FCSTD DOCUMENT  (FreeCAD 1.0R39285 (Git))
Label: pinWheel
License: All rights reserved
LicenseURL: https://en.wikipedia.org/wiki/All_rights_reserved
objects: Sketcher::SketchObject×193, Part::Extrusion×189, Part::Feature×37, Part::MultiFuse×17, Part::Cut×10, App::Part×5, Part::Cylinder×3, Part::Box×2, Part::Loft×2, Part::Fillet×2, Part::Compound×1
note: 649 computed .brp shape members not serialized (recipe doc carries the construction recipe); baked Part::Feature solids carry a one-line shape summary decoded from their .brp

FEATURE [Sketcher::SketchObject] Sketch
  ArcFitTolerance = 1e-06
  FullyConstrained = true
  MakeInternals = false
  Placement = pos=(0,0,0) rot=(1,0,0;1.5708rad)
  sketch-geometry (14):
    g0: LineSegment StartX=0 StartY=130 StartZ=0 EndX=-112.583 EndY=65 EndZ=0
    g1: LineSegment StartX=-112.583 StartY=65 StartZ=0 EndX=-112.583 EndY=-65 EndZ=0
    g2: LineSegment StartX=-112.583 StartY=-65 StartZ=0 EndX=-4.9e-15 EndY=-130 EndZ=0
    g3: LineSegment StartX=0 StartY=-130 StartZ=0 EndX=112.583 EndY=-65 EndZ=0
    g4: LineSegment StartX=112.583 StartY=-65 StartZ=0 EndX=112.583 EndY=65 EndZ=0
    g5: LineSegment StartX=112.583 StartY=65 StartZ=0 EndX=4.9e-15 EndY=130 EndZ=0
    g6: Circle [constr] CenterX=0 CenterY=0 CenterZ=0 NormalX=0 NormalY=0 NormalZ=1 AngleXU=0 Radius=130
    g7: LineSegment StartX=0 StartY=135 StartZ=0 EndX=-116.913 EndY=67.5 EndZ=0
    g8: LineSegment StartX=-116.913 StartY=67.5 StartZ=0 EndX=-116.913 EndY=-67.5 EndZ=0
    g9: LineSegment StartX=-116.913 StartY=-67.5 StartZ=0 EndX=4.2e-15 EndY=-135 EndZ=0
    g10: LineSegment StartX=0 StartY=-135 StartZ=0 EndX=116.913 EndY=-67.5 EndZ=0
    g11: LineSegment StartX=116.913 StartY=-67.5 StartZ=0 EndX=116.913 EndY=67.5 EndZ=0
    g12: LineSegment StartX=116.913 StartY=67.5 StartZ=0 EndX=-5e-15 EndY=135 EndZ=0
    g13: Circle [constr] CenterX=0 CenterY=0 CenterZ=0 NormalX=0 NormalY=0 NormalZ=1 AngleXU=0 Radius=135
  constraints (32):
    c: Coincident(g0,g1)
    c: Coincident(g1,g2)
    c: Coincident(g2,g3)
    c: Coincident(g3,g4)
    c: Coincident(g4,g5)
    c: Coincident(g5,g0)
    c: Equal(g0, g1-g5) x5
    c: PointOnObject(g0,g6)
    c: PointOnObject(g1,g6)
    c: PointOnObject(g2,g6)
    c: PointOnObject(g3,g6)
    c: PointOnObject(g4,g6)
    c: PointOnObject(g5,g6)
    c: Coincident(g6,g-1)
    c: PointOnObject(g5,g-2)
    c: Diameter(g6) = 260
    c: Coincident(g7,g8)
    c: Coincident(g8,g9)
    c: Coincident(g9,g10)
    c: Coincident(g10,g11)
    c: Coincident(g11,g12)
    c: Coincident(g12,g7)
    c: Equal(g7, g8-g12) x5
    c: PointOnObject(g7,g13)
    c: PointOnObject(g8,g13)
    c: PointOnObject(g9,g13)
    c: PointOnObject(g10,g13)
    c: PointOnObject(g11,g13)
    c: PointOnObject(g12,g13)
    c: Coincident(g13,g6)
    c: PointOnObject(g12,g-2)
    c: Diameter(g13) = 270
FEATURE [Part::Extrusion] Extrude  label="hexShell"
  Base = -> Sketch
  Dir = (0,-1,2e-16)
  DirMode = 2
  FaceMakerClass = Part::FaceMakerBullseye
  FaceMakerMode = 3
  LengthFwd = 150
  LengthRev = 0
  Solid = true
  Symmetric = false
FEATURE [Part::Feature] Shape  label="hex"
  Placement = pos=(13,10,0) rot=(0,0,1;0rad)
  shape: bbox 306 x 310 x 2e-07 mm, 718 faces, 0 solids (baked)
FEATURE [Part::Box] Box  label="Cube"
  AttacherType = Attacher::AttachEngine3D
  Height = 10
  Length = 320
  Width = 320
FEATURE [Part::Extrusion] Extrude001
  Base = -> Shape
  Dir = (0,0,1)
  DirMode = 2
  FaceMakerClass = Part::FaceMakerBullseye
  FaceMakerMode = 3
  LengthFwd = 10
  LengthRev = 0
  Solid = false
  Symmetric = false
FEATURE [Part::Cut] Cut  label="hexMesh"
  Base = -> Box
  Placement = pos=(-170,-139.5,-157.5) rot=(1,0,0;1.5708rad)
  Refine = true
  Tool = -> Extrude001
FEATURE [Sketcher::SketchObject] Sketch001
  ArcFitTolerance = 1e-06
  FullyConstrained = true
  MakeInternals = false
  Placement = pos=(0,0,0) rot=(1,0,0;1.5708rad)
  sketch-geometry (11):
    g0: LineSegment StartX=0 StartY=132.5 StartZ=0 EndX=-114.748 EndY=66.25 EndZ=0
    g1: LineSegment StartX=-114.748 StartY=66.25 StartZ=0 EndX=-114.748 EndY=-66.25 EndZ=0
    g2: LineSegment StartX=-114.748 StartY=-66.25 StartZ=0 EndX=3.8584e-11 EndY=-132.5 EndZ=0
    g3: LineSegment StartX=3.85825e-11 StartY=-132.5 StartZ=0 EndX=114.748 EndY=-66.25 EndZ=0
    g4: LineSegment StartX=114.748 StartY=-66.25 StartZ=0 EndX=114.748 EndY=66.25 EndZ=0
    g5: LineSegment StartX=114.748 StartY=66.25 StartZ=0 EndX=7e-15 EndY=132.5 EndZ=0
    g6: Circle [constr] CenterX=0 CenterY=0 CenterZ=0 NormalX=0 NormalY=0 NormalZ=1 AngleXU=0 Radius=132.5
    g7: LineSegment StartX=-175 StartY=165 StartZ=0 EndX=-175 EndY=-165 EndZ=0
    g8: LineSegment StartX=-175 StartY=-165 StartZ=0 EndX=155 EndY=-165 EndZ=0
    g9: LineSegment StartX=155 StartY=-165 StartZ=0 EndX=155 EndY=165 EndZ=0
    g10: LineSegment StartX=155 StartY=165 StartZ=0 EndX=-175 EndY=165 EndZ=0
  constraints (28):
    c: Coincident(g0,g1)
    c: Coincident(g1,g2)
    c: Coincident(g2,g3)
    c: Coincident(g3,g4)
    c: Coincident(g4,g5)
    c: Coincident(g5,g0)
    c: Equal(g0, g1-g5) x5
    c: PointOnObject(g0,g6)
    c: PointOnObject(g1,g6)
    c: PointOnObject(g2,g6)
    c: PointOnObject(g3,g6)
    c: PointOnObject(g4,g6)
    c: PointOnObject(g5,g6)
    c: Coincident(g6,g-1)
    c: PointOnObject(g5,g-2)
    c: Diameter(g6) = 265
    c: Coincident(g7,g8)
    c: Coincident(g8,g9)
    c: Coincident(g9,g10)
    c: Coincident(g10,g7)
    c: Vertical(g7)
    c: Vertical(g9)
    c: Horizontal(g8)
    c: Horizontal(g10)
    c: DistanceY(g7,g7) = 330
    c: DistanceX(g10,g10) = 330
    c: Distance(g7,g-1) = 165
    c: Distance(g7,g-2) = 175
FEATURE [Part::Extrusion] Extrude002
  Base = -> Sketch001
  Dir = (0,-1,2e-16)
  DirMode = 2
  FaceMakerClass = Part::FaceMakerBullseye
  FaceMakerMode = 3
  LengthFwd = 20
  LengthRev = 0
  Placement = pos=(0,-134,0) rot=(0,0,1;0rad)
  Solid = true
  Symmetric = false
FEATURE [Part::Cut] Cut001  label="Mesh"
  Base = -> Cut
  Refine = true
  Tool = -> Extrude002
FEATURE [Part::Box] Box001  label="stand"
  AttacherType = Attacher::AttachEngine3D
  Height = 500
  Length = 60
  Placement = pos=(-30,150,-472) rot=(0,0,1;0rad)
  Width = 30
FEATURE [Part::Cylinder] Cylinder  label="pinWheelAxis"
  Angle = 360
  AttacherType = Attacher::AttachEngine3D
  FirstAngle = 0
  Height = 25
  Placement = pos=(0,-140,0) rot=(1,0,0;1.5708rad)
  Radius = 3
  SecondAngle = 0
FEATURE [Part::Feature] Part__Feature  label="PW00.01"
  Placement = pos=(0,0,0) rot=(1,0,0;1.5708rad)
  shape: bbox 56.83 x 111.6 x 23.27 mm, 29 faces (baked)
FEATURE [Part::Feature] Part__Feature001  label="PW00.02"
  Placement = pos=(0,0,0.1) rot=(0.862856,-0.357407,-0.357407;1.71777rad)
  shape: bbox 94.97 x 95.87 x 23.27 mm, 29 faces (baked)
FEATURE [Part::Feature] Part__Feature002  label="PW00.03"
  Placement = pos=(0,0,0.2) rot=(0.57735,-0.57735,-0.57735;2.0944rad)
  shape: bbox 111.6 x 56.83 x 23.27 mm, 29 faces (baked)
FEATURE [Part::Feature] Part__Feature003  label="PW00.04"
  Placement = pos=(0,0,0.3) rot=(-0.281085,0.678598,0.678598;3.68962rad)
  shape: bbox 95.87 x 94.97 x 23.27 mm, 29 faces (baked)
FEATURE [Part::Feature] Part__Feature004  label="PW00.05"
  Placement = pos=(0,0,0.4) rot=(0,0.707107,0.707107;3.14159rad)
  shape: bbox 56.83 x 111.6 x 23.27 mm, 29 faces (baked)
FEATURE [Part::Feature] Part__Feature005  label="PW00.06"
  Placement = pos=(0,0,0.5) rot=(0.281085,0.678598,0.678598;2.59356rad)
  shape: bbox 94.97 x 95.87 x 23.27 mm, 29 faces (baked)
FEATURE [Part::Feature] Part__Feature006  label="PW00.07"
  Placement = pos=(0,0,0.6) rot=(0.57735,0.57735,0.57735;2.0944rad)
  shape: bbox 111.6 x 56.83 x 23.27 mm, 29 faces (baked)
FEATURE [Part::Feature] Part__Feature007  label="PW00.08"
  Placement = pos=(0,0,0.7) rot=(0.862856,0.357407,0.357407;1.71777rad)
  shape: bbox 95.87 x 94.97 x 23.27 mm, 29 faces (baked)
FEATURE [Part::Feature] Part__Feature009  label="PW00.10"
  Placement = pos=(2.46e-14,1.99e-14,-6.99945) rot=(0,0,1;0rad)
  shape: bbox 12 x 12 x 10 mm, 5 faces (baked)
FEATURE [Part::Feature] Part__Feature010  label="PW00.11"
  Placement = pos=(1.67e-14,1.9e-15,-6.5475) rot=(0,0,1;0rad)
  shape: bbox 5.016 x 5.016 x 2.016 mm, 3 faces (baked)
FEATURE [App::Part] PW00_00  label="wheel"
  Group = -> [Part__Feature,Part__Feature001,Part__Feature002,Part__Feature003,Part__Feature004,Part__Feature005,Part__Feature006,Part__Feature007,Part__Feature009,Part__Feature010]
  Origin = -> Origin
  Placement = pos=(0,-166.5,-5.03e-14) rot=(1,0,0;1.5708rad)
FEATURE [Sketcher::SketchObject] Sketch004
  ArcFitTolerance = 1e-06
  FullyConstrained = true
  MakeInternals = false
  Placement = pos=(0,-150,0) rot=(1,0,0;1.5708rad)
  sketch-geometry (7):
    g0: LineSegment StartX=0 StartY=135 StartZ=0 EndX=-116.913 EndY=67.5 EndZ=0
    g1: LineSegment StartX=-116.913 StartY=67.5 StartZ=0 EndX=-116.913 EndY=-67.5 EndZ=0
    g2: LineSegment StartX=-116.913 StartY=-67.5 StartZ=0 EndX=1.92e-14 EndY=-135 EndZ=0
    g3: LineSegment StartX=1.42e-14 StartY=-135 StartZ=0 EndX=116.913 EndY=-67.5 EndZ=0
    g4: LineSegment StartX=116.913 StartY=-67.5 StartZ=0 EndX=116.913 EndY=67.5 EndZ=0
    g5: LineSegment StartX=116.913 StartY=67.5 StartZ=0 EndX=-4.2e-15 EndY=135 EndZ=0
    g6: Circle [constr] CenterX=0 CenterY=0 CenterZ=0 NormalX=0 NormalY=0 NormalZ=1 AngleXU=0 Radius=135
  constraints (16):
    c: Coincident(g0,g1)
    c: Coincident(g1,g2)
    c: Coincident(g2,g3)
    c: Coincident(g3,g4)
    c: Coincident(g4,g5)
    c: Coincident(g5,g0)
    c: Equal(g0, g1-g5) x5
    c: PointOnObject(g0,g6)
    c: PointOnObject(g1,g6)
    c: PointOnObject(g2,g6)
    c: PointOnObject(g3,g6)
    c: PointOnObject(g4,g6)
    c: PointOnObject(g5,g6)
    c: PointOnObject(g5,g-2)
    c: Diameter(g6) = 270
    c: Coincident(g6,g-1)
FEATURE [Sketcher::SketchObject] Sketch005
  ArcFitTolerance = 1e-06
  FullyConstrained = true
  MakeInternals = false
  Placement = pos=(0,0,0) rot=(1,0,0;1.5708rad)
  sketch-geometry (8):
    g0: Circle [constr] CenterX=0 CenterY=0 CenterZ=0 NormalX=0 NormalY=0 NormalZ=1 AngleXU=0 Radius=20
    g1: LineSegment StartX=0 StartY=25 StartZ=0 EndX=-21.6506 EndY=12.5 EndZ=0
    g2: LineSegment StartX=-21.6506 StartY=12.5 StartZ=0 EndX=-21.6506 EndY=-12.5 EndZ=0
    g3: LineSegment StartX=-21.6506 StartY=-12.5 StartZ=0 EndX=-1.7133e-12 EndY=-25 EndZ=0
    g4: LineSegment StartX=-1.7124e-12 StartY=-25 StartZ=0 EndX=21.6506 EndY=-12.5 EndZ=0
    g5: LineSegment StartX=21.6506 StartY=-12.5 StartZ=0 EndX=21.6506 EndY=12.5 EndZ=0
    g6: LineSegment StartX=21.6506 StartY=12.5 StartZ=0 EndX=1e-15 EndY=25 EndZ=0
    g7: Circle [constr] CenterX=0 CenterY=0 CenterZ=0 NormalX=0 NormalY=0 NormalZ=1 AngleXU=0 Radius=25
  constraints (18):
    c: Coincident(g0,g-1)
    c: Diameter(g0) = 40
    c: Coincident(g1,g2)
    c: Coincident(g2,g3)
    c: Coincident(g3,g4)
    c: Coincident(g4,g5)
    c: Coincident(g5,g6)
    c: Coincident(g6,g1)
    c: Equal(g1, g2-g6) x5
    c: PointOnObject(g1,g7)
    c: PointOnObject(g2,g7)
    c: PointOnObject(g3,g7)
    c: PointOnObject(g4,g7)
    c: PointOnObject(g5,g7)
    c: PointOnObject(g6,g7)
    c: Coincident(g7,g0)
    c: PointOnObject(g6,g-2)
    c: Diameter(g7) = 50
FEATURE [Sketcher::SketchObject] Sketch006
  ArcFitTolerance = 1e-06
  FullyConstrained = true
  MakeInternals = false
  Placement = pos=(0,-150,0) rot=(1,0,0;1.5708rad)
  sketch-geometry (8):
    g0: LineSegment StartX=0 StartY=130 StartZ=0 EndX=-112.583 EndY=65 EndZ=0
    g1: LineSegment StartX=-112.583 StartY=65 StartZ=0 EndX=-112.583 EndY=-65 EndZ=0
    g2: LineSegment StartX=-112.583 StartY=-65 StartZ=0 EndX=-1.13e-14 EndY=-130 EndZ=0
    g3: LineSegment StartX=1.42e-14 StartY=-130 StartZ=0 EndX=112.583 EndY=-65 EndZ=0
    g4: LineSegment StartX=112.583 StartY=-65 StartZ=0 EndX=112.583 EndY=65 EndZ=0
    g5: LineSegment StartX=112.583 StartY=65 StartZ=0 EndX=4.7e-15 EndY=130 EndZ=0
    g6: Circle [constr] CenterX=0 CenterY=0 CenterZ=0 NormalX=0 NormalY=0 NormalZ=1 AngleXU=0 Radius=130
    g7: Circle [constr] CenterX=0 CenterY=0 CenterZ=0 NormalX=0 NormalY=0 NormalZ=1 AngleXU=0 Radius=135
  constraints (18):
    c: Coincident(g0,g1)
    c: Coincident(g1,g2)
    c: Coincident(g2,g3)
    c: Coincident(g3,g4)
    c: Coincident(g4,g5)
    c: Coincident(g5,g0)
    c: Equal(g0, g1-g5) x5
    c: PointOnObject(g0,g6)
    c: PointOnObject(g1,g6)
    c: PointOnObject(g2,g6)
    c: PointOnObject(g3,g6)
    c: PointOnObject(g4,g6)
    c: PointOnObject(g5,g6)
    c: Coincident(g6,g-1)
    c: PointOnObject(g5,g-2)
    c: Diameter(g6) = 260
    c: Coincident(g7,g6)
    c: Diameter(g7) = 270
FEATURE [Sketcher::SketchObject] Sketch007
  ArcFitTolerance = 1e-06
  FullyConstrained = true
  MakeInternals = false
  Placement = pos=(0,0,0) rot=(1,0,0;1.5708rad)
  sketch-geometry (8):
    g0: LineSegment StartX=0 StartY=20 StartZ=0 EndX=-17.3205 EndY=10 EndZ=0
    g1: LineSegment StartX=-17.3205 StartY=10 StartZ=0 EndX=-17.3205 EndY=-10 EndZ=0
    g2: LineSegment StartX=-17.3205 StartY=-10 StartZ=0 EndX=-2.7e-15 EndY=-20 EndZ=0
    g3: LineSegment StartX=-3.6e-15 StartY=-20 StartZ=0 EndX=17.3205 EndY=-10 EndZ=0
    g4: LineSegment StartX=17.3205 StartY=-10 StartZ=0 EndX=17.3205 EndY=10 EndZ=0
    g5: LineSegment StartX=17.3205 StartY=10 StartZ=0 EndX=4e-16 EndY=20 EndZ=0
    g6: Circle [constr] CenterX=0 CenterY=0 CenterZ=0 NormalX=0 NormalY=0 NormalZ=1 AngleXU=0 Radius=20
    g7: Circle [constr] CenterX=0 CenterY=0 CenterZ=0 NormalX=0 NormalY=0 NormalZ=1 AngleXU=0 Radius=25
  constraints (18):
    c: Coincident(g0,g1)
    c: Coincident(g1,g2)
    c: Coincident(g2,g3)
    c: Coincident(g3,g4)
    c: Coincident(g4,g5)
    c: Coincident(g5,g0)
    c: Equal(g0, g1-g5) x5
    c: PointOnObject(g0,g6)
    c: PointOnObject(g1,g6)
    c: PointOnObject(g2,g6)
    c: PointOnObject(g3,g6)
    c: PointOnObject(g4,g6)
    c: PointOnObject(g5,g6)
    c: Coincident(g6,g-1)
    c: PointOnObject(g5,g-2)
    c: Diameter(g6) = 40
    c: Coincident(g7,g6)
    c: Diameter(g7) = 50
FEATURE [Part::Loft] Loft002
  Closed = false
  MaxDegree = 5
  Ruled = false
  Sections = -> [Sketch006,Sketch007]
  Solid = true
FEATURE [Part::Loft] Loft003
  Closed = false
  MaxDegree = 5
  Ruled = false
  Sections = -> [Sketch004,Sketch005]
  Solid = true
FEATURE [Part::Cut] Cut002  label="backEncloser"
  Base = -> Loft003
  Placement = pos=(0,150,0) rot=(0,0,1;0rad)
  Refine = true
  Tool = -> Loft002
FEATURE [Part::Feature] Part__Feature023  label="COZIR"
  Placement = pos=(5.41029,2.97838,5.56111) rot=(0,0,1;0rad)
  shape: bbox 51.61 x 17 x 50.23 mm, 43 faces (baked)
FEATURE [Part::Feature] Part__Feature024  label="COMPOUND"
  shape: bbox 3.14 x 5 x 10.76 mm, 60 faces, 10 solids (baked)
FEATURE [App::Part] COZIR_Sensor_v2  label="COZIR Sensor v2"
  Group = -> [Part__Feature023,Part__Feature024]
  Origin = -> Origin002
  Placement = pos=(18,-15,8.25) rot=(0,-1,0;5.75959rad)
FEATURE [Part::Feature] Part__Feature059  label="ips7100"
  Placement = pos=(-24,0,222) rot=(0.999993,-0.003655,0;3.14159rad)
  shape: bbox 48.14 x 14.05 x 44.14 mm, 1935 faces (baked)
FEATURE [Part::Compound] Compound  label="ips7100s"
  Links = -> [Part__Feature059]
  Placement = pos=(48.8551,-46.85,39.7193) rot=(-0.127223,0.126421,0.983785;4.70221rad)
FEATURE [Part::Feature] Part__Feature334  label="CAPC-0805-T0.95-BN v012"
  Placement = pos=(-5.48627,2.66154,1.6) rot=(0,0,-1;1.5708rad)
  shape: bbox 1.35 x 2.1 x 0.95 mm, 42 faces (baked)
FEATURE [Part::Feature] Part__Feature335  label="CAPC-0805-T0.95-BN v013"
  Placement = pos=(-3.43627,2.66154,1.6) rot=(0,0,-1;1.5708rad)
  shape: bbox 1.35 x 2.1 x 0.95 mm, 42 faces (baked)
FEATURE [Part::Feature] Part__Feature336  label="CAPC-0603-T0.9-BN v009"
  Placement = pos=(-1.69987,-3.28475,1.6) rot=(0,0,1;0rad)
  shape: bbox 1.7 x 0.9 x 0.9 mm, 42 faces (baked)
FEATURE [Part::Feature] Part__Feature337  label="BODY_MF06A003"
  Placement = pos=(0,0,0.762) rot=(0.57735,-0.57735,-0.57735;2.0944rad)
  shape: bbox 1.601 x 2.921 x 1.016 mm, 42 faces (baked)
FEATURE [Part::Feature] Part__Feature338  label="LEAD_MF06A018"
  Placement = pos=(-0.9652,-0.9525,0.1016) rot=(0.57735,-0.57735,-0.57735;2.0944rad)
  shape: bbox 0.6223 x 0.3749 x 0.8636 mm, 14 faces (baked)
FEATURE [Part::Feature] Part__Feature339  label="LEAD_MF06A019"
  Placement = pos=(-0.9652,0,0.1016) rot=(0.57735,-0.57735,-0.57735;2.0944rad)
  shape: bbox 0.6223 x 0.3749 x 0.8636 mm, 14 faces (baked)
FEATURE [Part::Feature] Part__Feature340  label="LEAD_MF06A020"
  Placement = pos=(-0.9652,0.9525,0.1016) rot=(0.57735,-0.57735,-0.57735;2.0944rad)
  shape: bbox 0.6223 x 0.3749 x 0.8636 mm, 14 faces (baked)
FEATURE [Part::Feature] Part__Feature341  label="LEAD_MF06A021"
  Placement = pos=(0.9652,-0.9525,0.1016) rot=(0.57735,0.57735,0.57735;2.0944rad)
  shape: bbox 0.6223 x 0.3749 x 0.8636 mm, 14 faces (baked)
FEATURE [Part::Feature] Part__Feature342  label="LEAD_MF06A022"
  Placement = pos=(0.9652,0,0.1016) rot=(0.57735,0.57735,0.57735;2.0944rad)
  shape: bbox 0.6223 x 0.3749 x 0.8636 mm, 14 faces (baked)
FEATURE [Part::Feature] Part__Feature343  label="LEAD_MF06A023"
  Placement = pos=(0.9652,0.9525,0.1016) rot=(0.57735,0.57735,0.57735;2.0944rad)
  shape: bbox 0.6223 x 0.3749 x 0.8636 mm, 14 faces (baked)
FEATURE [Part::Feature] Part__Feature344  label="SOT363 v005"
  Placement = pos=(4.97054,-0.645171,1.675) rot=(0,0,1;3.14159rad)
  shape: bbox 2.1 x 2 x 1.1 mm, 94 faces, 7 solids (baked)
FEATURE [Part::Feature] Part__Feature345  label="LED 0603 single color v005"
  Placement = pos=(-9.18406,3.72778,1.60762) rot=(0,0,1;1.5708rad)
  shape: bbox 1.961 x 0.7932 x 0.7145 mm, 63 faces, 5 solids (baked)
FEATURE [Part::Feature] Part__Feature346  label="RESC-0603 v007"
  Placement = pos=(4.83432,-3.67461,1.6) rot=(0,0,1;0rad)
  shape: bbox 1.7 x 0.9 x 0.55 mm, 52 faces, 3 solids (baked)
FEATURE [Part::Feature] Part__Feature347  label="RESC-0603 v008"
  Placement = pos=(-7.14949,3.61248,1.6) rot=(0,0,-1;1.5708rad)
  shape: bbox 0.9 x 1.7 x 0.55 mm, 52 faces, 3 solids (baked)
FEATURE [Part::Feature] Part__Feature348  label="Printed Circuit Board004"
  shape: bbox 25.4 x 17.78 x 1.6 mm, 42 faces (baked)
FEATURE [Part::Feature] Part__Feature349  label="EAHC2835WD009"
  shape: bbox 3.513 x 2.813 x 0.7485 mm, 108 faces, 4 solids (baked)
FEATURE [Part::Feature] Part__Feature350  label="AS7341 v005"
  Placement = pos=(0,-0.339822,1.6) rot=(0,0,1;0rad)
  shape: bbox 2 x 3.1 x 1.1 mm, 267 faces, 26 solids (baked)
FEATURE [Part::Feature] Part__Feature351  label="CAPC-0805-T0.95-BN v014"
  Placement = pos=(-5.01759,-3.15294,1.6) rot=(0,0,1;0rad)
  shape: bbox 2.1 x 1.35 x 0.95 mm, 42 faces (baked)
FEATURE [Part::Feature] Part__Feature352  label="YC164_RESPACK v007"
  Placement = pos=(2.99591,1.52916,1.6) rot=(0,0,1;0rad)
  shape: bbox 3.2 x 1.6 x 0.61 mm, 172 faces (baked)
FEATURE [Part::Feature] Part__Feature353  label="qwicc v009"
  Placement = pos=(-10.8364,0.0607456,1.65) rot=(0,0,-1;1.5708rad)
  shape: bbox 4.95 x 6 x 2.96 mm, 229 faces, 7 solids (baked)
FEATURE [Part::Feature] Part__Feature354  label="qwicc v010"
  Placement = pos=(10.8256,0.00556102,1.65) rot=(0,0,1;1.5708rad)
  shape: bbox 4.95 x 6 x 2.96 mm, 229 faces, 7 solids (baked)
FEATURE [App::Part] sot_23_6_v005  label="sot-23-6 v005"
  Group = -> [Part__Feature337,Part__Feature338,Part__Feature339,Part__Feature340,Part__Feature341,Part__Feature342,Part__Feature343]
  Origin = -> Origin019
  Placement = pos=(-4.47945,-0.603742,1.69152) rot=(0,0,1;0rad)
FEATURE [App::Part] Adafruit_AS7341_STEMMA_QT_v005  label="bme280"
  Group = -> [Part__Feature348,Part__Feature349,Part__Feature350,Part__Feature351,Part__Feature334,Part__Feature335,Part__Feature336,sot_23_6_v005,Part__Feature344,Part__Feature345,Part__Feature346,Part__Feature347,Part__Feature352,Part__Feature353,Part__Feature354]
  Origin = -> Origin020
  Placement = pos=(-39.4483,-2,71.3086) rot=(-0.962637,0.19148,-0.19148;4.67432rad)
FEATURE [Sketcher::SketchObject] Sketch386
  ArcFitTolerance = 0
  FullyConstrained = true
  MakeInternals = false
  Placement = pos=(0,0,0) rot=(1,0,0;1.5708rad)
  sketch-geometry (6):
    g0: Circle CenterX=202.5 CenterY=16.1 CenterZ=0 NormalX=0 NormalY=0 NormalZ=1 AngleXU=0 Radius=1.625
    g1: Circle CenterX=202.5 CenterY=16.1 CenterZ=0 NormalX=0 NormalY=0 NormalZ=1 AngleXU=0 Radius=5
    g2: Circle CenterX=224.07 CenterY=53.45 CenterZ=0 NormalX=0 NormalY=0 NormalZ=1 AngleXU=0 Radius=5
    g3: Circle CenterX=180.93 CenterY=53.45 CenterZ=0 NormalX=0 NormalY=0 NormalZ=1 AngleXU=0 Radius=5
    g4: Circle CenterX=180.93 CenterY=53.45 CenterZ=0 NormalX=0 NormalY=0 NormalZ=1 AngleXU=0 Radius=1.625
    g5: Circle CenterX=224.07 CenterY=53.45 CenterZ=0 NormalX=0 NormalY=0 NormalZ=1 AngleXU=0 Radius=1.625
  constraints (15):
    c: DistanceX(g0) = 202.5
    c: DistanceY(g0) = 16.1
    c: Coincident(g0,g1)
    c: DistanceY(g3,g2) = 0
    c: Equal(g1,g2)
    c: Equal(g1,g3)
    c: Diameter(g1) = 10
    c: Equal(g0,g5)
    c: Equal(g0,g4)
    c: Diameter(g0) = 3.25
    c: DistanceY(g0,g3) = 37.35
    c: DistanceX(g3,g0) = 21.57
    c: DistanceX(g0,g2) = 21.57
    c: Coincident(g5,g2)
    c: Coincident(g4,g3)
FEATURE [Part::Extrusion] Extrude379  label="co2Mount003"
  Base = -> Sketch386
  Dir = (0,-1,2e-16)
  DirMode = 2
  FaceMakerClass = Part::FaceMakerBullseye
  FaceMakerMode = 3
  LengthFwd = 22
  LengthRev = 0
  Placement = pos=(-202.681,8,35.5181) rot=(0,0,1;0rad)
  Solid = true
  Symmetric = false
FEATURE [Sketcher::SketchObject] Sketch387
  ArcFitTolerance = 1e-06
  FullyConstrained = true
  MakeInternals = false
  Placement = pos=(0,0,0) rot=(1,0,0;1.5708rad)
  sketch-geometry (11):
    g0: ArcOfCircle CenterX=0 CenterY=75 CenterZ=0 NormalX=0 NormalY=0 NormalZ=1 AngleXU=0 Radius=65 StartAngle=3.14161 EndAngle=6.2832
    g1: LineSegment StartX=-65 StartY=74.999 StartZ=0 EndX=3e-16 EndY=105.31 EndZ=0
    g2: LineSegment StartX=3e-16 StartY=105.31 StartZ=0 EndX=65 EndY=75.001 EndZ=0
    g3: ArcOfCircle CenterX=32.0734 CenterY=74.8326 CenterZ=0 NormalX=0 NormalY=0 NormalZ=1 AngleXU=0 Radius=4 StartAngle=0.252249 EndAngle=3.39384
    g4: ArcOfCircle CenterX=37.1 CenterY=55.33 CenterZ=0 NormalX=0 NormalY=0 NormalZ=1 AngleXU=0 Radius=4 StartAngle=3.39384 EndAngle=6.53543
    g5: LineSegment StartX=35.9468 StartY=75.831 StartZ=0 EndX=40.9734 EndY=56.3283 EndZ=0
    g6: LineSegment StartX=28.2 StartY=73.8343 StartZ=0 EndX=33.2266 EndY=54.3317 EndZ=0
    g7: Circle CenterX=-60 CenterY=70 CenterZ=0 NormalX=0 NormalY=0 NormalZ=1 AngleXU=0 Radius=1.75
    g8: Circle CenterX=60 CenterY=70 CenterZ=0 NormalX=0 NormalY=0 NormalZ=1 AngleXU=0 Radius=1.75
    g9: Circle CenterX=-6 CenterY=100 CenterZ=0 NormalX=0 NormalY=0 NormalZ=1 AngleXU=0 Radius=1.75
    g10: Circle CenterX=6 CenterY=100 CenterZ=0 NormalX=0 NormalY=0 NormalZ=1 AngleXU=0 Radius=1.75
  constraints (32):
    c: PointOnObject(g0,g-2)
    c: Radius(g0) = 65
    c: Coincident(g1,g0)
    c: PointOnObject(g1,g-2)
    c: Coincident(g2,g1)
    c: Coincident(g2,g0)
    c: Angle(g1,g2) = 2.26893
    c: Angle(g0) = 3.14159
    c: Distance(g1,g1) = 71.72
    c: DistanceY(g-1,g0) = 75
    c: Tangent(g3,g5) = 1.5708
    c: Tangent(g3,g6) = -1.5708
    c: Tangent(g4,g5) = 1.5708
    c: Tangent(g4,g6) = -1.5708
    c: Equal(g3,g4)
    c: Distance(g4,g-2) = 37.1
    c: DistanceY(g-1,g4) = 55.33
    c: Distance(g4,g4) = 8
    c: Distance(g4,g3) = 20.14
    c: Distance(g3,g-2) = 28.2
    c: Equal(g9,g10)
    c: Equal(g9,g8)
    c: Equal(g9,g7)
    c: Diameter(g9) = 3.5
    c: Distance(g7,g-2) = 60
    c: Distance(g8,g-2) = 60
    c: Horizontal(g7,g8)
    c: DistanceY(g-1,g7) = 70
    c: DistanceY(g-1,g9) = 100
    c: DistanceX(g9,g-1) = 6
    c: Horizontal(g9,g10)
    c: Distance(g10,g-2) = 6
FEATURE [Part::Extrusion] Extrude380  label="sensorBase"
  Base = -> Sketch387
  Dir = (0,-1,2e-16)
  DirMode = 2
  FaceMakerClass = Part::FaceMakerBullseye
  FaceMakerMode = 3
  LengthFwd = 7
  LengthRev = 0
  Placement = pos=(0,15,0) rot=(0,0,1;0rad)
  Solid = true
  Symmetric = false
FEATURE [Sketcher::SketchObject] Sketch388
  ArcFitTolerance = 0
  FullyConstrained = true
  MakeInternals = false
  Placement = pos=(0,0,0) rot=(1,0,0;1.5708rad)
  sketch-geometry (8):
    g0: Circle CenterX=173.65 CenterY=40.16 CenterZ=0 NormalX=0 NormalY=0 NormalZ=1 AngleXU=0 Radius=5
    g1: Circle CenterX=186.35 CenterY=40.16 CenterZ=0 NormalX=0 NormalY=0 NormalZ=1 AngleXU=0 Radius=5
    g2: Circle CenterX=173.65 CenterY=19.84 CenterZ=0 NormalX=0 NormalY=0 NormalZ=1 AngleXU=0 Radius=5
    g3: Circle CenterX=186.35 CenterY=19.84 CenterZ=0 NormalX=0 NormalY=0 NormalZ=1 AngleXU=0 Radius=5
    g4: Circle CenterX=173.65 CenterY=19.84 CenterZ=0 NormalX=0 NormalY=0 NormalZ=1 AngleXU=0 Radius=1.125
    g5: Circle CenterX=186.35 CenterY=19.84 CenterZ=0 NormalX=0 NormalY=0 NormalZ=1 AngleXU=0 Radius=1.125
    g6: Circle CenterX=186.35 CenterY=40.16 CenterZ=0 NormalX=0 NormalY=0 NormalZ=1 AngleXU=0 Radius=1.125
    g7: Circle CenterX=173.65 CenterY=40.16 CenterZ=0 NormalX=0 NormalY=0 NormalZ=1 AngleXU=0 Radius=1.125
  constraints (20):
    c: DistanceY(g1,g0) = 0
    c: DistanceX(g0) = 173.65
    c: DistanceY(g0) = 40.16
    c: DistanceY(g2,g0) = 20.32
    c: Horizontal(g2,g3)
    c: Vertical(g3,g1)
    c: Equal(g0,g1)
    c: Equal(g0,g2)
    c: Equal(g0,g3)
    c: Diameter(g0) = 10
    c: DistanceX(g0,g1) = 12.7
    c: Vertical(g2,g0)
    c: Coincident(g4,g2)
    c: Coincident(g5,g3)
    c: Coincident(g6,g1)
    c: Coincident(g7,g0)
    c: Equal(g4,g5)
    c: Equal(g4,g7)
    c: Equal(g4,g6)
    c: Diameter(g4) = 2.25
FEATURE [Part::Extrusion] Extrude381  label="i2cMounts003"
  Base = -> Sketch388
  Dir = (0,-1,2e-16)
  DirMode = 2
  FaceMakerClass = Part::FaceMakerBullseye
  FaceMakerMode = 3
  LengthFwd = 10
  LengthRev = 0
  Placement = pos=(-136.04,8,226.12) rot=(0,-1,0;5.10509rad)
  Solid = true
  Symmetric = false
FEATURE [Part::Feature] Part__Feature355  label="ips7101"
  Placement = pos=(-24,0,222) rot=(0.999993,-0.003655,0;3.14159rad)
  shape: bbox 48.14 x 14.05 x 44.14 mm, 1935 faces (baked)
FEATURE [Sketcher::SketchObject] Sketch390
  ArcFitTolerance = 1e-06
  FullyConstrained = true
  MakeInternals = false
  MapMode = 3
  Placement = pos=(103.996,0.641742,-0.641742) rot=(0.578538,-0.574968,-0.578538;2.08727rad)
  sketch-geometry (10):
    g0: LineSegment StartX=-55 StartY=0 StartZ=0 EndX=-39.5 EndY=0 EndZ=0
    g1: LineSegment StartX=-39.5 StartY=0 StartZ=0 EndX=-39.5 EndY=7.25 EndZ=0
    g2: LineSegment StartX=-39.5 StartY=7.25 StartZ=0 EndX=-55 EndY=7.25 EndZ=0
    g3: LineSegment StartX=-55 StartY=7.25 StartZ=0 EndX=-55 EndY=0 EndZ=0
    g4: LineSegment StartX=-55 StartY=36.75 StartZ=0 EndX=7.1e-15 EndY=36.75 EndZ=0
    g5: LineSegment StartX=7.1e-15 StartY=36.75 StartZ=0 EndX=7.1e-15 EndY=44 EndZ=0
    g6: LineSegment StartX=7.1e-15 StartY=44 StartZ=0 EndX=-55 EndY=44 EndZ=0
    g7: LineSegment StartX=-55 StartY=44 StartZ=0 EndX=-55 EndY=36.75 EndZ=0
    g8: Circle CenterX=-44.4 CenterY=3.625 CenterZ=0 NormalX=0 NormalY=0 NormalZ=1 AngleXU=0 Radius=1.25
    g9: Circle CenterX=-3.625 CenterY=40.375 CenterZ=0 NormalX=0 NormalY=0 NormalZ=1 AngleXU=0 Radius=1.25
  constraints (30):
    c: Coincident(g0,g1)
    c: Coincident(g1,g2)
    c: Coincident(g2,g3)
    c: Coincident(g3,g0)
    c: Horizontal(g0)
    c: Horizontal(g2)
    c: Vertical(g1)
    c: Vertical(g3)
    c: PointOnObject(g0,g-1)
    c: Coincident(g4,g5)
    c: Coincident(g5,g6)
    c: Coincident(g6,g7)
    c: Coincident(g7,g4)
    c: Horizontal(g4)
    c: Horizontal(g6)
    c: Vertical(g5)
    c: Vertical(g7)
    c: Distance(g3,g3) = 7.25
    c: Distance(g-1,g3) = 55
    c: Distance(g-2,g7) = 55
    c: DistanceY(g2,g4) = 29.5
    c: Distance(g5,g5) = 7.25
    c: DistanceX(g6,g6) = 55
    c: Distance(g4,g1) = 39.5
    c: DistanceX(g8,g-1) = 44.4
    c: DistanceY(g-1,g8) = 3.625
    c: Diameter(g8) = 2.5
    c: Distance(g9,g4) = 3.625
    c: Diameter(g9) = 2.5
    c: Distance(g9,g5) = 3.625
FEATURE [Part::Extrusion] Extrude382  label="ipsHold"
  Base = -> Sketch390
  Dir = (-0.999962,-0.00617059,0.00617059)
  DirMode = 2
  FaceMakerClass = Part::FaceMakerBullseye
  FaceMakerMode = 3
  LengthFwd = 6
  LengthRev = 0
  Placement = pos=(-46,-47.5,15) rot=(0,1,0;6.02139rad)
  Solid = true
  Symmetric = false
FEATURE [Part::MultiFuse] Fusion
  Refine = true
  Shapes = -> [Extrude380,Extrude381,Extrude379]
FEATURE [Part::MultiFuse] Fusion545  label="BaseHold"
  Refine = true
  Shapes = -> [Extrude382,Fusion]
FEATURE [Part::Feature] Part__Feature356  label="RaspberryPiZeroW002"
  Placement = pos=(-13.5,25.25,64.18) rot=(0,-1,0;3.14159rad)
  shape: bbox 65.9 x 4.8 x 31.25 mm, 368 faces, 2 solids (baked)
FEATURE [Sketcher::SketchObject] Sketch391
  ArcFitTolerance = 1e-06
  AttachmentSupport = -> [Fusion545]
  FullyConstrained = true
  MakeInternals = false
  MapMode = 3
  Placement = pos=(0,0,0) rot=(1,0,0;1.5708rad)
  sketch-geometry (8):
    g0: Circle CenterX=15.525 CenterY=75.71 CenterZ=0 NormalX=0 NormalY=0 NormalZ=1 AngleXU=0 Radius=1.125
    g1: Circle CenterX=-42.525 CenterY=75.71 CenterZ=0 NormalX=0 NormalY=0 NormalZ=1 AngleXU=0 Radius=1.125
    g2: Circle CenterX=15.525 CenterY=52.66 CenterZ=0 NormalX=0 NormalY=0 NormalZ=1 AngleXU=0 Radius=1.125
    g3: Circle CenterX=-42.525 CenterY=52.66 CenterZ=0 NormalX=0 NormalY=0 NormalZ=1 AngleXU=0 Radius=1.125
    g4: Circle CenterX=15.525 CenterY=75.71 CenterZ=0 NormalX=0 NormalY=0 NormalZ=1 AngleXU=0 Radius=5
    g5: Circle CenterX=15.525 CenterY=52.66 CenterZ=0 NormalX=0 NormalY=0 NormalZ=1 AngleXU=0 Radius=5
    g6: Circle CenterX=-42.525 CenterY=52.66 CenterZ=0 NormalX=0 NormalY=0 NormalZ=1 AngleXU=0 Radius=5
    g7: Circle CenterX=-42.525 CenterY=75.71 CenterZ=0 NormalX=0 NormalY=0 NormalZ=1 AngleXU=0 Radius=5
  constraints (20):
    c: Equal(g0,g1)
    c: Equal(g0,g2)
    c: Equal(g0,g3)
    c: Diameter(g0) = 2.25
    c: Coincident(g4,g0)
    c: Coincident(g5,g2)
    c: Coincident(g6,g3)
    c: Coincident(g7,g1)
    c: Equal(g4,g5)
    c: Equal(g4,g6)
    c: Equal(g4,g7)
    c: Diameter(g4) = 10
    c: Distance(g2,g-2) = 15.525
    c: Distance(g2,g-1) = 52.66
    c: Vertical(g2,g0)
    c: Horizontal(g3,g2)
    c: DistanceX(g3,g2) = 58.05
    c: Vertical(g1,g3)
    c: DistanceY(g2,g0) = 23.05
    c: Horizontal(g0,g1)
FEATURE [Part::Extrusion] Extrude383  label="piHold"
  Base = -> Sketch391
  Dir = (0,-1,2e-16)
  DirMode = 2
  FaceMakerClass = Part::FaceMakerBullseye
  FaceMakerMode = 3
  LengthFwd = 10
  LengthRev = 0
  Placement = pos=(0,25,0) rot=(0,0,1;0rad)
  Solid = true
  Symmetric = false
FEATURE [Part::MultiFuse] Fusion546
  Refine = true
  Shapes = -> [Fusion545,Extrude383]
FEATURE [Part::Fillet] Fillet096  label="sensorBaseFillet"
  Base = -> Fusion546
  EdgeLinks = -> Fusion546 [Edge1,Edge3,Edge4,Edge6,Edge7,Edge11,Edge12,Edge17,Edge21,Edge22,Edge20,Edge23,Edge19,Edge25,Edge26,Edge27,Edge28,Edge29,Edge30,Edge31,Edge32,Edge35,Edge36,Edge38,Edge39,Edge41,Edge60,Edge62,Edge64,Edge66,Edge72,Edge74,Edge76,Edge77,Edge84,Edge85,Edge86,Edge87,Edge99]
  Edges = 39 edges: [Edge1 r=1,Edge3 r=1,Edge4 r=1,Edge6 r=1,Edge7 r=1,Edge11 r=1,Edge12 r=1,Edge17 r=1,Edge21 r=1,Edge22 r=1,Edge20 r=1,Edge23 r=1,Edge19 r=1,Edge25 r=1,Edge26 r=1,Edge27 r=1,Edge28 r=1,Edge29 r=1,Edge30 r=1,Edge31 r=1,Edge32 r=1,Edge35 r=1,Edge36 r=1,Edge38 r=5,Edge39 r=5,Edge41 r=5,Edge60 r=1,Edge62 r=1,Edge64 r=1,Edge66 r=1,Edge72 r=1,Edge74 r=1,Edge76 r=1,Edge77 r=1,Edge84 r=1,Edge85 r=1,Edge86 r=1,Edge87 r=1,Edge99 r=1]
FEATURE [Sketcher::SketchObject] Sketch392
  ArcFitTolerance = 1e-06
  FullyConstrained = true
  MakeInternals = false
  Placement = pos=(0,0,0) rot=(1,0,0;1.5708rad)
  sketch-geometry (8):
    g0: Circle CenterX=-60 CenterY=70 CenterZ=0 NormalX=0 NormalY=0 NormalZ=1 AngleXU=0 Radius=5
    g1: Circle CenterX=-60 CenterY=70 CenterZ=0 NormalX=0 NormalY=0 NormalZ=1 AngleXU=0 Radius=1.75
    g2: Circle CenterX=60 CenterY=70 CenterZ=0 NormalX=0 NormalY=0 NormalZ=1 AngleXU=0 Radius=5
    g3: Circle CenterX=60 CenterY=70 CenterZ=0 NormalX=0 NormalY=0 NormalZ=1 AngleXU=0 Radius=1.75
    g4: Circle CenterX=-6 CenterY=100 CenterZ=0 NormalX=0 NormalY=0 NormalZ=1 AngleXU=0 Radius=5
    g5: Circle CenterX=6 CenterY=100 CenterZ=0 NormalX=0 NormalY=0 NormalZ=1 AngleXU=0 Radius=5
    g6: Circle CenterX=-6 CenterY=100 CenterZ=0 NormalX=0 NormalY=0 NormalZ=1 AngleXU=0 Radius=1.75
    g7: Circle CenterX=6 CenterY=100 CenterZ=0 NormalX=0 NormalY=0 NormalZ=1 AngleXU=0 Radius=1.75
  constraints (20):
    c: Coincident(g1,g0)
    c: Coincident(g3,g2)
    c: Equal(g0,g2)
    c: Diameter(g0) = 10
    c: Equal(g1,g3)
    c: Diameter(g1) = 3.5
    c: Distance(g0,g-2) = 60
    c: Distance(g0,g-1) = 70
    c: Horizontal(g0,g2)
    c: Distance(g2,g-2) = 60
    c: Coincident(g6,g4)
    c: Coincident(g7,g5)
    c: Equal(g4,g5)
    c: Diameter(g4) = 10
    c: Equal(g6,g7)
    c: Diameter(g6) = 3.5
    c: Distance(g4,g-2) = 6
    c: DistanceY(g-1,g4) = 100
    c: Horizontal(g4,g5)
    c: DistanceX(g-1,g5) = 6
FEATURE [Part::Extrusion] Extrude384  label="baseMount"
  Base = -> Sketch392
  Dir = (0,-1,2e-16)
  DirMode = 2
  FaceMakerClass = Part::FaceMakerBullseye
  FaceMakerMode = 3
  LengthFwd = 40
  LengthRev = 0
  Placement = pos=(0,55,0) rot=(0,0,1;0rad)
  Solid = true
  Symmetric = false
FEATURE [Sketcher::SketchObject] Sketch393
  ArcFitTolerance = 1e-06
  FullyConstrained = true
  MakeInternals = false
  Placement = pos=(0,0,0) rot=(1,0,0;1.5708rad)
  sketch-geometry (14):
    g0: LineSegment StartX=6.2e-15 StartY=122.5 StartZ=0 EndX=-106.088 EndY=61.25 EndZ=0
    g1: LineSegment StartX=-106.088 StartY=61.25 StartZ=0 EndX=-106.088 EndY=-61.25 EndZ=0
    g2: LineSegment StartX=-106.088 StartY=-61.25 StartZ=0 EndX=-1.66e-14 EndY=-122.5 EndZ=0
    g3: LineSegment StartX=-1.66e-14 StartY=-122.5 StartZ=0 EndX=106.088 EndY=-61.25 EndZ=0
    g4: LineSegment StartX=106.088 StartY=-61.25 StartZ=0 EndX=106.088 EndY=61.25 EndZ=0
    g5: LineSegment StartX=106.088 StartY=61.25 StartZ=0 EndX=6.2e-15 EndY=122.5 EndZ=0
    g6: Circle [constr] CenterX=0 CenterY=0 CenterZ=0 NormalX=0 NormalY=0 NormalZ=1 AngleXU=0 Radius=122.5
    g7: LineSegment StartX=4.7e-15 StartY=130 StartZ=0 EndX=-112.583 EndY=65 EndZ=0
    g8: LineSegment StartX=-112.583 StartY=65 StartZ=0 EndX=-112.583 EndY=-65 EndZ=0
    g9: LineSegment StartX=-112.583 StartY=-65 StartZ=0 EndX=-4.9e-15 EndY=-130 EndZ=0
    g10: LineSegment StartX=-4.9e-15 StartY=-130 StartZ=0 EndX=112.583 EndY=-65 EndZ=0
    g11: LineSegment StartX=112.583 StartY=-65 StartZ=0 EndX=112.583 EndY=65 EndZ=0
    g12: LineSegment StartX=112.583 StartY=65 StartZ=0 EndX=4.7e-15 EndY=130 EndZ=0
    g13: Circle [constr] CenterX=0 CenterY=0 CenterZ=0 NormalX=0 NormalY=0 NormalZ=1 AngleXU=0 Radius=130
  constraints (32):
    c: Coincident(g0,g1)
    c: Coincident(g1,g2)
    c: Coincident(g2,g3)
    c: Coincident(g3,g4)
    c: Coincident(g4,g5)
    c: Coincident(g5,g0)
    c: Equal(g0, g1-g5) x5
    c: PointOnObject(g0,g6)
    c: PointOnObject(g1,g6)
    c: PointOnObject(g2,g6)
    c: PointOnObject(g3,g6)
    c: PointOnObject(g4,g6)
    c: PointOnObject(g5,g6)
    c: Coincident(g6,g-1)
    c: PointOnObject(g5,g-2)
    c: Diameter(g6) = 245
    c: Coincident(g7,g8)
    c: Coincident(g8,g9)
    c: Coincident(g9,g10)
    c: Coincident(g10,g11)
    c: Coincident(g11,g12)
    c: Coincident(g12,g7)
    c: Equal(g7, g8-g12) x5
    c: PointOnObject(g7,g13)
    c: PointOnObject(g8,g13)
    c: PointOnObject(g9,g13)
    c: PointOnObject(g10,g13)
    c: PointOnObject(g11,g13)
    c: PointOnObject(g12,g13)
    c: Coincident(g13,g6)
    c: PointOnObject(g12,g-2)
    c: Diameter(g13) = 260
FEATURE [Part::Extrusion] Extrude385  label="hexShellinner"
  Base = -> Sketch393
  Dir = (0,-1,2e-16)
  DirMode = 2
  FaceMakerClass = Part::FaceMakerBullseye
  FaceMakerMode = 3
  LengthFwd = 10
  LengthRev = 0
  Placement = pos=(0,-125,0) rot=(0,0,1;0rad)
  Solid = true
  Symmetric = false
FEATURE [Sketcher::SketchObject] Sketch394
  ArcFitTolerance = 1e-06
  FullyConstrained = true
  MakeInternals = false
  Placement = pos=(0,0,0) rot=(1,0,0;1.5708rad)
  sketch-geometry (49):
    g0: LineSegment StartX=1e-16 StartY=3.5 StartZ=0 EndX=-3.03109 EndY=1.75 EndZ=0
    g1: LineSegment StartX=-3.03109 StartY=1.75 StartZ=0 EndX=-3.03109 EndY=-1.75 EndZ=0
    g2: LineSegment StartX=-3.03109 StartY=-1.75 StartZ=0 EndX=-1e-16 EndY=-3.5 EndZ=0
    g3: LineSegment StartX=-1e-16 StartY=-3.5 StartZ=0 EndX=3.03109 EndY=-1.75 EndZ=0
    g4: LineSegment StartX=3.03109 StartY=-1.75 StartZ=0 EndX=3.03109 EndY=1.75 EndZ=0
    g5: LineSegment StartX=3.03109 StartY=1.75 StartZ=0 EndX=1e-16 EndY=3.5 EndZ=0
    g6: Circle [constr] CenterX=0 CenterY=0 CenterZ=0 NormalX=0 NormalY=0 NormalZ=1 AngleXU=0 Radius=3.5
    g7: LineSegment StartX=4.96892 StartY=-1.75002 StartZ=0 EndX=8.00002 EndY=-3.5 EndZ=0
    g8: LineSegment StartX=8.00002 StartY=-3.5 StartZ=0 EndX=11.0311 EndY=-1.74998 EndZ=0
    g9: LineSegment StartX=11.0311 StartY=-1.74998 StartZ=0 EndX=11.0311 EndY=1.75002 EndZ=0
    g10: LineSegment StartX=11.0311 StartY=1.75002 StartZ=0 EndX=7.99998 EndY=3.5 EndZ=0
    g11: LineSegment StartX=7.99998 StartY=3.5 StartZ=0 EndX=4.9689 EndY=1.74998 EndZ=0
    g12: LineSegment StartX=4.9689 StartY=1.74998 StartZ=0 EndX=4.96892 EndY=-1.75002 EndZ=0
    g13: Circle [constr] CenterX=8 CenterY=0 CenterZ=0 NormalX=0 NormalY=0 NormalZ=1 AngleXU=0 Radius=3.5
    g14: LineSegment StartX=4.03109 StartY=3.5 StartZ=0 EndX=7.06218 EndY=5.25 EndZ=0
    g15: LineSegment StartX=7.06218 StartY=5.25 StartZ=0 EndX=7.06218 EndY=8.75 EndZ=0
    g16: LineSegment StartX=7.06218 StartY=8.75 StartZ=0 EndX=4.03109 EndY=10.5 EndZ=0
    g17: LineSegment StartX=4.03109 StartY=10.5 StartZ=0 EndX=1 EndY=8.75 EndZ=0
    g18: LineSegment StartX=1 StartY=8.75 StartZ=0 EndX=1 EndY=5.25 EndZ=0
    g19: LineSegment StartX=1 StartY=5.25 StartZ=0 EndX=4.03109 EndY=3.5 EndZ=0
    g20: Circle [constr] CenterX=4.03109 CenterY=7 CenterZ=0 NormalX=0 NormalY=0 NormalZ=1 AngleXU=0 Radius=3.5
    g21: LineSegment StartX=-1 StartY=5.25 StartZ=0 EndX=-1 EndY=8.75 EndZ=0
    g22: LineSegment StartX=-1 StartY=8.75 StartZ=0 EndX=-4.03109 EndY=10.5 EndZ=0
    g23: LineSegment StartX=-4.03109 StartY=10.5 StartZ=0 EndX=-7.06218 EndY=8.75 EndZ=0
    g24: LineSegment StartX=-7.06218 StartY=8.75 StartZ=0 EndX=-7.06218 EndY=5.25 EndZ=0
    g25: LineSegment StartX=-7.06218 StartY=5.25 StartZ=0 EndX=-4.03109 EndY=3.5 EndZ=0
    g26: LineSegment StartX=-4.03109 StartY=3.5 StartZ=0 EndX=-1 EndY=5.25 EndZ=0
    g27: Circle [constr] CenterX=-4.03109 CenterY=7 CenterZ=0 NormalX=0 NormalY=0 NormalZ=1 AngleXU=0 Radius=3.5
    g28: LineSegment StartX=-4.96891 StartY=-1.75 StartZ=0 EndX=-4.96891 EndY=1.75 EndZ=0
    g29: LineSegment StartX=-4.96891 StartY=1.75 StartZ=0 EndX=-8 EndY=3.5 EndZ=0
    g30: LineSegment StartX=-8 StartY=3.5 StartZ=0 EndX=-11.0311 EndY=1.75 EndZ=0
    g31: LineSegment StartX=-11.0311 StartY=1.75 StartZ=0 EndX=-11.0311 EndY=-1.75 EndZ=0
    g32: LineSegment StartX=-11.0311 StartY=-1.75 StartZ=0 EndX=-8 EndY=-3.5 EndZ=0
    g33: LineSegment StartX=-8 StartY=-3.5 StartZ=0 EndX=-4.96891 EndY=-1.75 EndZ=0
    g34: Circle [constr] CenterX=-8 CenterY=0 CenterZ=0 NormalX=0 NormalY=0 NormalZ=1 AngleXU=0 Radius=3.5
    g35: LineSegment StartX=-4.03109 StartY=-3.5 StartZ=0 EndX=-7.06218 EndY=-5.25 EndZ=0
    g36: LineSegment StartX=-7.06218 StartY=-5.25 StartZ=0 EndX=-7.06218 EndY=-8.75 EndZ=0
    g37: LineSegment StartX=-7.06218 StartY=-8.75 StartZ=0 EndX=-4.03109 EndY=-10.5 EndZ=0
    g38: LineSegment StartX=-4.03109 StartY=-10.5 StartZ=0 EndX=-1 EndY=-8.75 EndZ=0
    g39: LineSegment StartX=-1 StartY=-8.75 StartZ=0 EndX=-1 EndY=-5.25 EndZ=0
    g40: LineSegment StartX=-1 StartY=-5.25 StartZ=0 EndX=-4.03109 EndY=-3.5 EndZ=0
    g41: Circle [constr] CenterX=-4.03109 CenterY=-7 CenterZ=0 NormalX=0 NormalY=0 NormalZ=1 AngleXU=0 Radius=3.5
    g42: LineSegment StartX=4.03109 StartY=-3.5 StartZ=0 EndX=1 EndY=-5.25 EndZ=0
    g43: LineSegment StartX=1 StartY=-5.25 StartZ=0 EndX=1 EndY=-8.75 EndZ=0
    g44: LineSegment StartX=1 StartY=-8.75 StartZ=0 EndX=4.03109 EndY=-10.5 EndZ=0
    g45: LineSegment StartX=4.03109 StartY=-10.5 StartZ=0 EndX=7.06218 EndY=-8.75 EndZ=0
    g46: LineSegment StartX=7.06218 StartY=-8.75 StartZ=0 EndX=7.06218 EndY=-5.25 EndZ=0
    g47: LineSegment StartX=7.06218 StartY=-5.25 StartZ=0 EndX=4.03109 EndY=-3.5 EndZ=0
    g48: Circle [constr] CenterX=4.03109 CenterY=-7 CenterZ=0 NormalX=0 NormalY=0 NormalZ=1 AngleXU=0 Radius=3.5
  constraints (117):
    c: Coincident(g0,g1)
    c: Coincident(g1,g2)
    c: Coincident(g2,g3)
    c: Coincident(g3,g4)
    c: Coincident(g4,g5)
    c: Coincident(g5,g0)
    c: Equal(g0, g1-g5) x5
    c: PointOnObject(g0,g6)
    c: PointOnObject(g1,g6)
    c: PointOnObject(g2,g6)
    c: PointOnObject(g3,g6)
    c: PointOnObject(g4,g6)
    c: PointOnObject(g5,g6)
    c: Coincident(g6,g-1)
    c: Diameter(g6) = 7
    c: PointOnObject(g0,g-2)
    c: Coincident(g7,g8)
    c: Coincident(g8,g9)
    c: Coincident(g9,g10)
    c: Coincident(g10,g11)
    c: Coincident(g11,g12)
    c: Coincident(g12,g7)
    c: Equal(g7, g8-g12) x5
    c: PointOnObject(g7,g13)
    c: PointOnObject(g8,g13)
    c: PointOnObject(g9,g13)
    c: PointOnObject(g10,g13)
    c: PointOnObject(g11,g13)
    c: PointOnObject(g12,g13)
    c: PointOnObject(g13,g-1)
    c: Diameter(g13) = 7
    c: Distance(g6,g13) = 8
    c: Horizontal(g0,g10)
    c: Coincident(g14,g15)
    c: Coincident(g15,g16)
    c: Coincident(g16,g17)
    c: Coincident(g17,g18)
    c: Coincident(g18,g19)
    c: Coincident(g19,g14)
    c: Equal(g14, g15-g19) x5
    c: PointOnObject(g14,g20)
    c: PointOnObject(g15,g20)
    c: PointOnObject(g16,g20)
    c: PointOnObject(g17,g20)
    c: PointOnObject(g18,g20)
    c: PointOnObject(g19,g20)
    c: Diameter(g20) = 7
    c: DistanceY(g-1,g20) = 7
    c: Vertical(g18)
    c: Distance(g17,g-2) = 1
    c: Coincident(g21,g22)
    c: Coincident(g22,g23)
    c: Coincident(g23,g24)
    c: Coincident(g24,g25)
    c: Coincident(g25,g26)
    c: Coincident(g26,g21)
    c: Equal(g21, g22-g26) x5
    c: PointOnObject(g21,g27)
    c: PointOnObject(g22,g27)
    c: PointOnObject(g23,g27)
    c: PointOnObject(g24,g27)
    c: PointOnObject(g25,g27)
    c: PointOnObject(g26,g27)
    c: Diameter(g27) = 7
    c: DistanceY(g-1,g27) = 7
    c: DistanceX(g21,g-1) = 1
    c: Vertical(g21)
    c: Coincident(g28,g29)
    c: Coincident(g29,g30)
    c: Coincident(g30,g31)
    c: Coincident(g31,g32)
    c: Coincident(g32,g33)
    c: Coincident(g33,g28)
    c: Equal(g28, g29-g33) x5
    c: PointOnObject(g28,g34)
    c: PointOnObject(g29,g34)
    c: PointOnObject(g30,g34)
    c: PointOnObject(g31,g34)
    c: PointOnObject(g32,g34)
    c: PointOnObject(g33,g34)
    c: PointOnObject(g34,g-1)
    c: Diameter(g34) = 7
    c: Vertical(g31)
    c: DistanceX(g34,g-1) = 8
    c: Coincident(g35,g36)
    c: Coincident(g36,g37)
    c: Coincident(g37,g38)
    c: Coincident(g38,g39)
    c: Coincident(g39,g40)
    c: Coincident(g40,g35)
    c: Equal(g35, g36-g40) x5
    c: PointOnObject(g35,g41)
    c: PointOnObject(g36,g41)
    c: PointOnObject(g37,g41)
    c: PointOnObject(g38,g41)
    c: PointOnObject(g39,g41)
    c: PointOnObject(g40,g41)
    c: Coincident(g42,g43)
    c: Coincident(g43,g44)
    c: Coincident(g44,g45)
    c: Coincident(g45,g46)
    c: Coincident(g46,g47)
    c: Coincident(g47,g42)
    c: Equal(g42, g43-g47) x5
    c: PointOnObject(g42,g48)
    c: PointOnObject(g43,g48)
    c: PointOnObject(g44,g48)
    c: PointOnObject(g45,g48)
    c: PointOnObject(g46,g48)
    c: PointOnObject(g47,g48)
    c: Equal(g41,g48)
    c: Diameter(g41) = 7
    c: Vertical(g39)
    c: Vertical(g43)
    c: Distance(g-2,g39) = 1
    c: Symmetric(g38,g43,g-2)
    c: Distance(g41,g-1) = 7
FEATURE [Part::Extrusion] Extrude386  label="hex1"
  Base = -> Sketch394
  Dir = (0,-1,2e-16)
  DirMode = 2
  FaceMakerClass = Part::FaceMakerBullseye
  FaceMakerMode = 3
  LengthFwd = 10
  LengthRev = 0
  Solid = true
  Symmetric = false
FEATURE [Sketcher::SketchObject] Sketch395
  ArcFitTolerance = 1e-06
  FullyConstrained = true
  MakeInternals = false
  Placement = pos=(0,0,0) rot=(1,0,0;1.5708rad)
  sketch-geometry (49):
    g0: LineSegment StartX=1e-16 StartY=3.5 StartZ=0 EndX=-3.03109 EndY=1.75 EndZ=0
    g1: LineSegment StartX=-3.03109 StartY=1.75 StartZ=0 EndX=-3.03109 EndY=-1.75 EndZ=0
    g2: LineSegment StartX=-3.03109 StartY=-1.75 StartZ=0 EndX=-1e-16 EndY=-3.5 EndZ=0
    g3: LineSegment StartX=-1e-16 StartY=-3.5 StartZ=0 EndX=3.03109 EndY=-1.75 EndZ=0
    g4: LineSegment StartX=3.03109 StartY=-1.75 StartZ=0 EndX=3.03109 EndY=1.75 EndZ=0
    g5: LineSegment StartX=3.03109 StartY=1.75 StartZ=0 EndX=1e-16 EndY=3.5 EndZ=0
    g6: Circle [constr] CenterX=0 CenterY=0 CenterZ=0 NormalX=0 NormalY=0 NormalZ=1 AngleXU=0 Radius=3.5
    g7: LineSegment StartX=4.96892 StartY=-1.75002 StartZ=0 EndX=8.00002 EndY=-3.5 EndZ=0
    g8: LineSegment StartX=8.00002 StartY=-3.5 StartZ=0 EndX=11.0311 EndY=-1.74998 EndZ=0
    g9: LineSegment StartX=11.0311 StartY=-1.74998 StartZ=0 EndX=11.0311 EndY=1.75002 EndZ=0
    g10: LineSegment StartX=11.0311 StartY=1.75002 StartZ=0 EndX=7.99998 EndY=3.5 EndZ=0
    g11: LineSegment StartX=7.99998 StartY=3.5 StartZ=0 EndX=4.9689 EndY=1.74998 EndZ=0
    g12: LineSegment StartX=4.9689 StartY=1.74998 StartZ=0 EndX=4.96892 EndY=-1.75002 EndZ=0
    g13: Circle [constr] CenterX=8 CenterY=0 CenterZ=0 NormalX=0 NormalY=0 NormalZ=1 AngleXU=0 Radius=3.5
    g14: LineSegment StartX=4.03109 StartY=3.5 StartZ=0 EndX=7.06218 EndY=5.25 EndZ=0
    g15: LineSegment StartX=7.06218 StartY=5.25 StartZ=0 EndX=7.06218 EndY=8.75 EndZ=0
    g16: LineSegment StartX=7.06218 StartY=8.75 StartZ=0 EndX=4.03109 EndY=10.5 EndZ=0
    g17: LineSegment StartX=4.03109 StartY=10.5 StartZ=0 EndX=1 EndY=8.75 EndZ=0
    g18: LineSegment StartX=1 StartY=8.75 StartZ=0 EndX=1 EndY=5.25 EndZ=0
    g19: LineSegment StartX=1 StartY=5.25 StartZ=0 EndX=4.03109 EndY=3.5 EndZ=0
    g20: Circle [constr] CenterX=4.03109 CenterY=7 CenterZ=0 NormalX=0 NormalY=0 NormalZ=1 AngleXU=0 Radius=3.5
    g21: LineSegment StartX=-1 StartY=5.25 StartZ=0 EndX=-1 EndY=8.75 EndZ=0
    g22: LineSegment StartX=-1 StartY=8.75 StartZ=0 EndX=-4.03109 EndY=10.5 EndZ=0
    g23: LineSegment StartX=-4.03109 StartY=10.5 StartZ=0 EndX=-7.06218 EndY=8.75 EndZ=0
    g24: LineSegment StartX=-7.06218 StartY=8.75 StartZ=0 EndX=-7.06218 EndY=5.25 EndZ=0
    g25: LineSegment StartX=-7.06218 StartY=5.25 StartZ=0 EndX=-4.03109 EndY=3.5 EndZ=0
    g26: LineSegment StartX=-4.03109 StartY=3.5 StartZ=0 EndX=-1 EndY=5.25 EndZ=0
    g27: Circle [constr] CenterX=-4.03109 CenterY=7 CenterZ=0 NormalX=0 NormalY=0 NormalZ=1 AngleXU=0 Radius=3.5
    g28: LineSegment StartX=-4.96891 StartY=-1.75 StartZ=0 EndX=-4.96891 EndY=1.75 EndZ=0
    g29: LineSegment StartX=-4.96891 StartY=1.75 StartZ=0 EndX=-8 EndY=3.5 EndZ=0
    g30: LineSegment StartX=-8 StartY=3.5 StartZ=0 EndX=-11.0311 EndY=1.75 EndZ=0
    g31: LineSegment StartX=-11.0311 StartY=1.75 StartZ=0 EndX=-11.0311 EndY=-1.75 EndZ=0
    g32: LineSegment StartX=-11.0311 StartY=-1.75 StartZ=0 EndX=-8 EndY=-3.5 EndZ=0
    g33: LineSegment StartX=-8 StartY=-3.5 StartZ=0 EndX=-4.96891 EndY=-1.75 EndZ=0
    g34: Circle [constr] CenterX=-8 CenterY=0 CenterZ=0 NormalX=0 NormalY=0 NormalZ=1 AngleXU=0 Radius=3.5
    g35: LineSegment StartX=-4.03109 StartY=-3.5 StartZ=0 EndX=-7.06218 EndY=-5.25 EndZ=0
    g36: LineSegment StartX=-7.06218 StartY=-5.25 StartZ=0 EndX=-7.06218 EndY=-8.75 EndZ=0
    g37: LineSegment StartX=-7.06218 StartY=-8.75 StartZ=0 EndX=-4.03109 EndY=-10.5 EndZ=0
    g38: LineSegment StartX=-4.03109 StartY=-10.5 StartZ=0 EndX=-1 EndY=-8.75 EndZ=0
    g39: LineSegment StartX=-1 StartY=-8.75 StartZ=0 EndX=-1 EndY=-5.25 EndZ=0
    g40: LineSegment StartX=-1 StartY=-5.25 StartZ=0 EndX=-4.03109 EndY=-3.5 EndZ=0
    g41: Circle [constr] CenterX=-4.03109 CenterY=-7 CenterZ=0 NormalX=0 NormalY=0 NormalZ=1 AngleXU=0 Radius=3.5
    g42: LineSegment StartX=4.03109 StartY=-3.5 StartZ=0 EndX=1 EndY=-5.25 EndZ=0
    g43: LineSegment StartX=1 StartY=-5.25 StartZ=0 EndX=1 EndY=-8.75 EndZ=0
    g44: LineSegment StartX=1 StartY=-8.75 StartZ=0 EndX=4.03109 EndY=-10.5 EndZ=0
    g45: LineSegment StartX=4.03109 StartY=-10.5 StartZ=0 EndX=7.06218 EndY=-8.75 EndZ=0
    g46: LineSegment StartX=7.06218 StartY=-8.75 StartZ=0 EndX=7.06218 EndY=-5.25 EndZ=0
    g47: LineSegment StartX=7.06218 StartY=-5.25 StartZ=0 EndX=4.03109 EndY=-3.5 EndZ=0
    g48: Circle [constr] CenterX=4.03109 CenterY=-7 CenterZ=0 NormalX=0 NormalY=0 NormalZ=1 AngleXU=0 Radius=3.5
  constraints (117):
    c: Coincident(g0,g1)
    c: Coincident(g1,g2)
    c: Coincident(g2,g3)
    c: Coincident(g3,g4)
    c: Coincident(g4,g5)
    c: Coincident(g5,g0)
    c: Equal(g0, g1-g5) x5
    c: PointOnObject(g0,g6)
    c: PointOnObject(g1,g6)
    c: PointOnObject(g2,g6)
    c: PointOnObject(g3,g6)
    c: PointOnObject(g4,g6)
    c: PointOnObject(g5,g6)
    c: Coincident(g6,g-1)
    c: Diameter(g6) = 7
    c: PointOnObject(g0,g-2)
    c: Coincident(g7,g8)
    c: Coincident(g8,g9)
    c: Coincident(g9,g10)
    c: Coincident(g10,g11)
    c: Coincident(g11,g12)
    c: Coincident(g12,g7)
    c: Equal(g7, g8-g12) x5
    c: PointOnObject(g7,g13)
    c: PointOnObject(g8,g13)
    c: PointOnObject(g9,g13)
    c: PointOnObject(g10,g13)
    c: PointOnObject(g11,g13)
    c: PointOnObject(g12,g13)
    c: PointOnObject(g13,g-1)
    c: Diameter(g13) = 7
    c: Distance(g6,g13) = 8
    c: Horizontal(g0,g10)
    c: Coincident(g14,g15)
    c: Coincident(g15,g16)
    c: Coincident(g16,g17)
    c: Coincident(g17,g18)
    c: Coincident(g18,g19)
    c: Coincident(g19,g14)
    c: Equal(g14, g15-g19) x5
    c: PointOnObject(g14,g20)
    c: PointOnObject(g15,g20)
    c: PointOnObject(g16,g20)
    c: PointOnObject(g17,g20)
    c: PointOnObject(g18,g20)
    c: PointOnObject(g19,g20)
    c: Diameter(g20) = 7
    c: DistanceY(g-1,g20) = 7
    c: Vertical(g18)
    c: Distance(g17,g-2) = 1
    c: Coincident(g21,g22)
    c: Coincident(g22,g23)
    c: Coincident(g23,g24)
    c: Coincident(g24,g25)
    c: Coincident(g25,g26)
    c: Coincident(g26,g21)
    c: Equal(g21, g22-g26) x5
    c: PointOnObject(g21,g27)
    c: PointOnObject(g22,g27)
    c: PointOnObject(g23,g27)
    c: PointOnObject(g24,g27)
    c: PointOnObject(g25,g27)
    c: PointOnObject(g26,g27)
    c: Diameter(g27) = 7
    c: DistanceY(g-1,g27) = 7
    c: DistanceX(g21,g-1) = 1
    c: Vertical(g21)
    c: Coincident(g28,g29)
    c: Coincident(g29,g30)
    c: Coincident(g30,g31)
    c: Coincident(g31,g32)
    c: Coincident(g32,g33)
    c: Coincident(g33,g28)
    c: Equal(g28, g29-g33) x5
    c: PointOnObject(g28,g34)
    c: PointOnObject(g29,g34)
    c: PointOnObject(g30,g34)
    c: PointOnObject(g31,g34)
    c: PointOnObject(g32,g34)
    c: PointOnObject(g33,g34)
    c: PointOnObject(g34,g-1)
    c: Diameter(g34) = 7
    c: Vertical(g31)
    c: DistanceX(g34,g-1) = 8
    c: Coincident(g35,g36)
    c: Coincident(g36,g37)
    c: Coincident(g37,g38)
    c: Coincident(g38,g39)
    c: Coincident(g39,g40)
    c: Coincident(g40,g35)
    c: Equal(g35, g36-g40) x5
    c: PointOnObject(g35,g41)
    c: PointOnObject(g36,g41)
    c: PointOnObject(g37,g41)
    c: PointOnObject(g38,g41)
    c: PointOnObject(g39,g41)
    c: PointOnObject(g40,g41)
    c: Coincident(g42,g43)
    c: Coincident(g43,g44)
    c: Coincident(g44,g45)
    c: Coincident(g45,g46)
    c: Coincident(g46,g47)
    c: Coincident(g47,g42)
    c: Equal(g42, g43-g47) x5
    c: PointOnObject(g42,g48)
    c: PointOnObject(g43,g48)
    c: PointOnObject(g44,g48)
    c: PointOnObject(g45,g48)
    c: PointOnObject(g46,g48)
    c: PointOnObject(g47,g48)
    c: Equal(g41,g48)
    c: Diameter(g41) = 7
    c: Vertical(g39)
    c: Vertical(g43)
    c: Distance(g-2,g39) = 1
    c: Symmetric(g38,g43,g-2)
    c: Distance(g41,g-1) = 7
FEATURE [Part::Extrusion] Extrude387  label="hex002"
  Base = -> Sketch395
  Dir = (0,-1,2e-16)
  DirMode = 2
  FaceMakerClass = Part::FaceMakerBullseye
  FaceMakerMode = 3
  LengthFwd = 10
  LengthRev = 0
  Placement = pos=(20,0,-7) rot=(0,0,1;0rad)
  Solid = true
  Symmetric = false
FEATURE [Sketcher::SketchObject] Sketch396
  ArcFitTolerance = 1e-06
  FullyConstrained = true
  MakeInternals = false
  Placement = pos=(0,0,0) rot=(1,0,0;1.5708rad)
  sketch-geometry (49):
    g0: LineSegment StartX=1e-16 StartY=3.5 StartZ=0 EndX=-3.03109 EndY=1.75 EndZ=0
    g1: LineSegment StartX=-3.03109 StartY=1.75 StartZ=0 EndX=-3.03109 EndY=-1.75 EndZ=0
    g2: LineSegment StartX=-3.03109 StartY=-1.75 StartZ=0 EndX=-1e-16 EndY=-3.5 EndZ=0
    g3: LineSegment StartX=-1e-16 StartY=-3.5 StartZ=0 EndX=3.03109 EndY=-1.75 EndZ=0
    g4: LineSegment StartX=3.03109 StartY=-1.75 StartZ=0 EndX=3.03109 EndY=1.75 EndZ=0
    g5: LineSegment StartX=3.03109 StartY=1.75 StartZ=0 EndX=1e-16 EndY=3.5 EndZ=0
    g6: Circle [constr] CenterX=0 CenterY=0 CenterZ=0 NormalX=0 NormalY=0 NormalZ=1 AngleXU=0 Radius=3.5
    g7: LineSegment StartX=4.96892 StartY=-1.75002 StartZ=0 EndX=8.00002 EndY=-3.5 EndZ=0
    g8: LineSegment StartX=8.00002 StartY=-3.5 StartZ=0 EndX=11.0311 EndY=-1.74998 EndZ=0
    g9: LineSegment StartX=11.0311 StartY=-1.74998 StartZ=0 EndX=11.0311 EndY=1.75002 EndZ=0
    g10: LineSegment StartX=11.0311 StartY=1.75002 StartZ=0 EndX=7.99998 EndY=3.5 EndZ=0
    g11: LineSegment StartX=7.99998 StartY=3.5 StartZ=0 EndX=4.9689 EndY=1.74998 EndZ=0
    g12: LineSegment StartX=4.9689 StartY=1.74998 StartZ=0 EndX=4.96892 EndY=-1.75002 EndZ=0
    g13: Circle [constr] CenterX=8 CenterY=0 CenterZ=0 NormalX=0 NormalY=0 NormalZ=1 AngleXU=0 Radius=3.5
    g14: LineSegment StartX=4.03109 StartY=3.5 StartZ=0 EndX=7.06218 EndY=5.25 EndZ=0
    g15: LineSegment StartX=7.06218 StartY=5.25 StartZ=0 EndX=7.06218 EndY=8.75 EndZ=0
    g16: LineSegment StartX=7.06218 StartY=8.75 StartZ=0 EndX=4.03109 EndY=10.5 EndZ=0
    g17: LineSegment StartX=4.03109 StartY=10.5 StartZ=0 EndX=1 EndY=8.75 EndZ=0
    g18: LineSegment StartX=1 StartY=8.75 StartZ=0 EndX=1 EndY=5.25 EndZ=0
    g19: LineSegment StartX=1 StartY=5.25 StartZ=0 EndX=4.03109 EndY=3.5 EndZ=0
    g20: Circle [constr] CenterX=4.03109 CenterY=7 CenterZ=0 NormalX=0 NormalY=0 NormalZ=1 AngleXU=0 Radius=3.5
    g21: LineSegment StartX=-1 StartY=5.25 StartZ=0 EndX=-1 EndY=8.75 EndZ=0
    g22: LineSegment StartX=-1 StartY=8.75 StartZ=0 EndX=-4.03109 EndY=10.5 EndZ=0
    g23: LineSegment StartX=-4.03109 StartY=10.5 StartZ=0 EndX=-7.06218 EndY=8.75 EndZ=0
    g24: LineSegment StartX=-7.06218 StartY=8.75 StartZ=0 EndX=-7.06218 EndY=5.25 EndZ=0
    g25: LineSegment StartX=-7.06218 StartY=5.25 StartZ=0 EndX=-4.03109 EndY=3.5 EndZ=0
    g26: LineSegment StartX=-4.03109 StartY=3.5 StartZ=0 EndX=-1 EndY=5.25 EndZ=0
    g27: Circle [constr] CenterX=-4.03109 CenterY=7 CenterZ=0 NormalX=0 NormalY=0 NormalZ=1 AngleXU=0 Radius=3.5
    g28: LineSegment StartX=-4.96891 StartY=-1.75 StartZ=0 EndX=-4.96891 EndY=1.75 EndZ=0
    g29: LineSegment StartX=-4.96891 StartY=1.75 StartZ=0 EndX=-8 EndY=3.5 EndZ=0
    g30: LineSegment StartX=-8 StartY=3.5 StartZ=0 EndX=-11.0311 EndY=1.75 EndZ=0
    g31: LineSegment StartX=-11.0311 StartY=1.75 StartZ=0 EndX=-11.0311 EndY=-1.75 EndZ=0
    g32: LineSegment StartX=-11.0311 StartY=-1.75 StartZ=0 EndX=-8 EndY=-3.5 EndZ=0
    g33: LineSegment StartX=-8 StartY=-3.5 StartZ=0 EndX=-4.96891 EndY=-1.75 EndZ=0
    g34: Circle [constr] CenterX=-8 CenterY=0 CenterZ=0 NormalX=0 NormalY=0 NormalZ=1 AngleXU=0 Radius=3.5
    g35: LineSegment StartX=-4.03109 StartY=-3.5 StartZ=0 EndX=-7.06218 EndY=-5.25 EndZ=0
    g36: LineSegment StartX=-7.06218 StartY=-5.25 StartZ=0 EndX=-7.06218 EndY=-8.75 EndZ=0
    g37: LineSegment StartX=-7.06218 StartY=-8.75 StartZ=0 EndX=-4.03109 EndY=-10.5 EndZ=0
    g38: LineSegment StartX=-4.03109 StartY=-10.5 StartZ=0 EndX=-1 EndY=-8.75 EndZ=0
    g39: LineSegment StartX=-1 StartY=-8.75 StartZ=0 EndX=-1 EndY=-5.25 EndZ=0
    g40: LineSegment StartX=-1 StartY=-5.25 StartZ=0 EndX=-4.03109 EndY=-3.5 EndZ=0
    g41: Circle [constr] CenterX=-4.03109 CenterY=-7 CenterZ=0 NormalX=0 NormalY=0 NormalZ=1 AngleXU=0 Radius=3.5
    g42: LineSegment StartX=4.03109 StartY=-3.5 StartZ=0 EndX=1 EndY=-5.25 EndZ=0
    g43: LineSegment StartX=1 StartY=-5.25 StartZ=0 EndX=1 EndY=-8.75 EndZ=0
    g44: LineSegment StartX=1 StartY=-8.75 StartZ=0 EndX=4.03109 EndY=-10.5 EndZ=0
    g45: LineSegment StartX=4.03109 StartY=-10.5 StartZ=0 EndX=7.06218 EndY=-8.75 EndZ=0
    g46: LineSegment StartX=7.06218 StartY=-8.75 StartZ=0 EndX=7.06218 EndY=-5.25 EndZ=0
    g47: LineSegment StartX=7.06218 StartY=-5.25 StartZ=0 EndX=4.03109 EndY=-3.5 EndZ=0
    g48: Circle [constr] CenterX=4.03109 CenterY=-7 CenterZ=0 NormalX=0 NormalY=0 NormalZ=1 AngleXU=0 Radius=3.5
  constraints (117):
    c: Coincident(g0,g1)
    c: Coincident(g1,g2)
    c: Coincident(g2,g3)
    c: Coincident(g3,g4)
    c: Coincident(g4,g5)
    c: Coincident(g5,g0)
    c: Equal(g0, g1-g5) x5
    c: PointOnObject(g0,g6)
    c: PointOnObject(g1,g6)
    c: PointOnObject(g2,g6)
    c: PointOnObject(g3,g6)
    c: PointOnObject(g4,g6)
    c: PointOnObject(g5,g6)
    c: Coincident(g6,g-1)
    c: Diameter(g6) = 7
    c: PointOnObject(g0,g-2)
    c: Coincident(g7,g8)
    c: Coincident(g8,g9)
    c: Coincident(g9,g10)
    c: Coincident(g10,g11)
    c: Coincident(g11,g12)
    c: Coincident(g12,g7)
    c: Equal(g7, g8-g12) x5
    c: PointOnObject(g7,g13)
    c: PointOnObject(g8,g13)
    c: PointOnObject(g9,g13)
    c: PointOnObject(g10,g13)
    c: PointOnObject(g11,g13)
    c: PointOnObject(g12,g13)
    c: PointOnObject(g13,g-1)
    c: Diameter(g13) = 7
    c: Distance(g6,g13) = 8
    c: Horizontal(g0,g10)
    c: Coincident(g14,g15)
    c: Coincident(g15,g16)
    c: Coincident(g16,g17)
    c: Coincident(g17,g18)
    c: Coincident(g18,g19)
    c: Coincident(g19,g14)
    c: Equal(g14, g15-g19) x5
    c: PointOnObject(g14,g20)
    c: PointOnObject(g15,g20)
    c: PointOnObject(g16,g20)
    c: PointOnObject(g17,g20)
    c: PointOnObject(g18,g20)
    c: PointOnObject(g19,g20)
    c: Diameter(g20) = 7
    c: DistanceY(g-1,g20) = 7
    c: Vertical(g18)
    c: Distance(g17,g-2) = 1
    c: Coincident(g21,g22)
    c: Coincident(g22,g23)
    c: Coincident(g23,g24)
    c: Coincident(g24,g25)
    c: Coincident(g25,g26)
    c: Coincident(g26,g21)
    c: Equal(g21, g22-g26) x5
    c: PointOnObject(g21,g27)
    c: PointOnObject(g22,g27)
    c: PointOnObject(g23,g27)
    c: PointOnObject(g24,g27)
    c: PointOnObject(g25,g27)
    c: PointOnObject(g26,g27)
    c: Diameter(g27) = 7
    c: DistanceY(g-1,g27) = 7
    c: DistanceX(g21,g-1) = 1
    c: Vertical(g21)
    c: Coincident(g28,g29)
    c: Coincident(g29,g30)
    c: Coincident(g30,g31)
    c: Coincident(g31,g32)
    c: Coincident(g32,g33)
    c: Coincident(g33,g28)
    c: Equal(g28, g29-g33) x5
    c: PointOnObject(g28,g34)
    c: PointOnObject(g29,g34)
    c: PointOnObject(g30,g34)
    c: PointOnObject(g31,g34)
    c: PointOnObject(g32,g34)
    c: PointOnObject(g33,g34)
    c: PointOnObject(g34,g-1)
    c: Diameter(g34) = 7
    c: Vertical(g31)
    c: DistanceX(g34,g-1) = 8
    c: Coincident(g35,g36)
    c: Coincident(g36,g37)
    c: Coincident(g37,g38)
    c: Coincident(g38,g39)
    c: Coincident(g39,g40)
    c: Coincident(g40,g35)
    c: Equal(g35, g36-g40) x5
    c: PointOnObject(g35,g41)
    c: PointOnObject(g36,g41)
    c: PointOnObject(g37,g41)
    c: PointOnObject(g38,g41)
    c: PointOnObject(g39,g41)
    c: PointOnObject(g40,g41)
    c: Coincident(g42,g43)
    c: Coincident(g43,g44)
    c: Coincident(g44,g45)
    c: Coincident(g45,g46)
    c: Coincident(g46,g47)
    c: Coincident(g47,g42)
    c: Equal(g42, g43-g47) x5
    c: PointOnObject(g42,g48)
    c: PointOnObject(g43,g48)
    c: PointOnObject(g44,g48)
    c: PointOnObject(g45,g48)
    c: PointOnObject(g46,g48)
    c: PointOnObject(g47,g48)
    c: Equal(g41,g48)
    c: Diameter(g41) = 7
    c: Vertical(g39)
    c: Vertical(g43)
    c: Distance(g-2,g39) = 1
    c: Symmetric(g38,g43,g-2)
    c: Distance(g41,g-1) = 7
FEATURE [Part::Extrusion] Extrude388  label="hex003"
  Base = -> Sketch396
  Dir = (0,-1,2e-16)
  DirMode = 2
  FaceMakerClass = Part::FaceMakerBullseye
  FaceMakerMode = 3
  LengthFwd = 10
  LengthRev = 0
  Placement = pos=(16,0,14) rot=(0,0,1;0rad)
  Solid = true
  Symmetric = false
FEATURE [Sketcher::SketchObject] Sketch397
  ArcFitTolerance = 1e-06
  FullyConstrained = true
  MakeInternals = false
  Placement = pos=(0,0,0) rot=(1,0,0;1.5708rad)
  sketch-geometry (49):
    g0: LineSegment StartX=1e-16 StartY=3.5 StartZ=0 EndX=-3.03109 EndY=1.75 EndZ=0
    g1: LineSegment StartX=-3.03109 StartY=1.75 StartZ=0 EndX=-3.03109 EndY=-1.75 EndZ=0
    g2: LineSegment StartX=-3.03109 StartY=-1.75 StartZ=0 EndX=-1e-16 EndY=-3.5 EndZ=0
    g3: LineSegment StartX=-1e-16 StartY=-3.5 StartZ=0 EndX=3.03109 EndY=-1.75 EndZ=0
    g4: LineSegment StartX=3.03109 StartY=-1.75 StartZ=0 EndX=3.03109 EndY=1.75 EndZ=0
    g5: LineSegment StartX=3.03109 StartY=1.75 StartZ=0 EndX=1e-16 EndY=3.5 EndZ=0
    g6: Circle [constr] CenterX=0 CenterY=0 CenterZ=0 NormalX=0 NormalY=0 NormalZ=1 AngleXU=0 Radius=3.5
    g7: LineSegment StartX=4.96892 StartY=-1.75002 StartZ=0 EndX=8.00002 EndY=-3.5 EndZ=0
    g8: LineSegment StartX=8.00002 StartY=-3.5 StartZ=0 EndX=11.0311 EndY=-1.74998 EndZ=0
    g9: LineSegment StartX=11.0311 StartY=-1.74998 StartZ=0 EndX=11.0311 EndY=1.75002 EndZ=0
    g10: LineSegment StartX=11.0311 StartY=1.75002 StartZ=0 EndX=7.99998 EndY=3.5 EndZ=0
    g11: LineSegment StartX=7.99998 StartY=3.5 StartZ=0 EndX=4.9689 EndY=1.74998 EndZ=0
    g12: LineSegment StartX=4.9689 StartY=1.74998 StartZ=0 EndX=4.96892 EndY=-1.75002 EndZ=0
    g13: Circle [constr] CenterX=8 CenterY=0 CenterZ=0 NormalX=0 NormalY=0 NormalZ=1 AngleXU=0 Radius=3.5
    g14: LineSegment StartX=4.03109 StartY=3.5 StartZ=0 EndX=7.06218 EndY=5.25 EndZ=0
    g15: LineSegment StartX=7.06218 StartY=5.25 StartZ=0 EndX=7.06218 EndY=8.75 EndZ=0
    g16: LineSegment StartX=7.06218 StartY=8.75 StartZ=0 EndX=4.03109 EndY=10.5 EndZ=0
    g17: LineSegment StartX=4.03109 StartY=10.5 StartZ=0 EndX=1 EndY=8.75 EndZ=0
    g18: LineSegment StartX=1 StartY=8.75 StartZ=0 EndX=1 EndY=5.25 EndZ=0
    g19: LineSegment StartX=1 StartY=5.25 StartZ=0 EndX=4.03109 EndY=3.5 EndZ=0
    g20: Circle [constr] CenterX=4.03109 CenterY=7 CenterZ=0 NormalX=0 NormalY=0 NormalZ=1 AngleXU=0 Radius=3.5
    g21: LineSegment StartX=-1 StartY=5.25 StartZ=0 EndX=-1 EndY=8.75 EndZ=0
    g22: LineSegment StartX=-1 StartY=8.75 StartZ=0 EndX=-4.03109 EndY=10.5 EndZ=0
    g23: LineSegment StartX=-4.03109 StartY=10.5 StartZ=0 EndX=-7.06218 EndY=8.75 EndZ=0
    g24: LineSegment StartX=-7.06218 StartY=8.75 StartZ=0 EndX=-7.06218 EndY=5.25 EndZ=0
    g25: LineSegment StartX=-7.06218 StartY=5.25 StartZ=0 EndX=-4.03109 EndY=3.5 EndZ=0
    g26: LineSegment StartX=-4.03109 StartY=3.5 StartZ=0 EndX=-1 EndY=5.25 EndZ=0
    g27: Circle [constr] CenterX=-4.03109 CenterY=7 CenterZ=0 NormalX=0 NormalY=0 NormalZ=1 AngleXU=0 Radius=3.5
    g28: LineSegment StartX=-4.96891 StartY=-1.75 StartZ=0 EndX=-4.96891 EndY=1.75 EndZ=0
    g29: LineSegment StartX=-4.96891 StartY=1.75 StartZ=0 EndX=-8 EndY=3.5 EndZ=0
    g30: LineSegment StartX=-8 StartY=3.5 StartZ=0 EndX=-11.0311 EndY=1.75 EndZ=0
    g31: LineSegment StartX=-11.0311 StartY=1.75 StartZ=0 EndX=-11.0311 EndY=-1.75 EndZ=0
    g32: LineSegment StartX=-11.0311 StartY=-1.75 StartZ=0 EndX=-8 EndY=-3.5 EndZ=0
    g33: LineSegment StartX=-8 StartY=-3.5 StartZ=0 EndX=-4.96891 EndY=-1.75 EndZ=0
    g34: Circle [constr] CenterX=-8 CenterY=0 CenterZ=0 NormalX=0 NormalY=0 NormalZ=1 AngleXU=0 Radius=3.5
    g35: LineSegment StartX=-4.03109 StartY=-3.5 StartZ=0 EndX=-7.06218 EndY=-5.25 EndZ=0
    g36: LineSegment StartX=-7.06218 StartY=-5.25 StartZ=0 EndX=-7.06218 EndY=-8.75 EndZ=0
    g37: LineSegment StartX=-7.06218 StartY=-8.75 StartZ=0 EndX=-4.03109 EndY=-10.5 EndZ=0
    g38: LineSegment StartX=-4.03109 StartY=-10.5 StartZ=0 EndX=-1 EndY=-8.75 EndZ=0
    g39: LineSegment StartX=-1 StartY=-8.75 StartZ=0 EndX=-1 EndY=-5.25 EndZ=0
    g40: LineSegment StartX=-1 StartY=-5.25 StartZ=0 EndX=-4.03109 EndY=-3.5 EndZ=0
    g41: Circle [constr] CenterX=-4.03109 CenterY=-7 CenterZ=0 NormalX=0 NormalY=0 NormalZ=1 AngleXU=0 Radius=3.5
    g42: LineSegment StartX=4.03109 StartY=-3.5 StartZ=0 EndX=1 EndY=-5.25 EndZ=0
    g43: LineSegment StartX=1 StartY=-5.25 StartZ=0 EndX=1 EndY=-8.75 EndZ=0
    g44: LineSegment StartX=1 StartY=-8.75 StartZ=0 EndX=4.03109 EndY=-10.5 EndZ=0
    g45: LineSegment StartX=4.03109 StartY=-10.5 StartZ=0 EndX=7.06218 EndY=-8.75 EndZ=0
    g46: LineSegment StartX=7.06218 StartY=-8.75 StartZ=0 EndX=7.06218 EndY=-5.25 EndZ=0
    g47: LineSegment StartX=7.06218 StartY=-5.25 StartZ=0 EndX=4.03109 EndY=-3.5 EndZ=0
    g48: Circle [constr] CenterX=4.03109 CenterY=-7 CenterZ=0 NormalX=0 NormalY=0 NormalZ=1 AngleXU=0 Radius=3.5
  constraints (117):
    c: Coincident(g0,g1)
    c: Coincident(g1,g2)
    c: Coincident(g2,g3)
    c: Coincident(g3,g4)
    c: Coincident(g4,g5)
    c: Coincident(g5,g0)
    c: Equal(g0, g1-g5) x5
    c: PointOnObject(g0,g6)
    c: PointOnObject(g1,g6)
    c: PointOnObject(g2,g6)
    c: PointOnObject(g3,g6)
    c: PointOnObject(g4,g6)
    c: PointOnObject(g5,g6)
    c: Coincident(g6,g-1)
    c: Diameter(g6) = 7
    c: PointOnObject(g0,g-2)
    c: Coincident(g7,g8)
    c: Coincident(g8,g9)
    c: Coincident(g9,g10)
    c: Coincident(g10,g11)
    c: Coincident(g11,g12)
    c: Coincident(g12,g7)
    c: Equal(g7, g8-g12) x5
    c: PointOnObject(g7,g13)
    c: PointOnObject(g8,g13)
    c: PointOnObject(g9,g13)
    c: PointOnObject(g10,g13)
    c: PointOnObject(g11,g13)
    c: PointOnObject(g12,g13)
    c: PointOnObject(g13,g-1)
    c: Diameter(g13) = 7
    c: Distance(g6,g13) = 8
    c: Horizontal(g0,g10)
    c: Coincident(g14,g15)
    c: Coincident(g15,g16)
    c: Coincident(g16,g17)
    c: Coincident(g17,g18)
    c: Coincident(g18,g19)
    c: Coincident(g19,g14)
    c: Equal(g14, g15-g19) x5
    c: PointOnObject(g14,g20)
    c: PointOnObject(g15,g20)
    c: PointOnObject(g16,g20)
    c: PointOnObject(g17,g20)
    c: PointOnObject(g18,g20)
    c: PointOnObject(g19,g20)
    c: Diameter(g20) = 7
    c: DistanceY(g-1,g20) = 7
    c: Vertical(g18)
    c: Distance(g17,g-2) = 1
    c: Coincident(g21,g22)
    c: Coincident(g22,g23)
    c: Coincident(g23,g24)
    c: Coincident(g24,g25)
    c: Coincident(g25,g26)
    c: Coincident(g26,g21)
    c: Equal(g21, g22-g26) x5
    c: PointOnObject(g21,g27)
    c: PointOnObject(g22,g27)
    c: PointOnObject(g23,g27)
    c: PointOnObject(g24,g27)
    c: PointOnObject(g25,g27)
    c: PointOnObject(g26,g27)
    c: Diameter(g27) = 7
    c: DistanceY(g-1,g27) = 7
    c: DistanceX(g21,g-1) = 1
    c: Vertical(g21)
    c: Coincident(g28,g29)
    c: Coincident(g29,g30)
    c: Coincident(g30,g31)
    c: Coincident(g31,g32)
    c: Coincident(g32,g33)
    c: Coincident(g33,g28)
    c: Equal(g28, g29-g33) x5
    c: PointOnObject(g28,g34)
    c: PointOnObject(g29,g34)
    c: PointOnObject(g30,g34)
    c: PointOnObject(g31,g34)
    c: PointOnObject(g32,g34)
    c: PointOnObject(g33,g34)
    c: PointOnObject(g34,g-1)
    c: Diameter(g34) = 7
    c: Vertical(g31)
    c: DistanceX(g34,g-1) = 8
    c: Coincident(g35,g36)
    c: Coincident(g36,g37)
    c: Coincident(g37,g38)
    c: Coincident(g38,g39)
    c: Coincident(g39,g40)
    c: Coincident(g40,g35)
    c: Equal(g35, g36-g40) x5
    c: PointOnObject(g35,g41)
    c: PointOnObject(g36,g41)
    c: PointOnObject(g37,g41)
    c: PointOnObject(g38,g41)
    c: PointOnObject(g39,g41)
    c: PointOnObject(g40,g41)
    c: Coincident(g42,g43)
    c: Coincident(g43,g44)
    c: Coincident(g44,g45)
    c: Coincident(g45,g46)
    c: Coincident(g46,g47)
    c: Coincident(g47,g42)
    c: Equal(g42, g43-g47) x5
    c: PointOnObject(g42,g48)
    c: PointOnObject(g43,g48)
    c: PointOnObject(g44,g48)
    c: PointOnObject(g45,g48)
    c: PointOnObject(g46,g48)
    c: PointOnObject(g47,g48)
    c: Equal(g41,g48)
    c: Diameter(g41) = 7
    c: Vertical(g39)
    c: Vertical(g43)
    c: Distance(g-2,g39) = 1
    c: Symmetric(g38,g43,g-2)
    c: Distance(g41,g-1) = 7
FEATURE [Part::Extrusion] Extrude389  label="hex004"
  Base = -> Sketch397
  Dir = (0,-1,2e-16)
  DirMode = 2
  FaceMakerClass = Part::FaceMakerBullseye
  FaceMakerMode = 3
  LengthFwd = 10
  LengthRev = 0
  Placement = pos=(-20,0,-7) rot=(0,0,1;0rad)
  Solid = true
  Symmetric = false
FEATURE [Sketcher::SketchObject] Sketch398
  ArcFitTolerance = 1e-06
  FullyConstrained = true
  MakeInternals = false
  Placement = pos=(0,0,0) rot=(1,0,0;1.5708rad)
  sketch-geometry (49):
    g0: LineSegment StartX=1e-16 StartY=3.5 StartZ=0 EndX=-3.03109 EndY=1.75 EndZ=0
    g1: LineSegment StartX=-3.03109 StartY=1.75 StartZ=0 EndX=-3.03109 EndY=-1.75 EndZ=0
    g2: LineSegment StartX=-3.03109 StartY=-1.75 StartZ=0 EndX=-1e-16 EndY=-3.5 EndZ=0
    g3: LineSegment StartX=-1e-16 StartY=-3.5 StartZ=0 EndX=3.03109 EndY=-1.75 EndZ=0
    g4: LineSegment StartX=3.03109 StartY=-1.75 StartZ=0 EndX=3.03109 EndY=1.75 EndZ=0
    g5: LineSegment StartX=3.03109 StartY=1.75 StartZ=0 EndX=1e-16 EndY=3.5 EndZ=0
    g6: Circle [constr] CenterX=0 CenterY=0 CenterZ=0 NormalX=0 NormalY=0 NormalZ=1 AngleXU=0 Radius=3.5
    g7: LineSegment StartX=4.96892 StartY=-1.75002 StartZ=0 EndX=8.00002 EndY=-3.5 EndZ=0
    g8: LineSegment StartX=8.00002 StartY=-3.5 StartZ=0 EndX=11.0311 EndY=-1.74998 EndZ=0
    g9: LineSegment StartX=11.0311 StartY=-1.74998 StartZ=0 EndX=11.0311 EndY=1.75002 EndZ=0
    g10: LineSegment StartX=11.0311 StartY=1.75002 StartZ=0 EndX=7.99998 EndY=3.5 EndZ=0
    g11: LineSegment StartX=7.99998 StartY=3.5 StartZ=0 EndX=4.9689 EndY=1.74998 EndZ=0
    g12: LineSegment StartX=4.9689 StartY=1.74998 StartZ=0 EndX=4.96892 EndY=-1.75002 EndZ=0
    g13: Circle [constr] CenterX=8 CenterY=0 CenterZ=0 NormalX=0 NormalY=0 NormalZ=1 AngleXU=0 Radius=3.5
    g14: LineSegment StartX=4.03109 StartY=3.5 StartZ=0 EndX=7.06218 EndY=5.25 EndZ=0
    g15: LineSegment StartX=7.06218 StartY=5.25 StartZ=0 EndX=7.06218 EndY=8.75 EndZ=0
    g16: LineSegment StartX=7.06218 StartY=8.75 StartZ=0 EndX=4.03109 EndY=10.5 EndZ=0
    g17: LineSegment StartX=4.03109 StartY=10.5 StartZ=0 EndX=1 EndY=8.75 EndZ=0
    g18: LineSegment StartX=1 StartY=8.75 StartZ=0 EndX=1 EndY=5.25 EndZ=0
    g19: LineSegment StartX=1 StartY=5.25 StartZ=0 EndX=4.03109 EndY=3.5 EndZ=0
    g20: Circle [constr] CenterX=4.03109 CenterY=7 CenterZ=0 NormalX=0 NormalY=0 NormalZ=1 AngleXU=0 Radius=3.5
    g21: LineSegment StartX=-1 StartY=5.25 StartZ=0 EndX=-1 EndY=8.75 EndZ=0
    g22: LineSegment StartX=-1 StartY=8.75 StartZ=0 EndX=-4.03109 EndY=10.5 EndZ=0
    g23: LineSegment StartX=-4.03109 StartY=10.5 StartZ=0 EndX=-7.06218 EndY=8.75 EndZ=0
    g24: LineSegment StartX=-7.06218 StartY=8.75 StartZ=0 EndX=-7.06218 EndY=5.25 EndZ=0
    g25: LineSegment StartX=-7.06218 StartY=5.25 StartZ=0 EndX=-4.03109 EndY=3.5 EndZ=0
    g26: LineSegment StartX=-4.03109 StartY=3.5 StartZ=0 EndX=-1 EndY=5.25 EndZ=0
    g27: Circle [constr] CenterX=-4.03109 CenterY=7 CenterZ=0 NormalX=0 NormalY=0 NormalZ=1 AngleXU=0 Radius=3.5
    g28: LineSegment StartX=-4.96891 StartY=-1.75 StartZ=0 EndX=-4.96891 EndY=1.75 EndZ=0
    g29: LineSegment StartX=-4.96891 StartY=1.75 StartZ=0 EndX=-8 EndY=3.5 EndZ=0
    g30: LineSegment StartX=-8 StartY=3.5 StartZ=0 EndX=-11.0311 EndY=1.75 EndZ=0
    g31: LineSegment StartX=-11.0311 StartY=1.75 StartZ=0 EndX=-11.0311 EndY=-1.75 EndZ=0
    g32: LineSegment StartX=-11.0311 StartY=-1.75 StartZ=0 EndX=-8 EndY=-3.5 EndZ=0
    g33: LineSegment StartX=-8 StartY=-3.5 StartZ=0 EndX=-4.96891 EndY=-1.75 EndZ=0
    g34: Circle [constr] CenterX=-8 CenterY=0 CenterZ=0 NormalX=0 NormalY=0 NormalZ=1 AngleXU=0 Radius=3.5
    g35: LineSegment StartX=-4.03109 StartY=-3.5 StartZ=0 EndX=-7.06218 EndY=-5.25 EndZ=0
    g36: LineSegment StartX=-7.06218 StartY=-5.25 StartZ=0 EndX=-7.06218 EndY=-8.75 EndZ=0
    g37: LineSegment StartX=-7.06218 StartY=-8.75 StartZ=0 EndX=-4.03109 EndY=-10.5 EndZ=0
    g38: LineSegment StartX=-4.03109 StartY=-10.5 StartZ=0 EndX=-1 EndY=-8.75 EndZ=0
    g39: LineSegment StartX=-1 StartY=-8.75 StartZ=0 EndX=-1 EndY=-5.25 EndZ=0
    g40: LineSegment StartX=-1 StartY=-5.25 StartZ=0 EndX=-4.03109 EndY=-3.5 EndZ=0
    g41: Circle [constr] CenterX=-4.03109 CenterY=-7 CenterZ=0 NormalX=0 NormalY=0 NormalZ=1 AngleXU=0 Radius=3.5
    g42: LineSegment StartX=4.03109 StartY=-3.5 StartZ=0 EndX=1 EndY=-5.25 EndZ=0
    g43: LineSegment StartX=1 StartY=-5.25 StartZ=0 EndX=1 EndY=-8.75 EndZ=0
    g44: LineSegment StartX=1 StartY=-8.75 StartZ=0 EndX=4.03109 EndY=-10.5 EndZ=0
    g45: LineSegment StartX=4.03109 StartY=-10.5 StartZ=0 EndX=7.06218 EndY=-8.75 EndZ=0
    g46: LineSegment StartX=7.06218 StartY=-8.75 StartZ=0 EndX=7.06218 EndY=-5.25 EndZ=0
    g47: LineSegment StartX=7.06218 StartY=-5.25 StartZ=0 EndX=4.03109 EndY=-3.5 EndZ=0
    g48: Circle [constr] CenterX=4.03109 CenterY=-7 CenterZ=0 NormalX=0 NormalY=0 NormalZ=1 AngleXU=0 Radius=3.5
  constraints (117):
    c: Coincident(g0,g1)
    c: Coincident(g1,g2)
    c: Coincident(g2,g3)
    c: Coincident(g3,g4)
    c: Coincident(g4,g5)
    c: Coincident(g5,g0)
    c: Equal(g0, g1-g5) x5
    c: PointOnObject(g0,g6)
    c: PointOnObject(g1,g6)
    c: PointOnObject(g2,g6)
    c: PointOnObject(g3,g6)
    c: PointOnObject(g4,g6)
    c: PointOnObject(g5,g6)
    c: Coincident(g6,g-1)
    c: Diameter(g6) = 7
    c: PointOnObject(g0,g-2)
    c: Coincident(g7,g8)
    c: Coincident(g8,g9)
    c: Coincident(g9,g10)
    c: Coincident(g10,g11)
    c: Coincident(g11,g12)
    c: Coincident(g12,g7)
    c: Equal(g7, g8-g12) x5
    c: PointOnObject(g7,g13)
    c: PointOnObject(g8,g13)
    c: PointOnObject(g9,g13)
    c: PointOnObject(g10,g13)
    c: PointOnObject(g11,g13)
    c: PointOnObject(g12,g13)
    c: PointOnObject(g13,g-1)
    c: Diameter(g13) = 7
    c: Distance(g6,g13) = 8
    c: Horizontal(g0,g10)
    c: Coincident(g14,g15)
    c: Coincident(g15,g16)
    c: Coincident(g16,g17)
    c: Coincident(g17,g18)
    c: Coincident(g18,g19)
    c: Coincident(g19,g14)
    c: Equal(g14, g15-g19) x5
    c: PointOnObject(g14,g20)
    c: PointOnObject(g15,g20)
    c: PointOnObject(g16,g20)
    c: PointOnObject(g17,g20)
    c: PointOnObject(g18,g20)
    c: PointOnObject(g19,g20)
    c: Diameter(g20) = 7
    c: DistanceY(g-1,g20) = 7
    c: Vertical(g18)
    c: Distance(g17,g-2) = 1
    c: Coincident(g21,g22)
    c: Coincident(g22,g23)
    c: Coincident(g23,g24)
    c: Coincident(g24,g25)
    c: Coincident(g25,g26)
    c: Coincident(g26,g21)
    c: Equal(g21, g22-g26) x5
    c: PointOnObject(g21,g27)
    c: PointOnObject(g22,g27)
    c: PointOnObject(g23,g27)
    c: PointOnObject(g24,g27)
    c: PointOnObject(g25,g27)
    c: PointOnObject(g26,g27)
    c: Diameter(g27) = 7
    c: DistanceY(g-1,g27) = 7
    c: DistanceX(g21,g-1) = 1
    c: Vertical(g21)
    c: Coincident(g28,g29)
    c: Coincident(g29,g30)
    c: Coincident(g30,g31)
    c: Coincident(g31,g32)
    c: Coincident(g32,g33)
    c: Coincident(g33,g28)
    c: Equal(g28, g29-g33) x5
    c: PointOnObject(g28,g34)
    c: PointOnObject(g29,g34)
    c: PointOnObject(g30,g34)
    c: PointOnObject(g31,g34)
    c: PointOnObject(g32,g34)
    c: PointOnObject(g33,g34)
    c: PointOnObject(g34,g-1)
    c: Diameter(g34) = 7
    c: Vertical(g31)
    c: DistanceX(g34,g-1) = 8
    c: Coincident(g35,g36)
    c: Coincident(g36,g37)
    c: Coincident(g37,g38)
    c: Coincident(g38,g39)
    c: Coincident(g39,g40)
    c: Coincident(g40,g35)
    c: Equal(g35, g36-g40) x5
    c: PointOnObject(g35,g41)
    c: PointOnObject(g36,g41)
    c: PointOnObject(g37,g41)
    c: PointOnObject(g38,g41)
    c: PointOnObject(g39,g41)
    c: PointOnObject(g40,g41)
    c: Coincident(g42,g43)
    c: Coincident(g43,g44)
    c: Coincident(g44,g45)
    c: Coincident(g45,g46)
    c: Coincident(g46,g47)
    c: Coincident(g47,g42)
    c: Equal(g42, g43-g47) x5
    c: PointOnObject(g42,g48)
    c: PointOnObject(g43,g48)
    c: PointOnObject(g44,g48)
    c: PointOnObject(g45,g48)
    c: PointOnObject(g46,g48)
    c: PointOnObject(g47,g48)
    c: Equal(g41,g48)
    c: Diameter(g41) = 7
    c: Vertical(g39)
    c: Vertical(g43)
    c: Distance(g-2,g39) = 1
    c: Symmetric(g38,g43,g-2)
    c: Distance(g41,g-1) = 7
FEATURE [Part::Extrusion] Extrude390  label="hex005"
  Base = -> Sketch398
  Dir = (0,-1,2e-16)
  DirMode = 2
  FaceMakerClass = Part::FaceMakerBullseye
  FaceMakerMode = 3
  LengthFwd = 10
  LengthRev = 0
  Placement = pos=(-16,0,14) rot=(0,0,1;0rad)
  Solid = true
  Symmetric = false
FEATURE [Sketcher::SketchObject] Sketch399
  ArcFitTolerance = 1e-06
  FullyConstrained = true
  MakeInternals = false
  Placement = pos=(0,0,0) rot=(1,0,0;1.5708rad)
  sketch-geometry (49):
    g0: LineSegment StartX=1e-16 StartY=3.5 StartZ=0 EndX=-3.03109 EndY=1.75 EndZ=0
    g1: LineSegment StartX=-3.03109 StartY=1.75 StartZ=0 EndX=-3.03109 EndY=-1.75 EndZ=0
    g2: LineSegment StartX=-3.03109 StartY=-1.75 StartZ=0 EndX=-1e-16 EndY=-3.5 EndZ=0
    g3: LineSegment StartX=-1e-16 StartY=-3.5 StartZ=0 EndX=3.03109 EndY=-1.75 EndZ=0
    g4: LineSegment StartX=3.03109 StartY=-1.75 StartZ=0 EndX=3.03109 EndY=1.75 EndZ=0
    g5: LineSegment StartX=3.03109 StartY=1.75 StartZ=0 EndX=1e-16 EndY=3.5 EndZ=0
    g6: Circle [constr] CenterX=0 CenterY=0 CenterZ=0 NormalX=0 NormalY=0 NormalZ=1 AngleXU=0 Radius=3.5
    g7: LineSegment StartX=4.96892 StartY=-1.75002 StartZ=0 EndX=8.00002 EndY=-3.5 EndZ=0
    g8: LineSegment StartX=8.00002 StartY=-3.5 StartZ=0 EndX=11.0311 EndY=-1.74998 EndZ=0
    g9: LineSegment StartX=11.0311 StartY=-1.74998 StartZ=0 EndX=11.0311 EndY=1.75002 EndZ=0
    g10: LineSegment StartX=11.0311 StartY=1.75002 StartZ=0 EndX=7.99998 EndY=3.5 EndZ=0
    g11: LineSegment StartX=7.99998 StartY=3.5 StartZ=0 EndX=4.9689 EndY=1.74998 EndZ=0
    g12: LineSegment StartX=4.9689 StartY=1.74998 StartZ=0 EndX=4.96892 EndY=-1.75002 EndZ=0
    g13: Circle [constr] CenterX=8 CenterY=0 CenterZ=0 NormalX=0 NormalY=0 NormalZ=1 AngleXU=0 Radius=3.5
    g14: LineSegment StartX=4.03109 StartY=3.5 StartZ=0 EndX=7.06218 EndY=5.25 EndZ=0
    g15: LineSegment StartX=7.06218 StartY=5.25 StartZ=0 EndX=7.06218 EndY=8.75 EndZ=0
    g16: LineSegment StartX=7.06218 StartY=8.75 StartZ=0 EndX=4.03109 EndY=10.5 EndZ=0
    g17: LineSegment StartX=4.03109 StartY=10.5 StartZ=0 EndX=1 EndY=8.75 EndZ=0
    g18: LineSegment StartX=1 StartY=8.75 StartZ=0 EndX=1 EndY=5.25 EndZ=0
    g19: LineSegment StartX=1 StartY=5.25 StartZ=0 EndX=4.03109 EndY=3.5 EndZ=0
    g20: Circle [constr] CenterX=4.03109 CenterY=7 CenterZ=0 NormalX=0 NormalY=0 NormalZ=1 AngleXU=0 Radius=3.5
    g21: LineSegment StartX=-1 StartY=5.25 StartZ=0 EndX=-1 EndY=8.75 EndZ=0
    g22: LineSegment StartX=-1 StartY=8.75 StartZ=0 EndX=-4.03109 EndY=10.5 EndZ=0
    g23: LineSegment StartX=-4.03109 StartY=10.5 StartZ=0 EndX=-7.06218 EndY=8.75 EndZ=0
    g24: LineSegment StartX=-7.06218 StartY=8.75 StartZ=0 EndX=-7.06218 EndY=5.25 EndZ=0
    g25: LineSegment StartX=-7.06218 StartY=5.25 StartZ=0 EndX=-4.03109 EndY=3.5 EndZ=0
    g26: LineSegment StartX=-4.03109 StartY=3.5 StartZ=0 EndX=-1 EndY=5.25 EndZ=0
    g27: Circle [constr] CenterX=-4.03109 CenterY=7 CenterZ=0 NormalX=0 NormalY=0 NormalZ=1 AngleXU=0 Radius=3.5
    g28: LineSegment StartX=-4.96891 StartY=-1.75 StartZ=0 EndX=-4.96891 EndY=1.75 EndZ=0
    g29: LineSegment StartX=-4.96891 StartY=1.75 StartZ=0 EndX=-8 EndY=3.5 EndZ=0
    g30: LineSegment StartX=-8 StartY=3.5 StartZ=0 EndX=-11.0311 EndY=1.75 EndZ=0
    g31: LineSegment StartX=-11.0311 StartY=1.75 StartZ=0 EndX=-11.0311 EndY=-1.75 EndZ=0
    g32: LineSegment StartX=-11.0311 StartY=-1.75 StartZ=0 EndX=-8 EndY=-3.5 EndZ=0
    g33: LineSegment StartX=-8 StartY=-3.5 StartZ=0 EndX=-4.96891 EndY=-1.75 EndZ=0
    g34: Circle [constr] CenterX=-8 CenterY=0 CenterZ=0 NormalX=0 NormalY=0 NormalZ=1 AngleXU=0 Radius=3.5
    g35: LineSegment StartX=-4.03109 StartY=-3.5 StartZ=0 EndX=-7.06218 EndY=-5.25 EndZ=0
    g36: LineSegment StartX=-7.06218 StartY=-5.25 StartZ=0 EndX=-7.06218 EndY=-8.75 EndZ=0
    g37: LineSegment StartX=-7.06218 StartY=-8.75 StartZ=0 EndX=-4.03109 EndY=-10.5 EndZ=0
    g38: LineSegment StartX=-4.03109 StartY=-10.5 StartZ=0 EndX=-1 EndY=-8.75 EndZ=0
    g39: LineSegment StartX=-1 StartY=-8.75 StartZ=0 EndX=-1 EndY=-5.25 EndZ=0
    g40: LineSegment StartX=-1 StartY=-5.25 StartZ=0 EndX=-4.03109 EndY=-3.5 EndZ=0
    g41: Circle [constr] CenterX=-4.03109 CenterY=-7 CenterZ=0 NormalX=0 NormalY=0 NormalZ=1 AngleXU=0 Radius=3.5
    g42: LineSegment StartX=4.03109 StartY=-3.5 StartZ=0 EndX=1 EndY=-5.25 EndZ=0
    g43: LineSegment StartX=1 StartY=-5.25 StartZ=0 EndX=1 EndY=-8.75 EndZ=0
    g44: LineSegment StartX=1 StartY=-8.75 StartZ=0 EndX=4.03109 EndY=-10.5 EndZ=0
    g45: LineSegment StartX=4.03109 StartY=-10.5 StartZ=0 EndX=7.06218 EndY=-8.75 EndZ=0
    g46: LineSegment StartX=7.06218 StartY=-8.75 StartZ=0 EndX=7.06218 EndY=-5.25 EndZ=0
    g47: LineSegment StartX=7.06218 StartY=-5.25 StartZ=0 EndX=4.03109 EndY=-3.5 EndZ=0
    g48: Circle [constr] CenterX=4.03109 CenterY=-7 CenterZ=0 NormalX=0 NormalY=0 NormalZ=1 AngleXU=0 Radius=3.5
  constraints (117):
    c: Coincident(g0,g1)
    c: Coincident(g1,g2)
    c: Coincident(g2,g3)
    c: Coincident(g3,g4)
    c: Coincident(g4,g5)
    c: Coincident(g5,g0)
    c: Equal(g0, g1-g5) x5
    c: PointOnObject(g0,g6)
    c: PointOnObject(g1,g6)
    c: PointOnObject(g2,g6)
    c: PointOnObject(g3,g6)
    c: PointOnObject(g4,g6)
    c: PointOnObject(g5,g6)
    c: Coincident(g6,g-1)
    c: Diameter(g6) = 7
    c: PointOnObject(g0,g-2)
    c: Coincident(g7,g8)
    c: Coincident(g8,g9)
    c: Coincident(g9,g10)
    c: Coincident(g10,g11)
    c: Coincident(g11,g12)
    c: Coincident(g12,g7)
    c: Equal(g7, g8-g12) x5
    c: PointOnObject(g7,g13)
    c: PointOnObject(g8,g13)
    c: PointOnObject(g9,g13)
    c: PointOnObject(g10,g13)
    c: PointOnObject(g11,g13)
    c: PointOnObject(g12,g13)
    c: PointOnObject(g13,g-1)
    c: Diameter(g13) = 7
    c: Distance(g6,g13) = 8
    c: Horizontal(g0,g10)
    c: Coincident(g14,g15)
    c: Coincident(g15,g16)
    c: Coincident(g16,g17)
    c: Coincident(g17,g18)
    c: Coincident(g18,g19)
    c: Coincident(g19,g14)
    c: Equal(g14, g15-g19) x5
    c: PointOnObject(g14,g20)
    c: PointOnObject(g15,g20)
    c: PointOnObject(g16,g20)
    c: PointOnObject(g17,g20)
    c: PointOnObject(g18,g20)
    c: PointOnObject(g19,g20)
    c: Diameter(g20) = 7
    c: DistanceY(g-1,g20) = 7
    c: Vertical(g18)
    c: Distance(g17,g-2) = 1
    c: Coincident(g21,g22)
    c: Coincident(g22,g23)
    c: Coincident(g23,g24)
    c: Coincident(g24,g25)
    c: Coincident(g25,g26)
    c: Coincident(g26,g21)
    c: Equal(g21, g22-g26) x5
    c: PointOnObject(g21,g27)
    c: PointOnObject(g22,g27)
    c: PointOnObject(g23,g27)
    c: PointOnObject(g24,g27)
    c: PointOnObject(g25,g27)
    c: PointOnObject(g26,g27)
    c: Diameter(g27) = 7
    c: DistanceY(g-1,g27) = 7
    c: DistanceX(g21,g-1) = 1
    c: Vertical(g21)
    c: Coincident(g28,g29)
    c: Coincident(g29,g30)
    c: Coincident(g30,g31)
    c: Coincident(g31,g32)
    c: Coincident(g32,g33)
    c: Coincident(g33,g28)
    c: Equal(g28, g29-g33) x5
    c: PointOnObject(g28,g34)
    c: PointOnObject(g29,g34)
    c: PointOnObject(g30,g34)
    c: PointOnObject(g31,g34)
    c: PointOnObject(g32,g34)
    c: PointOnObject(g33,g34)
    c: PointOnObject(g34,g-1)
    c: Diameter(g34) = 7
    c: Vertical(g31)
    c: DistanceX(g34,g-1) = 8
    c: Coincident(g35,g36)
    c: Coincident(g36,g37)
    c: Coincident(g37,g38)
    c: Coincident(g38,g39)
    c: Coincident(g39,g40)
    c: Coincident(g40,g35)
    c: Equal(g35, g36-g40) x5
    c: PointOnObject(g35,g41)
    c: PointOnObject(g36,g41)
    c: PointOnObject(g37,g41)
    c: PointOnObject(g38,g41)
    c: PointOnObject(g39,g41)
    c: PointOnObject(g40,g41)
    c: Coincident(g42,g43)
    c: Coincident(g43,g44)
    c: Coincident(g44,g45)
    c: Coincident(g45,g46)
    c: Coincident(g46,g47)
    c: Coincident(g47,g42)
    c: Equal(g42, g43-g47) x5
    c: PointOnObject(g42,g48)
    c: PointOnObject(g43,g48)
    c: PointOnObject(g44,g48)
    c: PointOnObject(g45,g48)
    c: PointOnObject(g46,g48)
    c: PointOnObject(g47,g48)
    c: Equal(g41,g48)
    c: Diameter(g41) = 7
    c: Vertical(g39)
    c: Vertical(g43)
    c: Distance(g-2,g39) = 1
    c: Symmetric(g38,g43,g-2)
    c: Distance(g41,g-1) = 7
FEATURE [Part::Extrusion] Extrude391  label="hex006"
  Base = -> Sketch399
  Dir = (0,-1,2e-16)
  DirMode = 2
  FaceMakerClass = Part::FaceMakerBullseye
  FaceMakerMode = 3
  LengthFwd = 10
  LengthRev = 0
  Placement = pos=(-4,0,-21) rot=(0,0,1;0rad)
  Solid = true
  Symmetric = false
FEATURE [Sketcher::SketchObject] Sketch400
  ArcFitTolerance = 1e-06
  FullyConstrained = true
  MakeInternals = false
  Placement = pos=(0,0,0) rot=(1,0,0;1.5708rad)
  sketch-geometry (49):
    g0: LineSegment StartX=1e-16 StartY=3.5 StartZ=0 EndX=-3.03109 EndY=1.75 EndZ=0
    g1: LineSegment StartX=-3.03109 StartY=1.75 StartZ=0 EndX=-3.03109 EndY=-1.75 EndZ=0
    g2: LineSegment StartX=-3.03109 StartY=-1.75 StartZ=0 EndX=-1e-16 EndY=-3.5 EndZ=0
    g3: LineSegment StartX=-1e-16 StartY=-3.5 StartZ=0 EndX=3.03109 EndY=-1.75 EndZ=0
    g4: LineSegment StartX=3.03109 StartY=-1.75 StartZ=0 EndX=3.03109 EndY=1.75 EndZ=0
    g5: LineSegment StartX=3.03109 StartY=1.75 StartZ=0 EndX=1e-16 EndY=3.5 EndZ=0
    g6: Circle [constr] CenterX=0 CenterY=0 CenterZ=0 NormalX=0 NormalY=0 NormalZ=1 AngleXU=0 Radius=3.5
    g7: LineSegment StartX=4.96892 StartY=-1.75002 StartZ=0 EndX=8.00002 EndY=-3.5 EndZ=0
    g8: LineSegment StartX=8.00002 StartY=-3.5 StartZ=0 EndX=11.0311 EndY=-1.74998 EndZ=0
    g9: LineSegment StartX=11.0311 StartY=-1.74998 StartZ=0 EndX=11.0311 EndY=1.75002 EndZ=0
    g10: LineSegment StartX=11.0311 StartY=1.75002 StartZ=0 EndX=7.99998 EndY=3.5 EndZ=0
    g11: LineSegment StartX=7.99998 StartY=3.5 StartZ=0 EndX=4.9689 EndY=1.74998 EndZ=0
    g12: LineSegment StartX=4.9689 StartY=1.74998 StartZ=0 EndX=4.96892 EndY=-1.75002 EndZ=0
    g13: Circle [constr] CenterX=8 CenterY=0 CenterZ=0 NormalX=0 NormalY=0 NormalZ=1 AngleXU=0 Radius=3.5
    g14: LineSegment StartX=4.03109 StartY=3.5 StartZ=0 EndX=7.06218 EndY=5.25 EndZ=0
    g15: LineSegment StartX=7.06218 StartY=5.25 StartZ=0 EndX=7.06218 EndY=8.75 EndZ=0
    g16: LineSegment StartX=7.06218 StartY=8.75 StartZ=0 EndX=4.03109 EndY=10.5 EndZ=0
    g17: LineSegment StartX=4.03109 StartY=10.5 StartZ=0 EndX=1 EndY=8.75 EndZ=0
    g18: LineSegment StartX=1 StartY=8.75 StartZ=0 EndX=1 EndY=5.25 EndZ=0
    g19: LineSegment StartX=1 StartY=5.25 StartZ=0 EndX=4.03109 EndY=3.5 EndZ=0
    g20: Circle [constr] CenterX=4.03109 CenterY=7 CenterZ=0 NormalX=0 NormalY=0 NormalZ=1 AngleXU=0 Radius=3.5
    g21: LineSegment StartX=-1 StartY=5.25 StartZ=0 EndX=-1 EndY=8.75 EndZ=0
    g22: LineSegment StartX=-1 StartY=8.75 StartZ=0 EndX=-4.03109 EndY=10.5 EndZ=0
    g23: LineSegment StartX=-4.03109 StartY=10.5 StartZ=0 EndX=-7.06218 EndY=8.75 EndZ=0
    g24: LineSegment StartX=-7.06218 StartY=8.75 StartZ=0 EndX=-7.06218 EndY=5.25 EndZ=0
    g25: LineSegment StartX=-7.06218 StartY=5.25 StartZ=0 EndX=-4.03109 EndY=3.5 EndZ=0
    g26: LineSegment StartX=-4.03109 StartY=3.5 StartZ=0 EndX=-1 EndY=5.25 EndZ=0
    g27: Circle [constr] CenterX=-4.03109 CenterY=7 CenterZ=0 NormalX=0 NormalY=0 NormalZ=1 AngleXU=0 Radius=3.5
    g28: LineSegment StartX=-4.96891 StartY=-1.75 StartZ=0 EndX=-4.96891 EndY=1.75 EndZ=0
    g29: LineSegment StartX=-4.96891 StartY=1.75 StartZ=0 EndX=-8 EndY=3.5 EndZ=0
    g30: LineSegment StartX=-8 StartY=3.5 StartZ=0 EndX=-11.0311 EndY=1.75 EndZ=0
    g31: LineSegment StartX=-11.0311 StartY=1.75 StartZ=0 EndX=-11.0311 EndY=-1.75 EndZ=0
    g32: LineSegment StartX=-11.0311 StartY=-1.75 StartZ=0 EndX=-8 EndY=-3.5 EndZ=0
    g33: LineSegment StartX=-8 StartY=-3.5 StartZ=0 EndX=-4.96891 EndY=-1.75 EndZ=0
    g34: Circle [constr] CenterX=-8 CenterY=0 CenterZ=0 NormalX=0 NormalY=0 NormalZ=1 AngleXU=0 Radius=3.5
    g35: LineSegment StartX=-4.03109 StartY=-3.5 StartZ=0 EndX=-7.06218 EndY=-5.25 EndZ=0
    g36: LineSegment StartX=-7.06218 StartY=-5.25 StartZ=0 EndX=-7.06218 EndY=-8.75 EndZ=0
    g37: LineSegment StartX=-7.06218 StartY=-8.75 StartZ=0 EndX=-4.03109 EndY=-10.5 EndZ=0
    g38: LineSegment StartX=-4.03109 StartY=-10.5 StartZ=0 EndX=-1 EndY=-8.75 EndZ=0
    g39: LineSegment StartX=-1 StartY=-8.75 StartZ=0 EndX=-1 EndY=-5.25 EndZ=0
    g40: LineSegment StartX=-1 StartY=-5.25 StartZ=0 EndX=-4.03109 EndY=-3.5 EndZ=0
    g41: Circle [constr] CenterX=-4.03109 CenterY=-7 CenterZ=0 NormalX=0 NormalY=0 NormalZ=1 AngleXU=0 Radius=3.5
    g42: LineSegment StartX=4.03109 StartY=-3.5 StartZ=0 EndX=1 EndY=-5.25 EndZ=0
    g43: LineSegment StartX=1 StartY=-5.25 StartZ=0 EndX=1 EndY=-8.75 EndZ=0
    g44: LineSegment StartX=1 StartY=-8.75 StartZ=0 EndX=4.03109 EndY=-10.5 EndZ=0
    g45: LineSegment StartX=4.03109 StartY=-10.5 StartZ=0 EndX=7.06218 EndY=-8.75 EndZ=0
    g46: LineSegment StartX=7.06218 StartY=-8.75 StartZ=0 EndX=7.06218 EndY=-5.25 EndZ=0
    g47: LineSegment StartX=7.06218 StartY=-5.25 StartZ=0 EndX=4.03109 EndY=-3.5 EndZ=0
    g48: Circle [constr] CenterX=4.03109 CenterY=-7 CenterZ=0 NormalX=0 NormalY=0 NormalZ=1 AngleXU=0 Radius=3.5
  constraints (117):
    c: Coincident(g0,g1)
    c: Coincident(g1,g2)
    c: Coincident(g2,g3)
    c: Coincident(g3,g4)
    c: Coincident(g4,g5)
    c: Coincident(g5,g0)
    c: Equal(g0, g1-g5) x5
    c: PointOnObject(g0,g6)
    c: PointOnObject(g1,g6)
    c: PointOnObject(g2,g6)
    c: PointOnObject(g3,g6)
    c: PointOnObject(g4,g6)
    c: PointOnObject(g5,g6)
    c: Coincident(g6,g-1)
    c: Diameter(g6) = 7
    c: PointOnObject(g0,g-2)
    c: Coincident(g7,g8)
    c: Coincident(g8,g9)
    c: Coincident(g9,g10)
    c: Coincident(g10,g11)
    c: Coincident(g11,g12)
    c: Coincident(g12,g7)
    c: Equal(g7, g8-g12) x5
    c: PointOnObject(g7,g13)
    c: PointOnObject(g8,g13)
    c: PointOnObject(g9,g13)
    c: PointOnObject(g10,g13)
    c: PointOnObject(g11,g13)
    c: PointOnObject(g12,g13)
    c: PointOnObject(g13,g-1)
    c: Diameter(g13) = 7
    c: Distance(g6,g13) = 8
    c: Horizontal(g0,g10)
    c: Coincident(g14,g15)
    c: Coincident(g15,g16)
    c: Coincident(g16,g17)
    c: Coincident(g17,g18)
    c: Coincident(g18,g19)
    c: Coincident(g19,g14)
    c: Equal(g14, g15-g19) x5
    c: PointOnObject(g14,g20)
    c: PointOnObject(g15,g20)
    c: PointOnObject(g16,g20)
    c: PointOnObject(g17,g20)
    c: PointOnObject(g18,g20)
    c: PointOnObject(g19,g20)
    c: Diameter(g20) = 7
    c: DistanceY(g-1,g20) = 7
    c: Vertical(g18)
    c: Distance(g17,g-2) = 1
    c: Coincident(g21,g22)
    c: Coincident(g22,g23)
    c: Coincident(g23,g24)
    c: Coincident(g24,g25)
    c: Coincident(g25,g26)
    c: Coincident(g26,g21)
    c: Equal(g21, g22-g26) x5
    c: PointOnObject(g21,g27)
    c: PointOnObject(g22,g27)
    c: PointOnObject(g23,g27)
    c: PointOnObject(g24,g27)
    c: PointOnObject(g25,g27)
    c: PointOnObject(g26,g27)
    c: Diameter(g27) = 7
    c: DistanceY(g-1,g27) = 7
    c: DistanceX(g21,g-1) = 1
    c: Vertical(g21)
    c: Coincident(g28,g29)
    c: Coincident(g29,g30)
    c: Coincident(g30,g31)
    c: Coincident(g31,g32)
    c: Coincident(g32,g33)
    c: Coincident(g33,g28)
    c: Equal(g28, g29-g33) x5
    c: PointOnObject(g28,g34)
    c: PointOnObject(g29,g34)
    c: PointOnObject(g30,g34)
    c: PointOnObject(g31,g34)
    c: PointOnObject(g32,g34)
    c: PointOnObject(g33,g34)
    c: PointOnObject(g34,g-1)
    c: Diameter(g34) = 7
    c: Vertical(g31)
    c: DistanceX(g34,g-1) = 8
    c: Coincident(g35,g36)
    c: Coincident(g36,g37)
    c: Coincident(g37,g38)
    c: Coincident(g38,g39)
    c: Coincident(g39,g40)
    c: Coincident(g40,g35)
    c: Equal(g35, g36-g40) x5
    c: PointOnObject(g35,g41)
    c: PointOnObject(g36,g41)
    c: PointOnObject(g37,g41)
    c: PointOnObject(g38,g41)
    c: PointOnObject(g39,g41)
    c: PointOnObject(g40,g41)
    c: Coincident(g42,g43)
    c: Coincident(g43,g44)
    c: Coincident(g44,g45)
    c: Coincident(g45,g46)
    c: Coincident(g46,g47)
    c: Coincident(g47,g42)
    c: Equal(g42, g43-g47) x5
    c: PointOnObject(g42,g48)
    c: PointOnObject(g43,g48)
    c: PointOnObject(g44,g48)
    c: PointOnObject(g45,g48)
    c: PointOnObject(g46,g48)
    c: PointOnObject(g47,g48)
    c: Equal(g41,g48)
    c: Diameter(g41) = 7
    c: Vertical(g39)
    c: Vertical(g43)
    c: Distance(g-2,g39) = 1
    c: Symmetric(g38,g43,g-2)
    c: Distance(g41,g-1) = 7
FEATURE [Part::Extrusion] Extrude392  label="hex007"
  Base = -> Sketch400
  Dir = (0,-1,2e-16)
  DirMode = 2
  FaceMakerClass = Part::FaceMakerBullseye
  FaceMakerMode = 3
  LengthFwd = 10
  LengthRev = 0
  Placement = pos=(16,0,-14) rot=(0,0,1;0rad)
  Solid = true
  Symmetric = false
FEATURE [Sketcher::SketchObject] Sketch401
  ArcFitTolerance = 1e-06
  FullyConstrained = true
  MakeInternals = false
  Placement = pos=(0,0,0) rot=(1,0,0;1.5708rad)
  sketch-geometry (49):
    g0: LineSegment StartX=1e-16 StartY=3.5 StartZ=0 EndX=-3.03109 EndY=1.75 EndZ=0
    g1: LineSegment StartX=-3.03109 StartY=1.75 StartZ=0 EndX=-3.03109 EndY=-1.75 EndZ=0
    g2: LineSegment StartX=-3.03109 StartY=-1.75 StartZ=0 EndX=-1e-16 EndY=-3.5 EndZ=0
    g3: LineSegment StartX=-1e-16 StartY=-3.5 StartZ=0 EndX=3.03109 EndY=-1.75 EndZ=0
    g4: LineSegment StartX=3.03109 StartY=-1.75 StartZ=0 EndX=3.03109 EndY=1.75 EndZ=0
    g5: LineSegment StartX=3.03109 StartY=1.75 StartZ=0 EndX=1e-16 EndY=3.5 EndZ=0
    g6: Circle [constr] CenterX=0 CenterY=0 CenterZ=0 NormalX=0 NormalY=0 NormalZ=1 AngleXU=0 Radius=3.5
    g7: LineSegment StartX=4.96892 StartY=-1.75002 StartZ=0 EndX=8.00002 EndY=-3.5 EndZ=0
    g8: LineSegment StartX=8.00002 StartY=-3.5 StartZ=0 EndX=11.0311 EndY=-1.74998 EndZ=0
    g9: LineSegment StartX=11.0311 StartY=-1.74998 StartZ=0 EndX=11.0311 EndY=1.75002 EndZ=0
    g10: LineSegment StartX=11.0311 StartY=1.75002 StartZ=0 EndX=7.99998 EndY=3.5 EndZ=0
    g11: LineSegment StartX=7.99998 StartY=3.5 StartZ=0 EndX=4.9689 EndY=1.74998 EndZ=0
    g12: LineSegment StartX=4.9689 StartY=1.74998 StartZ=0 EndX=4.96892 EndY=-1.75002 EndZ=0
    g13: Circle [constr] CenterX=8 CenterY=0 CenterZ=0 NormalX=0 NormalY=0 NormalZ=1 AngleXU=0 Radius=3.5
    g14: LineSegment StartX=4.03109 StartY=3.5 StartZ=0 EndX=7.06218 EndY=5.25 EndZ=0
    g15: LineSegment StartX=7.06218 StartY=5.25 StartZ=0 EndX=7.06218 EndY=8.75 EndZ=0
    g16: LineSegment StartX=7.06218 StartY=8.75 StartZ=0 EndX=4.03109 EndY=10.5 EndZ=0
    g17: LineSegment StartX=4.03109 StartY=10.5 StartZ=0 EndX=1 EndY=8.75 EndZ=0
    g18: LineSegment StartX=1 StartY=8.75 StartZ=0 EndX=1 EndY=5.25 EndZ=0
    g19: LineSegment StartX=1 StartY=5.25 StartZ=0 EndX=4.03109 EndY=3.5 EndZ=0
    g20: Circle [constr] CenterX=4.03109 CenterY=7 CenterZ=0 NormalX=0 NormalY=0 NormalZ=1 AngleXU=0 Radius=3.5
    g21: LineSegment StartX=-1 StartY=5.25 StartZ=0 EndX=-1 EndY=8.75 EndZ=0
    g22: LineSegment StartX=-1 StartY=8.75 StartZ=0 EndX=-4.03109 EndY=10.5 EndZ=0
    g23: LineSegment StartX=-4.03109 StartY=10.5 StartZ=0 EndX=-7.06218 EndY=8.75 EndZ=0
    g24: LineSegment StartX=-7.06218 StartY=8.75 StartZ=0 EndX=-7.06218 EndY=5.25 EndZ=0
    g25: LineSegment StartX=-7.06218 StartY=5.25 StartZ=0 EndX=-4.03109 EndY=3.5 EndZ=0
    g26: LineSegment StartX=-4.03109 StartY=3.5 StartZ=0 EndX=-1 EndY=5.25 EndZ=0
    g27: Circle [constr] CenterX=-4.03109 CenterY=7 CenterZ=0 NormalX=0 NormalY=0 NormalZ=1 AngleXU=0 Radius=3.5
    g28: LineSegment StartX=-4.96891 StartY=-1.75 StartZ=0 EndX=-4.96891 EndY=1.75 EndZ=0
    g29: LineSegment StartX=-4.96891 StartY=1.75 StartZ=0 EndX=-8 EndY=3.5 EndZ=0
    g30: LineSegment StartX=-8 StartY=3.5 StartZ=0 EndX=-11.0311 EndY=1.75 EndZ=0
    g31: LineSegment StartX=-11.0311 StartY=1.75 StartZ=0 EndX=-11.0311 EndY=-1.75 EndZ=0
    g32: LineSegment StartX=-11.0311 StartY=-1.75 StartZ=0 EndX=-8 EndY=-3.5 EndZ=0
    g33: LineSegment StartX=-8 StartY=-3.5 StartZ=0 EndX=-4.96891 EndY=-1.75 EndZ=0
    g34: Circle [constr] CenterX=-8 CenterY=0 CenterZ=0 NormalX=0 NormalY=0 NormalZ=1 AngleXU=0 Radius=3.5
    g35: LineSegment StartX=-4.03109 StartY=-3.5 StartZ=0 EndX=-7.06218 EndY=-5.25 EndZ=0
    g36: LineSegment StartX=-7.06218 StartY=-5.25 StartZ=0 EndX=-7.06218 EndY=-8.75 EndZ=0
    g37: LineSegment StartX=-7.06218 StartY=-8.75 StartZ=0 EndX=-4.03109 EndY=-10.5 EndZ=0
    g38: LineSegment StartX=-4.03109 StartY=-10.5 StartZ=0 EndX=-1 EndY=-8.75 EndZ=0
    g39: LineSegment StartX=-1 StartY=-8.75 StartZ=0 EndX=-1 EndY=-5.25 EndZ=0
    g40: LineSegment StartX=-1 StartY=-5.25 StartZ=0 EndX=-4.03109 EndY=-3.5 EndZ=0
    g41: Circle [constr] CenterX=-4.03109 CenterY=-7 CenterZ=0 NormalX=0 NormalY=0 NormalZ=1 AngleXU=0 Radius=3.5
    g42: LineSegment StartX=4.03109 StartY=-3.5 StartZ=0 EndX=1 EndY=-5.25 EndZ=0
    g43: LineSegment StartX=1 StartY=-5.25 StartZ=0 EndX=1 EndY=-8.75 EndZ=0
    g44: LineSegment StartX=1 StartY=-8.75 StartZ=0 EndX=4.03109 EndY=-10.5 EndZ=0
    g45: LineSegment StartX=4.03109 StartY=-10.5 StartZ=0 EndX=7.06218 EndY=-8.75 EndZ=0
    g46: LineSegment StartX=7.06218 StartY=-8.75 StartZ=0 EndX=7.06218 EndY=-5.25 EndZ=0
    g47: LineSegment StartX=7.06218 StartY=-5.25 StartZ=0 EndX=4.03109 EndY=-3.5 EndZ=0
    g48: Circle [constr] CenterX=4.03109 CenterY=-7 CenterZ=0 NormalX=0 NormalY=0 NormalZ=1 AngleXU=0 Radius=3.5
  constraints (117):
    c: Coincident(g0,g1)
    c: Coincident(g1,g2)
    c: Coincident(g2,g3)
    c: Coincident(g3,g4)
    c: Coincident(g4,g5)
    c: Coincident(g5,g0)
    c: Equal(g0, g1-g5) x5
    c: PointOnObject(g0,g6)
    c: PointOnObject(g1,g6)
    c: PointOnObject(g2,g6)
    c: PointOnObject(g3,g6)
    c: PointOnObject(g4,g6)
    c: PointOnObject(g5,g6)
    c: Coincident(g6,g-1)
    c: Diameter(g6) = 7
    c: PointOnObject(g0,g-2)
    c: Coincident(g7,g8)
    c: Coincident(g8,g9)
    c: Coincident(g9,g10)
    c: Coincident(g10,g11)
    c: Coincident(g11,g12)
    c: Coincident(g12,g7)
    c: Equal(g7, g8-g12) x5
    c: PointOnObject(g7,g13)
    c: PointOnObject(g8,g13)
    c: PointOnObject(g9,g13)
    c: PointOnObject(g10,g13)
    c: PointOnObject(g11,g13)
    c: PointOnObject(g12,g13)
    c: PointOnObject(g13,g-1)
    c: Diameter(g13) = 7
    c: Distance(g6,g13) = 8
    c: Horizontal(g0,g10)
    c: Coincident(g14,g15)
    c: Coincident(g15,g16)
    c: Coincident(g16,g17)
    c: Coincident(g17,g18)
    c: Coincident(g18,g19)
    c: Coincident(g19,g14)
    c: Equal(g14, g15-g19) x5
    c: PointOnObject(g14,g20)
    c: PointOnObject(g15,g20)
    c: PointOnObject(g16,g20)
    c: PointOnObject(g17,g20)
    c: PointOnObject(g18,g20)
    c: PointOnObject(g19,g20)
    c: Diameter(g20) = 7
    c: DistanceY(g-1,g20) = 7
    c: Vertical(g18)
    c: Distance(g17,g-2) = 1
    c: Coincident(g21,g22)
    c: Coincident(g22,g23)
    c: Coincident(g23,g24)
    c: Coincident(g24,g25)
    c: Coincident(g25,g26)
    c: Coincident(g26,g21)
    c: Equal(g21, g22-g26) x5
    c: PointOnObject(g21,g27)
    c: PointOnObject(g22,g27)
    c: PointOnObject(g23,g27)
    c: PointOnObject(g24,g27)
    c: PointOnObject(g25,g27)
    c: PointOnObject(g26,g27)
    c: Diameter(g27) = 7
    c: DistanceY(g-1,g27) = 7
    c: DistanceX(g21,g-1) = 1
    c: Vertical(g21)
    c: Coincident(g28,g29)
    c: Coincident(g29,g30)
    c: Coincident(g30,g31)
    c: Coincident(g31,g32)
    c: Coincident(g32,g33)
    c: Coincident(g33,g28)
    c: Equal(g28, g29-g33) x5
    c: PointOnObject(g28,g34)
    c: PointOnObject(g29,g34)
    c: PointOnObject(g30,g34)
    c: PointOnObject(g31,g34)
    c: PointOnObject(g32,g34)
    c: PointOnObject(g33,g34)
    c: PointOnObject(g34,g-1)
    c: Diameter(g34) = 7
    c: Vertical(g31)
    c: DistanceX(g34,g-1) = 8
    c: Coincident(g35,g36)
    c: Coincident(g36,g37)
    c: Coincident(g37,g38)
    c: Coincident(g38,g39)
    c: Coincident(g39,g40)
    c: Coincident(g40,g35)
    c: Equal(g35, g36-g40) x5
    c: PointOnObject(g35,g41)
    c: PointOnObject(g36,g41)
    c: PointOnObject(g37,g41)
    c: PointOnObject(g38,g41)
    c: PointOnObject(g39,g41)
    c: PointOnObject(g40,g41)
    c: Coincident(g42,g43)
    c: Coincident(g43,g44)
    c: Coincident(g44,g45)
    c: Coincident(g45,g46)
    c: Coincident(g46,g47)
    c: Coincident(g47,g42)
    c: Equal(g42, g43-g47) x5
    c: PointOnObject(g42,g48)
    c: PointOnObject(g43,g48)
    c: PointOnObject(g44,g48)
    c: PointOnObject(g45,g48)
    c: PointOnObject(g46,g48)
    c: PointOnObject(g47,g48)
    c: Equal(g41,g48)
    c: Diameter(g41) = 7
    c: Vertical(g39)
    c: Vertical(g43)
    c: Distance(g-2,g39) = 1
    c: Symmetric(g38,g43,g-2)
    c: Distance(g41,g-1) = 7
FEATURE [Part::Extrusion] Extrude393  label="hex008"
  Base = -> Sketch401
  Dir = (0,-1,2e-16)
  DirMode = 2
  FaceMakerClass = Part::FaceMakerBullseye
  FaceMakerMode = 3
  LengthFwd = 10
  LengthRev = 0
  Placement = pos=(-4,0,21) rot=(0,0,1;0rad)
  Solid = true
  Symmetric = false
FEATURE [Sketcher::SketchObject] Sketch402
  ArcFitTolerance = 1e-06
  FullyConstrained = true
  MakeInternals = false
  Placement = pos=(0,0,0) rot=(1,0,0;1.5708rad)
  sketch-geometry (49):
    g0: LineSegment StartX=1e-16 StartY=3.5 StartZ=0 EndX=-3.03109 EndY=1.75 EndZ=0
    g1: LineSegment StartX=-3.03109 StartY=1.75 StartZ=0 EndX=-3.03109 EndY=-1.75 EndZ=0
    g2: LineSegment StartX=-3.03109 StartY=-1.75 StartZ=0 EndX=-1e-16 EndY=-3.5 EndZ=0
    g3: LineSegment StartX=-1e-16 StartY=-3.5 StartZ=0 EndX=3.03109 EndY=-1.75 EndZ=0
    g4: LineSegment StartX=3.03109 StartY=-1.75 StartZ=0 EndX=3.03109 EndY=1.75 EndZ=0
    g5: LineSegment StartX=3.03109 StartY=1.75 StartZ=0 EndX=1e-16 EndY=3.5 EndZ=0
    g6: Circle [constr] CenterX=0 CenterY=0 CenterZ=0 NormalX=0 NormalY=0 NormalZ=1 AngleXU=0 Radius=3.5
    g7: LineSegment StartX=4.96892 StartY=-1.75002 StartZ=0 EndX=8.00002 EndY=-3.5 EndZ=0
    g8: LineSegment StartX=8.00002 StartY=-3.5 StartZ=0 EndX=11.0311 EndY=-1.74998 EndZ=0
    g9: LineSegment StartX=11.0311 StartY=-1.74998 StartZ=0 EndX=11.0311 EndY=1.75002 EndZ=0
    g10: LineSegment StartX=11.0311 StartY=1.75002 StartZ=0 EndX=7.99998 EndY=3.5 EndZ=0
    g11: LineSegment StartX=7.99998 StartY=3.5 StartZ=0 EndX=4.9689 EndY=1.74998 EndZ=0
    g12: LineSegment StartX=4.9689 StartY=1.74998 StartZ=0 EndX=4.96892 EndY=-1.75002 EndZ=0
    g13: Circle [constr] CenterX=8 CenterY=0 CenterZ=0 NormalX=0 NormalY=0 NormalZ=1 AngleXU=0 Radius=3.5
    g14: LineSegment StartX=4.03109 StartY=3.5 StartZ=0 EndX=7.06218 EndY=5.25 EndZ=0
    g15: LineSegment StartX=7.06218 StartY=5.25 StartZ=0 EndX=7.06218 EndY=8.75 EndZ=0
    g16: LineSegment StartX=7.06218 StartY=8.75 StartZ=0 EndX=4.03109 EndY=10.5 EndZ=0
    g17: LineSegment StartX=4.03109 StartY=10.5 StartZ=0 EndX=1 EndY=8.75 EndZ=0
    g18: LineSegment StartX=1 StartY=8.75 StartZ=0 EndX=1 EndY=5.25 EndZ=0
    g19: LineSegment StartX=1 StartY=5.25 StartZ=0 EndX=4.03109 EndY=3.5 EndZ=0
    g20: Circle [constr] CenterX=4.03109 CenterY=7 CenterZ=0 NormalX=0 NormalY=0 NormalZ=1 AngleXU=0 Radius=3.5
    g21: LineSegment StartX=-1 StartY=5.25 StartZ=0 EndX=-1 EndY=8.75 EndZ=0
    g22: LineSegment StartX=-1 StartY=8.75 StartZ=0 EndX=-4.03109 EndY=10.5 EndZ=0
    g23: LineSegment StartX=-4.03109 StartY=10.5 StartZ=0 EndX=-7.06218 EndY=8.75 EndZ=0
    g24: LineSegment StartX=-7.06218 StartY=8.75 StartZ=0 EndX=-7.06218 EndY=5.25 EndZ=0
    g25: LineSegment StartX=-7.06218 StartY=5.25 StartZ=0 EndX=-4.03109 EndY=3.5 EndZ=0
    g26: LineSegment StartX=-4.03109 StartY=3.5 StartZ=0 EndX=-1 EndY=5.25 EndZ=0
    g27: Circle [constr] CenterX=-4.03109 CenterY=7 CenterZ=0 NormalX=0 NormalY=0 NormalZ=1 AngleXU=0 Radius=3.5
    g28: LineSegment StartX=-4.96891 StartY=-1.75 StartZ=0 EndX=-4.96891 EndY=1.75 EndZ=0
    g29: LineSegment StartX=-4.96891 StartY=1.75 StartZ=0 EndX=-8 EndY=3.5 EndZ=0
    g30: LineSegment StartX=-8 StartY=3.5 StartZ=0 EndX=-11.0311 EndY=1.75 EndZ=0
    g31: LineSegment StartX=-11.0311 StartY=1.75 StartZ=0 EndX=-11.0311 EndY=-1.75 EndZ=0
    g32: LineSegment StartX=-11.0311 StartY=-1.75 StartZ=0 EndX=-8 EndY=-3.5 EndZ=0
    g33: LineSegment StartX=-8 StartY=-3.5 StartZ=0 EndX=-4.96891 EndY=-1.75 EndZ=0
    g34: Circle [constr] CenterX=-8 CenterY=0 CenterZ=0 NormalX=0 NormalY=0 NormalZ=1 AngleXU=0 Radius=3.5
    g35: LineSegment StartX=-4.03109 StartY=-3.5 StartZ=0 EndX=-7.06218 EndY=-5.25 EndZ=0
    g36: LineSegment StartX=-7.06218 StartY=-5.25 StartZ=0 EndX=-7.06218 EndY=-8.75 EndZ=0
    g37: LineSegment StartX=-7.06218 StartY=-8.75 StartZ=0 EndX=-4.03109 EndY=-10.5 EndZ=0
    g38: LineSegment StartX=-4.03109 StartY=-10.5 StartZ=0 EndX=-1 EndY=-8.75 EndZ=0
    g39: LineSegment StartX=-1 StartY=-8.75 StartZ=0 EndX=-1 EndY=-5.25 EndZ=0
    g40: LineSegment StartX=-1 StartY=-5.25 StartZ=0 EndX=-4.03109 EndY=-3.5 EndZ=0
    g41: Circle [constr] CenterX=-4.03109 CenterY=-7 CenterZ=0 NormalX=0 NormalY=0 NormalZ=1 AngleXU=0 Radius=3.5
    g42: LineSegment StartX=4.03109 StartY=-3.5 StartZ=0 EndX=1 EndY=-5.25 EndZ=0
    g43: LineSegment StartX=1 StartY=-5.25 StartZ=0 EndX=1 EndY=-8.75 EndZ=0
    g44: LineSegment StartX=1 StartY=-8.75 StartZ=0 EndX=4.03109 EndY=-10.5 EndZ=0
    g45: LineSegment StartX=4.03109 StartY=-10.5 StartZ=0 EndX=7.06218 EndY=-8.75 EndZ=0
    g46: LineSegment StartX=7.06218 StartY=-8.75 StartZ=0 EndX=7.06218 EndY=-5.25 EndZ=0
    g47: LineSegment StartX=7.06218 StartY=-5.25 StartZ=0 EndX=4.03109 EndY=-3.5 EndZ=0
    g48: Circle [constr] CenterX=4.03109 CenterY=-7 CenterZ=0 NormalX=0 NormalY=0 NormalZ=1 AngleXU=0 Radius=3.5
  constraints (117):
    c: Coincident(g0,g1)
    c: Coincident(g1,g2)
    c: Coincident(g2,g3)
    c: Coincident(g3,g4)
    c: Coincident(g4,g5)
    c: Coincident(g5,g0)
    c: Equal(g0, g1-g5) x5
    c: PointOnObject(g0,g6)
    c: PointOnObject(g1,g6)
    c: PointOnObject(g2,g6)
    c: PointOnObject(g3,g6)
    c: PointOnObject(g4,g6)
    c: PointOnObject(g5,g6)
    c: Coincident(g6,g-1)
    c: Diameter(g6) = 7
    c: PointOnObject(g0,g-2)
    c: Coincident(g7,g8)
    c: Coincident(g8,g9)
    c: Coincident(g9,g10)
    c: Coincident(g10,g11)
    c: Coincident(g11,g12)
    c: Coincident(g12,g7)
    c: Equal(g7, g8-g12) x5
    c: PointOnObject(g7,g13)
    c: PointOnObject(g8,g13)
    c: PointOnObject(g9,g13)
    c: PointOnObject(g10,g13)
    c: PointOnObject(g11,g13)
    c: PointOnObject(g12,g13)
    c: PointOnObject(g13,g-1)
    c: Diameter(g13) = 7
    c: Distance(g6,g13) = 8
    c: Horizontal(g0,g10)
    c: Coincident(g14,g15)
    c: Coincident(g15,g16)
    c: Coincident(g16,g17)
    c: Coincident(g17,g18)
    c: Coincident(g18,g19)
    c: Coincident(g19,g14)
    c: Equal(g14, g15-g19) x5
    c: PointOnObject(g14,g20)
    c: PointOnObject(g15,g20)
    c: PointOnObject(g16,g20)
    c: PointOnObject(g17,g20)
    c: PointOnObject(g18,g20)
    c: PointOnObject(g19,g20)
    c: Diameter(g20) = 7
    c: DistanceY(g-1,g20) = 7
    c: Vertical(g18)
    c: Distance(g17,g-2) = 1
    c: Coincident(g21,g22)
    c: Coincident(g22,g23)
    c: Coincident(g23,g24)
    c: Coincident(g24,g25)
    c: Coincident(g25,g26)
    c: Coincident(g26,g21)
    c: Equal(g21, g22-g26) x5
    c: PointOnObject(g21,g27)
    c: PointOnObject(g22,g27)
    c: PointOnObject(g23,g27)
    c: PointOnObject(g24,g27)
    c: PointOnObject(g25,g27)
    c: PointOnObject(g26,g27)
    c: Diameter(g27) = 7
    c: DistanceY(g-1,g27) = 7
    c: DistanceX(g21,g-1) = 1
    c: Vertical(g21)
    c: Coincident(g28,g29)
    c: Coincident(g29,g30)
    c: Coincident(g30,g31)
    c: Coincident(g31,g32)
    c: Coincident(g32,g33)
    c: Coincident(g33,g28)
    c: Equal(g28, g29-g33) x5
    c: PointOnObject(g28,g34)
    c: PointOnObject(g29,g34)
    c: PointOnObject(g30,g34)
    c: PointOnObject(g31,g34)
    c: PointOnObject(g32,g34)
    c: PointOnObject(g33,g34)
    c: PointOnObject(g34,g-1)
    c: Diameter(g34) = 7
    c: Vertical(g31)
    c: DistanceX(g34,g-1) = 8
    c: Coincident(g35,g36)
    c: Coincident(g36,g37)
    c: Coincident(g37,g38)
    c: Coincident(g38,g39)
    c: Coincident(g39,g40)
    c: Coincident(g40,g35)
    c: Equal(g35, g36-g40) x5
    c: PointOnObject(g35,g41)
    c: PointOnObject(g36,g41)
    c: PointOnObject(g37,g41)
    c: PointOnObject(g38,g41)
    c: PointOnObject(g39,g41)
    c: PointOnObject(g40,g41)
    c: Coincident(g42,g43)
    c: Coincident(g43,g44)
    c: Coincident(g44,g45)
    c: Coincident(g45,g46)
    c: Coincident(g46,g47)
    c: Coincident(g47,g42)
    c: Equal(g42, g43-g47) x5
    c: PointOnObject(g42,g48)
    c: PointOnObject(g43,g48)
    c: PointOnObject(g44,g48)
    c: PointOnObject(g45,g48)
    c: PointOnObject(g46,g48)
    c: PointOnObject(g47,g48)
    c: Equal(g41,g48)
    c: Diameter(g41) = 7
    c: Vertical(g39)
    c: Vertical(g43)
    c: Distance(g-2,g39) = 1
    c: Symmetric(g38,g43,g-2)
    c: Distance(g41,g-1) = 7
FEATURE [Part::Extrusion] Extrude394  label="hex009"
  Base = -> Sketch402
  Dir = (0,-1,2e-16)
  DirMode = 2
  FaceMakerClass = Part::FaceMakerBullseye
  FaceMakerMode = 3
  LengthFwd = 10
  LengthRev = 0
  Placement = pos=(12,0,-35) rot=(0,0,1;0rad)
  Solid = true
  Symmetric = false
FEATURE [Sketcher::SketchObject] Sketch403
  ArcFitTolerance = 1e-06
  FullyConstrained = true
  MakeInternals = false
  Placement = pos=(0,0,0) rot=(1,0,0;1.5708rad)
  sketch-geometry (49):
    g0: LineSegment StartX=1e-16 StartY=3.5 StartZ=0 EndX=-3.03109 EndY=1.75 EndZ=0
    g1: LineSegment StartX=-3.03109 StartY=1.75 StartZ=0 EndX=-3.03109 EndY=-1.75 EndZ=0
    g2: LineSegment StartX=-3.03109 StartY=-1.75 StartZ=0 EndX=-1e-16 EndY=-3.5 EndZ=0
    g3: LineSegment StartX=-1e-16 StartY=-3.5 StartZ=0 EndX=3.03109 EndY=-1.75 EndZ=0
    g4: LineSegment StartX=3.03109 StartY=-1.75 StartZ=0 EndX=3.03109 EndY=1.75 EndZ=0
    g5: LineSegment StartX=3.03109 StartY=1.75 StartZ=0 EndX=1e-16 EndY=3.5 EndZ=0
    g6: Circle [constr] CenterX=0 CenterY=0 CenterZ=0 NormalX=0 NormalY=0 NormalZ=1 AngleXU=0 Radius=3.5
    g7: LineSegment StartX=4.96892 StartY=-1.75002 StartZ=0 EndX=8.00002 EndY=-3.5 EndZ=0
    g8: LineSegment StartX=8.00002 StartY=-3.5 StartZ=0 EndX=11.0311 EndY=-1.74998 EndZ=0
    g9: LineSegment StartX=11.0311 StartY=-1.74998 StartZ=0 EndX=11.0311 EndY=1.75002 EndZ=0
    g10: LineSegment StartX=11.0311 StartY=1.75002 StartZ=0 EndX=7.99998 EndY=3.5 EndZ=0
    g11: LineSegment StartX=7.99998 StartY=3.5 StartZ=0 EndX=4.9689 EndY=1.74998 EndZ=0
    g12: LineSegment StartX=4.9689 StartY=1.74998 StartZ=0 EndX=4.96892 EndY=-1.75002 EndZ=0
    g13: Circle [constr] CenterX=8 CenterY=0 CenterZ=0 NormalX=0 NormalY=0 NormalZ=1 AngleXU=0 Radius=3.5
    g14: LineSegment StartX=4.03109 StartY=3.5 StartZ=0 EndX=7.06218 EndY=5.25 EndZ=0
    g15: LineSegment StartX=7.06218 StartY=5.25 StartZ=0 EndX=7.06218 EndY=8.75 EndZ=0
    g16: LineSegment StartX=7.06218 StartY=8.75 StartZ=0 EndX=4.03109 EndY=10.5 EndZ=0
    g17: LineSegment StartX=4.03109 StartY=10.5 StartZ=0 EndX=1 EndY=8.75 EndZ=0
    g18: LineSegment StartX=1 StartY=8.75 StartZ=0 EndX=1 EndY=5.25 EndZ=0
    g19: LineSegment StartX=1 StartY=5.25 StartZ=0 EndX=4.03109 EndY=3.5 EndZ=0
    g20: Circle [constr] CenterX=4.03109 CenterY=7 CenterZ=0 NormalX=0 NormalY=0 NormalZ=1 AngleXU=0 Radius=3.5
    g21: LineSegment StartX=-1 StartY=5.25 StartZ=0 EndX=-1 EndY=8.75 EndZ=0
    g22: LineSegment StartX=-1 StartY=8.75 StartZ=0 EndX=-4.03109 EndY=10.5 EndZ=0
    g23: LineSegment StartX=-4.03109 StartY=10.5 StartZ=0 EndX=-7.06218 EndY=8.75 EndZ=0
    g24: LineSegment StartX=-7.06218 StartY=8.75 StartZ=0 EndX=-7.06218 EndY=5.25 EndZ=0
    g25: LineSegment StartX=-7.06218 StartY=5.25 StartZ=0 EndX=-4.03109 EndY=3.5 EndZ=0
    g26: LineSegment StartX=-4.03109 StartY=3.5 StartZ=0 EndX=-1 EndY=5.25 EndZ=0
    g27: Circle [constr] CenterX=-4.03109 CenterY=7 CenterZ=0 NormalX=0 NormalY=0 NormalZ=1 AngleXU=0 Radius=3.5
    g28: LineSegment StartX=-4.96891 StartY=-1.75 StartZ=0 EndX=-4.96891 EndY=1.75 EndZ=0
    g29: LineSegment StartX=-4.96891 StartY=1.75 StartZ=0 EndX=-8 EndY=3.5 EndZ=0
    g30: LineSegment StartX=-8 StartY=3.5 StartZ=0 EndX=-11.0311 EndY=1.75 EndZ=0
    g31: LineSegment StartX=-11.0311 StartY=1.75 StartZ=0 EndX=-11.0311 EndY=-1.75 EndZ=0
    g32: LineSegment StartX=-11.0311 StartY=-1.75 StartZ=0 EndX=-8 EndY=-3.5 EndZ=0
    g33: LineSegment StartX=-8 StartY=-3.5 StartZ=0 EndX=-4.96891 EndY=-1.75 EndZ=0
    g34: Circle [constr] CenterX=-8 CenterY=0 CenterZ=0 NormalX=0 NormalY=0 NormalZ=1 AngleXU=0 Radius=3.5
    g35: LineSegment StartX=-4.03109 StartY=-3.5 StartZ=0 EndX=-7.06218 EndY=-5.25 EndZ=0
    g36: LineSegment StartX=-7.06218 StartY=-5.25 StartZ=0 EndX=-7.06218 EndY=-8.75 EndZ=0
    g37: LineSegment StartX=-7.06218 StartY=-8.75 StartZ=0 EndX=-4.03109 EndY=-10.5 EndZ=0
    g38: LineSegment StartX=-4.03109 StartY=-10.5 StartZ=0 EndX=-1 EndY=-8.75 EndZ=0
    g39: LineSegment StartX=-1 StartY=-8.75 StartZ=0 EndX=-1 EndY=-5.25 EndZ=0
    g40: LineSegment StartX=-1 StartY=-5.25 StartZ=0 EndX=-4.03109 EndY=-3.5 EndZ=0
    g41: Circle [constr] CenterX=-4.03109 CenterY=-7 CenterZ=0 NormalX=0 NormalY=0 NormalZ=1 AngleXU=0 Radius=3.5
    g42: LineSegment StartX=4.03109 StartY=-3.5 StartZ=0 EndX=1 EndY=-5.25 EndZ=0
    g43: LineSegment StartX=1 StartY=-5.25 StartZ=0 EndX=1 EndY=-8.75 EndZ=0
    g44: LineSegment StartX=1 StartY=-8.75 StartZ=0 EndX=4.03109 EndY=-10.5 EndZ=0
    g45: LineSegment StartX=4.03109 StartY=-10.5 StartZ=0 EndX=7.06218 EndY=-8.75 EndZ=0
    g46: LineSegment StartX=7.06218 StartY=-8.75 StartZ=0 EndX=7.06218 EndY=-5.25 EndZ=0
    g47: LineSegment StartX=7.06218 StartY=-5.25 StartZ=0 EndX=4.03109 EndY=-3.5 EndZ=0
    g48: Circle [constr] CenterX=4.03109 CenterY=-7 CenterZ=0 NormalX=0 NormalY=0 NormalZ=1 AngleXU=0 Radius=3.5
  constraints (117):
    c: Coincident(g0,g1)
    c: Coincident(g1,g2)
    c: Coincident(g2,g3)
    c: Coincident(g3,g4)
    c: Coincident(g4,g5)
    c: Coincident(g5,g0)
    c: Equal(g0, g1-g5) x5
    c: PointOnObject(g0,g6)
    c: PointOnObject(g1,g6)
    c: PointOnObject(g2,g6)
    c: PointOnObject(g3,g6)
    c: PointOnObject(g4,g6)
    c: PointOnObject(g5,g6)
    c: Coincident(g6,g-1)
    c: Diameter(g6) = 7
    c: PointOnObject(g0,g-2)
    c: Coincident(g7,g8)
    c: Coincident(g8,g9)
    c: Coincident(g9,g10)
    c: Coincident(g10,g11)
    c: Coincident(g11,g12)
    c: Coincident(g12,g7)
    c: Equal(g7, g8-g12) x5
    c: PointOnObject(g7,g13)
    c: PointOnObject(g8,g13)
    c: PointOnObject(g9,g13)
    c: PointOnObject(g10,g13)
    c: PointOnObject(g11,g13)
    c: PointOnObject(g12,g13)
    c: PointOnObject(g13,g-1)
    c: Diameter(g13) = 7
    c: Distance(g6,g13) = 8
    c: Horizontal(g0,g10)
    c: Coincident(g14,g15)
    c: Coincident(g15,g16)
    c: Coincident(g16,g17)
    c: Coincident(g17,g18)
    c: Coincident(g18,g19)
    c: Coincident(g19,g14)
    c: Equal(g14, g15-g19) x5
    c: PointOnObject(g14,g20)
    c: PointOnObject(g15,g20)
    c: PointOnObject(g16,g20)
    c: PointOnObject(g17,g20)
    c: PointOnObject(g18,g20)
    c: PointOnObject(g19,g20)
    c: Diameter(g20) = 7
    c: DistanceY(g-1,g20) = 7
    c: Vertical(g18)
    c: Distance(g17,g-2) = 1
    c: Coincident(g21,g22)
    c: Coincident(g22,g23)
    c: Coincident(g23,g24)
    c: Coincident(g24,g25)
    c: Coincident(g25,g26)
    c: Coincident(g26,g21)
    c: Equal(g21, g22-g26) x5
    c: PointOnObject(g21,g27)
    c: PointOnObject(g22,g27)
    c: PointOnObject(g23,g27)
    c: PointOnObject(g24,g27)
    c: PointOnObject(g25,g27)
    c: PointOnObject(g26,g27)
    c: Diameter(g27) = 7
    c: DistanceY(g-1,g27) = 7
    c: DistanceX(g21,g-1) = 1
    c: Vertical(g21)
    c: Coincident(g28,g29)
    c: Coincident(g29,g30)
    c: Coincident(g30,g31)
    c: Coincident(g31,g32)
    c: Coincident(g32,g33)
    c: Coincident(g33,g28)
    c: Equal(g28, g29-g33) x5
    c: PointOnObject(g28,g34)
    c: PointOnObject(g29,g34)
    c: PointOnObject(g30,g34)
    c: PointOnObject(g31,g34)
    c: PointOnObject(g32,g34)
    c: PointOnObject(g33,g34)
    c: PointOnObject(g34,g-1)
    c: Diameter(g34) = 7
    c: Vertical(g31)
    c: DistanceX(g34,g-1) = 8
    c: Coincident(g35,g36)
    c: Coincident(g36,g37)
    c: Coincident(g37,g38)
    c: Coincident(g38,g39)
    c: Coincident(g39,g40)
    c: Coincident(g40,g35)
    c: Equal(g35, g36-g40) x5
    c: PointOnObject(g35,g41)
    c: PointOnObject(g36,g41)
    c: PointOnObject(g37,g41)
    c: PointOnObject(g38,g41)
    c: PointOnObject(g39,g41)
    c: PointOnObject(g40,g41)
    c: Coincident(g42,g43)
    c: Coincident(g43,g44)
    c: Coincident(g44,g45)
    c: Coincident(g45,g46)
    c: Coincident(g46,g47)
    c: Coincident(g47,g42)
    c: Equal(g42, g43-g47) x5
    c: PointOnObject(g42,g48)
    c: PointOnObject(g43,g48)
    c: PointOnObject(g44,g48)
    c: PointOnObject(g45,g48)
    c: PointOnObject(g46,g48)
    c: PointOnObject(g47,g48)
    c: Equal(g41,g48)
    c: Diameter(g41) = 7
    c: Vertical(g39)
    c: Vertical(g43)
    c: Distance(g-2,g39) = 1
    c: Symmetric(g38,g43,g-2)
    c: Distance(g41,g-1) = 7
FEATURE [Part::Extrusion] Extrude395  label="hex010"
  Base = -> Sketch403
  Dir = (0,-1,2e-16)
  DirMode = 2
  FaceMakerClass = Part::FaceMakerBullseye
  FaceMakerMode = 3
  LengthFwd = 10
  LengthRev = 0
  Placement = pos=(12,0,35) rot=(0,0,1;0rad)
  Solid = true
  Symmetric = false
FEATURE [Sketcher::SketchObject] Sketch404
  ArcFitTolerance = 1e-06
  FullyConstrained = true
  MakeInternals = false
  Placement = pos=(0,0,0) rot=(1,0,0;1.5708rad)
  sketch-geometry (49):
    g0: LineSegment StartX=1e-16 StartY=3.5 StartZ=0 EndX=-3.03109 EndY=1.75 EndZ=0
    g1: LineSegment StartX=-3.03109 StartY=1.75 StartZ=0 EndX=-3.03109 EndY=-1.75 EndZ=0
    g2: LineSegment StartX=-3.03109 StartY=-1.75 StartZ=0 EndX=-1e-16 EndY=-3.5 EndZ=0
    g3: LineSegment StartX=-1e-16 StartY=-3.5 StartZ=0 EndX=3.03109 EndY=-1.75 EndZ=0
    g4: LineSegment StartX=3.03109 StartY=-1.75 StartZ=0 EndX=3.03109 EndY=1.75 EndZ=0
    g5: LineSegment StartX=3.03109 StartY=1.75 StartZ=0 EndX=1e-16 EndY=3.5 EndZ=0
    g6: Circle [constr] CenterX=0 CenterY=0 CenterZ=0 NormalX=0 NormalY=0 NormalZ=1 AngleXU=0 Radius=3.5
    g7: LineSegment StartX=4.96892 StartY=-1.75002 StartZ=0 EndX=8.00002 EndY=-3.5 EndZ=0
    g8: LineSegment StartX=8.00002 StartY=-3.5 StartZ=0 EndX=11.0311 EndY=-1.74998 EndZ=0
    g9: LineSegment StartX=11.0311 StartY=-1.74998 StartZ=0 EndX=11.0311 EndY=1.75002 EndZ=0
    g10: LineSegment StartX=11.0311 StartY=1.75002 StartZ=0 EndX=7.99998 EndY=3.5 EndZ=0
    g11: LineSegment StartX=7.99998 StartY=3.5 StartZ=0 EndX=4.9689 EndY=1.74998 EndZ=0
    g12: LineSegment StartX=4.9689 StartY=1.74998 StartZ=0 EndX=4.96892 EndY=-1.75002 EndZ=0
    g13: Circle [constr] CenterX=8 CenterY=0 CenterZ=0 NormalX=0 NormalY=0 NormalZ=1 AngleXU=0 Radius=3.5
    g14: LineSegment StartX=4.03109 StartY=3.5 StartZ=0 EndX=7.06218 EndY=5.25 EndZ=0
    g15: LineSegment StartX=7.06218 StartY=5.25 StartZ=0 EndX=7.06218 EndY=8.75 EndZ=0
    g16: LineSegment StartX=7.06218 StartY=8.75 StartZ=0 EndX=4.03109 EndY=10.5 EndZ=0
    g17: LineSegment StartX=4.03109 StartY=10.5 StartZ=0 EndX=1 EndY=8.75 EndZ=0
    g18: LineSegment StartX=1 StartY=8.75 StartZ=0 EndX=1 EndY=5.25 EndZ=0
    g19: LineSegment StartX=1 StartY=5.25 StartZ=0 EndX=4.03109 EndY=3.5 EndZ=0
    g20: Circle [constr] CenterX=4.03109 CenterY=7 CenterZ=0 NormalX=0 NormalY=0 NormalZ=1 AngleXU=0 Radius=3.5
    g21: LineSegment StartX=-1 StartY=5.25 StartZ=0 EndX=-1 EndY=8.75 EndZ=0
    g22: LineSegment StartX=-1 StartY=8.75 StartZ=0 EndX=-4.03109 EndY=10.5 EndZ=0
    g23: LineSegment StartX=-4.03109 StartY=10.5 StartZ=0 EndX=-7.06218 EndY=8.75 EndZ=0
    g24: LineSegment StartX=-7.06218 StartY=8.75 StartZ=0 EndX=-7.06218 EndY=5.25 EndZ=0
    g25: LineSegment StartX=-7.06218 StartY=5.25 StartZ=0 EndX=-4.03109 EndY=3.5 EndZ=0
    g26: LineSegment StartX=-4.03109 StartY=3.5 StartZ=0 EndX=-1 EndY=5.25 EndZ=0
    g27: Circle [constr] CenterX=-4.03109 CenterY=7 CenterZ=0 NormalX=0 NormalY=0 NormalZ=1 AngleXU=0 Radius=3.5
    g28: LineSegment StartX=-4.96891 StartY=-1.75 StartZ=0 EndX=-4.96891 EndY=1.75 EndZ=0
    g29: LineSegment StartX=-4.96891 StartY=1.75 StartZ=0 EndX=-8 EndY=3.5 EndZ=0
    g30: LineSegment StartX=-8 StartY=3.5 StartZ=0 EndX=-11.0311 EndY=1.75 EndZ=0
    g31: LineSegment StartX=-11.0311 StartY=1.75 StartZ=0 EndX=-11.0311 EndY=-1.75 EndZ=0
    g32: LineSegment StartX=-11.0311 StartY=-1.75 StartZ=0 EndX=-8 EndY=-3.5 EndZ=0
    g33: LineSegment StartX=-8 StartY=-3.5 StartZ=0 EndX=-4.96891 EndY=-1.75 EndZ=0
    g34: Circle [constr] CenterX=-8 CenterY=0 CenterZ=0 NormalX=0 NormalY=0 NormalZ=1 AngleXU=0 Radius=3.5
    g35: LineSegment StartX=-4.03109 StartY=-3.5 StartZ=0 EndX=-7.06218 EndY=-5.25 EndZ=0
    g36: LineSegment StartX=-7.06218 StartY=-5.25 StartZ=0 EndX=-7.06218 EndY=-8.75 EndZ=0
    g37: LineSegment StartX=-7.06218 StartY=-8.75 StartZ=0 EndX=-4.03109 EndY=-10.5 EndZ=0
    g38: LineSegment StartX=-4.03109 StartY=-10.5 StartZ=0 EndX=-1 EndY=-8.75 EndZ=0
    g39: LineSegment StartX=-1 StartY=-8.75 StartZ=0 EndX=-1 EndY=-5.25 EndZ=0
    g40: LineSegment StartX=-1 StartY=-5.25 StartZ=0 EndX=-4.03109 EndY=-3.5 EndZ=0
    g41: Circle [constr] CenterX=-4.03109 CenterY=-7 CenterZ=0 NormalX=0 NormalY=0 NormalZ=1 AngleXU=0 Radius=3.5
    g42: LineSegment StartX=4.03109 StartY=-3.5 StartZ=0 EndX=1 EndY=-5.25 EndZ=0
    g43: LineSegment StartX=1 StartY=-5.25 StartZ=0 EndX=1 EndY=-8.75 EndZ=0
    g44: LineSegment StartX=1 StartY=-8.75 StartZ=0 EndX=4.03109 EndY=-10.5 EndZ=0
    g45: LineSegment StartX=4.03109 StartY=-10.5 StartZ=0 EndX=7.06218 EndY=-8.75 EndZ=0
    g46: LineSegment StartX=7.06218 StartY=-8.75 StartZ=0 EndX=7.06218 EndY=-5.25 EndZ=0
    g47: LineSegment StartX=7.06218 StartY=-5.25 StartZ=0 EndX=4.03109 EndY=-3.5 EndZ=0
    g48: Circle [constr] CenterX=4.03109 CenterY=-7 CenterZ=0 NormalX=0 NormalY=0 NormalZ=1 AngleXU=0 Radius=3.5
  constraints (117):
    c: Coincident(g0,g1)
    c: Coincident(g1,g2)
    c: Coincident(g2,g3)
    c: Coincident(g3,g4)
    c: Coincident(g4,g5)
    c: Coincident(g5,g0)
    c: Equal(g0, g1-g5) x5
    c: PointOnObject(g0,g6)
    c: PointOnObject(g1,g6)
    c: PointOnObject(g2,g6)
    c: PointOnObject(g3,g6)
    c: PointOnObject(g4,g6)
    c: PointOnObject(g5,g6)
    c: Coincident(g6,g-1)
    c: Diameter(g6) = 7
    c: PointOnObject(g0,g-2)
    c: Coincident(g7,g8)
    c: Coincident(g8,g9)
    c: Coincident(g9,g10)
    c: Coincident(g10,g11)
    c: Coincident(g11,g12)
    c: Coincident(g12,g7)
    c: Equal(g7, g8-g12) x5
    c: PointOnObject(g7,g13)
    c: PointOnObject(g8,g13)
    c: PointOnObject(g9,g13)
    c: PointOnObject(g10,g13)
    c: PointOnObject(g11,g13)
    c: PointOnObject(g12,g13)
    c: PointOnObject(g13,g-1)
    c: Diameter(g13) = 7
    c: Distance(g6,g13) = 8
    c: Horizontal(g0,g10)
    c: Coincident(g14,g15)
    c: Coincident(g15,g16)
    c: Coincident(g16,g17)
    c: Coincident(g17,g18)
    c: Coincident(g18,g19)
    c: Coincident(g19,g14)
    c: Equal(g14, g15-g19) x5
    c: PointOnObject(g14,g20)
    c: PointOnObject(g15,g20)
    c: PointOnObject(g16,g20)
    c: PointOnObject(g17,g20)
    c: PointOnObject(g18,g20)
    c: PointOnObject(g19,g20)
    c: Diameter(g20) = 7
    c: DistanceY(g-1,g20) = 7
    c: Vertical(g18)
    c: Distance(g17,g-2) = 1
    c: Coincident(g21,g22)
    c: Coincident(g22,g23)
    c: Coincident(g23,g24)
    c: Coincident(g24,g25)
    c: Coincident(g25,g26)
    c: Coincident(g26,g21)
    c: Equal(g21, g22-g26) x5
    c: PointOnObject(g21,g27)
    c: PointOnObject(g22,g27)
    c: PointOnObject(g23,g27)
    c: PointOnObject(g24,g27)
    c: PointOnObject(g25,g27)
    c: PointOnObject(g26,g27)
    c: Diameter(g27) = 7
    c: DistanceY(g-1,g27) = 7
    c: DistanceX(g21,g-1) = 1
    c: Vertical(g21)
    c: Coincident(g28,g29)
    c: Coincident(g29,g30)
    c: Coincident(g30,g31)
    c: Coincident(g31,g32)
    c: Coincident(g32,g33)
    c: Coincident(g33,g28)
    c: Equal(g28, g29-g33) x5
    c: PointOnObject(g28,g34)
    c: PointOnObject(g29,g34)
    c: PointOnObject(g30,g34)
    c: PointOnObject(g31,g34)
    c: PointOnObject(g32,g34)
    c: PointOnObject(g33,g34)
    c: PointOnObject(g34,g-1)
    c: Diameter(g34) = 7
    c: Vertical(g31)
    c: DistanceX(g34,g-1) = 8
    c: Coincident(g35,g36)
    c: Coincident(g36,g37)
    c: Coincident(g37,g38)
    c: Coincident(g38,g39)
    c: Coincident(g39,g40)
    c: Coincident(g40,g35)
    c: Equal(g35, g36-g40) x5
    c: PointOnObject(g35,g41)
    c: PointOnObject(g36,g41)
    c: PointOnObject(g37,g41)
    c: PointOnObject(g38,g41)
    c: PointOnObject(g39,g41)
    c: PointOnObject(g40,g41)
    c: Coincident(g42,g43)
    c: Coincident(g43,g44)
    c: Coincident(g44,g45)
    c: Coincident(g45,g46)
    c: Coincident(g46,g47)
    c: Coincident(g47,g42)
    c: Equal(g42, g43-g47) x5
    c: PointOnObject(g42,g48)
    c: PointOnObject(g43,g48)
    c: PointOnObject(g44,g48)
    c: PointOnObject(g45,g48)
    c: PointOnObject(g46,g48)
    c: PointOnObject(g47,g48)
    c: Equal(g41,g48)
    c: Diameter(g41) = 7
    c: Vertical(g39)
    c: Vertical(g43)
    c: Distance(g-2,g39) = 1
    c: Symmetric(g38,g43,g-2)
    c: Distance(g41,g-1) = 7
FEATURE [Part::Extrusion] Extrude396  label="hex011"
  Base = -> Sketch404
  Dir = (0,-1,2e-16)
  DirMode = 2
  FaceMakerClass = Part::FaceMakerBullseye
  FaceMakerMode = 3
  LengthFwd = 10
  LengthRev = 0
  Placement = pos=(-36,0,7) rot=(0,0,1;0rad)
  Solid = true
  Symmetric = false
FEATURE [Sketcher::SketchObject] Sketch405
  ArcFitTolerance = 1e-06
  FullyConstrained = true
  MakeInternals = false
  Placement = pos=(0,0,0) rot=(1,0,0;1.5708rad)
  sketch-geometry (49):
    g0: LineSegment StartX=1e-16 StartY=3.5 StartZ=0 EndX=-3.03109 EndY=1.75 EndZ=0
    g1: LineSegment StartX=-3.03109 StartY=1.75 StartZ=0 EndX=-3.03109 EndY=-1.75 EndZ=0
    g2: LineSegment StartX=-3.03109 StartY=-1.75 StartZ=0 EndX=-1e-16 EndY=-3.5 EndZ=0
    g3: LineSegment StartX=-1e-16 StartY=-3.5 StartZ=0 EndX=3.03109 EndY=-1.75 EndZ=0
    g4: LineSegment StartX=3.03109 StartY=-1.75 StartZ=0 EndX=3.03109 EndY=1.75 EndZ=0
    g5: LineSegment StartX=3.03109 StartY=1.75 StartZ=0 EndX=1e-16 EndY=3.5 EndZ=0
    g6: Circle [constr] CenterX=0 CenterY=0 CenterZ=0 NormalX=0 NormalY=0 NormalZ=1 AngleXU=0 Radius=3.5
    g7: LineSegment StartX=4.96892 StartY=-1.75002 StartZ=0 EndX=8.00002 EndY=-3.5 EndZ=0
    g8: LineSegment StartX=8.00002 StartY=-3.5 StartZ=0 EndX=11.0311 EndY=-1.74998 EndZ=0
    g9: LineSegment StartX=11.0311 StartY=-1.74998 StartZ=0 EndX=11.0311 EndY=1.75002 EndZ=0
    g10: LineSegment StartX=11.0311 StartY=1.75002 StartZ=0 EndX=7.99998 EndY=3.5 EndZ=0
    g11: LineSegment StartX=7.99998 StartY=3.5 StartZ=0 EndX=4.9689 EndY=1.74998 EndZ=0
    g12: LineSegment StartX=4.9689 StartY=1.74998 StartZ=0 EndX=4.96892 EndY=-1.75002 EndZ=0
    g13: Circle [constr] CenterX=8 CenterY=0 CenterZ=0 NormalX=0 NormalY=0 NormalZ=1 AngleXU=0 Radius=3.5
    g14: LineSegment StartX=4.03109 StartY=3.5 StartZ=0 EndX=7.06218 EndY=5.25 EndZ=0
    g15: LineSegment StartX=7.06218 StartY=5.25 StartZ=0 EndX=7.06218 EndY=8.75 EndZ=0
    g16: LineSegment StartX=7.06218 StartY=8.75 StartZ=0 EndX=4.03109 EndY=10.5 EndZ=0
    g17: LineSegment StartX=4.03109 StartY=10.5 StartZ=0 EndX=1 EndY=8.75 EndZ=0
    g18: LineSegment StartX=1 StartY=8.75 StartZ=0 EndX=1 EndY=5.25 EndZ=0
    g19: LineSegment StartX=1 StartY=5.25 StartZ=0 EndX=4.03109 EndY=3.5 EndZ=0
    g20: Circle [constr] CenterX=4.03109 CenterY=7 CenterZ=0 NormalX=0 NormalY=0 NormalZ=1 AngleXU=0 Radius=3.5
    g21: LineSegment StartX=-1 StartY=5.25 StartZ=0 EndX=-1 EndY=8.75 EndZ=0
    g22: LineSegment StartX=-1 StartY=8.75 StartZ=0 EndX=-4.03109 EndY=10.5 EndZ=0
    g23: LineSegment StartX=-4.03109 StartY=10.5 StartZ=0 EndX=-7.06218 EndY=8.75 EndZ=0
    g24: LineSegment StartX=-7.06218 StartY=8.75 StartZ=0 EndX=-7.06218 EndY=5.25 EndZ=0
    g25: LineSegment StartX=-7.06218 StartY=5.25 StartZ=0 EndX=-4.03109 EndY=3.5 EndZ=0
    g26: LineSegment StartX=-4.03109 StartY=3.5 StartZ=0 EndX=-1 EndY=5.25 EndZ=0
    g27: Circle [constr] CenterX=-4.03109 CenterY=7 CenterZ=0 NormalX=0 NormalY=0 NormalZ=1 AngleXU=0 Radius=3.5
    g28: LineSegment StartX=-4.96891 StartY=-1.75 StartZ=0 EndX=-4.96891 EndY=1.75 EndZ=0
    g29: LineSegment StartX=-4.96891 StartY=1.75 StartZ=0 EndX=-8 EndY=3.5 EndZ=0
    g30: LineSegment StartX=-8 StartY=3.5 StartZ=0 EndX=-11.0311 EndY=1.75 EndZ=0
    g31: LineSegment StartX=-11.0311 StartY=1.75 StartZ=0 EndX=-11.0311 EndY=-1.75 EndZ=0
    g32: LineSegment StartX=-11.0311 StartY=-1.75 StartZ=0 EndX=-8 EndY=-3.5 EndZ=0
    g33: LineSegment StartX=-8 StartY=-3.5 StartZ=0 EndX=-4.96891 EndY=-1.75 EndZ=0
    g34: Circle [constr] CenterX=-8 CenterY=0 CenterZ=0 NormalX=0 NormalY=0 NormalZ=1 AngleXU=0 Radius=3.5
    g35: LineSegment StartX=-4.03109 StartY=-3.5 StartZ=0 EndX=-7.06218 EndY=-5.25 EndZ=0
    g36: LineSegment StartX=-7.06218 StartY=-5.25 StartZ=0 EndX=-7.06218 EndY=-8.75 EndZ=0
    g37: LineSegment StartX=-7.06218 StartY=-8.75 StartZ=0 EndX=-4.03109 EndY=-10.5 EndZ=0
    g38: LineSegment StartX=-4.03109 StartY=-10.5 StartZ=0 EndX=-1 EndY=-8.75 EndZ=0
    g39: LineSegment StartX=-1 StartY=-8.75 StartZ=0 EndX=-1 EndY=-5.25 EndZ=0
    g40: LineSegment StartX=-1 StartY=-5.25 StartZ=0 EndX=-4.03109 EndY=-3.5 EndZ=0
    g41: Circle [constr] CenterX=-4.03109 CenterY=-7 CenterZ=0 NormalX=0 NormalY=0 NormalZ=1 AngleXU=0 Radius=3.5
    g42: LineSegment StartX=4.03109 StartY=-3.5 StartZ=0 EndX=1 EndY=-5.25 EndZ=0
    g43: LineSegment StartX=1 StartY=-5.25 StartZ=0 EndX=1 EndY=-8.75 EndZ=0
    g44: LineSegment StartX=1 StartY=-8.75 StartZ=0 EndX=4.03109 EndY=-10.5 EndZ=0
    g45: LineSegment StartX=4.03109 StartY=-10.5 StartZ=0 EndX=7.06218 EndY=-8.75 EndZ=0
    g46: LineSegment StartX=7.06218 StartY=-8.75 StartZ=0 EndX=7.06218 EndY=-5.25 EndZ=0
    g47: LineSegment StartX=7.06218 StartY=-5.25 StartZ=0 EndX=4.03109 EndY=-3.5 EndZ=0
    g48: Circle [constr] CenterX=4.03109 CenterY=-7 CenterZ=0 NormalX=0 NormalY=0 NormalZ=1 AngleXU=0 Radius=3.5
  constraints (117):
    c: Coincident(g0,g1)
    c: Coincident(g1,g2)
    c: Coincident(g2,g3)
    c: Coincident(g3,g4)
    c: Coincident(g4,g5)
    c: Coincident(g5,g0)
    c: Equal(g0, g1-g5) x5
    c: PointOnObject(g0,g6)
    c: PointOnObject(g1,g6)
    c: PointOnObject(g2,g6)
    c: PointOnObject(g3,g6)
    c: PointOnObject(g4,g6)
    c: PointOnObject(g5,g6)
    c: Coincident(g6,g-1)
    c: Diameter(g6) = 7
    c: PointOnObject(g0,g-2)
    c: Coincident(g7,g8)
    c: Coincident(g8,g9)
    c: Coincident(g9,g10)
    c: Coincident(g10,g11)
    c: Coincident(g11,g12)
    c: Coincident(g12,g7)
    c: Equal(g7, g8-g12) x5
    c: PointOnObject(g7,g13)
    c: PointOnObject(g8,g13)
    c: PointOnObject(g9,g13)
    c: PointOnObject(g10,g13)
    c: PointOnObject(g11,g13)
    c: PointOnObject(g12,g13)
    c: PointOnObject(g13,g-1)
    c: Diameter(g13) = 7
    c: Distance(g6,g13) = 8
    c: Horizontal(g0,g10)
    c: Coincident(g14,g15)
    c: Coincident(g15,g16)
    c: Coincident(g16,g17)
    c: Coincident(g17,g18)
    c: Coincident(g18,g19)
    c: Coincident(g19,g14)
    c: Equal(g14, g15-g19) x5
    c: PointOnObject(g14,g20)
    c: PointOnObject(g15,g20)
    c: PointOnObject(g16,g20)
    c: PointOnObject(g17,g20)
    c: PointOnObject(g18,g20)
    c: PointOnObject(g19,g20)
    c: Diameter(g20) = 7
    c: DistanceY(g-1,g20) = 7
    c: Vertical(g18)
    c: Distance(g17,g-2) = 1
    c: Coincident(g21,g22)
    c: Coincident(g22,g23)
    c: Coincident(g23,g24)
    c: Coincident(g24,g25)
    c: Coincident(g25,g26)
    c: Coincident(g26,g21)
    c: Equal(g21, g22-g26) x5
    c: PointOnObject(g21,g27)
    c: PointOnObject(g22,g27)
    c: PointOnObject(g23,g27)
    c: PointOnObject(g24,g27)
    c: PointOnObject(g25,g27)
    c: PointOnObject(g26,g27)
    c: Diameter(g27) = 7
    c: DistanceY(g-1,g27) = 7
    c: DistanceX(g21,g-1) = 1
    c: Vertical(g21)
    c: Coincident(g28,g29)
    c: Coincident(g29,g30)
    c: Coincident(g30,g31)
    c: Coincident(g31,g32)
    c: Coincident(g32,g33)
    c: Coincident(g33,g28)
    c: Equal(g28, g29-g33) x5
    c: PointOnObject(g28,g34)
    c: PointOnObject(g29,g34)
    c: PointOnObject(g30,g34)
    c: PointOnObject(g31,g34)
    c: PointOnObject(g32,g34)
    c: PointOnObject(g33,g34)
    c: PointOnObject(g34,g-1)
    c: Diameter(g34) = 7
    c: Vertical(g31)
    c: DistanceX(g34,g-1) = 8
    c: Coincident(g35,g36)
    c: Coincident(g36,g37)
    c: Coincident(g37,g38)
    c: Coincident(g38,g39)
    c: Coincident(g39,g40)
    c: Coincident(g40,g35)
    c: Equal(g35, g36-g40) x5
    c: PointOnObject(g35,g41)
    c: PointOnObject(g36,g41)
    c: PointOnObject(g37,g41)
    c: PointOnObject(g38,g41)
    c: PointOnObject(g39,g41)
    c: PointOnObject(g40,g41)
    c: Coincident(g42,g43)
    c: Coincident(g43,g44)
    c: Coincident(g44,g45)
    c: Coincident(g45,g46)
    c: Coincident(g46,g47)
    c: Coincident(g47,g42)
    c: Equal(g42, g43-g47) x5
    c: PointOnObject(g42,g48)
    c: PointOnObject(g43,g48)
    c: PointOnObject(g44,g48)
    c: PointOnObject(g45,g48)
    c: PointOnObject(g46,g48)
    c: PointOnObject(g47,g48)
    c: Equal(g41,g48)
    c: Diameter(g41) = 7
    c: Vertical(g39)
    c: Vertical(g43)
    c: Distance(g-2,g39) = 1
    c: Symmetric(g38,g43,g-2)
    c: Distance(g41,g-1) = 7
FEATURE [Part::Extrusion] Extrude397  label="hex012"
  Base = -> Sketch405
  Dir = (0,-1,2e-16)
  DirMode = 2
  FaceMakerClass = Part::FaceMakerBullseye
  FaceMakerMode = 3
  LengthFwd = 10
  LengthRev = 0
  Placement = pos=(36,0,7) rot=(0,0,1;0rad)
  Solid = true
  Symmetric = false
FEATURE [Sketcher::SketchObject] Sketch406
  ArcFitTolerance = 1e-06
  FullyConstrained = true
  MakeInternals = false
  Placement = pos=(0,0,0) rot=(1,0,0;1.5708rad)
  sketch-geometry (49):
    g0: LineSegment StartX=1e-16 StartY=3.5 StartZ=0 EndX=-3.03109 EndY=1.75 EndZ=0
    g1: LineSegment StartX=-3.03109 StartY=1.75 StartZ=0 EndX=-3.03109 EndY=-1.75 EndZ=0
    g2: LineSegment StartX=-3.03109 StartY=-1.75 StartZ=0 EndX=-1e-16 EndY=-3.5 EndZ=0
    g3: LineSegment StartX=-1e-16 StartY=-3.5 StartZ=0 EndX=3.03109 EndY=-1.75 EndZ=0
    g4: LineSegment StartX=3.03109 StartY=-1.75 StartZ=0 EndX=3.03109 EndY=1.75 EndZ=0
    g5: LineSegment StartX=3.03109 StartY=1.75 StartZ=0 EndX=1e-16 EndY=3.5 EndZ=0
    g6: Circle [constr] CenterX=0 CenterY=0 CenterZ=0 NormalX=0 NormalY=0 NormalZ=1 AngleXU=0 Radius=3.5
    g7: LineSegment StartX=4.96892 StartY=-1.75002 StartZ=0 EndX=8.00002 EndY=-3.5 EndZ=0
    g8: LineSegment StartX=8.00002 StartY=-3.5 StartZ=0 EndX=11.0311 EndY=-1.74998 EndZ=0
    g9: LineSegment StartX=11.0311 StartY=-1.74998 StartZ=0 EndX=11.0311 EndY=1.75002 EndZ=0
    g10: LineSegment StartX=11.0311 StartY=1.75002 StartZ=0 EndX=7.99998 EndY=3.5 EndZ=0
    g11: LineSegment StartX=7.99998 StartY=3.5 StartZ=0 EndX=4.9689 EndY=1.74998 EndZ=0
    g12: LineSegment StartX=4.9689 StartY=1.74998 StartZ=0 EndX=4.96892 EndY=-1.75002 EndZ=0
    g13: Circle [constr] CenterX=8 CenterY=0 CenterZ=0 NormalX=0 NormalY=0 NormalZ=1 AngleXU=0 Radius=3.5
    g14: LineSegment StartX=4.03109 StartY=3.5 StartZ=0 EndX=7.06218 EndY=5.25 EndZ=0
    g15: LineSegment StartX=7.06218 StartY=5.25 StartZ=0 EndX=7.06218 EndY=8.75 EndZ=0
    g16: LineSegment StartX=7.06218 StartY=8.75 StartZ=0 EndX=4.03109 EndY=10.5 EndZ=0
    g17: LineSegment StartX=4.03109 StartY=10.5 StartZ=0 EndX=1 EndY=8.75 EndZ=0
    g18: LineSegment StartX=1 StartY=8.75 StartZ=0 EndX=1 EndY=5.25 EndZ=0
    g19: LineSegment StartX=1 StartY=5.25 StartZ=0 EndX=4.03109 EndY=3.5 EndZ=0
    g20: Circle [constr] CenterX=4.03109 CenterY=7 CenterZ=0 NormalX=0 NormalY=0 NormalZ=1 AngleXU=0 Radius=3.5
    g21: LineSegment StartX=-1 StartY=5.25 StartZ=0 EndX=-1 EndY=8.75 EndZ=0
    g22: LineSegment StartX=-1 StartY=8.75 StartZ=0 EndX=-4.03109 EndY=10.5 EndZ=0
    g23: LineSegment StartX=-4.03109 StartY=10.5 StartZ=0 EndX=-7.06218 EndY=8.75 EndZ=0
    g24: LineSegment StartX=-7.06218 StartY=8.75 StartZ=0 EndX=-7.06218 EndY=5.25 EndZ=0
    g25: LineSegment StartX=-7.06218 StartY=5.25 StartZ=0 EndX=-4.03109 EndY=3.5 EndZ=0
    g26: LineSegment StartX=-4.03109 StartY=3.5 StartZ=0 EndX=-1 EndY=5.25 EndZ=0
    g27: Circle [constr] CenterX=-4.03109 CenterY=7 CenterZ=0 NormalX=0 NormalY=0 NormalZ=1 AngleXU=0 Radius=3.5
    g28: LineSegment StartX=-4.96891 StartY=-1.75 StartZ=0 EndX=-4.96891 EndY=1.75 EndZ=0
    g29: LineSegment StartX=-4.96891 StartY=1.75 StartZ=0 EndX=-8 EndY=3.5 EndZ=0
    g30: LineSegment StartX=-8 StartY=3.5 StartZ=0 EndX=-11.0311 EndY=1.75 EndZ=0
    g31: LineSegment StartX=-11.0311 StartY=1.75 StartZ=0 EndX=-11.0311 EndY=-1.75 EndZ=0
    g32: LineSegment StartX=-11.0311 StartY=-1.75 StartZ=0 EndX=-8 EndY=-3.5 EndZ=0
    g33: LineSegment StartX=-8 StartY=-3.5 StartZ=0 EndX=-4.96891 EndY=-1.75 EndZ=0
    g34: Circle [constr] CenterX=-8 CenterY=0 CenterZ=0 NormalX=0 NormalY=0 NormalZ=1 AngleXU=0 Radius=3.5
    g35: LineSegment StartX=-4.03109 StartY=-3.5 StartZ=0 EndX=-7.06218 EndY=-5.25 EndZ=0
    g36: LineSegment StartX=-7.06218 StartY=-5.25 StartZ=0 EndX=-7.06218 EndY=-8.75 EndZ=0
    g37: LineSegment StartX=-7.06218 StartY=-8.75 StartZ=0 EndX=-4.03109 EndY=-10.5 EndZ=0
    g38: LineSegment StartX=-4.03109 StartY=-10.5 StartZ=0 EndX=-1 EndY=-8.75 EndZ=0
    g39: LineSegment StartX=-1 StartY=-8.75 StartZ=0 EndX=-1 EndY=-5.25 EndZ=0
    g40: LineSegment StartX=-1 StartY=-5.25 StartZ=0 EndX=-4.03109 EndY=-3.5 EndZ=0
    g41: Circle [constr] CenterX=-4.03109 CenterY=-7 CenterZ=0 NormalX=0 NormalY=0 NormalZ=1 AngleXU=0 Radius=3.5
    g42: LineSegment StartX=4.03109 StartY=-3.5 StartZ=0 EndX=1 EndY=-5.25 EndZ=0
    g43: LineSegment StartX=1 StartY=-5.25 StartZ=0 EndX=1 EndY=-8.75 EndZ=0
    g44: LineSegment StartX=1 StartY=-8.75 StartZ=0 EndX=4.03109 EndY=-10.5 EndZ=0
    g45: LineSegment StartX=4.03109 StartY=-10.5 StartZ=0 EndX=7.06218 EndY=-8.75 EndZ=0
    g46: LineSegment StartX=7.06218 StartY=-8.75 StartZ=0 EndX=7.06218 EndY=-5.25 EndZ=0
    g47: LineSegment StartX=7.06218 StartY=-5.25 StartZ=0 EndX=4.03109 EndY=-3.5 EndZ=0
    g48: Circle [constr] CenterX=4.03109 CenterY=-7 CenterZ=0 NormalX=0 NormalY=0 NormalZ=1 AngleXU=0 Radius=3.5
  constraints (117):
    c: Coincident(g0,g1)
    c: Coincident(g1,g2)
    c: Coincident(g2,g3)
    c: Coincident(g3,g4)
    c: Coincident(g4,g5)
    c: Coincident(g5,g0)
    c: Equal(g0, g1-g5) x5
    c: PointOnObject(g0,g6)
    c: PointOnObject(g1,g6)
    c: PointOnObject(g2,g6)
    c: PointOnObject(g3,g6)
    c: PointOnObject(g4,g6)
    c: PointOnObject(g5,g6)
    c: Coincident(g6,g-1)
    c: Diameter(g6) = 7
    c: PointOnObject(g0,g-2)
    c: Coincident(g7,g8)
    c: Coincident(g8,g9)
    c: Coincident(g9,g10)
    c: Coincident(g10,g11)
    c: Coincident(g11,g12)
    c: Coincident(g12,g7)
    c: Equal(g7, g8-g12) x5
    c: PointOnObject(g7,g13)
    c: PointOnObject(g8,g13)
    c: PointOnObject(g9,g13)
    c: PointOnObject(g10,g13)
    c: PointOnObject(g11,g13)
    c: PointOnObject(g12,g13)
    c: PointOnObject(g13,g-1)
    c: Diameter(g13) = 7
    c: Distance(g6,g13) = 8
    c: Horizontal(g0,g10)
    c: Coincident(g14,g15)
    c: Coincident(g15,g16)
    c: Coincident(g16,g17)
    c: Coincident(g17,g18)
    c: Coincident(g18,g19)
    c: Coincident(g19,g14)
    c: Equal(g14, g15-g19) x5
    c: PointOnObject(g14,g20)
    c: PointOnObject(g15,g20)
    c: PointOnObject(g16,g20)
    c: PointOnObject(g17,g20)
    c: PointOnObject(g18,g20)
    c: PointOnObject(g19,g20)
    c: Diameter(g20) = 7
    c: DistanceY(g-1,g20) = 7
    c: Vertical(g18)
    c: Distance(g17,g-2) = 1
    c: Coincident(g21,g22)
    c: Coincident(g22,g23)
    c: Coincident(g23,g24)
    c: Coincident(g24,g25)
    c: Coincident(g25,g26)
    c: Coincident(g26,g21)
    c: Equal(g21, g22-g26) x5
    c: PointOnObject(g21,g27)
    c: PointOnObject(g22,g27)
    c: PointOnObject(g23,g27)
    c: PointOnObject(g24,g27)
    c: PointOnObject(g25,g27)
    c: PointOnObject(g26,g27)
    c: Diameter(g27) = 7
    c: DistanceY(g-1,g27) = 7
    c: DistanceX(g21,g-1) = 1
    c: Vertical(g21)
    c: Coincident(g28,g29)
    c: Coincident(g29,g30)
    c: Coincident(g30,g31)
    c: Coincident(g31,g32)
    c: Coincident(g32,g33)
    c: Coincident(g33,g28)
    c: Equal(g28, g29-g33) x5
    c: PointOnObject(g28,g34)
    c: PointOnObject(g29,g34)
    c: PointOnObject(g30,g34)
    c: PointOnObject(g31,g34)
    c: PointOnObject(g32,g34)
    c: PointOnObject(g33,g34)
    c: PointOnObject(g34,g-1)
    c: Diameter(g34) = 7
    c: Vertical(g31)
    c: DistanceX(g34,g-1) = 8
    c: Coincident(g35,g36)
    c: Coincident(g36,g37)
    c: Coincident(g37,g38)
    c: Coincident(g38,g39)
    c: Coincident(g39,g40)
    c: Coincident(g40,g35)
    c: Equal(g35, g36-g40) x5
    c: PointOnObject(g35,g41)
    c: PointOnObject(g36,g41)
    c: PointOnObject(g37,g41)
    c: PointOnObject(g38,g41)
    c: PointOnObject(g39,g41)
    c: PointOnObject(g40,g41)
    c: Coincident(g42,g43)
    c: Coincident(g43,g44)
    c: Coincident(g44,g45)
    c: Coincident(g45,g46)
    c: Coincident(g46,g47)
    c: Coincident(g47,g42)
    c: Equal(g42, g43-g47) x5
    c: PointOnObject(g42,g48)
    c: PointOnObject(g43,g48)
    c: PointOnObject(g44,g48)
    c: PointOnObject(g45,g48)
    c: PointOnObject(g46,g48)
    c: PointOnObject(g47,g48)
    c: Equal(g41,g48)
    c: Diameter(g41) = 7
    c: Vertical(g39)
    c: Vertical(g43)
    c: Distance(g-2,g39) = 1
    c: Symmetric(g38,g43,g-2)
    c: Distance(g41,g-1) = 7
FEATURE [Part::Extrusion] Extrude398  label="hex013"
  Base = -> Sketch406
  Dir = (0,-1,2e-16)
  DirMode = 2
  FaceMakerClass = Part::FaceMakerBullseye
  FaceMakerMode = 3
  LengthFwd = 10
  LengthRev = 0
  Placement = pos=(32,0,28) rot=(0,0,1;0rad)
  Solid = true
  Symmetric = false
FEATURE [Sketcher::SketchObject] Sketch407
  ArcFitTolerance = 1e-06
  FullyConstrained = true
  MakeInternals = false
  Placement = pos=(0,0,0) rot=(1,0,0;1.5708rad)
  sketch-geometry (49):
    g0: LineSegment StartX=1e-16 StartY=3.5 StartZ=0 EndX=-3.03109 EndY=1.75 EndZ=0
    g1: LineSegment StartX=-3.03109 StartY=1.75 StartZ=0 EndX=-3.03109 EndY=-1.75 EndZ=0
    g2: LineSegment StartX=-3.03109 StartY=-1.75 StartZ=0 EndX=-1e-16 EndY=-3.5 EndZ=0
    g3: LineSegment StartX=-1e-16 StartY=-3.5 StartZ=0 EndX=3.03109 EndY=-1.75 EndZ=0
    g4: LineSegment StartX=3.03109 StartY=-1.75 StartZ=0 EndX=3.03109 EndY=1.75 EndZ=0
    g5: LineSegment StartX=3.03109 StartY=1.75 StartZ=0 EndX=1e-16 EndY=3.5 EndZ=0
    g6: Circle [constr] CenterX=0 CenterY=0 CenterZ=0 NormalX=0 NormalY=0 NormalZ=1 AngleXU=0 Radius=3.5
    g7: LineSegment StartX=4.96892 StartY=-1.75002 StartZ=0 EndX=8.00002 EndY=-3.5 EndZ=0
    g8: LineSegment StartX=8.00002 StartY=-3.5 StartZ=0 EndX=11.0311 EndY=-1.74998 EndZ=0
    g9: LineSegment StartX=11.0311 StartY=-1.74998 StartZ=0 EndX=11.0311 EndY=1.75002 EndZ=0
    g10: LineSegment StartX=11.0311 StartY=1.75002 StartZ=0 EndX=7.99998 EndY=3.5 EndZ=0
    g11: LineSegment StartX=7.99998 StartY=3.5 StartZ=0 EndX=4.9689 EndY=1.74998 EndZ=0
    g12: LineSegment StartX=4.9689 StartY=1.74998 StartZ=0 EndX=4.96892 EndY=-1.75002 EndZ=0
    g13: Circle [constr] CenterX=8 CenterY=0 CenterZ=0 NormalX=0 NormalY=0 NormalZ=1 AngleXU=0 Radius=3.5
    g14: LineSegment StartX=4.03109 StartY=3.5 StartZ=0 EndX=7.06218 EndY=5.25 EndZ=0
    g15: LineSegment StartX=7.06218 StartY=5.25 StartZ=0 EndX=7.06218 EndY=8.75 EndZ=0
    g16: LineSegment StartX=7.06218 StartY=8.75 StartZ=0 EndX=4.03109 EndY=10.5 EndZ=0
    g17: LineSegment StartX=4.03109 StartY=10.5 StartZ=0 EndX=1 EndY=8.75 EndZ=0
    g18: LineSegment StartX=1 StartY=8.75 StartZ=0 EndX=1 EndY=5.25 EndZ=0
    g19: LineSegment StartX=1 StartY=5.25 StartZ=0 EndX=4.03109 EndY=3.5 EndZ=0
    g20: Circle [constr] CenterX=4.03109 CenterY=7 CenterZ=0 NormalX=0 NormalY=0 NormalZ=1 AngleXU=0 Radius=3.5
    g21: LineSegment StartX=-1 StartY=5.25 StartZ=0 EndX=-1 EndY=8.75 EndZ=0
    g22: LineSegment StartX=-1 StartY=8.75 StartZ=0 EndX=-4.03109 EndY=10.5 EndZ=0
    g23: LineSegment StartX=-4.03109 StartY=10.5 StartZ=0 EndX=-7.06218 EndY=8.75 EndZ=0
    g24: LineSegment StartX=-7.06218 StartY=8.75 StartZ=0 EndX=-7.06218 EndY=5.25 EndZ=0
    g25: LineSegment StartX=-7.06218 StartY=5.25 StartZ=0 EndX=-4.03109 EndY=3.5 EndZ=0
    g26: LineSegment StartX=-4.03109 StartY=3.5 StartZ=0 EndX=-1 EndY=5.25 EndZ=0
    g27: Circle [constr] CenterX=-4.03109 CenterY=7 CenterZ=0 NormalX=0 NormalY=0 NormalZ=1 AngleXU=0 Radius=3.5
    g28: LineSegment StartX=-4.96891 StartY=-1.75 StartZ=0 EndX=-4.96891 EndY=1.75 EndZ=0
    g29: LineSegment StartX=-4.96891 StartY=1.75 StartZ=0 EndX=-8 EndY=3.5 EndZ=0
    g30: LineSegment StartX=-8 StartY=3.5 StartZ=0 EndX=-11.0311 EndY=1.75 EndZ=0
    g31: LineSegment StartX=-11.0311 StartY=1.75 StartZ=0 EndX=-11.0311 EndY=-1.75 EndZ=0
    g32: LineSegment StartX=-11.0311 StartY=-1.75 StartZ=0 EndX=-8 EndY=-3.5 EndZ=0
    g33: LineSegment StartX=-8 StartY=-3.5 StartZ=0 EndX=-4.96891 EndY=-1.75 EndZ=0
    g34: Circle [constr] CenterX=-8 CenterY=0 CenterZ=0 NormalX=0 NormalY=0 NormalZ=1 AngleXU=0 Radius=3.5
    g35: LineSegment StartX=-4.03109 StartY=-3.5 StartZ=0 EndX=-7.06218 EndY=-5.25 EndZ=0
    g36: LineSegment StartX=-7.06218 StartY=-5.25 StartZ=0 EndX=-7.06218 EndY=-8.75 EndZ=0
    g37: LineSegment StartX=-7.06218 StartY=-8.75 StartZ=0 EndX=-4.03109 EndY=-10.5 EndZ=0
    g38: LineSegment StartX=-4.03109 StartY=-10.5 StartZ=0 EndX=-1 EndY=-8.75 EndZ=0
    g39: LineSegment StartX=-1 StartY=-8.75 StartZ=0 EndX=-1 EndY=-5.25 EndZ=0
    g40: LineSegment StartX=-1 StartY=-5.25 StartZ=0 EndX=-4.03109 EndY=-3.5 EndZ=0
    g41: Circle [constr] CenterX=-4.03109 CenterY=-7 CenterZ=0 NormalX=0 NormalY=0 NormalZ=1 AngleXU=0 Radius=3.5
    g42: LineSegment StartX=4.03109 StartY=-3.5 StartZ=0 EndX=1 EndY=-5.25 EndZ=0
    g43: LineSegment StartX=1 StartY=-5.25 StartZ=0 EndX=1 EndY=-8.75 EndZ=0
    g44: LineSegment StartX=1 StartY=-8.75 StartZ=0 EndX=4.03109 EndY=-10.5 EndZ=0
    g45: LineSegment StartX=4.03109 StartY=-10.5 StartZ=0 EndX=7.06218 EndY=-8.75 EndZ=0
    g46: LineSegment StartX=7.06218 StartY=-8.75 StartZ=0 EndX=7.06218 EndY=-5.25 EndZ=0
    g47: LineSegment StartX=7.06218 StartY=-5.25 StartZ=0 EndX=4.03109 EndY=-3.5 EndZ=0
    g48: Circle [constr] CenterX=4.03109 CenterY=-7 CenterZ=0 NormalX=0 NormalY=0 NormalZ=1 AngleXU=0 Radius=3.5
  constraints (117):
    c: Coincident(g0,g1)
    c: Coincident(g1,g2)
    c: Coincident(g2,g3)
    c: Coincident(g3,g4)
    c: Coincident(g4,g5)
    c: Coincident(g5,g0)
    c: Equal(g0, g1-g5) x5
    c: PointOnObject(g0,g6)
    c: PointOnObject(g1,g6)
    c: PointOnObject(g2,g6)
    c: PointOnObject(g3,g6)
    c: PointOnObject(g4,g6)
    c: PointOnObject(g5,g6)
    c: Coincident(g6,g-1)
    c: Diameter(g6) = 7
    c: PointOnObject(g0,g-2)
    c: Coincident(g7,g8)
    c: Coincident(g8,g9)
    c: Coincident(g9,g10)
    c: Coincident(g10,g11)
    c: Coincident(g11,g12)
    c: Coincident(g12,g7)
    c: Equal(g7, g8-g12) x5
    c: PointOnObject(g7,g13)
    c: PointOnObject(g8,g13)
    c: PointOnObject(g9,g13)
    c: PointOnObject(g10,g13)
    c: PointOnObject(g11,g13)
    c: PointOnObject(g12,g13)
    c: PointOnObject(g13,g-1)
    c: Diameter(g13) = 7
    c: Distance(g6,g13) = 8
    c: Horizontal(g0,g10)
    c: Coincident(g14,g15)
    c: Coincident(g15,g16)
    c: Coincident(g16,g17)
    c: Coincident(g17,g18)
    c: Coincident(g18,g19)
    c: Coincident(g19,g14)
    c: Equal(g14, g15-g19) x5
    c: PointOnObject(g14,g20)
    c: PointOnObject(g15,g20)
    c: PointOnObject(g16,g20)
    c: PointOnObject(g17,g20)
    c: PointOnObject(g18,g20)
    c: PointOnObject(g19,g20)
    c: Diameter(g20) = 7
    c: DistanceY(g-1,g20) = 7
    c: Vertical(g18)
    c: Distance(g17,g-2) = 1
    c: Coincident(g21,g22)
    c: Coincident(g22,g23)
    c: Coincident(g23,g24)
    c: Coincident(g24,g25)
    c: Coincident(g25,g26)
    c: Coincident(g26,g21)
    c: Equal(g21, g22-g26) x5
    c: PointOnObject(g21,g27)
    c: PointOnObject(g22,g27)
    c: PointOnObject(g23,g27)
    c: PointOnObject(g24,g27)
    c: PointOnObject(g25,g27)
    c: PointOnObject(g26,g27)
    c: Diameter(g27) = 7
    c: DistanceY(g-1,g27) = 7
    c: DistanceX(g21,g-1) = 1
    c: Vertical(g21)
    c: Coincident(g28,g29)
    c: Coincident(g29,g30)
    c: Coincident(g30,g31)
    c: Coincident(g31,g32)
    c: Coincident(g32,g33)
    c: Coincident(g33,g28)
    c: Equal(g28, g29-g33) x5
    c: PointOnObject(g28,g34)
    c: PointOnObject(g29,g34)
    c: PointOnObject(g30,g34)
    c: PointOnObject(g31,g34)
    c: PointOnObject(g32,g34)
    c: PointOnObject(g33,g34)
    c: PointOnObject(g34,g-1)
    c: Diameter(g34) = 7
    c: Vertical(g31)
    c: DistanceX(g34,g-1) = 8
    c: Coincident(g35,g36)
    c: Coincident(g36,g37)
    c: Coincident(g37,g38)
    c: Coincident(g38,g39)
    c: Coincident(g39,g40)
    c: Coincident(g40,g35)
    c: Equal(g35, g36-g40) x5
    c: PointOnObject(g35,g41)
    c: PointOnObject(g36,g41)
    c: PointOnObject(g37,g41)
    c: PointOnObject(g38,g41)
    c: PointOnObject(g39,g41)
    c: PointOnObject(g40,g41)
    c: Coincident(g42,g43)
    c: Coincident(g43,g44)
    c: Coincident(g44,g45)
    c: Coincident(g45,g46)
    c: Coincident(g46,g47)
    c: Coincident(g47,g42)
    c: Equal(g42, g43-g47) x5
    c: PointOnObject(g42,g48)
    c: PointOnObject(g43,g48)
    c: PointOnObject(g44,g48)
    c: PointOnObject(g45,g48)
    c: PointOnObject(g46,g48)
    c: PointOnObject(g47,g48)
    c: Equal(g41,g48)
    c: Diameter(g41) = 7
    c: Vertical(g39)
    c: Vertical(g43)
    c: Distance(g-2,g39) = 1
    c: Symmetric(g38,g43,g-2)
    c: Distance(g41,g-1) = 7
FEATURE [Part::Extrusion] Extrude399  label="hex014"
  Base = -> Sketch407
  Dir = (0,-1,2e-16)
  DirMode = 2
  FaceMakerClass = Part::FaceMakerBullseye
  FaceMakerMode = 3
  LengthFwd = 10
  LengthRev = 0
  Placement = pos=(-40,0,-14) rot=(0,0,1;0rad)
  Solid = true
  Symmetric = false
FEATURE [Sketcher::SketchObject] Sketch408
  ArcFitTolerance = 1e-06
  FullyConstrained = true
  MakeInternals = false
  Placement = pos=(0,0,0) rot=(1,0,0;1.5708rad)
  sketch-geometry (49):
    g0: LineSegment StartX=1e-16 StartY=3.5 StartZ=0 EndX=-3.03109 EndY=1.75 EndZ=0
    g1: LineSegment StartX=-3.03109 StartY=1.75 StartZ=0 EndX=-3.03109 EndY=-1.75 EndZ=0
    g2: LineSegment StartX=-3.03109 StartY=-1.75 StartZ=0 EndX=-1e-16 EndY=-3.5 EndZ=0
    g3: LineSegment StartX=-1e-16 StartY=-3.5 StartZ=0 EndX=3.03109 EndY=-1.75 EndZ=0
    g4: LineSegment StartX=3.03109 StartY=-1.75 StartZ=0 EndX=3.03109 EndY=1.75 EndZ=0
    g5: LineSegment StartX=3.03109 StartY=1.75 StartZ=0 EndX=1e-16 EndY=3.5 EndZ=0
    g6: Circle [constr] CenterX=0 CenterY=0 CenterZ=0 NormalX=0 NormalY=0 NormalZ=1 AngleXU=0 Radius=3.5
    g7: LineSegment StartX=4.96892 StartY=-1.75002 StartZ=0 EndX=8.00002 EndY=-3.5 EndZ=0
    g8: LineSegment StartX=8.00002 StartY=-3.5 StartZ=0 EndX=11.0311 EndY=-1.74998 EndZ=0
    g9: LineSegment StartX=11.0311 StartY=-1.74998 StartZ=0 EndX=11.0311 EndY=1.75002 EndZ=0
    g10: LineSegment StartX=11.0311 StartY=1.75002 StartZ=0 EndX=7.99998 EndY=3.5 EndZ=0
    g11: LineSegment StartX=7.99998 StartY=3.5 StartZ=0 EndX=4.9689 EndY=1.74998 EndZ=0
    g12: LineSegment StartX=4.9689 StartY=1.74998 StartZ=0 EndX=4.96892 EndY=-1.75002 EndZ=0
    g13: Circle [constr] CenterX=8 CenterY=0 CenterZ=0 NormalX=0 NormalY=0 NormalZ=1 AngleXU=0 Radius=3.5
    g14: LineSegment StartX=4.03109 StartY=3.5 StartZ=0 EndX=7.06218 EndY=5.25 EndZ=0
    g15: LineSegment StartX=7.06218 StartY=5.25 StartZ=0 EndX=7.06218 EndY=8.75 EndZ=0
    g16: LineSegment StartX=7.06218 StartY=8.75 StartZ=0 EndX=4.03109 EndY=10.5 EndZ=0
    g17: LineSegment StartX=4.03109 StartY=10.5 StartZ=0 EndX=1 EndY=8.75 EndZ=0
    g18: LineSegment StartX=1 StartY=8.75 StartZ=0 EndX=1 EndY=5.25 EndZ=0
    g19: LineSegment StartX=1 StartY=5.25 StartZ=0 EndX=4.03109 EndY=3.5 EndZ=0
    g20: Circle [constr] CenterX=4.03109 CenterY=7 CenterZ=0 NormalX=0 NormalY=0 NormalZ=1 AngleXU=0 Radius=3.5
    g21: LineSegment StartX=-1 StartY=5.25 StartZ=0 EndX=-1 EndY=8.75 EndZ=0
    g22: LineSegment StartX=-1 StartY=8.75 StartZ=0 EndX=-4.03109 EndY=10.5 EndZ=0
    g23: LineSegment StartX=-4.03109 StartY=10.5 StartZ=0 EndX=-7.06218 EndY=8.75 EndZ=0
    g24: LineSegment StartX=-7.06218 StartY=8.75 StartZ=0 EndX=-7.06218 EndY=5.25 EndZ=0
    g25: LineSegment StartX=-7.06218 StartY=5.25 StartZ=0 EndX=-4.03109 EndY=3.5 EndZ=0
    g26: LineSegment StartX=-4.03109 StartY=3.5 StartZ=0 EndX=-1 EndY=5.25 EndZ=0
    g27: Circle [constr] CenterX=-4.03109 CenterY=7 CenterZ=0 NormalX=0 NormalY=0 NormalZ=1 AngleXU=0 Radius=3.5
    g28: LineSegment StartX=-4.96891 StartY=-1.75 StartZ=0 EndX=-4.96891 EndY=1.75 EndZ=0
    g29: LineSegment StartX=-4.96891 StartY=1.75 StartZ=0 EndX=-8 EndY=3.5 EndZ=0
    g30: LineSegment StartX=-8 StartY=3.5 StartZ=0 EndX=-11.0311 EndY=1.75 EndZ=0
    g31: LineSegment StartX=-11.0311 StartY=1.75 StartZ=0 EndX=-11.0311 EndY=-1.75 EndZ=0
    g32: LineSegment StartX=-11.0311 StartY=-1.75 StartZ=0 EndX=-8 EndY=-3.5 EndZ=0
    g33: LineSegment StartX=-8 StartY=-3.5 StartZ=0 EndX=-4.96891 EndY=-1.75 EndZ=0
    g34: Circle [constr] CenterX=-8 CenterY=0 CenterZ=0 NormalX=0 NormalY=0 NormalZ=1 AngleXU=0 Radius=3.5
    g35: LineSegment StartX=-4.03109 StartY=-3.5 StartZ=0 EndX=-7.06218 EndY=-5.25 EndZ=0
    g36: LineSegment StartX=-7.06218 StartY=-5.25 StartZ=0 EndX=-7.06218 EndY=-8.75 EndZ=0
    g37: LineSegment StartX=-7.06218 StartY=-8.75 StartZ=0 EndX=-4.03109 EndY=-10.5 EndZ=0
    g38: LineSegment StartX=-4.03109 StartY=-10.5 StartZ=0 EndX=-1 EndY=-8.75 EndZ=0
    g39: LineSegment StartX=-1 StartY=-8.75 StartZ=0 EndX=-1 EndY=-5.25 EndZ=0
    g40: LineSegment StartX=-1 StartY=-5.25 StartZ=0 EndX=-4.03109 EndY=-3.5 EndZ=0
    g41: Circle [constr] CenterX=-4.03109 CenterY=-7 CenterZ=0 NormalX=0 NormalY=0 NormalZ=1 AngleXU=0 Radius=3.5
    g42: LineSegment StartX=4.03109 StartY=-3.5 StartZ=0 EndX=1 EndY=-5.25 EndZ=0
    g43: LineSegment StartX=1 StartY=-5.25 StartZ=0 EndX=1 EndY=-8.75 EndZ=0
    g44: LineSegment StartX=1 StartY=-8.75 StartZ=0 EndX=4.03109 EndY=-10.5 EndZ=0
    g45: LineSegment StartX=4.03109 StartY=-10.5 StartZ=0 EndX=7.06218 EndY=-8.75 EndZ=0
    g46: LineSegment StartX=7.06218 StartY=-8.75 StartZ=0 EndX=7.06218 EndY=-5.25 EndZ=0
    g47: LineSegment StartX=7.06218 StartY=-5.25 StartZ=0 EndX=4.03109 EndY=-3.5 EndZ=0
    g48: Circle [constr] CenterX=4.03109 CenterY=-7 CenterZ=0 NormalX=0 NormalY=0 NormalZ=1 AngleXU=0 Radius=3.5
  constraints (117):
    c: Coincident(g0,g1)
    c: Coincident(g1,g2)
    c: Coincident(g2,g3)
    c: Coincident(g3,g4)
    c: Coincident(g4,g5)
    c: Coincident(g5,g0)
    c: Equal(g0, g1-g5) x5
    c: PointOnObject(g0,g6)
    c: PointOnObject(g1,g6)
    c: PointOnObject(g2,g6)
    c: PointOnObject(g3,g6)
    c: PointOnObject(g4,g6)
    c: PointOnObject(g5,g6)
    c: Coincident(g6,g-1)
    c: Diameter(g6) = 7
    c: PointOnObject(g0,g-2)
    c: Coincident(g7,g8)
    c: Coincident(g8,g9)
    c: Coincident(g9,g10)
    c: Coincident(g10,g11)
    c: Coincident(g11,g12)
    c: Coincident(g12,g7)
    c: Equal(g7, g8-g12) x5
    c: PointOnObject(g7,g13)
    c: PointOnObject(g8,g13)
    c: PointOnObject(g9,g13)
    c: PointOnObject(g10,g13)
    c: PointOnObject(g11,g13)
    c: PointOnObject(g12,g13)
    c: PointOnObject(g13,g-1)
    c: Diameter(g13) = 7
    c: Distance(g6,g13) = 8
    c: Horizontal(g0,g10)
    c: Coincident(g14,g15)
    c: Coincident(g15,g16)
    c: Coincident(g16,g17)
    c: Coincident(g17,g18)
    c: Coincident(g18,g19)
    c: Coincident(g19,g14)
    c: Equal(g14, g15-g19) x5
    c: PointOnObject(g14,g20)
    c: PointOnObject(g15,g20)
    c: PointOnObject(g16,g20)
    c: PointOnObject(g17,g20)
    c: PointOnObject(g18,g20)
    c: PointOnObject(g19,g20)
    c: Diameter(g20) = 7
    c: DistanceY(g-1,g20) = 7
    c: Vertical(g18)
    c: Distance(g17,g-2) = 1
    c: Coincident(g21,g22)
    c: Coincident(g22,g23)
    c: Coincident(g23,g24)
    c: Coincident(g24,g25)
    c: Coincident(g25,g26)
    c: Coincident(g26,g21)
    c: Equal(g21, g22-g26) x5
    c: PointOnObject(g21,g27)
    c: PointOnObject(g22,g27)
    c: PointOnObject(g23,g27)
    c: PointOnObject(g24,g27)
    c: PointOnObject(g25,g27)
    c: PointOnObject(g26,g27)
    c: Diameter(g27) = 7
    c: DistanceY(g-1,g27) = 7
    c: DistanceX(g21,g-1) = 1
    c: Vertical(g21)
    c: Coincident(g28,g29)
    c: Coincident(g29,g30)
    c: Coincident(g30,g31)
    c: Coincident(g31,g32)
    c: Coincident(g32,g33)
    c: Coincident(g33,g28)
    c: Equal(g28, g29-g33) x5
    c: PointOnObject(g28,g34)
    c: PointOnObject(g29,g34)
    c: PointOnObject(g30,g34)
    c: PointOnObject(g31,g34)
    c: PointOnObject(g32,g34)
    c: PointOnObject(g33,g34)
    c: PointOnObject(g34,g-1)
    c: Diameter(g34) = 7
    c: Vertical(g31)
    c: DistanceX(g34,g-1) = 8
    c: Coincident(g35,g36)
    c: Coincident(g36,g37)
    c: Coincident(g37,g38)
    c: Coincident(g38,g39)
    c: Coincident(g39,g40)
    c: Coincident(g40,g35)
    c: Equal(g35, g36-g40) x5
    c: PointOnObject(g35,g41)
    c: PointOnObject(g36,g41)
    c: PointOnObject(g37,g41)
    c: PointOnObject(g38,g41)
    c: PointOnObject(g39,g41)
    c: PointOnObject(g40,g41)
    c: Coincident(g42,g43)
    c: Coincident(g43,g44)
    c: Coincident(g44,g45)
    c: Coincident(g45,g46)
    c: Coincident(g46,g47)
    c: Coincident(g47,g42)
    c: Equal(g42, g43-g47) x5
    c: PointOnObject(g42,g48)
    c: PointOnObject(g43,g48)
    c: PointOnObject(g44,g48)
    c: PointOnObject(g45,g48)
    c: PointOnObject(g46,g48)
    c: PointOnObject(g47,g48)
    c: Equal(g41,g48)
    c: Diameter(g41) = 7
    c: Vertical(g39)
    c: Vertical(g43)
    c: Distance(g-2,g39) = 1
    c: Symmetric(g38,g43,g-2)
    c: Distance(g41,g-1) = 7
FEATURE [Part::Extrusion] Extrude400  label="hex015"
  Base = -> Sketch408
  Dir = (0,-1,2e-16)
  DirMode = 2
  FaceMakerClass = Part::FaceMakerBullseye
  FaceMakerMode = 3
  LengthFwd = 10
  LengthRev = 0
  Placement = pos=(-24,0,-28) rot=(0,0,1;0rad)
  Solid = true
  Symmetric = false
FEATURE [Sketcher::SketchObject] Sketch409
  ArcFitTolerance = 1e-06
  FullyConstrained = true
  MakeInternals = false
  Placement = pos=(0,0,0) rot=(1,0,0;1.5708rad)
  sketch-geometry (49):
    g0: LineSegment StartX=1e-16 StartY=3.5 StartZ=0 EndX=-3.03109 EndY=1.75 EndZ=0
    g1: LineSegment StartX=-3.03109 StartY=1.75 StartZ=0 EndX=-3.03109 EndY=-1.75 EndZ=0
    g2: LineSegment StartX=-3.03109 StartY=-1.75 StartZ=0 EndX=-1e-16 EndY=-3.5 EndZ=0
    g3: LineSegment StartX=-1e-16 StartY=-3.5 StartZ=0 EndX=3.03109 EndY=-1.75 EndZ=0
    g4: LineSegment StartX=3.03109 StartY=-1.75 StartZ=0 EndX=3.03109 EndY=1.75 EndZ=0
    g5: LineSegment StartX=3.03109 StartY=1.75 StartZ=0 EndX=1e-16 EndY=3.5 EndZ=0
    g6: Circle [constr] CenterX=0 CenterY=0 CenterZ=0 NormalX=0 NormalY=0 NormalZ=1 AngleXU=0 Radius=3.5
    g7: LineSegment StartX=4.96892 StartY=-1.75002 StartZ=0 EndX=8.00002 EndY=-3.5 EndZ=0
    g8: LineSegment StartX=8.00002 StartY=-3.5 StartZ=0 EndX=11.0311 EndY=-1.74998 EndZ=0
    g9: LineSegment StartX=11.0311 StartY=-1.74998 StartZ=0 EndX=11.0311 EndY=1.75002 EndZ=0
    g10: LineSegment StartX=11.0311 StartY=1.75002 StartZ=0 EndX=7.99998 EndY=3.5 EndZ=0
    g11: LineSegment StartX=7.99998 StartY=3.5 StartZ=0 EndX=4.9689 EndY=1.74998 EndZ=0
    g12: LineSegment StartX=4.9689 StartY=1.74998 StartZ=0 EndX=4.96892 EndY=-1.75002 EndZ=0
    g13: Circle [constr] CenterX=8 CenterY=0 CenterZ=0 NormalX=0 NormalY=0 NormalZ=1 AngleXU=0 Radius=3.5
    g14: LineSegment StartX=4.03109 StartY=3.5 StartZ=0 EndX=7.06218 EndY=5.25 EndZ=0
    g15: LineSegment StartX=7.06218 StartY=5.25 StartZ=0 EndX=7.06218 EndY=8.75 EndZ=0
    g16: LineSegment StartX=7.06218 StartY=8.75 StartZ=0 EndX=4.03109 EndY=10.5 EndZ=0
    g17: LineSegment StartX=4.03109 StartY=10.5 StartZ=0 EndX=1 EndY=8.75 EndZ=0
    g18: LineSegment StartX=1 StartY=8.75 StartZ=0 EndX=1 EndY=5.25 EndZ=0
    g19: LineSegment StartX=1 StartY=5.25 StartZ=0 EndX=4.03109 EndY=3.5 EndZ=0
    g20: Circle [constr] CenterX=4.03109 CenterY=7 CenterZ=0 NormalX=0 NormalY=0 NormalZ=1 AngleXU=0 Radius=3.5
    g21: LineSegment StartX=-1 StartY=5.25 StartZ=0 EndX=-1 EndY=8.75 EndZ=0
    g22: LineSegment StartX=-1 StartY=8.75 StartZ=0 EndX=-4.03109 EndY=10.5 EndZ=0
    g23: LineSegment StartX=-4.03109 StartY=10.5 StartZ=0 EndX=-7.06218 EndY=8.75 EndZ=0
    g24: LineSegment StartX=-7.06218 StartY=8.75 StartZ=0 EndX=-7.06218 EndY=5.25 EndZ=0
    g25: LineSegment StartX=-7.06218 StartY=5.25 StartZ=0 EndX=-4.03109 EndY=3.5 EndZ=0
    g26: LineSegment StartX=-4.03109 StartY=3.5 StartZ=0 EndX=-1 EndY=5.25 EndZ=0
    g27: Circle [constr] CenterX=-4.03109 CenterY=7 CenterZ=0 NormalX=0 NormalY=0 NormalZ=1 AngleXU=0 Radius=3.5
    g28: LineSegment StartX=-4.96891 StartY=-1.75 StartZ=0 EndX=-4.96891 EndY=1.75 EndZ=0
    g29: LineSegment StartX=-4.96891 StartY=1.75 StartZ=0 EndX=-8 EndY=3.5 EndZ=0
    g30: LineSegment StartX=-8 StartY=3.5 StartZ=0 EndX=-11.0311 EndY=1.75 EndZ=0
    g31: LineSegment StartX=-11.0311 StartY=1.75 StartZ=0 EndX=-11.0311 EndY=-1.75 EndZ=0
    g32: LineSegment StartX=-11.0311 StartY=-1.75 StartZ=0 EndX=-8 EndY=-3.5 EndZ=0
    g33: LineSegment StartX=-8 StartY=-3.5 StartZ=0 EndX=-4.96891 EndY=-1.75 EndZ=0
    g34: Circle [constr] CenterX=-8 CenterY=0 CenterZ=0 NormalX=0 NormalY=0 NormalZ=1 AngleXU=0 Radius=3.5
    g35: LineSegment StartX=-4.03109 StartY=-3.5 StartZ=0 EndX=-7.06218 EndY=-5.25 EndZ=0
    g36: LineSegment StartX=-7.06218 StartY=-5.25 StartZ=0 EndX=-7.06218 EndY=-8.75 EndZ=0
    g37: LineSegment StartX=-7.06218 StartY=-8.75 StartZ=0 EndX=-4.03109 EndY=-10.5 EndZ=0
    g38: LineSegment StartX=-4.03109 StartY=-10.5 StartZ=0 EndX=-1 EndY=-8.75 EndZ=0
    g39: LineSegment StartX=-1 StartY=-8.75 StartZ=0 EndX=-1 EndY=-5.25 EndZ=0
    g40: LineSegment StartX=-1 StartY=-5.25 StartZ=0 EndX=-4.03109 EndY=-3.5 EndZ=0
    g41: Circle [constr] CenterX=-4.03109 CenterY=-7 CenterZ=0 NormalX=0 NormalY=0 NormalZ=1 AngleXU=0 Radius=3.5
    g42: LineSegment StartX=4.03109 StartY=-3.5 StartZ=0 EndX=1 EndY=-5.25 EndZ=0
    g43: LineSegment StartX=1 StartY=-5.25 StartZ=0 EndX=1 EndY=-8.75 EndZ=0
    g44: LineSegment StartX=1 StartY=-8.75 StartZ=0 EndX=4.03109 EndY=-10.5 EndZ=0
    g45: LineSegment StartX=4.03109 StartY=-10.5 StartZ=0 EndX=7.06218 EndY=-8.75 EndZ=0
    g46: LineSegment StartX=7.06218 StartY=-8.75 StartZ=0 EndX=7.06218 EndY=-5.25 EndZ=0
    g47: LineSegment StartX=7.06218 StartY=-5.25 StartZ=0 EndX=4.03109 EndY=-3.5 EndZ=0
    g48: Circle [constr] CenterX=4.03109 CenterY=-7 CenterZ=0 NormalX=0 NormalY=0 NormalZ=1 AngleXU=0 Radius=3.5
  constraints (117):
    c: Coincident(g0,g1)
    c: Coincident(g1,g2)
    c: Coincident(g2,g3)
    c: Coincident(g3,g4)
    c: Coincident(g4,g5)
    c: Coincident(g5,g0)
    c: Equal(g0, g1-g5) x5
    c: PointOnObject(g0,g6)
    c: PointOnObject(g1,g6)
    c: PointOnObject(g2,g6)
    c: PointOnObject(g3,g6)
    c: PointOnObject(g4,g6)
    c: PointOnObject(g5,g6)
    c: Coincident(g6,g-1)
    c: Diameter(g6) = 7
    c: PointOnObject(g0,g-2)
    c: Coincident(g7,g8)
    c: Coincident(g8,g9)
    c: Coincident(g9,g10)
    c: Coincident(g10,g11)
    c: Coincident(g11,g12)
    c: Coincident(g12,g7)
    c: Equal(g7, g8-g12) x5
    c: PointOnObject(g7,g13)
    c: PointOnObject(g8,g13)
    c: PointOnObject(g9,g13)
    c: PointOnObject(g10,g13)
    c: PointOnObject(g11,g13)
    c: PointOnObject(g12,g13)
    c: PointOnObject(g13,g-1)
    c: Diameter(g13) = 7
    c: Distance(g6,g13) = 8
    c: Horizontal(g0,g10)
    c: Coincident(g14,g15)
    c: Coincident(g15,g16)
    c: Coincident(g16,g17)
    c: Coincident(g17,g18)
    c: Coincident(g18,g19)
    c: Coincident(g19,g14)
    c: Equal(g14, g15-g19) x5
    c: PointOnObject(g14,g20)
    c: PointOnObject(g15,g20)
    c: PointOnObject(g16,g20)
    c: PointOnObject(g17,g20)
    c: PointOnObject(g18,g20)
    c: PointOnObject(g19,g20)
    c: Diameter(g20) = 7
    c: DistanceY(g-1,g20) = 7
    c: Vertical(g18)
    c: Distance(g17,g-2) = 1
    c: Coincident(g21,g22)
    c: Coincident(g22,g23)
    c: Coincident(g23,g24)
    c: Coincident(g24,g25)
    c: Coincident(g25,g26)
    c: Coincident(g26,g21)
    c: Equal(g21, g22-g26) x5
    c: PointOnObject(g21,g27)
    c: PointOnObject(g22,g27)
    c: PointOnObject(g23,g27)
    c: PointOnObject(g24,g27)
    c: PointOnObject(g25,g27)
    c: PointOnObject(g26,g27)
    c: Diameter(g27) = 7
    c: DistanceY(g-1,g27) = 7
    c: DistanceX(g21,g-1) = 1
    c: Vertical(g21)
    c: Coincident(g28,g29)
    c: Coincident(g29,g30)
    c: Coincident(g30,g31)
    c: Coincident(g31,g32)
    c: Coincident(g32,g33)
    c: Coincident(g33,g28)
    c: Equal(g28, g29-g33) x5
    c: PointOnObject(g28,g34)
    c: PointOnObject(g29,g34)
    c: PointOnObject(g30,g34)
    c: PointOnObject(g31,g34)
    c: PointOnObject(g32,g34)
    c: PointOnObject(g33,g34)
    c: PointOnObject(g34,g-1)
    c: Diameter(g34) = 7
    c: Vertical(g31)
    c: DistanceX(g34,g-1) = 8
    c: Coincident(g35,g36)
    c: Coincident(g36,g37)
    c: Coincident(g37,g38)
    c: Coincident(g38,g39)
    c: Coincident(g39,g40)
    c: Coincident(g40,g35)
    c: Equal(g35, g36-g40) x5
    c: PointOnObject(g35,g41)
    c: PointOnObject(g36,g41)
    c: PointOnObject(g37,g41)
    c: PointOnObject(g38,g41)
    c: PointOnObject(g39,g41)
    c: PointOnObject(g40,g41)
    c: Coincident(g42,g43)
    c: Coincident(g43,g44)
    c: Coincident(g44,g45)
    c: Coincident(g45,g46)
    c: Coincident(g46,g47)
    c: Coincident(g47,g42)
    c: Equal(g42, g43-g47) x5
    c: PointOnObject(g42,g48)
    c: PointOnObject(g43,g48)
    c: PointOnObject(g44,g48)
    c: PointOnObject(g45,g48)
    c: PointOnObject(g46,g48)
    c: PointOnObject(g47,g48)
    c: Equal(g41,g48)
    c: Diameter(g41) = 7
    c: Vertical(g39)
    c: Vertical(g43)
    c: Distance(g-2,g39) = 1
    c: Symmetric(g38,g43,g-2)
    c: Distance(g41,g-1) = 7
FEATURE [Part::Extrusion] Extrude401  label="hex016"
  Base = -> Sketch409
  Dir = (0,-1,2e-16)
  DirMode = 2
  FaceMakerClass = Part::FaceMakerBullseye
  FaceMakerMode = 3
  LengthFwd = 10
  LengthRev = 0
  Placement = pos=(-8,0,-42) rot=(0,0,1;0rad)
  Solid = true
  Symmetric = false
FEATURE [Sketcher::SketchObject] Sketch410
  ArcFitTolerance = 1e-06
  FullyConstrained = true
  MakeInternals = false
  Placement = pos=(0,0,0) rot=(1,0,0;1.5708rad)
  sketch-geometry (49):
    g0: LineSegment StartX=1e-16 StartY=3.5 StartZ=0 EndX=-3.03109 EndY=1.75 EndZ=0
    g1: LineSegment StartX=-3.03109 StartY=1.75 StartZ=0 EndX=-3.03109 EndY=-1.75 EndZ=0
    g2: LineSegment StartX=-3.03109 StartY=-1.75 StartZ=0 EndX=-1e-16 EndY=-3.5 EndZ=0
    g3: LineSegment StartX=-1e-16 StartY=-3.5 StartZ=0 EndX=3.03109 EndY=-1.75 EndZ=0
    g4: LineSegment StartX=3.03109 StartY=-1.75 StartZ=0 EndX=3.03109 EndY=1.75 EndZ=0
    g5: LineSegment StartX=3.03109 StartY=1.75 StartZ=0 EndX=1e-16 EndY=3.5 EndZ=0
    g6: Circle [constr] CenterX=0 CenterY=0 CenterZ=0 NormalX=0 NormalY=0 NormalZ=1 AngleXU=0 Radius=3.5
    g7: LineSegment StartX=4.96892 StartY=-1.75002 StartZ=0 EndX=8.00002 EndY=-3.5 EndZ=0
    g8: LineSegment StartX=8.00002 StartY=-3.5 StartZ=0 EndX=11.0311 EndY=-1.74998 EndZ=0
    g9: LineSegment StartX=11.0311 StartY=-1.74998 StartZ=0 EndX=11.0311 EndY=1.75002 EndZ=0
    g10: LineSegment StartX=11.0311 StartY=1.75002 StartZ=0 EndX=7.99998 EndY=3.5 EndZ=0
    g11: LineSegment StartX=7.99998 StartY=3.5 StartZ=0 EndX=4.9689 EndY=1.74998 EndZ=0
    g12: LineSegment StartX=4.9689 StartY=1.74998 StartZ=0 EndX=4.96892 EndY=-1.75002 EndZ=0
    g13: Circle [constr] CenterX=8 CenterY=0 CenterZ=0 NormalX=0 NormalY=0 NormalZ=1 AngleXU=0 Radius=3.5
    g14: LineSegment StartX=4.03109 StartY=3.5 StartZ=0 EndX=7.06218 EndY=5.25 EndZ=0
    g15: LineSegment StartX=7.06218 StartY=5.25 StartZ=0 EndX=7.06218 EndY=8.75 EndZ=0
    g16: LineSegment StartX=7.06218 StartY=8.75 StartZ=0 EndX=4.03109 EndY=10.5 EndZ=0
    g17: LineSegment StartX=4.03109 StartY=10.5 StartZ=0 EndX=1 EndY=8.75 EndZ=0
    g18: LineSegment StartX=1 StartY=8.75 StartZ=0 EndX=1 EndY=5.25 EndZ=0
    g19: LineSegment StartX=1 StartY=5.25 StartZ=0 EndX=4.03109 EndY=3.5 EndZ=0
    g20: Circle [constr] CenterX=4.03109 CenterY=7 CenterZ=0 NormalX=0 NormalY=0 NormalZ=1 AngleXU=0 Radius=3.5
    g21: LineSegment StartX=-1 StartY=5.25 StartZ=0 EndX=-1 EndY=8.75 EndZ=0
    g22: LineSegment StartX=-1 StartY=8.75 StartZ=0 EndX=-4.03109 EndY=10.5 EndZ=0
    g23: LineSegment StartX=-4.03109 StartY=10.5 StartZ=0 EndX=-7.06218 EndY=8.75 EndZ=0
    g24: LineSegment StartX=-7.06218 StartY=8.75 StartZ=0 EndX=-7.06218 EndY=5.25 EndZ=0
    g25: LineSegment StartX=-7.06218 StartY=5.25 StartZ=0 EndX=-4.03109 EndY=3.5 EndZ=0
    g26: LineSegment StartX=-4.03109 StartY=3.5 StartZ=0 EndX=-1 EndY=5.25 EndZ=0
    g27: Circle [constr] CenterX=-4.03109 CenterY=7 CenterZ=0 NormalX=0 NormalY=0 NormalZ=1 AngleXU=0 Radius=3.5
    g28: LineSegment StartX=-4.96891 StartY=-1.75 StartZ=0 EndX=-4.96891 EndY=1.75 EndZ=0
    g29: LineSegment StartX=-4.96891 StartY=1.75 StartZ=0 EndX=-8 EndY=3.5 EndZ=0
    g30: LineSegment StartX=-8 StartY=3.5 StartZ=0 EndX=-11.0311 EndY=1.75 EndZ=0
    g31: LineSegment StartX=-11.0311 StartY=1.75 StartZ=0 EndX=-11.0311 EndY=-1.75 EndZ=0
    g32: LineSegment StartX=-11.0311 StartY=-1.75 StartZ=0 EndX=-8 EndY=-3.5 EndZ=0
    g33: LineSegment StartX=-8 StartY=-3.5 StartZ=0 EndX=-4.96891 EndY=-1.75 EndZ=0
    g34: Circle [constr] CenterX=-8 CenterY=0 CenterZ=0 NormalX=0 NormalY=0 NormalZ=1 AngleXU=0 Radius=3.5
    g35: LineSegment StartX=-4.03109 StartY=-3.5 StartZ=0 EndX=-7.06218 EndY=-5.25 EndZ=0
    g36: LineSegment StartX=-7.06218 StartY=-5.25 StartZ=0 EndX=-7.06218 EndY=-8.75 EndZ=0
    g37: LineSegment StartX=-7.06218 StartY=-8.75 StartZ=0 EndX=-4.03109 EndY=-10.5 EndZ=0
    g38: LineSegment StartX=-4.03109 StartY=-10.5 StartZ=0 EndX=-1 EndY=-8.75 EndZ=0
    g39: LineSegment StartX=-1 StartY=-8.75 StartZ=0 EndX=-1 EndY=-5.25 EndZ=0
    g40: LineSegment StartX=-1 StartY=-5.25 StartZ=0 EndX=-4.03109 EndY=-3.5 EndZ=0
    g41: Circle [constr] CenterX=-4.03109 CenterY=-7 CenterZ=0 NormalX=0 NormalY=0 NormalZ=1 AngleXU=0 Radius=3.5
    g42: LineSegment StartX=4.03109 StartY=-3.5 StartZ=0 EndX=1 EndY=-5.25 EndZ=0
    g43: LineSegment StartX=1 StartY=-5.25 StartZ=0 EndX=1 EndY=-8.75 EndZ=0
    g44: LineSegment StartX=1 StartY=-8.75 StartZ=0 EndX=4.03109 EndY=-10.5 EndZ=0
    g45: LineSegment StartX=4.03109 StartY=-10.5 StartZ=0 EndX=7.06218 EndY=-8.75 EndZ=0
    g46: LineSegment StartX=7.06218 StartY=-8.75 StartZ=0 EndX=7.06218 EndY=-5.25 EndZ=0
    g47: LineSegment StartX=7.06218 StartY=-5.25 StartZ=0 EndX=4.03109 EndY=-3.5 EndZ=0
    g48: Circle [constr] CenterX=4.03109 CenterY=-7 CenterZ=0 NormalX=0 NormalY=0 NormalZ=1 AngleXU=0 Radius=3.5
  constraints (117):
    c: Coincident(g0,g1)
    c: Coincident(g1,g2)
    c: Coincident(g2,g3)
    c: Coincident(g3,g4)
    c: Coincident(g4,g5)
    c: Coincident(g5,g0)
    c: Equal(g0, g1-g5) x5
    c: PointOnObject(g0,g6)
    c: PointOnObject(g1,g6)
    c: PointOnObject(g2,g6)
    c: PointOnObject(g3,g6)
    c: PointOnObject(g4,g6)
    c: PointOnObject(g5,g6)
    c: Coincident(g6,g-1)
    c: Diameter(g6) = 7
    c: PointOnObject(g0,g-2)
    c: Coincident(g7,g8)
    c: Coincident(g8,g9)
    c: Coincident(g9,g10)
    c: Coincident(g10,g11)
    c: Coincident(g11,g12)
    c: Coincident(g12,g7)
    c: Equal(g7, g8-g12) x5
    c: PointOnObject(g7,g13)
    c: PointOnObject(g8,g13)
    c: PointOnObject(g9,g13)
    c: PointOnObject(g10,g13)
    c: PointOnObject(g11,g13)
    c: PointOnObject(g12,g13)
    c: PointOnObject(g13,g-1)
    c: Diameter(g13) = 7
    c: Distance(g6,g13) = 8
    c: Horizontal(g0,g10)
    c: Coincident(g14,g15)
    c: Coincident(g15,g16)
    c: Coincident(g16,g17)
    c: Coincident(g17,g18)
    c: Coincident(g18,g19)
    c: Coincident(g19,g14)
    c: Equal(g14, g15-g19) x5
    c: PointOnObject(g14,g20)
    c: PointOnObject(g15,g20)
    c: PointOnObject(g16,g20)
    c: PointOnObject(g17,g20)
    c: PointOnObject(g18,g20)
    c: PointOnObject(g19,g20)
    c: Diameter(g20) = 7
    c: DistanceY(g-1,g20) = 7
    c: Vertical(g18)
    c: Distance(g17,g-2) = 1
    c: Coincident(g21,g22)
    c: Coincident(g22,g23)
    c: Coincident(g23,g24)
    c: Coincident(g24,g25)
    c: Coincident(g25,g26)
    c: Coincident(g26,g21)
    c: Equal(g21, g22-g26) x5
    c: PointOnObject(g21,g27)
    c: PointOnObject(g22,g27)
    c: PointOnObject(g23,g27)
    c: PointOnObject(g24,g27)
    c: PointOnObject(g25,g27)
    c: PointOnObject(g26,g27)
    c: Diameter(g27) = 7
    c: DistanceY(g-1,g27) = 7
    c: DistanceX(g21,g-1) = 1
    c: Vertical(g21)
    c: Coincident(g28,g29)
    c: Coincident(g29,g30)
    c: Coincident(g30,g31)
    c: Coincident(g31,g32)
    c: Coincident(g32,g33)
    c: Coincident(g33,g28)
    c: Equal(g28, g29-g33) x5
    c: PointOnObject(g28,g34)
    c: PointOnObject(g29,g34)
    c: PointOnObject(g30,g34)
    c: PointOnObject(g31,g34)
    c: PointOnObject(g32,g34)
    c: PointOnObject(g33,g34)
    c: PointOnObject(g34,g-1)
    c: Diameter(g34) = 7
    c: Vertical(g31)
    c: DistanceX(g34,g-1) = 8
    c: Coincident(g35,g36)
    c: Coincident(g36,g37)
    c: Coincident(g37,g38)
    c: Coincident(g38,g39)
    c: Coincident(g39,g40)
    c: Coincident(g40,g35)
    c: Equal(g35, g36-g40) x5
    c: PointOnObject(g35,g41)
    c: PointOnObject(g36,g41)
    c: PointOnObject(g37,g41)
    c: PointOnObject(g38,g41)
    c: PointOnObject(g39,g41)
    c: PointOnObject(g40,g41)
    c: Coincident(g42,g43)
    c: Coincident(g43,g44)
    c: Coincident(g44,g45)
    c: Coincident(g45,g46)
    c: Coincident(g46,g47)
    c: Coincident(g47,g42)
    c: Equal(g42, g43-g47) x5
    c: PointOnObject(g42,g48)
    c: PointOnObject(g43,g48)
    c: PointOnObject(g44,g48)
    c: PointOnObject(g45,g48)
    c: PointOnObject(g46,g48)
    c: PointOnObject(g47,g48)
    c: Equal(g41,g48)
    c: Diameter(g41) = 7
    c: Vertical(g39)
    c: Vertical(g43)
    c: Distance(g-2,g39) = 1
    c: Symmetric(g38,g43,g-2)
    c: Distance(g41,g-1) = 7
FEATURE [Part::Extrusion] Extrude402  label="hex017"
  Base = -> Sketch410
  Dir = (0,-1,2e-16)
  DirMode = 2
  FaceMakerClass = Part::FaceMakerBullseye
  FaceMakerMode = 3
  LengthFwd = 10
  LengthRev = 0
  Placement = pos=(32,0,-28) rot=(0,0,1;0rad)
  Solid = true
  Symmetric = false
FEATURE [Sketcher::SketchObject] Sketch411
  ArcFitTolerance = 1e-06
  FullyConstrained = true
  MakeInternals = false
  Placement = pos=(0,0,0) rot=(1,0,0;1.5708rad)
  sketch-geometry (49):
    g0: LineSegment StartX=1e-16 StartY=3.5 StartZ=0 EndX=-3.03109 EndY=1.75 EndZ=0
    g1: LineSegment StartX=-3.03109 StartY=1.75 StartZ=0 EndX=-3.03109 EndY=-1.75 EndZ=0
    g2: LineSegment StartX=-3.03109 StartY=-1.75 StartZ=0 EndX=-1e-16 EndY=-3.5 EndZ=0
    g3: LineSegment StartX=-1e-16 StartY=-3.5 StartZ=0 EndX=3.03109 EndY=-1.75 EndZ=0
    g4: LineSegment StartX=3.03109 StartY=-1.75 StartZ=0 EndX=3.03109 EndY=1.75 EndZ=0
    g5: LineSegment StartX=3.03109 StartY=1.75 StartZ=0 EndX=1e-16 EndY=3.5 EndZ=0
    g6: Circle [constr] CenterX=0 CenterY=0 CenterZ=0 NormalX=0 NormalY=0 NormalZ=1 AngleXU=0 Radius=3.5
    g7: LineSegment StartX=4.96892 StartY=-1.75002 StartZ=0 EndX=8.00002 EndY=-3.5 EndZ=0
    g8: LineSegment StartX=8.00002 StartY=-3.5 StartZ=0 EndX=11.0311 EndY=-1.74998 EndZ=0
    g9: LineSegment StartX=11.0311 StartY=-1.74998 StartZ=0 EndX=11.0311 EndY=1.75002 EndZ=0
    g10: LineSegment StartX=11.0311 StartY=1.75002 StartZ=0 EndX=7.99998 EndY=3.5 EndZ=0
    g11: LineSegment StartX=7.99998 StartY=3.5 StartZ=0 EndX=4.9689 EndY=1.74998 EndZ=0
    g12: LineSegment StartX=4.9689 StartY=1.74998 StartZ=0 EndX=4.96892 EndY=-1.75002 EndZ=0
    g13: Circle [constr] CenterX=8 CenterY=0 CenterZ=0 NormalX=0 NormalY=0 NormalZ=1 AngleXU=0 Radius=3.5
    g14: LineSegment StartX=4.03109 StartY=3.5 StartZ=0 EndX=7.06218 EndY=5.25 EndZ=0
    g15: LineSegment StartX=7.06218 StartY=5.25 StartZ=0 EndX=7.06218 EndY=8.75 EndZ=0
    g16: LineSegment StartX=7.06218 StartY=8.75 StartZ=0 EndX=4.03109 EndY=10.5 EndZ=0
    g17: LineSegment StartX=4.03109 StartY=10.5 StartZ=0 EndX=1 EndY=8.75 EndZ=0
    g18: LineSegment StartX=1 StartY=8.75 StartZ=0 EndX=1 EndY=5.25 EndZ=0
    g19: LineSegment StartX=1 StartY=5.25 StartZ=0 EndX=4.03109 EndY=3.5 EndZ=0
    g20: Circle [constr] CenterX=4.03109 CenterY=7 CenterZ=0 NormalX=0 NormalY=0 NormalZ=1 AngleXU=0 Radius=3.5
    g21: LineSegment StartX=-1 StartY=5.25 StartZ=0 EndX=-1 EndY=8.75 EndZ=0
    g22: LineSegment StartX=-1 StartY=8.75 StartZ=0 EndX=-4.03109 EndY=10.5 EndZ=0
    g23: LineSegment StartX=-4.03109 StartY=10.5 StartZ=0 EndX=-7.06218 EndY=8.75 EndZ=0
    g24: LineSegment StartX=-7.06218 StartY=8.75 StartZ=0 EndX=-7.06218 EndY=5.25 EndZ=0
    g25: LineSegment StartX=-7.06218 StartY=5.25 StartZ=0 EndX=-4.03109 EndY=3.5 EndZ=0
    g26: LineSegment StartX=-4.03109 StartY=3.5 StartZ=0 EndX=-1 EndY=5.25 EndZ=0
    g27: Circle [constr] CenterX=-4.03109 CenterY=7 CenterZ=0 NormalX=0 NormalY=0 NormalZ=1 AngleXU=0 Radius=3.5
    g28: LineSegment StartX=-4.96891 StartY=-1.75 StartZ=0 EndX=-4.96891 EndY=1.75 EndZ=0
    g29: LineSegment StartX=-4.96891 StartY=1.75 StartZ=0 EndX=-8 EndY=3.5 EndZ=0
    g30: LineSegment StartX=-8 StartY=3.5 StartZ=0 EndX=-11.0311 EndY=1.75 EndZ=0
    g31: LineSegment StartX=-11.0311 StartY=1.75 StartZ=0 EndX=-11.0311 EndY=-1.75 EndZ=0
    g32: LineSegment StartX=-11.0311 StartY=-1.75 StartZ=0 EndX=-8 EndY=-3.5 EndZ=0
    g33: LineSegment StartX=-8 StartY=-3.5 StartZ=0 EndX=-4.96891 EndY=-1.75 EndZ=0
    g34: Circle [constr] CenterX=-8 CenterY=0 CenterZ=0 NormalX=0 NormalY=0 NormalZ=1 AngleXU=0 Radius=3.5
    g35: LineSegment StartX=-4.03109 StartY=-3.5 StartZ=0 EndX=-7.06218 EndY=-5.25 EndZ=0
    g36: LineSegment StartX=-7.06218 StartY=-5.25 StartZ=0 EndX=-7.06218 EndY=-8.75 EndZ=0
    g37: LineSegment StartX=-7.06218 StartY=-8.75 StartZ=0 EndX=-4.03109 EndY=-10.5 EndZ=0
    g38: LineSegment StartX=-4.03109 StartY=-10.5 StartZ=0 EndX=-1 EndY=-8.75 EndZ=0
    g39: LineSegment StartX=-1 StartY=-8.75 StartZ=0 EndX=-1 EndY=-5.25 EndZ=0
    g40: LineSegment StartX=-1 StartY=-5.25 StartZ=0 EndX=-4.03109 EndY=-3.5 EndZ=0
    g41: Circle [constr] CenterX=-4.03109 CenterY=-7 CenterZ=0 NormalX=0 NormalY=0 NormalZ=1 AngleXU=0 Radius=3.5
    g42: LineSegment StartX=4.03109 StartY=-3.5 StartZ=0 EndX=1 EndY=-5.25 EndZ=0
    g43: LineSegment StartX=1 StartY=-5.25 StartZ=0 EndX=1 EndY=-8.75 EndZ=0
    g44: LineSegment StartX=1 StartY=-8.75 StartZ=0 EndX=4.03109 EndY=-10.5 EndZ=0
    g45: LineSegment StartX=4.03109 StartY=-10.5 StartZ=0 EndX=7.06218 EndY=-8.75 EndZ=0
    g46: LineSegment StartX=7.06218 StartY=-8.75 StartZ=0 EndX=7.06218 EndY=-5.25 EndZ=0
    g47: LineSegment StartX=7.06218 StartY=-5.25 StartZ=0 EndX=4.03109 EndY=-3.5 EndZ=0
    g48: Circle [constr] CenterX=4.03109 CenterY=-7 CenterZ=0 NormalX=0 NormalY=0 NormalZ=1 AngleXU=0 Radius=3.5
  constraints (117):
    c: Coincident(g0,g1)
    c: Coincident(g1,g2)
    c: Coincident(g2,g3)
    c: Coincident(g3,g4)
    c: Coincident(g4,g5)
    c: Coincident(g5,g0)
    c: Equal(g0, g1-g5) x5
    c: PointOnObject(g0,g6)
    c: PointOnObject(g1,g6)
    c: PointOnObject(g2,g6)
    c: PointOnObject(g3,g6)
    c: PointOnObject(g4,g6)
    c: PointOnObject(g5,g6)
    c: Coincident(g6,g-1)
    c: Diameter(g6) = 7
    c: PointOnObject(g0,g-2)
    c: Coincident(g7,g8)
    c: Coincident(g8,g9)
    c: Coincident(g9,g10)
    c: Coincident(g10,g11)
    c: Coincident(g11,g12)
    c: Coincident(g12,g7)
    c: Equal(g7, g8-g12) x5
    c: PointOnObject(g7,g13)
    c: PointOnObject(g8,g13)
    c: PointOnObject(g9,g13)
    c: PointOnObject(g10,g13)
    c: PointOnObject(g11,g13)
    c: PointOnObject(g12,g13)
    c: PointOnObject(g13,g-1)
    c: Diameter(g13) = 7
    c: Distance(g6,g13) = 8
    c: Horizontal(g0,g10)
    c: Coincident(g14,g15)
    c: Coincident(g15,g16)
    c: Coincident(g16,g17)
    c: Coincident(g17,g18)
    c: Coincident(g18,g19)
    c: Coincident(g19,g14)
    c: Equal(g14, g15-g19) x5
    c: PointOnObject(g14,g20)
    c: PointOnObject(g15,g20)
    c: PointOnObject(g16,g20)
    c: PointOnObject(g17,g20)
    c: PointOnObject(g18,g20)
    c: PointOnObject(g19,g20)
    c: Diameter(g20) = 7
    c: DistanceY(g-1,g20) = 7
    c: Vertical(g18)
    c: Distance(g17,g-2) = 1
    c: Coincident(g21,g22)
    c: Coincident(g22,g23)
    c: Coincident(g23,g24)
    c: Coincident(g24,g25)
    c: Coincident(g25,g26)
    c: Coincident(g26,g21)
    c: Equal(g21, g22-g26) x5
    c: PointOnObject(g21,g27)
    c: PointOnObject(g22,g27)
    c: PointOnObject(g23,g27)
    c: PointOnObject(g24,g27)
    c: PointOnObject(g25,g27)
    c: PointOnObject(g26,g27)
    c: Diameter(g27) = 7
    c: DistanceY(g-1,g27) = 7
    c: DistanceX(g21,g-1) = 1
    c: Vertical(g21)
    c: Coincident(g28,g29)
    c: Coincident(g29,g30)
    c: Coincident(g30,g31)
    c: Coincident(g31,g32)
    c: Coincident(g32,g33)
    c: Coincident(g33,g28)
    c: Equal(g28, g29-g33) x5
    c: PointOnObject(g28,g34)
    c: PointOnObject(g29,g34)
    c: PointOnObject(g30,g34)
    c: PointOnObject(g31,g34)
    c: PointOnObject(g32,g34)
    c: PointOnObject(g33,g34)
    c: PointOnObject(g34,g-1)
    c: Diameter(g34) = 7
    c: Vertical(g31)
    c: DistanceX(g34,g-1) = 8
    c: Coincident(g35,g36)
    c: Coincident(g36,g37)
    c: Coincident(g37,g38)
    c: Coincident(g38,g39)
    c: Coincident(g39,g40)
    c: Coincident(g40,g35)
    c: Equal(g35, g36-g40) x5
    c: PointOnObject(g35,g41)
    c: PointOnObject(g36,g41)
    c: PointOnObject(g37,g41)
    c: PointOnObject(g38,g41)
    c: PointOnObject(g39,g41)
    c: PointOnObject(g40,g41)
    c: Coincident(g42,g43)
    c: Coincident(g43,g44)
    c: Coincident(g44,g45)
    c: Coincident(g45,g46)
    c: Coincident(g46,g47)
    c: Coincident(g47,g42)
    c: Equal(g42, g43-g47) x5
    c: PointOnObject(g42,g48)
    c: PointOnObject(g43,g48)
    c: PointOnObject(g44,g48)
    c: PointOnObject(g45,g48)
    c: PointOnObject(g46,g48)
    c: PointOnObject(g47,g48)
    c: Equal(g41,g48)
    c: Diameter(g41) = 7
    c: Vertical(g39)
    c: Vertical(g43)
    c: Distance(g-2,g39) = 1
    c: Symmetric(g38,g43,g-2)
    c: Distance(g41,g-1) = 7
FEATURE [Part::Extrusion] Extrude403  label="hex018"
  Base = -> Sketch411
  Dir = (0,-1,2e-16)
  DirMode = 2
  FaceMakerClass = Part::FaceMakerBullseye
  FaceMakerMode = 3
  LengthFwd = 10
  LengthRev = 0
  Placement = pos=(36,0,-7) rot=(0,0,1;0rad)
  Solid = true
  Symmetric = false
FEATURE [Sketcher::SketchObject] Sketch412
  ArcFitTolerance = 1e-06
  FullyConstrained = true
  MakeInternals = false
  Placement = pos=(0,0,0) rot=(1,0,0;1.5708rad)
  sketch-geometry (49):
    g0: LineSegment StartX=1e-16 StartY=3.5 StartZ=0 EndX=-3.03109 EndY=1.75 EndZ=0
    g1: LineSegment StartX=-3.03109 StartY=1.75 StartZ=0 EndX=-3.03109 EndY=-1.75 EndZ=0
    g2: LineSegment StartX=-3.03109 StartY=-1.75 StartZ=0 EndX=-1e-16 EndY=-3.5 EndZ=0
    g3: LineSegment StartX=-1e-16 StartY=-3.5 StartZ=0 EndX=3.03109 EndY=-1.75 EndZ=0
    g4: LineSegment StartX=3.03109 StartY=-1.75 StartZ=0 EndX=3.03109 EndY=1.75 EndZ=0
    g5: LineSegment StartX=3.03109 StartY=1.75 StartZ=0 EndX=1e-16 EndY=3.5 EndZ=0
    g6: Circle [constr] CenterX=0 CenterY=0 CenterZ=0 NormalX=0 NormalY=0 NormalZ=1 AngleXU=0 Radius=3.5
    g7: LineSegment StartX=4.96892 StartY=-1.75002 StartZ=0 EndX=8.00002 EndY=-3.5 EndZ=0
    g8: LineSegment StartX=8.00002 StartY=-3.5 StartZ=0 EndX=11.0311 EndY=-1.74998 EndZ=0
    g9: LineSegment StartX=11.0311 StartY=-1.74998 StartZ=0 EndX=11.0311 EndY=1.75002 EndZ=0
    g10: LineSegment StartX=11.0311 StartY=1.75002 StartZ=0 EndX=7.99998 EndY=3.5 EndZ=0
    g11: LineSegment StartX=7.99998 StartY=3.5 StartZ=0 EndX=4.9689 EndY=1.74998 EndZ=0
    g12: LineSegment StartX=4.9689 StartY=1.74998 StartZ=0 EndX=4.96892 EndY=-1.75002 EndZ=0
    g13: Circle [constr] CenterX=8 CenterY=0 CenterZ=0 NormalX=0 NormalY=0 NormalZ=1 AngleXU=0 Radius=3.5
    g14: LineSegment StartX=4.03109 StartY=3.5 StartZ=0 EndX=7.06218 EndY=5.25 EndZ=0
    g15: LineSegment StartX=7.06218 StartY=5.25 StartZ=0 EndX=7.06218 EndY=8.75 EndZ=0
    g16: LineSegment StartX=7.06218 StartY=8.75 StartZ=0 EndX=4.03109 EndY=10.5 EndZ=0
    g17: LineSegment StartX=4.03109 StartY=10.5 StartZ=0 EndX=1 EndY=8.75 EndZ=0
    g18: LineSegment StartX=1 StartY=8.75 StartZ=0 EndX=1 EndY=5.25 EndZ=0
    g19: LineSegment StartX=1 StartY=5.25 StartZ=0 EndX=4.03109 EndY=3.5 EndZ=0
    g20: Circle [constr] CenterX=4.03109 CenterY=7 CenterZ=0 NormalX=0 NormalY=0 NormalZ=1 AngleXU=0 Radius=3.5
    g21: LineSegment StartX=-1 StartY=5.25 StartZ=0 EndX=-1 EndY=8.75 EndZ=0
    g22: LineSegment StartX=-1 StartY=8.75 StartZ=0 EndX=-4.03109 EndY=10.5 EndZ=0
    g23: LineSegment StartX=-4.03109 StartY=10.5 StartZ=0 EndX=-7.06218 EndY=8.75 EndZ=0
    g24: LineSegment StartX=-7.06218 StartY=8.75 StartZ=0 EndX=-7.06218 EndY=5.25 EndZ=0
    g25: LineSegment StartX=-7.06218 StartY=5.25 StartZ=0 EndX=-4.03109 EndY=3.5 EndZ=0
    g26: LineSegment StartX=-4.03109 StartY=3.5 StartZ=0 EndX=-1 EndY=5.25 EndZ=0
    g27: Circle [constr] CenterX=-4.03109 CenterY=7 CenterZ=0 NormalX=0 NormalY=0 NormalZ=1 AngleXU=0 Radius=3.5
    g28: LineSegment StartX=-4.96891 StartY=-1.75 StartZ=0 EndX=-4.96891 EndY=1.75 EndZ=0
    g29: LineSegment StartX=-4.96891 StartY=1.75 StartZ=0 EndX=-8 EndY=3.5 EndZ=0
    g30: LineSegment StartX=-8 StartY=3.5 StartZ=0 EndX=-11.0311 EndY=1.75 EndZ=0
    g31: LineSegment StartX=-11.0311 StartY=1.75 StartZ=0 EndX=-11.0311 EndY=-1.75 EndZ=0
    g32: LineSegment StartX=-11.0311 StartY=-1.75 StartZ=0 EndX=-8 EndY=-3.5 EndZ=0
    g33: LineSegment StartX=-8 StartY=-3.5 StartZ=0 EndX=-4.96891 EndY=-1.75 EndZ=0
    g34: Circle [constr] CenterX=-8 CenterY=0 CenterZ=0 NormalX=0 NormalY=0 NormalZ=1 AngleXU=0 Radius=3.5
    g35: LineSegment StartX=-4.03109 StartY=-3.5 StartZ=0 EndX=-7.06218 EndY=-5.25 EndZ=0
    g36: LineSegment StartX=-7.06218 StartY=-5.25 StartZ=0 EndX=-7.06218 EndY=-8.75 EndZ=0
    g37: LineSegment StartX=-7.06218 StartY=-8.75 StartZ=0 EndX=-4.03109 EndY=-10.5 EndZ=0
    g38: LineSegment StartX=-4.03109 StartY=-10.5 StartZ=0 EndX=-1 EndY=-8.75 EndZ=0
    g39: LineSegment StartX=-1 StartY=-8.75 StartZ=0 EndX=-1 EndY=-5.25 EndZ=0
    g40: LineSegment StartX=-1 StartY=-5.25 StartZ=0 EndX=-4.03109 EndY=-3.5 EndZ=0
    g41: Circle [constr] CenterX=-4.03109 CenterY=-7 CenterZ=0 NormalX=0 NormalY=0 NormalZ=1 AngleXU=0 Radius=3.5
    g42: LineSegment StartX=4.03109 StartY=-3.5 StartZ=0 EndX=1 EndY=-5.25 EndZ=0
    g43: LineSegment StartX=1 StartY=-5.25 StartZ=0 EndX=1 EndY=-8.75 EndZ=0
    g44: LineSegment StartX=1 StartY=-8.75 StartZ=0 EndX=4.03109 EndY=-10.5 EndZ=0
    g45: LineSegment StartX=4.03109 StartY=-10.5 StartZ=0 EndX=7.06218 EndY=-8.75 EndZ=0
    g46: LineSegment StartX=7.06218 StartY=-8.75 StartZ=0 EndX=7.06218 EndY=-5.25 EndZ=0
    g47: LineSegment StartX=7.06218 StartY=-5.25 StartZ=0 EndX=4.03109 EndY=-3.5 EndZ=0
    g48: Circle [constr] CenterX=4.03109 CenterY=-7 CenterZ=0 NormalX=0 NormalY=0 NormalZ=1 AngleXU=0 Radius=3.5
  constraints (117):
    c: Coincident(g0,g1)
    c: Coincident(g1,g2)
    c: Coincident(g2,g3)
    c: Coincident(g3,g4)
    c: Coincident(g4,g5)
    c: Coincident(g5,g0)
    c: Equal(g0, g1-g5) x5
    c: PointOnObject(g0,g6)
    c: PointOnObject(g1,g6)
    c: PointOnObject(g2,g6)
    c: PointOnObject(g3,g6)
    c: PointOnObject(g4,g6)
    c: PointOnObject(g5,g6)
    c: Coincident(g6,g-1)
    c: Diameter(g6) = 7
    c: PointOnObject(g0,g-2)
    c: Coincident(g7,g8)
    c: Coincident(g8,g9)
    c: Coincident(g9,g10)
    c: Coincident(g10,g11)
    c: Coincident(g11,g12)
    c: Coincident(g12,g7)
    c: Equal(g7, g8-g12) x5
    c: PointOnObject(g7,g13)
    c: PointOnObject(g8,g13)
    c: PointOnObject(g9,g13)
    c: PointOnObject(g10,g13)
    c: PointOnObject(g11,g13)
    c: PointOnObject(g12,g13)
    c: PointOnObject(g13,g-1)
    c: Diameter(g13) = 7
    c: Distance(g6,g13) = 8
    c: Horizontal(g0,g10)
    c: Coincident(g14,g15)
    c: Coincident(g15,g16)
    c: Coincident(g16,g17)
    c: Coincident(g17,g18)
    c: Coincident(g18,g19)
    c: Coincident(g19,g14)
    c: Equal(g14, g15-g19) x5
    c: PointOnObject(g14,g20)
    c: PointOnObject(g15,g20)
    c: PointOnObject(g16,g20)
    c: PointOnObject(g17,g20)
    c: PointOnObject(g18,g20)
    c: PointOnObject(g19,g20)
    c: Diameter(g20) = 7
    c: DistanceY(g-1,g20) = 7
    c: Vertical(g18)
    c: Distance(g17,g-2) = 1
    c: Coincident(g21,g22)
    c: Coincident(g22,g23)
    c: Coincident(g23,g24)
    c: Coincident(g24,g25)
    c: Coincident(g25,g26)
    c: Coincident(g26,g21)
    c: Equal(g21, g22-g26) x5
    c: PointOnObject(g21,g27)
    c: PointOnObject(g22,g27)
    c: PointOnObject(g23,g27)
    c: PointOnObject(g24,g27)
    c: PointOnObject(g25,g27)
    c: PointOnObject(g26,g27)
    c: Diameter(g27) = 7
    c: DistanceY(g-1,g27) = 7
    c: DistanceX(g21,g-1) = 1
    c: Vertical(g21)
    c: Coincident(g28,g29)
    c: Coincident(g29,g30)
    c: Coincident(g30,g31)
    c: Coincident(g31,g32)
    c: Coincident(g32,g33)
    c: Coincident(g33,g28)
    c: Equal(g28, g29-g33) x5
    c: PointOnObject(g28,g34)
    c: PointOnObject(g29,g34)
    c: PointOnObject(g30,g34)
    c: PointOnObject(g31,g34)
    c: PointOnObject(g32,g34)
    c: PointOnObject(g33,g34)
    c: PointOnObject(g34,g-1)
    c: Diameter(g34) = 7
    c: Vertical(g31)
    c: DistanceX(g34,g-1) = 8
    c: Coincident(g35,g36)
    c: Coincident(g36,g37)
    c: Coincident(g37,g38)
    c: Coincident(g38,g39)
    c: Coincident(g39,g40)
    c: Coincident(g40,g35)
    c: Equal(g35, g36-g40) x5
    c: PointOnObject(g35,g41)
    c: PointOnObject(g36,g41)
    c: PointOnObject(g37,g41)
    c: PointOnObject(g38,g41)
    c: PointOnObject(g39,g41)
    c: PointOnObject(g40,g41)
    c: Coincident(g42,g43)
    c: Coincident(g43,g44)
    c: Coincident(g44,g45)
    c: Coincident(g45,g46)
    c: Coincident(g46,g47)
    c: Coincident(g47,g42)
    c: Equal(g42, g43-g47) x5
    c: PointOnObject(g42,g48)
    c: PointOnObject(g43,g48)
    c: PointOnObject(g44,g48)
    c: PointOnObject(g45,g48)
    c: PointOnObject(g46,g48)
    c: PointOnObject(g47,g48)
    c: Equal(g41,g48)
    c: Diameter(g41) = 7
    c: Vertical(g39)
    c: Vertical(g43)
    c: Distance(g-2,g39) = 1
    c: Symmetric(g38,g43,g-2)
    c: Distance(g41,g-1) = 7
FEATURE [Part::Extrusion] Extrude404  label="hex019"
  Base = -> Sketch412
  Dir = (0,-1,2e-16)
  DirMode = 2
  FaceMakerClass = Part::FaceMakerBullseye
  FaceMakerMode = 3
  LengthFwd = 10
  LengthRev = 0
  Placement = pos=(56,0,0) rot=(0,0,1;0rad)
  Solid = true
  Symmetric = false
FEATURE [Sketcher::SketchObject] Sketch413
  ArcFitTolerance = 1e-06
  FullyConstrained = true
  MakeInternals = false
  Placement = pos=(0,0,0) rot=(1,0,0;1.5708rad)
  sketch-geometry (49):
    g0: LineSegment StartX=1e-16 StartY=3.5 StartZ=0 EndX=-3.03109 EndY=1.75 EndZ=0
    g1: LineSegment StartX=-3.03109 StartY=1.75 StartZ=0 EndX=-3.03109 EndY=-1.75 EndZ=0
    g2: LineSegment StartX=-3.03109 StartY=-1.75 StartZ=0 EndX=-1e-16 EndY=-3.5 EndZ=0
    g3: LineSegment StartX=-1e-16 StartY=-3.5 StartZ=0 EndX=3.03109 EndY=-1.75 EndZ=0
    g4: LineSegment StartX=3.03109 StartY=-1.75 StartZ=0 EndX=3.03109 EndY=1.75 EndZ=0
    g5: LineSegment StartX=3.03109 StartY=1.75 StartZ=0 EndX=1e-16 EndY=3.5 EndZ=0
    g6: Circle [constr] CenterX=0 CenterY=0 CenterZ=0 NormalX=0 NormalY=0 NormalZ=1 AngleXU=0 Radius=3.5
    g7: LineSegment StartX=4.96892 StartY=-1.75002 StartZ=0 EndX=8.00002 EndY=-3.5 EndZ=0
    g8: LineSegment StartX=8.00002 StartY=-3.5 StartZ=0 EndX=11.0311 EndY=-1.74998 EndZ=0
    g9: LineSegment StartX=11.0311 StartY=-1.74998 StartZ=0 EndX=11.0311 EndY=1.75002 EndZ=0
    g10: LineSegment StartX=11.0311 StartY=1.75002 StartZ=0 EndX=7.99998 EndY=3.5 EndZ=0
    g11: LineSegment StartX=7.99998 StartY=3.5 StartZ=0 EndX=4.9689 EndY=1.74998 EndZ=0
    g12: LineSegment StartX=4.9689 StartY=1.74998 StartZ=0 EndX=4.96892 EndY=-1.75002 EndZ=0
    g13: Circle [constr] CenterX=8 CenterY=0 CenterZ=0 NormalX=0 NormalY=0 NormalZ=1 AngleXU=0 Radius=3.5
    g14: LineSegment StartX=4.03109 StartY=3.5 StartZ=0 EndX=7.06218 EndY=5.25 EndZ=0
    g15: LineSegment StartX=7.06218 StartY=5.25 StartZ=0 EndX=7.06218 EndY=8.75 EndZ=0
    g16: LineSegment StartX=7.06218 StartY=8.75 StartZ=0 EndX=4.03109 EndY=10.5 EndZ=0
    g17: LineSegment StartX=4.03109 StartY=10.5 StartZ=0 EndX=1 EndY=8.75 EndZ=0
    g18: LineSegment StartX=1 StartY=8.75 StartZ=0 EndX=1 EndY=5.25 EndZ=0
    g19: LineSegment StartX=1 StartY=5.25 StartZ=0 EndX=4.03109 EndY=3.5 EndZ=0
    g20: Circle [constr] CenterX=4.03109 CenterY=7 CenterZ=0 NormalX=0 NormalY=0 NormalZ=1 AngleXU=0 Radius=3.5
    g21: LineSegment StartX=-1 StartY=5.25 StartZ=0 EndX=-1 EndY=8.75 EndZ=0
    g22: LineSegment StartX=-1 StartY=8.75 StartZ=0 EndX=-4.03109 EndY=10.5 EndZ=0
    g23: LineSegment StartX=-4.03109 StartY=10.5 StartZ=0 EndX=-7.06218 EndY=8.75 EndZ=0
    g24: LineSegment StartX=-7.06218 StartY=8.75 StartZ=0 EndX=-7.06218 EndY=5.25 EndZ=0
    g25: LineSegment StartX=-7.06218 StartY=5.25 StartZ=0 EndX=-4.03109 EndY=3.5 EndZ=0
    g26: LineSegment StartX=-4.03109 StartY=3.5 StartZ=0 EndX=-1 EndY=5.25 EndZ=0
    g27: Circle [constr] CenterX=-4.03109 CenterY=7 CenterZ=0 NormalX=0 NormalY=0 NormalZ=1 AngleXU=0 Radius=3.5
    g28: LineSegment StartX=-4.96891 StartY=-1.75 StartZ=0 EndX=-4.96891 EndY=1.75 EndZ=0
    g29: LineSegment StartX=-4.96891 StartY=1.75 StartZ=0 EndX=-8 EndY=3.5 EndZ=0
    g30: LineSegment StartX=-8 StartY=3.5 StartZ=0 EndX=-11.0311 EndY=1.75 EndZ=0
    g31: LineSegment StartX=-11.0311 StartY=1.75 StartZ=0 EndX=-11.0311 EndY=-1.75 EndZ=0
    g32: LineSegment StartX=-11.0311 StartY=-1.75 StartZ=0 EndX=-8 EndY=-3.5 EndZ=0
    g33: LineSegment StartX=-8 StartY=-3.5 StartZ=0 EndX=-4.96891 EndY=-1.75 EndZ=0
    g34: Circle [constr] CenterX=-8 CenterY=0 CenterZ=0 NormalX=0 NormalY=0 NormalZ=1 AngleXU=0 Radius=3.5
    g35: LineSegment StartX=-4.03109 StartY=-3.5 StartZ=0 EndX=-7.06218 EndY=-5.25 EndZ=0
    g36: LineSegment StartX=-7.06218 StartY=-5.25 StartZ=0 EndX=-7.06218 EndY=-8.75 EndZ=0
    g37: LineSegment StartX=-7.06218 StartY=-8.75 StartZ=0 EndX=-4.03109 EndY=-10.5 EndZ=0
    g38: LineSegment StartX=-4.03109 StartY=-10.5 StartZ=0 EndX=-1 EndY=-8.75 EndZ=0
    g39: LineSegment StartX=-1 StartY=-8.75 StartZ=0 EndX=-1 EndY=-5.25 EndZ=0
    g40: LineSegment StartX=-1 StartY=-5.25 StartZ=0 EndX=-4.03109 EndY=-3.5 EndZ=0
    g41: Circle [constr] CenterX=-4.03109 CenterY=-7 CenterZ=0 NormalX=0 NormalY=0 NormalZ=1 AngleXU=0 Radius=3.5
    g42: LineSegment StartX=4.03109 StartY=-3.5 StartZ=0 EndX=1 EndY=-5.25 EndZ=0
    g43: LineSegment StartX=1 StartY=-5.25 StartZ=0 EndX=1 EndY=-8.75 EndZ=0
    g44: LineSegment StartX=1 StartY=-8.75 StartZ=0 EndX=4.03109 EndY=-10.5 EndZ=0
    g45: LineSegment StartX=4.03109 StartY=-10.5 StartZ=0 EndX=7.06218 EndY=-8.75 EndZ=0
    g46: LineSegment StartX=7.06218 StartY=-8.75 StartZ=0 EndX=7.06218 EndY=-5.25 EndZ=0
    g47: LineSegment StartX=7.06218 StartY=-5.25 StartZ=0 EndX=4.03109 EndY=-3.5 EndZ=0
    g48: Circle [constr] CenterX=4.03109 CenterY=-7 CenterZ=0 NormalX=0 NormalY=0 NormalZ=1 AngleXU=0 Radius=3.5
  constraints (117):
    c: Coincident(g0,g1)
    c: Coincident(g1,g2)
    c: Coincident(g2,g3)
    c: Coincident(g3,g4)
    c: Coincident(g4,g5)
    c: Coincident(g5,g0)
    c: Equal(g0, g1-g5) x5
    c: PointOnObject(g0,g6)
    c: PointOnObject(g1,g6)
    c: PointOnObject(g2,g6)
    c: PointOnObject(g3,g6)
    c: PointOnObject(g4,g6)
    c: PointOnObject(g5,g6)
    c: Coincident(g6,g-1)
    c: Diameter(g6) = 7
    c: PointOnObject(g0,g-2)
    c: Coincident(g7,g8)
    c: Coincident(g8,g9)
    c: Coincident(g9,g10)
    c: Coincident(g10,g11)
    c: Coincident(g11,g12)
    c: Coincident(g12,g7)
    c: Equal(g7, g8-g12) x5
    c: PointOnObject(g7,g13)
    c: PointOnObject(g8,g13)
    c: PointOnObject(g9,g13)
    c: PointOnObject(g10,g13)
    c: PointOnObject(g11,g13)
    c: PointOnObject(g12,g13)
    c: PointOnObject(g13,g-1)
    c: Diameter(g13) = 7
    c: Distance(g6,g13) = 8
    c: Horizontal(g0,g10)
    c: Coincident(g14,g15)
    c: Coincident(g15,g16)
    c: Coincident(g16,g17)
    c: Coincident(g17,g18)
    c: Coincident(g18,g19)
    c: Coincident(g19,g14)
    c: Equal(g14, g15-g19) x5
    c: PointOnObject(g14,g20)
    c: PointOnObject(g15,g20)
    c: PointOnObject(g16,g20)
    c: PointOnObject(g17,g20)
    c: PointOnObject(g18,g20)
    c: PointOnObject(g19,g20)
    c: Diameter(g20) = 7
    c: DistanceY(g-1,g20) = 7
    c: Vertical(g18)
    c: Distance(g17,g-2) = 1
    c: Coincident(g21,g22)
    c: Coincident(g22,g23)
    c: Coincident(g23,g24)
    c: Coincident(g24,g25)
    c: Coincident(g25,g26)
    c: Coincident(g26,g21)
    c: Equal(g21, g22-g26) x5
    c: PointOnObject(g21,g27)
    c: PointOnObject(g22,g27)
    c: PointOnObject(g23,g27)
    c: PointOnObject(g24,g27)
    c: PointOnObject(g25,g27)
    c: PointOnObject(g26,g27)
    c: Diameter(g27) = 7
    c: DistanceY(g-1,g27) = 7
    c: DistanceX(g21,g-1) = 1
    c: Vertical(g21)
    c: Coincident(g28,g29)
    c: Coincident(g29,g30)
    c: Coincident(g30,g31)
    c: Coincident(g31,g32)
    c: Coincident(g32,g33)
    c: Coincident(g33,g28)
    c: Equal(g28, g29-g33) x5
    c: PointOnObject(g28,g34)
    c: PointOnObject(g29,g34)
    c: PointOnObject(g30,g34)
    c: PointOnObject(g31,g34)
    c: PointOnObject(g32,g34)
    c: PointOnObject(g33,g34)
    c: PointOnObject(g34,g-1)
    c: Diameter(g34) = 7
    c: Vertical(g31)
    c: DistanceX(g34,g-1) = 8
    c: Coincident(g35,g36)
    c: Coincident(g36,g37)
    c: Coincident(g37,g38)
    c: Coincident(g38,g39)
    c: Coincident(g39,g40)
    c: Coincident(g40,g35)
    c: Equal(g35, g36-g40) x5
    c: PointOnObject(g35,g41)
    c: PointOnObject(g36,g41)
    c: PointOnObject(g37,g41)
    c: PointOnObject(g38,g41)
    c: PointOnObject(g39,g41)
    c: PointOnObject(g40,g41)
    c: Coincident(g42,g43)
    c: Coincident(g43,g44)
    c: Coincident(g44,g45)
    c: Coincident(g45,g46)
    c: Coincident(g46,g47)
    c: Coincident(g47,g42)
    c: Equal(g42, g43-g47) x5
    c: PointOnObject(g42,g48)
    c: PointOnObject(g43,g48)
    c: PointOnObject(g44,g48)
    c: PointOnObject(g45,g48)
    c: PointOnObject(g46,g48)
    c: PointOnObject(g47,g48)
    c: Equal(g41,g48)
    c: Diameter(g41) = 7
    c: Vertical(g39)
    c: Vertical(g43)
    c: Distance(g-2,g39) = 1
    c: Symmetric(g38,g43,g-2)
    c: Distance(g41,g-1) = 7
FEATURE [Part::Extrusion] Extrude405  label="hex020"
  Base = -> Sketch413
  Dir = (0,-1,2e-16)
  DirMode = 2
  FaceMakerClass = Part::FaceMakerBullseye
  FaceMakerMode = 3
  LengthFwd = 10
  LengthRev = 0
  Placement = pos=(52,0,-21) rot=(0,0,1;0rad)
  Solid = true
  Symmetric = false
FEATURE [Sketcher::SketchObject] Sketch414
  ArcFitTolerance = 1e-06
  FullyConstrained = true
  MakeInternals = false
  Placement = pos=(0,0,0) rot=(1,0,0;1.5708rad)
  sketch-geometry (49):
    g0: LineSegment StartX=1e-16 StartY=3.5 StartZ=0 EndX=-3.03109 EndY=1.75 EndZ=0
    g1: LineSegment StartX=-3.03109 StartY=1.75 StartZ=0 EndX=-3.03109 EndY=-1.75 EndZ=0
    g2: LineSegment StartX=-3.03109 StartY=-1.75 StartZ=0 EndX=-1e-16 EndY=-3.5 EndZ=0
    g3: LineSegment StartX=-1e-16 StartY=-3.5 StartZ=0 EndX=3.03109 EndY=-1.75 EndZ=0
    g4: LineSegment StartX=3.03109 StartY=-1.75 StartZ=0 EndX=3.03109 EndY=1.75 EndZ=0
    g5: LineSegment StartX=3.03109 StartY=1.75 StartZ=0 EndX=1e-16 EndY=3.5 EndZ=0
    g6: Circle [constr] CenterX=0 CenterY=0 CenterZ=0 NormalX=0 NormalY=0 NormalZ=1 AngleXU=0 Radius=3.5
    g7: LineSegment StartX=4.96892 StartY=-1.75002 StartZ=0 EndX=8.00002 EndY=-3.5 EndZ=0
    g8: LineSegment StartX=8.00002 StartY=-3.5 StartZ=0 EndX=11.0311 EndY=-1.74998 EndZ=0
    g9: LineSegment StartX=11.0311 StartY=-1.74998 StartZ=0 EndX=11.0311 EndY=1.75002 EndZ=0
    g10: LineSegment StartX=11.0311 StartY=1.75002 StartZ=0 EndX=7.99998 EndY=3.5 EndZ=0
    g11: LineSegment StartX=7.99998 StartY=3.5 StartZ=0 EndX=4.9689 EndY=1.74998 EndZ=0
    g12: LineSegment StartX=4.9689 StartY=1.74998 StartZ=0 EndX=4.96892 EndY=-1.75002 EndZ=0
    g13: Circle [constr] CenterX=8 CenterY=0 CenterZ=0 NormalX=0 NormalY=0 NormalZ=1 AngleXU=0 Radius=3.5
    g14: LineSegment StartX=4.03109 StartY=3.5 StartZ=0 EndX=7.06218 EndY=5.25 EndZ=0
    g15: LineSegment StartX=7.06218 StartY=5.25 StartZ=0 EndX=7.06218 EndY=8.75 EndZ=0
    g16: LineSegment StartX=7.06218 StartY=8.75 StartZ=0 EndX=4.03109 EndY=10.5 EndZ=0
    g17: LineSegment StartX=4.03109 StartY=10.5 StartZ=0 EndX=1 EndY=8.75 EndZ=0
    g18: LineSegment StartX=1 StartY=8.75 StartZ=0 EndX=1 EndY=5.25 EndZ=0
    g19: LineSegment StartX=1 StartY=5.25 StartZ=0 EndX=4.03109 EndY=3.5 EndZ=0
    g20: Circle [constr] CenterX=4.03109 CenterY=7 CenterZ=0 NormalX=0 NormalY=0 NormalZ=1 AngleXU=0 Radius=3.5
    g21: LineSegment StartX=-1 StartY=5.25 StartZ=0 EndX=-1 EndY=8.75 EndZ=0
    g22: LineSegment StartX=-1 StartY=8.75 StartZ=0 EndX=-4.03109 EndY=10.5 EndZ=0
    g23: LineSegment StartX=-4.03109 StartY=10.5 StartZ=0 EndX=-7.06218 EndY=8.75 EndZ=0
    g24: LineSegment StartX=-7.06218 StartY=8.75 StartZ=0 EndX=-7.06218 EndY=5.25 EndZ=0
    g25: LineSegment StartX=-7.06218 StartY=5.25 StartZ=0 EndX=-4.03109 EndY=3.5 EndZ=0
    g26: LineSegment StartX=-4.03109 StartY=3.5 StartZ=0 EndX=-1 EndY=5.25 EndZ=0
    g27: Circle [constr] CenterX=-4.03109 CenterY=7 CenterZ=0 NormalX=0 NormalY=0 NormalZ=1 AngleXU=0 Radius=3.5
    g28: LineSegment StartX=-4.96891 StartY=-1.75 StartZ=0 EndX=-4.96891 EndY=1.75 EndZ=0
    g29: LineSegment StartX=-4.96891 StartY=1.75 StartZ=0 EndX=-8 EndY=3.5 EndZ=0
    g30: LineSegment StartX=-8 StartY=3.5 StartZ=0 EndX=-11.0311 EndY=1.75 EndZ=0
    g31: LineSegment StartX=-11.0311 StartY=1.75 StartZ=0 EndX=-11.0311 EndY=-1.75 EndZ=0
    g32: LineSegment StartX=-11.0311 StartY=-1.75 StartZ=0 EndX=-8 EndY=-3.5 EndZ=0
    g33: LineSegment StartX=-8 StartY=-3.5 StartZ=0 EndX=-4.96891 EndY=-1.75 EndZ=0
    g34: Circle [constr] CenterX=-8 CenterY=0 CenterZ=0 NormalX=0 NormalY=0 NormalZ=1 AngleXU=0 Radius=3.5
    g35: LineSegment StartX=-4.03109 StartY=-3.5 StartZ=0 EndX=-7.06218 EndY=-5.25 EndZ=0
    g36: LineSegment StartX=-7.06218 StartY=-5.25 StartZ=0 EndX=-7.06218 EndY=-8.75 EndZ=0
    g37: LineSegment StartX=-7.06218 StartY=-8.75 StartZ=0 EndX=-4.03109 EndY=-10.5 EndZ=0
    g38: LineSegment StartX=-4.03109 StartY=-10.5 StartZ=0 EndX=-1 EndY=-8.75 EndZ=0
    g39: LineSegment StartX=-1 StartY=-8.75 StartZ=0 EndX=-1 EndY=-5.25 EndZ=0
    g40: LineSegment StartX=-1 StartY=-5.25 StartZ=0 EndX=-4.03109 EndY=-3.5 EndZ=0
    g41: Circle [constr] CenterX=-4.03109 CenterY=-7 CenterZ=0 NormalX=0 NormalY=0 NormalZ=1 AngleXU=0 Radius=3.5
    g42: LineSegment StartX=4.03109 StartY=-3.5 StartZ=0 EndX=1 EndY=-5.25 EndZ=0
    g43: LineSegment StartX=1 StartY=-5.25 StartZ=0 EndX=1 EndY=-8.75 EndZ=0
    g44: LineSegment StartX=1 StartY=-8.75 StartZ=0 EndX=4.03109 EndY=-10.5 EndZ=0
    g45: LineSegment StartX=4.03109 StartY=-10.5 StartZ=0 EndX=7.06218 EndY=-8.75 EndZ=0
    g46: LineSegment StartX=7.06218 StartY=-8.75 StartZ=0 EndX=7.06218 EndY=-5.25 EndZ=0
    g47: LineSegment StartX=7.06218 StartY=-5.25 StartZ=0 EndX=4.03109 EndY=-3.5 EndZ=0
    g48: Circle [constr] CenterX=4.03109 CenterY=-7 CenterZ=0 NormalX=0 NormalY=0 NormalZ=1 AngleXU=0 Radius=3.5
  constraints (117):
    c: Coincident(g0,g1)
    c: Coincident(g1,g2)
    c: Coincident(g2,g3)
    c: Coincident(g3,g4)
    c: Coincident(g4,g5)
    c: Coincident(g5,g0)
    c: Equal(g0, g1-g5) x5
    c: PointOnObject(g0,g6)
    c: PointOnObject(g1,g6)
    c: PointOnObject(g2,g6)
    c: PointOnObject(g3,g6)
    c: PointOnObject(g4,g6)
    c: PointOnObject(g5,g6)
    c: Coincident(g6,g-1)
    c: Diameter(g6) = 7
    c: PointOnObject(g0,g-2)
    c: Coincident(g7,g8)
    c: Coincident(g8,g9)
    c: Coincident(g9,g10)
    c: Coincident(g10,g11)
    c: Coincident(g11,g12)
    c: Coincident(g12,g7)
    c: Equal(g7, g8-g12) x5
    c: PointOnObject(g7,g13)
    c: PointOnObject(g8,g13)
    c: PointOnObject(g9,g13)
    c: PointOnObject(g10,g13)
    c: PointOnObject(g11,g13)
    c: PointOnObject(g12,g13)
    c: PointOnObject(g13,g-1)
    c: Diameter(g13) = 7
    c: Distance(g6,g13) = 8
    c: Horizontal(g0,g10)
    c: Coincident(g14,g15)
    c: Coincident(g15,g16)
    c: Coincident(g16,g17)
    c: Coincident(g17,g18)
    c: Coincident(g18,g19)
    c: Coincident(g19,g14)
    c: Equal(g14, g15-g19) x5
    c: PointOnObject(g14,g20)
    c: PointOnObject(g15,g20)
    c: PointOnObject(g16,g20)
    c: PointOnObject(g17,g20)
    c: PointOnObject(g18,g20)
    c: PointOnObject(g19,g20)
    c: Diameter(g20) = 7
    c: DistanceY(g-1,g20) = 7
    c: Vertical(g18)
    c: Distance(g17,g-2) = 1
    c: Coincident(g21,g22)
    c: Coincident(g22,g23)
    c: Coincident(g23,g24)
    c: Coincident(g24,g25)
    c: Coincident(g25,g26)
    c: Coincident(g26,g21)
    c: Equal(g21, g22-g26) x5
    c: PointOnObject(g21,g27)
    c: PointOnObject(g22,g27)
    c: PointOnObject(g23,g27)
    c: PointOnObject(g24,g27)
    c: PointOnObject(g25,g27)
    c: PointOnObject(g26,g27)
    c: Diameter(g27) = 7
    c: DistanceY(g-1,g27) = 7
    c: DistanceX(g21,g-1) = 1
    c: Vertical(g21)
    c: Coincident(g28,g29)
    c: Coincident(g29,g30)
    c: Coincident(g30,g31)
    c: Coincident(g31,g32)
    c: Coincident(g32,g33)
    c: Coincident(g33,g28)
    c: Equal(g28, g29-g33) x5
    c: PointOnObject(g28,g34)
    c: PointOnObject(g29,g34)
    c: PointOnObject(g30,g34)
    c: PointOnObject(g31,g34)
    c: PointOnObject(g32,g34)
    c: PointOnObject(g33,g34)
    c: PointOnObject(g34,g-1)
    c: Diameter(g34) = 7
    c: Vertical(g31)
    c: DistanceX(g34,g-1) = 8
    c: Coincident(g35,g36)
    c: Coincident(g36,g37)
    c: Coincident(g37,g38)
    c: Coincident(g38,g39)
    c: Coincident(g39,g40)
    c: Coincident(g40,g35)
    c: Equal(g35, g36-g40) x5
    c: PointOnObject(g35,g41)
    c: PointOnObject(g36,g41)
    c: PointOnObject(g37,g41)
    c: PointOnObject(g38,g41)
    c: PointOnObject(g39,g41)
    c: PointOnObject(g40,g41)
    c: Coincident(g42,g43)
    c: Coincident(g43,g44)
    c: Coincident(g44,g45)
    c: Coincident(g45,g46)
    c: Coincident(g46,g47)
    c: Coincident(g47,g42)
    c: Equal(g42, g43-g47) x5
    c: PointOnObject(g42,g48)
    c: PointOnObject(g43,g48)
    c: PointOnObject(g44,g48)
    c: PointOnObject(g45,g48)
    c: PointOnObject(g46,g48)
    c: PointOnObject(g47,g48)
    c: Equal(g41,g48)
    c: Diameter(g41) = 7
    c: Vertical(g39)
    c: Vertical(g43)
    c: Distance(g-2,g39) = 1
    c: Symmetric(g38,g43,g-2)
    c: Distance(g41,g-1) = 7
FEATURE [Part::Extrusion] Extrude406  label="hex021"
  Base = -> Sketch414
  Dir = (0,-1,2e-16)
  DirMode = 2
  FaceMakerClass = Part::FaceMakerBullseye
  FaceMakerMode = 3
  LengthFwd = 10
  LengthRev = 0
  Placement = pos=(-56,0,0) rot=(0,0,1;0rad)
  Solid = true
  Symmetric = false
FEATURE [Sketcher::SketchObject] Sketch415
  ArcFitTolerance = 1e-06
  FullyConstrained = true
  MakeInternals = false
  Placement = pos=(0,0,0) rot=(1,0,0;1.5708rad)
  sketch-geometry (49):
    g0: LineSegment StartX=1e-16 StartY=3.5 StartZ=0 EndX=-3.03109 EndY=1.75 EndZ=0
    g1: LineSegment StartX=-3.03109 StartY=1.75 StartZ=0 EndX=-3.03109 EndY=-1.75 EndZ=0
    g2: LineSegment StartX=-3.03109 StartY=-1.75 StartZ=0 EndX=-1e-16 EndY=-3.5 EndZ=0
    g3: LineSegment StartX=-1e-16 StartY=-3.5 StartZ=0 EndX=3.03109 EndY=-1.75 EndZ=0
    g4: LineSegment StartX=3.03109 StartY=-1.75 StartZ=0 EndX=3.03109 EndY=1.75 EndZ=0
    g5: LineSegment StartX=3.03109 StartY=1.75 StartZ=0 EndX=1e-16 EndY=3.5 EndZ=0
    g6: Circle [constr] CenterX=0 CenterY=0 CenterZ=0 NormalX=0 NormalY=0 NormalZ=1 AngleXU=0 Radius=3.5
    g7: LineSegment StartX=4.96892 StartY=-1.75002 StartZ=0 EndX=8.00002 EndY=-3.5 EndZ=0
    g8: LineSegment StartX=8.00002 StartY=-3.5 StartZ=0 EndX=11.0311 EndY=-1.74998 EndZ=0
    g9: LineSegment StartX=11.0311 StartY=-1.74998 StartZ=0 EndX=11.0311 EndY=1.75002 EndZ=0
    g10: LineSegment StartX=11.0311 StartY=1.75002 StartZ=0 EndX=7.99998 EndY=3.5 EndZ=0
    g11: LineSegment StartX=7.99998 StartY=3.5 StartZ=0 EndX=4.9689 EndY=1.74998 EndZ=0
    g12: LineSegment StartX=4.9689 StartY=1.74998 StartZ=0 EndX=4.96892 EndY=-1.75002 EndZ=0
    g13: Circle [constr] CenterX=8 CenterY=0 CenterZ=0 NormalX=0 NormalY=0 NormalZ=1 AngleXU=0 Radius=3.5
    g14: LineSegment StartX=4.03109 StartY=3.5 StartZ=0 EndX=7.06218 EndY=5.25 EndZ=0
    g15: LineSegment StartX=7.06218 StartY=5.25 StartZ=0 EndX=7.06218 EndY=8.75 EndZ=0
    g16: LineSegment StartX=7.06218 StartY=8.75 StartZ=0 EndX=4.03109 EndY=10.5 EndZ=0
    g17: LineSegment StartX=4.03109 StartY=10.5 StartZ=0 EndX=1 EndY=8.75 EndZ=0
    g18: LineSegment StartX=1 StartY=8.75 StartZ=0 EndX=1 EndY=5.25 EndZ=0
    g19: LineSegment StartX=1 StartY=5.25 StartZ=0 EndX=4.03109 EndY=3.5 EndZ=0
    g20: Circle [constr] CenterX=4.03109 CenterY=7 CenterZ=0 NormalX=0 NormalY=0 NormalZ=1 AngleXU=0 Radius=3.5
    g21: LineSegment StartX=-1 StartY=5.25 StartZ=0 EndX=-1 EndY=8.75 EndZ=0
    g22: LineSegment StartX=-1 StartY=8.75 StartZ=0 EndX=-4.03109 EndY=10.5 EndZ=0
    g23: LineSegment StartX=-4.03109 StartY=10.5 StartZ=0 EndX=-7.06218 EndY=8.75 EndZ=0
    g24: LineSegment StartX=-7.06218 StartY=8.75 StartZ=0 EndX=-7.06218 EndY=5.25 EndZ=0
    g25: LineSegment StartX=-7.06218 StartY=5.25 StartZ=0 EndX=-4.03109 EndY=3.5 EndZ=0
    g26: LineSegment StartX=-4.03109 StartY=3.5 StartZ=0 EndX=-1 EndY=5.25 EndZ=0
    g27: Circle [constr] CenterX=-4.03109 CenterY=7 CenterZ=0 NormalX=0 NormalY=0 NormalZ=1 AngleXU=0 Radius=3.5
    g28: LineSegment StartX=-4.96891 StartY=-1.75 StartZ=0 EndX=-4.96891 EndY=1.75 EndZ=0
    g29: LineSegment StartX=-4.96891 StartY=1.75 StartZ=0 EndX=-8 EndY=3.5 EndZ=0
    g30: LineSegment StartX=-8 StartY=3.5 StartZ=0 EndX=-11.0311 EndY=1.75 EndZ=0
    g31: LineSegment StartX=-11.0311 StartY=1.75 StartZ=0 EndX=-11.0311 EndY=-1.75 EndZ=0
    g32: LineSegment StartX=-11.0311 StartY=-1.75 StartZ=0 EndX=-8 EndY=-3.5 EndZ=0
    g33: LineSegment StartX=-8 StartY=-3.5 StartZ=0 EndX=-4.96891 EndY=-1.75 EndZ=0
    g34: Circle [constr] CenterX=-8 CenterY=0 CenterZ=0 NormalX=0 NormalY=0 NormalZ=1 AngleXU=0 Radius=3.5
    g35: LineSegment StartX=-4.03109 StartY=-3.5 StartZ=0 EndX=-7.06218 EndY=-5.25 EndZ=0
    g36: LineSegment StartX=-7.06218 StartY=-5.25 StartZ=0 EndX=-7.06218 EndY=-8.75 EndZ=0
    g37: LineSegment StartX=-7.06218 StartY=-8.75 StartZ=0 EndX=-4.03109 EndY=-10.5 EndZ=0
    g38: LineSegment StartX=-4.03109 StartY=-10.5 StartZ=0 EndX=-1 EndY=-8.75 EndZ=0
    g39: LineSegment StartX=-1 StartY=-8.75 StartZ=0 EndX=-1 EndY=-5.25 EndZ=0
    g40: LineSegment StartX=-1 StartY=-5.25 StartZ=0 EndX=-4.03109 EndY=-3.5 EndZ=0
    g41: Circle [constr] CenterX=-4.03109 CenterY=-7 CenterZ=0 NormalX=0 NormalY=0 NormalZ=1 AngleXU=0 Radius=3.5
    g42: LineSegment StartX=4.03109 StartY=-3.5 StartZ=0 EndX=1 EndY=-5.25 EndZ=0
    g43: LineSegment StartX=1 StartY=-5.25 StartZ=0 EndX=1 EndY=-8.75 EndZ=0
    g44: LineSegment StartX=1 StartY=-8.75 StartZ=0 EndX=4.03109 EndY=-10.5 EndZ=0
    g45: LineSegment StartX=4.03109 StartY=-10.5 StartZ=0 EndX=7.06218 EndY=-8.75 EndZ=0
    g46: LineSegment StartX=7.06218 StartY=-8.75 StartZ=0 EndX=7.06218 EndY=-5.25 EndZ=0
    g47: LineSegment StartX=7.06218 StartY=-5.25 StartZ=0 EndX=4.03109 EndY=-3.5 EndZ=0
    g48: Circle [constr] CenterX=4.03109 CenterY=-7 CenterZ=0 NormalX=0 NormalY=0 NormalZ=1 AngleXU=0 Radius=3.5
  constraints (117):
    c: Coincident(g0,g1)
    c: Coincident(g1,g2)
    c: Coincident(g2,g3)
    c: Coincident(g3,g4)
    c: Coincident(g4,g5)
    c: Coincident(g5,g0)
    c: Equal(g0, g1-g5) x5
    c: PointOnObject(g0,g6)
    c: PointOnObject(g1,g6)
    c: PointOnObject(g2,g6)
    c: PointOnObject(g3,g6)
    c: PointOnObject(g4,g6)
    c: PointOnObject(g5,g6)
    c: Coincident(g6,g-1)
    c: Diameter(g6) = 7
    c: PointOnObject(g0,g-2)
    c: Coincident(g7,g8)
    c: Coincident(g8,g9)
    c: Coincident(g9,g10)
    c: Coincident(g10,g11)
    c: Coincident(g11,g12)
    c: Coincident(g12,g7)
    c: Equal(g7, g8-g12) x5
    c: PointOnObject(g7,g13)
    c: PointOnObject(g8,g13)
    c: PointOnObject(g9,g13)
    c: PointOnObject(g10,g13)
    c: PointOnObject(g11,g13)
    c: PointOnObject(g12,g13)
    c: PointOnObject(g13,g-1)
    c: Diameter(g13) = 7
    c: Distance(g6,g13) = 8
    c: Horizontal(g0,g10)
    c: Coincident(g14,g15)
    c: Coincident(g15,g16)
    c: Coincident(g16,g17)
    c: Coincident(g17,g18)
    c: Coincident(g18,g19)
    c: Coincident(g19,g14)
    c: Equal(g14, g15-g19) x5
    c: PointOnObject(g14,g20)
    c: PointOnObject(g15,g20)
    c: PointOnObject(g16,g20)
    c: PointOnObject(g17,g20)
    c: PointOnObject(g18,g20)
    c: PointOnObject(g19,g20)
    c: Diameter(g20) = 7
    c: DistanceY(g-1,g20) = 7
    c: Vertical(g18)
    c: Distance(g17,g-2) = 1
    c: Coincident(g21,g22)
    c: Coincident(g22,g23)
    c: Coincident(g23,g24)
    c: Coincident(g24,g25)
    c: Coincident(g25,g26)
    c: Coincident(g26,g21)
    c: Equal(g21, g22-g26) x5
    c: PointOnObject(g21,g27)
    c: PointOnObject(g22,g27)
    c: PointOnObject(g23,g27)
    c: PointOnObject(g24,g27)
    c: PointOnObject(g25,g27)
    c: PointOnObject(g26,g27)
    c: Diameter(g27) = 7
    c: DistanceY(g-1,g27) = 7
    c: DistanceX(g21,g-1) = 1
    c: Vertical(g21)
    c: Coincident(g28,g29)
    c: Coincident(g29,g30)
    c: Coincident(g30,g31)
    c: Coincident(g31,g32)
    c: Coincident(g32,g33)
    c: Coincident(g33,g28)
    c: Equal(g28, g29-g33) x5
    c: PointOnObject(g28,g34)
    c: PointOnObject(g29,g34)
    c: PointOnObject(g30,g34)
    c: PointOnObject(g31,g34)
    c: PointOnObject(g32,g34)
    c: PointOnObject(g33,g34)
    c: PointOnObject(g34,g-1)
    c: Diameter(g34) = 7
    c: Vertical(g31)
    c: DistanceX(g34,g-1) = 8
    c: Coincident(g35,g36)
    c: Coincident(g36,g37)
    c: Coincident(g37,g38)
    c: Coincident(g38,g39)
    c: Coincident(g39,g40)
    c: Coincident(g40,g35)
    c: Equal(g35, g36-g40) x5
    c: PointOnObject(g35,g41)
    c: PointOnObject(g36,g41)
    c: PointOnObject(g37,g41)
    c: PointOnObject(g38,g41)
    c: PointOnObject(g39,g41)
    c: PointOnObject(g40,g41)
    c: Coincident(g42,g43)
    c: Coincident(g43,g44)
    c: Coincident(g44,g45)
    c: Coincident(g45,g46)
    c: Coincident(g46,g47)
    c: Coincident(g47,g42)
    c: Equal(g42, g43-g47) x5
    c: PointOnObject(g42,g48)
    c: PointOnObject(g43,g48)
    c: PointOnObject(g44,g48)
    c: PointOnObject(g45,g48)
    c: PointOnObject(g46,g48)
    c: PointOnObject(g47,g48)
    c: Equal(g41,g48)
    c: Diameter(g41) = 7
    c: Vertical(g39)
    c: Vertical(g43)
    c: Distance(g-2,g39) = 1
    c: Symmetric(g38,g43,g-2)
    c: Distance(g41,g-1) = 7
FEATURE [Part::Extrusion] Extrude407  label="hex022"
  Base = -> Sketch415
  Dir = (0,-1,2e-16)
  DirMode = 2
  FaceMakerClass = Part::FaceMakerBullseye
  FaceMakerMode = 3
  LengthFwd = 10
  LengthRev = 0
  Placement = pos=(-52,0,21) rot=(0,0,1;0rad)
  Solid = true
  Symmetric = false
FEATURE [Sketcher::SketchObject] Sketch416
  ArcFitTolerance = 1e-06
  FullyConstrained = true
  MakeInternals = false
  Placement = pos=(0,0,0) rot=(1,0,0;1.5708rad)
  sketch-geometry (49):
    g0: LineSegment StartX=1e-16 StartY=3.5 StartZ=0 EndX=-3.03109 EndY=1.75 EndZ=0
    g1: LineSegment StartX=-3.03109 StartY=1.75 StartZ=0 EndX=-3.03109 EndY=-1.75 EndZ=0
    g2: LineSegment StartX=-3.03109 StartY=-1.75 StartZ=0 EndX=-1e-16 EndY=-3.5 EndZ=0
    g3: LineSegment StartX=-1e-16 StartY=-3.5 StartZ=0 EndX=3.03109 EndY=-1.75 EndZ=0
    g4: LineSegment StartX=3.03109 StartY=-1.75 StartZ=0 EndX=3.03109 EndY=1.75 EndZ=0
    g5: LineSegment StartX=3.03109 StartY=1.75 StartZ=0 EndX=1e-16 EndY=3.5 EndZ=0
    g6: Circle [constr] CenterX=0 CenterY=0 CenterZ=0 NormalX=0 NormalY=0 NormalZ=1 AngleXU=0 Radius=3.5
    g7: LineSegment StartX=4.96892 StartY=-1.75002 StartZ=0 EndX=8.00002 EndY=-3.5 EndZ=0
    g8: LineSegment StartX=8.00002 StartY=-3.5 StartZ=0 EndX=11.0311 EndY=-1.74998 EndZ=0
    g9: LineSegment StartX=11.0311 StartY=-1.74998 StartZ=0 EndX=11.0311 EndY=1.75002 EndZ=0
    g10: LineSegment StartX=11.0311 StartY=1.75002 StartZ=0 EndX=7.99998 EndY=3.5 EndZ=0
    g11: LineSegment StartX=7.99998 StartY=3.5 StartZ=0 EndX=4.9689 EndY=1.74998 EndZ=0
    g12: LineSegment StartX=4.9689 StartY=1.74998 StartZ=0 EndX=4.96892 EndY=-1.75002 EndZ=0
    g13: Circle [constr] CenterX=8 CenterY=0 CenterZ=0 NormalX=0 NormalY=0 NormalZ=1 AngleXU=0 Radius=3.5
    g14: LineSegment StartX=4.03109 StartY=3.5 StartZ=0 EndX=7.06218 EndY=5.25 EndZ=0
    g15: LineSegment StartX=7.06218 StartY=5.25 StartZ=0 EndX=7.06218 EndY=8.75 EndZ=0
    g16: LineSegment StartX=7.06218 StartY=8.75 StartZ=0 EndX=4.03109 EndY=10.5 EndZ=0
    g17: LineSegment StartX=4.03109 StartY=10.5 StartZ=0 EndX=1 EndY=8.75 EndZ=0
    g18: LineSegment StartX=1 StartY=8.75 StartZ=0 EndX=1 EndY=5.25 EndZ=0
    g19: LineSegment StartX=1 StartY=5.25 StartZ=0 EndX=4.03109 EndY=3.5 EndZ=0
    g20: Circle [constr] CenterX=4.03109 CenterY=7 CenterZ=0 NormalX=0 NormalY=0 NormalZ=1 AngleXU=0 Radius=3.5
    g21: LineSegment StartX=-1 StartY=5.25 StartZ=0 EndX=-1 EndY=8.75 EndZ=0
    g22: LineSegment StartX=-1 StartY=8.75 StartZ=0 EndX=-4.03109 EndY=10.5 EndZ=0
    g23: LineSegment StartX=-4.03109 StartY=10.5 StartZ=0 EndX=-7.06218 EndY=8.75 EndZ=0
    g24: LineSegment StartX=-7.06218 StartY=8.75 StartZ=0 EndX=-7.06218 EndY=5.25 EndZ=0
    g25: LineSegment StartX=-7.06218 StartY=5.25 StartZ=0 EndX=-4.03109 EndY=3.5 EndZ=0
    g26: LineSegment StartX=-4.03109 StartY=3.5 StartZ=0 EndX=-1 EndY=5.25 EndZ=0
    g27: Circle [constr] CenterX=-4.03109 CenterY=7 CenterZ=0 NormalX=0 NormalY=0 NormalZ=1 AngleXU=0 Radius=3.5
    g28: LineSegment StartX=-4.96891 StartY=-1.75 StartZ=0 EndX=-4.96891 EndY=1.75 EndZ=0
    g29: LineSegment StartX=-4.96891 StartY=1.75 StartZ=0 EndX=-8 EndY=3.5 EndZ=0
    g30: LineSegment StartX=-8 StartY=3.5 StartZ=0 EndX=-11.0311 EndY=1.75 EndZ=0
    g31: LineSegment StartX=-11.0311 StartY=1.75 StartZ=0 EndX=-11.0311 EndY=-1.75 EndZ=0
    g32: LineSegment StartX=-11.0311 StartY=-1.75 StartZ=0 EndX=-8 EndY=-3.5 EndZ=0
    g33: LineSegment StartX=-8 StartY=-3.5 StartZ=0 EndX=-4.96891 EndY=-1.75 EndZ=0
    g34: Circle [constr] CenterX=-8 CenterY=0 CenterZ=0 NormalX=0 NormalY=0 NormalZ=1 AngleXU=0 Radius=3.5
    g35: LineSegment StartX=-4.03109 StartY=-3.5 StartZ=0 EndX=-7.06218 EndY=-5.25 EndZ=0
    g36: LineSegment StartX=-7.06218 StartY=-5.25 StartZ=0 EndX=-7.06218 EndY=-8.75 EndZ=0
    g37: LineSegment StartX=-7.06218 StartY=-8.75 StartZ=0 EndX=-4.03109 EndY=-10.5 EndZ=0
    g38: LineSegment StartX=-4.03109 StartY=-10.5 StartZ=0 EndX=-1 EndY=-8.75 EndZ=0
    g39: LineSegment StartX=-1 StartY=-8.75 StartZ=0 EndX=-1 EndY=-5.25 EndZ=0
    g40: LineSegment StartX=-1 StartY=-5.25 StartZ=0 EndX=-4.03109 EndY=-3.5 EndZ=0
    g41: Circle [constr] CenterX=-4.03109 CenterY=-7 CenterZ=0 NormalX=0 NormalY=0 NormalZ=1 AngleXU=0 Radius=3.5
    g42: LineSegment StartX=4.03109 StartY=-3.5 StartZ=0 EndX=1 EndY=-5.25 EndZ=0
    g43: LineSegment StartX=1 StartY=-5.25 StartZ=0 EndX=1 EndY=-8.75 EndZ=0
    g44: LineSegment StartX=1 StartY=-8.75 StartZ=0 EndX=4.03109 EndY=-10.5 EndZ=0
    g45: LineSegment StartX=4.03109 StartY=-10.5 StartZ=0 EndX=7.06218 EndY=-8.75 EndZ=0
    g46: LineSegment StartX=7.06218 StartY=-8.75 StartZ=0 EndX=7.06218 EndY=-5.25 EndZ=0
    g47: LineSegment StartX=7.06218 StartY=-5.25 StartZ=0 EndX=4.03109 EndY=-3.5 EndZ=0
    g48: Circle [constr] CenterX=4.03109 CenterY=-7 CenterZ=0 NormalX=0 NormalY=0 NormalZ=1 AngleXU=0 Radius=3.5
  constraints (117):
    c: Coincident(g0,g1)
    c: Coincident(g1,g2)
    c: Coincident(g2,g3)
    c: Coincident(g3,g4)
    c: Coincident(g4,g5)
    c: Coincident(g5,g0)
    c: Equal(g0, g1-g5) x5
    c: PointOnObject(g0,g6)
    c: PointOnObject(g1,g6)
    c: PointOnObject(g2,g6)
    c: PointOnObject(g3,g6)
    c: PointOnObject(g4,g6)
    c: PointOnObject(g5,g6)
    c: Coincident(g6,g-1)
    c: Diameter(g6) = 7
    c: PointOnObject(g0,g-2)
    c: Coincident(g7,g8)
    c: Coincident(g8,g9)
    c: Coincident(g9,g10)
    c: Coincident(g10,g11)
    c: Coincident(g11,g12)
    c: Coincident(g12,g7)
    c: Equal(g7, g8-g12) x5
    c: PointOnObject(g7,g13)
    c: PointOnObject(g8,g13)
    c: PointOnObject(g9,g13)
    c: PointOnObject(g10,g13)
    c: PointOnObject(g11,g13)
    c: PointOnObject(g12,g13)
    c: PointOnObject(g13,g-1)
    c: Diameter(g13) = 7
    c: Distance(g6,g13) = 8
    c: Horizontal(g0,g10)
    c: Coincident(g14,g15)
    c: Coincident(g15,g16)
    c: Coincident(g16,g17)
    c: Coincident(g17,g18)
    c: Coincident(g18,g19)
    c: Coincident(g19,g14)
    c: Equal(g14, g15-g19) x5
    c: PointOnObject(g14,g20)
    c: PointOnObject(g15,g20)
    c: PointOnObject(g16,g20)
    c: PointOnObject(g17,g20)
    c: PointOnObject(g18,g20)
    c: PointOnObject(g19,g20)
    c: Diameter(g20) = 7
    c: DistanceY(g-1,g20) = 7
    c: Vertical(g18)
    c: Distance(g17,g-2) = 1
    c: Coincident(g21,g22)
    c: Coincident(g22,g23)
    c: Coincident(g23,g24)
    c: Coincident(g24,g25)
    c: Coincident(g25,g26)
    c: Coincident(g26,g21)
    c: Equal(g21, g22-g26) x5
    c: PointOnObject(g21,g27)
    c: PointOnObject(g22,g27)
    c: PointOnObject(g23,g27)
    c: PointOnObject(g24,g27)
    c: PointOnObject(g25,g27)
    c: PointOnObject(g26,g27)
    c: Diameter(g27) = 7
    c: DistanceY(g-1,g27) = 7
    c: DistanceX(g21,g-1) = 1
    c: Vertical(g21)
    c: Coincident(g28,g29)
    c: Coincident(g29,g30)
    c: Coincident(g30,g31)
    c: Coincident(g31,g32)
    c: Coincident(g32,g33)
    c: Coincident(g33,g28)
    c: Equal(g28, g29-g33) x5
    c: PointOnObject(g28,g34)
    c: PointOnObject(g29,g34)
    c: PointOnObject(g30,g34)
    c: PointOnObject(g31,g34)
    c: PointOnObject(g32,g34)
    c: PointOnObject(g33,g34)
    c: PointOnObject(g34,g-1)
    c: Diameter(g34) = 7
    c: Vertical(g31)
    c: DistanceX(g34,g-1) = 8
    c: Coincident(g35,g36)
    c: Coincident(g36,g37)
    c: Coincident(g37,g38)
    c: Coincident(g38,g39)
    c: Coincident(g39,g40)
    c: Coincident(g40,g35)
    c: Equal(g35, g36-g40) x5
    c: PointOnObject(g35,g41)
    c: PointOnObject(g36,g41)
    c: PointOnObject(g37,g41)
    c: PointOnObject(g38,g41)
    c: PointOnObject(g39,g41)
    c: PointOnObject(g40,g41)
    c: Coincident(g42,g43)
    c: Coincident(g43,g44)
    c: Coincident(g44,g45)
    c: Coincident(g45,g46)
    c: Coincident(g46,g47)
    c: Coincident(g47,g42)
    c: Equal(g42, g43-g47) x5
    c: PointOnObject(g42,g48)
    c: PointOnObject(g43,g48)
    c: PointOnObject(g44,g48)
    c: PointOnObject(g45,g48)
    c: PointOnObject(g46,g48)
    c: PointOnObject(g47,g48)
    c: Equal(g41,g48)
    c: Diameter(g41) = 7
    c: Vertical(g39)
    c: Vertical(g43)
    c: Distance(g-2,g39) = 1
    c: Symmetric(g38,g43,g-2)
    c: Distance(g41,g-1) = 7
FEATURE [Part::Extrusion] Extrude408  label="hex023"
  Base = -> Sketch416
  Dir = (0,-1,2e-16)
  DirMode = 2
  FaceMakerClass = Part::FaceMakerBullseye
  FaceMakerMode = 3
  LengthFwd = 10
  LengthRev = 0
  Placement = pos=(52,0,21) rot=(0,0,1;0rad)
  Solid = true
  Symmetric = false
FEATURE [Sketcher::SketchObject] Sketch417
  ArcFitTolerance = 1e-06
  FullyConstrained = true
  MakeInternals = false
  Placement = pos=(0,0,0) rot=(1,0,0;1.5708rad)
  sketch-geometry (49):
    g0: LineSegment StartX=1e-16 StartY=3.5 StartZ=0 EndX=-3.03109 EndY=1.75 EndZ=0
    g1: LineSegment StartX=-3.03109 StartY=1.75 StartZ=0 EndX=-3.03109 EndY=-1.75 EndZ=0
    g2: LineSegment StartX=-3.03109 StartY=-1.75 StartZ=0 EndX=-1e-16 EndY=-3.5 EndZ=0
    g3: LineSegment StartX=-1e-16 StartY=-3.5 StartZ=0 EndX=3.03109 EndY=-1.75 EndZ=0
    g4: LineSegment StartX=3.03109 StartY=-1.75 StartZ=0 EndX=3.03109 EndY=1.75 EndZ=0
    g5: LineSegment StartX=3.03109 StartY=1.75 StartZ=0 EndX=1e-16 EndY=3.5 EndZ=0
    g6: Circle [constr] CenterX=0 CenterY=0 CenterZ=0 NormalX=0 NormalY=0 NormalZ=1 AngleXU=0 Radius=3.5
    g7: LineSegment StartX=4.96892 StartY=-1.75002 StartZ=0 EndX=8.00002 EndY=-3.5 EndZ=0
    g8: LineSegment StartX=8.00002 StartY=-3.5 StartZ=0 EndX=11.0311 EndY=-1.74998 EndZ=0
    g9: LineSegment StartX=11.0311 StartY=-1.74998 StartZ=0 EndX=11.0311 EndY=1.75002 EndZ=0
    g10: LineSegment StartX=11.0311 StartY=1.75002 StartZ=0 EndX=7.99998 EndY=3.5 EndZ=0
    g11: LineSegment StartX=7.99998 StartY=3.5 StartZ=0 EndX=4.9689 EndY=1.74998 EndZ=0
    g12: LineSegment StartX=4.9689 StartY=1.74998 StartZ=0 EndX=4.96892 EndY=-1.75002 EndZ=0
    g13: Circle [constr] CenterX=8 CenterY=0 CenterZ=0 NormalX=0 NormalY=0 NormalZ=1 AngleXU=0 Radius=3.5
    g14: LineSegment StartX=4.03109 StartY=3.5 StartZ=0 EndX=7.06218 EndY=5.25 EndZ=0
    g15: LineSegment StartX=7.06218 StartY=5.25 StartZ=0 EndX=7.06218 EndY=8.75 EndZ=0
    g16: LineSegment StartX=7.06218 StartY=8.75 StartZ=0 EndX=4.03109 EndY=10.5 EndZ=0
    g17: LineSegment StartX=4.03109 StartY=10.5 StartZ=0 EndX=1 EndY=8.75 EndZ=0
    g18: LineSegment StartX=1 StartY=8.75 StartZ=0 EndX=1 EndY=5.25 EndZ=0
    g19: LineSegment StartX=1 StartY=5.25 StartZ=0 EndX=4.03109 EndY=3.5 EndZ=0
    g20: Circle [constr] CenterX=4.03109 CenterY=7 CenterZ=0 NormalX=0 NormalY=0 NormalZ=1 AngleXU=0 Radius=3.5
    g21: LineSegment StartX=-1 StartY=5.25 StartZ=0 EndX=-1 EndY=8.75 EndZ=0
    g22: LineSegment StartX=-1 StartY=8.75 StartZ=0 EndX=-4.03109 EndY=10.5 EndZ=0
    g23: LineSegment StartX=-4.03109 StartY=10.5 StartZ=0 EndX=-7.06218 EndY=8.75 EndZ=0
    g24: LineSegment StartX=-7.06218 StartY=8.75 StartZ=0 EndX=-7.06218 EndY=5.25 EndZ=0
    g25: LineSegment StartX=-7.06218 StartY=5.25 StartZ=0 EndX=-4.03109 EndY=3.5 EndZ=0
    g26: LineSegment StartX=-4.03109 StartY=3.5 StartZ=0 EndX=-1 EndY=5.25 EndZ=0
    g27: Circle [constr] CenterX=-4.03109 CenterY=7 CenterZ=0 NormalX=0 NormalY=0 NormalZ=1 AngleXU=0 Radius=3.5
    g28: LineSegment StartX=-4.96891 StartY=-1.75 StartZ=0 EndX=-4.96891 EndY=1.75 EndZ=0
    g29: LineSegment StartX=-4.96891 StartY=1.75 StartZ=0 EndX=-8 EndY=3.5 EndZ=0
    g30: LineSegment StartX=-8 StartY=3.5 StartZ=0 EndX=-11.0311 EndY=1.75 EndZ=0
    g31: LineSegment StartX=-11.0311 StartY=1.75 StartZ=0 EndX=-11.0311 EndY=-1.75 EndZ=0
    g32: LineSegment StartX=-11.0311 StartY=-1.75 StartZ=0 EndX=-8 EndY=-3.5 EndZ=0
    g33: LineSegment StartX=-8 StartY=-3.5 StartZ=0 EndX=-4.96891 EndY=-1.75 EndZ=0
    g34: Circle [constr] CenterX=-8 CenterY=0 CenterZ=0 NormalX=0 NormalY=0 NormalZ=1 AngleXU=0 Radius=3.5
    g35: LineSegment StartX=-4.03109 StartY=-3.5 StartZ=0 EndX=-7.06218 EndY=-5.25 EndZ=0
    g36: LineSegment StartX=-7.06218 StartY=-5.25 StartZ=0 EndX=-7.06218 EndY=-8.75 EndZ=0
    g37: LineSegment StartX=-7.06218 StartY=-8.75 StartZ=0 EndX=-4.03109 EndY=-10.5 EndZ=0
    g38: LineSegment StartX=-4.03109 StartY=-10.5 StartZ=0 EndX=-1 EndY=-8.75 EndZ=0
    g39: LineSegment StartX=-1 StartY=-8.75 StartZ=0 EndX=-1 EndY=-5.25 EndZ=0
    g40: LineSegment StartX=-1 StartY=-5.25 StartZ=0 EndX=-4.03109 EndY=-3.5 EndZ=0
    g41: Circle [constr] CenterX=-4.03109 CenterY=-7 CenterZ=0 NormalX=0 NormalY=0 NormalZ=1 AngleXU=0 Radius=3.5
    g42: LineSegment StartX=4.03109 StartY=-3.5 StartZ=0 EndX=1 EndY=-5.25 EndZ=0
    g43: LineSegment StartX=1 StartY=-5.25 StartZ=0 EndX=1 EndY=-8.75 EndZ=0
    g44: LineSegment StartX=1 StartY=-8.75 StartZ=0 EndX=4.03109 EndY=-10.5 EndZ=0
    g45: LineSegment StartX=4.03109 StartY=-10.5 StartZ=0 EndX=7.06218 EndY=-8.75 EndZ=0
    g46: LineSegment StartX=7.06218 StartY=-8.75 StartZ=0 EndX=7.06218 EndY=-5.25 EndZ=0
    g47: LineSegment StartX=7.06218 StartY=-5.25 StartZ=0 EndX=4.03109 EndY=-3.5 EndZ=0
    g48: Circle [constr] CenterX=4.03109 CenterY=-7 CenterZ=0 NormalX=0 NormalY=0 NormalZ=1 AngleXU=0 Radius=3.5
  constraints (117):
    c: Coincident(g0,g1)
    c: Coincident(g1,g2)
    c: Coincident(g2,g3)
    c: Coincident(g3,g4)
    c: Coincident(g4,g5)
    c: Coincident(g5,g0)
    c: Equal(g0, g1-g5) x5
    c: PointOnObject(g0,g6)
    c: PointOnObject(g1,g6)
    c: PointOnObject(g2,g6)
    c: PointOnObject(g3,g6)
    c: PointOnObject(g4,g6)
    c: PointOnObject(g5,g6)
    c: Coincident(g6,g-1)
    c: Diameter(g6) = 7
    c: PointOnObject(g0,g-2)
    c: Coincident(g7,g8)
    c: Coincident(g8,g9)
    c: Coincident(g9,g10)
    c: Coincident(g10,g11)
    c: Coincident(g11,g12)
    c: Coincident(g12,g7)
    c: Equal(g7, g8-g12) x5
    c: PointOnObject(g7,g13)
    c: PointOnObject(g8,g13)
    c: PointOnObject(g9,g13)
    c: PointOnObject(g10,g13)
    c: PointOnObject(g11,g13)
    c: PointOnObject(g12,g13)
    c: PointOnObject(g13,g-1)
    c: Diameter(g13) = 7
    c: Distance(g6,g13) = 8
    c: Horizontal(g0,g10)
    c: Coincident(g14,g15)
    c: Coincident(g15,g16)
    c: Coincident(g16,g17)
    c: Coincident(g17,g18)
    c: Coincident(g18,g19)
    c: Coincident(g19,g14)
    c: Equal(g14, g15-g19) x5
    c: PointOnObject(g14,g20)
    c: PointOnObject(g15,g20)
    c: PointOnObject(g16,g20)
    c: PointOnObject(g17,g20)
    c: PointOnObject(g18,g20)
    c: PointOnObject(g19,g20)
    c: Diameter(g20) = 7
    c: DistanceY(g-1,g20) = 7
    c: Vertical(g18)
    c: Distance(g17,g-2) = 1
    c: Coincident(g21,g22)
    c: Coincident(g22,g23)
    c: Coincident(g23,g24)
    c: Coincident(g24,g25)
    c: Coincident(g25,g26)
    c: Coincident(g26,g21)
    c: Equal(g21, g22-g26) x5
    c: PointOnObject(g21,g27)
    c: PointOnObject(g22,g27)
    c: PointOnObject(g23,g27)
    c: PointOnObject(g24,g27)
    c: PointOnObject(g25,g27)
    c: PointOnObject(g26,g27)
    c: Diameter(g27) = 7
    c: DistanceY(g-1,g27) = 7
    c: DistanceX(g21,g-1) = 1
    c: Vertical(g21)
    c: Coincident(g28,g29)
    c: Coincident(g29,g30)
    c: Coincident(g30,g31)
    c: Coincident(g31,g32)
    c: Coincident(g32,g33)
    c: Coincident(g33,g28)
    c: Equal(g28, g29-g33) x5
    c: PointOnObject(g28,g34)
    c: PointOnObject(g29,g34)
    c: PointOnObject(g30,g34)
    c: PointOnObject(g31,g34)
    c: PointOnObject(g32,g34)
    c: PointOnObject(g33,g34)
    c: PointOnObject(g34,g-1)
    c: Diameter(g34) = 7
    c: Vertical(g31)
    c: DistanceX(g34,g-1) = 8
    c: Coincident(g35,g36)
    c: Coincident(g36,g37)
    c: Coincident(g37,g38)
    c: Coincident(g38,g39)
    c: Coincident(g39,g40)
    c: Coincident(g40,g35)
    c: Equal(g35, g36-g40) x5
    c: PointOnObject(g35,g41)
    c: PointOnObject(g36,g41)
    c: PointOnObject(g37,g41)
    c: PointOnObject(g38,g41)
    c: PointOnObject(g39,g41)
    c: PointOnObject(g40,g41)
    c: Coincident(g42,g43)
    c: Coincident(g43,g44)
    c: Coincident(g44,g45)
    c: Coincident(g45,g46)
    c: Coincident(g46,g47)
    c: Coincident(g47,g42)
    c: Equal(g42, g43-g47) x5
    c: PointOnObject(g42,g48)
    c: PointOnObject(g43,g48)
    c: PointOnObject(g44,g48)
    c: PointOnObject(g45,g48)
    c: PointOnObject(g46,g48)
    c: PointOnObject(g47,g48)
    c: Equal(g41,g48)
    c: Diameter(g41) = 7
    c: Vertical(g39)
    c: Vertical(g43)
    c: Distance(g-2,g39) = 1
    c: Symmetric(g38,g43,g-2)
    c: Distance(g41,g-1) = 7
FEATURE [Part::Extrusion] Extrude409  label="hex024"
  Base = -> Sketch417
  Dir = (0,-1,2e-16)
  DirMode = 2
  FaceMakerClass = Part::FaceMakerBullseye
  FaceMakerMode = 3
  LengthFwd = 10
  LengthRev = 0
  Placement = pos=(-32,0,28) rot=(0,0,1;0rad)
  Solid = true
  Symmetric = false
FEATURE [Sketcher::SketchObject] Sketch418
  ArcFitTolerance = 1e-06
  FullyConstrained = true
  MakeInternals = false
  Placement = pos=(0,0,0) rot=(1,0,0;1.5708rad)
  sketch-geometry (49):
    g0: LineSegment StartX=1e-16 StartY=3.5 StartZ=0 EndX=-3.03109 EndY=1.75 EndZ=0
    g1: LineSegment StartX=-3.03109 StartY=1.75 StartZ=0 EndX=-3.03109 EndY=-1.75 EndZ=0
    g2: LineSegment StartX=-3.03109 StartY=-1.75 StartZ=0 EndX=-1e-16 EndY=-3.5 EndZ=0
    g3: LineSegment StartX=-1e-16 StartY=-3.5 StartZ=0 EndX=3.03109 EndY=-1.75 EndZ=0
    g4: LineSegment StartX=3.03109 StartY=-1.75 StartZ=0 EndX=3.03109 EndY=1.75 EndZ=0
    g5: LineSegment StartX=3.03109 StartY=1.75 StartZ=0 EndX=1e-16 EndY=3.5 EndZ=0
    g6: Circle [constr] CenterX=0 CenterY=0 CenterZ=0 NormalX=0 NormalY=0 NormalZ=1 AngleXU=0 Radius=3.5
    g7: LineSegment StartX=4.96892 StartY=-1.75002 StartZ=0 EndX=8.00002 EndY=-3.5 EndZ=0
    g8: LineSegment StartX=8.00002 StartY=-3.5 StartZ=0 EndX=11.0311 EndY=-1.74998 EndZ=0
    g9: LineSegment StartX=11.0311 StartY=-1.74998 StartZ=0 EndX=11.0311 EndY=1.75002 EndZ=0
    g10: LineSegment StartX=11.0311 StartY=1.75002 StartZ=0 EndX=7.99998 EndY=3.5 EndZ=0
    g11: LineSegment StartX=7.99998 StartY=3.5 StartZ=0 EndX=4.9689 EndY=1.74998 EndZ=0
    g12: LineSegment StartX=4.9689 StartY=1.74998 StartZ=0 EndX=4.96892 EndY=-1.75002 EndZ=0
    g13: Circle [constr] CenterX=8 CenterY=0 CenterZ=0 NormalX=0 NormalY=0 NormalZ=1 AngleXU=0 Radius=3.5
    g14: LineSegment StartX=4.03109 StartY=3.5 StartZ=0 EndX=7.06218 EndY=5.25 EndZ=0
    g15: LineSegment StartX=7.06218 StartY=5.25 StartZ=0 EndX=7.06218 EndY=8.75 EndZ=0
    g16: LineSegment StartX=7.06218 StartY=8.75 StartZ=0 EndX=4.03109 EndY=10.5 EndZ=0
    g17: LineSegment StartX=4.03109 StartY=10.5 StartZ=0 EndX=1 EndY=8.75 EndZ=0
    g18: LineSegment StartX=1 StartY=8.75 StartZ=0 EndX=1 EndY=5.25 EndZ=0
    g19: LineSegment StartX=1 StartY=5.25 StartZ=0 EndX=4.03109 EndY=3.5 EndZ=0
    g20: Circle [constr] CenterX=4.03109 CenterY=7 CenterZ=0 NormalX=0 NormalY=0 NormalZ=1 AngleXU=0 Radius=3.5
    g21: LineSegment StartX=-1 StartY=5.25 StartZ=0 EndX=-1 EndY=8.75 EndZ=0
    g22: LineSegment StartX=-1 StartY=8.75 StartZ=0 EndX=-4.03109 EndY=10.5 EndZ=0
    g23: LineSegment StartX=-4.03109 StartY=10.5 StartZ=0 EndX=-7.06218 EndY=8.75 EndZ=0
    g24: LineSegment StartX=-7.06218 StartY=8.75 StartZ=0 EndX=-7.06218 EndY=5.25 EndZ=0
    g25: LineSegment StartX=-7.06218 StartY=5.25 StartZ=0 EndX=-4.03109 EndY=3.5 EndZ=0
    g26: LineSegment StartX=-4.03109 StartY=3.5 StartZ=0 EndX=-1 EndY=5.25 EndZ=0
    g27: Circle [constr] CenterX=-4.03109 CenterY=7 CenterZ=0 NormalX=0 NormalY=0 NormalZ=1 AngleXU=0 Radius=3.5
    g28: LineSegment StartX=-4.96891 StartY=-1.75 StartZ=0 EndX=-4.96891 EndY=1.75 EndZ=0
    g29: LineSegment StartX=-4.96891 StartY=1.75 StartZ=0 EndX=-8 EndY=3.5 EndZ=0
    g30: LineSegment StartX=-8 StartY=3.5 StartZ=0 EndX=-11.0311 EndY=1.75 EndZ=0
    g31: LineSegment StartX=-11.0311 StartY=1.75 StartZ=0 EndX=-11.0311 EndY=-1.75 EndZ=0
    g32: LineSegment StartX=-11.0311 StartY=-1.75 StartZ=0 EndX=-8 EndY=-3.5 EndZ=0
    g33: LineSegment StartX=-8 StartY=-3.5 StartZ=0 EndX=-4.96891 EndY=-1.75 EndZ=0
    g34: Circle [constr] CenterX=-8 CenterY=0 CenterZ=0 NormalX=0 NormalY=0 NormalZ=1 AngleXU=0 Radius=3.5
    g35: LineSegment StartX=-4.03109 StartY=-3.5 StartZ=0 EndX=-7.06218 EndY=-5.25 EndZ=0
    g36: LineSegment StartX=-7.06218 StartY=-5.25 StartZ=0 EndX=-7.06218 EndY=-8.75 EndZ=0
    g37: LineSegment StartX=-7.06218 StartY=-8.75 StartZ=0 EndX=-4.03109 EndY=-10.5 EndZ=0
    g38: LineSegment StartX=-4.03109 StartY=-10.5 StartZ=0 EndX=-1 EndY=-8.75 EndZ=0
    g39: LineSegment StartX=-1 StartY=-8.75 StartZ=0 EndX=-1 EndY=-5.25 EndZ=0
    g40: LineSegment StartX=-1 StartY=-5.25 StartZ=0 EndX=-4.03109 EndY=-3.5 EndZ=0
    g41: Circle [constr] CenterX=-4.03109 CenterY=-7 CenterZ=0 NormalX=0 NormalY=0 NormalZ=1 AngleXU=0 Radius=3.5
    g42: LineSegment StartX=4.03109 StartY=-3.5 StartZ=0 EndX=1 EndY=-5.25 EndZ=0
    g43: LineSegment StartX=1 StartY=-5.25 StartZ=0 EndX=1 EndY=-8.75 EndZ=0
    g44: LineSegment StartX=1 StartY=-8.75 StartZ=0 EndX=4.03109 EndY=-10.5 EndZ=0
    g45: LineSegment StartX=4.03109 StartY=-10.5 StartZ=0 EndX=7.06218 EndY=-8.75 EndZ=0
    g46: LineSegment StartX=7.06218 StartY=-8.75 StartZ=0 EndX=7.06218 EndY=-5.25 EndZ=0
    g47: LineSegment StartX=7.06218 StartY=-5.25 StartZ=0 EndX=4.03109 EndY=-3.5 EndZ=0
    g48: Circle [constr] CenterX=4.03109 CenterY=-7 CenterZ=0 NormalX=0 NormalY=0 NormalZ=1 AngleXU=0 Radius=3.5
  constraints (117):
    c: Coincident(g0,g1)
    c: Coincident(g1,g2)
    c: Coincident(g2,g3)
    c: Coincident(g3,g4)
    c: Coincident(g4,g5)
    c: Coincident(g5,g0)
    c: Equal(g0, g1-g5) x5
    c: PointOnObject(g0,g6)
    c: PointOnObject(g1,g6)
    c: PointOnObject(g2,g6)
    c: PointOnObject(g3,g6)
    c: PointOnObject(g4,g6)
    c: PointOnObject(g5,g6)
    c: Coincident(g6,g-1)
    c: Diameter(g6) = 7
    c: PointOnObject(g0,g-2)
    c: Coincident(g7,g8)
    c: Coincident(g8,g9)
    c: Coincident(g9,g10)
    c: Coincident(g10,g11)
    c: Coincident(g11,g12)
    c: Coincident(g12,g7)
    c: Equal(g7, g8-g12) x5
    c: PointOnObject(g7,g13)
    c: PointOnObject(g8,g13)
    c: PointOnObject(g9,g13)
    c: PointOnObject(g10,g13)
    c: PointOnObject(g11,g13)
    c: PointOnObject(g12,g13)
    c: PointOnObject(g13,g-1)
    c: Diameter(g13) = 7
    c: Distance(g6,g13) = 8
    c: Horizontal(g0,g10)
    c: Coincident(g14,g15)
    c: Coincident(g15,g16)
    c: Coincident(g16,g17)
    c: Coincident(g17,g18)
    c: Coincident(g18,g19)
    c: Coincident(g19,g14)
    c: Equal(g14, g15-g19) x5
    c: PointOnObject(g14,g20)
    c: PointOnObject(g15,g20)
    c: PointOnObject(g16,g20)
    c: PointOnObject(g17,g20)
    c: PointOnObject(g18,g20)
    c: PointOnObject(g19,g20)
    c: Diameter(g20) = 7
    c: DistanceY(g-1,g20) = 7
    c: Vertical(g18)
    c: Distance(g17,g-2) = 1
    c: Coincident(g21,g22)
    c: Coincident(g22,g23)
    c: Coincident(g23,g24)
    c: Coincident(g24,g25)
    c: Coincident(g25,g26)
    c: Coincident(g26,g21)
    c: Equal(g21, g22-g26) x5
    c: PointOnObject(g21,g27)
    c: PointOnObject(g22,g27)
    c: PointOnObject(g23,g27)
    c: PointOnObject(g24,g27)
    c: PointOnObject(g25,g27)
    c: PointOnObject(g26,g27)
    c: Diameter(g27) = 7
    c: DistanceY(g-1,g27) = 7
    c: DistanceX(g21,g-1) = 1
    c: Vertical(g21)
    c: Coincident(g28,g29)
    c: Coincident(g29,g30)
    c: Coincident(g30,g31)
    c: Coincident(g31,g32)
    c: Coincident(g32,g33)
    c: Coincident(g33,g28)
    c: Equal(g28, g29-g33) x5
    c: PointOnObject(g28,g34)
    c: PointOnObject(g29,g34)
    c: PointOnObject(g30,g34)
    c: PointOnObject(g31,g34)
    c: PointOnObject(g32,g34)
    c: PointOnObject(g33,g34)
    c: PointOnObject(g34,g-1)
    c: Diameter(g34) = 7
    c: Vertical(g31)
    c: DistanceX(g34,g-1) = 8
    c: Coincident(g35,g36)
    c: Coincident(g36,g37)
    c: Coincident(g37,g38)
    c: Coincident(g38,g39)
    c: Coincident(g39,g40)
    c: Coincident(g40,g35)
    c: Equal(g35, g36-g40) x5
    c: PointOnObject(g35,g41)
    c: PointOnObject(g36,g41)
    c: PointOnObject(g37,g41)
    c: PointOnObject(g38,g41)
    c: PointOnObject(g39,g41)
    c: PointOnObject(g40,g41)
    c: Coincident(g42,g43)
    c: Coincident(g43,g44)
    c: Coincident(g44,g45)
    c: Coincident(g45,g46)
    c: Coincident(g46,g47)
    c: Coincident(g47,g42)
    c: Equal(g42, g43-g47) x5
    c: PointOnObject(g42,g48)
    c: PointOnObject(g43,g48)
    c: PointOnObject(g44,g48)
    c: PointOnObject(g45,g48)
    c: PointOnObject(g46,g48)
    c: PointOnObject(g47,g48)
    c: Equal(g41,g48)
    c: Diameter(g41) = 7
    c: Vertical(g39)
    c: Vertical(g43)
    c: Distance(g-2,g39) = 1
    c: Symmetric(g38,g43,g-2)
    c: Distance(g41,g-1) = 7
FEATURE [Part::Extrusion] Extrude410  label="hex025"
  Base = -> Sketch418
  Dir = (0,-1,2e-16)
  DirMode = 2
  FaceMakerClass = Part::FaceMakerBullseye
  FaceMakerMode = 3
  LengthFwd = 10
  LengthRev = 0
  Placement = pos=(-12,0,35) rot=(0,0,1;0rad)
  Solid = true
  Symmetric = false
FEATURE [Sketcher::SketchObject] Sketch419
  ArcFitTolerance = 1e-06
  FullyConstrained = true
  MakeInternals = false
  Placement = pos=(0,0,0) rot=(1,0,0;1.5708rad)
  sketch-geometry (49):
    g0: LineSegment StartX=1e-16 StartY=3.5 StartZ=0 EndX=-3.03109 EndY=1.75 EndZ=0
    g1: LineSegment StartX=-3.03109 StartY=1.75 StartZ=0 EndX=-3.03109 EndY=-1.75 EndZ=0
    g2: LineSegment StartX=-3.03109 StartY=-1.75 StartZ=0 EndX=-1e-16 EndY=-3.5 EndZ=0
    g3: LineSegment StartX=-1e-16 StartY=-3.5 StartZ=0 EndX=3.03109 EndY=-1.75 EndZ=0
    g4: LineSegment StartX=3.03109 StartY=-1.75 StartZ=0 EndX=3.03109 EndY=1.75 EndZ=0
    g5: LineSegment StartX=3.03109 StartY=1.75 StartZ=0 EndX=1e-16 EndY=3.5 EndZ=0
    g6: Circle [constr] CenterX=0 CenterY=0 CenterZ=0 NormalX=0 NormalY=0 NormalZ=1 AngleXU=0 Radius=3.5
    g7: LineSegment StartX=4.96892 StartY=-1.75002 StartZ=0 EndX=8.00002 EndY=-3.5 EndZ=0
    g8: LineSegment StartX=8.00002 StartY=-3.5 StartZ=0 EndX=11.0311 EndY=-1.74998 EndZ=0
    g9: LineSegment StartX=11.0311 StartY=-1.74998 StartZ=0 EndX=11.0311 EndY=1.75002 EndZ=0
    g10: LineSegment StartX=11.0311 StartY=1.75002 StartZ=0 EndX=7.99998 EndY=3.5 EndZ=0
    g11: LineSegment StartX=7.99998 StartY=3.5 StartZ=0 EndX=4.9689 EndY=1.74998 EndZ=0
    g12: LineSegment StartX=4.9689 StartY=1.74998 StartZ=0 EndX=4.96892 EndY=-1.75002 EndZ=0
    g13: Circle [constr] CenterX=8 CenterY=0 CenterZ=0 NormalX=0 NormalY=0 NormalZ=1 AngleXU=0 Radius=3.5
    g14: LineSegment StartX=4.03109 StartY=3.5 StartZ=0 EndX=7.06218 EndY=5.25 EndZ=0
    g15: LineSegment StartX=7.06218 StartY=5.25 StartZ=0 EndX=7.06218 EndY=8.75 EndZ=0
    g16: LineSegment StartX=7.06218 StartY=8.75 StartZ=0 EndX=4.03109 EndY=10.5 EndZ=0
    g17: LineSegment StartX=4.03109 StartY=10.5 StartZ=0 EndX=1 EndY=8.75 EndZ=0
    g18: LineSegment StartX=1 StartY=8.75 StartZ=0 EndX=1 EndY=5.25 EndZ=0
    g19: LineSegment StartX=1 StartY=5.25 StartZ=0 EndX=4.03109 EndY=3.5 EndZ=0
    g20: Circle [constr] CenterX=4.03109 CenterY=7 CenterZ=0 NormalX=0 NormalY=0 NormalZ=1 AngleXU=0 Radius=3.5
    g21: LineSegment StartX=-1 StartY=5.25 StartZ=0 EndX=-1 EndY=8.75 EndZ=0
    g22: LineSegment StartX=-1 StartY=8.75 StartZ=0 EndX=-4.03109 EndY=10.5 EndZ=0
    g23: LineSegment StartX=-4.03109 StartY=10.5 StartZ=0 EndX=-7.06218 EndY=8.75 EndZ=0
    g24: LineSegment StartX=-7.06218 StartY=8.75 StartZ=0 EndX=-7.06218 EndY=5.25 EndZ=0
    g25: LineSegment StartX=-7.06218 StartY=5.25 StartZ=0 EndX=-4.03109 EndY=3.5 EndZ=0
    g26: LineSegment StartX=-4.03109 StartY=3.5 StartZ=0 EndX=-1 EndY=5.25 EndZ=0
    g27: Circle [constr] CenterX=-4.03109 CenterY=7 CenterZ=0 NormalX=0 NormalY=0 NormalZ=1 AngleXU=0 Radius=3.5
    g28: LineSegment StartX=-4.96891 StartY=-1.75 StartZ=0 EndX=-4.96891 EndY=1.75 EndZ=0
    g29: LineSegment StartX=-4.96891 StartY=1.75 StartZ=0 EndX=-8 EndY=3.5 EndZ=0
    g30: LineSegment StartX=-8 StartY=3.5 StartZ=0 EndX=-11.0311 EndY=1.75 EndZ=0
    g31: LineSegment StartX=-11.0311 StartY=1.75 StartZ=0 EndX=-11.0311 EndY=-1.75 EndZ=0
    g32: LineSegment StartX=-11.0311 StartY=-1.75 StartZ=0 EndX=-8 EndY=-3.5 EndZ=0
    g33: LineSegment StartX=-8 StartY=-3.5 StartZ=0 EndX=-4.96891 EndY=-1.75 EndZ=0
    g34: Circle [constr] CenterX=-8 CenterY=0 CenterZ=0 NormalX=0 NormalY=0 NormalZ=1 AngleXU=0 Radius=3.5
    g35: LineSegment StartX=-4.03109 StartY=-3.5 StartZ=0 EndX=-7.06218 EndY=-5.25 EndZ=0
    g36: LineSegment StartX=-7.06218 StartY=-5.25 StartZ=0 EndX=-7.06218 EndY=-8.75 EndZ=0
    g37: LineSegment StartX=-7.06218 StartY=-8.75 StartZ=0 EndX=-4.03109 EndY=-10.5 EndZ=0
    g38: LineSegment StartX=-4.03109 StartY=-10.5 StartZ=0 EndX=-1 EndY=-8.75 EndZ=0
    g39: LineSegment StartX=-1 StartY=-8.75 StartZ=0 EndX=-1 EndY=-5.25 EndZ=0
    g40: LineSegment StartX=-1 StartY=-5.25 StartZ=0 EndX=-4.03109 EndY=-3.5 EndZ=0
    g41: Circle [constr] CenterX=-4.03109 CenterY=-7 CenterZ=0 NormalX=0 NormalY=0 NormalZ=1 AngleXU=0 Radius=3.5
    g42: LineSegment StartX=4.03109 StartY=-3.5 StartZ=0 EndX=1 EndY=-5.25 EndZ=0
    g43: LineSegment StartX=1 StartY=-5.25 StartZ=0 EndX=1 EndY=-8.75 EndZ=0
    g44: LineSegment StartX=1 StartY=-8.75 StartZ=0 EndX=4.03109 EndY=-10.5 EndZ=0
    g45: LineSegment StartX=4.03109 StartY=-10.5 StartZ=0 EndX=7.06218 EndY=-8.75 EndZ=0
    g46: LineSegment StartX=7.06218 StartY=-8.75 StartZ=0 EndX=7.06218 EndY=-5.25 EndZ=0
    g47: LineSegment StartX=7.06218 StartY=-5.25 StartZ=0 EndX=4.03109 EndY=-3.5 EndZ=0
    g48: Circle [constr] CenterX=4.03109 CenterY=-7 CenterZ=0 NormalX=0 NormalY=0 NormalZ=1 AngleXU=0 Radius=3.5
  constraints (117):
    c: Coincident(g0,g1)
    c: Coincident(g1,g2)
    c: Coincident(g2,g3)
    c: Coincident(g3,g4)
    c: Coincident(g4,g5)
    c: Coincident(g5,g0)
    c: Equal(g0, g1-g5) x5
    c: PointOnObject(g0,g6)
    c: PointOnObject(g1,g6)
    c: PointOnObject(g2,g6)
    c: PointOnObject(g3,g6)
    c: PointOnObject(g4,g6)
    c: PointOnObject(g5,g6)
    c: Coincident(g6,g-1)
    c: Diameter(g6) = 7
    c: PointOnObject(g0,g-2)
    c: Coincident(g7,g8)
    c: Coincident(g8,g9)
    c: Coincident(g9,g10)
    c: Coincident(g10,g11)
    c: Coincident(g11,g12)
    c: Coincident(g12,g7)
    c: Equal(g7, g8-g12) x5
    c: PointOnObject(g7,g13)
    c: PointOnObject(g8,g13)
    c: PointOnObject(g9,g13)
    c: PointOnObject(g10,g13)
    c: PointOnObject(g11,g13)
    c: PointOnObject(g12,g13)
    c: PointOnObject(g13,g-1)
    c: Diameter(g13) = 7
    c: Distance(g6,g13) = 8
    c: Horizontal(g0,g10)
    c: Coincident(g14,g15)
    c: Coincident(g15,g16)
    c: Coincident(g16,g17)
    c: Coincident(g17,g18)
    c: Coincident(g18,g19)
    c: Coincident(g19,g14)
    c: Equal(g14, g15-g19) x5
    c: PointOnObject(g14,g20)
    c: PointOnObject(g15,g20)
    c: PointOnObject(g16,g20)
    c: PointOnObject(g17,g20)
    c: PointOnObject(g18,g20)
    c: PointOnObject(g19,g20)
    c: Diameter(g20) = 7
    c: DistanceY(g-1,g20) = 7
    c: Vertical(g18)
    c: Distance(g17,g-2) = 1
    c: Coincident(g21,g22)
    c: Coincident(g22,g23)
    c: Coincident(g23,g24)
    c: Coincident(g24,g25)
    c: Coincident(g25,g26)
    c: Coincident(g26,g21)
    c: Equal(g21, g22-g26) x5
    c: PointOnObject(g21,g27)
    c: PointOnObject(g22,g27)
    c: PointOnObject(g23,g27)
    c: PointOnObject(g24,g27)
    c: PointOnObject(g25,g27)
    c: PointOnObject(g26,g27)
    c: Diameter(g27) = 7
    c: DistanceY(g-1,g27) = 7
    c: DistanceX(g21,g-1) = 1
    c: Vertical(g21)
    c: Coincident(g28,g29)
    c: Coincident(g29,g30)
    c: Coincident(g30,g31)
    c: Coincident(g31,g32)
    c: Coincident(g32,g33)
    c: Coincident(g33,g28)
    c: Equal(g28, g29-g33) x5
    c: PointOnObject(g28,g34)
    c: PointOnObject(g29,g34)
    c: PointOnObject(g30,g34)
    c: PointOnObject(g31,g34)
    c: PointOnObject(g32,g34)
    c: PointOnObject(g33,g34)
    c: PointOnObject(g34,g-1)
    c: Diameter(g34) = 7
    c: Vertical(g31)
    c: DistanceX(g34,g-1) = 8
    c: Coincident(g35,g36)
    c: Coincident(g36,g37)
    c: Coincident(g37,g38)
    c: Coincident(g38,g39)
    c: Coincident(g39,g40)
    c: Coincident(g40,g35)
    c: Equal(g35, g36-g40) x5
    c: PointOnObject(g35,g41)
    c: PointOnObject(g36,g41)
    c: PointOnObject(g37,g41)
    c: PointOnObject(g38,g41)
    c: PointOnObject(g39,g41)
    c: PointOnObject(g40,g41)
    c: Coincident(g42,g43)
    c: Coincident(g43,g44)
    c: Coincident(g44,g45)
    c: Coincident(g45,g46)
    c: Coincident(g46,g47)
    c: Coincident(g47,g42)
    c: Equal(g42, g43-g47) x5
    c: PointOnObject(g42,g48)
    c: PointOnObject(g43,g48)
    c: PointOnObject(g44,g48)
    c: PointOnObject(g45,g48)
    c: PointOnObject(g46,g48)
    c: PointOnObject(g47,g48)
    c: Equal(g41,g48)
    c: Diameter(g41) = 7
    c: Vertical(g39)
    c: Vertical(g43)
    c: Distance(g-2,g39) = 1
    c: Symmetric(g38,g43,g-2)
    c: Distance(g41,g-1) = 7
FEATURE [Part::Extrusion] Extrude411  label="hex026"
  Base = -> Sketch419
  Dir = (0,-1,2e-16)
  DirMode = 2
  FaceMakerClass = Part::FaceMakerBullseye
  FaceMakerMode = 3
  LengthFwd = 10
  LengthRev = 0
  Placement = pos=(-80,0,0) rot=(0,0,1;0rad)
  Solid = true
  Symmetric = false
FEATURE [Sketcher::SketchObject] Sketch420
  ArcFitTolerance = 1e-06
  FullyConstrained = true
  MakeInternals = false
  Placement = pos=(0,0,0) rot=(1,0,0;1.5708rad)
  sketch-geometry (49):
    g0: LineSegment StartX=1e-16 StartY=3.5 StartZ=0 EndX=-3.03109 EndY=1.75 EndZ=0
    g1: LineSegment StartX=-3.03109 StartY=1.75 StartZ=0 EndX=-3.03109 EndY=-1.75 EndZ=0
    g2: LineSegment StartX=-3.03109 StartY=-1.75 StartZ=0 EndX=-1e-16 EndY=-3.5 EndZ=0
    g3: LineSegment StartX=-1e-16 StartY=-3.5 StartZ=0 EndX=3.03109 EndY=-1.75 EndZ=0
    g4: LineSegment StartX=3.03109 StartY=-1.75 StartZ=0 EndX=3.03109 EndY=1.75 EndZ=0
    g5: LineSegment StartX=3.03109 StartY=1.75 StartZ=0 EndX=1e-16 EndY=3.5 EndZ=0
    g6: Circle [constr] CenterX=0 CenterY=0 CenterZ=0 NormalX=0 NormalY=0 NormalZ=1 AngleXU=0 Radius=3.5
    g7: LineSegment StartX=4.96892 StartY=-1.75002 StartZ=0 EndX=8.00002 EndY=-3.5 EndZ=0
    g8: LineSegment StartX=8.00002 StartY=-3.5 StartZ=0 EndX=11.0311 EndY=-1.74998 EndZ=0
    g9: LineSegment StartX=11.0311 StartY=-1.74998 StartZ=0 EndX=11.0311 EndY=1.75002 EndZ=0
    g10: LineSegment StartX=11.0311 StartY=1.75002 StartZ=0 EndX=7.99998 EndY=3.5 EndZ=0
    g11: LineSegment StartX=7.99998 StartY=3.5 StartZ=0 EndX=4.9689 EndY=1.74998 EndZ=0
    g12: LineSegment StartX=4.9689 StartY=1.74998 StartZ=0 EndX=4.96892 EndY=-1.75002 EndZ=0
    g13: Circle [constr] CenterX=8 CenterY=0 CenterZ=0 NormalX=0 NormalY=0 NormalZ=1 AngleXU=0 Radius=3.5
    g14: LineSegment StartX=4.03109 StartY=3.5 StartZ=0 EndX=7.06218 EndY=5.25 EndZ=0
    g15: LineSegment StartX=7.06218 StartY=5.25 StartZ=0 EndX=7.06218 EndY=8.75 EndZ=0
    g16: LineSegment StartX=7.06218 StartY=8.75 StartZ=0 EndX=4.03109 EndY=10.5 EndZ=0
    g17: LineSegment StartX=4.03109 StartY=10.5 StartZ=0 EndX=1 EndY=8.75 EndZ=0
    g18: LineSegment StartX=1 StartY=8.75 StartZ=0 EndX=1 EndY=5.25 EndZ=0
    g19: LineSegment StartX=1 StartY=5.25 StartZ=0 EndX=4.03109 EndY=3.5 EndZ=0
    g20: Circle [constr] CenterX=4.03109 CenterY=7 CenterZ=0 NormalX=0 NormalY=0 NormalZ=1 AngleXU=0 Radius=3.5
    g21: LineSegment StartX=-1 StartY=5.25 StartZ=0 EndX=-1 EndY=8.75 EndZ=0
    g22: LineSegment StartX=-1 StartY=8.75 StartZ=0 EndX=-4.03109 EndY=10.5 EndZ=0
    g23: LineSegment StartX=-4.03109 StartY=10.5 StartZ=0 EndX=-7.06218 EndY=8.75 EndZ=0
    g24: LineSegment StartX=-7.06218 StartY=8.75 StartZ=0 EndX=-7.06218 EndY=5.25 EndZ=0
    g25: LineSegment StartX=-7.06218 StartY=5.25 StartZ=0 EndX=-4.03109 EndY=3.5 EndZ=0
    g26: LineSegment StartX=-4.03109 StartY=3.5 StartZ=0 EndX=-1 EndY=5.25 EndZ=0
    g27: Circle [constr] CenterX=-4.03109 CenterY=7 CenterZ=0 NormalX=0 NormalY=0 NormalZ=1 AngleXU=0 Radius=3.5
    g28: LineSegment StartX=-4.96891 StartY=-1.75 StartZ=0 EndX=-4.96891 EndY=1.75 EndZ=0
    g29: LineSegment StartX=-4.96891 StartY=1.75 StartZ=0 EndX=-8 EndY=3.5 EndZ=0
    g30: LineSegment StartX=-8 StartY=3.5 StartZ=0 EndX=-11.0311 EndY=1.75 EndZ=0
    g31: LineSegment StartX=-11.0311 StartY=1.75 StartZ=0 EndX=-11.0311 EndY=-1.75 EndZ=0
    g32: LineSegment StartX=-11.0311 StartY=-1.75 StartZ=0 EndX=-8 EndY=-3.5 EndZ=0
    g33: LineSegment StartX=-8 StartY=-3.5 StartZ=0 EndX=-4.96891 EndY=-1.75 EndZ=0
    g34: Circle [constr] CenterX=-8 CenterY=0 CenterZ=0 NormalX=0 NormalY=0 NormalZ=1 AngleXU=0 Radius=3.5
    g35: LineSegment StartX=-4.03109 StartY=-3.5 StartZ=0 EndX=-7.06218 EndY=-5.25 EndZ=0
    g36: LineSegment StartX=-7.06218 StartY=-5.25 StartZ=0 EndX=-7.06218 EndY=-8.75 EndZ=0
    g37: LineSegment StartX=-7.06218 StartY=-8.75 StartZ=0 EndX=-4.03109 EndY=-10.5 EndZ=0
    g38: LineSegment StartX=-4.03109 StartY=-10.5 StartZ=0 EndX=-1 EndY=-8.75 EndZ=0
    g39: LineSegment StartX=-1 StartY=-8.75 StartZ=0 EndX=-1 EndY=-5.25 EndZ=0
    g40: LineSegment StartX=-1 StartY=-5.25 StartZ=0 EndX=-4.03109 EndY=-3.5 EndZ=0
    g41: Circle [constr] CenterX=-4.03109 CenterY=-7 CenterZ=0 NormalX=0 NormalY=0 NormalZ=1 AngleXU=0 Radius=3.5
    g42: LineSegment StartX=4.03109 StartY=-3.5 StartZ=0 EndX=1 EndY=-5.25 EndZ=0
    g43: LineSegment StartX=1 StartY=-5.25 StartZ=0 EndX=1 EndY=-8.75 EndZ=0
    g44: LineSegment StartX=1 StartY=-8.75 StartZ=0 EndX=4.03109 EndY=-10.5 EndZ=0
    g45: LineSegment StartX=4.03109 StartY=-10.5 StartZ=0 EndX=7.06218 EndY=-8.75 EndZ=0
    g46: LineSegment StartX=7.06218 StartY=-8.75 StartZ=0 EndX=7.06218 EndY=-5.25 EndZ=0
    g47: LineSegment StartX=7.06218 StartY=-5.25 StartZ=0 EndX=4.03109 EndY=-3.5 EndZ=0
    g48: Circle [constr] CenterX=4.03109 CenterY=-7 CenterZ=0 NormalX=0 NormalY=0 NormalZ=1 AngleXU=0 Radius=3.5
  constraints (117):
    c: Coincident(g0,g1)
    c: Coincident(g1,g2)
    c: Coincident(g2,g3)
    c: Coincident(g3,g4)
    c: Coincident(g4,g5)
    c: Coincident(g5,g0)
    c: Equal(g0, g1-g5) x5
    c: PointOnObject(g0,g6)
    c: PointOnObject(g1,g6)
    c: PointOnObject(g2,g6)
    c: PointOnObject(g3,g6)
    c: PointOnObject(g4,g6)
    c: PointOnObject(g5,g6)
    c: Coincident(g6,g-1)
    c: Diameter(g6) = 7
    c: PointOnObject(g0,g-2)
    c: Coincident(g7,g8)
    c: Coincident(g8,g9)
    c: Coincident(g9,g10)
    c: Coincident(g10,g11)
    c: Coincident(g11,g12)
    c: Coincident(g12,g7)
    c: Equal(g7, g8-g12) x5
    c: PointOnObject(g7,g13)
    c: PointOnObject(g8,g13)
    c: PointOnObject(g9,g13)
    c: PointOnObject(g10,g13)
    c: PointOnObject(g11,g13)
    c: PointOnObject(g12,g13)
    c: PointOnObject(g13,g-1)
    c: Diameter(g13) = 7
    c: Distance(g6,g13) = 8
    c: Horizontal(g0,g10)
    c: Coincident(g14,g15)
    c: Coincident(g15,g16)
    c: Coincident(g16,g17)
    c: Coincident(g17,g18)
    c: Coincident(g18,g19)
    c: Coincident(g19,g14)
    c: Equal(g14, g15-g19) x5
    c: PointOnObject(g14,g20)
    c: PointOnObject(g15,g20)
    c: PointOnObject(g16,g20)
    c: PointOnObject(g17,g20)
    c: PointOnObject(g18,g20)
    c: PointOnObject(g19,g20)
    c: Diameter(g20) = 7
    c: DistanceY(g-1,g20) = 7
    c: Vertical(g18)
    c: Distance(g17,g-2) = 1
    c: Coincident(g21,g22)
    c: Coincident(g22,g23)
    c: Coincident(g23,g24)
    c: Coincident(g24,g25)
    c: Coincident(g25,g26)
    c: Coincident(g26,g21)
    c: Equal(g21, g22-g26) x5
    c: PointOnObject(g21,g27)
    c: PointOnObject(g22,g27)
    c: PointOnObject(g23,g27)
    c: PointOnObject(g24,g27)
    c: PointOnObject(g25,g27)
    c: PointOnObject(g26,g27)
    c: Diameter(g27) = 7
    c: DistanceY(g-1,g27) = 7
    c: DistanceX(g21,g-1) = 1
    c: Vertical(g21)
    c: Coincident(g28,g29)
    c: Coincident(g29,g30)
    c: Coincident(g30,g31)
    c: Coincident(g31,g32)
    c: Coincident(g32,g33)
    c: Coincident(g33,g28)
    c: Equal(g28, g29-g33) x5
    c: PointOnObject(g28,g34)
    c: PointOnObject(g29,g34)
    c: PointOnObject(g30,g34)
    c: PointOnObject(g31,g34)
    c: PointOnObject(g32,g34)
    c: PointOnObject(g33,g34)
    c: PointOnObject(g34,g-1)
    c: Diameter(g34) = 7
    c: Vertical(g31)
    c: DistanceX(g34,g-1) = 8
    c: Coincident(g35,g36)
    c: Coincident(g36,g37)
    c: Coincident(g37,g38)
    c: Coincident(g38,g39)
    c: Coincident(g39,g40)
    c: Coincident(g40,g35)
    c: Equal(g35, g36-g40) x5
    c: PointOnObject(g35,g41)
    c: PointOnObject(g36,g41)
    c: PointOnObject(g37,g41)
    c: PointOnObject(g38,g41)
    c: PointOnObject(g39,g41)
    c: PointOnObject(g40,g41)
    c: Coincident(g42,g43)
    c: Coincident(g43,g44)
    c: Coincident(g44,g45)
    c: Coincident(g45,g46)
    c: Coincident(g46,g47)
    c: Coincident(g47,g42)
    c: Equal(g42, g43-g47) x5
    c: PointOnObject(g42,g48)
    c: PointOnObject(g43,g48)
    c: PointOnObject(g44,g48)
    c: PointOnObject(g45,g48)
    c: PointOnObject(g46,g48)
    c: PointOnObject(g47,g48)
    c: Equal(g41,g48)
    c: Diameter(g41) = 7
    c: Vertical(g39)
    c: Vertical(g43)
    c: Distance(g-2,g39) = 1
    c: Symmetric(g38,g43,g-2)
    c: Distance(g41,g-1) = 7
FEATURE [Part::Extrusion] Extrude412  label="hex027"
  Base = -> Sketch420
  Dir = (0,-1,2e-16)
  DirMode = 2
  FaceMakerClass = Part::FaceMakerBullseye
  FaceMakerMode = 3
  LengthFwd = 10
  LengthRev = 0
  Placement = pos=(-104,0,0) rot=(0,0,1;0rad)
  Solid = true
  Symmetric = false
FEATURE [Sketcher::SketchObject] Sketch421
  ArcFitTolerance = 1e-06
  FullyConstrained = true
  MakeInternals = false
  Placement = pos=(0,0,0) rot=(1,0,0;1.5708rad)
  sketch-geometry (49):
    g0: LineSegment StartX=1e-16 StartY=3.5 StartZ=0 EndX=-3.03109 EndY=1.75 EndZ=0
    g1: LineSegment StartX=-3.03109 StartY=1.75 StartZ=0 EndX=-3.03109 EndY=-1.75 EndZ=0
    g2: LineSegment StartX=-3.03109 StartY=-1.75 StartZ=0 EndX=-1e-16 EndY=-3.5 EndZ=0
    g3: LineSegment StartX=-1e-16 StartY=-3.5 StartZ=0 EndX=3.03109 EndY=-1.75 EndZ=0
    g4: LineSegment StartX=3.03109 StartY=-1.75 StartZ=0 EndX=3.03109 EndY=1.75 EndZ=0
    g5: LineSegment StartX=3.03109 StartY=1.75 StartZ=0 EndX=1e-16 EndY=3.5 EndZ=0
    g6: Circle [constr] CenterX=0 CenterY=0 CenterZ=0 NormalX=0 NormalY=0 NormalZ=1 AngleXU=0 Radius=3.5
    g7: LineSegment StartX=4.96892 StartY=-1.75002 StartZ=0 EndX=8.00002 EndY=-3.5 EndZ=0
    g8: LineSegment StartX=8.00002 StartY=-3.5 StartZ=0 EndX=11.0311 EndY=-1.74998 EndZ=0
    g9: LineSegment StartX=11.0311 StartY=-1.74998 StartZ=0 EndX=11.0311 EndY=1.75002 EndZ=0
    g10: LineSegment StartX=11.0311 StartY=1.75002 StartZ=0 EndX=7.99998 EndY=3.5 EndZ=0
    g11: LineSegment StartX=7.99998 StartY=3.5 StartZ=0 EndX=4.9689 EndY=1.74998 EndZ=0
    g12: LineSegment StartX=4.9689 StartY=1.74998 StartZ=0 EndX=4.96892 EndY=-1.75002 EndZ=0
    g13: Circle [constr] CenterX=8 CenterY=0 CenterZ=0 NormalX=0 NormalY=0 NormalZ=1 AngleXU=0 Radius=3.5
    g14: LineSegment StartX=4.03109 StartY=3.5 StartZ=0 EndX=7.06218 EndY=5.25 EndZ=0
    g15: LineSegment StartX=7.06218 StartY=5.25 StartZ=0 EndX=7.06218 EndY=8.75 EndZ=0
    g16: LineSegment StartX=7.06218 StartY=8.75 StartZ=0 EndX=4.03109 EndY=10.5 EndZ=0
    g17: LineSegment StartX=4.03109 StartY=10.5 StartZ=0 EndX=1 EndY=8.75 EndZ=0
    g18: LineSegment StartX=1 StartY=8.75 StartZ=0 EndX=1 EndY=5.25 EndZ=0
    g19: LineSegment StartX=1 StartY=5.25 StartZ=0 EndX=4.03109 EndY=3.5 EndZ=0
    g20: Circle [constr] CenterX=4.03109 CenterY=7 CenterZ=0 NormalX=0 NormalY=0 NormalZ=1 AngleXU=0 Radius=3.5
    g21: LineSegment StartX=-1 StartY=5.25 StartZ=0 EndX=-1 EndY=8.75 EndZ=0
    g22: LineSegment StartX=-1 StartY=8.75 StartZ=0 EndX=-4.03109 EndY=10.5 EndZ=0
    g23: LineSegment StartX=-4.03109 StartY=10.5 StartZ=0 EndX=-7.06218 EndY=8.75 EndZ=0
    g24: LineSegment StartX=-7.06218 StartY=8.75 StartZ=0 EndX=-7.06218 EndY=5.25 EndZ=0
    g25: LineSegment StartX=-7.06218 StartY=5.25 StartZ=0 EndX=-4.03109 EndY=3.5 EndZ=0
    g26: LineSegment StartX=-4.03109 StartY=3.5 StartZ=0 EndX=-1 EndY=5.25 EndZ=0
    g27: Circle [constr] CenterX=-4.03109 CenterY=7 CenterZ=0 NormalX=0 NormalY=0 NormalZ=1 AngleXU=0 Radius=3.5
    g28: LineSegment StartX=-4.96891 StartY=-1.75 StartZ=0 EndX=-4.96891 EndY=1.75 EndZ=0
    g29: LineSegment StartX=-4.96891 StartY=1.75 StartZ=0 EndX=-8 EndY=3.5 EndZ=0
    g30: LineSegment StartX=-8 StartY=3.5 StartZ=0 EndX=-11.0311 EndY=1.75 EndZ=0
    g31: LineSegment StartX=-11.0311 StartY=1.75 StartZ=0 EndX=-11.0311 EndY=-1.75 EndZ=0
    g32: LineSegment StartX=-11.0311 StartY=-1.75 StartZ=0 EndX=-8 EndY=-3.5 EndZ=0
    g33: LineSegment StartX=-8 StartY=-3.5 StartZ=0 EndX=-4.96891 EndY=-1.75 EndZ=0
    g34: Circle [constr] CenterX=-8 CenterY=0 CenterZ=0 NormalX=0 NormalY=0 NormalZ=1 AngleXU=0 Radius=3.5
    g35: LineSegment StartX=-4.03109 StartY=-3.5 StartZ=0 EndX=-7.06218 EndY=-5.25 EndZ=0
    g36: LineSegment StartX=-7.06218 StartY=-5.25 StartZ=0 EndX=-7.06218 EndY=-8.75 EndZ=0
    g37: LineSegment StartX=-7.06218 StartY=-8.75 StartZ=0 EndX=-4.03109 EndY=-10.5 EndZ=0
    g38: LineSegment StartX=-4.03109 StartY=-10.5 StartZ=0 EndX=-1 EndY=-8.75 EndZ=0
    g39: LineSegment StartX=-1 StartY=-8.75 StartZ=0 EndX=-1 EndY=-5.25 EndZ=0
    g40: LineSegment StartX=-1 StartY=-5.25 StartZ=0 EndX=-4.03109 EndY=-3.5 EndZ=0
    g41: Circle [constr] CenterX=-4.03109 CenterY=-7 CenterZ=0 NormalX=0 NormalY=0 NormalZ=1 AngleXU=0 Radius=3.5
    g42: LineSegment StartX=4.03109 StartY=-3.5 StartZ=0 EndX=1 EndY=-5.25 EndZ=0
    g43: LineSegment StartX=1 StartY=-5.25 StartZ=0 EndX=1 EndY=-8.75 EndZ=0
    g44: LineSegment StartX=1 StartY=-8.75 StartZ=0 EndX=4.03109 EndY=-10.5 EndZ=0
    g45: LineSegment StartX=4.03109 StartY=-10.5 StartZ=0 EndX=7.06218 EndY=-8.75 EndZ=0
    g46: LineSegment StartX=7.06218 StartY=-8.75 StartZ=0 EndX=7.06218 EndY=-5.25 EndZ=0
    g47: LineSegment StartX=7.06218 StartY=-5.25 StartZ=0 EndX=4.03109 EndY=-3.5 EndZ=0
    g48: Circle [constr] CenterX=4.03109 CenterY=-7 CenterZ=0 NormalX=0 NormalY=0 NormalZ=1 AngleXU=0 Radius=3.5
  constraints (117):
    c: Coincident(g0,g1)
    c: Coincident(g1,g2)
    c: Coincident(g2,g3)
    c: Coincident(g3,g4)
    c: Coincident(g4,g5)
    c: Coincident(g5,g0)
    c: Equal(g0, g1-g5) x5
    c: PointOnObject(g0,g6)
    c: PointOnObject(g1,g6)
    c: PointOnObject(g2,g6)
    c: PointOnObject(g3,g6)
    c: PointOnObject(g4,g6)
    c: PointOnObject(g5,g6)
    c: Coincident(g6,g-1)
    c: Diameter(g6) = 7
    c: PointOnObject(g0,g-2)
    c: Coincident(g7,g8)
    c: Coincident(g8,g9)
    c: Coincident(g9,g10)
    c: Coincident(g10,g11)
    c: Coincident(g11,g12)
    c: Coincident(g12,g7)
    c: Equal(g7, g8-g12) x5
    c: PointOnObject(g7,g13)
    c: PointOnObject(g8,g13)
    c: PointOnObject(g9,g13)
    c: PointOnObject(g10,g13)
    c: PointOnObject(g11,g13)
    c: PointOnObject(g12,g13)
    c: PointOnObject(g13,g-1)
    c: Diameter(g13) = 7
    c: Distance(g6,g13) = 8
    c: Horizontal(g0,g10)
    c: Coincident(g14,g15)
    c: Coincident(g15,g16)
    c: Coincident(g16,g17)
    c: Coincident(g17,g18)
    c: Coincident(g18,g19)
    c: Coincident(g19,g14)
    c: Equal(g14, g15-g19) x5
    c: PointOnObject(g14,g20)
    c: PointOnObject(g15,g20)
    c: PointOnObject(g16,g20)
    c: PointOnObject(g17,g20)
    c: PointOnObject(g18,g20)
    c: PointOnObject(g19,g20)
    c: Diameter(g20) = 7
    c: DistanceY(g-1,g20) = 7
    c: Vertical(g18)
    c: Distance(g17,g-2) = 1
    c: Coincident(g21,g22)
    c: Coincident(g22,g23)
    c: Coincident(g23,g24)
    c: Coincident(g24,g25)
    c: Coincident(g25,g26)
    c: Coincident(g26,g21)
    c: Equal(g21, g22-g26) x5
    c: PointOnObject(g21,g27)
    c: PointOnObject(g22,g27)
    c: PointOnObject(g23,g27)
    c: PointOnObject(g24,g27)
    c: PointOnObject(g25,g27)
    c: PointOnObject(g26,g27)
    c: Diameter(g27) = 7
    c: DistanceY(g-1,g27) = 7
    c: DistanceX(g21,g-1) = 1
    c: Vertical(g21)
    c: Coincident(g28,g29)
    c: Coincident(g29,g30)
    c: Coincident(g30,g31)
    c: Coincident(g31,g32)
    c: Coincident(g32,g33)
    c: Coincident(g33,g28)
    c: Equal(g28, g29-g33) x5
    c: PointOnObject(g28,g34)
    c: PointOnObject(g29,g34)
    c: PointOnObject(g30,g34)
    c: PointOnObject(g31,g34)
    c: PointOnObject(g32,g34)
    c: PointOnObject(g33,g34)
    c: PointOnObject(g34,g-1)
    c: Diameter(g34) = 7
    c: Vertical(g31)
    c: DistanceX(g34,g-1) = 8
    c: Coincident(g35,g36)
    c: Coincident(g36,g37)
    c: Coincident(g37,g38)
    c: Coincident(g38,g39)
    c: Coincident(g39,g40)
    c: Coincident(g40,g35)
    c: Equal(g35, g36-g40) x5
    c: PointOnObject(g35,g41)
    c: PointOnObject(g36,g41)
    c: PointOnObject(g37,g41)
    c: PointOnObject(g38,g41)
    c: PointOnObject(g39,g41)
    c: PointOnObject(g40,g41)
    c: Coincident(g42,g43)
    c: Coincident(g43,g44)
    c: Coincident(g44,g45)
    c: Coincident(g45,g46)
    c: Coincident(g46,g47)
    c: Coincident(g47,g42)
    c: Equal(g42, g43-g47) x5
    c: PointOnObject(g42,g48)
    c: PointOnObject(g43,g48)
    c: PointOnObject(g44,g48)
    c: PointOnObject(g45,g48)
    c: PointOnObject(g46,g48)
    c: PointOnObject(g47,g48)
    c: Equal(g41,g48)
    c: Diameter(g41) = 7
    c: Vertical(g39)
    c: Vertical(g43)
    c: Distance(g-2,g39) = 1
    c: Symmetric(g38,g43,g-2)
    c: Distance(g41,g-1) = 7
FEATURE [Part::Extrusion] Extrude413  label="hex028"
  Base = -> Sketch421
  Dir = (0,-1,2e-16)
  DirMode = 2
  FaceMakerClass = Part::FaceMakerBullseye
  FaceMakerMode = 3
  LengthFwd = 10
  LengthRev = 0
  Placement = pos=(-64,0,14) rot=(0,0,1;0rad)
  Solid = true
  Symmetric = false
FEATURE [Sketcher::SketchObject] Sketch422
  ArcFitTolerance = 1e-06
  FullyConstrained = true
  MakeInternals = false
  Placement = pos=(0,0,0) rot=(1,0,0;1.5708rad)
  sketch-geometry (49):
    g0: LineSegment StartX=1e-16 StartY=3.5 StartZ=0 EndX=-3.03109 EndY=1.75 EndZ=0
    g1: LineSegment StartX=-3.03109 StartY=1.75 StartZ=0 EndX=-3.03109 EndY=-1.75 EndZ=0
    g2: LineSegment StartX=-3.03109 StartY=-1.75 StartZ=0 EndX=-1e-16 EndY=-3.5 EndZ=0
    g3: LineSegment StartX=-1e-16 StartY=-3.5 StartZ=0 EndX=3.03109 EndY=-1.75 EndZ=0
    g4: LineSegment StartX=3.03109 StartY=-1.75 StartZ=0 EndX=3.03109 EndY=1.75 EndZ=0
    g5: LineSegment StartX=3.03109 StartY=1.75 StartZ=0 EndX=1e-16 EndY=3.5 EndZ=0
    g6: Circle [constr] CenterX=0 CenterY=0 CenterZ=0 NormalX=0 NormalY=0 NormalZ=1 AngleXU=0 Radius=3.5
    g7: LineSegment StartX=4.96892 StartY=-1.75002 StartZ=0 EndX=8.00002 EndY=-3.5 EndZ=0
    g8: LineSegment StartX=8.00002 StartY=-3.5 StartZ=0 EndX=11.0311 EndY=-1.74998 EndZ=0
    g9: LineSegment StartX=11.0311 StartY=-1.74998 StartZ=0 EndX=11.0311 EndY=1.75002 EndZ=0
    g10: LineSegment StartX=11.0311 StartY=1.75002 StartZ=0 EndX=7.99998 EndY=3.5 EndZ=0
    g11: LineSegment StartX=7.99998 StartY=3.5 StartZ=0 EndX=4.9689 EndY=1.74998 EndZ=0
    g12: LineSegment StartX=4.9689 StartY=1.74998 StartZ=0 EndX=4.96892 EndY=-1.75002 EndZ=0
    g13: Circle [constr] CenterX=8 CenterY=0 CenterZ=0 NormalX=0 NormalY=0 NormalZ=1 AngleXU=0 Radius=3.5
    g14: LineSegment StartX=4.03109 StartY=3.5 StartZ=0 EndX=7.06218 EndY=5.25 EndZ=0
    g15: LineSegment StartX=7.06218 StartY=5.25 StartZ=0 EndX=7.06218 EndY=8.75 EndZ=0
    g16: LineSegment StartX=7.06218 StartY=8.75 StartZ=0 EndX=4.03109 EndY=10.5 EndZ=0
    g17: LineSegment StartX=4.03109 StartY=10.5 StartZ=0 EndX=1 EndY=8.75 EndZ=0
    g18: LineSegment StartX=1 StartY=8.75 StartZ=0 EndX=1 EndY=5.25 EndZ=0
    g19: LineSegment StartX=1 StartY=5.25 StartZ=0 EndX=4.03109 EndY=3.5 EndZ=0
    g20: Circle [constr] CenterX=4.03109 CenterY=7 CenterZ=0 NormalX=0 NormalY=0 NormalZ=1 AngleXU=0 Radius=3.5
    g21: LineSegment StartX=-1 StartY=5.25 StartZ=0 EndX=-1 EndY=8.75 EndZ=0
    g22: LineSegment StartX=-1 StartY=8.75 StartZ=0 EndX=-4.03109 EndY=10.5 EndZ=0
    g23: LineSegment StartX=-4.03109 StartY=10.5 StartZ=0 EndX=-7.06218 EndY=8.75 EndZ=0
    g24: LineSegment StartX=-7.06218 StartY=8.75 StartZ=0 EndX=-7.06218 EndY=5.25 EndZ=0
    g25: LineSegment StartX=-7.06218 StartY=5.25 StartZ=0 EndX=-4.03109 EndY=3.5 EndZ=0
    g26: LineSegment StartX=-4.03109 StartY=3.5 StartZ=0 EndX=-1 EndY=5.25 EndZ=0
    g27: Circle [constr] CenterX=-4.03109 CenterY=7 CenterZ=0 NormalX=0 NormalY=0 NormalZ=1 AngleXU=0 Radius=3.5
    g28: LineSegment StartX=-4.96891 StartY=-1.75 StartZ=0 EndX=-4.96891 EndY=1.75 EndZ=0
    g29: LineSegment StartX=-4.96891 StartY=1.75 StartZ=0 EndX=-8 EndY=3.5 EndZ=0
    g30: LineSegment StartX=-8 StartY=3.5 StartZ=0 EndX=-11.0311 EndY=1.75 EndZ=0
    g31: LineSegment StartX=-11.0311 StartY=1.75 StartZ=0 EndX=-11.0311 EndY=-1.75 EndZ=0
    g32: LineSegment StartX=-11.0311 StartY=-1.75 StartZ=0 EndX=-8 EndY=-3.5 EndZ=0
    g33: LineSegment StartX=-8 StartY=-3.5 StartZ=0 EndX=-4.96891 EndY=-1.75 EndZ=0
    g34: Circle [constr] CenterX=-8 CenterY=0 CenterZ=0 NormalX=0 NormalY=0 NormalZ=1 AngleXU=0 Radius=3.5
    g35: LineSegment StartX=-4.03109 StartY=-3.5 StartZ=0 EndX=-7.06218 EndY=-5.25 EndZ=0
    g36: LineSegment StartX=-7.06218 StartY=-5.25 StartZ=0 EndX=-7.06218 EndY=-8.75 EndZ=0
    g37: LineSegment StartX=-7.06218 StartY=-8.75 StartZ=0 EndX=-4.03109 EndY=-10.5 EndZ=0
    g38: LineSegment StartX=-4.03109 StartY=-10.5 StartZ=0 EndX=-1 EndY=-8.75 EndZ=0
    g39: LineSegment StartX=-1 StartY=-8.75 StartZ=0 EndX=-1 EndY=-5.25 EndZ=0
    g40: LineSegment StartX=-1 StartY=-5.25 StartZ=0 EndX=-4.03109 EndY=-3.5 EndZ=0
    g41: Circle [constr] CenterX=-4.03109 CenterY=-7 CenterZ=0 NormalX=0 NormalY=0 NormalZ=1 AngleXU=0 Radius=3.5
    g42: LineSegment StartX=4.03109 StartY=-3.5 StartZ=0 EndX=1 EndY=-5.25 EndZ=0
    g43: LineSegment StartX=1 StartY=-5.25 StartZ=0 EndX=1 EndY=-8.75 EndZ=0
    g44: LineSegment StartX=1 StartY=-8.75 StartZ=0 EndX=4.03109 EndY=-10.5 EndZ=0
    g45: LineSegment StartX=4.03109 StartY=-10.5 StartZ=0 EndX=7.06218 EndY=-8.75 EndZ=0
    g46: LineSegment StartX=7.06218 StartY=-8.75 StartZ=0 EndX=7.06218 EndY=-5.25 EndZ=0
    g47: LineSegment StartX=7.06218 StartY=-5.25 StartZ=0 EndX=4.03109 EndY=-3.5 EndZ=0
    g48: Circle [constr] CenterX=4.03109 CenterY=-7 CenterZ=0 NormalX=0 NormalY=0 NormalZ=1 AngleXU=0 Radius=3.5
  constraints (117):
    c: Coincident(g0,g1)
    c: Coincident(g1,g2)
    c: Coincident(g2,g3)
    c: Coincident(g3,g4)
    c: Coincident(g4,g5)
    c: Coincident(g5,g0)
    c: Equal(g0, g1-g5) x5
    c: PointOnObject(g0,g6)
    c: PointOnObject(g1,g6)
    c: PointOnObject(g2,g6)
    c: PointOnObject(g3,g6)
    c: PointOnObject(g4,g6)
    c: PointOnObject(g5,g6)
    c: Coincident(g6,g-1)
    c: Diameter(g6) = 7
    c: PointOnObject(g0,g-2)
    c: Coincident(g7,g8)
    c: Coincident(g8,g9)
    c: Coincident(g9,g10)
    c: Coincident(g10,g11)
    c: Coincident(g11,g12)
    c: Coincident(g12,g7)
    c: Equal(g7, g8-g12) x5
    c: PointOnObject(g7,g13)
    c: PointOnObject(g8,g13)
    c: PointOnObject(g9,g13)
    c: PointOnObject(g10,g13)
    c: PointOnObject(g11,g13)
    c: PointOnObject(g12,g13)
    c: PointOnObject(g13,g-1)
    c: Diameter(g13) = 7
    c: Distance(g6,g13) = 8
    c: Horizontal(g0,g10)
    c: Coincident(g14,g15)
    c: Coincident(g15,g16)
    c: Coincident(g16,g17)
    c: Coincident(g17,g18)
    c: Coincident(g18,g19)
    c: Coincident(g19,g14)
    c: Equal(g14, g15-g19) x5
    c: PointOnObject(g14,g20)
    c: PointOnObject(g15,g20)
    c: PointOnObject(g16,g20)
    c: PointOnObject(g17,g20)
    c: PointOnObject(g18,g20)
    c: PointOnObject(g19,g20)
    c: Diameter(g20) = 7
    c: DistanceY(g-1,g20) = 7
    c: Vertical(g18)
    c: Distance(g17,g-2) = 1
    c: Coincident(g21,g22)
    c: Coincident(g22,g23)
    c: Coincident(g23,g24)
    c: Coincident(g24,g25)
    c: Coincident(g25,g26)
    c: Coincident(g26,g21)
    c: Equal(g21, g22-g26) x5
    c: PointOnObject(g21,g27)
    c: PointOnObject(g22,g27)
    c: PointOnObject(g23,g27)
    c: PointOnObject(g24,g27)
    c: PointOnObject(g25,g27)
    c: PointOnObject(g26,g27)
    c: Diameter(g27) = 7
    c: DistanceY(g-1,g27) = 7
    c: DistanceX(g21,g-1) = 1
    c: Vertical(g21)
    c: Coincident(g28,g29)
    c: Coincident(g29,g30)
    c: Coincident(g30,g31)
    c: Coincident(g31,g32)
    c: Coincident(g32,g33)
    c: Coincident(g33,g28)
    c: Equal(g28, g29-g33) x5
    c: PointOnObject(g28,g34)
    c: PointOnObject(g29,g34)
    c: PointOnObject(g30,g34)
    c: PointOnObject(g31,g34)
    c: PointOnObject(g32,g34)
    c: PointOnObject(g33,g34)
    c: PointOnObject(g34,g-1)
    c: Diameter(g34) = 7
    c: Vertical(g31)
    c: DistanceX(g34,g-1) = 8
    c: Coincident(g35,g36)
    c: Coincident(g36,g37)
    c: Coincident(g37,g38)
    c: Coincident(g38,g39)
    c: Coincident(g39,g40)
    c: Coincident(g40,g35)
    c: Equal(g35, g36-g40) x5
    c: PointOnObject(g35,g41)
    c: PointOnObject(g36,g41)
    c: PointOnObject(g37,g41)
    c: PointOnObject(g38,g41)
    c: PointOnObject(g39,g41)
    c: PointOnObject(g40,g41)
    c: Coincident(g42,g43)
    c: Coincident(g43,g44)
    c: Coincident(g44,g45)
    c: Coincident(g45,g46)
    c: Coincident(g46,g47)
    c: Coincident(g47,g42)
    c: Equal(g42, g43-g47) x5
    c: PointOnObject(g42,g48)
    c: PointOnObject(g43,g48)
    c: PointOnObject(g44,g48)
    c: PointOnObject(g45,g48)
    c: PointOnObject(g46,g48)
    c: PointOnObject(g47,g48)
    c: Equal(g41,g48)
    c: Diameter(g41) = 7
    c: Vertical(g39)
    c: Vertical(g43)
    c: Distance(g-2,g39) = 1
    c: Symmetric(g38,g43,g-2)
    c: Distance(g41,g-1) = 7
FEATURE [Part::Extrusion] Extrude414  label="hex029"
  Base = -> Sketch422
  Dir = (0,-1,2e-16)
  DirMode = 2
  FaceMakerClass = Part::FaceMakerBullseye
  FaceMakerMode = 3
  LengthFwd = 10
  LengthRev = 0
  Placement = pos=(-64,0,-14) rot=(0,0,1;0rad)
  Solid = true
  Symmetric = false
FEATURE [Sketcher::SketchObject] Sketch423
  ArcFitTolerance = 1e-06
  FullyConstrained = true
  MakeInternals = false
  Placement = pos=(0,0,0) rot=(1,0,0;1.5708rad)
  sketch-geometry (49):
    g0: LineSegment StartX=1e-16 StartY=3.5 StartZ=0 EndX=-3.03109 EndY=1.75 EndZ=0
    g1: LineSegment StartX=-3.03109 StartY=1.75 StartZ=0 EndX=-3.03109 EndY=-1.75 EndZ=0
    g2: LineSegment StartX=-3.03109 StartY=-1.75 StartZ=0 EndX=-1e-16 EndY=-3.5 EndZ=0
    g3: LineSegment StartX=-1e-16 StartY=-3.5 StartZ=0 EndX=3.03109 EndY=-1.75 EndZ=0
    g4: LineSegment StartX=3.03109 StartY=-1.75 StartZ=0 EndX=3.03109 EndY=1.75 EndZ=0
    g5: LineSegment StartX=3.03109 StartY=1.75 StartZ=0 EndX=1e-16 EndY=3.5 EndZ=0
    g6: Circle [constr] CenterX=0 CenterY=0 CenterZ=0 NormalX=0 NormalY=0 NormalZ=1 AngleXU=0 Radius=3.5
    g7: LineSegment StartX=4.96892 StartY=-1.75002 StartZ=0 EndX=8.00002 EndY=-3.5 EndZ=0
    g8: LineSegment StartX=8.00002 StartY=-3.5 StartZ=0 EndX=11.0311 EndY=-1.74998 EndZ=0
    g9: LineSegment StartX=11.0311 StartY=-1.74998 StartZ=0 EndX=11.0311 EndY=1.75002 EndZ=0
    g10: LineSegment StartX=11.0311 StartY=1.75002 StartZ=0 EndX=7.99998 EndY=3.5 EndZ=0
    g11: LineSegment StartX=7.99998 StartY=3.5 StartZ=0 EndX=4.9689 EndY=1.74998 EndZ=0
    g12: LineSegment StartX=4.9689 StartY=1.74998 StartZ=0 EndX=4.96892 EndY=-1.75002 EndZ=0
    g13: Circle [constr] CenterX=8 CenterY=0 CenterZ=0 NormalX=0 NormalY=0 NormalZ=1 AngleXU=0 Radius=3.5
    g14: LineSegment StartX=4.03109 StartY=3.5 StartZ=0 EndX=7.06218 EndY=5.25 EndZ=0
    g15: LineSegment StartX=7.06218 StartY=5.25 StartZ=0 EndX=7.06218 EndY=8.75 EndZ=0
    g16: LineSegment StartX=7.06218 StartY=8.75 StartZ=0 EndX=4.03109 EndY=10.5 EndZ=0
    g17: LineSegment StartX=4.03109 StartY=10.5 StartZ=0 EndX=1 EndY=8.75 EndZ=0
    g18: LineSegment StartX=1 StartY=8.75 StartZ=0 EndX=1 EndY=5.25 EndZ=0
    g19: LineSegment StartX=1 StartY=5.25 StartZ=0 EndX=4.03109 EndY=3.5 EndZ=0
    g20: Circle [constr] CenterX=4.03109 CenterY=7 CenterZ=0 NormalX=0 NormalY=0 NormalZ=1 AngleXU=0 Radius=3.5
    g21: LineSegment StartX=-1 StartY=5.25 StartZ=0 EndX=-1 EndY=8.75 EndZ=0
    g22: LineSegment StartX=-1 StartY=8.75 StartZ=0 EndX=-4.03109 EndY=10.5 EndZ=0
    g23: LineSegment StartX=-4.03109 StartY=10.5 StartZ=0 EndX=-7.06218 EndY=8.75 EndZ=0
    g24: LineSegment StartX=-7.06218 StartY=8.75 StartZ=0 EndX=-7.06218 EndY=5.25 EndZ=0
    g25: LineSegment StartX=-7.06218 StartY=5.25 StartZ=0 EndX=-4.03109 EndY=3.5 EndZ=0
    g26: LineSegment StartX=-4.03109 StartY=3.5 StartZ=0 EndX=-1 EndY=5.25 EndZ=0
    g27: Circle [constr] CenterX=-4.03109 CenterY=7 CenterZ=0 NormalX=0 NormalY=0 NormalZ=1 AngleXU=0 Radius=3.5
    g28: LineSegment StartX=-4.96891 StartY=-1.75 StartZ=0 EndX=-4.96891 EndY=1.75 EndZ=0
    g29: LineSegment StartX=-4.96891 StartY=1.75 StartZ=0 EndX=-8 EndY=3.5 EndZ=0
    g30: LineSegment StartX=-8 StartY=3.5 StartZ=0 EndX=-11.0311 EndY=1.75 EndZ=0
    g31: LineSegment StartX=-11.0311 StartY=1.75 StartZ=0 EndX=-11.0311 EndY=-1.75 EndZ=0
    g32: LineSegment StartX=-11.0311 StartY=-1.75 StartZ=0 EndX=-8 EndY=-3.5 EndZ=0
    g33: LineSegment StartX=-8 StartY=-3.5 StartZ=0 EndX=-4.96891 EndY=-1.75 EndZ=0
    g34: Circle [constr] CenterX=-8 CenterY=0 CenterZ=0 NormalX=0 NormalY=0 NormalZ=1 AngleXU=0 Radius=3.5
    g35: LineSegment StartX=-4.03109 StartY=-3.5 StartZ=0 EndX=-7.06218 EndY=-5.25 EndZ=0
    g36: LineSegment StartX=-7.06218 StartY=-5.25 StartZ=0 EndX=-7.06218 EndY=-8.75 EndZ=0
    g37: LineSegment StartX=-7.06218 StartY=-8.75 StartZ=0 EndX=-4.03109 EndY=-10.5 EndZ=0
    g38: LineSegment StartX=-4.03109 StartY=-10.5 StartZ=0 EndX=-1 EndY=-8.75 EndZ=0
    g39: LineSegment StartX=-1 StartY=-8.75 StartZ=0 EndX=-1 EndY=-5.25 EndZ=0
    g40: LineSegment StartX=-1 StartY=-5.25 StartZ=0 EndX=-4.03109 EndY=-3.5 EndZ=0
    g41: Circle [constr] CenterX=-4.03109 CenterY=-7 CenterZ=0 NormalX=0 NormalY=0 NormalZ=1 AngleXU=0 Radius=3.5
    g42: LineSegment StartX=4.03109 StartY=-3.5 StartZ=0 EndX=1 EndY=-5.25 EndZ=0
    g43: LineSegment StartX=1 StartY=-5.25 StartZ=0 EndX=1 EndY=-8.75 EndZ=0
    g44: LineSegment StartX=1 StartY=-8.75 StartZ=0 EndX=4.03109 EndY=-10.5 EndZ=0
    g45: LineSegment StartX=4.03109 StartY=-10.5 StartZ=0 EndX=7.06218 EndY=-8.75 EndZ=0
    g46: LineSegment StartX=7.06218 StartY=-8.75 StartZ=0 EndX=7.06218 EndY=-5.25 EndZ=0
    g47: LineSegment StartX=7.06218 StartY=-5.25 StartZ=0 EndX=4.03109 EndY=-3.5 EndZ=0
    g48: Circle [constr] CenterX=4.03109 CenterY=-7 CenterZ=0 NormalX=0 NormalY=0 NormalZ=1 AngleXU=0 Radius=3.5
  constraints (117):
    c: Coincident(g0,g1)
    c: Coincident(g1,g2)
    c: Coincident(g2,g3)
    c: Coincident(g3,g4)
    c: Coincident(g4,g5)
    c: Coincident(g5,g0)
    c: Equal(g0, g1-g5) x5
    c: PointOnObject(g0,g6)
    c: PointOnObject(g1,g6)
    c: PointOnObject(g2,g6)
    c: PointOnObject(g3,g6)
    c: PointOnObject(g4,g6)
    c: PointOnObject(g5,g6)
    c: Coincident(g6,g-1)
    c: Diameter(g6) = 7
    c: PointOnObject(g0,g-2)
    c: Coincident(g7,g8)
    c: Coincident(g8,g9)
    c: Coincident(g9,g10)
    c: Coincident(g10,g11)
    c: Coincident(g11,g12)
    c: Coincident(g12,g7)
    c: Equal(g7, g8-g12) x5
    c: PointOnObject(g7,g13)
    c: PointOnObject(g8,g13)
    c: PointOnObject(g9,g13)
    c: PointOnObject(g10,g13)
    c: PointOnObject(g11,g13)
    c: PointOnObject(g12,g13)
    c: PointOnObject(g13,g-1)
    c: Diameter(g13) = 7
    c: Distance(g6,g13) = 8
    c: Horizontal(g0,g10)
    c: Coincident(g14,g15)
    c: Coincident(g15,g16)
    c: Coincident(g16,g17)
    c: Coincident(g17,g18)
    c: Coincident(g18,g19)
    c: Coincident(g19,g14)
    c: Equal(g14, g15-g19) x5
    c: PointOnObject(g14,g20)
    c: PointOnObject(g15,g20)
    c: PointOnObject(g16,g20)
    c: PointOnObject(g17,g20)
    c: PointOnObject(g18,g20)
    c: PointOnObject(g19,g20)
    c: Diameter(g20) = 7
    c: DistanceY(g-1,g20) = 7
    c: Vertical(g18)
    c: Distance(g17,g-2) = 1
    c: Coincident(g21,g22)
    c: Coincident(g22,g23)
    c: Coincident(g23,g24)
    c: Coincident(g24,g25)
    c: Coincident(g25,g26)
    c: Coincident(g26,g21)
    c: Equal(g21, g22-g26) x5
    c: PointOnObject(g21,g27)
    c: PointOnObject(g22,g27)
    c: PointOnObject(g23,g27)
    c: PointOnObject(g24,g27)
    c: PointOnObject(g25,g27)
    c: PointOnObject(g26,g27)
    c: Diameter(g27) = 7
    c: DistanceY(g-1,g27) = 7
    c: DistanceX(g21,g-1) = 1
    c: Vertical(g21)
    c: Coincident(g28,g29)
    c: Coincident(g29,g30)
    c: Coincident(g30,g31)
    c: Coincident(g31,g32)
    c: Coincident(g32,g33)
    c: Coincident(g33,g28)
    c: Equal(g28, g29-g33) x5
    c: PointOnObject(g28,g34)
    c: PointOnObject(g29,g34)
    c: PointOnObject(g30,g34)
    c: PointOnObject(g31,g34)
    c: PointOnObject(g32,g34)
    c: PointOnObject(g33,g34)
    c: PointOnObject(g34,g-1)
    c: Diameter(g34) = 7
    c: Vertical(g31)
    c: DistanceX(g34,g-1) = 8
    c: Coincident(g35,g36)
    c: Coincident(g36,g37)
    c: Coincident(g37,g38)
    c: Coincident(g38,g39)
    c: Coincident(g39,g40)
    c: Coincident(g40,g35)
    c: Equal(g35, g36-g40) x5
    c: PointOnObject(g35,g41)
    c: PointOnObject(g36,g41)
    c: PointOnObject(g37,g41)
    c: PointOnObject(g38,g41)
    c: PointOnObject(g39,g41)
    c: PointOnObject(g40,g41)
    c: Coincident(g42,g43)
    c: Coincident(g43,g44)
    c: Coincident(g44,g45)
    c: Coincident(g45,g46)
    c: Coincident(g46,g47)
    c: Coincident(g47,g42)
    c: Equal(g42, g43-g47) x5
    c: PointOnObject(g42,g48)
    c: PointOnObject(g43,g48)
    c: PointOnObject(g44,g48)
    c: PointOnObject(g45,g48)
    c: PointOnObject(g46,g48)
    c: PointOnObject(g47,g48)
    c: Equal(g41,g48)
    c: Diameter(g41) = 7
    c: Vertical(g39)
    c: Vertical(g43)
    c: Distance(g-2,g39) = 1
    c: Symmetric(g38,g43,g-2)
    c: Distance(g41,g-1) = 7
FEATURE [Part::Extrusion] Extrude415  label="hex030"
  Base = -> Sketch423
  Dir = (0,-1,2e-16)
  DirMode = 2
  FaceMakerClass = Part::FaceMakerBullseye
  FaceMakerMode = 3
  LengthFwd = 10
  LengthRev = 0
  Placement = pos=(-48,0,-28) rot=(0,0,1;0rad)
  Solid = true
  Symmetric = false
FEATURE [Sketcher::SketchObject] Sketch424
  ArcFitTolerance = 1e-06
  FullyConstrained = true
  MakeInternals = false
  Placement = pos=(0,0,0) rot=(1,0,0;1.5708rad)
  sketch-geometry (49):
    g0: LineSegment StartX=1e-16 StartY=3.5 StartZ=0 EndX=-3.03109 EndY=1.75 EndZ=0
    g1: LineSegment StartX=-3.03109 StartY=1.75 StartZ=0 EndX=-3.03109 EndY=-1.75 EndZ=0
    g2: LineSegment StartX=-3.03109 StartY=-1.75 StartZ=0 EndX=-1e-16 EndY=-3.5 EndZ=0
    g3: LineSegment StartX=-1e-16 StartY=-3.5 StartZ=0 EndX=3.03109 EndY=-1.75 EndZ=0
    g4: LineSegment StartX=3.03109 StartY=-1.75 StartZ=0 EndX=3.03109 EndY=1.75 EndZ=0
    g5: LineSegment StartX=3.03109 StartY=1.75 StartZ=0 EndX=1e-16 EndY=3.5 EndZ=0
    g6: Circle [constr] CenterX=0 CenterY=0 CenterZ=0 NormalX=0 NormalY=0 NormalZ=1 AngleXU=0 Radius=3.5
    g7: LineSegment StartX=4.96892 StartY=-1.75002 StartZ=0 EndX=8.00002 EndY=-3.5 EndZ=0
    g8: LineSegment StartX=8.00002 StartY=-3.5 StartZ=0 EndX=11.0311 EndY=-1.74998 EndZ=0
    g9: LineSegment StartX=11.0311 StartY=-1.74998 StartZ=0 EndX=11.0311 EndY=1.75002 EndZ=0
    g10: LineSegment StartX=11.0311 StartY=1.75002 StartZ=0 EndX=7.99998 EndY=3.5 EndZ=0
    g11: LineSegment StartX=7.99998 StartY=3.5 StartZ=0 EndX=4.9689 EndY=1.74998 EndZ=0
    g12: LineSegment StartX=4.9689 StartY=1.74998 StartZ=0 EndX=4.96892 EndY=-1.75002 EndZ=0
    g13: Circle [constr] CenterX=8 CenterY=0 CenterZ=0 NormalX=0 NormalY=0 NormalZ=1 AngleXU=0 Radius=3.5
    g14: LineSegment StartX=4.03109 StartY=3.5 StartZ=0 EndX=7.06218 EndY=5.25 EndZ=0
    g15: LineSegment StartX=7.06218 StartY=5.25 StartZ=0 EndX=7.06218 EndY=8.75 EndZ=0
    g16: LineSegment StartX=7.06218 StartY=8.75 StartZ=0 EndX=4.03109 EndY=10.5 EndZ=0
    g17: LineSegment StartX=4.03109 StartY=10.5 StartZ=0 EndX=1 EndY=8.75 EndZ=0
    g18: LineSegment StartX=1 StartY=8.75 StartZ=0 EndX=1 EndY=5.25 EndZ=0
    g19: LineSegment StartX=1 StartY=5.25 StartZ=0 EndX=4.03109 EndY=3.5 EndZ=0
    g20: Circle [constr] CenterX=4.03109 CenterY=7 CenterZ=0 NormalX=0 NormalY=0 NormalZ=1 AngleXU=0 Radius=3.5
    g21: LineSegment StartX=-1 StartY=5.25 StartZ=0 EndX=-1 EndY=8.75 EndZ=0
    g22: LineSegment StartX=-1 StartY=8.75 StartZ=0 EndX=-4.03109 EndY=10.5 EndZ=0
    g23: LineSegment StartX=-4.03109 StartY=10.5 StartZ=0 EndX=-7.06218 EndY=8.75 EndZ=0
    g24: LineSegment StartX=-7.06218 StartY=8.75 StartZ=0 EndX=-7.06218 EndY=5.25 EndZ=0
    g25: LineSegment StartX=-7.06218 StartY=5.25 StartZ=0 EndX=-4.03109 EndY=3.5 EndZ=0
    g26: LineSegment StartX=-4.03109 StartY=3.5 StartZ=0 EndX=-1 EndY=5.25 EndZ=0
    g27: Circle [constr] CenterX=-4.03109 CenterY=7 CenterZ=0 NormalX=0 NormalY=0 NormalZ=1 AngleXU=0 Radius=3.5
    g28: LineSegment StartX=-4.96891 StartY=-1.75 StartZ=0 EndX=-4.96891 EndY=1.75 EndZ=0
    g29: LineSegment StartX=-4.96891 StartY=1.75 StartZ=0 EndX=-8 EndY=3.5 EndZ=0
    g30: LineSegment StartX=-8 StartY=3.5 StartZ=0 EndX=-11.0311 EndY=1.75 EndZ=0
    g31: LineSegment StartX=-11.0311 StartY=1.75 StartZ=0 EndX=-11.0311 EndY=-1.75 EndZ=0
    g32: LineSegment StartX=-11.0311 StartY=-1.75 StartZ=0 EndX=-8 EndY=-3.5 EndZ=0
    g33: LineSegment StartX=-8 StartY=-3.5 StartZ=0 EndX=-4.96891 EndY=-1.75 EndZ=0
    g34: Circle [constr] CenterX=-8 CenterY=0 CenterZ=0 NormalX=0 NormalY=0 NormalZ=1 AngleXU=0 Radius=3.5
    g35: LineSegment StartX=-4.03109 StartY=-3.5 StartZ=0 EndX=-7.06218 EndY=-5.25 EndZ=0
    g36: LineSegment StartX=-7.06218 StartY=-5.25 StartZ=0 EndX=-7.06218 EndY=-8.75 EndZ=0
    g37: LineSegment StartX=-7.06218 StartY=-8.75 StartZ=0 EndX=-4.03109 EndY=-10.5 EndZ=0
    g38: LineSegment StartX=-4.03109 StartY=-10.5 StartZ=0 EndX=-1 EndY=-8.75 EndZ=0
    g39: LineSegment StartX=-1 StartY=-8.75 StartZ=0 EndX=-1 EndY=-5.25 EndZ=0
    g40: LineSegment StartX=-1 StartY=-5.25 StartZ=0 EndX=-4.03109 EndY=-3.5 EndZ=0
    g41: Circle [constr] CenterX=-4.03109 CenterY=-7 CenterZ=0 NormalX=0 NormalY=0 NormalZ=1 AngleXU=0 Radius=3.5
    g42: LineSegment StartX=4.03109 StartY=-3.5 StartZ=0 EndX=1 EndY=-5.25 EndZ=0
    g43: LineSegment StartX=1 StartY=-5.25 StartZ=0 EndX=1 EndY=-8.75 EndZ=0
    g44: LineSegment StartX=1 StartY=-8.75 StartZ=0 EndX=4.03109 EndY=-10.5 EndZ=0
    g45: LineSegment StartX=4.03109 StartY=-10.5 StartZ=0 EndX=7.06218 EndY=-8.75 EndZ=0
    g46: LineSegment StartX=7.06218 StartY=-8.75 StartZ=0 EndX=7.06218 EndY=-5.25 EndZ=0
    g47: LineSegment StartX=7.06218 StartY=-5.25 StartZ=0 EndX=4.03109 EndY=-3.5 EndZ=0
    g48: Circle [constr] CenterX=4.03109 CenterY=-7 CenterZ=0 NormalX=0 NormalY=0 NormalZ=1 AngleXU=0 Radius=3.5
  constraints (117):
    c: Coincident(g0,g1)
    c: Coincident(g1,g2)
    c: Coincident(g2,g3)
    c: Coincident(g3,g4)
    c: Coincident(g4,g5)
    c: Coincident(g5,g0)
    c: Equal(g0, g1-g5) x5
    c: PointOnObject(g0,g6)
    c: PointOnObject(g1,g6)
    c: PointOnObject(g2,g6)
    c: PointOnObject(g3,g6)
    c: PointOnObject(g4,g6)
    c: PointOnObject(g5,g6)
    c: Coincident(g6,g-1)
    c: Diameter(g6) = 7
    c: PointOnObject(g0,g-2)
    c: Coincident(g7,g8)
    c: Coincident(g8,g9)
    c: Coincident(g9,g10)
    c: Coincident(g10,g11)
    c: Coincident(g11,g12)
    c: Coincident(g12,g7)
    c: Equal(g7, g8-g12) x5
    c: PointOnObject(g7,g13)
    c: PointOnObject(g8,g13)
    c: PointOnObject(g9,g13)
    c: PointOnObject(g10,g13)
    c: PointOnObject(g11,g13)
    c: PointOnObject(g12,g13)
    c: PointOnObject(g13,g-1)
    c: Diameter(g13) = 7
    c: Distance(g6,g13) = 8
    c: Horizontal(g0,g10)
    c: Coincident(g14,g15)
    c: Coincident(g15,g16)
    c: Coincident(g16,g17)
    c: Coincident(g17,g18)
    c: Coincident(g18,g19)
    c: Coincident(g19,g14)
    c: Equal(g14, g15-g19) x5
    c: PointOnObject(g14,g20)
    c: PointOnObject(g15,g20)
    c: PointOnObject(g16,g20)
    c: PointOnObject(g17,g20)
    c: PointOnObject(g18,g20)
    c: PointOnObject(g19,g20)
    c: Diameter(g20) = 7
    c: DistanceY(g-1,g20) = 7
    c: Vertical(g18)
    c: Distance(g17,g-2) = 1
    c: Coincident(g21,g22)
    c: Coincident(g22,g23)
    c: Coincident(g23,g24)
    c: Coincident(g24,g25)
    c: Coincident(g25,g26)
    c: Coincident(g26,g21)
    c: Equal(g21, g22-g26) x5
    c: PointOnObject(g21,g27)
    c: PointOnObject(g22,g27)
    c: PointOnObject(g23,g27)
    c: PointOnObject(g24,g27)
    c: PointOnObject(g25,g27)
    c: PointOnObject(g26,g27)
    c: Diameter(g27) = 7
    c: DistanceY(g-1,g27) = 7
    c: DistanceX(g21,g-1) = 1
    c: Vertical(g21)
    c: Coincident(g28,g29)
    c: Coincident(g29,g30)
    c: Coincident(g30,g31)
    c: Coincident(g31,g32)
    c: Coincident(g32,g33)
    c: Coincident(g33,g28)
    c: Equal(g28, g29-g33) x5
    c: PointOnObject(g28,g34)
    c: PointOnObject(g29,g34)
    c: PointOnObject(g30,g34)
    c: PointOnObject(g31,g34)
    c: PointOnObject(g32,g34)
    c: PointOnObject(g33,g34)
    c: PointOnObject(g34,g-1)
    c: Diameter(g34) = 7
    c: Vertical(g31)
    c: DistanceX(g34,g-1) = 8
    c: Coincident(g35,g36)
    c: Coincident(g36,g37)
    c: Coincident(g37,g38)
    c: Coincident(g38,g39)
    c: Coincident(g39,g40)
    c: Coincident(g40,g35)
    c: Equal(g35, g36-g40) x5
    c: PointOnObject(g35,g41)
    c: PointOnObject(g36,g41)
    c: PointOnObject(g37,g41)
    c: PointOnObject(g38,g41)
    c: PointOnObject(g39,g41)
    c: PointOnObject(g40,g41)
    c: Coincident(g42,g43)
    c: Coincident(g43,g44)
    c: Coincident(g44,g45)
    c: Coincident(g45,g46)
    c: Coincident(g46,g47)
    c: Coincident(g47,g42)
    c: Equal(g42, g43-g47) x5
    c: PointOnObject(g42,g48)
    c: PointOnObject(g43,g48)
    c: PointOnObject(g44,g48)
    c: PointOnObject(g45,g48)
    c: PointOnObject(g46,g48)
    c: PointOnObject(g47,g48)
    c: Equal(g41,g48)
    c: Diameter(g41) = 7
    c: Vertical(g39)
    c: Vertical(g43)
    c: Distance(g-2,g39) = 1
    c: Symmetric(g38,g43,g-2)
    c: Distance(g41,g-1) = 7
FEATURE [Part::Extrusion] Extrude416  label="hex031"
  Base = -> Sketch424
  Dir = (0,-1,2e-16)
  DirMode = 2
  FaceMakerClass = Part::FaceMakerBullseye
  FaceMakerMode = 3
  LengthFwd = 10
  LengthRev = 0
  Placement = pos=(-32,0,-42) rot=(0,0,1;0rad)
  Solid = true
  Symmetric = false
FEATURE [Sketcher::SketchObject] Sketch425
  ArcFitTolerance = 1e-06
  FullyConstrained = true
  MakeInternals = false
  Placement = pos=(0,0,0) rot=(1,0,0;1.5708rad)
  sketch-geometry (49):
    g0: LineSegment StartX=1e-16 StartY=3.5 StartZ=0 EndX=-3.03109 EndY=1.75 EndZ=0
    g1: LineSegment StartX=-3.03109 StartY=1.75 StartZ=0 EndX=-3.03109 EndY=-1.75 EndZ=0
    g2: LineSegment StartX=-3.03109 StartY=-1.75 StartZ=0 EndX=-1e-16 EndY=-3.5 EndZ=0
    g3: LineSegment StartX=-1e-16 StartY=-3.5 StartZ=0 EndX=3.03109 EndY=-1.75 EndZ=0
    g4: LineSegment StartX=3.03109 StartY=-1.75 StartZ=0 EndX=3.03109 EndY=1.75 EndZ=0
    g5: LineSegment StartX=3.03109 StartY=1.75 StartZ=0 EndX=1e-16 EndY=3.5 EndZ=0
    g6: Circle [constr] CenterX=0 CenterY=0 CenterZ=0 NormalX=0 NormalY=0 NormalZ=1 AngleXU=0 Radius=3.5
    g7: LineSegment StartX=4.96892 StartY=-1.75002 StartZ=0 EndX=8.00002 EndY=-3.5 EndZ=0
    g8: LineSegment StartX=8.00002 StartY=-3.5 StartZ=0 EndX=11.0311 EndY=-1.74998 EndZ=0
    g9: LineSegment StartX=11.0311 StartY=-1.74998 StartZ=0 EndX=11.0311 EndY=1.75002 EndZ=0
    g10: LineSegment StartX=11.0311 StartY=1.75002 StartZ=0 EndX=7.99998 EndY=3.5 EndZ=0
    g11: LineSegment StartX=7.99998 StartY=3.5 StartZ=0 EndX=4.9689 EndY=1.74998 EndZ=0
    g12: LineSegment StartX=4.9689 StartY=1.74998 StartZ=0 EndX=4.96892 EndY=-1.75002 EndZ=0
    g13: Circle [constr] CenterX=8 CenterY=0 CenterZ=0 NormalX=0 NormalY=0 NormalZ=1 AngleXU=0 Radius=3.5
    g14: LineSegment StartX=4.03109 StartY=3.5 StartZ=0 EndX=7.06218 EndY=5.25 EndZ=0
    g15: LineSegment StartX=7.06218 StartY=5.25 StartZ=0 EndX=7.06218 EndY=8.75 EndZ=0
    g16: LineSegment StartX=7.06218 StartY=8.75 StartZ=0 EndX=4.03109 EndY=10.5 EndZ=0
    g17: LineSegment StartX=4.03109 StartY=10.5 StartZ=0 EndX=1 EndY=8.75 EndZ=0
    g18: LineSegment StartX=1 StartY=8.75 StartZ=0 EndX=1 EndY=5.25 EndZ=0
    g19: LineSegment StartX=1 StartY=5.25 StartZ=0 EndX=4.03109 EndY=3.5 EndZ=0
    g20: Circle [constr] CenterX=4.03109 CenterY=7 CenterZ=0 NormalX=0 NormalY=0 NormalZ=1 AngleXU=0 Radius=3.5
    g21: LineSegment StartX=-1 StartY=5.25 StartZ=0 EndX=-1 EndY=8.75 EndZ=0
    g22: LineSegment StartX=-1 StartY=8.75 StartZ=0 EndX=-4.03109 EndY=10.5 EndZ=0
    g23: LineSegment StartX=-4.03109 StartY=10.5 StartZ=0 EndX=-7.06218 EndY=8.75 EndZ=0
    g24: LineSegment StartX=-7.06218 StartY=8.75 StartZ=0 EndX=-7.06218 EndY=5.25 EndZ=0
    g25: LineSegment StartX=-7.06218 StartY=5.25 StartZ=0 EndX=-4.03109 EndY=3.5 EndZ=0
    g26: LineSegment StartX=-4.03109 StartY=3.5 StartZ=0 EndX=-1 EndY=5.25 EndZ=0
    g27: Circle [constr] CenterX=-4.03109 CenterY=7 CenterZ=0 NormalX=0 NormalY=0 NormalZ=1 AngleXU=0 Radius=3.5
    g28: LineSegment StartX=-4.96891 StartY=-1.75 StartZ=0 EndX=-4.96891 EndY=1.75 EndZ=0
    g29: LineSegment StartX=-4.96891 StartY=1.75 StartZ=0 EndX=-8 EndY=3.5 EndZ=0
    g30: LineSegment StartX=-8 StartY=3.5 StartZ=0 EndX=-11.0311 EndY=1.75 EndZ=0
    g31: LineSegment StartX=-11.0311 StartY=1.75 StartZ=0 EndX=-11.0311 EndY=-1.75 EndZ=0
    g32: LineSegment StartX=-11.0311 StartY=-1.75 StartZ=0 EndX=-8 EndY=-3.5 EndZ=0
    g33: LineSegment StartX=-8 StartY=-3.5 StartZ=0 EndX=-4.96891 EndY=-1.75 EndZ=0
    g34: Circle [constr] CenterX=-8 CenterY=0 CenterZ=0 NormalX=0 NormalY=0 NormalZ=1 AngleXU=0 Radius=3.5
    g35: LineSegment StartX=-4.03109 StartY=-3.5 StartZ=0 EndX=-7.06218 EndY=-5.25 EndZ=0
    g36: LineSegment StartX=-7.06218 StartY=-5.25 StartZ=0 EndX=-7.06218 EndY=-8.75 EndZ=0
    g37: LineSegment StartX=-7.06218 StartY=-8.75 StartZ=0 EndX=-4.03109 EndY=-10.5 EndZ=0
    g38: LineSegment StartX=-4.03109 StartY=-10.5 StartZ=0 EndX=-1 EndY=-8.75 EndZ=0
    g39: LineSegment StartX=-1 StartY=-8.75 StartZ=0 EndX=-1 EndY=-5.25 EndZ=0
    g40: LineSegment StartX=-1 StartY=-5.25 StartZ=0 EndX=-4.03109 EndY=-3.5 EndZ=0
    g41: Circle [constr] CenterX=-4.03109 CenterY=-7 CenterZ=0 NormalX=0 NormalY=0 NormalZ=1 AngleXU=0 Radius=3.5
    g42: LineSegment StartX=4.03109 StartY=-3.5 StartZ=0 EndX=1 EndY=-5.25 EndZ=0
    g43: LineSegment StartX=1 StartY=-5.25 StartZ=0 EndX=1 EndY=-8.75 EndZ=0
    g44: LineSegment StartX=1 StartY=-8.75 StartZ=0 EndX=4.03109 EndY=-10.5 EndZ=0
    g45: LineSegment StartX=4.03109 StartY=-10.5 StartZ=0 EndX=7.06218 EndY=-8.75 EndZ=0
    g46: LineSegment StartX=7.06218 StartY=-8.75 StartZ=0 EndX=7.06218 EndY=-5.25 EndZ=0
    g47: LineSegment StartX=7.06218 StartY=-5.25 StartZ=0 EndX=4.03109 EndY=-3.5 EndZ=0
    g48: Circle [constr] CenterX=4.03109 CenterY=-7 CenterZ=0 NormalX=0 NormalY=0 NormalZ=1 AngleXU=0 Radius=3.5
  constraints (117):
    c: Coincident(g0,g1)
    c: Coincident(g1,g2)
    c: Coincident(g2,g3)
    c: Coincident(g3,g4)
    c: Coincident(g4,g5)
    c: Coincident(g5,g0)
    c: Equal(g0, g1-g5) x5
    c: PointOnObject(g0,g6)
    c: PointOnObject(g1,g6)
    c: PointOnObject(g2,g6)
    c: PointOnObject(g3,g6)
    c: PointOnObject(g4,g6)
    c: PointOnObject(g5,g6)
    c: Coincident(g6,g-1)
    c: Diameter(g6) = 7
    c: PointOnObject(g0,g-2)
    c: Coincident(g7,g8)
    c: Coincident(g8,g9)
    c: Coincident(g9,g10)
    c: Coincident(g10,g11)
    c: Coincident(g11,g12)
    c: Coincident(g12,g7)
    c: Equal(g7, g8-g12) x5
    c: PointOnObject(g7,g13)
    c: PointOnObject(g8,g13)
    c: PointOnObject(g9,g13)
    c: PointOnObject(g10,g13)
    c: PointOnObject(g11,g13)
    c: PointOnObject(g12,g13)
    c: PointOnObject(g13,g-1)
    c: Diameter(g13) = 7
    c: Distance(g6,g13) = 8
    c: Horizontal(g0,g10)
    c: Coincident(g14,g15)
    c: Coincident(g15,g16)
    c: Coincident(g16,g17)
    c: Coincident(g17,g18)
    c: Coincident(g18,g19)
    c: Coincident(g19,g14)
    c: Equal(g14, g15-g19) x5
    c: PointOnObject(g14,g20)
    c: PointOnObject(g15,g20)
    c: PointOnObject(g16,g20)
    c: PointOnObject(g17,g20)
    c: PointOnObject(g18,g20)
    c: PointOnObject(g19,g20)
    c: Diameter(g20) = 7
    c: DistanceY(g-1,g20) = 7
    c: Vertical(g18)
    c: Distance(g17,g-2) = 1
    c: Coincident(g21,g22)
    c: Coincident(g22,g23)
    c: Coincident(g23,g24)
    c: Coincident(g24,g25)
    c: Coincident(g25,g26)
    c: Coincident(g26,g21)
    c: Equal(g21, g22-g26) x5
    c: PointOnObject(g21,g27)
    c: PointOnObject(g22,g27)
    c: PointOnObject(g23,g27)
    c: PointOnObject(g24,g27)
    c: PointOnObject(g25,g27)
    c: PointOnObject(g26,g27)
    c: Diameter(g27) = 7
    c: DistanceY(g-1,g27) = 7
    c: DistanceX(g21,g-1) = 1
    c: Vertical(g21)
    c: Coincident(g28,g29)
    c: Coincident(g29,g30)
    c: Coincident(g30,g31)
    c: Coincident(g31,g32)
    c: Coincident(g32,g33)
    c: Coincident(g33,g28)
    c: Equal(g28, g29-g33) x5
    c: PointOnObject(g28,g34)
    c: PointOnObject(g29,g34)
    c: PointOnObject(g30,g34)
    c: PointOnObject(g31,g34)
    c: PointOnObject(g32,g34)
    c: PointOnObject(g33,g34)
    c: PointOnObject(g34,g-1)
    c: Diameter(g34) = 7
    c: Vertical(g31)
    c: DistanceX(g34,g-1) = 8
    c: Coincident(g35,g36)
    c: Coincident(g36,g37)
    c: Coincident(g37,g38)
    c: Coincident(g38,g39)
    c: Coincident(g39,g40)
    c: Coincident(g40,g35)
    c: Equal(g35, g36-g40) x5
    c: PointOnObject(g35,g41)
    c: PointOnObject(g36,g41)
    c: PointOnObject(g37,g41)
    c: PointOnObject(g38,g41)
    c: PointOnObject(g39,g41)
    c: PointOnObject(g40,g41)
    c: Coincident(g42,g43)
    c: Coincident(g43,g44)
    c: Coincident(g44,g45)
    c: Coincident(g45,g46)
    c: Coincident(g46,g47)
    c: Coincident(g47,g42)
    c: Equal(g42, g43-g47) x5
    c: PointOnObject(g42,g48)
    c: PointOnObject(g43,g48)
    c: PointOnObject(g44,g48)
    c: PointOnObject(g45,g48)
    c: PointOnObject(g46,g48)
    c: PointOnObject(g47,g48)
    c: Equal(g41,g48)
    c: Diameter(g41) = 7
    c: Vertical(g39)
    c: Vertical(g43)
    c: Distance(g-2,g39) = 1
    c: Symmetric(g38,g43,g-2)
    c: Distance(g41,g-1) = 7
FEATURE [Part::Extrusion] Extrude417  label="hex032"
  Base = -> Sketch425
  Dir = (0,-1,2e-16)
  DirMode = 2
  FaceMakerClass = Part::FaceMakerBullseye
  FaceMakerMode = 3
  LengthFwd = 10
  LengthRev = 0
  Placement = pos=(-56,0,-42) rot=(0,0,1;0rad)
  Solid = true
  Symmetric = false
FEATURE [Sketcher::SketchObject] Sketch426
  ArcFitTolerance = 1e-06
  FullyConstrained = true
  MakeInternals = false
  Placement = pos=(0,0,0) rot=(1,0,0;1.5708rad)
  sketch-geometry (49):
    g0: LineSegment StartX=1e-16 StartY=3.5 StartZ=0 EndX=-3.03109 EndY=1.75 EndZ=0
    g1: LineSegment StartX=-3.03109 StartY=1.75 StartZ=0 EndX=-3.03109 EndY=-1.75 EndZ=0
    g2: LineSegment StartX=-3.03109 StartY=-1.75 StartZ=0 EndX=-1e-16 EndY=-3.5 EndZ=0
    g3: LineSegment StartX=-1e-16 StartY=-3.5 StartZ=0 EndX=3.03109 EndY=-1.75 EndZ=0
    g4: LineSegment StartX=3.03109 StartY=-1.75 StartZ=0 EndX=3.03109 EndY=1.75 EndZ=0
    g5: LineSegment StartX=3.03109 StartY=1.75 StartZ=0 EndX=1e-16 EndY=3.5 EndZ=0
    g6: Circle [constr] CenterX=0 CenterY=0 CenterZ=0 NormalX=0 NormalY=0 NormalZ=1 AngleXU=0 Radius=3.5
    g7: LineSegment StartX=4.96892 StartY=-1.75002 StartZ=0 EndX=8.00002 EndY=-3.5 EndZ=0
    g8: LineSegment StartX=8.00002 StartY=-3.5 StartZ=0 EndX=11.0311 EndY=-1.74998 EndZ=0
    g9: LineSegment StartX=11.0311 StartY=-1.74998 StartZ=0 EndX=11.0311 EndY=1.75002 EndZ=0
    g10: LineSegment StartX=11.0311 StartY=1.75002 StartZ=0 EndX=7.99998 EndY=3.5 EndZ=0
    g11: LineSegment StartX=7.99998 StartY=3.5 StartZ=0 EndX=4.9689 EndY=1.74998 EndZ=0
    g12: LineSegment StartX=4.9689 StartY=1.74998 StartZ=0 EndX=4.96892 EndY=-1.75002 EndZ=0
    g13: Circle [constr] CenterX=8 CenterY=0 CenterZ=0 NormalX=0 NormalY=0 NormalZ=1 AngleXU=0 Radius=3.5
    g14: LineSegment StartX=4.03109 StartY=3.5 StartZ=0 EndX=7.06218 EndY=5.25 EndZ=0
    g15: LineSegment StartX=7.06218 StartY=5.25 StartZ=0 EndX=7.06218 EndY=8.75 EndZ=0
    g16: LineSegment StartX=7.06218 StartY=8.75 StartZ=0 EndX=4.03109 EndY=10.5 EndZ=0
    g17: LineSegment StartX=4.03109 StartY=10.5 StartZ=0 EndX=1 EndY=8.75 EndZ=0
    g18: LineSegment StartX=1 StartY=8.75 StartZ=0 EndX=1 EndY=5.25 EndZ=0
    g19: LineSegment StartX=1 StartY=5.25 StartZ=0 EndX=4.03109 EndY=3.5 EndZ=0
    g20: Circle [constr] CenterX=4.03109 CenterY=7 CenterZ=0 NormalX=0 NormalY=0 NormalZ=1 AngleXU=0 Radius=3.5
    g21: LineSegment StartX=-1 StartY=5.25 StartZ=0 EndX=-1 EndY=8.75 EndZ=0
    g22: LineSegment StartX=-1 StartY=8.75 StartZ=0 EndX=-4.03109 EndY=10.5 EndZ=0
    g23: LineSegment StartX=-4.03109 StartY=10.5 StartZ=0 EndX=-7.06218 EndY=8.75 EndZ=0
    g24: LineSegment StartX=-7.06218 StartY=8.75 StartZ=0 EndX=-7.06218 EndY=5.25 EndZ=0
    g25: LineSegment StartX=-7.06218 StartY=5.25 StartZ=0 EndX=-4.03109 EndY=3.5 EndZ=0
    g26: LineSegment StartX=-4.03109 StartY=3.5 StartZ=0 EndX=-1 EndY=5.25 EndZ=0
    g27: Circle [constr] CenterX=-4.03109 CenterY=7 CenterZ=0 NormalX=0 NormalY=0 NormalZ=1 AngleXU=0 Radius=3.5
    g28: LineSegment StartX=-4.96891 StartY=-1.75 StartZ=0 EndX=-4.96891 EndY=1.75 EndZ=0
    g29: LineSegment StartX=-4.96891 StartY=1.75 StartZ=0 EndX=-8 EndY=3.5 EndZ=0
    g30: LineSegment StartX=-8 StartY=3.5 StartZ=0 EndX=-11.0311 EndY=1.75 EndZ=0
    g31: LineSegment StartX=-11.0311 StartY=1.75 StartZ=0 EndX=-11.0311 EndY=-1.75 EndZ=0
    g32: LineSegment StartX=-11.0311 StartY=-1.75 StartZ=0 EndX=-8 EndY=-3.5 EndZ=0
    g33: LineSegment StartX=-8 StartY=-3.5 StartZ=0 EndX=-4.96891 EndY=-1.75 EndZ=0
    g34: Circle [constr] CenterX=-8 CenterY=0 CenterZ=0 NormalX=0 NormalY=0 NormalZ=1 AngleXU=0 Radius=3.5
    g35: LineSegment StartX=-4.03109 StartY=-3.5 StartZ=0 EndX=-7.06218 EndY=-5.25 EndZ=0
    g36: LineSegment StartX=-7.06218 StartY=-5.25 StartZ=0 EndX=-7.06218 EndY=-8.75 EndZ=0
    g37: LineSegment StartX=-7.06218 StartY=-8.75 StartZ=0 EndX=-4.03109 EndY=-10.5 EndZ=0
    g38: LineSegment StartX=-4.03109 StartY=-10.5 StartZ=0 EndX=-1 EndY=-8.75 EndZ=0
    g39: LineSegment StartX=-1 StartY=-8.75 StartZ=0 EndX=-1 EndY=-5.25 EndZ=0
    g40: LineSegment StartX=-1 StartY=-5.25 StartZ=0 EndX=-4.03109 EndY=-3.5 EndZ=0
    g41: Circle [constr] CenterX=-4.03109 CenterY=-7 CenterZ=0 NormalX=0 NormalY=0 NormalZ=1 AngleXU=0 Radius=3.5
    g42: LineSegment StartX=4.03109 StartY=-3.5 StartZ=0 EndX=1 EndY=-5.25 EndZ=0
    g43: LineSegment StartX=1 StartY=-5.25 StartZ=0 EndX=1 EndY=-8.75 EndZ=0
    g44: LineSegment StartX=1 StartY=-8.75 StartZ=0 EndX=4.03109 EndY=-10.5 EndZ=0
    g45: LineSegment StartX=4.03109 StartY=-10.5 StartZ=0 EndX=7.06218 EndY=-8.75 EndZ=0
    g46: LineSegment StartX=7.06218 StartY=-8.75 StartZ=0 EndX=7.06218 EndY=-5.25 EndZ=0
    g47: LineSegment StartX=7.06218 StartY=-5.25 StartZ=0 EndX=4.03109 EndY=-3.5 EndZ=0
    g48: Circle [constr] CenterX=4.03109 CenterY=-7 CenterZ=0 NormalX=0 NormalY=0 NormalZ=1 AngleXU=0 Radius=3.5
  constraints (117):
    c: Coincident(g0,g1)
    c: Coincident(g1,g2)
    c: Coincident(g2,g3)
    c: Coincident(g3,g4)
    c: Coincident(g4,g5)
    c: Coincident(g5,g0)
    c: Equal(g0, g1-g5) x5
    c: PointOnObject(g0,g6)
    c: PointOnObject(g1,g6)
    c: PointOnObject(g2,g6)
    c: PointOnObject(g3,g6)
    c: PointOnObject(g4,g6)
    c: PointOnObject(g5,g6)
    c: Coincident(g6,g-1)
    c: Diameter(g6) = 7
    c: PointOnObject(g0,g-2)
    c: Coincident(g7,g8)
    c: Coincident(g8,g9)
    c: Coincident(g9,g10)
    c: Coincident(g10,g11)
    c: Coincident(g11,g12)
    c: Coincident(g12,g7)
    c: Equal(g7, g8-g12) x5
    c: PointOnObject(g7,g13)
    c: PointOnObject(g8,g13)
    c: PointOnObject(g9,g13)
    c: PointOnObject(g10,g13)
    c: PointOnObject(g11,g13)
    c: PointOnObject(g12,g13)
    c: PointOnObject(g13,g-1)
    c: Diameter(g13) = 7
    c: Distance(g6,g13) = 8
    c: Horizontal(g0,g10)
    c: Coincident(g14,g15)
    c: Coincident(g15,g16)
    c: Coincident(g16,g17)
    c: Coincident(g17,g18)
    c: Coincident(g18,g19)
    c: Coincident(g19,g14)
    c: Equal(g14, g15-g19) x5
    c: PointOnObject(g14,g20)
    c: PointOnObject(g15,g20)
    c: PointOnObject(g16,g20)
    c: PointOnObject(g17,g20)
    c: PointOnObject(g18,g20)
    c: PointOnObject(g19,g20)
    c: Diameter(g20) = 7
    c: DistanceY(g-1,g20) = 7
    c: Vertical(g18)
    c: Distance(g17,g-2) = 1
    c: Coincident(g21,g22)
    c: Coincident(g22,g23)
    c: Coincident(g23,g24)
    c: Coincident(g24,g25)
    c: Coincident(g25,g26)
    c: Coincident(g26,g21)
    c: Equal(g21, g22-g26) x5
    c: PointOnObject(g21,g27)
    c: PointOnObject(g22,g27)
    c: PointOnObject(g23,g27)
    c: PointOnObject(g24,g27)
    c: PointOnObject(g25,g27)
    c: PointOnObject(g26,g27)
    c: Diameter(g27) = 7
    c: DistanceY(g-1,g27) = 7
    c: DistanceX(g21,g-1) = 1
    c: Vertical(g21)
    c: Coincident(g28,g29)
    c: Coincident(g29,g30)
    c: Coincident(g30,g31)
    c: Coincident(g31,g32)
    c: Coincident(g32,g33)
    c: Coincident(g33,g28)
    c: Equal(g28, g29-g33) x5
    c: PointOnObject(g28,g34)
    c: PointOnObject(g29,g34)
    c: PointOnObject(g30,g34)
    c: PointOnObject(g31,g34)
    c: PointOnObject(g32,g34)
    c: PointOnObject(g33,g34)
    c: PointOnObject(g34,g-1)
    c: Diameter(g34) = 7
    c: Vertical(g31)
    c: DistanceX(g34,g-1) = 8
    c: Coincident(g35,g36)
    c: Coincident(g36,g37)
    c: Coincident(g37,g38)
    c: Coincident(g38,g39)
    c: Coincident(g39,g40)
    c: Coincident(g40,g35)
    c: Equal(g35, g36-g40) x5
    c: PointOnObject(g35,g41)
    c: PointOnObject(g36,g41)
    c: PointOnObject(g37,g41)
    c: PointOnObject(g38,g41)
    c: PointOnObject(g39,g41)
    c: PointOnObject(g40,g41)
    c: Coincident(g42,g43)
    c: Coincident(g43,g44)
    c: Coincident(g44,g45)
    c: Coincident(g45,g46)
    c: Coincident(g46,g47)
    c: Coincident(g47,g42)
    c: Equal(g42, g43-g47) x5
    c: PointOnObject(g42,g48)
    c: PointOnObject(g43,g48)
    c: PointOnObject(g44,g48)
    c: PointOnObject(g45,g48)
    c: PointOnObject(g46,g48)
    c: PointOnObject(g47,g48)
    c: Equal(g41,g48)
    c: Diameter(g41) = 7
    c: Vertical(g39)
    c: Vertical(g43)
    c: Distance(g-2,g39) = 1
    c: Symmetric(g38,g43,g-2)
    c: Distance(g41,g-1) = 7
FEATURE [Part::Extrusion] Extrude418  label="hex033"
  Base = -> Sketch426
  Dir = (0,-1,2e-16)
  DirMode = 2
  FaceMakerClass = Part::FaceMakerBullseye
  FaceMakerMode = 3
  LengthFwd = 10
  LengthRev = 0
  Placement = pos=(-40,0,-56) rot=(0,0,1;0rad)
  Solid = true
  Symmetric = false
FEATURE [Sketcher::SketchObject] Sketch427
  ArcFitTolerance = 1e-06
  FullyConstrained = true
  MakeInternals = false
  Placement = pos=(0,0,0) rot=(1,0,0;1.5708rad)
  sketch-geometry (49):
    g0: LineSegment StartX=1e-16 StartY=3.5 StartZ=0 EndX=-3.03109 EndY=1.75 EndZ=0
    g1: LineSegment StartX=-3.03109 StartY=1.75 StartZ=0 EndX=-3.03109 EndY=-1.75 EndZ=0
    g2: LineSegment StartX=-3.03109 StartY=-1.75 StartZ=0 EndX=-1e-16 EndY=-3.5 EndZ=0
    g3: LineSegment StartX=-1e-16 StartY=-3.5 StartZ=0 EndX=3.03109 EndY=-1.75 EndZ=0
    g4: LineSegment StartX=3.03109 StartY=-1.75 StartZ=0 EndX=3.03109 EndY=1.75 EndZ=0
    g5: LineSegment StartX=3.03109 StartY=1.75 StartZ=0 EndX=1e-16 EndY=3.5 EndZ=0
    g6: Circle [constr] CenterX=0 CenterY=0 CenterZ=0 NormalX=0 NormalY=0 NormalZ=1 AngleXU=0 Radius=3.5
    g7: LineSegment StartX=4.96892 StartY=-1.75002 StartZ=0 EndX=8.00002 EndY=-3.5 EndZ=0
    g8: LineSegment StartX=8.00002 StartY=-3.5 StartZ=0 EndX=11.0311 EndY=-1.74998 EndZ=0
    g9: LineSegment StartX=11.0311 StartY=-1.74998 StartZ=0 EndX=11.0311 EndY=1.75002 EndZ=0
    g10: LineSegment StartX=11.0311 StartY=1.75002 StartZ=0 EndX=7.99998 EndY=3.5 EndZ=0
    g11: LineSegment StartX=7.99998 StartY=3.5 StartZ=0 EndX=4.9689 EndY=1.74998 EndZ=0
    g12: LineSegment StartX=4.9689 StartY=1.74998 StartZ=0 EndX=4.96892 EndY=-1.75002 EndZ=0
    g13: Circle [constr] CenterX=8 CenterY=0 CenterZ=0 NormalX=0 NormalY=0 NormalZ=1 AngleXU=0 Radius=3.5
    g14: LineSegment StartX=4.03109 StartY=3.5 StartZ=0 EndX=7.06218 EndY=5.25 EndZ=0
    g15: LineSegment StartX=7.06218 StartY=5.25 StartZ=0 EndX=7.06218 EndY=8.75 EndZ=0
    g16: LineSegment StartX=7.06218 StartY=8.75 StartZ=0 EndX=4.03109 EndY=10.5 EndZ=0
    g17: LineSegment StartX=4.03109 StartY=10.5 StartZ=0 EndX=1 EndY=8.75 EndZ=0
    g18: LineSegment StartX=1 StartY=8.75 StartZ=0 EndX=1 EndY=5.25 EndZ=0
    g19: LineSegment StartX=1 StartY=5.25 StartZ=0 EndX=4.03109 EndY=3.5 EndZ=0
    g20: Circle [constr] CenterX=4.03109 CenterY=7 CenterZ=0 NormalX=0 NormalY=0 NormalZ=1 AngleXU=0 Radius=3.5
    g21: LineSegment StartX=-1 StartY=5.25 StartZ=0 EndX=-1 EndY=8.75 EndZ=0
    g22: LineSegment StartX=-1 StartY=8.75 StartZ=0 EndX=-4.03109 EndY=10.5 EndZ=0
    g23: LineSegment StartX=-4.03109 StartY=10.5 StartZ=0 EndX=-7.06218 EndY=8.75 EndZ=0
    g24: LineSegment StartX=-7.06218 StartY=8.75 StartZ=0 EndX=-7.06218 EndY=5.25 EndZ=0
    g25: LineSegment StartX=-7.06218 StartY=5.25 StartZ=0 EndX=-4.03109 EndY=3.5 EndZ=0
    g26: LineSegment StartX=-4.03109 StartY=3.5 StartZ=0 EndX=-1 EndY=5.25 EndZ=0
    g27: Circle [constr] CenterX=-4.03109 CenterY=7 CenterZ=0 NormalX=0 NormalY=0 NormalZ=1 AngleXU=0 Radius=3.5
    g28: LineSegment StartX=-4.96891 StartY=-1.75 StartZ=0 EndX=-4.96891 EndY=1.75 EndZ=0
    g29: LineSegment StartX=-4.96891 StartY=1.75 StartZ=0 EndX=-8 EndY=3.5 EndZ=0
    g30: LineSegment StartX=-8 StartY=3.5 StartZ=0 EndX=-11.0311 EndY=1.75 EndZ=0
    g31: LineSegment StartX=-11.0311 StartY=1.75 StartZ=0 EndX=-11.0311 EndY=-1.75 EndZ=0
    g32: LineSegment StartX=-11.0311 StartY=-1.75 StartZ=0 EndX=-8 EndY=-3.5 EndZ=0
    g33: LineSegment StartX=-8 StartY=-3.5 StartZ=0 EndX=-4.96891 EndY=-1.75 EndZ=0
    g34: Circle [constr] CenterX=-8 CenterY=0 CenterZ=0 NormalX=0 NormalY=0 NormalZ=1 AngleXU=0 Radius=3.5
    g35: LineSegment StartX=-4.03109 StartY=-3.5 StartZ=0 EndX=-7.06218 EndY=-5.25 EndZ=0
    g36: LineSegment StartX=-7.06218 StartY=-5.25 StartZ=0 EndX=-7.06218 EndY=-8.75 EndZ=0
    g37: LineSegment StartX=-7.06218 StartY=-8.75 StartZ=0 EndX=-4.03109 EndY=-10.5 EndZ=0
    g38: LineSegment StartX=-4.03109 StartY=-10.5 StartZ=0 EndX=-1 EndY=-8.75 EndZ=0
    g39: LineSegment StartX=-1 StartY=-8.75 StartZ=0 EndX=-1 EndY=-5.25 EndZ=0
    g40: LineSegment StartX=-1 StartY=-5.25 StartZ=0 EndX=-4.03109 EndY=-3.5 EndZ=0
    g41: Circle [constr] CenterX=-4.03109 CenterY=-7 CenterZ=0 NormalX=0 NormalY=0 NormalZ=1 AngleXU=0 Radius=3.5
    g42: LineSegment StartX=4.03109 StartY=-3.5 StartZ=0 EndX=1 EndY=-5.25 EndZ=0
    g43: LineSegment StartX=1 StartY=-5.25 StartZ=0 EndX=1 EndY=-8.75 EndZ=0
    g44: LineSegment StartX=1 StartY=-8.75 StartZ=0 EndX=4.03109 EndY=-10.5 EndZ=0
    g45: LineSegment StartX=4.03109 StartY=-10.5 StartZ=0 EndX=7.06218 EndY=-8.75 EndZ=0
    g46: LineSegment StartX=7.06218 StartY=-8.75 StartZ=0 EndX=7.06218 EndY=-5.25 EndZ=0
    g47: LineSegment StartX=7.06218 StartY=-5.25 StartZ=0 EndX=4.03109 EndY=-3.5 EndZ=0
    g48: Circle [constr] CenterX=4.03109 CenterY=-7 CenterZ=0 NormalX=0 NormalY=0 NormalZ=1 AngleXU=0 Radius=3.5
  constraints (117):
    c: Coincident(g0,g1)
    c: Coincident(g1,g2)
    c: Coincident(g2,g3)
    c: Coincident(g3,g4)
    c: Coincident(g4,g5)
    c: Coincident(g5,g0)
    c: Equal(g0, g1-g5) x5
    c: PointOnObject(g0,g6)
    c: PointOnObject(g1,g6)
    c: PointOnObject(g2,g6)
    c: PointOnObject(g3,g6)
    c: PointOnObject(g4,g6)
    c: PointOnObject(g5,g6)
    c: Coincident(g6,g-1)
    c: Diameter(g6) = 7
    c: PointOnObject(g0,g-2)
    c: Coincident(g7,g8)
    c: Coincident(g8,g9)
    c: Coincident(g9,g10)
    c: Coincident(g10,g11)
    c: Coincident(g11,g12)
    c: Coincident(g12,g7)
    c: Equal(g7, g8-g12) x5
    c: PointOnObject(g7,g13)
    c: PointOnObject(g8,g13)
    c: PointOnObject(g9,g13)
    c: PointOnObject(g10,g13)
    c: PointOnObject(g11,g13)
    c: PointOnObject(g12,g13)
    c: PointOnObject(g13,g-1)
    c: Diameter(g13) = 7
    c: Distance(g6,g13) = 8
    c: Horizontal(g0,g10)
    c: Coincident(g14,g15)
    c: Coincident(g15,g16)
    c: Coincident(g16,g17)
    c: Coincident(g17,g18)
    c: Coincident(g18,g19)
    c: Coincident(g19,g14)
    c: Equal(g14, g15-g19) x5
    c: PointOnObject(g14,g20)
    c: PointOnObject(g15,g20)
    c: PointOnObject(g16,g20)
    c: PointOnObject(g17,g20)
    c: PointOnObject(g18,g20)
    c: PointOnObject(g19,g20)
    c: Diameter(g20) = 7
    c: DistanceY(g-1,g20) = 7
    c: Vertical(g18)
    c: Distance(g17,g-2) = 1
    c: Coincident(g21,g22)
    c: Coincident(g22,g23)
    c: Coincident(g23,g24)
    c: Coincident(g24,g25)
    c: Coincident(g25,g26)
    c: Coincident(g26,g21)
    c: Equal(g21, g22-g26) x5
    c: PointOnObject(g21,g27)
    c: PointOnObject(g22,g27)
    c: PointOnObject(g23,g27)
    c: PointOnObject(g24,g27)
    c: PointOnObject(g25,g27)
    c: PointOnObject(g26,g27)
    c: Diameter(g27) = 7
    c: DistanceY(g-1,g27) = 7
    c: DistanceX(g21,g-1) = 1
    c: Vertical(g21)
    c: Coincident(g28,g29)
    c: Coincident(g29,g30)
    c: Coincident(g30,g31)
    c: Coincident(g31,g32)
    c: Coincident(g32,g33)
    c: Coincident(g33,g28)
    c: Equal(g28, g29-g33) x5
    c: PointOnObject(g28,g34)
    c: PointOnObject(g29,g34)
    c: PointOnObject(g30,g34)
    c: PointOnObject(g31,g34)
    c: PointOnObject(g32,g34)
    c: PointOnObject(g33,g34)
    c: PointOnObject(g34,g-1)
    c: Diameter(g34) = 7
    c: Vertical(g31)
    c: DistanceX(g34,g-1) = 8
    c: Coincident(g35,g36)
    c: Coincident(g36,g37)
    c: Coincident(g37,g38)
    c: Coincident(g38,g39)
    c: Coincident(g39,g40)
    c: Coincident(g40,g35)
    c: Equal(g35, g36-g40) x5
    c: PointOnObject(g35,g41)
    c: PointOnObject(g36,g41)
    c: PointOnObject(g37,g41)
    c: PointOnObject(g38,g41)
    c: PointOnObject(g39,g41)
    c: PointOnObject(g40,g41)
    c: Coincident(g42,g43)
    c: Coincident(g43,g44)
    c: Coincident(g44,g45)
    c: Coincident(g45,g46)
    c: Coincident(g46,g47)
    c: Coincident(g47,g42)
    c: Equal(g42, g43-g47) x5
    c: PointOnObject(g42,g48)
    c: PointOnObject(g43,g48)
    c: PointOnObject(g44,g48)
    c: PointOnObject(g45,g48)
    c: PointOnObject(g46,g48)
    c: PointOnObject(g47,g48)
    c: Equal(g41,g48)
    c: Diameter(g41) = 7
    c: Vertical(g39)
    c: Vertical(g43)
    c: Distance(g-2,g39) = 1
    c: Symmetric(g38,g43,g-2)
    c: Distance(g41,g-1) = 7
FEATURE [Part::Extrusion] Extrude419  label="hex034"
  Base = -> Sketch427
  Dir = (0,-1,2e-16)
  DirMode = 2
  FaceMakerClass = Part::FaceMakerBullseye
  FaceMakerMode = 3
  LengthFwd = 10
  LengthRev = 0
  Placement = pos=(-16,0,-56) rot=(0,0,1;0rad)
  Solid = true
  Symmetric = false
FEATURE [Sketcher::SketchObject] Sketch428
  ArcFitTolerance = 1e-06
  FullyConstrained = true
  MakeInternals = false
  Placement = pos=(0,0,0) rot=(1,0,0;1.5708rad)
  sketch-geometry (49):
    g0: LineSegment StartX=1e-16 StartY=3.5 StartZ=0 EndX=-3.03109 EndY=1.75 EndZ=0
    g1: LineSegment StartX=-3.03109 StartY=1.75 StartZ=0 EndX=-3.03109 EndY=-1.75 EndZ=0
    g2: LineSegment StartX=-3.03109 StartY=-1.75 StartZ=0 EndX=-1e-16 EndY=-3.5 EndZ=0
    g3: LineSegment StartX=-1e-16 StartY=-3.5 StartZ=0 EndX=3.03109 EndY=-1.75 EndZ=0
    g4: LineSegment StartX=3.03109 StartY=-1.75 StartZ=0 EndX=3.03109 EndY=1.75 EndZ=0
    g5: LineSegment StartX=3.03109 StartY=1.75 StartZ=0 EndX=1e-16 EndY=3.5 EndZ=0
    g6: Circle [constr] CenterX=0 CenterY=0 CenterZ=0 NormalX=0 NormalY=0 NormalZ=1 AngleXU=0 Radius=3.5
    g7: LineSegment StartX=4.96892 StartY=-1.75002 StartZ=0 EndX=8.00002 EndY=-3.5 EndZ=0
    g8: LineSegment StartX=8.00002 StartY=-3.5 StartZ=0 EndX=11.0311 EndY=-1.74998 EndZ=0
    g9: LineSegment StartX=11.0311 StartY=-1.74998 StartZ=0 EndX=11.0311 EndY=1.75002 EndZ=0
    g10: LineSegment StartX=11.0311 StartY=1.75002 StartZ=0 EndX=7.99998 EndY=3.5 EndZ=0
    g11: LineSegment StartX=7.99998 StartY=3.5 StartZ=0 EndX=4.9689 EndY=1.74998 EndZ=0
    g12: LineSegment StartX=4.9689 StartY=1.74998 StartZ=0 EndX=4.96892 EndY=-1.75002 EndZ=0
    g13: Circle [constr] CenterX=8 CenterY=0 CenterZ=0 NormalX=0 NormalY=0 NormalZ=1 AngleXU=0 Radius=3.5
    g14: LineSegment StartX=4.03109 StartY=3.5 StartZ=0 EndX=7.06218 EndY=5.25 EndZ=0
    g15: LineSegment StartX=7.06218 StartY=5.25 StartZ=0 EndX=7.06218 EndY=8.75 EndZ=0
    g16: LineSegment StartX=7.06218 StartY=8.75 StartZ=0 EndX=4.03109 EndY=10.5 EndZ=0
    g17: LineSegment StartX=4.03109 StartY=10.5 StartZ=0 EndX=1 EndY=8.75 EndZ=0
    g18: LineSegment StartX=1 StartY=8.75 StartZ=0 EndX=1 EndY=5.25 EndZ=0
    g19: LineSegment StartX=1 StartY=5.25 StartZ=0 EndX=4.03109 EndY=3.5 EndZ=0
    g20: Circle [constr] CenterX=4.03109 CenterY=7 CenterZ=0 NormalX=0 NormalY=0 NormalZ=1 AngleXU=0 Radius=3.5
    g21: LineSegment StartX=-1 StartY=5.25 StartZ=0 EndX=-1 EndY=8.75 EndZ=0
    g22: LineSegment StartX=-1 StartY=8.75 StartZ=0 EndX=-4.03109 EndY=10.5 EndZ=0
    g23: LineSegment StartX=-4.03109 StartY=10.5 StartZ=0 EndX=-7.06218 EndY=8.75 EndZ=0
    g24: LineSegment StartX=-7.06218 StartY=8.75 StartZ=0 EndX=-7.06218 EndY=5.25 EndZ=0
    g25: LineSegment StartX=-7.06218 StartY=5.25 StartZ=0 EndX=-4.03109 EndY=3.5 EndZ=0
    g26: LineSegment StartX=-4.03109 StartY=3.5 StartZ=0 EndX=-1 EndY=5.25 EndZ=0
    g27: Circle [constr] CenterX=-4.03109 CenterY=7 CenterZ=0 NormalX=0 NormalY=0 NormalZ=1 AngleXU=0 Radius=3.5
    g28: LineSegment StartX=-4.96891 StartY=-1.75 StartZ=0 EndX=-4.96891 EndY=1.75 EndZ=0
    g29: LineSegment StartX=-4.96891 StartY=1.75 StartZ=0 EndX=-8 EndY=3.5 EndZ=0
    g30: LineSegment StartX=-8 StartY=3.5 StartZ=0 EndX=-11.0311 EndY=1.75 EndZ=0
    g31: LineSegment StartX=-11.0311 StartY=1.75 StartZ=0 EndX=-11.0311 EndY=-1.75 EndZ=0
    g32: LineSegment StartX=-11.0311 StartY=-1.75 StartZ=0 EndX=-8 EndY=-3.5 EndZ=0
    g33: LineSegment StartX=-8 StartY=-3.5 StartZ=0 EndX=-4.96891 EndY=-1.75 EndZ=0
    g34: Circle [constr] CenterX=-8 CenterY=0 CenterZ=0 NormalX=0 NormalY=0 NormalZ=1 AngleXU=0 Radius=3.5
    g35: LineSegment StartX=-4.03109 StartY=-3.5 StartZ=0 EndX=-7.06218 EndY=-5.25 EndZ=0
    g36: LineSegment StartX=-7.06218 StartY=-5.25 StartZ=0 EndX=-7.06218 EndY=-8.75 EndZ=0
    g37: LineSegment StartX=-7.06218 StartY=-8.75 StartZ=0 EndX=-4.03109 EndY=-10.5 EndZ=0
    g38: LineSegment StartX=-4.03109 StartY=-10.5 StartZ=0 EndX=-1 EndY=-8.75 EndZ=0
    g39: LineSegment StartX=-1 StartY=-8.75 StartZ=0 EndX=-1 EndY=-5.25 EndZ=0
    g40: LineSegment StartX=-1 StartY=-5.25 StartZ=0 EndX=-4.03109 EndY=-3.5 EndZ=0
    g41: Circle [constr] CenterX=-4.03109 CenterY=-7 CenterZ=0 NormalX=0 NormalY=0 NormalZ=1 AngleXU=0 Radius=3.5
    g42: LineSegment StartX=4.03109 StartY=-3.5 StartZ=0 EndX=1 EndY=-5.25 EndZ=0
    g43: LineSegment StartX=1 StartY=-5.25 StartZ=0 EndX=1 EndY=-8.75 EndZ=0
    g44: LineSegment StartX=1 StartY=-8.75 StartZ=0 EndX=4.03109 EndY=-10.5 EndZ=0
    g45: LineSegment StartX=4.03109 StartY=-10.5 StartZ=0 EndX=7.06218 EndY=-8.75 EndZ=0
    g46: LineSegment StartX=7.06218 StartY=-8.75 StartZ=0 EndX=7.06218 EndY=-5.25 EndZ=0
    g47: LineSegment StartX=7.06218 StartY=-5.25 StartZ=0 EndX=4.03109 EndY=-3.5 EndZ=0
    g48: Circle [constr] CenterX=4.03109 CenterY=-7 CenterZ=0 NormalX=0 NormalY=0 NormalZ=1 AngleXU=0 Radius=3.5
  constraints (117):
    c: Coincident(g0,g1)
    c: Coincident(g1,g2)
    c: Coincident(g2,g3)
    c: Coincident(g3,g4)
    c: Coincident(g4,g5)
    c: Coincident(g5,g0)
    c: Equal(g0, g1-g5) x5
    c: PointOnObject(g0,g6)
    c: PointOnObject(g1,g6)
    c: PointOnObject(g2,g6)
    c: PointOnObject(g3,g6)
    c: PointOnObject(g4,g6)
    c: PointOnObject(g5,g6)
    c: Coincident(g6,g-1)
    c: Diameter(g6) = 7
    c: PointOnObject(g0,g-2)
    c: Coincident(g7,g8)
    c: Coincident(g8,g9)
    c: Coincident(g9,g10)
    c: Coincident(g10,g11)
    c: Coincident(g11,g12)
    c: Coincident(g12,g7)
    c: Equal(g7, g8-g12) x5
    c: PointOnObject(g7,g13)
    c: PointOnObject(g8,g13)
    c: PointOnObject(g9,g13)
    c: PointOnObject(g10,g13)
    c: PointOnObject(g11,g13)
    c: PointOnObject(g12,g13)
    c: PointOnObject(g13,g-1)
    c: Diameter(g13) = 7
    c: Distance(g6,g13) = 8
    c: Horizontal(g0,g10)
    c: Coincident(g14,g15)
    c: Coincident(g15,g16)
    c: Coincident(g16,g17)
    c: Coincident(g17,g18)
    c: Coincident(g18,g19)
    c: Coincident(g19,g14)
    c: Equal(g14, g15-g19) x5
    c: PointOnObject(g14,g20)
    c: PointOnObject(g15,g20)
    c: PointOnObject(g16,g20)
    c: PointOnObject(g17,g20)
    c: PointOnObject(g18,g20)
    c: PointOnObject(g19,g20)
    c: Diameter(g20) = 7
    c: DistanceY(g-1,g20) = 7
    c: Vertical(g18)
    c: Distance(g17,g-2) = 1
    c: Coincident(g21,g22)
    c: Coincident(g22,g23)
    c: Coincident(g23,g24)
    c: Coincident(g24,g25)
    c: Coincident(g25,g26)
    c: Coincident(g26,g21)
    c: Equal(g21, g22-g26) x5
    c: PointOnObject(g21,g27)
    c: PointOnObject(g22,g27)
    c: PointOnObject(g23,g27)
    c: PointOnObject(g24,g27)
    c: PointOnObject(g25,g27)
    c: PointOnObject(g26,g27)
    c: Diameter(g27) = 7
    c: DistanceY(g-1,g27) = 7
    c: DistanceX(g21,g-1) = 1
    c: Vertical(g21)
    c: Coincident(g28,g29)
    c: Coincident(g29,g30)
    c: Coincident(g30,g31)
    c: Coincident(g31,g32)
    c: Coincident(g32,g33)
    c: Coincident(g33,g28)
    c: Equal(g28, g29-g33) x5
    c: PointOnObject(g28,g34)
    c: PointOnObject(g29,g34)
    c: PointOnObject(g30,g34)
    c: PointOnObject(g31,g34)
    c: PointOnObject(g32,g34)
    c: PointOnObject(g33,g34)
    c: PointOnObject(g34,g-1)
    c: Diameter(g34) = 7
    c: Vertical(g31)
    c: DistanceX(g34,g-1) = 8
    c: Coincident(g35,g36)
    c: Coincident(g36,g37)
    c: Coincident(g37,g38)
    c: Coincident(g38,g39)
    c: Coincident(g39,g40)
    c: Coincident(g40,g35)
    c: Equal(g35, g36-g40) x5
    c: PointOnObject(g35,g41)
    c: PointOnObject(g36,g41)
    c: PointOnObject(g37,g41)
    c: PointOnObject(g38,g41)
    c: PointOnObject(g39,g41)
    c: PointOnObject(g40,g41)
    c: Coincident(g42,g43)
    c: Coincident(g43,g44)
    c: Coincident(g44,g45)
    c: Coincident(g45,g46)
    c: Coincident(g46,g47)
    c: Coincident(g47,g42)
    c: Equal(g42, g43-g47) x5
    c: PointOnObject(g42,g48)
    c: PointOnObject(g43,g48)
    c: PointOnObject(g44,g48)
    c: PointOnObject(g45,g48)
    c: PointOnObject(g46,g48)
    c: PointOnObject(g47,g48)
    c: Equal(g41,g48)
    c: Diameter(g41) = 7
    c: Vertical(g39)
    c: Vertical(g43)
    c: Distance(g-2,g39) = 1
    c: Symmetric(g38,g43,g-2)
    c: Distance(g41,g-1) = 7
FEATURE [Part::Extrusion] Extrude420  label="hex035"
  Base = -> Sketch428
  Dir = (0,-1,2e-16)
  DirMode = 2
  FaceMakerClass = Part::FaceMakerBullseye
  FaceMakerMode = 3
  LengthFwd = 10
  LengthRev = 0
  Placement = pos=(8,0,-56) rot=(0,0,1;0rad)
  Solid = true
  Symmetric = false
FEATURE [Sketcher::SketchObject] Sketch429
  ArcFitTolerance = 1e-06
  FullyConstrained = true
  MakeInternals = false
  Placement = pos=(0,0,0) rot=(1,0,0;1.5708rad)
  sketch-geometry (49):
    g0: LineSegment StartX=1e-16 StartY=3.5 StartZ=0 EndX=-3.03109 EndY=1.75 EndZ=0
    g1: LineSegment StartX=-3.03109 StartY=1.75 StartZ=0 EndX=-3.03109 EndY=-1.75 EndZ=0
    g2: LineSegment StartX=-3.03109 StartY=-1.75 StartZ=0 EndX=-1e-16 EndY=-3.5 EndZ=0
    g3: LineSegment StartX=-1e-16 StartY=-3.5 StartZ=0 EndX=3.03109 EndY=-1.75 EndZ=0
    g4: LineSegment StartX=3.03109 StartY=-1.75 StartZ=0 EndX=3.03109 EndY=1.75 EndZ=0
    g5: LineSegment StartX=3.03109 StartY=1.75 StartZ=0 EndX=1e-16 EndY=3.5 EndZ=0
    g6: Circle [constr] CenterX=0 CenterY=0 CenterZ=0 NormalX=0 NormalY=0 NormalZ=1 AngleXU=0 Radius=3.5
    g7: LineSegment StartX=4.96892 StartY=-1.75002 StartZ=0 EndX=8.00002 EndY=-3.5 EndZ=0
    g8: LineSegment StartX=8.00002 StartY=-3.5 StartZ=0 EndX=11.0311 EndY=-1.74998 EndZ=0
    g9: LineSegment StartX=11.0311 StartY=-1.74998 StartZ=0 EndX=11.0311 EndY=1.75002 EndZ=0
    g10: LineSegment StartX=11.0311 StartY=1.75002 StartZ=0 EndX=7.99998 EndY=3.5 EndZ=0
    g11: LineSegment StartX=7.99998 StartY=3.5 StartZ=0 EndX=4.9689 EndY=1.74998 EndZ=0
    g12: LineSegment StartX=4.9689 StartY=1.74998 StartZ=0 EndX=4.96892 EndY=-1.75002 EndZ=0
    g13: Circle [constr] CenterX=8 CenterY=0 CenterZ=0 NormalX=0 NormalY=0 NormalZ=1 AngleXU=0 Radius=3.5
    g14: LineSegment StartX=4.03109 StartY=3.5 StartZ=0 EndX=7.06218 EndY=5.25 EndZ=0
    g15: LineSegment StartX=7.06218 StartY=5.25 StartZ=0 EndX=7.06218 EndY=8.75 EndZ=0
    g16: LineSegment StartX=7.06218 StartY=8.75 StartZ=0 EndX=4.03109 EndY=10.5 EndZ=0
    g17: LineSegment StartX=4.03109 StartY=10.5 StartZ=0 EndX=1 EndY=8.75 EndZ=0
    g18: LineSegment StartX=1 StartY=8.75 StartZ=0 EndX=1 EndY=5.25 EndZ=0
    g19: LineSegment StartX=1 StartY=5.25 StartZ=0 EndX=4.03109 EndY=3.5 EndZ=0
    g20: Circle [constr] CenterX=4.03109 CenterY=7 CenterZ=0 NormalX=0 NormalY=0 NormalZ=1 AngleXU=0 Radius=3.5
    g21: LineSegment StartX=-1 StartY=5.25 StartZ=0 EndX=-1 EndY=8.75 EndZ=0
    g22: LineSegment StartX=-1 StartY=8.75 StartZ=0 EndX=-4.03109 EndY=10.5 EndZ=0
    g23: LineSegment StartX=-4.03109 StartY=10.5 StartZ=0 EndX=-7.06218 EndY=8.75 EndZ=0
    g24: LineSegment StartX=-7.06218 StartY=8.75 StartZ=0 EndX=-7.06218 EndY=5.25 EndZ=0
    g25: LineSegment StartX=-7.06218 StartY=5.25 StartZ=0 EndX=-4.03109 EndY=3.5 EndZ=0
    g26: LineSegment StartX=-4.03109 StartY=3.5 StartZ=0 EndX=-1 EndY=5.25 EndZ=0
    g27: Circle [constr] CenterX=-4.03109 CenterY=7 CenterZ=0 NormalX=0 NormalY=0 NormalZ=1 AngleXU=0 Radius=3.5
    g28: LineSegment StartX=-4.96891 StartY=-1.75 StartZ=0 EndX=-4.96891 EndY=1.75 EndZ=0
    g29: LineSegment StartX=-4.96891 StartY=1.75 StartZ=0 EndX=-8 EndY=3.5 EndZ=0
    g30: LineSegment StartX=-8 StartY=3.5 StartZ=0 EndX=-11.0311 EndY=1.75 EndZ=0
    g31: LineSegment StartX=-11.0311 StartY=1.75 StartZ=0 EndX=-11.0311 EndY=-1.75 EndZ=0
    g32: LineSegment StartX=-11.0311 StartY=-1.75 StartZ=0 EndX=-8 EndY=-3.5 EndZ=0
    g33: LineSegment StartX=-8 StartY=-3.5 StartZ=0 EndX=-4.96891 EndY=-1.75 EndZ=0
    g34: Circle [constr] CenterX=-8 CenterY=0 CenterZ=0 NormalX=0 NormalY=0 NormalZ=1 AngleXU=0 Radius=3.5
    g35: LineSegment StartX=-4.03109 StartY=-3.5 StartZ=0 EndX=-7.06218 EndY=-5.25 EndZ=0
    g36: LineSegment StartX=-7.06218 StartY=-5.25 StartZ=0 EndX=-7.06218 EndY=-8.75 EndZ=0
    g37: LineSegment StartX=-7.06218 StartY=-8.75 StartZ=0 EndX=-4.03109 EndY=-10.5 EndZ=0
    g38: LineSegment StartX=-4.03109 StartY=-10.5 StartZ=0 EndX=-1 EndY=-8.75 EndZ=0
    g39: LineSegment StartX=-1 StartY=-8.75 StartZ=0 EndX=-1 EndY=-5.25 EndZ=0
    g40: LineSegment StartX=-1 StartY=-5.25 StartZ=0 EndX=-4.03109 EndY=-3.5 EndZ=0
    g41: Circle [constr] CenterX=-4.03109 CenterY=-7 CenterZ=0 NormalX=0 NormalY=0 NormalZ=1 AngleXU=0 Radius=3.5
    g42: LineSegment StartX=4.03109 StartY=-3.5 StartZ=0 EndX=1 EndY=-5.25 EndZ=0
    g43: LineSegment StartX=1 StartY=-5.25 StartZ=0 EndX=1 EndY=-8.75 EndZ=0
    g44: LineSegment StartX=1 StartY=-8.75 StartZ=0 EndX=4.03109 EndY=-10.5 EndZ=0
    g45: LineSegment StartX=4.03109 StartY=-10.5 StartZ=0 EndX=7.06218 EndY=-8.75 EndZ=0
    g46: LineSegment StartX=7.06218 StartY=-8.75 StartZ=0 EndX=7.06218 EndY=-5.25 EndZ=0
    g47: LineSegment StartX=7.06218 StartY=-5.25 StartZ=0 EndX=4.03109 EndY=-3.5 EndZ=0
    g48: Circle [constr] CenterX=4.03109 CenterY=-7 CenterZ=0 NormalX=0 NormalY=0 NormalZ=1 AngleXU=0 Radius=3.5
  constraints (117):
    c: Coincident(g0,g1)
    c: Coincident(g1,g2)
    c: Coincident(g2,g3)
    c: Coincident(g3,g4)
    c: Coincident(g4,g5)
    c: Coincident(g5,g0)
    c: Equal(g0, g1-g5) x5
    c: PointOnObject(g0,g6)
    c: PointOnObject(g1,g6)
    c: PointOnObject(g2,g6)
    c: PointOnObject(g3,g6)
    c: PointOnObject(g4,g6)
    c: PointOnObject(g5,g6)
    c: Coincident(g6,g-1)
    c: Diameter(g6) = 7
    c: PointOnObject(g0,g-2)
    c: Coincident(g7,g8)
    c: Coincident(g8,g9)
    c: Coincident(g9,g10)
    c: Coincident(g10,g11)
    c: Coincident(g11,g12)
    c: Coincident(g12,g7)
    c: Equal(g7, g8-g12) x5
    c: PointOnObject(g7,g13)
    c: PointOnObject(g8,g13)
    c: PointOnObject(g9,g13)
    c: PointOnObject(g10,g13)
    c: PointOnObject(g11,g13)
    c: PointOnObject(g12,g13)
    c: PointOnObject(g13,g-1)
    c: Diameter(g13) = 7
    c: Distance(g6,g13) = 8
    c: Horizontal(g0,g10)
    c: Coincident(g14,g15)
    c: Coincident(g15,g16)
    c: Coincident(g16,g17)
    c: Coincident(g17,g18)
    c: Coincident(g18,g19)
    c: Coincident(g19,g14)
    c: Equal(g14, g15-g19) x5
    c: PointOnObject(g14,g20)
    c: PointOnObject(g15,g20)
    c: PointOnObject(g16,g20)
    c: PointOnObject(g17,g20)
    c: PointOnObject(g18,g20)
    c: PointOnObject(g19,g20)
    c: Diameter(g20) = 7
    c: DistanceY(g-1,g20) = 7
    c: Vertical(g18)
    c: Distance(g17,g-2) = 1
    c: Coincident(g21,g22)
    c: Coincident(g22,g23)
    c: Coincident(g23,g24)
    c: Coincident(g24,g25)
    c: Coincident(g25,g26)
    c: Coincident(g26,g21)
    c: Equal(g21, g22-g26) x5
    c: PointOnObject(g21,g27)
    c: PointOnObject(g22,g27)
    c: PointOnObject(g23,g27)
    c: PointOnObject(g24,g27)
    c: PointOnObject(g25,g27)
    c: PointOnObject(g26,g27)
    c: Diameter(g27) = 7
    c: DistanceY(g-1,g27) = 7
    c: DistanceX(g21,g-1) = 1
    c: Vertical(g21)
    c: Coincident(g28,g29)
    c: Coincident(g29,g30)
    c: Coincident(g30,g31)
    c: Coincident(g31,g32)
    c: Coincident(g32,g33)
    c: Coincident(g33,g28)
    c: Equal(g28, g29-g33) x5
    c: PointOnObject(g28,g34)
    c: PointOnObject(g29,g34)
    c: PointOnObject(g30,g34)
    c: PointOnObject(g31,g34)
    c: PointOnObject(g32,g34)
    c: PointOnObject(g33,g34)
    c: PointOnObject(g34,g-1)
    c: Diameter(g34) = 7
    c: Vertical(g31)
    c: DistanceX(g34,g-1) = 8
    c: Coincident(g35,g36)
    c: Coincident(g36,g37)
    c: Coincident(g37,g38)
    c: Coincident(g38,g39)
    c: Coincident(g39,g40)
    c: Coincident(g40,g35)
    c: Equal(g35, g36-g40) x5
    c: PointOnObject(g35,g41)
    c: PointOnObject(g36,g41)
    c: PointOnObject(g37,g41)
    c: PointOnObject(g38,g41)
    c: PointOnObject(g39,g41)
    c: PointOnObject(g40,g41)
    c: Coincident(g42,g43)
    c: Coincident(g43,g44)
    c: Coincident(g44,g45)
    c: Coincident(g45,g46)
    c: Coincident(g46,g47)
    c: Coincident(g47,g42)
    c: Equal(g42, g43-g47) x5
    c: PointOnObject(g42,g48)
    c: PointOnObject(g43,g48)
    c: PointOnObject(g44,g48)
    c: PointOnObject(g45,g48)
    c: PointOnObject(g46,g48)
    c: PointOnObject(g47,g48)
    c: Equal(g41,g48)
    c: Diameter(g41) = 7
    c: Vertical(g39)
    c: Vertical(g43)
    c: Distance(g-2,g39) = 1
    c: Symmetric(g38,g43,g-2)
    c: Distance(g41,g-1) = 7
FEATURE [Part::Extrusion] Extrude421  label="hex036"
  Base = -> Sketch429
  Dir = (0,-1,2e-16)
  DirMode = 2
  FaceMakerClass = Part::FaceMakerBullseye
  FaceMakerMode = 3
  LengthFwd = 10
  LengthRev = 0
  Placement = pos=(28,0,-49) rot=(0,0,1;0rad)
  Solid = true
  Symmetric = false
FEATURE [Sketcher::SketchObject] Sketch430
  ArcFitTolerance = 1e-06
  FullyConstrained = true
  MakeInternals = false
  Placement = pos=(0,0,0) rot=(1,0,0;1.5708rad)
  sketch-geometry (49):
    g0: LineSegment StartX=1e-16 StartY=3.5 StartZ=0 EndX=-3.03109 EndY=1.75 EndZ=0
    g1: LineSegment StartX=-3.03109 StartY=1.75 StartZ=0 EndX=-3.03109 EndY=-1.75 EndZ=0
    g2: LineSegment StartX=-3.03109 StartY=-1.75 StartZ=0 EndX=-1e-16 EndY=-3.5 EndZ=0
    g3: LineSegment StartX=-1e-16 StartY=-3.5 StartZ=0 EndX=3.03109 EndY=-1.75 EndZ=0
    g4: LineSegment StartX=3.03109 StartY=-1.75 StartZ=0 EndX=3.03109 EndY=1.75 EndZ=0
    g5: LineSegment StartX=3.03109 StartY=1.75 StartZ=0 EndX=1e-16 EndY=3.5 EndZ=0
    g6: Circle [constr] CenterX=0 CenterY=0 CenterZ=0 NormalX=0 NormalY=0 NormalZ=1 AngleXU=0 Radius=3.5
    g7: LineSegment StartX=4.96892 StartY=-1.75002 StartZ=0 EndX=8.00002 EndY=-3.5 EndZ=0
    g8: LineSegment StartX=8.00002 StartY=-3.5 StartZ=0 EndX=11.0311 EndY=-1.74998 EndZ=0
    g9: LineSegment StartX=11.0311 StartY=-1.74998 StartZ=0 EndX=11.0311 EndY=1.75002 EndZ=0
    g10: LineSegment StartX=11.0311 StartY=1.75002 StartZ=0 EndX=7.99998 EndY=3.5 EndZ=0
    g11: LineSegment StartX=7.99998 StartY=3.5 StartZ=0 EndX=4.9689 EndY=1.74998 EndZ=0
    g12: LineSegment StartX=4.9689 StartY=1.74998 StartZ=0 EndX=4.96892 EndY=-1.75002 EndZ=0
    g13: Circle [constr] CenterX=8 CenterY=0 CenterZ=0 NormalX=0 NormalY=0 NormalZ=1 AngleXU=0 Radius=3.5
    g14: LineSegment StartX=4.03109 StartY=3.5 StartZ=0 EndX=7.06218 EndY=5.25 EndZ=0
    g15: LineSegment StartX=7.06218 StartY=5.25 StartZ=0 EndX=7.06218 EndY=8.75 EndZ=0
    g16: LineSegment StartX=7.06218 StartY=8.75 StartZ=0 EndX=4.03109 EndY=10.5 EndZ=0
    g17: LineSegment StartX=4.03109 StartY=10.5 StartZ=0 EndX=1 EndY=8.75 EndZ=0
    g18: LineSegment StartX=1 StartY=8.75 StartZ=0 EndX=1 EndY=5.25 EndZ=0
    g19: LineSegment StartX=1 StartY=5.25 StartZ=0 EndX=4.03109 EndY=3.5 EndZ=0
    g20: Circle [constr] CenterX=4.03109 CenterY=7 CenterZ=0 NormalX=0 NormalY=0 NormalZ=1 AngleXU=0 Radius=3.5
    g21: LineSegment StartX=-1 StartY=5.25 StartZ=0 EndX=-1 EndY=8.75 EndZ=0
    g22: LineSegment StartX=-1 StartY=8.75 StartZ=0 EndX=-4.03109 EndY=10.5 EndZ=0
    g23: LineSegment StartX=-4.03109 StartY=10.5 StartZ=0 EndX=-7.06218 EndY=8.75 EndZ=0
    g24: LineSegment StartX=-7.06218 StartY=8.75 StartZ=0 EndX=-7.06218 EndY=5.25 EndZ=0
    g25: LineSegment StartX=-7.06218 StartY=5.25 StartZ=0 EndX=-4.03109 EndY=3.5 EndZ=0
    g26: LineSegment StartX=-4.03109 StartY=3.5 StartZ=0 EndX=-1 EndY=5.25 EndZ=0
    g27: Circle [constr] CenterX=-4.03109 CenterY=7 CenterZ=0 NormalX=0 NormalY=0 NormalZ=1 AngleXU=0 Radius=3.5
    g28: LineSegment StartX=-4.96891 StartY=-1.75 StartZ=0 EndX=-4.96891 EndY=1.75 EndZ=0
    g29: LineSegment StartX=-4.96891 StartY=1.75 StartZ=0 EndX=-8 EndY=3.5 EndZ=0
    g30: LineSegment StartX=-8 StartY=3.5 StartZ=0 EndX=-11.0311 EndY=1.75 EndZ=0
    g31: LineSegment StartX=-11.0311 StartY=1.75 StartZ=0 EndX=-11.0311 EndY=-1.75 EndZ=0
    g32: LineSegment StartX=-11.0311 StartY=-1.75 StartZ=0 EndX=-8 EndY=-3.5 EndZ=0
    g33: LineSegment StartX=-8 StartY=-3.5 StartZ=0 EndX=-4.96891 EndY=-1.75 EndZ=0
    g34: Circle [constr] CenterX=-8 CenterY=0 CenterZ=0 NormalX=0 NormalY=0 NormalZ=1 AngleXU=0 Radius=3.5
    g35: LineSegment StartX=-4.03109 StartY=-3.5 StartZ=0 EndX=-7.06218 EndY=-5.25 EndZ=0
    g36: LineSegment StartX=-7.06218 StartY=-5.25 StartZ=0 EndX=-7.06218 EndY=-8.75 EndZ=0
    g37: LineSegment StartX=-7.06218 StartY=-8.75 StartZ=0 EndX=-4.03109 EndY=-10.5 EndZ=0
    g38: LineSegment StartX=-4.03109 StartY=-10.5 StartZ=0 EndX=-1 EndY=-8.75 EndZ=0
    g39: LineSegment StartX=-1 StartY=-8.75 StartZ=0 EndX=-1 EndY=-5.25 EndZ=0
    g40: LineSegment StartX=-1 StartY=-5.25 StartZ=0 EndX=-4.03109 EndY=-3.5 EndZ=0
    g41: Circle [constr] CenterX=-4.03109 CenterY=-7 CenterZ=0 NormalX=0 NormalY=0 NormalZ=1 AngleXU=0 Radius=3.5
    g42: LineSegment StartX=4.03109 StartY=-3.5 StartZ=0 EndX=1 EndY=-5.25 EndZ=0
    g43: LineSegment StartX=1 StartY=-5.25 StartZ=0 EndX=1 EndY=-8.75 EndZ=0
    g44: LineSegment StartX=1 StartY=-8.75 StartZ=0 EndX=4.03109 EndY=-10.5 EndZ=0
    g45: LineSegment StartX=4.03109 StartY=-10.5 StartZ=0 EndX=7.06218 EndY=-8.75 EndZ=0
    g46: LineSegment StartX=7.06218 StartY=-8.75 StartZ=0 EndX=7.06218 EndY=-5.25 EndZ=0
    g47: LineSegment StartX=7.06218 StartY=-5.25 StartZ=0 EndX=4.03109 EndY=-3.5 EndZ=0
    g48: Circle [constr] CenterX=4.03109 CenterY=-7 CenterZ=0 NormalX=0 NormalY=0 NormalZ=1 AngleXU=0 Radius=3.5
  constraints (117):
    c: Coincident(g0,g1)
    c: Coincident(g1,g2)
    c: Coincident(g2,g3)
    c: Coincident(g3,g4)
    c: Coincident(g4,g5)
    c: Coincident(g5,g0)
    c: Equal(g0, g1-g5) x5
    c: PointOnObject(g0,g6)
    c: PointOnObject(g1,g6)
    c: PointOnObject(g2,g6)
    c: PointOnObject(g3,g6)
    c: PointOnObject(g4,g6)
    c: PointOnObject(g5,g6)
    c: Coincident(g6,g-1)
    c: Diameter(g6) = 7
    c: PointOnObject(g0,g-2)
    c: Coincident(g7,g8)
    c: Coincident(g8,g9)
    c: Coincident(g9,g10)
    c: Coincident(g10,g11)
    c: Coincident(g11,g12)
    c: Coincident(g12,g7)
    c: Equal(g7, g8-g12) x5
    c: PointOnObject(g7,g13)
    c: PointOnObject(g8,g13)
    c: PointOnObject(g9,g13)
    c: PointOnObject(g10,g13)
    c: PointOnObject(g11,g13)
    c: PointOnObject(g12,g13)
    c: PointOnObject(g13,g-1)
    c: Diameter(g13) = 7
    c: Distance(g6,g13) = 8
    c: Horizontal(g0,g10)
    c: Coincident(g14,g15)
    c: Coincident(g15,g16)
    c: Coincident(g16,g17)
    c: Coincident(g17,g18)
    c: Coincident(g18,g19)
    c: Coincident(g19,g14)
    c: Equal(g14, g15-g19) x5
    c: PointOnObject(g14,g20)
    c: PointOnObject(g15,g20)
    c: PointOnObject(g16,g20)
    c: PointOnObject(g17,g20)
    c: PointOnObject(g18,g20)
    c: PointOnObject(g19,g20)
    c: Diameter(g20) = 7
    c: DistanceY(g-1,g20) = 7
    c: Vertical(g18)
    c: Distance(g17,g-2) = 1
    c: Coincident(g21,g22)
    c: Coincident(g22,g23)
    c: Coincident(g23,g24)
    c: Coincident(g24,g25)
    c: Coincident(g25,g26)
    c: Coincident(g26,g21)
    c: Equal(g21, g22-g26) x5
    c: PointOnObject(g21,g27)
    c: PointOnObject(g22,g27)
    c: PointOnObject(g23,g27)
    c: PointOnObject(g24,g27)
    c: PointOnObject(g25,g27)
    c: PointOnObject(g26,g27)
    c: Diameter(g27) = 7
    c: DistanceY(g-1,g27) = 7
    c: DistanceX(g21,g-1) = 1
    c: Vertical(g21)
    c: Coincident(g28,g29)
    c: Coincident(g29,g30)
    c: Coincident(g30,g31)
    c: Coincident(g31,g32)
    c: Coincident(g32,g33)
    c: Coincident(g33,g28)
    c: Equal(g28, g29-g33) x5
    c: PointOnObject(g28,g34)
    c: PointOnObject(g29,g34)
    c: PointOnObject(g30,g34)
    c: PointOnObject(g31,g34)
    c: PointOnObject(g32,g34)
    c: PointOnObject(g33,g34)
    c: PointOnObject(g34,g-1)
    c: Diameter(g34) = 7
    c: Vertical(g31)
    c: DistanceX(g34,g-1) = 8
    c: Coincident(g35,g36)
    c: Coincident(g36,g37)
    c: Coincident(g37,g38)
    c: Coincident(g38,g39)
    c: Coincident(g39,g40)
    c: Coincident(g40,g35)
    c: Equal(g35, g36-g40) x5
    c: PointOnObject(g35,g41)
    c: PointOnObject(g36,g41)
    c: PointOnObject(g37,g41)
    c: PointOnObject(g38,g41)
    c: PointOnObject(g39,g41)
    c: PointOnObject(g40,g41)
    c: Coincident(g42,g43)
    c: Coincident(g43,g44)
    c: Coincident(g44,g45)
    c: Coincident(g45,g46)
    c: Coincident(g46,g47)
    c: Coincident(g47,g42)
    c: Equal(g42, g43-g47) x5
    c: PointOnObject(g42,g48)
    c: PointOnObject(g43,g48)
    c: PointOnObject(g44,g48)
    c: PointOnObject(g45,g48)
    c: PointOnObject(g46,g48)
    c: PointOnObject(g47,g48)
    c: Equal(g41,g48)
    c: Diameter(g41) = 7
    c: Vertical(g39)
    c: Vertical(g43)
    c: Distance(g-2,g39) = 1
    c: Symmetric(g38,g43,g-2)
    c: Distance(g41,g-1) = 7
FEATURE [Part::Extrusion] Extrude422  label="hex037"
  Base = -> Sketch430
  Dir = (0,-1,2e-16)
  DirMode = 2
  FaceMakerClass = Part::FaceMakerBullseye
  FaceMakerMode = 3
  LengthFwd = 10
  LengthRev = 0
  Placement = pos=(48,0,-42) rot=(0,0,1;0rad)
  Solid = true
  Symmetric = false
FEATURE [Sketcher::SketchObject] Sketch431
  ArcFitTolerance = 1e-06
  FullyConstrained = true
  MakeInternals = false
  Placement = pos=(0,0,0) rot=(1,0,0;1.5708rad)
  sketch-geometry (49):
    g0: LineSegment StartX=1e-16 StartY=3.5 StartZ=0 EndX=-3.03109 EndY=1.75 EndZ=0
    g1: LineSegment StartX=-3.03109 StartY=1.75 StartZ=0 EndX=-3.03109 EndY=-1.75 EndZ=0
    g2: LineSegment StartX=-3.03109 StartY=-1.75 StartZ=0 EndX=-1e-16 EndY=-3.5 EndZ=0
    g3: LineSegment StartX=-1e-16 StartY=-3.5 StartZ=0 EndX=3.03109 EndY=-1.75 EndZ=0
    g4: LineSegment StartX=3.03109 StartY=-1.75 StartZ=0 EndX=3.03109 EndY=1.75 EndZ=0
    g5: LineSegment StartX=3.03109 StartY=1.75 StartZ=0 EndX=1e-16 EndY=3.5 EndZ=0
    g6: Circle [constr] CenterX=0 CenterY=0 CenterZ=0 NormalX=0 NormalY=0 NormalZ=1 AngleXU=0 Radius=3.5
    g7: LineSegment StartX=4.96892 StartY=-1.75002 StartZ=0 EndX=8.00002 EndY=-3.5 EndZ=0
    g8: LineSegment StartX=8.00002 StartY=-3.5 StartZ=0 EndX=11.0311 EndY=-1.74998 EndZ=0
    g9: LineSegment StartX=11.0311 StartY=-1.74998 StartZ=0 EndX=11.0311 EndY=1.75002 EndZ=0
    g10: LineSegment StartX=11.0311 StartY=1.75002 StartZ=0 EndX=7.99998 EndY=3.5 EndZ=0
    g11: LineSegment StartX=7.99998 StartY=3.5 StartZ=0 EndX=4.9689 EndY=1.74998 EndZ=0
    g12: LineSegment StartX=4.9689 StartY=1.74998 StartZ=0 EndX=4.96892 EndY=-1.75002 EndZ=0
    g13: Circle [constr] CenterX=8 CenterY=0 CenterZ=0 NormalX=0 NormalY=0 NormalZ=1 AngleXU=0 Radius=3.5
    g14: LineSegment StartX=4.03109 StartY=3.5 StartZ=0 EndX=7.06218 EndY=5.25 EndZ=0
    g15: LineSegment StartX=7.06218 StartY=5.25 StartZ=0 EndX=7.06218 EndY=8.75 EndZ=0
    g16: LineSegment StartX=7.06218 StartY=8.75 StartZ=0 EndX=4.03109 EndY=10.5 EndZ=0
    g17: LineSegment StartX=4.03109 StartY=10.5 StartZ=0 EndX=1 EndY=8.75 EndZ=0
    g18: LineSegment StartX=1 StartY=8.75 StartZ=0 EndX=1 EndY=5.25 EndZ=0
    g19: LineSegment StartX=1 StartY=5.25 StartZ=0 EndX=4.03109 EndY=3.5 EndZ=0
    g20: Circle [constr] CenterX=4.03109 CenterY=7 CenterZ=0 NormalX=0 NormalY=0 NormalZ=1 AngleXU=0 Radius=3.5
    g21: LineSegment StartX=-1 StartY=5.25 StartZ=0 EndX=-1 EndY=8.75 EndZ=0
    g22: LineSegment StartX=-1 StartY=8.75 StartZ=0 EndX=-4.03109 EndY=10.5 EndZ=0
    g23: LineSegment StartX=-4.03109 StartY=10.5 StartZ=0 EndX=-7.06218 EndY=8.75 EndZ=0
    g24: LineSegment StartX=-7.06218 StartY=8.75 StartZ=0 EndX=-7.06218 EndY=5.25 EndZ=0
    g25: LineSegment StartX=-7.06218 StartY=5.25 StartZ=0 EndX=-4.03109 EndY=3.5 EndZ=0
    g26: LineSegment StartX=-4.03109 StartY=3.5 StartZ=0 EndX=-1 EndY=5.25 EndZ=0
    g27: Circle [constr] CenterX=-4.03109 CenterY=7 CenterZ=0 NormalX=0 NormalY=0 NormalZ=1 AngleXU=0 Radius=3.5
    g28: LineSegment StartX=-4.96891 StartY=-1.75 StartZ=0 EndX=-4.96891 EndY=1.75 EndZ=0
    g29: LineSegment StartX=-4.96891 StartY=1.75 StartZ=0 EndX=-8 EndY=3.5 EndZ=0
    g30: LineSegment StartX=-8 StartY=3.5 StartZ=0 EndX=-11.0311 EndY=1.75 EndZ=0
    g31: LineSegment StartX=-11.0311 StartY=1.75 StartZ=0 EndX=-11.0311 EndY=-1.75 EndZ=0
    g32: LineSegment StartX=-11.0311 StartY=-1.75 StartZ=0 EndX=-8 EndY=-3.5 EndZ=0
    g33: LineSegment StartX=-8 StartY=-3.5 StartZ=0 EndX=-4.96891 EndY=-1.75 EndZ=0
    g34: Circle [constr] CenterX=-8 CenterY=0 CenterZ=0 NormalX=0 NormalY=0 NormalZ=1 AngleXU=0 Radius=3.5
    g35: LineSegment StartX=-4.03109 StartY=-3.5 StartZ=0 EndX=-7.06218 EndY=-5.25 EndZ=0
    g36: LineSegment StartX=-7.06218 StartY=-5.25 StartZ=0 EndX=-7.06218 EndY=-8.75 EndZ=0
    g37: LineSegment StartX=-7.06218 StartY=-8.75 StartZ=0 EndX=-4.03109 EndY=-10.5 EndZ=0
    g38: LineSegment StartX=-4.03109 StartY=-10.5 StartZ=0 EndX=-1 EndY=-8.75 EndZ=0
    g39: LineSegment StartX=-1 StartY=-8.75 StartZ=0 EndX=-1 EndY=-5.25 EndZ=0
    g40: LineSegment StartX=-1 StartY=-5.25 StartZ=0 EndX=-4.03109 EndY=-3.5 EndZ=0
    g41: Circle [constr] CenterX=-4.03109 CenterY=-7 CenterZ=0 NormalX=0 NormalY=0 NormalZ=1 AngleXU=0 Radius=3.5
    g42: LineSegment StartX=4.03109 StartY=-3.5 StartZ=0 EndX=1 EndY=-5.25 EndZ=0
    g43: LineSegment StartX=1 StartY=-5.25 StartZ=0 EndX=1 EndY=-8.75 EndZ=0
    g44: LineSegment StartX=1 StartY=-8.75 StartZ=0 EndX=4.03109 EndY=-10.5 EndZ=0
    g45: LineSegment StartX=4.03109 StartY=-10.5 StartZ=0 EndX=7.06218 EndY=-8.75 EndZ=0
    g46: LineSegment StartX=7.06218 StartY=-8.75 StartZ=0 EndX=7.06218 EndY=-5.25 EndZ=0
    g47: LineSegment StartX=7.06218 StartY=-5.25 StartZ=0 EndX=4.03109 EndY=-3.5 EndZ=0
    g48: Circle [constr] CenterX=4.03109 CenterY=-7 CenterZ=0 NormalX=0 NormalY=0 NormalZ=1 AngleXU=0 Radius=3.5
  constraints (117):
    c: Coincident(g0,g1)
    c: Coincident(g1,g2)
    c: Coincident(g2,g3)
    c: Coincident(g3,g4)
    c: Coincident(g4,g5)
    c: Coincident(g5,g0)
    c: Equal(g0, g1-g5) x5
    c: PointOnObject(g0,g6)
    c: PointOnObject(g1,g6)
    c: PointOnObject(g2,g6)
    c: PointOnObject(g3,g6)
    c: PointOnObject(g4,g6)
    c: PointOnObject(g5,g6)
    c: Coincident(g6,g-1)
    c: Diameter(g6) = 7
    c: PointOnObject(g0,g-2)
    c: Coincident(g7,g8)
    c: Coincident(g8,g9)
    c: Coincident(g9,g10)
    c: Coincident(g10,g11)
    c: Coincident(g11,g12)
    c: Coincident(g12,g7)
    c: Equal(g7, g8-g12) x5
    c: PointOnObject(g7,g13)
    c: PointOnObject(g8,g13)
    c: PointOnObject(g9,g13)
    c: PointOnObject(g10,g13)
    c: PointOnObject(g11,g13)
    c: PointOnObject(g12,g13)
    c: PointOnObject(g13,g-1)
    c: Diameter(g13) = 7
    c: Distance(g6,g13) = 8
    c: Horizontal(g0,g10)
    c: Coincident(g14,g15)
    c: Coincident(g15,g16)
    c: Coincident(g16,g17)
    c: Coincident(g17,g18)
    c: Coincident(g18,g19)
    c: Coincident(g19,g14)
    c: Equal(g14, g15-g19) x5
    c: PointOnObject(g14,g20)
    c: PointOnObject(g15,g20)
    c: PointOnObject(g16,g20)
    c: PointOnObject(g17,g20)
    c: PointOnObject(g18,g20)
    c: PointOnObject(g19,g20)
    c: Diameter(g20) = 7
    c: DistanceY(g-1,g20) = 7
    c: Vertical(g18)
    c: Distance(g17,g-2) = 1
    c: Coincident(g21,g22)
    c: Coincident(g22,g23)
    c: Coincident(g23,g24)
    c: Coincident(g24,g25)
    c: Coincident(g25,g26)
    c: Coincident(g26,g21)
    c: Equal(g21, g22-g26) x5
    c: PointOnObject(g21,g27)
    c: PointOnObject(g22,g27)
    c: PointOnObject(g23,g27)
    c: PointOnObject(g24,g27)
    c: PointOnObject(g25,g27)
    c: PointOnObject(g26,g27)
    c: Diameter(g27) = 7
    c: DistanceY(g-1,g27) = 7
    c: DistanceX(g21,g-1) = 1
    c: Vertical(g21)
    c: Coincident(g28,g29)
    c: Coincident(g29,g30)
    c: Coincident(g30,g31)
    c: Coincident(g31,g32)
    c: Coincident(g32,g33)
    c: Coincident(g33,g28)
    c: Equal(g28, g29-g33) x5
    c: PointOnObject(g28,g34)
    c: PointOnObject(g29,g34)
    c: PointOnObject(g30,g34)
    c: PointOnObject(g31,g34)
    c: PointOnObject(g32,g34)
    c: PointOnObject(g33,g34)
    c: PointOnObject(g34,g-1)
    c: Diameter(g34) = 7
    c: Vertical(g31)
    c: DistanceX(g34,g-1) = 8
    c: Coincident(g35,g36)
    c: Coincident(g36,g37)
    c: Coincident(g37,g38)
    c: Coincident(g38,g39)
    c: Coincident(g39,g40)
    c: Coincident(g40,g35)
    c: Equal(g35, g36-g40) x5
    c: PointOnObject(g35,g41)
    c: PointOnObject(g36,g41)
    c: PointOnObject(g37,g41)
    c: PointOnObject(g38,g41)
    c: PointOnObject(g39,g41)
    c: PointOnObject(g40,g41)
    c: Coincident(g42,g43)
    c: Coincident(g43,g44)
    c: Coincident(g44,g45)
    c: Coincident(g45,g46)
    c: Coincident(g46,g47)
    c: Coincident(g47,g42)
    c: Equal(g42, g43-g47) x5
    c: PointOnObject(g42,g48)
    c: PointOnObject(g43,g48)
    c: PointOnObject(g44,g48)
    c: PointOnObject(g45,g48)
    c: PointOnObject(g46,g48)
    c: PointOnObject(g47,g48)
    c: Equal(g41,g48)
    c: Diameter(g41) = 7
    c: Vertical(g39)
    c: Vertical(g43)
    c: Distance(g-2,g39) = 1
    c: Symmetric(g38,g43,g-2)
    c: Distance(g41,g-1) = 7
FEATURE [Part::Extrusion] Extrude423  label="hex038"
  Base = -> Sketch431
  Dir = (0,-1,2e-16)
  DirMode = 2
  FaceMakerClass = Part::FaceMakerBullseye
  FaceMakerMode = 3
  LengthFwd = 10
  LengthRev = 0
  Placement = pos=(68,0,-35) rot=(0,0,1;0rad)
  Solid = true
  Symmetric = false
FEATURE [Sketcher::SketchObject] Sketch432
  ArcFitTolerance = 1e-06
  FullyConstrained = true
  MakeInternals = false
  Placement = pos=(0,0,0) rot=(1,0,0;1.5708rad)
  sketch-geometry (49):
    g0: LineSegment StartX=1e-16 StartY=3.5 StartZ=0 EndX=-3.03109 EndY=1.75 EndZ=0
    g1: LineSegment StartX=-3.03109 StartY=1.75 StartZ=0 EndX=-3.03109 EndY=-1.75 EndZ=0
    g2: LineSegment StartX=-3.03109 StartY=-1.75 StartZ=0 EndX=-1e-16 EndY=-3.5 EndZ=0
    g3: LineSegment StartX=-1e-16 StartY=-3.5 StartZ=0 EndX=3.03109 EndY=-1.75 EndZ=0
    g4: LineSegment StartX=3.03109 StartY=-1.75 StartZ=0 EndX=3.03109 EndY=1.75 EndZ=0
    g5: LineSegment StartX=3.03109 StartY=1.75 StartZ=0 EndX=1e-16 EndY=3.5 EndZ=0
    g6: Circle [constr] CenterX=0 CenterY=0 CenterZ=0 NormalX=0 NormalY=0 NormalZ=1 AngleXU=0 Radius=3.5
    g7: LineSegment StartX=4.96892 StartY=-1.75002 StartZ=0 EndX=8.00002 EndY=-3.5 EndZ=0
    g8: LineSegment StartX=8.00002 StartY=-3.5 StartZ=0 EndX=11.0311 EndY=-1.74998 EndZ=0
    g9: LineSegment StartX=11.0311 StartY=-1.74998 StartZ=0 EndX=11.0311 EndY=1.75002 EndZ=0
    g10: LineSegment StartX=11.0311 StartY=1.75002 StartZ=0 EndX=7.99998 EndY=3.5 EndZ=0
    g11: LineSegment StartX=7.99998 StartY=3.5 StartZ=0 EndX=4.9689 EndY=1.74998 EndZ=0
    g12: LineSegment StartX=4.9689 StartY=1.74998 StartZ=0 EndX=4.96892 EndY=-1.75002 EndZ=0
    g13: Circle [constr] CenterX=8 CenterY=0 CenterZ=0 NormalX=0 NormalY=0 NormalZ=1 AngleXU=0 Radius=3.5
    g14: LineSegment StartX=4.03109 StartY=3.5 StartZ=0 EndX=7.06218 EndY=5.25 EndZ=0
    g15: LineSegment StartX=7.06218 StartY=5.25 StartZ=0 EndX=7.06218 EndY=8.75 EndZ=0
    g16: LineSegment StartX=7.06218 StartY=8.75 StartZ=0 EndX=4.03109 EndY=10.5 EndZ=0
    g17: LineSegment StartX=4.03109 StartY=10.5 StartZ=0 EndX=1 EndY=8.75 EndZ=0
    g18: LineSegment StartX=1 StartY=8.75 StartZ=0 EndX=1 EndY=5.25 EndZ=0
    g19: LineSegment StartX=1 StartY=5.25 StartZ=0 EndX=4.03109 EndY=3.5 EndZ=0
    g20: Circle [constr] CenterX=4.03109 CenterY=7 CenterZ=0 NormalX=0 NormalY=0 NormalZ=1 AngleXU=0 Radius=3.5
    g21: LineSegment StartX=-1 StartY=5.25 StartZ=0 EndX=-1 EndY=8.75 EndZ=0
    g22: LineSegment StartX=-1 StartY=8.75 StartZ=0 EndX=-4.03109 EndY=10.5 EndZ=0
    g23: LineSegment StartX=-4.03109 StartY=10.5 StartZ=0 EndX=-7.06218 EndY=8.75 EndZ=0
    g24: LineSegment StartX=-7.06218 StartY=8.75 StartZ=0 EndX=-7.06218 EndY=5.25 EndZ=0
    g25: LineSegment StartX=-7.06218 StartY=5.25 StartZ=0 EndX=-4.03109 EndY=3.5 EndZ=0
    g26: LineSegment StartX=-4.03109 StartY=3.5 StartZ=0 EndX=-1 EndY=5.25 EndZ=0
    g27: Circle [constr] CenterX=-4.03109 CenterY=7 CenterZ=0 NormalX=0 NormalY=0 NormalZ=1 AngleXU=0 Radius=3.5
    g28: LineSegment StartX=-4.96891 StartY=-1.75 StartZ=0 EndX=-4.96891 EndY=1.75 EndZ=0
    g29: LineSegment StartX=-4.96891 StartY=1.75 StartZ=0 EndX=-8 EndY=3.5 EndZ=0
    g30: LineSegment StartX=-8 StartY=3.5 StartZ=0 EndX=-11.0311 EndY=1.75 EndZ=0
    g31: LineSegment StartX=-11.0311 StartY=1.75 StartZ=0 EndX=-11.0311 EndY=-1.75 EndZ=0
    g32: LineSegment StartX=-11.0311 StartY=-1.75 StartZ=0 EndX=-8 EndY=-3.5 EndZ=0
    g33: LineSegment StartX=-8 StartY=-3.5 StartZ=0 EndX=-4.96891 EndY=-1.75 EndZ=0
    g34: Circle [constr] CenterX=-8 CenterY=0 CenterZ=0 NormalX=0 NormalY=0 NormalZ=1 AngleXU=0 Radius=3.5
    g35: LineSegment StartX=-4.03109 StartY=-3.5 StartZ=0 EndX=-7.06218 EndY=-5.25 EndZ=0
    g36: LineSegment StartX=-7.06218 StartY=-5.25 StartZ=0 EndX=-7.06218 EndY=-8.75 EndZ=0
    g37: LineSegment StartX=-7.06218 StartY=-8.75 StartZ=0 EndX=-4.03109 EndY=-10.5 EndZ=0
    g38: LineSegment StartX=-4.03109 StartY=-10.5 StartZ=0 EndX=-1 EndY=-8.75 EndZ=0
    g39: LineSegment StartX=-1 StartY=-8.75 StartZ=0 EndX=-1 EndY=-5.25 EndZ=0
    g40: LineSegment StartX=-1 StartY=-5.25 StartZ=0 EndX=-4.03109 EndY=-3.5 EndZ=0
    g41: Circle [constr] CenterX=-4.03109 CenterY=-7 CenterZ=0 NormalX=0 NormalY=0 NormalZ=1 AngleXU=0 Radius=3.5
    g42: LineSegment StartX=4.03109 StartY=-3.5 StartZ=0 EndX=1 EndY=-5.25 EndZ=0
    g43: LineSegment StartX=1 StartY=-5.25 StartZ=0 EndX=1 EndY=-8.75 EndZ=0
    g44: LineSegment StartX=1 StartY=-8.75 StartZ=0 EndX=4.03109 EndY=-10.5 EndZ=0
    g45: LineSegment StartX=4.03109 StartY=-10.5 StartZ=0 EndX=7.06218 EndY=-8.75 EndZ=0
    g46: LineSegment StartX=7.06218 StartY=-8.75 StartZ=0 EndX=7.06218 EndY=-5.25 EndZ=0
    g47: LineSegment StartX=7.06218 StartY=-5.25 StartZ=0 EndX=4.03109 EndY=-3.5 EndZ=0
    g48: Circle [constr] CenterX=4.03109 CenterY=-7 CenterZ=0 NormalX=0 NormalY=0 NormalZ=1 AngleXU=0 Radius=3.5
  constraints (117):
    c: Coincident(g0,g1)
    c: Coincident(g1,g2)
    c: Coincident(g2,g3)
    c: Coincident(g3,g4)
    c: Coincident(g4,g5)
    c: Coincident(g5,g0)
    c: Equal(g0, g1-g5) x5
    c: PointOnObject(g0,g6)
    c: PointOnObject(g1,g6)
    c: PointOnObject(g2,g6)
    c: PointOnObject(g3,g6)
    c: PointOnObject(g4,g6)
    c: PointOnObject(g5,g6)
    c: Coincident(g6,g-1)
    c: Diameter(g6) = 7
    c: PointOnObject(g0,g-2)
    c: Coincident(g7,g8)
    c: Coincident(g8,g9)
    c: Coincident(g9,g10)
    c: Coincident(g10,g11)
    c: Coincident(g11,g12)
    c: Coincident(g12,g7)
    c: Equal(g7, g8-g12) x5
    c: PointOnObject(g7,g13)
    c: PointOnObject(g8,g13)
    c: PointOnObject(g9,g13)
    c: PointOnObject(g10,g13)
    c: PointOnObject(g11,g13)
    c: PointOnObject(g12,g13)
    c: PointOnObject(g13,g-1)
    c: Diameter(g13) = 7
    c: Distance(g6,g13) = 8
    c: Horizontal(g0,g10)
    c: Coincident(g14,g15)
    c: Coincident(g15,g16)
    c: Coincident(g16,g17)
    c: Coincident(g17,g18)
    c: Coincident(g18,g19)
    c: Coincident(g19,g14)
    c: Equal(g14, g15-g19) x5
    c: PointOnObject(g14,g20)
    c: PointOnObject(g15,g20)
    c: PointOnObject(g16,g20)
    c: PointOnObject(g17,g20)
    c: PointOnObject(g18,g20)
    c: PointOnObject(g19,g20)
    c: Diameter(g20) = 7
    c: DistanceY(g-1,g20) = 7
    c: Vertical(g18)
    c: Distance(g17,g-2) = 1
    c: Coincident(g21,g22)
    c: Coincident(g22,g23)
    c: Coincident(g23,g24)
    c: Coincident(g24,g25)
    c: Coincident(g25,g26)
    c: Coincident(g26,g21)
    c: Equal(g21, g22-g26) x5
    c: PointOnObject(g21,g27)
    c: PointOnObject(g22,g27)
    c: PointOnObject(g23,g27)
    c: PointOnObject(g24,g27)
    c: PointOnObject(g25,g27)
    c: PointOnObject(g26,g27)
    c: Diameter(g27) = 7
    c: DistanceY(g-1,g27) = 7
    c: DistanceX(g21,g-1) = 1
    c: Vertical(g21)
    c: Coincident(g28,g29)
    c: Coincident(g29,g30)
    c: Coincident(g30,g31)
    c: Coincident(g31,g32)
    c: Coincident(g32,g33)
    c: Coincident(g33,g28)
    c: Equal(g28, g29-g33) x5
    c: PointOnObject(g28,g34)
    c: PointOnObject(g29,g34)
    c: PointOnObject(g30,g34)
    c: PointOnObject(g31,g34)
    c: PointOnObject(g32,g34)
    c: PointOnObject(g33,g34)
    c: PointOnObject(g34,g-1)
    c: Diameter(g34) = 7
    c: Vertical(g31)
    c: DistanceX(g34,g-1) = 8
    c: Coincident(g35,g36)
    c: Coincident(g36,g37)
    c: Coincident(g37,g38)
    c: Coincident(g38,g39)
    c: Coincident(g39,g40)
    c: Coincident(g40,g35)
    c: Equal(g35, g36-g40) x5
    c: PointOnObject(g35,g41)
    c: PointOnObject(g36,g41)
    c: PointOnObject(g37,g41)
    c: PointOnObject(g38,g41)
    c: PointOnObject(g39,g41)
    c: PointOnObject(g40,g41)
    c: Coincident(g42,g43)
    c: Coincident(g43,g44)
    c: Coincident(g44,g45)
    c: Coincident(g45,g46)
    c: Coincident(g46,g47)
    c: Coincident(g47,g42)
    c: Equal(g42, g43-g47) x5
    c: PointOnObject(g42,g48)
    c: PointOnObject(g43,g48)
    c: PointOnObject(g44,g48)
    c: PointOnObject(g45,g48)
    c: PointOnObject(g46,g48)
    c: PointOnObject(g47,g48)
    c: Equal(g41,g48)
    c: Diameter(g41) = 7
    c: Vertical(g39)
    c: Vertical(g43)
    c: Distance(g-2,g39) = 1
    c: Symmetric(g38,g43,g-2)
    c: Distance(g41,g-1) = 7
FEATURE [Part::Extrusion] Extrude424  label="hex039"
  Base = -> Sketch432
  Dir = (0,-1,2e-16)
  DirMode = 2
  FaceMakerClass = Part::FaceMakerBullseye
  FaceMakerMode = 3
  LengthFwd = 10
  LengthRev = 0
  Placement = pos=(72,0,-14) rot=(0,0,1;0rad)
  Solid = true
  Symmetric = false
FEATURE [Sketcher::SketchObject] Sketch433
  ArcFitTolerance = 1e-06
  FullyConstrained = true
  MakeInternals = false
  Placement = pos=(0,0,0) rot=(1,0,0;1.5708rad)
  sketch-geometry (49):
    g0: LineSegment StartX=1e-16 StartY=3.5 StartZ=0 EndX=-3.03109 EndY=1.75 EndZ=0
    g1: LineSegment StartX=-3.03109 StartY=1.75 StartZ=0 EndX=-3.03109 EndY=-1.75 EndZ=0
    g2: LineSegment StartX=-3.03109 StartY=-1.75 StartZ=0 EndX=-1e-16 EndY=-3.5 EndZ=0
    g3: LineSegment StartX=-1e-16 StartY=-3.5 StartZ=0 EndX=3.03109 EndY=-1.75 EndZ=0
    g4: LineSegment StartX=3.03109 StartY=-1.75 StartZ=0 EndX=3.03109 EndY=1.75 EndZ=0
    g5: LineSegment StartX=3.03109 StartY=1.75 StartZ=0 EndX=1e-16 EndY=3.5 EndZ=0
    g6: Circle [constr] CenterX=0 CenterY=0 CenterZ=0 NormalX=0 NormalY=0 NormalZ=1 AngleXU=0 Radius=3.5
    g7: LineSegment StartX=4.96892 StartY=-1.75002 StartZ=0 EndX=8.00002 EndY=-3.5 EndZ=0
    g8: LineSegment StartX=8.00002 StartY=-3.5 StartZ=0 EndX=11.0311 EndY=-1.74998 EndZ=0
    g9: LineSegment StartX=11.0311 StartY=-1.74998 StartZ=0 EndX=11.0311 EndY=1.75002 EndZ=0
    g10: LineSegment StartX=11.0311 StartY=1.75002 StartZ=0 EndX=7.99998 EndY=3.5 EndZ=0
    g11: LineSegment StartX=7.99998 StartY=3.5 StartZ=0 EndX=4.9689 EndY=1.74998 EndZ=0
    g12: LineSegment StartX=4.9689 StartY=1.74998 StartZ=0 EndX=4.96892 EndY=-1.75002 EndZ=0
    g13: Circle [constr] CenterX=8 CenterY=0 CenterZ=0 NormalX=0 NormalY=0 NormalZ=1 AngleXU=0 Radius=3.5
    g14: LineSegment StartX=4.03109 StartY=3.5 StartZ=0 EndX=7.06218 EndY=5.25 EndZ=0
    g15: LineSegment StartX=7.06218 StartY=5.25 StartZ=0 EndX=7.06218 EndY=8.75 EndZ=0
    g16: LineSegment StartX=7.06218 StartY=8.75 StartZ=0 EndX=4.03109 EndY=10.5 EndZ=0
    g17: LineSegment StartX=4.03109 StartY=10.5 StartZ=0 EndX=1 EndY=8.75 EndZ=0
    g18: LineSegment StartX=1 StartY=8.75 StartZ=0 EndX=1 EndY=5.25 EndZ=0
    g19: LineSegment StartX=1 StartY=5.25 StartZ=0 EndX=4.03109 EndY=3.5 EndZ=0
    g20: Circle [constr] CenterX=4.03109 CenterY=7 CenterZ=0 NormalX=0 NormalY=0 NormalZ=1 AngleXU=0 Radius=3.5
    g21: LineSegment StartX=-1 StartY=5.25 StartZ=0 EndX=-1 EndY=8.75 EndZ=0
    g22: LineSegment StartX=-1 StartY=8.75 StartZ=0 EndX=-4.03109 EndY=10.5 EndZ=0
    g23: LineSegment StartX=-4.03109 StartY=10.5 StartZ=0 EndX=-7.06218 EndY=8.75 EndZ=0
    g24: LineSegment StartX=-7.06218 StartY=8.75 StartZ=0 EndX=-7.06218 EndY=5.25 EndZ=0
    g25: LineSegment StartX=-7.06218 StartY=5.25 StartZ=0 EndX=-4.03109 EndY=3.5 EndZ=0
    g26: LineSegment StartX=-4.03109 StartY=3.5 StartZ=0 EndX=-1 EndY=5.25 EndZ=0
    g27: Circle [constr] CenterX=-4.03109 CenterY=7 CenterZ=0 NormalX=0 NormalY=0 NormalZ=1 AngleXU=0 Radius=3.5
    g28: LineSegment StartX=-4.96891 StartY=-1.75 StartZ=0 EndX=-4.96891 EndY=1.75 EndZ=0
    g29: LineSegment StartX=-4.96891 StartY=1.75 StartZ=0 EndX=-8 EndY=3.5 EndZ=0
    g30: LineSegment StartX=-8 StartY=3.5 StartZ=0 EndX=-11.0311 EndY=1.75 EndZ=0
    g31: LineSegment StartX=-11.0311 StartY=1.75 StartZ=0 EndX=-11.0311 EndY=-1.75 EndZ=0
    g32: LineSegment StartX=-11.0311 StartY=-1.75 StartZ=0 EndX=-8 EndY=-3.5 EndZ=0
    g33: LineSegment StartX=-8 StartY=-3.5 StartZ=0 EndX=-4.96891 EndY=-1.75 EndZ=0
    g34: Circle [constr] CenterX=-8 CenterY=0 CenterZ=0 NormalX=0 NormalY=0 NormalZ=1 AngleXU=0 Radius=3.5
    g35: LineSegment StartX=-4.03109 StartY=-3.5 StartZ=0 EndX=-7.06218 EndY=-5.25 EndZ=0
    g36: LineSegment StartX=-7.06218 StartY=-5.25 StartZ=0 EndX=-7.06218 EndY=-8.75 EndZ=0
    g37: LineSegment StartX=-7.06218 StartY=-8.75 StartZ=0 EndX=-4.03109 EndY=-10.5 EndZ=0
    g38: LineSegment StartX=-4.03109 StartY=-10.5 StartZ=0 EndX=-1 EndY=-8.75 EndZ=0
    g39: LineSegment StartX=-1 StartY=-8.75 StartZ=0 EndX=-1 EndY=-5.25 EndZ=0
    g40: LineSegment StartX=-1 StartY=-5.25 StartZ=0 EndX=-4.03109 EndY=-3.5 EndZ=0
    g41: Circle [constr] CenterX=-4.03109 CenterY=-7 CenterZ=0 NormalX=0 NormalY=0 NormalZ=1 AngleXU=0 Radius=3.5
    g42: LineSegment StartX=4.03109 StartY=-3.5 StartZ=0 EndX=1 EndY=-5.25 EndZ=0
    g43: LineSegment StartX=1 StartY=-5.25 StartZ=0 EndX=1 EndY=-8.75 EndZ=0
    g44: LineSegment StartX=1 StartY=-8.75 StartZ=0 EndX=4.03109 EndY=-10.5 EndZ=0
    g45: LineSegment StartX=4.03109 StartY=-10.5 StartZ=0 EndX=7.06218 EndY=-8.75 EndZ=0
    g46: LineSegment StartX=7.06218 StartY=-8.75 StartZ=0 EndX=7.06218 EndY=-5.25 EndZ=0
    g47: LineSegment StartX=7.06218 StartY=-5.25 StartZ=0 EndX=4.03109 EndY=-3.5 EndZ=0
    g48: Circle [constr] CenterX=4.03109 CenterY=-7 CenterZ=0 NormalX=0 NormalY=0 NormalZ=1 AngleXU=0 Radius=3.5
  constraints (117):
    c: Coincident(g0,g1)
    c: Coincident(g1,g2)
    c: Coincident(g2,g3)
    c: Coincident(g3,g4)
    c: Coincident(g4,g5)
    c: Coincident(g5,g0)
    c: Equal(g0, g1-g5) x5
    c: PointOnObject(g0,g6)
    c: PointOnObject(g1,g6)
    c: PointOnObject(g2,g6)
    c: PointOnObject(g3,g6)
    c: PointOnObject(g4,g6)
    c: PointOnObject(g5,g6)
    c: Coincident(g6,g-1)
    c: Diameter(g6) = 7
    c: PointOnObject(g0,g-2)
    c: Coincident(g7,g8)
    c: Coincident(g8,g9)
    c: Coincident(g9,g10)
    c: Coincident(g10,g11)
    c: Coincident(g11,g12)
    c: Coincident(g12,g7)
    c: Equal(g7, g8-g12) x5
    c: PointOnObject(g7,g13)
    c: PointOnObject(g8,g13)
    c: PointOnObject(g9,g13)
    c: PointOnObject(g10,g13)
    c: PointOnObject(g11,g13)
    c: PointOnObject(g12,g13)
    c: PointOnObject(g13,g-1)
    c: Diameter(g13) = 7
    c: Distance(g6,g13) = 8
    c: Horizontal(g0,g10)
    c: Coincident(g14,g15)
    c: Coincident(g15,g16)
    c: Coincident(g16,g17)
    c: Coincident(g17,g18)
    c: Coincident(g18,g19)
    c: Coincident(g19,g14)
    c: Equal(g14, g15-g19) x5
    c: PointOnObject(g14,g20)
    c: PointOnObject(g15,g20)
    c: PointOnObject(g16,g20)
    c: PointOnObject(g17,g20)
    c: PointOnObject(g18,g20)
    c: PointOnObject(g19,g20)
    c: Diameter(g20) = 7
    c: DistanceY(g-1,g20) = 7
    c: Vertical(g18)
    c: Distance(g17,g-2) = 1
    c: Coincident(g21,g22)
    c: Coincident(g22,g23)
    c: Coincident(g23,g24)
    c: Coincident(g24,g25)
    c: Coincident(g25,g26)
    c: Coincident(g26,g21)
    c: Equal(g21, g22-g26) x5
    c: PointOnObject(g21,g27)
    c: PointOnObject(g22,g27)
    c: PointOnObject(g23,g27)
    c: PointOnObject(g24,g27)
    c: PointOnObject(g25,g27)
    c: PointOnObject(g26,g27)
    c: Diameter(g27) = 7
    c: DistanceY(g-1,g27) = 7
    c: DistanceX(g21,g-1) = 1
    c: Vertical(g21)
    c: Coincident(g28,g29)
    c: Coincident(g29,g30)
    c: Coincident(g30,g31)
    c: Coincident(g31,g32)
    c: Coincident(g32,g33)
    c: Coincident(g33,g28)
    c: Equal(g28, g29-g33) x5
    c: PointOnObject(g28,g34)
    c: PointOnObject(g29,g34)
    c: PointOnObject(g30,g34)
    c: PointOnObject(g31,g34)
    c: PointOnObject(g32,g34)
    c: PointOnObject(g33,g34)
    c: PointOnObject(g34,g-1)
    c: Diameter(g34) = 7
    c: Vertical(g31)
    c: DistanceX(g34,g-1) = 8
    c: Coincident(g35,g36)
    c: Coincident(g36,g37)
    c: Coincident(g37,g38)
    c: Coincident(g38,g39)
    c: Coincident(g39,g40)
    c: Coincident(g40,g35)
    c: Equal(g35, g36-g40) x5
    c: PointOnObject(g35,g41)
    c: PointOnObject(g36,g41)
    c: PointOnObject(g37,g41)
    c: PointOnObject(g38,g41)
    c: PointOnObject(g39,g41)
    c: PointOnObject(g40,g41)
    c: Coincident(g42,g43)
    c: Coincident(g43,g44)
    c: Coincident(g44,g45)
    c: Coincident(g45,g46)
    c: Coincident(g46,g47)
    c: Coincident(g47,g42)
    c: Equal(g42, g43-g47) x5
    c: PointOnObject(g42,g48)
    c: PointOnObject(g43,g48)
    c: PointOnObject(g44,g48)
    c: PointOnObject(g45,g48)
    c: PointOnObject(g46,g48)
    c: PointOnObject(g47,g48)
    c: Equal(g41,g48)
    c: Diameter(g41) = 7
    c: Vertical(g39)
    c: Vertical(g43)
    c: Distance(g-2,g39) = 1
    c: Symmetric(g38,g43,g-2)
    c: Distance(g41,g-1) = 7
FEATURE [Part::Extrusion] Extrude425  label="hex040"
  Base = -> Sketch433
  Dir = (0,-1,2e-16)
  DirMode = 2
  FaceMakerClass = Part::FaceMakerBullseye
  FaceMakerMode = 3
  LengthFwd = 10
  LengthRev = 0
  Placement = pos=(72,0,14) rot=(0,0,1;0rad)
  Solid = true
  Symmetric = false
FEATURE [Sketcher::SketchObject] Sketch434
  ArcFitTolerance = 1e-06
  FullyConstrained = true
  MakeInternals = false
  Placement = pos=(0,0,0) rot=(1,0,0;1.5708rad)
  sketch-geometry (49):
    g0: LineSegment StartX=1e-16 StartY=3.5 StartZ=0 EndX=-3.03109 EndY=1.75 EndZ=0
    g1: LineSegment StartX=-3.03109 StartY=1.75 StartZ=0 EndX=-3.03109 EndY=-1.75 EndZ=0
    g2: LineSegment StartX=-3.03109 StartY=-1.75 StartZ=0 EndX=-1e-16 EndY=-3.5 EndZ=0
    g3: LineSegment StartX=-1e-16 StartY=-3.5 StartZ=0 EndX=3.03109 EndY=-1.75 EndZ=0
    g4: LineSegment StartX=3.03109 StartY=-1.75 StartZ=0 EndX=3.03109 EndY=1.75 EndZ=0
    g5: LineSegment StartX=3.03109 StartY=1.75 StartZ=0 EndX=1e-16 EndY=3.5 EndZ=0
    g6: Circle [constr] CenterX=0 CenterY=0 CenterZ=0 NormalX=0 NormalY=0 NormalZ=1 AngleXU=0 Radius=3.5
    g7: LineSegment StartX=4.96892 StartY=-1.75002 StartZ=0 EndX=8.00002 EndY=-3.5 EndZ=0
    g8: LineSegment StartX=8.00002 StartY=-3.5 StartZ=0 EndX=11.0311 EndY=-1.74998 EndZ=0
    g9: LineSegment StartX=11.0311 StartY=-1.74998 StartZ=0 EndX=11.0311 EndY=1.75002 EndZ=0
    g10: LineSegment StartX=11.0311 StartY=1.75002 StartZ=0 EndX=7.99998 EndY=3.5 EndZ=0
    g11: LineSegment StartX=7.99998 StartY=3.5 StartZ=0 EndX=4.9689 EndY=1.74998 EndZ=0
    g12: LineSegment StartX=4.9689 StartY=1.74998 StartZ=0 EndX=4.96892 EndY=-1.75002 EndZ=0
    g13: Circle [constr] CenterX=8 CenterY=0 CenterZ=0 NormalX=0 NormalY=0 NormalZ=1 AngleXU=0 Radius=3.5
    g14: LineSegment StartX=4.03109 StartY=3.5 StartZ=0 EndX=7.06218 EndY=5.25 EndZ=0
    g15: LineSegment StartX=7.06218 StartY=5.25 StartZ=0 EndX=7.06218 EndY=8.75 EndZ=0
    g16: LineSegment StartX=7.06218 StartY=8.75 StartZ=0 EndX=4.03109 EndY=10.5 EndZ=0
    g17: LineSegment StartX=4.03109 StartY=10.5 StartZ=0 EndX=1 EndY=8.75 EndZ=0
    g18: LineSegment StartX=1 StartY=8.75 StartZ=0 EndX=1 EndY=5.25 EndZ=0
    g19: LineSegment StartX=1 StartY=5.25 StartZ=0 EndX=4.03109 EndY=3.5 EndZ=0
    g20: Circle [constr] CenterX=4.03109 CenterY=7 CenterZ=0 NormalX=0 NormalY=0 NormalZ=1 AngleXU=0 Radius=3.5
    g21: LineSegment StartX=-1 StartY=5.25 StartZ=0 EndX=-1 EndY=8.75 EndZ=0
    g22: LineSegment StartX=-1 StartY=8.75 StartZ=0 EndX=-4.03109 EndY=10.5 EndZ=0
    g23: LineSegment StartX=-4.03109 StartY=10.5 StartZ=0 EndX=-7.06218 EndY=8.75 EndZ=0
    g24: LineSegment StartX=-7.06218 StartY=8.75 StartZ=0 EndX=-7.06218 EndY=5.25 EndZ=0
    g25: LineSegment StartX=-7.06218 StartY=5.25 StartZ=0 EndX=-4.03109 EndY=3.5 EndZ=0
    g26: LineSegment StartX=-4.03109 StartY=3.5 StartZ=0 EndX=-1 EndY=5.25 EndZ=0
    g27: Circle [constr] CenterX=-4.03109 CenterY=7 CenterZ=0 NormalX=0 NormalY=0 NormalZ=1 AngleXU=0 Radius=3.5
    g28: LineSegment StartX=-4.96891 StartY=-1.75 StartZ=0 EndX=-4.96891 EndY=1.75 EndZ=0
    g29: LineSegment StartX=-4.96891 StartY=1.75 StartZ=0 EndX=-8 EndY=3.5 EndZ=0
    g30: LineSegment StartX=-8 StartY=3.5 StartZ=0 EndX=-11.0311 EndY=1.75 EndZ=0
    g31: LineSegment StartX=-11.0311 StartY=1.75 StartZ=0 EndX=-11.0311 EndY=-1.75 EndZ=0
    g32: LineSegment StartX=-11.0311 StartY=-1.75 StartZ=0 EndX=-8 EndY=-3.5 EndZ=0
    g33: LineSegment StartX=-8 StartY=-3.5 StartZ=0 EndX=-4.96891 EndY=-1.75 EndZ=0
    g34: Circle [constr] CenterX=-8 CenterY=0 CenterZ=0 NormalX=0 NormalY=0 NormalZ=1 AngleXU=0 Radius=3.5
    g35: LineSegment StartX=-4.03109 StartY=-3.5 StartZ=0 EndX=-7.06218 EndY=-5.25 EndZ=0
    g36: LineSegment StartX=-7.06218 StartY=-5.25 StartZ=0 EndX=-7.06218 EndY=-8.75 EndZ=0
    g37: LineSegment StartX=-7.06218 StartY=-8.75 StartZ=0 EndX=-4.03109 EndY=-10.5 EndZ=0
    g38: LineSegment StartX=-4.03109 StartY=-10.5 StartZ=0 EndX=-1 EndY=-8.75 EndZ=0
    g39: LineSegment StartX=-1 StartY=-8.75 StartZ=0 EndX=-1 EndY=-5.25 EndZ=0
    g40: LineSegment StartX=-1 StartY=-5.25 StartZ=0 EndX=-4.03109 EndY=-3.5 EndZ=0
    g41: Circle [constr] CenterX=-4.03109 CenterY=-7 CenterZ=0 NormalX=0 NormalY=0 NormalZ=1 AngleXU=0 Radius=3.5
    g42: LineSegment StartX=4.03109 StartY=-3.5 StartZ=0 EndX=1 EndY=-5.25 EndZ=0
    g43: LineSegment StartX=1 StartY=-5.25 StartZ=0 EndX=1 EndY=-8.75 EndZ=0
    g44: LineSegment StartX=1 StartY=-8.75 StartZ=0 EndX=4.03109 EndY=-10.5 EndZ=0
    g45: LineSegment StartX=4.03109 StartY=-10.5 StartZ=0 EndX=7.06218 EndY=-8.75 EndZ=0
    g46: LineSegment StartX=7.06218 StartY=-8.75 StartZ=0 EndX=7.06218 EndY=-5.25 EndZ=0
    g47: LineSegment StartX=7.06218 StartY=-5.25 StartZ=0 EndX=4.03109 EndY=-3.5 EndZ=0
    g48: Circle [constr] CenterX=4.03109 CenterY=-7 CenterZ=0 NormalX=0 NormalY=0 NormalZ=1 AngleXU=0 Radius=3.5
  constraints (117):
    c: Coincident(g0,g1)
    c: Coincident(g1,g2)
    c: Coincident(g2,g3)
    c: Coincident(g3,g4)
    c: Coincident(g4,g5)
    c: Coincident(g5,g0)
    c: Equal(g0, g1-g5) x5
    c: PointOnObject(g0,g6)
    c: PointOnObject(g1,g6)
    c: PointOnObject(g2,g6)
    c: PointOnObject(g3,g6)
    c: PointOnObject(g4,g6)
    c: PointOnObject(g5,g6)
    c: Coincident(g6,g-1)
    c: Diameter(g6) = 7
    c: PointOnObject(g0,g-2)
    c: Coincident(g7,g8)
    c: Coincident(g8,g9)
    c: Coincident(g9,g10)
    c: Coincident(g10,g11)
    c: Coincident(g11,g12)
    c: Coincident(g12,g7)
    c: Equal(g7, g8-g12) x5
    c: PointOnObject(g7,g13)
    c: PointOnObject(g8,g13)
    c: PointOnObject(g9,g13)
    c: PointOnObject(g10,g13)
    c: PointOnObject(g11,g13)
    c: PointOnObject(g12,g13)
    c: PointOnObject(g13,g-1)
    c: Diameter(g13) = 7
    c: Distance(g6,g13) = 8
    c: Horizontal(g0,g10)
    c: Coincident(g14,g15)
    c: Coincident(g15,g16)
    c: Coincident(g16,g17)
    c: Coincident(g17,g18)
    c: Coincident(g18,g19)
    c: Coincident(g19,g14)
    c: Equal(g14, g15-g19) x5
    c: PointOnObject(g14,g20)
    c: PointOnObject(g15,g20)
    c: PointOnObject(g16,g20)
    c: PointOnObject(g17,g20)
    c: PointOnObject(g18,g20)
    c: PointOnObject(g19,g20)
    c: Diameter(g20) = 7
    c: DistanceY(g-1,g20) = 7
    c: Vertical(g18)
    c: Distance(g17,g-2) = 1
    c: Coincident(g21,g22)
    c: Coincident(g22,g23)
    c: Coincident(g23,g24)
    c: Coincident(g24,g25)
    c: Coincident(g25,g26)
    c: Coincident(g26,g21)
    c: Equal(g21, g22-g26) x5
    c: PointOnObject(g21,g27)
    c: PointOnObject(g22,g27)
    c: PointOnObject(g23,g27)
    c: PointOnObject(g24,g27)
    c: PointOnObject(g25,g27)
    c: PointOnObject(g26,g27)
    c: Diameter(g27) = 7
    c: DistanceY(g-1,g27) = 7
    c: DistanceX(g21,g-1) = 1
    c: Vertical(g21)
    c: Coincident(g28,g29)
    c: Coincident(g29,g30)
    c: Coincident(g30,g31)
    c: Coincident(g31,g32)
    c: Coincident(g32,g33)
    c: Coincident(g33,g28)
    c: Equal(g28, g29-g33) x5
    c: PointOnObject(g28,g34)
    c: PointOnObject(g29,g34)
    c: PointOnObject(g30,g34)
    c: PointOnObject(g31,g34)
    c: PointOnObject(g32,g34)
    c: PointOnObject(g33,g34)
    c: PointOnObject(g34,g-1)
    c: Diameter(g34) = 7
    c: Vertical(g31)
    c: DistanceX(g34,g-1) = 8
    c: Coincident(g35,g36)
    c: Coincident(g36,g37)
    c: Coincident(g37,g38)
    c: Coincident(g38,g39)
    c: Coincident(g39,g40)
    c: Coincident(g40,g35)
    c: Equal(g35, g36-g40) x5
    c: PointOnObject(g35,g41)
    c: PointOnObject(g36,g41)
    c: PointOnObject(g37,g41)
    c: PointOnObject(g38,g41)
    c: PointOnObject(g39,g41)
    c: PointOnObject(g40,g41)
    c: Coincident(g42,g43)
    c: Coincident(g43,g44)
    c: Coincident(g44,g45)
    c: Coincident(g45,g46)
    c: Coincident(g46,g47)
    c: Coincident(g47,g42)
    c: Equal(g42, g43-g47) x5
    c: PointOnObject(g42,g48)
    c: PointOnObject(g43,g48)
    c: PointOnObject(g44,g48)
    c: PointOnObject(g45,g48)
    c: PointOnObject(g46,g48)
    c: PointOnObject(g47,g48)
    c: Equal(g41,g48)
    c: Diameter(g41) = 7
    c: Vertical(g39)
    c: Vertical(g43)
    c: Distance(g-2,g39) = 1
    c: Symmetric(g38,g43,g-2)
    c: Distance(g41,g-1) = 7
FEATURE [Part::Extrusion] Extrude426  label="hex041"
  Base = -> Sketch434
  Dir = (0,-1,2e-16)
  DirMode = 2
  FaceMakerClass = Part::FaceMakerBullseye
  FaceMakerMode = 3
  LengthFwd = 10
  LengthRev = 0
  Placement = pos=(80,0,0) rot=(0,0,1;0rad)
  Solid = true
  Symmetric = false
FEATURE [Sketcher::SketchObject] Sketch435
  ArcFitTolerance = 1e-06
  FullyConstrained = true
  MakeInternals = false
  Placement = pos=(0,0,0) rot=(1,0,0;1.5708rad)
  sketch-geometry (49):
    g0: LineSegment StartX=1e-16 StartY=3.5 StartZ=0 EndX=-3.03109 EndY=1.75 EndZ=0
    g1: LineSegment StartX=-3.03109 StartY=1.75 StartZ=0 EndX=-3.03109 EndY=-1.75 EndZ=0
    g2: LineSegment StartX=-3.03109 StartY=-1.75 StartZ=0 EndX=-1e-16 EndY=-3.5 EndZ=0
    g3: LineSegment StartX=-1e-16 StartY=-3.5 StartZ=0 EndX=3.03109 EndY=-1.75 EndZ=0
    g4: LineSegment StartX=3.03109 StartY=-1.75 StartZ=0 EndX=3.03109 EndY=1.75 EndZ=0
    g5: LineSegment StartX=3.03109 StartY=1.75 StartZ=0 EndX=1e-16 EndY=3.5 EndZ=0
    g6: Circle [constr] CenterX=0 CenterY=0 CenterZ=0 NormalX=0 NormalY=0 NormalZ=1 AngleXU=0 Radius=3.5
    g7: LineSegment StartX=4.96892 StartY=-1.75002 StartZ=0 EndX=8.00002 EndY=-3.5 EndZ=0
    g8: LineSegment StartX=8.00002 StartY=-3.5 StartZ=0 EndX=11.0311 EndY=-1.74998 EndZ=0
    g9: LineSegment StartX=11.0311 StartY=-1.74998 StartZ=0 EndX=11.0311 EndY=1.75002 EndZ=0
    g10: LineSegment StartX=11.0311 StartY=1.75002 StartZ=0 EndX=7.99998 EndY=3.5 EndZ=0
    g11: LineSegment StartX=7.99998 StartY=3.5 StartZ=0 EndX=4.9689 EndY=1.74998 EndZ=0
    g12: LineSegment StartX=4.9689 StartY=1.74998 StartZ=0 EndX=4.96892 EndY=-1.75002 EndZ=0
    g13: Circle [constr] CenterX=8 CenterY=0 CenterZ=0 NormalX=0 NormalY=0 NormalZ=1 AngleXU=0 Radius=3.5
    g14: LineSegment StartX=4.03109 StartY=3.5 StartZ=0 EndX=7.06218 EndY=5.25 EndZ=0
    g15: LineSegment StartX=7.06218 StartY=5.25 StartZ=0 EndX=7.06218 EndY=8.75 EndZ=0
    g16: LineSegment StartX=7.06218 StartY=8.75 StartZ=0 EndX=4.03109 EndY=10.5 EndZ=0
    g17: LineSegment StartX=4.03109 StartY=10.5 StartZ=0 EndX=1 EndY=8.75 EndZ=0
    g18: LineSegment StartX=1 StartY=8.75 StartZ=0 EndX=1 EndY=5.25 EndZ=0
    g19: LineSegment StartX=1 StartY=5.25 StartZ=0 EndX=4.03109 EndY=3.5 EndZ=0
    g20: Circle [constr] CenterX=4.03109 CenterY=7 CenterZ=0 NormalX=0 NormalY=0 NormalZ=1 AngleXU=0 Radius=3.5
    g21: LineSegment StartX=-1 StartY=5.25 StartZ=0 EndX=-1 EndY=8.75 EndZ=0
    g22: LineSegment StartX=-1 StartY=8.75 StartZ=0 EndX=-4.03109 EndY=10.5 EndZ=0
    g23: LineSegment StartX=-4.03109 StartY=10.5 StartZ=0 EndX=-7.06218 EndY=8.75 EndZ=0
    g24: LineSegment StartX=-7.06218 StartY=8.75 StartZ=0 EndX=-7.06218 EndY=5.25 EndZ=0
    g25: LineSegment StartX=-7.06218 StartY=5.25 StartZ=0 EndX=-4.03109 EndY=3.5 EndZ=0
    g26: LineSegment StartX=-4.03109 StartY=3.5 StartZ=0 EndX=-1 EndY=5.25 EndZ=0
    g27: Circle [constr] CenterX=-4.03109 CenterY=7 CenterZ=0 NormalX=0 NormalY=0 NormalZ=1 AngleXU=0 Radius=3.5
    g28: LineSegment StartX=-4.96891 StartY=-1.75 StartZ=0 EndX=-4.96891 EndY=1.75 EndZ=0
    g29: LineSegment StartX=-4.96891 StartY=1.75 StartZ=0 EndX=-8 EndY=3.5 EndZ=0
    g30: LineSegment StartX=-8 StartY=3.5 StartZ=0 EndX=-11.0311 EndY=1.75 EndZ=0
    g31: LineSegment StartX=-11.0311 StartY=1.75 StartZ=0 EndX=-11.0311 EndY=-1.75 EndZ=0
    g32: LineSegment StartX=-11.0311 StartY=-1.75 StartZ=0 EndX=-8 EndY=-3.5 EndZ=0
    g33: LineSegment StartX=-8 StartY=-3.5 StartZ=0 EndX=-4.96891 EndY=-1.75 EndZ=0
    g34: Circle [constr] CenterX=-8 CenterY=0 CenterZ=0 NormalX=0 NormalY=0 NormalZ=1 AngleXU=0 Radius=3.5
    g35: LineSegment StartX=-4.03109 StartY=-3.5 StartZ=0 EndX=-7.06218 EndY=-5.25 EndZ=0
    g36: LineSegment StartX=-7.06218 StartY=-5.25 StartZ=0 EndX=-7.06218 EndY=-8.75 EndZ=0
    g37: LineSegment StartX=-7.06218 StartY=-8.75 StartZ=0 EndX=-4.03109 EndY=-10.5 EndZ=0
    g38: LineSegment StartX=-4.03109 StartY=-10.5 StartZ=0 EndX=-1 EndY=-8.75 EndZ=0
    g39: LineSegment StartX=-1 StartY=-8.75 StartZ=0 EndX=-1 EndY=-5.25 EndZ=0
    g40: LineSegment StartX=-1 StartY=-5.25 StartZ=0 EndX=-4.03109 EndY=-3.5 EndZ=0
    g41: Circle [constr] CenterX=-4.03109 CenterY=-7 CenterZ=0 NormalX=0 NormalY=0 NormalZ=1 AngleXU=0 Radius=3.5
    g42: LineSegment StartX=4.03109 StartY=-3.5 StartZ=0 EndX=1 EndY=-5.25 EndZ=0
    g43: LineSegment StartX=1 StartY=-5.25 StartZ=0 EndX=1 EndY=-8.75 EndZ=0
    g44: LineSegment StartX=1 StartY=-8.75 StartZ=0 EndX=4.03109 EndY=-10.5 EndZ=0
    g45: LineSegment StartX=4.03109 StartY=-10.5 StartZ=0 EndX=7.06218 EndY=-8.75 EndZ=0
    g46: LineSegment StartX=7.06218 StartY=-8.75 StartZ=0 EndX=7.06218 EndY=-5.25 EndZ=0
    g47: LineSegment StartX=7.06218 StartY=-5.25 StartZ=0 EndX=4.03109 EndY=-3.5 EndZ=0
    g48: Circle [constr] CenterX=4.03109 CenterY=-7 CenterZ=0 NormalX=0 NormalY=0 NormalZ=1 AngleXU=0 Radius=3.5
  constraints (117):
    c: Coincident(g0,g1)
    c: Coincident(g1,g2)
    c: Coincident(g2,g3)
    c: Coincident(g3,g4)
    c: Coincident(g4,g5)
    c: Coincident(g5,g0)
    c: Equal(g0, g1-g5) x5
    c: PointOnObject(g0,g6)
    c: PointOnObject(g1,g6)
    c: PointOnObject(g2,g6)
    c: PointOnObject(g3,g6)
    c: PointOnObject(g4,g6)
    c: PointOnObject(g5,g6)
    c: Coincident(g6,g-1)
    c: Diameter(g6) = 7
    c: PointOnObject(g0,g-2)
    c: Coincident(g7,g8)
    c: Coincident(g8,g9)
    c: Coincident(g9,g10)
    c: Coincident(g10,g11)
    c: Coincident(g11,g12)
    c: Coincident(g12,g7)
    c: Equal(g7, g8-g12) x5
    c: PointOnObject(g7,g13)
    c: PointOnObject(g8,g13)
    c: PointOnObject(g9,g13)
    c: PointOnObject(g10,g13)
    c: PointOnObject(g11,g13)
    c: PointOnObject(g12,g13)
    c: PointOnObject(g13,g-1)
    c: Diameter(g13) = 7
    c: Distance(g6,g13) = 8
    c: Horizontal(g0,g10)
    c: Coincident(g14,g15)
    c: Coincident(g15,g16)
    c: Coincident(g16,g17)
    c: Coincident(g17,g18)
    c: Coincident(g18,g19)
    c: Coincident(g19,g14)
    c: Equal(g14, g15-g19) x5
    c: PointOnObject(g14,g20)
    c: PointOnObject(g15,g20)
    c: PointOnObject(g16,g20)
    c: PointOnObject(g17,g20)
    c: PointOnObject(g18,g20)
    c: PointOnObject(g19,g20)
    c: Diameter(g20) = 7
    c: DistanceY(g-1,g20) = 7
    c: Vertical(g18)
    c: Distance(g17,g-2) = 1
    c: Coincident(g21,g22)
    c: Coincident(g22,g23)
    c: Coincident(g23,g24)
    c: Coincident(g24,g25)
    c: Coincident(g25,g26)
    c: Coincident(g26,g21)
    c: Equal(g21, g22-g26) x5
    c: PointOnObject(g21,g27)
    c: PointOnObject(g22,g27)
    c: PointOnObject(g23,g27)
    c: PointOnObject(g24,g27)
    c: PointOnObject(g25,g27)
    c: PointOnObject(g26,g27)
    c: Diameter(g27) = 7
    c: DistanceY(g-1,g27) = 7
    c: DistanceX(g21,g-1) = 1
    c: Vertical(g21)
    c: Coincident(g28,g29)
    c: Coincident(g29,g30)
    c: Coincident(g30,g31)
    c: Coincident(g31,g32)
    c: Coincident(g32,g33)
    c: Coincident(g33,g28)
    c: Equal(g28, g29-g33) x5
    c: PointOnObject(g28,g34)
    c: PointOnObject(g29,g34)
    c: PointOnObject(g30,g34)
    c: PointOnObject(g31,g34)
    c: PointOnObject(g32,g34)
    c: PointOnObject(g33,g34)
    c: PointOnObject(g34,g-1)
    c: Diameter(g34) = 7
    c: Vertical(g31)
    c: DistanceX(g34,g-1) = 8
    c: Coincident(g35,g36)
    c: Coincident(g36,g37)
    c: Coincident(g37,g38)
    c: Coincident(g38,g39)
    c: Coincident(g39,g40)
    c: Coincident(g40,g35)
    c: Equal(g35, g36-g40) x5
    c: PointOnObject(g35,g41)
    c: PointOnObject(g36,g41)
    c: PointOnObject(g37,g41)
    c: PointOnObject(g38,g41)
    c: PointOnObject(g39,g41)
    c: PointOnObject(g40,g41)
    c: Coincident(g42,g43)
    c: Coincident(g43,g44)
    c: Coincident(g44,g45)
    c: Coincident(g45,g46)
    c: Coincident(g46,g47)
    c: Coincident(g47,g42)
    c: Equal(g42, g43-g47) x5
    c: PointOnObject(g42,g48)
    c: PointOnObject(g43,g48)
    c: PointOnObject(g44,g48)
    c: PointOnObject(g45,g48)
    c: PointOnObject(g46,g48)
    c: PointOnObject(g47,g48)
    c: Equal(g41,g48)
    c: Diameter(g41) = 7
    c: Vertical(g39)
    c: Vertical(g43)
    c: Distance(g-2,g39) = 1
    c: Symmetric(g38,g43,g-2)
    c: Distance(g41,g-1) = 7
FEATURE [Part::Extrusion] Extrude427  label="hex042"
  Base = -> Sketch435
  Dir = (0,-1,2e-16)
  DirMode = 2
  FaceMakerClass = Part::FaceMakerBullseye
  FaceMakerMode = 3
  LengthFwd = 10
  LengthRev = 0
  Placement = pos=(104,0,0) rot=(0,0,1;0rad)
  Solid = true
  Symmetric = false
FEATURE [Sketcher::SketchObject] Sketch436
  ArcFitTolerance = 1e-06
  FullyConstrained = true
  MakeInternals = false
  Placement = pos=(0,0,0) rot=(1,0,0;1.5708rad)
  sketch-geometry (49):
    g0: LineSegment StartX=1e-16 StartY=3.5 StartZ=0 EndX=-3.03109 EndY=1.75 EndZ=0
    g1: LineSegment StartX=-3.03109 StartY=1.75 StartZ=0 EndX=-3.03109 EndY=-1.75 EndZ=0
    g2: LineSegment StartX=-3.03109 StartY=-1.75 StartZ=0 EndX=-1e-16 EndY=-3.5 EndZ=0
    g3: LineSegment StartX=-1e-16 StartY=-3.5 StartZ=0 EndX=3.03109 EndY=-1.75 EndZ=0
    g4: LineSegment StartX=3.03109 StartY=-1.75 StartZ=0 EndX=3.03109 EndY=1.75 EndZ=0
    g5: LineSegment StartX=3.03109 StartY=1.75 StartZ=0 EndX=1e-16 EndY=3.5 EndZ=0
    g6: Circle [constr] CenterX=0 CenterY=0 CenterZ=0 NormalX=0 NormalY=0 NormalZ=1 AngleXU=0 Radius=3.5
    g7: LineSegment StartX=4.96892 StartY=-1.75002 StartZ=0 EndX=8.00002 EndY=-3.5 EndZ=0
    g8: LineSegment StartX=8.00002 StartY=-3.5 StartZ=0 EndX=11.0311 EndY=-1.74998 EndZ=0
    g9: LineSegment StartX=11.0311 StartY=-1.74998 StartZ=0 EndX=11.0311 EndY=1.75002 EndZ=0
    g10: LineSegment StartX=11.0311 StartY=1.75002 StartZ=0 EndX=7.99998 EndY=3.5 EndZ=0
    g11: LineSegment StartX=7.99998 StartY=3.5 StartZ=0 EndX=4.9689 EndY=1.74998 EndZ=0
    g12: LineSegment StartX=4.9689 StartY=1.74998 StartZ=0 EndX=4.96892 EndY=-1.75002 EndZ=0
    g13: Circle [constr] CenterX=8 CenterY=0 CenterZ=0 NormalX=0 NormalY=0 NormalZ=1 AngleXU=0 Radius=3.5
    g14: LineSegment StartX=4.03109 StartY=3.5 StartZ=0 EndX=7.06218 EndY=5.25 EndZ=0
    g15: LineSegment StartX=7.06218 StartY=5.25 StartZ=0 EndX=7.06218 EndY=8.75 EndZ=0
    g16: LineSegment StartX=7.06218 StartY=8.75 StartZ=0 EndX=4.03109 EndY=10.5 EndZ=0
    g17: LineSegment StartX=4.03109 StartY=10.5 StartZ=0 EndX=1 EndY=8.75 EndZ=0
    g18: LineSegment StartX=1 StartY=8.75 StartZ=0 EndX=1 EndY=5.25 EndZ=0
    g19: LineSegment StartX=1 StartY=5.25 StartZ=0 EndX=4.03109 EndY=3.5 EndZ=0
    g20: Circle [constr] CenterX=4.03109 CenterY=7 CenterZ=0 NormalX=0 NormalY=0 NormalZ=1 AngleXU=0 Radius=3.5
    g21: LineSegment StartX=-1 StartY=5.25 StartZ=0 EndX=-1 EndY=8.75 EndZ=0
    g22: LineSegment StartX=-1 StartY=8.75 StartZ=0 EndX=-4.03109 EndY=10.5 EndZ=0
    g23: LineSegment StartX=-4.03109 StartY=10.5 StartZ=0 EndX=-7.06218 EndY=8.75 EndZ=0
    g24: LineSegment StartX=-7.06218 StartY=8.75 StartZ=0 EndX=-7.06218 EndY=5.25 EndZ=0
    g25: LineSegment StartX=-7.06218 StartY=5.25 StartZ=0 EndX=-4.03109 EndY=3.5 EndZ=0
    g26: LineSegment StartX=-4.03109 StartY=3.5 StartZ=0 EndX=-1 EndY=5.25 EndZ=0
    g27: Circle [constr] CenterX=-4.03109 CenterY=7 CenterZ=0 NormalX=0 NormalY=0 NormalZ=1 AngleXU=0 Radius=3.5
    g28: LineSegment StartX=-4.96891 StartY=-1.75 StartZ=0 EndX=-4.96891 EndY=1.75 EndZ=0
    g29: LineSegment StartX=-4.96891 StartY=1.75 StartZ=0 EndX=-8 EndY=3.5 EndZ=0
    g30: LineSegment StartX=-8 StartY=3.5 StartZ=0 EndX=-11.0311 EndY=1.75 EndZ=0
    g31: LineSegment StartX=-11.0311 StartY=1.75 StartZ=0 EndX=-11.0311 EndY=-1.75 EndZ=0
    g32: LineSegment StartX=-11.0311 StartY=-1.75 StartZ=0 EndX=-8 EndY=-3.5 EndZ=0
    g33: LineSegment StartX=-8 StartY=-3.5 StartZ=0 EndX=-4.96891 EndY=-1.75 EndZ=0
    g34: Circle [constr] CenterX=-8 CenterY=0 CenterZ=0 NormalX=0 NormalY=0 NormalZ=1 AngleXU=0 Radius=3.5
    g35: LineSegment StartX=-4.03109 StartY=-3.5 StartZ=0 EndX=-7.06218 EndY=-5.25 EndZ=0
    g36: LineSegment StartX=-7.06218 StartY=-5.25 StartZ=0 EndX=-7.06218 EndY=-8.75 EndZ=0
    g37: LineSegment StartX=-7.06218 StartY=-8.75 StartZ=0 EndX=-4.03109 EndY=-10.5 EndZ=0
    g38: LineSegment StartX=-4.03109 StartY=-10.5 StartZ=0 EndX=-1 EndY=-8.75 EndZ=0
    g39: LineSegment StartX=-1 StartY=-8.75 StartZ=0 EndX=-1 EndY=-5.25 EndZ=0
    g40: LineSegment StartX=-1 StartY=-5.25 StartZ=0 EndX=-4.03109 EndY=-3.5 EndZ=0
    g41: Circle [constr] CenterX=-4.03109 CenterY=-7 CenterZ=0 NormalX=0 NormalY=0 NormalZ=1 AngleXU=0 Radius=3.5
    g42: LineSegment StartX=4.03109 StartY=-3.5 StartZ=0 EndX=1 EndY=-5.25 EndZ=0
    g43: LineSegment StartX=1 StartY=-5.25 StartZ=0 EndX=1 EndY=-8.75 EndZ=0
    g44: LineSegment StartX=1 StartY=-8.75 StartZ=0 EndX=4.03109 EndY=-10.5 EndZ=0
    g45: LineSegment StartX=4.03109 StartY=-10.5 StartZ=0 EndX=7.06218 EndY=-8.75 EndZ=0
    g46: LineSegment StartX=7.06218 StartY=-8.75 StartZ=0 EndX=7.06218 EndY=-5.25 EndZ=0
    g47: LineSegment StartX=7.06218 StartY=-5.25 StartZ=0 EndX=4.03109 EndY=-3.5 EndZ=0
    g48: Circle [constr] CenterX=4.03109 CenterY=-7 CenterZ=0 NormalX=0 NormalY=0 NormalZ=1 AngleXU=0 Radius=3.5
  constraints (117):
    c: Coincident(g0,g1)
    c: Coincident(g1,g2)
    c: Coincident(g2,g3)
    c: Coincident(g3,g4)
    c: Coincident(g4,g5)
    c: Coincident(g5,g0)
    c: Equal(g0, g1-g5) x5
    c: PointOnObject(g0,g6)
    c: PointOnObject(g1,g6)
    c: PointOnObject(g2,g6)
    c: PointOnObject(g3,g6)
    c: PointOnObject(g4,g6)
    c: PointOnObject(g5,g6)
    c: Coincident(g6,g-1)
    c: Diameter(g6) = 7
    c: PointOnObject(g0,g-2)
    c: Coincident(g7,g8)
    c: Coincident(g8,g9)
    c: Coincident(g9,g10)
    c: Coincident(g10,g11)
    c: Coincident(g11,g12)
    c: Coincident(g12,g7)
    c: Equal(g7, g8-g12) x5
    c: PointOnObject(g7,g13)
    c: PointOnObject(g8,g13)
    c: PointOnObject(g9,g13)
    c: PointOnObject(g10,g13)
    c: PointOnObject(g11,g13)
    c: PointOnObject(g12,g13)
    c: PointOnObject(g13,g-1)
    c: Diameter(g13) = 7
    c: Distance(g6,g13) = 8
    c: Horizontal(g0,g10)
    c: Coincident(g14,g15)
    c: Coincident(g15,g16)
    c: Coincident(g16,g17)
    c: Coincident(g17,g18)
    c: Coincident(g18,g19)
    c: Coincident(g19,g14)
    c: Equal(g14, g15-g19) x5
    c: PointOnObject(g14,g20)
    c: PointOnObject(g15,g20)
    c: PointOnObject(g16,g20)
    c: PointOnObject(g17,g20)
    c: PointOnObject(g18,g20)
    c: PointOnObject(g19,g20)
    c: Diameter(g20) = 7
    c: DistanceY(g-1,g20) = 7
    c: Vertical(g18)
    c: Distance(g17,g-2) = 1
    c: Coincident(g21,g22)
    c: Coincident(g22,g23)
    c: Coincident(g23,g24)
    c: Coincident(g24,g25)
    c: Coincident(g25,g26)
    c: Coincident(g26,g21)
    c: Equal(g21, g22-g26) x5
    c: PointOnObject(g21,g27)
    c: PointOnObject(g22,g27)
    c: PointOnObject(g23,g27)
    c: PointOnObject(g24,g27)
    c: PointOnObject(g25,g27)
    c: PointOnObject(g26,g27)
    c: Diameter(g27) = 7
    c: DistanceY(g-1,g27) = 7
    c: DistanceX(g21,g-1) = 1
    c: Vertical(g21)
    c: Coincident(g28,g29)
    c: Coincident(g29,g30)
    c: Coincident(g30,g31)
    c: Coincident(g31,g32)
    c: Coincident(g32,g33)
    c: Coincident(g33,g28)
    c: Equal(g28, g29-g33) x5
    c: PointOnObject(g28,g34)
    c: PointOnObject(g29,g34)
    c: PointOnObject(g30,g34)
    c: PointOnObject(g31,g34)
    c: PointOnObject(g32,g34)
    c: PointOnObject(g33,g34)
    c: PointOnObject(g34,g-1)
    c: Diameter(g34) = 7
    c: Vertical(g31)
    c: DistanceX(g34,g-1) = 8
    c: Coincident(g35,g36)
    c: Coincident(g36,g37)
    c: Coincident(g37,g38)
    c: Coincident(g38,g39)
    c: Coincident(g39,g40)
    c: Coincident(g40,g35)
    c: Equal(g35, g36-g40) x5
    c: PointOnObject(g35,g41)
    c: PointOnObject(g36,g41)
    c: PointOnObject(g37,g41)
    c: PointOnObject(g38,g41)
    c: PointOnObject(g39,g41)
    c: PointOnObject(g40,g41)
    c: Coincident(g42,g43)
    c: Coincident(g43,g44)
    c: Coincident(g44,g45)
    c: Coincident(g45,g46)
    c: Coincident(g46,g47)
    c: Coincident(g47,g42)
    c: Equal(g42, g43-g47) x5
    c: PointOnObject(g42,g48)
    c: PointOnObject(g43,g48)
    c: PointOnObject(g44,g48)
    c: PointOnObject(g45,g48)
    c: PointOnObject(g46,g48)
    c: PointOnObject(g47,g48)
    c: Equal(g41,g48)
    c: Diameter(g41) = 7
    c: Vertical(g39)
    c: Vertical(g43)
    c: Distance(g-2,g39) = 1
    c: Symmetric(g38,g43,g-2)
    c: Distance(g41,g-1) = 7
FEATURE [Part::Extrusion] Extrude428  label="hex043"
  Base = -> Sketch436
  Dir = (0,-1,2e-16)
  DirMode = 2
  FaceMakerClass = Part::FaceMakerBullseye
  FaceMakerMode = 3
  LengthFwd = 10
  LengthRev = 0
  Placement = pos=(96,0,-14) rot=(0,0,1;0rad)
  Solid = true
  Symmetric = false
FEATURE [Sketcher::SketchObject] Sketch437
  ArcFitTolerance = 1e-06
  FullyConstrained = true
  MakeInternals = false
  Placement = pos=(0,0,0) rot=(1,0,0;1.5708rad)
  sketch-geometry (49):
    g0: LineSegment StartX=1e-16 StartY=3.5 StartZ=0 EndX=-3.03109 EndY=1.75 EndZ=0
    g1: LineSegment StartX=-3.03109 StartY=1.75 StartZ=0 EndX=-3.03109 EndY=-1.75 EndZ=0
    g2: LineSegment StartX=-3.03109 StartY=-1.75 StartZ=0 EndX=-1e-16 EndY=-3.5 EndZ=0
    g3: LineSegment StartX=-1e-16 StartY=-3.5 StartZ=0 EndX=3.03109 EndY=-1.75 EndZ=0
    g4: LineSegment StartX=3.03109 StartY=-1.75 StartZ=0 EndX=3.03109 EndY=1.75 EndZ=0
    g5: LineSegment StartX=3.03109 StartY=1.75 StartZ=0 EndX=1e-16 EndY=3.5 EndZ=0
    g6: Circle [constr] CenterX=0 CenterY=0 CenterZ=0 NormalX=0 NormalY=0 NormalZ=1 AngleXU=0 Radius=3.5
    g7: LineSegment StartX=4.96892 StartY=-1.75002 StartZ=0 EndX=8.00002 EndY=-3.5 EndZ=0
    g8: LineSegment StartX=8.00002 StartY=-3.5 StartZ=0 EndX=11.0311 EndY=-1.74998 EndZ=0
    g9: LineSegment StartX=11.0311 StartY=-1.74998 StartZ=0 EndX=11.0311 EndY=1.75002 EndZ=0
    g10: LineSegment StartX=11.0311 StartY=1.75002 StartZ=0 EndX=7.99998 EndY=3.5 EndZ=0
    g11: LineSegment StartX=7.99998 StartY=3.5 StartZ=0 EndX=4.9689 EndY=1.74998 EndZ=0
    g12: LineSegment StartX=4.9689 StartY=1.74998 StartZ=0 EndX=4.96892 EndY=-1.75002 EndZ=0
    g13: Circle [constr] CenterX=8 CenterY=0 CenterZ=0 NormalX=0 NormalY=0 NormalZ=1 AngleXU=0 Radius=3.5
    g14: LineSegment StartX=4.03109 StartY=3.5 StartZ=0 EndX=7.06218 EndY=5.25 EndZ=0
    g15: LineSegment StartX=7.06218 StartY=5.25 StartZ=0 EndX=7.06218 EndY=8.75 EndZ=0
    g16: LineSegment StartX=7.06218 StartY=8.75 StartZ=0 EndX=4.03109 EndY=10.5 EndZ=0
    g17: LineSegment StartX=4.03109 StartY=10.5 StartZ=0 EndX=1 EndY=8.75 EndZ=0
    g18: LineSegment StartX=1 StartY=8.75 StartZ=0 EndX=1 EndY=5.25 EndZ=0
    g19: LineSegment StartX=1 StartY=5.25 StartZ=0 EndX=4.03109 EndY=3.5 EndZ=0
    g20: Circle [constr] CenterX=4.03109 CenterY=7 CenterZ=0 NormalX=0 NormalY=0 NormalZ=1 AngleXU=0 Radius=3.5
    g21: LineSegment StartX=-1 StartY=5.25 StartZ=0 EndX=-1 EndY=8.75 EndZ=0
    g22: LineSegment StartX=-1 StartY=8.75 StartZ=0 EndX=-4.03109 EndY=10.5 EndZ=0
    g23: LineSegment StartX=-4.03109 StartY=10.5 StartZ=0 EndX=-7.06218 EndY=8.75 EndZ=0
    g24: LineSegment StartX=-7.06218 StartY=8.75 StartZ=0 EndX=-7.06218 EndY=5.25 EndZ=0
    g25: LineSegment StartX=-7.06218 StartY=5.25 StartZ=0 EndX=-4.03109 EndY=3.5 EndZ=0
    g26: LineSegment StartX=-4.03109 StartY=3.5 StartZ=0 EndX=-1 EndY=5.25 EndZ=0
    g27: Circle [constr] CenterX=-4.03109 CenterY=7 CenterZ=0 NormalX=0 NormalY=0 NormalZ=1 AngleXU=0 Radius=3.5
    g28: LineSegment StartX=-4.96891 StartY=-1.75 StartZ=0 EndX=-4.96891 EndY=1.75 EndZ=0
    g29: LineSegment StartX=-4.96891 StartY=1.75 StartZ=0 EndX=-8 EndY=3.5 EndZ=0
    g30: LineSegment StartX=-8 StartY=3.5 StartZ=0 EndX=-11.0311 EndY=1.75 EndZ=0
    g31: LineSegment StartX=-11.0311 StartY=1.75 StartZ=0 EndX=-11.0311 EndY=-1.75 EndZ=0
    g32: LineSegment StartX=-11.0311 StartY=-1.75 StartZ=0 EndX=-8 EndY=-3.5 EndZ=0
    g33: LineSegment StartX=-8 StartY=-3.5 StartZ=0 EndX=-4.96891 EndY=-1.75 EndZ=0
    g34: Circle [constr] CenterX=-8 CenterY=0 CenterZ=0 NormalX=0 NormalY=0 NormalZ=1 AngleXU=0 Radius=3.5
    g35: LineSegment StartX=-4.03109 StartY=-3.5 StartZ=0 EndX=-7.06218 EndY=-5.25 EndZ=0
    g36: LineSegment StartX=-7.06218 StartY=-5.25 StartZ=0 EndX=-7.06218 EndY=-8.75 EndZ=0
    g37: LineSegment StartX=-7.06218 StartY=-8.75 StartZ=0 EndX=-4.03109 EndY=-10.5 EndZ=0
    g38: LineSegment StartX=-4.03109 StartY=-10.5 StartZ=0 EndX=-1 EndY=-8.75 EndZ=0
    g39: LineSegment StartX=-1 StartY=-8.75 StartZ=0 EndX=-1 EndY=-5.25 EndZ=0
    g40: LineSegment StartX=-1 StartY=-5.25 StartZ=0 EndX=-4.03109 EndY=-3.5 EndZ=0
    g41: Circle [constr] CenterX=-4.03109 CenterY=-7 CenterZ=0 NormalX=0 NormalY=0 NormalZ=1 AngleXU=0 Radius=3.5
    g42: LineSegment StartX=4.03109 StartY=-3.5 StartZ=0 EndX=1 EndY=-5.25 EndZ=0
    g43: LineSegment StartX=1 StartY=-5.25 StartZ=0 EndX=1 EndY=-8.75 EndZ=0
    g44: LineSegment StartX=1 StartY=-8.75 StartZ=0 EndX=4.03109 EndY=-10.5 EndZ=0
    g45: LineSegment StartX=4.03109 StartY=-10.5 StartZ=0 EndX=7.06218 EndY=-8.75 EndZ=0
    g46: LineSegment StartX=7.06218 StartY=-8.75 StartZ=0 EndX=7.06218 EndY=-5.25 EndZ=0
    g47: LineSegment StartX=7.06218 StartY=-5.25 StartZ=0 EndX=4.03109 EndY=-3.5 EndZ=0
    g48: Circle [constr] CenterX=4.03109 CenterY=-7 CenterZ=0 NormalX=0 NormalY=0 NormalZ=1 AngleXU=0 Radius=3.5
  constraints (117):
    c: Coincident(g0,g1)
    c: Coincident(g1,g2)
    c: Coincident(g2,g3)
    c: Coincident(g3,g4)
    c: Coincident(g4,g5)
    c: Coincident(g5,g0)
    c: Equal(g0, g1-g5) x5
    c: PointOnObject(g0,g6)
    c: PointOnObject(g1,g6)
    c: PointOnObject(g2,g6)
    c: PointOnObject(g3,g6)
    c: PointOnObject(g4,g6)
    c: PointOnObject(g5,g6)
    c: Coincident(g6,g-1)
    c: Diameter(g6) = 7
    c: PointOnObject(g0,g-2)
    c: Coincident(g7,g8)
    c: Coincident(g8,g9)
    c: Coincident(g9,g10)
    c: Coincident(g10,g11)
    c: Coincident(g11,g12)
    c: Coincident(g12,g7)
    c: Equal(g7, g8-g12) x5
    c: PointOnObject(g7,g13)
    c: PointOnObject(g8,g13)
    c: PointOnObject(g9,g13)
    c: PointOnObject(g10,g13)
    c: PointOnObject(g11,g13)
    c: PointOnObject(g12,g13)
    c: PointOnObject(g13,g-1)
    c: Diameter(g13) = 7
    c: Distance(g6,g13) = 8
    c: Horizontal(g0,g10)
    c: Coincident(g14,g15)
    c: Coincident(g15,g16)
    c: Coincident(g16,g17)
    c: Coincident(g17,g18)
    c: Coincident(g18,g19)
    c: Coincident(g19,g14)
    c: Equal(g14, g15-g19) x5
    c: PointOnObject(g14,g20)
    c: PointOnObject(g15,g20)
    c: PointOnObject(g16,g20)
    c: PointOnObject(g17,g20)
    c: PointOnObject(g18,g20)
    c: PointOnObject(g19,g20)
    c: Diameter(g20) = 7
    c: DistanceY(g-1,g20) = 7
    c: Vertical(g18)
    c: Distance(g17,g-2) = 1
    c: Coincident(g21,g22)
    c: Coincident(g22,g23)
    c: Coincident(g23,g24)
    c: Coincident(g24,g25)
    c: Coincident(g25,g26)
    c: Coincident(g26,g21)
    c: Equal(g21, g22-g26) x5
    c: PointOnObject(g21,g27)
    c: PointOnObject(g22,g27)
    c: PointOnObject(g23,g27)
    c: PointOnObject(g24,g27)
    c: PointOnObject(g25,g27)
    c: PointOnObject(g26,g27)
    c: Diameter(g27) = 7
    c: DistanceY(g-1,g27) = 7
    c: DistanceX(g21,g-1) = 1
    c: Vertical(g21)
    c: Coincident(g28,g29)
    c: Coincident(g29,g30)
    c: Coincident(g30,g31)
    c: Coincident(g31,g32)
    c: Coincident(g32,g33)
    c: Coincident(g33,g28)
    c: Equal(g28, g29-g33) x5
    c: PointOnObject(g28,g34)
    c: PointOnObject(g29,g34)
    c: PointOnObject(g30,g34)
    c: PointOnObject(g31,g34)
    c: PointOnObject(g32,g34)
    c: PointOnObject(g33,g34)
    c: PointOnObject(g34,g-1)
    c: Diameter(g34) = 7
    c: Vertical(g31)
    c: DistanceX(g34,g-1) = 8
    c: Coincident(g35,g36)
    c: Coincident(g36,g37)
    c: Coincident(g37,g38)
    c: Coincident(g38,g39)
    c: Coincident(g39,g40)
    c: Coincident(g40,g35)
    c: Equal(g35, g36-g40) x5
    c: PointOnObject(g35,g41)
    c: PointOnObject(g36,g41)
    c: PointOnObject(g37,g41)
    c: PointOnObject(g38,g41)
    c: PointOnObject(g39,g41)
    c: PointOnObject(g40,g41)
    c: Coincident(g42,g43)
    c: Coincident(g43,g44)
    c: Coincident(g44,g45)
    c: Coincident(g45,g46)
    c: Coincident(g46,g47)
    c: Coincident(g47,g42)
    c: Equal(g42, g43-g47) x5
    c: PointOnObject(g42,g48)
    c: PointOnObject(g43,g48)
    c: PointOnObject(g44,g48)
    c: PointOnObject(g45,g48)
    c: PointOnObject(g46,g48)
    c: PointOnObject(g47,g48)
    c: Equal(g41,g48)
    c: Diameter(g41) = 7
    c: Vertical(g39)
    c: Vertical(g43)
    c: Distance(g-2,g39) = 1
    c: Symmetric(g38,g43,g-2)
    c: Distance(g41,g-1) = 7
FEATURE [Part::Extrusion] Extrude429  label="hex044"
  Base = -> Sketch437
  Dir = (0,-1,2e-16)
  DirMode = 2
  FaceMakerClass = Part::FaceMakerBullseye
  FaceMakerMode = 3
  LengthFwd = 10
  LengthRev = 0
  Placement = pos=(88,0,-28) rot=(0,0,1;0rad)
  Solid = true
  Symmetric = false
FEATURE [Sketcher::SketchObject] Sketch438
  ArcFitTolerance = 1e-06
  FullyConstrained = true
  MakeInternals = false
  Placement = pos=(0,0,0) rot=(1,0,0;1.5708rad)
  sketch-geometry (49):
    g0: LineSegment StartX=1e-16 StartY=3.5 StartZ=0 EndX=-3.03109 EndY=1.75 EndZ=0
    g1: LineSegment StartX=-3.03109 StartY=1.75 StartZ=0 EndX=-3.03109 EndY=-1.75 EndZ=0
    g2: LineSegment StartX=-3.03109 StartY=-1.75 StartZ=0 EndX=-1e-16 EndY=-3.5 EndZ=0
    g3: LineSegment StartX=-1e-16 StartY=-3.5 StartZ=0 EndX=3.03109 EndY=-1.75 EndZ=0
    g4: LineSegment StartX=3.03109 StartY=-1.75 StartZ=0 EndX=3.03109 EndY=1.75 EndZ=0
    g5: LineSegment StartX=3.03109 StartY=1.75 StartZ=0 EndX=1e-16 EndY=3.5 EndZ=0
    g6: Circle [constr] CenterX=0 CenterY=0 CenterZ=0 NormalX=0 NormalY=0 NormalZ=1 AngleXU=0 Radius=3.5
    g7: LineSegment StartX=4.96892 StartY=-1.75002 StartZ=0 EndX=8.00002 EndY=-3.5 EndZ=0
    g8: LineSegment StartX=8.00002 StartY=-3.5 StartZ=0 EndX=11.0311 EndY=-1.74998 EndZ=0
    g9: LineSegment StartX=11.0311 StartY=-1.74998 StartZ=0 EndX=11.0311 EndY=1.75002 EndZ=0
    g10: LineSegment StartX=11.0311 StartY=1.75002 StartZ=0 EndX=7.99998 EndY=3.5 EndZ=0
    g11: LineSegment StartX=7.99998 StartY=3.5 StartZ=0 EndX=4.9689 EndY=1.74998 EndZ=0
    g12: LineSegment StartX=4.9689 StartY=1.74998 StartZ=0 EndX=4.96892 EndY=-1.75002 EndZ=0
    g13: Circle [constr] CenterX=8 CenterY=0 CenterZ=0 NormalX=0 NormalY=0 NormalZ=1 AngleXU=0 Radius=3.5
    g14: LineSegment StartX=4.03109 StartY=3.5 StartZ=0 EndX=7.06218 EndY=5.25 EndZ=0
    g15: LineSegment StartX=7.06218 StartY=5.25 StartZ=0 EndX=7.06218 EndY=8.75 EndZ=0
    g16: LineSegment StartX=7.06218 StartY=8.75 StartZ=0 EndX=4.03109 EndY=10.5 EndZ=0
    g17: LineSegment StartX=4.03109 StartY=10.5 StartZ=0 EndX=1 EndY=8.75 EndZ=0
    g18: LineSegment StartX=1 StartY=8.75 StartZ=0 EndX=1 EndY=5.25 EndZ=0
    g19: LineSegment StartX=1 StartY=5.25 StartZ=0 EndX=4.03109 EndY=3.5 EndZ=0
    g20: Circle [constr] CenterX=4.03109 CenterY=7 CenterZ=0 NormalX=0 NormalY=0 NormalZ=1 AngleXU=0 Radius=3.5
    g21: LineSegment StartX=-1 StartY=5.25 StartZ=0 EndX=-1 EndY=8.75 EndZ=0
    g22: LineSegment StartX=-1 StartY=8.75 StartZ=0 EndX=-4.03109 EndY=10.5 EndZ=0
    g23: LineSegment StartX=-4.03109 StartY=10.5 StartZ=0 EndX=-7.06218 EndY=8.75 EndZ=0
    g24: LineSegment StartX=-7.06218 StartY=8.75 StartZ=0 EndX=-7.06218 EndY=5.25 EndZ=0
    g25: LineSegment StartX=-7.06218 StartY=5.25 StartZ=0 EndX=-4.03109 EndY=3.5 EndZ=0
    g26: LineSegment StartX=-4.03109 StartY=3.5 StartZ=0 EndX=-1 EndY=5.25 EndZ=0
    g27: Circle [constr] CenterX=-4.03109 CenterY=7 CenterZ=0 NormalX=0 NormalY=0 NormalZ=1 AngleXU=0 Radius=3.5
    g28: LineSegment StartX=-4.96891 StartY=-1.75 StartZ=0 EndX=-4.96891 EndY=1.75 EndZ=0
    g29: LineSegment StartX=-4.96891 StartY=1.75 StartZ=0 EndX=-8 EndY=3.5 EndZ=0
    g30: LineSegment StartX=-8 StartY=3.5 StartZ=0 EndX=-11.0311 EndY=1.75 EndZ=0
    g31: LineSegment StartX=-11.0311 StartY=1.75 StartZ=0 EndX=-11.0311 EndY=-1.75 EndZ=0
    g32: LineSegment StartX=-11.0311 StartY=-1.75 StartZ=0 EndX=-8 EndY=-3.5 EndZ=0
    g33: LineSegment StartX=-8 StartY=-3.5 StartZ=0 EndX=-4.96891 EndY=-1.75 EndZ=0
    g34: Circle [constr] CenterX=-8 CenterY=0 CenterZ=0 NormalX=0 NormalY=0 NormalZ=1 AngleXU=0 Radius=3.5
    g35: LineSegment StartX=-4.03109 StartY=-3.5 StartZ=0 EndX=-7.06218 EndY=-5.25 EndZ=0
    g36: LineSegment StartX=-7.06218 StartY=-5.25 StartZ=0 EndX=-7.06218 EndY=-8.75 EndZ=0
    g37: LineSegment StartX=-7.06218 StartY=-8.75 StartZ=0 EndX=-4.03109 EndY=-10.5 EndZ=0
    g38: LineSegment StartX=-4.03109 StartY=-10.5 StartZ=0 EndX=-1 EndY=-8.75 EndZ=0
    g39: LineSegment StartX=-1 StartY=-8.75 StartZ=0 EndX=-1 EndY=-5.25 EndZ=0
    g40: LineSegment StartX=-1 StartY=-5.25 StartZ=0 EndX=-4.03109 EndY=-3.5 EndZ=0
    g41: Circle [constr] CenterX=-4.03109 CenterY=-7 CenterZ=0 NormalX=0 NormalY=0 NormalZ=1 AngleXU=0 Radius=3.5
    g42: LineSegment StartX=4.03109 StartY=-3.5 StartZ=0 EndX=1 EndY=-5.25 EndZ=0
    g43: LineSegment StartX=1 StartY=-5.25 StartZ=0 EndX=1 EndY=-8.75 EndZ=0
    g44: LineSegment StartX=1 StartY=-8.75 StartZ=0 EndX=4.03109 EndY=-10.5 EndZ=0
    g45: LineSegment StartX=4.03109 StartY=-10.5 StartZ=0 EndX=7.06218 EndY=-8.75 EndZ=0
    g46: LineSegment StartX=7.06218 StartY=-8.75 StartZ=0 EndX=7.06218 EndY=-5.25 EndZ=0
    g47: LineSegment StartX=7.06218 StartY=-5.25 StartZ=0 EndX=4.03109 EndY=-3.5 EndZ=0
    g48: Circle [constr] CenterX=4.03109 CenterY=-7 CenterZ=0 NormalX=0 NormalY=0 NormalZ=1 AngleXU=0 Radius=3.5
  constraints (117):
    c: Coincident(g0,g1)
    c: Coincident(g1,g2)
    c: Coincident(g2,g3)
    c: Coincident(g3,g4)
    c: Coincident(g4,g5)
    c: Coincident(g5,g0)
    c: Equal(g0, g1-g5) x5
    c: PointOnObject(g0,g6)
    c: PointOnObject(g1,g6)
    c: PointOnObject(g2,g6)
    c: PointOnObject(g3,g6)
    c: PointOnObject(g4,g6)
    c: PointOnObject(g5,g6)
    c: Coincident(g6,g-1)
    c: Diameter(g6) = 7
    c: PointOnObject(g0,g-2)
    c: Coincident(g7,g8)
    c: Coincident(g8,g9)
    c: Coincident(g9,g10)
    c: Coincident(g10,g11)
    c: Coincident(g11,g12)
    c: Coincident(g12,g7)
    c: Equal(g7, g8-g12) x5
    c: PointOnObject(g7,g13)
    c: PointOnObject(g8,g13)
    c: PointOnObject(g9,g13)
    c: PointOnObject(g10,g13)
    c: PointOnObject(g11,g13)
    c: PointOnObject(g12,g13)
    c: PointOnObject(g13,g-1)
    c: Diameter(g13) = 7
    c: Distance(g6,g13) = 8
    c: Horizontal(g0,g10)
    c: Coincident(g14,g15)
    c: Coincident(g15,g16)
    c: Coincident(g16,g17)
    c: Coincident(g17,g18)
    c: Coincident(g18,g19)
    c: Coincident(g19,g14)
    c: Equal(g14, g15-g19) x5
    c: PointOnObject(g14,g20)
    c: PointOnObject(g15,g20)
    c: PointOnObject(g16,g20)
    c: PointOnObject(g17,g20)
    c: PointOnObject(g18,g20)
    c: PointOnObject(g19,g20)
    c: Diameter(g20) = 7
    c: DistanceY(g-1,g20) = 7
    c: Vertical(g18)
    c: Distance(g17,g-2) = 1
    c: Coincident(g21,g22)
    c: Coincident(g22,g23)
    c: Coincident(g23,g24)
    c: Coincident(g24,g25)
    c: Coincident(g25,g26)
    c: Coincident(g26,g21)
    c: Equal(g21, g22-g26) x5
    c: PointOnObject(g21,g27)
    c: PointOnObject(g22,g27)
    c: PointOnObject(g23,g27)
    c: PointOnObject(g24,g27)
    c: PointOnObject(g25,g27)
    c: PointOnObject(g26,g27)
    c: Diameter(g27) = 7
    c: DistanceY(g-1,g27) = 7
    c: DistanceX(g21,g-1) = 1
    c: Vertical(g21)
    c: Coincident(g28,g29)
    c: Coincident(g29,g30)
    c: Coincident(g30,g31)
    c: Coincident(g31,g32)
    c: Coincident(g32,g33)
    c: Coincident(g33,g28)
    c: Equal(g28, g29-g33) x5
    c: PointOnObject(g28,g34)
    c: PointOnObject(g29,g34)
    c: PointOnObject(g30,g34)
    c: PointOnObject(g31,g34)
    c: PointOnObject(g32,g34)
    c: PointOnObject(g33,g34)
    c: PointOnObject(g34,g-1)
    c: Diameter(g34) = 7
    c: Vertical(g31)
    c: DistanceX(g34,g-1) = 8
    c: Coincident(g35,g36)
    c: Coincident(g36,g37)
    c: Coincident(g37,g38)
    c: Coincident(g38,g39)
    c: Coincident(g39,g40)
    c: Coincident(g40,g35)
    c: Equal(g35, g36-g40) x5
    c: PointOnObject(g35,g41)
    c: PointOnObject(g36,g41)
    c: PointOnObject(g37,g41)
    c: PointOnObject(g38,g41)
    c: PointOnObject(g39,g41)
    c: PointOnObject(g40,g41)
    c: Coincident(g42,g43)
    c: Coincident(g43,g44)
    c: Coincident(g44,g45)
    c: Coincident(g45,g46)
    c: Coincident(g46,g47)
    c: Coincident(g47,g42)
    c: Equal(g42, g43-g47) x5
    c: PointOnObject(g42,g48)
    c: PointOnObject(g43,g48)
    c: PointOnObject(g44,g48)
    c: PointOnObject(g45,g48)
    c: PointOnObject(g46,g48)
    c: PointOnObject(g47,g48)
    c: Equal(g41,g48)
    c: Diameter(g41) = 7
    c: Vertical(g39)
    c: Vertical(g43)
    c: Distance(g-2,g39) = 1
    c: Symmetric(g38,g43,g-2)
    c: Distance(g41,g-1) = 7
FEATURE [Part::Extrusion] Extrude430  label="hex045"
  Base = -> Sketch438
  Dir = (0,-1,2e-16)
  DirMode = 2
  FaceMakerClass = Part::FaceMakerBullseye
  FaceMakerMode = 3
  LengthFwd = 10
  LengthRev = 0
  Placement = pos=(104,0,-28) rot=(0,0,1;0rad)
  Solid = true
  Symmetric = false
FEATURE [Sketcher::SketchObject] Sketch439
  ArcFitTolerance = 1e-06
  FullyConstrained = true
  MakeInternals = false
  Placement = pos=(0,0,0) rot=(1,0,0;1.5708rad)
  sketch-geometry (49):
    g0: LineSegment StartX=1e-16 StartY=3.5 StartZ=0 EndX=-3.03109 EndY=1.75 EndZ=0
    g1: LineSegment StartX=-3.03109 StartY=1.75 StartZ=0 EndX=-3.03109 EndY=-1.75 EndZ=0
    g2: LineSegment StartX=-3.03109 StartY=-1.75 StartZ=0 EndX=-1e-16 EndY=-3.5 EndZ=0
    g3: LineSegment StartX=-1e-16 StartY=-3.5 StartZ=0 EndX=3.03109 EndY=-1.75 EndZ=0
    g4: LineSegment StartX=3.03109 StartY=-1.75 StartZ=0 EndX=3.03109 EndY=1.75 EndZ=0
    g5: LineSegment StartX=3.03109 StartY=1.75 StartZ=0 EndX=1e-16 EndY=3.5 EndZ=0
    g6: Circle [constr] CenterX=0 CenterY=0 CenterZ=0 NormalX=0 NormalY=0 NormalZ=1 AngleXU=0 Radius=3.5
    g7: LineSegment StartX=4.96892 StartY=-1.75002 StartZ=0 EndX=8.00002 EndY=-3.5 EndZ=0
    g8: LineSegment StartX=8.00002 StartY=-3.5 StartZ=0 EndX=11.0311 EndY=-1.74998 EndZ=0
    g9: LineSegment StartX=11.0311 StartY=-1.74998 StartZ=0 EndX=11.0311 EndY=1.75002 EndZ=0
    g10: LineSegment StartX=11.0311 StartY=1.75002 StartZ=0 EndX=7.99998 EndY=3.5 EndZ=0
    g11: LineSegment StartX=7.99998 StartY=3.5 StartZ=0 EndX=4.9689 EndY=1.74998 EndZ=0
    g12: LineSegment StartX=4.9689 StartY=1.74998 StartZ=0 EndX=4.96892 EndY=-1.75002 EndZ=0
    g13: Circle [constr] CenterX=8 CenterY=0 CenterZ=0 NormalX=0 NormalY=0 NormalZ=1 AngleXU=0 Radius=3.5
    g14: LineSegment StartX=4.03109 StartY=3.5 StartZ=0 EndX=7.06218 EndY=5.25 EndZ=0
    g15: LineSegment StartX=7.06218 StartY=5.25 StartZ=0 EndX=7.06218 EndY=8.75 EndZ=0
    g16: LineSegment StartX=7.06218 StartY=8.75 StartZ=0 EndX=4.03109 EndY=10.5 EndZ=0
    g17: LineSegment StartX=4.03109 StartY=10.5 StartZ=0 EndX=1 EndY=8.75 EndZ=0
    g18: LineSegment StartX=1 StartY=8.75 StartZ=0 EndX=1 EndY=5.25 EndZ=0
    g19: LineSegment StartX=1 StartY=5.25 StartZ=0 EndX=4.03109 EndY=3.5 EndZ=0
    g20: Circle [constr] CenterX=4.03109 CenterY=7 CenterZ=0 NormalX=0 NormalY=0 NormalZ=1 AngleXU=0 Radius=3.5
    g21: LineSegment StartX=-1 StartY=5.25 StartZ=0 EndX=-1 EndY=8.75 EndZ=0
    g22: LineSegment StartX=-1 StartY=8.75 StartZ=0 EndX=-4.03109 EndY=10.5 EndZ=0
    g23: LineSegment StartX=-4.03109 StartY=10.5 StartZ=0 EndX=-7.06218 EndY=8.75 EndZ=0
    g24: LineSegment StartX=-7.06218 StartY=8.75 StartZ=0 EndX=-7.06218 EndY=5.25 EndZ=0
    g25: LineSegment StartX=-7.06218 StartY=5.25 StartZ=0 EndX=-4.03109 EndY=3.5 EndZ=0
    g26: LineSegment StartX=-4.03109 StartY=3.5 StartZ=0 EndX=-1 EndY=5.25 EndZ=0
    g27: Circle [constr] CenterX=-4.03109 CenterY=7 CenterZ=0 NormalX=0 NormalY=0 NormalZ=1 AngleXU=0 Radius=3.5
    g28: LineSegment StartX=-4.96891 StartY=-1.75 StartZ=0 EndX=-4.96891 EndY=1.75 EndZ=0
    g29: LineSegment StartX=-4.96891 StartY=1.75 StartZ=0 EndX=-8 EndY=3.5 EndZ=0
    g30: LineSegment StartX=-8 StartY=3.5 StartZ=0 EndX=-11.0311 EndY=1.75 EndZ=0
    g31: LineSegment StartX=-11.0311 StartY=1.75 StartZ=0 EndX=-11.0311 EndY=-1.75 EndZ=0
    g32: LineSegment StartX=-11.0311 StartY=-1.75 StartZ=0 EndX=-8 EndY=-3.5 EndZ=0
    g33: LineSegment StartX=-8 StartY=-3.5 StartZ=0 EndX=-4.96891 EndY=-1.75 EndZ=0
    g34: Circle [constr] CenterX=-8 CenterY=0 CenterZ=0 NormalX=0 NormalY=0 NormalZ=1 AngleXU=0 Radius=3.5
    g35: LineSegment StartX=-4.03109 StartY=-3.5 StartZ=0 EndX=-7.06218 EndY=-5.25 EndZ=0
    g36: LineSegment StartX=-7.06218 StartY=-5.25 StartZ=0 EndX=-7.06218 EndY=-8.75 EndZ=0
    g37: LineSegment StartX=-7.06218 StartY=-8.75 StartZ=0 EndX=-4.03109 EndY=-10.5 EndZ=0
    g38: LineSegment StartX=-4.03109 StartY=-10.5 StartZ=0 EndX=-1 EndY=-8.75 EndZ=0
    g39: LineSegment StartX=-1 StartY=-8.75 StartZ=0 EndX=-1 EndY=-5.25 EndZ=0
    g40: LineSegment StartX=-1 StartY=-5.25 StartZ=0 EndX=-4.03109 EndY=-3.5 EndZ=0
    g41: Circle [constr] CenterX=-4.03109 CenterY=-7 CenterZ=0 NormalX=0 NormalY=0 NormalZ=1 AngleXU=0 Radius=3.5
    g42: LineSegment StartX=4.03109 StartY=-3.5 StartZ=0 EndX=1 EndY=-5.25 EndZ=0
    g43: LineSegment StartX=1 StartY=-5.25 StartZ=0 EndX=1 EndY=-8.75 EndZ=0
    g44: LineSegment StartX=1 StartY=-8.75 StartZ=0 EndX=4.03109 EndY=-10.5 EndZ=0
    g45: LineSegment StartX=4.03109 StartY=-10.5 StartZ=0 EndX=7.06218 EndY=-8.75 EndZ=0
    g46: LineSegment StartX=7.06218 StartY=-8.75 StartZ=0 EndX=7.06218 EndY=-5.25 EndZ=0
    g47: LineSegment StartX=7.06218 StartY=-5.25 StartZ=0 EndX=4.03109 EndY=-3.5 EndZ=0
    g48: Circle [constr] CenterX=4.03109 CenterY=-7 CenterZ=0 NormalX=0 NormalY=0 NormalZ=1 AngleXU=0 Radius=3.5
  constraints (117):
    c: Coincident(g0,g1)
    c: Coincident(g1,g2)
    c: Coincident(g2,g3)
    c: Coincident(g3,g4)
    c: Coincident(g4,g5)
    c: Coincident(g5,g0)
    c: Equal(g0, g1-g5) x5
    c: PointOnObject(g0,g6)
    c: PointOnObject(g1,g6)
    c: PointOnObject(g2,g6)
    c: PointOnObject(g3,g6)
    c: PointOnObject(g4,g6)
    c: PointOnObject(g5,g6)
    c: Coincident(g6,g-1)
    c: Diameter(g6) = 7
    c: PointOnObject(g0,g-2)
    c: Coincident(g7,g8)
    c: Coincident(g8,g9)
    c: Coincident(g9,g10)
    c: Coincident(g10,g11)
    c: Coincident(g11,g12)
    c: Coincident(g12,g7)
    c: Equal(g7, g8-g12) x5
    c: PointOnObject(g7,g13)
    c: PointOnObject(g8,g13)
    c: PointOnObject(g9,g13)
    c: PointOnObject(g10,g13)
    c: PointOnObject(g11,g13)
    c: PointOnObject(g12,g13)
    c: PointOnObject(g13,g-1)
    c: Diameter(g13) = 7
    c: Distance(g6,g13) = 8
    c: Horizontal(g0,g10)
    c: Coincident(g14,g15)
    c: Coincident(g15,g16)
    c: Coincident(g16,g17)
    c: Coincident(g17,g18)
    c: Coincident(g18,g19)
    c: Coincident(g19,g14)
    c: Equal(g14, g15-g19) x5
    c: PointOnObject(g14,g20)
    c: PointOnObject(g15,g20)
    c: PointOnObject(g16,g20)
    c: PointOnObject(g17,g20)
    c: PointOnObject(g18,g20)
    c: PointOnObject(g19,g20)
    c: Diameter(g20) = 7
    c: DistanceY(g-1,g20) = 7
    c: Vertical(g18)
    c: Distance(g17,g-2) = 1
    c: Coincident(g21,g22)
    c: Coincident(g22,g23)
    c: Coincident(g23,g24)
    c: Coincident(g24,g25)
    c: Coincident(g25,g26)
    c: Coincident(g26,g21)
    c: Equal(g21, g22-g26) x5
    c: PointOnObject(g21,g27)
    c: PointOnObject(g22,g27)
    c: PointOnObject(g23,g27)
    c: PointOnObject(g24,g27)
    c: PointOnObject(g25,g27)
    c: PointOnObject(g26,g27)
    c: Diameter(g27) = 7
    c: DistanceY(g-1,g27) = 7
    c: DistanceX(g21,g-1) = 1
    c: Vertical(g21)
    c: Coincident(g28,g29)
    c: Coincident(g29,g30)
    c: Coincident(g30,g31)
    c: Coincident(g31,g32)
    c: Coincident(g32,g33)
    c: Coincident(g33,g28)
    c: Equal(g28, g29-g33) x5
    c: PointOnObject(g28,g34)
    c: PointOnObject(g29,g34)
    c: PointOnObject(g30,g34)
    c: PointOnObject(g31,g34)
    c: PointOnObject(g32,g34)
    c: PointOnObject(g33,g34)
    c: PointOnObject(g34,g-1)
    c: Diameter(g34) = 7
    c: Vertical(g31)
    c: DistanceX(g34,g-1) = 8
    c: Coincident(g35,g36)
    c: Coincident(g36,g37)
    c: Coincident(g37,g38)
    c: Coincident(g38,g39)
    c: Coincident(g39,g40)
    c: Coincident(g40,g35)
    c: Equal(g35, g36-g40) x5
    c: PointOnObject(g35,g41)
    c: PointOnObject(g36,g41)
    c: PointOnObject(g37,g41)
    c: PointOnObject(g38,g41)
    c: PointOnObject(g39,g41)
    c: PointOnObject(g40,g41)
    c: Coincident(g42,g43)
    c: Coincident(g43,g44)
    c: Coincident(g44,g45)
    c: Coincident(g45,g46)
    c: Coincident(g46,g47)
    c: Coincident(g47,g42)
    c: Equal(g42, g43-g47) x5
    c: PointOnObject(g42,g48)
    c: PointOnObject(g43,g48)
    c: PointOnObject(g44,g48)
    c: PointOnObject(g45,g48)
    c: PointOnObject(g46,g48)
    c: PointOnObject(g47,g48)
    c: Equal(g41,g48)
    c: Diameter(g41) = 7
    c: Vertical(g39)
    c: Vertical(g43)
    c: Distance(g-2,g39) = 1
    c: Symmetric(g38,g43,g-2)
    c: Distance(g41,g-1) = 7
FEATURE [Part::Extrusion] Extrude431  label="hex046"
  Base = -> Sketch439
  Dir = (0,-1,2e-16)
  DirMode = 2
  FaceMakerClass = Part::FaceMakerBullseye
  FaceMakerMode = 3
  LengthFwd = 10
  LengthRev = 0
  Placement = pos=(-96,0,-14) rot=(0,0,1;0rad)
  Solid = true
  Symmetric = false
FEATURE [Sketcher::SketchObject] Sketch440
  ArcFitTolerance = 1e-06
  FullyConstrained = true
  MakeInternals = false
  Placement = pos=(0,0,0) rot=(1,0,0;1.5708rad)
  sketch-geometry (49):
    g0: LineSegment StartX=1e-16 StartY=3.5 StartZ=0 EndX=-3.03109 EndY=1.75 EndZ=0
    g1: LineSegment StartX=-3.03109 StartY=1.75 StartZ=0 EndX=-3.03109 EndY=-1.75 EndZ=0
    g2: LineSegment StartX=-3.03109 StartY=-1.75 StartZ=0 EndX=-1e-16 EndY=-3.5 EndZ=0
    g3: LineSegment StartX=-1e-16 StartY=-3.5 StartZ=0 EndX=3.03109 EndY=-1.75 EndZ=0
    g4: LineSegment StartX=3.03109 StartY=-1.75 StartZ=0 EndX=3.03109 EndY=1.75 EndZ=0
    g5: LineSegment StartX=3.03109 StartY=1.75 StartZ=0 EndX=1e-16 EndY=3.5 EndZ=0
    g6: Circle [constr] CenterX=0 CenterY=0 CenterZ=0 NormalX=0 NormalY=0 NormalZ=1 AngleXU=0 Radius=3.5
    g7: LineSegment StartX=4.96892 StartY=-1.75002 StartZ=0 EndX=8.00002 EndY=-3.5 EndZ=0
    g8: LineSegment StartX=8.00002 StartY=-3.5 StartZ=0 EndX=11.0311 EndY=-1.74998 EndZ=0
    g9: LineSegment StartX=11.0311 StartY=-1.74998 StartZ=0 EndX=11.0311 EndY=1.75002 EndZ=0
    g10: LineSegment StartX=11.0311 StartY=1.75002 StartZ=0 EndX=7.99998 EndY=3.5 EndZ=0
    g11: LineSegment StartX=7.99998 StartY=3.5 StartZ=0 EndX=4.9689 EndY=1.74998 EndZ=0
    g12: LineSegment StartX=4.9689 StartY=1.74998 StartZ=0 EndX=4.96892 EndY=-1.75002 EndZ=0
    g13: Circle [constr] CenterX=8 CenterY=0 CenterZ=0 NormalX=0 NormalY=0 NormalZ=1 AngleXU=0 Radius=3.5
    g14: LineSegment StartX=4.03109 StartY=3.5 StartZ=0 EndX=7.06218 EndY=5.25 EndZ=0
    g15: LineSegment StartX=7.06218 StartY=5.25 StartZ=0 EndX=7.06218 EndY=8.75 EndZ=0
    g16: LineSegment StartX=7.06218 StartY=8.75 StartZ=0 EndX=4.03109 EndY=10.5 EndZ=0
    g17: LineSegment StartX=4.03109 StartY=10.5 StartZ=0 EndX=1 EndY=8.75 EndZ=0
    g18: LineSegment StartX=1 StartY=8.75 StartZ=0 EndX=1 EndY=5.25 EndZ=0
    g19: LineSegment StartX=1 StartY=5.25 StartZ=0 EndX=4.03109 EndY=3.5 EndZ=0
    g20: Circle [constr] CenterX=4.03109 CenterY=7 CenterZ=0 NormalX=0 NormalY=0 NormalZ=1 AngleXU=0 Radius=3.5
    g21: LineSegment StartX=-1 StartY=5.25 StartZ=0 EndX=-1 EndY=8.75 EndZ=0
    g22: LineSegment StartX=-1 StartY=8.75 StartZ=0 EndX=-4.03109 EndY=10.5 EndZ=0
    g23: LineSegment StartX=-4.03109 StartY=10.5 StartZ=0 EndX=-7.06218 EndY=8.75 EndZ=0
    g24: LineSegment StartX=-7.06218 StartY=8.75 StartZ=0 EndX=-7.06218 EndY=5.25 EndZ=0
    g25: LineSegment StartX=-7.06218 StartY=5.25 StartZ=0 EndX=-4.03109 EndY=3.5 EndZ=0
    g26: LineSegment StartX=-4.03109 StartY=3.5 StartZ=0 EndX=-1 EndY=5.25 EndZ=0
    g27: Circle [constr] CenterX=-4.03109 CenterY=7 CenterZ=0 NormalX=0 NormalY=0 NormalZ=1 AngleXU=0 Radius=3.5
    g28: LineSegment StartX=-4.96891 StartY=-1.75 StartZ=0 EndX=-4.96891 EndY=1.75 EndZ=0
    g29: LineSegment StartX=-4.96891 StartY=1.75 StartZ=0 EndX=-8 EndY=3.5 EndZ=0
    g30: LineSegment StartX=-8 StartY=3.5 StartZ=0 EndX=-11.0311 EndY=1.75 EndZ=0
    g31: LineSegment StartX=-11.0311 StartY=1.75 StartZ=0 EndX=-11.0311 EndY=-1.75 EndZ=0
    g32: LineSegment StartX=-11.0311 StartY=-1.75 StartZ=0 EndX=-8 EndY=-3.5 EndZ=0
    g33: LineSegment StartX=-8 StartY=-3.5 StartZ=0 EndX=-4.96891 EndY=-1.75 EndZ=0
    g34: Circle [constr] CenterX=-8 CenterY=0 CenterZ=0 NormalX=0 NormalY=0 NormalZ=1 AngleXU=0 Radius=3.5
    g35: LineSegment StartX=-4.03109 StartY=-3.5 StartZ=0 EndX=-7.06218 EndY=-5.25 EndZ=0
    g36: LineSegment StartX=-7.06218 StartY=-5.25 StartZ=0 EndX=-7.06218 EndY=-8.75 EndZ=0
    g37: LineSegment StartX=-7.06218 StartY=-8.75 StartZ=0 EndX=-4.03109 EndY=-10.5 EndZ=0
    g38: LineSegment StartX=-4.03109 StartY=-10.5 StartZ=0 EndX=-1 EndY=-8.75 EndZ=0
    g39: LineSegment StartX=-1 StartY=-8.75 StartZ=0 EndX=-1 EndY=-5.25 EndZ=0
    g40: LineSegment StartX=-1 StartY=-5.25 StartZ=0 EndX=-4.03109 EndY=-3.5 EndZ=0
    g41: Circle [constr] CenterX=-4.03109 CenterY=-7 CenterZ=0 NormalX=0 NormalY=0 NormalZ=1 AngleXU=0 Radius=3.5
    g42: LineSegment StartX=4.03109 StartY=-3.5 StartZ=0 EndX=1 EndY=-5.25 EndZ=0
    g43: LineSegment StartX=1 StartY=-5.25 StartZ=0 EndX=1 EndY=-8.75 EndZ=0
    g44: LineSegment StartX=1 StartY=-8.75 StartZ=0 EndX=4.03109 EndY=-10.5 EndZ=0
    g45: LineSegment StartX=4.03109 StartY=-10.5 StartZ=0 EndX=7.06218 EndY=-8.75 EndZ=0
    g46: LineSegment StartX=7.06218 StartY=-8.75 StartZ=0 EndX=7.06218 EndY=-5.25 EndZ=0
    g47: LineSegment StartX=7.06218 StartY=-5.25 StartZ=0 EndX=4.03109 EndY=-3.5 EndZ=0
    g48: Circle [constr] CenterX=4.03109 CenterY=-7 CenterZ=0 NormalX=0 NormalY=0 NormalZ=1 AngleXU=0 Radius=3.5
  constraints (117):
    c: Coincident(g0,g1)
    c: Coincident(g1,g2)
    c: Coincident(g2,g3)
    c: Coincident(g3,g4)
    c: Coincident(g4,g5)
    c: Coincident(g5,g0)
    c: Equal(g0, g1-g5) x5
    c: PointOnObject(g0,g6)
    c: PointOnObject(g1,g6)
    c: PointOnObject(g2,g6)
    c: PointOnObject(g3,g6)
    c: PointOnObject(g4,g6)
    c: PointOnObject(g5,g6)
    c: Coincident(g6,g-1)
    c: Diameter(g6) = 7
    c: PointOnObject(g0,g-2)
    c: Coincident(g7,g8)
    c: Coincident(g8,g9)
    c: Coincident(g9,g10)
    c: Coincident(g10,g11)
    c: Coincident(g11,g12)
    c: Coincident(g12,g7)
    c: Equal(g7, g8-g12) x5
    c: PointOnObject(g7,g13)
    c: PointOnObject(g8,g13)
    c: PointOnObject(g9,g13)
    c: PointOnObject(g10,g13)
    c: PointOnObject(g11,g13)
    c: PointOnObject(g12,g13)
    c: PointOnObject(g13,g-1)
    c: Diameter(g13) = 7
    c: Distance(g6,g13) = 8
    c: Horizontal(g0,g10)
    c: Coincident(g14,g15)
    c: Coincident(g15,g16)
    c: Coincident(g16,g17)
    c: Coincident(g17,g18)
    c: Coincident(g18,g19)
    c: Coincident(g19,g14)
    c: Equal(g14, g15-g19) x5
    c: PointOnObject(g14,g20)
    c: PointOnObject(g15,g20)
    c: PointOnObject(g16,g20)
    c: PointOnObject(g17,g20)
    c: PointOnObject(g18,g20)
    c: PointOnObject(g19,g20)
    c: Diameter(g20) = 7
    c: DistanceY(g-1,g20) = 7
    c: Vertical(g18)
    c: Distance(g17,g-2) = 1
    c: Coincident(g21,g22)
    c: Coincident(g22,g23)
    c: Coincident(g23,g24)
    c: Coincident(g24,g25)
    c: Coincident(g25,g26)
    c: Coincident(g26,g21)
    c: Equal(g21, g22-g26) x5
    c: PointOnObject(g21,g27)
    c: PointOnObject(g22,g27)
    c: PointOnObject(g23,g27)
    c: PointOnObject(g24,g27)
    c: PointOnObject(g25,g27)
    c: PointOnObject(g26,g27)
    c: Diameter(g27) = 7
    c: DistanceY(g-1,g27) = 7
    c: DistanceX(g21,g-1) = 1
    c: Vertical(g21)
    c: Coincident(g28,g29)
    c: Coincident(g29,g30)
    c: Coincident(g30,g31)
    c: Coincident(g31,g32)
    c: Coincident(g32,g33)
    c: Coincident(g33,g28)
    c: Equal(g28, g29-g33) x5
    c: PointOnObject(g28,g34)
    c: PointOnObject(g29,g34)
    c: PointOnObject(g30,g34)
    c: PointOnObject(g31,g34)
    c: PointOnObject(g32,g34)
    c: PointOnObject(g33,g34)
    c: PointOnObject(g34,g-1)
    c: Diameter(g34) = 7
    c: Vertical(g31)
    c: DistanceX(g34,g-1) = 8
    c: Coincident(g35,g36)
    c: Coincident(g36,g37)
    c: Coincident(g37,g38)
    c: Coincident(g38,g39)
    c: Coincident(g39,g40)
    c: Coincident(g40,g35)
    c: Equal(g35, g36-g40) x5
    c: PointOnObject(g35,g41)
    c: PointOnObject(g36,g41)
    c: PointOnObject(g37,g41)
    c: PointOnObject(g38,g41)
    c: PointOnObject(g39,g41)
    c: PointOnObject(g40,g41)
    c: Coincident(g42,g43)
    c: Coincident(g43,g44)
    c: Coincident(g44,g45)
    c: Coincident(g45,g46)
    c: Coincident(g46,g47)
    c: Coincident(g47,g42)
    c: Equal(g42, g43-g47) x5
    c: PointOnObject(g42,g48)
    c: PointOnObject(g43,g48)
    c: PointOnObject(g44,g48)
    c: PointOnObject(g45,g48)
    c: PointOnObject(g46,g48)
    c: PointOnObject(g47,g48)
    c: Equal(g41,g48)
    c: Diameter(g41) = 7
    c: Vertical(g39)
    c: Vertical(g43)
    c: Distance(g-2,g39) = 1
    c: Symmetric(g38,g43,g-2)
    c: Distance(g41,g-1) = 7
FEATURE [Part::Extrusion] Extrude432  label="hex047"
  Base = -> Sketch440
  Dir = (0,-1,2e-16)
  DirMode = 2
  FaceMakerClass = Part::FaceMakerBullseye
  FaceMakerMode = 3
  LengthFwd = 10
  LengthRev = 0
  Placement = pos=(-68,0,-35) rot=(0,0,1;0rad)
  Solid = true
  Symmetric = false
FEATURE [Sketcher::SketchObject] Sketch441
  ArcFitTolerance = 1e-06
  FullyConstrained = true
  MakeInternals = false
  Placement = pos=(0,0,0) rot=(1,0,0;1.5708rad)
  sketch-geometry (49):
    g0: LineSegment StartX=1e-16 StartY=3.5 StartZ=0 EndX=-3.03109 EndY=1.75 EndZ=0
    g1: LineSegment StartX=-3.03109 StartY=1.75 StartZ=0 EndX=-3.03109 EndY=-1.75 EndZ=0
    g2: LineSegment StartX=-3.03109 StartY=-1.75 StartZ=0 EndX=-1e-16 EndY=-3.5 EndZ=0
    g3: LineSegment StartX=-1e-16 StartY=-3.5 StartZ=0 EndX=3.03109 EndY=-1.75 EndZ=0
    g4: LineSegment StartX=3.03109 StartY=-1.75 StartZ=0 EndX=3.03109 EndY=1.75 EndZ=0
    g5: LineSegment StartX=3.03109 StartY=1.75 StartZ=0 EndX=1e-16 EndY=3.5 EndZ=0
    g6: Circle [constr] CenterX=0 CenterY=0 CenterZ=0 NormalX=0 NormalY=0 NormalZ=1 AngleXU=0 Radius=3.5
    g7: LineSegment StartX=4.96892 StartY=-1.75002 StartZ=0 EndX=8.00002 EndY=-3.5 EndZ=0
    g8: LineSegment StartX=8.00002 StartY=-3.5 StartZ=0 EndX=11.0311 EndY=-1.74998 EndZ=0
    g9: LineSegment StartX=11.0311 StartY=-1.74998 StartZ=0 EndX=11.0311 EndY=1.75002 EndZ=0
    g10: LineSegment StartX=11.0311 StartY=1.75002 StartZ=0 EndX=7.99998 EndY=3.5 EndZ=0
    g11: LineSegment StartX=7.99998 StartY=3.5 StartZ=0 EndX=4.9689 EndY=1.74998 EndZ=0
    g12: LineSegment StartX=4.9689 StartY=1.74998 StartZ=0 EndX=4.96892 EndY=-1.75002 EndZ=0
    g13: Circle [constr] CenterX=8 CenterY=0 CenterZ=0 NormalX=0 NormalY=0 NormalZ=1 AngleXU=0 Radius=3.5
    g14: LineSegment StartX=4.03109 StartY=3.5 StartZ=0 EndX=7.06218 EndY=5.25 EndZ=0
    g15: LineSegment StartX=7.06218 StartY=5.25 StartZ=0 EndX=7.06218 EndY=8.75 EndZ=0
    g16: LineSegment StartX=7.06218 StartY=8.75 StartZ=0 EndX=4.03109 EndY=10.5 EndZ=0
    g17: LineSegment StartX=4.03109 StartY=10.5 StartZ=0 EndX=1 EndY=8.75 EndZ=0
    g18: LineSegment StartX=1 StartY=8.75 StartZ=0 EndX=1 EndY=5.25 EndZ=0
    g19: LineSegment StartX=1 StartY=5.25 StartZ=0 EndX=4.03109 EndY=3.5 EndZ=0
    g20: Circle [constr] CenterX=4.03109 CenterY=7 CenterZ=0 NormalX=0 NormalY=0 NormalZ=1 AngleXU=0 Radius=3.5
    g21: LineSegment StartX=-1 StartY=5.25 StartZ=0 EndX=-1 EndY=8.75 EndZ=0
    g22: LineSegment StartX=-1 StartY=8.75 StartZ=0 EndX=-4.03109 EndY=10.5 EndZ=0
    g23: LineSegment StartX=-4.03109 StartY=10.5 StartZ=0 EndX=-7.06218 EndY=8.75 EndZ=0
    g24: LineSegment StartX=-7.06218 StartY=8.75 StartZ=0 EndX=-7.06218 EndY=5.25 EndZ=0
    g25: LineSegment StartX=-7.06218 StartY=5.25 StartZ=0 EndX=-4.03109 EndY=3.5 EndZ=0
    g26: LineSegment StartX=-4.03109 StartY=3.5 StartZ=0 EndX=-1 EndY=5.25 EndZ=0
    g27: Circle [constr] CenterX=-4.03109 CenterY=7 CenterZ=0 NormalX=0 NormalY=0 NormalZ=1 AngleXU=0 Radius=3.5
    g28: LineSegment StartX=-4.96891 StartY=-1.75 StartZ=0 EndX=-4.96891 EndY=1.75 EndZ=0
    g29: LineSegment StartX=-4.96891 StartY=1.75 StartZ=0 EndX=-8 EndY=3.5 EndZ=0
    g30: LineSegment StartX=-8 StartY=3.5 StartZ=0 EndX=-11.0311 EndY=1.75 EndZ=0
    g31: LineSegment StartX=-11.0311 StartY=1.75 StartZ=0 EndX=-11.0311 EndY=-1.75 EndZ=0
    g32: LineSegment StartX=-11.0311 StartY=-1.75 StartZ=0 EndX=-8 EndY=-3.5 EndZ=0
    g33: LineSegment StartX=-8 StartY=-3.5 StartZ=0 EndX=-4.96891 EndY=-1.75 EndZ=0
    g34: Circle [constr] CenterX=-8 CenterY=0 CenterZ=0 NormalX=0 NormalY=0 NormalZ=1 AngleXU=0 Radius=3.5
    g35: LineSegment StartX=-4.03109 StartY=-3.5 StartZ=0 EndX=-7.06218 EndY=-5.25 EndZ=0
    g36: LineSegment StartX=-7.06218 StartY=-5.25 StartZ=0 EndX=-7.06218 EndY=-8.75 EndZ=0
    g37: LineSegment StartX=-7.06218 StartY=-8.75 StartZ=0 EndX=-4.03109 EndY=-10.5 EndZ=0
    g38: LineSegment StartX=-4.03109 StartY=-10.5 StartZ=0 EndX=-1 EndY=-8.75 EndZ=0
    g39: LineSegment StartX=-1 StartY=-8.75 StartZ=0 EndX=-1 EndY=-5.25 EndZ=0
    g40: LineSegment StartX=-1 StartY=-5.25 StartZ=0 EndX=-4.03109 EndY=-3.5 EndZ=0
    g41: Circle [constr] CenterX=-4.03109 CenterY=-7 CenterZ=0 NormalX=0 NormalY=0 NormalZ=1 AngleXU=0 Radius=3.5
    g42: LineSegment StartX=4.03109 StartY=-3.5 StartZ=0 EndX=1 EndY=-5.25 EndZ=0
    g43: LineSegment StartX=1 StartY=-5.25 StartZ=0 EndX=1 EndY=-8.75 EndZ=0
    g44: LineSegment StartX=1 StartY=-8.75 StartZ=0 EndX=4.03109 EndY=-10.5 EndZ=0
    g45: LineSegment StartX=4.03109 StartY=-10.5 StartZ=0 EndX=7.06218 EndY=-8.75 EndZ=0
    g46: LineSegment StartX=7.06218 StartY=-8.75 StartZ=0 EndX=7.06218 EndY=-5.25 EndZ=0
    g47: LineSegment StartX=7.06218 StartY=-5.25 StartZ=0 EndX=4.03109 EndY=-3.5 EndZ=0
    g48: Circle [constr] CenterX=4.03109 CenterY=-7 CenterZ=0 NormalX=0 NormalY=0 NormalZ=1 AngleXU=0 Radius=3.5
  constraints (117):
    c: Coincident(g0,g1)
    c: Coincident(g1,g2)
    c: Coincident(g2,g3)
    c: Coincident(g3,g4)
    c: Coincident(g4,g5)
    c: Coincident(g5,g0)
    c: Equal(g0, g1-g5) x5
    c: PointOnObject(g0,g6)
    c: PointOnObject(g1,g6)
    c: PointOnObject(g2,g6)
    c: PointOnObject(g3,g6)
    c: PointOnObject(g4,g6)
    c: PointOnObject(g5,g6)
    c: Coincident(g6,g-1)
    c: Diameter(g6) = 7
    c: PointOnObject(g0,g-2)
    c: Coincident(g7,g8)
    c: Coincident(g8,g9)
    c: Coincident(g9,g10)
    c: Coincident(g10,g11)
    c: Coincident(g11,g12)
    c: Coincident(g12,g7)
    c: Equal(g7, g8-g12) x5
    c: PointOnObject(g7,g13)
    c: PointOnObject(g8,g13)
    c: PointOnObject(g9,g13)
    c: PointOnObject(g10,g13)
    c: PointOnObject(g11,g13)
    c: PointOnObject(g12,g13)
    c: PointOnObject(g13,g-1)
    c: Diameter(g13) = 7
    c: Distance(g6,g13) = 8
    c: Horizontal(g0,g10)
    c: Coincident(g14,g15)
    c: Coincident(g15,g16)
    c: Coincident(g16,g17)
    c: Coincident(g17,g18)
    c: Coincident(g18,g19)
    c: Coincident(g19,g14)
    c: Equal(g14, g15-g19) x5
    c: PointOnObject(g14,g20)
    c: PointOnObject(g15,g20)
    c: PointOnObject(g16,g20)
    c: PointOnObject(g17,g20)
    c: PointOnObject(g18,g20)
    c: PointOnObject(g19,g20)
    c: Diameter(g20) = 7
    c: DistanceY(g-1,g20) = 7
    c: Vertical(g18)
    c: Distance(g17,g-2) = 1
    c: Coincident(g21,g22)
    c: Coincident(g22,g23)
    c: Coincident(g23,g24)
    c: Coincident(g24,g25)
    c: Coincident(g25,g26)
    c: Coincident(g26,g21)
    c: Equal(g21, g22-g26) x5
    c: PointOnObject(g21,g27)
    c: PointOnObject(g22,g27)
    c: PointOnObject(g23,g27)
    c: PointOnObject(g24,g27)
    c: PointOnObject(g25,g27)
    c: PointOnObject(g26,g27)
    c: Diameter(g27) = 7
    c: DistanceY(g-1,g27) = 7
    c: DistanceX(g21,g-1) = 1
    c: Vertical(g21)
    c: Coincident(g28,g29)
    c: Coincident(g29,g30)
    c: Coincident(g30,g31)
    c: Coincident(g31,g32)
    c: Coincident(g32,g33)
    c: Coincident(g33,g28)
    c: Equal(g28, g29-g33) x5
    c: PointOnObject(g28,g34)
    c: PointOnObject(g29,g34)
    c: PointOnObject(g30,g34)
    c: PointOnObject(g31,g34)
    c: PointOnObject(g32,g34)
    c: PointOnObject(g33,g34)
    c: PointOnObject(g34,g-1)
    c: Diameter(g34) = 7
    c: Vertical(g31)
    c: DistanceX(g34,g-1) = 8
    c: Coincident(g35,g36)
    c: Coincident(g36,g37)
    c: Coincident(g37,g38)
    c: Coincident(g38,g39)
    c: Coincident(g39,g40)
    c: Coincident(g40,g35)
    c: Equal(g35, g36-g40) x5
    c: PointOnObject(g35,g41)
    c: PointOnObject(g36,g41)
    c: PointOnObject(g37,g41)
    c: PointOnObject(g38,g41)
    c: PointOnObject(g39,g41)
    c: PointOnObject(g40,g41)
    c: Coincident(g42,g43)
    c: Coincident(g43,g44)
    c: Coincident(g44,g45)
    c: Coincident(g45,g46)
    c: Coincident(g46,g47)
    c: Coincident(g47,g42)
    c: Equal(g42, g43-g47) x5
    c: PointOnObject(g42,g48)
    c: PointOnObject(g43,g48)
    c: PointOnObject(g44,g48)
    c: PointOnObject(g45,g48)
    c: PointOnObject(g46,g48)
    c: PointOnObject(g47,g48)
    c: Equal(g41,g48)
    c: Diameter(g41) = 7
    c: Vertical(g39)
    c: Vertical(g43)
    c: Distance(g-2,g39) = 1
    c: Symmetric(g38,g43,g-2)
    c: Distance(g41,g-1) = 7
FEATURE [Part::Extrusion] Extrude433  label="hex048"
  Base = -> Sketch441
  Dir = (0,-1,2e-16)
  DirMode = 2
  FaceMakerClass = Part::FaceMakerBullseye
  FaceMakerMode = 3
  LengthFwd = 10
  LengthRev = 0
  Placement = pos=(-84,0,-21) rot=(0,0,1;0rad)
  Solid = true
  Symmetric = false
FEATURE [Sketcher::SketchObject] Sketch442
  ArcFitTolerance = 1e-06
  FullyConstrained = true
  MakeInternals = false
  Placement = pos=(0,0,0) rot=(1,0,0;1.5708rad)
  sketch-geometry (49):
    g0: LineSegment StartX=1e-16 StartY=3.5 StartZ=0 EndX=-3.03109 EndY=1.75 EndZ=0
    g1: LineSegment StartX=-3.03109 StartY=1.75 StartZ=0 EndX=-3.03109 EndY=-1.75 EndZ=0
    g2: LineSegment StartX=-3.03109 StartY=-1.75 StartZ=0 EndX=-1e-16 EndY=-3.5 EndZ=0
    g3: LineSegment StartX=-1e-16 StartY=-3.5 StartZ=0 EndX=3.03109 EndY=-1.75 EndZ=0
    g4: LineSegment StartX=3.03109 StartY=-1.75 StartZ=0 EndX=3.03109 EndY=1.75 EndZ=0
    g5: LineSegment StartX=3.03109 StartY=1.75 StartZ=0 EndX=1e-16 EndY=3.5 EndZ=0
    g6: Circle [constr] CenterX=0 CenterY=0 CenterZ=0 NormalX=0 NormalY=0 NormalZ=1 AngleXU=0 Radius=3.5
    g7: LineSegment StartX=4.96892 StartY=-1.75002 StartZ=0 EndX=8.00002 EndY=-3.5 EndZ=0
    g8: LineSegment StartX=8.00002 StartY=-3.5 StartZ=0 EndX=11.0311 EndY=-1.74998 EndZ=0
    g9: LineSegment StartX=11.0311 StartY=-1.74998 StartZ=0 EndX=11.0311 EndY=1.75002 EndZ=0
    g10: LineSegment StartX=11.0311 StartY=1.75002 StartZ=0 EndX=7.99998 EndY=3.5 EndZ=0
    g11: LineSegment StartX=7.99998 StartY=3.5 StartZ=0 EndX=4.9689 EndY=1.74998 EndZ=0
    g12: LineSegment StartX=4.9689 StartY=1.74998 StartZ=0 EndX=4.96892 EndY=-1.75002 EndZ=0
    g13: Circle [constr] CenterX=8 CenterY=0 CenterZ=0 NormalX=0 NormalY=0 NormalZ=1 AngleXU=0 Radius=3.5
    g14: LineSegment StartX=4.03109 StartY=3.5 StartZ=0 EndX=7.06218 EndY=5.25 EndZ=0
    g15: LineSegment StartX=7.06218 StartY=5.25 StartZ=0 EndX=7.06218 EndY=8.75 EndZ=0
    g16: LineSegment StartX=7.06218 StartY=8.75 StartZ=0 EndX=4.03109 EndY=10.5 EndZ=0
    g17: LineSegment StartX=4.03109 StartY=10.5 StartZ=0 EndX=1 EndY=8.75 EndZ=0
    g18: LineSegment StartX=1 StartY=8.75 StartZ=0 EndX=1 EndY=5.25 EndZ=0
    g19: LineSegment StartX=1 StartY=5.25 StartZ=0 EndX=4.03109 EndY=3.5 EndZ=0
    g20: Circle [constr] CenterX=4.03109 CenterY=7 CenterZ=0 NormalX=0 NormalY=0 NormalZ=1 AngleXU=0 Radius=3.5
    g21: LineSegment StartX=-1 StartY=5.25 StartZ=0 EndX=-1 EndY=8.75 EndZ=0
    g22: LineSegment StartX=-1 StartY=8.75 StartZ=0 EndX=-4.03109 EndY=10.5 EndZ=0
    g23: LineSegment StartX=-4.03109 StartY=10.5 StartZ=0 EndX=-7.06218 EndY=8.75 EndZ=0
    g24: LineSegment StartX=-7.06218 StartY=8.75 StartZ=0 EndX=-7.06218 EndY=5.25 EndZ=0
    g25: LineSegment StartX=-7.06218 StartY=5.25 StartZ=0 EndX=-4.03109 EndY=3.5 EndZ=0
    g26: LineSegment StartX=-4.03109 StartY=3.5 StartZ=0 EndX=-1 EndY=5.25 EndZ=0
    g27: Circle [constr] CenterX=-4.03109 CenterY=7 CenterZ=0 NormalX=0 NormalY=0 NormalZ=1 AngleXU=0 Radius=3.5
    g28: LineSegment StartX=-4.96891 StartY=-1.75 StartZ=0 EndX=-4.96891 EndY=1.75 EndZ=0
    g29: LineSegment StartX=-4.96891 StartY=1.75 StartZ=0 EndX=-8 EndY=3.5 EndZ=0
    g30: LineSegment StartX=-8 StartY=3.5 StartZ=0 EndX=-11.0311 EndY=1.75 EndZ=0
    g31: LineSegment StartX=-11.0311 StartY=1.75 StartZ=0 EndX=-11.0311 EndY=-1.75 EndZ=0
    g32: LineSegment StartX=-11.0311 StartY=-1.75 StartZ=0 EndX=-8 EndY=-3.5 EndZ=0
    g33: LineSegment StartX=-8 StartY=-3.5 StartZ=0 EndX=-4.96891 EndY=-1.75 EndZ=0
    g34: Circle [constr] CenterX=-8 CenterY=0 CenterZ=0 NormalX=0 NormalY=0 NormalZ=1 AngleXU=0 Radius=3.5
    g35: LineSegment StartX=-4.03109 StartY=-3.5 StartZ=0 EndX=-7.06218 EndY=-5.25 EndZ=0
    g36: LineSegment StartX=-7.06218 StartY=-5.25 StartZ=0 EndX=-7.06218 EndY=-8.75 EndZ=0
    g37: LineSegment StartX=-7.06218 StartY=-8.75 StartZ=0 EndX=-4.03109 EndY=-10.5 EndZ=0
    g38: LineSegment StartX=-4.03109 StartY=-10.5 StartZ=0 EndX=-1 EndY=-8.75 EndZ=0
    g39: LineSegment StartX=-1 StartY=-8.75 StartZ=0 EndX=-1 EndY=-5.25 EndZ=0
    g40: LineSegment StartX=-1 StartY=-5.25 StartZ=0 EndX=-4.03109 EndY=-3.5 EndZ=0
    g41: Circle [constr] CenterX=-4.03109 CenterY=-7 CenterZ=0 NormalX=0 NormalY=0 NormalZ=1 AngleXU=0 Radius=3.5
    g42: LineSegment StartX=4.03109 StartY=-3.5 StartZ=0 EndX=1 EndY=-5.25 EndZ=0
    g43: LineSegment StartX=1 StartY=-5.25 StartZ=0 EndX=1 EndY=-8.75 EndZ=0
    g44: LineSegment StartX=1 StartY=-8.75 StartZ=0 EndX=4.03109 EndY=-10.5 EndZ=0
    g45: LineSegment StartX=4.03109 StartY=-10.5 StartZ=0 EndX=7.06218 EndY=-8.75 EndZ=0
    g46: LineSegment StartX=7.06218 StartY=-8.75 StartZ=0 EndX=7.06218 EndY=-5.25 EndZ=0
    g47: LineSegment StartX=7.06218 StartY=-5.25 StartZ=0 EndX=4.03109 EndY=-3.5 EndZ=0
    g48: Circle [constr] CenterX=4.03109 CenterY=-7 CenterZ=0 NormalX=0 NormalY=0 NormalZ=1 AngleXU=0 Radius=3.5
  constraints (117):
    c: Coincident(g0,g1)
    c: Coincident(g1,g2)
    c: Coincident(g2,g3)
    c: Coincident(g3,g4)
    c: Coincident(g4,g5)
    c: Coincident(g5,g0)
    c: Equal(g0, g1-g5) x5
    c: PointOnObject(g0,g6)
    c: PointOnObject(g1,g6)
    c: PointOnObject(g2,g6)
    c: PointOnObject(g3,g6)
    c: PointOnObject(g4,g6)
    c: PointOnObject(g5,g6)
    c: Coincident(g6,g-1)
    c: Diameter(g6) = 7
    c: PointOnObject(g0,g-2)
    c: Coincident(g7,g8)
    c: Coincident(g8,g9)
    c: Coincident(g9,g10)
    c: Coincident(g10,g11)
    c: Coincident(g11,g12)
    c: Coincident(g12,g7)
    c: Equal(g7, g8-g12) x5
    c: PointOnObject(g7,g13)
    c: PointOnObject(g8,g13)
    c: PointOnObject(g9,g13)
    c: PointOnObject(g10,g13)
    c: PointOnObject(g11,g13)
    c: PointOnObject(g12,g13)
    c: PointOnObject(g13,g-1)
    c: Diameter(g13) = 7
    c: Distance(g6,g13) = 8
    c: Horizontal(g0,g10)
    c: Coincident(g14,g15)
    c: Coincident(g15,g16)
    c: Coincident(g16,g17)
    c: Coincident(g17,g18)
    c: Coincident(g18,g19)
    c: Coincident(g19,g14)
    c: Equal(g14, g15-g19) x5
    c: PointOnObject(g14,g20)
    c: PointOnObject(g15,g20)
    c: PointOnObject(g16,g20)
    c: PointOnObject(g17,g20)
    c: PointOnObject(g18,g20)
    c: PointOnObject(g19,g20)
    c: Diameter(g20) = 7
    c: DistanceY(g-1,g20) = 7
    c: Vertical(g18)
    c: Distance(g17,g-2) = 1
    c: Coincident(g21,g22)
    c: Coincident(g22,g23)
    c: Coincident(g23,g24)
    c: Coincident(g24,g25)
    c: Coincident(g25,g26)
    c: Coincident(g26,g21)
    c: Equal(g21, g22-g26) x5
    c: PointOnObject(g21,g27)
    c: PointOnObject(g22,g27)
    c: PointOnObject(g23,g27)
    c: PointOnObject(g24,g27)
    c: PointOnObject(g25,g27)
    c: PointOnObject(g26,g27)
    c: Diameter(g27) = 7
    c: DistanceY(g-1,g27) = 7
    c: DistanceX(g21,g-1) = 1
    c: Vertical(g21)
    c: Coincident(g28,g29)
    c: Coincident(g29,g30)
    c: Coincident(g30,g31)
    c: Coincident(g31,g32)
    c: Coincident(g32,g33)
    c: Coincident(g33,g28)
    c: Equal(g28, g29-g33) x5
    c: PointOnObject(g28,g34)
    c: PointOnObject(g29,g34)
    c: PointOnObject(g30,g34)
    c: PointOnObject(g31,g34)
    c: PointOnObject(g32,g34)
    c: PointOnObject(g33,g34)
    c: PointOnObject(g34,g-1)
    c: Diameter(g34) = 7
    c: Vertical(g31)
    c: DistanceX(g34,g-1) = 8
    c: Coincident(g35,g36)
    c: Coincident(g36,g37)
    c: Coincident(g37,g38)
    c: Coincident(g38,g39)
    c: Coincident(g39,g40)
    c: Coincident(g40,g35)
    c: Equal(g35, g36-g40) x5
    c: PointOnObject(g35,g41)
    c: PointOnObject(g36,g41)
    c: PointOnObject(g37,g41)
    c: PointOnObject(g38,g41)
    c: PointOnObject(g39,g41)
    c: PointOnObject(g40,g41)
    c: Coincident(g42,g43)
    c: Coincident(g43,g44)
    c: Coincident(g44,g45)
    c: Coincident(g45,g46)
    c: Coincident(g46,g47)
    c: Coincident(g47,g42)
    c: Equal(g42, g43-g47) x5
    c: PointOnObject(g42,g48)
    c: PointOnObject(g43,g48)
    c: PointOnObject(g44,g48)
    c: PointOnObject(g45,g48)
    c: PointOnObject(g46,g48)
    c: PointOnObject(g47,g48)
    c: Equal(g41,g48)
    c: Diameter(g41) = 7
    c: Vertical(g39)
    c: Vertical(g43)
    c: Distance(g-2,g39) = 1
    c: Symmetric(g38,g43,g-2)
    c: Distance(g41,g-1) = 7
FEATURE [Part::Extrusion] Extrude434  label="hex049"
  Base = -> Sketch442
  Dir = (0,-1,2e-16)
  DirMode = 2
  FaceMakerClass = Part::FaceMakerBullseye
  FaceMakerMode = 3
  LengthFwd = 10
  LengthRev = 0
  Placement = pos=(-88,0,14) rot=(0,0,1;0rad)
  Solid = true
  Symmetric = false
FEATURE [Sketcher::SketchObject] Sketch443
  ArcFitTolerance = 1e-06
  FullyConstrained = true
  MakeInternals = false
  Placement = pos=(0,0,0) rot=(1,0,0;1.5708rad)
  sketch-geometry (49):
    g0: LineSegment StartX=1e-16 StartY=3.5 StartZ=0 EndX=-3.03109 EndY=1.75 EndZ=0
    g1: LineSegment StartX=-3.03109 StartY=1.75 StartZ=0 EndX=-3.03109 EndY=-1.75 EndZ=0
    g2: LineSegment StartX=-3.03109 StartY=-1.75 StartZ=0 EndX=-1e-16 EndY=-3.5 EndZ=0
    g3: LineSegment StartX=-1e-16 StartY=-3.5 StartZ=0 EndX=3.03109 EndY=-1.75 EndZ=0
    g4: LineSegment StartX=3.03109 StartY=-1.75 StartZ=0 EndX=3.03109 EndY=1.75 EndZ=0
    g5: LineSegment StartX=3.03109 StartY=1.75 StartZ=0 EndX=1e-16 EndY=3.5 EndZ=0
    g6: Circle [constr] CenterX=0 CenterY=0 CenterZ=0 NormalX=0 NormalY=0 NormalZ=1 AngleXU=0 Radius=3.5
    g7: LineSegment StartX=4.96892 StartY=-1.75002 StartZ=0 EndX=8.00002 EndY=-3.5 EndZ=0
    g8: LineSegment StartX=8.00002 StartY=-3.5 StartZ=0 EndX=11.0311 EndY=-1.74998 EndZ=0
    g9: LineSegment StartX=11.0311 StartY=-1.74998 StartZ=0 EndX=11.0311 EndY=1.75002 EndZ=0
    g10: LineSegment StartX=11.0311 StartY=1.75002 StartZ=0 EndX=7.99998 EndY=3.5 EndZ=0
    g11: LineSegment StartX=7.99998 StartY=3.5 StartZ=0 EndX=4.9689 EndY=1.74998 EndZ=0
    g12: LineSegment StartX=4.9689 StartY=1.74998 StartZ=0 EndX=4.96892 EndY=-1.75002 EndZ=0
    g13: Circle [constr] CenterX=8 CenterY=0 CenterZ=0 NormalX=0 NormalY=0 NormalZ=1 AngleXU=0 Radius=3.5
    g14: LineSegment StartX=4.03109 StartY=3.5 StartZ=0 EndX=7.06218 EndY=5.25 EndZ=0
    g15: LineSegment StartX=7.06218 StartY=5.25 StartZ=0 EndX=7.06218 EndY=8.75 EndZ=0
    g16: LineSegment StartX=7.06218 StartY=8.75 StartZ=0 EndX=4.03109 EndY=10.5 EndZ=0
    g17: LineSegment StartX=4.03109 StartY=10.5 StartZ=0 EndX=1 EndY=8.75 EndZ=0
    g18: LineSegment StartX=1 StartY=8.75 StartZ=0 EndX=1 EndY=5.25 EndZ=0
    g19: LineSegment StartX=1 StartY=5.25 StartZ=0 EndX=4.03109 EndY=3.5 EndZ=0
    g20: Circle [constr] CenterX=4.03109 CenterY=7 CenterZ=0 NormalX=0 NormalY=0 NormalZ=1 AngleXU=0 Radius=3.5
    g21: LineSegment StartX=-1 StartY=5.25 StartZ=0 EndX=-1 EndY=8.75 EndZ=0
    g22: LineSegment StartX=-1 StartY=8.75 StartZ=0 EndX=-4.03109 EndY=10.5 EndZ=0
    g23: LineSegment StartX=-4.03109 StartY=10.5 StartZ=0 EndX=-7.06218 EndY=8.75 EndZ=0
    g24: LineSegment StartX=-7.06218 StartY=8.75 StartZ=0 EndX=-7.06218 EndY=5.25 EndZ=0
    g25: LineSegment StartX=-7.06218 StartY=5.25 StartZ=0 EndX=-4.03109 EndY=3.5 EndZ=0
    g26: LineSegment StartX=-4.03109 StartY=3.5 StartZ=0 EndX=-1 EndY=5.25 EndZ=0
    g27: Circle [constr] CenterX=-4.03109 CenterY=7 CenterZ=0 NormalX=0 NormalY=0 NormalZ=1 AngleXU=0 Radius=3.5
    g28: LineSegment StartX=-4.96891 StartY=-1.75 StartZ=0 EndX=-4.96891 EndY=1.75 EndZ=0
    g29: LineSegment StartX=-4.96891 StartY=1.75 StartZ=0 EndX=-8 EndY=3.5 EndZ=0
    g30: LineSegment StartX=-8 StartY=3.5 StartZ=0 EndX=-11.0311 EndY=1.75 EndZ=0
    g31: LineSegment StartX=-11.0311 StartY=1.75 StartZ=0 EndX=-11.0311 EndY=-1.75 EndZ=0
    g32: LineSegment StartX=-11.0311 StartY=-1.75 StartZ=0 EndX=-8 EndY=-3.5 EndZ=0
    g33: LineSegment StartX=-8 StartY=-3.5 StartZ=0 EndX=-4.96891 EndY=-1.75 EndZ=0
    g34: Circle [constr] CenterX=-8 CenterY=0 CenterZ=0 NormalX=0 NormalY=0 NormalZ=1 AngleXU=0 Radius=3.5
    g35: LineSegment StartX=-4.03109 StartY=-3.5 StartZ=0 EndX=-7.06218 EndY=-5.25 EndZ=0
    g36: LineSegment StartX=-7.06218 StartY=-5.25 StartZ=0 EndX=-7.06218 EndY=-8.75 EndZ=0
    g37: LineSegment StartX=-7.06218 StartY=-8.75 StartZ=0 EndX=-4.03109 EndY=-10.5 EndZ=0
    g38: LineSegment StartX=-4.03109 StartY=-10.5 StartZ=0 EndX=-1 EndY=-8.75 EndZ=0
    g39: LineSegment StartX=-1 StartY=-8.75 StartZ=0 EndX=-1 EndY=-5.25 EndZ=0
    g40: LineSegment StartX=-1 StartY=-5.25 StartZ=0 EndX=-4.03109 EndY=-3.5 EndZ=0
    g41: Circle [constr] CenterX=-4.03109 CenterY=-7 CenterZ=0 NormalX=0 NormalY=0 NormalZ=1 AngleXU=0 Radius=3.5
    g42: LineSegment StartX=4.03109 StartY=-3.5 StartZ=0 EndX=1 EndY=-5.25 EndZ=0
    g43: LineSegment StartX=1 StartY=-5.25 StartZ=0 EndX=1 EndY=-8.75 EndZ=0
    g44: LineSegment StartX=1 StartY=-8.75 StartZ=0 EndX=4.03109 EndY=-10.5 EndZ=0
    g45: LineSegment StartX=4.03109 StartY=-10.5 StartZ=0 EndX=7.06218 EndY=-8.75 EndZ=0
    g46: LineSegment StartX=7.06218 StartY=-8.75 StartZ=0 EndX=7.06218 EndY=-5.25 EndZ=0
    g47: LineSegment StartX=7.06218 StartY=-5.25 StartZ=0 EndX=4.03109 EndY=-3.5 EndZ=0
    g48: Circle [constr] CenterX=4.03109 CenterY=-7 CenterZ=0 NormalX=0 NormalY=0 NormalZ=1 AngleXU=0 Radius=3.5
  constraints (117):
    c: Coincident(g0,g1)
    c: Coincident(g1,g2)
    c: Coincident(g2,g3)
    c: Coincident(g3,g4)
    c: Coincident(g4,g5)
    c: Coincident(g5,g0)
    c: Equal(g0, g1-g5) x5
    c: PointOnObject(g0,g6)
    c: PointOnObject(g1,g6)
    c: PointOnObject(g2,g6)
    c: PointOnObject(g3,g6)
    c: PointOnObject(g4,g6)
    c: PointOnObject(g5,g6)
    c: Coincident(g6,g-1)
    c: Diameter(g6) = 7
    c: PointOnObject(g0,g-2)
    c: Coincident(g7,g8)
    c: Coincident(g8,g9)
    c: Coincident(g9,g10)
    c: Coincident(g10,g11)
    c: Coincident(g11,g12)
    c: Coincident(g12,g7)
    c: Equal(g7, g8-g12) x5
    c: PointOnObject(g7,g13)
    c: PointOnObject(g8,g13)
    c: PointOnObject(g9,g13)
    c: PointOnObject(g10,g13)
    c: PointOnObject(g11,g13)
    c: PointOnObject(g12,g13)
    c: PointOnObject(g13,g-1)
    c: Diameter(g13) = 7
    c: Distance(g6,g13) = 8
    c: Horizontal(g0,g10)
    c: Coincident(g14,g15)
    c: Coincident(g15,g16)
    c: Coincident(g16,g17)
    c: Coincident(g17,g18)
    c: Coincident(g18,g19)
    c: Coincident(g19,g14)
    c: Equal(g14, g15-g19) x5
    c: PointOnObject(g14,g20)
    c: PointOnObject(g15,g20)
    c: PointOnObject(g16,g20)
    c: PointOnObject(g17,g20)
    c: PointOnObject(g18,g20)
    c: PointOnObject(g19,g20)
    c: Diameter(g20) = 7
    c: DistanceY(g-1,g20) = 7
    c: Vertical(g18)
    c: Distance(g17,g-2) = 1
    c: Coincident(g21,g22)
    c: Coincident(g22,g23)
    c: Coincident(g23,g24)
    c: Coincident(g24,g25)
    c: Coincident(g25,g26)
    c: Coincident(g26,g21)
    c: Equal(g21, g22-g26) x5
    c: PointOnObject(g21,g27)
    c: PointOnObject(g22,g27)
    c: PointOnObject(g23,g27)
    c: PointOnObject(g24,g27)
    c: PointOnObject(g25,g27)
    c: PointOnObject(g26,g27)
    c: Diameter(g27) = 7
    c: DistanceY(g-1,g27) = 7
    c: DistanceX(g21,g-1) = 1
    c: Vertical(g21)
    c: Coincident(g28,g29)
    c: Coincident(g29,g30)
    c: Coincident(g30,g31)
    c: Coincident(g31,g32)
    c: Coincident(g32,g33)
    c: Coincident(g33,g28)
    c: Equal(g28, g29-g33) x5
    c: PointOnObject(g28,g34)
    c: PointOnObject(g29,g34)
    c: PointOnObject(g30,g34)
    c: PointOnObject(g31,g34)
    c: PointOnObject(g32,g34)
    c: PointOnObject(g33,g34)
    c: PointOnObject(g34,g-1)
    c: Diameter(g34) = 7
    c: Vertical(g31)
    c: DistanceX(g34,g-1) = 8
    c: Coincident(g35,g36)
    c: Coincident(g36,g37)
    c: Coincident(g37,g38)
    c: Coincident(g38,g39)
    c: Coincident(g39,g40)
    c: Coincident(g40,g35)
    c: Equal(g35, g36-g40) x5
    c: PointOnObject(g35,g41)
    c: PointOnObject(g36,g41)
    c: PointOnObject(g37,g41)
    c: PointOnObject(g38,g41)
    c: PointOnObject(g39,g41)
    c: PointOnObject(g40,g41)
    c: Coincident(g42,g43)
    c: Coincident(g43,g44)
    c: Coincident(g44,g45)
    c: Coincident(g45,g46)
    c: Coincident(g46,g47)
    c: Coincident(g47,g42)
    c: Equal(g42, g43-g47) x5
    c: PointOnObject(g42,g48)
    c: PointOnObject(g43,g48)
    c: PointOnObject(g44,g48)
    c: PointOnObject(g45,g48)
    c: PointOnObject(g46,g48)
    c: PointOnObject(g47,g48)
    c: Equal(g41,g48)
    c: Diameter(g41) = 7
    c: Vertical(g39)
    c: Vertical(g43)
    c: Distance(g-2,g39) = 1
    c: Symmetric(g38,g43,g-2)
    c: Distance(g41,g-1) = 7
FEATURE [Part::Extrusion] Extrude435  label="hex050"
  Base = -> Sketch443
  Dir = (0,-1,2e-16)
  DirMode = 2
  FaceMakerClass = Part::FaceMakerBullseye
  FaceMakerMode = 3
  LengthFwd = 10
  LengthRev = 0
  Placement = pos=(96,0,14) rot=(0,0,1;0rad)
  Solid = true
  Symmetric = false
FEATURE [Part::MultiFuse] Fusion547
  Refine = true
  Shapes = -> [Extrude386,Extrude387,Extrude388,Extrude389,Extrude390,Extrude391,Extrude392,Extrude393,Extrude394,Extrude395,Extrude396,Extrude397,Extrude398,Extrude399,Extrude400,Extrude401,Extrude402,Extrude403,Extrude404,Extrude405,Extrude406,Extrude407,Extrude408,Extrude409,Extrude410,Extrude411,Extrude412,Extrude413,Extrude414,Extrude415,Extrude416,Extrude417,Extrude418,Extrude419,Extrude420,Extrude421,+14 more]
FEATURE [Sketcher::SketchObject] Sketch444
  ArcFitTolerance = 1e-06
  FullyConstrained = true
  MakeInternals = false
  Placement = pos=(0,0,0) rot=(1,0,0;1.5708rad)
  sketch-geometry (49):
    g0: LineSegment StartX=1e-16 StartY=3.5 StartZ=0 EndX=-3.03109 EndY=1.75 EndZ=0
    g1: LineSegment StartX=-3.03109 StartY=1.75 StartZ=0 EndX=-3.03109 EndY=-1.75 EndZ=0
    g2: LineSegment StartX=-3.03109 StartY=-1.75 StartZ=0 EndX=-1e-16 EndY=-3.5 EndZ=0
    g3: LineSegment StartX=-1e-16 StartY=-3.5 StartZ=0 EndX=3.03109 EndY=-1.75 EndZ=0
    g4: LineSegment StartX=3.03109 StartY=-1.75 StartZ=0 EndX=3.03109 EndY=1.75 EndZ=0
    g5: LineSegment StartX=3.03109 StartY=1.75 StartZ=0 EndX=1e-16 EndY=3.5 EndZ=0
    g6: Circle [constr] CenterX=0 CenterY=0 CenterZ=0 NormalX=0 NormalY=0 NormalZ=1 AngleXU=0 Radius=3.5
    g7: LineSegment StartX=4.96892 StartY=-1.75002 StartZ=0 EndX=8.00002 EndY=-3.5 EndZ=0
    g8: LineSegment StartX=8.00002 StartY=-3.5 StartZ=0 EndX=11.0311 EndY=-1.74998 EndZ=0
    g9: LineSegment StartX=11.0311 StartY=-1.74998 StartZ=0 EndX=11.0311 EndY=1.75002 EndZ=0
    g10: LineSegment StartX=11.0311 StartY=1.75002 StartZ=0 EndX=7.99998 EndY=3.5 EndZ=0
    g11: LineSegment StartX=7.99998 StartY=3.5 StartZ=0 EndX=4.9689 EndY=1.74998 EndZ=0
    g12: LineSegment StartX=4.9689 StartY=1.74998 StartZ=0 EndX=4.96892 EndY=-1.75002 EndZ=0
    g13: Circle [constr] CenterX=8 CenterY=0 CenterZ=0 NormalX=0 NormalY=0 NormalZ=1 AngleXU=0 Radius=3.5
    g14: LineSegment StartX=4.03109 StartY=3.5 StartZ=0 EndX=7.06218 EndY=5.25 EndZ=0
    g15: LineSegment StartX=7.06218 StartY=5.25 StartZ=0 EndX=7.06218 EndY=8.75 EndZ=0
    g16: LineSegment StartX=7.06218 StartY=8.75 StartZ=0 EndX=4.03109 EndY=10.5 EndZ=0
    g17: LineSegment StartX=4.03109 StartY=10.5 StartZ=0 EndX=1 EndY=8.75 EndZ=0
    g18: LineSegment StartX=1 StartY=8.75 StartZ=0 EndX=1 EndY=5.25 EndZ=0
    g19: LineSegment StartX=1 StartY=5.25 StartZ=0 EndX=4.03109 EndY=3.5 EndZ=0
    g20: Circle [constr] CenterX=4.03109 CenterY=7 CenterZ=0 NormalX=0 NormalY=0 NormalZ=1 AngleXU=0 Radius=3.5
    g21: LineSegment StartX=-1 StartY=5.25 StartZ=0 EndX=-1 EndY=8.75 EndZ=0
    g22: LineSegment StartX=-1 StartY=8.75 StartZ=0 EndX=-4.03109 EndY=10.5 EndZ=0
    g23: LineSegment StartX=-4.03109 StartY=10.5 StartZ=0 EndX=-7.06218 EndY=8.75 EndZ=0
    g24: LineSegment StartX=-7.06218 StartY=8.75 StartZ=0 EndX=-7.06218 EndY=5.25 EndZ=0
    g25: LineSegment StartX=-7.06218 StartY=5.25 StartZ=0 EndX=-4.03109 EndY=3.5 EndZ=0
    g26: LineSegment StartX=-4.03109 StartY=3.5 StartZ=0 EndX=-1 EndY=5.25 EndZ=0
    g27: Circle [constr] CenterX=-4.03109 CenterY=7 CenterZ=0 NormalX=0 NormalY=0 NormalZ=1 AngleXU=0 Radius=3.5
    g28: LineSegment StartX=-4.96891 StartY=-1.75 StartZ=0 EndX=-4.96891 EndY=1.75 EndZ=0
    g29: LineSegment StartX=-4.96891 StartY=1.75 StartZ=0 EndX=-8 EndY=3.5 EndZ=0
    g30: LineSegment StartX=-8 StartY=3.5 StartZ=0 EndX=-11.0311 EndY=1.75 EndZ=0
    g31: LineSegment StartX=-11.0311 StartY=1.75 StartZ=0 EndX=-11.0311 EndY=-1.75 EndZ=0
    g32: LineSegment StartX=-11.0311 StartY=-1.75 StartZ=0 EndX=-8 EndY=-3.5 EndZ=0
    g33: LineSegment StartX=-8 StartY=-3.5 StartZ=0 EndX=-4.96891 EndY=-1.75 EndZ=0
    g34: Circle [constr] CenterX=-8 CenterY=0 CenterZ=0 NormalX=0 NormalY=0 NormalZ=1 AngleXU=0 Radius=3.5
    g35: LineSegment StartX=-4.03109 StartY=-3.5 StartZ=0 EndX=-7.06218 EndY=-5.25 EndZ=0
    g36: LineSegment StartX=-7.06218 StartY=-5.25 StartZ=0 EndX=-7.06218 EndY=-8.75 EndZ=0
    g37: LineSegment StartX=-7.06218 StartY=-8.75 StartZ=0 EndX=-4.03109 EndY=-10.5 EndZ=0
    g38: LineSegment StartX=-4.03109 StartY=-10.5 StartZ=0 EndX=-1 EndY=-8.75 EndZ=0
    g39: LineSegment StartX=-1 StartY=-8.75 StartZ=0 EndX=-1 EndY=-5.25 EndZ=0
    g40: LineSegment StartX=-1 StartY=-5.25 StartZ=0 EndX=-4.03109 EndY=-3.5 EndZ=0
    g41: Circle [constr] CenterX=-4.03109 CenterY=-7 CenterZ=0 NormalX=0 NormalY=0 NormalZ=1 AngleXU=0 Radius=3.5
    g42: LineSegment StartX=4.03109 StartY=-3.5 StartZ=0 EndX=1 EndY=-5.25 EndZ=0
    g43: LineSegment StartX=1 StartY=-5.25 StartZ=0 EndX=1 EndY=-8.75 EndZ=0
    g44: LineSegment StartX=1 StartY=-8.75 StartZ=0 EndX=4.03109 EndY=-10.5 EndZ=0
    g45: LineSegment StartX=4.03109 StartY=-10.5 StartZ=0 EndX=7.06218 EndY=-8.75 EndZ=0
    g46: LineSegment StartX=7.06218 StartY=-8.75 StartZ=0 EndX=7.06218 EndY=-5.25 EndZ=0
    g47: LineSegment StartX=7.06218 StartY=-5.25 StartZ=0 EndX=4.03109 EndY=-3.5 EndZ=0
    g48: Circle [constr] CenterX=4.03109 CenterY=-7 CenterZ=0 NormalX=0 NormalY=0 NormalZ=1 AngleXU=0 Radius=3.5
  constraints (117):
    c: Coincident(g0,g1)
    c: Coincident(g1,g2)
    c: Coincident(g2,g3)
    c: Coincident(g3,g4)
    c: Coincident(g4,g5)
    c: Coincident(g5,g0)
    c: Equal(g0, g1-g5) x5
    c: PointOnObject(g0,g6)
    c: PointOnObject(g1,g6)
    c: PointOnObject(g2,g6)
    c: PointOnObject(g3,g6)
    c: PointOnObject(g4,g6)
    c: PointOnObject(g5,g6)
    c: Coincident(g6,g-1)
    c: Diameter(g6) = 7
    c: PointOnObject(g0,g-2)
    c: Coincident(g7,g8)
    c: Coincident(g8,g9)
    c: Coincident(g9,g10)
    c: Coincident(g10,g11)
    c: Coincident(g11,g12)
    c: Coincident(g12,g7)
    c: Equal(g7, g8-g12) x5
    c: PointOnObject(g7,g13)
    c: PointOnObject(g8,g13)
    c: PointOnObject(g9,g13)
    c: PointOnObject(g10,g13)
    c: PointOnObject(g11,g13)
    c: PointOnObject(g12,g13)
    c: PointOnObject(g13,g-1)
    c: Diameter(g13) = 7
    c: Distance(g6,g13) = 8
    c: Horizontal(g0,g10)
    c: Coincident(g14,g15)
    c: Coincident(g15,g16)
    c: Coincident(g16,g17)
    c: Coincident(g17,g18)
    c: Coincident(g18,g19)
    c: Coincident(g19,g14)
    c: Equal(g14, g15-g19) x5
    c: PointOnObject(g14,g20)
    c: PointOnObject(g15,g20)
    c: PointOnObject(g16,g20)
    c: PointOnObject(g17,g20)
    c: PointOnObject(g18,g20)
    c: PointOnObject(g19,g20)
    c: Diameter(g20) = 7
    c: DistanceY(g-1,g20) = 7
    c: Vertical(g18)
    c: Distance(g17,g-2) = 1
    c: Coincident(g21,g22)
    c: Coincident(g22,g23)
    c: Coincident(g23,g24)
    c: Coincident(g24,g25)
    c: Coincident(g25,g26)
    c: Coincident(g26,g21)
    c: Equal(g21, g22-g26) x5
    c: PointOnObject(g21,g27)
    c: PointOnObject(g22,g27)
    c: PointOnObject(g23,g27)
    c: PointOnObject(g24,g27)
    c: PointOnObject(g25,g27)
    c: PointOnObject(g26,g27)
    c: Diameter(g27) = 7
    c: DistanceY(g-1,g27) = 7
    c: DistanceX(g21,g-1) = 1
    c: Vertical(g21)
    c: Coincident(g28,g29)
    c: Coincident(g29,g30)
    c: Coincident(g30,g31)
    c: Coincident(g31,g32)
    c: Coincident(g32,g33)
    c: Coincident(g33,g28)
    c: Equal(g28, g29-g33) x5
    c: PointOnObject(g28,g34)
    c: PointOnObject(g29,g34)
    c: PointOnObject(g30,g34)
    c: PointOnObject(g31,g34)
    c: PointOnObject(g32,g34)
    c: PointOnObject(g33,g34)
    c: PointOnObject(g34,g-1)
    c: Diameter(g34) = 7
    c: Vertical(g31)
    c: DistanceX(g34,g-1) = 8
    c: Coincident(g35,g36)
    c: Coincident(g36,g37)
    c: Coincident(g37,g38)
    c: Coincident(g38,g39)
    c: Coincident(g39,g40)
    c: Coincident(g40,g35)
    c: Equal(g35, g36-g40) x5
    c: PointOnObject(g35,g41)
    c: PointOnObject(g36,g41)
    c: PointOnObject(g37,g41)
    c: PointOnObject(g38,g41)
    c: PointOnObject(g39,g41)
    c: PointOnObject(g40,g41)
    c: Coincident(g42,g43)
    c: Coincident(g43,g44)
    c: Coincident(g44,g45)
    c: Coincident(g45,g46)
    c: Coincident(g46,g47)
    c: Coincident(g47,g42)
    c: Equal(g42, g43-g47) x5
    c: PointOnObject(g42,g48)
    c: PointOnObject(g43,g48)
    c: PointOnObject(g44,g48)
    c: PointOnObject(g45,g48)
    c: PointOnObject(g46,g48)
    c: PointOnObject(g47,g48)
    c: Equal(g41,g48)
    c: Diameter(g41) = 7
    c: Vertical(g39)
    c: Vertical(g43)
    c: Distance(g-2,g39) = 1
    c: Symmetric(g38,g43,g-2)
    c: Distance(g41,g-1) = 7
FEATURE [Part::Extrusion] Extrude436  label="hex051"
  Base = -> Sketch444
  Dir = (0,-1,2e-16)
  DirMode = 2
  FaceMakerClass = Part::FaceMakerBullseye
  FaceMakerMode = 3
  LengthFwd = 10
  LengthRev = 0
  Solid = true
  Symmetric = false
FEATURE [Sketcher::SketchObject] Sketch445
  ArcFitTolerance = 1e-06
  FullyConstrained = true
  MakeInternals = false
  Placement = pos=(0,0,0) rot=(1,0,0;1.5708rad)
  sketch-geometry (49):
    g0: LineSegment StartX=1e-16 StartY=3.5 StartZ=0 EndX=-3.03109 EndY=1.75 EndZ=0
    g1: LineSegment StartX=-3.03109 StartY=1.75 StartZ=0 EndX=-3.03109 EndY=-1.75 EndZ=0
    g2: LineSegment StartX=-3.03109 StartY=-1.75 StartZ=0 EndX=-1e-16 EndY=-3.5 EndZ=0
    g3: LineSegment StartX=-1e-16 StartY=-3.5 StartZ=0 EndX=3.03109 EndY=-1.75 EndZ=0
    g4: LineSegment StartX=3.03109 StartY=-1.75 StartZ=0 EndX=3.03109 EndY=1.75 EndZ=0
    g5: LineSegment StartX=3.03109 StartY=1.75 StartZ=0 EndX=1e-16 EndY=3.5 EndZ=0
    g6: Circle [constr] CenterX=0 CenterY=0 CenterZ=0 NormalX=0 NormalY=0 NormalZ=1 AngleXU=0 Radius=3.5
    g7: LineSegment StartX=4.96892 StartY=-1.75002 StartZ=0 EndX=8.00002 EndY=-3.5 EndZ=0
    g8: LineSegment StartX=8.00002 StartY=-3.5 StartZ=0 EndX=11.0311 EndY=-1.74998 EndZ=0
    g9: LineSegment StartX=11.0311 StartY=-1.74998 StartZ=0 EndX=11.0311 EndY=1.75002 EndZ=0
    g10: LineSegment StartX=11.0311 StartY=1.75002 StartZ=0 EndX=7.99998 EndY=3.5 EndZ=0
    g11: LineSegment StartX=7.99998 StartY=3.5 StartZ=0 EndX=4.9689 EndY=1.74998 EndZ=0
    g12: LineSegment StartX=4.9689 StartY=1.74998 StartZ=0 EndX=4.96892 EndY=-1.75002 EndZ=0
    g13: Circle [constr] CenterX=8 CenterY=0 CenterZ=0 NormalX=0 NormalY=0 NormalZ=1 AngleXU=0 Radius=3.5
    g14: LineSegment StartX=4.03109 StartY=3.5 StartZ=0 EndX=7.06218 EndY=5.25 EndZ=0
    g15: LineSegment StartX=7.06218 StartY=5.25 StartZ=0 EndX=7.06218 EndY=8.75 EndZ=0
    g16: LineSegment StartX=7.06218 StartY=8.75 StartZ=0 EndX=4.03109 EndY=10.5 EndZ=0
    g17: LineSegment StartX=4.03109 StartY=10.5 StartZ=0 EndX=1 EndY=8.75 EndZ=0
    g18: LineSegment StartX=1 StartY=8.75 StartZ=0 EndX=1 EndY=5.25 EndZ=0
    g19: LineSegment StartX=1 StartY=5.25 StartZ=0 EndX=4.03109 EndY=3.5 EndZ=0
    g20: Circle [constr] CenterX=4.03109 CenterY=7 CenterZ=0 NormalX=0 NormalY=0 NormalZ=1 AngleXU=0 Radius=3.5
    g21: LineSegment StartX=-1 StartY=5.25 StartZ=0 EndX=-1 EndY=8.75 EndZ=0
    g22: LineSegment StartX=-1 StartY=8.75 StartZ=0 EndX=-4.03109 EndY=10.5 EndZ=0
    g23: LineSegment StartX=-4.03109 StartY=10.5 StartZ=0 EndX=-7.06218 EndY=8.75 EndZ=0
    g24: LineSegment StartX=-7.06218 StartY=8.75 StartZ=0 EndX=-7.06218 EndY=5.25 EndZ=0
    g25: LineSegment StartX=-7.06218 StartY=5.25 StartZ=0 EndX=-4.03109 EndY=3.5 EndZ=0
    g26: LineSegment StartX=-4.03109 StartY=3.5 StartZ=0 EndX=-1 EndY=5.25 EndZ=0
    g27: Circle [constr] CenterX=-4.03109 CenterY=7 CenterZ=0 NormalX=0 NormalY=0 NormalZ=1 AngleXU=0 Radius=3.5
    g28: LineSegment StartX=-4.96891 StartY=-1.75 StartZ=0 EndX=-4.96891 EndY=1.75 EndZ=0
    g29: LineSegment StartX=-4.96891 StartY=1.75 StartZ=0 EndX=-8 EndY=3.5 EndZ=0
    g30: LineSegment StartX=-8 StartY=3.5 StartZ=0 EndX=-11.0311 EndY=1.75 EndZ=0
    g31: LineSegment StartX=-11.0311 StartY=1.75 StartZ=0 EndX=-11.0311 EndY=-1.75 EndZ=0
    g32: LineSegment StartX=-11.0311 StartY=-1.75 StartZ=0 EndX=-8 EndY=-3.5 EndZ=0
    g33: LineSegment StartX=-8 StartY=-3.5 StartZ=0 EndX=-4.96891 EndY=-1.75 EndZ=0
    g34: Circle [constr] CenterX=-8 CenterY=0 CenterZ=0 NormalX=0 NormalY=0 NormalZ=1 AngleXU=0 Radius=3.5
    g35: LineSegment StartX=-4.03109 StartY=-3.5 StartZ=0 EndX=-7.06218 EndY=-5.25 EndZ=0
    g36: LineSegment StartX=-7.06218 StartY=-5.25 StartZ=0 EndX=-7.06218 EndY=-8.75 EndZ=0
    g37: LineSegment StartX=-7.06218 StartY=-8.75 StartZ=0 EndX=-4.03109 EndY=-10.5 EndZ=0
    g38: LineSegment StartX=-4.03109 StartY=-10.5 StartZ=0 EndX=-1 EndY=-8.75 EndZ=0
    g39: LineSegment StartX=-1 StartY=-8.75 StartZ=0 EndX=-1 EndY=-5.25 EndZ=0
    g40: LineSegment StartX=-1 StartY=-5.25 StartZ=0 EndX=-4.03109 EndY=-3.5 EndZ=0
    g41: Circle [constr] CenterX=-4.03109 CenterY=-7 CenterZ=0 NormalX=0 NormalY=0 NormalZ=1 AngleXU=0 Radius=3.5
    g42: LineSegment StartX=4.03109 StartY=-3.5 StartZ=0 EndX=1 EndY=-5.25 EndZ=0
    g43: LineSegment StartX=1 StartY=-5.25 StartZ=0 EndX=1 EndY=-8.75 EndZ=0
    g44: LineSegment StartX=1 StartY=-8.75 StartZ=0 EndX=4.03109 EndY=-10.5 EndZ=0
    g45: LineSegment StartX=4.03109 StartY=-10.5 StartZ=0 EndX=7.06218 EndY=-8.75 EndZ=0
    g46: LineSegment StartX=7.06218 StartY=-8.75 StartZ=0 EndX=7.06218 EndY=-5.25 EndZ=0
    g47: LineSegment StartX=7.06218 StartY=-5.25 StartZ=0 EndX=4.03109 EndY=-3.5 EndZ=0
    g48: Circle [constr] CenterX=4.03109 CenterY=-7 CenterZ=0 NormalX=0 NormalY=0 NormalZ=1 AngleXU=0 Radius=3.5
  constraints (117):
    c: Coincident(g0,g1)
    c: Coincident(g1,g2)
    c: Coincident(g2,g3)
    c: Coincident(g3,g4)
    c: Coincident(g4,g5)
    c: Coincident(g5,g0)
    c: Equal(g0, g1-g5) x5
    c: PointOnObject(g0,g6)
    c: PointOnObject(g1,g6)
    c: PointOnObject(g2,g6)
    c: PointOnObject(g3,g6)
    c: PointOnObject(g4,g6)
    c: PointOnObject(g5,g6)
    c: Coincident(g6,g-1)
    c: Diameter(g6) = 7
    c: PointOnObject(g0,g-2)
    c: Coincident(g7,g8)
    c: Coincident(g8,g9)
    c: Coincident(g9,g10)
    c: Coincident(g10,g11)
    c: Coincident(g11,g12)
    c: Coincident(g12,g7)
    c: Equal(g7, g8-g12) x5
    c: PointOnObject(g7,g13)
    c: PointOnObject(g8,g13)
    c: PointOnObject(g9,g13)
    c: PointOnObject(g10,g13)
    c: PointOnObject(g11,g13)
    c: PointOnObject(g12,g13)
    c: PointOnObject(g13,g-1)
    c: Diameter(g13) = 7
    c: Distance(g6,g13) = 8
    c: Horizontal(g0,g10)
    c: Coincident(g14,g15)
    c: Coincident(g15,g16)
    c: Coincident(g16,g17)
    c: Coincident(g17,g18)
    c: Coincident(g18,g19)
    c: Coincident(g19,g14)
    c: Equal(g14, g15-g19) x5
    c: PointOnObject(g14,g20)
    c: PointOnObject(g15,g20)
    c: PointOnObject(g16,g20)
    c: PointOnObject(g17,g20)
    c: PointOnObject(g18,g20)
    c: PointOnObject(g19,g20)
    c: Diameter(g20) = 7
    c: DistanceY(g-1,g20) = 7
    c: Vertical(g18)
    c: Distance(g17,g-2) = 1
    c: Coincident(g21,g22)
    c: Coincident(g22,g23)
    c: Coincident(g23,g24)
    c: Coincident(g24,g25)
    c: Coincident(g25,g26)
    c: Coincident(g26,g21)
    c: Equal(g21, g22-g26) x5
    c: PointOnObject(g21,g27)
    c: PointOnObject(g22,g27)
    c: PointOnObject(g23,g27)
    c: PointOnObject(g24,g27)
    c: PointOnObject(g25,g27)
    c: PointOnObject(g26,g27)
    c: Diameter(g27) = 7
    c: DistanceY(g-1,g27) = 7
    c: DistanceX(g21,g-1) = 1
    c: Vertical(g21)
    c: Coincident(g28,g29)
    c: Coincident(g29,g30)
    c: Coincident(g30,g31)
    c: Coincident(g31,g32)
    c: Coincident(g32,g33)
    c: Coincident(g33,g28)
    c: Equal(g28, g29-g33) x5
    c: PointOnObject(g28,g34)
    c: PointOnObject(g29,g34)
    c: PointOnObject(g30,g34)
    c: PointOnObject(g31,g34)
    c: PointOnObject(g32,g34)
    c: PointOnObject(g33,g34)
    c: PointOnObject(g34,g-1)
    c: Diameter(g34) = 7
    c: Vertical(g31)
    c: DistanceX(g34,g-1) = 8
    c: Coincident(g35,g36)
    c: Coincident(g36,g37)
    c: Coincident(g37,g38)
    c: Coincident(g38,g39)
    c: Coincident(g39,g40)
    c: Coincident(g40,g35)
    c: Equal(g35, g36-g40) x5
    c: PointOnObject(g35,g41)
    c: PointOnObject(g36,g41)
    c: PointOnObject(g37,g41)
    c: PointOnObject(g38,g41)
    c: PointOnObject(g39,g41)
    c: PointOnObject(g40,g41)
    c: Coincident(g42,g43)
    c: Coincident(g43,g44)
    c: Coincident(g44,g45)
    c: Coincident(g45,g46)
    c: Coincident(g46,g47)
    c: Coincident(g47,g42)
    c: Equal(g42, g43-g47) x5
    c: PointOnObject(g42,g48)
    c: PointOnObject(g43,g48)
    c: PointOnObject(g44,g48)
    c: PointOnObject(g45,g48)
    c: PointOnObject(g46,g48)
    c: PointOnObject(g47,g48)
    c: Equal(g41,g48)
    c: Diameter(g41) = 7
    c: Vertical(g39)
    c: Vertical(g43)
    c: Distance(g-2,g39) = 1
    c: Symmetric(g38,g43,g-2)
    c: Distance(g41,g-1) = 7
FEATURE [Part::Extrusion] Extrude437  label="hex052"
  Base = -> Sketch445
  Dir = (0,-1,2e-16)
  DirMode = 2
  FaceMakerClass = Part::FaceMakerBullseye
  FaceMakerMode = 3
  LengthFwd = 10
  LengthRev = 0
  Placement = pos=(20,0,-7) rot=(0,0,1;0rad)
  Solid = true
  Symmetric = false
FEATURE [Sketcher::SketchObject] Sketch446
  ArcFitTolerance = 1e-06
  FullyConstrained = true
  MakeInternals = false
  Placement = pos=(0,0,0) rot=(1,0,0;1.5708rad)
  sketch-geometry (49):
    g0: LineSegment StartX=1e-16 StartY=3.5 StartZ=0 EndX=-3.03109 EndY=1.75 EndZ=0
    g1: LineSegment StartX=-3.03109 StartY=1.75 StartZ=0 EndX=-3.03109 EndY=-1.75 EndZ=0
    g2: LineSegment StartX=-3.03109 StartY=-1.75 StartZ=0 EndX=-1e-16 EndY=-3.5 EndZ=0
    g3: LineSegment StartX=-1e-16 StartY=-3.5 StartZ=0 EndX=3.03109 EndY=-1.75 EndZ=0
    g4: LineSegment StartX=3.03109 StartY=-1.75 StartZ=0 EndX=3.03109 EndY=1.75 EndZ=0
    g5: LineSegment StartX=3.03109 StartY=1.75 StartZ=0 EndX=1e-16 EndY=3.5 EndZ=0
    g6: Circle [constr] CenterX=0 CenterY=0 CenterZ=0 NormalX=0 NormalY=0 NormalZ=1 AngleXU=0 Radius=3.5
    g7: LineSegment StartX=4.96892 StartY=-1.75002 StartZ=0 EndX=8.00002 EndY=-3.5 EndZ=0
    g8: LineSegment StartX=8.00002 StartY=-3.5 StartZ=0 EndX=11.0311 EndY=-1.74998 EndZ=0
    g9: LineSegment StartX=11.0311 StartY=-1.74998 StartZ=0 EndX=11.0311 EndY=1.75002 EndZ=0
    g10: LineSegment StartX=11.0311 StartY=1.75002 StartZ=0 EndX=7.99998 EndY=3.5 EndZ=0
    g11: LineSegment StartX=7.99998 StartY=3.5 StartZ=0 EndX=4.9689 EndY=1.74998 EndZ=0
    g12: LineSegment StartX=4.9689 StartY=1.74998 StartZ=0 EndX=4.96892 EndY=-1.75002 EndZ=0
    g13: Circle [constr] CenterX=8 CenterY=0 CenterZ=0 NormalX=0 NormalY=0 NormalZ=1 AngleXU=0 Radius=3.5
    g14: LineSegment StartX=4.03109 StartY=3.5 StartZ=0 EndX=7.06218 EndY=5.25 EndZ=0
    g15: LineSegment StartX=7.06218 StartY=5.25 StartZ=0 EndX=7.06218 EndY=8.75 EndZ=0
    g16: LineSegment StartX=7.06218 StartY=8.75 StartZ=0 EndX=4.03109 EndY=10.5 EndZ=0
    g17: LineSegment StartX=4.03109 StartY=10.5 StartZ=0 EndX=1 EndY=8.75 EndZ=0
    g18: LineSegment StartX=1 StartY=8.75 StartZ=0 EndX=1 EndY=5.25 EndZ=0
    g19: LineSegment StartX=1 StartY=5.25 StartZ=0 EndX=4.03109 EndY=3.5 EndZ=0
    g20: Circle [constr] CenterX=4.03109 CenterY=7 CenterZ=0 NormalX=0 NormalY=0 NormalZ=1 AngleXU=0 Radius=3.5
    g21: LineSegment StartX=-1 StartY=5.25 StartZ=0 EndX=-1 EndY=8.75 EndZ=0
    g22: LineSegment StartX=-1 StartY=8.75 StartZ=0 EndX=-4.03109 EndY=10.5 EndZ=0
    g23: LineSegment StartX=-4.03109 StartY=10.5 StartZ=0 EndX=-7.06218 EndY=8.75 EndZ=0
    g24: LineSegment StartX=-7.06218 StartY=8.75 StartZ=0 EndX=-7.06218 EndY=5.25 EndZ=0
    g25: LineSegment StartX=-7.06218 StartY=5.25 StartZ=0 EndX=-4.03109 EndY=3.5 EndZ=0
    g26: LineSegment StartX=-4.03109 StartY=3.5 StartZ=0 EndX=-1 EndY=5.25 EndZ=0
    g27: Circle [constr] CenterX=-4.03109 CenterY=7 CenterZ=0 NormalX=0 NormalY=0 NormalZ=1 AngleXU=0 Radius=3.5
    g28: LineSegment StartX=-4.96891 StartY=-1.75 StartZ=0 EndX=-4.96891 EndY=1.75 EndZ=0
    g29: LineSegment StartX=-4.96891 StartY=1.75 StartZ=0 EndX=-8 EndY=3.5 EndZ=0
    g30: LineSegment StartX=-8 StartY=3.5 StartZ=0 EndX=-11.0311 EndY=1.75 EndZ=0
    g31: LineSegment StartX=-11.0311 StartY=1.75 StartZ=0 EndX=-11.0311 EndY=-1.75 EndZ=0
    g32: LineSegment StartX=-11.0311 StartY=-1.75 StartZ=0 EndX=-8 EndY=-3.5 EndZ=0
    g33: LineSegment StartX=-8 StartY=-3.5 StartZ=0 EndX=-4.96891 EndY=-1.75 EndZ=0
    g34: Circle [constr] CenterX=-8 CenterY=0 CenterZ=0 NormalX=0 NormalY=0 NormalZ=1 AngleXU=0 Radius=3.5
    g35: LineSegment StartX=-4.03109 StartY=-3.5 StartZ=0 EndX=-7.06218 EndY=-5.25 EndZ=0
    g36: LineSegment StartX=-7.06218 StartY=-5.25 StartZ=0 EndX=-7.06218 EndY=-8.75 EndZ=0
    g37: LineSegment StartX=-7.06218 StartY=-8.75 StartZ=0 EndX=-4.03109 EndY=-10.5 EndZ=0
    g38: LineSegment StartX=-4.03109 StartY=-10.5 StartZ=0 EndX=-1 EndY=-8.75 EndZ=0
    g39: LineSegment StartX=-1 StartY=-8.75 StartZ=0 EndX=-1 EndY=-5.25 EndZ=0
    g40: LineSegment StartX=-1 StartY=-5.25 StartZ=0 EndX=-4.03109 EndY=-3.5 EndZ=0
    g41: Circle [constr] CenterX=-4.03109 CenterY=-7 CenterZ=0 NormalX=0 NormalY=0 NormalZ=1 AngleXU=0 Radius=3.5
    g42: LineSegment StartX=4.03109 StartY=-3.5 StartZ=0 EndX=1 EndY=-5.25 EndZ=0
    g43: LineSegment StartX=1 StartY=-5.25 StartZ=0 EndX=1 EndY=-8.75 EndZ=0
    g44: LineSegment StartX=1 StartY=-8.75 StartZ=0 EndX=4.03109 EndY=-10.5 EndZ=0
    g45: LineSegment StartX=4.03109 StartY=-10.5 StartZ=0 EndX=7.06218 EndY=-8.75 EndZ=0
    g46: LineSegment StartX=7.06218 StartY=-8.75 StartZ=0 EndX=7.06218 EndY=-5.25 EndZ=0
    g47: LineSegment StartX=7.06218 StartY=-5.25 StartZ=0 EndX=4.03109 EndY=-3.5 EndZ=0
    g48: Circle [constr] CenterX=4.03109 CenterY=-7 CenterZ=0 NormalX=0 NormalY=0 NormalZ=1 AngleXU=0 Radius=3.5
  constraints (117):
    c: Coincident(g0,g1)
    c: Coincident(g1,g2)
    c: Coincident(g2,g3)
    c: Coincident(g3,g4)
    c: Coincident(g4,g5)
    c: Coincident(g5,g0)
    c: Equal(g0, g1-g5) x5
    c: PointOnObject(g0,g6)
    c: PointOnObject(g1,g6)
    c: PointOnObject(g2,g6)
    c: PointOnObject(g3,g6)
    c: PointOnObject(g4,g6)
    c: PointOnObject(g5,g6)
    c: Coincident(g6,g-1)
    c: Diameter(g6) = 7
    c: PointOnObject(g0,g-2)
    c: Coincident(g7,g8)
    c: Coincident(g8,g9)
    c: Coincident(g9,g10)
    c: Coincident(g10,g11)
    c: Coincident(g11,g12)
    c: Coincident(g12,g7)
    c: Equal(g7, g8-g12) x5
    c: PointOnObject(g7,g13)
    c: PointOnObject(g8,g13)
    c: PointOnObject(g9,g13)
    c: PointOnObject(g10,g13)
    c: PointOnObject(g11,g13)
    c: PointOnObject(g12,g13)
    c: PointOnObject(g13,g-1)
    c: Diameter(g13) = 7
    c: Distance(g6,g13) = 8
    c: Horizontal(g0,g10)
    c: Coincident(g14,g15)
    c: Coincident(g15,g16)
    c: Coincident(g16,g17)
    c: Coincident(g17,g18)
    c: Coincident(g18,g19)
    c: Coincident(g19,g14)
    c: Equal(g14, g15-g19) x5
    c: PointOnObject(g14,g20)
    c: PointOnObject(g15,g20)
    c: PointOnObject(g16,g20)
    c: PointOnObject(g17,g20)
    c: PointOnObject(g18,g20)
    c: PointOnObject(g19,g20)
    c: Diameter(g20) = 7
    c: DistanceY(g-1,g20) = 7
    c: Vertical(g18)
    c: Distance(g17,g-2) = 1
    c: Coincident(g21,g22)
    c: Coincident(g22,g23)
    c: Coincident(g23,g24)
    c: Coincident(g24,g25)
    c: Coincident(g25,g26)
    c: Coincident(g26,g21)
    c: Equal(g21, g22-g26) x5
    c: PointOnObject(g21,g27)
    c: PointOnObject(g22,g27)
    c: PointOnObject(g23,g27)
    c: PointOnObject(g24,g27)
    c: PointOnObject(g25,g27)
    c: PointOnObject(g26,g27)
    c: Diameter(g27) = 7
    c: DistanceY(g-1,g27) = 7
    c: DistanceX(g21,g-1) = 1
    c: Vertical(g21)
    c: Coincident(g28,g29)
    c: Coincident(g29,g30)
    c: Coincident(g30,g31)
    c: Coincident(g31,g32)
    c: Coincident(g32,g33)
    c: Coincident(g33,g28)
    c: Equal(g28, g29-g33) x5
    c: PointOnObject(g28,g34)
    c: PointOnObject(g29,g34)
    c: PointOnObject(g30,g34)
    c: PointOnObject(g31,g34)
    c: PointOnObject(g32,g34)
    c: PointOnObject(g33,g34)
    c: PointOnObject(g34,g-1)
    c: Diameter(g34) = 7
    c: Vertical(g31)
    c: DistanceX(g34,g-1) = 8
    c: Coincident(g35,g36)
    c: Coincident(g36,g37)
    c: Coincident(g37,g38)
    c: Coincident(g38,g39)
    c: Coincident(g39,g40)
    c: Coincident(g40,g35)
    c: Equal(g35, g36-g40) x5
    c: PointOnObject(g35,g41)
    c: PointOnObject(g36,g41)
    c: PointOnObject(g37,g41)
    c: PointOnObject(g38,g41)
    c: PointOnObject(g39,g41)
    c: PointOnObject(g40,g41)
    c: Coincident(g42,g43)
    c: Coincident(g43,g44)
    c: Coincident(g44,g45)
    c: Coincident(g45,g46)
    c: Coincident(g46,g47)
    c: Coincident(g47,g42)
    c: Equal(g42, g43-g47) x5
    c: PointOnObject(g42,g48)
    c: PointOnObject(g43,g48)
    c: PointOnObject(g44,g48)
    c: PointOnObject(g45,g48)
    c: PointOnObject(g46,g48)
    c: PointOnObject(g47,g48)
    c: Equal(g41,g48)
    c: Diameter(g41) = 7
    c: Vertical(g39)
    c: Vertical(g43)
    c: Distance(g-2,g39) = 1
    c: Symmetric(g38,g43,g-2)
    c: Distance(g41,g-1) = 7
FEATURE [Part::Extrusion] Extrude438  label="hex053"
  Base = -> Sketch446
  Dir = (0,-1,2e-16)
  DirMode = 2
  FaceMakerClass = Part::FaceMakerBullseye
  FaceMakerMode = 3
  LengthFwd = 10
  LengthRev = 0
  Placement = pos=(16,0,14) rot=(0,0,1;0rad)
  Solid = true
  Symmetric = false
FEATURE [Sketcher::SketchObject] Sketch447
  ArcFitTolerance = 1e-06
  FullyConstrained = true
  MakeInternals = false
  Placement = pos=(0,0,0) rot=(1,0,0;1.5708rad)
  sketch-geometry (49):
    g0: LineSegment StartX=1e-16 StartY=3.5 StartZ=0 EndX=-3.03109 EndY=1.75 EndZ=0
    g1: LineSegment StartX=-3.03109 StartY=1.75 StartZ=0 EndX=-3.03109 EndY=-1.75 EndZ=0
    g2: LineSegment StartX=-3.03109 StartY=-1.75 StartZ=0 EndX=-1e-16 EndY=-3.5 EndZ=0
    g3: LineSegment StartX=-1e-16 StartY=-3.5 StartZ=0 EndX=3.03109 EndY=-1.75 EndZ=0
    g4: LineSegment StartX=3.03109 StartY=-1.75 StartZ=0 EndX=3.03109 EndY=1.75 EndZ=0
    g5: LineSegment StartX=3.03109 StartY=1.75 StartZ=0 EndX=1e-16 EndY=3.5 EndZ=0
    g6: Circle [constr] CenterX=0 CenterY=0 CenterZ=0 NormalX=0 NormalY=0 NormalZ=1 AngleXU=0 Radius=3.5
    g7: LineSegment StartX=4.96892 StartY=-1.75002 StartZ=0 EndX=8.00002 EndY=-3.5 EndZ=0
    g8: LineSegment StartX=8.00002 StartY=-3.5 StartZ=0 EndX=11.0311 EndY=-1.74998 EndZ=0
    g9: LineSegment StartX=11.0311 StartY=-1.74998 StartZ=0 EndX=11.0311 EndY=1.75002 EndZ=0
    g10: LineSegment StartX=11.0311 StartY=1.75002 StartZ=0 EndX=7.99998 EndY=3.5 EndZ=0
    g11: LineSegment StartX=7.99998 StartY=3.5 StartZ=0 EndX=4.9689 EndY=1.74998 EndZ=0
    g12: LineSegment StartX=4.9689 StartY=1.74998 StartZ=0 EndX=4.96892 EndY=-1.75002 EndZ=0
    g13: Circle [constr] CenterX=8 CenterY=0 CenterZ=0 NormalX=0 NormalY=0 NormalZ=1 AngleXU=0 Radius=3.5
    g14: LineSegment StartX=4.03109 StartY=3.5 StartZ=0 EndX=7.06218 EndY=5.25 EndZ=0
    g15: LineSegment StartX=7.06218 StartY=5.25 StartZ=0 EndX=7.06218 EndY=8.75 EndZ=0
    g16: LineSegment StartX=7.06218 StartY=8.75 StartZ=0 EndX=4.03109 EndY=10.5 EndZ=0
    g17: LineSegment StartX=4.03109 StartY=10.5 StartZ=0 EndX=1 EndY=8.75 EndZ=0
    g18: LineSegment StartX=1 StartY=8.75 StartZ=0 EndX=1 EndY=5.25 EndZ=0
    g19: LineSegment StartX=1 StartY=5.25 StartZ=0 EndX=4.03109 EndY=3.5 EndZ=0
    g20: Circle [constr] CenterX=4.03109 CenterY=7 CenterZ=0 NormalX=0 NormalY=0 NormalZ=1 AngleXU=0 Radius=3.5
    g21: LineSegment StartX=-1 StartY=5.25 StartZ=0 EndX=-1 EndY=8.75 EndZ=0
    g22: LineSegment StartX=-1 StartY=8.75 StartZ=0 EndX=-4.03109 EndY=10.5 EndZ=0
    g23: LineSegment StartX=-4.03109 StartY=10.5 StartZ=0 EndX=-7.06218 EndY=8.75 EndZ=0
    g24: LineSegment StartX=-7.06218 StartY=8.75 StartZ=0 EndX=-7.06218 EndY=5.25 EndZ=0
    g25: LineSegment StartX=-7.06218 StartY=5.25 StartZ=0 EndX=-4.03109 EndY=3.5 EndZ=0
    g26: LineSegment StartX=-4.03109 StartY=3.5 StartZ=0 EndX=-1 EndY=5.25 EndZ=0
    g27: Circle [constr] CenterX=-4.03109 CenterY=7 CenterZ=0 NormalX=0 NormalY=0 NormalZ=1 AngleXU=0 Radius=3.5
    g28: LineSegment StartX=-4.96891 StartY=-1.75 StartZ=0 EndX=-4.96891 EndY=1.75 EndZ=0
    g29: LineSegment StartX=-4.96891 StartY=1.75 StartZ=0 EndX=-8 EndY=3.5 EndZ=0
    g30: LineSegment StartX=-8 StartY=3.5 StartZ=0 EndX=-11.0311 EndY=1.75 EndZ=0
    g31: LineSegment StartX=-11.0311 StartY=1.75 StartZ=0 EndX=-11.0311 EndY=-1.75 EndZ=0
    g32: LineSegment StartX=-11.0311 StartY=-1.75 StartZ=0 EndX=-8 EndY=-3.5 EndZ=0
    g33: LineSegment StartX=-8 StartY=-3.5 StartZ=0 EndX=-4.96891 EndY=-1.75 EndZ=0
    g34: Circle [constr] CenterX=-8 CenterY=0 CenterZ=0 NormalX=0 NormalY=0 NormalZ=1 AngleXU=0 Radius=3.5
    g35: LineSegment StartX=-4.03109 StartY=-3.5 StartZ=0 EndX=-7.06218 EndY=-5.25 EndZ=0
    g36: LineSegment StartX=-7.06218 StartY=-5.25 StartZ=0 EndX=-7.06218 EndY=-8.75 EndZ=0
    g37: LineSegment StartX=-7.06218 StartY=-8.75 StartZ=0 EndX=-4.03109 EndY=-10.5 EndZ=0
    g38: LineSegment StartX=-4.03109 StartY=-10.5 StartZ=0 EndX=-1 EndY=-8.75 EndZ=0
    g39: LineSegment StartX=-1 StartY=-8.75 StartZ=0 EndX=-1 EndY=-5.25 EndZ=0
    g40: LineSegment StartX=-1 StartY=-5.25 StartZ=0 EndX=-4.03109 EndY=-3.5 EndZ=0
    g41: Circle [constr] CenterX=-4.03109 CenterY=-7 CenterZ=0 NormalX=0 NormalY=0 NormalZ=1 AngleXU=0 Radius=3.5
    g42: LineSegment StartX=4.03109 StartY=-3.5 StartZ=0 EndX=1 EndY=-5.25 EndZ=0
    g43: LineSegment StartX=1 StartY=-5.25 StartZ=0 EndX=1 EndY=-8.75 EndZ=0
    g44: LineSegment StartX=1 StartY=-8.75 StartZ=0 EndX=4.03109 EndY=-10.5 EndZ=0
    g45: LineSegment StartX=4.03109 StartY=-10.5 StartZ=0 EndX=7.06218 EndY=-8.75 EndZ=0
    g46: LineSegment StartX=7.06218 StartY=-8.75 StartZ=0 EndX=7.06218 EndY=-5.25 EndZ=0
    g47: LineSegment StartX=7.06218 StartY=-5.25 StartZ=0 EndX=4.03109 EndY=-3.5 EndZ=0
    g48: Circle [constr] CenterX=4.03109 CenterY=-7 CenterZ=0 NormalX=0 NormalY=0 NormalZ=1 AngleXU=0 Radius=3.5
  constraints (117):
    c: Coincident(g0,g1)
    c: Coincident(g1,g2)
    c: Coincident(g2,g3)
    c: Coincident(g3,g4)
    c: Coincident(g4,g5)
    c: Coincident(g5,g0)
    c: Equal(g0, g1-g5) x5
    c: PointOnObject(g0,g6)
    c: PointOnObject(g1,g6)
    c: PointOnObject(g2,g6)
    c: PointOnObject(g3,g6)
    c: PointOnObject(g4,g6)
    c: PointOnObject(g5,g6)
    c: Coincident(g6,g-1)
    c: Diameter(g6) = 7
    c: PointOnObject(g0,g-2)
    c: Coincident(g7,g8)
    c: Coincident(g8,g9)
    c: Coincident(g9,g10)
    c: Coincident(g10,g11)
    c: Coincident(g11,g12)
    c: Coincident(g12,g7)
    c: Equal(g7, g8-g12) x5
    c: PointOnObject(g7,g13)
    c: PointOnObject(g8,g13)
    c: PointOnObject(g9,g13)
    c: PointOnObject(g10,g13)
    c: PointOnObject(g11,g13)
    c: PointOnObject(g12,g13)
    c: PointOnObject(g13,g-1)
    c: Diameter(g13) = 7
    c: Distance(g6,g13) = 8
    c: Horizontal(g0,g10)
    c: Coincident(g14,g15)
    c: Coincident(g15,g16)
    c: Coincident(g16,g17)
    c: Coincident(g17,g18)
    c: Coincident(g18,g19)
    c: Coincident(g19,g14)
    c: Equal(g14, g15-g19) x5
    c: PointOnObject(g14,g20)
    c: PointOnObject(g15,g20)
    c: PointOnObject(g16,g20)
    c: PointOnObject(g17,g20)
    c: PointOnObject(g18,g20)
    c: PointOnObject(g19,g20)
    c: Diameter(g20) = 7
    c: DistanceY(g-1,g20) = 7
    c: Vertical(g18)
    c: Distance(g17,g-2) = 1
    c: Coincident(g21,g22)
    c: Coincident(g22,g23)
    c: Coincident(g23,g24)
    c: Coincident(g24,g25)
    c: Coincident(g25,g26)
    c: Coincident(g26,g21)
    c: Equal(g21, g22-g26) x5
    c: PointOnObject(g21,g27)
    c: PointOnObject(g22,g27)
    c: PointOnObject(g23,g27)
    c: PointOnObject(g24,g27)
    c: PointOnObject(g25,g27)
    c: PointOnObject(g26,g27)
    c: Diameter(g27) = 7
    c: DistanceY(g-1,g27) = 7
    c: DistanceX(g21,g-1) = 1
    c: Vertical(g21)
    c: Coincident(g28,g29)
    c: Coincident(g29,g30)
    c: Coincident(g30,g31)
    c: Coincident(g31,g32)
    c: Coincident(g32,g33)
    c: Coincident(g33,g28)
    c: Equal(g28, g29-g33) x5
    c: PointOnObject(g28,g34)
    c: PointOnObject(g29,g34)
    c: PointOnObject(g30,g34)
    c: PointOnObject(g31,g34)
    c: PointOnObject(g32,g34)
    c: PointOnObject(g33,g34)
    c: PointOnObject(g34,g-1)
    c: Diameter(g34) = 7
    c: Vertical(g31)
    c: DistanceX(g34,g-1) = 8
    c: Coincident(g35,g36)
    c: Coincident(g36,g37)
    c: Coincident(g37,g38)
    c: Coincident(g38,g39)
    c: Coincident(g39,g40)
    c: Coincident(g40,g35)
    c: Equal(g35, g36-g40) x5
    c: PointOnObject(g35,g41)
    c: PointOnObject(g36,g41)
    c: PointOnObject(g37,g41)
    c: PointOnObject(g38,g41)
    c: PointOnObject(g39,g41)
    c: PointOnObject(g40,g41)
    c: Coincident(g42,g43)
    c: Coincident(g43,g44)
    c: Coincident(g44,g45)
    c: Coincident(g45,g46)
    c: Coincident(g46,g47)
    c: Coincident(g47,g42)
    c: Equal(g42, g43-g47) x5
    c: PointOnObject(g42,g48)
    c: PointOnObject(g43,g48)
    c: PointOnObject(g44,g48)
    c: PointOnObject(g45,g48)
    c: PointOnObject(g46,g48)
    c: PointOnObject(g47,g48)
    c: Equal(g41,g48)
    c: Diameter(g41) = 7
    c: Vertical(g39)
    c: Vertical(g43)
    c: Distance(g-2,g39) = 1
    c: Symmetric(g38,g43,g-2)
    c: Distance(g41,g-1) = 7
FEATURE [Part::Extrusion] Extrude439  label="hex054"
  Base = -> Sketch447
  Dir = (0,-1,2e-16)
  DirMode = 2
  FaceMakerClass = Part::FaceMakerBullseye
  FaceMakerMode = 3
  LengthFwd = 10
  LengthRev = 0
  Placement = pos=(-20,0,-7) rot=(0,0,1;0rad)
  Solid = true
  Symmetric = false
FEATURE [Sketcher::SketchObject] Sketch448
  ArcFitTolerance = 1e-06
  FullyConstrained = true
  MakeInternals = false
  Placement = pos=(0,0,0) rot=(1,0,0;1.5708rad)
  sketch-geometry (49):
    g0: LineSegment StartX=1e-16 StartY=3.5 StartZ=0 EndX=-3.03109 EndY=1.75 EndZ=0
    g1: LineSegment StartX=-3.03109 StartY=1.75 StartZ=0 EndX=-3.03109 EndY=-1.75 EndZ=0
    g2: LineSegment StartX=-3.03109 StartY=-1.75 StartZ=0 EndX=-1e-16 EndY=-3.5 EndZ=0
    g3: LineSegment StartX=-1e-16 StartY=-3.5 StartZ=0 EndX=3.03109 EndY=-1.75 EndZ=0
    g4: LineSegment StartX=3.03109 StartY=-1.75 StartZ=0 EndX=3.03109 EndY=1.75 EndZ=0
    g5: LineSegment StartX=3.03109 StartY=1.75 StartZ=0 EndX=1e-16 EndY=3.5 EndZ=0
    g6: Circle [constr] CenterX=0 CenterY=0 CenterZ=0 NormalX=0 NormalY=0 NormalZ=1 AngleXU=0 Radius=3.5
    g7: LineSegment StartX=4.96892 StartY=-1.75002 StartZ=0 EndX=8.00002 EndY=-3.5 EndZ=0
    g8: LineSegment StartX=8.00002 StartY=-3.5 StartZ=0 EndX=11.0311 EndY=-1.74998 EndZ=0
    g9: LineSegment StartX=11.0311 StartY=-1.74998 StartZ=0 EndX=11.0311 EndY=1.75002 EndZ=0
    g10: LineSegment StartX=11.0311 StartY=1.75002 StartZ=0 EndX=7.99998 EndY=3.5 EndZ=0
    g11: LineSegment StartX=7.99998 StartY=3.5 StartZ=0 EndX=4.9689 EndY=1.74998 EndZ=0
    g12: LineSegment StartX=4.9689 StartY=1.74998 StartZ=0 EndX=4.96892 EndY=-1.75002 EndZ=0
    g13: Circle [constr] CenterX=8 CenterY=0 CenterZ=0 NormalX=0 NormalY=0 NormalZ=1 AngleXU=0 Radius=3.5
    g14: LineSegment StartX=4.03109 StartY=3.5 StartZ=0 EndX=7.06218 EndY=5.25 EndZ=0
    g15: LineSegment StartX=7.06218 StartY=5.25 StartZ=0 EndX=7.06218 EndY=8.75 EndZ=0
    g16: LineSegment StartX=7.06218 StartY=8.75 StartZ=0 EndX=4.03109 EndY=10.5 EndZ=0
    g17: LineSegment StartX=4.03109 StartY=10.5 StartZ=0 EndX=1 EndY=8.75 EndZ=0
    g18: LineSegment StartX=1 StartY=8.75 StartZ=0 EndX=1 EndY=5.25 EndZ=0
    g19: LineSegment StartX=1 StartY=5.25 StartZ=0 EndX=4.03109 EndY=3.5 EndZ=0
    g20: Circle [constr] CenterX=4.03109 CenterY=7 CenterZ=0 NormalX=0 NormalY=0 NormalZ=1 AngleXU=0 Radius=3.5
    g21: LineSegment StartX=-1 StartY=5.25 StartZ=0 EndX=-1 EndY=8.75 EndZ=0
    g22: LineSegment StartX=-1 StartY=8.75 StartZ=0 EndX=-4.03109 EndY=10.5 EndZ=0
    g23: LineSegment StartX=-4.03109 StartY=10.5 StartZ=0 EndX=-7.06218 EndY=8.75 EndZ=0
    g24: LineSegment StartX=-7.06218 StartY=8.75 StartZ=0 EndX=-7.06218 EndY=5.25 EndZ=0
    g25: LineSegment StartX=-7.06218 StartY=5.25 StartZ=0 EndX=-4.03109 EndY=3.5 EndZ=0
    g26: LineSegment StartX=-4.03109 StartY=3.5 StartZ=0 EndX=-1 EndY=5.25 EndZ=0
    g27: Circle [constr] CenterX=-4.03109 CenterY=7 CenterZ=0 NormalX=0 NormalY=0 NormalZ=1 AngleXU=0 Radius=3.5
    g28: LineSegment StartX=-4.96891 StartY=-1.75 StartZ=0 EndX=-4.96891 EndY=1.75 EndZ=0
    g29: LineSegment StartX=-4.96891 StartY=1.75 StartZ=0 EndX=-8 EndY=3.5 EndZ=0
    g30: LineSegment StartX=-8 StartY=3.5 StartZ=0 EndX=-11.0311 EndY=1.75 EndZ=0
    g31: LineSegment StartX=-11.0311 StartY=1.75 StartZ=0 EndX=-11.0311 EndY=-1.75 EndZ=0
    g32: LineSegment StartX=-11.0311 StartY=-1.75 StartZ=0 EndX=-8 EndY=-3.5 EndZ=0
    g33: LineSegment StartX=-8 StartY=-3.5 StartZ=0 EndX=-4.96891 EndY=-1.75 EndZ=0
    g34: Circle [constr] CenterX=-8 CenterY=0 CenterZ=0 NormalX=0 NormalY=0 NormalZ=1 AngleXU=0 Radius=3.5
    g35: LineSegment StartX=-4.03109 StartY=-3.5 StartZ=0 EndX=-7.06218 EndY=-5.25 EndZ=0
    g36: LineSegment StartX=-7.06218 StartY=-5.25 StartZ=0 EndX=-7.06218 EndY=-8.75 EndZ=0
    g37: LineSegment StartX=-7.06218 StartY=-8.75 StartZ=0 EndX=-4.03109 EndY=-10.5 EndZ=0
    g38: LineSegment StartX=-4.03109 StartY=-10.5 StartZ=0 EndX=-1 EndY=-8.75 EndZ=0
    g39: LineSegment StartX=-1 StartY=-8.75 StartZ=0 EndX=-1 EndY=-5.25 EndZ=0
    g40: LineSegment StartX=-1 StartY=-5.25 StartZ=0 EndX=-4.03109 EndY=-3.5 EndZ=0
    g41: Circle [constr] CenterX=-4.03109 CenterY=-7 CenterZ=0 NormalX=0 NormalY=0 NormalZ=1 AngleXU=0 Radius=3.5
    g42: LineSegment StartX=4.03109 StartY=-3.5 StartZ=0 EndX=1 EndY=-5.25 EndZ=0
    g43: LineSegment StartX=1 StartY=-5.25 StartZ=0 EndX=1 EndY=-8.75 EndZ=0
    g44: LineSegment StartX=1 StartY=-8.75 StartZ=0 EndX=4.03109 EndY=-10.5 EndZ=0
    g45: LineSegment StartX=4.03109 StartY=-10.5 StartZ=0 EndX=7.06218 EndY=-8.75 EndZ=0
    g46: LineSegment StartX=7.06218 StartY=-8.75 StartZ=0 EndX=7.06218 EndY=-5.25 EndZ=0
    g47: LineSegment StartX=7.06218 StartY=-5.25 StartZ=0 EndX=4.03109 EndY=-3.5 EndZ=0
    g48: Circle [constr] CenterX=4.03109 CenterY=-7 CenterZ=0 NormalX=0 NormalY=0 NormalZ=1 AngleXU=0 Radius=3.5
  constraints (117):
    c: Coincident(g0,g1)
    c: Coincident(g1,g2)
    c: Coincident(g2,g3)
    c: Coincident(g3,g4)
    c: Coincident(g4,g5)
    c: Coincident(g5,g0)
    c: Equal(g0, g1-g5) x5
    c: PointOnObject(g0,g6)
    c: PointOnObject(g1,g6)
    c: PointOnObject(g2,g6)
    c: PointOnObject(g3,g6)
    c: PointOnObject(g4,g6)
    c: PointOnObject(g5,g6)
    c: Coincident(g6,g-1)
    c: Diameter(g6) = 7
    c: PointOnObject(g0,g-2)
    c: Coincident(g7,g8)
    c: Coincident(g8,g9)
    c: Coincident(g9,g10)
    c: Coincident(g10,g11)
    c: Coincident(g11,g12)
    c: Coincident(g12,g7)
    c: Equal(g7, g8-g12) x5
    c: PointOnObject(g7,g13)
    c: PointOnObject(g8,g13)
    c: PointOnObject(g9,g13)
    c: PointOnObject(g10,g13)
    c: PointOnObject(g11,g13)
    c: PointOnObject(g12,g13)
    c: PointOnObject(g13,g-1)
    c: Diameter(g13) = 7
    c: Distance(g6,g13) = 8
    c: Horizontal(g0,g10)
    c: Coincident(g14,g15)
    c: Coincident(g15,g16)
    c: Coincident(g16,g17)
    c: Coincident(g17,g18)
    c: Coincident(g18,g19)
    c: Coincident(g19,g14)
    c: Equal(g14, g15-g19) x5
    c: PointOnObject(g14,g20)
    c: PointOnObject(g15,g20)
    c: PointOnObject(g16,g20)
    c: PointOnObject(g17,g20)
    c: PointOnObject(g18,g20)
    c: PointOnObject(g19,g20)
    c: Diameter(g20) = 7
    c: DistanceY(g-1,g20) = 7
    c: Vertical(g18)
    c: Distance(g17,g-2) = 1
    c: Coincident(g21,g22)
    c: Coincident(g22,g23)
    c: Coincident(g23,g24)
    c: Coincident(g24,g25)
    c: Coincident(g25,g26)
    c: Coincident(g26,g21)
    c: Equal(g21, g22-g26) x5
    c: PointOnObject(g21,g27)
    c: PointOnObject(g22,g27)
    c: PointOnObject(g23,g27)
    c: PointOnObject(g24,g27)
    c: PointOnObject(g25,g27)
    c: PointOnObject(g26,g27)
    c: Diameter(g27) = 7
    c: DistanceY(g-1,g27) = 7
    c: DistanceX(g21,g-1) = 1
    c: Vertical(g21)
    c: Coincident(g28,g29)
    c: Coincident(g29,g30)
    c: Coincident(g30,g31)
    c: Coincident(g31,g32)
    c: Coincident(g32,g33)
    c: Coincident(g33,g28)
    c: Equal(g28, g29-g33) x5
    c: PointOnObject(g28,g34)
    c: PointOnObject(g29,g34)
    c: PointOnObject(g30,g34)
    c: PointOnObject(g31,g34)
    c: PointOnObject(g32,g34)
    c: PointOnObject(g33,g34)
    c: PointOnObject(g34,g-1)
    c: Diameter(g34) = 7
    c: Vertical(g31)
    c: DistanceX(g34,g-1) = 8
    c: Coincident(g35,g36)
    c: Coincident(g36,g37)
    c: Coincident(g37,g38)
    c: Coincident(g38,g39)
    c: Coincident(g39,g40)
    c: Coincident(g40,g35)
    c: Equal(g35, g36-g40) x5
    c: PointOnObject(g35,g41)
    c: PointOnObject(g36,g41)
    c: PointOnObject(g37,g41)
    c: PointOnObject(g38,g41)
    c: PointOnObject(g39,g41)
    c: PointOnObject(g40,g41)
    c: Coincident(g42,g43)
    c: Coincident(g43,g44)
    c: Coincident(g44,g45)
    c: Coincident(g45,g46)
    c: Coincident(g46,g47)
    c: Coincident(g47,g42)
    c: Equal(g42, g43-g47) x5
    c: PointOnObject(g42,g48)
    c: PointOnObject(g43,g48)
    c: PointOnObject(g44,g48)
    c: PointOnObject(g45,g48)
    c: PointOnObject(g46,g48)
    c: PointOnObject(g47,g48)
    c: Equal(g41,g48)
    c: Diameter(g41) = 7
    c: Vertical(g39)
    c: Vertical(g43)
    c: Distance(g-2,g39) = 1
    c: Symmetric(g38,g43,g-2)
    c: Distance(g41,g-1) = 7
FEATURE [Part::Extrusion] Extrude440  label="hex055"
  Base = -> Sketch448
  Dir = (0,-1,2e-16)
  DirMode = 2
  FaceMakerClass = Part::FaceMakerBullseye
  FaceMakerMode = 3
  LengthFwd = 10
  LengthRev = 0
  Placement = pos=(-16,0,14) rot=(0,0,1;0rad)
  Solid = true
  Symmetric = false
FEATURE [Sketcher::SketchObject] Sketch449
  ArcFitTolerance = 1e-06
  FullyConstrained = true
  MakeInternals = false
  Placement = pos=(0,0,0) rot=(1,0,0;1.5708rad)
  sketch-geometry (49):
    g0: LineSegment StartX=1e-16 StartY=3.5 StartZ=0 EndX=-3.03109 EndY=1.75 EndZ=0
    g1: LineSegment StartX=-3.03109 StartY=1.75 StartZ=0 EndX=-3.03109 EndY=-1.75 EndZ=0
    g2: LineSegment StartX=-3.03109 StartY=-1.75 StartZ=0 EndX=-1e-16 EndY=-3.5 EndZ=0
    g3: LineSegment StartX=-1e-16 StartY=-3.5 StartZ=0 EndX=3.03109 EndY=-1.75 EndZ=0
    g4: LineSegment StartX=3.03109 StartY=-1.75 StartZ=0 EndX=3.03109 EndY=1.75 EndZ=0
    g5: LineSegment StartX=3.03109 StartY=1.75 StartZ=0 EndX=1e-16 EndY=3.5 EndZ=0
    g6: Circle [constr] CenterX=0 CenterY=0 CenterZ=0 NormalX=0 NormalY=0 NormalZ=1 AngleXU=0 Radius=3.5
    g7: LineSegment StartX=4.96892 StartY=-1.75002 StartZ=0 EndX=8.00002 EndY=-3.5 EndZ=0
    g8: LineSegment StartX=8.00002 StartY=-3.5 StartZ=0 EndX=11.0311 EndY=-1.74998 EndZ=0
    g9: LineSegment StartX=11.0311 StartY=-1.74998 StartZ=0 EndX=11.0311 EndY=1.75002 EndZ=0
    g10: LineSegment StartX=11.0311 StartY=1.75002 StartZ=0 EndX=7.99998 EndY=3.5 EndZ=0
    g11: LineSegment StartX=7.99998 StartY=3.5 StartZ=0 EndX=4.9689 EndY=1.74998 EndZ=0
    g12: LineSegment StartX=4.9689 StartY=1.74998 StartZ=0 EndX=4.96892 EndY=-1.75002 EndZ=0
    g13: Circle [constr] CenterX=8 CenterY=0 CenterZ=0 NormalX=0 NormalY=0 NormalZ=1 AngleXU=0 Radius=3.5
    g14: LineSegment StartX=4.03109 StartY=3.5 StartZ=0 EndX=7.06218 EndY=5.25 EndZ=0
    g15: LineSegment StartX=7.06218 StartY=5.25 StartZ=0 EndX=7.06218 EndY=8.75 EndZ=0
    g16: LineSegment StartX=7.06218 StartY=8.75 StartZ=0 EndX=4.03109 EndY=10.5 EndZ=0
    g17: LineSegment StartX=4.03109 StartY=10.5 StartZ=0 EndX=1 EndY=8.75 EndZ=0
    g18: LineSegment StartX=1 StartY=8.75 StartZ=0 EndX=1 EndY=5.25 EndZ=0
    g19: LineSegment StartX=1 StartY=5.25 StartZ=0 EndX=4.03109 EndY=3.5 EndZ=0
    g20: Circle [constr] CenterX=4.03109 CenterY=7 CenterZ=0 NormalX=0 NormalY=0 NormalZ=1 AngleXU=0 Radius=3.5
    g21: LineSegment StartX=-1 StartY=5.25 StartZ=0 EndX=-1 EndY=8.75 EndZ=0
    g22: LineSegment StartX=-1 StartY=8.75 StartZ=0 EndX=-4.03109 EndY=10.5 EndZ=0
    g23: LineSegment StartX=-4.03109 StartY=10.5 StartZ=0 EndX=-7.06218 EndY=8.75 EndZ=0
    g24: LineSegment StartX=-7.06218 StartY=8.75 StartZ=0 EndX=-7.06218 EndY=5.25 EndZ=0
    g25: LineSegment StartX=-7.06218 StartY=5.25 StartZ=0 EndX=-4.03109 EndY=3.5 EndZ=0
    g26: LineSegment StartX=-4.03109 StartY=3.5 StartZ=0 EndX=-1 EndY=5.25 EndZ=0
    g27: Circle [constr] CenterX=-4.03109 CenterY=7 CenterZ=0 NormalX=0 NormalY=0 NormalZ=1 AngleXU=0 Radius=3.5
    g28: LineSegment StartX=-4.96891 StartY=-1.75 StartZ=0 EndX=-4.96891 EndY=1.75 EndZ=0
    g29: LineSegment StartX=-4.96891 StartY=1.75 StartZ=0 EndX=-8 EndY=3.5 EndZ=0
    g30: LineSegment StartX=-8 StartY=3.5 StartZ=0 EndX=-11.0311 EndY=1.75 EndZ=0
    g31: LineSegment StartX=-11.0311 StartY=1.75 StartZ=0 EndX=-11.0311 EndY=-1.75 EndZ=0
    g32: LineSegment StartX=-11.0311 StartY=-1.75 StartZ=0 EndX=-8 EndY=-3.5 EndZ=0
    g33: LineSegment StartX=-8 StartY=-3.5 StartZ=0 EndX=-4.96891 EndY=-1.75 EndZ=0
    g34: Circle [constr] CenterX=-8 CenterY=0 CenterZ=0 NormalX=0 NormalY=0 NormalZ=1 AngleXU=0 Radius=3.5
    g35: LineSegment StartX=-4.03109 StartY=-3.5 StartZ=0 EndX=-7.06218 EndY=-5.25 EndZ=0
    g36: LineSegment StartX=-7.06218 StartY=-5.25 StartZ=0 EndX=-7.06218 EndY=-8.75 EndZ=0
    g37: LineSegment StartX=-7.06218 StartY=-8.75 StartZ=0 EndX=-4.03109 EndY=-10.5 EndZ=0
    g38: LineSegment StartX=-4.03109 StartY=-10.5 StartZ=0 EndX=-1 EndY=-8.75 EndZ=0
    g39: LineSegment StartX=-1 StartY=-8.75 StartZ=0 EndX=-1 EndY=-5.25 EndZ=0
    g40: LineSegment StartX=-1 StartY=-5.25 StartZ=0 EndX=-4.03109 EndY=-3.5 EndZ=0
    g41: Circle [constr] CenterX=-4.03109 CenterY=-7 CenterZ=0 NormalX=0 NormalY=0 NormalZ=1 AngleXU=0 Radius=3.5
    g42: LineSegment StartX=4.03109 StartY=-3.5 StartZ=0 EndX=1 EndY=-5.25 EndZ=0
    g43: LineSegment StartX=1 StartY=-5.25 StartZ=0 EndX=1 EndY=-8.75 EndZ=0
    g44: LineSegment StartX=1 StartY=-8.75 StartZ=0 EndX=4.03109 EndY=-10.5 EndZ=0
    g45: LineSegment StartX=4.03109 StartY=-10.5 StartZ=0 EndX=7.06218 EndY=-8.75 EndZ=0
    g46: LineSegment StartX=7.06218 StartY=-8.75 StartZ=0 EndX=7.06218 EndY=-5.25 EndZ=0
    g47: LineSegment StartX=7.06218 StartY=-5.25 StartZ=0 EndX=4.03109 EndY=-3.5 EndZ=0
    g48: Circle [constr] CenterX=4.03109 CenterY=-7 CenterZ=0 NormalX=0 NormalY=0 NormalZ=1 AngleXU=0 Radius=3.5
  constraints (117):
    c: Coincident(g0,g1)
    c: Coincident(g1,g2)
    c: Coincident(g2,g3)
    c: Coincident(g3,g4)
    c: Coincident(g4,g5)
    c: Coincident(g5,g0)
    c: Equal(g0, g1-g5) x5
    c: PointOnObject(g0,g6)
    c: PointOnObject(g1,g6)
    c: PointOnObject(g2,g6)
    c: PointOnObject(g3,g6)
    c: PointOnObject(g4,g6)
    c: PointOnObject(g5,g6)
    c: Coincident(g6,g-1)
    c: Diameter(g6) = 7
    c: PointOnObject(g0,g-2)
    c: Coincident(g7,g8)
    c: Coincident(g8,g9)
    c: Coincident(g9,g10)
    c: Coincident(g10,g11)
    c: Coincident(g11,g12)
    c: Coincident(g12,g7)
    c: Equal(g7, g8-g12) x5
    c: PointOnObject(g7,g13)
    c: PointOnObject(g8,g13)
    c: PointOnObject(g9,g13)
    c: PointOnObject(g10,g13)
    c: PointOnObject(g11,g13)
    c: PointOnObject(g12,g13)
    c: PointOnObject(g13,g-1)
    c: Diameter(g13) = 7
    c: Distance(g6,g13) = 8
    c: Horizontal(g0,g10)
    c: Coincident(g14,g15)
    c: Coincident(g15,g16)
    c: Coincident(g16,g17)
    c: Coincident(g17,g18)
    c: Coincident(g18,g19)
    c: Coincident(g19,g14)
    c: Equal(g14, g15-g19) x5
    c: PointOnObject(g14,g20)
    c: PointOnObject(g15,g20)
    c: PointOnObject(g16,g20)
    c: PointOnObject(g17,g20)
    c: PointOnObject(g18,g20)
    c: PointOnObject(g19,g20)
    c: Diameter(g20) = 7
    c: DistanceY(g-1,g20) = 7
    c: Vertical(g18)
    c: Distance(g17,g-2) = 1
    c: Coincident(g21,g22)
    c: Coincident(g22,g23)
    c: Coincident(g23,g24)
    c: Coincident(g24,g25)
    c: Coincident(g25,g26)
    c: Coincident(g26,g21)
    c: Equal(g21, g22-g26) x5
    c: PointOnObject(g21,g27)
    c: PointOnObject(g22,g27)
    c: PointOnObject(g23,g27)
    c: PointOnObject(g24,g27)
    c: PointOnObject(g25,g27)
    c: PointOnObject(g26,g27)
    c: Diameter(g27) = 7
    c: DistanceY(g-1,g27) = 7
    c: DistanceX(g21,g-1) = 1
    c: Vertical(g21)
    c: Coincident(g28,g29)
    c: Coincident(g29,g30)
    c: Coincident(g30,g31)
    c: Coincident(g31,g32)
    c: Coincident(g32,g33)
    c: Coincident(g33,g28)
    c: Equal(g28, g29-g33) x5
    c: PointOnObject(g28,g34)
    c: PointOnObject(g29,g34)
    c: PointOnObject(g30,g34)
    c: PointOnObject(g31,g34)
    c: PointOnObject(g32,g34)
    c: PointOnObject(g33,g34)
    c: PointOnObject(g34,g-1)
    c: Diameter(g34) = 7
    c: Vertical(g31)
    c: DistanceX(g34,g-1) = 8
    c: Coincident(g35,g36)
    c: Coincident(g36,g37)
    c: Coincident(g37,g38)
    c: Coincident(g38,g39)
    c: Coincident(g39,g40)
    c: Coincident(g40,g35)
    c: Equal(g35, g36-g40) x5
    c: PointOnObject(g35,g41)
    c: PointOnObject(g36,g41)
    c: PointOnObject(g37,g41)
    c: PointOnObject(g38,g41)
    c: PointOnObject(g39,g41)
    c: PointOnObject(g40,g41)
    c: Coincident(g42,g43)
    c: Coincident(g43,g44)
    c: Coincident(g44,g45)
    c: Coincident(g45,g46)
    c: Coincident(g46,g47)
    c: Coincident(g47,g42)
    c: Equal(g42, g43-g47) x5
    c: PointOnObject(g42,g48)
    c: PointOnObject(g43,g48)
    c: PointOnObject(g44,g48)
    c: PointOnObject(g45,g48)
    c: PointOnObject(g46,g48)
    c: PointOnObject(g47,g48)
    c: Equal(g41,g48)
    c: Diameter(g41) = 7
    c: Vertical(g39)
    c: Vertical(g43)
    c: Distance(g-2,g39) = 1
    c: Symmetric(g38,g43,g-2)
    c: Distance(g41,g-1) = 7
FEATURE [Part::Extrusion] Extrude441  label="hex056"
  Base = -> Sketch449
  Dir = (0,-1,2e-16)
  DirMode = 2
  FaceMakerClass = Part::FaceMakerBullseye
  FaceMakerMode = 3
  LengthFwd = 10
  LengthRev = 0
  Placement = pos=(-4,0,-21) rot=(0,0,1;0rad)
  Solid = true
  Symmetric = false
FEATURE [Sketcher::SketchObject] Sketch450
  ArcFitTolerance = 1e-06
  FullyConstrained = true
  MakeInternals = false
  Placement = pos=(0,0,0) rot=(1,0,0;1.5708rad)
  sketch-geometry (49):
    g0: LineSegment StartX=1e-16 StartY=3.5 StartZ=0 EndX=-3.03109 EndY=1.75 EndZ=0
    g1: LineSegment StartX=-3.03109 StartY=1.75 StartZ=0 EndX=-3.03109 EndY=-1.75 EndZ=0
    g2: LineSegment StartX=-3.03109 StartY=-1.75 StartZ=0 EndX=-1e-16 EndY=-3.5 EndZ=0
    g3: LineSegment StartX=-1e-16 StartY=-3.5 StartZ=0 EndX=3.03109 EndY=-1.75 EndZ=0
    g4: LineSegment StartX=3.03109 StartY=-1.75 StartZ=0 EndX=3.03109 EndY=1.75 EndZ=0
    g5: LineSegment StartX=3.03109 StartY=1.75 StartZ=0 EndX=1e-16 EndY=3.5 EndZ=0
    g6: Circle [constr] CenterX=0 CenterY=0 CenterZ=0 NormalX=0 NormalY=0 NormalZ=1 AngleXU=0 Radius=3.5
    g7: LineSegment StartX=4.96892 StartY=-1.75002 StartZ=0 EndX=8.00002 EndY=-3.5 EndZ=0
    g8: LineSegment StartX=8.00002 StartY=-3.5 StartZ=0 EndX=11.0311 EndY=-1.74998 EndZ=0
    g9: LineSegment StartX=11.0311 StartY=-1.74998 StartZ=0 EndX=11.0311 EndY=1.75002 EndZ=0
    g10: LineSegment StartX=11.0311 StartY=1.75002 StartZ=0 EndX=7.99998 EndY=3.5 EndZ=0
    g11: LineSegment StartX=7.99998 StartY=3.5 StartZ=0 EndX=4.9689 EndY=1.74998 EndZ=0
    g12: LineSegment StartX=4.9689 StartY=1.74998 StartZ=0 EndX=4.96892 EndY=-1.75002 EndZ=0
    g13: Circle [constr] CenterX=8 CenterY=0 CenterZ=0 NormalX=0 NormalY=0 NormalZ=1 AngleXU=0 Radius=3.5
    g14: LineSegment StartX=4.03109 StartY=3.5 StartZ=0 EndX=7.06218 EndY=5.25 EndZ=0
    g15: LineSegment StartX=7.06218 StartY=5.25 StartZ=0 EndX=7.06218 EndY=8.75 EndZ=0
    g16: LineSegment StartX=7.06218 StartY=8.75 StartZ=0 EndX=4.03109 EndY=10.5 EndZ=0
    g17: LineSegment StartX=4.03109 StartY=10.5 StartZ=0 EndX=1 EndY=8.75 EndZ=0
    g18: LineSegment StartX=1 StartY=8.75 StartZ=0 EndX=1 EndY=5.25 EndZ=0
    g19: LineSegment StartX=1 StartY=5.25 StartZ=0 EndX=4.03109 EndY=3.5 EndZ=0
    g20: Circle [constr] CenterX=4.03109 CenterY=7 CenterZ=0 NormalX=0 NormalY=0 NormalZ=1 AngleXU=0 Radius=3.5
    g21: LineSegment StartX=-1 StartY=5.25 StartZ=0 EndX=-1 EndY=8.75 EndZ=0
    g22: LineSegment StartX=-1 StartY=8.75 StartZ=0 EndX=-4.03109 EndY=10.5 EndZ=0
    g23: LineSegment StartX=-4.03109 StartY=10.5 StartZ=0 EndX=-7.06218 EndY=8.75 EndZ=0
    g24: LineSegment StartX=-7.06218 StartY=8.75 StartZ=0 EndX=-7.06218 EndY=5.25 EndZ=0
    g25: LineSegment StartX=-7.06218 StartY=5.25 StartZ=0 EndX=-4.03109 EndY=3.5 EndZ=0
    g26: LineSegment StartX=-4.03109 StartY=3.5 StartZ=0 EndX=-1 EndY=5.25 EndZ=0
    g27: Circle [constr] CenterX=-4.03109 CenterY=7 CenterZ=0 NormalX=0 NormalY=0 NormalZ=1 AngleXU=0 Radius=3.5
    g28: LineSegment StartX=-4.96891 StartY=-1.75 StartZ=0 EndX=-4.96891 EndY=1.75 EndZ=0
    g29: LineSegment StartX=-4.96891 StartY=1.75 StartZ=0 EndX=-8 EndY=3.5 EndZ=0
    g30: LineSegment StartX=-8 StartY=3.5 StartZ=0 EndX=-11.0311 EndY=1.75 EndZ=0
    g31: LineSegment StartX=-11.0311 StartY=1.75 StartZ=0 EndX=-11.0311 EndY=-1.75 EndZ=0
    g32: LineSegment StartX=-11.0311 StartY=-1.75 StartZ=0 EndX=-8 EndY=-3.5 EndZ=0
    g33: LineSegment StartX=-8 StartY=-3.5 StartZ=0 EndX=-4.96891 EndY=-1.75 EndZ=0
    g34: Circle [constr] CenterX=-8 CenterY=0 CenterZ=0 NormalX=0 NormalY=0 NormalZ=1 AngleXU=0 Radius=3.5
    g35: LineSegment StartX=-4.03109 StartY=-3.5 StartZ=0 EndX=-7.06218 EndY=-5.25 EndZ=0
    g36: LineSegment StartX=-7.06218 StartY=-5.25 StartZ=0 EndX=-7.06218 EndY=-8.75 EndZ=0
    g37: LineSegment StartX=-7.06218 StartY=-8.75 StartZ=0 EndX=-4.03109 EndY=-10.5 EndZ=0
    g38: LineSegment StartX=-4.03109 StartY=-10.5 StartZ=0 EndX=-1 EndY=-8.75 EndZ=0
    g39: LineSegment StartX=-1 StartY=-8.75 StartZ=0 EndX=-1 EndY=-5.25 EndZ=0
    g40: LineSegment StartX=-1 StartY=-5.25 StartZ=0 EndX=-4.03109 EndY=-3.5 EndZ=0
    g41: Circle [constr] CenterX=-4.03109 CenterY=-7 CenterZ=0 NormalX=0 NormalY=0 NormalZ=1 AngleXU=0 Radius=3.5
    g42: LineSegment StartX=4.03109 StartY=-3.5 StartZ=0 EndX=1 EndY=-5.25 EndZ=0
    g43: LineSegment StartX=1 StartY=-5.25 StartZ=0 EndX=1 EndY=-8.75 EndZ=0
    g44: LineSegment StartX=1 StartY=-8.75 StartZ=0 EndX=4.03109 EndY=-10.5 EndZ=0
    g45: LineSegment StartX=4.03109 StartY=-10.5 StartZ=0 EndX=7.06218 EndY=-8.75 EndZ=0
    g46: LineSegment StartX=7.06218 StartY=-8.75 StartZ=0 EndX=7.06218 EndY=-5.25 EndZ=0
    g47: LineSegment StartX=7.06218 StartY=-5.25 StartZ=0 EndX=4.03109 EndY=-3.5 EndZ=0
    g48: Circle [constr] CenterX=4.03109 CenterY=-7 CenterZ=0 NormalX=0 NormalY=0 NormalZ=1 AngleXU=0 Radius=3.5
  constraints (117):
    c: Coincident(g0,g1)
    c: Coincident(g1,g2)
    c: Coincident(g2,g3)
    c: Coincident(g3,g4)
    c: Coincident(g4,g5)
    c: Coincident(g5,g0)
    c: Equal(g0, g1-g5) x5
    c: PointOnObject(g0,g6)
    c: PointOnObject(g1,g6)
    c: PointOnObject(g2,g6)
    c: PointOnObject(g3,g6)
    c: PointOnObject(g4,g6)
    c: PointOnObject(g5,g6)
    c: Coincident(g6,g-1)
    c: Diameter(g6) = 7
    c: PointOnObject(g0,g-2)
    c: Coincident(g7,g8)
    c: Coincident(g8,g9)
    c: Coincident(g9,g10)
    c: Coincident(g10,g11)
    c: Coincident(g11,g12)
    c: Coincident(g12,g7)
    c: Equal(g7, g8-g12) x5
    c: PointOnObject(g7,g13)
    c: PointOnObject(g8,g13)
    c: PointOnObject(g9,g13)
    c: PointOnObject(g10,g13)
    c: PointOnObject(g11,g13)
    c: PointOnObject(g12,g13)
    c: PointOnObject(g13,g-1)
    c: Diameter(g13) = 7
    c: Distance(g6,g13) = 8
    c: Horizontal(g0,g10)
    c: Coincident(g14,g15)
    c: Coincident(g15,g16)
    c: Coincident(g16,g17)
    c: Coincident(g17,g18)
    c: Coincident(g18,g19)
    c: Coincident(g19,g14)
    c: Equal(g14, g15-g19) x5
    c: PointOnObject(g14,g20)
    c: PointOnObject(g15,g20)
    c: PointOnObject(g16,g20)
    c: PointOnObject(g17,g20)
    c: PointOnObject(g18,g20)
    c: PointOnObject(g19,g20)
    c: Diameter(g20) = 7
    c: DistanceY(g-1,g20) = 7
    c: Vertical(g18)
    c: Distance(g17,g-2) = 1
    c: Coincident(g21,g22)
    c: Coincident(g22,g23)
    c: Coincident(g23,g24)
    c: Coincident(g24,g25)
    c: Coincident(g25,g26)
    c: Coincident(g26,g21)
    c: Equal(g21, g22-g26) x5
    c: PointOnObject(g21,g27)
    c: PointOnObject(g22,g27)
    c: PointOnObject(g23,g27)
    c: PointOnObject(g24,g27)
    c: PointOnObject(g25,g27)
    c: PointOnObject(g26,g27)
    c: Diameter(g27) = 7
    c: DistanceY(g-1,g27) = 7
    c: DistanceX(g21,g-1) = 1
    c: Vertical(g21)
    c: Coincident(g28,g29)
    c: Coincident(g29,g30)
    c: Coincident(g30,g31)
    c: Coincident(g31,g32)
    c: Coincident(g32,g33)
    c: Coincident(g33,g28)
    c: Equal(g28, g29-g33) x5
    c: PointOnObject(g28,g34)
    c: PointOnObject(g29,g34)
    c: PointOnObject(g30,g34)
    c: PointOnObject(g31,g34)
    c: PointOnObject(g32,g34)
    c: PointOnObject(g33,g34)
    c: PointOnObject(g34,g-1)
    c: Diameter(g34) = 7
    c: Vertical(g31)
    c: DistanceX(g34,g-1) = 8
    c: Coincident(g35,g36)
    c: Coincident(g36,g37)
    c: Coincident(g37,g38)
    c: Coincident(g38,g39)
    c: Coincident(g39,g40)
    c: Coincident(g40,g35)
    c: Equal(g35, g36-g40) x5
    c: PointOnObject(g35,g41)
    c: PointOnObject(g36,g41)
    c: PointOnObject(g37,g41)
    c: PointOnObject(g38,g41)
    c: PointOnObject(g39,g41)
    c: PointOnObject(g40,g41)
    c: Coincident(g42,g43)
    c: Coincident(g43,g44)
    c: Coincident(g44,g45)
    c: Coincident(g45,g46)
    c: Coincident(g46,g47)
    c: Coincident(g47,g42)
    c: Equal(g42, g43-g47) x5
    c: PointOnObject(g42,g48)
    c: PointOnObject(g43,g48)
    c: PointOnObject(g44,g48)
    c: PointOnObject(g45,g48)
    c: PointOnObject(g46,g48)
    c: PointOnObject(g47,g48)
    c: Equal(g41,g48)
    c: Diameter(g41) = 7
    c: Vertical(g39)
    c: Vertical(g43)
    c: Distance(g-2,g39) = 1
    c: Symmetric(g38,g43,g-2)
    c: Distance(g41,g-1) = 7
FEATURE [Part::Extrusion] Extrude442  label="hex057"
  Base = -> Sketch450
  Dir = (0,-1,2e-16)
  DirMode = 2
  FaceMakerClass = Part::FaceMakerBullseye
  FaceMakerMode = 3
  LengthFwd = 10
  LengthRev = 0
  Placement = pos=(16,0,-14) rot=(0,0,1;0rad)
  Solid = true
  Symmetric = false
FEATURE [Sketcher::SketchObject] Sketch451
  ArcFitTolerance = 1e-06
  FullyConstrained = true
  MakeInternals = false
  Placement = pos=(0,0,0) rot=(1,0,0;1.5708rad)
  sketch-geometry (49):
    g0: LineSegment StartX=1e-16 StartY=3.5 StartZ=0 EndX=-3.03109 EndY=1.75 EndZ=0
    g1: LineSegment StartX=-3.03109 StartY=1.75 StartZ=0 EndX=-3.03109 EndY=-1.75 EndZ=0
    g2: LineSegment StartX=-3.03109 StartY=-1.75 StartZ=0 EndX=-1e-16 EndY=-3.5 EndZ=0
    g3: LineSegment StartX=-1e-16 StartY=-3.5 StartZ=0 EndX=3.03109 EndY=-1.75 EndZ=0
    g4: LineSegment StartX=3.03109 StartY=-1.75 StartZ=0 EndX=3.03109 EndY=1.75 EndZ=0
    g5: LineSegment StartX=3.03109 StartY=1.75 StartZ=0 EndX=1e-16 EndY=3.5 EndZ=0
    g6: Circle [constr] CenterX=0 CenterY=0 CenterZ=0 NormalX=0 NormalY=0 NormalZ=1 AngleXU=0 Radius=3.5
    g7: LineSegment StartX=4.96892 StartY=-1.75002 StartZ=0 EndX=8.00002 EndY=-3.5 EndZ=0
    g8: LineSegment StartX=8.00002 StartY=-3.5 StartZ=0 EndX=11.0311 EndY=-1.74998 EndZ=0
    g9: LineSegment StartX=11.0311 StartY=-1.74998 StartZ=0 EndX=11.0311 EndY=1.75002 EndZ=0
    g10: LineSegment StartX=11.0311 StartY=1.75002 StartZ=0 EndX=7.99998 EndY=3.5 EndZ=0
    g11: LineSegment StartX=7.99998 StartY=3.5 StartZ=0 EndX=4.9689 EndY=1.74998 EndZ=0
    g12: LineSegment StartX=4.9689 StartY=1.74998 StartZ=0 EndX=4.96892 EndY=-1.75002 EndZ=0
    g13: Circle [constr] CenterX=8 CenterY=0 CenterZ=0 NormalX=0 NormalY=0 NormalZ=1 AngleXU=0 Radius=3.5
    g14: LineSegment StartX=4.03109 StartY=3.5 StartZ=0 EndX=7.06218 EndY=5.25 EndZ=0
    g15: LineSegment StartX=7.06218 StartY=5.25 StartZ=0 EndX=7.06218 EndY=8.75 EndZ=0
    g16: LineSegment StartX=7.06218 StartY=8.75 StartZ=0 EndX=4.03109 EndY=10.5 EndZ=0
    g17: LineSegment StartX=4.03109 StartY=10.5 StartZ=0 EndX=1 EndY=8.75 EndZ=0
    g18: LineSegment StartX=1 StartY=8.75 StartZ=0 EndX=1 EndY=5.25 EndZ=0
    g19: LineSegment StartX=1 StartY=5.25 StartZ=0 EndX=4.03109 EndY=3.5 EndZ=0
    g20: Circle [constr] CenterX=4.03109 CenterY=7 CenterZ=0 NormalX=0 NormalY=0 NormalZ=1 AngleXU=0 Radius=3.5
    g21: LineSegment StartX=-1 StartY=5.25 StartZ=0 EndX=-1 EndY=8.75 EndZ=0
    g22: LineSegment StartX=-1 StartY=8.75 StartZ=0 EndX=-4.03109 EndY=10.5 EndZ=0
    g23: LineSegment StartX=-4.03109 StartY=10.5 StartZ=0 EndX=-7.06218 EndY=8.75 EndZ=0
    g24: LineSegment StartX=-7.06218 StartY=8.75 StartZ=0 EndX=-7.06218 EndY=5.25 EndZ=0
    g25: LineSegment StartX=-7.06218 StartY=5.25 StartZ=0 EndX=-4.03109 EndY=3.5 EndZ=0
    g26: LineSegment StartX=-4.03109 StartY=3.5 StartZ=0 EndX=-1 EndY=5.25 EndZ=0
    g27: Circle [constr] CenterX=-4.03109 CenterY=7 CenterZ=0 NormalX=0 NormalY=0 NormalZ=1 AngleXU=0 Radius=3.5
    g28: LineSegment StartX=-4.96891 StartY=-1.75 StartZ=0 EndX=-4.96891 EndY=1.75 EndZ=0
    g29: LineSegment StartX=-4.96891 StartY=1.75 StartZ=0 EndX=-8 EndY=3.5 EndZ=0
    g30: LineSegment StartX=-8 StartY=3.5 StartZ=0 EndX=-11.0311 EndY=1.75 EndZ=0
    g31: LineSegment StartX=-11.0311 StartY=1.75 StartZ=0 EndX=-11.0311 EndY=-1.75 EndZ=0
    g32: LineSegment StartX=-11.0311 StartY=-1.75 StartZ=0 EndX=-8 EndY=-3.5 EndZ=0
    g33: LineSegment StartX=-8 StartY=-3.5 StartZ=0 EndX=-4.96891 EndY=-1.75 EndZ=0
    g34: Circle [constr] CenterX=-8 CenterY=0 CenterZ=0 NormalX=0 NormalY=0 NormalZ=1 AngleXU=0 Radius=3.5
    g35: LineSegment StartX=-4.03109 StartY=-3.5 StartZ=0 EndX=-7.06218 EndY=-5.25 EndZ=0
    g36: LineSegment StartX=-7.06218 StartY=-5.25 StartZ=0 EndX=-7.06218 EndY=-8.75 EndZ=0
    g37: LineSegment StartX=-7.06218 StartY=-8.75 StartZ=0 EndX=-4.03109 EndY=-10.5 EndZ=0
    g38: LineSegment StartX=-4.03109 StartY=-10.5 StartZ=0 EndX=-1 EndY=-8.75 EndZ=0
    g39: LineSegment StartX=-1 StartY=-8.75 StartZ=0 EndX=-1 EndY=-5.25 EndZ=0
    g40: LineSegment StartX=-1 StartY=-5.25 StartZ=0 EndX=-4.03109 EndY=-3.5 EndZ=0
    g41: Circle [constr] CenterX=-4.03109 CenterY=-7 CenterZ=0 NormalX=0 NormalY=0 NormalZ=1 AngleXU=0 Radius=3.5
    g42: LineSegment StartX=4.03109 StartY=-3.5 StartZ=0 EndX=1 EndY=-5.25 EndZ=0
    g43: LineSegment StartX=1 StartY=-5.25 StartZ=0 EndX=1 EndY=-8.75 EndZ=0
    g44: LineSegment StartX=1 StartY=-8.75 StartZ=0 EndX=4.03109 EndY=-10.5 EndZ=0
    g45: LineSegment StartX=4.03109 StartY=-10.5 StartZ=0 EndX=7.06218 EndY=-8.75 EndZ=0
    g46: LineSegment StartX=7.06218 StartY=-8.75 StartZ=0 EndX=7.06218 EndY=-5.25 EndZ=0
    g47: LineSegment StartX=7.06218 StartY=-5.25 StartZ=0 EndX=4.03109 EndY=-3.5 EndZ=0
    g48: Circle [constr] CenterX=4.03109 CenterY=-7 CenterZ=0 NormalX=0 NormalY=0 NormalZ=1 AngleXU=0 Radius=3.5
  constraints (117):
    c: Coincident(g0,g1)
    c: Coincident(g1,g2)
    c: Coincident(g2,g3)
    c: Coincident(g3,g4)
    c: Coincident(g4,g5)
    c: Coincident(g5,g0)
    c: Equal(g0, g1-g5) x5
    c: PointOnObject(g0,g6)
    c: PointOnObject(g1,g6)
    c: PointOnObject(g2,g6)
    c: PointOnObject(g3,g6)
    c: PointOnObject(g4,g6)
    c: PointOnObject(g5,g6)
    c: Coincident(g6,g-1)
    c: Diameter(g6) = 7
    c: PointOnObject(g0,g-2)
    c: Coincident(g7,g8)
    c: Coincident(g8,g9)
    c: Coincident(g9,g10)
    c: Coincident(g10,g11)
    c: Coincident(g11,g12)
    c: Coincident(g12,g7)
    c: Equal(g7, g8-g12) x5
    c: PointOnObject(g7,g13)
    c: PointOnObject(g8,g13)
    c: PointOnObject(g9,g13)
    c: PointOnObject(g10,g13)
    c: PointOnObject(g11,g13)
    c: PointOnObject(g12,g13)
    c: PointOnObject(g13,g-1)
    c: Diameter(g13) = 7
    c: Distance(g6,g13) = 8
    c: Horizontal(g0,g10)
    c: Coincident(g14,g15)
    c: Coincident(g15,g16)
    c: Coincident(g16,g17)
    c: Coincident(g17,g18)
    c: Coincident(g18,g19)
    c: Coincident(g19,g14)
    c: Equal(g14, g15-g19) x5
    c: PointOnObject(g14,g20)
    c: PointOnObject(g15,g20)
    c: PointOnObject(g16,g20)
    c: PointOnObject(g17,g20)
    c: PointOnObject(g18,g20)
    c: PointOnObject(g19,g20)
    c: Diameter(g20) = 7
    c: DistanceY(g-1,g20) = 7
    c: Vertical(g18)
    c: Distance(g17,g-2) = 1
    c: Coincident(g21,g22)
    c: Coincident(g22,g23)
    c: Coincident(g23,g24)
    c: Coincident(g24,g25)
    c: Coincident(g25,g26)
    c: Coincident(g26,g21)
    c: Equal(g21, g22-g26) x5
    c: PointOnObject(g21,g27)
    c: PointOnObject(g22,g27)
    c: PointOnObject(g23,g27)
    c: PointOnObject(g24,g27)
    c: PointOnObject(g25,g27)
    c: PointOnObject(g26,g27)
    c: Diameter(g27) = 7
    c: DistanceY(g-1,g27) = 7
    c: DistanceX(g21,g-1) = 1
    c: Vertical(g21)
    c: Coincident(g28,g29)
    c: Coincident(g29,g30)
    c: Coincident(g30,g31)
    c: Coincident(g31,g32)
    c: Coincident(g32,g33)
    c: Coincident(g33,g28)
    c: Equal(g28, g29-g33) x5
    c: PointOnObject(g28,g34)
    c: PointOnObject(g29,g34)
    c: PointOnObject(g30,g34)
    c: PointOnObject(g31,g34)
    c: PointOnObject(g32,g34)
    c: PointOnObject(g33,g34)
    c: PointOnObject(g34,g-1)
    c: Diameter(g34) = 7
    c: Vertical(g31)
    c: DistanceX(g34,g-1) = 8
    c: Coincident(g35,g36)
    c: Coincident(g36,g37)
    c: Coincident(g37,g38)
    c: Coincident(g38,g39)
    c: Coincident(g39,g40)
    c: Coincident(g40,g35)
    c: Equal(g35, g36-g40) x5
    c: PointOnObject(g35,g41)
    c: PointOnObject(g36,g41)
    c: PointOnObject(g37,g41)
    c: PointOnObject(g38,g41)
    c: PointOnObject(g39,g41)
    c: PointOnObject(g40,g41)
    c: Coincident(g42,g43)
    c: Coincident(g43,g44)
    c: Coincident(g44,g45)
    c: Coincident(g45,g46)
    c: Coincident(g46,g47)
    c: Coincident(g47,g42)
    c: Equal(g42, g43-g47) x5
    c: PointOnObject(g42,g48)
    c: PointOnObject(g43,g48)
    c: PointOnObject(g44,g48)
    c: PointOnObject(g45,g48)
    c: PointOnObject(g46,g48)
    c: PointOnObject(g47,g48)
    c: Equal(g41,g48)
    c: Diameter(g41) = 7
    c: Vertical(g39)
    c: Vertical(g43)
    c: Distance(g-2,g39) = 1
    c: Symmetric(g38,g43,g-2)
    c: Distance(g41,g-1) = 7
FEATURE [Part::Extrusion] Extrude443  label="hex058"
  Base = -> Sketch451
  Dir = (0,-1,2e-16)
  DirMode = 2
  FaceMakerClass = Part::FaceMakerBullseye
  FaceMakerMode = 3
  LengthFwd = 10
  LengthRev = 0
  Placement = pos=(-4,0,21) rot=(0,0,1;0rad)
  Solid = true
  Symmetric = false
FEATURE [Sketcher::SketchObject] Sketch452
  ArcFitTolerance = 1e-06
  FullyConstrained = true
  MakeInternals = false
  Placement = pos=(0,0,0) rot=(1,0,0;1.5708rad)
  sketch-geometry (49):
    g0: LineSegment StartX=1e-16 StartY=3.5 StartZ=0 EndX=-3.03109 EndY=1.75 EndZ=0
    g1: LineSegment StartX=-3.03109 StartY=1.75 StartZ=0 EndX=-3.03109 EndY=-1.75 EndZ=0
    g2: LineSegment StartX=-3.03109 StartY=-1.75 StartZ=0 EndX=-1e-16 EndY=-3.5 EndZ=0
    g3: LineSegment StartX=-1e-16 StartY=-3.5 StartZ=0 EndX=3.03109 EndY=-1.75 EndZ=0
    g4: LineSegment StartX=3.03109 StartY=-1.75 StartZ=0 EndX=3.03109 EndY=1.75 EndZ=0
    g5: LineSegment StartX=3.03109 StartY=1.75 StartZ=0 EndX=1e-16 EndY=3.5 EndZ=0
    g6: Circle [constr] CenterX=0 CenterY=0 CenterZ=0 NormalX=0 NormalY=0 NormalZ=1 AngleXU=0 Radius=3.5
    g7: LineSegment StartX=4.96892 StartY=-1.75002 StartZ=0 EndX=8.00002 EndY=-3.5 EndZ=0
    g8: LineSegment StartX=8.00002 StartY=-3.5 StartZ=0 EndX=11.0311 EndY=-1.74998 EndZ=0
    g9: LineSegment StartX=11.0311 StartY=-1.74998 StartZ=0 EndX=11.0311 EndY=1.75002 EndZ=0
    g10: LineSegment StartX=11.0311 StartY=1.75002 StartZ=0 EndX=7.99998 EndY=3.5 EndZ=0
    g11: LineSegment StartX=7.99998 StartY=3.5 StartZ=0 EndX=4.9689 EndY=1.74998 EndZ=0
    g12: LineSegment StartX=4.9689 StartY=1.74998 StartZ=0 EndX=4.96892 EndY=-1.75002 EndZ=0
    g13: Circle [constr] CenterX=8 CenterY=0 CenterZ=0 NormalX=0 NormalY=0 NormalZ=1 AngleXU=0 Radius=3.5
    g14: LineSegment StartX=4.03109 StartY=3.5 StartZ=0 EndX=7.06218 EndY=5.25 EndZ=0
    g15: LineSegment StartX=7.06218 StartY=5.25 StartZ=0 EndX=7.06218 EndY=8.75 EndZ=0
    g16: LineSegment StartX=7.06218 StartY=8.75 StartZ=0 EndX=4.03109 EndY=10.5 EndZ=0
    g17: LineSegment StartX=4.03109 StartY=10.5 StartZ=0 EndX=1 EndY=8.75 EndZ=0
    g18: LineSegment StartX=1 StartY=8.75 StartZ=0 EndX=1 EndY=5.25 EndZ=0
    g19: LineSegment StartX=1 StartY=5.25 StartZ=0 EndX=4.03109 EndY=3.5 EndZ=0
    g20: Circle [constr] CenterX=4.03109 CenterY=7 CenterZ=0 NormalX=0 NormalY=0 NormalZ=1 AngleXU=0 Radius=3.5
    g21: LineSegment StartX=-1 StartY=5.25 StartZ=0 EndX=-1 EndY=8.75 EndZ=0
    g22: LineSegment StartX=-1 StartY=8.75 StartZ=0 EndX=-4.03109 EndY=10.5 EndZ=0
    g23: LineSegment StartX=-4.03109 StartY=10.5 StartZ=0 EndX=-7.06218 EndY=8.75 EndZ=0
    g24: LineSegment StartX=-7.06218 StartY=8.75 StartZ=0 EndX=-7.06218 EndY=5.25 EndZ=0
    g25: LineSegment StartX=-7.06218 StartY=5.25 StartZ=0 EndX=-4.03109 EndY=3.5 EndZ=0
    g26: LineSegment StartX=-4.03109 StartY=3.5 StartZ=0 EndX=-1 EndY=5.25 EndZ=0
    g27: Circle [constr] CenterX=-4.03109 CenterY=7 CenterZ=0 NormalX=0 NormalY=0 NormalZ=1 AngleXU=0 Radius=3.5
    g28: LineSegment StartX=-4.96891 StartY=-1.75 StartZ=0 EndX=-4.96891 EndY=1.75 EndZ=0
    g29: LineSegment StartX=-4.96891 StartY=1.75 StartZ=0 EndX=-8 EndY=3.5 EndZ=0
    g30: LineSegment StartX=-8 StartY=3.5 StartZ=0 EndX=-11.0311 EndY=1.75 EndZ=0
    g31: LineSegment StartX=-11.0311 StartY=1.75 StartZ=0 EndX=-11.0311 EndY=-1.75 EndZ=0
    g32: LineSegment StartX=-11.0311 StartY=-1.75 StartZ=0 EndX=-8 EndY=-3.5 EndZ=0
    g33: LineSegment StartX=-8 StartY=-3.5 StartZ=0 EndX=-4.96891 EndY=-1.75 EndZ=0
    g34: Circle [constr] CenterX=-8 CenterY=0 CenterZ=0 NormalX=0 NormalY=0 NormalZ=1 AngleXU=0 Radius=3.5
    g35: LineSegment StartX=-4.03109 StartY=-3.5 StartZ=0 EndX=-7.06218 EndY=-5.25 EndZ=0
    g36: LineSegment StartX=-7.06218 StartY=-5.25 StartZ=0 EndX=-7.06218 EndY=-8.75 EndZ=0
    g37: LineSegment StartX=-7.06218 StartY=-8.75 StartZ=0 EndX=-4.03109 EndY=-10.5 EndZ=0
    g38: LineSegment StartX=-4.03109 StartY=-10.5 StartZ=0 EndX=-1 EndY=-8.75 EndZ=0
    g39: LineSegment StartX=-1 StartY=-8.75 StartZ=0 EndX=-1 EndY=-5.25 EndZ=0
    g40: LineSegment StartX=-1 StartY=-5.25 StartZ=0 EndX=-4.03109 EndY=-3.5 EndZ=0
    g41: Circle [constr] CenterX=-4.03109 CenterY=-7 CenterZ=0 NormalX=0 NormalY=0 NormalZ=1 AngleXU=0 Radius=3.5
    g42: LineSegment StartX=4.03109 StartY=-3.5 StartZ=0 EndX=1 EndY=-5.25 EndZ=0
    g43: LineSegment StartX=1 StartY=-5.25 StartZ=0 EndX=1 EndY=-8.75 EndZ=0
    g44: LineSegment StartX=1 StartY=-8.75 StartZ=0 EndX=4.03109 EndY=-10.5 EndZ=0
    g45: LineSegment StartX=4.03109 StartY=-10.5 StartZ=0 EndX=7.06218 EndY=-8.75 EndZ=0
    g46: LineSegment StartX=7.06218 StartY=-8.75 StartZ=0 EndX=7.06218 EndY=-5.25 EndZ=0
    g47: LineSegment StartX=7.06218 StartY=-5.25 StartZ=0 EndX=4.03109 EndY=-3.5 EndZ=0
    g48: Circle [constr] CenterX=4.03109 CenterY=-7 CenterZ=0 NormalX=0 NormalY=0 NormalZ=1 AngleXU=0 Radius=3.5
  constraints (117):
    c: Coincident(g0,g1)
    c: Coincident(g1,g2)
    c: Coincident(g2,g3)
    c: Coincident(g3,g4)
    c: Coincident(g4,g5)
    c: Coincident(g5,g0)
    c: Equal(g0, g1-g5) x5
    c: PointOnObject(g0,g6)
    c: PointOnObject(g1,g6)
    c: PointOnObject(g2,g6)
    c: PointOnObject(g3,g6)
    c: PointOnObject(g4,g6)
    c: PointOnObject(g5,g6)
    c: Coincident(g6,g-1)
    c: Diameter(g6) = 7
    c: PointOnObject(g0,g-2)
    c: Coincident(g7,g8)
    c: Coincident(g8,g9)
    c: Coincident(g9,g10)
    c: Coincident(g10,g11)
    c: Coincident(g11,g12)
    c: Coincident(g12,g7)
    c: Equal(g7, g8-g12) x5
    c: PointOnObject(g7,g13)
    c: PointOnObject(g8,g13)
    c: PointOnObject(g9,g13)
    c: PointOnObject(g10,g13)
    c: PointOnObject(g11,g13)
    c: PointOnObject(g12,g13)
    c: PointOnObject(g13,g-1)
    c: Diameter(g13) = 7
    c: Distance(g6,g13) = 8
    c: Horizontal(g0,g10)
    c: Coincident(g14,g15)
    c: Coincident(g15,g16)
    c: Coincident(g16,g17)
    c: Coincident(g17,g18)
    c: Coincident(g18,g19)
    c: Coincident(g19,g14)
    c: Equal(g14, g15-g19) x5
    c: PointOnObject(g14,g20)
    c: PointOnObject(g15,g20)
    c: PointOnObject(g16,g20)
    c: PointOnObject(g17,g20)
    c: PointOnObject(g18,g20)
    c: PointOnObject(g19,g20)
    c: Diameter(g20) = 7
    c: DistanceY(g-1,g20) = 7
    c: Vertical(g18)
    c: Distance(g17,g-2) = 1
    c: Coincident(g21,g22)
    c: Coincident(g22,g23)
    c: Coincident(g23,g24)
    c: Coincident(g24,g25)
    c: Coincident(g25,g26)
    c: Coincident(g26,g21)
    c: Equal(g21, g22-g26) x5
    c: PointOnObject(g21,g27)
    c: PointOnObject(g22,g27)
    c: PointOnObject(g23,g27)
    c: PointOnObject(g24,g27)
    c: PointOnObject(g25,g27)
    c: PointOnObject(g26,g27)
    c: Diameter(g27) = 7
    c: DistanceY(g-1,g27) = 7
    c: DistanceX(g21,g-1) = 1
    c: Vertical(g21)
    c: Coincident(g28,g29)
    c: Coincident(g29,g30)
    c: Coincident(g30,g31)
    c: Coincident(g31,g32)
    c: Coincident(g32,g33)
    c: Coincident(g33,g28)
    c: Equal(g28, g29-g33) x5
    c: PointOnObject(g28,g34)
    c: PointOnObject(g29,g34)
    c: PointOnObject(g30,g34)
    c: PointOnObject(g31,g34)
    c: PointOnObject(g32,g34)
    c: PointOnObject(g33,g34)
    c: PointOnObject(g34,g-1)
    c: Diameter(g34) = 7
    c: Vertical(g31)
    c: DistanceX(g34,g-1) = 8
    c: Coincident(g35,g36)
    c: Coincident(g36,g37)
    c: Coincident(g37,g38)
    c: Coincident(g38,g39)
    c: Coincident(g39,g40)
    c: Coincident(g40,g35)
    c: Equal(g35, g36-g40) x5
    c: PointOnObject(g35,g41)
    c: PointOnObject(g36,g41)
    c: PointOnObject(g37,g41)
    c: PointOnObject(g38,g41)
    c: PointOnObject(g39,g41)
    c: PointOnObject(g40,g41)
    c: Coincident(g42,g43)
    c: Coincident(g43,g44)
    c: Coincident(g44,g45)
    c: Coincident(g45,g46)
    c: Coincident(g46,g47)
    c: Coincident(g47,g42)
    c: Equal(g42, g43-g47) x5
    c: PointOnObject(g42,g48)
    c: PointOnObject(g43,g48)
    c: PointOnObject(g44,g48)
    c: PointOnObject(g45,g48)
    c: PointOnObject(g46,g48)
    c: PointOnObject(g47,g48)
    c: Equal(g41,g48)
    c: Diameter(g41) = 7
    c: Vertical(g39)
    c: Vertical(g43)
    c: Distance(g-2,g39) = 1
    c: Symmetric(g38,g43,g-2)
    c: Distance(g41,g-1) = 7
FEATURE [Part::Extrusion] Extrude444  label="hex059"
  Base = -> Sketch452
  Dir = (0,-1,2e-16)
  DirMode = 2
  FaceMakerClass = Part::FaceMakerBullseye
  FaceMakerMode = 3
  LengthFwd = 10
  LengthRev = 0
  Placement = pos=(12,0,-35) rot=(0,0,1;0rad)
  Solid = true
  Symmetric = false
FEATURE [Sketcher::SketchObject] Sketch453
  ArcFitTolerance = 1e-06
  FullyConstrained = true
  MakeInternals = false
  Placement = pos=(0,0,0) rot=(1,0,0;1.5708rad)
  sketch-geometry (49):
    g0: LineSegment StartX=1e-16 StartY=3.5 StartZ=0 EndX=-3.03109 EndY=1.75 EndZ=0
    g1: LineSegment StartX=-3.03109 StartY=1.75 StartZ=0 EndX=-3.03109 EndY=-1.75 EndZ=0
    g2: LineSegment StartX=-3.03109 StartY=-1.75 StartZ=0 EndX=-1e-16 EndY=-3.5 EndZ=0
    g3: LineSegment StartX=-1e-16 StartY=-3.5 StartZ=0 EndX=3.03109 EndY=-1.75 EndZ=0
    g4: LineSegment StartX=3.03109 StartY=-1.75 StartZ=0 EndX=3.03109 EndY=1.75 EndZ=0
    g5: LineSegment StartX=3.03109 StartY=1.75 StartZ=0 EndX=1e-16 EndY=3.5 EndZ=0
    g6: Circle [constr] CenterX=0 CenterY=0 CenterZ=0 NormalX=0 NormalY=0 NormalZ=1 AngleXU=0 Radius=3.5
    g7: LineSegment StartX=4.96892 StartY=-1.75002 StartZ=0 EndX=8.00002 EndY=-3.5 EndZ=0
    g8: LineSegment StartX=8.00002 StartY=-3.5 StartZ=0 EndX=11.0311 EndY=-1.74998 EndZ=0
    g9: LineSegment StartX=11.0311 StartY=-1.74998 StartZ=0 EndX=11.0311 EndY=1.75002 EndZ=0
    g10: LineSegment StartX=11.0311 StartY=1.75002 StartZ=0 EndX=7.99998 EndY=3.5 EndZ=0
    g11: LineSegment StartX=7.99998 StartY=3.5 StartZ=0 EndX=4.9689 EndY=1.74998 EndZ=0
    g12: LineSegment StartX=4.9689 StartY=1.74998 StartZ=0 EndX=4.96892 EndY=-1.75002 EndZ=0
    g13: Circle [constr] CenterX=8 CenterY=0 CenterZ=0 NormalX=0 NormalY=0 NormalZ=1 AngleXU=0 Radius=3.5
    g14: LineSegment StartX=4.03109 StartY=3.5 StartZ=0 EndX=7.06218 EndY=5.25 EndZ=0
    g15: LineSegment StartX=7.06218 StartY=5.25 StartZ=0 EndX=7.06218 EndY=8.75 EndZ=0
    g16: LineSegment StartX=7.06218 StartY=8.75 StartZ=0 EndX=4.03109 EndY=10.5 EndZ=0
    g17: LineSegment StartX=4.03109 StartY=10.5 StartZ=0 EndX=1 EndY=8.75 EndZ=0
    g18: LineSegment StartX=1 StartY=8.75 StartZ=0 EndX=1 EndY=5.25 EndZ=0
    g19: LineSegment StartX=1 StartY=5.25 StartZ=0 EndX=4.03109 EndY=3.5 EndZ=0
    g20: Circle [constr] CenterX=4.03109 CenterY=7 CenterZ=0 NormalX=0 NormalY=0 NormalZ=1 AngleXU=0 Radius=3.5
    g21: LineSegment StartX=-1 StartY=5.25 StartZ=0 EndX=-1 EndY=8.75 EndZ=0
    g22: LineSegment StartX=-1 StartY=8.75 StartZ=0 EndX=-4.03109 EndY=10.5 EndZ=0
    g23: LineSegment StartX=-4.03109 StartY=10.5 StartZ=0 EndX=-7.06218 EndY=8.75 EndZ=0
    g24: LineSegment StartX=-7.06218 StartY=8.75 StartZ=0 EndX=-7.06218 EndY=5.25 EndZ=0
    g25: LineSegment StartX=-7.06218 StartY=5.25 StartZ=0 EndX=-4.03109 EndY=3.5 EndZ=0
    g26: LineSegment StartX=-4.03109 StartY=3.5 StartZ=0 EndX=-1 EndY=5.25 EndZ=0
    g27: Circle [constr] CenterX=-4.03109 CenterY=7 CenterZ=0 NormalX=0 NormalY=0 NormalZ=1 AngleXU=0 Radius=3.5
    g28: LineSegment StartX=-4.96891 StartY=-1.75 StartZ=0 EndX=-4.96891 EndY=1.75 EndZ=0
    g29: LineSegment StartX=-4.96891 StartY=1.75 StartZ=0 EndX=-8 EndY=3.5 EndZ=0
    g30: LineSegment StartX=-8 StartY=3.5 StartZ=0 EndX=-11.0311 EndY=1.75 EndZ=0
    g31: LineSegment StartX=-11.0311 StartY=1.75 StartZ=0 EndX=-11.0311 EndY=-1.75 EndZ=0
    g32: LineSegment StartX=-11.0311 StartY=-1.75 StartZ=0 EndX=-8 EndY=-3.5 EndZ=0
    g33: LineSegment StartX=-8 StartY=-3.5 StartZ=0 EndX=-4.96891 EndY=-1.75 EndZ=0
    g34: Circle [constr] CenterX=-8 CenterY=0 CenterZ=0 NormalX=0 NormalY=0 NormalZ=1 AngleXU=0 Radius=3.5
    g35: LineSegment StartX=-4.03109 StartY=-3.5 StartZ=0 EndX=-7.06218 EndY=-5.25 EndZ=0
    g36: LineSegment StartX=-7.06218 StartY=-5.25 StartZ=0 EndX=-7.06218 EndY=-8.75 EndZ=0
    g37: LineSegment StartX=-7.06218 StartY=-8.75 StartZ=0 EndX=-4.03109 EndY=-10.5 EndZ=0
    g38: LineSegment StartX=-4.03109 StartY=-10.5 StartZ=0 EndX=-1 EndY=-8.75 EndZ=0
    g39: LineSegment StartX=-1 StartY=-8.75 StartZ=0 EndX=-1 EndY=-5.25 EndZ=0
    g40: LineSegment StartX=-1 StartY=-5.25 StartZ=0 EndX=-4.03109 EndY=-3.5 EndZ=0
    g41: Circle [constr] CenterX=-4.03109 CenterY=-7 CenterZ=0 NormalX=0 NormalY=0 NormalZ=1 AngleXU=0 Radius=3.5
    g42: LineSegment StartX=4.03109 StartY=-3.5 StartZ=0 EndX=1 EndY=-5.25 EndZ=0
    g43: LineSegment StartX=1 StartY=-5.25 StartZ=0 EndX=1 EndY=-8.75 EndZ=0
    g44: LineSegment StartX=1 StartY=-8.75 StartZ=0 EndX=4.03109 EndY=-10.5 EndZ=0
    g45: LineSegment StartX=4.03109 StartY=-10.5 StartZ=0 EndX=7.06218 EndY=-8.75 EndZ=0
    g46: LineSegment StartX=7.06218 StartY=-8.75 StartZ=0 EndX=7.06218 EndY=-5.25 EndZ=0
    g47: LineSegment StartX=7.06218 StartY=-5.25 StartZ=0 EndX=4.03109 EndY=-3.5 EndZ=0
    g48: Circle [constr] CenterX=4.03109 CenterY=-7 CenterZ=0 NormalX=0 NormalY=0 NormalZ=1 AngleXU=0 Radius=3.5
  constraints (117):
    c: Coincident(g0,g1)
    c: Coincident(g1,g2)
    c: Coincident(g2,g3)
    c: Coincident(g3,g4)
    c: Coincident(g4,g5)
    c: Coincident(g5,g0)
    c: Equal(g0, g1-g5) x5
    c: PointOnObject(g0,g6)
    c: PointOnObject(g1,g6)
    c: PointOnObject(g2,g6)
    c: PointOnObject(g3,g6)
    c: PointOnObject(g4,g6)
    c: PointOnObject(g5,g6)
    c: Coincident(g6,g-1)
    c: Diameter(g6) = 7
    c: PointOnObject(g0,g-2)
    c: Coincident(g7,g8)
    c: Coincident(g8,g9)
    c: Coincident(g9,g10)
    c: Coincident(g10,g11)
    c: Coincident(g11,g12)
    c: Coincident(g12,g7)
    c: Equal(g7, g8-g12) x5
    c: PointOnObject(g7,g13)
    c: PointOnObject(g8,g13)
    c: PointOnObject(g9,g13)
    c: PointOnObject(g10,g13)
    c: PointOnObject(g11,g13)
    c: PointOnObject(g12,g13)
    c: PointOnObject(g13,g-1)
    c: Diameter(g13) = 7
    c: Distance(g6,g13) = 8
    c: Horizontal(g0,g10)
    c: Coincident(g14,g15)
    c: Coincident(g15,g16)
    c: Coincident(g16,g17)
    c: Coincident(g17,g18)
    c: Coincident(g18,g19)
    c: Coincident(g19,g14)
    c: Equal(g14, g15-g19) x5
    c: PointOnObject(g14,g20)
    c: PointOnObject(g15,g20)
    c: PointOnObject(g16,g20)
    c: PointOnObject(g17,g20)
    c: PointOnObject(g18,g20)
    c: PointOnObject(g19,g20)
    c: Diameter(g20) = 7
    c: DistanceY(g-1,g20) = 7
    c: Vertical(g18)
    c: Distance(g17,g-2) = 1
    c: Coincident(g21,g22)
    c: Coincident(g22,g23)
    c: Coincident(g23,g24)
    c: Coincident(g24,g25)
    c: Coincident(g25,g26)
    c: Coincident(g26,g21)
    c: Equal(g21, g22-g26) x5
    c: PointOnObject(g21,g27)
    c: PointOnObject(g22,g27)
    c: PointOnObject(g23,g27)
    c: PointOnObject(g24,g27)
    c: PointOnObject(g25,g27)
    c: PointOnObject(g26,g27)
    c: Diameter(g27) = 7
    c: DistanceY(g-1,g27) = 7
    c: DistanceX(g21,g-1) = 1
    c: Vertical(g21)
    c: Coincident(g28,g29)
    c: Coincident(g29,g30)
    c: Coincident(g30,g31)
    c: Coincident(g31,g32)
    c: Coincident(g32,g33)
    c: Coincident(g33,g28)
    c: Equal(g28, g29-g33) x5
    c: PointOnObject(g28,g34)
    c: PointOnObject(g29,g34)
    c: PointOnObject(g30,g34)
    c: PointOnObject(g31,g34)
    c: PointOnObject(g32,g34)
    c: PointOnObject(g33,g34)
    c: PointOnObject(g34,g-1)
    c: Diameter(g34) = 7
    c: Vertical(g31)
    c: DistanceX(g34,g-1) = 8
    c: Coincident(g35,g36)
    c: Coincident(g36,g37)
    c: Coincident(g37,g38)
    c: Coincident(g38,g39)
    c: Coincident(g39,g40)
    c: Coincident(g40,g35)
    c: Equal(g35, g36-g40) x5
    c: PointOnObject(g35,g41)
    c: PointOnObject(g36,g41)
    c: PointOnObject(g37,g41)
    c: PointOnObject(g38,g41)
    c: PointOnObject(g39,g41)
    c: PointOnObject(g40,g41)
    c: Coincident(g42,g43)
    c: Coincident(g43,g44)
    c: Coincident(g44,g45)
    c: Coincident(g45,g46)
    c: Coincident(g46,g47)
    c: Coincident(g47,g42)
    c: Equal(g42, g43-g47) x5
    c: PointOnObject(g42,g48)
    c: PointOnObject(g43,g48)
    c: PointOnObject(g44,g48)
    c: PointOnObject(g45,g48)
    c: PointOnObject(g46,g48)
    c: PointOnObject(g47,g48)
    c: Equal(g41,g48)
    c: Diameter(g41) = 7
    c: Vertical(g39)
    c: Vertical(g43)
    c: Distance(g-2,g39) = 1
    c: Symmetric(g38,g43,g-2)
    c: Distance(g41,g-1) = 7
FEATURE [Part::Extrusion] Extrude445  label="hex060"
  Base = -> Sketch453
  Dir = (0,-1,2e-16)
  DirMode = 2
  FaceMakerClass = Part::FaceMakerBullseye
  FaceMakerMode = 3
  LengthFwd = 10
  LengthRev = 0
  Placement = pos=(12,0,35) rot=(0,0,1;0rad)
  Solid = true
  Symmetric = false
FEATURE [Sketcher::SketchObject] Sketch454
  ArcFitTolerance = 1e-06
  FullyConstrained = true
  MakeInternals = false
  Placement = pos=(0,0,0) rot=(1,0,0;1.5708rad)
  sketch-geometry (49):
    g0: LineSegment StartX=1e-16 StartY=3.5 StartZ=0 EndX=-3.03109 EndY=1.75 EndZ=0
    g1: LineSegment StartX=-3.03109 StartY=1.75 StartZ=0 EndX=-3.03109 EndY=-1.75 EndZ=0
    g2: LineSegment StartX=-3.03109 StartY=-1.75 StartZ=0 EndX=-1e-16 EndY=-3.5 EndZ=0
    g3: LineSegment StartX=-1e-16 StartY=-3.5 StartZ=0 EndX=3.03109 EndY=-1.75 EndZ=0
    g4: LineSegment StartX=3.03109 StartY=-1.75 StartZ=0 EndX=3.03109 EndY=1.75 EndZ=0
    g5: LineSegment StartX=3.03109 StartY=1.75 StartZ=0 EndX=1e-16 EndY=3.5 EndZ=0
    g6: Circle [constr] CenterX=0 CenterY=0 CenterZ=0 NormalX=0 NormalY=0 NormalZ=1 AngleXU=0 Radius=3.5
    g7: LineSegment StartX=4.96892 StartY=-1.75002 StartZ=0 EndX=8.00002 EndY=-3.5 EndZ=0
    g8: LineSegment StartX=8.00002 StartY=-3.5 StartZ=0 EndX=11.0311 EndY=-1.74998 EndZ=0
    g9: LineSegment StartX=11.0311 StartY=-1.74998 StartZ=0 EndX=11.0311 EndY=1.75002 EndZ=0
    g10: LineSegment StartX=11.0311 StartY=1.75002 StartZ=0 EndX=7.99998 EndY=3.5 EndZ=0
    g11: LineSegment StartX=7.99998 StartY=3.5 StartZ=0 EndX=4.9689 EndY=1.74998 EndZ=0
    g12: LineSegment StartX=4.9689 StartY=1.74998 StartZ=0 EndX=4.96892 EndY=-1.75002 EndZ=0
    g13: Circle [constr] CenterX=8 CenterY=0 CenterZ=0 NormalX=0 NormalY=0 NormalZ=1 AngleXU=0 Radius=3.5
    g14: LineSegment StartX=4.03109 StartY=3.5 StartZ=0 EndX=7.06218 EndY=5.25 EndZ=0
    g15: LineSegment StartX=7.06218 StartY=5.25 StartZ=0 EndX=7.06218 EndY=8.75 EndZ=0
    g16: LineSegment StartX=7.06218 StartY=8.75 StartZ=0 EndX=4.03109 EndY=10.5 EndZ=0
    g17: LineSegment StartX=4.03109 StartY=10.5 StartZ=0 EndX=1 EndY=8.75 EndZ=0
    g18: LineSegment StartX=1 StartY=8.75 StartZ=0 EndX=1 EndY=5.25 EndZ=0
    g19: LineSegment StartX=1 StartY=5.25 StartZ=0 EndX=4.03109 EndY=3.5 EndZ=0
    g20: Circle [constr] CenterX=4.03109 CenterY=7 CenterZ=0 NormalX=0 NormalY=0 NormalZ=1 AngleXU=0 Radius=3.5
    g21: LineSegment StartX=-1 StartY=5.25 StartZ=0 EndX=-1 EndY=8.75 EndZ=0
    g22: LineSegment StartX=-1 StartY=8.75 StartZ=0 EndX=-4.03109 EndY=10.5 EndZ=0
    g23: LineSegment StartX=-4.03109 StartY=10.5 StartZ=0 EndX=-7.06218 EndY=8.75 EndZ=0
    g24: LineSegment StartX=-7.06218 StartY=8.75 StartZ=0 EndX=-7.06218 EndY=5.25 EndZ=0
    g25: LineSegment StartX=-7.06218 StartY=5.25 StartZ=0 EndX=-4.03109 EndY=3.5 EndZ=0
    g26: LineSegment StartX=-4.03109 StartY=3.5 StartZ=0 EndX=-1 EndY=5.25 EndZ=0
    g27: Circle [constr] CenterX=-4.03109 CenterY=7 CenterZ=0 NormalX=0 NormalY=0 NormalZ=1 AngleXU=0 Radius=3.5
    g28: LineSegment StartX=-4.96891 StartY=-1.75 StartZ=0 EndX=-4.96891 EndY=1.75 EndZ=0
    g29: LineSegment StartX=-4.96891 StartY=1.75 StartZ=0 EndX=-8 EndY=3.5 EndZ=0
    g30: LineSegment StartX=-8 StartY=3.5 StartZ=0 EndX=-11.0311 EndY=1.75 EndZ=0
    g31: LineSegment StartX=-11.0311 StartY=1.75 StartZ=0 EndX=-11.0311 EndY=-1.75 EndZ=0
    g32: LineSegment StartX=-11.0311 StartY=-1.75 StartZ=0 EndX=-8 EndY=-3.5 EndZ=0
    g33: LineSegment StartX=-8 StartY=-3.5 StartZ=0 EndX=-4.96891 EndY=-1.75 EndZ=0
    g34: Circle [constr] CenterX=-8 CenterY=0 CenterZ=0 NormalX=0 NormalY=0 NormalZ=1 AngleXU=0 Radius=3.5
    g35: LineSegment StartX=-4.03109 StartY=-3.5 StartZ=0 EndX=-7.06218 EndY=-5.25 EndZ=0
    g36: LineSegment StartX=-7.06218 StartY=-5.25 StartZ=0 EndX=-7.06218 EndY=-8.75 EndZ=0
    g37: LineSegment StartX=-7.06218 StartY=-8.75 StartZ=0 EndX=-4.03109 EndY=-10.5 EndZ=0
    g38: LineSegment StartX=-4.03109 StartY=-10.5 StartZ=0 EndX=-1 EndY=-8.75 EndZ=0
    g39: LineSegment StartX=-1 StartY=-8.75 StartZ=0 EndX=-1 EndY=-5.25 EndZ=0
    g40: LineSegment StartX=-1 StartY=-5.25 StartZ=0 EndX=-4.03109 EndY=-3.5 EndZ=0
    g41: Circle [constr] CenterX=-4.03109 CenterY=-7 CenterZ=0 NormalX=0 NormalY=0 NormalZ=1 AngleXU=0 Radius=3.5
    g42: LineSegment StartX=4.03109 StartY=-3.5 StartZ=0 EndX=1 EndY=-5.25 EndZ=0
    g43: LineSegment StartX=1 StartY=-5.25 StartZ=0 EndX=1 EndY=-8.75 EndZ=0
    g44: LineSegment StartX=1 StartY=-8.75 StartZ=0 EndX=4.03109 EndY=-10.5 EndZ=0
    g45: LineSegment StartX=4.03109 StartY=-10.5 StartZ=0 EndX=7.06218 EndY=-8.75 EndZ=0
    g46: LineSegment StartX=7.06218 StartY=-8.75 StartZ=0 EndX=7.06218 EndY=-5.25 EndZ=0
    g47: LineSegment StartX=7.06218 StartY=-5.25 StartZ=0 EndX=4.03109 EndY=-3.5 EndZ=0
    g48: Circle [constr] CenterX=4.03109 CenterY=-7 CenterZ=0 NormalX=0 NormalY=0 NormalZ=1 AngleXU=0 Radius=3.5
  constraints (117):
    c: Coincident(g0,g1)
    c: Coincident(g1,g2)
    c: Coincident(g2,g3)
    c: Coincident(g3,g4)
    c: Coincident(g4,g5)
    c: Coincident(g5,g0)
    c: Equal(g0, g1-g5) x5
    c: PointOnObject(g0,g6)
    c: PointOnObject(g1,g6)
    c: PointOnObject(g2,g6)
    c: PointOnObject(g3,g6)
    c: PointOnObject(g4,g6)
    c: PointOnObject(g5,g6)
    c: Coincident(g6,g-1)
    c: Diameter(g6) = 7
    c: PointOnObject(g0,g-2)
    c: Coincident(g7,g8)
    c: Coincident(g8,g9)
    c: Coincident(g9,g10)
    c: Coincident(g10,g11)
    c: Coincident(g11,g12)
    c: Coincident(g12,g7)
    c: Equal(g7, g8-g12) x5
    c: PointOnObject(g7,g13)
    c: PointOnObject(g8,g13)
    c: PointOnObject(g9,g13)
    c: PointOnObject(g10,g13)
    c: PointOnObject(g11,g13)
    c: PointOnObject(g12,g13)
    c: PointOnObject(g13,g-1)
    c: Diameter(g13) = 7
    c: Distance(g6,g13) = 8
    c: Horizontal(g0,g10)
    c: Coincident(g14,g15)
    c: Coincident(g15,g16)
    c: Coincident(g16,g17)
    c: Coincident(g17,g18)
    c: Coincident(g18,g19)
    c: Coincident(g19,g14)
    c: Equal(g14, g15-g19) x5
    c: PointOnObject(g14,g20)
    c: PointOnObject(g15,g20)
    c: PointOnObject(g16,g20)
    c: PointOnObject(g17,g20)
    c: PointOnObject(g18,g20)
    c: PointOnObject(g19,g20)
    c: Diameter(g20) = 7
    c: DistanceY(g-1,g20) = 7
    c: Vertical(g18)
    c: Distance(g17,g-2) = 1
    c: Coincident(g21,g22)
    c: Coincident(g22,g23)
    c: Coincident(g23,g24)
    c: Coincident(g24,g25)
    c: Coincident(g25,g26)
    c: Coincident(g26,g21)
    c: Equal(g21, g22-g26) x5
    c: PointOnObject(g21,g27)
    c: PointOnObject(g22,g27)
    c: PointOnObject(g23,g27)
    c: PointOnObject(g24,g27)
    c: PointOnObject(g25,g27)
    c: PointOnObject(g26,g27)
    c: Diameter(g27) = 7
    c: DistanceY(g-1,g27) = 7
    c: DistanceX(g21,g-1) = 1
    c: Vertical(g21)
    c: Coincident(g28,g29)
    c: Coincident(g29,g30)
    c: Coincident(g30,g31)
    c: Coincident(g31,g32)
    c: Coincident(g32,g33)
    c: Coincident(g33,g28)
    c: Equal(g28, g29-g33) x5
    c: PointOnObject(g28,g34)
    c: PointOnObject(g29,g34)
    c: PointOnObject(g30,g34)
    c: PointOnObject(g31,g34)
    c: PointOnObject(g32,g34)
    c: PointOnObject(g33,g34)
    c: PointOnObject(g34,g-1)
    c: Diameter(g34) = 7
    c: Vertical(g31)
    c: DistanceX(g34,g-1) = 8
    c: Coincident(g35,g36)
    c: Coincident(g36,g37)
    c: Coincident(g37,g38)
    c: Coincident(g38,g39)
    c: Coincident(g39,g40)
    c: Coincident(g40,g35)
    c: Equal(g35, g36-g40) x5
    c: PointOnObject(g35,g41)
    c: PointOnObject(g36,g41)
    c: PointOnObject(g37,g41)
    c: PointOnObject(g38,g41)
    c: PointOnObject(g39,g41)
    c: PointOnObject(g40,g41)
    c: Coincident(g42,g43)
    c: Coincident(g43,g44)
    c: Coincident(g44,g45)
    c: Coincident(g45,g46)
    c: Coincident(g46,g47)
    c: Coincident(g47,g42)
    c: Equal(g42, g43-g47) x5
    c: PointOnObject(g42,g48)
    c: PointOnObject(g43,g48)
    c: PointOnObject(g44,g48)
    c: PointOnObject(g45,g48)
    c: PointOnObject(g46,g48)
    c: PointOnObject(g47,g48)
    c: Equal(g41,g48)
    c: Diameter(g41) = 7
    c: Vertical(g39)
    c: Vertical(g43)
    c: Distance(g-2,g39) = 1
    c: Symmetric(g38,g43,g-2)
    c: Distance(g41,g-1) = 7
FEATURE [Part::Extrusion] Extrude446  label="hex061"
  Base = -> Sketch454
  Dir = (0,-1,2e-16)
  DirMode = 2
  FaceMakerClass = Part::FaceMakerBullseye
  FaceMakerMode = 3
  LengthFwd = 10
  LengthRev = 0
  Placement = pos=(-36,0,7) rot=(0,0,1;0rad)
  Solid = true
  Symmetric = false
FEATURE [Sketcher::SketchObject] Sketch455
  ArcFitTolerance = 1e-06
  FullyConstrained = true
  MakeInternals = false
  Placement = pos=(0,0,0) rot=(1,0,0;1.5708rad)
  sketch-geometry (49):
    g0: LineSegment StartX=1e-16 StartY=3.5 StartZ=0 EndX=-3.03109 EndY=1.75 EndZ=0
    g1: LineSegment StartX=-3.03109 StartY=1.75 StartZ=0 EndX=-3.03109 EndY=-1.75 EndZ=0
    g2: LineSegment StartX=-3.03109 StartY=-1.75 StartZ=0 EndX=-1e-16 EndY=-3.5 EndZ=0
    g3: LineSegment StartX=-1e-16 StartY=-3.5 StartZ=0 EndX=3.03109 EndY=-1.75 EndZ=0
    g4: LineSegment StartX=3.03109 StartY=-1.75 StartZ=0 EndX=3.03109 EndY=1.75 EndZ=0
    g5: LineSegment StartX=3.03109 StartY=1.75 StartZ=0 EndX=1e-16 EndY=3.5 EndZ=0
    g6: Circle [constr] CenterX=0 CenterY=0 CenterZ=0 NormalX=0 NormalY=0 NormalZ=1 AngleXU=0 Radius=3.5
    g7: LineSegment StartX=4.96892 StartY=-1.75002 StartZ=0 EndX=8.00002 EndY=-3.5 EndZ=0
    g8: LineSegment StartX=8.00002 StartY=-3.5 StartZ=0 EndX=11.0311 EndY=-1.74998 EndZ=0
    g9: LineSegment StartX=11.0311 StartY=-1.74998 StartZ=0 EndX=11.0311 EndY=1.75002 EndZ=0
    g10: LineSegment StartX=11.0311 StartY=1.75002 StartZ=0 EndX=7.99998 EndY=3.5 EndZ=0
    g11: LineSegment StartX=7.99998 StartY=3.5 StartZ=0 EndX=4.9689 EndY=1.74998 EndZ=0
    g12: LineSegment StartX=4.9689 StartY=1.74998 StartZ=0 EndX=4.96892 EndY=-1.75002 EndZ=0
    g13: Circle [constr] CenterX=8 CenterY=0 CenterZ=0 NormalX=0 NormalY=0 NormalZ=1 AngleXU=0 Radius=3.5
    g14: LineSegment StartX=4.03109 StartY=3.5 StartZ=0 EndX=7.06218 EndY=5.25 EndZ=0
    g15: LineSegment StartX=7.06218 StartY=5.25 StartZ=0 EndX=7.06218 EndY=8.75 EndZ=0
    g16: LineSegment StartX=7.06218 StartY=8.75 StartZ=0 EndX=4.03109 EndY=10.5 EndZ=0
    g17: LineSegment StartX=4.03109 StartY=10.5 StartZ=0 EndX=1 EndY=8.75 EndZ=0
    g18: LineSegment StartX=1 StartY=8.75 StartZ=0 EndX=1 EndY=5.25 EndZ=0
    g19: LineSegment StartX=1 StartY=5.25 StartZ=0 EndX=4.03109 EndY=3.5 EndZ=0
    g20: Circle [constr] CenterX=4.03109 CenterY=7 CenterZ=0 NormalX=0 NormalY=0 NormalZ=1 AngleXU=0 Radius=3.5
    g21: LineSegment StartX=-1 StartY=5.25 StartZ=0 EndX=-1 EndY=8.75 EndZ=0
    g22: LineSegment StartX=-1 StartY=8.75 StartZ=0 EndX=-4.03109 EndY=10.5 EndZ=0
    g23: LineSegment StartX=-4.03109 StartY=10.5 StartZ=0 EndX=-7.06218 EndY=8.75 EndZ=0
    g24: LineSegment StartX=-7.06218 StartY=8.75 StartZ=0 EndX=-7.06218 EndY=5.25 EndZ=0
    g25: LineSegment StartX=-7.06218 StartY=5.25 StartZ=0 EndX=-4.03109 EndY=3.5 EndZ=0
    g26: LineSegment StartX=-4.03109 StartY=3.5 StartZ=0 EndX=-1 EndY=5.25 EndZ=0
    g27: Circle [constr] CenterX=-4.03109 CenterY=7 CenterZ=0 NormalX=0 NormalY=0 NormalZ=1 AngleXU=0 Radius=3.5
    g28: LineSegment StartX=-4.96891 StartY=-1.75 StartZ=0 EndX=-4.96891 EndY=1.75 EndZ=0
    g29: LineSegment StartX=-4.96891 StartY=1.75 StartZ=0 EndX=-8 EndY=3.5 EndZ=0
    g30: LineSegment StartX=-8 StartY=3.5 StartZ=0 EndX=-11.0311 EndY=1.75 EndZ=0
    g31: LineSegment StartX=-11.0311 StartY=1.75 StartZ=0 EndX=-11.0311 EndY=-1.75 EndZ=0
    g32: LineSegment StartX=-11.0311 StartY=-1.75 StartZ=0 EndX=-8 EndY=-3.5 EndZ=0
    g33: LineSegment StartX=-8 StartY=-3.5 StartZ=0 EndX=-4.96891 EndY=-1.75 EndZ=0
    g34: Circle [constr] CenterX=-8 CenterY=0 CenterZ=0 NormalX=0 NormalY=0 NormalZ=1 AngleXU=0 Radius=3.5
    g35: LineSegment StartX=-4.03109 StartY=-3.5 StartZ=0 EndX=-7.06218 EndY=-5.25 EndZ=0
    g36: LineSegment StartX=-7.06218 StartY=-5.25 StartZ=0 EndX=-7.06218 EndY=-8.75 EndZ=0
    g37: LineSegment StartX=-7.06218 StartY=-8.75 StartZ=0 EndX=-4.03109 EndY=-10.5 EndZ=0
    g38: LineSegment StartX=-4.03109 StartY=-10.5 StartZ=0 EndX=-1 EndY=-8.75 EndZ=0
    g39: LineSegment StartX=-1 StartY=-8.75 StartZ=0 EndX=-1 EndY=-5.25 EndZ=0
    g40: LineSegment StartX=-1 StartY=-5.25 StartZ=0 EndX=-4.03109 EndY=-3.5 EndZ=0
    g41: Circle [constr] CenterX=-4.03109 CenterY=-7 CenterZ=0 NormalX=0 NormalY=0 NormalZ=1 AngleXU=0 Radius=3.5
    g42: LineSegment StartX=4.03109 StartY=-3.5 StartZ=0 EndX=1 EndY=-5.25 EndZ=0
    g43: LineSegment StartX=1 StartY=-5.25 StartZ=0 EndX=1 EndY=-8.75 EndZ=0
    g44: LineSegment StartX=1 StartY=-8.75 StartZ=0 EndX=4.03109 EndY=-10.5 EndZ=0
    g45: LineSegment StartX=4.03109 StartY=-10.5 StartZ=0 EndX=7.06218 EndY=-8.75 EndZ=0
    g46: LineSegment StartX=7.06218 StartY=-8.75 StartZ=0 EndX=7.06218 EndY=-5.25 EndZ=0
    g47: LineSegment StartX=7.06218 StartY=-5.25 StartZ=0 EndX=4.03109 EndY=-3.5 EndZ=0
    g48: Circle [constr] CenterX=4.03109 CenterY=-7 CenterZ=0 NormalX=0 NormalY=0 NormalZ=1 AngleXU=0 Radius=3.5
  constraints (117):
    c: Coincident(g0,g1)
    c: Coincident(g1,g2)
    c: Coincident(g2,g3)
    c: Coincident(g3,g4)
    c: Coincident(g4,g5)
    c: Coincident(g5,g0)
    c: Equal(g0, g1-g5) x5
    c: PointOnObject(g0,g6)
    c: PointOnObject(g1,g6)
    c: PointOnObject(g2,g6)
    c: PointOnObject(g3,g6)
    c: PointOnObject(g4,g6)
    c: PointOnObject(g5,g6)
    c: Coincident(g6,g-1)
    c: Diameter(g6) = 7
    c: PointOnObject(g0,g-2)
    c: Coincident(g7,g8)
    c: Coincident(g8,g9)
    c: Coincident(g9,g10)
    c: Coincident(g10,g11)
    c: Coincident(g11,g12)
    c: Coincident(g12,g7)
    c: Equal(g7, g8-g12) x5
    c: PointOnObject(g7,g13)
    c: PointOnObject(g8,g13)
    c: PointOnObject(g9,g13)
    c: PointOnObject(g10,g13)
    c: PointOnObject(g11,g13)
    c: PointOnObject(g12,g13)
    c: PointOnObject(g13,g-1)
    c: Diameter(g13) = 7
    c: Distance(g6,g13) = 8
    c: Horizontal(g0,g10)
    c: Coincident(g14,g15)
    c: Coincident(g15,g16)
    c: Coincident(g16,g17)
    c: Coincident(g17,g18)
    c: Coincident(g18,g19)
    c: Coincident(g19,g14)
    c: Equal(g14, g15-g19) x5
    c: PointOnObject(g14,g20)
    c: PointOnObject(g15,g20)
    c: PointOnObject(g16,g20)
    c: PointOnObject(g17,g20)
    c: PointOnObject(g18,g20)
    c: PointOnObject(g19,g20)
    c: Diameter(g20) = 7
    c: DistanceY(g-1,g20) = 7
    c: Vertical(g18)
    c: Distance(g17,g-2) = 1
    c: Coincident(g21,g22)
    c: Coincident(g22,g23)
    c: Coincident(g23,g24)
    c: Coincident(g24,g25)
    c: Coincident(g25,g26)
    c: Coincident(g26,g21)
    c: Equal(g21, g22-g26) x5
    c: PointOnObject(g21,g27)
    c: PointOnObject(g22,g27)
    c: PointOnObject(g23,g27)
    c: PointOnObject(g24,g27)
    c: PointOnObject(g25,g27)
    c: PointOnObject(g26,g27)
    c: Diameter(g27) = 7
    c: DistanceY(g-1,g27) = 7
    c: DistanceX(g21,g-1) = 1
    c: Vertical(g21)
    c: Coincident(g28,g29)
    c: Coincident(g29,g30)
    c: Coincident(g30,g31)
    c: Coincident(g31,g32)
    c: Coincident(g32,g33)
    c: Coincident(g33,g28)
    c: Equal(g28, g29-g33) x5
    c: PointOnObject(g28,g34)
    c: PointOnObject(g29,g34)
    c: PointOnObject(g30,g34)
    c: PointOnObject(g31,g34)
    c: PointOnObject(g32,g34)
    c: PointOnObject(g33,g34)
    c: PointOnObject(g34,g-1)
    c: Diameter(g34) = 7
    c: Vertical(g31)
    c: DistanceX(g34,g-1) = 8
    c: Coincident(g35,g36)
    c: Coincident(g36,g37)
    c: Coincident(g37,g38)
    c: Coincident(g38,g39)
    c: Coincident(g39,g40)
    c: Coincident(g40,g35)
    c: Equal(g35, g36-g40) x5
    c: PointOnObject(g35,g41)
    c: PointOnObject(g36,g41)
    c: PointOnObject(g37,g41)
    c: PointOnObject(g38,g41)
    c: PointOnObject(g39,g41)
    c: PointOnObject(g40,g41)
    c: Coincident(g42,g43)
    c: Coincident(g43,g44)
    c: Coincident(g44,g45)
    c: Coincident(g45,g46)
    c: Coincident(g46,g47)
    c: Coincident(g47,g42)
    c: Equal(g42, g43-g47) x5
    c: PointOnObject(g42,g48)
    c: PointOnObject(g43,g48)
    c: PointOnObject(g44,g48)
    c: PointOnObject(g45,g48)
    c: PointOnObject(g46,g48)
    c: PointOnObject(g47,g48)
    c: Equal(g41,g48)
    c: Diameter(g41) = 7
    c: Vertical(g39)
    c: Vertical(g43)
    c: Distance(g-2,g39) = 1
    c: Symmetric(g38,g43,g-2)
    c: Distance(g41,g-1) = 7
FEATURE [Part::Extrusion] Extrude447  label="hex062"
  Base = -> Sketch455
  Dir = (0,-1,2e-16)
  DirMode = 2
  FaceMakerClass = Part::FaceMakerBullseye
  FaceMakerMode = 3
  LengthFwd = 10
  LengthRev = 0
  Placement = pos=(36,0,7) rot=(0,0,1;0rad)
  Solid = true
  Symmetric = false
FEATURE [Sketcher::SketchObject] Sketch456
  ArcFitTolerance = 1e-06
  FullyConstrained = true
  MakeInternals = false
  Placement = pos=(0,0,0) rot=(1,0,0;1.5708rad)
  sketch-geometry (49):
    g0: LineSegment StartX=1e-16 StartY=3.5 StartZ=0 EndX=-3.03109 EndY=1.75 EndZ=0
    g1: LineSegment StartX=-3.03109 StartY=1.75 StartZ=0 EndX=-3.03109 EndY=-1.75 EndZ=0
    g2: LineSegment StartX=-3.03109 StartY=-1.75 StartZ=0 EndX=-1e-16 EndY=-3.5 EndZ=0
    g3: LineSegment StartX=-1e-16 StartY=-3.5 StartZ=0 EndX=3.03109 EndY=-1.75 EndZ=0
    g4: LineSegment StartX=3.03109 StartY=-1.75 StartZ=0 EndX=3.03109 EndY=1.75 EndZ=0
    g5: LineSegment StartX=3.03109 StartY=1.75 StartZ=0 EndX=1e-16 EndY=3.5 EndZ=0
    g6: Circle [constr] CenterX=0 CenterY=0 CenterZ=0 NormalX=0 NormalY=0 NormalZ=1 AngleXU=0 Radius=3.5
    g7: LineSegment StartX=4.96892 StartY=-1.75002 StartZ=0 EndX=8.00002 EndY=-3.5 EndZ=0
    g8: LineSegment StartX=8.00002 StartY=-3.5 StartZ=0 EndX=11.0311 EndY=-1.74998 EndZ=0
    g9: LineSegment StartX=11.0311 StartY=-1.74998 StartZ=0 EndX=11.0311 EndY=1.75002 EndZ=0
    g10: LineSegment StartX=11.0311 StartY=1.75002 StartZ=0 EndX=7.99998 EndY=3.5 EndZ=0
    g11: LineSegment StartX=7.99998 StartY=3.5 StartZ=0 EndX=4.9689 EndY=1.74998 EndZ=0
    g12: LineSegment StartX=4.9689 StartY=1.74998 StartZ=0 EndX=4.96892 EndY=-1.75002 EndZ=0
    g13: Circle [constr] CenterX=8 CenterY=0 CenterZ=0 NormalX=0 NormalY=0 NormalZ=1 AngleXU=0 Radius=3.5
    g14: LineSegment StartX=4.03109 StartY=3.5 StartZ=0 EndX=7.06218 EndY=5.25 EndZ=0
    g15: LineSegment StartX=7.06218 StartY=5.25 StartZ=0 EndX=7.06218 EndY=8.75 EndZ=0
    g16: LineSegment StartX=7.06218 StartY=8.75 StartZ=0 EndX=4.03109 EndY=10.5 EndZ=0
    g17: LineSegment StartX=4.03109 StartY=10.5 StartZ=0 EndX=1 EndY=8.75 EndZ=0
    g18: LineSegment StartX=1 StartY=8.75 StartZ=0 EndX=1 EndY=5.25 EndZ=0
    g19: LineSegment StartX=1 StartY=5.25 StartZ=0 EndX=4.03109 EndY=3.5 EndZ=0
    g20: Circle [constr] CenterX=4.03109 CenterY=7 CenterZ=0 NormalX=0 NormalY=0 NormalZ=1 AngleXU=0 Radius=3.5
    g21: LineSegment StartX=-1 StartY=5.25 StartZ=0 EndX=-1 EndY=8.75 EndZ=0
    g22: LineSegment StartX=-1 StartY=8.75 StartZ=0 EndX=-4.03109 EndY=10.5 EndZ=0
    g23: LineSegment StartX=-4.03109 StartY=10.5 StartZ=0 EndX=-7.06218 EndY=8.75 EndZ=0
    g24: LineSegment StartX=-7.06218 StartY=8.75 StartZ=0 EndX=-7.06218 EndY=5.25 EndZ=0
    g25: LineSegment StartX=-7.06218 StartY=5.25 StartZ=0 EndX=-4.03109 EndY=3.5 EndZ=0
    g26: LineSegment StartX=-4.03109 StartY=3.5 StartZ=0 EndX=-1 EndY=5.25 EndZ=0
    g27: Circle [constr] CenterX=-4.03109 CenterY=7 CenterZ=0 NormalX=0 NormalY=0 NormalZ=1 AngleXU=0 Radius=3.5
    g28: LineSegment StartX=-4.96891 StartY=-1.75 StartZ=0 EndX=-4.96891 EndY=1.75 EndZ=0
    g29: LineSegment StartX=-4.96891 StartY=1.75 StartZ=0 EndX=-8 EndY=3.5 EndZ=0
    g30: LineSegment StartX=-8 StartY=3.5 StartZ=0 EndX=-11.0311 EndY=1.75 EndZ=0
    g31: LineSegment StartX=-11.0311 StartY=1.75 StartZ=0 EndX=-11.0311 EndY=-1.75 EndZ=0
    g32: LineSegment StartX=-11.0311 StartY=-1.75 StartZ=0 EndX=-8 EndY=-3.5 EndZ=0
    g33: LineSegment StartX=-8 StartY=-3.5 StartZ=0 EndX=-4.96891 EndY=-1.75 EndZ=0
    g34: Circle [constr] CenterX=-8 CenterY=0 CenterZ=0 NormalX=0 NormalY=0 NormalZ=1 AngleXU=0 Radius=3.5
    g35: LineSegment StartX=-4.03109 StartY=-3.5 StartZ=0 EndX=-7.06218 EndY=-5.25 EndZ=0
    g36: LineSegment StartX=-7.06218 StartY=-5.25 StartZ=0 EndX=-7.06218 EndY=-8.75 EndZ=0
    g37: LineSegment StartX=-7.06218 StartY=-8.75 StartZ=0 EndX=-4.03109 EndY=-10.5 EndZ=0
    g38: LineSegment StartX=-4.03109 StartY=-10.5 StartZ=0 EndX=-1 EndY=-8.75 EndZ=0
    g39: LineSegment StartX=-1 StartY=-8.75 StartZ=0 EndX=-1 EndY=-5.25 EndZ=0
    g40: LineSegment StartX=-1 StartY=-5.25 StartZ=0 EndX=-4.03109 EndY=-3.5 EndZ=0
    g41: Circle [constr] CenterX=-4.03109 CenterY=-7 CenterZ=0 NormalX=0 NormalY=0 NormalZ=1 AngleXU=0 Radius=3.5
    g42: LineSegment StartX=4.03109 StartY=-3.5 StartZ=0 EndX=1 EndY=-5.25 EndZ=0
    g43: LineSegment StartX=1 StartY=-5.25 StartZ=0 EndX=1 EndY=-8.75 EndZ=0
    g44: LineSegment StartX=1 StartY=-8.75 StartZ=0 EndX=4.03109 EndY=-10.5 EndZ=0
    g45: LineSegment StartX=4.03109 StartY=-10.5 StartZ=0 EndX=7.06218 EndY=-8.75 EndZ=0
    g46: LineSegment StartX=7.06218 StartY=-8.75 StartZ=0 EndX=7.06218 EndY=-5.25 EndZ=0
    g47: LineSegment StartX=7.06218 StartY=-5.25 StartZ=0 EndX=4.03109 EndY=-3.5 EndZ=0
    g48: Circle [constr] CenterX=4.03109 CenterY=-7 CenterZ=0 NormalX=0 NormalY=0 NormalZ=1 AngleXU=0 Radius=3.5
  constraints (117):
    c: Coincident(g0,g1)
    c: Coincident(g1,g2)
    c: Coincident(g2,g3)
    c: Coincident(g3,g4)
    c: Coincident(g4,g5)
    c: Coincident(g5,g0)
    c: Equal(g0, g1-g5) x5
    c: PointOnObject(g0,g6)
    c: PointOnObject(g1,g6)
    c: PointOnObject(g2,g6)
    c: PointOnObject(g3,g6)
    c: PointOnObject(g4,g6)
    c: PointOnObject(g5,g6)
    c: Coincident(g6,g-1)
    c: Diameter(g6) = 7
    c: PointOnObject(g0,g-2)
    c: Coincident(g7,g8)
    c: Coincident(g8,g9)
    c: Coincident(g9,g10)
    c: Coincident(g10,g11)
    c: Coincident(g11,g12)
    c: Coincident(g12,g7)
    c: Equal(g7, g8-g12) x5
    c: PointOnObject(g7,g13)
    c: PointOnObject(g8,g13)
    c: PointOnObject(g9,g13)
    c: PointOnObject(g10,g13)
    c: PointOnObject(g11,g13)
    c: PointOnObject(g12,g13)
    c: PointOnObject(g13,g-1)
    c: Diameter(g13) = 7
    c: Distance(g6,g13) = 8
    c: Horizontal(g0,g10)
    c: Coincident(g14,g15)
    c: Coincident(g15,g16)
    c: Coincident(g16,g17)
    c: Coincident(g17,g18)
    c: Coincident(g18,g19)
    c: Coincident(g19,g14)
    c: Equal(g14, g15-g19) x5
    c: PointOnObject(g14,g20)
    c: PointOnObject(g15,g20)
    c: PointOnObject(g16,g20)
    c: PointOnObject(g17,g20)
    c: PointOnObject(g18,g20)
    c: PointOnObject(g19,g20)
    c: Diameter(g20) = 7
    c: DistanceY(g-1,g20) = 7
    c: Vertical(g18)
    c: Distance(g17,g-2) = 1
    c: Coincident(g21,g22)
    c: Coincident(g22,g23)
    c: Coincident(g23,g24)
    c: Coincident(g24,g25)
    c: Coincident(g25,g26)
    c: Coincident(g26,g21)
    c: Equal(g21, g22-g26) x5
    c: PointOnObject(g21,g27)
    c: PointOnObject(g22,g27)
    c: PointOnObject(g23,g27)
    c: PointOnObject(g24,g27)
    c: PointOnObject(g25,g27)
    c: PointOnObject(g26,g27)
    c: Diameter(g27) = 7
    c: DistanceY(g-1,g27) = 7
    c: DistanceX(g21,g-1) = 1
    c: Vertical(g21)
    c: Coincident(g28,g29)
    c: Coincident(g29,g30)
    c: Coincident(g30,g31)
    c: Coincident(g31,g32)
    c: Coincident(g32,g33)
    c: Coincident(g33,g28)
    c: Equal(g28, g29-g33) x5
    c: PointOnObject(g28,g34)
    c: PointOnObject(g29,g34)
    c: PointOnObject(g30,g34)
    c: PointOnObject(g31,g34)
    c: PointOnObject(g32,g34)
    c: PointOnObject(g33,g34)
    c: PointOnObject(g34,g-1)
    c: Diameter(g34) = 7
    c: Vertical(g31)
    c: DistanceX(g34,g-1) = 8
    c: Coincident(g35,g36)
    c: Coincident(g36,g37)
    c: Coincident(g37,g38)
    c: Coincident(g38,g39)
    c: Coincident(g39,g40)
    c: Coincident(g40,g35)
    c: Equal(g35, g36-g40) x5
    c: PointOnObject(g35,g41)
    c: PointOnObject(g36,g41)
    c: PointOnObject(g37,g41)
    c: PointOnObject(g38,g41)
    c: PointOnObject(g39,g41)
    c: PointOnObject(g40,g41)
    c: Coincident(g42,g43)
    c: Coincident(g43,g44)
    c: Coincident(g44,g45)
    c: Coincident(g45,g46)
    c: Coincident(g46,g47)
    c: Coincident(g47,g42)
    c: Equal(g42, g43-g47) x5
    c: PointOnObject(g42,g48)
    c: PointOnObject(g43,g48)
    c: PointOnObject(g44,g48)
    c: PointOnObject(g45,g48)
    c: PointOnObject(g46,g48)
    c: PointOnObject(g47,g48)
    c: Equal(g41,g48)
    c: Diameter(g41) = 7
    c: Vertical(g39)
    c: Vertical(g43)
    c: Distance(g-2,g39) = 1
    c: Symmetric(g38,g43,g-2)
    c: Distance(g41,g-1) = 7
FEATURE [Part::Extrusion] Extrude448  label="hex063"
  Base = -> Sketch456
  Dir = (0,-1,2e-16)
  DirMode = 2
  FaceMakerClass = Part::FaceMakerBullseye
  FaceMakerMode = 3
  LengthFwd = 10
  LengthRev = 0
  Placement = pos=(32,0,28) rot=(0,0,1;0rad)
  Solid = true
  Symmetric = false
FEATURE [Sketcher::SketchObject] Sketch457
  ArcFitTolerance = 1e-06
  FullyConstrained = true
  MakeInternals = false
  Placement = pos=(0,0,0) rot=(1,0,0;1.5708rad)
  sketch-geometry (49):
    g0: LineSegment StartX=1e-16 StartY=3.5 StartZ=0 EndX=-3.03109 EndY=1.75 EndZ=0
    g1: LineSegment StartX=-3.03109 StartY=1.75 StartZ=0 EndX=-3.03109 EndY=-1.75 EndZ=0
    g2: LineSegment StartX=-3.03109 StartY=-1.75 StartZ=0 EndX=-1e-16 EndY=-3.5 EndZ=0
    g3: LineSegment StartX=-1e-16 StartY=-3.5 StartZ=0 EndX=3.03109 EndY=-1.75 EndZ=0
    g4: LineSegment StartX=3.03109 StartY=-1.75 StartZ=0 EndX=3.03109 EndY=1.75 EndZ=0
    g5: LineSegment StartX=3.03109 StartY=1.75 StartZ=0 EndX=1e-16 EndY=3.5 EndZ=0
    g6: Circle [constr] CenterX=0 CenterY=0 CenterZ=0 NormalX=0 NormalY=0 NormalZ=1 AngleXU=0 Radius=3.5
    g7: LineSegment StartX=4.96892 StartY=-1.75002 StartZ=0 EndX=8.00002 EndY=-3.5 EndZ=0
    g8: LineSegment StartX=8.00002 StartY=-3.5 StartZ=0 EndX=11.0311 EndY=-1.74998 EndZ=0
    g9: LineSegment StartX=11.0311 StartY=-1.74998 StartZ=0 EndX=11.0311 EndY=1.75002 EndZ=0
    g10: LineSegment StartX=11.0311 StartY=1.75002 StartZ=0 EndX=7.99998 EndY=3.5 EndZ=0
    g11: LineSegment StartX=7.99998 StartY=3.5 StartZ=0 EndX=4.9689 EndY=1.74998 EndZ=0
    g12: LineSegment StartX=4.9689 StartY=1.74998 StartZ=0 EndX=4.96892 EndY=-1.75002 EndZ=0
    g13: Circle [constr] CenterX=8 CenterY=0 CenterZ=0 NormalX=0 NormalY=0 NormalZ=1 AngleXU=0 Radius=3.5
    g14: LineSegment StartX=4.03109 StartY=3.5 StartZ=0 EndX=7.06218 EndY=5.25 EndZ=0
    g15: LineSegment StartX=7.06218 StartY=5.25 StartZ=0 EndX=7.06218 EndY=8.75 EndZ=0
    g16: LineSegment StartX=7.06218 StartY=8.75 StartZ=0 EndX=4.03109 EndY=10.5 EndZ=0
    g17: LineSegment StartX=4.03109 StartY=10.5 StartZ=0 EndX=1 EndY=8.75 EndZ=0
    g18: LineSegment StartX=1 StartY=8.75 StartZ=0 EndX=1 EndY=5.25 EndZ=0
    g19: LineSegment StartX=1 StartY=5.25 StartZ=0 EndX=4.03109 EndY=3.5 EndZ=0
    g20: Circle [constr] CenterX=4.03109 CenterY=7 CenterZ=0 NormalX=0 NormalY=0 NormalZ=1 AngleXU=0 Radius=3.5
    g21: LineSegment StartX=-1 StartY=5.25 StartZ=0 EndX=-1 EndY=8.75 EndZ=0
    g22: LineSegment StartX=-1 StartY=8.75 StartZ=0 EndX=-4.03109 EndY=10.5 EndZ=0
    g23: LineSegment StartX=-4.03109 StartY=10.5 StartZ=0 EndX=-7.06218 EndY=8.75 EndZ=0
    g24: LineSegment StartX=-7.06218 StartY=8.75 StartZ=0 EndX=-7.06218 EndY=5.25 EndZ=0
    g25: LineSegment StartX=-7.06218 StartY=5.25 StartZ=0 EndX=-4.03109 EndY=3.5 EndZ=0
    g26: LineSegment StartX=-4.03109 StartY=3.5 StartZ=0 EndX=-1 EndY=5.25 EndZ=0
    g27: Circle [constr] CenterX=-4.03109 CenterY=7 CenterZ=0 NormalX=0 NormalY=0 NormalZ=1 AngleXU=0 Radius=3.5
    g28: LineSegment StartX=-4.96891 StartY=-1.75 StartZ=0 EndX=-4.96891 EndY=1.75 EndZ=0
    g29: LineSegment StartX=-4.96891 StartY=1.75 StartZ=0 EndX=-8 EndY=3.5 EndZ=0
    g30: LineSegment StartX=-8 StartY=3.5 StartZ=0 EndX=-11.0311 EndY=1.75 EndZ=0
    g31: LineSegment StartX=-11.0311 StartY=1.75 StartZ=0 EndX=-11.0311 EndY=-1.75 EndZ=0
    g32: LineSegment StartX=-11.0311 StartY=-1.75 StartZ=0 EndX=-8 EndY=-3.5 EndZ=0
    g33: LineSegment StartX=-8 StartY=-3.5 StartZ=0 EndX=-4.96891 EndY=-1.75 EndZ=0
    g34: Circle [constr] CenterX=-8 CenterY=0 CenterZ=0 NormalX=0 NormalY=0 NormalZ=1 AngleXU=0 Radius=3.5
    g35: LineSegment StartX=-4.03109 StartY=-3.5 StartZ=0 EndX=-7.06218 EndY=-5.25 EndZ=0
    g36: LineSegment StartX=-7.06218 StartY=-5.25 StartZ=0 EndX=-7.06218 EndY=-8.75 EndZ=0
    g37: LineSegment StartX=-7.06218 StartY=-8.75 StartZ=0 EndX=-4.03109 EndY=-10.5 EndZ=0
    g38: LineSegment StartX=-4.03109 StartY=-10.5 StartZ=0 EndX=-1 EndY=-8.75 EndZ=0
    g39: LineSegment StartX=-1 StartY=-8.75 StartZ=0 EndX=-1 EndY=-5.25 EndZ=0
    g40: LineSegment StartX=-1 StartY=-5.25 StartZ=0 EndX=-4.03109 EndY=-3.5 EndZ=0
    g41: Circle [constr] CenterX=-4.03109 CenterY=-7 CenterZ=0 NormalX=0 NormalY=0 NormalZ=1 AngleXU=0 Radius=3.5
    g42: LineSegment StartX=4.03109 StartY=-3.5 StartZ=0 EndX=1 EndY=-5.25 EndZ=0
    g43: LineSegment StartX=1 StartY=-5.25 StartZ=0 EndX=1 EndY=-8.75 EndZ=0
    g44: LineSegment StartX=1 StartY=-8.75 StartZ=0 EndX=4.03109 EndY=-10.5 EndZ=0
    g45: LineSegment StartX=4.03109 StartY=-10.5 StartZ=0 EndX=7.06218 EndY=-8.75 EndZ=0
    g46: LineSegment StartX=7.06218 StartY=-8.75 StartZ=0 EndX=7.06218 EndY=-5.25 EndZ=0
    g47: LineSegment StartX=7.06218 StartY=-5.25 StartZ=0 EndX=4.03109 EndY=-3.5 EndZ=0
    g48: Circle [constr] CenterX=4.03109 CenterY=-7 CenterZ=0 NormalX=0 NormalY=0 NormalZ=1 AngleXU=0 Radius=3.5
  constraints (117):
    c: Coincident(g0,g1)
    c: Coincident(g1,g2)
    c: Coincident(g2,g3)
    c: Coincident(g3,g4)
    c: Coincident(g4,g5)
    c: Coincident(g5,g0)
    c: Equal(g0, g1-g5) x5
    c: PointOnObject(g0,g6)
    c: PointOnObject(g1,g6)
    c: PointOnObject(g2,g6)
    c: PointOnObject(g3,g6)
    c: PointOnObject(g4,g6)
    c: PointOnObject(g5,g6)
    c: Coincident(g6,g-1)
    c: Diameter(g6) = 7
    c: PointOnObject(g0,g-2)
    c: Coincident(g7,g8)
    c: Coincident(g8,g9)
    c: Coincident(g9,g10)
    c: Coincident(g10,g11)
    c: Coincident(g11,g12)
    c: Coincident(g12,g7)
    c: Equal(g7, g8-g12) x5
    c: PointOnObject(g7,g13)
    c: PointOnObject(g8,g13)
    c: PointOnObject(g9,g13)
    c: PointOnObject(g10,g13)
    c: PointOnObject(g11,g13)
    c: PointOnObject(g12,g13)
    c: PointOnObject(g13,g-1)
    c: Diameter(g13) = 7
    c: Distance(g6,g13) = 8
    c: Horizontal(g0,g10)
    c: Coincident(g14,g15)
    c: Coincident(g15,g16)
    c: Coincident(g16,g17)
    c: Coincident(g17,g18)
    c: Coincident(g18,g19)
    c: Coincident(g19,g14)
    c: Equal(g14, g15-g19) x5
    c: PointOnObject(g14,g20)
    c: PointOnObject(g15,g20)
    c: PointOnObject(g16,g20)
    c: PointOnObject(g17,g20)
    c: PointOnObject(g18,g20)
    c: PointOnObject(g19,g20)
    c: Diameter(g20) = 7
    c: DistanceY(g-1,g20) = 7
    c: Vertical(g18)
    c: Distance(g17,g-2) = 1
    c: Coincident(g21,g22)
    c: Coincident(g22,g23)
    c: Coincident(g23,g24)
    c: Coincident(g24,g25)
    c: Coincident(g25,g26)
    c: Coincident(g26,g21)
    c: Equal(g21, g22-g26) x5
    c: PointOnObject(g21,g27)
    c: PointOnObject(g22,g27)
    c: PointOnObject(g23,g27)
    c: PointOnObject(g24,g27)
    c: PointOnObject(g25,g27)
    c: PointOnObject(g26,g27)
    c: Diameter(g27) = 7
    c: DistanceY(g-1,g27) = 7
    c: DistanceX(g21,g-1) = 1
    c: Vertical(g21)
    c: Coincident(g28,g29)
    c: Coincident(g29,g30)
    c: Coincident(g30,g31)
    c: Coincident(g31,g32)
    c: Coincident(g32,g33)
    c: Coincident(g33,g28)
    c: Equal(g28, g29-g33) x5
    c: PointOnObject(g28,g34)
    c: PointOnObject(g29,g34)
    c: PointOnObject(g30,g34)
    c: PointOnObject(g31,g34)
    c: PointOnObject(g32,g34)
    c: PointOnObject(g33,g34)
    c: PointOnObject(g34,g-1)
    c: Diameter(g34) = 7
    c: Vertical(g31)
    c: DistanceX(g34,g-1) = 8
    c: Coincident(g35,g36)
    c: Coincident(g36,g37)
    c: Coincident(g37,g38)
    c: Coincident(g38,g39)
    c: Coincident(g39,g40)
    c: Coincident(g40,g35)
    c: Equal(g35, g36-g40) x5
    c: PointOnObject(g35,g41)
    c: PointOnObject(g36,g41)
    c: PointOnObject(g37,g41)
    c: PointOnObject(g38,g41)
    c: PointOnObject(g39,g41)
    c: PointOnObject(g40,g41)
    c: Coincident(g42,g43)
    c: Coincident(g43,g44)
    c: Coincident(g44,g45)
    c: Coincident(g45,g46)
    c: Coincident(g46,g47)
    c: Coincident(g47,g42)
    c: Equal(g42, g43-g47) x5
    c: PointOnObject(g42,g48)
    c: PointOnObject(g43,g48)
    c: PointOnObject(g44,g48)
    c: PointOnObject(g45,g48)
    c: PointOnObject(g46,g48)
    c: PointOnObject(g47,g48)
    c: Equal(g41,g48)
    c: Diameter(g41) = 7
    c: Vertical(g39)
    c: Vertical(g43)
    c: Distance(g-2,g39) = 1
    c: Symmetric(g38,g43,g-2)
    c: Distance(g41,g-1) = 7
FEATURE [Part::Extrusion] Extrude449  label="hex064"
  Base = -> Sketch457
  Dir = (0,-1,2e-16)
  DirMode = 2
  FaceMakerClass = Part::FaceMakerBullseye
  FaceMakerMode = 3
  LengthFwd = 10
  LengthRev = 0
  Placement = pos=(-40,0,-14) rot=(0,0,1;0rad)
  Solid = true
  Symmetric = false
FEATURE [Sketcher::SketchObject] Sketch458
  ArcFitTolerance = 1e-06
  FullyConstrained = true
  MakeInternals = false
  Placement = pos=(0,0,0) rot=(1,0,0;1.5708rad)
  sketch-geometry (49):
    g0: LineSegment StartX=1e-16 StartY=3.5 StartZ=0 EndX=-3.03109 EndY=1.75 EndZ=0
    g1: LineSegment StartX=-3.03109 StartY=1.75 StartZ=0 EndX=-3.03109 EndY=-1.75 EndZ=0
    g2: LineSegment StartX=-3.03109 StartY=-1.75 StartZ=0 EndX=-1e-16 EndY=-3.5 EndZ=0
    g3: LineSegment StartX=-1e-16 StartY=-3.5 StartZ=0 EndX=3.03109 EndY=-1.75 EndZ=0
    g4: LineSegment StartX=3.03109 StartY=-1.75 StartZ=0 EndX=3.03109 EndY=1.75 EndZ=0
    g5: LineSegment StartX=3.03109 StartY=1.75 StartZ=0 EndX=1e-16 EndY=3.5 EndZ=0
    g6: Circle [constr] CenterX=0 CenterY=0 CenterZ=0 NormalX=0 NormalY=0 NormalZ=1 AngleXU=0 Radius=3.5
    g7: LineSegment StartX=4.96892 StartY=-1.75002 StartZ=0 EndX=8.00002 EndY=-3.5 EndZ=0
    g8: LineSegment StartX=8.00002 StartY=-3.5 StartZ=0 EndX=11.0311 EndY=-1.74998 EndZ=0
    g9: LineSegment StartX=11.0311 StartY=-1.74998 StartZ=0 EndX=11.0311 EndY=1.75002 EndZ=0
    g10: LineSegment StartX=11.0311 StartY=1.75002 StartZ=0 EndX=7.99998 EndY=3.5 EndZ=0
    g11: LineSegment StartX=7.99998 StartY=3.5 StartZ=0 EndX=4.9689 EndY=1.74998 EndZ=0
    g12: LineSegment StartX=4.9689 StartY=1.74998 StartZ=0 EndX=4.96892 EndY=-1.75002 EndZ=0
    g13: Circle [constr] CenterX=8 CenterY=0 CenterZ=0 NormalX=0 NormalY=0 NormalZ=1 AngleXU=0 Radius=3.5
    g14: LineSegment StartX=4.03109 StartY=3.5 StartZ=0 EndX=7.06218 EndY=5.25 EndZ=0
    g15: LineSegment StartX=7.06218 StartY=5.25 StartZ=0 EndX=7.06218 EndY=8.75 EndZ=0
    g16: LineSegment StartX=7.06218 StartY=8.75 StartZ=0 EndX=4.03109 EndY=10.5 EndZ=0
    g17: LineSegment StartX=4.03109 StartY=10.5 StartZ=0 EndX=1 EndY=8.75 EndZ=0
    g18: LineSegment StartX=1 StartY=8.75 StartZ=0 EndX=1 EndY=5.25 EndZ=0
    g19: LineSegment StartX=1 StartY=5.25 StartZ=0 EndX=4.03109 EndY=3.5 EndZ=0
    g20: Circle [constr] CenterX=4.03109 CenterY=7 CenterZ=0 NormalX=0 NormalY=0 NormalZ=1 AngleXU=0 Radius=3.5
    g21: LineSegment StartX=-1 StartY=5.25 StartZ=0 EndX=-1 EndY=8.75 EndZ=0
    g22: LineSegment StartX=-1 StartY=8.75 StartZ=0 EndX=-4.03109 EndY=10.5 EndZ=0
    g23: LineSegment StartX=-4.03109 StartY=10.5 StartZ=0 EndX=-7.06218 EndY=8.75 EndZ=0
    g24: LineSegment StartX=-7.06218 StartY=8.75 StartZ=0 EndX=-7.06218 EndY=5.25 EndZ=0
    g25: LineSegment StartX=-7.06218 StartY=5.25 StartZ=0 EndX=-4.03109 EndY=3.5 EndZ=0
    g26: LineSegment StartX=-4.03109 StartY=3.5 StartZ=0 EndX=-1 EndY=5.25 EndZ=0
    g27: Circle [constr] CenterX=-4.03109 CenterY=7 CenterZ=0 NormalX=0 NormalY=0 NormalZ=1 AngleXU=0 Radius=3.5
    g28: LineSegment StartX=-4.96891 StartY=-1.75 StartZ=0 EndX=-4.96891 EndY=1.75 EndZ=0
    g29: LineSegment StartX=-4.96891 StartY=1.75 StartZ=0 EndX=-8 EndY=3.5 EndZ=0
    g30: LineSegment StartX=-8 StartY=3.5 StartZ=0 EndX=-11.0311 EndY=1.75 EndZ=0
    g31: LineSegment StartX=-11.0311 StartY=1.75 StartZ=0 EndX=-11.0311 EndY=-1.75 EndZ=0
    g32: LineSegment StartX=-11.0311 StartY=-1.75 StartZ=0 EndX=-8 EndY=-3.5 EndZ=0
    g33: LineSegment StartX=-8 StartY=-3.5 StartZ=0 EndX=-4.96891 EndY=-1.75 EndZ=0
    g34: Circle [constr] CenterX=-8 CenterY=0 CenterZ=0 NormalX=0 NormalY=0 NormalZ=1 AngleXU=0 Radius=3.5
    g35: LineSegment StartX=-4.03109 StartY=-3.5 StartZ=0 EndX=-7.06218 EndY=-5.25 EndZ=0
    g36: LineSegment StartX=-7.06218 StartY=-5.25 StartZ=0 EndX=-7.06218 EndY=-8.75 EndZ=0
    g37: LineSegment StartX=-7.06218 StartY=-8.75 StartZ=0 EndX=-4.03109 EndY=-10.5 EndZ=0
    g38: LineSegment StartX=-4.03109 StartY=-10.5 StartZ=0 EndX=-1 EndY=-8.75 EndZ=0
    g39: LineSegment StartX=-1 StartY=-8.75 StartZ=0 EndX=-1 EndY=-5.25 EndZ=0
    g40: LineSegment StartX=-1 StartY=-5.25 StartZ=0 EndX=-4.03109 EndY=-3.5 EndZ=0
    g41: Circle [constr] CenterX=-4.03109 CenterY=-7 CenterZ=0 NormalX=0 NormalY=0 NormalZ=1 AngleXU=0 Radius=3.5
    g42: LineSegment StartX=4.03109 StartY=-3.5 StartZ=0 EndX=1 EndY=-5.25 EndZ=0
    g43: LineSegment StartX=1 StartY=-5.25 StartZ=0 EndX=1 EndY=-8.75 EndZ=0
    g44: LineSegment StartX=1 StartY=-8.75 StartZ=0 EndX=4.03109 EndY=-10.5 EndZ=0
    g45: LineSegment StartX=4.03109 StartY=-10.5 StartZ=0 EndX=7.06218 EndY=-8.75 EndZ=0
    g46: LineSegment StartX=7.06218 StartY=-8.75 StartZ=0 EndX=7.06218 EndY=-5.25 EndZ=0
    g47: LineSegment StartX=7.06218 StartY=-5.25 StartZ=0 EndX=4.03109 EndY=-3.5 EndZ=0
    g48: Circle [constr] CenterX=4.03109 CenterY=-7 CenterZ=0 NormalX=0 NormalY=0 NormalZ=1 AngleXU=0 Radius=3.5
  constraints (117):
    c: Coincident(g0,g1)
    c: Coincident(g1,g2)
    c: Coincident(g2,g3)
    c: Coincident(g3,g4)
    c: Coincident(g4,g5)
    c: Coincident(g5,g0)
    c: Equal(g0, g1-g5) x5
    c: PointOnObject(g0,g6)
    c: PointOnObject(g1,g6)
    c: PointOnObject(g2,g6)
    c: PointOnObject(g3,g6)
    c: PointOnObject(g4,g6)
    c: PointOnObject(g5,g6)
    c: Coincident(g6,g-1)
    c: Diameter(g6) = 7
    c: PointOnObject(g0,g-2)
    c: Coincident(g7,g8)
    c: Coincident(g8,g9)
    c: Coincident(g9,g10)
    c: Coincident(g10,g11)
    c: Coincident(g11,g12)
    c: Coincident(g12,g7)
    c: Equal(g7, g8-g12) x5
    c: PointOnObject(g7,g13)
    c: PointOnObject(g8,g13)
    c: PointOnObject(g9,g13)
    c: PointOnObject(g10,g13)
    c: PointOnObject(g11,g13)
    c: PointOnObject(g12,g13)
    c: PointOnObject(g13,g-1)
    c: Diameter(g13) = 7
    c: Distance(g6,g13) = 8
    c: Horizontal(g0,g10)
    c: Coincident(g14,g15)
    c: Coincident(g15,g16)
    c: Coincident(g16,g17)
    c: Coincident(g17,g18)
    c: Coincident(g18,g19)
    c: Coincident(g19,g14)
    c: Equal(g14, g15-g19) x5
    c: PointOnObject(g14,g20)
    c: PointOnObject(g15,g20)
    c: PointOnObject(g16,g20)
    c: PointOnObject(g17,g20)
    c: PointOnObject(g18,g20)
    c: PointOnObject(g19,g20)
    c: Diameter(g20) = 7
    c: DistanceY(g-1,g20) = 7
    c: Vertical(g18)
    c: Distance(g17,g-2) = 1
    c: Coincident(g21,g22)
    c: Coincident(g22,g23)
    c: Coincident(g23,g24)
    c: Coincident(g24,g25)
    c: Coincident(g25,g26)
    c: Coincident(g26,g21)
    c: Equal(g21, g22-g26) x5
    c: PointOnObject(g21,g27)
    c: PointOnObject(g22,g27)
    c: PointOnObject(g23,g27)
    c: PointOnObject(g24,g27)
    c: PointOnObject(g25,g27)
    c: PointOnObject(g26,g27)
    c: Diameter(g27) = 7
    c: DistanceY(g-1,g27) = 7
    c: DistanceX(g21,g-1) = 1
    c: Vertical(g21)
    c: Coincident(g28,g29)
    c: Coincident(g29,g30)
    c: Coincident(g30,g31)
    c: Coincident(g31,g32)
    c: Coincident(g32,g33)
    c: Coincident(g33,g28)
    c: Equal(g28, g29-g33) x5
    c: PointOnObject(g28,g34)
    c: PointOnObject(g29,g34)
    c: PointOnObject(g30,g34)
    c: PointOnObject(g31,g34)
    c: PointOnObject(g32,g34)
    c: PointOnObject(g33,g34)
    c: PointOnObject(g34,g-1)
    c: Diameter(g34) = 7
    c: Vertical(g31)
    c: DistanceX(g34,g-1) = 8
    c: Coincident(g35,g36)
    c: Coincident(g36,g37)
    c: Coincident(g37,g38)
    c: Coincident(g38,g39)
    c: Coincident(g39,g40)
    c: Coincident(g40,g35)
    c: Equal(g35, g36-g40) x5
    c: PointOnObject(g35,g41)
    c: PointOnObject(g36,g41)
    c: PointOnObject(g37,g41)
    c: PointOnObject(g38,g41)
    c: PointOnObject(g39,g41)
    c: PointOnObject(g40,g41)
    c: Coincident(g42,g43)
    c: Coincident(g43,g44)
    c: Coincident(g44,g45)
    c: Coincident(g45,g46)
    c: Coincident(g46,g47)
    c: Coincident(g47,g42)
    c: Equal(g42, g43-g47) x5
    c: PointOnObject(g42,g48)
    c: PointOnObject(g43,g48)
    c: PointOnObject(g44,g48)
    c: PointOnObject(g45,g48)
    c: PointOnObject(g46,g48)
    c: PointOnObject(g47,g48)
    c: Equal(g41,g48)
    c: Diameter(g41) = 7
    c: Vertical(g39)
    c: Vertical(g43)
    c: Distance(g-2,g39) = 1
    c: Symmetric(g38,g43,g-2)
    c: Distance(g41,g-1) = 7
FEATURE [Part::Extrusion] Extrude450  label="hex065"
  Base = -> Sketch458
  Dir = (0,-1,2e-16)
  DirMode = 2
  FaceMakerClass = Part::FaceMakerBullseye
  FaceMakerMode = 3
  LengthFwd = 10
  LengthRev = 0
  Placement = pos=(-24,0,-28) rot=(0,0,1;0rad)
  Solid = true
  Symmetric = false
FEATURE [Sketcher::SketchObject] Sketch459
  ArcFitTolerance = 1e-06
  FullyConstrained = true
  MakeInternals = false
  Placement = pos=(0,0,0) rot=(1,0,0;1.5708rad)
  sketch-geometry (49):
    g0: LineSegment StartX=1e-16 StartY=3.5 StartZ=0 EndX=-3.03109 EndY=1.75 EndZ=0
    g1: LineSegment StartX=-3.03109 StartY=1.75 StartZ=0 EndX=-3.03109 EndY=-1.75 EndZ=0
    g2: LineSegment StartX=-3.03109 StartY=-1.75 StartZ=0 EndX=-1e-16 EndY=-3.5 EndZ=0
    g3: LineSegment StartX=-1e-16 StartY=-3.5 StartZ=0 EndX=3.03109 EndY=-1.75 EndZ=0
    g4: LineSegment StartX=3.03109 StartY=-1.75 StartZ=0 EndX=3.03109 EndY=1.75 EndZ=0
    g5: LineSegment StartX=3.03109 StartY=1.75 StartZ=0 EndX=1e-16 EndY=3.5 EndZ=0
    g6: Circle [constr] CenterX=0 CenterY=0 CenterZ=0 NormalX=0 NormalY=0 NormalZ=1 AngleXU=0 Radius=3.5
    g7: LineSegment StartX=4.96892 StartY=-1.75002 StartZ=0 EndX=8.00002 EndY=-3.5 EndZ=0
    g8: LineSegment StartX=8.00002 StartY=-3.5 StartZ=0 EndX=11.0311 EndY=-1.74998 EndZ=0
    g9: LineSegment StartX=11.0311 StartY=-1.74998 StartZ=0 EndX=11.0311 EndY=1.75002 EndZ=0
    g10: LineSegment StartX=11.0311 StartY=1.75002 StartZ=0 EndX=7.99998 EndY=3.5 EndZ=0
    g11: LineSegment StartX=7.99998 StartY=3.5 StartZ=0 EndX=4.9689 EndY=1.74998 EndZ=0
    g12: LineSegment StartX=4.9689 StartY=1.74998 StartZ=0 EndX=4.96892 EndY=-1.75002 EndZ=0
    g13: Circle [constr] CenterX=8 CenterY=0 CenterZ=0 NormalX=0 NormalY=0 NormalZ=1 AngleXU=0 Radius=3.5
    g14: LineSegment StartX=4.03109 StartY=3.5 StartZ=0 EndX=7.06218 EndY=5.25 EndZ=0
    g15: LineSegment StartX=7.06218 StartY=5.25 StartZ=0 EndX=7.06218 EndY=8.75 EndZ=0
    g16: LineSegment StartX=7.06218 StartY=8.75 StartZ=0 EndX=4.03109 EndY=10.5 EndZ=0
    g17: LineSegment StartX=4.03109 StartY=10.5 StartZ=0 EndX=1 EndY=8.75 EndZ=0
    g18: LineSegment StartX=1 StartY=8.75 StartZ=0 EndX=1 EndY=5.25 EndZ=0
    g19: LineSegment StartX=1 StartY=5.25 StartZ=0 EndX=4.03109 EndY=3.5 EndZ=0
    g20: Circle [constr] CenterX=4.03109 CenterY=7 CenterZ=0 NormalX=0 NormalY=0 NormalZ=1 AngleXU=0 Radius=3.5
    g21: LineSegment StartX=-1 StartY=5.25 StartZ=0 EndX=-1 EndY=8.75 EndZ=0
    g22: LineSegment StartX=-1 StartY=8.75 StartZ=0 EndX=-4.03109 EndY=10.5 EndZ=0
    g23: LineSegment StartX=-4.03109 StartY=10.5 StartZ=0 EndX=-7.06218 EndY=8.75 EndZ=0
    g24: LineSegment StartX=-7.06218 StartY=8.75 StartZ=0 EndX=-7.06218 EndY=5.25 EndZ=0
    g25: LineSegment StartX=-7.06218 StartY=5.25 StartZ=0 EndX=-4.03109 EndY=3.5 EndZ=0
    g26: LineSegment StartX=-4.03109 StartY=3.5 StartZ=0 EndX=-1 EndY=5.25 EndZ=0
    g27: Circle [constr] CenterX=-4.03109 CenterY=7 CenterZ=0 NormalX=0 NormalY=0 NormalZ=1 AngleXU=0 Radius=3.5
    g28: LineSegment StartX=-4.96891 StartY=-1.75 StartZ=0 EndX=-4.96891 EndY=1.75 EndZ=0
    g29: LineSegment StartX=-4.96891 StartY=1.75 StartZ=0 EndX=-8 EndY=3.5 EndZ=0
    g30: LineSegment StartX=-8 StartY=3.5 StartZ=0 EndX=-11.0311 EndY=1.75 EndZ=0
    g31: LineSegment StartX=-11.0311 StartY=1.75 StartZ=0 EndX=-11.0311 EndY=-1.75 EndZ=0
    g32: LineSegment StartX=-11.0311 StartY=-1.75 StartZ=0 EndX=-8 EndY=-3.5 EndZ=0
    g33: LineSegment StartX=-8 StartY=-3.5 StartZ=0 EndX=-4.96891 EndY=-1.75 EndZ=0
    g34: Circle [constr] CenterX=-8 CenterY=0 CenterZ=0 NormalX=0 NormalY=0 NormalZ=1 AngleXU=0 Radius=3.5
    g35: LineSegment StartX=-4.03109 StartY=-3.5 StartZ=0 EndX=-7.06218 EndY=-5.25 EndZ=0
    g36: LineSegment StartX=-7.06218 StartY=-5.25 StartZ=0 EndX=-7.06218 EndY=-8.75 EndZ=0
    g37: LineSegment StartX=-7.06218 StartY=-8.75 StartZ=0 EndX=-4.03109 EndY=-10.5 EndZ=0
    g38: LineSegment StartX=-4.03109 StartY=-10.5 StartZ=0 EndX=-1 EndY=-8.75 EndZ=0
    g39: LineSegment StartX=-1 StartY=-8.75 StartZ=0 EndX=-1 EndY=-5.25 EndZ=0
    g40: LineSegment StartX=-1 StartY=-5.25 StartZ=0 EndX=-4.03109 EndY=-3.5 EndZ=0
    g41: Circle [constr] CenterX=-4.03109 CenterY=-7 CenterZ=0 NormalX=0 NormalY=0 NormalZ=1 AngleXU=0 Radius=3.5
    g42: LineSegment StartX=4.03109 StartY=-3.5 StartZ=0 EndX=1 EndY=-5.25 EndZ=0
    g43: LineSegment StartX=1 StartY=-5.25 StartZ=0 EndX=1 EndY=-8.75 EndZ=0
    g44: LineSegment StartX=1 StartY=-8.75 StartZ=0 EndX=4.03109 EndY=-10.5 EndZ=0
    g45: LineSegment StartX=4.03109 StartY=-10.5 StartZ=0 EndX=7.06218 EndY=-8.75 EndZ=0
    g46: LineSegment StartX=7.06218 StartY=-8.75 StartZ=0 EndX=7.06218 EndY=-5.25 EndZ=0
    g47: LineSegment StartX=7.06218 StartY=-5.25 StartZ=0 EndX=4.03109 EndY=-3.5 EndZ=0
    g48: Circle [constr] CenterX=4.03109 CenterY=-7 CenterZ=0 NormalX=0 NormalY=0 NormalZ=1 AngleXU=0 Radius=3.5
  constraints (117):
    c: Coincident(g0,g1)
    c: Coincident(g1,g2)
    c: Coincident(g2,g3)
    c: Coincident(g3,g4)
    c: Coincident(g4,g5)
    c: Coincident(g5,g0)
    c: Equal(g0, g1-g5) x5
    c: PointOnObject(g0,g6)
    c: PointOnObject(g1,g6)
    c: PointOnObject(g2,g6)
    c: PointOnObject(g3,g6)
    c: PointOnObject(g4,g6)
    c: PointOnObject(g5,g6)
    c: Coincident(g6,g-1)
    c: Diameter(g6) = 7
    c: PointOnObject(g0,g-2)
    c: Coincident(g7,g8)
    c: Coincident(g8,g9)
    c: Coincident(g9,g10)
    c: Coincident(g10,g11)
    c: Coincident(g11,g12)
    c: Coincident(g12,g7)
    c: Equal(g7, g8-g12) x5
    c: PointOnObject(g7,g13)
    c: PointOnObject(g8,g13)
    c: PointOnObject(g9,g13)
    c: PointOnObject(g10,g13)
    c: PointOnObject(g11,g13)
    c: PointOnObject(g12,g13)
    c: PointOnObject(g13,g-1)
    c: Diameter(g13) = 7
    c: Distance(g6,g13) = 8
    c: Horizontal(g0,g10)
    c: Coincident(g14,g15)
    c: Coincident(g15,g16)
    c: Coincident(g16,g17)
    c: Coincident(g17,g18)
    c: Coincident(g18,g19)
    c: Coincident(g19,g14)
    c: Equal(g14, g15-g19) x5
    c: PointOnObject(g14,g20)
    c: PointOnObject(g15,g20)
    c: PointOnObject(g16,g20)
    c: PointOnObject(g17,g20)
    c: PointOnObject(g18,g20)
    c: PointOnObject(g19,g20)
    c: Diameter(g20) = 7
    c: DistanceY(g-1,g20) = 7
    c: Vertical(g18)
    c: Distance(g17,g-2) = 1
    c: Coincident(g21,g22)
    c: Coincident(g22,g23)
    c: Coincident(g23,g24)
    c: Coincident(g24,g25)
    c: Coincident(g25,g26)
    c: Coincident(g26,g21)
    c: Equal(g21, g22-g26) x5
    c: PointOnObject(g21,g27)
    c: PointOnObject(g22,g27)
    c: PointOnObject(g23,g27)
    c: PointOnObject(g24,g27)
    c: PointOnObject(g25,g27)
    c: PointOnObject(g26,g27)
    c: Diameter(g27) = 7
    c: DistanceY(g-1,g27) = 7
    c: DistanceX(g21,g-1) = 1
    c: Vertical(g21)
    c: Coincident(g28,g29)
    c: Coincident(g29,g30)
    c: Coincident(g30,g31)
    c: Coincident(g31,g32)
    c: Coincident(g32,g33)
    c: Coincident(g33,g28)
    c: Equal(g28, g29-g33) x5
    c: PointOnObject(g28,g34)
    c: PointOnObject(g29,g34)
    c: PointOnObject(g30,g34)
    c: PointOnObject(g31,g34)
    c: PointOnObject(g32,g34)
    c: PointOnObject(g33,g34)
    c: PointOnObject(g34,g-1)
    c: Diameter(g34) = 7
    c: Vertical(g31)
    c: DistanceX(g34,g-1) = 8
    c: Coincident(g35,g36)
    c: Coincident(g36,g37)
    c: Coincident(g37,g38)
    c: Coincident(g38,g39)
    c: Coincident(g39,g40)
    c: Coincident(g40,g35)
    c: Equal(g35, g36-g40) x5
    c: PointOnObject(g35,g41)
    c: PointOnObject(g36,g41)
    c: PointOnObject(g37,g41)
    c: PointOnObject(g38,g41)
    c: PointOnObject(g39,g41)
    c: PointOnObject(g40,g41)
    c: Coincident(g42,g43)
    c: Coincident(g43,g44)
    c: Coincident(g44,g45)
    c: Coincident(g45,g46)
    c: Coincident(g46,g47)
    c: Coincident(g47,g42)
    c: Equal(g42, g43-g47) x5
    c: PointOnObject(g42,g48)
    c: PointOnObject(g43,g48)
    c: PointOnObject(g44,g48)
    c: PointOnObject(g45,g48)
    c: PointOnObject(g46,g48)
    c: PointOnObject(g47,g48)
    c: Equal(g41,g48)
    c: Diameter(g41) = 7
    c: Vertical(g39)
    c: Vertical(g43)
    c: Distance(g-2,g39) = 1
    c: Symmetric(g38,g43,g-2)
    c: Distance(g41,g-1) = 7
FEATURE [Part::Extrusion] Extrude451  label="hex066"
  Base = -> Sketch459
  Dir = (0,-1,2e-16)
  DirMode = 2
  FaceMakerClass = Part::FaceMakerBullseye
  FaceMakerMode = 3
  LengthFwd = 10
  LengthRev = 0
  Placement = pos=(-8,0,-42) rot=(0,0,1;0rad)
  Solid = true
  Symmetric = false
FEATURE [Sketcher::SketchObject] Sketch460
  ArcFitTolerance = 1e-06
  FullyConstrained = true
  MakeInternals = false
  Placement = pos=(0,0,0) rot=(1,0,0;1.5708rad)
  sketch-geometry (49):
    g0: LineSegment StartX=1e-16 StartY=3.5 StartZ=0 EndX=-3.03109 EndY=1.75 EndZ=0
    g1: LineSegment StartX=-3.03109 StartY=1.75 StartZ=0 EndX=-3.03109 EndY=-1.75 EndZ=0
    g2: LineSegment StartX=-3.03109 StartY=-1.75 StartZ=0 EndX=-1e-16 EndY=-3.5 EndZ=0
    g3: LineSegment StartX=-1e-16 StartY=-3.5 StartZ=0 EndX=3.03109 EndY=-1.75 EndZ=0
    g4: LineSegment StartX=3.03109 StartY=-1.75 StartZ=0 EndX=3.03109 EndY=1.75 EndZ=0
    g5: LineSegment StartX=3.03109 StartY=1.75 StartZ=0 EndX=1e-16 EndY=3.5 EndZ=0
    g6: Circle [constr] CenterX=0 CenterY=0 CenterZ=0 NormalX=0 NormalY=0 NormalZ=1 AngleXU=0 Radius=3.5
    g7: LineSegment StartX=4.96892 StartY=-1.75002 StartZ=0 EndX=8.00002 EndY=-3.5 EndZ=0
    g8: LineSegment StartX=8.00002 StartY=-3.5 StartZ=0 EndX=11.0311 EndY=-1.74998 EndZ=0
    g9: LineSegment StartX=11.0311 StartY=-1.74998 StartZ=0 EndX=11.0311 EndY=1.75002 EndZ=0
    g10: LineSegment StartX=11.0311 StartY=1.75002 StartZ=0 EndX=7.99998 EndY=3.5 EndZ=0
    g11: LineSegment StartX=7.99998 StartY=3.5 StartZ=0 EndX=4.9689 EndY=1.74998 EndZ=0
    g12: LineSegment StartX=4.9689 StartY=1.74998 StartZ=0 EndX=4.96892 EndY=-1.75002 EndZ=0
    g13: Circle [constr] CenterX=8 CenterY=0 CenterZ=0 NormalX=0 NormalY=0 NormalZ=1 AngleXU=0 Radius=3.5
    g14: LineSegment StartX=4.03109 StartY=3.5 StartZ=0 EndX=7.06218 EndY=5.25 EndZ=0
    g15: LineSegment StartX=7.06218 StartY=5.25 StartZ=0 EndX=7.06218 EndY=8.75 EndZ=0
    g16: LineSegment StartX=7.06218 StartY=8.75 StartZ=0 EndX=4.03109 EndY=10.5 EndZ=0
    g17: LineSegment StartX=4.03109 StartY=10.5 StartZ=0 EndX=1 EndY=8.75 EndZ=0
    g18: LineSegment StartX=1 StartY=8.75 StartZ=0 EndX=1 EndY=5.25 EndZ=0
    g19: LineSegment StartX=1 StartY=5.25 StartZ=0 EndX=4.03109 EndY=3.5 EndZ=0
    g20: Circle [constr] CenterX=4.03109 CenterY=7 CenterZ=0 NormalX=0 NormalY=0 NormalZ=1 AngleXU=0 Radius=3.5
    g21: LineSegment StartX=-1 StartY=5.25 StartZ=0 EndX=-1 EndY=8.75 EndZ=0
    g22: LineSegment StartX=-1 StartY=8.75 StartZ=0 EndX=-4.03109 EndY=10.5 EndZ=0
    g23: LineSegment StartX=-4.03109 StartY=10.5 StartZ=0 EndX=-7.06218 EndY=8.75 EndZ=0
    g24: LineSegment StartX=-7.06218 StartY=8.75 StartZ=0 EndX=-7.06218 EndY=5.25 EndZ=0
    g25: LineSegment StartX=-7.06218 StartY=5.25 StartZ=0 EndX=-4.03109 EndY=3.5 EndZ=0
    g26: LineSegment StartX=-4.03109 StartY=3.5 StartZ=0 EndX=-1 EndY=5.25 EndZ=0
    g27: Circle [constr] CenterX=-4.03109 CenterY=7 CenterZ=0 NormalX=0 NormalY=0 NormalZ=1 AngleXU=0 Radius=3.5
    g28: LineSegment StartX=-4.96891 StartY=-1.75 StartZ=0 EndX=-4.96891 EndY=1.75 EndZ=0
    g29: LineSegment StartX=-4.96891 StartY=1.75 StartZ=0 EndX=-8 EndY=3.5 EndZ=0
    g30: LineSegment StartX=-8 StartY=3.5 StartZ=0 EndX=-11.0311 EndY=1.75 EndZ=0
    g31: LineSegment StartX=-11.0311 StartY=1.75 StartZ=0 EndX=-11.0311 EndY=-1.75 EndZ=0
    g32: LineSegment StartX=-11.0311 StartY=-1.75 StartZ=0 EndX=-8 EndY=-3.5 EndZ=0
    g33: LineSegment StartX=-8 StartY=-3.5 StartZ=0 EndX=-4.96891 EndY=-1.75 EndZ=0
    g34: Circle [constr] CenterX=-8 CenterY=0 CenterZ=0 NormalX=0 NormalY=0 NormalZ=1 AngleXU=0 Radius=3.5
    g35: LineSegment StartX=-4.03109 StartY=-3.5 StartZ=0 EndX=-7.06218 EndY=-5.25 EndZ=0
    g36: LineSegment StartX=-7.06218 StartY=-5.25 StartZ=0 EndX=-7.06218 EndY=-8.75 EndZ=0
    g37: LineSegment StartX=-7.06218 StartY=-8.75 StartZ=0 EndX=-4.03109 EndY=-10.5 EndZ=0
    g38: LineSegment StartX=-4.03109 StartY=-10.5 StartZ=0 EndX=-1 EndY=-8.75 EndZ=0
    g39: LineSegment StartX=-1 StartY=-8.75 StartZ=0 EndX=-1 EndY=-5.25 EndZ=0
    g40: LineSegment StartX=-1 StartY=-5.25 StartZ=0 EndX=-4.03109 EndY=-3.5 EndZ=0
    g41: Circle [constr] CenterX=-4.03109 CenterY=-7 CenterZ=0 NormalX=0 NormalY=0 NormalZ=1 AngleXU=0 Radius=3.5
    g42: LineSegment StartX=4.03109 StartY=-3.5 StartZ=0 EndX=1 EndY=-5.25 EndZ=0
    g43: LineSegment StartX=1 StartY=-5.25 StartZ=0 EndX=1 EndY=-8.75 EndZ=0
    g44: LineSegment StartX=1 StartY=-8.75 StartZ=0 EndX=4.03109 EndY=-10.5 EndZ=0
    g45: LineSegment StartX=4.03109 StartY=-10.5 StartZ=0 EndX=7.06218 EndY=-8.75 EndZ=0
    g46: LineSegment StartX=7.06218 StartY=-8.75 StartZ=0 EndX=7.06218 EndY=-5.25 EndZ=0
    g47: LineSegment StartX=7.06218 StartY=-5.25 StartZ=0 EndX=4.03109 EndY=-3.5 EndZ=0
    g48: Circle [constr] CenterX=4.03109 CenterY=-7 CenterZ=0 NormalX=0 NormalY=0 NormalZ=1 AngleXU=0 Radius=3.5
  constraints (117):
    c: Coincident(g0,g1)
    c: Coincident(g1,g2)
    c: Coincident(g2,g3)
    c: Coincident(g3,g4)
    c: Coincident(g4,g5)
    c: Coincident(g5,g0)
    c: Equal(g0, g1-g5) x5
    c: PointOnObject(g0,g6)
    c: PointOnObject(g1,g6)
    c: PointOnObject(g2,g6)
    c: PointOnObject(g3,g6)
    c: PointOnObject(g4,g6)
    c: PointOnObject(g5,g6)
    c: Coincident(g6,g-1)
    c: Diameter(g6) = 7
    c: PointOnObject(g0,g-2)
    c: Coincident(g7,g8)
    c: Coincident(g8,g9)
    c: Coincident(g9,g10)
    c: Coincident(g10,g11)
    c: Coincident(g11,g12)
    c: Coincident(g12,g7)
    c: Equal(g7, g8-g12) x5
    c: PointOnObject(g7,g13)
    c: PointOnObject(g8,g13)
    c: PointOnObject(g9,g13)
    c: PointOnObject(g10,g13)
    c: PointOnObject(g11,g13)
    c: PointOnObject(g12,g13)
    c: PointOnObject(g13,g-1)
    c: Diameter(g13) = 7
    c: Distance(g6,g13) = 8
    c: Horizontal(g0,g10)
    c: Coincident(g14,g15)
    c: Coincident(g15,g16)
    c: Coincident(g16,g17)
    c: Coincident(g17,g18)
    c: Coincident(g18,g19)
    c: Coincident(g19,g14)
    c: Equal(g14, g15-g19) x5
    c: PointOnObject(g14,g20)
    c: PointOnObject(g15,g20)
    c: PointOnObject(g16,g20)
    c: PointOnObject(g17,g20)
    c: PointOnObject(g18,g20)
    c: PointOnObject(g19,g20)
    c: Diameter(g20) = 7
    c: DistanceY(g-1,g20) = 7
    c: Vertical(g18)
    c: Distance(g17,g-2) = 1
    c: Coincident(g21,g22)
    c: Coincident(g22,g23)
    c: Coincident(g23,g24)
    c: Coincident(g24,g25)
    c: Coincident(g25,g26)
    c: Coincident(g26,g21)
    c: Equal(g21, g22-g26) x5
    c: PointOnObject(g21,g27)
    c: PointOnObject(g22,g27)
    c: PointOnObject(g23,g27)
    c: PointOnObject(g24,g27)
    c: PointOnObject(g25,g27)
    c: PointOnObject(g26,g27)
    c: Diameter(g27) = 7
    c: DistanceY(g-1,g27) = 7
    c: DistanceX(g21,g-1) = 1
    c: Vertical(g21)
    c: Coincident(g28,g29)
    c: Coincident(g29,g30)
    c: Coincident(g30,g31)
    c: Coincident(g31,g32)
    c: Coincident(g32,g33)
    c: Coincident(g33,g28)
    c: Equal(g28, g29-g33) x5
    c: PointOnObject(g28,g34)
    c: PointOnObject(g29,g34)
    c: PointOnObject(g30,g34)
    c: PointOnObject(g31,g34)
    c: PointOnObject(g32,g34)
    c: PointOnObject(g33,g34)
    c: PointOnObject(g34,g-1)
    c: Diameter(g34) = 7
    c: Vertical(g31)
    c: DistanceX(g34,g-1) = 8
    c: Coincident(g35,g36)
    c: Coincident(g36,g37)
    c: Coincident(g37,g38)
    c: Coincident(g38,g39)
    c: Coincident(g39,g40)
    c: Coincident(g40,g35)
    c: Equal(g35, g36-g40) x5
    c: PointOnObject(g35,g41)
    c: PointOnObject(g36,g41)
    c: PointOnObject(g37,g41)
    c: PointOnObject(g38,g41)
    c: PointOnObject(g39,g41)
    c: PointOnObject(g40,g41)
    c: Coincident(g42,g43)
    c: Coincident(g43,g44)
    c: Coincident(g44,g45)
    c: Coincident(g45,g46)
    c: Coincident(g46,g47)
    c: Coincident(g47,g42)
    c: Equal(g42, g43-g47) x5
    c: PointOnObject(g42,g48)
    c: PointOnObject(g43,g48)
    c: PointOnObject(g44,g48)
    c: PointOnObject(g45,g48)
    c: PointOnObject(g46,g48)
    c: PointOnObject(g47,g48)
    c: Equal(g41,g48)
    c: Diameter(g41) = 7
    c: Vertical(g39)
    c: Vertical(g43)
    c: Distance(g-2,g39) = 1
    c: Symmetric(g38,g43,g-2)
    c: Distance(g41,g-1) = 7
FEATURE [Part::Extrusion] Extrude452  label="hex067"
  Base = -> Sketch460
  Dir = (0,-1,2e-16)
  DirMode = 2
  FaceMakerClass = Part::FaceMakerBullseye
  FaceMakerMode = 3
  LengthFwd = 10
  LengthRev = 0
  Placement = pos=(32,0,-28) rot=(0,0,1;0rad)
  Solid = true
  Symmetric = false
FEATURE [Sketcher::SketchObject] Sketch461
  ArcFitTolerance = 1e-06
  FullyConstrained = true
  MakeInternals = false
  Placement = pos=(0,0,0) rot=(1,0,0;1.5708rad)
  sketch-geometry (49):
    g0: LineSegment StartX=1e-16 StartY=3.5 StartZ=0 EndX=-3.03109 EndY=1.75 EndZ=0
    g1: LineSegment StartX=-3.03109 StartY=1.75 StartZ=0 EndX=-3.03109 EndY=-1.75 EndZ=0
    g2: LineSegment StartX=-3.03109 StartY=-1.75 StartZ=0 EndX=-1e-16 EndY=-3.5 EndZ=0
    g3: LineSegment StartX=-1e-16 StartY=-3.5 StartZ=0 EndX=3.03109 EndY=-1.75 EndZ=0
    g4: LineSegment StartX=3.03109 StartY=-1.75 StartZ=0 EndX=3.03109 EndY=1.75 EndZ=0
    g5: LineSegment StartX=3.03109 StartY=1.75 StartZ=0 EndX=1e-16 EndY=3.5 EndZ=0
    g6: Circle [constr] CenterX=0 CenterY=0 CenterZ=0 NormalX=0 NormalY=0 NormalZ=1 AngleXU=0 Radius=3.5
    g7: LineSegment StartX=4.96892 StartY=-1.75002 StartZ=0 EndX=8.00002 EndY=-3.5 EndZ=0
    g8: LineSegment StartX=8.00002 StartY=-3.5 StartZ=0 EndX=11.0311 EndY=-1.74998 EndZ=0
    g9: LineSegment StartX=11.0311 StartY=-1.74998 StartZ=0 EndX=11.0311 EndY=1.75002 EndZ=0
    g10: LineSegment StartX=11.0311 StartY=1.75002 StartZ=0 EndX=7.99998 EndY=3.5 EndZ=0
    g11: LineSegment StartX=7.99998 StartY=3.5 StartZ=0 EndX=4.9689 EndY=1.74998 EndZ=0
    g12: LineSegment StartX=4.9689 StartY=1.74998 StartZ=0 EndX=4.96892 EndY=-1.75002 EndZ=0
    g13: Circle [constr] CenterX=8 CenterY=0 CenterZ=0 NormalX=0 NormalY=0 NormalZ=1 AngleXU=0 Radius=3.5
    g14: LineSegment StartX=4.03109 StartY=3.5 StartZ=0 EndX=7.06218 EndY=5.25 EndZ=0
    g15: LineSegment StartX=7.06218 StartY=5.25 StartZ=0 EndX=7.06218 EndY=8.75 EndZ=0
    g16: LineSegment StartX=7.06218 StartY=8.75 StartZ=0 EndX=4.03109 EndY=10.5 EndZ=0
    g17: LineSegment StartX=4.03109 StartY=10.5 StartZ=0 EndX=1 EndY=8.75 EndZ=0
    g18: LineSegment StartX=1 StartY=8.75 StartZ=0 EndX=1 EndY=5.25 EndZ=0
    g19: LineSegment StartX=1 StartY=5.25 StartZ=0 EndX=4.03109 EndY=3.5 EndZ=0
    g20: Circle [constr] CenterX=4.03109 CenterY=7 CenterZ=0 NormalX=0 NormalY=0 NormalZ=1 AngleXU=0 Radius=3.5
    g21: LineSegment StartX=-1 StartY=5.25 StartZ=0 EndX=-1 EndY=8.75 EndZ=0
    g22: LineSegment StartX=-1 StartY=8.75 StartZ=0 EndX=-4.03109 EndY=10.5 EndZ=0
    g23: LineSegment StartX=-4.03109 StartY=10.5 StartZ=0 EndX=-7.06218 EndY=8.75 EndZ=0
    g24: LineSegment StartX=-7.06218 StartY=8.75 StartZ=0 EndX=-7.06218 EndY=5.25 EndZ=0
    g25: LineSegment StartX=-7.06218 StartY=5.25 StartZ=0 EndX=-4.03109 EndY=3.5 EndZ=0
    g26: LineSegment StartX=-4.03109 StartY=3.5 StartZ=0 EndX=-1 EndY=5.25 EndZ=0
    g27: Circle [constr] CenterX=-4.03109 CenterY=7 CenterZ=0 NormalX=0 NormalY=0 NormalZ=1 AngleXU=0 Radius=3.5
    g28: LineSegment StartX=-4.96891 StartY=-1.75 StartZ=0 EndX=-4.96891 EndY=1.75 EndZ=0
    g29: LineSegment StartX=-4.96891 StartY=1.75 StartZ=0 EndX=-8 EndY=3.5 EndZ=0
    g30: LineSegment StartX=-8 StartY=3.5 StartZ=0 EndX=-11.0311 EndY=1.75 EndZ=0
    g31: LineSegment StartX=-11.0311 StartY=1.75 StartZ=0 EndX=-11.0311 EndY=-1.75 EndZ=0
    g32: LineSegment StartX=-11.0311 StartY=-1.75 StartZ=0 EndX=-8 EndY=-3.5 EndZ=0
    g33: LineSegment StartX=-8 StartY=-3.5 StartZ=0 EndX=-4.96891 EndY=-1.75 EndZ=0
    g34: Circle [constr] CenterX=-8 CenterY=0 CenterZ=0 NormalX=0 NormalY=0 NormalZ=1 AngleXU=0 Radius=3.5
    g35: LineSegment StartX=-4.03109 StartY=-3.5 StartZ=0 EndX=-7.06218 EndY=-5.25 EndZ=0
    g36: LineSegment StartX=-7.06218 StartY=-5.25 StartZ=0 EndX=-7.06218 EndY=-8.75 EndZ=0
    g37: LineSegment StartX=-7.06218 StartY=-8.75 StartZ=0 EndX=-4.03109 EndY=-10.5 EndZ=0
    g38: LineSegment StartX=-4.03109 StartY=-10.5 StartZ=0 EndX=-1 EndY=-8.75 EndZ=0
    g39: LineSegment StartX=-1 StartY=-8.75 StartZ=0 EndX=-1 EndY=-5.25 EndZ=0
    g40: LineSegment StartX=-1 StartY=-5.25 StartZ=0 EndX=-4.03109 EndY=-3.5 EndZ=0
    g41: Circle [constr] CenterX=-4.03109 CenterY=-7 CenterZ=0 NormalX=0 NormalY=0 NormalZ=1 AngleXU=0 Radius=3.5
    g42: LineSegment StartX=4.03109 StartY=-3.5 StartZ=0 EndX=1 EndY=-5.25 EndZ=0
    g43: LineSegment StartX=1 StartY=-5.25 StartZ=0 EndX=1 EndY=-8.75 EndZ=0
    g44: LineSegment StartX=1 StartY=-8.75 StartZ=0 EndX=4.03109 EndY=-10.5 EndZ=0
    g45: LineSegment StartX=4.03109 StartY=-10.5 StartZ=0 EndX=7.06218 EndY=-8.75 EndZ=0
    g46: LineSegment StartX=7.06218 StartY=-8.75 StartZ=0 EndX=7.06218 EndY=-5.25 EndZ=0
    g47: LineSegment StartX=7.06218 StartY=-5.25 StartZ=0 EndX=4.03109 EndY=-3.5 EndZ=0
    g48: Circle [constr] CenterX=4.03109 CenterY=-7 CenterZ=0 NormalX=0 NormalY=0 NormalZ=1 AngleXU=0 Radius=3.5
  constraints (117):
    c: Coincident(g0,g1)
    c: Coincident(g1,g2)
    c: Coincident(g2,g3)
    c: Coincident(g3,g4)
    c: Coincident(g4,g5)
    c: Coincident(g5,g0)
    c: Equal(g0, g1-g5) x5
    c: PointOnObject(g0,g6)
    c: PointOnObject(g1,g6)
    c: PointOnObject(g2,g6)
    c: PointOnObject(g3,g6)
    c: PointOnObject(g4,g6)
    c: PointOnObject(g5,g6)
    c: Coincident(g6,g-1)
    c: Diameter(g6) = 7
    c: PointOnObject(g0,g-2)
    c: Coincident(g7,g8)
    c: Coincident(g8,g9)
    c: Coincident(g9,g10)
    c: Coincident(g10,g11)
    c: Coincident(g11,g12)
    c: Coincident(g12,g7)
    c: Equal(g7, g8-g12) x5
    c: PointOnObject(g7,g13)
    c: PointOnObject(g8,g13)
    c: PointOnObject(g9,g13)
    c: PointOnObject(g10,g13)
    c: PointOnObject(g11,g13)
    c: PointOnObject(g12,g13)
    c: PointOnObject(g13,g-1)
    c: Diameter(g13) = 7
    c: Distance(g6,g13) = 8
    c: Horizontal(g0,g10)
    c: Coincident(g14,g15)
    c: Coincident(g15,g16)
    c: Coincident(g16,g17)
    c: Coincident(g17,g18)
    c: Coincident(g18,g19)
    c: Coincident(g19,g14)
    c: Equal(g14, g15-g19) x5
    c: PointOnObject(g14,g20)
    c: PointOnObject(g15,g20)
    c: PointOnObject(g16,g20)
    c: PointOnObject(g17,g20)
    c: PointOnObject(g18,g20)
    c: PointOnObject(g19,g20)
    c: Diameter(g20) = 7
    c: DistanceY(g-1,g20) = 7
    c: Vertical(g18)
    c: Distance(g17,g-2) = 1
    c: Coincident(g21,g22)
    c: Coincident(g22,g23)
    c: Coincident(g23,g24)
    c: Coincident(g24,g25)
    c: Coincident(g25,g26)
    c: Coincident(g26,g21)
    c: Equal(g21, g22-g26) x5
    c: PointOnObject(g21,g27)
    c: PointOnObject(g22,g27)
    c: PointOnObject(g23,g27)
    c: PointOnObject(g24,g27)
    c: PointOnObject(g25,g27)
    c: PointOnObject(g26,g27)
    c: Diameter(g27) = 7
    c: DistanceY(g-1,g27) = 7
    c: DistanceX(g21,g-1) = 1
    c: Vertical(g21)
    c: Coincident(g28,g29)
    c: Coincident(g29,g30)
    c: Coincident(g30,g31)
    c: Coincident(g31,g32)
    c: Coincident(g32,g33)
    c: Coincident(g33,g28)
    c: Equal(g28, g29-g33) x5
    c: PointOnObject(g28,g34)
    c: PointOnObject(g29,g34)
    c: PointOnObject(g30,g34)
    c: PointOnObject(g31,g34)
    c: PointOnObject(g32,g34)
    c: PointOnObject(g33,g34)
    c: PointOnObject(g34,g-1)
    c: Diameter(g34) = 7
    c: Vertical(g31)
    c: DistanceX(g34,g-1) = 8
    c: Coincident(g35,g36)
    c: Coincident(g36,g37)
    c: Coincident(g37,g38)
    c: Coincident(g38,g39)
    c: Coincident(g39,g40)
    c: Coincident(g40,g35)
    c: Equal(g35, g36-g40) x5
    c: PointOnObject(g35,g41)
    c: PointOnObject(g36,g41)
    c: PointOnObject(g37,g41)
    c: PointOnObject(g38,g41)
    c: PointOnObject(g39,g41)
    c: PointOnObject(g40,g41)
    c: Coincident(g42,g43)
    c: Coincident(g43,g44)
    c: Coincident(g44,g45)
    c: Coincident(g45,g46)
    c: Coincident(g46,g47)
    c: Coincident(g47,g42)
    c: Equal(g42, g43-g47) x5
    c: PointOnObject(g42,g48)
    c: PointOnObject(g43,g48)
    c: PointOnObject(g44,g48)
    c: PointOnObject(g45,g48)
    c: PointOnObject(g46,g48)
    c: PointOnObject(g47,g48)
    c: Equal(g41,g48)
    c: Diameter(g41) = 7
    c: Vertical(g39)
    c: Vertical(g43)
    c: Distance(g-2,g39) = 1
    c: Symmetric(g38,g43,g-2)
    c: Distance(g41,g-1) = 7
FEATURE [Part::Extrusion] Extrude453  label="hex068"
  Base = -> Sketch461
  Dir = (0,-1,2e-16)
  DirMode = 2
  FaceMakerClass = Part::FaceMakerBullseye
  FaceMakerMode = 3
  LengthFwd = 10
  LengthRev = 0
  Placement = pos=(36,0,-7) rot=(0,0,1;0rad)
  Solid = true
  Symmetric = false
FEATURE [Sketcher::SketchObject] Sketch462
  ArcFitTolerance = 1e-06
  FullyConstrained = true
  MakeInternals = false
  Placement = pos=(0,0,0) rot=(1,0,0;1.5708rad)
  sketch-geometry (49):
    g0: LineSegment StartX=1e-16 StartY=3.5 StartZ=0 EndX=-3.03109 EndY=1.75 EndZ=0
    g1: LineSegment StartX=-3.03109 StartY=1.75 StartZ=0 EndX=-3.03109 EndY=-1.75 EndZ=0
    g2: LineSegment StartX=-3.03109 StartY=-1.75 StartZ=0 EndX=-1e-16 EndY=-3.5 EndZ=0
    g3: LineSegment StartX=-1e-16 StartY=-3.5 StartZ=0 EndX=3.03109 EndY=-1.75 EndZ=0
    g4: LineSegment StartX=3.03109 StartY=-1.75 StartZ=0 EndX=3.03109 EndY=1.75 EndZ=0
    g5: LineSegment StartX=3.03109 StartY=1.75 StartZ=0 EndX=1e-16 EndY=3.5 EndZ=0
    g6: Circle [constr] CenterX=0 CenterY=0 CenterZ=0 NormalX=0 NormalY=0 NormalZ=1 AngleXU=0 Radius=3.5
    g7: LineSegment StartX=4.96892 StartY=-1.75002 StartZ=0 EndX=8.00002 EndY=-3.5 EndZ=0
    g8: LineSegment StartX=8.00002 StartY=-3.5 StartZ=0 EndX=11.0311 EndY=-1.74998 EndZ=0
    g9: LineSegment StartX=11.0311 StartY=-1.74998 StartZ=0 EndX=11.0311 EndY=1.75002 EndZ=0
    g10: LineSegment StartX=11.0311 StartY=1.75002 StartZ=0 EndX=7.99998 EndY=3.5 EndZ=0
    g11: LineSegment StartX=7.99998 StartY=3.5 StartZ=0 EndX=4.9689 EndY=1.74998 EndZ=0
    g12: LineSegment StartX=4.9689 StartY=1.74998 StartZ=0 EndX=4.96892 EndY=-1.75002 EndZ=0
    g13: Circle [constr] CenterX=8 CenterY=0 CenterZ=0 NormalX=0 NormalY=0 NormalZ=1 AngleXU=0 Radius=3.5
    g14: LineSegment StartX=4.03109 StartY=3.5 StartZ=0 EndX=7.06218 EndY=5.25 EndZ=0
    g15: LineSegment StartX=7.06218 StartY=5.25 StartZ=0 EndX=7.06218 EndY=8.75 EndZ=0
    g16: LineSegment StartX=7.06218 StartY=8.75 StartZ=0 EndX=4.03109 EndY=10.5 EndZ=0
    g17: LineSegment StartX=4.03109 StartY=10.5 StartZ=0 EndX=1 EndY=8.75 EndZ=0
    g18: LineSegment StartX=1 StartY=8.75 StartZ=0 EndX=1 EndY=5.25 EndZ=0
    g19: LineSegment StartX=1 StartY=5.25 StartZ=0 EndX=4.03109 EndY=3.5 EndZ=0
    g20: Circle [constr] CenterX=4.03109 CenterY=7 CenterZ=0 NormalX=0 NormalY=0 NormalZ=1 AngleXU=0 Radius=3.5
    g21: LineSegment StartX=-1 StartY=5.25 StartZ=0 EndX=-1 EndY=8.75 EndZ=0
    g22: LineSegment StartX=-1 StartY=8.75 StartZ=0 EndX=-4.03109 EndY=10.5 EndZ=0
    g23: LineSegment StartX=-4.03109 StartY=10.5 StartZ=0 EndX=-7.06218 EndY=8.75 EndZ=0
    g24: LineSegment StartX=-7.06218 StartY=8.75 StartZ=0 EndX=-7.06218 EndY=5.25 EndZ=0
    g25: LineSegment StartX=-7.06218 StartY=5.25 StartZ=0 EndX=-4.03109 EndY=3.5 EndZ=0
    g26: LineSegment StartX=-4.03109 StartY=3.5 StartZ=0 EndX=-1 EndY=5.25 EndZ=0
    g27: Circle [constr] CenterX=-4.03109 CenterY=7 CenterZ=0 NormalX=0 NormalY=0 NormalZ=1 AngleXU=0 Radius=3.5
    g28: LineSegment StartX=-4.96891 StartY=-1.75 StartZ=0 EndX=-4.96891 EndY=1.75 EndZ=0
    g29: LineSegment StartX=-4.96891 StartY=1.75 StartZ=0 EndX=-8 EndY=3.5 EndZ=0
    g30: LineSegment StartX=-8 StartY=3.5 StartZ=0 EndX=-11.0311 EndY=1.75 EndZ=0
    g31: LineSegment StartX=-11.0311 StartY=1.75 StartZ=0 EndX=-11.0311 EndY=-1.75 EndZ=0
    g32: LineSegment StartX=-11.0311 StartY=-1.75 StartZ=0 EndX=-8 EndY=-3.5 EndZ=0
    g33: LineSegment StartX=-8 StartY=-3.5 StartZ=0 EndX=-4.96891 EndY=-1.75 EndZ=0
    g34: Circle [constr] CenterX=-8 CenterY=0 CenterZ=0 NormalX=0 NormalY=0 NormalZ=1 AngleXU=0 Radius=3.5
    g35: LineSegment StartX=-4.03109 StartY=-3.5 StartZ=0 EndX=-7.06218 EndY=-5.25 EndZ=0
    g36: LineSegment StartX=-7.06218 StartY=-5.25 StartZ=0 EndX=-7.06218 EndY=-8.75 EndZ=0
    g37: LineSegment StartX=-7.06218 StartY=-8.75 StartZ=0 EndX=-4.03109 EndY=-10.5 EndZ=0
    g38: LineSegment StartX=-4.03109 StartY=-10.5 StartZ=0 EndX=-1 EndY=-8.75 EndZ=0
    g39: LineSegment StartX=-1 StartY=-8.75 StartZ=0 EndX=-1 EndY=-5.25 EndZ=0
    g40: LineSegment StartX=-1 StartY=-5.25 StartZ=0 EndX=-4.03109 EndY=-3.5 EndZ=0
    g41: Circle [constr] CenterX=-4.03109 CenterY=-7 CenterZ=0 NormalX=0 NormalY=0 NormalZ=1 AngleXU=0 Radius=3.5
    g42: LineSegment StartX=4.03109 StartY=-3.5 StartZ=0 EndX=1 EndY=-5.25 EndZ=0
    g43: LineSegment StartX=1 StartY=-5.25 StartZ=0 EndX=1 EndY=-8.75 EndZ=0
    g44: LineSegment StartX=1 StartY=-8.75 StartZ=0 EndX=4.03109 EndY=-10.5 EndZ=0
    g45: LineSegment StartX=4.03109 StartY=-10.5 StartZ=0 EndX=7.06218 EndY=-8.75 EndZ=0
    g46: LineSegment StartX=7.06218 StartY=-8.75 StartZ=0 EndX=7.06218 EndY=-5.25 EndZ=0
    g47: LineSegment StartX=7.06218 StartY=-5.25 StartZ=0 EndX=4.03109 EndY=-3.5 EndZ=0
    g48: Circle [constr] CenterX=4.03109 CenterY=-7 CenterZ=0 NormalX=0 NormalY=0 NormalZ=1 AngleXU=0 Radius=3.5
  constraints (117):
    c: Coincident(g0,g1)
    c: Coincident(g1,g2)
    c: Coincident(g2,g3)
    c: Coincident(g3,g4)
    c: Coincident(g4,g5)
    c: Coincident(g5,g0)
    c: Equal(g0, g1-g5) x5
    c: PointOnObject(g0,g6)
    c: PointOnObject(g1,g6)
    c: PointOnObject(g2,g6)
    c: PointOnObject(g3,g6)
    c: PointOnObject(g4,g6)
    c: PointOnObject(g5,g6)
    c: Coincident(g6,g-1)
    c: Diameter(g6) = 7
    c: PointOnObject(g0,g-2)
    c: Coincident(g7,g8)
    c: Coincident(g8,g9)
    c: Coincident(g9,g10)
    c: Coincident(g10,g11)
    c: Coincident(g11,g12)
    c: Coincident(g12,g7)
    c: Equal(g7, g8-g12) x5
    c: PointOnObject(g7,g13)
    c: PointOnObject(g8,g13)
    c: PointOnObject(g9,g13)
    c: PointOnObject(g10,g13)
    c: PointOnObject(g11,g13)
    c: PointOnObject(g12,g13)
    c: PointOnObject(g13,g-1)
    c: Diameter(g13) = 7
    c: Distance(g6,g13) = 8
    c: Horizontal(g0,g10)
    c: Coincident(g14,g15)
    c: Coincident(g15,g16)
    c: Coincident(g16,g17)
    c: Coincident(g17,g18)
    c: Coincident(g18,g19)
    c: Coincident(g19,g14)
    c: Equal(g14, g15-g19) x5
    c: PointOnObject(g14,g20)
    c: PointOnObject(g15,g20)
    c: PointOnObject(g16,g20)
    c: PointOnObject(g17,g20)
    c: PointOnObject(g18,g20)
    c: PointOnObject(g19,g20)
    c: Diameter(g20) = 7
    c: DistanceY(g-1,g20) = 7
    c: Vertical(g18)
    c: Distance(g17,g-2) = 1
    c: Coincident(g21,g22)
    c: Coincident(g22,g23)
    c: Coincident(g23,g24)
    c: Coincident(g24,g25)
    c: Coincident(g25,g26)
    c: Coincident(g26,g21)
    c: Equal(g21, g22-g26) x5
    c: PointOnObject(g21,g27)
    c: PointOnObject(g22,g27)
    c: PointOnObject(g23,g27)
    c: PointOnObject(g24,g27)
    c: PointOnObject(g25,g27)
    c: PointOnObject(g26,g27)
    c: Diameter(g27) = 7
    c: DistanceY(g-1,g27) = 7
    c: DistanceX(g21,g-1) = 1
    c: Vertical(g21)
    c: Coincident(g28,g29)
    c: Coincident(g29,g30)
    c: Coincident(g30,g31)
    c: Coincident(g31,g32)
    c: Coincident(g32,g33)
    c: Coincident(g33,g28)
    c: Equal(g28, g29-g33) x5
    c: PointOnObject(g28,g34)
    c: PointOnObject(g29,g34)
    c: PointOnObject(g30,g34)
    c: PointOnObject(g31,g34)
    c: PointOnObject(g32,g34)
    c: PointOnObject(g33,g34)
    c: PointOnObject(g34,g-1)
    c: Diameter(g34) = 7
    c: Vertical(g31)
    c: DistanceX(g34,g-1) = 8
    c: Coincident(g35,g36)
    c: Coincident(g36,g37)
    c: Coincident(g37,g38)
    c: Coincident(g38,g39)
    c: Coincident(g39,g40)
    c: Coincident(g40,g35)
    c: Equal(g35, g36-g40) x5
    c: PointOnObject(g35,g41)
    c: PointOnObject(g36,g41)
    c: PointOnObject(g37,g41)
    c: PointOnObject(g38,g41)
    c: PointOnObject(g39,g41)
    c: PointOnObject(g40,g41)
    c: Coincident(g42,g43)
    c: Coincident(g43,g44)
    c: Coincident(g44,g45)
    c: Coincident(g45,g46)
    c: Coincident(g46,g47)
    c: Coincident(g47,g42)
    c: Equal(g42, g43-g47) x5
    c: PointOnObject(g42,g48)
    c: PointOnObject(g43,g48)
    c: PointOnObject(g44,g48)
    c: PointOnObject(g45,g48)
    c: PointOnObject(g46,g48)
    c: PointOnObject(g47,g48)
    c: Equal(g41,g48)
    c: Diameter(g41) = 7
    c: Vertical(g39)
    c: Vertical(g43)
    c: Distance(g-2,g39) = 1
    c: Symmetric(g38,g43,g-2)
    c: Distance(g41,g-1) = 7
FEATURE [Part::Extrusion] Extrude454  label="hex069"
  Base = -> Sketch462
  Dir = (0,-1,2e-16)
  DirMode = 2
  FaceMakerClass = Part::FaceMakerBullseye
  FaceMakerMode = 3
  LengthFwd = 10
  LengthRev = 0
  Placement = pos=(56,0,0) rot=(0,0,1;0rad)
  Solid = true
  Symmetric = false
FEATURE [Sketcher::SketchObject] Sketch463
  ArcFitTolerance = 1e-06
  FullyConstrained = true
  MakeInternals = false
  Placement = pos=(0,0,0) rot=(1,0,0;1.5708rad)
  sketch-geometry (49):
    g0: LineSegment StartX=1e-16 StartY=3.5 StartZ=0 EndX=-3.03109 EndY=1.75 EndZ=0
    g1: LineSegment StartX=-3.03109 StartY=1.75 StartZ=0 EndX=-3.03109 EndY=-1.75 EndZ=0
    g2: LineSegment StartX=-3.03109 StartY=-1.75 StartZ=0 EndX=-1e-16 EndY=-3.5 EndZ=0
    g3: LineSegment StartX=-1e-16 StartY=-3.5 StartZ=0 EndX=3.03109 EndY=-1.75 EndZ=0
    g4: LineSegment StartX=3.03109 StartY=-1.75 StartZ=0 EndX=3.03109 EndY=1.75 EndZ=0
    g5: LineSegment StartX=3.03109 StartY=1.75 StartZ=0 EndX=1e-16 EndY=3.5 EndZ=0
    g6: Circle [constr] CenterX=0 CenterY=0 CenterZ=0 NormalX=0 NormalY=0 NormalZ=1 AngleXU=0 Radius=3.5
    g7: LineSegment StartX=4.96892 StartY=-1.75002 StartZ=0 EndX=8.00002 EndY=-3.5 EndZ=0
    g8: LineSegment StartX=8.00002 StartY=-3.5 StartZ=0 EndX=11.0311 EndY=-1.74998 EndZ=0
    g9: LineSegment StartX=11.0311 StartY=-1.74998 StartZ=0 EndX=11.0311 EndY=1.75002 EndZ=0
    g10: LineSegment StartX=11.0311 StartY=1.75002 StartZ=0 EndX=7.99998 EndY=3.5 EndZ=0
    g11: LineSegment StartX=7.99998 StartY=3.5 StartZ=0 EndX=4.9689 EndY=1.74998 EndZ=0
    g12: LineSegment StartX=4.9689 StartY=1.74998 StartZ=0 EndX=4.96892 EndY=-1.75002 EndZ=0
    g13: Circle [constr] CenterX=8 CenterY=0 CenterZ=0 NormalX=0 NormalY=0 NormalZ=1 AngleXU=0 Radius=3.5
    g14: LineSegment StartX=4.03109 StartY=3.5 StartZ=0 EndX=7.06218 EndY=5.25 EndZ=0
    g15: LineSegment StartX=7.06218 StartY=5.25 StartZ=0 EndX=7.06218 EndY=8.75 EndZ=0
    g16: LineSegment StartX=7.06218 StartY=8.75 StartZ=0 EndX=4.03109 EndY=10.5 EndZ=0
    g17: LineSegment StartX=4.03109 StartY=10.5 StartZ=0 EndX=1 EndY=8.75 EndZ=0
    g18: LineSegment StartX=1 StartY=8.75 StartZ=0 EndX=1 EndY=5.25 EndZ=0
    g19: LineSegment StartX=1 StartY=5.25 StartZ=0 EndX=4.03109 EndY=3.5 EndZ=0
    g20: Circle [constr] CenterX=4.03109 CenterY=7 CenterZ=0 NormalX=0 NormalY=0 NormalZ=1 AngleXU=0 Radius=3.5
    g21: LineSegment StartX=-1 StartY=5.25 StartZ=0 EndX=-1 EndY=8.75 EndZ=0
    g22: LineSegment StartX=-1 StartY=8.75 StartZ=0 EndX=-4.03109 EndY=10.5 EndZ=0
    g23: LineSegment StartX=-4.03109 StartY=10.5 StartZ=0 EndX=-7.06218 EndY=8.75 EndZ=0
    g24: LineSegment StartX=-7.06218 StartY=8.75 StartZ=0 EndX=-7.06218 EndY=5.25 EndZ=0
    g25: LineSegment StartX=-7.06218 StartY=5.25 StartZ=0 EndX=-4.03109 EndY=3.5 EndZ=0
    g26: LineSegment StartX=-4.03109 StartY=3.5 StartZ=0 EndX=-1 EndY=5.25 EndZ=0
    g27: Circle [constr] CenterX=-4.03109 CenterY=7 CenterZ=0 NormalX=0 NormalY=0 NormalZ=1 AngleXU=0 Radius=3.5
    g28: LineSegment StartX=-4.96891 StartY=-1.75 StartZ=0 EndX=-4.96891 EndY=1.75 EndZ=0
    g29: LineSegment StartX=-4.96891 StartY=1.75 StartZ=0 EndX=-8 EndY=3.5 EndZ=0
    g30: LineSegment StartX=-8 StartY=3.5 StartZ=0 EndX=-11.0311 EndY=1.75 EndZ=0
    g31: LineSegment StartX=-11.0311 StartY=1.75 StartZ=0 EndX=-11.0311 EndY=-1.75 EndZ=0
    g32: LineSegment StartX=-11.0311 StartY=-1.75 StartZ=0 EndX=-8 EndY=-3.5 EndZ=0
    g33: LineSegment StartX=-8 StartY=-3.5 StartZ=0 EndX=-4.96891 EndY=-1.75 EndZ=0
    g34: Circle [constr] CenterX=-8 CenterY=0 CenterZ=0 NormalX=0 NormalY=0 NormalZ=1 AngleXU=0 Radius=3.5
    g35: LineSegment StartX=-4.03109 StartY=-3.5 StartZ=0 EndX=-7.06218 EndY=-5.25 EndZ=0
    g36: LineSegment StartX=-7.06218 StartY=-5.25 StartZ=0 EndX=-7.06218 EndY=-8.75 EndZ=0
    g37: LineSegment StartX=-7.06218 StartY=-8.75 StartZ=0 EndX=-4.03109 EndY=-10.5 EndZ=0
    g38: LineSegment StartX=-4.03109 StartY=-10.5 StartZ=0 EndX=-1 EndY=-8.75 EndZ=0
    g39: LineSegment StartX=-1 StartY=-8.75 StartZ=0 EndX=-1 EndY=-5.25 EndZ=0
    g40: LineSegment StartX=-1 StartY=-5.25 StartZ=0 EndX=-4.03109 EndY=-3.5 EndZ=0
    g41: Circle [constr] CenterX=-4.03109 CenterY=-7 CenterZ=0 NormalX=0 NormalY=0 NormalZ=1 AngleXU=0 Radius=3.5
    g42: LineSegment StartX=4.03109 StartY=-3.5 StartZ=0 EndX=1 EndY=-5.25 EndZ=0
    g43: LineSegment StartX=1 StartY=-5.25 StartZ=0 EndX=1 EndY=-8.75 EndZ=0
    g44: LineSegment StartX=1 StartY=-8.75 StartZ=0 EndX=4.03109 EndY=-10.5 EndZ=0
    g45: LineSegment StartX=4.03109 StartY=-10.5 StartZ=0 EndX=7.06218 EndY=-8.75 EndZ=0
    g46: LineSegment StartX=7.06218 StartY=-8.75 StartZ=0 EndX=7.06218 EndY=-5.25 EndZ=0
    g47: LineSegment StartX=7.06218 StartY=-5.25 StartZ=0 EndX=4.03109 EndY=-3.5 EndZ=0
    g48: Circle [constr] CenterX=4.03109 CenterY=-7 CenterZ=0 NormalX=0 NormalY=0 NormalZ=1 AngleXU=0 Radius=3.5
  constraints (117):
    c: Coincident(g0,g1)
    c: Coincident(g1,g2)
    c: Coincident(g2,g3)
    c: Coincident(g3,g4)
    c: Coincident(g4,g5)
    c: Coincident(g5,g0)
    c: Equal(g0, g1-g5) x5
    c: PointOnObject(g0,g6)
    c: PointOnObject(g1,g6)
    c: PointOnObject(g2,g6)
    c: PointOnObject(g3,g6)
    c: PointOnObject(g4,g6)
    c: PointOnObject(g5,g6)
    c: Coincident(g6,g-1)
    c: Diameter(g6) = 7
    c: PointOnObject(g0,g-2)
    c: Coincident(g7,g8)
    c: Coincident(g8,g9)
    c: Coincident(g9,g10)
    c: Coincident(g10,g11)
    c: Coincident(g11,g12)
    c: Coincident(g12,g7)
    c: Equal(g7, g8-g12) x5
    c: PointOnObject(g7,g13)
    c: PointOnObject(g8,g13)
    c: PointOnObject(g9,g13)
    c: PointOnObject(g10,g13)
    c: PointOnObject(g11,g13)
    c: PointOnObject(g12,g13)
    c: PointOnObject(g13,g-1)
    c: Diameter(g13) = 7
    c: Distance(g6,g13) = 8
    c: Horizontal(g0,g10)
    c: Coincident(g14,g15)
    c: Coincident(g15,g16)
    c: Coincident(g16,g17)
    c: Coincident(g17,g18)
    c: Coincident(g18,g19)
    c: Coincident(g19,g14)
    c: Equal(g14, g15-g19) x5
    c: PointOnObject(g14,g20)
    c: PointOnObject(g15,g20)
    c: PointOnObject(g16,g20)
    c: PointOnObject(g17,g20)
    c: PointOnObject(g18,g20)
    c: PointOnObject(g19,g20)
    c: Diameter(g20) = 7
    c: DistanceY(g-1,g20) = 7
    c: Vertical(g18)
    c: Distance(g17,g-2) = 1
    c: Coincident(g21,g22)
    c: Coincident(g22,g23)
    c: Coincident(g23,g24)
    c: Coincident(g24,g25)
    c: Coincident(g25,g26)
    c: Coincident(g26,g21)
    c: Equal(g21, g22-g26) x5
    c: PointOnObject(g21,g27)
    c: PointOnObject(g22,g27)
    c: PointOnObject(g23,g27)
    c: PointOnObject(g24,g27)
    c: PointOnObject(g25,g27)
    c: PointOnObject(g26,g27)
    c: Diameter(g27) = 7
    c: DistanceY(g-1,g27) = 7
    c: DistanceX(g21,g-1) = 1
    c: Vertical(g21)
    c: Coincident(g28,g29)
    c: Coincident(g29,g30)
    c: Coincident(g30,g31)
    c: Coincident(g31,g32)
    c: Coincident(g32,g33)
    c: Coincident(g33,g28)
    c: Equal(g28, g29-g33) x5
    c: PointOnObject(g28,g34)
    c: PointOnObject(g29,g34)
    c: PointOnObject(g30,g34)
    c: PointOnObject(g31,g34)
    c: PointOnObject(g32,g34)
    c: PointOnObject(g33,g34)
    c: PointOnObject(g34,g-1)
    c: Diameter(g34) = 7
    c: Vertical(g31)
    c: DistanceX(g34,g-1) = 8
    c: Coincident(g35,g36)
    c: Coincident(g36,g37)
    c: Coincident(g37,g38)
    c: Coincident(g38,g39)
    c: Coincident(g39,g40)
    c: Coincident(g40,g35)
    c: Equal(g35, g36-g40) x5
    c: PointOnObject(g35,g41)
    c: PointOnObject(g36,g41)
    c: PointOnObject(g37,g41)
    c: PointOnObject(g38,g41)
    c: PointOnObject(g39,g41)
    c: PointOnObject(g40,g41)
    c: Coincident(g42,g43)
    c: Coincident(g43,g44)
    c: Coincident(g44,g45)
    c: Coincident(g45,g46)
    c: Coincident(g46,g47)
    c: Coincident(g47,g42)
    c: Equal(g42, g43-g47) x5
    c: PointOnObject(g42,g48)
    c: PointOnObject(g43,g48)
    c: PointOnObject(g44,g48)
    c: PointOnObject(g45,g48)
    c: PointOnObject(g46,g48)
    c: PointOnObject(g47,g48)
    c: Equal(g41,g48)
    c: Diameter(g41) = 7
    c: Vertical(g39)
    c: Vertical(g43)
    c: Distance(g-2,g39) = 1
    c: Symmetric(g38,g43,g-2)
    c: Distance(g41,g-1) = 7
FEATURE [Part::Extrusion] Extrude455  label="hex070"
  Base = -> Sketch463
  Dir = (0,-1,2e-16)
  DirMode = 2
  FaceMakerClass = Part::FaceMakerBullseye
  FaceMakerMode = 3
  LengthFwd = 10
  LengthRev = 0
  Placement = pos=(52,0,-21) rot=(0,0,1;0rad)
  Solid = true
  Symmetric = false
FEATURE [Sketcher::SketchObject] Sketch464
  ArcFitTolerance = 1e-06
  FullyConstrained = true
  MakeInternals = false
  Placement = pos=(0,0,0) rot=(1,0,0;1.5708rad)
  sketch-geometry (49):
    g0: LineSegment StartX=1e-16 StartY=3.5 StartZ=0 EndX=-3.03109 EndY=1.75 EndZ=0
    g1: LineSegment StartX=-3.03109 StartY=1.75 StartZ=0 EndX=-3.03109 EndY=-1.75 EndZ=0
    g2: LineSegment StartX=-3.03109 StartY=-1.75 StartZ=0 EndX=-1e-16 EndY=-3.5 EndZ=0
    g3: LineSegment StartX=-1e-16 StartY=-3.5 StartZ=0 EndX=3.03109 EndY=-1.75 EndZ=0
    g4: LineSegment StartX=3.03109 StartY=-1.75 StartZ=0 EndX=3.03109 EndY=1.75 EndZ=0
    g5: LineSegment StartX=3.03109 StartY=1.75 StartZ=0 EndX=1e-16 EndY=3.5 EndZ=0
    g6: Circle [constr] CenterX=0 CenterY=0 CenterZ=0 NormalX=0 NormalY=0 NormalZ=1 AngleXU=0 Radius=3.5
    g7: LineSegment StartX=4.96892 StartY=-1.75002 StartZ=0 EndX=8.00002 EndY=-3.5 EndZ=0
    g8: LineSegment StartX=8.00002 StartY=-3.5 StartZ=0 EndX=11.0311 EndY=-1.74998 EndZ=0
    g9: LineSegment StartX=11.0311 StartY=-1.74998 StartZ=0 EndX=11.0311 EndY=1.75002 EndZ=0
    g10: LineSegment StartX=11.0311 StartY=1.75002 StartZ=0 EndX=7.99998 EndY=3.5 EndZ=0
    g11: LineSegment StartX=7.99998 StartY=3.5 StartZ=0 EndX=4.9689 EndY=1.74998 EndZ=0
    g12: LineSegment StartX=4.9689 StartY=1.74998 StartZ=0 EndX=4.96892 EndY=-1.75002 EndZ=0
    g13: Circle [constr] CenterX=8 CenterY=0 CenterZ=0 NormalX=0 NormalY=0 NormalZ=1 AngleXU=0 Radius=3.5
    g14: LineSegment StartX=4.03109 StartY=3.5 StartZ=0 EndX=7.06218 EndY=5.25 EndZ=0
    g15: LineSegment StartX=7.06218 StartY=5.25 StartZ=0 EndX=7.06218 EndY=8.75 EndZ=0
    g16: LineSegment StartX=7.06218 StartY=8.75 StartZ=0 EndX=4.03109 EndY=10.5 EndZ=0
    g17: LineSegment StartX=4.03109 StartY=10.5 StartZ=0 EndX=1 EndY=8.75 EndZ=0
    g18: LineSegment StartX=1 StartY=8.75 StartZ=0 EndX=1 EndY=5.25 EndZ=0
    g19: LineSegment StartX=1 StartY=5.25 StartZ=0 EndX=4.03109 EndY=3.5 EndZ=0
    g20: Circle [constr] CenterX=4.03109 CenterY=7 CenterZ=0 NormalX=0 NormalY=0 NormalZ=1 AngleXU=0 Radius=3.5
    g21: LineSegment StartX=-1 StartY=5.25 StartZ=0 EndX=-1 EndY=8.75 EndZ=0
    g22: LineSegment StartX=-1 StartY=8.75 StartZ=0 EndX=-4.03109 EndY=10.5 EndZ=0
    g23: LineSegment StartX=-4.03109 StartY=10.5 StartZ=0 EndX=-7.06218 EndY=8.75 EndZ=0
    g24: LineSegment StartX=-7.06218 StartY=8.75 StartZ=0 EndX=-7.06218 EndY=5.25 EndZ=0
    g25: LineSegment StartX=-7.06218 StartY=5.25 StartZ=0 EndX=-4.03109 EndY=3.5 EndZ=0
    g26: LineSegment StartX=-4.03109 StartY=3.5 StartZ=0 EndX=-1 EndY=5.25 EndZ=0
    g27: Circle [constr] CenterX=-4.03109 CenterY=7 CenterZ=0 NormalX=0 NormalY=0 NormalZ=1 AngleXU=0 Radius=3.5
    g28: LineSegment StartX=-4.96891 StartY=-1.75 StartZ=0 EndX=-4.96891 EndY=1.75 EndZ=0
    g29: LineSegment StartX=-4.96891 StartY=1.75 StartZ=0 EndX=-8 EndY=3.5 EndZ=0
    g30: LineSegment StartX=-8 StartY=3.5 StartZ=0 EndX=-11.0311 EndY=1.75 EndZ=0
    g31: LineSegment StartX=-11.0311 StartY=1.75 StartZ=0 EndX=-11.0311 EndY=-1.75 EndZ=0
    g32: LineSegment StartX=-11.0311 StartY=-1.75 StartZ=0 EndX=-8 EndY=-3.5 EndZ=0
    g33: LineSegment StartX=-8 StartY=-3.5 StartZ=0 EndX=-4.96891 EndY=-1.75 EndZ=0
    g34: Circle [constr] CenterX=-8 CenterY=0 CenterZ=0 NormalX=0 NormalY=0 NormalZ=1 AngleXU=0 Radius=3.5
    g35: LineSegment StartX=-4.03109 StartY=-3.5 StartZ=0 EndX=-7.06218 EndY=-5.25 EndZ=0
    g36: LineSegment StartX=-7.06218 StartY=-5.25 StartZ=0 EndX=-7.06218 EndY=-8.75 EndZ=0
    g37: LineSegment StartX=-7.06218 StartY=-8.75 StartZ=0 EndX=-4.03109 EndY=-10.5 EndZ=0
    g38: LineSegment StartX=-4.03109 StartY=-10.5 StartZ=0 EndX=-1 EndY=-8.75 EndZ=0
    g39: LineSegment StartX=-1 StartY=-8.75 StartZ=0 EndX=-1 EndY=-5.25 EndZ=0
    g40: LineSegment StartX=-1 StartY=-5.25 StartZ=0 EndX=-4.03109 EndY=-3.5 EndZ=0
    g41: Circle [constr] CenterX=-4.03109 CenterY=-7 CenterZ=0 NormalX=0 NormalY=0 NormalZ=1 AngleXU=0 Radius=3.5
    g42: LineSegment StartX=4.03109 StartY=-3.5 StartZ=0 EndX=1 EndY=-5.25 EndZ=0
    g43: LineSegment StartX=1 StartY=-5.25 StartZ=0 EndX=1 EndY=-8.75 EndZ=0
    g44: LineSegment StartX=1 StartY=-8.75 StartZ=0 EndX=4.03109 EndY=-10.5 EndZ=0
    g45: LineSegment StartX=4.03109 StartY=-10.5 StartZ=0 EndX=7.06218 EndY=-8.75 EndZ=0
    g46: LineSegment StartX=7.06218 StartY=-8.75 StartZ=0 EndX=7.06218 EndY=-5.25 EndZ=0
    g47: LineSegment StartX=7.06218 StartY=-5.25 StartZ=0 EndX=4.03109 EndY=-3.5 EndZ=0
    g48: Circle [constr] CenterX=4.03109 CenterY=-7 CenterZ=0 NormalX=0 NormalY=0 NormalZ=1 AngleXU=0 Radius=3.5
  constraints (117):
    c: Coincident(g0,g1)
    c: Coincident(g1,g2)
    c: Coincident(g2,g3)
    c: Coincident(g3,g4)
    c: Coincident(g4,g5)
    c: Coincident(g5,g0)
    c: Equal(g0, g1-g5) x5
    c: PointOnObject(g0,g6)
    c: PointOnObject(g1,g6)
    c: PointOnObject(g2,g6)
    c: PointOnObject(g3,g6)
    c: PointOnObject(g4,g6)
    c: PointOnObject(g5,g6)
    c: Coincident(g6,g-1)
    c: Diameter(g6) = 7
    c: PointOnObject(g0,g-2)
    c: Coincident(g7,g8)
    c: Coincident(g8,g9)
    c: Coincident(g9,g10)
    c: Coincident(g10,g11)
    c: Coincident(g11,g12)
    c: Coincident(g12,g7)
    c: Equal(g7, g8-g12) x5
    c: PointOnObject(g7,g13)
    c: PointOnObject(g8,g13)
    c: PointOnObject(g9,g13)
    c: PointOnObject(g10,g13)
    c: PointOnObject(g11,g13)
    c: PointOnObject(g12,g13)
    c: PointOnObject(g13,g-1)
    c: Diameter(g13) = 7
    c: Distance(g6,g13) = 8
    c: Horizontal(g0,g10)
    c: Coincident(g14,g15)
    c: Coincident(g15,g16)
    c: Coincident(g16,g17)
    c: Coincident(g17,g18)
    c: Coincident(g18,g19)
    c: Coincident(g19,g14)
    c: Equal(g14, g15-g19) x5
    c: PointOnObject(g14,g20)
    c: PointOnObject(g15,g20)
    c: PointOnObject(g16,g20)
    c: PointOnObject(g17,g20)
    c: PointOnObject(g18,g20)
    c: PointOnObject(g19,g20)
    c: Diameter(g20) = 7
    c: DistanceY(g-1,g20) = 7
    c: Vertical(g18)
    c: Distance(g17,g-2) = 1
    c: Coincident(g21,g22)
    c: Coincident(g22,g23)
    c: Coincident(g23,g24)
    c: Coincident(g24,g25)
    c: Coincident(g25,g26)
    c: Coincident(g26,g21)
    c: Equal(g21, g22-g26) x5
    c: PointOnObject(g21,g27)
    c: PointOnObject(g22,g27)
    c: PointOnObject(g23,g27)
    c: PointOnObject(g24,g27)
    c: PointOnObject(g25,g27)
    c: PointOnObject(g26,g27)
    c: Diameter(g27) = 7
    c: DistanceY(g-1,g27) = 7
    c: DistanceX(g21,g-1) = 1
    c: Vertical(g21)
    c: Coincident(g28,g29)
    c: Coincident(g29,g30)
    c: Coincident(g30,g31)
    c: Coincident(g31,g32)
    c: Coincident(g32,g33)
    c: Coincident(g33,g28)
    c: Equal(g28, g29-g33) x5
    c: PointOnObject(g28,g34)
    c: PointOnObject(g29,g34)
    c: PointOnObject(g30,g34)
    c: PointOnObject(g31,g34)
    c: PointOnObject(g32,g34)
    c: PointOnObject(g33,g34)
    c: PointOnObject(g34,g-1)
    c: Diameter(g34) = 7
    c: Vertical(g31)
    c: DistanceX(g34,g-1) = 8
    c: Coincident(g35,g36)
    c: Coincident(g36,g37)
    c: Coincident(g37,g38)
    c: Coincident(g38,g39)
    c: Coincident(g39,g40)
    c: Coincident(g40,g35)
    c: Equal(g35, g36-g40) x5
    c: PointOnObject(g35,g41)
    c: PointOnObject(g36,g41)
    c: PointOnObject(g37,g41)
    c: PointOnObject(g38,g41)
    c: PointOnObject(g39,g41)
    c: PointOnObject(g40,g41)
    c: Coincident(g42,g43)
    c: Coincident(g43,g44)
    c: Coincident(g44,g45)
    c: Coincident(g45,g46)
    c: Coincident(g46,g47)
    c: Coincident(g47,g42)
    c: Equal(g42, g43-g47) x5
    c: PointOnObject(g42,g48)
    c: PointOnObject(g43,g48)
    c: PointOnObject(g44,g48)
    c: PointOnObject(g45,g48)
    c: PointOnObject(g46,g48)
    c: PointOnObject(g47,g48)
    c: Equal(g41,g48)
    c: Diameter(g41) = 7
    c: Vertical(g39)
    c: Vertical(g43)
    c: Distance(g-2,g39) = 1
    c: Symmetric(g38,g43,g-2)
    c: Distance(g41,g-1) = 7
FEATURE [Part::Extrusion] Extrude456  label="hex071"
  Base = -> Sketch464
  Dir = (0,-1,2e-16)
  DirMode = 2
  FaceMakerClass = Part::FaceMakerBullseye
  FaceMakerMode = 3
  LengthFwd = 10
  LengthRev = 0
  Placement = pos=(-56,0,0) rot=(0,0,1;0rad)
  Solid = true
  Symmetric = false
FEATURE [Sketcher::SketchObject] Sketch465
  ArcFitTolerance = 1e-06
  FullyConstrained = true
  MakeInternals = false
  Placement = pos=(0,0,0) rot=(1,0,0;1.5708rad)
  sketch-geometry (49):
    g0: LineSegment StartX=1e-16 StartY=3.5 StartZ=0 EndX=-3.03109 EndY=1.75 EndZ=0
    g1: LineSegment StartX=-3.03109 StartY=1.75 StartZ=0 EndX=-3.03109 EndY=-1.75 EndZ=0
    g2: LineSegment StartX=-3.03109 StartY=-1.75 StartZ=0 EndX=-1e-16 EndY=-3.5 EndZ=0
    g3: LineSegment StartX=-1e-16 StartY=-3.5 StartZ=0 EndX=3.03109 EndY=-1.75 EndZ=0
    g4: LineSegment StartX=3.03109 StartY=-1.75 StartZ=0 EndX=3.03109 EndY=1.75 EndZ=0
    g5: LineSegment StartX=3.03109 StartY=1.75 StartZ=0 EndX=1e-16 EndY=3.5 EndZ=0
    g6: Circle [constr] CenterX=0 CenterY=0 CenterZ=0 NormalX=0 NormalY=0 NormalZ=1 AngleXU=0 Radius=3.5
    g7: LineSegment StartX=4.96892 StartY=-1.75002 StartZ=0 EndX=8.00002 EndY=-3.5 EndZ=0
    g8: LineSegment StartX=8.00002 StartY=-3.5 StartZ=0 EndX=11.0311 EndY=-1.74998 EndZ=0
    g9: LineSegment StartX=11.0311 StartY=-1.74998 StartZ=0 EndX=11.0311 EndY=1.75002 EndZ=0
    g10: LineSegment StartX=11.0311 StartY=1.75002 StartZ=0 EndX=7.99998 EndY=3.5 EndZ=0
    g11: LineSegment StartX=7.99998 StartY=3.5 StartZ=0 EndX=4.9689 EndY=1.74998 EndZ=0
    g12: LineSegment StartX=4.9689 StartY=1.74998 StartZ=0 EndX=4.96892 EndY=-1.75002 EndZ=0
    g13: Circle [constr] CenterX=8 CenterY=0 CenterZ=0 NormalX=0 NormalY=0 NormalZ=1 AngleXU=0 Radius=3.5
    g14: LineSegment StartX=4.03109 StartY=3.5 StartZ=0 EndX=7.06218 EndY=5.25 EndZ=0
    g15: LineSegment StartX=7.06218 StartY=5.25 StartZ=0 EndX=7.06218 EndY=8.75 EndZ=0
    g16: LineSegment StartX=7.06218 StartY=8.75 StartZ=0 EndX=4.03109 EndY=10.5 EndZ=0
    g17: LineSegment StartX=4.03109 StartY=10.5 StartZ=0 EndX=1 EndY=8.75 EndZ=0
    g18: LineSegment StartX=1 StartY=8.75 StartZ=0 EndX=1 EndY=5.25 EndZ=0
    g19: LineSegment StartX=1 StartY=5.25 StartZ=0 EndX=4.03109 EndY=3.5 EndZ=0
    g20: Circle [constr] CenterX=4.03109 CenterY=7 CenterZ=0 NormalX=0 NormalY=0 NormalZ=1 AngleXU=0 Radius=3.5
    g21: LineSegment StartX=-1 StartY=5.25 StartZ=0 EndX=-1 EndY=8.75 EndZ=0
    g22: LineSegment StartX=-1 StartY=8.75 StartZ=0 EndX=-4.03109 EndY=10.5 EndZ=0
    g23: LineSegment StartX=-4.03109 StartY=10.5 StartZ=0 EndX=-7.06218 EndY=8.75 EndZ=0
    g24: LineSegment StartX=-7.06218 StartY=8.75 StartZ=0 EndX=-7.06218 EndY=5.25 EndZ=0
    g25: LineSegment StartX=-7.06218 StartY=5.25 StartZ=0 EndX=-4.03109 EndY=3.5 EndZ=0
    g26: LineSegment StartX=-4.03109 StartY=3.5 StartZ=0 EndX=-1 EndY=5.25 EndZ=0
    g27: Circle [constr] CenterX=-4.03109 CenterY=7 CenterZ=0 NormalX=0 NormalY=0 NormalZ=1 AngleXU=0 Radius=3.5
    g28: LineSegment StartX=-4.96891 StartY=-1.75 StartZ=0 EndX=-4.96891 EndY=1.75 EndZ=0
    g29: LineSegment StartX=-4.96891 StartY=1.75 StartZ=0 EndX=-8 EndY=3.5 EndZ=0
    g30: LineSegment StartX=-8 StartY=3.5 StartZ=0 EndX=-11.0311 EndY=1.75 EndZ=0
    g31: LineSegment StartX=-11.0311 StartY=1.75 StartZ=0 EndX=-11.0311 EndY=-1.75 EndZ=0
    g32: LineSegment StartX=-11.0311 StartY=-1.75 StartZ=0 EndX=-8 EndY=-3.5 EndZ=0
    g33: LineSegment StartX=-8 StartY=-3.5 StartZ=0 EndX=-4.96891 EndY=-1.75 EndZ=0
    g34: Circle [constr] CenterX=-8 CenterY=0 CenterZ=0 NormalX=0 NormalY=0 NormalZ=1 AngleXU=0 Radius=3.5
    g35: LineSegment StartX=-4.03109 StartY=-3.5 StartZ=0 EndX=-7.06218 EndY=-5.25 EndZ=0
    g36: LineSegment StartX=-7.06218 StartY=-5.25 StartZ=0 EndX=-7.06218 EndY=-8.75 EndZ=0
    g37: LineSegment StartX=-7.06218 StartY=-8.75 StartZ=0 EndX=-4.03109 EndY=-10.5 EndZ=0
    g38: LineSegment StartX=-4.03109 StartY=-10.5 StartZ=0 EndX=-1 EndY=-8.75 EndZ=0
    g39: LineSegment StartX=-1 StartY=-8.75 StartZ=0 EndX=-1 EndY=-5.25 EndZ=0
    g40: LineSegment StartX=-1 StartY=-5.25 StartZ=0 EndX=-4.03109 EndY=-3.5 EndZ=0
    g41: Circle [constr] CenterX=-4.03109 CenterY=-7 CenterZ=0 NormalX=0 NormalY=0 NormalZ=1 AngleXU=0 Radius=3.5
    g42: LineSegment StartX=4.03109 StartY=-3.5 StartZ=0 EndX=1 EndY=-5.25 EndZ=0
    g43: LineSegment StartX=1 StartY=-5.25 StartZ=0 EndX=1 EndY=-8.75 EndZ=0
    g44: LineSegment StartX=1 StartY=-8.75 StartZ=0 EndX=4.03109 EndY=-10.5 EndZ=0
    g45: LineSegment StartX=4.03109 StartY=-10.5 StartZ=0 EndX=7.06218 EndY=-8.75 EndZ=0
    g46: LineSegment StartX=7.06218 StartY=-8.75 StartZ=0 EndX=7.06218 EndY=-5.25 EndZ=0
    g47: LineSegment StartX=7.06218 StartY=-5.25 StartZ=0 EndX=4.03109 EndY=-3.5 EndZ=0
    g48: Circle [constr] CenterX=4.03109 CenterY=-7 CenterZ=0 NormalX=0 NormalY=0 NormalZ=1 AngleXU=0 Radius=3.5
  constraints (117):
    c: Coincident(g0,g1)
    c: Coincident(g1,g2)
    c: Coincident(g2,g3)
    c: Coincident(g3,g4)
    c: Coincident(g4,g5)
    c: Coincident(g5,g0)
    c: Equal(g0, g1-g5) x5
    c: PointOnObject(g0,g6)
    c: PointOnObject(g1,g6)
    c: PointOnObject(g2,g6)
    c: PointOnObject(g3,g6)
    c: PointOnObject(g4,g6)
    c: PointOnObject(g5,g6)
    c: Coincident(g6,g-1)
    c: Diameter(g6) = 7
    c: PointOnObject(g0,g-2)
    c: Coincident(g7,g8)
    c: Coincident(g8,g9)
    c: Coincident(g9,g10)
    c: Coincident(g10,g11)
    c: Coincident(g11,g12)
    c: Coincident(g12,g7)
    c: Equal(g7, g8-g12) x5
    c: PointOnObject(g7,g13)
    c: PointOnObject(g8,g13)
    c: PointOnObject(g9,g13)
    c: PointOnObject(g10,g13)
    c: PointOnObject(g11,g13)
    c: PointOnObject(g12,g13)
    c: PointOnObject(g13,g-1)
    c: Diameter(g13) = 7
    c: Distance(g6,g13) = 8
    c: Horizontal(g0,g10)
    c: Coincident(g14,g15)
    c: Coincident(g15,g16)
    c: Coincident(g16,g17)
    c: Coincident(g17,g18)
    c: Coincident(g18,g19)
    c: Coincident(g19,g14)
    c: Equal(g14, g15-g19) x5
    c: PointOnObject(g14,g20)
    c: PointOnObject(g15,g20)
    c: PointOnObject(g16,g20)
    c: PointOnObject(g17,g20)
    c: PointOnObject(g18,g20)
    c: PointOnObject(g19,g20)
    c: Diameter(g20) = 7
    c: DistanceY(g-1,g20) = 7
    c: Vertical(g18)
    c: Distance(g17,g-2) = 1
    c: Coincident(g21,g22)
    c: Coincident(g22,g23)
    c: Coincident(g23,g24)
    c: Coincident(g24,g25)
    c: Coincident(g25,g26)
    c: Coincident(g26,g21)
    c: Equal(g21, g22-g26) x5
    c: PointOnObject(g21,g27)
    c: PointOnObject(g22,g27)
    c: PointOnObject(g23,g27)
    c: PointOnObject(g24,g27)
    c: PointOnObject(g25,g27)
    c: PointOnObject(g26,g27)
    c: Diameter(g27) = 7
    c: DistanceY(g-1,g27) = 7
    c: DistanceX(g21,g-1) = 1
    c: Vertical(g21)
    c: Coincident(g28,g29)
    c: Coincident(g29,g30)
    c: Coincident(g30,g31)
    c: Coincident(g31,g32)
    c: Coincident(g32,g33)
    c: Coincident(g33,g28)
    c: Equal(g28, g29-g33) x5
    c: PointOnObject(g28,g34)
    c: PointOnObject(g29,g34)
    c: PointOnObject(g30,g34)
    c: PointOnObject(g31,g34)
    c: PointOnObject(g32,g34)
    c: PointOnObject(g33,g34)
    c: PointOnObject(g34,g-1)
    c: Diameter(g34) = 7
    c: Vertical(g31)
    c: DistanceX(g34,g-1) = 8
    c: Coincident(g35,g36)
    c: Coincident(g36,g37)
    c: Coincident(g37,g38)
    c: Coincident(g38,g39)
    c: Coincident(g39,g40)
    c: Coincident(g40,g35)
    c: Equal(g35, g36-g40) x5
    c: PointOnObject(g35,g41)
    c: PointOnObject(g36,g41)
    c: PointOnObject(g37,g41)
    c: PointOnObject(g38,g41)
    c: PointOnObject(g39,g41)
    c: PointOnObject(g40,g41)
    c: Coincident(g42,g43)
    c: Coincident(g43,g44)
    c: Coincident(g44,g45)
    c: Coincident(g45,g46)
    c: Coincident(g46,g47)
    c: Coincident(g47,g42)
    c: Equal(g42, g43-g47) x5
    c: PointOnObject(g42,g48)
    c: PointOnObject(g43,g48)
    c: PointOnObject(g44,g48)
    c: PointOnObject(g45,g48)
    c: PointOnObject(g46,g48)
    c: PointOnObject(g47,g48)
    c: Equal(g41,g48)
    c: Diameter(g41) = 7
    c: Vertical(g39)
    c: Vertical(g43)
    c: Distance(g-2,g39) = 1
    c: Symmetric(g38,g43,g-2)
    c: Distance(g41,g-1) = 7
FEATURE [Part::Extrusion] Extrude457  label="hex072"
  Base = -> Sketch465
  Dir = (0,-1,2e-16)
  DirMode = 2
  FaceMakerClass = Part::FaceMakerBullseye
  FaceMakerMode = 3
  LengthFwd = 10
  LengthRev = 0
  Placement = pos=(-52,0,21) rot=(0,0,1;0rad)
  Solid = true
  Symmetric = false
FEATURE [Sketcher::SketchObject] Sketch466
  ArcFitTolerance = 1e-06
  FullyConstrained = true
  MakeInternals = false
  Placement = pos=(0,0,0) rot=(1,0,0;1.5708rad)
  sketch-geometry (49):
    g0: LineSegment StartX=1e-16 StartY=3.5 StartZ=0 EndX=-3.03109 EndY=1.75 EndZ=0
    g1: LineSegment StartX=-3.03109 StartY=1.75 StartZ=0 EndX=-3.03109 EndY=-1.75 EndZ=0
    g2: LineSegment StartX=-3.03109 StartY=-1.75 StartZ=0 EndX=-1e-16 EndY=-3.5 EndZ=0
    g3: LineSegment StartX=-1e-16 StartY=-3.5 StartZ=0 EndX=3.03109 EndY=-1.75 EndZ=0
    g4: LineSegment StartX=3.03109 StartY=-1.75 StartZ=0 EndX=3.03109 EndY=1.75 EndZ=0
    g5: LineSegment StartX=3.03109 StartY=1.75 StartZ=0 EndX=1e-16 EndY=3.5 EndZ=0
    g6: Circle [constr] CenterX=0 CenterY=0 CenterZ=0 NormalX=0 NormalY=0 NormalZ=1 AngleXU=0 Radius=3.5
    g7: LineSegment StartX=4.96892 StartY=-1.75002 StartZ=0 EndX=8.00002 EndY=-3.5 EndZ=0
    g8: LineSegment StartX=8.00002 StartY=-3.5 StartZ=0 EndX=11.0311 EndY=-1.74998 EndZ=0
    g9: LineSegment StartX=11.0311 StartY=-1.74998 StartZ=0 EndX=11.0311 EndY=1.75002 EndZ=0
    g10: LineSegment StartX=11.0311 StartY=1.75002 StartZ=0 EndX=7.99998 EndY=3.5 EndZ=0
    g11: LineSegment StartX=7.99998 StartY=3.5 StartZ=0 EndX=4.9689 EndY=1.74998 EndZ=0
    g12: LineSegment StartX=4.9689 StartY=1.74998 StartZ=0 EndX=4.96892 EndY=-1.75002 EndZ=0
    g13: Circle [constr] CenterX=8 CenterY=0 CenterZ=0 NormalX=0 NormalY=0 NormalZ=1 AngleXU=0 Radius=3.5
    g14: LineSegment StartX=4.03109 StartY=3.5 StartZ=0 EndX=7.06218 EndY=5.25 EndZ=0
    g15: LineSegment StartX=7.06218 StartY=5.25 StartZ=0 EndX=7.06218 EndY=8.75 EndZ=0
    g16: LineSegment StartX=7.06218 StartY=8.75 StartZ=0 EndX=4.03109 EndY=10.5 EndZ=0
    g17: LineSegment StartX=4.03109 StartY=10.5 StartZ=0 EndX=1 EndY=8.75 EndZ=0
    g18: LineSegment StartX=1 StartY=8.75 StartZ=0 EndX=1 EndY=5.25 EndZ=0
    g19: LineSegment StartX=1 StartY=5.25 StartZ=0 EndX=4.03109 EndY=3.5 EndZ=0
    g20: Circle [constr] CenterX=4.03109 CenterY=7 CenterZ=0 NormalX=0 NormalY=0 NormalZ=1 AngleXU=0 Radius=3.5
    g21: LineSegment StartX=-1 StartY=5.25 StartZ=0 EndX=-1 EndY=8.75 EndZ=0
    g22: LineSegment StartX=-1 StartY=8.75 StartZ=0 EndX=-4.03109 EndY=10.5 EndZ=0
    g23: LineSegment StartX=-4.03109 StartY=10.5 StartZ=0 EndX=-7.06218 EndY=8.75 EndZ=0
    g24: LineSegment StartX=-7.06218 StartY=8.75 StartZ=0 EndX=-7.06218 EndY=5.25 EndZ=0
    g25: LineSegment StartX=-7.06218 StartY=5.25 StartZ=0 EndX=-4.03109 EndY=3.5 EndZ=0
    g26: LineSegment StartX=-4.03109 StartY=3.5 StartZ=0 EndX=-1 EndY=5.25 EndZ=0
    g27: Circle [constr] CenterX=-4.03109 CenterY=7 CenterZ=0 NormalX=0 NormalY=0 NormalZ=1 AngleXU=0 Radius=3.5
    g28: LineSegment StartX=-4.96891 StartY=-1.75 StartZ=0 EndX=-4.96891 EndY=1.75 EndZ=0
    g29: LineSegment StartX=-4.96891 StartY=1.75 StartZ=0 EndX=-8 EndY=3.5 EndZ=0
    g30: LineSegment StartX=-8 StartY=3.5 StartZ=0 EndX=-11.0311 EndY=1.75 EndZ=0
    g31: LineSegment StartX=-11.0311 StartY=1.75 StartZ=0 EndX=-11.0311 EndY=-1.75 EndZ=0
    g32: LineSegment StartX=-11.0311 StartY=-1.75 StartZ=0 EndX=-8 EndY=-3.5 EndZ=0
    g33: LineSegment StartX=-8 StartY=-3.5 StartZ=0 EndX=-4.96891 EndY=-1.75 EndZ=0
    g34: Circle [constr] CenterX=-8 CenterY=0 CenterZ=0 NormalX=0 NormalY=0 NormalZ=1 AngleXU=0 Radius=3.5
    g35: LineSegment StartX=-4.03109 StartY=-3.5 StartZ=0 EndX=-7.06218 EndY=-5.25 EndZ=0
    g36: LineSegment StartX=-7.06218 StartY=-5.25 StartZ=0 EndX=-7.06218 EndY=-8.75 EndZ=0
    g37: LineSegment StartX=-7.06218 StartY=-8.75 StartZ=0 EndX=-4.03109 EndY=-10.5 EndZ=0
    g38: LineSegment StartX=-4.03109 StartY=-10.5 StartZ=0 EndX=-1 EndY=-8.75 EndZ=0
    g39: LineSegment StartX=-1 StartY=-8.75 StartZ=0 EndX=-1 EndY=-5.25 EndZ=0
    g40: LineSegment StartX=-1 StartY=-5.25 StartZ=0 EndX=-4.03109 EndY=-3.5 EndZ=0
    g41: Circle [constr] CenterX=-4.03109 CenterY=-7 CenterZ=0 NormalX=0 NormalY=0 NormalZ=1 AngleXU=0 Radius=3.5
    g42: LineSegment StartX=4.03109 StartY=-3.5 StartZ=0 EndX=1 EndY=-5.25 EndZ=0
    g43: LineSegment StartX=1 StartY=-5.25 StartZ=0 EndX=1 EndY=-8.75 EndZ=0
    g44: LineSegment StartX=1 StartY=-8.75 StartZ=0 EndX=4.03109 EndY=-10.5 EndZ=0
    g45: LineSegment StartX=4.03109 StartY=-10.5 StartZ=0 EndX=7.06218 EndY=-8.75 EndZ=0
    g46: LineSegment StartX=7.06218 StartY=-8.75 StartZ=0 EndX=7.06218 EndY=-5.25 EndZ=0
    g47: LineSegment StartX=7.06218 StartY=-5.25 StartZ=0 EndX=4.03109 EndY=-3.5 EndZ=0
    g48: Circle [constr] CenterX=4.03109 CenterY=-7 CenterZ=0 NormalX=0 NormalY=0 NormalZ=1 AngleXU=0 Radius=3.5
  constraints (117):
    c: Coincident(g0,g1)
    c: Coincident(g1,g2)
    c: Coincident(g2,g3)
    c: Coincident(g3,g4)
    c: Coincident(g4,g5)
    c: Coincident(g5,g0)
    c: Equal(g0, g1-g5) x5
    c: PointOnObject(g0,g6)
    c: PointOnObject(g1,g6)
    c: PointOnObject(g2,g6)
    c: PointOnObject(g3,g6)
    c: PointOnObject(g4,g6)
    c: PointOnObject(g5,g6)
    c: Coincident(g6,g-1)
    c: Diameter(g6) = 7
    c: PointOnObject(g0,g-2)
    c: Coincident(g7,g8)
    c: Coincident(g8,g9)
    c: Coincident(g9,g10)
    c: Coincident(g10,g11)
    c: Coincident(g11,g12)
    c: Coincident(g12,g7)
    c: Equal(g7, g8-g12) x5
    c: PointOnObject(g7,g13)
    c: PointOnObject(g8,g13)
    c: PointOnObject(g9,g13)
    c: PointOnObject(g10,g13)
    c: PointOnObject(g11,g13)
    c: PointOnObject(g12,g13)
    c: PointOnObject(g13,g-1)
    c: Diameter(g13) = 7
    c: Distance(g6,g13) = 8
    c: Horizontal(g0,g10)
    c: Coincident(g14,g15)
    c: Coincident(g15,g16)
    c: Coincident(g16,g17)
    c: Coincident(g17,g18)
    c: Coincident(g18,g19)
    c: Coincident(g19,g14)
    c: Equal(g14, g15-g19) x5
    c: PointOnObject(g14,g20)
    c: PointOnObject(g15,g20)
    c: PointOnObject(g16,g20)
    c: PointOnObject(g17,g20)
    c: PointOnObject(g18,g20)
    c: PointOnObject(g19,g20)
    c: Diameter(g20) = 7
    c: DistanceY(g-1,g20) = 7
    c: Vertical(g18)
    c: Distance(g17,g-2) = 1
    c: Coincident(g21,g22)
    c: Coincident(g22,g23)
    c: Coincident(g23,g24)
    c: Coincident(g24,g25)
    c: Coincident(g25,g26)
    c: Coincident(g26,g21)
    c: Equal(g21, g22-g26) x5
    c: PointOnObject(g21,g27)
    c: PointOnObject(g22,g27)
    c: PointOnObject(g23,g27)
    c: PointOnObject(g24,g27)
    c: PointOnObject(g25,g27)
    c: PointOnObject(g26,g27)
    c: Diameter(g27) = 7
    c: DistanceY(g-1,g27) = 7
    c: DistanceX(g21,g-1) = 1
    c: Vertical(g21)
    c: Coincident(g28,g29)
    c: Coincident(g29,g30)
    c: Coincident(g30,g31)
    c: Coincident(g31,g32)
    c: Coincident(g32,g33)
    c: Coincident(g33,g28)
    c: Equal(g28, g29-g33) x5
    c: PointOnObject(g28,g34)
    c: PointOnObject(g29,g34)
    c: PointOnObject(g30,g34)
    c: PointOnObject(g31,g34)
    c: PointOnObject(g32,g34)
    c: PointOnObject(g33,g34)
    c: PointOnObject(g34,g-1)
    c: Diameter(g34) = 7
    c: Vertical(g31)
    c: DistanceX(g34,g-1) = 8
    c: Coincident(g35,g36)
    c: Coincident(g36,g37)
    c: Coincident(g37,g38)
    c: Coincident(g38,g39)
    c: Coincident(g39,g40)
    c: Coincident(g40,g35)
    c: Equal(g35, g36-g40) x5
    c: PointOnObject(g35,g41)
    c: PointOnObject(g36,g41)
    c: PointOnObject(g37,g41)
    c: PointOnObject(g38,g41)
    c: PointOnObject(g39,g41)
    c: PointOnObject(g40,g41)
    c: Coincident(g42,g43)
    c: Coincident(g43,g44)
    c: Coincident(g44,g45)
    c: Coincident(g45,g46)
    c: Coincident(g46,g47)
    c: Coincident(g47,g42)
    c: Equal(g42, g43-g47) x5
    c: PointOnObject(g42,g48)
    c: PointOnObject(g43,g48)
    c: PointOnObject(g44,g48)
    c: PointOnObject(g45,g48)
    c: PointOnObject(g46,g48)
    c: PointOnObject(g47,g48)
    c: Equal(g41,g48)
    c: Diameter(g41) = 7
    c: Vertical(g39)
    c: Vertical(g43)
    c: Distance(g-2,g39) = 1
    c: Symmetric(g38,g43,g-2)
    c: Distance(g41,g-1) = 7
FEATURE [Part::Extrusion] Extrude458  label="hex073"
  Base = -> Sketch466
  Dir = (0,-1,2e-16)
  DirMode = 2
  FaceMakerClass = Part::FaceMakerBullseye
  FaceMakerMode = 3
  LengthFwd = 10
  LengthRev = 0
  Placement = pos=(52,0,21) rot=(0,0,1;0rad)
  Solid = true
  Symmetric = false
FEATURE [Sketcher::SketchObject] Sketch467
  ArcFitTolerance = 1e-06
  FullyConstrained = true
  MakeInternals = false
  Placement = pos=(0,0,0) rot=(1,0,0;1.5708rad)
  sketch-geometry (49):
    g0: LineSegment StartX=1e-16 StartY=3.5 StartZ=0 EndX=-3.03109 EndY=1.75 EndZ=0
    g1: LineSegment StartX=-3.03109 StartY=1.75 StartZ=0 EndX=-3.03109 EndY=-1.75 EndZ=0
    g2: LineSegment StartX=-3.03109 StartY=-1.75 StartZ=0 EndX=-1e-16 EndY=-3.5 EndZ=0
    g3: LineSegment StartX=-1e-16 StartY=-3.5 StartZ=0 EndX=3.03109 EndY=-1.75 EndZ=0
    g4: LineSegment StartX=3.03109 StartY=-1.75 StartZ=0 EndX=3.03109 EndY=1.75 EndZ=0
    g5: LineSegment StartX=3.03109 StartY=1.75 StartZ=0 EndX=1e-16 EndY=3.5 EndZ=0
    g6: Circle [constr] CenterX=0 CenterY=0 CenterZ=0 NormalX=0 NormalY=0 NormalZ=1 AngleXU=0 Radius=3.5
    g7: LineSegment StartX=4.96892 StartY=-1.75002 StartZ=0 EndX=8.00002 EndY=-3.5 EndZ=0
    g8: LineSegment StartX=8.00002 StartY=-3.5 StartZ=0 EndX=11.0311 EndY=-1.74998 EndZ=0
    g9: LineSegment StartX=11.0311 StartY=-1.74998 StartZ=0 EndX=11.0311 EndY=1.75002 EndZ=0
    g10: LineSegment StartX=11.0311 StartY=1.75002 StartZ=0 EndX=7.99998 EndY=3.5 EndZ=0
    g11: LineSegment StartX=7.99998 StartY=3.5 StartZ=0 EndX=4.9689 EndY=1.74998 EndZ=0
    g12: LineSegment StartX=4.9689 StartY=1.74998 StartZ=0 EndX=4.96892 EndY=-1.75002 EndZ=0
    g13: Circle [constr] CenterX=8 CenterY=0 CenterZ=0 NormalX=0 NormalY=0 NormalZ=1 AngleXU=0 Radius=3.5
    g14: LineSegment StartX=4.03109 StartY=3.5 StartZ=0 EndX=7.06218 EndY=5.25 EndZ=0
    g15: LineSegment StartX=7.06218 StartY=5.25 StartZ=0 EndX=7.06218 EndY=8.75 EndZ=0
    g16: LineSegment StartX=7.06218 StartY=8.75 StartZ=0 EndX=4.03109 EndY=10.5 EndZ=0
    g17: LineSegment StartX=4.03109 StartY=10.5 StartZ=0 EndX=1 EndY=8.75 EndZ=0
    g18: LineSegment StartX=1 StartY=8.75 StartZ=0 EndX=1 EndY=5.25 EndZ=0
    g19: LineSegment StartX=1 StartY=5.25 StartZ=0 EndX=4.03109 EndY=3.5 EndZ=0
    g20: Circle [constr] CenterX=4.03109 CenterY=7 CenterZ=0 NormalX=0 NormalY=0 NormalZ=1 AngleXU=0 Radius=3.5
    g21: LineSegment StartX=-1 StartY=5.25 StartZ=0 EndX=-1 EndY=8.75 EndZ=0
    g22: LineSegment StartX=-1 StartY=8.75 StartZ=0 EndX=-4.03109 EndY=10.5 EndZ=0
    g23: LineSegment StartX=-4.03109 StartY=10.5 StartZ=0 EndX=-7.06218 EndY=8.75 EndZ=0
    g24: LineSegment StartX=-7.06218 StartY=8.75 StartZ=0 EndX=-7.06218 EndY=5.25 EndZ=0
    g25: LineSegment StartX=-7.06218 StartY=5.25 StartZ=0 EndX=-4.03109 EndY=3.5 EndZ=0
    g26: LineSegment StartX=-4.03109 StartY=3.5 StartZ=0 EndX=-1 EndY=5.25 EndZ=0
    g27: Circle [constr] CenterX=-4.03109 CenterY=7 CenterZ=0 NormalX=0 NormalY=0 NormalZ=1 AngleXU=0 Radius=3.5
    g28: LineSegment StartX=-4.96891 StartY=-1.75 StartZ=0 EndX=-4.96891 EndY=1.75 EndZ=0
    g29: LineSegment StartX=-4.96891 StartY=1.75 StartZ=0 EndX=-8 EndY=3.5 EndZ=0
    g30: LineSegment StartX=-8 StartY=3.5 StartZ=0 EndX=-11.0311 EndY=1.75 EndZ=0
    g31: LineSegment StartX=-11.0311 StartY=1.75 StartZ=0 EndX=-11.0311 EndY=-1.75 EndZ=0
    g32: LineSegment StartX=-11.0311 StartY=-1.75 StartZ=0 EndX=-8 EndY=-3.5 EndZ=0
    g33: LineSegment StartX=-8 StartY=-3.5 StartZ=0 EndX=-4.96891 EndY=-1.75 EndZ=0
    g34: Circle [constr] CenterX=-8 CenterY=0 CenterZ=0 NormalX=0 NormalY=0 NormalZ=1 AngleXU=0 Radius=3.5
    g35: LineSegment StartX=-4.03109 StartY=-3.5 StartZ=0 EndX=-7.06218 EndY=-5.25 EndZ=0
    g36: LineSegment StartX=-7.06218 StartY=-5.25 StartZ=0 EndX=-7.06218 EndY=-8.75 EndZ=0
    g37: LineSegment StartX=-7.06218 StartY=-8.75 StartZ=0 EndX=-4.03109 EndY=-10.5 EndZ=0
    g38: LineSegment StartX=-4.03109 StartY=-10.5 StartZ=0 EndX=-1 EndY=-8.75 EndZ=0
    g39: LineSegment StartX=-1 StartY=-8.75 StartZ=0 EndX=-1 EndY=-5.25 EndZ=0
    g40: LineSegment StartX=-1 StartY=-5.25 StartZ=0 EndX=-4.03109 EndY=-3.5 EndZ=0
    g41: Circle [constr] CenterX=-4.03109 CenterY=-7 CenterZ=0 NormalX=0 NormalY=0 NormalZ=1 AngleXU=0 Radius=3.5
    g42: LineSegment StartX=4.03109 StartY=-3.5 StartZ=0 EndX=1 EndY=-5.25 EndZ=0
    g43: LineSegment StartX=1 StartY=-5.25 StartZ=0 EndX=1 EndY=-8.75 EndZ=0
    g44: LineSegment StartX=1 StartY=-8.75 StartZ=0 EndX=4.03109 EndY=-10.5 EndZ=0
    g45: LineSegment StartX=4.03109 StartY=-10.5 StartZ=0 EndX=7.06218 EndY=-8.75 EndZ=0
    g46: LineSegment StartX=7.06218 StartY=-8.75 StartZ=0 EndX=7.06218 EndY=-5.25 EndZ=0
    g47: LineSegment StartX=7.06218 StartY=-5.25 StartZ=0 EndX=4.03109 EndY=-3.5 EndZ=0
    g48: Circle [constr] CenterX=4.03109 CenterY=-7 CenterZ=0 NormalX=0 NormalY=0 NormalZ=1 AngleXU=0 Radius=3.5
  constraints (117):
    c: Coincident(g0,g1)
    c: Coincident(g1,g2)
    c: Coincident(g2,g3)
    c: Coincident(g3,g4)
    c: Coincident(g4,g5)
    c: Coincident(g5,g0)
    c: Equal(g0, g1-g5) x5
    c: PointOnObject(g0,g6)
    c: PointOnObject(g1,g6)
    c: PointOnObject(g2,g6)
    c: PointOnObject(g3,g6)
    c: PointOnObject(g4,g6)
    c: PointOnObject(g5,g6)
    c: Coincident(g6,g-1)
    c: Diameter(g6) = 7
    c: PointOnObject(g0,g-2)
    c: Coincident(g7,g8)
    c: Coincident(g8,g9)
    c: Coincident(g9,g10)
    c: Coincident(g10,g11)
    c: Coincident(g11,g12)
    c: Coincident(g12,g7)
    c: Equal(g7, g8-g12) x5
    c: PointOnObject(g7,g13)
    c: PointOnObject(g8,g13)
    c: PointOnObject(g9,g13)
    c: PointOnObject(g10,g13)
    c: PointOnObject(g11,g13)
    c: PointOnObject(g12,g13)
    c: PointOnObject(g13,g-1)
    c: Diameter(g13) = 7
    c: Distance(g6,g13) = 8
    c: Horizontal(g0,g10)
    c: Coincident(g14,g15)
    c: Coincident(g15,g16)
    c: Coincident(g16,g17)
    c: Coincident(g17,g18)
    c: Coincident(g18,g19)
    c: Coincident(g19,g14)
    c: Equal(g14, g15-g19) x5
    c: PointOnObject(g14,g20)
    c: PointOnObject(g15,g20)
    c: PointOnObject(g16,g20)
    c: PointOnObject(g17,g20)
    c: PointOnObject(g18,g20)
    c: PointOnObject(g19,g20)
    c: Diameter(g20) = 7
    c: DistanceY(g-1,g20) = 7
    c: Vertical(g18)
    c: Distance(g17,g-2) = 1
    c: Coincident(g21,g22)
    c: Coincident(g22,g23)
    c: Coincident(g23,g24)
    c: Coincident(g24,g25)
    c: Coincident(g25,g26)
    c: Coincident(g26,g21)
    c: Equal(g21, g22-g26) x5
    c: PointOnObject(g21,g27)
    c: PointOnObject(g22,g27)
    c: PointOnObject(g23,g27)
    c: PointOnObject(g24,g27)
    c: PointOnObject(g25,g27)
    c: PointOnObject(g26,g27)
    c: Diameter(g27) = 7
    c: DistanceY(g-1,g27) = 7
    c: DistanceX(g21,g-1) = 1
    c: Vertical(g21)
    c: Coincident(g28,g29)
    c: Coincident(g29,g30)
    c: Coincident(g30,g31)
    c: Coincident(g31,g32)
    c: Coincident(g32,g33)
    c: Coincident(g33,g28)
    c: Equal(g28, g29-g33) x5
    c: PointOnObject(g28,g34)
    c: PointOnObject(g29,g34)
    c: PointOnObject(g30,g34)
    c: PointOnObject(g31,g34)
    c: PointOnObject(g32,g34)
    c: PointOnObject(g33,g34)
    c: PointOnObject(g34,g-1)
    c: Diameter(g34) = 7
    c: Vertical(g31)
    c: DistanceX(g34,g-1) = 8
    c: Coincident(g35,g36)
    c: Coincident(g36,g37)
    c: Coincident(g37,g38)
    c: Coincident(g38,g39)
    c: Coincident(g39,g40)
    c: Coincident(g40,g35)
    c: Equal(g35, g36-g40) x5
    c: PointOnObject(g35,g41)
    c: PointOnObject(g36,g41)
    c: PointOnObject(g37,g41)
    c: PointOnObject(g38,g41)
    c: PointOnObject(g39,g41)
    c: PointOnObject(g40,g41)
    c: Coincident(g42,g43)
    c: Coincident(g43,g44)
    c: Coincident(g44,g45)
    c: Coincident(g45,g46)
    c: Coincident(g46,g47)
    c: Coincident(g47,g42)
    c: Equal(g42, g43-g47) x5
    c: PointOnObject(g42,g48)
    c: PointOnObject(g43,g48)
    c: PointOnObject(g44,g48)
    c: PointOnObject(g45,g48)
    c: PointOnObject(g46,g48)
    c: PointOnObject(g47,g48)
    c: Equal(g41,g48)
    c: Diameter(g41) = 7
    c: Vertical(g39)
    c: Vertical(g43)
    c: Distance(g-2,g39) = 1
    c: Symmetric(g38,g43,g-2)
    c: Distance(g41,g-1) = 7
FEATURE [Part::Extrusion] Extrude459  label="hex074"
  Base = -> Sketch467
  Dir = (0,-1,2e-16)
  DirMode = 2
  FaceMakerClass = Part::FaceMakerBullseye
  FaceMakerMode = 3
  LengthFwd = 10
  LengthRev = 0
  Placement = pos=(-32,0,28) rot=(0,0,1;0rad)
  Solid = true
  Symmetric = false
FEATURE [Sketcher::SketchObject] Sketch468
  ArcFitTolerance = 1e-06
  FullyConstrained = true
  MakeInternals = false
  Placement = pos=(0,0,0) rot=(1,0,0;1.5708rad)
  sketch-geometry (49):
    g0: LineSegment StartX=1e-16 StartY=3.5 StartZ=0 EndX=-3.03109 EndY=1.75 EndZ=0
    g1: LineSegment StartX=-3.03109 StartY=1.75 StartZ=0 EndX=-3.03109 EndY=-1.75 EndZ=0
    g2: LineSegment StartX=-3.03109 StartY=-1.75 StartZ=0 EndX=-1e-16 EndY=-3.5 EndZ=0
    g3: LineSegment StartX=-1e-16 StartY=-3.5 StartZ=0 EndX=3.03109 EndY=-1.75 EndZ=0
    g4: LineSegment StartX=3.03109 StartY=-1.75 StartZ=0 EndX=3.03109 EndY=1.75 EndZ=0
    g5: LineSegment StartX=3.03109 StartY=1.75 StartZ=0 EndX=1e-16 EndY=3.5 EndZ=0
    g6: Circle [constr] CenterX=0 CenterY=0 CenterZ=0 NormalX=0 NormalY=0 NormalZ=1 AngleXU=0 Radius=3.5
    g7: LineSegment StartX=4.96892 StartY=-1.75002 StartZ=0 EndX=8.00002 EndY=-3.5 EndZ=0
    g8: LineSegment StartX=8.00002 StartY=-3.5 StartZ=0 EndX=11.0311 EndY=-1.74998 EndZ=0
    g9: LineSegment StartX=11.0311 StartY=-1.74998 StartZ=0 EndX=11.0311 EndY=1.75002 EndZ=0
    g10: LineSegment StartX=11.0311 StartY=1.75002 StartZ=0 EndX=7.99998 EndY=3.5 EndZ=0
    g11: LineSegment StartX=7.99998 StartY=3.5 StartZ=0 EndX=4.9689 EndY=1.74998 EndZ=0
    g12: LineSegment StartX=4.9689 StartY=1.74998 StartZ=0 EndX=4.96892 EndY=-1.75002 EndZ=0
    g13: Circle [constr] CenterX=8 CenterY=0 CenterZ=0 NormalX=0 NormalY=0 NormalZ=1 AngleXU=0 Radius=3.5
    g14: LineSegment StartX=4.03109 StartY=3.5 StartZ=0 EndX=7.06218 EndY=5.25 EndZ=0
    g15: LineSegment StartX=7.06218 StartY=5.25 StartZ=0 EndX=7.06218 EndY=8.75 EndZ=0
    g16: LineSegment StartX=7.06218 StartY=8.75 StartZ=0 EndX=4.03109 EndY=10.5 EndZ=0
    g17: LineSegment StartX=4.03109 StartY=10.5 StartZ=0 EndX=1 EndY=8.75 EndZ=0
    g18: LineSegment StartX=1 StartY=8.75 StartZ=0 EndX=1 EndY=5.25 EndZ=0
    g19: LineSegment StartX=1 StartY=5.25 StartZ=0 EndX=4.03109 EndY=3.5 EndZ=0
    g20: Circle [constr] CenterX=4.03109 CenterY=7 CenterZ=0 NormalX=0 NormalY=0 NormalZ=1 AngleXU=0 Radius=3.5
    g21: LineSegment StartX=-1 StartY=5.25 StartZ=0 EndX=-1 EndY=8.75 EndZ=0
    g22: LineSegment StartX=-1 StartY=8.75 StartZ=0 EndX=-4.03109 EndY=10.5 EndZ=0
    g23: LineSegment StartX=-4.03109 StartY=10.5 StartZ=0 EndX=-7.06218 EndY=8.75 EndZ=0
    g24: LineSegment StartX=-7.06218 StartY=8.75 StartZ=0 EndX=-7.06218 EndY=5.25 EndZ=0
    g25: LineSegment StartX=-7.06218 StartY=5.25 StartZ=0 EndX=-4.03109 EndY=3.5 EndZ=0
    g26: LineSegment StartX=-4.03109 StartY=3.5 StartZ=0 EndX=-1 EndY=5.25 EndZ=0
    g27: Circle [constr] CenterX=-4.03109 CenterY=7 CenterZ=0 NormalX=0 NormalY=0 NormalZ=1 AngleXU=0 Radius=3.5
    g28: LineSegment StartX=-4.96891 StartY=-1.75 StartZ=0 EndX=-4.96891 EndY=1.75 EndZ=0
    g29: LineSegment StartX=-4.96891 StartY=1.75 StartZ=0 EndX=-8 EndY=3.5 EndZ=0
    g30: LineSegment StartX=-8 StartY=3.5 StartZ=0 EndX=-11.0311 EndY=1.75 EndZ=0
    g31: LineSegment StartX=-11.0311 StartY=1.75 StartZ=0 EndX=-11.0311 EndY=-1.75 EndZ=0
    g32: LineSegment StartX=-11.0311 StartY=-1.75 StartZ=0 EndX=-8 EndY=-3.5 EndZ=0
    g33: LineSegment StartX=-8 StartY=-3.5 StartZ=0 EndX=-4.96891 EndY=-1.75 EndZ=0
    g34: Circle [constr] CenterX=-8 CenterY=0 CenterZ=0 NormalX=0 NormalY=0 NormalZ=1 AngleXU=0 Radius=3.5
    g35: LineSegment StartX=-4.03109 StartY=-3.5 StartZ=0 EndX=-7.06218 EndY=-5.25 EndZ=0
    g36: LineSegment StartX=-7.06218 StartY=-5.25 StartZ=0 EndX=-7.06218 EndY=-8.75 EndZ=0
    g37: LineSegment StartX=-7.06218 StartY=-8.75 StartZ=0 EndX=-4.03109 EndY=-10.5 EndZ=0
    g38: LineSegment StartX=-4.03109 StartY=-10.5 StartZ=0 EndX=-1 EndY=-8.75 EndZ=0
    g39: LineSegment StartX=-1 StartY=-8.75 StartZ=0 EndX=-1 EndY=-5.25 EndZ=0
    g40: LineSegment StartX=-1 StartY=-5.25 StartZ=0 EndX=-4.03109 EndY=-3.5 EndZ=0
    g41: Circle [constr] CenterX=-4.03109 CenterY=-7 CenterZ=0 NormalX=0 NormalY=0 NormalZ=1 AngleXU=0 Radius=3.5
    g42: LineSegment StartX=4.03109 StartY=-3.5 StartZ=0 EndX=1 EndY=-5.25 EndZ=0
    g43: LineSegment StartX=1 StartY=-5.25 StartZ=0 EndX=1 EndY=-8.75 EndZ=0
    g44: LineSegment StartX=1 StartY=-8.75 StartZ=0 EndX=4.03109 EndY=-10.5 EndZ=0
    g45: LineSegment StartX=4.03109 StartY=-10.5 StartZ=0 EndX=7.06218 EndY=-8.75 EndZ=0
    g46: LineSegment StartX=7.06218 StartY=-8.75 StartZ=0 EndX=7.06218 EndY=-5.25 EndZ=0
    g47: LineSegment StartX=7.06218 StartY=-5.25 StartZ=0 EndX=4.03109 EndY=-3.5 EndZ=0
    g48: Circle [constr] CenterX=4.03109 CenterY=-7 CenterZ=0 NormalX=0 NormalY=0 NormalZ=1 AngleXU=0 Radius=3.5
  constraints (117):
    c: Coincident(g0,g1)
    c: Coincident(g1,g2)
    c: Coincident(g2,g3)
    c: Coincident(g3,g4)
    c: Coincident(g4,g5)
    c: Coincident(g5,g0)
    c: Equal(g0, g1-g5) x5
    c: PointOnObject(g0,g6)
    c: PointOnObject(g1,g6)
    c: PointOnObject(g2,g6)
    c: PointOnObject(g3,g6)
    c: PointOnObject(g4,g6)
    c: PointOnObject(g5,g6)
    c: Coincident(g6,g-1)
    c: Diameter(g6) = 7
    c: PointOnObject(g0,g-2)
    c: Coincident(g7,g8)
    c: Coincident(g8,g9)
    c: Coincident(g9,g10)
    c: Coincident(g10,g11)
    c: Coincident(g11,g12)
    c: Coincident(g12,g7)
    c: Equal(g7, g8-g12) x5
    c: PointOnObject(g7,g13)
    c: PointOnObject(g8,g13)
    c: PointOnObject(g9,g13)
    c: PointOnObject(g10,g13)
    c: PointOnObject(g11,g13)
    c: PointOnObject(g12,g13)
    c: PointOnObject(g13,g-1)
    c: Diameter(g13) = 7
    c: Distance(g6,g13) = 8
    c: Horizontal(g0,g10)
    c: Coincident(g14,g15)
    c: Coincident(g15,g16)
    c: Coincident(g16,g17)
    c: Coincident(g17,g18)
    c: Coincident(g18,g19)
    c: Coincident(g19,g14)
    c: Equal(g14, g15-g19) x5
    c: PointOnObject(g14,g20)
    c: PointOnObject(g15,g20)
    c: PointOnObject(g16,g20)
    c: PointOnObject(g17,g20)
    c: PointOnObject(g18,g20)
    c: PointOnObject(g19,g20)
    c: Diameter(g20) = 7
    c: DistanceY(g-1,g20) = 7
    c: Vertical(g18)
    c: Distance(g17,g-2) = 1
    c: Coincident(g21,g22)
    c: Coincident(g22,g23)
    c: Coincident(g23,g24)
    c: Coincident(g24,g25)
    c: Coincident(g25,g26)
    c: Coincident(g26,g21)
    c: Equal(g21, g22-g26) x5
    c: PointOnObject(g21,g27)
    c: PointOnObject(g22,g27)
    c: PointOnObject(g23,g27)
    c: PointOnObject(g24,g27)
    c: PointOnObject(g25,g27)
    c: PointOnObject(g26,g27)
    c: Diameter(g27) = 7
    c: DistanceY(g-1,g27) = 7
    c: DistanceX(g21,g-1) = 1
    c: Vertical(g21)
    c: Coincident(g28,g29)
    c: Coincident(g29,g30)
    c: Coincident(g30,g31)
    c: Coincident(g31,g32)
    c: Coincident(g32,g33)
    c: Coincident(g33,g28)
    c: Equal(g28, g29-g33) x5
    c: PointOnObject(g28,g34)
    c: PointOnObject(g29,g34)
    c: PointOnObject(g30,g34)
    c: PointOnObject(g31,g34)
    c: PointOnObject(g32,g34)
    c: PointOnObject(g33,g34)
    c: PointOnObject(g34,g-1)
    c: Diameter(g34) = 7
    c: Vertical(g31)
    c: DistanceX(g34,g-1) = 8
    c: Coincident(g35,g36)
    c: Coincident(g36,g37)
    c: Coincident(g37,g38)
    c: Coincident(g38,g39)
    c: Coincident(g39,g40)
    c: Coincident(g40,g35)
    c: Equal(g35, g36-g40) x5
    c: PointOnObject(g35,g41)
    c: PointOnObject(g36,g41)
    c: PointOnObject(g37,g41)
    c: PointOnObject(g38,g41)
    c: PointOnObject(g39,g41)
    c: PointOnObject(g40,g41)
    c: Coincident(g42,g43)
    c: Coincident(g43,g44)
    c: Coincident(g44,g45)
    c: Coincident(g45,g46)
    c: Coincident(g46,g47)
    c: Coincident(g47,g42)
    c: Equal(g42, g43-g47) x5
    c: PointOnObject(g42,g48)
    c: PointOnObject(g43,g48)
    c: PointOnObject(g44,g48)
    c: PointOnObject(g45,g48)
    c: PointOnObject(g46,g48)
    c: PointOnObject(g47,g48)
    c: Equal(g41,g48)
    c: Diameter(g41) = 7
    c: Vertical(g39)
    c: Vertical(g43)
    c: Distance(g-2,g39) = 1
    c: Symmetric(g38,g43,g-2)
    c: Distance(g41,g-1) = 7
FEATURE [Part::Extrusion] Extrude460  label="hex075"
  Base = -> Sketch468
  Dir = (0,-1,2e-16)
  DirMode = 2
  FaceMakerClass = Part::FaceMakerBullseye
  FaceMakerMode = 3
  LengthFwd = 10
  LengthRev = 0
  Placement = pos=(-12,0,35) rot=(0,0,1;0rad)
  Solid = true
  Symmetric = false
FEATURE [Sketcher::SketchObject] Sketch469
  ArcFitTolerance = 1e-06
  FullyConstrained = true
  MakeInternals = false
  Placement = pos=(0,0,0) rot=(1,0,0;1.5708rad)
  sketch-geometry (49):
    g0: LineSegment StartX=1e-16 StartY=3.5 StartZ=0 EndX=-3.03109 EndY=1.75 EndZ=0
    g1: LineSegment StartX=-3.03109 StartY=1.75 StartZ=0 EndX=-3.03109 EndY=-1.75 EndZ=0
    g2: LineSegment StartX=-3.03109 StartY=-1.75 StartZ=0 EndX=-1e-16 EndY=-3.5 EndZ=0
    g3: LineSegment StartX=-1e-16 StartY=-3.5 StartZ=0 EndX=3.03109 EndY=-1.75 EndZ=0
    g4: LineSegment StartX=3.03109 StartY=-1.75 StartZ=0 EndX=3.03109 EndY=1.75 EndZ=0
    g5: LineSegment StartX=3.03109 StartY=1.75 StartZ=0 EndX=1e-16 EndY=3.5 EndZ=0
    g6: Circle [constr] CenterX=0 CenterY=0 CenterZ=0 NormalX=0 NormalY=0 NormalZ=1 AngleXU=0 Radius=3.5
    g7: LineSegment StartX=4.96892 StartY=-1.75002 StartZ=0 EndX=8.00002 EndY=-3.5 EndZ=0
    g8: LineSegment StartX=8.00002 StartY=-3.5 StartZ=0 EndX=11.0311 EndY=-1.74998 EndZ=0
    g9: LineSegment StartX=11.0311 StartY=-1.74998 StartZ=0 EndX=11.0311 EndY=1.75002 EndZ=0
    g10: LineSegment StartX=11.0311 StartY=1.75002 StartZ=0 EndX=7.99998 EndY=3.5 EndZ=0
    g11: LineSegment StartX=7.99998 StartY=3.5 StartZ=0 EndX=4.9689 EndY=1.74998 EndZ=0
    g12: LineSegment StartX=4.9689 StartY=1.74998 StartZ=0 EndX=4.96892 EndY=-1.75002 EndZ=0
    g13: Circle [constr] CenterX=8 CenterY=0 CenterZ=0 NormalX=0 NormalY=0 NormalZ=1 AngleXU=0 Radius=3.5
    g14: LineSegment StartX=4.03109 StartY=3.5 StartZ=0 EndX=7.06218 EndY=5.25 EndZ=0
    g15: LineSegment StartX=7.06218 StartY=5.25 StartZ=0 EndX=7.06218 EndY=8.75 EndZ=0
    g16: LineSegment StartX=7.06218 StartY=8.75 StartZ=0 EndX=4.03109 EndY=10.5 EndZ=0
    g17: LineSegment StartX=4.03109 StartY=10.5 StartZ=0 EndX=1 EndY=8.75 EndZ=0
    g18: LineSegment StartX=1 StartY=8.75 StartZ=0 EndX=1 EndY=5.25 EndZ=0
    g19: LineSegment StartX=1 StartY=5.25 StartZ=0 EndX=4.03109 EndY=3.5 EndZ=0
    g20: Circle [constr] CenterX=4.03109 CenterY=7 CenterZ=0 NormalX=0 NormalY=0 NormalZ=1 AngleXU=0 Radius=3.5
    g21: LineSegment StartX=-1 StartY=5.25 StartZ=0 EndX=-1 EndY=8.75 EndZ=0
    g22: LineSegment StartX=-1 StartY=8.75 StartZ=0 EndX=-4.03109 EndY=10.5 EndZ=0
    g23: LineSegment StartX=-4.03109 StartY=10.5 StartZ=0 EndX=-7.06218 EndY=8.75 EndZ=0
    g24: LineSegment StartX=-7.06218 StartY=8.75 StartZ=0 EndX=-7.06218 EndY=5.25 EndZ=0
    g25: LineSegment StartX=-7.06218 StartY=5.25 StartZ=0 EndX=-4.03109 EndY=3.5 EndZ=0
    g26: LineSegment StartX=-4.03109 StartY=3.5 StartZ=0 EndX=-1 EndY=5.25 EndZ=0
    g27: Circle [constr] CenterX=-4.03109 CenterY=7 CenterZ=0 NormalX=0 NormalY=0 NormalZ=1 AngleXU=0 Radius=3.5
    g28: LineSegment StartX=-4.96891 StartY=-1.75 StartZ=0 EndX=-4.96891 EndY=1.75 EndZ=0
    g29: LineSegment StartX=-4.96891 StartY=1.75 StartZ=0 EndX=-8 EndY=3.5 EndZ=0
    g30: LineSegment StartX=-8 StartY=3.5 StartZ=0 EndX=-11.0311 EndY=1.75 EndZ=0
    g31: LineSegment StartX=-11.0311 StartY=1.75 StartZ=0 EndX=-11.0311 EndY=-1.75 EndZ=0
    g32: LineSegment StartX=-11.0311 StartY=-1.75 StartZ=0 EndX=-8 EndY=-3.5 EndZ=0
    g33: LineSegment StartX=-8 StartY=-3.5 StartZ=0 EndX=-4.96891 EndY=-1.75 EndZ=0
    g34: Circle [constr] CenterX=-8 CenterY=0 CenterZ=0 NormalX=0 NormalY=0 NormalZ=1 AngleXU=0 Radius=3.5
    g35: LineSegment StartX=-4.03109 StartY=-3.5 StartZ=0 EndX=-7.06218 EndY=-5.25 EndZ=0
    g36: LineSegment StartX=-7.06218 StartY=-5.25 StartZ=0 EndX=-7.06218 EndY=-8.75 EndZ=0
    g37: LineSegment StartX=-7.06218 StartY=-8.75 StartZ=0 EndX=-4.03109 EndY=-10.5 EndZ=0
    g38: LineSegment StartX=-4.03109 StartY=-10.5 StartZ=0 EndX=-1 EndY=-8.75 EndZ=0
    g39: LineSegment StartX=-1 StartY=-8.75 StartZ=0 EndX=-1 EndY=-5.25 EndZ=0
    g40: LineSegment StartX=-1 StartY=-5.25 StartZ=0 EndX=-4.03109 EndY=-3.5 EndZ=0
    g41: Circle [constr] CenterX=-4.03109 CenterY=-7 CenterZ=0 NormalX=0 NormalY=0 NormalZ=1 AngleXU=0 Radius=3.5
    g42: LineSegment StartX=4.03109 StartY=-3.5 StartZ=0 EndX=1 EndY=-5.25 EndZ=0
    g43: LineSegment StartX=1 StartY=-5.25 StartZ=0 EndX=1 EndY=-8.75 EndZ=0
    g44: LineSegment StartX=1 StartY=-8.75 StartZ=0 EndX=4.03109 EndY=-10.5 EndZ=0
    g45: LineSegment StartX=4.03109 StartY=-10.5 StartZ=0 EndX=7.06218 EndY=-8.75 EndZ=0
    g46: LineSegment StartX=7.06218 StartY=-8.75 StartZ=0 EndX=7.06218 EndY=-5.25 EndZ=0
    g47: LineSegment StartX=7.06218 StartY=-5.25 StartZ=0 EndX=4.03109 EndY=-3.5 EndZ=0
    g48: Circle [constr] CenterX=4.03109 CenterY=-7 CenterZ=0 NormalX=0 NormalY=0 NormalZ=1 AngleXU=0 Radius=3.5
  constraints (117):
    c: Coincident(g0,g1)
    c: Coincident(g1,g2)
    c: Coincident(g2,g3)
    c: Coincident(g3,g4)
    c: Coincident(g4,g5)
    c: Coincident(g5,g0)
    c: Equal(g0, g1-g5) x5
    c: PointOnObject(g0,g6)
    c: PointOnObject(g1,g6)
    c: PointOnObject(g2,g6)
    c: PointOnObject(g3,g6)
    c: PointOnObject(g4,g6)
    c: PointOnObject(g5,g6)
    c: Coincident(g6,g-1)
    c: Diameter(g6) = 7
    c: PointOnObject(g0,g-2)
    c: Coincident(g7,g8)
    c: Coincident(g8,g9)
    c: Coincident(g9,g10)
    c: Coincident(g10,g11)
    c: Coincident(g11,g12)
    c: Coincident(g12,g7)
    c: Equal(g7, g8-g12) x5
    c: PointOnObject(g7,g13)
    c: PointOnObject(g8,g13)
    c: PointOnObject(g9,g13)
    c: PointOnObject(g10,g13)
    c: PointOnObject(g11,g13)
    c: PointOnObject(g12,g13)
    c: PointOnObject(g13,g-1)
    c: Diameter(g13) = 7
    c: Distance(g6,g13) = 8
    c: Horizontal(g0,g10)
    c: Coincident(g14,g15)
    c: Coincident(g15,g16)
    c: Coincident(g16,g17)
    c: Coincident(g17,g18)
    c: Coincident(g18,g19)
    c: Coincident(g19,g14)
    c: Equal(g14, g15-g19) x5
    c: PointOnObject(g14,g20)
    c: PointOnObject(g15,g20)
    c: PointOnObject(g16,g20)
    c: PointOnObject(g17,g20)
    c: PointOnObject(g18,g20)
    c: PointOnObject(g19,g20)
    c: Diameter(g20) = 7
    c: DistanceY(g-1,g20) = 7
    c: Vertical(g18)
    c: Distance(g17,g-2) = 1
    c: Coincident(g21,g22)
    c: Coincident(g22,g23)
    c: Coincident(g23,g24)
    c: Coincident(g24,g25)
    c: Coincident(g25,g26)
    c: Coincident(g26,g21)
    c: Equal(g21, g22-g26) x5
    c: PointOnObject(g21,g27)
    c: PointOnObject(g22,g27)
    c: PointOnObject(g23,g27)
    c: PointOnObject(g24,g27)
    c: PointOnObject(g25,g27)
    c: PointOnObject(g26,g27)
    c: Diameter(g27) = 7
    c: DistanceY(g-1,g27) = 7
    c: DistanceX(g21,g-1) = 1
    c: Vertical(g21)
    c: Coincident(g28,g29)
    c: Coincident(g29,g30)
    c: Coincident(g30,g31)
    c: Coincident(g31,g32)
    c: Coincident(g32,g33)
    c: Coincident(g33,g28)
    c: Equal(g28, g29-g33) x5
    c: PointOnObject(g28,g34)
    c: PointOnObject(g29,g34)
    c: PointOnObject(g30,g34)
    c: PointOnObject(g31,g34)
    c: PointOnObject(g32,g34)
    c: PointOnObject(g33,g34)
    c: PointOnObject(g34,g-1)
    c: Diameter(g34) = 7
    c: Vertical(g31)
    c: DistanceX(g34,g-1) = 8
    c: Coincident(g35,g36)
    c: Coincident(g36,g37)
    c: Coincident(g37,g38)
    c: Coincident(g38,g39)
    c: Coincident(g39,g40)
    c: Coincident(g40,g35)
    c: Equal(g35, g36-g40) x5
    c: PointOnObject(g35,g41)
    c: PointOnObject(g36,g41)
    c: PointOnObject(g37,g41)
    c: PointOnObject(g38,g41)
    c: PointOnObject(g39,g41)
    c: PointOnObject(g40,g41)
    c: Coincident(g42,g43)
    c: Coincident(g43,g44)
    c: Coincident(g44,g45)
    c: Coincident(g45,g46)
    c: Coincident(g46,g47)
    c: Coincident(g47,g42)
    c: Equal(g42, g43-g47) x5
    c: PointOnObject(g42,g48)
    c: PointOnObject(g43,g48)
    c: PointOnObject(g44,g48)
    c: PointOnObject(g45,g48)
    c: PointOnObject(g46,g48)
    c: PointOnObject(g47,g48)
    c: Equal(g41,g48)
    c: Diameter(g41) = 7
    c: Vertical(g39)
    c: Vertical(g43)
    c: Distance(g-2,g39) = 1
    c: Symmetric(g38,g43,g-2)
    c: Distance(g41,g-1) = 7
FEATURE [Part::Extrusion] Extrude461  label="hex076"
  Base = -> Sketch469
  Dir = (0,-1,2e-16)
  DirMode = 2
  FaceMakerClass = Part::FaceMakerBullseye
  FaceMakerMode = 3
  LengthFwd = 10
  LengthRev = 0
  Placement = pos=(-80,0,0) rot=(0,0,1;0rad)
  Solid = true
  Symmetric = false
FEATURE [Sketcher::SketchObject] Sketch470
  ArcFitTolerance = 1e-06
  FullyConstrained = true
  MakeInternals = false
  Placement = pos=(0,0,0) rot=(1,0,0;1.5708rad)
  sketch-geometry (49):
    g0: LineSegment StartX=1e-16 StartY=3.5 StartZ=0 EndX=-3.03109 EndY=1.75 EndZ=0
    g1: LineSegment StartX=-3.03109 StartY=1.75 StartZ=0 EndX=-3.03109 EndY=-1.75 EndZ=0
    g2: LineSegment StartX=-3.03109 StartY=-1.75 StartZ=0 EndX=-1e-16 EndY=-3.5 EndZ=0
    g3: LineSegment StartX=-1e-16 StartY=-3.5 StartZ=0 EndX=3.03109 EndY=-1.75 EndZ=0
    g4: LineSegment StartX=3.03109 StartY=-1.75 StartZ=0 EndX=3.03109 EndY=1.75 EndZ=0
    g5: LineSegment StartX=3.03109 StartY=1.75 StartZ=0 EndX=1e-16 EndY=3.5 EndZ=0
    g6: Circle [constr] CenterX=0 CenterY=0 CenterZ=0 NormalX=0 NormalY=0 NormalZ=1 AngleXU=0 Radius=3.5
    g7: LineSegment StartX=4.96892 StartY=-1.75002 StartZ=0 EndX=8.00002 EndY=-3.5 EndZ=0
    g8: LineSegment StartX=8.00002 StartY=-3.5 StartZ=0 EndX=11.0311 EndY=-1.74998 EndZ=0
    g9: LineSegment StartX=11.0311 StartY=-1.74998 StartZ=0 EndX=11.0311 EndY=1.75002 EndZ=0
    g10: LineSegment StartX=11.0311 StartY=1.75002 StartZ=0 EndX=7.99998 EndY=3.5 EndZ=0
    g11: LineSegment StartX=7.99998 StartY=3.5 StartZ=0 EndX=4.9689 EndY=1.74998 EndZ=0
    g12: LineSegment StartX=4.9689 StartY=1.74998 StartZ=0 EndX=4.96892 EndY=-1.75002 EndZ=0
    g13: Circle [constr] CenterX=8 CenterY=0 CenterZ=0 NormalX=0 NormalY=0 NormalZ=1 AngleXU=0 Radius=3.5
    g14: LineSegment StartX=4.03109 StartY=3.5 StartZ=0 EndX=7.06218 EndY=5.25 EndZ=0
    g15: LineSegment StartX=7.06218 StartY=5.25 StartZ=0 EndX=7.06218 EndY=8.75 EndZ=0
    g16: LineSegment StartX=7.06218 StartY=8.75 StartZ=0 EndX=4.03109 EndY=10.5 EndZ=0
    g17: LineSegment StartX=4.03109 StartY=10.5 StartZ=0 EndX=1 EndY=8.75 EndZ=0
    g18: LineSegment StartX=1 StartY=8.75 StartZ=0 EndX=1 EndY=5.25 EndZ=0
    g19: LineSegment StartX=1 StartY=5.25 StartZ=0 EndX=4.03109 EndY=3.5 EndZ=0
    g20: Circle [constr] CenterX=4.03109 CenterY=7 CenterZ=0 NormalX=0 NormalY=0 NormalZ=1 AngleXU=0 Radius=3.5
    g21: LineSegment StartX=-1 StartY=5.25 StartZ=0 EndX=-1 EndY=8.75 EndZ=0
    g22: LineSegment StartX=-1 StartY=8.75 StartZ=0 EndX=-4.03109 EndY=10.5 EndZ=0
    g23: LineSegment StartX=-4.03109 StartY=10.5 StartZ=0 EndX=-7.06218 EndY=8.75 EndZ=0
    g24: LineSegment StartX=-7.06218 StartY=8.75 StartZ=0 EndX=-7.06218 EndY=5.25 EndZ=0
    g25: LineSegment StartX=-7.06218 StartY=5.25 StartZ=0 EndX=-4.03109 EndY=3.5 EndZ=0
    g26: LineSegment StartX=-4.03109 StartY=3.5 StartZ=0 EndX=-1 EndY=5.25 EndZ=0
    g27: Circle [constr] CenterX=-4.03109 CenterY=7 CenterZ=0 NormalX=0 NormalY=0 NormalZ=1 AngleXU=0 Radius=3.5
    g28: LineSegment StartX=-4.96891 StartY=-1.75 StartZ=0 EndX=-4.96891 EndY=1.75 EndZ=0
    g29: LineSegment StartX=-4.96891 StartY=1.75 StartZ=0 EndX=-8 EndY=3.5 EndZ=0
    g30: LineSegment StartX=-8 StartY=3.5 StartZ=0 EndX=-11.0311 EndY=1.75 EndZ=0
    g31: LineSegment StartX=-11.0311 StartY=1.75 StartZ=0 EndX=-11.0311 EndY=-1.75 EndZ=0
    g32: LineSegment StartX=-11.0311 StartY=-1.75 StartZ=0 EndX=-8 EndY=-3.5 EndZ=0
    g33: LineSegment StartX=-8 StartY=-3.5 StartZ=0 EndX=-4.96891 EndY=-1.75 EndZ=0
    g34: Circle [constr] CenterX=-8 CenterY=0 CenterZ=0 NormalX=0 NormalY=0 NormalZ=1 AngleXU=0 Radius=3.5
    g35: LineSegment StartX=-4.03109 StartY=-3.5 StartZ=0 EndX=-7.06218 EndY=-5.25 EndZ=0
    g36: LineSegment StartX=-7.06218 StartY=-5.25 StartZ=0 EndX=-7.06218 EndY=-8.75 EndZ=0
    g37: LineSegment StartX=-7.06218 StartY=-8.75 StartZ=0 EndX=-4.03109 EndY=-10.5 EndZ=0
    g38: LineSegment StartX=-4.03109 StartY=-10.5 StartZ=0 EndX=-1 EndY=-8.75 EndZ=0
    g39: LineSegment StartX=-1 StartY=-8.75 StartZ=0 EndX=-1 EndY=-5.25 EndZ=0
    g40: LineSegment StartX=-1 StartY=-5.25 StartZ=0 EndX=-4.03109 EndY=-3.5 EndZ=0
    g41: Circle [constr] CenterX=-4.03109 CenterY=-7 CenterZ=0 NormalX=0 NormalY=0 NormalZ=1 AngleXU=0 Radius=3.5
    g42: LineSegment StartX=4.03109 StartY=-3.5 StartZ=0 EndX=1 EndY=-5.25 EndZ=0
    g43: LineSegment StartX=1 StartY=-5.25 StartZ=0 EndX=1 EndY=-8.75 EndZ=0
    g44: LineSegment StartX=1 StartY=-8.75 StartZ=0 EndX=4.03109 EndY=-10.5 EndZ=0
    g45: LineSegment StartX=4.03109 StartY=-10.5 StartZ=0 EndX=7.06218 EndY=-8.75 EndZ=0
    g46: LineSegment StartX=7.06218 StartY=-8.75 StartZ=0 EndX=7.06218 EndY=-5.25 EndZ=0
    g47: LineSegment StartX=7.06218 StartY=-5.25 StartZ=0 EndX=4.03109 EndY=-3.5 EndZ=0
    g48: Circle [constr] CenterX=4.03109 CenterY=-7 CenterZ=0 NormalX=0 NormalY=0 NormalZ=1 AngleXU=0 Radius=3.5
  constraints (117):
    c: Coincident(g0,g1)
    c: Coincident(g1,g2)
    c: Coincident(g2,g3)
    c: Coincident(g3,g4)
    c: Coincident(g4,g5)
    c: Coincident(g5,g0)
    c: Equal(g0, g1-g5) x5
    c: PointOnObject(g0,g6)
    c: PointOnObject(g1,g6)
    c: PointOnObject(g2,g6)
    c: PointOnObject(g3,g6)
    c: PointOnObject(g4,g6)
    c: PointOnObject(g5,g6)
    c: Coincident(g6,g-1)
    c: Diameter(g6) = 7
    c: PointOnObject(g0,g-2)
    c: Coincident(g7,g8)
    c: Coincident(g8,g9)
    c: Coincident(g9,g10)
    c: Coincident(g10,g11)
    c: Coincident(g11,g12)
    c: Coincident(g12,g7)
    c: Equal(g7, g8-g12) x5
    c: PointOnObject(g7,g13)
    c: PointOnObject(g8,g13)
    c: PointOnObject(g9,g13)
    c: PointOnObject(g10,g13)
    c: PointOnObject(g11,g13)
    c: PointOnObject(g12,g13)
    c: PointOnObject(g13,g-1)
    c: Diameter(g13) = 7
    c: Distance(g6,g13) = 8
    c: Horizontal(g0,g10)
    c: Coincident(g14,g15)
    c: Coincident(g15,g16)
    c: Coincident(g16,g17)
    c: Coincident(g17,g18)
    c: Coincident(g18,g19)
    c: Coincident(g19,g14)
    c: Equal(g14, g15-g19) x5
    c: PointOnObject(g14,g20)
    c: PointOnObject(g15,g20)
    c: PointOnObject(g16,g20)
    c: PointOnObject(g17,g20)
    c: PointOnObject(g18,g20)
    c: PointOnObject(g19,g20)
    c: Diameter(g20) = 7
    c: DistanceY(g-1,g20) = 7
    c: Vertical(g18)
    c: Distance(g17,g-2) = 1
    c: Coincident(g21,g22)
    c: Coincident(g22,g23)
    c: Coincident(g23,g24)
    c: Coincident(g24,g25)
    c: Coincident(g25,g26)
    c: Coincident(g26,g21)
    c: Equal(g21, g22-g26) x5
    c: PointOnObject(g21,g27)
    c: PointOnObject(g22,g27)
    c: PointOnObject(g23,g27)
    c: PointOnObject(g24,g27)
    c: PointOnObject(g25,g27)
    c: PointOnObject(g26,g27)
    c: Diameter(g27) = 7
    c: DistanceY(g-1,g27) = 7
    c: DistanceX(g21,g-1) = 1
    c: Vertical(g21)
    c: Coincident(g28,g29)
    c: Coincident(g29,g30)
    c: Coincident(g30,g31)
    c: Coincident(g31,g32)
    c: Coincident(g32,g33)
    c: Coincident(g33,g28)
    c: Equal(g28, g29-g33) x5
    c: PointOnObject(g28,g34)
    c: PointOnObject(g29,g34)
    c: PointOnObject(g30,g34)
    c: PointOnObject(g31,g34)
    c: PointOnObject(g32,g34)
    c: PointOnObject(g33,g34)
    c: PointOnObject(g34,g-1)
    c: Diameter(g34) = 7
    c: Vertical(g31)
    c: DistanceX(g34,g-1) = 8
    c: Coincident(g35,g36)
    c: Coincident(g36,g37)
    c: Coincident(g37,g38)
    c: Coincident(g38,g39)
    c: Coincident(g39,g40)
    c: Coincident(g40,g35)
    c: Equal(g35, g36-g40) x5
    c: PointOnObject(g35,g41)
    c: PointOnObject(g36,g41)
    c: PointOnObject(g37,g41)
    c: PointOnObject(g38,g41)
    c: PointOnObject(g39,g41)
    c: PointOnObject(g40,g41)
    c: Coincident(g42,g43)
    c: Coincident(g43,g44)
    c: Coincident(g44,g45)
    c: Coincident(g45,g46)
    c: Coincident(g46,g47)
    c: Coincident(g47,g42)
    c: Equal(g42, g43-g47) x5
    c: PointOnObject(g42,g48)
    c: PointOnObject(g43,g48)
    c: PointOnObject(g44,g48)
    c: PointOnObject(g45,g48)
    c: PointOnObject(g46,g48)
    c: PointOnObject(g47,g48)
    c: Equal(g41,g48)
    c: Diameter(g41) = 7
    c: Vertical(g39)
    c: Vertical(g43)
    c: Distance(g-2,g39) = 1
    c: Symmetric(g38,g43,g-2)
    c: Distance(g41,g-1) = 7
FEATURE [Part::Extrusion] Extrude462  label="hex077"
  Base = -> Sketch470
  Dir = (0,-1,2e-16)
  DirMode = 2
  FaceMakerClass = Part::FaceMakerBullseye
  FaceMakerMode = 3
  LengthFwd = 10
  LengthRev = 0
  Placement = pos=(-104,0,0) rot=(0,0,1;0rad)
  Solid = true
  Symmetric = false
FEATURE [Sketcher::SketchObject] Sketch471
  ArcFitTolerance = 1e-06
  FullyConstrained = true
  MakeInternals = false
  Placement = pos=(0,0,0) rot=(1,0,0;1.5708rad)
  sketch-geometry (49):
    g0: LineSegment StartX=1e-16 StartY=3.5 StartZ=0 EndX=-3.03109 EndY=1.75 EndZ=0
    g1: LineSegment StartX=-3.03109 StartY=1.75 StartZ=0 EndX=-3.03109 EndY=-1.75 EndZ=0
    g2: LineSegment StartX=-3.03109 StartY=-1.75 StartZ=0 EndX=-1e-16 EndY=-3.5 EndZ=0
    g3: LineSegment StartX=-1e-16 StartY=-3.5 StartZ=0 EndX=3.03109 EndY=-1.75 EndZ=0
    g4: LineSegment StartX=3.03109 StartY=-1.75 StartZ=0 EndX=3.03109 EndY=1.75 EndZ=0
    g5: LineSegment StartX=3.03109 StartY=1.75 StartZ=0 EndX=1e-16 EndY=3.5 EndZ=0
    g6: Circle [constr] CenterX=0 CenterY=0 CenterZ=0 NormalX=0 NormalY=0 NormalZ=1 AngleXU=0 Radius=3.5
    g7: LineSegment StartX=4.96892 StartY=-1.75002 StartZ=0 EndX=8.00002 EndY=-3.5 EndZ=0
    g8: LineSegment StartX=8.00002 StartY=-3.5 StartZ=0 EndX=11.0311 EndY=-1.74998 EndZ=0
    g9: LineSegment StartX=11.0311 StartY=-1.74998 StartZ=0 EndX=11.0311 EndY=1.75002 EndZ=0
    g10: LineSegment StartX=11.0311 StartY=1.75002 StartZ=0 EndX=7.99998 EndY=3.5 EndZ=0
    g11: LineSegment StartX=7.99998 StartY=3.5 StartZ=0 EndX=4.9689 EndY=1.74998 EndZ=0
    g12: LineSegment StartX=4.9689 StartY=1.74998 StartZ=0 EndX=4.96892 EndY=-1.75002 EndZ=0
    g13: Circle [constr] CenterX=8 CenterY=0 CenterZ=0 NormalX=0 NormalY=0 NormalZ=1 AngleXU=0 Radius=3.5
    g14: LineSegment StartX=4.03109 StartY=3.5 StartZ=0 EndX=7.06218 EndY=5.25 EndZ=0
    g15: LineSegment StartX=7.06218 StartY=5.25 StartZ=0 EndX=7.06218 EndY=8.75 EndZ=0
    g16: LineSegment StartX=7.06218 StartY=8.75 StartZ=0 EndX=4.03109 EndY=10.5 EndZ=0
    g17: LineSegment StartX=4.03109 StartY=10.5 StartZ=0 EndX=1 EndY=8.75 EndZ=0
    g18: LineSegment StartX=1 StartY=8.75 StartZ=0 EndX=1 EndY=5.25 EndZ=0
    g19: LineSegment StartX=1 StartY=5.25 StartZ=0 EndX=4.03109 EndY=3.5 EndZ=0
    g20: Circle [constr] CenterX=4.03109 CenterY=7 CenterZ=0 NormalX=0 NormalY=0 NormalZ=1 AngleXU=0 Radius=3.5
    g21: LineSegment StartX=-1 StartY=5.25 StartZ=0 EndX=-1 EndY=8.75 EndZ=0
    g22: LineSegment StartX=-1 StartY=8.75 StartZ=0 EndX=-4.03109 EndY=10.5 EndZ=0
    g23: LineSegment StartX=-4.03109 StartY=10.5 StartZ=0 EndX=-7.06218 EndY=8.75 EndZ=0
    g24: LineSegment StartX=-7.06218 StartY=8.75 StartZ=0 EndX=-7.06218 EndY=5.25 EndZ=0
    g25: LineSegment StartX=-7.06218 StartY=5.25 StartZ=0 EndX=-4.03109 EndY=3.5 EndZ=0
    g26: LineSegment StartX=-4.03109 StartY=3.5 StartZ=0 EndX=-1 EndY=5.25 EndZ=0
    g27: Circle [constr] CenterX=-4.03109 CenterY=7 CenterZ=0 NormalX=0 NormalY=0 NormalZ=1 AngleXU=0 Radius=3.5
    g28: LineSegment StartX=-4.96891 StartY=-1.75 StartZ=0 EndX=-4.96891 EndY=1.75 EndZ=0
    g29: LineSegment StartX=-4.96891 StartY=1.75 StartZ=0 EndX=-8 EndY=3.5 EndZ=0
    g30: LineSegment StartX=-8 StartY=3.5 StartZ=0 EndX=-11.0311 EndY=1.75 EndZ=0
    g31: LineSegment StartX=-11.0311 StartY=1.75 StartZ=0 EndX=-11.0311 EndY=-1.75 EndZ=0
    g32: LineSegment StartX=-11.0311 StartY=-1.75 StartZ=0 EndX=-8 EndY=-3.5 EndZ=0
    g33: LineSegment StartX=-8 StartY=-3.5 StartZ=0 EndX=-4.96891 EndY=-1.75 EndZ=0
    g34: Circle [constr] CenterX=-8 CenterY=0 CenterZ=0 NormalX=0 NormalY=0 NormalZ=1 AngleXU=0 Radius=3.5
    g35: LineSegment StartX=-4.03109 StartY=-3.5 StartZ=0 EndX=-7.06218 EndY=-5.25 EndZ=0
    g36: LineSegment StartX=-7.06218 StartY=-5.25 StartZ=0 EndX=-7.06218 EndY=-8.75 EndZ=0
    g37: LineSegment StartX=-7.06218 StartY=-8.75 StartZ=0 EndX=-4.03109 EndY=-10.5 EndZ=0
    g38: LineSegment StartX=-4.03109 StartY=-10.5 StartZ=0 EndX=-1 EndY=-8.75 EndZ=0
    g39: LineSegment StartX=-1 StartY=-8.75 StartZ=0 EndX=-1 EndY=-5.25 EndZ=0
    g40: LineSegment StartX=-1 StartY=-5.25 StartZ=0 EndX=-4.03109 EndY=-3.5 EndZ=0
    g41: Circle [constr] CenterX=-4.03109 CenterY=-7 CenterZ=0 NormalX=0 NormalY=0 NormalZ=1 AngleXU=0 Radius=3.5
    g42: LineSegment StartX=4.03109 StartY=-3.5 StartZ=0 EndX=1 EndY=-5.25 EndZ=0
    g43: LineSegment StartX=1 StartY=-5.25 StartZ=0 EndX=1 EndY=-8.75 EndZ=0
    g44: LineSegment StartX=1 StartY=-8.75 StartZ=0 EndX=4.03109 EndY=-10.5 EndZ=0
    g45: LineSegment StartX=4.03109 StartY=-10.5 StartZ=0 EndX=7.06218 EndY=-8.75 EndZ=0
    g46: LineSegment StartX=7.06218 StartY=-8.75 StartZ=0 EndX=7.06218 EndY=-5.25 EndZ=0
    g47: LineSegment StartX=7.06218 StartY=-5.25 StartZ=0 EndX=4.03109 EndY=-3.5 EndZ=0
    g48: Circle [constr] CenterX=4.03109 CenterY=-7 CenterZ=0 NormalX=0 NormalY=0 NormalZ=1 AngleXU=0 Radius=3.5
  constraints (117):
    c: Coincident(g0,g1)
    c: Coincident(g1,g2)
    c: Coincident(g2,g3)
    c: Coincident(g3,g4)
    c: Coincident(g4,g5)
    c: Coincident(g5,g0)
    c: Equal(g0, g1-g5) x5
    c: PointOnObject(g0,g6)
    c: PointOnObject(g1,g6)
    c: PointOnObject(g2,g6)
    c: PointOnObject(g3,g6)
    c: PointOnObject(g4,g6)
    c: PointOnObject(g5,g6)
    c: Coincident(g6,g-1)
    c: Diameter(g6) = 7
    c: PointOnObject(g0,g-2)
    c: Coincident(g7,g8)
    c: Coincident(g8,g9)
    c: Coincident(g9,g10)
    c: Coincident(g10,g11)
    c: Coincident(g11,g12)
    c: Coincident(g12,g7)
    c: Equal(g7, g8-g12) x5
    c: PointOnObject(g7,g13)
    c: PointOnObject(g8,g13)
    c: PointOnObject(g9,g13)
    c: PointOnObject(g10,g13)
    c: PointOnObject(g11,g13)
    c: PointOnObject(g12,g13)
    c: PointOnObject(g13,g-1)
    c: Diameter(g13) = 7
    c: Distance(g6,g13) = 8
    c: Horizontal(g0,g10)
    c: Coincident(g14,g15)
    c: Coincident(g15,g16)
    c: Coincident(g16,g17)
    c: Coincident(g17,g18)
    c: Coincident(g18,g19)
    c: Coincident(g19,g14)
    c: Equal(g14, g15-g19) x5
    c: PointOnObject(g14,g20)
    c: PointOnObject(g15,g20)
    c: PointOnObject(g16,g20)
    c: PointOnObject(g17,g20)
    c: PointOnObject(g18,g20)
    c: PointOnObject(g19,g20)
    c: Diameter(g20) = 7
    c: DistanceY(g-1,g20) = 7
    c: Vertical(g18)
    c: Distance(g17,g-2) = 1
    c: Coincident(g21,g22)
    c: Coincident(g22,g23)
    c: Coincident(g23,g24)
    c: Coincident(g24,g25)
    c: Coincident(g25,g26)
    c: Coincident(g26,g21)
    c: Equal(g21, g22-g26) x5
    c: PointOnObject(g21,g27)
    c: PointOnObject(g22,g27)
    c: PointOnObject(g23,g27)
    c: PointOnObject(g24,g27)
    c: PointOnObject(g25,g27)
    c: PointOnObject(g26,g27)
    c: Diameter(g27) = 7
    c: DistanceY(g-1,g27) = 7
    c: DistanceX(g21,g-1) = 1
    c: Vertical(g21)
    c: Coincident(g28,g29)
    c: Coincident(g29,g30)
    c: Coincident(g30,g31)
    c: Coincident(g31,g32)
    c: Coincident(g32,g33)
    c: Coincident(g33,g28)
    c: Equal(g28, g29-g33) x5
    c: PointOnObject(g28,g34)
    c: PointOnObject(g29,g34)
    c: PointOnObject(g30,g34)
    c: PointOnObject(g31,g34)
    c: PointOnObject(g32,g34)
    c: PointOnObject(g33,g34)
    c: PointOnObject(g34,g-1)
    c: Diameter(g34) = 7
    c: Vertical(g31)
    c: DistanceX(g34,g-1) = 8
    c: Coincident(g35,g36)
    c: Coincident(g36,g37)
    c: Coincident(g37,g38)
    c: Coincident(g38,g39)
    c: Coincident(g39,g40)
    c: Coincident(g40,g35)
    c: Equal(g35, g36-g40) x5
    c: PointOnObject(g35,g41)
    c: PointOnObject(g36,g41)
    c: PointOnObject(g37,g41)
    c: PointOnObject(g38,g41)
    c: PointOnObject(g39,g41)
    c: PointOnObject(g40,g41)
    c: Coincident(g42,g43)
    c: Coincident(g43,g44)
    c: Coincident(g44,g45)
    c: Coincident(g45,g46)
    c: Coincident(g46,g47)
    c: Coincident(g47,g42)
    c: Equal(g42, g43-g47) x5
    c: PointOnObject(g42,g48)
    c: PointOnObject(g43,g48)
    c: PointOnObject(g44,g48)
    c: PointOnObject(g45,g48)
    c: PointOnObject(g46,g48)
    c: PointOnObject(g47,g48)
    c: Equal(g41,g48)
    c: Diameter(g41) = 7
    c: Vertical(g39)
    c: Vertical(g43)
    c: Distance(g-2,g39) = 1
    c: Symmetric(g38,g43,g-2)
    c: Distance(g41,g-1) = 7
FEATURE [Part::Extrusion] Extrude463  label="hex078"
  Base = -> Sketch471
  Dir = (0,-1,2e-16)
  DirMode = 2
  FaceMakerClass = Part::FaceMakerBullseye
  FaceMakerMode = 3
  LengthFwd = 10
  LengthRev = 0
  Placement = pos=(-64,0,14) rot=(0,0,1;0rad)
  Solid = true
  Symmetric = false
FEATURE [Sketcher::SketchObject] Sketch472
  ArcFitTolerance = 1e-06
  FullyConstrained = true
  MakeInternals = false
  Placement = pos=(0,0,0) rot=(1,0,0;1.5708rad)
  sketch-geometry (49):
    g0: LineSegment StartX=1e-16 StartY=3.5 StartZ=0 EndX=-3.03109 EndY=1.75 EndZ=0
    g1: LineSegment StartX=-3.03109 StartY=1.75 StartZ=0 EndX=-3.03109 EndY=-1.75 EndZ=0
    g2: LineSegment StartX=-3.03109 StartY=-1.75 StartZ=0 EndX=-1e-16 EndY=-3.5 EndZ=0
    g3: LineSegment StartX=-1e-16 StartY=-3.5 StartZ=0 EndX=3.03109 EndY=-1.75 EndZ=0
    g4: LineSegment StartX=3.03109 StartY=-1.75 StartZ=0 EndX=3.03109 EndY=1.75 EndZ=0
    g5: LineSegment StartX=3.03109 StartY=1.75 StartZ=0 EndX=1e-16 EndY=3.5 EndZ=0
    g6: Circle [constr] CenterX=0 CenterY=0 CenterZ=0 NormalX=0 NormalY=0 NormalZ=1 AngleXU=0 Radius=3.5
    g7: LineSegment StartX=4.96892 StartY=-1.75002 StartZ=0 EndX=8.00002 EndY=-3.5 EndZ=0
    g8: LineSegment StartX=8.00002 StartY=-3.5 StartZ=0 EndX=11.0311 EndY=-1.74998 EndZ=0
    g9: LineSegment StartX=11.0311 StartY=-1.74998 StartZ=0 EndX=11.0311 EndY=1.75002 EndZ=0
    g10: LineSegment StartX=11.0311 StartY=1.75002 StartZ=0 EndX=7.99998 EndY=3.5 EndZ=0
    g11: LineSegment StartX=7.99998 StartY=3.5 StartZ=0 EndX=4.9689 EndY=1.74998 EndZ=0
    g12: LineSegment StartX=4.9689 StartY=1.74998 StartZ=0 EndX=4.96892 EndY=-1.75002 EndZ=0
    g13: Circle [constr] CenterX=8 CenterY=0 CenterZ=0 NormalX=0 NormalY=0 NormalZ=1 AngleXU=0 Radius=3.5
    g14: LineSegment StartX=4.03109 StartY=3.5 StartZ=0 EndX=7.06218 EndY=5.25 EndZ=0
    g15: LineSegment StartX=7.06218 StartY=5.25 StartZ=0 EndX=7.06218 EndY=8.75 EndZ=0
    g16: LineSegment StartX=7.06218 StartY=8.75 StartZ=0 EndX=4.03109 EndY=10.5 EndZ=0
    g17: LineSegment StartX=4.03109 StartY=10.5 StartZ=0 EndX=1 EndY=8.75 EndZ=0
    g18: LineSegment StartX=1 StartY=8.75 StartZ=0 EndX=1 EndY=5.25 EndZ=0
    g19: LineSegment StartX=1 StartY=5.25 StartZ=0 EndX=4.03109 EndY=3.5 EndZ=0
    g20: Circle [constr] CenterX=4.03109 CenterY=7 CenterZ=0 NormalX=0 NormalY=0 NormalZ=1 AngleXU=0 Radius=3.5
    g21: LineSegment StartX=-1 StartY=5.25 StartZ=0 EndX=-1 EndY=8.75 EndZ=0
    g22: LineSegment StartX=-1 StartY=8.75 StartZ=0 EndX=-4.03109 EndY=10.5 EndZ=0
    g23: LineSegment StartX=-4.03109 StartY=10.5 StartZ=0 EndX=-7.06218 EndY=8.75 EndZ=0
    g24: LineSegment StartX=-7.06218 StartY=8.75 StartZ=0 EndX=-7.06218 EndY=5.25 EndZ=0
    g25: LineSegment StartX=-7.06218 StartY=5.25 StartZ=0 EndX=-4.03109 EndY=3.5 EndZ=0
    g26: LineSegment StartX=-4.03109 StartY=3.5 StartZ=0 EndX=-1 EndY=5.25 EndZ=0
    g27: Circle [constr] CenterX=-4.03109 CenterY=7 CenterZ=0 NormalX=0 NormalY=0 NormalZ=1 AngleXU=0 Radius=3.5
    g28: LineSegment StartX=-4.96891 StartY=-1.75 StartZ=0 EndX=-4.96891 EndY=1.75 EndZ=0
    g29: LineSegment StartX=-4.96891 StartY=1.75 StartZ=0 EndX=-8 EndY=3.5 EndZ=0
    g30: LineSegment StartX=-8 StartY=3.5 StartZ=0 EndX=-11.0311 EndY=1.75 EndZ=0
    g31: LineSegment StartX=-11.0311 StartY=1.75 StartZ=0 EndX=-11.0311 EndY=-1.75 EndZ=0
    g32: LineSegment StartX=-11.0311 StartY=-1.75 StartZ=0 EndX=-8 EndY=-3.5 EndZ=0
    g33: LineSegment StartX=-8 StartY=-3.5 StartZ=0 EndX=-4.96891 EndY=-1.75 EndZ=0
    g34: Circle [constr] CenterX=-8 CenterY=0 CenterZ=0 NormalX=0 NormalY=0 NormalZ=1 AngleXU=0 Radius=3.5
    g35: LineSegment StartX=-4.03109 StartY=-3.5 StartZ=0 EndX=-7.06218 EndY=-5.25 EndZ=0
    g36: LineSegment StartX=-7.06218 StartY=-5.25 StartZ=0 EndX=-7.06218 EndY=-8.75 EndZ=0
    g37: LineSegment StartX=-7.06218 StartY=-8.75 StartZ=0 EndX=-4.03109 EndY=-10.5 EndZ=0
    g38: LineSegment StartX=-4.03109 StartY=-10.5 StartZ=0 EndX=-1 EndY=-8.75 EndZ=0
    g39: LineSegment StartX=-1 StartY=-8.75 StartZ=0 EndX=-1 EndY=-5.25 EndZ=0
    g40: LineSegment StartX=-1 StartY=-5.25 StartZ=0 EndX=-4.03109 EndY=-3.5 EndZ=0
    g41: Circle [constr] CenterX=-4.03109 CenterY=-7 CenterZ=0 NormalX=0 NormalY=0 NormalZ=1 AngleXU=0 Radius=3.5
    g42: LineSegment StartX=4.03109 StartY=-3.5 StartZ=0 EndX=1 EndY=-5.25 EndZ=0
    g43: LineSegment StartX=1 StartY=-5.25 StartZ=0 EndX=1 EndY=-8.75 EndZ=0
    g44: LineSegment StartX=1 StartY=-8.75 StartZ=0 EndX=4.03109 EndY=-10.5 EndZ=0
    g45: LineSegment StartX=4.03109 StartY=-10.5 StartZ=0 EndX=7.06218 EndY=-8.75 EndZ=0
    g46: LineSegment StartX=7.06218 StartY=-8.75 StartZ=0 EndX=7.06218 EndY=-5.25 EndZ=0
    g47: LineSegment StartX=7.06218 StartY=-5.25 StartZ=0 EndX=4.03109 EndY=-3.5 EndZ=0
    g48: Circle [constr] CenterX=4.03109 CenterY=-7 CenterZ=0 NormalX=0 NormalY=0 NormalZ=1 AngleXU=0 Radius=3.5
  constraints (117):
    c: Coincident(g0,g1)
    c: Coincident(g1,g2)
    c: Coincident(g2,g3)
    c: Coincident(g3,g4)
    c: Coincident(g4,g5)
    c: Coincident(g5,g0)
    c: Equal(g0, g1-g5) x5
    c: PointOnObject(g0,g6)
    c: PointOnObject(g1,g6)
    c: PointOnObject(g2,g6)
    c: PointOnObject(g3,g6)
    c: PointOnObject(g4,g6)
    c: PointOnObject(g5,g6)
    c: Coincident(g6,g-1)
    c: Diameter(g6) = 7
    c: PointOnObject(g0,g-2)
    c: Coincident(g7,g8)
    c: Coincident(g8,g9)
    c: Coincident(g9,g10)
    c: Coincident(g10,g11)
    c: Coincident(g11,g12)
    c: Coincident(g12,g7)
    c: Equal(g7, g8-g12) x5
    c: PointOnObject(g7,g13)
    c: PointOnObject(g8,g13)
    c: PointOnObject(g9,g13)
    c: PointOnObject(g10,g13)
    c: PointOnObject(g11,g13)
    c: PointOnObject(g12,g13)
    c: PointOnObject(g13,g-1)
    c: Diameter(g13) = 7
    c: Distance(g6,g13) = 8
    c: Horizontal(g0,g10)
    c: Coincident(g14,g15)
    c: Coincident(g15,g16)
    c: Coincident(g16,g17)
    c: Coincident(g17,g18)
    c: Coincident(g18,g19)
    c: Coincident(g19,g14)
    c: Equal(g14, g15-g19) x5
    c: PointOnObject(g14,g20)
    c: PointOnObject(g15,g20)
    c: PointOnObject(g16,g20)
    c: PointOnObject(g17,g20)
    c: PointOnObject(g18,g20)
    c: PointOnObject(g19,g20)
    c: Diameter(g20) = 7
    c: DistanceY(g-1,g20) = 7
    c: Vertical(g18)
    c: Distance(g17,g-2) = 1
    c: Coincident(g21,g22)
    c: Coincident(g22,g23)
    c: Coincident(g23,g24)
    c: Coincident(g24,g25)
    c: Coincident(g25,g26)
    c: Coincident(g26,g21)
    c: Equal(g21, g22-g26) x5
    c: PointOnObject(g21,g27)
    c: PointOnObject(g22,g27)
    c: PointOnObject(g23,g27)
    c: PointOnObject(g24,g27)
    c: PointOnObject(g25,g27)
    c: PointOnObject(g26,g27)
    c: Diameter(g27) = 7
    c: DistanceY(g-1,g27) = 7
    c: DistanceX(g21,g-1) = 1
    c: Vertical(g21)
    c: Coincident(g28,g29)
    c: Coincident(g29,g30)
    c: Coincident(g30,g31)
    c: Coincident(g31,g32)
    c: Coincident(g32,g33)
    c: Coincident(g33,g28)
    c: Equal(g28, g29-g33) x5
    c: PointOnObject(g28,g34)
    c: PointOnObject(g29,g34)
    c: PointOnObject(g30,g34)
    c: PointOnObject(g31,g34)
    c: PointOnObject(g32,g34)
    c: PointOnObject(g33,g34)
    c: PointOnObject(g34,g-1)
    c: Diameter(g34) = 7
    c: Vertical(g31)
    c: DistanceX(g34,g-1) = 8
    c: Coincident(g35,g36)
    c: Coincident(g36,g37)
    c: Coincident(g37,g38)
    c: Coincident(g38,g39)
    c: Coincident(g39,g40)
    c: Coincident(g40,g35)
    c: Equal(g35, g36-g40) x5
    c: PointOnObject(g35,g41)
    c: PointOnObject(g36,g41)
    c: PointOnObject(g37,g41)
    c: PointOnObject(g38,g41)
    c: PointOnObject(g39,g41)
    c: PointOnObject(g40,g41)
    c: Coincident(g42,g43)
    c: Coincident(g43,g44)
    c: Coincident(g44,g45)
    c: Coincident(g45,g46)
    c: Coincident(g46,g47)
    c: Coincident(g47,g42)
    c: Equal(g42, g43-g47) x5
    c: PointOnObject(g42,g48)
    c: PointOnObject(g43,g48)
    c: PointOnObject(g44,g48)
    c: PointOnObject(g45,g48)
    c: PointOnObject(g46,g48)
    c: PointOnObject(g47,g48)
    c: Equal(g41,g48)
    c: Diameter(g41) = 7
    c: Vertical(g39)
    c: Vertical(g43)
    c: Distance(g-2,g39) = 1
    c: Symmetric(g38,g43,g-2)
    c: Distance(g41,g-1) = 7
FEATURE [Part::Extrusion] Extrude464  label="hex079"
  Base = -> Sketch472
  Dir = (0,-1,2e-16)
  DirMode = 2
  FaceMakerClass = Part::FaceMakerBullseye
  FaceMakerMode = 3
  LengthFwd = 10
  LengthRev = 0
  Placement = pos=(-64,0,-14) rot=(0,0,1;0rad)
  Solid = true
  Symmetric = false
FEATURE [Sketcher::SketchObject] Sketch473
  ArcFitTolerance = 1e-06
  FullyConstrained = true
  MakeInternals = false
  Placement = pos=(0,0,0) rot=(1,0,0;1.5708rad)
  sketch-geometry (49):
    g0: LineSegment StartX=1e-16 StartY=3.5 StartZ=0 EndX=-3.03109 EndY=1.75 EndZ=0
    g1: LineSegment StartX=-3.03109 StartY=1.75 StartZ=0 EndX=-3.03109 EndY=-1.75 EndZ=0
    g2: LineSegment StartX=-3.03109 StartY=-1.75 StartZ=0 EndX=-1e-16 EndY=-3.5 EndZ=0
    g3: LineSegment StartX=-1e-16 StartY=-3.5 StartZ=0 EndX=3.03109 EndY=-1.75 EndZ=0
    g4: LineSegment StartX=3.03109 StartY=-1.75 StartZ=0 EndX=3.03109 EndY=1.75 EndZ=0
    g5: LineSegment StartX=3.03109 StartY=1.75 StartZ=0 EndX=1e-16 EndY=3.5 EndZ=0
    g6: Circle [constr] CenterX=0 CenterY=0 CenterZ=0 NormalX=0 NormalY=0 NormalZ=1 AngleXU=0 Radius=3.5
    g7: LineSegment StartX=4.96892 StartY=-1.75002 StartZ=0 EndX=8.00002 EndY=-3.5 EndZ=0
    g8: LineSegment StartX=8.00002 StartY=-3.5 StartZ=0 EndX=11.0311 EndY=-1.74998 EndZ=0
    g9: LineSegment StartX=11.0311 StartY=-1.74998 StartZ=0 EndX=11.0311 EndY=1.75002 EndZ=0
    g10: LineSegment StartX=11.0311 StartY=1.75002 StartZ=0 EndX=7.99998 EndY=3.5 EndZ=0
    g11: LineSegment StartX=7.99998 StartY=3.5 StartZ=0 EndX=4.9689 EndY=1.74998 EndZ=0
    g12: LineSegment StartX=4.9689 StartY=1.74998 StartZ=0 EndX=4.96892 EndY=-1.75002 EndZ=0
    g13: Circle [constr] CenterX=8 CenterY=0 CenterZ=0 NormalX=0 NormalY=0 NormalZ=1 AngleXU=0 Radius=3.5
    g14: LineSegment StartX=4.03109 StartY=3.5 StartZ=0 EndX=7.06218 EndY=5.25 EndZ=0
    g15: LineSegment StartX=7.06218 StartY=5.25 StartZ=0 EndX=7.06218 EndY=8.75 EndZ=0
    g16: LineSegment StartX=7.06218 StartY=8.75 StartZ=0 EndX=4.03109 EndY=10.5 EndZ=0
    g17: LineSegment StartX=4.03109 StartY=10.5 StartZ=0 EndX=1 EndY=8.75 EndZ=0
    g18: LineSegment StartX=1 StartY=8.75 StartZ=0 EndX=1 EndY=5.25 EndZ=0
    g19: LineSegment StartX=1 StartY=5.25 StartZ=0 EndX=4.03109 EndY=3.5 EndZ=0
    g20: Circle [constr] CenterX=4.03109 CenterY=7 CenterZ=0 NormalX=0 NormalY=0 NormalZ=1 AngleXU=0 Radius=3.5
    g21: LineSegment StartX=-1 StartY=5.25 StartZ=0 EndX=-1 EndY=8.75 EndZ=0
    g22: LineSegment StartX=-1 StartY=8.75 StartZ=0 EndX=-4.03109 EndY=10.5 EndZ=0
    g23: LineSegment StartX=-4.03109 StartY=10.5 StartZ=0 EndX=-7.06218 EndY=8.75 EndZ=0
    g24: LineSegment StartX=-7.06218 StartY=8.75 StartZ=0 EndX=-7.06218 EndY=5.25 EndZ=0
    g25: LineSegment StartX=-7.06218 StartY=5.25 StartZ=0 EndX=-4.03109 EndY=3.5 EndZ=0
    g26: LineSegment StartX=-4.03109 StartY=3.5 StartZ=0 EndX=-1 EndY=5.25 EndZ=0
    g27: Circle [constr] CenterX=-4.03109 CenterY=7 CenterZ=0 NormalX=0 NormalY=0 NormalZ=1 AngleXU=0 Radius=3.5
    g28: LineSegment StartX=-4.96891 StartY=-1.75 StartZ=0 EndX=-4.96891 EndY=1.75 EndZ=0
    g29: LineSegment StartX=-4.96891 StartY=1.75 StartZ=0 EndX=-8 EndY=3.5 EndZ=0
    g30: LineSegment StartX=-8 StartY=3.5 StartZ=0 EndX=-11.0311 EndY=1.75 EndZ=0
    g31: LineSegment StartX=-11.0311 StartY=1.75 StartZ=0 EndX=-11.0311 EndY=-1.75 EndZ=0
    g32: LineSegment StartX=-11.0311 StartY=-1.75 StartZ=0 EndX=-8 EndY=-3.5 EndZ=0
    g33: LineSegment StartX=-8 StartY=-3.5 StartZ=0 EndX=-4.96891 EndY=-1.75 EndZ=0
    g34: Circle [constr] CenterX=-8 CenterY=0 CenterZ=0 NormalX=0 NormalY=0 NormalZ=1 AngleXU=0 Radius=3.5
    g35: LineSegment StartX=-4.03109 StartY=-3.5 StartZ=0 EndX=-7.06218 EndY=-5.25 EndZ=0
    g36: LineSegment StartX=-7.06218 StartY=-5.25 StartZ=0 EndX=-7.06218 EndY=-8.75 EndZ=0
    g37: LineSegment StartX=-7.06218 StartY=-8.75 StartZ=0 EndX=-4.03109 EndY=-10.5 EndZ=0
    g38: LineSegment StartX=-4.03109 StartY=-10.5 StartZ=0 EndX=-1 EndY=-8.75 EndZ=0
    g39: LineSegment StartX=-1 StartY=-8.75 StartZ=0 EndX=-1 EndY=-5.25 EndZ=0
    g40: LineSegment StartX=-1 StartY=-5.25 StartZ=0 EndX=-4.03109 EndY=-3.5 EndZ=0
    g41: Circle [constr] CenterX=-4.03109 CenterY=-7 CenterZ=0 NormalX=0 NormalY=0 NormalZ=1 AngleXU=0 Radius=3.5
    g42: LineSegment StartX=4.03109 StartY=-3.5 StartZ=0 EndX=1 EndY=-5.25 EndZ=0
    g43: LineSegment StartX=1 StartY=-5.25 StartZ=0 EndX=1 EndY=-8.75 EndZ=0
    g44: LineSegment StartX=1 StartY=-8.75 StartZ=0 EndX=4.03109 EndY=-10.5 EndZ=0
    g45: LineSegment StartX=4.03109 StartY=-10.5 StartZ=0 EndX=7.06218 EndY=-8.75 EndZ=0
    g46: LineSegment StartX=7.06218 StartY=-8.75 StartZ=0 EndX=7.06218 EndY=-5.25 EndZ=0
    g47: LineSegment StartX=7.06218 StartY=-5.25 StartZ=0 EndX=4.03109 EndY=-3.5 EndZ=0
    g48: Circle [constr] CenterX=4.03109 CenterY=-7 CenterZ=0 NormalX=0 NormalY=0 NormalZ=1 AngleXU=0 Radius=3.5
  constraints (117):
    c: Coincident(g0,g1)
    c: Coincident(g1,g2)
    c: Coincident(g2,g3)
    c: Coincident(g3,g4)
    c: Coincident(g4,g5)
    c: Coincident(g5,g0)
    c: Equal(g0, g1-g5) x5
    c: PointOnObject(g0,g6)
    c: PointOnObject(g1,g6)
    c: PointOnObject(g2,g6)
    c: PointOnObject(g3,g6)
    c: PointOnObject(g4,g6)
    c: PointOnObject(g5,g6)
    c: Coincident(g6,g-1)
    c: Diameter(g6) = 7
    c: PointOnObject(g0,g-2)
    c: Coincident(g7,g8)
    c: Coincident(g8,g9)
    c: Coincident(g9,g10)
    c: Coincident(g10,g11)
    c: Coincident(g11,g12)
    c: Coincident(g12,g7)
    c: Equal(g7, g8-g12) x5
    c: PointOnObject(g7,g13)
    c: PointOnObject(g8,g13)
    c: PointOnObject(g9,g13)
    c: PointOnObject(g10,g13)
    c: PointOnObject(g11,g13)
    c: PointOnObject(g12,g13)
    c: PointOnObject(g13,g-1)
    c: Diameter(g13) = 7
    c: Distance(g6,g13) = 8
    c: Horizontal(g0,g10)
    c: Coincident(g14,g15)
    c: Coincident(g15,g16)
    c: Coincident(g16,g17)
    c: Coincident(g17,g18)
    c: Coincident(g18,g19)
    c: Coincident(g19,g14)
    c: Equal(g14, g15-g19) x5
    c: PointOnObject(g14,g20)
    c: PointOnObject(g15,g20)
    c: PointOnObject(g16,g20)
    c: PointOnObject(g17,g20)
    c: PointOnObject(g18,g20)
    c: PointOnObject(g19,g20)
    c: Diameter(g20) = 7
    c: DistanceY(g-1,g20) = 7
    c: Vertical(g18)
    c: Distance(g17,g-2) = 1
    c: Coincident(g21,g22)
    c: Coincident(g22,g23)
    c: Coincident(g23,g24)
    c: Coincident(g24,g25)
    c: Coincident(g25,g26)
    c: Coincident(g26,g21)
    c: Equal(g21, g22-g26) x5
    c: PointOnObject(g21,g27)
    c: PointOnObject(g22,g27)
    c: PointOnObject(g23,g27)
    c: PointOnObject(g24,g27)
    c: PointOnObject(g25,g27)
    c: PointOnObject(g26,g27)
    c: Diameter(g27) = 7
    c: DistanceY(g-1,g27) = 7
    c: DistanceX(g21,g-1) = 1
    c: Vertical(g21)
    c: Coincident(g28,g29)
    c: Coincident(g29,g30)
    c: Coincident(g30,g31)
    c: Coincident(g31,g32)
    c: Coincident(g32,g33)
    c: Coincident(g33,g28)
    c: Equal(g28, g29-g33) x5
    c: PointOnObject(g28,g34)
    c: PointOnObject(g29,g34)
    c: PointOnObject(g30,g34)
    c: PointOnObject(g31,g34)
    c: PointOnObject(g32,g34)
    c: PointOnObject(g33,g34)
    c: PointOnObject(g34,g-1)
    c: Diameter(g34) = 7
    c: Vertical(g31)
    c: DistanceX(g34,g-1) = 8
    c: Coincident(g35,g36)
    c: Coincident(g36,g37)
    c: Coincident(g37,g38)
    c: Coincident(g38,g39)
    c: Coincident(g39,g40)
    c: Coincident(g40,g35)
    c: Equal(g35, g36-g40) x5
    c: PointOnObject(g35,g41)
    c: PointOnObject(g36,g41)
    c: PointOnObject(g37,g41)
    c: PointOnObject(g38,g41)
    c: PointOnObject(g39,g41)
    c: PointOnObject(g40,g41)
    c: Coincident(g42,g43)
    c: Coincident(g43,g44)
    c: Coincident(g44,g45)
    c: Coincident(g45,g46)
    c: Coincident(g46,g47)
    c: Coincident(g47,g42)
    c: Equal(g42, g43-g47) x5
    c: PointOnObject(g42,g48)
    c: PointOnObject(g43,g48)
    c: PointOnObject(g44,g48)
    c: PointOnObject(g45,g48)
    c: PointOnObject(g46,g48)
    c: PointOnObject(g47,g48)
    c: Equal(g41,g48)
    c: Diameter(g41) = 7
    c: Vertical(g39)
    c: Vertical(g43)
    c: Distance(g-2,g39) = 1
    c: Symmetric(g38,g43,g-2)
    c: Distance(g41,g-1) = 7
FEATURE [Part::Extrusion] Extrude465  label="hex080"
  Base = -> Sketch473
  Dir = (0,-1,2e-16)
  DirMode = 2
  FaceMakerClass = Part::FaceMakerBullseye
  FaceMakerMode = 3
  LengthFwd = 10
  LengthRev = 0
  Placement = pos=(-48,0,-28) rot=(0,0,1;0rad)
  Solid = true
  Symmetric = false
FEATURE [Sketcher::SketchObject] Sketch474
  ArcFitTolerance = 1e-06
  FullyConstrained = true
  MakeInternals = false
  Placement = pos=(0,0,0) rot=(1,0,0;1.5708rad)
  sketch-geometry (49):
    g0: LineSegment StartX=1e-16 StartY=3.5 StartZ=0 EndX=-3.03109 EndY=1.75 EndZ=0
    g1: LineSegment StartX=-3.03109 StartY=1.75 StartZ=0 EndX=-3.03109 EndY=-1.75 EndZ=0
    g2: LineSegment StartX=-3.03109 StartY=-1.75 StartZ=0 EndX=-1e-16 EndY=-3.5 EndZ=0
    g3: LineSegment StartX=-1e-16 StartY=-3.5 StartZ=0 EndX=3.03109 EndY=-1.75 EndZ=0
    g4: LineSegment StartX=3.03109 StartY=-1.75 StartZ=0 EndX=3.03109 EndY=1.75 EndZ=0
    g5: LineSegment StartX=3.03109 StartY=1.75 StartZ=0 EndX=1e-16 EndY=3.5 EndZ=0
    g6: Circle [constr] CenterX=0 CenterY=0 CenterZ=0 NormalX=0 NormalY=0 NormalZ=1 AngleXU=0 Radius=3.5
    g7: LineSegment StartX=4.96892 StartY=-1.75002 StartZ=0 EndX=8.00002 EndY=-3.5 EndZ=0
    g8: LineSegment StartX=8.00002 StartY=-3.5 StartZ=0 EndX=11.0311 EndY=-1.74998 EndZ=0
    g9: LineSegment StartX=11.0311 StartY=-1.74998 StartZ=0 EndX=11.0311 EndY=1.75002 EndZ=0
    g10: LineSegment StartX=11.0311 StartY=1.75002 StartZ=0 EndX=7.99998 EndY=3.5 EndZ=0
    g11: LineSegment StartX=7.99998 StartY=3.5 StartZ=0 EndX=4.9689 EndY=1.74998 EndZ=0
    g12: LineSegment StartX=4.9689 StartY=1.74998 StartZ=0 EndX=4.96892 EndY=-1.75002 EndZ=0
    g13: Circle [constr] CenterX=8 CenterY=0 CenterZ=0 NormalX=0 NormalY=0 NormalZ=1 AngleXU=0 Radius=3.5
    g14: LineSegment StartX=4.03109 StartY=3.5 StartZ=0 EndX=7.06218 EndY=5.25 EndZ=0
    g15: LineSegment StartX=7.06218 StartY=5.25 StartZ=0 EndX=7.06218 EndY=8.75 EndZ=0
    g16: LineSegment StartX=7.06218 StartY=8.75 StartZ=0 EndX=4.03109 EndY=10.5 EndZ=0
    g17: LineSegment StartX=4.03109 StartY=10.5 StartZ=0 EndX=1 EndY=8.75 EndZ=0
    g18: LineSegment StartX=1 StartY=8.75 StartZ=0 EndX=1 EndY=5.25 EndZ=0
    g19: LineSegment StartX=1 StartY=5.25 StartZ=0 EndX=4.03109 EndY=3.5 EndZ=0
    g20: Circle [constr] CenterX=4.03109 CenterY=7 CenterZ=0 NormalX=0 NormalY=0 NormalZ=1 AngleXU=0 Radius=3.5
    g21: LineSegment StartX=-1 StartY=5.25 StartZ=0 EndX=-1 EndY=8.75 EndZ=0
    g22: LineSegment StartX=-1 StartY=8.75 StartZ=0 EndX=-4.03109 EndY=10.5 EndZ=0
    g23: LineSegment StartX=-4.03109 StartY=10.5 StartZ=0 EndX=-7.06218 EndY=8.75 EndZ=0
    g24: LineSegment StartX=-7.06218 StartY=8.75 StartZ=0 EndX=-7.06218 EndY=5.25 EndZ=0
    g25: LineSegment StartX=-7.06218 StartY=5.25 StartZ=0 EndX=-4.03109 EndY=3.5 EndZ=0
    g26: LineSegment StartX=-4.03109 StartY=3.5 StartZ=0 EndX=-1 EndY=5.25 EndZ=0
    g27: Circle [constr] CenterX=-4.03109 CenterY=7 CenterZ=0 NormalX=0 NormalY=0 NormalZ=1 AngleXU=0 Radius=3.5
    g28: LineSegment StartX=-4.96891 StartY=-1.75 StartZ=0 EndX=-4.96891 EndY=1.75 EndZ=0
    g29: LineSegment StartX=-4.96891 StartY=1.75 StartZ=0 EndX=-8 EndY=3.5 EndZ=0
    g30: LineSegment StartX=-8 StartY=3.5 StartZ=0 EndX=-11.0311 EndY=1.75 EndZ=0
    g31: LineSegment StartX=-11.0311 StartY=1.75 StartZ=0 EndX=-11.0311 EndY=-1.75 EndZ=0
    g32: LineSegment StartX=-11.0311 StartY=-1.75 StartZ=0 EndX=-8 EndY=-3.5 EndZ=0
    g33: LineSegment StartX=-8 StartY=-3.5 StartZ=0 EndX=-4.96891 EndY=-1.75 EndZ=0
    g34: Circle [constr] CenterX=-8 CenterY=0 CenterZ=0 NormalX=0 NormalY=0 NormalZ=1 AngleXU=0 Radius=3.5
    g35: LineSegment StartX=-4.03109 StartY=-3.5 StartZ=0 EndX=-7.06218 EndY=-5.25 EndZ=0
    g36: LineSegment StartX=-7.06218 StartY=-5.25 StartZ=0 EndX=-7.06218 EndY=-8.75 EndZ=0
    g37: LineSegment StartX=-7.06218 StartY=-8.75 StartZ=0 EndX=-4.03109 EndY=-10.5 EndZ=0
    g38: LineSegment StartX=-4.03109 StartY=-10.5 StartZ=0 EndX=-1 EndY=-8.75 EndZ=0
    g39: LineSegment StartX=-1 StartY=-8.75 StartZ=0 EndX=-1 EndY=-5.25 EndZ=0
    g40: LineSegment StartX=-1 StartY=-5.25 StartZ=0 EndX=-4.03109 EndY=-3.5 EndZ=0
    g41: Circle [constr] CenterX=-4.03109 CenterY=-7 CenterZ=0 NormalX=0 NormalY=0 NormalZ=1 AngleXU=0 Radius=3.5
    g42: LineSegment StartX=4.03109 StartY=-3.5 StartZ=0 EndX=1 EndY=-5.25 EndZ=0
    g43: LineSegment StartX=1 StartY=-5.25 StartZ=0 EndX=1 EndY=-8.75 EndZ=0
    g44: LineSegment StartX=1 StartY=-8.75 StartZ=0 EndX=4.03109 EndY=-10.5 EndZ=0
    g45: LineSegment StartX=4.03109 StartY=-10.5 StartZ=0 EndX=7.06218 EndY=-8.75 EndZ=0
    g46: LineSegment StartX=7.06218 StartY=-8.75 StartZ=0 EndX=7.06218 EndY=-5.25 EndZ=0
    g47: LineSegment StartX=7.06218 StartY=-5.25 StartZ=0 EndX=4.03109 EndY=-3.5 EndZ=0
    g48: Circle [constr] CenterX=4.03109 CenterY=-7 CenterZ=0 NormalX=0 NormalY=0 NormalZ=1 AngleXU=0 Radius=3.5
  constraints (117):
    c: Coincident(g0,g1)
    c: Coincident(g1,g2)
    c: Coincident(g2,g3)
    c: Coincident(g3,g4)
    c: Coincident(g4,g5)
    c: Coincident(g5,g0)
    c: Equal(g0, g1-g5) x5
    c: PointOnObject(g0,g6)
    c: PointOnObject(g1,g6)
    c: PointOnObject(g2,g6)
    c: PointOnObject(g3,g6)
    c: PointOnObject(g4,g6)
    c: PointOnObject(g5,g6)
    c: Coincident(g6,g-1)
    c: Diameter(g6) = 7
    c: PointOnObject(g0,g-2)
    c: Coincident(g7,g8)
    c: Coincident(g8,g9)
    c: Coincident(g9,g10)
    c: Coincident(g10,g11)
    c: Coincident(g11,g12)
    c: Coincident(g12,g7)
    c: Equal(g7, g8-g12) x5
    c: PointOnObject(g7,g13)
    c: PointOnObject(g8,g13)
    c: PointOnObject(g9,g13)
    c: PointOnObject(g10,g13)
    c: PointOnObject(g11,g13)
    c: PointOnObject(g12,g13)
    c: PointOnObject(g13,g-1)
    c: Diameter(g13) = 7
    c: Distance(g6,g13) = 8
    c: Horizontal(g0,g10)
    c: Coincident(g14,g15)
    c: Coincident(g15,g16)
    c: Coincident(g16,g17)
    c: Coincident(g17,g18)
    c: Coincident(g18,g19)
    c: Coincident(g19,g14)
    c: Equal(g14, g15-g19) x5
    c: PointOnObject(g14,g20)
    c: PointOnObject(g15,g20)
    c: PointOnObject(g16,g20)
    c: PointOnObject(g17,g20)
    c: PointOnObject(g18,g20)
    c: PointOnObject(g19,g20)
    c: Diameter(g20) = 7
    c: DistanceY(g-1,g20) = 7
    c: Vertical(g18)
    c: Distance(g17,g-2) = 1
    c: Coincident(g21,g22)
    c: Coincident(g22,g23)
    c: Coincident(g23,g24)
    c: Coincident(g24,g25)
    c: Coincident(g25,g26)
    c: Coincident(g26,g21)
    c: Equal(g21, g22-g26) x5
    c: PointOnObject(g21,g27)
    c: PointOnObject(g22,g27)
    c: PointOnObject(g23,g27)
    c: PointOnObject(g24,g27)
    c: PointOnObject(g25,g27)
    c: PointOnObject(g26,g27)
    c: Diameter(g27) = 7
    c: DistanceY(g-1,g27) = 7
    c: DistanceX(g21,g-1) = 1
    c: Vertical(g21)
    c: Coincident(g28,g29)
    c: Coincident(g29,g30)
    c: Coincident(g30,g31)
    c: Coincident(g31,g32)
    c: Coincident(g32,g33)
    c: Coincident(g33,g28)
    c: Equal(g28, g29-g33) x5
    c: PointOnObject(g28,g34)
    c: PointOnObject(g29,g34)
    c: PointOnObject(g30,g34)
    c: PointOnObject(g31,g34)
    c: PointOnObject(g32,g34)
    c: PointOnObject(g33,g34)
    c: PointOnObject(g34,g-1)
    c: Diameter(g34) = 7
    c: Vertical(g31)
    c: DistanceX(g34,g-1) = 8
    c: Coincident(g35,g36)
    c: Coincident(g36,g37)
    c: Coincident(g37,g38)
    c: Coincident(g38,g39)
    c: Coincident(g39,g40)
    c: Coincident(g40,g35)
    c: Equal(g35, g36-g40) x5
    c: PointOnObject(g35,g41)
    c: PointOnObject(g36,g41)
    c: PointOnObject(g37,g41)
    c: PointOnObject(g38,g41)
    c: PointOnObject(g39,g41)
    c: PointOnObject(g40,g41)
    c: Coincident(g42,g43)
    c: Coincident(g43,g44)
    c: Coincident(g44,g45)
    c: Coincident(g45,g46)
    c: Coincident(g46,g47)
    c: Coincident(g47,g42)
    c: Equal(g42, g43-g47) x5
    c: PointOnObject(g42,g48)
    c: PointOnObject(g43,g48)
    c: PointOnObject(g44,g48)
    c: PointOnObject(g45,g48)
    c: PointOnObject(g46,g48)
    c: PointOnObject(g47,g48)
    c: Equal(g41,g48)
    c: Diameter(g41) = 7
    c: Vertical(g39)
    c: Vertical(g43)
    c: Distance(g-2,g39) = 1
    c: Symmetric(g38,g43,g-2)
    c: Distance(g41,g-1) = 7
FEATURE [Part::Extrusion] Extrude466  label="hex081"
  Base = -> Sketch474
  Dir = (0,-1,2e-16)
  DirMode = 2
  FaceMakerClass = Part::FaceMakerBullseye
  FaceMakerMode = 3
  LengthFwd = 10
  LengthRev = 0
  Placement = pos=(-32,0,-42) rot=(0,0,1;0rad)
  Solid = true
  Symmetric = false
FEATURE [Sketcher::SketchObject] Sketch475
  ArcFitTolerance = 1e-06
  FullyConstrained = true
  MakeInternals = false
  Placement = pos=(0,0,0) rot=(1,0,0;1.5708rad)
  sketch-geometry (49):
    g0: LineSegment StartX=1e-16 StartY=3.5 StartZ=0 EndX=-3.03109 EndY=1.75 EndZ=0
    g1: LineSegment StartX=-3.03109 StartY=1.75 StartZ=0 EndX=-3.03109 EndY=-1.75 EndZ=0
    g2: LineSegment StartX=-3.03109 StartY=-1.75 StartZ=0 EndX=-1e-16 EndY=-3.5 EndZ=0
    g3: LineSegment StartX=-1e-16 StartY=-3.5 StartZ=0 EndX=3.03109 EndY=-1.75 EndZ=0
    g4: LineSegment StartX=3.03109 StartY=-1.75 StartZ=0 EndX=3.03109 EndY=1.75 EndZ=0
    g5: LineSegment StartX=3.03109 StartY=1.75 StartZ=0 EndX=1e-16 EndY=3.5 EndZ=0
    g6: Circle [constr] CenterX=0 CenterY=0 CenterZ=0 NormalX=0 NormalY=0 NormalZ=1 AngleXU=0 Radius=3.5
    g7: LineSegment StartX=4.96892 StartY=-1.75002 StartZ=0 EndX=8.00002 EndY=-3.5 EndZ=0
    g8: LineSegment StartX=8.00002 StartY=-3.5 StartZ=0 EndX=11.0311 EndY=-1.74998 EndZ=0
    g9: LineSegment StartX=11.0311 StartY=-1.74998 StartZ=0 EndX=11.0311 EndY=1.75002 EndZ=0
    g10: LineSegment StartX=11.0311 StartY=1.75002 StartZ=0 EndX=7.99998 EndY=3.5 EndZ=0
    g11: LineSegment StartX=7.99998 StartY=3.5 StartZ=0 EndX=4.9689 EndY=1.74998 EndZ=0
    g12: LineSegment StartX=4.9689 StartY=1.74998 StartZ=0 EndX=4.96892 EndY=-1.75002 EndZ=0
    g13: Circle [constr] CenterX=8 CenterY=0 CenterZ=0 NormalX=0 NormalY=0 NormalZ=1 AngleXU=0 Radius=3.5
    g14: LineSegment StartX=4.03109 StartY=3.5 StartZ=0 EndX=7.06218 EndY=5.25 EndZ=0
    g15: LineSegment StartX=7.06218 StartY=5.25 StartZ=0 EndX=7.06218 EndY=8.75 EndZ=0
    g16: LineSegment StartX=7.06218 StartY=8.75 StartZ=0 EndX=4.03109 EndY=10.5 EndZ=0
    g17: LineSegment StartX=4.03109 StartY=10.5 StartZ=0 EndX=1 EndY=8.75 EndZ=0
    g18: LineSegment StartX=1 StartY=8.75 StartZ=0 EndX=1 EndY=5.25 EndZ=0
    g19: LineSegment StartX=1 StartY=5.25 StartZ=0 EndX=4.03109 EndY=3.5 EndZ=0
    g20: Circle [constr] CenterX=4.03109 CenterY=7 CenterZ=0 NormalX=0 NormalY=0 NormalZ=1 AngleXU=0 Radius=3.5
    g21: LineSegment StartX=-1 StartY=5.25 StartZ=0 EndX=-1 EndY=8.75 EndZ=0
    g22: LineSegment StartX=-1 StartY=8.75 StartZ=0 EndX=-4.03109 EndY=10.5 EndZ=0
    g23: LineSegment StartX=-4.03109 StartY=10.5 StartZ=0 EndX=-7.06218 EndY=8.75 EndZ=0
    g24: LineSegment StartX=-7.06218 StartY=8.75 StartZ=0 EndX=-7.06218 EndY=5.25 EndZ=0
    g25: LineSegment StartX=-7.06218 StartY=5.25 StartZ=0 EndX=-4.03109 EndY=3.5 EndZ=0
    g26: LineSegment StartX=-4.03109 StartY=3.5 StartZ=0 EndX=-1 EndY=5.25 EndZ=0
    g27: Circle [constr] CenterX=-4.03109 CenterY=7 CenterZ=0 NormalX=0 NormalY=0 NormalZ=1 AngleXU=0 Radius=3.5
    g28: LineSegment StartX=-4.96891 StartY=-1.75 StartZ=0 EndX=-4.96891 EndY=1.75 EndZ=0
    g29: LineSegment StartX=-4.96891 StartY=1.75 StartZ=0 EndX=-8 EndY=3.5 EndZ=0
    g30: LineSegment StartX=-8 StartY=3.5 StartZ=0 EndX=-11.0311 EndY=1.75 EndZ=0
    g31: LineSegment StartX=-11.0311 StartY=1.75 StartZ=0 EndX=-11.0311 EndY=-1.75 EndZ=0
    g32: LineSegment StartX=-11.0311 StartY=-1.75 StartZ=0 EndX=-8 EndY=-3.5 EndZ=0
    g33: LineSegment StartX=-8 StartY=-3.5 StartZ=0 EndX=-4.96891 EndY=-1.75 EndZ=0
    g34: Circle [constr] CenterX=-8 CenterY=0 CenterZ=0 NormalX=0 NormalY=0 NormalZ=1 AngleXU=0 Radius=3.5
    g35: LineSegment StartX=-4.03109 StartY=-3.5 StartZ=0 EndX=-7.06218 EndY=-5.25 EndZ=0
    g36: LineSegment StartX=-7.06218 StartY=-5.25 StartZ=0 EndX=-7.06218 EndY=-8.75 EndZ=0
    g37: LineSegment StartX=-7.06218 StartY=-8.75 StartZ=0 EndX=-4.03109 EndY=-10.5 EndZ=0
    g38: LineSegment StartX=-4.03109 StartY=-10.5 StartZ=0 EndX=-1 EndY=-8.75 EndZ=0
    g39: LineSegment StartX=-1 StartY=-8.75 StartZ=0 EndX=-1 EndY=-5.25 EndZ=0
    g40: LineSegment StartX=-1 StartY=-5.25 StartZ=0 EndX=-4.03109 EndY=-3.5 EndZ=0
    g41: Circle [constr] CenterX=-4.03109 CenterY=-7 CenterZ=0 NormalX=0 NormalY=0 NormalZ=1 AngleXU=0 Radius=3.5
    g42: LineSegment StartX=4.03109 StartY=-3.5 StartZ=0 EndX=1 EndY=-5.25 EndZ=0
    g43: LineSegment StartX=1 StartY=-5.25 StartZ=0 EndX=1 EndY=-8.75 EndZ=0
    g44: LineSegment StartX=1 StartY=-8.75 StartZ=0 EndX=4.03109 EndY=-10.5 EndZ=0
    g45: LineSegment StartX=4.03109 StartY=-10.5 StartZ=0 EndX=7.06218 EndY=-8.75 EndZ=0
    g46: LineSegment StartX=7.06218 StartY=-8.75 StartZ=0 EndX=7.06218 EndY=-5.25 EndZ=0
    g47: LineSegment StartX=7.06218 StartY=-5.25 StartZ=0 EndX=4.03109 EndY=-3.5 EndZ=0
    g48: Circle [constr] CenterX=4.03109 CenterY=-7 CenterZ=0 NormalX=0 NormalY=0 NormalZ=1 AngleXU=0 Radius=3.5
  constraints (117):
    c: Coincident(g0,g1)
    c: Coincident(g1,g2)
    c: Coincident(g2,g3)
    c: Coincident(g3,g4)
    c: Coincident(g4,g5)
    c: Coincident(g5,g0)
    c: Equal(g0, g1-g5) x5
    c: PointOnObject(g0,g6)
    c: PointOnObject(g1,g6)
    c: PointOnObject(g2,g6)
    c: PointOnObject(g3,g6)
    c: PointOnObject(g4,g6)
    c: PointOnObject(g5,g6)
    c: Coincident(g6,g-1)
    c: Diameter(g6) = 7
    c: PointOnObject(g0,g-2)
    c: Coincident(g7,g8)
    c: Coincident(g8,g9)
    c: Coincident(g9,g10)
    c: Coincident(g10,g11)
    c: Coincident(g11,g12)
    c: Coincident(g12,g7)
    c: Equal(g7, g8-g12) x5
    c: PointOnObject(g7,g13)
    c: PointOnObject(g8,g13)
    c: PointOnObject(g9,g13)
    c: PointOnObject(g10,g13)
    c: PointOnObject(g11,g13)
    c: PointOnObject(g12,g13)
    c: PointOnObject(g13,g-1)
    c: Diameter(g13) = 7
    c: Distance(g6,g13) = 8
    c: Horizontal(g0,g10)
    c: Coincident(g14,g15)
    c: Coincident(g15,g16)
    c: Coincident(g16,g17)
    c: Coincident(g17,g18)
    c: Coincident(g18,g19)
    c: Coincident(g19,g14)
    c: Equal(g14, g15-g19) x5
    c: PointOnObject(g14,g20)
    c: PointOnObject(g15,g20)
    c: PointOnObject(g16,g20)
    c: PointOnObject(g17,g20)
    c: PointOnObject(g18,g20)
    c: PointOnObject(g19,g20)
    c: Diameter(g20) = 7
    c: DistanceY(g-1,g20) = 7
    c: Vertical(g18)
    c: Distance(g17,g-2) = 1
    c: Coincident(g21,g22)
    c: Coincident(g22,g23)
    c: Coincident(g23,g24)
    c: Coincident(g24,g25)
    c: Coincident(g25,g26)
    c: Coincident(g26,g21)
    c: Equal(g21, g22-g26) x5
    c: PointOnObject(g21,g27)
    c: PointOnObject(g22,g27)
    c: PointOnObject(g23,g27)
    c: PointOnObject(g24,g27)
    c: PointOnObject(g25,g27)
    c: PointOnObject(g26,g27)
    c: Diameter(g27) = 7
    c: DistanceY(g-1,g27) = 7
    c: DistanceX(g21,g-1) = 1
    c: Vertical(g21)
    c: Coincident(g28,g29)
    c: Coincident(g29,g30)
    c: Coincident(g30,g31)
    c: Coincident(g31,g32)
    c: Coincident(g32,g33)
    c: Coincident(g33,g28)
    c: Equal(g28, g29-g33) x5
    c: PointOnObject(g28,g34)
    c: PointOnObject(g29,g34)
    c: PointOnObject(g30,g34)
    c: PointOnObject(g31,g34)
    c: PointOnObject(g32,g34)
    c: PointOnObject(g33,g34)
    c: PointOnObject(g34,g-1)
    c: Diameter(g34) = 7
    c: Vertical(g31)
    c: DistanceX(g34,g-1) = 8
    c: Coincident(g35,g36)
    c: Coincident(g36,g37)
    c: Coincident(g37,g38)
    c: Coincident(g38,g39)
    c: Coincident(g39,g40)
    c: Coincident(g40,g35)
    c: Equal(g35, g36-g40) x5
    c: PointOnObject(g35,g41)
    c: PointOnObject(g36,g41)
    c: PointOnObject(g37,g41)
    c: PointOnObject(g38,g41)
    c: PointOnObject(g39,g41)
    c: PointOnObject(g40,g41)
    c: Coincident(g42,g43)
    c: Coincident(g43,g44)
    c: Coincident(g44,g45)
    c: Coincident(g45,g46)
    c: Coincident(g46,g47)
    c: Coincident(g47,g42)
    c: Equal(g42, g43-g47) x5
    c: PointOnObject(g42,g48)
    c: PointOnObject(g43,g48)
    c: PointOnObject(g44,g48)
    c: PointOnObject(g45,g48)
    c: PointOnObject(g46,g48)
    c: PointOnObject(g47,g48)
    c: Equal(g41,g48)
    c: Diameter(g41) = 7
    c: Vertical(g39)
    c: Vertical(g43)
    c: Distance(g-2,g39) = 1
    c: Symmetric(g38,g43,g-2)
    c: Distance(g41,g-1) = 7
FEATURE [Part::Extrusion] Extrude467  label="hex082"
  Base = -> Sketch475
  Dir = (0,-1,2e-16)
  DirMode = 2
  FaceMakerClass = Part::FaceMakerBullseye
  FaceMakerMode = 3
  LengthFwd = 10
  LengthRev = 0
  Placement = pos=(-56,0,-42) rot=(0,0,1;0rad)
  Solid = true
  Symmetric = false
FEATURE [Sketcher::SketchObject] Sketch476
  ArcFitTolerance = 1e-06
  FullyConstrained = true
  MakeInternals = false
  Placement = pos=(0,0,0) rot=(1,0,0;1.5708rad)
  sketch-geometry (49):
    g0: LineSegment StartX=1e-16 StartY=3.5 StartZ=0 EndX=-3.03109 EndY=1.75 EndZ=0
    g1: LineSegment StartX=-3.03109 StartY=1.75 StartZ=0 EndX=-3.03109 EndY=-1.75 EndZ=0
    g2: LineSegment StartX=-3.03109 StartY=-1.75 StartZ=0 EndX=-1e-16 EndY=-3.5 EndZ=0
    g3: LineSegment StartX=-1e-16 StartY=-3.5 StartZ=0 EndX=3.03109 EndY=-1.75 EndZ=0
    g4: LineSegment StartX=3.03109 StartY=-1.75 StartZ=0 EndX=3.03109 EndY=1.75 EndZ=0
    g5: LineSegment StartX=3.03109 StartY=1.75 StartZ=0 EndX=1e-16 EndY=3.5 EndZ=0
    g6: Circle [constr] CenterX=0 CenterY=0 CenterZ=0 NormalX=0 NormalY=0 NormalZ=1 AngleXU=0 Radius=3.5
    g7: LineSegment StartX=4.96892 StartY=-1.75002 StartZ=0 EndX=8.00002 EndY=-3.5 EndZ=0
    g8: LineSegment StartX=8.00002 StartY=-3.5 StartZ=0 EndX=11.0311 EndY=-1.74998 EndZ=0
    g9: LineSegment StartX=11.0311 StartY=-1.74998 StartZ=0 EndX=11.0311 EndY=1.75002 EndZ=0
    g10: LineSegment StartX=11.0311 StartY=1.75002 StartZ=0 EndX=7.99998 EndY=3.5 EndZ=0
    g11: LineSegment StartX=7.99998 StartY=3.5 StartZ=0 EndX=4.9689 EndY=1.74998 EndZ=0
    g12: LineSegment StartX=4.9689 StartY=1.74998 StartZ=0 EndX=4.96892 EndY=-1.75002 EndZ=0
    g13: Circle [constr] CenterX=8 CenterY=0 CenterZ=0 NormalX=0 NormalY=0 NormalZ=1 AngleXU=0 Radius=3.5
    g14: LineSegment StartX=4.03109 StartY=3.5 StartZ=0 EndX=7.06218 EndY=5.25 EndZ=0
    g15: LineSegment StartX=7.06218 StartY=5.25 StartZ=0 EndX=7.06218 EndY=8.75 EndZ=0
    g16: LineSegment StartX=7.06218 StartY=8.75 StartZ=0 EndX=4.03109 EndY=10.5 EndZ=0
    g17: LineSegment StartX=4.03109 StartY=10.5 StartZ=0 EndX=1 EndY=8.75 EndZ=0
    g18: LineSegment StartX=1 StartY=8.75 StartZ=0 EndX=1 EndY=5.25 EndZ=0
    g19: LineSegment StartX=1 StartY=5.25 StartZ=0 EndX=4.03109 EndY=3.5 EndZ=0
    g20: Circle [constr] CenterX=4.03109 CenterY=7 CenterZ=0 NormalX=0 NormalY=0 NormalZ=1 AngleXU=0 Radius=3.5
    g21: LineSegment StartX=-1 StartY=5.25 StartZ=0 EndX=-1 EndY=8.75 EndZ=0
    g22: LineSegment StartX=-1 StartY=8.75 StartZ=0 EndX=-4.03109 EndY=10.5 EndZ=0
    g23: LineSegment StartX=-4.03109 StartY=10.5 StartZ=0 EndX=-7.06218 EndY=8.75 EndZ=0
    g24: LineSegment StartX=-7.06218 StartY=8.75 StartZ=0 EndX=-7.06218 EndY=5.25 EndZ=0
    g25: LineSegment StartX=-7.06218 StartY=5.25 StartZ=0 EndX=-4.03109 EndY=3.5 EndZ=0
    g26: LineSegment StartX=-4.03109 StartY=3.5 StartZ=0 EndX=-1 EndY=5.25 EndZ=0
    g27: Circle [constr] CenterX=-4.03109 CenterY=7 CenterZ=0 NormalX=0 NormalY=0 NormalZ=1 AngleXU=0 Radius=3.5
    g28: LineSegment StartX=-4.96891 StartY=-1.75 StartZ=0 EndX=-4.96891 EndY=1.75 EndZ=0
    g29: LineSegment StartX=-4.96891 StartY=1.75 StartZ=0 EndX=-8 EndY=3.5 EndZ=0
    g30: LineSegment StartX=-8 StartY=3.5 StartZ=0 EndX=-11.0311 EndY=1.75 EndZ=0
    g31: LineSegment StartX=-11.0311 StartY=1.75 StartZ=0 EndX=-11.0311 EndY=-1.75 EndZ=0
    g32: LineSegment StartX=-11.0311 StartY=-1.75 StartZ=0 EndX=-8 EndY=-3.5 EndZ=0
    g33: LineSegment StartX=-8 StartY=-3.5 StartZ=0 EndX=-4.96891 EndY=-1.75 EndZ=0
    g34: Circle [constr] CenterX=-8 CenterY=0 CenterZ=0 NormalX=0 NormalY=0 NormalZ=1 AngleXU=0 Radius=3.5
    g35: LineSegment StartX=-4.03109 StartY=-3.5 StartZ=0 EndX=-7.06218 EndY=-5.25 EndZ=0
    g36: LineSegment StartX=-7.06218 StartY=-5.25 StartZ=0 EndX=-7.06218 EndY=-8.75 EndZ=0
    g37: LineSegment StartX=-7.06218 StartY=-8.75 StartZ=0 EndX=-4.03109 EndY=-10.5 EndZ=0
    g38: LineSegment StartX=-4.03109 StartY=-10.5 StartZ=0 EndX=-1 EndY=-8.75 EndZ=0
    g39: LineSegment StartX=-1 StartY=-8.75 StartZ=0 EndX=-1 EndY=-5.25 EndZ=0
    g40: LineSegment StartX=-1 StartY=-5.25 StartZ=0 EndX=-4.03109 EndY=-3.5 EndZ=0
    g41: Circle [constr] CenterX=-4.03109 CenterY=-7 CenterZ=0 NormalX=0 NormalY=0 NormalZ=1 AngleXU=0 Radius=3.5
    g42: LineSegment StartX=4.03109 StartY=-3.5 StartZ=0 EndX=1 EndY=-5.25 EndZ=0
    g43: LineSegment StartX=1 StartY=-5.25 StartZ=0 EndX=1 EndY=-8.75 EndZ=0
    g44: LineSegment StartX=1 StartY=-8.75 StartZ=0 EndX=4.03109 EndY=-10.5 EndZ=0
    g45: LineSegment StartX=4.03109 StartY=-10.5 StartZ=0 EndX=7.06218 EndY=-8.75 EndZ=0
    g46: LineSegment StartX=7.06218 StartY=-8.75 StartZ=0 EndX=7.06218 EndY=-5.25 EndZ=0
    g47: LineSegment StartX=7.06218 StartY=-5.25 StartZ=0 EndX=4.03109 EndY=-3.5 EndZ=0
    g48: Circle [constr] CenterX=4.03109 CenterY=-7 CenterZ=0 NormalX=0 NormalY=0 NormalZ=1 AngleXU=0 Radius=3.5
  constraints (117):
    c: Coincident(g0,g1)
    c: Coincident(g1,g2)
    c: Coincident(g2,g3)
    c: Coincident(g3,g4)
    c: Coincident(g4,g5)
    c: Coincident(g5,g0)
    c: Equal(g0, g1-g5) x5
    c: PointOnObject(g0,g6)
    c: PointOnObject(g1,g6)
    c: PointOnObject(g2,g6)
    c: PointOnObject(g3,g6)
    c: PointOnObject(g4,g6)
    c: PointOnObject(g5,g6)
    c: Coincident(g6,g-1)
    c: Diameter(g6) = 7
    c: PointOnObject(g0,g-2)
    c: Coincident(g7,g8)
    c: Coincident(g8,g9)
    c: Coincident(g9,g10)
    c: Coincident(g10,g11)
    c: Coincident(g11,g12)
    c: Coincident(g12,g7)
    c: Equal(g7, g8-g12) x5
    c: PointOnObject(g7,g13)
    c: PointOnObject(g8,g13)
    c: PointOnObject(g9,g13)
    c: PointOnObject(g10,g13)
    c: PointOnObject(g11,g13)
    c: PointOnObject(g12,g13)
    c: PointOnObject(g13,g-1)
    c: Diameter(g13) = 7
    c: Distance(g6,g13) = 8
    c: Horizontal(g0,g10)
    c: Coincident(g14,g15)
    c: Coincident(g15,g16)
    c: Coincident(g16,g17)
    c: Coincident(g17,g18)
    c: Coincident(g18,g19)
    c: Coincident(g19,g14)
    c: Equal(g14, g15-g19) x5
    c: PointOnObject(g14,g20)
    c: PointOnObject(g15,g20)
    c: PointOnObject(g16,g20)
    c: PointOnObject(g17,g20)
    c: PointOnObject(g18,g20)
    c: PointOnObject(g19,g20)
    c: Diameter(g20) = 7
    c: DistanceY(g-1,g20) = 7
    c: Vertical(g18)
    c: Distance(g17,g-2) = 1
    c: Coincident(g21,g22)
    c: Coincident(g22,g23)
    c: Coincident(g23,g24)
    c: Coincident(g24,g25)
    c: Coincident(g25,g26)
    c: Coincident(g26,g21)
    c: Equal(g21, g22-g26) x5
    c: PointOnObject(g21,g27)
    c: PointOnObject(g22,g27)
    c: PointOnObject(g23,g27)
    c: PointOnObject(g24,g27)
    c: PointOnObject(g25,g27)
    c: PointOnObject(g26,g27)
    c: Diameter(g27) = 7
    c: DistanceY(g-1,g27) = 7
    c: DistanceX(g21,g-1) = 1
    c: Vertical(g21)
    c: Coincident(g28,g29)
    c: Coincident(g29,g30)
    c: Coincident(g30,g31)
    c: Coincident(g31,g32)
    c: Coincident(g32,g33)
    c: Coincident(g33,g28)
    c: Equal(g28, g29-g33) x5
    c: PointOnObject(g28,g34)
    c: PointOnObject(g29,g34)
    c: PointOnObject(g30,g34)
    c: PointOnObject(g31,g34)
    c: PointOnObject(g32,g34)
    c: PointOnObject(g33,g34)
    c: PointOnObject(g34,g-1)
    c: Diameter(g34) = 7
    c: Vertical(g31)
    c: DistanceX(g34,g-1) = 8
    c: Coincident(g35,g36)
    c: Coincident(g36,g37)
    c: Coincident(g37,g38)
    c: Coincident(g38,g39)
    c: Coincident(g39,g40)
    c: Coincident(g40,g35)
    c: Equal(g35, g36-g40) x5
    c: PointOnObject(g35,g41)
    c: PointOnObject(g36,g41)
    c: PointOnObject(g37,g41)
    c: PointOnObject(g38,g41)
    c: PointOnObject(g39,g41)
    c: PointOnObject(g40,g41)
    c: Coincident(g42,g43)
    c: Coincident(g43,g44)
    c: Coincident(g44,g45)
    c: Coincident(g45,g46)
    c: Coincident(g46,g47)
    c: Coincident(g47,g42)
    c: Equal(g42, g43-g47) x5
    c: PointOnObject(g42,g48)
    c: PointOnObject(g43,g48)
    c: PointOnObject(g44,g48)
    c: PointOnObject(g45,g48)
    c: PointOnObject(g46,g48)
    c: PointOnObject(g47,g48)
    c: Equal(g41,g48)
    c: Diameter(g41) = 7
    c: Vertical(g39)
    c: Vertical(g43)
    c: Distance(g-2,g39) = 1
    c: Symmetric(g38,g43,g-2)
    c: Distance(g41,g-1) = 7
FEATURE [Part::Extrusion] Extrude468  label="hex083"
  Base = -> Sketch476
  Dir = (0,-1,2e-16)
  DirMode = 2
  FaceMakerClass = Part::FaceMakerBullseye
  FaceMakerMode = 3
  LengthFwd = 10
  LengthRev = 0
  Placement = pos=(-40,0,-56) rot=(0,0,1;0rad)
  Solid = true
  Symmetric = false
FEATURE [Sketcher::SketchObject] Sketch477
  ArcFitTolerance = 1e-06
  FullyConstrained = true
  MakeInternals = false
  Placement = pos=(0,0,0) rot=(1,0,0;1.5708rad)
  sketch-geometry (49):
    g0: LineSegment StartX=1e-16 StartY=3.5 StartZ=0 EndX=-3.03109 EndY=1.75 EndZ=0
    g1: LineSegment StartX=-3.03109 StartY=1.75 StartZ=0 EndX=-3.03109 EndY=-1.75 EndZ=0
    g2: LineSegment StartX=-3.03109 StartY=-1.75 StartZ=0 EndX=-1e-16 EndY=-3.5 EndZ=0
    g3: LineSegment StartX=-1e-16 StartY=-3.5 StartZ=0 EndX=3.03109 EndY=-1.75 EndZ=0
    g4: LineSegment StartX=3.03109 StartY=-1.75 StartZ=0 EndX=3.03109 EndY=1.75 EndZ=0
    g5: LineSegment StartX=3.03109 StartY=1.75 StartZ=0 EndX=1e-16 EndY=3.5 EndZ=0
    g6: Circle [constr] CenterX=0 CenterY=0 CenterZ=0 NormalX=0 NormalY=0 NormalZ=1 AngleXU=0 Radius=3.5
    g7: LineSegment StartX=4.96892 StartY=-1.75002 StartZ=0 EndX=8.00002 EndY=-3.5 EndZ=0
    g8: LineSegment StartX=8.00002 StartY=-3.5 StartZ=0 EndX=11.0311 EndY=-1.74998 EndZ=0
    g9: LineSegment StartX=11.0311 StartY=-1.74998 StartZ=0 EndX=11.0311 EndY=1.75002 EndZ=0
    g10: LineSegment StartX=11.0311 StartY=1.75002 StartZ=0 EndX=7.99998 EndY=3.5 EndZ=0
    g11: LineSegment StartX=7.99998 StartY=3.5 StartZ=0 EndX=4.9689 EndY=1.74998 EndZ=0
    g12: LineSegment StartX=4.9689 StartY=1.74998 StartZ=0 EndX=4.96892 EndY=-1.75002 EndZ=0
    g13: Circle [constr] CenterX=8 CenterY=0 CenterZ=0 NormalX=0 NormalY=0 NormalZ=1 AngleXU=0 Radius=3.5
    g14: LineSegment StartX=4.03109 StartY=3.5 StartZ=0 EndX=7.06218 EndY=5.25 EndZ=0
    g15: LineSegment StartX=7.06218 StartY=5.25 StartZ=0 EndX=7.06218 EndY=8.75 EndZ=0
    g16: LineSegment StartX=7.06218 StartY=8.75 StartZ=0 EndX=4.03109 EndY=10.5 EndZ=0
    g17: LineSegment StartX=4.03109 StartY=10.5 StartZ=0 EndX=1 EndY=8.75 EndZ=0
    g18: LineSegment StartX=1 StartY=8.75 StartZ=0 EndX=1 EndY=5.25 EndZ=0
    g19: LineSegment StartX=1 StartY=5.25 StartZ=0 EndX=4.03109 EndY=3.5 EndZ=0
    g20: Circle [constr] CenterX=4.03109 CenterY=7 CenterZ=0 NormalX=0 NormalY=0 NormalZ=1 AngleXU=0 Radius=3.5
    g21: LineSegment StartX=-1 StartY=5.25 StartZ=0 EndX=-1 EndY=8.75 EndZ=0
    g22: LineSegment StartX=-1 StartY=8.75 StartZ=0 EndX=-4.03109 EndY=10.5 EndZ=0
    g23: LineSegment StartX=-4.03109 StartY=10.5 StartZ=0 EndX=-7.06218 EndY=8.75 EndZ=0
    g24: LineSegment StartX=-7.06218 StartY=8.75 StartZ=0 EndX=-7.06218 EndY=5.25 EndZ=0
    g25: LineSegment StartX=-7.06218 StartY=5.25 StartZ=0 EndX=-4.03109 EndY=3.5 EndZ=0
    g26: LineSegment StartX=-4.03109 StartY=3.5 StartZ=0 EndX=-1 EndY=5.25 EndZ=0
    g27: Circle [constr] CenterX=-4.03109 CenterY=7 CenterZ=0 NormalX=0 NormalY=0 NormalZ=1 AngleXU=0 Radius=3.5
    g28: LineSegment StartX=-4.96891 StartY=-1.75 StartZ=0 EndX=-4.96891 EndY=1.75 EndZ=0
    g29: LineSegment StartX=-4.96891 StartY=1.75 StartZ=0 EndX=-8 EndY=3.5 EndZ=0
    g30: LineSegment StartX=-8 StartY=3.5 StartZ=0 EndX=-11.0311 EndY=1.75 EndZ=0
    g31: LineSegment StartX=-11.0311 StartY=1.75 StartZ=0 EndX=-11.0311 EndY=-1.75 EndZ=0
    g32: LineSegment StartX=-11.0311 StartY=-1.75 StartZ=0 EndX=-8 EndY=-3.5 EndZ=0
    g33: LineSegment StartX=-8 StartY=-3.5 StartZ=0 EndX=-4.96891 EndY=-1.75 EndZ=0
    g34: Circle [constr] CenterX=-8 CenterY=0 CenterZ=0 NormalX=0 NormalY=0 NormalZ=1 AngleXU=0 Radius=3.5
    g35: LineSegment StartX=-4.03109 StartY=-3.5 StartZ=0 EndX=-7.06218 EndY=-5.25 EndZ=0
    g36: LineSegment StartX=-7.06218 StartY=-5.25 StartZ=0 EndX=-7.06218 EndY=-8.75 EndZ=0
    g37: LineSegment StartX=-7.06218 StartY=-8.75 StartZ=0 EndX=-4.03109 EndY=-10.5 EndZ=0
    g38: LineSegment StartX=-4.03109 StartY=-10.5 StartZ=0 EndX=-1 EndY=-8.75 EndZ=0
    g39: LineSegment StartX=-1 StartY=-8.75 StartZ=0 EndX=-1 EndY=-5.25 EndZ=0
    g40: LineSegment StartX=-1 StartY=-5.25 StartZ=0 EndX=-4.03109 EndY=-3.5 EndZ=0
    g41: Circle [constr] CenterX=-4.03109 CenterY=-7 CenterZ=0 NormalX=0 NormalY=0 NormalZ=1 AngleXU=0 Radius=3.5
    g42: LineSegment StartX=4.03109 StartY=-3.5 StartZ=0 EndX=1 EndY=-5.25 EndZ=0
    g43: LineSegment StartX=1 StartY=-5.25 StartZ=0 EndX=1 EndY=-8.75 EndZ=0
    g44: LineSegment StartX=1 StartY=-8.75 StartZ=0 EndX=4.03109 EndY=-10.5 EndZ=0
    g45: LineSegment StartX=4.03109 StartY=-10.5 StartZ=0 EndX=7.06218 EndY=-8.75 EndZ=0
    g46: LineSegment StartX=7.06218 StartY=-8.75 StartZ=0 EndX=7.06218 EndY=-5.25 EndZ=0
    g47: LineSegment StartX=7.06218 StartY=-5.25 StartZ=0 EndX=4.03109 EndY=-3.5 EndZ=0
    g48: Circle [constr] CenterX=4.03109 CenterY=-7 CenterZ=0 NormalX=0 NormalY=0 NormalZ=1 AngleXU=0 Radius=3.5
  constraints (117):
    c: Coincident(g0,g1)
    c: Coincident(g1,g2)
    c: Coincident(g2,g3)
    c: Coincident(g3,g4)
    c: Coincident(g4,g5)
    c: Coincident(g5,g0)
    c: Equal(g0, g1-g5) x5
    c: PointOnObject(g0,g6)
    c: PointOnObject(g1,g6)
    c: PointOnObject(g2,g6)
    c: PointOnObject(g3,g6)
    c: PointOnObject(g4,g6)
    c: PointOnObject(g5,g6)
    c: Coincident(g6,g-1)
    c: Diameter(g6) = 7
    c: PointOnObject(g0,g-2)
    c: Coincident(g7,g8)
    c: Coincident(g8,g9)
    c: Coincident(g9,g10)
    c: Coincident(g10,g11)
    c: Coincident(g11,g12)
    c: Coincident(g12,g7)
    c: Equal(g7, g8-g12) x5
    c: PointOnObject(g7,g13)
    c: PointOnObject(g8,g13)
    c: PointOnObject(g9,g13)
    c: PointOnObject(g10,g13)
    c: PointOnObject(g11,g13)
    c: PointOnObject(g12,g13)
    c: PointOnObject(g13,g-1)
    c: Diameter(g13) = 7
    c: Distance(g6,g13) = 8
    c: Horizontal(g0,g10)
    c: Coincident(g14,g15)
    c: Coincident(g15,g16)
    c: Coincident(g16,g17)
    c: Coincident(g17,g18)
    c: Coincident(g18,g19)
    c: Coincident(g19,g14)
    c: Equal(g14, g15-g19) x5
    c: PointOnObject(g14,g20)
    c: PointOnObject(g15,g20)
    c: PointOnObject(g16,g20)
    c: PointOnObject(g17,g20)
    c: PointOnObject(g18,g20)
    c: PointOnObject(g19,g20)
    c: Diameter(g20) = 7
    c: DistanceY(g-1,g20) = 7
    c: Vertical(g18)
    c: Distance(g17,g-2) = 1
    c: Coincident(g21,g22)
    c: Coincident(g22,g23)
    c: Coincident(g23,g24)
    c: Coincident(g24,g25)
    c: Coincident(g25,g26)
    c: Coincident(g26,g21)
    c: Equal(g21, g22-g26) x5
    c: PointOnObject(g21,g27)
    c: PointOnObject(g22,g27)
    c: PointOnObject(g23,g27)
    c: PointOnObject(g24,g27)
    c: PointOnObject(g25,g27)
    c: PointOnObject(g26,g27)
    c: Diameter(g27) = 7
    c: DistanceY(g-1,g27) = 7
    c: DistanceX(g21,g-1) = 1
    c: Vertical(g21)
    c: Coincident(g28,g29)
    c: Coincident(g29,g30)
    c: Coincident(g30,g31)
    c: Coincident(g31,g32)
    c: Coincident(g32,g33)
    c: Coincident(g33,g28)
    c: Equal(g28, g29-g33) x5
    c: PointOnObject(g28,g34)
    c: PointOnObject(g29,g34)
    c: PointOnObject(g30,g34)
    c: PointOnObject(g31,g34)
    c: PointOnObject(g32,g34)
    c: PointOnObject(g33,g34)
    c: PointOnObject(g34,g-1)
    c: Diameter(g34) = 7
    c: Vertical(g31)
    c: DistanceX(g34,g-1) = 8
    c: Coincident(g35,g36)
    c: Coincident(g36,g37)
    c: Coincident(g37,g38)
    c: Coincident(g38,g39)
    c: Coincident(g39,g40)
    c: Coincident(g40,g35)
    c: Equal(g35, g36-g40) x5
    c: PointOnObject(g35,g41)
    c: PointOnObject(g36,g41)
    c: PointOnObject(g37,g41)
    c: PointOnObject(g38,g41)
    c: PointOnObject(g39,g41)
    c: PointOnObject(g40,g41)
    c: Coincident(g42,g43)
    c: Coincident(g43,g44)
    c: Coincident(g44,g45)
    c: Coincident(g45,g46)
    c: Coincident(g46,g47)
    c: Coincident(g47,g42)
    c: Equal(g42, g43-g47) x5
    c: PointOnObject(g42,g48)
    c: PointOnObject(g43,g48)
    c: PointOnObject(g44,g48)
    c: PointOnObject(g45,g48)
    c: PointOnObject(g46,g48)
    c: PointOnObject(g47,g48)
    c: Equal(g41,g48)
    c: Diameter(g41) = 7
    c: Vertical(g39)
    c: Vertical(g43)
    c: Distance(g-2,g39) = 1
    c: Symmetric(g38,g43,g-2)
    c: Distance(g41,g-1) = 7
FEATURE [Part::Extrusion] Extrude469  label="hex084"
  Base = -> Sketch477
  Dir = (0,-1,2e-16)
  DirMode = 2
  FaceMakerClass = Part::FaceMakerBullseye
  FaceMakerMode = 3
  LengthFwd = 10
  LengthRev = 0
  Placement = pos=(-16,0,-56) rot=(0,0,1;0rad)
  Solid = true
  Symmetric = false
FEATURE [Sketcher::SketchObject] Sketch478
  ArcFitTolerance = 1e-06
  FullyConstrained = true
  MakeInternals = false
  Placement = pos=(0,0,0) rot=(1,0,0;1.5708rad)
  sketch-geometry (49):
    g0: LineSegment StartX=1e-16 StartY=3.5 StartZ=0 EndX=-3.03109 EndY=1.75 EndZ=0
    g1: LineSegment StartX=-3.03109 StartY=1.75 StartZ=0 EndX=-3.03109 EndY=-1.75 EndZ=0
    g2: LineSegment StartX=-3.03109 StartY=-1.75 StartZ=0 EndX=-1e-16 EndY=-3.5 EndZ=0
    g3: LineSegment StartX=-1e-16 StartY=-3.5 StartZ=0 EndX=3.03109 EndY=-1.75 EndZ=0
    g4: LineSegment StartX=3.03109 StartY=-1.75 StartZ=0 EndX=3.03109 EndY=1.75 EndZ=0
    g5: LineSegment StartX=3.03109 StartY=1.75 StartZ=0 EndX=1e-16 EndY=3.5 EndZ=0
    g6: Circle [constr] CenterX=0 CenterY=0 CenterZ=0 NormalX=0 NormalY=0 NormalZ=1 AngleXU=0 Radius=3.5
    g7: LineSegment StartX=4.96892 StartY=-1.75002 StartZ=0 EndX=8.00002 EndY=-3.5 EndZ=0
    g8: LineSegment StartX=8.00002 StartY=-3.5 StartZ=0 EndX=11.0311 EndY=-1.74998 EndZ=0
    g9: LineSegment StartX=11.0311 StartY=-1.74998 StartZ=0 EndX=11.0311 EndY=1.75002 EndZ=0
    g10: LineSegment StartX=11.0311 StartY=1.75002 StartZ=0 EndX=7.99998 EndY=3.5 EndZ=0
    g11: LineSegment StartX=7.99998 StartY=3.5 StartZ=0 EndX=4.9689 EndY=1.74998 EndZ=0
    g12: LineSegment StartX=4.9689 StartY=1.74998 StartZ=0 EndX=4.96892 EndY=-1.75002 EndZ=0
    g13: Circle [constr] CenterX=8 CenterY=0 CenterZ=0 NormalX=0 NormalY=0 NormalZ=1 AngleXU=0 Radius=3.5
    g14: LineSegment StartX=4.03109 StartY=3.5 StartZ=0 EndX=7.06218 EndY=5.25 EndZ=0
    g15: LineSegment StartX=7.06218 StartY=5.25 StartZ=0 EndX=7.06218 EndY=8.75 EndZ=0
    g16: LineSegment StartX=7.06218 StartY=8.75 StartZ=0 EndX=4.03109 EndY=10.5 EndZ=0
    g17: LineSegment StartX=4.03109 StartY=10.5 StartZ=0 EndX=1 EndY=8.75 EndZ=0
    g18: LineSegment StartX=1 StartY=8.75 StartZ=0 EndX=1 EndY=5.25 EndZ=0
    g19: LineSegment StartX=1 StartY=5.25 StartZ=0 EndX=4.03109 EndY=3.5 EndZ=0
    g20: Circle [constr] CenterX=4.03109 CenterY=7 CenterZ=0 NormalX=0 NormalY=0 NormalZ=1 AngleXU=0 Radius=3.5
    g21: LineSegment StartX=-1 StartY=5.25 StartZ=0 EndX=-1 EndY=8.75 EndZ=0
    g22: LineSegment StartX=-1 StartY=8.75 StartZ=0 EndX=-4.03109 EndY=10.5 EndZ=0
    g23: LineSegment StartX=-4.03109 StartY=10.5 StartZ=0 EndX=-7.06218 EndY=8.75 EndZ=0
    g24: LineSegment StartX=-7.06218 StartY=8.75 StartZ=0 EndX=-7.06218 EndY=5.25 EndZ=0
    g25: LineSegment StartX=-7.06218 StartY=5.25 StartZ=0 EndX=-4.03109 EndY=3.5 EndZ=0
    g26: LineSegment StartX=-4.03109 StartY=3.5 StartZ=0 EndX=-1 EndY=5.25 EndZ=0
    g27: Circle [constr] CenterX=-4.03109 CenterY=7 CenterZ=0 NormalX=0 NormalY=0 NormalZ=1 AngleXU=0 Radius=3.5
    g28: LineSegment StartX=-4.96891 StartY=-1.75 StartZ=0 EndX=-4.96891 EndY=1.75 EndZ=0
    g29: LineSegment StartX=-4.96891 StartY=1.75 StartZ=0 EndX=-8 EndY=3.5 EndZ=0
    g30: LineSegment StartX=-8 StartY=3.5 StartZ=0 EndX=-11.0311 EndY=1.75 EndZ=0
    g31: LineSegment StartX=-11.0311 StartY=1.75 StartZ=0 EndX=-11.0311 EndY=-1.75 EndZ=0
    g32: LineSegment StartX=-11.0311 StartY=-1.75 StartZ=0 EndX=-8 EndY=-3.5 EndZ=0
    g33: LineSegment StartX=-8 StartY=-3.5 StartZ=0 EndX=-4.96891 EndY=-1.75 EndZ=0
    g34: Circle [constr] CenterX=-8 CenterY=0 CenterZ=0 NormalX=0 NormalY=0 NormalZ=1 AngleXU=0 Radius=3.5
    g35: LineSegment StartX=-4.03109 StartY=-3.5 StartZ=0 EndX=-7.06218 EndY=-5.25 EndZ=0
    g36: LineSegment StartX=-7.06218 StartY=-5.25 StartZ=0 EndX=-7.06218 EndY=-8.75 EndZ=0
    g37: LineSegment StartX=-7.06218 StartY=-8.75 StartZ=0 EndX=-4.03109 EndY=-10.5 EndZ=0
    g38: LineSegment StartX=-4.03109 StartY=-10.5 StartZ=0 EndX=-1 EndY=-8.75 EndZ=0
    g39: LineSegment StartX=-1 StartY=-8.75 StartZ=0 EndX=-1 EndY=-5.25 EndZ=0
    g40: LineSegment StartX=-1 StartY=-5.25 StartZ=0 EndX=-4.03109 EndY=-3.5 EndZ=0
    g41: Circle [constr] CenterX=-4.03109 CenterY=-7 CenterZ=0 NormalX=0 NormalY=0 NormalZ=1 AngleXU=0 Radius=3.5
    g42: LineSegment StartX=4.03109 StartY=-3.5 StartZ=0 EndX=1 EndY=-5.25 EndZ=0
    g43: LineSegment StartX=1 StartY=-5.25 StartZ=0 EndX=1 EndY=-8.75 EndZ=0
    g44: LineSegment StartX=1 StartY=-8.75 StartZ=0 EndX=4.03109 EndY=-10.5 EndZ=0
    g45: LineSegment StartX=4.03109 StartY=-10.5 StartZ=0 EndX=7.06218 EndY=-8.75 EndZ=0
    g46: LineSegment StartX=7.06218 StartY=-8.75 StartZ=0 EndX=7.06218 EndY=-5.25 EndZ=0
    g47: LineSegment StartX=7.06218 StartY=-5.25 StartZ=0 EndX=4.03109 EndY=-3.5 EndZ=0
    g48: Circle [constr] CenterX=4.03109 CenterY=-7 CenterZ=0 NormalX=0 NormalY=0 NormalZ=1 AngleXU=0 Radius=3.5
  constraints (117):
    c: Coincident(g0,g1)
    c: Coincident(g1,g2)
    c: Coincident(g2,g3)
    c: Coincident(g3,g4)
    c: Coincident(g4,g5)
    c: Coincident(g5,g0)
    c: Equal(g0, g1-g5) x5
    c: PointOnObject(g0,g6)
    c: PointOnObject(g1,g6)
    c: PointOnObject(g2,g6)
    c: PointOnObject(g3,g6)
    c: PointOnObject(g4,g6)
    c: PointOnObject(g5,g6)
    c: Coincident(g6,g-1)
    c: Diameter(g6) = 7
    c: PointOnObject(g0,g-2)
    c: Coincident(g7,g8)
    c: Coincident(g8,g9)
    c: Coincident(g9,g10)
    c: Coincident(g10,g11)
    c: Coincident(g11,g12)
    c: Coincident(g12,g7)
    c: Equal(g7, g8-g12) x5
    c: PointOnObject(g7,g13)
    c: PointOnObject(g8,g13)
    c: PointOnObject(g9,g13)
    c: PointOnObject(g10,g13)
    c: PointOnObject(g11,g13)
    c: PointOnObject(g12,g13)
    c: PointOnObject(g13,g-1)
    c: Diameter(g13) = 7
    c: Distance(g6,g13) = 8
    c: Horizontal(g0,g10)
    c: Coincident(g14,g15)
    c: Coincident(g15,g16)
    c: Coincident(g16,g17)
    c: Coincident(g17,g18)
    c: Coincident(g18,g19)
    c: Coincident(g19,g14)
    c: Equal(g14, g15-g19) x5
    c: PointOnObject(g14,g20)
    c: PointOnObject(g15,g20)
    c: PointOnObject(g16,g20)
    c: PointOnObject(g17,g20)
    c: PointOnObject(g18,g20)
    c: PointOnObject(g19,g20)
    c: Diameter(g20) = 7
    c: DistanceY(g-1,g20) = 7
    c: Vertical(g18)
    c: Distance(g17,g-2) = 1
    c: Coincident(g21,g22)
    c: Coincident(g22,g23)
    c: Coincident(g23,g24)
    c: Coincident(g24,g25)
    c: Coincident(g25,g26)
    c: Coincident(g26,g21)
    c: Equal(g21, g22-g26) x5
    c: PointOnObject(g21,g27)
    c: PointOnObject(g22,g27)
    c: PointOnObject(g23,g27)
    c: PointOnObject(g24,g27)
    c: PointOnObject(g25,g27)
    c: PointOnObject(g26,g27)
    c: Diameter(g27) = 7
    c: DistanceY(g-1,g27) = 7
    c: DistanceX(g21,g-1) = 1
    c: Vertical(g21)
    c: Coincident(g28,g29)
    c: Coincident(g29,g30)
    c: Coincident(g30,g31)
    c: Coincident(g31,g32)
    c: Coincident(g32,g33)
    c: Coincident(g33,g28)
    c: Equal(g28, g29-g33) x5
    c: PointOnObject(g28,g34)
    c: PointOnObject(g29,g34)
    c: PointOnObject(g30,g34)
    c: PointOnObject(g31,g34)
    c: PointOnObject(g32,g34)
    c: PointOnObject(g33,g34)
    c: PointOnObject(g34,g-1)
    c: Diameter(g34) = 7
    c: Vertical(g31)
    c: DistanceX(g34,g-1) = 8
    c: Coincident(g35,g36)
    c: Coincident(g36,g37)
    c: Coincident(g37,g38)
    c: Coincident(g38,g39)
    c: Coincident(g39,g40)
    c: Coincident(g40,g35)
    c: Equal(g35, g36-g40) x5
    c: PointOnObject(g35,g41)
    c: PointOnObject(g36,g41)
    c: PointOnObject(g37,g41)
    c: PointOnObject(g38,g41)
    c: PointOnObject(g39,g41)
    c: PointOnObject(g40,g41)
    c: Coincident(g42,g43)
    c: Coincident(g43,g44)
    c: Coincident(g44,g45)
    c: Coincident(g45,g46)
    c: Coincident(g46,g47)
    c: Coincident(g47,g42)
    c: Equal(g42, g43-g47) x5
    c: PointOnObject(g42,g48)
    c: PointOnObject(g43,g48)
    c: PointOnObject(g44,g48)
    c: PointOnObject(g45,g48)
    c: PointOnObject(g46,g48)
    c: PointOnObject(g47,g48)
    c: Equal(g41,g48)
    c: Diameter(g41) = 7
    c: Vertical(g39)
    c: Vertical(g43)
    c: Distance(g-2,g39) = 1
    c: Symmetric(g38,g43,g-2)
    c: Distance(g41,g-1) = 7
FEATURE [Part::Extrusion] Extrude470  label="hex085"
  Base = -> Sketch478
  Dir = (0,-1,2e-16)
  DirMode = 2
  FaceMakerClass = Part::FaceMakerBullseye
  FaceMakerMode = 3
  LengthFwd = 10
  LengthRev = 0
  Placement = pos=(8,0,-56) rot=(0,0,1;0rad)
  Solid = true
  Symmetric = false
FEATURE [Sketcher::SketchObject] Sketch479
  ArcFitTolerance = 1e-06
  FullyConstrained = true
  MakeInternals = false
  Placement = pos=(0,0,0) rot=(1,0,0;1.5708rad)
  sketch-geometry (49):
    g0: LineSegment StartX=1e-16 StartY=3.5 StartZ=0 EndX=-3.03109 EndY=1.75 EndZ=0
    g1: LineSegment StartX=-3.03109 StartY=1.75 StartZ=0 EndX=-3.03109 EndY=-1.75 EndZ=0
    g2: LineSegment StartX=-3.03109 StartY=-1.75 StartZ=0 EndX=-1e-16 EndY=-3.5 EndZ=0
    g3: LineSegment StartX=-1e-16 StartY=-3.5 StartZ=0 EndX=3.03109 EndY=-1.75 EndZ=0
    g4: LineSegment StartX=3.03109 StartY=-1.75 StartZ=0 EndX=3.03109 EndY=1.75 EndZ=0
    g5: LineSegment StartX=3.03109 StartY=1.75 StartZ=0 EndX=1e-16 EndY=3.5 EndZ=0
    g6: Circle [constr] CenterX=0 CenterY=0 CenterZ=0 NormalX=0 NormalY=0 NormalZ=1 AngleXU=0 Radius=3.5
    g7: LineSegment StartX=4.96892 StartY=-1.75002 StartZ=0 EndX=8.00002 EndY=-3.5 EndZ=0
    g8: LineSegment StartX=8.00002 StartY=-3.5 StartZ=0 EndX=11.0311 EndY=-1.74998 EndZ=0
    g9: LineSegment StartX=11.0311 StartY=-1.74998 StartZ=0 EndX=11.0311 EndY=1.75002 EndZ=0
    g10: LineSegment StartX=11.0311 StartY=1.75002 StartZ=0 EndX=7.99998 EndY=3.5 EndZ=0
    g11: LineSegment StartX=7.99998 StartY=3.5 StartZ=0 EndX=4.9689 EndY=1.74998 EndZ=0
    g12: LineSegment StartX=4.9689 StartY=1.74998 StartZ=0 EndX=4.96892 EndY=-1.75002 EndZ=0
    g13: Circle [constr] CenterX=8 CenterY=0 CenterZ=0 NormalX=0 NormalY=0 NormalZ=1 AngleXU=0 Radius=3.5
    g14: LineSegment StartX=4.03109 StartY=3.5 StartZ=0 EndX=7.06218 EndY=5.25 EndZ=0
    g15: LineSegment StartX=7.06218 StartY=5.25 StartZ=0 EndX=7.06218 EndY=8.75 EndZ=0
    g16: LineSegment StartX=7.06218 StartY=8.75 StartZ=0 EndX=4.03109 EndY=10.5 EndZ=0
    g17: LineSegment StartX=4.03109 StartY=10.5 StartZ=0 EndX=1 EndY=8.75 EndZ=0
    g18: LineSegment StartX=1 StartY=8.75 StartZ=0 EndX=1 EndY=5.25 EndZ=0
    g19: LineSegment StartX=1 StartY=5.25 StartZ=0 EndX=4.03109 EndY=3.5 EndZ=0
    g20: Circle [constr] CenterX=4.03109 CenterY=7 CenterZ=0 NormalX=0 NormalY=0 NormalZ=1 AngleXU=0 Radius=3.5
    g21: LineSegment StartX=-1 StartY=5.25 StartZ=0 EndX=-1 EndY=8.75 EndZ=0
    g22: LineSegment StartX=-1 StartY=8.75 StartZ=0 EndX=-4.03109 EndY=10.5 EndZ=0
    g23: LineSegment StartX=-4.03109 StartY=10.5 StartZ=0 EndX=-7.06218 EndY=8.75 EndZ=0
    g24: LineSegment StartX=-7.06218 StartY=8.75 StartZ=0 EndX=-7.06218 EndY=5.25 EndZ=0
    g25: LineSegment StartX=-7.06218 StartY=5.25 StartZ=0 EndX=-4.03109 EndY=3.5 EndZ=0
    g26: LineSegment StartX=-4.03109 StartY=3.5 StartZ=0 EndX=-1 EndY=5.25 EndZ=0
    g27: Circle [constr] CenterX=-4.03109 CenterY=7 CenterZ=0 NormalX=0 NormalY=0 NormalZ=1 AngleXU=0 Radius=3.5
    g28: LineSegment StartX=-4.96891 StartY=-1.75 StartZ=0 EndX=-4.96891 EndY=1.75 EndZ=0
    g29: LineSegment StartX=-4.96891 StartY=1.75 StartZ=0 EndX=-8 EndY=3.5 EndZ=0
    g30: LineSegment StartX=-8 StartY=3.5 StartZ=0 EndX=-11.0311 EndY=1.75 EndZ=0
    g31: LineSegment StartX=-11.0311 StartY=1.75 StartZ=0 EndX=-11.0311 EndY=-1.75 EndZ=0
    g32: LineSegment StartX=-11.0311 StartY=-1.75 StartZ=0 EndX=-8 EndY=-3.5 EndZ=0
    g33: LineSegment StartX=-8 StartY=-3.5 StartZ=0 EndX=-4.96891 EndY=-1.75 EndZ=0
    g34: Circle [constr] CenterX=-8 CenterY=0 CenterZ=0 NormalX=0 NormalY=0 NormalZ=1 AngleXU=0 Radius=3.5
    g35: LineSegment StartX=-4.03109 StartY=-3.5 StartZ=0 EndX=-7.06218 EndY=-5.25 EndZ=0
    g36: LineSegment StartX=-7.06218 StartY=-5.25 StartZ=0 EndX=-7.06218 EndY=-8.75 EndZ=0
    g37: LineSegment StartX=-7.06218 StartY=-8.75 StartZ=0 EndX=-4.03109 EndY=-10.5 EndZ=0
    g38: LineSegment StartX=-4.03109 StartY=-10.5 StartZ=0 EndX=-1 EndY=-8.75 EndZ=0
    g39: LineSegment StartX=-1 StartY=-8.75 StartZ=0 EndX=-1 EndY=-5.25 EndZ=0
    g40: LineSegment StartX=-1 StartY=-5.25 StartZ=0 EndX=-4.03109 EndY=-3.5 EndZ=0
    g41: Circle [constr] CenterX=-4.03109 CenterY=-7 CenterZ=0 NormalX=0 NormalY=0 NormalZ=1 AngleXU=0 Radius=3.5
    g42: LineSegment StartX=4.03109 StartY=-3.5 StartZ=0 EndX=1 EndY=-5.25 EndZ=0
    g43: LineSegment StartX=1 StartY=-5.25 StartZ=0 EndX=1 EndY=-8.75 EndZ=0
    g44: LineSegment StartX=1 StartY=-8.75 StartZ=0 EndX=4.03109 EndY=-10.5 EndZ=0
    g45: LineSegment StartX=4.03109 StartY=-10.5 StartZ=0 EndX=7.06218 EndY=-8.75 EndZ=0
    g46: LineSegment StartX=7.06218 StartY=-8.75 StartZ=0 EndX=7.06218 EndY=-5.25 EndZ=0
    g47: LineSegment StartX=7.06218 StartY=-5.25 StartZ=0 EndX=4.03109 EndY=-3.5 EndZ=0
    g48: Circle [constr] CenterX=4.03109 CenterY=-7 CenterZ=0 NormalX=0 NormalY=0 NormalZ=1 AngleXU=0 Radius=3.5
  constraints (117):
    c: Coincident(g0,g1)
    c: Coincident(g1,g2)
    c: Coincident(g2,g3)
    c: Coincident(g3,g4)
    c: Coincident(g4,g5)
    c: Coincident(g5,g0)
    c: Equal(g0, g1-g5) x5
    c: PointOnObject(g0,g6)
    c: PointOnObject(g1,g6)
    c: PointOnObject(g2,g6)
    c: PointOnObject(g3,g6)
    c: PointOnObject(g4,g6)
    c: PointOnObject(g5,g6)
    c: Coincident(g6,g-1)
    c: Diameter(g6) = 7
    c: PointOnObject(g0,g-2)
    c: Coincident(g7,g8)
    c: Coincident(g8,g9)
    c: Coincident(g9,g10)
    c: Coincident(g10,g11)
    c: Coincident(g11,g12)
    c: Coincident(g12,g7)
    c: Equal(g7, g8-g12) x5
    c: PointOnObject(g7,g13)
    c: PointOnObject(g8,g13)
    c: PointOnObject(g9,g13)
    c: PointOnObject(g10,g13)
    c: PointOnObject(g11,g13)
    c: PointOnObject(g12,g13)
    c: PointOnObject(g13,g-1)
    c: Diameter(g13) = 7
    c: Distance(g6,g13) = 8
    c: Horizontal(g0,g10)
    c: Coincident(g14,g15)
    c: Coincident(g15,g16)
    c: Coincident(g16,g17)
    c: Coincident(g17,g18)
    c: Coincident(g18,g19)
    c: Coincident(g19,g14)
    c: Equal(g14, g15-g19) x5
    c: PointOnObject(g14,g20)
    c: PointOnObject(g15,g20)
    c: PointOnObject(g16,g20)
    c: PointOnObject(g17,g20)
    c: PointOnObject(g18,g20)
    c: PointOnObject(g19,g20)
    c: Diameter(g20) = 7
    c: DistanceY(g-1,g20) = 7
    c: Vertical(g18)
    c: Distance(g17,g-2) = 1
    c: Coincident(g21,g22)
    c: Coincident(g22,g23)
    c: Coincident(g23,g24)
    c: Coincident(g24,g25)
    c: Coincident(g25,g26)
    c: Coincident(g26,g21)
    c: Equal(g21, g22-g26) x5
    c: PointOnObject(g21,g27)
    c: PointOnObject(g22,g27)
    c: PointOnObject(g23,g27)
    c: PointOnObject(g24,g27)
    c: PointOnObject(g25,g27)
    c: PointOnObject(g26,g27)
    c: Diameter(g27) = 7
    c: DistanceY(g-1,g27) = 7
    c: DistanceX(g21,g-1) = 1
    c: Vertical(g21)
    c: Coincident(g28,g29)
    c: Coincident(g29,g30)
    c: Coincident(g30,g31)
    c: Coincident(g31,g32)
    c: Coincident(g32,g33)
    c: Coincident(g33,g28)
    c: Equal(g28, g29-g33) x5
    c: PointOnObject(g28,g34)
    c: PointOnObject(g29,g34)
    c: PointOnObject(g30,g34)
    c: PointOnObject(g31,g34)
    c: PointOnObject(g32,g34)
    c: PointOnObject(g33,g34)
    c: PointOnObject(g34,g-1)
    c: Diameter(g34) = 7
    c: Vertical(g31)
    c: DistanceX(g34,g-1) = 8
    c: Coincident(g35,g36)
    c: Coincident(g36,g37)
    c: Coincident(g37,g38)
    c: Coincident(g38,g39)
    c: Coincident(g39,g40)
    c: Coincident(g40,g35)
    c: Equal(g35, g36-g40) x5
    c: PointOnObject(g35,g41)
    c: PointOnObject(g36,g41)
    c: PointOnObject(g37,g41)
    c: PointOnObject(g38,g41)
    c: PointOnObject(g39,g41)
    c: PointOnObject(g40,g41)
    c: Coincident(g42,g43)
    c: Coincident(g43,g44)
    c: Coincident(g44,g45)
    c: Coincident(g45,g46)
    c: Coincident(g46,g47)
    c: Coincident(g47,g42)
    c: Equal(g42, g43-g47) x5
    c: PointOnObject(g42,g48)
    c: PointOnObject(g43,g48)
    c: PointOnObject(g44,g48)
    c: PointOnObject(g45,g48)
    c: PointOnObject(g46,g48)
    c: PointOnObject(g47,g48)
    c: Equal(g41,g48)
    c: Diameter(g41) = 7
    c: Vertical(g39)
    c: Vertical(g43)
    c: Distance(g-2,g39) = 1
    c: Symmetric(g38,g43,g-2)
    c: Distance(g41,g-1) = 7
FEATURE [Part::Extrusion] Extrude471  label="hex086"
  Base = -> Sketch479
  Dir = (0,-1,2e-16)
  DirMode = 2
  FaceMakerClass = Part::FaceMakerBullseye
  FaceMakerMode = 3
  LengthFwd = 10
  LengthRev = 0
  Placement = pos=(28,0,-49) rot=(0,0,1;0rad)
  Solid = true
  Symmetric = false
FEATURE [Sketcher::SketchObject] Sketch480
  ArcFitTolerance = 1e-06
  FullyConstrained = true
  MakeInternals = false
  Placement = pos=(0,0,0) rot=(1,0,0;1.5708rad)
  sketch-geometry (49):
    g0: LineSegment StartX=1e-16 StartY=3.5 StartZ=0 EndX=-3.03109 EndY=1.75 EndZ=0
    g1: LineSegment StartX=-3.03109 StartY=1.75 StartZ=0 EndX=-3.03109 EndY=-1.75 EndZ=0
    g2: LineSegment StartX=-3.03109 StartY=-1.75 StartZ=0 EndX=-1e-16 EndY=-3.5 EndZ=0
    g3: LineSegment StartX=-1e-16 StartY=-3.5 StartZ=0 EndX=3.03109 EndY=-1.75 EndZ=0
    g4: LineSegment StartX=3.03109 StartY=-1.75 StartZ=0 EndX=3.03109 EndY=1.75 EndZ=0
    g5: LineSegment StartX=3.03109 StartY=1.75 StartZ=0 EndX=1e-16 EndY=3.5 EndZ=0
    g6: Circle [constr] CenterX=0 CenterY=0 CenterZ=0 NormalX=0 NormalY=0 NormalZ=1 AngleXU=0 Radius=3.5
    g7: LineSegment StartX=4.96892 StartY=-1.75002 StartZ=0 EndX=8.00002 EndY=-3.5 EndZ=0
    g8: LineSegment StartX=8.00002 StartY=-3.5 StartZ=0 EndX=11.0311 EndY=-1.74998 EndZ=0
    g9: LineSegment StartX=11.0311 StartY=-1.74998 StartZ=0 EndX=11.0311 EndY=1.75002 EndZ=0
    g10: LineSegment StartX=11.0311 StartY=1.75002 StartZ=0 EndX=7.99998 EndY=3.5 EndZ=0
    g11: LineSegment StartX=7.99998 StartY=3.5 StartZ=0 EndX=4.9689 EndY=1.74998 EndZ=0
    g12: LineSegment StartX=4.9689 StartY=1.74998 StartZ=0 EndX=4.96892 EndY=-1.75002 EndZ=0
    g13: Circle [constr] CenterX=8 CenterY=0 CenterZ=0 NormalX=0 NormalY=0 NormalZ=1 AngleXU=0 Radius=3.5
    g14: LineSegment StartX=4.03109 StartY=3.5 StartZ=0 EndX=7.06218 EndY=5.25 EndZ=0
    g15: LineSegment StartX=7.06218 StartY=5.25 StartZ=0 EndX=7.06218 EndY=8.75 EndZ=0
    g16: LineSegment StartX=7.06218 StartY=8.75 StartZ=0 EndX=4.03109 EndY=10.5 EndZ=0
    g17: LineSegment StartX=4.03109 StartY=10.5 StartZ=0 EndX=1 EndY=8.75 EndZ=0
    g18: LineSegment StartX=1 StartY=8.75 StartZ=0 EndX=1 EndY=5.25 EndZ=0
    g19: LineSegment StartX=1 StartY=5.25 StartZ=0 EndX=4.03109 EndY=3.5 EndZ=0
    g20: Circle [constr] CenterX=4.03109 CenterY=7 CenterZ=0 NormalX=0 NormalY=0 NormalZ=1 AngleXU=0 Radius=3.5
    g21: LineSegment StartX=-1 StartY=5.25 StartZ=0 EndX=-1 EndY=8.75 EndZ=0
    g22: LineSegment StartX=-1 StartY=8.75 StartZ=0 EndX=-4.03109 EndY=10.5 EndZ=0
    g23: LineSegment StartX=-4.03109 StartY=10.5 StartZ=0 EndX=-7.06218 EndY=8.75 EndZ=0
    g24: LineSegment StartX=-7.06218 StartY=8.75 StartZ=0 EndX=-7.06218 EndY=5.25 EndZ=0
    g25: LineSegment StartX=-7.06218 StartY=5.25 StartZ=0 EndX=-4.03109 EndY=3.5 EndZ=0
    g26: LineSegment StartX=-4.03109 StartY=3.5 StartZ=0 EndX=-1 EndY=5.25 EndZ=0
    g27: Circle [constr] CenterX=-4.03109 CenterY=7 CenterZ=0 NormalX=0 NormalY=0 NormalZ=1 AngleXU=0 Radius=3.5
    g28: LineSegment StartX=-4.96891 StartY=-1.75 StartZ=0 EndX=-4.96891 EndY=1.75 EndZ=0
    g29: LineSegment StartX=-4.96891 StartY=1.75 StartZ=0 EndX=-8 EndY=3.5 EndZ=0
    g30: LineSegment StartX=-8 StartY=3.5 StartZ=0 EndX=-11.0311 EndY=1.75 EndZ=0
    g31: LineSegment StartX=-11.0311 StartY=1.75 StartZ=0 EndX=-11.0311 EndY=-1.75 EndZ=0
    g32: LineSegment StartX=-11.0311 StartY=-1.75 StartZ=0 EndX=-8 EndY=-3.5 EndZ=0
    g33: LineSegment StartX=-8 StartY=-3.5 StartZ=0 EndX=-4.96891 EndY=-1.75 EndZ=0
    g34: Circle [constr] CenterX=-8 CenterY=0 CenterZ=0 NormalX=0 NormalY=0 NormalZ=1 AngleXU=0 Radius=3.5
    g35: LineSegment StartX=-4.03109 StartY=-3.5 StartZ=0 EndX=-7.06218 EndY=-5.25 EndZ=0
    g36: LineSegment StartX=-7.06218 StartY=-5.25 StartZ=0 EndX=-7.06218 EndY=-8.75 EndZ=0
    g37: LineSegment StartX=-7.06218 StartY=-8.75 StartZ=0 EndX=-4.03109 EndY=-10.5 EndZ=0
    g38: LineSegment StartX=-4.03109 StartY=-10.5 StartZ=0 EndX=-1 EndY=-8.75 EndZ=0
    g39: LineSegment StartX=-1 StartY=-8.75 StartZ=0 EndX=-1 EndY=-5.25 EndZ=0
    g40: LineSegment StartX=-1 StartY=-5.25 StartZ=0 EndX=-4.03109 EndY=-3.5 EndZ=0
    g41: Circle [constr] CenterX=-4.03109 CenterY=-7 CenterZ=0 NormalX=0 NormalY=0 NormalZ=1 AngleXU=0 Radius=3.5
    g42: LineSegment StartX=4.03109 StartY=-3.5 StartZ=0 EndX=1 EndY=-5.25 EndZ=0
    g43: LineSegment StartX=1 StartY=-5.25 StartZ=0 EndX=1 EndY=-8.75 EndZ=0
    g44: LineSegment StartX=1 StartY=-8.75 StartZ=0 EndX=4.03109 EndY=-10.5 EndZ=0
    g45: LineSegment StartX=4.03109 StartY=-10.5 StartZ=0 EndX=7.06218 EndY=-8.75 EndZ=0
    g46: LineSegment StartX=7.06218 StartY=-8.75 StartZ=0 EndX=7.06218 EndY=-5.25 EndZ=0
    g47: LineSegment StartX=7.06218 StartY=-5.25 StartZ=0 EndX=4.03109 EndY=-3.5 EndZ=0
    g48: Circle [constr] CenterX=4.03109 CenterY=-7 CenterZ=0 NormalX=0 NormalY=0 NormalZ=1 AngleXU=0 Radius=3.5
  constraints (117):
    c: Coincident(g0,g1)
    c: Coincident(g1,g2)
    c: Coincident(g2,g3)
    c: Coincident(g3,g4)
    c: Coincident(g4,g5)
    c: Coincident(g5,g0)
    c: Equal(g0, g1-g5) x5
    c: PointOnObject(g0,g6)
    c: PointOnObject(g1,g6)
    c: PointOnObject(g2,g6)
    c: PointOnObject(g3,g6)
    c: PointOnObject(g4,g6)
    c: PointOnObject(g5,g6)
    c: Coincident(g6,g-1)
    c: Diameter(g6) = 7
    c: PointOnObject(g0,g-2)
    c: Coincident(g7,g8)
    c: Coincident(g8,g9)
    c: Coincident(g9,g10)
    c: Coincident(g10,g11)
    c: Coincident(g11,g12)
    c: Coincident(g12,g7)
    c: Equal(g7, g8-g12) x5
    c: PointOnObject(g7,g13)
    c: PointOnObject(g8,g13)
    c: PointOnObject(g9,g13)
    c: PointOnObject(g10,g13)
    c: PointOnObject(g11,g13)
    c: PointOnObject(g12,g13)
    c: PointOnObject(g13,g-1)
    c: Diameter(g13) = 7
    c: Distance(g6,g13) = 8
    c: Horizontal(g0,g10)
    c: Coincident(g14,g15)
    c: Coincident(g15,g16)
    c: Coincident(g16,g17)
    c: Coincident(g17,g18)
    c: Coincident(g18,g19)
    c: Coincident(g19,g14)
    c: Equal(g14, g15-g19) x5
    c: PointOnObject(g14,g20)
    c: PointOnObject(g15,g20)
    c: PointOnObject(g16,g20)
    c: PointOnObject(g17,g20)
    c: PointOnObject(g18,g20)
    c: PointOnObject(g19,g20)
    c: Diameter(g20) = 7
    c: DistanceY(g-1,g20) = 7
    c: Vertical(g18)
    c: Distance(g17,g-2) = 1
    c: Coincident(g21,g22)
    c: Coincident(g22,g23)
    c: Coincident(g23,g24)
    c: Coincident(g24,g25)
    c: Coincident(g25,g26)
    c: Coincident(g26,g21)
    c: Equal(g21, g22-g26) x5
    c: PointOnObject(g21,g27)
    c: PointOnObject(g22,g27)
    c: PointOnObject(g23,g27)
    c: PointOnObject(g24,g27)
    c: PointOnObject(g25,g27)
    c: PointOnObject(g26,g27)
    c: Diameter(g27) = 7
    c: DistanceY(g-1,g27) = 7
    c: DistanceX(g21,g-1) = 1
    c: Vertical(g21)
    c: Coincident(g28,g29)
    c: Coincident(g29,g30)
    c: Coincident(g30,g31)
    c: Coincident(g31,g32)
    c: Coincident(g32,g33)
    c: Coincident(g33,g28)
    c: Equal(g28, g29-g33) x5
    c: PointOnObject(g28,g34)
    c: PointOnObject(g29,g34)
    c: PointOnObject(g30,g34)
    c: PointOnObject(g31,g34)
    c: PointOnObject(g32,g34)
    c: PointOnObject(g33,g34)
    c: PointOnObject(g34,g-1)
    c: Diameter(g34) = 7
    c: Vertical(g31)
    c: DistanceX(g34,g-1) = 8
    c: Coincident(g35,g36)
    c: Coincident(g36,g37)
    c: Coincident(g37,g38)
    c: Coincident(g38,g39)
    c: Coincident(g39,g40)
    c: Coincident(g40,g35)
    c: Equal(g35, g36-g40) x5
    c: PointOnObject(g35,g41)
    c: PointOnObject(g36,g41)
    c: PointOnObject(g37,g41)
    c: PointOnObject(g38,g41)
    c: PointOnObject(g39,g41)
    c: PointOnObject(g40,g41)
    c: Coincident(g42,g43)
    c: Coincident(g43,g44)
    c: Coincident(g44,g45)
    c: Coincident(g45,g46)
    c: Coincident(g46,g47)
    c: Coincident(g47,g42)
    c: Equal(g42, g43-g47) x5
    c: PointOnObject(g42,g48)
    c: PointOnObject(g43,g48)
    c: PointOnObject(g44,g48)
    c: PointOnObject(g45,g48)
    c: PointOnObject(g46,g48)
    c: PointOnObject(g47,g48)
    c: Equal(g41,g48)
    c: Diameter(g41) = 7
    c: Vertical(g39)
    c: Vertical(g43)
    c: Distance(g-2,g39) = 1
    c: Symmetric(g38,g43,g-2)
    c: Distance(g41,g-1) = 7
FEATURE [Part::Extrusion] Extrude472  label="hex087"
  Base = -> Sketch480
  Dir = (0,-1,2e-16)
  DirMode = 2
  FaceMakerClass = Part::FaceMakerBullseye
  FaceMakerMode = 3
  LengthFwd = 10
  LengthRev = 0
  Placement = pos=(48,0,-42) rot=(0,0,1;0rad)
  Solid = true
  Symmetric = false
FEATURE [Sketcher::SketchObject] Sketch481
  ArcFitTolerance = 1e-06
  FullyConstrained = true
  MakeInternals = false
  Placement = pos=(0,0,0) rot=(1,0,0;1.5708rad)
  sketch-geometry (49):
    g0: LineSegment StartX=1e-16 StartY=3.5 StartZ=0 EndX=-3.03109 EndY=1.75 EndZ=0
    g1: LineSegment StartX=-3.03109 StartY=1.75 StartZ=0 EndX=-3.03109 EndY=-1.75 EndZ=0
    g2: LineSegment StartX=-3.03109 StartY=-1.75 StartZ=0 EndX=-1e-16 EndY=-3.5 EndZ=0
    g3: LineSegment StartX=-1e-16 StartY=-3.5 StartZ=0 EndX=3.03109 EndY=-1.75 EndZ=0
    g4: LineSegment StartX=3.03109 StartY=-1.75 StartZ=0 EndX=3.03109 EndY=1.75 EndZ=0
    g5: LineSegment StartX=3.03109 StartY=1.75 StartZ=0 EndX=1e-16 EndY=3.5 EndZ=0
    g6: Circle [constr] CenterX=0 CenterY=0 CenterZ=0 NormalX=0 NormalY=0 NormalZ=1 AngleXU=0 Radius=3.5
    g7: LineSegment StartX=4.96892 StartY=-1.75002 StartZ=0 EndX=8.00002 EndY=-3.5 EndZ=0
    g8: LineSegment StartX=8.00002 StartY=-3.5 StartZ=0 EndX=11.0311 EndY=-1.74998 EndZ=0
    g9: LineSegment StartX=11.0311 StartY=-1.74998 StartZ=0 EndX=11.0311 EndY=1.75002 EndZ=0
    g10: LineSegment StartX=11.0311 StartY=1.75002 StartZ=0 EndX=7.99998 EndY=3.5 EndZ=0
    g11: LineSegment StartX=7.99998 StartY=3.5 StartZ=0 EndX=4.9689 EndY=1.74998 EndZ=0
    g12: LineSegment StartX=4.9689 StartY=1.74998 StartZ=0 EndX=4.96892 EndY=-1.75002 EndZ=0
    g13: Circle [constr] CenterX=8 CenterY=0 CenterZ=0 NormalX=0 NormalY=0 NormalZ=1 AngleXU=0 Radius=3.5
    g14: LineSegment StartX=4.03109 StartY=3.5 StartZ=0 EndX=7.06218 EndY=5.25 EndZ=0
    g15: LineSegment StartX=7.06218 StartY=5.25 StartZ=0 EndX=7.06218 EndY=8.75 EndZ=0
    g16: LineSegment StartX=7.06218 StartY=8.75 StartZ=0 EndX=4.03109 EndY=10.5 EndZ=0
    g17: LineSegment StartX=4.03109 StartY=10.5 StartZ=0 EndX=1 EndY=8.75 EndZ=0
    g18: LineSegment StartX=1 StartY=8.75 StartZ=0 EndX=1 EndY=5.25 EndZ=0
    g19: LineSegment StartX=1 StartY=5.25 StartZ=0 EndX=4.03109 EndY=3.5 EndZ=0
    g20: Circle [constr] CenterX=4.03109 CenterY=7 CenterZ=0 NormalX=0 NormalY=0 NormalZ=1 AngleXU=0 Radius=3.5
    g21: LineSegment StartX=-1 StartY=5.25 StartZ=0 EndX=-1 EndY=8.75 EndZ=0
    g22: LineSegment StartX=-1 StartY=8.75 StartZ=0 EndX=-4.03109 EndY=10.5 EndZ=0
    g23: LineSegment StartX=-4.03109 StartY=10.5 StartZ=0 EndX=-7.06218 EndY=8.75 EndZ=0
    g24: LineSegment StartX=-7.06218 StartY=8.75 StartZ=0 EndX=-7.06218 EndY=5.25 EndZ=0
    g25: LineSegment StartX=-7.06218 StartY=5.25 StartZ=0 EndX=-4.03109 EndY=3.5 EndZ=0
    g26: LineSegment StartX=-4.03109 StartY=3.5 StartZ=0 EndX=-1 EndY=5.25 EndZ=0
    g27: Circle [constr] CenterX=-4.03109 CenterY=7 CenterZ=0 NormalX=0 NormalY=0 NormalZ=1 AngleXU=0 Radius=3.5
    g28: LineSegment StartX=-4.96891 StartY=-1.75 StartZ=0 EndX=-4.96891 EndY=1.75 EndZ=0
    g29: LineSegment StartX=-4.96891 StartY=1.75 StartZ=0 EndX=-8 EndY=3.5 EndZ=0
    g30: LineSegment StartX=-8 StartY=3.5 StartZ=0 EndX=-11.0311 EndY=1.75 EndZ=0
    g31: LineSegment StartX=-11.0311 StartY=1.75 StartZ=0 EndX=-11.0311 EndY=-1.75 EndZ=0
    g32: LineSegment StartX=-11.0311 StartY=-1.75 StartZ=0 EndX=-8 EndY=-3.5 EndZ=0
    g33: LineSegment StartX=-8 StartY=-3.5 StartZ=0 EndX=-4.96891 EndY=-1.75 EndZ=0
    g34: Circle [constr] CenterX=-8 CenterY=0 CenterZ=0 NormalX=0 NormalY=0 NormalZ=1 AngleXU=0 Radius=3.5
    g35: LineSegment StartX=-4.03109 StartY=-3.5 StartZ=0 EndX=-7.06218 EndY=-5.25 EndZ=0
    g36: LineSegment StartX=-7.06218 StartY=-5.25 StartZ=0 EndX=-7.06218 EndY=-8.75 EndZ=0
    g37: LineSegment StartX=-7.06218 StartY=-8.75 StartZ=0 EndX=-4.03109 EndY=-10.5 EndZ=0
    g38: LineSegment StartX=-4.03109 StartY=-10.5 StartZ=0 EndX=-1 EndY=-8.75 EndZ=0
    g39: LineSegment StartX=-1 StartY=-8.75 StartZ=0 EndX=-1 EndY=-5.25 EndZ=0
    g40: LineSegment StartX=-1 StartY=-5.25 StartZ=0 EndX=-4.03109 EndY=-3.5 EndZ=0
    g41: Circle [constr] CenterX=-4.03109 CenterY=-7 CenterZ=0 NormalX=0 NormalY=0 NormalZ=1 AngleXU=0 Radius=3.5
    g42: LineSegment StartX=4.03109 StartY=-3.5 StartZ=0 EndX=1 EndY=-5.25 EndZ=0
    g43: LineSegment StartX=1 StartY=-5.25 StartZ=0 EndX=1 EndY=-8.75 EndZ=0
    g44: LineSegment StartX=1 StartY=-8.75 StartZ=0 EndX=4.03109 EndY=-10.5 EndZ=0
    g45: LineSegment StartX=4.03109 StartY=-10.5 StartZ=0 EndX=7.06218 EndY=-8.75 EndZ=0
    g46: LineSegment StartX=7.06218 StartY=-8.75 StartZ=0 EndX=7.06218 EndY=-5.25 EndZ=0
    g47: LineSegment StartX=7.06218 StartY=-5.25 StartZ=0 EndX=4.03109 EndY=-3.5 EndZ=0
    g48: Circle [constr] CenterX=4.03109 CenterY=-7 CenterZ=0 NormalX=0 NormalY=0 NormalZ=1 AngleXU=0 Radius=3.5
  constraints (117):
    c: Coincident(g0,g1)
    c: Coincident(g1,g2)
    c: Coincident(g2,g3)
    c: Coincident(g3,g4)
    c: Coincident(g4,g5)
    c: Coincident(g5,g0)
    c: Equal(g0, g1-g5) x5
    c: PointOnObject(g0,g6)
    c: PointOnObject(g1,g6)
    c: PointOnObject(g2,g6)
    c: PointOnObject(g3,g6)
    c: PointOnObject(g4,g6)
    c: PointOnObject(g5,g6)
    c: Coincident(g6,g-1)
    c: Diameter(g6) = 7
    c: PointOnObject(g0,g-2)
    c: Coincident(g7,g8)
    c: Coincident(g8,g9)
    c: Coincident(g9,g10)
    c: Coincident(g10,g11)
    c: Coincident(g11,g12)
    c: Coincident(g12,g7)
    c: Equal(g7, g8-g12) x5
    c: PointOnObject(g7,g13)
    c: PointOnObject(g8,g13)
    c: PointOnObject(g9,g13)
    c: PointOnObject(g10,g13)
    c: PointOnObject(g11,g13)
    c: PointOnObject(g12,g13)
    c: PointOnObject(g13,g-1)
    c: Diameter(g13) = 7
    c: Distance(g6,g13) = 8
    c: Horizontal(g0,g10)
    c: Coincident(g14,g15)
    c: Coincident(g15,g16)
    c: Coincident(g16,g17)
    c: Coincident(g17,g18)
    c: Coincident(g18,g19)
    c: Coincident(g19,g14)
    c: Equal(g14, g15-g19) x5
    c: PointOnObject(g14,g20)
    c: PointOnObject(g15,g20)
    c: PointOnObject(g16,g20)
    c: PointOnObject(g17,g20)
    c: PointOnObject(g18,g20)
    c: PointOnObject(g19,g20)
    c: Diameter(g20) = 7
    c: DistanceY(g-1,g20) = 7
    c: Vertical(g18)
    c: Distance(g17,g-2) = 1
    c: Coincident(g21,g22)
    c: Coincident(g22,g23)
    c: Coincident(g23,g24)
    c: Coincident(g24,g25)
    c: Coincident(g25,g26)
    c: Coincident(g26,g21)
    c: Equal(g21, g22-g26) x5
    c: PointOnObject(g21,g27)
    c: PointOnObject(g22,g27)
    c: PointOnObject(g23,g27)
    c: PointOnObject(g24,g27)
    c: PointOnObject(g25,g27)
    c: PointOnObject(g26,g27)
    c: Diameter(g27) = 7
    c: DistanceY(g-1,g27) = 7
    c: DistanceX(g21,g-1) = 1
    c: Vertical(g21)
    c: Coincident(g28,g29)
    c: Coincident(g29,g30)
    c: Coincident(g30,g31)
    c: Coincident(g31,g32)
    c: Coincident(g32,g33)
    c: Coincident(g33,g28)
    c: Equal(g28, g29-g33) x5
    c: PointOnObject(g28,g34)
    c: PointOnObject(g29,g34)
    c: PointOnObject(g30,g34)
    c: PointOnObject(g31,g34)
    c: PointOnObject(g32,g34)
    c: PointOnObject(g33,g34)
    c: PointOnObject(g34,g-1)
    c: Diameter(g34) = 7
    c: Vertical(g31)
    c: DistanceX(g34,g-1) = 8
    c: Coincident(g35,g36)
    c: Coincident(g36,g37)
    c: Coincident(g37,g38)
    c: Coincident(g38,g39)
    c: Coincident(g39,g40)
    c: Coincident(g40,g35)
    c: Equal(g35, g36-g40) x5
    c: PointOnObject(g35,g41)
    c: PointOnObject(g36,g41)
    c: PointOnObject(g37,g41)
    c: PointOnObject(g38,g41)
    c: PointOnObject(g39,g41)
    c: PointOnObject(g40,g41)
    c: Coincident(g42,g43)
    c: Coincident(g43,g44)
    c: Coincident(g44,g45)
    c: Coincident(g45,g46)
    c: Coincident(g46,g47)
    c: Coincident(g47,g42)
    c: Equal(g42, g43-g47) x5
    c: PointOnObject(g42,g48)
    c: PointOnObject(g43,g48)
    c: PointOnObject(g44,g48)
    c: PointOnObject(g45,g48)
    c: PointOnObject(g46,g48)
    c: PointOnObject(g47,g48)
    c: Equal(g41,g48)
    c: Diameter(g41) = 7
    c: Vertical(g39)
    c: Vertical(g43)
    c: Distance(g-2,g39) = 1
    c: Symmetric(g38,g43,g-2)
    c: Distance(g41,g-1) = 7
FEATURE [Part::Extrusion] Extrude473  label="hex088"
  Base = -> Sketch481
  Dir = (0,-1,2e-16)
  DirMode = 2
  FaceMakerClass = Part::FaceMakerBullseye
  FaceMakerMode = 3
  LengthFwd = 10
  LengthRev = 0
  Placement = pos=(68,0,-35) rot=(0,0,1;0rad)
  Solid = true
  Symmetric = false
FEATURE [Sketcher::SketchObject] Sketch482
  ArcFitTolerance = 1e-06
  FullyConstrained = true
  MakeInternals = false
  Placement = pos=(0,0,0) rot=(1,0,0;1.5708rad)
  sketch-geometry (49):
    g0: LineSegment StartX=1e-16 StartY=3.5 StartZ=0 EndX=-3.03109 EndY=1.75 EndZ=0
    g1: LineSegment StartX=-3.03109 StartY=1.75 StartZ=0 EndX=-3.03109 EndY=-1.75 EndZ=0
    g2: LineSegment StartX=-3.03109 StartY=-1.75 StartZ=0 EndX=-1e-16 EndY=-3.5 EndZ=0
    g3: LineSegment StartX=-1e-16 StartY=-3.5 StartZ=0 EndX=3.03109 EndY=-1.75 EndZ=0
    g4: LineSegment StartX=3.03109 StartY=-1.75 StartZ=0 EndX=3.03109 EndY=1.75 EndZ=0
    g5: LineSegment StartX=3.03109 StartY=1.75 StartZ=0 EndX=1e-16 EndY=3.5 EndZ=0
    g6: Circle [constr] CenterX=0 CenterY=0 CenterZ=0 NormalX=0 NormalY=0 NormalZ=1 AngleXU=0 Radius=3.5
    g7: LineSegment StartX=4.96892 StartY=-1.75002 StartZ=0 EndX=8.00002 EndY=-3.5 EndZ=0
    g8: LineSegment StartX=8.00002 StartY=-3.5 StartZ=0 EndX=11.0311 EndY=-1.74998 EndZ=0
    g9: LineSegment StartX=11.0311 StartY=-1.74998 StartZ=0 EndX=11.0311 EndY=1.75002 EndZ=0
    g10: LineSegment StartX=11.0311 StartY=1.75002 StartZ=0 EndX=7.99998 EndY=3.5 EndZ=0
    g11: LineSegment StartX=7.99998 StartY=3.5 StartZ=0 EndX=4.9689 EndY=1.74998 EndZ=0
    g12: LineSegment StartX=4.9689 StartY=1.74998 StartZ=0 EndX=4.96892 EndY=-1.75002 EndZ=0
    g13: Circle [constr] CenterX=8 CenterY=0 CenterZ=0 NormalX=0 NormalY=0 NormalZ=1 AngleXU=0 Radius=3.5
    g14: LineSegment StartX=4.03109 StartY=3.5 StartZ=0 EndX=7.06218 EndY=5.25 EndZ=0
    g15: LineSegment StartX=7.06218 StartY=5.25 StartZ=0 EndX=7.06218 EndY=8.75 EndZ=0
    g16: LineSegment StartX=7.06218 StartY=8.75 StartZ=0 EndX=4.03109 EndY=10.5 EndZ=0
    g17: LineSegment StartX=4.03109 StartY=10.5 StartZ=0 EndX=1 EndY=8.75 EndZ=0
    g18: LineSegment StartX=1 StartY=8.75 StartZ=0 EndX=1 EndY=5.25 EndZ=0
    g19: LineSegment StartX=1 StartY=5.25 StartZ=0 EndX=4.03109 EndY=3.5 EndZ=0
    g20: Circle [constr] CenterX=4.03109 CenterY=7 CenterZ=0 NormalX=0 NormalY=0 NormalZ=1 AngleXU=0 Radius=3.5
    g21: LineSegment StartX=-1 StartY=5.25 StartZ=0 EndX=-1 EndY=8.75 EndZ=0
    g22: LineSegment StartX=-1 StartY=8.75 StartZ=0 EndX=-4.03109 EndY=10.5 EndZ=0
    g23: LineSegment StartX=-4.03109 StartY=10.5 StartZ=0 EndX=-7.06218 EndY=8.75 EndZ=0
    g24: LineSegment StartX=-7.06218 StartY=8.75 StartZ=0 EndX=-7.06218 EndY=5.25 EndZ=0
    g25: LineSegment StartX=-7.06218 StartY=5.25 StartZ=0 EndX=-4.03109 EndY=3.5 EndZ=0
    g26: LineSegment StartX=-4.03109 StartY=3.5 StartZ=0 EndX=-1 EndY=5.25 EndZ=0
    g27: Circle [constr] CenterX=-4.03109 CenterY=7 CenterZ=0 NormalX=0 NormalY=0 NormalZ=1 AngleXU=0 Radius=3.5
    g28: LineSegment StartX=-4.96891 StartY=-1.75 StartZ=0 EndX=-4.96891 EndY=1.75 EndZ=0
    g29: LineSegment StartX=-4.96891 StartY=1.75 StartZ=0 EndX=-8 EndY=3.5 EndZ=0
    g30: LineSegment StartX=-8 StartY=3.5 StartZ=0 EndX=-11.0311 EndY=1.75 EndZ=0
    g31: LineSegment StartX=-11.0311 StartY=1.75 StartZ=0 EndX=-11.0311 EndY=-1.75 EndZ=0
    g32: LineSegment StartX=-11.0311 StartY=-1.75 StartZ=0 EndX=-8 EndY=-3.5 EndZ=0
    g33: LineSegment StartX=-8 StartY=-3.5 StartZ=0 EndX=-4.96891 EndY=-1.75 EndZ=0
    g34: Circle [constr] CenterX=-8 CenterY=0 CenterZ=0 NormalX=0 NormalY=0 NormalZ=1 AngleXU=0 Radius=3.5
    g35: LineSegment StartX=-4.03109 StartY=-3.5 StartZ=0 EndX=-7.06218 EndY=-5.25 EndZ=0
    g36: LineSegment StartX=-7.06218 StartY=-5.25 StartZ=0 EndX=-7.06218 EndY=-8.75 EndZ=0
    g37: LineSegment StartX=-7.06218 StartY=-8.75 StartZ=0 EndX=-4.03109 EndY=-10.5 EndZ=0
    g38: LineSegment StartX=-4.03109 StartY=-10.5 StartZ=0 EndX=-1 EndY=-8.75 EndZ=0
    g39: LineSegment StartX=-1 StartY=-8.75 StartZ=0 EndX=-1 EndY=-5.25 EndZ=0
    g40: LineSegment StartX=-1 StartY=-5.25 StartZ=0 EndX=-4.03109 EndY=-3.5 EndZ=0
    g41: Circle [constr] CenterX=-4.03109 CenterY=-7 CenterZ=0 NormalX=0 NormalY=0 NormalZ=1 AngleXU=0 Radius=3.5
    g42: LineSegment StartX=4.03109 StartY=-3.5 StartZ=0 EndX=1 EndY=-5.25 EndZ=0
    g43: LineSegment StartX=1 StartY=-5.25 StartZ=0 EndX=1 EndY=-8.75 EndZ=0
    g44: LineSegment StartX=1 StartY=-8.75 StartZ=0 EndX=4.03109 EndY=-10.5 EndZ=0
    g45: LineSegment StartX=4.03109 StartY=-10.5 StartZ=0 EndX=7.06218 EndY=-8.75 EndZ=0
    g46: LineSegment StartX=7.06218 StartY=-8.75 StartZ=0 EndX=7.06218 EndY=-5.25 EndZ=0
    g47: LineSegment StartX=7.06218 StartY=-5.25 StartZ=0 EndX=4.03109 EndY=-3.5 EndZ=0
    g48: Circle [constr] CenterX=4.03109 CenterY=-7 CenterZ=0 NormalX=0 NormalY=0 NormalZ=1 AngleXU=0 Radius=3.5
  constraints (117):
    c: Coincident(g0,g1)
    c: Coincident(g1,g2)
    c: Coincident(g2,g3)
    c: Coincident(g3,g4)
    c: Coincident(g4,g5)
    c: Coincident(g5,g0)
    c: Equal(g0, g1-g5) x5
    c: PointOnObject(g0,g6)
    c: PointOnObject(g1,g6)
    c: PointOnObject(g2,g6)
    c: PointOnObject(g3,g6)
    c: PointOnObject(g4,g6)
    c: PointOnObject(g5,g6)
    c: Coincident(g6,g-1)
    c: Diameter(g6) = 7
    c: PointOnObject(g0,g-2)
    c: Coincident(g7,g8)
    c: Coincident(g8,g9)
    c: Coincident(g9,g10)
    c: Coincident(g10,g11)
    c: Coincident(g11,g12)
    c: Coincident(g12,g7)
    c: Equal(g7, g8-g12) x5
    c: PointOnObject(g7,g13)
    c: PointOnObject(g8,g13)
    c: PointOnObject(g9,g13)
    c: PointOnObject(g10,g13)
    c: PointOnObject(g11,g13)
    c: PointOnObject(g12,g13)
    c: PointOnObject(g13,g-1)
    c: Diameter(g13) = 7
    c: Distance(g6,g13) = 8
    c: Horizontal(g0,g10)
    c: Coincident(g14,g15)
    c: Coincident(g15,g16)
    c: Coincident(g16,g17)
    c: Coincident(g17,g18)
    c: Coincident(g18,g19)
    c: Coincident(g19,g14)
    c: Equal(g14, g15-g19) x5
    c: PointOnObject(g14,g20)
    c: PointOnObject(g15,g20)
    c: PointOnObject(g16,g20)
    c: PointOnObject(g17,g20)
    c: PointOnObject(g18,g20)
    c: PointOnObject(g19,g20)
    c: Diameter(g20) = 7
    c: DistanceY(g-1,g20) = 7
    c: Vertical(g18)
    c: Distance(g17,g-2) = 1
    c: Coincident(g21,g22)
    c: Coincident(g22,g23)
    c: Coincident(g23,g24)
    c: Coincident(g24,g25)
    c: Coincident(g25,g26)
    c: Coincident(g26,g21)
    c: Equal(g21, g22-g26) x5
    c: PointOnObject(g21,g27)
    c: PointOnObject(g22,g27)
    c: PointOnObject(g23,g27)
    c: PointOnObject(g24,g27)
    c: PointOnObject(g25,g27)
    c: PointOnObject(g26,g27)
    c: Diameter(g27) = 7
    c: DistanceY(g-1,g27) = 7
    c: DistanceX(g21,g-1) = 1
    c: Vertical(g21)
    c: Coincident(g28,g29)
    c: Coincident(g29,g30)
    c: Coincident(g30,g31)
    c: Coincident(g31,g32)
    c: Coincident(g32,g33)
    c: Coincident(g33,g28)
    c: Equal(g28, g29-g33) x5
    c: PointOnObject(g28,g34)
    c: PointOnObject(g29,g34)
    c: PointOnObject(g30,g34)
    c: PointOnObject(g31,g34)
    c: PointOnObject(g32,g34)
    c: PointOnObject(g33,g34)
    c: PointOnObject(g34,g-1)
    c: Diameter(g34) = 7
    c: Vertical(g31)
    c: DistanceX(g34,g-1) = 8
    c: Coincident(g35,g36)
    c: Coincident(g36,g37)
    c: Coincident(g37,g38)
    c: Coincident(g38,g39)
    c: Coincident(g39,g40)
    c: Coincident(g40,g35)
    c: Equal(g35, g36-g40) x5
    c: PointOnObject(g35,g41)
    c: PointOnObject(g36,g41)
    c: PointOnObject(g37,g41)
    c: PointOnObject(g38,g41)
    c: PointOnObject(g39,g41)
    c: PointOnObject(g40,g41)
    c: Coincident(g42,g43)
    c: Coincident(g43,g44)
    c: Coincident(g44,g45)
    c: Coincident(g45,g46)
    c: Coincident(g46,g47)
    c: Coincident(g47,g42)
    c: Equal(g42, g43-g47) x5
    c: PointOnObject(g42,g48)
    c: PointOnObject(g43,g48)
    c: PointOnObject(g44,g48)
    c: PointOnObject(g45,g48)
    c: PointOnObject(g46,g48)
    c: PointOnObject(g47,g48)
    c: Equal(g41,g48)
    c: Diameter(g41) = 7
    c: Vertical(g39)
    c: Vertical(g43)
    c: Distance(g-2,g39) = 1
    c: Symmetric(g38,g43,g-2)
    c: Distance(g41,g-1) = 7
FEATURE [Part::Extrusion] Extrude474  label="hex089"
  Base = -> Sketch482
  Dir = (0,-1,2e-16)
  DirMode = 2
  FaceMakerClass = Part::FaceMakerBullseye
  FaceMakerMode = 3
  LengthFwd = 10
  LengthRev = 0
  Placement = pos=(72,0,-14) rot=(0,0,1;0rad)
  Solid = true
  Symmetric = false
FEATURE [Sketcher::SketchObject] Sketch483
  ArcFitTolerance = 1e-06
  FullyConstrained = true
  MakeInternals = false
  Placement = pos=(0,0,0) rot=(1,0,0;1.5708rad)
  sketch-geometry (49):
    g0: LineSegment StartX=1e-16 StartY=3.5 StartZ=0 EndX=-3.03109 EndY=1.75 EndZ=0
    g1: LineSegment StartX=-3.03109 StartY=1.75 StartZ=0 EndX=-3.03109 EndY=-1.75 EndZ=0
    g2: LineSegment StartX=-3.03109 StartY=-1.75 StartZ=0 EndX=-1e-16 EndY=-3.5 EndZ=0
    g3: LineSegment StartX=-1e-16 StartY=-3.5 StartZ=0 EndX=3.03109 EndY=-1.75 EndZ=0
    g4: LineSegment StartX=3.03109 StartY=-1.75 StartZ=0 EndX=3.03109 EndY=1.75 EndZ=0
    g5: LineSegment StartX=3.03109 StartY=1.75 StartZ=0 EndX=1e-16 EndY=3.5 EndZ=0
    g6: Circle [constr] CenterX=0 CenterY=0 CenterZ=0 NormalX=0 NormalY=0 NormalZ=1 AngleXU=0 Radius=3.5
    g7: LineSegment StartX=4.96892 StartY=-1.75002 StartZ=0 EndX=8.00002 EndY=-3.5 EndZ=0
    g8: LineSegment StartX=8.00002 StartY=-3.5 StartZ=0 EndX=11.0311 EndY=-1.74998 EndZ=0
    g9: LineSegment StartX=11.0311 StartY=-1.74998 StartZ=0 EndX=11.0311 EndY=1.75002 EndZ=0
    g10: LineSegment StartX=11.0311 StartY=1.75002 StartZ=0 EndX=7.99998 EndY=3.5 EndZ=0
    g11: LineSegment StartX=7.99998 StartY=3.5 StartZ=0 EndX=4.9689 EndY=1.74998 EndZ=0
    g12: LineSegment StartX=4.9689 StartY=1.74998 StartZ=0 EndX=4.96892 EndY=-1.75002 EndZ=0
    g13: Circle [constr] CenterX=8 CenterY=0 CenterZ=0 NormalX=0 NormalY=0 NormalZ=1 AngleXU=0 Radius=3.5
    g14: LineSegment StartX=4.03109 StartY=3.5 StartZ=0 EndX=7.06218 EndY=5.25 EndZ=0
    g15: LineSegment StartX=7.06218 StartY=5.25 StartZ=0 EndX=7.06218 EndY=8.75 EndZ=0
    g16: LineSegment StartX=7.06218 StartY=8.75 StartZ=0 EndX=4.03109 EndY=10.5 EndZ=0
    g17: LineSegment StartX=4.03109 StartY=10.5 StartZ=0 EndX=1 EndY=8.75 EndZ=0
    g18: LineSegment StartX=1 StartY=8.75 StartZ=0 EndX=1 EndY=5.25 EndZ=0
    g19: LineSegment StartX=1 StartY=5.25 StartZ=0 EndX=4.03109 EndY=3.5 EndZ=0
    g20: Circle [constr] CenterX=4.03109 CenterY=7 CenterZ=0 NormalX=0 NormalY=0 NormalZ=1 AngleXU=0 Radius=3.5
    g21: LineSegment StartX=-1 StartY=5.25 StartZ=0 EndX=-1 EndY=8.75 EndZ=0
    g22: LineSegment StartX=-1 StartY=8.75 StartZ=0 EndX=-4.03109 EndY=10.5 EndZ=0
    g23: LineSegment StartX=-4.03109 StartY=10.5 StartZ=0 EndX=-7.06218 EndY=8.75 EndZ=0
    g24: LineSegment StartX=-7.06218 StartY=8.75 StartZ=0 EndX=-7.06218 EndY=5.25 EndZ=0
    g25: LineSegment StartX=-7.06218 StartY=5.25 StartZ=0 EndX=-4.03109 EndY=3.5 EndZ=0
    g26: LineSegment StartX=-4.03109 StartY=3.5 StartZ=0 EndX=-1 EndY=5.25 EndZ=0
    g27: Circle [constr] CenterX=-4.03109 CenterY=7 CenterZ=0 NormalX=0 NormalY=0 NormalZ=1 AngleXU=0 Radius=3.5
    g28: LineSegment StartX=-4.96891 StartY=-1.75 StartZ=0 EndX=-4.96891 EndY=1.75 EndZ=0
    g29: LineSegment StartX=-4.96891 StartY=1.75 StartZ=0 EndX=-8 EndY=3.5 EndZ=0
    g30: LineSegment StartX=-8 StartY=3.5 StartZ=0 EndX=-11.0311 EndY=1.75 EndZ=0
    g31: LineSegment StartX=-11.0311 StartY=1.75 StartZ=0 EndX=-11.0311 EndY=-1.75 EndZ=0
    g32: LineSegment StartX=-11.0311 StartY=-1.75 StartZ=0 EndX=-8 EndY=-3.5 EndZ=0
    g33: LineSegment StartX=-8 StartY=-3.5 StartZ=0 EndX=-4.96891 EndY=-1.75 EndZ=0
    g34: Circle [constr] CenterX=-8 CenterY=0 CenterZ=0 NormalX=0 NormalY=0 NormalZ=1 AngleXU=0 Radius=3.5
    g35: LineSegment StartX=-4.03109 StartY=-3.5 StartZ=0 EndX=-7.06218 EndY=-5.25 EndZ=0
    g36: LineSegment StartX=-7.06218 StartY=-5.25 StartZ=0 EndX=-7.06218 EndY=-8.75 EndZ=0
    g37: LineSegment StartX=-7.06218 StartY=-8.75 StartZ=0 EndX=-4.03109 EndY=-10.5 EndZ=0
    g38: LineSegment StartX=-4.03109 StartY=-10.5 StartZ=0 EndX=-1 EndY=-8.75 EndZ=0
    g39: LineSegment StartX=-1 StartY=-8.75 StartZ=0 EndX=-1 EndY=-5.25 EndZ=0
    g40: LineSegment StartX=-1 StartY=-5.25 StartZ=0 EndX=-4.03109 EndY=-3.5 EndZ=0
    g41: Circle [constr] CenterX=-4.03109 CenterY=-7 CenterZ=0 NormalX=0 NormalY=0 NormalZ=1 AngleXU=0 Radius=3.5
    g42: LineSegment StartX=4.03109 StartY=-3.5 StartZ=0 EndX=1 EndY=-5.25 EndZ=0
    g43: LineSegment StartX=1 StartY=-5.25 StartZ=0 EndX=1 EndY=-8.75 EndZ=0
    g44: LineSegment StartX=1 StartY=-8.75 StartZ=0 EndX=4.03109 EndY=-10.5 EndZ=0
    g45: LineSegment StartX=4.03109 StartY=-10.5 StartZ=0 EndX=7.06218 EndY=-8.75 EndZ=0
    g46: LineSegment StartX=7.06218 StartY=-8.75 StartZ=0 EndX=7.06218 EndY=-5.25 EndZ=0
    g47: LineSegment StartX=7.06218 StartY=-5.25 StartZ=0 EndX=4.03109 EndY=-3.5 EndZ=0
    g48: Circle [constr] CenterX=4.03109 CenterY=-7 CenterZ=0 NormalX=0 NormalY=0 NormalZ=1 AngleXU=0 Radius=3.5
  constraints (117):
    c: Coincident(g0,g1)
    c: Coincident(g1,g2)
    c: Coincident(g2,g3)
    c: Coincident(g3,g4)
    c: Coincident(g4,g5)
    c: Coincident(g5,g0)
    c: Equal(g0, g1-g5) x5
    c: PointOnObject(g0,g6)
    c: PointOnObject(g1,g6)
    c: PointOnObject(g2,g6)
    c: PointOnObject(g3,g6)
    c: PointOnObject(g4,g6)
    c: PointOnObject(g5,g6)
    c: Coincident(g6,g-1)
    c: Diameter(g6) = 7
    c: PointOnObject(g0,g-2)
    c: Coincident(g7,g8)
    c: Coincident(g8,g9)
    c: Coincident(g9,g10)
    c: Coincident(g10,g11)
    c: Coincident(g11,g12)
    c: Coincident(g12,g7)
    c: Equal(g7, g8-g12) x5
    c: PointOnObject(g7,g13)
    c: PointOnObject(g8,g13)
    c: PointOnObject(g9,g13)
    c: PointOnObject(g10,g13)
    c: PointOnObject(g11,g13)
    c: PointOnObject(g12,g13)
    c: PointOnObject(g13,g-1)
    c: Diameter(g13) = 7
    c: Distance(g6,g13) = 8
    c: Horizontal(g0,g10)
    c: Coincident(g14,g15)
    c: Coincident(g15,g16)
    c: Coincident(g16,g17)
    c: Coincident(g17,g18)
    c: Coincident(g18,g19)
    c: Coincident(g19,g14)
    c: Equal(g14, g15-g19) x5
    c: PointOnObject(g14,g20)
    c: PointOnObject(g15,g20)
    c: PointOnObject(g16,g20)
    c: PointOnObject(g17,g20)
    c: PointOnObject(g18,g20)
    c: PointOnObject(g19,g20)
    c: Diameter(g20) = 7
    c: DistanceY(g-1,g20) = 7
    c: Vertical(g18)
    c: Distance(g17,g-2) = 1
    c: Coincident(g21,g22)
    c: Coincident(g22,g23)
    c: Coincident(g23,g24)
    c: Coincident(g24,g25)
    c: Coincident(g25,g26)
    c: Coincident(g26,g21)
    c: Equal(g21, g22-g26) x5
    c: PointOnObject(g21,g27)
    c: PointOnObject(g22,g27)
    c: PointOnObject(g23,g27)
    c: PointOnObject(g24,g27)
    c: PointOnObject(g25,g27)
    c: PointOnObject(g26,g27)
    c: Diameter(g27) = 7
    c: DistanceY(g-1,g27) = 7
    c: DistanceX(g21,g-1) = 1
    c: Vertical(g21)
    c: Coincident(g28,g29)
    c: Coincident(g29,g30)
    c: Coincident(g30,g31)
    c: Coincident(g31,g32)
    c: Coincident(g32,g33)
    c: Coincident(g33,g28)
    c: Equal(g28, g29-g33) x5
    c: PointOnObject(g28,g34)
    c: PointOnObject(g29,g34)
    c: PointOnObject(g30,g34)
    c: PointOnObject(g31,g34)
    c: PointOnObject(g32,g34)
    c: PointOnObject(g33,g34)
    c: PointOnObject(g34,g-1)
    c: Diameter(g34) = 7
    c: Vertical(g31)
    c: DistanceX(g34,g-1) = 8
    c: Coincident(g35,g36)
    c: Coincident(g36,g37)
    c: Coincident(g37,g38)
    c: Coincident(g38,g39)
    c: Coincident(g39,g40)
    c: Coincident(g40,g35)
    c: Equal(g35, g36-g40) x5
    c: PointOnObject(g35,g41)
    c: PointOnObject(g36,g41)
    c: PointOnObject(g37,g41)
    c: PointOnObject(g38,g41)
    c: PointOnObject(g39,g41)
    c: PointOnObject(g40,g41)
    c: Coincident(g42,g43)
    c: Coincident(g43,g44)
    c: Coincident(g44,g45)
    c: Coincident(g45,g46)
    c: Coincident(g46,g47)
    c: Coincident(g47,g42)
    c: Equal(g42, g43-g47) x5
    c: PointOnObject(g42,g48)
    c: PointOnObject(g43,g48)
    c: PointOnObject(g44,g48)
    c: PointOnObject(g45,g48)
    c: PointOnObject(g46,g48)
    c: PointOnObject(g47,g48)
    c: Equal(g41,g48)
    c: Diameter(g41) = 7
    c: Vertical(g39)
    c: Vertical(g43)
    c: Distance(g-2,g39) = 1
    c: Symmetric(g38,g43,g-2)
    c: Distance(g41,g-1) = 7
FEATURE [Part::Extrusion] Extrude475  label="hex090"
  Base = -> Sketch483
  Dir = (0,-1,2e-16)
  DirMode = 2
  FaceMakerClass = Part::FaceMakerBullseye
  FaceMakerMode = 3
  LengthFwd = 10
  LengthRev = 0
  Placement = pos=(72,0,14) rot=(0,0,1;0rad)
  Solid = true
  Symmetric = false
FEATURE [Sketcher::SketchObject] Sketch484
  ArcFitTolerance = 1e-06
  FullyConstrained = true
  MakeInternals = false
  Placement = pos=(0,0,0) rot=(1,0,0;1.5708rad)
  sketch-geometry (49):
    g0: LineSegment StartX=1e-16 StartY=3.5 StartZ=0 EndX=-3.03109 EndY=1.75 EndZ=0
    g1: LineSegment StartX=-3.03109 StartY=1.75 StartZ=0 EndX=-3.03109 EndY=-1.75 EndZ=0
    g2: LineSegment StartX=-3.03109 StartY=-1.75 StartZ=0 EndX=-1e-16 EndY=-3.5 EndZ=0
    g3: LineSegment StartX=-1e-16 StartY=-3.5 StartZ=0 EndX=3.03109 EndY=-1.75 EndZ=0
    g4: LineSegment StartX=3.03109 StartY=-1.75 StartZ=0 EndX=3.03109 EndY=1.75 EndZ=0
    g5: LineSegment StartX=3.03109 StartY=1.75 StartZ=0 EndX=1e-16 EndY=3.5 EndZ=0
    g6: Circle [constr] CenterX=0 CenterY=0 CenterZ=0 NormalX=0 NormalY=0 NormalZ=1 AngleXU=0 Radius=3.5
    g7: LineSegment StartX=4.96892 StartY=-1.75002 StartZ=0 EndX=8.00002 EndY=-3.5 EndZ=0
    g8: LineSegment StartX=8.00002 StartY=-3.5 StartZ=0 EndX=11.0311 EndY=-1.74998 EndZ=0
    g9: LineSegment StartX=11.0311 StartY=-1.74998 StartZ=0 EndX=11.0311 EndY=1.75002 EndZ=0
    g10: LineSegment StartX=11.0311 StartY=1.75002 StartZ=0 EndX=7.99998 EndY=3.5 EndZ=0
    g11: LineSegment StartX=7.99998 StartY=3.5 StartZ=0 EndX=4.9689 EndY=1.74998 EndZ=0
    g12: LineSegment StartX=4.9689 StartY=1.74998 StartZ=0 EndX=4.96892 EndY=-1.75002 EndZ=0
    g13: Circle [constr] CenterX=8 CenterY=0 CenterZ=0 NormalX=0 NormalY=0 NormalZ=1 AngleXU=0 Radius=3.5
    g14: LineSegment StartX=4.03109 StartY=3.5 StartZ=0 EndX=7.06218 EndY=5.25 EndZ=0
    g15: LineSegment StartX=7.06218 StartY=5.25 StartZ=0 EndX=7.06218 EndY=8.75 EndZ=0
    g16: LineSegment StartX=7.06218 StartY=8.75 StartZ=0 EndX=4.03109 EndY=10.5 EndZ=0
    g17: LineSegment StartX=4.03109 StartY=10.5 StartZ=0 EndX=1 EndY=8.75 EndZ=0
    g18: LineSegment StartX=1 StartY=8.75 StartZ=0 EndX=1 EndY=5.25 EndZ=0
    g19: LineSegment StartX=1 StartY=5.25 StartZ=0 EndX=4.03109 EndY=3.5 EndZ=0
    g20: Circle [constr] CenterX=4.03109 CenterY=7 CenterZ=0 NormalX=0 NormalY=0 NormalZ=1 AngleXU=0 Radius=3.5
    g21: LineSegment StartX=-1 StartY=5.25 StartZ=0 EndX=-1 EndY=8.75 EndZ=0
    g22: LineSegment StartX=-1 StartY=8.75 StartZ=0 EndX=-4.03109 EndY=10.5 EndZ=0
    g23: LineSegment StartX=-4.03109 StartY=10.5 StartZ=0 EndX=-7.06218 EndY=8.75 EndZ=0
    g24: LineSegment StartX=-7.06218 StartY=8.75 StartZ=0 EndX=-7.06218 EndY=5.25 EndZ=0
    g25: LineSegment StartX=-7.06218 StartY=5.25 StartZ=0 EndX=-4.03109 EndY=3.5 EndZ=0
    g26: LineSegment StartX=-4.03109 StartY=3.5 StartZ=0 EndX=-1 EndY=5.25 EndZ=0
    g27: Circle [constr] CenterX=-4.03109 CenterY=7 CenterZ=0 NormalX=0 NormalY=0 NormalZ=1 AngleXU=0 Radius=3.5
    g28: LineSegment StartX=-4.96891 StartY=-1.75 StartZ=0 EndX=-4.96891 EndY=1.75 EndZ=0
    g29: LineSegment StartX=-4.96891 StartY=1.75 StartZ=0 EndX=-8 EndY=3.5 EndZ=0
    g30: LineSegment StartX=-8 StartY=3.5 StartZ=0 EndX=-11.0311 EndY=1.75 EndZ=0
    g31: LineSegment StartX=-11.0311 StartY=1.75 StartZ=0 EndX=-11.0311 EndY=-1.75 EndZ=0
    g32: LineSegment StartX=-11.0311 StartY=-1.75 StartZ=0 EndX=-8 EndY=-3.5 EndZ=0
    g33: LineSegment StartX=-8 StartY=-3.5 StartZ=0 EndX=-4.96891 EndY=-1.75 EndZ=0
    g34: Circle [constr] CenterX=-8 CenterY=0 CenterZ=0 NormalX=0 NormalY=0 NormalZ=1 AngleXU=0 Radius=3.5
    g35: LineSegment StartX=-4.03109 StartY=-3.5 StartZ=0 EndX=-7.06218 EndY=-5.25 EndZ=0
    g36: LineSegment StartX=-7.06218 StartY=-5.25 StartZ=0 EndX=-7.06218 EndY=-8.75 EndZ=0
    g37: LineSegment StartX=-7.06218 StartY=-8.75 StartZ=0 EndX=-4.03109 EndY=-10.5 EndZ=0
    g38: LineSegment StartX=-4.03109 StartY=-10.5 StartZ=0 EndX=-1 EndY=-8.75 EndZ=0
    g39: LineSegment StartX=-1 StartY=-8.75 StartZ=0 EndX=-1 EndY=-5.25 EndZ=0
    g40: LineSegment StartX=-1 StartY=-5.25 StartZ=0 EndX=-4.03109 EndY=-3.5 EndZ=0
    g41: Circle [constr] CenterX=-4.03109 CenterY=-7 CenterZ=0 NormalX=0 NormalY=0 NormalZ=1 AngleXU=0 Radius=3.5
    g42: LineSegment StartX=4.03109 StartY=-3.5 StartZ=0 EndX=1 EndY=-5.25 EndZ=0
    g43: LineSegment StartX=1 StartY=-5.25 StartZ=0 EndX=1 EndY=-8.75 EndZ=0
    g44: LineSegment StartX=1 StartY=-8.75 StartZ=0 EndX=4.03109 EndY=-10.5 EndZ=0
    g45: LineSegment StartX=4.03109 StartY=-10.5 StartZ=0 EndX=7.06218 EndY=-8.75 EndZ=0
    g46: LineSegment StartX=7.06218 StartY=-8.75 StartZ=0 EndX=7.06218 EndY=-5.25 EndZ=0
    g47: LineSegment StartX=7.06218 StartY=-5.25 StartZ=0 EndX=4.03109 EndY=-3.5 EndZ=0
    g48: Circle [constr] CenterX=4.03109 CenterY=-7 CenterZ=0 NormalX=0 NormalY=0 NormalZ=1 AngleXU=0 Radius=3.5
  constraints (117):
    c: Coincident(g0,g1)
    c: Coincident(g1,g2)
    c: Coincident(g2,g3)
    c: Coincident(g3,g4)
    c: Coincident(g4,g5)
    c: Coincident(g5,g0)
    c: Equal(g0, g1-g5) x5
    c: PointOnObject(g0,g6)
    c: PointOnObject(g1,g6)
    c: PointOnObject(g2,g6)
    c: PointOnObject(g3,g6)
    c: PointOnObject(g4,g6)
    c: PointOnObject(g5,g6)
    c: Coincident(g6,g-1)
    c: Diameter(g6) = 7
    c: PointOnObject(g0,g-2)
    c: Coincident(g7,g8)
    c: Coincident(g8,g9)
    c: Coincident(g9,g10)
    c: Coincident(g10,g11)
    c: Coincident(g11,g12)
    c: Coincident(g12,g7)
    c: Equal(g7, g8-g12) x5
    c: PointOnObject(g7,g13)
    c: PointOnObject(g8,g13)
    c: PointOnObject(g9,g13)
    c: PointOnObject(g10,g13)
    c: PointOnObject(g11,g13)
    c: PointOnObject(g12,g13)
    c: PointOnObject(g13,g-1)
    c: Diameter(g13) = 7
    c: Distance(g6,g13) = 8
    c: Horizontal(g0,g10)
    c: Coincident(g14,g15)
    c: Coincident(g15,g16)
    c: Coincident(g16,g17)
    c: Coincident(g17,g18)
    c: Coincident(g18,g19)
    c: Coincident(g19,g14)
    c: Equal(g14, g15-g19) x5
    c: PointOnObject(g14,g20)
    c: PointOnObject(g15,g20)
    c: PointOnObject(g16,g20)
    c: PointOnObject(g17,g20)
    c: PointOnObject(g18,g20)
    c: PointOnObject(g19,g20)
    c: Diameter(g20) = 7
    c: DistanceY(g-1,g20) = 7
    c: Vertical(g18)
    c: Distance(g17,g-2) = 1
    c: Coincident(g21,g22)
    c: Coincident(g22,g23)
    c: Coincident(g23,g24)
    c: Coincident(g24,g25)
    c: Coincident(g25,g26)
    c: Coincident(g26,g21)
    c: Equal(g21, g22-g26) x5
    c: PointOnObject(g21,g27)
    c: PointOnObject(g22,g27)
    c: PointOnObject(g23,g27)
    c: PointOnObject(g24,g27)
    c: PointOnObject(g25,g27)
    c: PointOnObject(g26,g27)
    c: Diameter(g27) = 7
    c: DistanceY(g-1,g27) = 7
    c: DistanceX(g21,g-1) = 1
    c: Vertical(g21)
    c: Coincident(g28,g29)
    c: Coincident(g29,g30)
    c: Coincident(g30,g31)
    c: Coincident(g31,g32)
    c: Coincident(g32,g33)
    c: Coincident(g33,g28)
    c: Equal(g28, g29-g33) x5
    c: PointOnObject(g28,g34)
    c: PointOnObject(g29,g34)
    c: PointOnObject(g30,g34)
    c: PointOnObject(g31,g34)
    c: PointOnObject(g32,g34)
    c: PointOnObject(g33,g34)
    c: PointOnObject(g34,g-1)
    c: Diameter(g34) = 7
    c: Vertical(g31)
    c: DistanceX(g34,g-1) = 8
    c: Coincident(g35,g36)
    c: Coincident(g36,g37)
    c: Coincident(g37,g38)
    c: Coincident(g38,g39)
    c: Coincident(g39,g40)
    c: Coincident(g40,g35)
    c: Equal(g35, g36-g40) x5
    c: PointOnObject(g35,g41)
    c: PointOnObject(g36,g41)
    c: PointOnObject(g37,g41)
    c: PointOnObject(g38,g41)
    c: PointOnObject(g39,g41)
    c: PointOnObject(g40,g41)
    c: Coincident(g42,g43)
    c: Coincident(g43,g44)
    c: Coincident(g44,g45)
    c: Coincident(g45,g46)
    c: Coincident(g46,g47)
    c: Coincident(g47,g42)
    c: Equal(g42, g43-g47) x5
    c: PointOnObject(g42,g48)
    c: PointOnObject(g43,g48)
    c: PointOnObject(g44,g48)
    c: PointOnObject(g45,g48)
    c: PointOnObject(g46,g48)
    c: PointOnObject(g47,g48)
    c: Equal(g41,g48)
    c: Diameter(g41) = 7
    c: Vertical(g39)
    c: Vertical(g43)
    c: Distance(g-2,g39) = 1
    c: Symmetric(g38,g43,g-2)
    c: Distance(g41,g-1) = 7
FEATURE [Part::Extrusion] Extrude476  label="hex091"
  Base = -> Sketch484
  Dir = (0,-1,2e-16)
  DirMode = 2
  FaceMakerClass = Part::FaceMakerBullseye
  FaceMakerMode = 3
  LengthFwd = 10
  LengthRev = 0
  Placement = pos=(80,0,0) rot=(0,0,1;0rad)
  Solid = true
  Symmetric = false
FEATURE [Sketcher::SketchObject] Sketch485
  ArcFitTolerance = 1e-06
  FullyConstrained = true
  MakeInternals = false
  Placement = pos=(0,0,0) rot=(1,0,0;1.5708rad)
  sketch-geometry (49):
    g0: LineSegment StartX=1e-16 StartY=3.5 StartZ=0 EndX=-3.03109 EndY=1.75 EndZ=0
    g1: LineSegment StartX=-3.03109 StartY=1.75 StartZ=0 EndX=-3.03109 EndY=-1.75 EndZ=0
    g2: LineSegment StartX=-3.03109 StartY=-1.75 StartZ=0 EndX=-1e-16 EndY=-3.5 EndZ=0
    g3: LineSegment StartX=-1e-16 StartY=-3.5 StartZ=0 EndX=3.03109 EndY=-1.75 EndZ=0
    g4: LineSegment StartX=3.03109 StartY=-1.75 StartZ=0 EndX=3.03109 EndY=1.75 EndZ=0
    g5: LineSegment StartX=3.03109 StartY=1.75 StartZ=0 EndX=1e-16 EndY=3.5 EndZ=0
    g6: Circle [constr] CenterX=0 CenterY=0 CenterZ=0 NormalX=0 NormalY=0 NormalZ=1 AngleXU=0 Radius=3.5
    g7: LineSegment StartX=4.96892 StartY=-1.75002 StartZ=0 EndX=8.00002 EndY=-3.5 EndZ=0
    g8: LineSegment StartX=8.00002 StartY=-3.5 StartZ=0 EndX=11.0311 EndY=-1.74998 EndZ=0
    g9: LineSegment StartX=11.0311 StartY=-1.74998 StartZ=0 EndX=11.0311 EndY=1.75002 EndZ=0
    g10: LineSegment StartX=11.0311 StartY=1.75002 StartZ=0 EndX=7.99998 EndY=3.5 EndZ=0
    g11: LineSegment StartX=7.99998 StartY=3.5 StartZ=0 EndX=4.9689 EndY=1.74998 EndZ=0
    g12: LineSegment StartX=4.9689 StartY=1.74998 StartZ=0 EndX=4.96892 EndY=-1.75002 EndZ=0
    g13: Circle [constr] CenterX=8 CenterY=0 CenterZ=0 NormalX=0 NormalY=0 NormalZ=1 AngleXU=0 Radius=3.5
    g14: LineSegment StartX=4.03109 StartY=3.5 StartZ=0 EndX=7.06218 EndY=5.25 EndZ=0
    g15: LineSegment StartX=7.06218 StartY=5.25 StartZ=0 EndX=7.06218 EndY=8.75 EndZ=0
    g16: LineSegment StartX=7.06218 StartY=8.75 StartZ=0 EndX=4.03109 EndY=10.5 EndZ=0
    g17: LineSegment StartX=4.03109 StartY=10.5 StartZ=0 EndX=1 EndY=8.75 EndZ=0
    g18: LineSegment StartX=1 StartY=8.75 StartZ=0 EndX=1 EndY=5.25 EndZ=0
    g19: LineSegment StartX=1 StartY=5.25 StartZ=0 EndX=4.03109 EndY=3.5 EndZ=0
    g20: Circle [constr] CenterX=4.03109 CenterY=7 CenterZ=0 NormalX=0 NormalY=0 NormalZ=1 AngleXU=0 Radius=3.5
    g21: LineSegment StartX=-1 StartY=5.25 StartZ=0 EndX=-1 EndY=8.75 EndZ=0
    g22: LineSegment StartX=-1 StartY=8.75 StartZ=0 EndX=-4.03109 EndY=10.5 EndZ=0
    g23: LineSegment StartX=-4.03109 StartY=10.5 StartZ=0 EndX=-7.06218 EndY=8.75 EndZ=0
    g24: LineSegment StartX=-7.06218 StartY=8.75 StartZ=0 EndX=-7.06218 EndY=5.25 EndZ=0
    g25: LineSegment StartX=-7.06218 StartY=5.25 StartZ=0 EndX=-4.03109 EndY=3.5 EndZ=0
    g26: LineSegment StartX=-4.03109 StartY=3.5 StartZ=0 EndX=-1 EndY=5.25 EndZ=0
    g27: Circle [constr] CenterX=-4.03109 CenterY=7 CenterZ=0 NormalX=0 NormalY=0 NormalZ=1 AngleXU=0 Radius=3.5
    g28: LineSegment StartX=-4.96891 StartY=-1.75 StartZ=0 EndX=-4.96891 EndY=1.75 EndZ=0
    g29: LineSegment StartX=-4.96891 StartY=1.75 StartZ=0 EndX=-8 EndY=3.5 EndZ=0
    g30: LineSegment StartX=-8 StartY=3.5 StartZ=0 EndX=-11.0311 EndY=1.75 EndZ=0
    g31: LineSegment StartX=-11.0311 StartY=1.75 StartZ=0 EndX=-11.0311 EndY=-1.75 EndZ=0
    g32: LineSegment StartX=-11.0311 StartY=-1.75 StartZ=0 EndX=-8 EndY=-3.5 EndZ=0
    g33: LineSegment StartX=-8 StartY=-3.5 StartZ=0 EndX=-4.96891 EndY=-1.75 EndZ=0
    g34: Circle [constr] CenterX=-8 CenterY=0 CenterZ=0 NormalX=0 NormalY=0 NormalZ=1 AngleXU=0 Radius=3.5
    g35: LineSegment StartX=-4.03109 StartY=-3.5 StartZ=0 EndX=-7.06218 EndY=-5.25 EndZ=0
    g36: LineSegment StartX=-7.06218 StartY=-5.25 StartZ=0 EndX=-7.06218 EndY=-8.75 EndZ=0
    g37: LineSegment StartX=-7.06218 StartY=-8.75 StartZ=0 EndX=-4.03109 EndY=-10.5 EndZ=0
    g38: LineSegment StartX=-4.03109 StartY=-10.5 StartZ=0 EndX=-1 EndY=-8.75 EndZ=0
    g39: LineSegment StartX=-1 StartY=-8.75 StartZ=0 EndX=-1 EndY=-5.25 EndZ=0
    g40: LineSegment StartX=-1 StartY=-5.25 StartZ=0 EndX=-4.03109 EndY=-3.5 EndZ=0
    g41: Circle [constr] CenterX=-4.03109 CenterY=-7 CenterZ=0 NormalX=0 NormalY=0 NormalZ=1 AngleXU=0 Radius=3.5
    g42: LineSegment StartX=4.03109 StartY=-3.5 StartZ=0 EndX=1 EndY=-5.25 EndZ=0
    g43: LineSegment StartX=1 StartY=-5.25 StartZ=0 EndX=1 EndY=-8.75 EndZ=0
    g44: LineSegment StartX=1 StartY=-8.75 StartZ=0 EndX=4.03109 EndY=-10.5 EndZ=0
    g45: LineSegment StartX=4.03109 StartY=-10.5 StartZ=0 EndX=7.06218 EndY=-8.75 EndZ=0
    g46: LineSegment StartX=7.06218 StartY=-8.75 StartZ=0 EndX=7.06218 EndY=-5.25 EndZ=0
    g47: LineSegment StartX=7.06218 StartY=-5.25 StartZ=0 EndX=4.03109 EndY=-3.5 EndZ=0
    g48: Circle [constr] CenterX=4.03109 CenterY=-7 CenterZ=0 NormalX=0 NormalY=0 NormalZ=1 AngleXU=0 Radius=3.5
  constraints (117):
    c: Coincident(g0,g1)
    c: Coincident(g1,g2)
    c: Coincident(g2,g3)
    c: Coincident(g3,g4)
    c: Coincident(g4,g5)
    c: Coincident(g5,g0)
    c: Equal(g0, g1-g5) x5
    c: PointOnObject(g0,g6)
    c: PointOnObject(g1,g6)
    c: PointOnObject(g2,g6)
    c: PointOnObject(g3,g6)
    c: PointOnObject(g4,g6)
    c: PointOnObject(g5,g6)
    c: Coincident(g6,g-1)
    c: Diameter(g6) = 7
    c: PointOnObject(g0,g-2)
    c: Coincident(g7,g8)
    c: Coincident(g8,g9)
    c: Coincident(g9,g10)
    c: Coincident(g10,g11)
    c: Coincident(g11,g12)
    c: Coincident(g12,g7)
    c: Equal(g7, g8-g12) x5
    c: PointOnObject(g7,g13)
    c: PointOnObject(g8,g13)
    c: PointOnObject(g9,g13)
    c: PointOnObject(g10,g13)
    c: PointOnObject(g11,g13)
    c: PointOnObject(g12,g13)
    c: PointOnObject(g13,g-1)
    c: Diameter(g13) = 7
    c: Distance(g6,g13) = 8
    c: Horizontal(g0,g10)
    c: Coincident(g14,g15)
    c: Coincident(g15,g16)
    c: Coincident(g16,g17)
    c: Coincident(g17,g18)
    c: Coincident(g18,g19)
    c: Coincident(g19,g14)
    c: Equal(g14, g15-g19) x5
    c: PointOnObject(g14,g20)
    c: PointOnObject(g15,g20)
    c: PointOnObject(g16,g20)
    c: PointOnObject(g17,g20)
    c: PointOnObject(g18,g20)
    c: PointOnObject(g19,g20)
    c: Diameter(g20) = 7
    c: DistanceY(g-1,g20) = 7
    c: Vertical(g18)
    c: Distance(g17,g-2) = 1
    c: Coincident(g21,g22)
    c: Coincident(g22,g23)
    c: Coincident(g23,g24)
    c: Coincident(g24,g25)
    c: Coincident(g25,g26)
    c: Coincident(g26,g21)
    c: Equal(g21, g22-g26) x5
    c: PointOnObject(g21,g27)
    c: PointOnObject(g22,g27)
    c: PointOnObject(g23,g27)
    c: PointOnObject(g24,g27)
    c: PointOnObject(g25,g27)
    c: PointOnObject(g26,g27)
    c: Diameter(g27) = 7
    c: DistanceY(g-1,g27) = 7
    c: DistanceX(g21,g-1) = 1
    c: Vertical(g21)
    c: Coincident(g28,g29)
    c: Coincident(g29,g30)
    c: Coincident(g30,g31)
    c: Coincident(g31,g32)
    c: Coincident(g32,g33)
    c: Coincident(g33,g28)
    c: Equal(g28, g29-g33) x5
    c: PointOnObject(g28,g34)
    c: PointOnObject(g29,g34)
    c: PointOnObject(g30,g34)
    c: PointOnObject(g31,g34)
    c: PointOnObject(g32,g34)
    c: PointOnObject(g33,g34)
    c: PointOnObject(g34,g-1)
    c: Diameter(g34) = 7
    c: Vertical(g31)
    c: DistanceX(g34,g-1) = 8
    c: Coincident(g35,g36)
    c: Coincident(g36,g37)
    c: Coincident(g37,g38)
    c: Coincident(g38,g39)
    c: Coincident(g39,g40)
    c: Coincident(g40,g35)
    c: Equal(g35, g36-g40) x5
    c: PointOnObject(g35,g41)
    c: PointOnObject(g36,g41)
    c: PointOnObject(g37,g41)
    c: PointOnObject(g38,g41)
    c: PointOnObject(g39,g41)
    c: PointOnObject(g40,g41)
    c: Coincident(g42,g43)
    c: Coincident(g43,g44)
    c: Coincident(g44,g45)
    c: Coincident(g45,g46)
    c: Coincident(g46,g47)
    c: Coincident(g47,g42)
    c: Equal(g42, g43-g47) x5
    c: PointOnObject(g42,g48)
    c: PointOnObject(g43,g48)
    c: PointOnObject(g44,g48)
    c: PointOnObject(g45,g48)
    c: PointOnObject(g46,g48)
    c: PointOnObject(g47,g48)
    c: Equal(g41,g48)
    c: Diameter(g41) = 7
    c: Vertical(g39)
    c: Vertical(g43)
    c: Distance(g-2,g39) = 1
    c: Symmetric(g38,g43,g-2)
    c: Distance(g41,g-1) = 7
FEATURE [Part::Extrusion] Extrude477  label="hex092"
  Base = -> Sketch485
  Dir = (0,-1,2e-16)
  DirMode = 2
  FaceMakerClass = Part::FaceMakerBullseye
  FaceMakerMode = 3
  LengthFwd = 10
  LengthRev = 0
  Placement = pos=(104,0,0) rot=(0,0,1;0rad)
  Solid = true
  Symmetric = false
FEATURE [Sketcher::SketchObject] Sketch486
  ArcFitTolerance = 1e-06
  FullyConstrained = true
  MakeInternals = false
  Placement = pos=(0,0,0) rot=(1,0,0;1.5708rad)
  sketch-geometry (49):
    g0: LineSegment StartX=1e-16 StartY=3.5 StartZ=0 EndX=-3.03109 EndY=1.75 EndZ=0
    g1: LineSegment StartX=-3.03109 StartY=1.75 StartZ=0 EndX=-3.03109 EndY=-1.75 EndZ=0
    g2: LineSegment StartX=-3.03109 StartY=-1.75 StartZ=0 EndX=-1e-16 EndY=-3.5 EndZ=0
    g3: LineSegment StartX=-1e-16 StartY=-3.5 StartZ=0 EndX=3.03109 EndY=-1.75 EndZ=0
    g4: LineSegment StartX=3.03109 StartY=-1.75 StartZ=0 EndX=3.03109 EndY=1.75 EndZ=0
    g5: LineSegment StartX=3.03109 StartY=1.75 StartZ=0 EndX=1e-16 EndY=3.5 EndZ=0
    g6: Circle [constr] CenterX=0 CenterY=0 CenterZ=0 NormalX=0 NormalY=0 NormalZ=1 AngleXU=0 Radius=3.5
    g7: LineSegment StartX=4.96892 StartY=-1.75002 StartZ=0 EndX=8.00002 EndY=-3.5 EndZ=0
    g8: LineSegment StartX=8.00002 StartY=-3.5 StartZ=0 EndX=11.0311 EndY=-1.74998 EndZ=0
    g9: LineSegment StartX=11.0311 StartY=-1.74998 StartZ=0 EndX=11.0311 EndY=1.75002 EndZ=0
    g10: LineSegment StartX=11.0311 StartY=1.75002 StartZ=0 EndX=7.99998 EndY=3.5 EndZ=0
    g11: LineSegment StartX=7.99998 StartY=3.5 StartZ=0 EndX=4.9689 EndY=1.74998 EndZ=0
    g12: LineSegment StartX=4.9689 StartY=1.74998 StartZ=0 EndX=4.96892 EndY=-1.75002 EndZ=0
    g13: Circle [constr] CenterX=8 CenterY=0 CenterZ=0 NormalX=0 NormalY=0 NormalZ=1 AngleXU=0 Radius=3.5
    g14: LineSegment StartX=4.03109 StartY=3.5 StartZ=0 EndX=7.06218 EndY=5.25 EndZ=0
    g15: LineSegment StartX=7.06218 StartY=5.25 StartZ=0 EndX=7.06218 EndY=8.75 EndZ=0
    g16: LineSegment StartX=7.06218 StartY=8.75 StartZ=0 EndX=4.03109 EndY=10.5 EndZ=0
    g17: LineSegment StartX=4.03109 StartY=10.5 StartZ=0 EndX=1 EndY=8.75 EndZ=0
    g18: LineSegment StartX=1 StartY=8.75 StartZ=0 EndX=1 EndY=5.25 EndZ=0
    g19: LineSegment StartX=1 StartY=5.25 StartZ=0 EndX=4.03109 EndY=3.5 EndZ=0
    g20: Circle [constr] CenterX=4.03109 CenterY=7 CenterZ=0 NormalX=0 NormalY=0 NormalZ=1 AngleXU=0 Radius=3.5
    g21: LineSegment StartX=-1 StartY=5.25 StartZ=0 EndX=-1 EndY=8.75 EndZ=0
    g22: LineSegment StartX=-1 StartY=8.75 StartZ=0 EndX=-4.03109 EndY=10.5 EndZ=0
    g23: LineSegment StartX=-4.03109 StartY=10.5 StartZ=0 EndX=-7.06218 EndY=8.75 EndZ=0
    g24: LineSegment StartX=-7.06218 StartY=8.75 StartZ=0 EndX=-7.06218 EndY=5.25 EndZ=0
    g25: LineSegment StartX=-7.06218 StartY=5.25 StartZ=0 EndX=-4.03109 EndY=3.5 EndZ=0
    g26: LineSegment StartX=-4.03109 StartY=3.5 StartZ=0 EndX=-1 EndY=5.25 EndZ=0
    g27: Circle [constr] CenterX=-4.03109 CenterY=7 CenterZ=0 NormalX=0 NormalY=0 NormalZ=1 AngleXU=0 Radius=3.5
    g28: LineSegment StartX=-4.96891 StartY=-1.75 StartZ=0 EndX=-4.96891 EndY=1.75 EndZ=0
    g29: LineSegment StartX=-4.96891 StartY=1.75 StartZ=0 EndX=-8 EndY=3.5 EndZ=0
    g30: LineSegment StartX=-8 StartY=3.5 StartZ=0 EndX=-11.0311 EndY=1.75 EndZ=0
    g31: LineSegment StartX=-11.0311 StartY=1.75 StartZ=0 EndX=-11.0311 EndY=-1.75 EndZ=0
    g32: LineSegment StartX=-11.0311 StartY=-1.75 StartZ=0 EndX=-8 EndY=-3.5 EndZ=0
    g33: LineSegment StartX=-8 StartY=-3.5 StartZ=0 EndX=-4.96891 EndY=-1.75 EndZ=0
    g34: Circle [constr] CenterX=-8 CenterY=0 CenterZ=0 NormalX=0 NormalY=0 NormalZ=1 AngleXU=0 Radius=3.5
    g35: LineSegment StartX=-4.03109 StartY=-3.5 StartZ=0 EndX=-7.06218 EndY=-5.25 EndZ=0
    g36: LineSegment StartX=-7.06218 StartY=-5.25 StartZ=0 EndX=-7.06218 EndY=-8.75 EndZ=0
    g37: LineSegment StartX=-7.06218 StartY=-8.75 StartZ=0 EndX=-4.03109 EndY=-10.5 EndZ=0
    g38: LineSegment StartX=-4.03109 StartY=-10.5 StartZ=0 EndX=-1 EndY=-8.75 EndZ=0
    g39: LineSegment StartX=-1 StartY=-8.75 StartZ=0 EndX=-1 EndY=-5.25 EndZ=0
    g40: LineSegment StartX=-1 StartY=-5.25 StartZ=0 EndX=-4.03109 EndY=-3.5 EndZ=0
    g41: Circle [constr] CenterX=-4.03109 CenterY=-7 CenterZ=0 NormalX=0 NormalY=0 NormalZ=1 AngleXU=0 Radius=3.5
    g42: LineSegment StartX=4.03109 StartY=-3.5 StartZ=0 EndX=1 EndY=-5.25 EndZ=0
    g43: LineSegment StartX=1 StartY=-5.25 StartZ=0 EndX=1 EndY=-8.75 EndZ=0
    g44: LineSegment StartX=1 StartY=-8.75 StartZ=0 EndX=4.03109 EndY=-10.5 EndZ=0
    g45: LineSegment StartX=4.03109 StartY=-10.5 StartZ=0 EndX=7.06218 EndY=-8.75 EndZ=0
    g46: LineSegment StartX=7.06218 StartY=-8.75 StartZ=0 EndX=7.06218 EndY=-5.25 EndZ=0
    g47: LineSegment StartX=7.06218 StartY=-5.25 StartZ=0 EndX=4.03109 EndY=-3.5 EndZ=0
    g48: Circle [constr] CenterX=4.03109 CenterY=-7 CenterZ=0 NormalX=0 NormalY=0 NormalZ=1 AngleXU=0 Radius=3.5
  constraints (117):
    c: Coincident(g0,g1)
    c: Coincident(g1,g2)
    c: Coincident(g2,g3)
    c: Coincident(g3,g4)
    c: Coincident(g4,g5)
    c: Coincident(g5,g0)
    c: Equal(g0, g1-g5) x5
    c: PointOnObject(g0,g6)
    c: PointOnObject(g1,g6)
    c: PointOnObject(g2,g6)
    c: PointOnObject(g3,g6)
    c: PointOnObject(g4,g6)
    c: PointOnObject(g5,g6)
    c: Coincident(g6,g-1)
    c: Diameter(g6) = 7
    c: PointOnObject(g0,g-2)
    c: Coincident(g7,g8)
    c: Coincident(g8,g9)
    c: Coincident(g9,g10)
    c: Coincident(g10,g11)
    c: Coincident(g11,g12)
    c: Coincident(g12,g7)
    c: Equal(g7, g8-g12) x5
    c: PointOnObject(g7,g13)
    c: PointOnObject(g8,g13)
    c: PointOnObject(g9,g13)
    c: PointOnObject(g10,g13)
    c: PointOnObject(g11,g13)
    c: PointOnObject(g12,g13)
    c: PointOnObject(g13,g-1)
    c: Diameter(g13) = 7
    c: Distance(g6,g13) = 8
    c: Horizontal(g0,g10)
    c: Coincident(g14,g15)
    c: Coincident(g15,g16)
    c: Coincident(g16,g17)
    c: Coincident(g17,g18)
    c: Coincident(g18,g19)
    c: Coincident(g19,g14)
    c: Equal(g14, g15-g19) x5
    c: PointOnObject(g14,g20)
    c: PointOnObject(g15,g20)
    c: PointOnObject(g16,g20)
    c: PointOnObject(g17,g20)
    c: PointOnObject(g18,g20)
    c: PointOnObject(g19,g20)
    c: Diameter(g20) = 7
    c: DistanceY(g-1,g20) = 7
    c: Vertical(g18)
    c: Distance(g17,g-2) = 1
    c: Coincident(g21,g22)
    c: Coincident(g22,g23)
    c: Coincident(g23,g24)
    c: Coincident(g24,g25)
    c: Coincident(g25,g26)
    c: Coincident(g26,g21)
    c: Equal(g21, g22-g26) x5
    c: PointOnObject(g21,g27)
    c: PointOnObject(g22,g27)
    c: PointOnObject(g23,g27)
    c: PointOnObject(g24,g27)
    c: PointOnObject(g25,g27)
    c: PointOnObject(g26,g27)
    c: Diameter(g27) = 7
    c: DistanceY(g-1,g27) = 7
    c: DistanceX(g21,g-1) = 1
    c: Vertical(g21)
    c: Coincident(g28,g29)
    c: Coincident(g29,g30)
    c: Coincident(g30,g31)
    c: Coincident(g31,g32)
    c: Coincident(g32,g33)
    c: Coincident(g33,g28)
    c: Equal(g28, g29-g33) x5
    c: PointOnObject(g28,g34)
    c: PointOnObject(g29,g34)
    c: PointOnObject(g30,g34)
    c: PointOnObject(g31,g34)
    c: PointOnObject(g32,g34)
    c: PointOnObject(g33,g34)
    c: PointOnObject(g34,g-1)
    c: Diameter(g34) = 7
    c: Vertical(g31)
    c: DistanceX(g34,g-1) = 8
    c: Coincident(g35,g36)
    c: Coincident(g36,g37)
    c: Coincident(g37,g38)
    c: Coincident(g38,g39)
    c: Coincident(g39,g40)
    c: Coincident(g40,g35)
    c: Equal(g35, g36-g40) x5
    c: PointOnObject(g35,g41)
    c: PointOnObject(g36,g41)
    c: PointOnObject(g37,g41)
    c: PointOnObject(g38,g41)
    c: PointOnObject(g39,g41)
    c: PointOnObject(g40,g41)
    c: Coincident(g42,g43)
    c: Coincident(g43,g44)
    c: Coincident(g44,g45)
    c: Coincident(g45,g46)
    c: Coincident(g46,g47)
    c: Coincident(g47,g42)
    c: Equal(g42, g43-g47) x5
    c: PointOnObject(g42,g48)
    c: PointOnObject(g43,g48)
    c: PointOnObject(g44,g48)
    c: PointOnObject(g45,g48)
    c: PointOnObject(g46,g48)
    c: PointOnObject(g47,g48)
    c: Equal(g41,g48)
    c: Diameter(g41) = 7
    c: Vertical(g39)
    c: Vertical(g43)
    c: Distance(g-2,g39) = 1
    c: Symmetric(g38,g43,g-2)
    c: Distance(g41,g-1) = 7
FEATURE [Part::Extrusion] Extrude478  label="hex093"
  Base = -> Sketch486
  Dir = (0,-1,2e-16)
  DirMode = 2
  FaceMakerClass = Part::FaceMakerBullseye
  FaceMakerMode = 3
  LengthFwd = 10
  LengthRev = 0
  Placement = pos=(96,0,-14) rot=(0,0,1;0rad)
  Solid = true
  Symmetric = false
FEATURE [Sketcher::SketchObject] Sketch487
  ArcFitTolerance = 1e-06
  FullyConstrained = true
  MakeInternals = false
  Placement = pos=(0,0,0) rot=(1,0,0;1.5708rad)
  sketch-geometry (49):
    g0: LineSegment StartX=1e-16 StartY=3.5 StartZ=0 EndX=-3.03109 EndY=1.75 EndZ=0
    g1: LineSegment StartX=-3.03109 StartY=1.75 StartZ=0 EndX=-3.03109 EndY=-1.75 EndZ=0
    g2: LineSegment StartX=-3.03109 StartY=-1.75 StartZ=0 EndX=-1e-16 EndY=-3.5 EndZ=0
    g3: LineSegment StartX=-1e-16 StartY=-3.5 StartZ=0 EndX=3.03109 EndY=-1.75 EndZ=0
    g4: LineSegment StartX=3.03109 StartY=-1.75 StartZ=0 EndX=3.03109 EndY=1.75 EndZ=0
    g5: LineSegment StartX=3.03109 StartY=1.75 StartZ=0 EndX=1e-16 EndY=3.5 EndZ=0
    g6: Circle [constr] CenterX=0 CenterY=0 CenterZ=0 NormalX=0 NormalY=0 NormalZ=1 AngleXU=0 Radius=3.5
    g7: LineSegment StartX=4.96892 StartY=-1.75002 StartZ=0 EndX=8.00002 EndY=-3.5 EndZ=0
    g8: LineSegment StartX=8.00002 StartY=-3.5 StartZ=0 EndX=11.0311 EndY=-1.74998 EndZ=0
    g9: LineSegment StartX=11.0311 StartY=-1.74998 StartZ=0 EndX=11.0311 EndY=1.75002 EndZ=0
    g10: LineSegment StartX=11.0311 StartY=1.75002 StartZ=0 EndX=7.99998 EndY=3.5 EndZ=0
    g11: LineSegment StartX=7.99998 StartY=3.5 StartZ=0 EndX=4.9689 EndY=1.74998 EndZ=0
    g12: LineSegment StartX=4.9689 StartY=1.74998 StartZ=0 EndX=4.96892 EndY=-1.75002 EndZ=0
    g13: Circle [constr] CenterX=8 CenterY=0 CenterZ=0 NormalX=0 NormalY=0 NormalZ=1 AngleXU=0 Radius=3.5
    g14: LineSegment StartX=4.03109 StartY=3.5 StartZ=0 EndX=7.06218 EndY=5.25 EndZ=0
    g15: LineSegment StartX=7.06218 StartY=5.25 StartZ=0 EndX=7.06218 EndY=8.75 EndZ=0
    g16: LineSegment StartX=7.06218 StartY=8.75 StartZ=0 EndX=4.03109 EndY=10.5 EndZ=0
    g17: LineSegment StartX=4.03109 StartY=10.5 StartZ=0 EndX=1 EndY=8.75 EndZ=0
    g18: LineSegment StartX=1 StartY=8.75 StartZ=0 EndX=1 EndY=5.25 EndZ=0
    g19: LineSegment StartX=1 StartY=5.25 StartZ=0 EndX=4.03109 EndY=3.5 EndZ=0
    g20: Circle [constr] CenterX=4.03109 CenterY=7 CenterZ=0 NormalX=0 NormalY=0 NormalZ=1 AngleXU=0 Radius=3.5
    g21: LineSegment StartX=-1 StartY=5.25 StartZ=0 EndX=-1 EndY=8.75 EndZ=0
    g22: LineSegment StartX=-1 StartY=8.75 StartZ=0 EndX=-4.03109 EndY=10.5 EndZ=0
    g23: LineSegment StartX=-4.03109 StartY=10.5 StartZ=0 EndX=-7.06218 EndY=8.75 EndZ=0
    g24: LineSegment StartX=-7.06218 StartY=8.75 StartZ=0 EndX=-7.06218 EndY=5.25 EndZ=0
    g25: LineSegment StartX=-7.06218 StartY=5.25 StartZ=0 EndX=-4.03109 EndY=3.5 EndZ=0
    g26: LineSegment StartX=-4.03109 StartY=3.5 StartZ=0 EndX=-1 EndY=5.25 EndZ=0
    g27: Circle [constr] CenterX=-4.03109 CenterY=7 CenterZ=0 NormalX=0 NormalY=0 NormalZ=1 AngleXU=0 Radius=3.5
    g28: LineSegment StartX=-4.96891 StartY=-1.75 StartZ=0 EndX=-4.96891 EndY=1.75 EndZ=0
    g29: LineSegment StartX=-4.96891 StartY=1.75 StartZ=0 EndX=-8 EndY=3.5 EndZ=0
    g30: LineSegment StartX=-8 StartY=3.5 StartZ=0 EndX=-11.0311 EndY=1.75 EndZ=0
    g31: LineSegment StartX=-11.0311 StartY=1.75 StartZ=0 EndX=-11.0311 EndY=-1.75 EndZ=0
    g32: LineSegment StartX=-11.0311 StartY=-1.75 StartZ=0 EndX=-8 EndY=-3.5 EndZ=0
    g33: LineSegment StartX=-8 StartY=-3.5 StartZ=0 EndX=-4.96891 EndY=-1.75 EndZ=0
    g34: Circle [constr] CenterX=-8 CenterY=0 CenterZ=0 NormalX=0 NormalY=0 NormalZ=1 AngleXU=0 Radius=3.5
    g35: LineSegment StartX=-4.03109 StartY=-3.5 StartZ=0 EndX=-7.06218 EndY=-5.25 EndZ=0
    g36: LineSegment StartX=-7.06218 StartY=-5.25 StartZ=0 EndX=-7.06218 EndY=-8.75 EndZ=0
    g37: LineSegment StartX=-7.06218 StartY=-8.75 StartZ=0 EndX=-4.03109 EndY=-10.5 EndZ=0
    g38: LineSegment StartX=-4.03109 StartY=-10.5 StartZ=0 EndX=-1 EndY=-8.75 EndZ=0
    g39: LineSegment StartX=-1 StartY=-8.75 StartZ=0 EndX=-1 EndY=-5.25 EndZ=0
    g40: LineSegment StartX=-1 StartY=-5.25 StartZ=0 EndX=-4.03109 EndY=-3.5 EndZ=0
    g41: Circle [constr] CenterX=-4.03109 CenterY=-7 CenterZ=0 NormalX=0 NormalY=0 NormalZ=1 AngleXU=0 Radius=3.5
    g42: LineSegment StartX=4.03109 StartY=-3.5 StartZ=0 EndX=1 EndY=-5.25 EndZ=0
    g43: LineSegment StartX=1 StartY=-5.25 StartZ=0 EndX=1 EndY=-8.75 EndZ=0
    g44: LineSegment StartX=1 StartY=-8.75 StartZ=0 EndX=4.03109 EndY=-10.5 EndZ=0
    g45: LineSegment StartX=4.03109 StartY=-10.5 StartZ=0 EndX=7.06218 EndY=-8.75 EndZ=0
    g46: LineSegment StartX=7.06218 StartY=-8.75 StartZ=0 EndX=7.06218 EndY=-5.25 EndZ=0
    g47: LineSegment StartX=7.06218 StartY=-5.25 StartZ=0 EndX=4.03109 EndY=-3.5 EndZ=0
    g48: Circle [constr] CenterX=4.03109 CenterY=-7 CenterZ=0 NormalX=0 NormalY=0 NormalZ=1 AngleXU=0 Radius=3.5
  constraints (117):
    c: Coincident(g0,g1)
    c: Coincident(g1,g2)
    c: Coincident(g2,g3)
    c: Coincident(g3,g4)
    c: Coincident(g4,g5)
    c: Coincident(g5,g0)
    c: Equal(g0, g1-g5) x5
    c: PointOnObject(g0,g6)
    c: PointOnObject(g1,g6)
    c: PointOnObject(g2,g6)
    c: PointOnObject(g3,g6)
    c: PointOnObject(g4,g6)
    c: PointOnObject(g5,g6)
    c: Coincident(g6,g-1)
    c: Diameter(g6) = 7
    c: PointOnObject(g0,g-2)
    c: Coincident(g7,g8)
    c: Coincident(g8,g9)
    c: Coincident(g9,g10)
    c: Coincident(g10,g11)
    c: Coincident(g11,g12)
    c: Coincident(g12,g7)
    c: Equal(g7, g8-g12) x5
    c: PointOnObject(g7,g13)
    c: PointOnObject(g8,g13)
    c: PointOnObject(g9,g13)
    c: PointOnObject(g10,g13)
    c: PointOnObject(g11,g13)
    c: PointOnObject(g12,g13)
    c: PointOnObject(g13,g-1)
    c: Diameter(g13) = 7
    c: Distance(g6,g13) = 8
    c: Horizontal(g0,g10)
    c: Coincident(g14,g15)
    c: Coincident(g15,g16)
    c: Coincident(g16,g17)
    c: Coincident(g17,g18)
    c: Coincident(g18,g19)
    c: Coincident(g19,g14)
    c: Equal(g14, g15-g19) x5
    c: PointOnObject(g14,g20)
    c: PointOnObject(g15,g20)
    c: PointOnObject(g16,g20)
    c: PointOnObject(g17,g20)
    c: PointOnObject(g18,g20)
    c: PointOnObject(g19,g20)
    c: Diameter(g20) = 7
    c: DistanceY(g-1,g20) = 7
    c: Vertical(g18)
    c: Distance(g17,g-2) = 1
    c: Coincident(g21,g22)
    c: Coincident(g22,g23)
    c: Coincident(g23,g24)
    c: Coincident(g24,g25)
    c: Coincident(g25,g26)
    c: Coincident(g26,g21)
    c: Equal(g21, g22-g26) x5
    c: PointOnObject(g21,g27)
    c: PointOnObject(g22,g27)
    c: PointOnObject(g23,g27)
    c: PointOnObject(g24,g27)
    c: PointOnObject(g25,g27)
    c: PointOnObject(g26,g27)
    c: Diameter(g27) = 7
    c: DistanceY(g-1,g27) = 7
    c: DistanceX(g21,g-1) = 1
    c: Vertical(g21)
    c: Coincident(g28,g29)
    c: Coincident(g29,g30)
    c: Coincident(g30,g31)
    c: Coincident(g31,g32)
    c: Coincident(g32,g33)
    c: Coincident(g33,g28)
    c: Equal(g28, g29-g33) x5
    c: PointOnObject(g28,g34)
    c: PointOnObject(g29,g34)
    c: PointOnObject(g30,g34)
    c: PointOnObject(g31,g34)
    c: PointOnObject(g32,g34)
    c: PointOnObject(g33,g34)
    c: PointOnObject(g34,g-1)
    c: Diameter(g34) = 7
    c: Vertical(g31)
    c: DistanceX(g34,g-1) = 8
    c: Coincident(g35,g36)
    c: Coincident(g36,g37)
    c: Coincident(g37,g38)
    c: Coincident(g38,g39)
    c: Coincident(g39,g40)
    c: Coincident(g40,g35)
    c: Equal(g35, g36-g40) x5
    c: PointOnObject(g35,g41)
    c: PointOnObject(g36,g41)
    c: PointOnObject(g37,g41)
    c: PointOnObject(g38,g41)
    c: PointOnObject(g39,g41)
    c: PointOnObject(g40,g41)
    c: Coincident(g42,g43)
    c: Coincident(g43,g44)
    c: Coincident(g44,g45)
    c: Coincident(g45,g46)
    c: Coincident(g46,g47)
    c: Coincident(g47,g42)
    c: Equal(g42, g43-g47) x5
    c: PointOnObject(g42,g48)
    c: PointOnObject(g43,g48)
    c: PointOnObject(g44,g48)
    c: PointOnObject(g45,g48)
    c: PointOnObject(g46,g48)
    c: PointOnObject(g47,g48)
    c: Equal(g41,g48)
    c: Diameter(g41) = 7
    c: Vertical(g39)
    c: Vertical(g43)
    c: Distance(g-2,g39) = 1
    c: Symmetric(g38,g43,g-2)
    c: Distance(g41,g-1) = 7
FEATURE [Part::Extrusion] Extrude479  label="hex094"
  Base = -> Sketch487
  Dir = (0,-1,2e-16)
  DirMode = 2
  FaceMakerClass = Part::FaceMakerBullseye
  FaceMakerMode = 3
  LengthFwd = 10
  LengthRev = 0
  Placement = pos=(88,0,-28) rot=(0,0,1;0rad)
  Solid = true
  Symmetric = false
FEATURE [Sketcher::SketchObject] Sketch488
  ArcFitTolerance = 1e-06
  FullyConstrained = true
  MakeInternals = false
  Placement = pos=(0,0,0) rot=(1,0,0;1.5708rad)
  sketch-geometry (49):
    g0: LineSegment StartX=1e-16 StartY=3.5 StartZ=0 EndX=-3.03109 EndY=1.75 EndZ=0
    g1: LineSegment StartX=-3.03109 StartY=1.75 StartZ=0 EndX=-3.03109 EndY=-1.75 EndZ=0
    g2: LineSegment StartX=-3.03109 StartY=-1.75 StartZ=0 EndX=-1e-16 EndY=-3.5 EndZ=0
    g3: LineSegment StartX=-1e-16 StartY=-3.5 StartZ=0 EndX=3.03109 EndY=-1.75 EndZ=0
    g4: LineSegment StartX=3.03109 StartY=-1.75 StartZ=0 EndX=3.03109 EndY=1.75 EndZ=0
    g5: LineSegment StartX=3.03109 StartY=1.75 StartZ=0 EndX=1e-16 EndY=3.5 EndZ=0
    g6: Circle [constr] CenterX=0 CenterY=0 CenterZ=0 NormalX=0 NormalY=0 NormalZ=1 AngleXU=0 Radius=3.5
    g7: LineSegment StartX=4.96892 StartY=-1.75002 StartZ=0 EndX=8.00002 EndY=-3.5 EndZ=0
    g8: LineSegment StartX=8.00002 StartY=-3.5 StartZ=0 EndX=11.0311 EndY=-1.74998 EndZ=0
    g9: LineSegment StartX=11.0311 StartY=-1.74998 StartZ=0 EndX=11.0311 EndY=1.75002 EndZ=0
    g10: LineSegment StartX=11.0311 StartY=1.75002 StartZ=0 EndX=7.99998 EndY=3.5 EndZ=0
    g11: LineSegment StartX=7.99998 StartY=3.5 StartZ=0 EndX=4.9689 EndY=1.74998 EndZ=0
    g12: LineSegment StartX=4.9689 StartY=1.74998 StartZ=0 EndX=4.96892 EndY=-1.75002 EndZ=0
    g13: Circle [constr] CenterX=8 CenterY=0 CenterZ=0 NormalX=0 NormalY=0 NormalZ=1 AngleXU=0 Radius=3.5
    g14: LineSegment StartX=4.03109 StartY=3.5 StartZ=0 EndX=7.06218 EndY=5.25 EndZ=0
    g15: LineSegment StartX=7.06218 StartY=5.25 StartZ=0 EndX=7.06218 EndY=8.75 EndZ=0
    g16: LineSegment StartX=7.06218 StartY=8.75 StartZ=0 EndX=4.03109 EndY=10.5 EndZ=0
    g17: LineSegment StartX=4.03109 StartY=10.5 StartZ=0 EndX=1 EndY=8.75 EndZ=0
    g18: LineSegment StartX=1 StartY=8.75 StartZ=0 EndX=1 EndY=5.25 EndZ=0
    g19: LineSegment StartX=1 StartY=5.25 StartZ=0 EndX=4.03109 EndY=3.5 EndZ=0
    g20: Circle [constr] CenterX=4.03109 CenterY=7 CenterZ=0 NormalX=0 NormalY=0 NormalZ=1 AngleXU=0 Radius=3.5
    g21: LineSegment StartX=-1 StartY=5.25 StartZ=0 EndX=-1 EndY=8.75 EndZ=0
    g22: LineSegment StartX=-1 StartY=8.75 StartZ=0 EndX=-4.03109 EndY=10.5 EndZ=0
    g23: LineSegment StartX=-4.03109 StartY=10.5 StartZ=0 EndX=-7.06218 EndY=8.75 EndZ=0
    g24: LineSegment StartX=-7.06218 StartY=8.75 StartZ=0 EndX=-7.06218 EndY=5.25 EndZ=0
    g25: LineSegment StartX=-7.06218 StartY=5.25 StartZ=0 EndX=-4.03109 EndY=3.5 EndZ=0
    g26: LineSegment StartX=-4.03109 StartY=3.5 StartZ=0 EndX=-1 EndY=5.25 EndZ=0
    g27: Circle [constr] CenterX=-4.03109 CenterY=7 CenterZ=0 NormalX=0 NormalY=0 NormalZ=1 AngleXU=0 Radius=3.5
    g28: LineSegment StartX=-4.96891 StartY=-1.75 StartZ=0 EndX=-4.96891 EndY=1.75 EndZ=0
    g29: LineSegment StartX=-4.96891 StartY=1.75 StartZ=0 EndX=-8 EndY=3.5 EndZ=0
    g30: LineSegment StartX=-8 StartY=3.5 StartZ=0 EndX=-11.0311 EndY=1.75 EndZ=0
    g31: LineSegment StartX=-11.0311 StartY=1.75 StartZ=0 EndX=-11.0311 EndY=-1.75 EndZ=0
    g32: LineSegment StartX=-11.0311 StartY=-1.75 StartZ=0 EndX=-8 EndY=-3.5 EndZ=0
    g33: LineSegment StartX=-8 StartY=-3.5 StartZ=0 EndX=-4.96891 EndY=-1.75 EndZ=0
    g34: Circle [constr] CenterX=-8 CenterY=0 CenterZ=0 NormalX=0 NormalY=0 NormalZ=1 AngleXU=0 Radius=3.5
    g35: LineSegment StartX=-4.03109 StartY=-3.5 StartZ=0 EndX=-7.06218 EndY=-5.25 EndZ=0
    g36: LineSegment StartX=-7.06218 StartY=-5.25 StartZ=0 EndX=-7.06218 EndY=-8.75 EndZ=0
    g37: LineSegment StartX=-7.06218 StartY=-8.75 StartZ=0 EndX=-4.03109 EndY=-10.5 EndZ=0
    g38: LineSegment StartX=-4.03109 StartY=-10.5 StartZ=0 EndX=-1 EndY=-8.75 EndZ=0
    g39: LineSegment StartX=-1 StartY=-8.75 StartZ=0 EndX=-1 EndY=-5.25 EndZ=0
    g40: LineSegment StartX=-1 StartY=-5.25 StartZ=0 EndX=-4.03109 EndY=-3.5 EndZ=0
    g41: Circle [constr] CenterX=-4.03109 CenterY=-7 CenterZ=0 NormalX=0 NormalY=0 NormalZ=1 AngleXU=0 Radius=3.5
    g42: LineSegment StartX=4.03109 StartY=-3.5 StartZ=0 EndX=1 EndY=-5.25 EndZ=0
    g43: LineSegment StartX=1 StartY=-5.25 StartZ=0 EndX=1 EndY=-8.75 EndZ=0
    g44: LineSegment StartX=1 StartY=-8.75 StartZ=0 EndX=4.03109 EndY=-10.5 EndZ=0
    g45: LineSegment StartX=4.03109 StartY=-10.5 StartZ=0 EndX=7.06218 EndY=-8.75 EndZ=0
    g46: LineSegment StartX=7.06218 StartY=-8.75 StartZ=0 EndX=7.06218 EndY=-5.25 EndZ=0
    g47: LineSegment StartX=7.06218 StartY=-5.25 StartZ=0 EndX=4.03109 EndY=-3.5 EndZ=0
    g48: Circle [constr] CenterX=4.03109 CenterY=-7 CenterZ=0 NormalX=0 NormalY=0 NormalZ=1 AngleXU=0 Radius=3.5
  constraints (117):
    c: Coincident(g0,g1)
    c: Coincident(g1,g2)
    c: Coincident(g2,g3)
    c: Coincident(g3,g4)
    c: Coincident(g4,g5)
    c: Coincident(g5,g0)
    c: Equal(g0, g1-g5) x5
    c: PointOnObject(g0,g6)
    c: PointOnObject(g1,g6)
    c: PointOnObject(g2,g6)
    c: PointOnObject(g3,g6)
    c: PointOnObject(g4,g6)
    c: PointOnObject(g5,g6)
    c: Coincident(g6,g-1)
    c: Diameter(g6) = 7
    c: PointOnObject(g0,g-2)
    c: Coincident(g7,g8)
    c: Coincident(g8,g9)
    c: Coincident(g9,g10)
    c: Coincident(g10,g11)
    c: Coincident(g11,g12)
    c: Coincident(g12,g7)
    c: Equal(g7, g8-g12) x5
    c: PointOnObject(g7,g13)
    c: PointOnObject(g8,g13)
    c: PointOnObject(g9,g13)
    c: PointOnObject(g10,g13)
    c: PointOnObject(g11,g13)
    c: PointOnObject(g12,g13)
    c: PointOnObject(g13,g-1)
    c: Diameter(g13) = 7
    c: Distance(g6,g13) = 8
    c: Horizontal(g0,g10)
    c: Coincident(g14,g15)
    c: Coincident(g15,g16)
    c: Coincident(g16,g17)
    c: Coincident(g17,g18)
    c: Coincident(g18,g19)
    c: Coincident(g19,g14)
    c: Equal(g14, g15-g19) x5
    c: PointOnObject(g14,g20)
    c: PointOnObject(g15,g20)
    c: PointOnObject(g16,g20)
    c: PointOnObject(g17,g20)
    c: PointOnObject(g18,g20)
    c: PointOnObject(g19,g20)
    c: Diameter(g20) = 7
    c: DistanceY(g-1,g20) = 7
    c: Vertical(g18)
    c: Distance(g17,g-2) = 1
    c: Coincident(g21,g22)
    c: Coincident(g22,g23)
    c: Coincident(g23,g24)
    c: Coincident(g24,g25)
    c: Coincident(g25,g26)
    c: Coincident(g26,g21)
    c: Equal(g21, g22-g26) x5
    c: PointOnObject(g21,g27)
    c: PointOnObject(g22,g27)
    c: PointOnObject(g23,g27)
    c: PointOnObject(g24,g27)
    c: PointOnObject(g25,g27)
    c: PointOnObject(g26,g27)
    c: Diameter(g27) = 7
    c: DistanceY(g-1,g27) = 7
    c: DistanceX(g21,g-1) = 1
    c: Vertical(g21)
    c: Coincident(g28,g29)
    c: Coincident(g29,g30)
    c: Coincident(g30,g31)
    c: Coincident(g31,g32)
    c: Coincident(g32,g33)
    c: Coincident(g33,g28)
    c: Equal(g28, g29-g33) x5
    c: PointOnObject(g28,g34)
    c: PointOnObject(g29,g34)
    c: PointOnObject(g30,g34)
    c: PointOnObject(g31,g34)
    c: PointOnObject(g32,g34)
    c: PointOnObject(g33,g34)
    c: PointOnObject(g34,g-1)
    c: Diameter(g34) = 7
    c: Vertical(g31)
    c: DistanceX(g34,g-1) = 8
    c: Coincident(g35,g36)
    c: Coincident(g36,g37)
    c: Coincident(g37,g38)
    c: Coincident(g38,g39)
    c: Coincident(g39,g40)
    c: Coincident(g40,g35)
    c: Equal(g35, g36-g40) x5
    c: PointOnObject(g35,g41)
    c: PointOnObject(g36,g41)
    c: PointOnObject(g37,g41)
    c: PointOnObject(g38,g41)
    c: PointOnObject(g39,g41)
    c: PointOnObject(g40,g41)
    c: Coincident(g42,g43)
    c: Coincident(g43,g44)
    c: Coincident(g44,g45)
    c: Coincident(g45,g46)
    c: Coincident(g46,g47)
    c: Coincident(g47,g42)
    c: Equal(g42, g43-g47) x5
    c: PointOnObject(g42,g48)
    c: PointOnObject(g43,g48)
    c: PointOnObject(g44,g48)
    c: PointOnObject(g45,g48)
    c: PointOnObject(g46,g48)
    c: PointOnObject(g47,g48)
    c: Equal(g41,g48)
    c: Diameter(g41) = 7
    c: Vertical(g39)
    c: Vertical(g43)
    c: Distance(g-2,g39) = 1
    c: Symmetric(g38,g43,g-2)
    c: Distance(g41,g-1) = 7
FEATURE [Part::Extrusion] Extrude480  label="hex095"
  Base = -> Sketch488
  Dir = (0,-1,2e-16)
  DirMode = 2
  FaceMakerClass = Part::FaceMakerBullseye
  FaceMakerMode = 3
  LengthFwd = 10
  LengthRev = 0
  Placement = pos=(104,0,-28) rot=(0,0,1;0rad)
  Solid = true
  Symmetric = false
FEATURE [Sketcher::SketchObject] Sketch489
  ArcFitTolerance = 1e-06
  FullyConstrained = true
  MakeInternals = false
  Placement = pos=(0,0,0) rot=(1,0,0;1.5708rad)
  sketch-geometry (49):
    g0: LineSegment StartX=1e-16 StartY=3.5 StartZ=0 EndX=-3.03109 EndY=1.75 EndZ=0
    g1: LineSegment StartX=-3.03109 StartY=1.75 StartZ=0 EndX=-3.03109 EndY=-1.75 EndZ=0
    g2: LineSegment StartX=-3.03109 StartY=-1.75 StartZ=0 EndX=-1e-16 EndY=-3.5 EndZ=0
    g3: LineSegment StartX=-1e-16 StartY=-3.5 StartZ=0 EndX=3.03109 EndY=-1.75 EndZ=0
    g4: LineSegment StartX=3.03109 StartY=-1.75 StartZ=0 EndX=3.03109 EndY=1.75 EndZ=0
    g5: LineSegment StartX=3.03109 StartY=1.75 StartZ=0 EndX=1e-16 EndY=3.5 EndZ=0
    g6: Circle [constr] CenterX=0 CenterY=0 CenterZ=0 NormalX=0 NormalY=0 NormalZ=1 AngleXU=0 Radius=3.5
    g7: LineSegment StartX=4.96892 StartY=-1.75002 StartZ=0 EndX=8.00002 EndY=-3.5 EndZ=0
    g8: LineSegment StartX=8.00002 StartY=-3.5 StartZ=0 EndX=11.0311 EndY=-1.74998 EndZ=0
    g9: LineSegment StartX=11.0311 StartY=-1.74998 StartZ=0 EndX=11.0311 EndY=1.75002 EndZ=0
    g10: LineSegment StartX=11.0311 StartY=1.75002 StartZ=0 EndX=7.99998 EndY=3.5 EndZ=0
    g11: LineSegment StartX=7.99998 StartY=3.5 StartZ=0 EndX=4.9689 EndY=1.74998 EndZ=0
    g12: LineSegment StartX=4.9689 StartY=1.74998 StartZ=0 EndX=4.96892 EndY=-1.75002 EndZ=0
    g13: Circle [constr] CenterX=8 CenterY=0 CenterZ=0 NormalX=0 NormalY=0 NormalZ=1 AngleXU=0 Radius=3.5
    g14: LineSegment StartX=4.03109 StartY=3.5 StartZ=0 EndX=7.06218 EndY=5.25 EndZ=0
    g15: LineSegment StartX=7.06218 StartY=5.25 StartZ=0 EndX=7.06218 EndY=8.75 EndZ=0
    g16: LineSegment StartX=7.06218 StartY=8.75 StartZ=0 EndX=4.03109 EndY=10.5 EndZ=0
    g17: LineSegment StartX=4.03109 StartY=10.5 StartZ=0 EndX=1 EndY=8.75 EndZ=0
    g18: LineSegment StartX=1 StartY=8.75 StartZ=0 EndX=1 EndY=5.25 EndZ=0
    g19: LineSegment StartX=1 StartY=5.25 StartZ=0 EndX=4.03109 EndY=3.5 EndZ=0
    g20: Circle [constr] CenterX=4.03109 CenterY=7 CenterZ=0 NormalX=0 NormalY=0 NormalZ=1 AngleXU=0 Radius=3.5
    g21: LineSegment StartX=-1 StartY=5.25 StartZ=0 EndX=-1 EndY=8.75 EndZ=0
    g22: LineSegment StartX=-1 StartY=8.75 StartZ=0 EndX=-4.03109 EndY=10.5 EndZ=0
    g23: LineSegment StartX=-4.03109 StartY=10.5 StartZ=0 EndX=-7.06218 EndY=8.75 EndZ=0
    g24: LineSegment StartX=-7.06218 StartY=8.75 StartZ=0 EndX=-7.06218 EndY=5.25 EndZ=0
    g25: LineSegment StartX=-7.06218 StartY=5.25 StartZ=0 EndX=-4.03109 EndY=3.5 EndZ=0
    g26: LineSegment StartX=-4.03109 StartY=3.5 StartZ=0 EndX=-1 EndY=5.25 EndZ=0
    g27: Circle [constr] CenterX=-4.03109 CenterY=7 CenterZ=0 NormalX=0 NormalY=0 NormalZ=1 AngleXU=0 Radius=3.5
    g28: LineSegment StartX=-4.96891 StartY=-1.75 StartZ=0 EndX=-4.96891 EndY=1.75 EndZ=0
    g29: LineSegment StartX=-4.96891 StartY=1.75 StartZ=0 EndX=-8 EndY=3.5 EndZ=0
    g30: LineSegment StartX=-8 StartY=3.5 StartZ=0 EndX=-11.0311 EndY=1.75 EndZ=0
    g31: LineSegment StartX=-11.0311 StartY=1.75 StartZ=0 EndX=-11.0311 EndY=-1.75 EndZ=0
    g32: LineSegment StartX=-11.0311 StartY=-1.75 StartZ=0 EndX=-8 EndY=-3.5 EndZ=0
    g33: LineSegment StartX=-8 StartY=-3.5 StartZ=0 EndX=-4.96891 EndY=-1.75 EndZ=0
    g34: Circle [constr] CenterX=-8 CenterY=0 CenterZ=0 NormalX=0 NormalY=0 NormalZ=1 AngleXU=0 Radius=3.5
    g35: LineSegment StartX=-4.03109 StartY=-3.5 StartZ=0 EndX=-7.06218 EndY=-5.25 EndZ=0
    g36: LineSegment StartX=-7.06218 StartY=-5.25 StartZ=0 EndX=-7.06218 EndY=-8.75 EndZ=0
    g37: LineSegment StartX=-7.06218 StartY=-8.75 StartZ=0 EndX=-4.03109 EndY=-10.5 EndZ=0
    g38: LineSegment StartX=-4.03109 StartY=-10.5 StartZ=0 EndX=-1 EndY=-8.75 EndZ=0
    g39: LineSegment StartX=-1 StartY=-8.75 StartZ=0 EndX=-1 EndY=-5.25 EndZ=0
    g40: LineSegment StartX=-1 StartY=-5.25 StartZ=0 EndX=-4.03109 EndY=-3.5 EndZ=0
    g41: Circle [constr] CenterX=-4.03109 CenterY=-7 CenterZ=0 NormalX=0 NormalY=0 NormalZ=1 AngleXU=0 Radius=3.5
    g42: LineSegment StartX=4.03109 StartY=-3.5 StartZ=0 EndX=1 EndY=-5.25 EndZ=0
    g43: LineSegment StartX=1 StartY=-5.25 StartZ=0 EndX=1 EndY=-8.75 EndZ=0
    g44: LineSegment StartX=1 StartY=-8.75 StartZ=0 EndX=4.03109 EndY=-10.5 EndZ=0
    g45: LineSegment StartX=4.03109 StartY=-10.5 StartZ=0 EndX=7.06218 EndY=-8.75 EndZ=0
    g46: LineSegment StartX=7.06218 StartY=-8.75 StartZ=0 EndX=7.06218 EndY=-5.25 EndZ=0
    g47: LineSegment StartX=7.06218 StartY=-5.25 StartZ=0 EndX=4.03109 EndY=-3.5 EndZ=0
    g48: Circle [constr] CenterX=4.03109 CenterY=-7 CenterZ=0 NormalX=0 NormalY=0 NormalZ=1 AngleXU=0 Radius=3.5
  constraints (117):
    c: Coincident(g0,g1)
    c: Coincident(g1,g2)
    c: Coincident(g2,g3)
    c: Coincident(g3,g4)
    c: Coincident(g4,g5)
    c: Coincident(g5,g0)
    c: Equal(g0, g1-g5) x5
    c: PointOnObject(g0,g6)
    c: PointOnObject(g1,g6)
    c: PointOnObject(g2,g6)
    c: PointOnObject(g3,g6)
    c: PointOnObject(g4,g6)
    c: PointOnObject(g5,g6)
    c: Coincident(g6,g-1)
    c: Diameter(g6) = 7
    c: PointOnObject(g0,g-2)
    c: Coincident(g7,g8)
    c: Coincident(g8,g9)
    c: Coincident(g9,g10)
    c: Coincident(g10,g11)
    c: Coincident(g11,g12)
    c: Coincident(g12,g7)
    c: Equal(g7, g8-g12) x5
    c: PointOnObject(g7,g13)
    c: PointOnObject(g8,g13)
    c: PointOnObject(g9,g13)
    c: PointOnObject(g10,g13)
    c: PointOnObject(g11,g13)
    c: PointOnObject(g12,g13)
    c: PointOnObject(g13,g-1)
    c: Diameter(g13) = 7
    c: Distance(g6,g13) = 8
    c: Horizontal(g0,g10)
    c: Coincident(g14,g15)
    c: Coincident(g15,g16)
    c: Coincident(g16,g17)
    c: Coincident(g17,g18)
    c: Coincident(g18,g19)
    c: Coincident(g19,g14)
    c: Equal(g14, g15-g19) x5
    c: PointOnObject(g14,g20)
    c: PointOnObject(g15,g20)
    c: PointOnObject(g16,g20)
    c: PointOnObject(g17,g20)
    c: PointOnObject(g18,g20)
    c: PointOnObject(g19,g20)
    c: Diameter(g20) = 7
    c: DistanceY(g-1,g20) = 7
    c: Vertical(g18)
    c: Distance(g17,g-2) = 1
    c: Coincident(g21,g22)
    c: Coincident(g22,g23)
    c: Coincident(g23,g24)
    c: Coincident(g24,g25)
    c: Coincident(g25,g26)
    c: Coincident(g26,g21)
    c: Equal(g21, g22-g26) x5
    c: PointOnObject(g21,g27)
    c: PointOnObject(g22,g27)
    c: PointOnObject(g23,g27)
    c: PointOnObject(g24,g27)
    c: PointOnObject(g25,g27)
    c: PointOnObject(g26,g27)
    c: Diameter(g27) = 7
    c: DistanceY(g-1,g27) = 7
    c: DistanceX(g21,g-1) = 1
    c: Vertical(g21)
    c: Coincident(g28,g29)
    c: Coincident(g29,g30)
    c: Coincident(g30,g31)
    c: Coincident(g31,g32)
    c: Coincident(g32,g33)
    c: Coincident(g33,g28)
    c: Equal(g28, g29-g33) x5
    c: PointOnObject(g28,g34)
    c: PointOnObject(g29,g34)
    c: PointOnObject(g30,g34)
    c: PointOnObject(g31,g34)
    c: PointOnObject(g32,g34)
    c: PointOnObject(g33,g34)
    c: PointOnObject(g34,g-1)
    c: Diameter(g34) = 7
    c: Vertical(g31)
    c: DistanceX(g34,g-1) = 8
    c: Coincident(g35,g36)
    c: Coincident(g36,g37)
    c: Coincident(g37,g38)
    c: Coincident(g38,g39)
    c: Coincident(g39,g40)
    c: Coincident(g40,g35)
    c: Equal(g35, g36-g40) x5
    c: PointOnObject(g35,g41)
    c: PointOnObject(g36,g41)
    c: PointOnObject(g37,g41)
    c: PointOnObject(g38,g41)
    c: PointOnObject(g39,g41)
    c: PointOnObject(g40,g41)
    c: Coincident(g42,g43)
    c: Coincident(g43,g44)
    c: Coincident(g44,g45)
    c: Coincident(g45,g46)
    c: Coincident(g46,g47)
    c: Coincident(g47,g42)
    c: Equal(g42, g43-g47) x5
    c: PointOnObject(g42,g48)
    c: PointOnObject(g43,g48)
    c: PointOnObject(g44,g48)
    c: PointOnObject(g45,g48)
    c: PointOnObject(g46,g48)
    c: PointOnObject(g47,g48)
    c: Equal(g41,g48)
    c: Diameter(g41) = 7
    c: Vertical(g39)
    c: Vertical(g43)
    c: Distance(g-2,g39) = 1
    c: Symmetric(g38,g43,g-2)
    c: Distance(g41,g-1) = 7
FEATURE [Part::Extrusion] Extrude481  label="hex096"
  Base = -> Sketch489
  Dir = (0,-1,2e-16)
  DirMode = 2
  FaceMakerClass = Part::FaceMakerBullseye
  FaceMakerMode = 3
  LengthFwd = 10
  LengthRev = 0
  Placement = pos=(-96,0,-14) rot=(0,0,1;0rad)
  Solid = true
  Symmetric = false
FEATURE [Sketcher::SketchObject] Sketch490
  ArcFitTolerance = 1e-06
  FullyConstrained = true
  MakeInternals = false
  Placement = pos=(0,0,0) rot=(1,0,0;1.5708rad)
  sketch-geometry (49):
    g0: LineSegment StartX=1e-16 StartY=3.5 StartZ=0 EndX=-3.03109 EndY=1.75 EndZ=0
    g1: LineSegment StartX=-3.03109 StartY=1.75 StartZ=0 EndX=-3.03109 EndY=-1.75 EndZ=0
    g2: LineSegment StartX=-3.03109 StartY=-1.75 StartZ=0 EndX=-1e-16 EndY=-3.5 EndZ=0
    g3: LineSegment StartX=-1e-16 StartY=-3.5 StartZ=0 EndX=3.03109 EndY=-1.75 EndZ=0
    g4: LineSegment StartX=3.03109 StartY=-1.75 StartZ=0 EndX=3.03109 EndY=1.75 EndZ=0
    g5: LineSegment StartX=3.03109 StartY=1.75 StartZ=0 EndX=1e-16 EndY=3.5 EndZ=0
    g6: Circle [constr] CenterX=0 CenterY=0 CenterZ=0 NormalX=0 NormalY=0 NormalZ=1 AngleXU=0 Radius=3.5
    g7: LineSegment StartX=4.96892 StartY=-1.75002 StartZ=0 EndX=8.00002 EndY=-3.5 EndZ=0
    g8: LineSegment StartX=8.00002 StartY=-3.5 StartZ=0 EndX=11.0311 EndY=-1.74998 EndZ=0
    g9: LineSegment StartX=11.0311 StartY=-1.74998 StartZ=0 EndX=11.0311 EndY=1.75002 EndZ=0
    g10: LineSegment StartX=11.0311 StartY=1.75002 StartZ=0 EndX=7.99998 EndY=3.5 EndZ=0
    g11: LineSegment StartX=7.99998 StartY=3.5 StartZ=0 EndX=4.9689 EndY=1.74998 EndZ=0
    g12: LineSegment StartX=4.9689 StartY=1.74998 StartZ=0 EndX=4.96892 EndY=-1.75002 EndZ=0
    g13: Circle [constr] CenterX=8 CenterY=0 CenterZ=0 NormalX=0 NormalY=0 NormalZ=1 AngleXU=0 Radius=3.5
    g14: LineSegment StartX=4.03109 StartY=3.5 StartZ=0 EndX=7.06218 EndY=5.25 EndZ=0
    g15: LineSegment StartX=7.06218 StartY=5.25 StartZ=0 EndX=7.06218 EndY=8.75 EndZ=0
    g16: LineSegment StartX=7.06218 StartY=8.75 StartZ=0 EndX=4.03109 EndY=10.5 EndZ=0
    g17: LineSegment StartX=4.03109 StartY=10.5 StartZ=0 EndX=1 EndY=8.75 EndZ=0
    g18: LineSegment StartX=1 StartY=8.75 StartZ=0 EndX=1 EndY=5.25 EndZ=0
    g19: LineSegment StartX=1 StartY=5.25 StartZ=0 EndX=4.03109 EndY=3.5 EndZ=0
    g20: Circle [constr] CenterX=4.03109 CenterY=7 CenterZ=0 NormalX=0 NormalY=0 NormalZ=1 AngleXU=0 Radius=3.5
    g21: LineSegment StartX=-1 StartY=5.25 StartZ=0 EndX=-1 EndY=8.75 EndZ=0
    g22: LineSegment StartX=-1 StartY=8.75 StartZ=0 EndX=-4.03109 EndY=10.5 EndZ=0
    g23: LineSegment StartX=-4.03109 StartY=10.5 StartZ=0 EndX=-7.06218 EndY=8.75 EndZ=0
    g24: LineSegment StartX=-7.06218 StartY=8.75 StartZ=0 EndX=-7.06218 EndY=5.25 EndZ=0
    g25: LineSegment StartX=-7.06218 StartY=5.25 StartZ=0 EndX=-4.03109 EndY=3.5 EndZ=0
    g26: LineSegment StartX=-4.03109 StartY=3.5 StartZ=0 EndX=-1 EndY=5.25 EndZ=0
    g27: Circle [constr] CenterX=-4.03109 CenterY=7 CenterZ=0 NormalX=0 NormalY=0 NormalZ=1 AngleXU=0 Radius=3.5
    g28: LineSegment StartX=-4.96891 StartY=-1.75 StartZ=0 EndX=-4.96891 EndY=1.75 EndZ=0
    g29: LineSegment StartX=-4.96891 StartY=1.75 StartZ=0 EndX=-8 EndY=3.5 EndZ=0
    g30: LineSegment StartX=-8 StartY=3.5 StartZ=0 EndX=-11.0311 EndY=1.75 EndZ=0
    g31: LineSegment StartX=-11.0311 StartY=1.75 StartZ=0 EndX=-11.0311 EndY=-1.75 EndZ=0
    g32: LineSegment StartX=-11.0311 StartY=-1.75 StartZ=0 EndX=-8 EndY=-3.5 EndZ=0
    g33: LineSegment StartX=-8 StartY=-3.5 StartZ=0 EndX=-4.96891 EndY=-1.75 EndZ=0
    g34: Circle [constr] CenterX=-8 CenterY=0 CenterZ=0 NormalX=0 NormalY=0 NormalZ=1 AngleXU=0 Radius=3.5
    g35: LineSegment StartX=-4.03109 StartY=-3.5 StartZ=0 EndX=-7.06218 EndY=-5.25 EndZ=0
    g36: LineSegment StartX=-7.06218 StartY=-5.25 StartZ=0 EndX=-7.06218 EndY=-8.75 EndZ=0
    g37: LineSegment StartX=-7.06218 StartY=-8.75 StartZ=0 EndX=-4.03109 EndY=-10.5 EndZ=0
    g38: LineSegment StartX=-4.03109 StartY=-10.5 StartZ=0 EndX=-1 EndY=-8.75 EndZ=0
    g39: LineSegment StartX=-1 StartY=-8.75 StartZ=0 EndX=-1 EndY=-5.25 EndZ=0
    g40: LineSegment StartX=-1 StartY=-5.25 StartZ=0 EndX=-4.03109 EndY=-3.5 EndZ=0
    g41: Circle [constr] CenterX=-4.03109 CenterY=-7 CenterZ=0 NormalX=0 NormalY=0 NormalZ=1 AngleXU=0 Radius=3.5
    g42: LineSegment StartX=4.03109 StartY=-3.5 StartZ=0 EndX=1 EndY=-5.25 EndZ=0
    g43: LineSegment StartX=1 StartY=-5.25 StartZ=0 EndX=1 EndY=-8.75 EndZ=0
    g44: LineSegment StartX=1 StartY=-8.75 StartZ=0 EndX=4.03109 EndY=-10.5 EndZ=0
    g45: LineSegment StartX=4.03109 StartY=-10.5 StartZ=0 EndX=7.06218 EndY=-8.75 EndZ=0
    g46: LineSegment StartX=7.06218 StartY=-8.75 StartZ=0 EndX=7.06218 EndY=-5.25 EndZ=0
    g47: LineSegment StartX=7.06218 StartY=-5.25 StartZ=0 EndX=4.03109 EndY=-3.5 EndZ=0
    g48: Circle [constr] CenterX=4.03109 CenterY=-7 CenterZ=0 NormalX=0 NormalY=0 NormalZ=1 AngleXU=0 Radius=3.5
  constraints (117):
    c: Coincident(g0,g1)
    c: Coincident(g1,g2)
    c: Coincident(g2,g3)
    c: Coincident(g3,g4)
    c: Coincident(g4,g5)
    c: Coincident(g5,g0)
    c: Equal(g0, g1-g5) x5
    c: PointOnObject(g0,g6)
    c: PointOnObject(g1,g6)
    c: PointOnObject(g2,g6)
    c: PointOnObject(g3,g6)
    c: PointOnObject(g4,g6)
    c: PointOnObject(g5,g6)
    c: Coincident(g6,g-1)
    c: Diameter(g6) = 7
    c: PointOnObject(g0,g-2)
    c: Coincident(g7,g8)
    c: Coincident(g8,g9)
    c: Coincident(g9,g10)
    c: Coincident(g10,g11)
    c: Coincident(g11,g12)
    c: Coincident(g12,g7)
    c: Equal(g7, g8-g12) x5
    c: PointOnObject(g7,g13)
    c: PointOnObject(g8,g13)
    c: PointOnObject(g9,g13)
    c: PointOnObject(g10,g13)
    c: PointOnObject(g11,g13)
    c: PointOnObject(g12,g13)
    c: PointOnObject(g13,g-1)
    c: Diameter(g13) = 7
    c: Distance(g6,g13) = 8
    c: Horizontal(g0,g10)
    c: Coincident(g14,g15)
    c: Coincident(g15,g16)
    c: Coincident(g16,g17)
    c: Coincident(g17,g18)
    c: Coincident(g18,g19)
    c: Coincident(g19,g14)
    c: Equal(g14, g15-g19) x5
    c: PointOnObject(g14,g20)
    c: PointOnObject(g15,g20)
    c: PointOnObject(g16,g20)
    c: PointOnObject(g17,g20)
    c: PointOnObject(g18,g20)
    c: PointOnObject(g19,g20)
    c: Diameter(g20) = 7
    c: DistanceY(g-1,g20) = 7
    c: Vertical(g18)
    c: Distance(g17,g-2) = 1
    c: Coincident(g21,g22)
    c: Coincident(g22,g23)
    c: Coincident(g23,g24)
    c: Coincident(g24,g25)
    c: Coincident(g25,g26)
    c: Coincident(g26,g21)
    c: Equal(g21, g22-g26) x5
    c: PointOnObject(g21,g27)
    c: PointOnObject(g22,g27)
    c: PointOnObject(g23,g27)
    c: PointOnObject(g24,g27)
    c: PointOnObject(g25,g27)
    c: PointOnObject(g26,g27)
    c: Diameter(g27) = 7
    c: DistanceY(g-1,g27) = 7
    c: DistanceX(g21,g-1) = 1
    c: Vertical(g21)
    c: Coincident(g28,g29)
    c: Coincident(g29,g30)
    c: Coincident(g30,g31)
    c: Coincident(g31,g32)
    c: Coincident(g32,g33)
    c: Coincident(g33,g28)
    c: Equal(g28, g29-g33) x5
    c: PointOnObject(g28,g34)
    c: PointOnObject(g29,g34)
    c: PointOnObject(g30,g34)
    c: PointOnObject(g31,g34)
    c: PointOnObject(g32,g34)
    c: PointOnObject(g33,g34)
    c: PointOnObject(g34,g-1)
    c: Diameter(g34) = 7
    c: Vertical(g31)
    c: DistanceX(g34,g-1) = 8
    c: Coincident(g35,g36)
    c: Coincident(g36,g37)
    c: Coincident(g37,g38)
    c: Coincident(g38,g39)
    c: Coincident(g39,g40)
    c: Coincident(g40,g35)
    c: Equal(g35, g36-g40) x5
    c: PointOnObject(g35,g41)
    c: PointOnObject(g36,g41)
    c: PointOnObject(g37,g41)
    c: PointOnObject(g38,g41)
    c: PointOnObject(g39,g41)
    c: PointOnObject(g40,g41)
    c: Coincident(g42,g43)
    c: Coincident(g43,g44)
    c: Coincident(g44,g45)
    c: Coincident(g45,g46)
    c: Coincident(g46,g47)
    c: Coincident(g47,g42)
    c: Equal(g42, g43-g47) x5
    c: PointOnObject(g42,g48)
    c: PointOnObject(g43,g48)
    c: PointOnObject(g44,g48)
    c: PointOnObject(g45,g48)
    c: PointOnObject(g46,g48)
    c: PointOnObject(g47,g48)
    c: Equal(g41,g48)
    c: Diameter(g41) = 7
    c: Vertical(g39)
    c: Vertical(g43)
    c: Distance(g-2,g39) = 1
    c: Symmetric(g38,g43,g-2)
    c: Distance(g41,g-1) = 7
FEATURE [Part::Extrusion] Extrude482  label="hex097"
  Base = -> Sketch490
  Dir = (0,-1,2e-16)
  DirMode = 2
  FaceMakerClass = Part::FaceMakerBullseye
  FaceMakerMode = 3
  LengthFwd = 10
  LengthRev = 0
  Placement = pos=(-68,0,-35) rot=(0,0,1;0rad)
  Solid = true
  Symmetric = false
FEATURE [Sketcher::SketchObject] Sketch491
  ArcFitTolerance = 1e-06
  FullyConstrained = true
  MakeInternals = false
  Placement = pos=(0,0,0) rot=(1,0,0;1.5708rad)
  sketch-geometry (49):
    g0: LineSegment StartX=1e-16 StartY=3.5 StartZ=0 EndX=-3.03109 EndY=1.75 EndZ=0
    g1: LineSegment StartX=-3.03109 StartY=1.75 StartZ=0 EndX=-3.03109 EndY=-1.75 EndZ=0
    g2: LineSegment StartX=-3.03109 StartY=-1.75 StartZ=0 EndX=-1e-16 EndY=-3.5 EndZ=0
    g3: LineSegment StartX=-1e-16 StartY=-3.5 StartZ=0 EndX=3.03109 EndY=-1.75 EndZ=0
    g4: LineSegment StartX=3.03109 StartY=-1.75 StartZ=0 EndX=3.03109 EndY=1.75 EndZ=0
    g5: LineSegment StartX=3.03109 StartY=1.75 StartZ=0 EndX=1e-16 EndY=3.5 EndZ=0
    g6: Circle [constr] CenterX=0 CenterY=0 CenterZ=0 NormalX=0 NormalY=0 NormalZ=1 AngleXU=0 Radius=3.5
    g7: LineSegment StartX=4.96892 StartY=-1.75002 StartZ=0 EndX=8.00002 EndY=-3.5 EndZ=0
    g8: LineSegment StartX=8.00002 StartY=-3.5 StartZ=0 EndX=11.0311 EndY=-1.74998 EndZ=0
    g9: LineSegment StartX=11.0311 StartY=-1.74998 StartZ=0 EndX=11.0311 EndY=1.75002 EndZ=0
    g10: LineSegment StartX=11.0311 StartY=1.75002 StartZ=0 EndX=7.99998 EndY=3.5 EndZ=0
    g11: LineSegment StartX=7.99998 StartY=3.5 StartZ=0 EndX=4.9689 EndY=1.74998 EndZ=0
    g12: LineSegment StartX=4.9689 StartY=1.74998 StartZ=0 EndX=4.96892 EndY=-1.75002 EndZ=0
    g13: Circle [constr] CenterX=8 CenterY=0 CenterZ=0 NormalX=0 NormalY=0 NormalZ=1 AngleXU=0 Radius=3.5
    g14: LineSegment StartX=4.03109 StartY=3.5 StartZ=0 EndX=7.06218 EndY=5.25 EndZ=0
    g15: LineSegment StartX=7.06218 StartY=5.25 StartZ=0 EndX=7.06218 EndY=8.75 EndZ=0
    g16: LineSegment StartX=7.06218 StartY=8.75 StartZ=0 EndX=4.03109 EndY=10.5 EndZ=0
    g17: LineSegment StartX=4.03109 StartY=10.5 StartZ=0 EndX=1 EndY=8.75 EndZ=0
    g18: LineSegment StartX=1 StartY=8.75 StartZ=0 EndX=1 EndY=5.25 EndZ=0
    g19: LineSegment StartX=1 StartY=5.25 StartZ=0 EndX=4.03109 EndY=3.5 EndZ=0
    g20: Circle [constr] CenterX=4.03109 CenterY=7 CenterZ=0 NormalX=0 NormalY=0 NormalZ=1 AngleXU=0 Radius=3.5
    g21: LineSegment StartX=-1 StartY=5.25 StartZ=0 EndX=-1 EndY=8.75 EndZ=0
    g22: LineSegment StartX=-1 StartY=8.75 StartZ=0 EndX=-4.03109 EndY=10.5 EndZ=0
    g23: LineSegment StartX=-4.03109 StartY=10.5 StartZ=0 EndX=-7.06218 EndY=8.75 EndZ=0
    g24: LineSegment StartX=-7.06218 StartY=8.75 StartZ=0 EndX=-7.06218 EndY=5.25 EndZ=0
    g25: LineSegment StartX=-7.06218 StartY=5.25 StartZ=0 EndX=-4.03109 EndY=3.5 EndZ=0
    g26: LineSegment StartX=-4.03109 StartY=3.5 StartZ=0 EndX=-1 EndY=5.25 EndZ=0
    g27: Circle [constr] CenterX=-4.03109 CenterY=7 CenterZ=0 NormalX=0 NormalY=0 NormalZ=1 AngleXU=0 Radius=3.5
    g28: LineSegment StartX=-4.96891 StartY=-1.75 StartZ=0 EndX=-4.96891 EndY=1.75 EndZ=0
    g29: LineSegment StartX=-4.96891 StartY=1.75 StartZ=0 EndX=-8 EndY=3.5 EndZ=0
    g30: LineSegment StartX=-8 StartY=3.5 StartZ=0 EndX=-11.0311 EndY=1.75 EndZ=0
    g31: LineSegment StartX=-11.0311 StartY=1.75 StartZ=0 EndX=-11.0311 EndY=-1.75 EndZ=0
    g32: LineSegment StartX=-11.0311 StartY=-1.75 StartZ=0 EndX=-8 EndY=-3.5 EndZ=0
    g33: LineSegment StartX=-8 StartY=-3.5 StartZ=0 EndX=-4.96891 EndY=-1.75 EndZ=0
    g34: Circle [constr] CenterX=-8 CenterY=0 CenterZ=0 NormalX=0 NormalY=0 NormalZ=1 AngleXU=0 Radius=3.5
    g35: LineSegment StartX=-4.03109 StartY=-3.5 StartZ=0 EndX=-7.06218 EndY=-5.25 EndZ=0
    g36: LineSegment StartX=-7.06218 StartY=-5.25 StartZ=0 EndX=-7.06218 EndY=-8.75 EndZ=0
    g37: LineSegment StartX=-7.06218 StartY=-8.75 StartZ=0 EndX=-4.03109 EndY=-10.5 EndZ=0
    g38: LineSegment StartX=-4.03109 StartY=-10.5 StartZ=0 EndX=-1 EndY=-8.75 EndZ=0
    g39: LineSegment StartX=-1 StartY=-8.75 StartZ=0 EndX=-1 EndY=-5.25 EndZ=0
    g40: LineSegment StartX=-1 StartY=-5.25 StartZ=0 EndX=-4.03109 EndY=-3.5 EndZ=0
    g41: Circle [constr] CenterX=-4.03109 CenterY=-7 CenterZ=0 NormalX=0 NormalY=0 NormalZ=1 AngleXU=0 Radius=3.5
    g42: LineSegment StartX=4.03109 StartY=-3.5 StartZ=0 EndX=1 EndY=-5.25 EndZ=0
    g43: LineSegment StartX=1 StartY=-5.25 StartZ=0 EndX=1 EndY=-8.75 EndZ=0
    g44: LineSegment StartX=1 StartY=-8.75 StartZ=0 EndX=4.03109 EndY=-10.5 EndZ=0
    g45: LineSegment StartX=4.03109 StartY=-10.5 StartZ=0 EndX=7.06218 EndY=-8.75 EndZ=0
    g46: LineSegment StartX=7.06218 StartY=-8.75 StartZ=0 EndX=7.06218 EndY=-5.25 EndZ=0
    g47: LineSegment StartX=7.06218 StartY=-5.25 StartZ=0 EndX=4.03109 EndY=-3.5 EndZ=0
    g48: Circle [constr] CenterX=4.03109 CenterY=-7 CenterZ=0 NormalX=0 NormalY=0 NormalZ=1 AngleXU=0 Radius=3.5
  constraints (117):
    c: Coincident(g0,g1)
    c: Coincident(g1,g2)
    c: Coincident(g2,g3)
    c: Coincident(g3,g4)
    c: Coincident(g4,g5)
    c: Coincident(g5,g0)
    c: Equal(g0, g1-g5) x5
    c: PointOnObject(g0,g6)
    c: PointOnObject(g1,g6)
    c: PointOnObject(g2,g6)
    c: PointOnObject(g3,g6)
    c: PointOnObject(g4,g6)
    c: PointOnObject(g5,g6)
    c: Coincident(g6,g-1)
    c: Diameter(g6) = 7
    c: PointOnObject(g0,g-2)
    c: Coincident(g7,g8)
    c: Coincident(g8,g9)
    c: Coincident(g9,g10)
    c: Coincident(g10,g11)
    c: Coincident(g11,g12)
    c: Coincident(g12,g7)
    c: Equal(g7, g8-g12) x5
    c: PointOnObject(g7,g13)
    c: PointOnObject(g8,g13)
    c: PointOnObject(g9,g13)
    c: PointOnObject(g10,g13)
    c: PointOnObject(g11,g13)
    c: PointOnObject(g12,g13)
    c: PointOnObject(g13,g-1)
    c: Diameter(g13) = 7
    c: Distance(g6,g13) = 8
    c: Horizontal(g0,g10)
    c: Coincident(g14,g15)
    c: Coincident(g15,g16)
    c: Coincident(g16,g17)
    c: Coincident(g17,g18)
    c: Coincident(g18,g19)
    c: Coincident(g19,g14)
    c: Equal(g14, g15-g19) x5
    c: PointOnObject(g14,g20)
    c: PointOnObject(g15,g20)
    c: PointOnObject(g16,g20)
    c: PointOnObject(g17,g20)
    c: PointOnObject(g18,g20)
    c: PointOnObject(g19,g20)
    c: Diameter(g20) = 7
    c: DistanceY(g-1,g20) = 7
    c: Vertical(g18)
    c: Distance(g17,g-2) = 1
    c: Coincident(g21,g22)
    c: Coincident(g22,g23)
    c: Coincident(g23,g24)
    c: Coincident(g24,g25)
    c: Coincident(g25,g26)
    c: Coincident(g26,g21)
    c: Equal(g21, g22-g26) x5
    c: PointOnObject(g21,g27)
    c: PointOnObject(g22,g27)
    c: PointOnObject(g23,g27)
    c: PointOnObject(g24,g27)
    c: PointOnObject(g25,g27)
    c: PointOnObject(g26,g27)
    c: Diameter(g27) = 7
    c: DistanceY(g-1,g27) = 7
    c: DistanceX(g21,g-1) = 1
    c: Vertical(g21)
    c: Coincident(g28,g29)
    c: Coincident(g29,g30)
    c: Coincident(g30,g31)
    c: Coincident(g31,g32)
    c: Coincident(g32,g33)
    c: Coincident(g33,g28)
    c: Equal(g28, g29-g33) x5
    c: PointOnObject(g28,g34)
    c: PointOnObject(g29,g34)
    c: PointOnObject(g30,g34)
    c: PointOnObject(g31,g34)
    c: PointOnObject(g32,g34)
    c: PointOnObject(g33,g34)
    c: PointOnObject(g34,g-1)
    c: Diameter(g34) = 7
    c: Vertical(g31)
    c: DistanceX(g34,g-1) = 8
    c: Coincident(g35,g36)
    c: Coincident(g36,g37)
    c: Coincident(g37,g38)
    c: Coincident(g38,g39)
    c: Coincident(g39,g40)
    c: Coincident(g40,g35)
    c: Equal(g35, g36-g40) x5
    c: PointOnObject(g35,g41)
    c: PointOnObject(g36,g41)
    c: PointOnObject(g37,g41)
    c: PointOnObject(g38,g41)
    c: PointOnObject(g39,g41)
    c: PointOnObject(g40,g41)
    c: Coincident(g42,g43)
    c: Coincident(g43,g44)
    c: Coincident(g44,g45)
    c: Coincident(g45,g46)
    c: Coincident(g46,g47)
    c: Coincident(g47,g42)
    c: Equal(g42, g43-g47) x5
    c: PointOnObject(g42,g48)
    c: PointOnObject(g43,g48)
    c: PointOnObject(g44,g48)
    c: PointOnObject(g45,g48)
    c: PointOnObject(g46,g48)
    c: PointOnObject(g47,g48)
    c: Equal(g41,g48)
    c: Diameter(g41) = 7
    c: Vertical(g39)
    c: Vertical(g43)
    c: Distance(g-2,g39) = 1
    c: Symmetric(g38,g43,g-2)
    c: Distance(g41,g-1) = 7
FEATURE [Part::Extrusion] Extrude483  label="hex098"
  Base = -> Sketch491
  Dir = (0,-1,2e-16)
  DirMode = 2
  FaceMakerClass = Part::FaceMakerBullseye
  FaceMakerMode = 3
  LengthFwd = 10
  LengthRev = 0
  Placement = pos=(-84,0,-21) rot=(0,0,1;0rad)
  Solid = true
  Symmetric = false
FEATURE [Sketcher::SketchObject] Sketch492
  ArcFitTolerance = 1e-06
  FullyConstrained = true
  MakeInternals = false
  Placement = pos=(0,0,0) rot=(1,0,0;1.5708rad)
  sketch-geometry (49):
    g0: LineSegment StartX=1e-16 StartY=3.5 StartZ=0 EndX=-3.03109 EndY=1.75 EndZ=0
    g1: LineSegment StartX=-3.03109 StartY=1.75 StartZ=0 EndX=-3.03109 EndY=-1.75 EndZ=0
    g2: LineSegment StartX=-3.03109 StartY=-1.75 StartZ=0 EndX=-1e-16 EndY=-3.5 EndZ=0
    g3: LineSegment StartX=-1e-16 StartY=-3.5 StartZ=0 EndX=3.03109 EndY=-1.75 EndZ=0
    g4: LineSegment StartX=3.03109 StartY=-1.75 StartZ=0 EndX=3.03109 EndY=1.75 EndZ=0
    g5: LineSegment StartX=3.03109 StartY=1.75 StartZ=0 EndX=1e-16 EndY=3.5 EndZ=0
    g6: Circle [constr] CenterX=0 CenterY=0 CenterZ=0 NormalX=0 NormalY=0 NormalZ=1 AngleXU=0 Radius=3.5
    g7: LineSegment StartX=4.96892 StartY=-1.75002 StartZ=0 EndX=8.00002 EndY=-3.5 EndZ=0
    g8: LineSegment StartX=8.00002 StartY=-3.5 StartZ=0 EndX=11.0311 EndY=-1.74998 EndZ=0
    g9: LineSegment StartX=11.0311 StartY=-1.74998 StartZ=0 EndX=11.0311 EndY=1.75002 EndZ=0
    g10: LineSegment StartX=11.0311 StartY=1.75002 StartZ=0 EndX=7.99998 EndY=3.5 EndZ=0
    g11: LineSegment StartX=7.99998 StartY=3.5 StartZ=0 EndX=4.9689 EndY=1.74998 EndZ=0
    g12: LineSegment StartX=4.9689 StartY=1.74998 StartZ=0 EndX=4.96892 EndY=-1.75002 EndZ=0
    g13: Circle [constr] CenterX=8 CenterY=0 CenterZ=0 NormalX=0 NormalY=0 NormalZ=1 AngleXU=0 Radius=3.5
    g14: LineSegment StartX=4.03109 StartY=3.5 StartZ=0 EndX=7.06218 EndY=5.25 EndZ=0
    g15: LineSegment StartX=7.06218 StartY=5.25 StartZ=0 EndX=7.06218 EndY=8.75 EndZ=0
    g16: LineSegment StartX=7.06218 StartY=8.75 StartZ=0 EndX=4.03109 EndY=10.5 EndZ=0
    g17: LineSegment StartX=4.03109 StartY=10.5 StartZ=0 EndX=1 EndY=8.75 EndZ=0
    g18: LineSegment StartX=1 StartY=8.75 StartZ=0 EndX=1 EndY=5.25 EndZ=0
    g19: LineSegment StartX=1 StartY=5.25 StartZ=0 EndX=4.03109 EndY=3.5 EndZ=0
    g20: Circle [constr] CenterX=4.03109 CenterY=7 CenterZ=0 NormalX=0 NormalY=0 NormalZ=1 AngleXU=0 Radius=3.5
    g21: LineSegment StartX=-1 StartY=5.25 StartZ=0 EndX=-1 EndY=8.75 EndZ=0
    g22: LineSegment StartX=-1 StartY=8.75 StartZ=0 EndX=-4.03109 EndY=10.5 EndZ=0
    g23: LineSegment StartX=-4.03109 StartY=10.5 StartZ=0 EndX=-7.06218 EndY=8.75 EndZ=0
    g24: LineSegment StartX=-7.06218 StartY=8.75 StartZ=0 EndX=-7.06218 EndY=5.25 EndZ=0
    g25: LineSegment StartX=-7.06218 StartY=5.25 StartZ=0 EndX=-4.03109 EndY=3.5 EndZ=0
    g26: LineSegment StartX=-4.03109 StartY=3.5 StartZ=0 EndX=-1 EndY=5.25 EndZ=0
    g27: Circle [constr] CenterX=-4.03109 CenterY=7 CenterZ=0 NormalX=0 NormalY=0 NormalZ=1 AngleXU=0 Radius=3.5
    g28: LineSegment StartX=-4.96891 StartY=-1.75 StartZ=0 EndX=-4.96891 EndY=1.75 EndZ=0
    g29: LineSegment StartX=-4.96891 StartY=1.75 StartZ=0 EndX=-8 EndY=3.5 EndZ=0
    g30: LineSegment StartX=-8 StartY=3.5 StartZ=0 EndX=-11.0311 EndY=1.75 EndZ=0
    g31: LineSegment StartX=-11.0311 StartY=1.75 StartZ=0 EndX=-11.0311 EndY=-1.75 EndZ=0
    g32: LineSegment StartX=-11.0311 StartY=-1.75 StartZ=0 EndX=-8 EndY=-3.5 EndZ=0
    g33: LineSegment StartX=-8 StartY=-3.5 StartZ=0 EndX=-4.96891 EndY=-1.75 EndZ=0
    g34: Circle [constr] CenterX=-8 CenterY=0 CenterZ=0 NormalX=0 NormalY=0 NormalZ=1 AngleXU=0 Radius=3.5
    g35: LineSegment StartX=-4.03109 StartY=-3.5 StartZ=0 EndX=-7.06218 EndY=-5.25 EndZ=0
    g36: LineSegment StartX=-7.06218 StartY=-5.25 StartZ=0 EndX=-7.06218 EndY=-8.75 EndZ=0
    g37: LineSegment StartX=-7.06218 StartY=-8.75 StartZ=0 EndX=-4.03109 EndY=-10.5 EndZ=0
    g38: LineSegment StartX=-4.03109 StartY=-10.5 StartZ=0 EndX=-1 EndY=-8.75 EndZ=0
    g39: LineSegment StartX=-1 StartY=-8.75 StartZ=0 EndX=-1 EndY=-5.25 EndZ=0
    g40: LineSegment StartX=-1 StartY=-5.25 StartZ=0 EndX=-4.03109 EndY=-3.5 EndZ=0
    g41: Circle [constr] CenterX=-4.03109 CenterY=-7 CenterZ=0 NormalX=0 NormalY=0 NormalZ=1 AngleXU=0 Radius=3.5
    g42: LineSegment StartX=4.03109 StartY=-3.5 StartZ=0 EndX=1 EndY=-5.25 EndZ=0
    g43: LineSegment StartX=1 StartY=-5.25 StartZ=0 EndX=1 EndY=-8.75 EndZ=0
    g44: LineSegment StartX=1 StartY=-8.75 StartZ=0 EndX=4.03109 EndY=-10.5 EndZ=0
    g45: LineSegment StartX=4.03109 StartY=-10.5 StartZ=0 EndX=7.06218 EndY=-8.75 EndZ=0
    g46: LineSegment StartX=7.06218 StartY=-8.75 StartZ=0 EndX=7.06218 EndY=-5.25 EndZ=0
    g47: LineSegment StartX=7.06218 StartY=-5.25 StartZ=0 EndX=4.03109 EndY=-3.5 EndZ=0
    g48: Circle [constr] CenterX=4.03109 CenterY=-7 CenterZ=0 NormalX=0 NormalY=0 NormalZ=1 AngleXU=0 Radius=3.5
  constraints (117):
    c: Coincident(g0,g1)
    c: Coincident(g1,g2)
    c: Coincident(g2,g3)
    c: Coincident(g3,g4)
    c: Coincident(g4,g5)
    c: Coincident(g5,g0)
    c: Equal(g0, g1-g5) x5
    c: PointOnObject(g0,g6)
    c: PointOnObject(g1,g6)
    c: PointOnObject(g2,g6)
    c: PointOnObject(g3,g6)
    c: PointOnObject(g4,g6)
    c: PointOnObject(g5,g6)
    c: Coincident(g6,g-1)
    c: Diameter(g6) = 7
    c: PointOnObject(g0,g-2)
    c: Coincident(g7,g8)
    c: Coincident(g8,g9)
    c: Coincident(g9,g10)
    c: Coincident(g10,g11)
    c: Coincident(g11,g12)
    c: Coincident(g12,g7)
    c: Equal(g7, g8-g12) x5
    c: PointOnObject(g7,g13)
    c: PointOnObject(g8,g13)
    c: PointOnObject(g9,g13)
    c: PointOnObject(g10,g13)
    c: PointOnObject(g11,g13)
    c: PointOnObject(g12,g13)
    c: PointOnObject(g13,g-1)
    c: Diameter(g13) = 7
    c: Distance(g6,g13) = 8
    c: Horizontal(g0,g10)
    c: Coincident(g14,g15)
    c: Coincident(g15,g16)
    c: Coincident(g16,g17)
    c: Coincident(g17,g18)
    c: Coincident(g18,g19)
    c: Coincident(g19,g14)
    c: Equal(g14, g15-g19) x5
    c: PointOnObject(g14,g20)
    c: PointOnObject(g15,g20)
    c: PointOnObject(g16,g20)
    c: PointOnObject(g17,g20)
    c: PointOnObject(g18,g20)
    c: PointOnObject(g19,g20)
    c: Diameter(g20) = 7
    c: DistanceY(g-1,g20) = 7
    c: Vertical(g18)
    c: Distance(g17,g-2) = 1
    c: Coincident(g21,g22)
    c: Coincident(g22,g23)
    c: Coincident(g23,g24)
    c: Coincident(g24,g25)
    c: Coincident(g25,g26)
    c: Coincident(g26,g21)
    c: Equal(g21, g22-g26) x5
    c: PointOnObject(g21,g27)
    c: PointOnObject(g22,g27)
    c: PointOnObject(g23,g27)
    c: PointOnObject(g24,g27)
    c: PointOnObject(g25,g27)
    c: PointOnObject(g26,g27)
    c: Diameter(g27) = 7
    c: DistanceY(g-1,g27) = 7
    c: DistanceX(g21,g-1) = 1
    c: Vertical(g21)
    c: Coincident(g28,g29)
    c: Coincident(g29,g30)
    c: Coincident(g30,g31)
    c: Coincident(g31,g32)
    c: Coincident(g32,g33)
    c: Coincident(g33,g28)
    c: Equal(g28, g29-g33) x5
    c: PointOnObject(g28,g34)
    c: PointOnObject(g29,g34)
    c: PointOnObject(g30,g34)
    c: PointOnObject(g31,g34)
    c: PointOnObject(g32,g34)
    c: PointOnObject(g33,g34)
    c: PointOnObject(g34,g-1)
    c: Diameter(g34) = 7
    c: Vertical(g31)
    c: DistanceX(g34,g-1) = 8
    c: Coincident(g35,g36)
    c: Coincident(g36,g37)
    c: Coincident(g37,g38)
    c: Coincident(g38,g39)
    c: Coincident(g39,g40)
    c: Coincident(g40,g35)
    c: Equal(g35, g36-g40) x5
    c: PointOnObject(g35,g41)
    c: PointOnObject(g36,g41)
    c: PointOnObject(g37,g41)
    c: PointOnObject(g38,g41)
    c: PointOnObject(g39,g41)
    c: PointOnObject(g40,g41)
    c: Coincident(g42,g43)
    c: Coincident(g43,g44)
    c: Coincident(g44,g45)
    c: Coincident(g45,g46)
    c: Coincident(g46,g47)
    c: Coincident(g47,g42)
    c: Equal(g42, g43-g47) x5
    c: PointOnObject(g42,g48)
    c: PointOnObject(g43,g48)
    c: PointOnObject(g44,g48)
    c: PointOnObject(g45,g48)
    c: PointOnObject(g46,g48)
    c: PointOnObject(g47,g48)
    c: Equal(g41,g48)
    c: Diameter(g41) = 7
    c: Vertical(g39)
    c: Vertical(g43)
    c: Distance(g-2,g39) = 1
    c: Symmetric(g38,g43,g-2)
    c: Distance(g41,g-1) = 7
FEATURE [Part::Extrusion] Extrude484  label="hex099"
  Base = -> Sketch492
  Dir = (0,-1,2e-16)
  DirMode = 2
  FaceMakerClass = Part::FaceMakerBullseye
  FaceMakerMode = 3
  LengthFwd = 10
  LengthRev = 0
  Placement = pos=(-88,0,14) rot=(0,0,1;0rad)
  Solid = true
  Symmetric = false
FEATURE [Sketcher::SketchObject] Sketch493
  ArcFitTolerance = 1e-06
  FullyConstrained = true
  MakeInternals = false
  Placement = pos=(0,0,0) rot=(1,0,0;1.5708rad)
  sketch-geometry (49):
    g0: LineSegment StartX=1e-16 StartY=3.5 StartZ=0 EndX=-3.03109 EndY=1.75 EndZ=0
    g1: LineSegment StartX=-3.03109 StartY=1.75 StartZ=0 EndX=-3.03109 EndY=-1.75 EndZ=0
    g2: LineSegment StartX=-3.03109 StartY=-1.75 StartZ=0 EndX=-1e-16 EndY=-3.5 EndZ=0
    g3: LineSegment StartX=-1e-16 StartY=-3.5 StartZ=0 EndX=3.03109 EndY=-1.75 EndZ=0
    g4: LineSegment StartX=3.03109 StartY=-1.75 StartZ=0 EndX=3.03109 EndY=1.75 EndZ=0
    g5: LineSegment StartX=3.03109 StartY=1.75 StartZ=0 EndX=1e-16 EndY=3.5 EndZ=0
    g6: Circle [constr] CenterX=0 CenterY=0 CenterZ=0 NormalX=0 NormalY=0 NormalZ=1 AngleXU=0 Radius=3.5
    g7: LineSegment StartX=4.96892 StartY=-1.75002 StartZ=0 EndX=8.00002 EndY=-3.5 EndZ=0
    g8: LineSegment StartX=8.00002 StartY=-3.5 StartZ=0 EndX=11.0311 EndY=-1.74998 EndZ=0
    g9: LineSegment StartX=11.0311 StartY=-1.74998 StartZ=0 EndX=11.0311 EndY=1.75002 EndZ=0
    g10: LineSegment StartX=11.0311 StartY=1.75002 StartZ=0 EndX=7.99998 EndY=3.5 EndZ=0
    g11: LineSegment StartX=7.99998 StartY=3.5 StartZ=0 EndX=4.9689 EndY=1.74998 EndZ=0
    g12: LineSegment StartX=4.9689 StartY=1.74998 StartZ=0 EndX=4.96892 EndY=-1.75002 EndZ=0
    g13: Circle [constr] CenterX=8 CenterY=0 CenterZ=0 NormalX=0 NormalY=0 NormalZ=1 AngleXU=0 Radius=3.5
    g14: LineSegment StartX=4.03109 StartY=3.5 StartZ=0 EndX=7.06218 EndY=5.25 EndZ=0
    g15: LineSegment StartX=7.06218 StartY=5.25 StartZ=0 EndX=7.06218 EndY=8.75 EndZ=0
    g16: LineSegment StartX=7.06218 StartY=8.75 StartZ=0 EndX=4.03109 EndY=10.5 EndZ=0
    g17: LineSegment StartX=4.03109 StartY=10.5 StartZ=0 EndX=1 EndY=8.75 EndZ=0
    g18: LineSegment StartX=1 StartY=8.75 StartZ=0 EndX=1 EndY=5.25 EndZ=0
    g19: LineSegment StartX=1 StartY=5.25 StartZ=0 EndX=4.03109 EndY=3.5 EndZ=0
    g20: Circle [constr] CenterX=4.03109 CenterY=7 CenterZ=0 NormalX=0 NormalY=0 NormalZ=1 AngleXU=0 Radius=3.5
    g21: LineSegment StartX=-1 StartY=5.25 StartZ=0 EndX=-1 EndY=8.75 EndZ=0
    g22: LineSegment StartX=-1 StartY=8.75 StartZ=0 EndX=-4.03109 EndY=10.5 EndZ=0
    g23: LineSegment StartX=-4.03109 StartY=10.5 StartZ=0 EndX=-7.06218 EndY=8.75 EndZ=0
    g24: LineSegment StartX=-7.06218 StartY=8.75 StartZ=0 EndX=-7.06218 EndY=5.25 EndZ=0
    g25: LineSegment StartX=-7.06218 StartY=5.25 StartZ=0 EndX=-4.03109 EndY=3.5 EndZ=0
    g26: LineSegment StartX=-4.03109 StartY=3.5 StartZ=0 EndX=-1 EndY=5.25 EndZ=0
    g27: Circle [constr] CenterX=-4.03109 CenterY=7 CenterZ=0 NormalX=0 NormalY=0 NormalZ=1 AngleXU=0 Radius=3.5
    g28: LineSegment StartX=-4.96891 StartY=-1.75 StartZ=0 EndX=-4.96891 EndY=1.75 EndZ=0
    g29: LineSegment StartX=-4.96891 StartY=1.75 StartZ=0 EndX=-8 EndY=3.5 EndZ=0
    g30: LineSegment StartX=-8 StartY=3.5 StartZ=0 EndX=-11.0311 EndY=1.75 EndZ=0
    g31: LineSegment StartX=-11.0311 StartY=1.75 StartZ=0 EndX=-11.0311 EndY=-1.75 EndZ=0
    g32: LineSegment StartX=-11.0311 StartY=-1.75 StartZ=0 EndX=-8 EndY=-3.5 EndZ=0
    g33: LineSegment StartX=-8 StartY=-3.5 StartZ=0 EndX=-4.96891 EndY=-1.75 EndZ=0
    g34: Circle [constr] CenterX=-8 CenterY=0 CenterZ=0 NormalX=0 NormalY=0 NormalZ=1 AngleXU=0 Radius=3.5
    g35: LineSegment StartX=-4.03109 StartY=-3.5 StartZ=0 EndX=-7.06218 EndY=-5.25 EndZ=0
    g36: LineSegment StartX=-7.06218 StartY=-5.25 StartZ=0 EndX=-7.06218 EndY=-8.75 EndZ=0
    g37: LineSegment StartX=-7.06218 StartY=-8.75 StartZ=0 EndX=-4.03109 EndY=-10.5 EndZ=0
    g38: LineSegment StartX=-4.03109 StartY=-10.5 StartZ=0 EndX=-1 EndY=-8.75 EndZ=0
    g39: LineSegment StartX=-1 StartY=-8.75 StartZ=0 EndX=-1 EndY=-5.25 EndZ=0
    g40: LineSegment StartX=-1 StartY=-5.25 StartZ=0 EndX=-4.03109 EndY=-3.5 EndZ=0
    g41: Circle [constr] CenterX=-4.03109 CenterY=-7 CenterZ=0 NormalX=0 NormalY=0 NormalZ=1 AngleXU=0 Radius=3.5
    g42: LineSegment StartX=4.03109 StartY=-3.5 StartZ=0 EndX=1 EndY=-5.25 EndZ=0
    g43: LineSegment StartX=1 StartY=-5.25 StartZ=0 EndX=1 EndY=-8.75 EndZ=0
    g44: LineSegment StartX=1 StartY=-8.75 StartZ=0 EndX=4.03109 EndY=-10.5 EndZ=0
    g45: LineSegment StartX=4.03109 StartY=-10.5 StartZ=0 EndX=7.06218 EndY=-8.75 EndZ=0
    g46: LineSegment StartX=7.06218 StartY=-8.75 StartZ=0 EndX=7.06218 EndY=-5.25 EndZ=0
    g47: LineSegment StartX=7.06218 StartY=-5.25 StartZ=0 EndX=4.03109 EndY=-3.5 EndZ=0
    g48: Circle [constr] CenterX=4.03109 CenterY=-7 CenterZ=0 NormalX=0 NormalY=0 NormalZ=1 AngleXU=0 Radius=3.5
  constraints (117):
    c: Coincident(g0,g1)
    c: Coincident(g1,g2)
    c: Coincident(g2,g3)
    c: Coincident(g3,g4)
    c: Coincident(g4,g5)
    c: Coincident(g5,g0)
    c: Equal(g0, g1-g5) x5
    c: PointOnObject(g0,g6)
    c: PointOnObject(g1,g6)
    c: PointOnObject(g2,g6)
    c: PointOnObject(g3,g6)
    c: PointOnObject(g4,g6)
    c: PointOnObject(g5,g6)
    c: Coincident(g6,g-1)
    c: Diameter(g6) = 7
    c: PointOnObject(g0,g-2)
    c: Coincident(g7,g8)
    c: Coincident(g8,g9)
    c: Coincident(g9,g10)
    c: Coincident(g10,g11)
    c: Coincident(g11,g12)
    c: Coincident(g12,g7)
    c: Equal(g7, g8-g12) x5
    c: PointOnObject(g7,g13)
    c: PointOnObject(g8,g13)
    c: PointOnObject(g9,g13)
    c: PointOnObject(g10,g13)
    c: PointOnObject(g11,g13)
    c: PointOnObject(g12,g13)
    c: PointOnObject(g13,g-1)
    c: Diameter(g13) = 7
    c: Distance(g6,g13) = 8
    c: Horizontal(g0,g10)
    c: Coincident(g14,g15)
    c: Coincident(g15,g16)
    c: Coincident(g16,g17)
    c: Coincident(g17,g18)
    c: Coincident(g18,g19)
    c: Coincident(g19,g14)
    c: Equal(g14, g15-g19) x5
    c: PointOnObject(g14,g20)
    c: PointOnObject(g15,g20)
    c: PointOnObject(g16,g20)
    c: PointOnObject(g17,g20)
    c: PointOnObject(g18,g20)
    c: PointOnObject(g19,g20)
    c: Diameter(g20) = 7
    c: DistanceY(g-1,g20) = 7
    c: Vertical(g18)
    c: Distance(g17,g-2) = 1
    c: Coincident(g21,g22)
    c: Coincident(g22,g23)
    c: Coincident(g23,g24)
    c: Coincident(g24,g25)
    c: Coincident(g25,g26)
    c: Coincident(g26,g21)
    c: Equal(g21, g22-g26) x5
    c: PointOnObject(g21,g27)
    c: PointOnObject(g22,g27)
    c: PointOnObject(g23,g27)
    c: PointOnObject(g24,g27)
    c: PointOnObject(g25,g27)
    c: PointOnObject(g26,g27)
    c: Diameter(g27) = 7
    c: DistanceY(g-1,g27) = 7
    c: DistanceX(g21,g-1) = 1
    c: Vertical(g21)
    c: Coincident(g28,g29)
    c: Coincident(g29,g30)
    c: Coincident(g30,g31)
    c: Coincident(g31,g32)
    c: Coincident(g32,g33)
    c: Coincident(g33,g28)
    c: Equal(g28, g29-g33) x5
    c: PointOnObject(g28,g34)
    c: PointOnObject(g29,g34)
    c: PointOnObject(g30,g34)
    c: PointOnObject(g31,g34)
    c: PointOnObject(g32,g34)
    c: PointOnObject(g33,g34)
    c: PointOnObject(g34,g-1)
    c: Diameter(g34) = 7
    c: Vertical(g31)
    c: DistanceX(g34,g-1) = 8
    c: Coincident(g35,g36)
    c: Coincident(g36,g37)
    c: Coincident(g37,g38)
    c: Coincident(g38,g39)
    c: Coincident(g39,g40)
    c: Coincident(g40,g35)
    c: Equal(g35, g36-g40) x5
    c: PointOnObject(g35,g41)
    c: PointOnObject(g36,g41)
    c: PointOnObject(g37,g41)
    c: PointOnObject(g38,g41)
    c: PointOnObject(g39,g41)
    c: PointOnObject(g40,g41)
    c: Coincident(g42,g43)
    c: Coincident(g43,g44)
    c: Coincident(g44,g45)
    c: Coincident(g45,g46)
    c: Coincident(g46,g47)
    c: Coincident(g47,g42)
    c: Equal(g42, g43-g47) x5
    c: PointOnObject(g42,g48)
    c: PointOnObject(g43,g48)
    c: PointOnObject(g44,g48)
    c: PointOnObject(g45,g48)
    c: PointOnObject(g46,g48)
    c: PointOnObject(g47,g48)
    c: Equal(g41,g48)
    c: Diameter(g41) = 7
    c: Vertical(g39)
    c: Vertical(g43)
    c: Distance(g-2,g39) = 1
    c: Symmetric(g38,g43,g-2)
    c: Distance(g41,g-1) = 7
FEATURE [Part::Extrusion] Extrude485  label="hex100"
  Base = -> Sketch493
  Dir = (0,-1,2e-16)
  DirMode = 2
  FaceMakerClass = Part::FaceMakerBullseye
  FaceMakerMode = 3
  LengthFwd = 10
  LengthRev = 0
  Placement = pos=(96,0,14) rot=(0,0,1;0rad)
  Solid = true
  Symmetric = false
FEATURE [Part::MultiFuse] Fusion548
  Placement = pos=(0,0,56) rot=(0,0,1;0rad)
  Refine = true
  Shapes = -> [Extrude436,Extrude437,Extrude438,Extrude439,Extrude440,Extrude441,Extrude442,Extrude443,Extrude444,Extrude445,Extrude446,Extrude447,Extrude448,Extrude449,Extrude450,Extrude451,Extrude452,Extrude453,Extrude454,Extrude455,Extrude456,Extrude457,Extrude458,Extrude459,Extrude460,Extrude461,Extrude462,Extrude463,Extrude464,Extrude465,Extrude466,Extrude467,Extrude468,Extrude469,Extrude470,Extrude471,+14 more]
FEATURE [Sketcher::SketchObject] Sketch494
  ArcFitTolerance = 1e-06
  FullyConstrained = true
  MakeInternals = false
  Placement = pos=(0,0,0) rot=(1,0,0;1.5708rad)
  sketch-geometry (49):
    g0: LineSegment StartX=1e-16 StartY=3.5 StartZ=0 EndX=-3.03109 EndY=1.75 EndZ=0
    g1: LineSegment StartX=-3.03109 StartY=1.75 StartZ=0 EndX=-3.03109 EndY=-1.75 EndZ=0
    g2: LineSegment StartX=-3.03109 StartY=-1.75 StartZ=0 EndX=-1e-16 EndY=-3.5 EndZ=0
    g3: LineSegment StartX=-1e-16 StartY=-3.5 StartZ=0 EndX=3.03109 EndY=-1.75 EndZ=0
    g4: LineSegment StartX=3.03109 StartY=-1.75 StartZ=0 EndX=3.03109 EndY=1.75 EndZ=0
    g5: LineSegment StartX=3.03109 StartY=1.75 StartZ=0 EndX=1e-16 EndY=3.5 EndZ=0
    g6: Circle [constr] CenterX=0 CenterY=0 CenterZ=0 NormalX=0 NormalY=0 NormalZ=1 AngleXU=0 Radius=3.5
    g7: LineSegment StartX=4.96892 StartY=-1.75002 StartZ=0 EndX=8.00002 EndY=-3.5 EndZ=0
    g8: LineSegment StartX=8.00002 StartY=-3.5 StartZ=0 EndX=11.0311 EndY=-1.74998 EndZ=0
    g9: LineSegment StartX=11.0311 StartY=-1.74998 StartZ=0 EndX=11.0311 EndY=1.75002 EndZ=0
    g10: LineSegment StartX=11.0311 StartY=1.75002 StartZ=0 EndX=7.99998 EndY=3.5 EndZ=0
    g11: LineSegment StartX=7.99998 StartY=3.5 StartZ=0 EndX=4.9689 EndY=1.74998 EndZ=0
    g12: LineSegment StartX=4.9689 StartY=1.74998 StartZ=0 EndX=4.96892 EndY=-1.75002 EndZ=0
    g13: Circle [constr] CenterX=8 CenterY=0 CenterZ=0 NormalX=0 NormalY=0 NormalZ=1 AngleXU=0 Radius=3.5
    g14: LineSegment StartX=4.03109 StartY=3.5 StartZ=0 EndX=7.06218 EndY=5.25 EndZ=0
    g15: LineSegment StartX=7.06218 StartY=5.25 StartZ=0 EndX=7.06218 EndY=8.75 EndZ=0
    g16: LineSegment StartX=7.06218 StartY=8.75 StartZ=0 EndX=4.03109 EndY=10.5 EndZ=0
    g17: LineSegment StartX=4.03109 StartY=10.5 StartZ=0 EndX=1 EndY=8.75 EndZ=0
    g18: LineSegment StartX=1 StartY=8.75 StartZ=0 EndX=1 EndY=5.25 EndZ=0
    g19: LineSegment StartX=1 StartY=5.25 StartZ=0 EndX=4.03109 EndY=3.5 EndZ=0
    g20: Circle [constr] CenterX=4.03109 CenterY=7 CenterZ=0 NormalX=0 NormalY=0 NormalZ=1 AngleXU=0 Radius=3.5
    g21: LineSegment StartX=-1 StartY=5.25 StartZ=0 EndX=-1 EndY=8.75 EndZ=0
    g22: LineSegment StartX=-1 StartY=8.75 StartZ=0 EndX=-4.03109 EndY=10.5 EndZ=0
    g23: LineSegment StartX=-4.03109 StartY=10.5 StartZ=0 EndX=-7.06218 EndY=8.75 EndZ=0
    g24: LineSegment StartX=-7.06218 StartY=8.75 StartZ=0 EndX=-7.06218 EndY=5.25 EndZ=0
    g25: LineSegment StartX=-7.06218 StartY=5.25 StartZ=0 EndX=-4.03109 EndY=3.5 EndZ=0
    g26: LineSegment StartX=-4.03109 StartY=3.5 StartZ=0 EndX=-1 EndY=5.25 EndZ=0
    g27: Circle [constr] CenterX=-4.03109 CenterY=7 CenterZ=0 NormalX=0 NormalY=0 NormalZ=1 AngleXU=0 Radius=3.5
    g28: LineSegment StartX=-4.96891 StartY=-1.75 StartZ=0 EndX=-4.96891 EndY=1.75 EndZ=0
    g29: LineSegment StartX=-4.96891 StartY=1.75 StartZ=0 EndX=-8 EndY=3.5 EndZ=0
    g30: LineSegment StartX=-8 StartY=3.5 StartZ=0 EndX=-11.0311 EndY=1.75 EndZ=0
    g31: LineSegment StartX=-11.0311 StartY=1.75 StartZ=0 EndX=-11.0311 EndY=-1.75 EndZ=0
    g32: LineSegment StartX=-11.0311 StartY=-1.75 StartZ=0 EndX=-8 EndY=-3.5 EndZ=0
    g33: LineSegment StartX=-8 StartY=-3.5 StartZ=0 EndX=-4.96891 EndY=-1.75 EndZ=0
    g34: Circle [constr] CenterX=-8 CenterY=0 CenterZ=0 NormalX=0 NormalY=0 NormalZ=1 AngleXU=0 Radius=3.5
    g35: LineSegment StartX=-4.03109 StartY=-3.5 StartZ=0 EndX=-7.06218 EndY=-5.25 EndZ=0
    g36: LineSegment StartX=-7.06218 StartY=-5.25 StartZ=0 EndX=-7.06218 EndY=-8.75 EndZ=0
    g37: LineSegment StartX=-7.06218 StartY=-8.75 StartZ=0 EndX=-4.03109 EndY=-10.5 EndZ=0
    g38: LineSegment StartX=-4.03109 StartY=-10.5 StartZ=0 EndX=-1 EndY=-8.75 EndZ=0
    g39: LineSegment StartX=-1 StartY=-8.75 StartZ=0 EndX=-1 EndY=-5.25 EndZ=0
    g40: LineSegment StartX=-1 StartY=-5.25 StartZ=0 EndX=-4.03109 EndY=-3.5 EndZ=0
    g41: Circle [constr] CenterX=-4.03109 CenterY=-7 CenterZ=0 NormalX=0 NormalY=0 NormalZ=1 AngleXU=0 Radius=3.5
    g42: LineSegment StartX=4.03109 StartY=-3.5 StartZ=0 EndX=1 EndY=-5.25 EndZ=0
    g43: LineSegment StartX=1 StartY=-5.25 StartZ=0 EndX=1 EndY=-8.75 EndZ=0
    g44: LineSegment StartX=1 StartY=-8.75 StartZ=0 EndX=4.03109 EndY=-10.5 EndZ=0
    g45: LineSegment StartX=4.03109 StartY=-10.5 StartZ=0 EndX=7.06218 EndY=-8.75 EndZ=0
    g46: LineSegment StartX=7.06218 StartY=-8.75 StartZ=0 EndX=7.06218 EndY=-5.25 EndZ=0
    g47: LineSegment StartX=7.06218 StartY=-5.25 StartZ=0 EndX=4.03109 EndY=-3.5 EndZ=0
    g48: Circle [constr] CenterX=4.03109 CenterY=-7 CenterZ=0 NormalX=0 NormalY=0 NormalZ=1 AngleXU=0 Radius=3.5
  constraints (117):
    c: Coincident(g0,g1)
    c: Coincident(g1,g2)
    c: Coincident(g2,g3)
    c: Coincident(g3,g4)
    c: Coincident(g4,g5)
    c: Coincident(g5,g0)
    c: Equal(g0, g1-g5) x5
    c: PointOnObject(g0,g6)
    c: PointOnObject(g1,g6)
    c: PointOnObject(g2,g6)
    c: PointOnObject(g3,g6)
    c: PointOnObject(g4,g6)
    c: PointOnObject(g5,g6)
    c: Coincident(g6,g-1)
    c: Diameter(g6) = 7
    c: PointOnObject(g0,g-2)
    c: Coincident(g7,g8)
    c: Coincident(g8,g9)
    c: Coincident(g9,g10)
    c: Coincident(g10,g11)
    c: Coincident(g11,g12)
    c: Coincident(g12,g7)
    c: Equal(g7, g8-g12) x5
    c: PointOnObject(g7,g13)
    c: PointOnObject(g8,g13)
    c: PointOnObject(g9,g13)
    c: PointOnObject(g10,g13)
    c: PointOnObject(g11,g13)
    c: PointOnObject(g12,g13)
    c: PointOnObject(g13,g-1)
    c: Diameter(g13) = 7
    c: Distance(g6,g13) = 8
    c: Horizontal(g0,g10)
    c: Coincident(g14,g15)
    c: Coincident(g15,g16)
    c: Coincident(g16,g17)
    c: Coincident(g17,g18)
    c: Coincident(g18,g19)
    c: Coincident(g19,g14)
    c: Equal(g14, g15-g19) x5
    c: PointOnObject(g14,g20)
    c: PointOnObject(g15,g20)
    c: PointOnObject(g16,g20)
    c: PointOnObject(g17,g20)
    c: PointOnObject(g18,g20)
    c: PointOnObject(g19,g20)
    c: Diameter(g20) = 7
    c: DistanceY(g-1,g20) = 7
    c: Vertical(g18)
    c: Distance(g17,g-2) = 1
    c: Coincident(g21,g22)
    c: Coincident(g22,g23)
    c: Coincident(g23,g24)
    c: Coincident(g24,g25)
    c: Coincident(g25,g26)
    c: Coincident(g26,g21)
    c: Equal(g21, g22-g26) x5
    c: PointOnObject(g21,g27)
    c: PointOnObject(g22,g27)
    c: PointOnObject(g23,g27)
    c: PointOnObject(g24,g27)
    c: PointOnObject(g25,g27)
    c: PointOnObject(g26,g27)
    c: Diameter(g27) = 7
    c: DistanceY(g-1,g27) = 7
    c: DistanceX(g21,g-1) = 1
    c: Vertical(g21)
    c: Coincident(g28,g29)
    c: Coincident(g29,g30)
    c: Coincident(g30,g31)
    c: Coincident(g31,g32)
    c: Coincident(g32,g33)
    c: Coincident(g33,g28)
    c: Equal(g28, g29-g33) x5
    c: PointOnObject(g28,g34)
    c: PointOnObject(g29,g34)
    c: PointOnObject(g30,g34)
    c: PointOnObject(g31,g34)
    c: PointOnObject(g32,g34)
    c: PointOnObject(g33,g34)
    c: PointOnObject(g34,g-1)
    c: Diameter(g34) = 7
    c: Vertical(g31)
    c: DistanceX(g34,g-1) = 8
    c: Coincident(g35,g36)
    c: Coincident(g36,g37)
    c: Coincident(g37,g38)
    c: Coincident(g38,g39)
    c: Coincident(g39,g40)
    c: Coincident(g40,g35)
    c: Equal(g35, g36-g40) x5
    c: PointOnObject(g35,g41)
    c: PointOnObject(g36,g41)
    c: PointOnObject(g37,g41)
    c: PointOnObject(g38,g41)
    c: PointOnObject(g39,g41)
    c: PointOnObject(g40,g41)
    c: Coincident(g42,g43)
    c: Coincident(g43,g44)
    c: Coincident(g44,g45)
    c: Coincident(g45,g46)
    c: Coincident(g46,g47)
    c: Coincident(g47,g42)
    c: Equal(g42, g43-g47) x5
    c: PointOnObject(g42,g48)
    c: PointOnObject(g43,g48)
    c: PointOnObject(g44,g48)
    c: PointOnObject(g45,g48)
    c: PointOnObject(g46,g48)
    c: PointOnObject(g47,g48)
    c: Equal(g41,g48)
    c: Diameter(g41) = 7
    c: Vertical(g39)
    c: Vertical(g43)
    c: Distance(g-2,g39) = 1
    c: Symmetric(g38,g43,g-2)
    c: Distance(g41,g-1) = 7
FEATURE [Part::Extrusion] Extrude486  label="hex101"
  Base = -> Sketch494
  Dir = (0,-1,2e-16)
  DirMode = 2
  FaceMakerClass = Part::FaceMakerBullseye
  FaceMakerMode = 3
  LengthFwd = 10
  LengthRev = 0
  Solid = true
  Symmetric = false
FEATURE [Sketcher::SketchObject] Sketch495
  ArcFitTolerance = 1e-06
  FullyConstrained = true
  MakeInternals = false
  Placement = pos=(0,0,0) rot=(1,0,0;1.5708rad)
  sketch-geometry (49):
    g0: LineSegment StartX=1e-16 StartY=3.5 StartZ=0 EndX=-3.03109 EndY=1.75 EndZ=0
    g1: LineSegment StartX=-3.03109 StartY=1.75 StartZ=0 EndX=-3.03109 EndY=-1.75 EndZ=0
    g2: LineSegment StartX=-3.03109 StartY=-1.75 StartZ=0 EndX=-1e-16 EndY=-3.5 EndZ=0
    g3: LineSegment StartX=-1e-16 StartY=-3.5 StartZ=0 EndX=3.03109 EndY=-1.75 EndZ=0
    g4: LineSegment StartX=3.03109 StartY=-1.75 StartZ=0 EndX=3.03109 EndY=1.75 EndZ=0
    g5: LineSegment StartX=3.03109 StartY=1.75 StartZ=0 EndX=1e-16 EndY=3.5 EndZ=0
    g6: Circle [constr] CenterX=0 CenterY=0 CenterZ=0 NormalX=0 NormalY=0 NormalZ=1 AngleXU=0 Radius=3.5
    g7: LineSegment StartX=4.96892 StartY=-1.75002 StartZ=0 EndX=8.00002 EndY=-3.5 EndZ=0
    g8: LineSegment StartX=8.00002 StartY=-3.5 StartZ=0 EndX=11.0311 EndY=-1.74998 EndZ=0
    g9: LineSegment StartX=11.0311 StartY=-1.74998 StartZ=0 EndX=11.0311 EndY=1.75002 EndZ=0
    g10: LineSegment StartX=11.0311 StartY=1.75002 StartZ=0 EndX=7.99998 EndY=3.5 EndZ=0
    g11: LineSegment StartX=7.99998 StartY=3.5 StartZ=0 EndX=4.9689 EndY=1.74998 EndZ=0
    g12: LineSegment StartX=4.9689 StartY=1.74998 StartZ=0 EndX=4.96892 EndY=-1.75002 EndZ=0
    g13: Circle [constr] CenterX=8 CenterY=0 CenterZ=0 NormalX=0 NormalY=0 NormalZ=1 AngleXU=0 Radius=3.5
    g14: LineSegment StartX=4.03109 StartY=3.5 StartZ=0 EndX=7.06218 EndY=5.25 EndZ=0
    g15: LineSegment StartX=7.06218 StartY=5.25 StartZ=0 EndX=7.06218 EndY=8.75 EndZ=0
    g16: LineSegment StartX=7.06218 StartY=8.75 StartZ=0 EndX=4.03109 EndY=10.5 EndZ=0
    g17: LineSegment StartX=4.03109 StartY=10.5 StartZ=0 EndX=1 EndY=8.75 EndZ=0
    g18: LineSegment StartX=1 StartY=8.75 StartZ=0 EndX=1 EndY=5.25 EndZ=0
    g19: LineSegment StartX=1 StartY=5.25 StartZ=0 EndX=4.03109 EndY=3.5 EndZ=0
    g20: Circle [constr] CenterX=4.03109 CenterY=7 CenterZ=0 NormalX=0 NormalY=0 NormalZ=1 AngleXU=0 Radius=3.5
    g21: LineSegment StartX=-1 StartY=5.25 StartZ=0 EndX=-1 EndY=8.75 EndZ=0
    g22: LineSegment StartX=-1 StartY=8.75 StartZ=0 EndX=-4.03109 EndY=10.5 EndZ=0
    g23: LineSegment StartX=-4.03109 StartY=10.5 StartZ=0 EndX=-7.06218 EndY=8.75 EndZ=0
    g24: LineSegment StartX=-7.06218 StartY=8.75 StartZ=0 EndX=-7.06218 EndY=5.25 EndZ=0
    g25: LineSegment StartX=-7.06218 StartY=5.25 StartZ=0 EndX=-4.03109 EndY=3.5 EndZ=0
    g26: LineSegment StartX=-4.03109 StartY=3.5 StartZ=0 EndX=-1 EndY=5.25 EndZ=0
    g27: Circle [constr] CenterX=-4.03109 CenterY=7 CenterZ=0 NormalX=0 NormalY=0 NormalZ=1 AngleXU=0 Radius=3.5
    g28: LineSegment StartX=-4.96891 StartY=-1.75 StartZ=0 EndX=-4.96891 EndY=1.75 EndZ=0
    g29: LineSegment StartX=-4.96891 StartY=1.75 StartZ=0 EndX=-8 EndY=3.5 EndZ=0
    g30: LineSegment StartX=-8 StartY=3.5 StartZ=0 EndX=-11.0311 EndY=1.75 EndZ=0
    g31: LineSegment StartX=-11.0311 StartY=1.75 StartZ=0 EndX=-11.0311 EndY=-1.75 EndZ=0
    g32: LineSegment StartX=-11.0311 StartY=-1.75 StartZ=0 EndX=-8 EndY=-3.5 EndZ=0
    g33: LineSegment StartX=-8 StartY=-3.5 StartZ=0 EndX=-4.96891 EndY=-1.75 EndZ=0
    g34: Circle [constr] CenterX=-8 CenterY=0 CenterZ=0 NormalX=0 NormalY=0 NormalZ=1 AngleXU=0 Radius=3.5
    g35: LineSegment StartX=-4.03109 StartY=-3.5 StartZ=0 EndX=-7.06218 EndY=-5.25 EndZ=0
    g36: LineSegment StartX=-7.06218 StartY=-5.25 StartZ=0 EndX=-7.06218 EndY=-8.75 EndZ=0
    g37: LineSegment StartX=-7.06218 StartY=-8.75 StartZ=0 EndX=-4.03109 EndY=-10.5 EndZ=0
    g38: LineSegment StartX=-4.03109 StartY=-10.5 StartZ=0 EndX=-1 EndY=-8.75 EndZ=0
    g39: LineSegment StartX=-1 StartY=-8.75 StartZ=0 EndX=-1 EndY=-5.25 EndZ=0
    g40: LineSegment StartX=-1 StartY=-5.25 StartZ=0 EndX=-4.03109 EndY=-3.5 EndZ=0
    g41: Circle [constr] CenterX=-4.03109 CenterY=-7 CenterZ=0 NormalX=0 NormalY=0 NormalZ=1 AngleXU=0 Radius=3.5
    g42: LineSegment StartX=4.03109 StartY=-3.5 StartZ=0 EndX=1 EndY=-5.25 EndZ=0
    g43: LineSegment StartX=1 StartY=-5.25 StartZ=0 EndX=1 EndY=-8.75 EndZ=0
    g44: LineSegment StartX=1 StartY=-8.75 StartZ=0 EndX=4.03109 EndY=-10.5 EndZ=0
    g45: LineSegment StartX=4.03109 StartY=-10.5 StartZ=0 EndX=7.06218 EndY=-8.75 EndZ=0
    g46: LineSegment StartX=7.06218 StartY=-8.75 StartZ=0 EndX=7.06218 EndY=-5.25 EndZ=0
    g47: LineSegment StartX=7.06218 StartY=-5.25 StartZ=0 EndX=4.03109 EndY=-3.5 EndZ=0
    g48: Circle [constr] CenterX=4.03109 CenterY=-7 CenterZ=0 NormalX=0 NormalY=0 NormalZ=1 AngleXU=0 Radius=3.5
  constraints (117):
    c: Coincident(g0,g1)
    c: Coincident(g1,g2)
    c: Coincident(g2,g3)
    c: Coincident(g3,g4)
    c: Coincident(g4,g5)
    c: Coincident(g5,g0)
    c: Equal(g0, g1-g5) x5
    c: PointOnObject(g0,g6)
    c: PointOnObject(g1,g6)
    c: PointOnObject(g2,g6)
    c: PointOnObject(g3,g6)
    c: PointOnObject(g4,g6)
    c: PointOnObject(g5,g6)
    c: Coincident(g6,g-1)
    c: Diameter(g6) = 7
    c: PointOnObject(g0,g-2)
    c: Coincident(g7,g8)
    c: Coincident(g8,g9)
    c: Coincident(g9,g10)
    c: Coincident(g10,g11)
    c: Coincident(g11,g12)
    c: Coincident(g12,g7)
    c: Equal(g7, g8-g12) x5
    c: PointOnObject(g7,g13)
    c: PointOnObject(g8,g13)
    c: PointOnObject(g9,g13)
    c: PointOnObject(g10,g13)
    c: PointOnObject(g11,g13)
    c: PointOnObject(g12,g13)
    c: PointOnObject(g13,g-1)
    c: Diameter(g13) = 7
    c: Distance(g6,g13) = 8
    c: Horizontal(g0,g10)
    c: Coincident(g14,g15)
    c: Coincident(g15,g16)
    c: Coincident(g16,g17)
    c: Coincident(g17,g18)
    c: Coincident(g18,g19)
    c: Coincident(g19,g14)
    c: Equal(g14, g15-g19) x5
    c: PointOnObject(g14,g20)
    c: PointOnObject(g15,g20)
    c: PointOnObject(g16,g20)
    c: PointOnObject(g17,g20)
    c: PointOnObject(g18,g20)
    c: PointOnObject(g19,g20)
    c: Diameter(g20) = 7
    c: DistanceY(g-1,g20) = 7
    c: Vertical(g18)
    c: Distance(g17,g-2) = 1
    c: Coincident(g21,g22)
    c: Coincident(g22,g23)
    c: Coincident(g23,g24)
    c: Coincident(g24,g25)
    c: Coincident(g25,g26)
    c: Coincident(g26,g21)
    c: Equal(g21, g22-g26) x5
    c: PointOnObject(g21,g27)
    c: PointOnObject(g22,g27)
    c: PointOnObject(g23,g27)
    c: PointOnObject(g24,g27)
    c: PointOnObject(g25,g27)
    c: PointOnObject(g26,g27)
    c: Diameter(g27) = 7
    c: DistanceY(g-1,g27) = 7
    c: DistanceX(g21,g-1) = 1
    c: Vertical(g21)
    c: Coincident(g28,g29)
    c: Coincident(g29,g30)
    c: Coincident(g30,g31)
    c: Coincident(g31,g32)
    c: Coincident(g32,g33)
    c: Coincident(g33,g28)
    c: Equal(g28, g29-g33) x5
    c: PointOnObject(g28,g34)
    c: PointOnObject(g29,g34)
    c: PointOnObject(g30,g34)
    c: PointOnObject(g31,g34)
    c: PointOnObject(g32,g34)
    c: PointOnObject(g33,g34)
    c: PointOnObject(g34,g-1)
    c: Diameter(g34) = 7
    c: Vertical(g31)
    c: DistanceX(g34,g-1) = 8
    c: Coincident(g35,g36)
    c: Coincident(g36,g37)
    c: Coincident(g37,g38)
    c: Coincident(g38,g39)
    c: Coincident(g39,g40)
    c: Coincident(g40,g35)
    c: Equal(g35, g36-g40) x5
    c: PointOnObject(g35,g41)
    c: PointOnObject(g36,g41)
    c: PointOnObject(g37,g41)
    c: PointOnObject(g38,g41)
    c: PointOnObject(g39,g41)
    c: PointOnObject(g40,g41)
    c: Coincident(g42,g43)
    c: Coincident(g43,g44)
    c: Coincident(g44,g45)
    c: Coincident(g45,g46)
    c: Coincident(g46,g47)
    c: Coincident(g47,g42)
    c: Equal(g42, g43-g47) x5
    c: PointOnObject(g42,g48)
    c: PointOnObject(g43,g48)
    c: PointOnObject(g44,g48)
    c: PointOnObject(g45,g48)
    c: PointOnObject(g46,g48)
    c: PointOnObject(g47,g48)
    c: Equal(g41,g48)
    c: Diameter(g41) = 7
    c: Vertical(g39)
    c: Vertical(g43)
    c: Distance(g-2,g39) = 1
    c: Symmetric(g38,g43,g-2)
    c: Distance(g41,g-1) = 7
FEATURE [Part::Extrusion] Extrude487  label="hex102"
  Base = -> Sketch495
  Dir = (0,-1,2e-16)
  DirMode = 2
  FaceMakerClass = Part::FaceMakerBullseye
  FaceMakerMode = 3
  LengthFwd = 10
  LengthRev = 0
  Placement = pos=(20,0,-7) rot=(0,0,1;0rad)
  Solid = true
  Symmetric = false
FEATURE [Sketcher::SketchObject] Sketch496
  ArcFitTolerance = 1e-06
  FullyConstrained = true
  MakeInternals = false
  Placement = pos=(0,0,0) rot=(1,0,0;1.5708rad)
  sketch-geometry (49):
    g0: LineSegment StartX=1e-16 StartY=3.5 StartZ=0 EndX=-3.03109 EndY=1.75 EndZ=0
    g1: LineSegment StartX=-3.03109 StartY=1.75 StartZ=0 EndX=-3.03109 EndY=-1.75 EndZ=0
    g2: LineSegment StartX=-3.03109 StartY=-1.75 StartZ=0 EndX=-1e-16 EndY=-3.5 EndZ=0
    g3: LineSegment StartX=-1e-16 StartY=-3.5 StartZ=0 EndX=3.03109 EndY=-1.75 EndZ=0
    g4: LineSegment StartX=3.03109 StartY=-1.75 StartZ=0 EndX=3.03109 EndY=1.75 EndZ=0
    g5: LineSegment StartX=3.03109 StartY=1.75 StartZ=0 EndX=1e-16 EndY=3.5 EndZ=0
    g6: Circle [constr] CenterX=0 CenterY=0 CenterZ=0 NormalX=0 NormalY=0 NormalZ=1 AngleXU=0 Radius=3.5
    g7: LineSegment StartX=4.96892 StartY=-1.75002 StartZ=0 EndX=8.00002 EndY=-3.5 EndZ=0
    g8: LineSegment StartX=8.00002 StartY=-3.5 StartZ=0 EndX=11.0311 EndY=-1.74998 EndZ=0
    g9: LineSegment StartX=11.0311 StartY=-1.74998 StartZ=0 EndX=11.0311 EndY=1.75002 EndZ=0
    g10: LineSegment StartX=11.0311 StartY=1.75002 StartZ=0 EndX=7.99998 EndY=3.5 EndZ=0
    g11: LineSegment StartX=7.99998 StartY=3.5 StartZ=0 EndX=4.9689 EndY=1.74998 EndZ=0
    g12: LineSegment StartX=4.9689 StartY=1.74998 StartZ=0 EndX=4.96892 EndY=-1.75002 EndZ=0
    g13: Circle [constr] CenterX=8 CenterY=0 CenterZ=0 NormalX=0 NormalY=0 NormalZ=1 AngleXU=0 Radius=3.5
    g14: LineSegment StartX=4.03109 StartY=3.5 StartZ=0 EndX=7.06218 EndY=5.25 EndZ=0
    g15: LineSegment StartX=7.06218 StartY=5.25 StartZ=0 EndX=7.06218 EndY=8.75 EndZ=0
    g16: LineSegment StartX=7.06218 StartY=8.75 StartZ=0 EndX=4.03109 EndY=10.5 EndZ=0
    g17: LineSegment StartX=4.03109 StartY=10.5 StartZ=0 EndX=1 EndY=8.75 EndZ=0
    g18: LineSegment StartX=1 StartY=8.75 StartZ=0 EndX=1 EndY=5.25 EndZ=0
    g19: LineSegment StartX=1 StartY=5.25 StartZ=0 EndX=4.03109 EndY=3.5 EndZ=0
    g20: Circle [constr] CenterX=4.03109 CenterY=7 CenterZ=0 NormalX=0 NormalY=0 NormalZ=1 AngleXU=0 Radius=3.5
    g21: LineSegment StartX=-1 StartY=5.25 StartZ=0 EndX=-1 EndY=8.75 EndZ=0
    g22: LineSegment StartX=-1 StartY=8.75 StartZ=0 EndX=-4.03109 EndY=10.5 EndZ=0
    g23: LineSegment StartX=-4.03109 StartY=10.5 StartZ=0 EndX=-7.06218 EndY=8.75 EndZ=0
    g24: LineSegment StartX=-7.06218 StartY=8.75 StartZ=0 EndX=-7.06218 EndY=5.25 EndZ=0
    g25: LineSegment StartX=-7.06218 StartY=5.25 StartZ=0 EndX=-4.03109 EndY=3.5 EndZ=0
    g26: LineSegment StartX=-4.03109 StartY=3.5 StartZ=0 EndX=-1 EndY=5.25 EndZ=0
    g27: Circle [constr] CenterX=-4.03109 CenterY=7 CenterZ=0 NormalX=0 NormalY=0 NormalZ=1 AngleXU=0 Radius=3.5
    g28: LineSegment StartX=-4.96891 StartY=-1.75 StartZ=0 EndX=-4.96891 EndY=1.75 EndZ=0
    g29: LineSegment StartX=-4.96891 StartY=1.75 StartZ=0 EndX=-8 EndY=3.5 EndZ=0
    g30: LineSegment StartX=-8 StartY=3.5 StartZ=0 EndX=-11.0311 EndY=1.75 EndZ=0
    g31: LineSegment StartX=-11.0311 StartY=1.75 StartZ=0 EndX=-11.0311 EndY=-1.75 EndZ=0
    g32: LineSegment StartX=-11.0311 StartY=-1.75 StartZ=0 EndX=-8 EndY=-3.5 EndZ=0
    g33: LineSegment StartX=-8 StartY=-3.5 StartZ=0 EndX=-4.96891 EndY=-1.75 EndZ=0
    g34: Circle [constr] CenterX=-8 CenterY=0 CenterZ=0 NormalX=0 NormalY=0 NormalZ=1 AngleXU=0 Radius=3.5
    g35: LineSegment StartX=-4.03109 StartY=-3.5 StartZ=0 EndX=-7.06218 EndY=-5.25 EndZ=0
    g36: LineSegment StartX=-7.06218 StartY=-5.25 StartZ=0 EndX=-7.06218 EndY=-8.75 EndZ=0
    g37: LineSegment StartX=-7.06218 StartY=-8.75 StartZ=0 EndX=-4.03109 EndY=-10.5 EndZ=0
    g38: LineSegment StartX=-4.03109 StartY=-10.5 StartZ=0 EndX=-1 EndY=-8.75 EndZ=0
    g39: LineSegment StartX=-1 StartY=-8.75 StartZ=0 EndX=-1 EndY=-5.25 EndZ=0
    g40: LineSegment StartX=-1 StartY=-5.25 StartZ=0 EndX=-4.03109 EndY=-3.5 EndZ=0
    g41: Circle [constr] CenterX=-4.03109 CenterY=-7 CenterZ=0 NormalX=0 NormalY=0 NormalZ=1 AngleXU=0 Radius=3.5
    g42: LineSegment StartX=4.03109 StartY=-3.5 StartZ=0 EndX=1 EndY=-5.25 EndZ=0
    g43: LineSegment StartX=1 StartY=-5.25 StartZ=0 EndX=1 EndY=-8.75 EndZ=0
    g44: LineSegment StartX=1 StartY=-8.75 StartZ=0 EndX=4.03109 EndY=-10.5 EndZ=0
    g45: LineSegment StartX=4.03109 StartY=-10.5 StartZ=0 EndX=7.06218 EndY=-8.75 EndZ=0
    g46: LineSegment StartX=7.06218 StartY=-8.75 StartZ=0 EndX=7.06218 EndY=-5.25 EndZ=0
    g47: LineSegment StartX=7.06218 StartY=-5.25 StartZ=0 EndX=4.03109 EndY=-3.5 EndZ=0
    g48: Circle [constr] CenterX=4.03109 CenterY=-7 CenterZ=0 NormalX=0 NormalY=0 NormalZ=1 AngleXU=0 Radius=3.5
  constraints (117):
    c: Coincident(g0,g1)
    c: Coincident(g1,g2)
    c: Coincident(g2,g3)
    c: Coincident(g3,g4)
    c: Coincident(g4,g5)
    c: Coincident(g5,g0)
    c: Equal(g0, g1-g5) x5
    c: PointOnObject(g0,g6)
    c: PointOnObject(g1,g6)
    c: PointOnObject(g2,g6)
    c: PointOnObject(g3,g6)
    c: PointOnObject(g4,g6)
    c: PointOnObject(g5,g6)
    c: Coincident(g6,g-1)
    c: Diameter(g6) = 7
    c: PointOnObject(g0,g-2)
    c: Coincident(g7,g8)
    c: Coincident(g8,g9)
    c: Coincident(g9,g10)
    c: Coincident(g10,g11)
    c: Coincident(g11,g12)
    c: Coincident(g12,g7)
    c: Equal(g7, g8-g12) x5
    c: PointOnObject(g7,g13)
    c: PointOnObject(g8,g13)
    c: PointOnObject(g9,g13)
    c: PointOnObject(g10,g13)
    c: PointOnObject(g11,g13)
    c: PointOnObject(g12,g13)
    c: PointOnObject(g13,g-1)
    c: Diameter(g13) = 7
    c: Distance(g6,g13) = 8
    c: Horizontal(g0,g10)
    c: Coincident(g14,g15)
    c: Coincident(g15,g16)
    c: Coincident(g16,g17)
    c: Coincident(g17,g18)
    c: Coincident(g18,g19)
    c: Coincident(g19,g14)
    c: Equal(g14, g15-g19) x5
    c: PointOnObject(g14,g20)
    c: PointOnObject(g15,g20)
    c: PointOnObject(g16,g20)
    c: PointOnObject(g17,g20)
    c: PointOnObject(g18,g20)
    c: PointOnObject(g19,g20)
    c: Diameter(g20) = 7
    c: DistanceY(g-1,g20) = 7
    c: Vertical(g18)
    c: Distance(g17,g-2) = 1
    c: Coincident(g21,g22)
    c: Coincident(g22,g23)
    c: Coincident(g23,g24)
    c: Coincident(g24,g25)
    c: Coincident(g25,g26)
    c: Coincident(g26,g21)
    c: Equal(g21, g22-g26) x5
    c: PointOnObject(g21,g27)
    c: PointOnObject(g22,g27)
    c: PointOnObject(g23,g27)
    c: PointOnObject(g24,g27)
    c: PointOnObject(g25,g27)
    c: PointOnObject(g26,g27)
    c: Diameter(g27) = 7
    c: DistanceY(g-1,g27) = 7
    c: DistanceX(g21,g-1) = 1
    c: Vertical(g21)
    c: Coincident(g28,g29)
    c: Coincident(g29,g30)
    c: Coincident(g30,g31)
    c: Coincident(g31,g32)
    c: Coincident(g32,g33)
    c: Coincident(g33,g28)
    c: Equal(g28, g29-g33) x5
    c: PointOnObject(g28,g34)
    c: PointOnObject(g29,g34)
    c: PointOnObject(g30,g34)
    c: PointOnObject(g31,g34)
    c: PointOnObject(g32,g34)
    c: PointOnObject(g33,g34)
    c: PointOnObject(g34,g-1)
    c: Diameter(g34) = 7
    c: Vertical(g31)
    c: DistanceX(g34,g-1) = 8
    c: Coincident(g35,g36)
    c: Coincident(g36,g37)
    c: Coincident(g37,g38)
    c: Coincident(g38,g39)
    c: Coincident(g39,g40)
    c: Coincident(g40,g35)
    c: Equal(g35, g36-g40) x5
    c: PointOnObject(g35,g41)
    c: PointOnObject(g36,g41)
    c: PointOnObject(g37,g41)
    c: PointOnObject(g38,g41)
    c: PointOnObject(g39,g41)
    c: PointOnObject(g40,g41)
    c: Coincident(g42,g43)
    c: Coincident(g43,g44)
    c: Coincident(g44,g45)
    c: Coincident(g45,g46)
    c: Coincident(g46,g47)
    c: Coincident(g47,g42)
    c: Equal(g42, g43-g47) x5
    c: PointOnObject(g42,g48)
    c: PointOnObject(g43,g48)
    c: PointOnObject(g44,g48)
    c: PointOnObject(g45,g48)
    c: PointOnObject(g46,g48)
    c: PointOnObject(g47,g48)
    c: Equal(g41,g48)
    c: Diameter(g41) = 7
    c: Vertical(g39)
    c: Vertical(g43)
    c: Distance(g-2,g39) = 1
    c: Symmetric(g38,g43,g-2)
    c: Distance(g41,g-1) = 7
FEATURE [Part::Extrusion] Extrude488  label="hex103"
  Base = -> Sketch496
  Dir = (0,-1,2e-16)
  DirMode = 2
  FaceMakerClass = Part::FaceMakerBullseye
  FaceMakerMode = 3
  LengthFwd = 10
  LengthRev = 0
  Placement = pos=(16,0,14) rot=(0,0,1;0rad)
  Solid = true
  Symmetric = false
FEATURE [Sketcher::SketchObject] Sketch497
  ArcFitTolerance = 1e-06
  FullyConstrained = true
  MakeInternals = false
  Placement = pos=(0,0,0) rot=(1,0,0;1.5708rad)
  sketch-geometry (49):
    g0: LineSegment StartX=1e-16 StartY=3.5 StartZ=0 EndX=-3.03109 EndY=1.75 EndZ=0
    g1: LineSegment StartX=-3.03109 StartY=1.75 StartZ=0 EndX=-3.03109 EndY=-1.75 EndZ=0
    g2: LineSegment StartX=-3.03109 StartY=-1.75 StartZ=0 EndX=-1e-16 EndY=-3.5 EndZ=0
    g3: LineSegment StartX=-1e-16 StartY=-3.5 StartZ=0 EndX=3.03109 EndY=-1.75 EndZ=0
    g4: LineSegment StartX=3.03109 StartY=-1.75 StartZ=0 EndX=3.03109 EndY=1.75 EndZ=0
    g5: LineSegment StartX=3.03109 StartY=1.75 StartZ=0 EndX=1e-16 EndY=3.5 EndZ=0
    g6: Circle [constr] CenterX=0 CenterY=0 CenterZ=0 NormalX=0 NormalY=0 NormalZ=1 AngleXU=0 Radius=3.5
    g7: LineSegment StartX=4.96892 StartY=-1.75002 StartZ=0 EndX=8.00002 EndY=-3.5 EndZ=0
    g8: LineSegment StartX=8.00002 StartY=-3.5 StartZ=0 EndX=11.0311 EndY=-1.74998 EndZ=0
    g9: LineSegment StartX=11.0311 StartY=-1.74998 StartZ=0 EndX=11.0311 EndY=1.75002 EndZ=0
    g10: LineSegment StartX=11.0311 StartY=1.75002 StartZ=0 EndX=7.99998 EndY=3.5 EndZ=0
    g11: LineSegment StartX=7.99998 StartY=3.5 StartZ=0 EndX=4.9689 EndY=1.74998 EndZ=0
    g12: LineSegment StartX=4.9689 StartY=1.74998 StartZ=0 EndX=4.96892 EndY=-1.75002 EndZ=0
    g13: Circle [constr] CenterX=8 CenterY=0 CenterZ=0 NormalX=0 NormalY=0 NormalZ=1 AngleXU=0 Radius=3.5
    g14: LineSegment StartX=4.03109 StartY=3.5 StartZ=0 EndX=7.06218 EndY=5.25 EndZ=0
    g15: LineSegment StartX=7.06218 StartY=5.25 StartZ=0 EndX=7.06218 EndY=8.75 EndZ=0
    g16: LineSegment StartX=7.06218 StartY=8.75 StartZ=0 EndX=4.03109 EndY=10.5 EndZ=0
    g17: LineSegment StartX=4.03109 StartY=10.5 StartZ=0 EndX=1 EndY=8.75 EndZ=0
    g18: LineSegment StartX=1 StartY=8.75 StartZ=0 EndX=1 EndY=5.25 EndZ=0
    g19: LineSegment StartX=1 StartY=5.25 StartZ=0 EndX=4.03109 EndY=3.5 EndZ=0
    g20: Circle [constr] CenterX=4.03109 CenterY=7 CenterZ=0 NormalX=0 NormalY=0 NormalZ=1 AngleXU=0 Radius=3.5
    g21: LineSegment StartX=-1 StartY=5.25 StartZ=0 EndX=-1 EndY=8.75 EndZ=0
    g22: LineSegment StartX=-1 StartY=8.75 StartZ=0 EndX=-4.03109 EndY=10.5 EndZ=0
    g23: LineSegment StartX=-4.03109 StartY=10.5 StartZ=0 EndX=-7.06218 EndY=8.75 EndZ=0
    g24: LineSegment StartX=-7.06218 StartY=8.75 StartZ=0 EndX=-7.06218 EndY=5.25 EndZ=0
    g25: LineSegment StartX=-7.06218 StartY=5.25 StartZ=0 EndX=-4.03109 EndY=3.5 EndZ=0
    g26: LineSegment StartX=-4.03109 StartY=3.5 StartZ=0 EndX=-1 EndY=5.25 EndZ=0
    g27: Circle [constr] CenterX=-4.03109 CenterY=7 CenterZ=0 NormalX=0 NormalY=0 NormalZ=1 AngleXU=0 Radius=3.5
    g28: LineSegment StartX=-4.96891 StartY=-1.75 StartZ=0 EndX=-4.96891 EndY=1.75 EndZ=0
    g29: LineSegment StartX=-4.96891 StartY=1.75 StartZ=0 EndX=-8 EndY=3.5 EndZ=0
    g30: LineSegment StartX=-8 StartY=3.5 StartZ=0 EndX=-11.0311 EndY=1.75 EndZ=0
    g31: LineSegment StartX=-11.0311 StartY=1.75 StartZ=0 EndX=-11.0311 EndY=-1.75 EndZ=0
    g32: LineSegment StartX=-11.0311 StartY=-1.75 StartZ=0 EndX=-8 EndY=-3.5 EndZ=0
    g33: LineSegment StartX=-8 StartY=-3.5 StartZ=0 EndX=-4.96891 EndY=-1.75 EndZ=0
    g34: Circle [constr] CenterX=-8 CenterY=0 CenterZ=0 NormalX=0 NormalY=0 NormalZ=1 AngleXU=0 Radius=3.5
    g35: LineSegment StartX=-4.03109 StartY=-3.5 StartZ=0 EndX=-7.06218 EndY=-5.25 EndZ=0
    g36: LineSegment StartX=-7.06218 StartY=-5.25 StartZ=0 EndX=-7.06218 EndY=-8.75 EndZ=0
    g37: LineSegment StartX=-7.06218 StartY=-8.75 StartZ=0 EndX=-4.03109 EndY=-10.5 EndZ=0
    g38: LineSegment StartX=-4.03109 StartY=-10.5 StartZ=0 EndX=-1 EndY=-8.75 EndZ=0
    g39: LineSegment StartX=-1 StartY=-8.75 StartZ=0 EndX=-1 EndY=-5.25 EndZ=0
    g40: LineSegment StartX=-1 StartY=-5.25 StartZ=0 EndX=-4.03109 EndY=-3.5 EndZ=0
    g41: Circle [constr] CenterX=-4.03109 CenterY=-7 CenterZ=0 NormalX=0 NormalY=0 NormalZ=1 AngleXU=0 Radius=3.5
    g42: LineSegment StartX=4.03109 StartY=-3.5 StartZ=0 EndX=1 EndY=-5.25 EndZ=0
    g43: LineSegment StartX=1 StartY=-5.25 StartZ=0 EndX=1 EndY=-8.75 EndZ=0
    g44: LineSegment StartX=1 StartY=-8.75 StartZ=0 EndX=4.03109 EndY=-10.5 EndZ=0
    g45: LineSegment StartX=4.03109 StartY=-10.5 StartZ=0 EndX=7.06218 EndY=-8.75 EndZ=0
    g46: LineSegment StartX=7.06218 StartY=-8.75 StartZ=0 EndX=7.06218 EndY=-5.25 EndZ=0
    g47: LineSegment StartX=7.06218 StartY=-5.25 StartZ=0 EndX=4.03109 EndY=-3.5 EndZ=0
    g48: Circle [constr] CenterX=4.03109 CenterY=-7 CenterZ=0 NormalX=0 NormalY=0 NormalZ=1 AngleXU=0 Radius=3.5
  constraints (117):
    c: Coincident(g0,g1)
    c: Coincident(g1,g2)
    c: Coincident(g2,g3)
    c: Coincident(g3,g4)
    c: Coincident(g4,g5)
    c: Coincident(g5,g0)
    c: Equal(g0, g1-g5) x5
    c: PointOnObject(g0,g6)
    c: PointOnObject(g1,g6)
    c: PointOnObject(g2,g6)
    c: PointOnObject(g3,g6)
    c: PointOnObject(g4,g6)
    c: PointOnObject(g5,g6)
    c: Coincident(g6,g-1)
    c: Diameter(g6) = 7
    c: PointOnObject(g0,g-2)
    c: Coincident(g7,g8)
    c: Coincident(g8,g9)
    c: Coincident(g9,g10)
    c: Coincident(g10,g11)
    c: Coincident(g11,g12)
    c: Coincident(g12,g7)
    c: Equal(g7, g8-g12) x5
    c: PointOnObject(g7,g13)
    c: PointOnObject(g8,g13)
    c: PointOnObject(g9,g13)
    c: PointOnObject(g10,g13)
    c: PointOnObject(g11,g13)
    c: PointOnObject(g12,g13)
    c: PointOnObject(g13,g-1)
    c: Diameter(g13) = 7
    c: Distance(g6,g13) = 8
    c: Horizontal(g0,g10)
    c: Coincident(g14,g15)
    c: Coincident(g15,g16)
    c: Coincident(g16,g17)
    c: Coincident(g17,g18)
    c: Coincident(g18,g19)
    c: Coincident(g19,g14)
    c: Equal(g14, g15-g19) x5
    c: PointOnObject(g14,g20)
    c: PointOnObject(g15,g20)
    c: PointOnObject(g16,g20)
    c: PointOnObject(g17,g20)
    c: PointOnObject(g18,g20)
    c: PointOnObject(g19,g20)
    c: Diameter(g20) = 7
    c: DistanceY(g-1,g20) = 7
    c: Vertical(g18)
    c: Distance(g17,g-2) = 1
    c: Coincident(g21,g22)
    c: Coincident(g22,g23)
    c: Coincident(g23,g24)
    c: Coincident(g24,g25)
    c: Coincident(g25,g26)
    c: Coincident(g26,g21)
    c: Equal(g21, g22-g26) x5
    c: PointOnObject(g21,g27)
    c: PointOnObject(g22,g27)
    c: PointOnObject(g23,g27)
    c: PointOnObject(g24,g27)
    c: PointOnObject(g25,g27)
    c: PointOnObject(g26,g27)
    c: Diameter(g27) = 7
    c: DistanceY(g-1,g27) = 7
    c: DistanceX(g21,g-1) = 1
    c: Vertical(g21)
    c: Coincident(g28,g29)
    c: Coincident(g29,g30)
    c: Coincident(g30,g31)
    c: Coincident(g31,g32)
    c: Coincident(g32,g33)
    c: Coincident(g33,g28)
    c: Equal(g28, g29-g33) x5
    c: PointOnObject(g28,g34)
    c: PointOnObject(g29,g34)
    c: PointOnObject(g30,g34)
    c: PointOnObject(g31,g34)
    c: PointOnObject(g32,g34)
    c: PointOnObject(g33,g34)
    c: PointOnObject(g34,g-1)
    c: Diameter(g34) = 7
    c: Vertical(g31)
    c: DistanceX(g34,g-1) = 8
    c: Coincident(g35,g36)
    c: Coincident(g36,g37)
    c: Coincident(g37,g38)
    c: Coincident(g38,g39)
    c: Coincident(g39,g40)
    c: Coincident(g40,g35)
    c: Equal(g35, g36-g40) x5
    c: PointOnObject(g35,g41)
    c: PointOnObject(g36,g41)
    c: PointOnObject(g37,g41)
    c: PointOnObject(g38,g41)
    c: PointOnObject(g39,g41)
    c: PointOnObject(g40,g41)
    c: Coincident(g42,g43)
    c: Coincident(g43,g44)
    c: Coincident(g44,g45)
    c: Coincident(g45,g46)
    c: Coincident(g46,g47)
    c: Coincident(g47,g42)
    c: Equal(g42, g43-g47) x5
    c: PointOnObject(g42,g48)
    c: PointOnObject(g43,g48)
    c: PointOnObject(g44,g48)
    c: PointOnObject(g45,g48)
    c: PointOnObject(g46,g48)
    c: PointOnObject(g47,g48)
    c: Equal(g41,g48)
    c: Diameter(g41) = 7
    c: Vertical(g39)
    c: Vertical(g43)
    c: Distance(g-2,g39) = 1
    c: Symmetric(g38,g43,g-2)
    c: Distance(g41,g-1) = 7
FEATURE [Part::Extrusion] Extrude489  label="hex104"
  Base = -> Sketch497
  Dir = (0,-1,2e-16)
  DirMode = 2
  FaceMakerClass = Part::FaceMakerBullseye
  FaceMakerMode = 3
  LengthFwd = 10
  LengthRev = 0
  Placement = pos=(-20,0,-7) rot=(0,0,1;0rad)
  Solid = true
  Symmetric = false
FEATURE [Sketcher::SketchObject] Sketch498
  ArcFitTolerance = 1e-06
  FullyConstrained = true
  MakeInternals = false
  Placement = pos=(0,0,0) rot=(1,0,0;1.5708rad)
  sketch-geometry (49):
    g0: LineSegment StartX=1e-16 StartY=3.5 StartZ=0 EndX=-3.03109 EndY=1.75 EndZ=0
    g1: LineSegment StartX=-3.03109 StartY=1.75 StartZ=0 EndX=-3.03109 EndY=-1.75 EndZ=0
    g2: LineSegment StartX=-3.03109 StartY=-1.75 StartZ=0 EndX=-1e-16 EndY=-3.5 EndZ=0
    g3: LineSegment StartX=-1e-16 StartY=-3.5 StartZ=0 EndX=3.03109 EndY=-1.75 EndZ=0
    g4: LineSegment StartX=3.03109 StartY=-1.75 StartZ=0 EndX=3.03109 EndY=1.75 EndZ=0
    g5: LineSegment StartX=3.03109 StartY=1.75 StartZ=0 EndX=1e-16 EndY=3.5 EndZ=0
    g6: Circle [constr] CenterX=0 CenterY=0 CenterZ=0 NormalX=0 NormalY=0 NormalZ=1 AngleXU=0 Radius=3.5
    g7: LineSegment StartX=4.96892 StartY=-1.75002 StartZ=0 EndX=8.00002 EndY=-3.5 EndZ=0
    g8: LineSegment StartX=8.00002 StartY=-3.5 StartZ=0 EndX=11.0311 EndY=-1.74998 EndZ=0
    g9: LineSegment StartX=11.0311 StartY=-1.74998 StartZ=0 EndX=11.0311 EndY=1.75002 EndZ=0
    g10: LineSegment StartX=11.0311 StartY=1.75002 StartZ=0 EndX=7.99998 EndY=3.5 EndZ=0
    g11: LineSegment StartX=7.99998 StartY=3.5 StartZ=0 EndX=4.9689 EndY=1.74998 EndZ=0
    g12: LineSegment StartX=4.9689 StartY=1.74998 StartZ=0 EndX=4.96892 EndY=-1.75002 EndZ=0
    g13: Circle [constr] CenterX=8 CenterY=0 CenterZ=0 NormalX=0 NormalY=0 NormalZ=1 AngleXU=0 Radius=3.5
    g14: LineSegment StartX=4.03109 StartY=3.5 StartZ=0 EndX=7.06218 EndY=5.25 EndZ=0
    g15: LineSegment StartX=7.06218 StartY=5.25 StartZ=0 EndX=7.06218 EndY=8.75 EndZ=0
    g16: LineSegment StartX=7.06218 StartY=8.75 StartZ=0 EndX=4.03109 EndY=10.5 EndZ=0
    g17: LineSegment StartX=4.03109 StartY=10.5 StartZ=0 EndX=1 EndY=8.75 EndZ=0
    g18: LineSegment StartX=1 StartY=8.75 StartZ=0 EndX=1 EndY=5.25 EndZ=0
    g19: LineSegment StartX=1 StartY=5.25 StartZ=0 EndX=4.03109 EndY=3.5 EndZ=0
    g20: Circle [constr] CenterX=4.03109 CenterY=7 CenterZ=0 NormalX=0 NormalY=0 NormalZ=1 AngleXU=0 Radius=3.5
    g21: LineSegment StartX=-1 StartY=5.25 StartZ=0 EndX=-1 EndY=8.75 EndZ=0
    g22: LineSegment StartX=-1 StartY=8.75 StartZ=0 EndX=-4.03109 EndY=10.5 EndZ=0
    g23: LineSegment StartX=-4.03109 StartY=10.5 StartZ=0 EndX=-7.06218 EndY=8.75 EndZ=0
    g24: LineSegment StartX=-7.06218 StartY=8.75 StartZ=0 EndX=-7.06218 EndY=5.25 EndZ=0
    g25: LineSegment StartX=-7.06218 StartY=5.25 StartZ=0 EndX=-4.03109 EndY=3.5 EndZ=0
    g26: LineSegment StartX=-4.03109 StartY=3.5 StartZ=0 EndX=-1 EndY=5.25 EndZ=0
    g27: Circle [constr] CenterX=-4.03109 CenterY=7 CenterZ=0 NormalX=0 NormalY=0 NormalZ=1 AngleXU=0 Radius=3.5
    g28: LineSegment StartX=-4.96891 StartY=-1.75 StartZ=0 EndX=-4.96891 EndY=1.75 EndZ=0
    g29: LineSegment StartX=-4.96891 StartY=1.75 StartZ=0 EndX=-8 EndY=3.5 EndZ=0
    g30: LineSegment StartX=-8 StartY=3.5 StartZ=0 EndX=-11.0311 EndY=1.75 EndZ=0
    g31: LineSegment StartX=-11.0311 StartY=1.75 StartZ=0 EndX=-11.0311 EndY=-1.75 EndZ=0
    g32: LineSegment StartX=-11.0311 StartY=-1.75 StartZ=0 EndX=-8 EndY=-3.5 EndZ=0
    g33: LineSegment StartX=-8 StartY=-3.5 StartZ=0 EndX=-4.96891 EndY=-1.75 EndZ=0
    g34: Circle [constr] CenterX=-8 CenterY=0 CenterZ=0 NormalX=0 NormalY=0 NormalZ=1 AngleXU=0 Radius=3.5
    g35: LineSegment StartX=-4.03109 StartY=-3.5 StartZ=0 EndX=-7.06218 EndY=-5.25 EndZ=0
    g36: LineSegment StartX=-7.06218 StartY=-5.25 StartZ=0 EndX=-7.06218 EndY=-8.75 EndZ=0
    g37: LineSegment StartX=-7.06218 StartY=-8.75 StartZ=0 EndX=-4.03109 EndY=-10.5 EndZ=0
    g38: LineSegment StartX=-4.03109 StartY=-10.5 StartZ=0 EndX=-1 EndY=-8.75 EndZ=0
    g39: LineSegment StartX=-1 StartY=-8.75 StartZ=0 EndX=-1 EndY=-5.25 EndZ=0
    g40: LineSegment StartX=-1 StartY=-5.25 StartZ=0 EndX=-4.03109 EndY=-3.5 EndZ=0
    g41: Circle [constr] CenterX=-4.03109 CenterY=-7 CenterZ=0 NormalX=0 NormalY=0 NormalZ=1 AngleXU=0 Radius=3.5
    g42: LineSegment StartX=4.03109 StartY=-3.5 StartZ=0 EndX=1 EndY=-5.25 EndZ=0
    g43: LineSegment StartX=1 StartY=-5.25 StartZ=0 EndX=1 EndY=-8.75 EndZ=0
    g44: LineSegment StartX=1 StartY=-8.75 StartZ=0 EndX=4.03109 EndY=-10.5 EndZ=0
    g45: LineSegment StartX=4.03109 StartY=-10.5 StartZ=0 EndX=7.06218 EndY=-8.75 EndZ=0
    g46: LineSegment StartX=7.06218 StartY=-8.75 StartZ=0 EndX=7.06218 EndY=-5.25 EndZ=0
    g47: LineSegment StartX=7.06218 StartY=-5.25 StartZ=0 EndX=4.03109 EndY=-3.5 EndZ=0
    g48: Circle [constr] CenterX=4.03109 CenterY=-7 CenterZ=0 NormalX=0 NormalY=0 NormalZ=1 AngleXU=0 Radius=3.5
  constraints (117):
    c: Coincident(g0,g1)
    c: Coincident(g1,g2)
    c: Coincident(g2,g3)
    c: Coincident(g3,g4)
    c: Coincident(g4,g5)
    c: Coincident(g5,g0)
    c: Equal(g0, g1-g5) x5
    c: PointOnObject(g0,g6)
    c: PointOnObject(g1,g6)
    c: PointOnObject(g2,g6)
    c: PointOnObject(g3,g6)
    c: PointOnObject(g4,g6)
    c: PointOnObject(g5,g6)
    c: Coincident(g6,g-1)
    c: Diameter(g6) = 7
    c: PointOnObject(g0,g-2)
    c: Coincident(g7,g8)
    c: Coincident(g8,g9)
    c: Coincident(g9,g10)
    c: Coincident(g10,g11)
    c: Coincident(g11,g12)
    c: Coincident(g12,g7)
    c: Equal(g7, g8-g12) x5
    c: PointOnObject(g7,g13)
    c: PointOnObject(g8,g13)
    c: PointOnObject(g9,g13)
    c: PointOnObject(g10,g13)
    c: PointOnObject(g11,g13)
    c: PointOnObject(g12,g13)
    c: PointOnObject(g13,g-1)
    c: Diameter(g13) = 7
    c: Distance(g6,g13) = 8
    c: Horizontal(g0,g10)
    c: Coincident(g14,g15)
    c: Coincident(g15,g16)
    c: Coincident(g16,g17)
    c: Coincident(g17,g18)
    c: Coincident(g18,g19)
    c: Coincident(g19,g14)
    c: Equal(g14, g15-g19) x5
    c: PointOnObject(g14,g20)
    c: PointOnObject(g15,g20)
    c: PointOnObject(g16,g20)
    c: PointOnObject(g17,g20)
    c: PointOnObject(g18,g20)
    c: PointOnObject(g19,g20)
    c: Diameter(g20) = 7
    c: DistanceY(g-1,g20) = 7
    c: Vertical(g18)
    c: Distance(g17,g-2) = 1
    c: Coincident(g21,g22)
    c: Coincident(g22,g23)
    c: Coincident(g23,g24)
    c: Coincident(g24,g25)
    c: Coincident(g25,g26)
    c: Coincident(g26,g21)
    c: Equal(g21, g22-g26) x5
    c: PointOnObject(g21,g27)
    c: PointOnObject(g22,g27)
    c: PointOnObject(g23,g27)
    c: PointOnObject(g24,g27)
    c: PointOnObject(g25,g27)
    c: PointOnObject(g26,g27)
    c: Diameter(g27) = 7
    c: DistanceY(g-1,g27) = 7
    c: DistanceX(g21,g-1) = 1
    c: Vertical(g21)
    c: Coincident(g28,g29)
    c: Coincident(g29,g30)
    c: Coincident(g30,g31)
    c: Coincident(g31,g32)
    c: Coincident(g32,g33)
    c: Coincident(g33,g28)
    c: Equal(g28, g29-g33) x5
    c: PointOnObject(g28,g34)
    c: PointOnObject(g29,g34)
    c: PointOnObject(g30,g34)
    c: PointOnObject(g31,g34)
    c: PointOnObject(g32,g34)
    c: PointOnObject(g33,g34)
    c: PointOnObject(g34,g-1)
    c: Diameter(g34) = 7
    c: Vertical(g31)
    c: DistanceX(g34,g-1) = 8
    c: Coincident(g35,g36)
    c: Coincident(g36,g37)
    c: Coincident(g37,g38)
    c: Coincident(g38,g39)
    c: Coincident(g39,g40)
    c: Coincident(g40,g35)
    c: Equal(g35, g36-g40) x5
    c: PointOnObject(g35,g41)
    c: PointOnObject(g36,g41)
    c: PointOnObject(g37,g41)
    c: PointOnObject(g38,g41)
    c: PointOnObject(g39,g41)
    c: PointOnObject(g40,g41)
    c: Coincident(g42,g43)
    c: Coincident(g43,g44)
    c: Coincident(g44,g45)
    c: Coincident(g45,g46)
    c: Coincident(g46,g47)
    c: Coincident(g47,g42)
    c: Equal(g42, g43-g47) x5
    c: PointOnObject(g42,g48)
    c: PointOnObject(g43,g48)
    c: PointOnObject(g44,g48)
    c: PointOnObject(g45,g48)
    c: PointOnObject(g46,g48)
    c: PointOnObject(g47,g48)
    c: Equal(g41,g48)
    c: Diameter(g41) = 7
    c: Vertical(g39)
    c: Vertical(g43)
    c: Distance(g-2,g39) = 1
    c: Symmetric(g38,g43,g-2)
    c: Distance(g41,g-1) = 7
FEATURE [Part::Extrusion] Extrude490  label="hex105"
  Base = -> Sketch498
  Dir = (0,-1,2e-16)
  DirMode = 2
  FaceMakerClass = Part::FaceMakerBullseye
  FaceMakerMode = 3
  LengthFwd = 10
  LengthRev = 0
  Placement = pos=(-16,0,14) rot=(0,0,1;0rad)
  Solid = true
  Symmetric = false
FEATURE [Sketcher::SketchObject] Sketch499
  ArcFitTolerance = 1e-06
  FullyConstrained = true
  MakeInternals = false
  Placement = pos=(0,0,0) rot=(1,0,0;1.5708rad)
  sketch-geometry (49):
    g0: LineSegment StartX=1e-16 StartY=3.5 StartZ=0 EndX=-3.03109 EndY=1.75 EndZ=0
    g1: LineSegment StartX=-3.03109 StartY=1.75 StartZ=0 EndX=-3.03109 EndY=-1.75 EndZ=0
    g2: LineSegment StartX=-3.03109 StartY=-1.75 StartZ=0 EndX=-1e-16 EndY=-3.5 EndZ=0
    g3: LineSegment StartX=-1e-16 StartY=-3.5 StartZ=0 EndX=3.03109 EndY=-1.75 EndZ=0
    g4: LineSegment StartX=3.03109 StartY=-1.75 StartZ=0 EndX=3.03109 EndY=1.75 EndZ=0
    g5: LineSegment StartX=3.03109 StartY=1.75 StartZ=0 EndX=1e-16 EndY=3.5 EndZ=0
    g6: Circle [constr] CenterX=0 CenterY=0 CenterZ=0 NormalX=0 NormalY=0 NormalZ=1 AngleXU=0 Radius=3.5
    g7: LineSegment StartX=4.96892 StartY=-1.75002 StartZ=0 EndX=8.00002 EndY=-3.5 EndZ=0
    g8: LineSegment StartX=8.00002 StartY=-3.5 StartZ=0 EndX=11.0311 EndY=-1.74998 EndZ=0
    g9: LineSegment StartX=11.0311 StartY=-1.74998 StartZ=0 EndX=11.0311 EndY=1.75002 EndZ=0
    g10: LineSegment StartX=11.0311 StartY=1.75002 StartZ=0 EndX=7.99998 EndY=3.5 EndZ=0
    g11: LineSegment StartX=7.99998 StartY=3.5 StartZ=0 EndX=4.9689 EndY=1.74998 EndZ=0
    g12: LineSegment StartX=4.9689 StartY=1.74998 StartZ=0 EndX=4.96892 EndY=-1.75002 EndZ=0
    g13: Circle [constr] CenterX=8 CenterY=0 CenterZ=0 NormalX=0 NormalY=0 NormalZ=1 AngleXU=0 Radius=3.5
    g14: LineSegment StartX=4.03109 StartY=3.5 StartZ=0 EndX=7.06218 EndY=5.25 EndZ=0
    g15: LineSegment StartX=7.06218 StartY=5.25 StartZ=0 EndX=7.06218 EndY=8.75 EndZ=0
    g16: LineSegment StartX=7.06218 StartY=8.75 StartZ=0 EndX=4.03109 EndY=10.5 EndZ=0
    g17: LineSegment StartX=4.03109 StartY=10.5 StartZ=0 EndX=1 EndY=8.75 EndZ=0
    g18: LineSegment StartX=1 StartY=8.75 StartZ=0 EndX=1 EndY=5.25 EndZ=0
    g19: LineSegment StartX=1 StartY=5.25 StartZ=0 EndX=4.03109 EndY=3.5 EndZ=0
    g20: Circle [constr] CenterX=4.03109 CenterY=7 CenterZ=0 NormalX=0 NormalY=0 NormalZ=1 AngleXU=0 Radius=3.5
    g21: LineSegment StartX=-1 StartY=5.25 StartZ=0 EndX=-1 EndY=8.75 EndZ=0
    g22: LineSegment StartX=-1 StartY=8.75 StartZ=0 EndX=-4.03109 EndY=10.5 EndZ=0
    g23: LineSegment StartX=-4.03109 StartY=10.5 StartZ=0 EndX=-7.06218 EndY=8.75 EndZ=0
    g24: LineSegment StartX=-7.06218 StartY=8.75 StartZ=0 EndX=-7.06218 EndY=5.25 EndZ=0
    g25: LineSegment StartX=-7.06218 StartY=5.25 StartZ=0 EndX=-4.03109 EndY=3.5 EndZ=0
    g26: LineSegment StartX=-4.03109 StartY=3.5 StartZ=0 EndX=-1 EndY=5.25 EndZ=0
    g27: Circle [constr] CenterX=-4.03109 CenterY=7 CenterZ=0 NormalX=0 NormalY=0 NormalZ=1 AngleXU=0 Radius=3.5
    g28: LineSegment StartX=-4.96891 StartY=-1.75 StartZ=0 EndX=-4.96891 EndY=1.75 EndZ=0
    g29: LineSegment StartX=-4.96891 StartY=1.75 StartZ=0 EndX=-8 EndY=3.5 EndZ=0
    g30: LineSegment StartX=-8 StartY=3.5 StartZ=0 EndX=-11.0311 EndY=1.75 EndZ=0
    g31: LineSegment StartX=-11.0311 StartY=1.75 StartZ=0 EndX=-11.0311 EndY=-1.75 EndZ=0
    g32: LineSegment StartX=-11.0311 StartY=-1.75 StartZ=0 EndX=-8 EndY=-3.5 EndZ=0
    g33: LineSegment StartX=-8 StartY=-3.5 StartZ=0 EndX=-4.96891 EndY=-1.75 EndZ=0
    g34: Circle [constr] CenterX=-8 CenterY=0 CenterZ=0 NormalX=0 NormalY=0 NormalZ=1 AngleXU=0 Radius=3.5
    g35: LineSegment StartX=-4.03109 StartY=-3.5 StartZ=0 EndX=-7.06218 EndY=-5.25 EndZ=0
    g36: LineSegment StartX=-7.06218 StartY=-5.25 StartZ=0 EndX=-7.06218 EndY=-8.75 EndZ=0
    g37: LineSegment StartX=-7.06218 StartY=-8.75 StartZ=0 EndX=-4.03109 EndY=-10.5 EndZ=0
    g38: LineSegment StartX=-4.03109 StartY=-10.5 StartZ=0 EndX=-1 EndY=-8.75 EndZ=0
    g39: LineSegment StartX=-1 StartY=-8.75 StartZ=0 EndX=-1 EndY=-5.25 EndZ=0
    g40: LineSegment StartX=-1 StartY=-5.25 StartZ=0 EndX=-4.03109 EndY=-3.5 EndZ=0
    g41: Circle [constr] CenterX=-4.03109 CenterY=-7 CenterZ=0 NormalX=0 NormalY=0 NormalZ=1 AngleXU=0 Radius=3.5
    g42: LineSegment StartX=4.03109 StartY=-3.5 StartZ=0 EndX=1 EndY=-5.25 EndZ=0
    g43: LineSegment StartX=1 StartY=-5.25 StartZ=0 EndX=1 EndY=-8.75 EndZ=0
    g44: LineSegment StartX=1 StartY=-8.75 StartZ=0 EndX=4.03109 EndY=-10.5 EndZ=0
    g45: LineSegment StartX=4.03109 StartY=-10.5 StartZ=0 EndX=7.06218 EndY=-8.75 EndZ=0
    g46: LineSegment StartX=7.06218 StartY=-8.75 StartZ=0 EndX=7.06218 EndY=-5.25 EndZ=0
    g47: LineSegment StartX=7.06218 StartY=-5.25 StartZ=0 EndX=4.03109 EndY=-3.5 EndZ=0
    g48: Circle [constr] CenterX=4.03109 CenterY=-7 CenterZ=0 NormalX=0 NormalY=0 NormalZ=1 AngleXU=0 Radius=3.5
  constraints (117):
    c: Coincident(g0,g1)
    c: Coincident(g1,g2)
    c: Coincident(g2,g3)
    c: Coincident(g3,g4)
    c: Coincident(g4,g5)
    c: Coincident(g5,g0)
    c: Equal(g0, g1-g5) x5
    c: PointOnObject(g0,g6)
    c: PointOnObject(g1,g6)
    c: PointOnObject(g2,g6)
    c: PointOnObject(g3,g6)
    c: PointOnObject(g4,g6)
    c: PointOnObject(g5,g6)
    c: Coincident(g6,g-1)
    c: Diameter(g6) = 7
    c: PointOnObject(g0,g-2)
    c: Coincident(g7,g8)
    c: Coincident(g8,g9)
    c: Coincident(g9,g10)
    c: Coincident(g10,g11)
    c: Coincident(g11,g12)
    c: Coincident(g12,g7)
    c: Equal(g7, g8-g12) x5
    c: PointOnObject(g7,g13)
    c: PointOnObject(g8,g13)
    c: PointOnObject(g9,g13)
    c: PointOnObject(g10,g13)
    c: PointOnObject(g11,g13)
    c: PointOnObject(g12,g13)
    c: PointOnObject(g13,g-1)
    c: Diameter(g13) = 7
    c: Distance(g6,g13) = 8
    c: Horizontal(g0,g10)
    c: Coincident(g14,g15)
    c: Coincident(g15,g16)
    c: Coincident(g16,g17)
    c: Coincident(g17,g18)
    c: Coincident(g18,g19)
    c: Coincident(g19,g14)
    c: Equal(g14, g15-g19) x5
    c: PointOnObject(g14,g20)
    c: PointOnObject(g15,g20)
    c: PointOnObject(g16,g20)
    c: PointOnObject(g17,g20)
    c: PointOnObject(g18,g20)
    c: PointOnObject(g19,g20)
    c: Diameter(g20) = 7
    c: DistanceY(g-1,g20) = 7
    c: Vertical(g18)
    c: Distance(g17,g-2) = 1
    c: Coincident(g21,g22)
    c: Coincident(g22,g23)
    c: Coincident(g23,g24)
    c: Coincident(g24,g25)
    c: Coincident(g25,g26)
    c: Coincident(g26,g21)
    c: Equal(g21, g22-g26) x5
    c: PointOnObject(g21,g27)
    c: PointOnObject(g22,g27)
    c: PointOnObject(g23,g27)
    c: PointOnObject(g24,g27)
    c: PointOnObject(g25,g27)
    c: PointOnObject(g26,g27)
    c: Diameter(g27) = 7
    c: DistanceY(g-1,g27) = 7
    c: DistanceX(g21,g-1) = 1
    c: Vertical(g21)
    c: Coincident(g28,g29)
    c: Coincident(g29,g30)
    c: Coincident(g30,g31)
    c: Coincident(g31,g32)
    c: Coincident(g32,g33)
    c: Coincident(g33,g28)
    c: Equal(g28, g29-g33) x5
    c: PointOnObject(g28,g34)
    c: PointOnObject(g29,g34)
    c: PointOnObject(g30,g34)
    c: PointOnObject(g31,g34)
    c: PointOnObject(g32,g34)
    c: PointOnObject(g33,g34)
    c: PointOnObject(g34,g-1)
    c: Diameter(g34) = 7
    c: Vertical(g31)
    c: DistanceX(g34,g-1) = 8
    c: Coincident(g35,g36)
    c: Coincident(g36,g37)
    c: Coincident(g37,g38)
    c: Coincident(g38,g39)
    c: Coincident(g39,g40)
    c: Coincident(g40,g35)
    c: Equal(g35, g36-g40) x5
    c: PointOnObject(g35,g41)
    c: PointOnObject(g36,g41)
    c: PointOnObject(g37,g41)
    c: PointOnObject(g38,g41)
    c: PointOnObject(g39,g41)
    c: PointOnObject(g40,g41)
    c: Coincident(g42,g43)
    c: Coincident(g43,g44)
    c: Coincident(g44,g45)
    c: Coincident(g45,g46)
    c: Coincident(g46,g47)
    c: Coincident(g47,g42)
    c: Equal(g42, g43-g47) x5
    c: PointOnObject(g42,g48)
    c: PointOnObject(g43,g48)
    c: PointOnObject(g44,g48)
    c: PointOnObject(g45,g48)
    c: PointOnObject(g46,g48)
    c: PointOnObject(g47,g48)
    c: Equal(g41,g48)
    c: Diameter(g41) = 7
    c: Vertical(g39)
    c: Vertical(g43)
    c: Distance(g-2,g39) = 1
    c: Symmetric(g38,g43,g-2)
    c: Distance(g41,g-1) = 7
FEATURE [Part::Extrusion] Extrude491  label="hex106"
  Base = -> Sketch499
  Dir = (0,-1,2e-16)
  DirMode = 2
  FaceMakerClass = Part::FaceMakerBullseye
  FaceMakerMode = 3
  LengthFwd = 10
  LengthRev = 0
  Placement = pos=(-4,0,-21) rot=(0,0,1;0rad)
  Solid = true
  Symmetric = false
FEATURE [Sketcher::SketchObject] Sketch500
  ArcFitTolerance = 1e-06
  FullyConstrained = true
  MakeInternals = false
  Placement = pos=(0,0,0) rot=(1,0,0;1.5708rad)
  sketch-geometry (49):
    g0: LineSegment StartX=1e-16 StartY=3.5 StartZ=0 EndX=-3.03109 EndY=1.75 EndZ=0
    g1: LineSegment StartX=-3.03109 StartY=1.75 StartZ=0 EndX=-3.03109 EndY=-1.75 EndZ=0
    g2: LineSegment StartX=-3.03109 StartY=-1.75 StartZ=0 EndX=-1e-16 EndY=-3.5 EndZ=0
    g3: LineSegment StartX=-1e-16 StartY=-3.5 StartZ=0 EndX=3.03109 EndY=-1.75 EndZ=0
    g4: LineSegment StartX=3.03109 StartY=-1.75 StartZ=0 EndX=3.03109 EndY=1.75 EndZ=0
    g5: LineSegment StartX=3.03109 StartY=1.75 StartZ=0 EndX=1e-16 EndY=3.5 EndZ=0
    g6: Circle [constr] CenterX=0 CenterY=0 CenterZ=0 NormalX=0 NormalY=0 NormalZ=1 AngleXU=0 Radius=3.5
    g7: LineSegment StartX=4.96892 StartY=-1.75002 StartZ=0 EndX=8.00002 EndY=-3.5 EndZ=0
    g8: LineSegment StartX=8.00002 StartY=-3.5 StartZ=0 EndX=11.0311 EndY=-1.74998 EndZ=0
    g9: LineSegment StartX=11.0311 StartY=-1.74998 StartZ=0 EndX=11.0311 EndY=1.75002 EndZ=0
    g10: LineSegment StartX=11.0311 StartY=1.75002 StartZ=0 EndX=7.99998 EndY=3.5 EndZ=0
    g11: LineSegment StartX=7.99998 StartY=3.5 StartZ=0 EndX=4.9689 EndY=1.74998 EndZ=0
    g12: LineSegment StartX=4.9689 StartY=1.74998 StartZ=0 EndX=4.96892 EndY=-1.75002 EndZ=0
    g13: Circle [constr] CenterX=8 CenterY=0 CenterZ=0 NormalX=0 NormalY=0 NormalZ=1 AngleXU=0 Radius=3.5
    g14: LineSegment StartX=4.03109 StartY=3.5 StartZ=0 EndX=7.06218 EndY=5.25 EndZ=0
    g15: LineSegment StartX=7.06218 StartY=5.25 StartZ=0 EndX=7.06218 EndY=8.75 EndZ=0
    g16: LineSegment StartX=7.06218 StartY=8.75 StartZ=0 EndX=4.03109 EndY=10.5 EndZ=0
    g17: LineSegment StartX=4.03109 StartY=10.5 StartZ=0 EndX=1 EndY=8.75 EndZ=0
    g18: LineSegment StartX=1 StartY=8.75 StartZ=0 EndX=1 EndY=5.25 EndZ=0
    g19: LineSegment StartX=1 StartY=5.25 StartZ=0 EndX=4.03109 EndY=3.5 EndZ=0
    g20: Circle [constr] CenterX=4.03109 CenterY=7 CenterZ=0 NormalX=0 NormalY=0 NormalZ=1 AngleXU=0 Radius=3.5
    g21: LineSegment StartX=-1 StartY=5.25 StartZ=0 EndX=-1 EndY=8.75 EndZ=0
    g22: LineSegment StartX=-1 StartY=8.75 StartZ=0 EndX=-4.03109 EndY=10.5 EndZ=0
    g23: LineSegment StartX=-4.03109 StartY=10.5 StartZ=0 EndX=-7.06218 EndY=8.75 EndZ=0
    g24: LineSegment StartX=-7.06218 StartY=8.75 StartZ=0 EndX=-7.06218 EndY=5.25 EndZ=0
    g25: LineSegment StartX=-7.06218 StartY=5.25 StartZ=0 EndX=-4.03109 EndY=3.5 EndZ=0
    g26: LineSegment StartX=-4.03109 StartY=3.5 StartZ=0 EndX=-1 EndY=5.25 EndZ=0
    g27: Circle [constr] CenterX=-4.03109 CenterY=7 CenterZ=0 NormalX=0 NormalY=0 NormalZ=1 AngleXU=0 Radius=3.5
    g28: LineSegment StartX=-4.96891 StartY=-1.75 StartZ=0 EndX=-4.96891 EndY=1.75 EndZ=0
    g29: LineSegment StartX=-4.96891 StartY=1.75 StartZ=0 EndX=-8 EndY=3.5 EndZ=0
    g30: LineSegment StartX=-8 StartY=3.5 StartZ=0 EndX=-11.0311 EndY=1.75 EndZ=0
    g31: LineSegment StartX=-11.0311 StartY=1.75 StartZ=0 EndX=-11.0311 EndY=-1.75 EndZ=0
    g32: LineSegment StartX=-11.0311 StartY=-1.75 StartZ=0 EndX=-8 EndY=-3.5 EndZ=0
    g33: LineSegment StartX=-8 StartY=-3.5 StartZ=0 EndX=-4.96891 EndY=-1.75 EndZ=0
    g34: Circle [constr] CenterX=-8 CenterY=0 CenterZ=0 NormalX=0 NormalY=0 NormalZ=1 AngleXU=0 Radius=3.5
    g35: LineSegment StartX=-4.03109 StartY=-3.5 StartZ=0 EndX=-7.06218 EndY=-5.25 EndZ=0
    g36: LineSegment StartX=-7.06218 StartY=-5.25 StartZ=0 EndX=-7.06218 EndY=-8.75 EndZ=0
    g37: LineSegment StartX=-7.06218 StartY=-8.75 StartZ=0 EndX=-4.03109 EndY=-10.5 EndZ=0
    g38: LineSegment StartX=-4.03109 StartY=-10.5 StartZ=0 EndX=-1 EndY=-8.75 EndZ=0
    g39: LineSegment StartX=-1 StartY=-8.75 StartZ=0 EndX=-1 EndY=-5.25 EndZ=0
    g40: LineSegment StartX=-1 StartY=-5.25 StartZ=0 EndX=-4.03109 EndY=-3.5 EndZ=0
    g41: Circle [constr] CenterX=-4.03109 CenterY=-7 CenterZ=0 NormalX=0 NormalY=0 NormalZ=1 AngleXU=0 Radius=3.5
    g42: LineSegment StartX=4.03109 StartY=-3.5 StartZ=0 EndX=1 EndY=-5.25 EndZ=0
    g43: LineSegment StartX=1 StartY=-5.25 StartZ=0 EndX=1 EndY=-8.75 EndZ=0
    g44: LineSegment StartX=1 StartY=-8.75 StartZ=0 EndX=4.03109 EndY=-10.5 EndZ=0
    g45: LineSegment StartX=4.03109 StartY=-10.5 StartZ=0 EndX=7.06218 EndY=-8.75 EndZ=0
    g46: LineSegment StartX=7.06218 StartY=-8.75 StartZ=0 EndX=7.06218 EndY=-5.25 EndZ=0
    g47: LineSegment StartX=7.06218 StartY=-5.25 StartZ=0 EndX=4.03109 EndY=-3.5 EndZ=0
    g48: Circle [constr] CenterX=4.03109 CenterY=-7 CenterZ=0 NormalX=0 NormalY=0 NormalZ=1 AngleXU=0 Radius=3.5
  constraints (117):
    c: Coincident(g0,g1)
    c: Coincident(g1,g2)
    c: Coincident(g2,g3)
    c: Coincident(g3,g4)
    c: Coincident(g4,g5)
    c: Coincident(g5,g0)
    c: Equal(g0, g1-g5) x5
    c: PointOnObject(g0,g6)
    c: PointOnObject(g1,g6)
    c: PointOnObject(g2,g6)
    c: PointOnObject(g3,g6)
    c: PointOnObject(g4,g6)
    c: PointOnObject(g5,g6)
    c: Coincident(g6,g-1)
    c: Diameter(g6) = 7
    c: PointOnObject(g0,g-2)
    c: Coincident(g7,g8)
    c: Coincident(g8,g9)
    c: Coincident(g9,g10)
    c: Coincident(g10,g11)
    c: Coincident(g11,g12)
    c: Coincident(g12,g7)
    c: Equal(g7, g8-g12) x5
    c: PointOnObject(g7,g13)
    c: PointOnObject(g8,g13)
    c: PointOnObject(g9,g13)
    c: PointOnObject(g10,g13)
    c: PointOnObject(g11,g13)
    c: PointOnObject(g12,g13)
    c: PointOnObject(g13,g-1)
    c: Diameter(g13) = 7
    c: Distance(g6,g13) = 8
    c: Horizontal(g0,g10)
    c: Coincident(g14,g15)
    c: Coincident(g15,g16)
    c: Coincident(g16,g17)
    c: Coincident(g17,g18)
    c: Coincident(g18,g19)
    c: Coincident(g19,g14)
    c: Equal(g14, g15-g19) x5
    c: PointOnObject(g14,g20)
    c: PointOnObject(g15,g20)
    c: PointOnObject(g16,g20)
    c: PointOnObject(g17,g20)
    c: PointOnObject(g18,g20)
    c: PointOnObject(g19,g20)
    c: Diameter(g20) = 7
    c: DistanceY(g-1,g20) = 7
    c: Vertical(g18)
    c: Distance(g17,g-2) = 1
    c: Coincident(g21,g22)
    c: Coincident(g22,g23)
    c: Coincident(g23,g24)
    c: Coincident(g24,g25)
    c: Coincident(g25,g26)
    c: Coincident(g26,g21)
    c: Equal(g21, g22-g26) x5
    c: PointOnObject(g21,g27)
    c: PointOnObject(g22,g27)
    c: PointOnObject(g23,g27)
    c: PointOnObject(g24,g27)
    c: PointOnObject(g25,g27)
    c: PointOnObject(g26,g27)
    c: Diameter(g27) = 7
    c: DistanceY(g-1,g27) = 7
    c: DistanceX(g21,g-1) = 1
    c: Vertical(g21)
    c: Coincident(g28,g29)
    c: Coincident(g29,g30)
    c: Coincident(g30,g31)
    c: Coincident(g31,g32)
    c: Coincident(g32,g33)
    c: Coincident(g33,g28)
    c: Equal(g28, g29-g33) x5
    c: PointOnObject(g28,g34)
    c: PointOnObject(g29,g34)
    c: PointOnObject(g30,g34)
    c: PointOnObject(g31,g34)
    c: PointOnObject(g32,g34)
    c: PointOnObject(g33,g34)
    c: PointOnObject(g34,g-1)
    c: Diameter(g34) = 7
    c: Vertical(g31)
    c: DistanceX(g34,g-1) = 8
    c: Coincident(g35,g36)
    c: Coincident(g36,g37)
    c: Coincident(g37,g38)
    c: Coincident(g38,g39)
    c: Coincident(g39,g40)
    c: Coincident(g40,g35)
    c: Equal(g35, g36-g40) x5
    c: PointOnObject(g35,g41)
    c: PointOnObject(g36,g41)
    c: PointOnObject(g37,g41)
    c: PointOnObject(g38,g41)
    c: PointOnObject(g39,g41)
    c: PointOnObject(g40,g41)
    c: Coincident(g42,g43)
    c: Coincident(g43,g44)
    c: Coincident(g44,g45)
    c: Coincident(g45,g46)
    c: Coincident(g46,g47)
    c: Coincident(g47,g42)
    c: Equal(g42, g43-g47) x5
    c: PointOnObject(g42,g48)
    c: PointOnObject(g43,g48)
    c: PointOnObject(g44,g48)
    c: PointOnObject(g45,g48)
    c: PointOnObject(g46,g48)
    c: PointOnObject(g47,g48)
    c: Equal(g41,g48)
    c: Diameter(g41) = 7
    c: Vertical(g39)
    c: Vertical(g43)
    c: Distance(g-2,g39) = 1
    c: Symmetric(g38,g43,g-2)
    c: Distance(g41,g-1) = 7
FEATURE [Part::Extrusion] Extrude492  label="hex107"
  Base = -> Sketch500
  Dir = (0,-1,2e-16)
  DirMode = 2
  FaceMakerClass = Part::FaceMakerBullseye
  FaceMakerMode = 3
  LengthFwd = 10
  LengthRev = 0
  Placement = pos=(16,0,-14) rot=(0,0,1;0rad)
  Solid = true
  Symmetric = false
FEATURE [Sketcher::SketchObject] Sketch501
  ArcFitTolerance = 1e-06
  FullyConstrained = true
  MakeInternals = false
  Placement = pos=(0,0,0) rot=(1,0,0;1.5708rad)
  sketch-geometry (49):
    g0: LineSegment StartX=1e-16 StartY=3.5 StartZ=0 EndX=-3.03109 EndY=1.75 EndZ=0
    g1: LineSegment StartX=-3.03109 StartY=1.75 StartZ=0 EndX=-3.03109 EndY=-1.75 EndZ=0
    g2: LineSegment StartX=-3.03109 StartY=-1.75 StartZ=0 EndX=-1e-16 EndY=-3.5 EndZ=0
    g3: LineSegment StartX=-1e-16 StartY=-3.5 StartZ=0 EndX=3.03109 EndY=-1.75 EndZ=0
    g4: LineSegment StartX=3.03109 StartY=-1.75 StartZ=0 EndX=3.03109 EndY=1.75 EndZ=0
    g5: LineSegment StartX=3.03109 StartY=1.75 StartZ=0 EndX=1e-16 EndY=3.5 EndZ=0
    g6: Circle [constr] CenterX=0 CenterY=0 CenterZ=0 NormalX=0 NormalY=0 NormalZ=1 AngleXU=0 Radius=3.5
    g7: LineSegment StartX=4.96892 StartY=-1.75002 StartZ=0 EndX=8.00002 EndY=-3.5 EndZ=0
    g8: LineSegment StartX=8.00002 StartY=-3.5 StartZ=0 EndX=11.0311 EndY=-1.74998 EndZ=0
    g9: LineSegment StartX=11.0311 StartY=-1.74998 StartZ=0 EndX=11.0311 EndY=1.75002 EndZ=0
    g10: LineSegment StartX=11.0311 StartY=1.75002 StartZ=0 EndX=7.99998 EndY=3.5 EndZ=0
    g11: LineSegment StartX=7.99998 StartY=3.5 StartZ=0 EndX=4.9689 EndY=1.74998 EndZ=0
    g12: LineSegment StartX=4.9689 StartY=1.74998 StartZ=0 EndX=4.96892 EndY=-1.75002 EndZ=0
    g13: Circle [constr] CenterX=8 CenterY=0 CenterZ=0 NormalX=0 NormalY=0 NormalZ=1 AngleXU=0 Radius=3.5
    g14: LineSegment StartX=4.03109 StartY=3.5 StartZ=0 EndX=7.06218 EndY=5.25 EndZ=0
    g15: LineSegment StartX=7.06218 StartY=5.25 StartZ=0 EndX=7.06218 EndY=8.75 EndZ=0
    g16: LineSegment StartX=7.06218 StartY=8.75 StartZ=0 EndX=4.03109 EndY=10.5 EndZ=0
    g17: LineSegment StartX=4.03109 StartY=10.5 StartZ=0 EndX=1 EndY=8.75 EndZ=0
    g18: LineSegment StartX=1 StartY=8.75 StartZ=0 EndX=1 EndY=5.25 EndZ=0
    g19: LineSegment StartX=1 StartY=5.25 StartZ=0 EndX=4.03109 EndY=3.5 EndZ=0
    g20: Circle [constr] CenterX=4.03109 CenterY=7 CenterZ=0 NormalX=0 NormalY=0 NormalZ=1 AngleXU=0 Radius=3.5
    g21: LineSegment StartX=-1 StartY=5.25 StartZ=0 EndX=-1 EndY=8.75 EndZ=0
    g22: LineSegment StartX=-1 StartY=8.75 StartZ=0 EndX=-4.03109 EndY=10.5 EndZ=0
    g23: LineSegment StartX=-4.03109 StartY=10.5 StartZ=0 EndX=-7.06218 EndY=8.75 EndZ=0
    g24: LineSegment StartX=-7.06218 StartY=8.75 StartZ=0 EndX=-7.06218 EndY=5.25 EndZ=0
    g25: LineSegment StartX=-7.06218 StartY=5.25 StartZ=0 EndX=-4.03109 EndY=3.5 EndZ=0
    g26: LineSegment StartX=-4.03109 StartY=3.5 StartZ=0 EndX=-1 EndY=5.25 EndZ=0
    g27: Circle [constr] CenterX=-4.03109 CenterY=7 CenterZ=0 NormalX=0 NormalY=0 NormalZ=1 AngleXU=0 Radius=3.5
    g28: LineSegment StartX=-4.96891 StartY=-1.75 StartZ=0 EndX=-4.96891 EndY=1.75 EndZ=0
    g29: LineSegment StartX=-4.96891 StartY=1.75 StartZ=0 EndX=-8 EndY=3.5 EndZ=0
    g30: LineSegment StartX=-8 StartY=3.5 StartZ=0 EndX=-11.0311 EndY=1.75 EndZ=0
    g31: LineSegment StartX=-11.0311 StartY=1.75 StartZ=0 EndX=-11.0311 EndY=-1.75 EndZ=0
    g32: LineSegment StartX=-11.0311 StartY=-1.75 StartZ=0 EndX=-8 EndY=-3.5 EndZ=0
    g33: LineSegment StartX=-8 StartY=-3.5 StartZ=0 EndX=-4.96891 EndY=-1.75 EndZ=0
    g34: Circle [constr] CenterX=-8 CenterY=0 CenterZ=0 NormalX=0 NormalY=0 NormalZ=1 AngleXU=0 Radius=3.5
    g35: LineSegment StartX=-4.03109 StartY=-3.5 StartZ=0 EndX=-7.06218 EndY=-5.25 EndZ=0
    g36: LineSegment StartX=-7.06218 StartY=-5.25 StartZ=0 EndX=-7.06218 EndY=-8.75 EndZ=0
    g37: LineSegment StartX=-7.06218 StartY=-8.75 StartZ=0 EndX=-4.03109 EndY=-10.5 EndZ=0
    g38: LineSegment StartX=-4.03109 StartY=-10.5 StartZ=0 EndX=-1 EndY=-8.75 EndZ=0
    g39: LineSegment StartX=-1 StartY=-8.75 StartZ=0 EndX=-1 EndY=-5.25 EndZ=0
    g40: LineSegment StartX=-1 StartY=-5.25 StartZ=0 EndX=-4.03109 EndY=-3.5 EndZ=0
    g41: Circle [constr] CenterX=-4.03109 CenterY=-7 CenterZ=0 NormalX=0 NormalY=0 NormalZ=1 AngleXU=0 Radius=3.5
    g42: LineSegment StartX=4.03109 StartY=-3.5 StartZ=0 EndX=1 EndY=-5.25 EndZ=0
    g43: LineSegment StartX=1 StartY=-5.25 StartZ=0 EndX=1 EndY=-8.75 EndZ=0
    g44: LineSegment StartX=1 StartY=-8.75 StartZ=0 EndX=4.03109 EndY=-10.5 EndZ=0
    g45: LineSegment StartX=4.03109 StartY=-10.5 StartZ=0 EndX=7.06218 EndY=-8.75 EndZ=0
    g46: LineSegment StartX=7.06218 StartY=-8.75 StartZ=0 EndX=7.06218 EndY=-5.25 EndZ=0
    g47: LineSegment StartX=7.06218 StartY=-5.25 StartZ=0 EndX=4.03109 EndY=-3.5 EndZ=0
    g48: Circle [constr] CenterX=4.03109 CenterY=-7 CenterZ=0 NormalX=0 NormalY=0 NormalZ=1 AngleXU=0 Radius=3.5
  constraints (117):
    c: Coincident(g0,g1)
    c: Coincident(g1,g2)
    c: Coincident(g2,g3)
    c: Coincident(g3,g4)
    c: Coincident(g4,g5)
    c: Coincident(g5,g0)
    c: Equal(g0, g1-g5) x5
    c: PointOnObject(g0,g6)
    c: PointOnObject(g1,g6)
    c: PointOnObject(g2,g6)
    c: PointOnObject(g3,g6)
    c: PointOnObject(g4,g6)
    c: PointOnObject(g5,g6)
    c: Coincident(g6,g-1)
    c: Diameter(g6) = 7
    c: PointOnObject(g0,g-2)
    c: Coincident(g7,g8)
    c: Coincident(g8,g9)
    c: Coincident(g9,g10)
    c: Coincident(g10,g11)
    c: Coincident(g11,g12)
    c: Coincident(g12,g7)
    c: Equal(g7, g8-g12) x5
    c: PointOnObject(g7,g13)
    c: PointOnObject(g8,g13)
    c: PointOnObject(g9,g13)
    c: PointOnObject(g10,g13)
    c: PointOnObject(g11,g13)
    c: PointOnObject(g12,g13)
    c: PointOnObject(g13,g-1)
    c: Diameter(g13) = 7
    c: Distance(g6,g13) = 8
    c: Horizontal(g0,g10)
    c: Coincident(g14,g15)
    c: Coincident(g15,g16)
    c: Coincident(g16,g17)
    c: Coincident(g17,g18)
    c: Coincident(g18,g19)
    c: Coincident(g19,g14)
    c: Equal(g14, g15-g19) x5
    c: PointOnObject(g14,g20)
    c: PointOnObject(g15,g20)
    c: PointOnObject(g16,g20)
    c: PointOnObject(g17,g20)
    c: PointOnObject(g18,g20)
    c: PointOnObject(g19,g20)
    c: Diameter(g20) = 7
    c: DistanceY(g-1,g20) = 7
    c: Vertical(g18)
    c: Distance(g17,g-2) = 1
    c: Coincident(g21,g22)
    c: Coincident(g22,g23)
    c: Coincident(g23,g24)
    c: Coincident(g24,g25)
    c: Coincident(g25,g26)
    c: Coincident(g26,g21)
    c: Equal(g21, g22-g26) x5
    c: PointOnObject(g21,g27)
    c: PointOnObject(g22,g27)
    c: PointOnObject(g23,g27)
    c: PointOnObject(g24,g27)
    c: PointOnObject(g25,g27)
    c: PointOnObject(g26,g27)
    c: Diameter(g27) = 7
    c: DistanceY(g-1,g27) = 7
    c: DistanceX(g21,g-1) = 1
    c: Vertical(g21)
    c: Coincident(g28,g29)
    c: Coincident(g29,g30)
    c: Coincident(g30,g31)
    c: Coincident(g31,g32)
    c: Coincident(g32,g33)
    c: Coincident(g33,g28)
    c: Equal(g28, g29-g33) x5
    c: PointOnObject(g28,g34)
    c: PointOnObject(g29,g34)
    c: PointOnObject(g30,g34)
    c: PointOnObject(g31,g34)
    c: PointOnObject(g32,g34)
    c: PointOnObject(g33,g34)
    c: PointOnObject(g34,g-1)
    c: Diameter(g34) = 7
    c: Vertical(g31)
    c: DistanceX(g34,g-1) = 8
    c: Coincident(g35,g36)
    c: Coincident(g36,g37)
    c: Coincident(g37,g38)
    c: Coincident(g38,g39)
    c: Coincident(g39,g40)
    c: Coincident(g40,g35)
    c: Equal(g35, g36-g40) x5
    c: PointOnObject(g35,g41)
    c: PointOnObject(g36,g41)
    c: PointOnObject(g37,g41)
    c: PointOnObject(g38,g41)
    c: PointOnObject(g39,g41)
    c: PointOnObject(g40,g41)
    c: Coincident(g42,g43)
    c: Coincident(g43,g44)
    c: Coincident(g44,g45)
    c: Coincident(g45,g46)
    c: Coincident(g46,g47)
    c: Coincident(g47,g42)
    c: Equal(g42, g43-g47) x5
    c: PointOnObject(g42,g48)
    c: PointOnObject(g43,g48)
    c: PointOnObject(g44,g48)
    c: PointOnObject(g45,g48)
    c: PointOnObject(g46,g48)
    c: PointOnObject(g47,g48)
    c: Equal(g41,g48)
    c: Diameter(g41) = 7
    c: Vertical(g39)
    c: Vertical(g43)
    c: Distance(g-2,g39) = 1
    c: Symmetric(g38,g43,g-2)
    c: Distance(g41,g-1) = 7
FEATURE [Part::Extrusion] Extrude493  label="hex108"
  Base = -> Sketch501
  Dir = (0,-1,2e-16)
  DirMode = 2
  FaceMakerClass = Part::FaceMakerBullseye
  FaceMakerMode = 3
  LengthFwd = 10
  LengthRev = 0
  Placement = pos=(-4,0,21) rot=(0,0,1;0rad)
  Solid = true
  Symmetric = false
FEATURE [Sketcher::SketchObject] Sketch502
  ArcFitTolerance = 1e-06
  FullyConstrained = true
  MakeInternals = false
  Placement = pos=(0,0,0) rot=(1,0,0;1.5708rad)
  sketch-geometry (49):
    g0: LineSegment StartX=1e-16 StartY=3.5 StartZ=0 EndX=-3.03109 EndY=1.75 EndZ=0
    g1: LineSegment StartX=-3.03109 StartY=1.75 StartZ=0 EndX=-3.03109 EndY=-1.75 EndZ=0
    g2: LineSegment StartX=-3.03109 StartY=-1.75 StartZ=0 EndX=-1e-16 EndY=-3.5 EndZ=0
    g3: LineSegment StartX=-1e-16 StartY=-3.5 StartZ=0 EndX=3.03109 EndY=-1.75 EndZ=0
    g4: LineSegment StartX=3.03109 StartY=-1.75 StartZ=0 EndX=3.03109 EndY=1.75 EndZ=0
    g5: LineSegment StartX=3.03109 StartY=1.75 StartZ=0 EndX=1e-16 EndY=3.5 EndZ=0
    g6: Circle [constr] CenterX=0 CenterY=0 CenterZ=0 NormalX=0 NormalY=0 NormalZ=1 AngleXU=0 Radius=3.5
    g7: LineSegment StartX=4.96892 StartY=-1.75002 StartZ=0 EndX=8.00002 EndY=-3.5 EndZ=0
    g8: LineSegment StartX=8.00002 StartY=-3.5 StartZ=0 EndX=11.0311 EndY=-1.74998 EndZ=0
    g9: LineSegment StartX=11.0311 StartY=-1.74998 StartZ=0 EndX=11.0311 EndY=1.75002 EndZ=0
    g10: LineSegment StartX=11.0311 StartY=1.75002 StartZ=0 EndX=7.99998 EndY=3.5 EndZ=0
    g11: LineSegment StartX=7.99998 StartY=3.5 StartZ=0 EndX=4.9689 EndY=1.74998 EndZ=0
    g12: LineSegment StartX=4.9689 StartY=1.74998 StartZ=0 EndX=4.96892 EndY=-1.75002 EndZ=0
    g13: Circle [constr] CenterX=8 CenterY=0 CenterZ=0 NormalX=0 NormalY=0 NormalZ=1 AngleXU=0 Radius=3.5
    g14: LineSegment StartX=4.03109 StartY=3.5 StartZ=0 EndX=7.06218 EndY=5.25 EndZ=0
    g15: LineSegment StartX=7.06218 StartY=5.25 StartZ=0 EndX=7.06218 EndY=8.75 EndZ=0
    g16: LineSegment StartX=7.06218 StartY=8.75 StartZ=0 EndX=4.03109 EndY=10.5 EndZ=0
    g17: LineSegment StartX=4.03109 StartY=10.5 StartZ=0 EndX=1 EndY=8.75 EndZ=0
    g18: LineSegment StartX=1 StartY=8.75 StartZ=0 EndX=1 EndY=5.25 EndZ=0
    g19: LineSegment StartX=1 StartY=5.25 StartZ=0 EndX=4.03109 EndY=3.5 EndZ=0
    g20: Circle [constr] CenterX=4.03109 CenterY=7 CenterZ=0 NormalX=0 NormalY=0 NormalZ=1 AngleXU=0 Radius=3.5
    g21: LineSegment StartX=-1 StartY=5.25 StartZ=0 EndX=-1 EndY=8.75 EndZ=0
    g22: LineSegment StartX=-1 StartY=8.75 StartZ=0 EndX=-4.03109 EndY=10.5 EndZ=0
    g23: LineSegment StartX=-4.03109 StartY=10.5 StartZ=0 EndX=-7.06218 EndY=8.75 EndZ=0
    g24: LineSegment StartX=-7.06218 StartY=8.75 StartZ=0 EndX=-7.06218 EndY=5.25 EndZ=0
    g25: LineSegment StartX=-7.06218 StartY=5.25 StartZ=0 EndX=-4.03109 EndY=3.5 EndZ=0
    g26: LineSegment StartX=-4.03109 StartY=3.5 StartZ=0 EndX=-1 EndY=5.25 EndZ=0
    g27: Circle [constr] CenterX=-4.03109 CenterY=7 CenterZ=0 NormalX=0 NormalY=0 NormalZ=1 AngleXU=0 Radius=3.5
    g28: LineSegment StartX=-4.96891 StartY=-1.75 StartZ=0 EndX=-4.96891 EndY=1.75 EndZ=0
    g29: LineSegment StartX=-4.96891 StartY=1.75 StartZ=0 EndX=-8 EndY=3.5 EndZ=0
    g30: LineSegment StartX=-8 StartY=3.5 StartZ=0 EndX=-11.0311 EndY=1.75 EndZ=0
    g31: LineSegment StartX=-11.0311 StartY=1.75 StartZ=0 EndX=-11.0311 EndY=-1.75 EndZ=0
    g32: LineSegment StartX=-11.0311 StartY=-1.75 StartZ=0 EndX=-8 EndY=-3.5 EndZ=0
    g33: LineSegment StartX=-8 StartY=-3.5 StartZ=0 EndX=-4.96891 EndY=-1.75 EndZ=0
    g34: Circle [constr] CenterX=-8 CenterY=0 CenterZ=0 NormalX=0 NormalY=0 NormalZ=1 AngleXU=0 Radius=3.5
    g35: LineSegment StartX=-4.03109 StartY=-3.5 StartZ=0 EndX=-7.06218 EndY=-5.25 EndZ=0
    g36: LineSegment StartX=-7.06218 StartY=-5.25 StartZ=0 EndX=-7.06218 EndY=-8.75 EndZ=0
    g37: LineSegment StartX=-7.06218 StartY=-8.75 StartZ=0 EndX=-4.03109 EndY=-10.5 EndZ=0
    g38: LineSegment StartX=-4.03109 StartY=-10.5 StartZ=0 EndX=-1 EndY=-8.75 EndZ=0
    g39: LineSegment StartX=-1 StartY=-8.75 StartZ=0 EndX=-1 EndY=-5.25 EndZ=0
    g40: LineSegment StartX=-1 StartY=-5.25 StartZ=0 EndX=-4.03109 EndY=-3.5 EndZ=0
    g41: Circle [constr] CenterX=-4.03109 CenterY=-7 CenterZ=0 NormalX=0 NormalY=0 NormalZ=1 AngleXU=0 Radius=3.5
    g42: LineSegment StartX=4.03109 StartY=-3.5 StartZ=0 EndX=1 EndY=-5.25 EndZ=0
    g43: LineSegment StartX=1 StartY=-5.25 StartZ=0 EndX=1 EndY=-8.75 EndZ=0
    g44: LineSegment StartX=1 StartY=-8.75 StartZ=0 EndX=4.03109 EndY=-10.5 EndZ=0
    g45: LineSegment StartX=4.03109 StartY=-10.5 StartZ=0 EndX=7.06218 EndY=-8.75 EndZ=0
    g46: LineSegment StartX=7.06218 StartY=-8.75 StartZ=0 EndX=7.06218 EndY=-5.25 EndZ=0
    g47: LineSegment StartX=7.06218 StartY=-5.25 StartZ=0 EndX=4.03109 EndY=-3.5 EndZ=0
    g48: Circle [constr] CenterX=4.03109 CenterY=-7 CenterZ=0 NormalX=0 NormalY=0 NormalZ=1 AngleXU=0 Radius=3.5
  constraints (117):
    c: Coincident(g0,g1)
    c: Coincident(g1,g2)
    c: Coincident(g2,g3)
    c: Coincident(g3,g4)
    c: Coincident(g4,g5)
    c: Coincident(g5,g0)
    c: Equal(g0, g1-g5) x5
    c: PointOnObject(g0,g6)
    c: PointOnObject(g1,g6)
    c: PointOnObject(g2,g6)
    c: PointOnObject(g3,g6)
    c: PointOnObject(g4,g6)
    c: PointOnObject(g5,g6)
    c: Coincident(g6,g-1)
    c: Diameter(g6) = 7
    c: PointOnObject(g0,g-2)
    c: Coincident(g7,g8)
    c: Coincident(g8,g9)
    c: Coincident(g9,g10)
    c: Coincident(g10,g11)
    c: Coincident(g11,g12)
    c: Coincident(g12,g7)
    c: Equal(g7, g8-g12) x5
    c: PointOnObject(g7,g13)
    c: PointOnObject(g8,g13)
    c: PointOnObject(g9,g13)
    c: PointOnObject(g10,g13)
    c: PointOnObject(g11,g13)
    c: PointOnObject(g12,g13)
    c: PointOnObject(g13,g-1)
    c: Diameter(g13) = 7
    c: Distance(g6,g13) = 8
    c: Horizontal(g0,g10)
    c: Coincident(g14,g15)
    c: Coincident(g15,g16)
    c: Coincident(g16,g17)
    c: Coincident(g17,g18)
    c: Coincident(g18,g19)
    c: Coincident(g19,g14)
    c: Equal(g14, g15-g19) x5
    c: PointOnObject(g14,g20)
    c: PointOnObject(g15,g20)
    c: PointOnObject(g16,g20)
    c: PointOnObject(g17,g20)
    c: PointOnObject(g18,g20)
    c: PointOnObject(g19,g20)
    c: Diameter(g20) = 7
    c: DistanceY(g-1,g20) = 7
    c: Vertical(g18)
    c: Distance(g17,g-2) = 1
    c: Coincident(g21,g22)
    c: Coincident(g22,g23)
    c: Coincident(g23,g24)
    c: Coincident(g24,g25)
    c: Coincident(g25,g26)
    c: Coincident(g26,g21)
    c: Equal(g21, g22-g26) x5
    c: PointOnObject(g21,g27)
    c: PointOnObject(g22,g27)
    c: PointOnObject(g23,g27)
    c: PointOnObject(g24,g27)
    c: PointOnObject(g25,g27)
    c: PointOnObject(g26,g27)
    c: Diameter(g27) = 7
    c: DistanceY(g-1,g27) = 7
    c: DistanceX(g21,g-1) = 1
    c: Vertical(g21)
    c: Coincident(g28,g29)
    c: Coincident(g29,g30)
    c: Coincident(g30,g31)
    c: Coincident(g31,g32)
    c: Coincident(g32,g33)
    c: Coincident(g33,g28)
    c: Equal(g28, g29-g33) x5
    c: PointOnObject(g28,g34)
    c: PointOnObject(g29,g34)
    c: PointOnObject(g30,g34)
    c: PointOnObject(g31,g34)
    c: PointOnObject(g32,g34)
    c: PointOnObject(g33,g34)
    c: PointOnObject(g34,g-1)
    c: Diameter(g34) = 7
    c: Vertical(g31)
    c: DistanceX(g34,g-1) = 8
    c: Coincident(g35,g36)
    c: Coincident(g36,g37)
    c: Coincident(g37,g38)
    c: Coincident(g38,g39)
    c: Coincident(g39,g40)
    c: Coincident(g40,g35)
    c: Equal(g35, g36-g40) x5
    c: PointOnObject(g35,g41)
    c: PointOnObject(g36,g41)
    c: PointOnObject(g37,g41)
    c: PointOnObject(g38,g41)
    c: PointOnObject(g39,g41)
    c: PointOnObject(g40,g41)
    c: Coincident(g42,g43)
    c: Coincident(g43,g44)
    c: Coincident(g44,g45)
    c: Coincident(g45,g46)
    c: Coincident(g46,g47)
    c: Coincident(g47,g42)
    c: Equal(g42, g43-g47) x5
    c: PointOnObject(g42,g48)
    c: PointOnObject(g43,g48)
    c: PointOnObject(g44,g48)
    c: PointOnObject(g45,g48)
    c: PointOnObject(g46,g48)
    c: PointOnObject(g47,g48)
    c: Equal(g41,g48)
    c: Diameter(g41) = 7
    c: Vertical(g39)
    c: Vertical(g43)
    c: Distance(g-2,g39) = 1
    c: Symmetric(g38,g43,g-2)
    c: Distance(g41,g-1) = 7
FEATURE [Part::Extrusion] Extrude494  label="hex109"
  Base = -> Sketch502
  Dir = (0,-1,2e-16)
  DirMode = 2
  FaceMakerClass = Part::FaceMakerBullseye
  FaceMakerMode = 3
  LengthFwd = 10
  LengthRev = 0
  Placement = pos=(12,0,-35) rot=(0,0,1;0rad)
  Solid = true
  Symmetric = false
FEATURE [Sketcher::SketchObject] Sketch503
  ArcFitTolerance = 1e-06
  FullyConstrained = true
  MakeInternals = false
  Placement = pos=(0,0,0) rot=(1,0,0;1.5708rad)
  sketch-geometry (49):
    g0: LineSegment StartX=1e-16 StartY=3.5 StartZ=0 EndX=-3.03109 EndY=1.75 EndZ=0
    g1: LineSegment StartX=-3.03109 StartY=1.75 StartZ=0 EndX=-3.03109 EndY=-1.75 EndZ=0
    g2: LineSegment StartX=-3.03109 StartY=-1.75 StartZ=0 EndX=-1e-16 EndY=-3.5 EndZ=0
    g3: LineSegment StartX=-1e-16 StartY=-3.5 StartZ=0 EndX=3.03109 EndY=-1.75 EndZ=0
    g4: LineSegment StartX=3.03109 StartY=-1.75 StartZ=0 EndX=3.03109 EndY=1.75 EndZ=0
    g5: LineSegment StartX=3.03109 StartY=1.75 StartZ=0 EndX=1e-16 EndY=3.5 EndZ=0
    g6: Circle [constr] CenterX=0 CenterY=0 CenterZ=0 NormalX=0 NormalY=0 NormalZ=1 AngleXU=0 Radius=3.5
    g7: LineSegment StartX=4.96892 StartY=-1.75002 StartZ=0 EndX=8.00002 EndY=-3.5 EndZ=0
    g8: LineSegment StartX=8.00002 StartY=-3.5 StartZ=0 EndX=11.0311 EndY=-1.74998 EndZ=0
    g9: LineSegment StartX=11.0311 StartY=-1.74998 StartZ=0 EndX=11.0311 EndY=1.75002 EndZ=0
    g10: LineSegment StartX=11.0311 StartY=1.75002 StartZ=0 EndX=7.99998 EndY=3.5 EndZ=0
    g11: LineSegment StartX=7.99998 StartY=3.5 StartZ=0 EndX=4.9689 EndY=1.74998 EndZ=0
    g12: LineSegment StartX=4.9689 StartY=1.74998 StartZ=0 EndX=4.96892 EndY=-1.75002 EndZ=0
    g13: Circle [constr] CenterX=8 CenterY=0 CenterZ=0 NormalX=0 NormalY=0 NormalZ=1 AngleXU=0 Radius=3.5
    g14: LineSegment StartX=4.03109 StartY=3.5 StartZ=0 EndX=7.06218 EndY=5.25 EndZ=0
    g15: LineSegment StartX=7.06218 StartY=5.25 StartZ=0 EndX=7.06218 EndY=8.75 EndZ=0
    g16: LineSegment StartX=7.06218 StartY=8.75 StartZ=0 EndX=4.03109 EndY=10.5 EndZ=0
    g17: LineSegment StartX=4.03109 StartY=10.5 StartZ=0 EndX=1 EndY=8.75 EndZ=0
    g18: LineSegment StartX=1 StartY=8.75 StartZ=0 EndX=1 EndY=5.25 EndZ=0
    g19: LineSegment StartX=1 StartY=5.25 StartZ=0 EndX=4.03109 EndY=3.5 EndZ=0
    g20: Circle [constr] CenterX=4.03109 CenterY=7 CenterZ=0 NormalX=0 NormalY=0 NormalZ=1 AngleXU=0 Radius=3.5
    g21: LineSegment StartX=-1 StartY=5.25 StartZ=0 EndX=-1 EndY=8.75 EndZ=0
    g22: LineSegment StartX=-1 StartY=8.75 StartZ=0 EndX=-4.03109 EndY=10.5 EndZ=0
    g23: LineSegment StartX=-4.03109 StartY=10.5 StartZ=0 EndX=-7.06218 EndY=8.75 EndZ=0
    g24: LineSegment StartX=-7.06218 StartY=8.75 StartZ=0 EndX=-7.06218 EndY=5.25 EndZ=0
    g25: LineSegment StartX=-7.06218 StartY=5.25 StartZ=0 EndX=-4.03109 EndY=3.5 EndZ=0
    g26: LineSegment StartX=-4.03109 StartY=3.5 StartZ=0 EndX=-1 EndY=5.25 EndZ=0
    g27: Circle [constr] CenterX=-4.03109 CenterY=7 CenterZ=0 NormalX=0 NormalY=0 NormalZ=1 AngleXU=0 Radius=3.5
    g28: LineSegment StartX=-4.96891 StartY=-1.75 StartZ=0 EndX=-4.96891 EndY=1.75 EndZ=0
    g29: LineSegment StartX=-4.96891 StartY=1.75 StartZ=0 EndX=-8 EndY=3.5 EndZ=0
    g30: LineSegment StartX=-8 StartY=3.5 StartZ=0 EndX=-11.0311 EndY=1.75 EndZ=0
    g31: LineSegment StartX=-11.0311 StartY=1.75 StartZ=0 EndX=-11.0311 EndY=-1.75 EndZ=0
    g32: LineSegment StartX=-11.0311 StartY=-1.75 StartZ=0 EndX=-8 EndY=-3.5 EndZ=0
    g33: LineSegment StartX=-8 StartY=-3.5 StartZ=0 EndX=-4.96891 EndY=-1.75 EndZ=0
    g34: Circle [constr] CenterX=-8 CenterY=0 CenterZ=0 NormalX=0 NormalY=0 NormalZ=1 AngleXU=0 Radius=3.5
    g35: LineSegment StartX=-4.03109 StartY=-3.5 StartZ=0 EndX=-7.06218 EndY=-5.25 EndZ=0
    g36: LineSegment StartX=-7.06218 StartY=-5.25 StartZ=0 EndX=-7.06218 EndY=-8.75 EndZ=0
    g37: LineSegment StartX=-7.06218 StartY=-8.75 StartZ=0 EndX=-4.03109 EndY=-10.5 EndZ=0
    g38: LineSegment StartX=-4.03109 StartY=-10.5 StartZ=0 EndX=-1 EndY=-8.75 EndZ=0
    g39: LineSegment StartX=-1 StartY=-8.75 StartZ=0 EndX=-1 EndY=-5.25 EndZ=0
    g40: LineSegment StartX=-1 StartY=-5.25 StartZ=0 EndX=-4.03109 EndY=-3.5 EndZ=0
    g41: Circle [constr] CenterX=-4.03109 CenterY=-7 CenterZ=0 NormalX=0 NormalY=0 NormalZ=1 AngleXU=0 Radius=3.5
    g42: LineSegment StartX=4.03109 StartY=-3.5 StartZ=0 EndX=1 EndY=-5.25 EndZ=0
    g43: LineSegment StartX=1 StartY=-5.25 StartZ=0 EndX=1 EndY=-8.75 EndZ=0
    g44: LineSegment StartX=1 StartY=-8.75 StartZ=0 EndX=4.03109 EndY=-10.5 EndZ=0
    g45: LineSegment StartX=4.03109 StartY=-10.5 StartZ=0 EndX=7.06218 EndY=-8.75 EndZ=0
    g46: LineSegment StartX=7.06218 StartY=-8.75 StartZ=0 EndX=7.06218 EndY=-5.25 EndZ=0
    g47: LineSegment StartX=7.06218 StartY=-5.25 StartZ=0 EndX=4.03109 EndY=-3.5 EndZ=0
    g48: Circle [constr] CenterX=4.03109 CenterY=-7 CenterZ=0 NormalX=0 NormalY=0 NormalZ=1 AngleXU=0 Radius=3.5
  constraints (117):
    c: Coincident(g0,g1)
    c: Coincident(g1,g2)
    c: Coincident(g2,g3)
    c: Coincident(g3,g4)
    c: Coincident(g4,g5)
    c: Coincident(g5,g0)
    c: Equal(g0, g1-g5) x5
    c: PointOnObject(g0,g6)
    c: PointOnObject(g1,g6)
    c: PointOnObject(g2,g6)
    c: PointOnObject(g3,g6)
    c: PointOnObject(g4,g6)
    c: PointOnObject(g5,g6)
    c: Coincident(g6,g-1)
    c: Diameter(g6) = 7
    c: PointOnObject(g0,g-2)
    c: Coincident(g7,g8)
    c: Coincident(g8,g9)
    c: Coincident(g9,g10)
    c: Coincident(g10,g11)
    c: Coincident(g11,g12)
    c: Coincident(g12,g7)
    c: Equal(g7, g8-g12) x5
    c: PointOnObject(g7,g13)
    c: PointOnObject(g8,g13)
    c: PointOnObject(g9,g13)
    c: PointOnObject(g10,g13)
    c: PointOnObject(g11,g13)
    c: PointOnObject(g12,g13)
    c: PointOnObject(g13,g-1)
    c: Diameter(g13) = 7
    c: Distance(g6,g13) = 8
    c: Horizontal(g0,g10)
    c: Coincident(g14,g15)
    c: Coincident(g15,g16)
    c: Coincident(g16,g17)
    c: Coincident(g17,g18)
    c: Coincident(g18,g19)
    c: Coincident(g19,g14)
    c: Equal(g14, g15-g19) x5
    c: PointOnObject(g14,g20)
    c: PointOnObject(g15,g20)
    c: PointOnObject(g16,g20)
    c: PointOnObject(g17,g20)
    c: PointOnObject(g18,g20)
    c: PointOnObject(g19,g20)
    c: Diameter(g20) = 7
    c: DistanceY(g-1,g20) = 7
    c: Vertical(g18)
    c: Distance(g17,g-2) = 1
    c: Coincident(g21,g22)
    c: Coincident(g22,g23)
    c: Coincident(g23,g24)
    c: Coincident(g24,g25)
    c: Coincident(g25,g26)
    c: Coincident(g26,g21)
    c: Equal(g21, g22-g26) x5
    c: PointOnObject(g21,g27)
    c: PointOnObject(g22,g27)
    c: PointOnObject(g23,g27)
    c: PointOnObject(g24,g27)
    c: PointOnObject(g25,g27)
    c: PointOnObject(g26,g27)
    c: Diameter(g27) = 7
    c: DistanceY(g-1,g27) = 7
    c: DistanceX(g21,g-1) = 1
    c: Vertical(g21)
    c: Coincident(g28,g29)
    c: Coincident(g29,g30)
    c: Coincident(g30,g31)
    c: Coincident(g31,g32)
    c: Coincident(g32,g33)
    c: Coincident(g33,g28)
    c: Equal(g28, g29-g33) x5
    c: PointOnObject(g28,g34)
    c: PointOnObject(g29,g34)
    c: PointOnObject(g30,g34)
    c: PointOnObject(g31,g34)
    c: PointOnObject(g32,g34)
    c: PointOnObject(g33,g34)
    c: PointOnObject(g34,g-1)
    c: Diameter(g34) = 7
    c: Vertical(g31)
    c: DistanceX(g34,g-1) = 8
    c: Coincident(g35,g36)
    c: Coincident(g36,g37)
    c: Coincident(g37,g38)
    c: Coincident(g38,g39)
    c: Coincident(g39,g40)
    c: Coincident(g40,g35)
    c: Equal(g35, g36-g40) x5
    c: PointOnObject(g35,g41)
    c: PointOnObject(g36,g41)
    c: PointOnObject(g37,g41)
    c: PointOnObject(g38,g41)
    c: PointOnObject(g39,g41)
    c: PointOnObject(g40,g41)
    c: Coincident(g42,g43)
    c: Coincident(g43,g44)
    c: Coincident(g44,g45)
    c: Coincident(g45,g46)
    c: Coincident(g46,g47)
    c: Coincident(g47,g42)
    c: Equal(g42, g43-g47) x5
    c: PointOnObject(g42,g48)
    c: PointOnObject(g43,g48)
    c: PointOnObject(g44,g48)
    c: PointOnObject(g45,g48)
    c: PointOnObject(g46,g48)
    c: PointOnObject(g47,g48)
    c: Equal(g41,g48)
    c: Diameter(g41) = 7
    c: Vertical(g39)
    c: Vertical(g43)
    c: Distance(g-2,g39) = 1
    c: Symmetric(g38,g43,g-2)
    c: Distance(g41,g-1) = 7
FEATURE [Part::Extrusion] Extrude495  label="hex110"
  Base = -> Sketch503
  Dir = (0,-1,2e-16)
  DirMode = 2
  FaceMakerClass = Part::FaceMakerBullseye
  FaceMakerMode = 3
  LengthFwd = 10
  LengthRev = 0
  Placement = pos=(12,0,35) rot=(0,0,1;0rad)
  Solid = true
  Symmetric = false
FEATURE [Sketcher::SketchObject] Sketch504
  ArcFitTolerance = 1e-06
  FullyConstrained = true
  MakeInternals = false
  Placement = pos=(0,0,0) rot=(1,0,0;1.5708rad)
  sketch-geometry (49):
    g0: LineSegment StartX=1e-16 StartY=3.5 StartZ=0 EndX=-3.03109 EndY=1.75 EndZ=0
    g1: LineSegment StartX=-3.03109 StartY=1.75 StartZ=0 EndX=-3.03109 EndY=-1.75 EndZ=0
    g2: LineSegment StartX=-3.03109 StartY=-1.75 StartZ=0 EndX=-1e-16 EndY=-3.5 EndZ=0
    g3: LineSegment StartX=-1e-16 StartY=-3.5 StartZ=0 EndX=3.03109 EndY=-1.75 EndZ=0
    g4: LineSegment StartX=3.03109 StartY=-1.75 StartZ=0 EndX=3.03109 EndY=1.75 EndZ=0
    g5: LineSegment StartX=3.03109 StartY=1.75 StartZ=0 EndX=1e-16 EndY=3.5 EndZ=0
    g6: Circle [constr] CenterX=0 CenterY=0 CenterZ=0 NormalX=0 NormalY=0 NormalZ=1 AngleXU=0 Radius=3.5
    g7: LineSegment StartX=4.96892 StartY=-1.75002 StartZ=0 EndX=8.00002 EndY=-3.5 EndZ=0
    g8: LineSegment StartX=8.00002 StartY=-3.5 StartZ=0 EndX=11.0311 EndY=-1.74998 EndZ=0
    g9: LineSegment StartX=11.0311 StartY=-1.74998 StartZ=0 EndX=11.0311 EndY=1.75002 EndZ=0
    g10: LineSegment StartX=11.0311 StartY=1.75002 StartZ=0 EndX=7.99998 EndY=3.5 EndZ=0
    g11: LineSegment StartX=7.99998 StartY=3.5 StartZ=0 EndX=4.9689 EndY=1.74998 EndZ=0
    g12: LineSegment StartX=4.9689 StartY=1.74998 StartZ=0 EndX=4.96892 EndY=-1.75002 EndZ=0
    g13: Circle [constr] CenterX=8 CenterY=0 CenterZ=0 NormalX=0 NormalY=0 NormalZ=1 AngleXU=0 Radius=3.5
    g14: LineSegment StartX=4.03109 StartY=3.5 StartZ=0 EndX=7.06218 EndY=5.25 EndZ=0
    g15: LineSegment StartX=7.06218 StartY=5.25 StartZ=0 EndX=7.06218 EndY=8.75 EndZ=0
    g16: LineSegment StartX=7.06218 StartY=8.75 StartZ=0 EndX=4.03109 EndY=10.5 EndZ=0
    g17: LineSegment StartX=4.03109 StartY=10.5 StartZ=0 EndX=1 EndY=8.75 EndZ=0
    g18: LineSegment StartX=1 StartY=8.75 StartZ=0 EndX=1 EndY=5.25 EndZ=0
    g19: LineSegment StartX=1 StartY=5.25 StartZ=0 EndX=4.03109 EndY=3.5 EndZ=0
    g20: Circle [constr] CenterX=4.03109 CenterY=7 CenterZ=0 NormalX=0 NormalY=0 NormalZ=1 AngleXU=0 Radius=3.5
    g21: LineSegment StartX=-1 StartY=5.25 StartZ=0 EndX=-1 EndY=8.75 EndZ=0
    g22: LineSegment StartX=-1 StartY=8.75 StartZ=0 EndX=-4.03109 EndY=10.5 EndZ=0
    g23: LineSegment StartX=-4.03109 StartY=10.5 StartZ=0 EndX=-7.06218 EndY=8.75 EndZ=0
    g24: LineSegment StartX=-7.06218 StartY=8.75 StartZ=0 EndX=-7.06218 EndY=5.25 EndZ=0
    g25: LineSegment StartX=-7.06218 StartY=5.25 StartZ=0 EndX=-4.03109 EndY=3.5 EndZ=0
    g26: LineSegment StartX=-4.03109 StartY=3.5 StartZ=0 EndX=-1 EndY=5.25 EndZ=0
    g27: Circle [constr] CenterX=-4.03109 CenterY=7 CenterZ=0 NormalX=0 NormalY=0 NormalZ=1 AngleXU=0 Radius=3.5
    g28: LineSegment StartX=-4.96891 StartY=-1.75 StartZ=0 EndX=-4.96891 EndY=1.75 EndZ=0
    g29: LineSegment StartX=-4.96891 StartY=1.75 StartZ=0 EndX=-8 EndY=3.5 EndZ=0
    g30: LineSegment StartX=-8 StartY=3.5 StartZ=0 EndX=-11.0311 EndY=1.75 EndZ=0
    g31: LineSegment StartX=-11.0311 StartY=1.75 StartZ=0 EndX=-11.0311 EndY=-1.75 EndZ=0
    g32: LineSegment StartX=-11.0311 StartY=-1.75 StartZ=0 EndX=-8 EndY=-3.5 EndZ=0
    g33: LineSegment StartX=-8 StartY=-3.5 StartZ=0 EndX=-4.96891 EndY=-1.75 EndZ=0
    g34: Circle [constr] CenterX=-8 CenterY=0 CenterZ=0 NormalX=0 NormalY=0 NormalZ=1 AngleXU=0 Radius=3.5
    g35: LineSegment StartX=-4.03109 StartY=-3.5 StartZ=0 EndX=-7.06218 EndY=-5.25 EndZ=0
    g36: LineSegment StartX=-7.06218 StartY=-5.25 StartZ=0 EndX=-7.06218 EndY=-8.75 EndZ=0
    g37: LineSegment StartX=-7.06218 StartY=-8.75 StartZ=0 EndX=-4.03109 EndY=-10.5 EndZ=0
    g38: LineSegment StartX=-4.03109 StartY=-10.5 StartZ=0 EndX=-1 EndY=-8.75 EndZ=0
    g39: LineSegment StartX=-1 StartY=-8.75 StartZ=0 EndX=-1 EndY=-5.25 EndZ=0
    g40: LineSegment StartX=-1 StartY=-5.25 StartZ=0 EndX=-4.03109 EndY=-3.5 EndZ=0
    g41: Circle [constr] CenterX=-4.03109 CenterY=-7 CenterZ=0 NormalX=0 NormalY=0 NormalZ=1 AngleXU=0 Radius=3.5
    g42: LineSegment StartX=4.03109 StartY=-3.5 StartZ=0 EndX=1 EndY=-5.25 EndZ=0
    g43: LineSegment StartX=1 StartY=-5.25 StartZ=0 EndX=1 EndY=-8.75 EndZ=0
    g44: LineSegment StartX=1 StartY=-8.75 StartZ=0 EndX=4.03109 EndY=-10.5 EndZ=0
    g45: LineSegment StartX=4.03109 StartY=-10.5 StartZ=0 EndX=7.06218 EndY=-8.75 EndZ=0
    g46: LineSegment StartX=7.06218 StartY=-8.75 StartZ=0 EndX=7.06218 EndY=-5.25 EndZ=0
    g47: LineSegment StartX=7.06218 StartY=-5.25 StartZ=0 EndX=4.03109 EndY=-3.5 EndZ=0
    g48: Circle [constr] CenterX=4.03109 CenterY=-7 CenterZ=0 NormalX=0 NormalY=0 NormalZ=1 AngleXU=0 Radius=3.5
  constraints (117):
    c: Coincident(g0,g1)
    c: Coincident(g1,g2)
    c: Coincident(g2,g3)
    c: Coincident(g3,g4)
    c: Coincident(g4,g5)
    c: Coincident(g5,g0)
    c: Equal(g0, g1-g5) x5
    c: PointOnObject(g0,g6)
    c: PointOnObject(g1,g6)
    c: PointOnObject(g2,g6)
    c: PointOnObject(g3,g6)
    c: PointOnObject(g4,g6)
    c: PointOnObject(g5,g6)
    c: Coincident(g6,g-1)
    c: Diameter(g6) = 7
    c: PointOnObject(g0,g-2)
    c: Coincident(g7,g8)
    c: Coincident(g8,g9)
    c: Coincident(g9,g10)
    c: Coincident(g10,g11)
    c: Coincident(g11,g12)
    c: Coincident(g12,g7)
    c: Equal(g7, g8-g12) x5
    c: PointOnObject(g7,g13)
    c: PointOnObject(g8,g13)
    c: PointOnObject(g9,g13)
    c: PointOnObject(g10,g13)
    c: PointOnObject(g11,g13)
    c: PointOnObject(g12,g13)
    c: PointOnObject(g13,g-1)
    c: Diameter(g13) = 7
    c: Distance(g6,g13) = 8
    c: Horizontal(g0,g10)
    c: Coincident(g14,g15)
    c: Coincident(g15,g16)
    c: Coincident(g16,g17)
    c: Coincident(g17,g18)
    c: Coincident(g18,g19)
    c: Coincident(g19,g14)
    c: Equal(g14, g15-g19) x5
    c: PointOnObject(g14,g20)
    c: PointOnObject(g15,g20)
    c: PointOnObject(g16,g20)
    c: PointOnObject(g17,g20)
    c: PointOnObject(g18,g20)
    c: PointOnObject(g19,g20)
    c: Diameter(g20) = 7
    c: DistanceY(g-1,g20) = 7
    c: Vertical(g18)
    c: Distance(g17,g-2) = 1
    c: Coincident(g21,g22)
    c: Coincident(g22,g23)
    c: Coincident(g23,g24)
    c: Coincident(g24,g25)
    c: Coincident(g25,g26)
    c: Coincident(g26,g21)
    c: Equal(g21, g22-g26) x5
    c: PointOnObject(g21,g27)
    c: PointOnObject(g22,g27)
    c: PointOnObject(g23,g27)
    c: PointOnObject(g24,g27)
    c: PointOnObject(g25,g27)
    c: PointOnObject(g26,g27)
    c: Diameter(g27) = 7
    c: DistanceY(g-1,g27) = 7
    c: DistanceX(g21,g-1) = 1
    c: Vertical(g21)
    c: Coincident(g28,g29)
    c: Coincident(g29,g30)
    c: Coincident(g30,g31)
    c: Coincident(g31,g32)
    c: Coincident(g32,g33)
    c: Coincident(g33,g28)
    c: Equal(g28, g29-g33) x5
    c: PointOnObject(g28,g34)
    c: PointOnObject(g29,g34)
    c: PointOnObject(g30,g34)
    c: PointOnObject(g31,g34)
    c: PointOnObject(g32,g34)
    c: PointOnObject(g33,g34)
    c: PointOnObject(g34,g-1)
    c: Diameter(g34) = 7
    c: Vertical(g31)
    c: DistanceX(g34,g-1) = 8
    c: Coincident(g35,g36)
    c: Coincident(g36,g37)
    c: Coincident(g37,g38)
    c: Coincident(g38,g39)
    c: Coincident(g39,g40)
    c: Coincident(g40,g35)
    c: Equal(g35, g36-g40) x5
    c: PointOnObject(g35,g41)
    c: PointOnObject(g36,g41)
    c: PointOnObject(g37,g41)
    c: PointOnObject(g38,g41)
    c: PointOnObject(g39,g41)
    c: PointOnObject(g40,g41)
    c: Coincident(g42,g43)
    c: Coincident(g43,g44)
    c: Coincident(g44,g45)
    c: Coincident(g45,g46)
    c: Coincident(g46,g47)
    c: Coincident(g47,g42)
    c: Equal(g42, g43-g47) x5
    c: PointOnObject(g42,g48)
    c: PointOnObject(g43,g48)
    c: PointOnObject(g44,g48)
    c: PointOnObject(g45,g48)
    c: PointOnObject(g46,g48)
    c: PointOnObject(g47,g48)
    c: Equal(g41,g48)
    c: Diameter(g41) = 7
    c: Vertical(g39)
    c: Vertical(g43)
    c: Distance(g-2,g39) = 1
    c: Symmetric(g38,g43,g-2)
    c: Distance(g41,g-1) = 7
FEATURE [Part::Extrusion] Extrude496  label="hex111"
  Base = -> Sketch504
  Dir = (0,-1,2e-16)
  DirMode = 2
  FaceMakerClass = Part::FaceMakerBullseye
  FaceMakerMode = 3
  LengthFwd = 10
  LengthRev = 0
  Placement = pos=(-36,0,7) rot=(0,0,1;0rad)
  Solid = true
  Symmetric = false
FEATURE [Sketcher::SketchObject] Sketch505
  ArcFitTolerance = 1e-06
  FullyConstrained = true
  MakeInternals = false
  Placement = pos=(0,0,0) rot=(1,0,0;1.5708rad)
  sketch-geometry (49):
    g0: LineSegment StartX=1e-16 StartY=3.5 StartZ=0 EndX=-3.03109 EndY=1.75 EndZ=0
    g1: LineSegment StartX=-3.03109 StartY=1.75 StartZ=0 EndX=-3.03109 EndY=-1.75 EndZ=0
    g2: LineSegment StartX=-3.03109 StartY=-1.75 StartZ=0 EndX=-1e-16 EndY=-3.5 EndZ=0
    g3: LineSegment StartX=-1e-16 StartY=-3.5 StartZ=0 EndX=3.03109 EndY=-1.75 EndZ=0
    g4: LineSegment StartX=3.03109 StartY=-1.75 StartZ=0 EndX=3.03109 EndY=1.75 EndZ=0
    g5: LineSegment StartX=3.03109 StartY=1.75 StartZ=0 EndX=1e-16 EndY=3.5 EndZ=0
    g6: Circle [constr] CenterX=0 CenterY=0 CenterZ=0 NormalX=0 NormalY=0 NormalZ=1 AngleXU=0 Radius=3.5
    g7: LineSegment StartX=4.96892 StartY=-1.75002 StartZ=0 EndX=8.00002 EndY=-3.5 EndZ=0
    g8: LineSegment StartX=8.00002 StartY=-3.5 StartZ=0 EndX=11.0311 EndY=-1.74998 EndZ=0
    g9: LineSegment StartX=11.0311 StartY=-1.74998 StartZ=0 EndX=11.0311 EndY=1.75002 EndZ=0
    g10: LineSegment StartX=11.0311 StartY=1.75002 StartZ=0 EndX=7.99998 EndY=3.5 EndZ=0
    g11: LineSegment StartX=7.99998 StartY=3.5 StartZ=0 EndX=4.9689 EndY=1.74998 EndZ=0
    g12: LineSegment StartX=4.9689 StartY=1.74998 StartZ=0 EndX=4.96892 EndY=-1.75002 EndZ=0
    g13: Circle [constr] CenterX=8 CenterY=0 CenterZ=0 NormalX=0 NormalY=0 NormalZ=1 AngleXU=0 Radius=3.5
    g14: LineSegment StartX=4.03109 StartY=3.5 StartZ=0 EndX=7.06218 EndY=5.25 EndZ=0
    g15: LineSegment StartX=7.06218 StartY=5.25 StartZ=0 EndX=7.06218 EndY=8.75 EndZ=0
    g16: LineSegment StartX=7.06218 StartY=8.75 StartZ=0 EndX=4.03109 EndY=10.5 EndZ=0
    g17: LineSegment StartX=4.03109 StartY=10.5 StartZ=0 EndX=1 EndY=8.75 EndZ=0
    g18: LineSegment StartX=1 StartY=8.75 StartZ=0 EndX=1 EndY=5.25 EndZ=0
    g19: LineSegment StartX=1 StartY=5.25 StartZ=0 EndX=4.03109 EndY=3.5 EndZ=0
    g20: Circle [constr] CenterX=4.03109 CenterY=7 CenterZ=0 NormalX=0 NormalY=0 NormalZ=1 AngleXU=0 Radius=3.5
    g21: LineSegment StartX=-1 StartY=5.25 StartZ=0 EndX=-1 EndY=8.75 EndZ=0
    g22: LineSegment StartX=-1 StartY=8.75 StartZ=0 EndX=-4.03109 EndY=10.5 EndZ=0
    g23: LineSegment StartX=-4.03109 StartY=10.5 StartZ=0 EndX=-7.06218 EndY=8.75 EndZ=0
    g24: LineSegment StartX=-7.06218 StartY=8.75 StartZ=0 EndX=-7.06218 EndY=5.25 EndZ=0
    g25: LineSegment StartX=-7.06218 StartY=5.25 StartZ=0 EndX=-4.03109 EndY=3.5 EndZ=0
    g26: LineSegment StartX=-4.03109 StartY=3.5 StartZ=0 EndX=-1 EndY=5.25 EndZ=0
    g27: Circle [constr] CenterX=-4.03109 CenterY=7 CenterZ=0 NormalX=0 NormalY=0 NormalZ=1 AngleXU=0 Radius=3.5
    g28: LineSegment StartX=-4.96891 StartY=-1.75 StartZ=0 EndX=-4.96891 EndY=1.75 EndZ=0
    g29: LineSegment StartX=-4.96891 StartY=1.75 StartZ=0 EndX=-8 EndY=3.5 EndZ=0
    g30: LineSegment StartX=-8 StartY=3.5 StartZ=0 EndX=-11.0311 EndY=1.75 EndZ=0
    g31: LineSegment StartX=-11.0311 StartY=1.75 StartZ=0 EndX=-11.0311 EndY=-1.75 EndZ=0
    g32: LineSegment StartX=-11.0311 StartY=-1.75 StartZ=0 EndX=-8 EndY=-3.5 EndZ=0
    g33: LineSegment StartX=-8 StartY=-3.5 StartZ=0 EndX=-4.96891 EndY=-1.75 EndZ=0
    g34: Circle [constr] CenterX=-8 CenterY=0 CenterZ=0 NormalX=0 NormalY=0 NormalZ=1 AngleXU=0 Radius=3.5
    g35: LineSegment StartX=-4.03109 StartY=-3.5 StartZ=0 EndX=-7.06218 EndY=-5.25 EndZ=0
    g36: LineSegment StartX=-7.06218 StartY=-5.25 StartZ=0 EndX=-7.06218 EndY=-8.75 EndZ=0
    g37: LineSegment StartX=-7.06218 StartY=-8.75 StartZ=0 EndX=-4.03109 EndY=-10.5 EndZ=0
    g38: LineSegment StartX=-4.03109 StartY=-10.5 StartZ=0 EndX=-1 EndY=-8.75 EndZ=0
    g39: LineSegment StartX=-1 StartY=-8.75 StartZ=0 EndX=-1 EndY=-5.25 EndZ=0
    g40: LineSegment StartX=-1 StartY=-5.25 StartZ=0 EndX=-4.03109 EndY=-3.5 EndZ=0
    g41: Circle [constr] CenterX=-4.03109 CenterY=-7 CenterZ=0 NormalX=0 NormalY=0 NormalZ=1 AngleXU=0 Radius=3.5
    g42: LineSegment StartX=4.03109 StartY=-3.5 StartZ=0 EndX=1 EndY=-5.25 EndZ=0
    g43: LineSegment StartX=1 StartY=-5.25 StartZ=0 EndX=1 EndY=-8.75 EndZ=0
    g44: LineSegment StartX=1 StartY=-8.75 StartZ=0 EndX=4.03109 EndY=-10.5 EndZ=0
    g45: LineSegment StartX=4.03109 StartY=-10.5 StartZ=0 EndX=7.06218 EndY=-8.75 EndZ=0
    g46: LineSegment StartX=7.06218 StartY=-8.75 StartZ=0 EndX=7.06218 EndY=-5.25 EndZ=0
    g47: LineSegment StartX=7.06218 StartY=-5.25 StartZ=0 EndX=4.03109 EndY=-3.5 EndZ=0
    g48: Circle [constr] CenterX=4.03109 CenterY=-7 CenterZ=0 NormalX=0 NormalY=0 NormalZ=1 AngleXU=0 Radius=3.5
  constraints (117):
    c: Coincident(g0,g1)
    c: Coincident(g1,g2)
    c: Coincident(g2,g3)
    c: Coincident(g3,g4)
    c: Coincident(g4,g5)
    c: Coincident(g5,g0)
    c: Equal(g0, g1-g5) x5
    c: PointOnObject(g0,g6)
    c: PointOnObject(g1,g6)
    c: PointOnObject(g2,g6)
    c: PointOnObject(g3,g6)
    c: PointOnObject(g4,g6)
    c: PointOnObject(g5,g6)
    c: Coincident(g6,g-1)
    c: Diameter(g6) = 7
    c: PointOnObject(g0,g-2)
    c: Coincident(g7,g8)
    c: Coincident(g8,g9)
    c: Coincident(g9,g10)
    c: Coincident(g10,g11)
    c: Coincident(g11,g12)
    c: Coincident(g12,g7)
    c: Equal(g7, g8-g12) x5
    c: PointOnObject(g7,g13)
    c: PointOnObject(g8,g13)
    c: PointOnObject(g9,g13)
    c: PointOnObject(g10,g13)
    c: PointOnObject(g11,g13)
    c: PointOnObject(g12,g13)
    c: PointOnObject(g13,g-1)
    c: Diameter(g13) = 7
    c: Distance(g6,g13) = 8
    c: Horizontal(g0,g10)
    c: Coincident(g14,g15)
    c: Coincident(g15,g16)
    c: Coincident(g16,g17)
    c: Coincident(g17,g18)
    c: Coincident(g18,g19)
    c: Coincident(g19,g14)
    c: Equal(g14, g15-g19) x5
    c: PointOnObject(g14,g20)
    c: PointOnObject(g15,g20)
    c: PointOnObject(g16,g20)
    c: PointOnObject(g17,g20)
    c: PointOnObject(g18,g20)
    c: PointOnObject(g19,g20)
    c: Diameter(g20) = 7
    c: DistanceY(g-1,g20) = 7
    c: Vertical(g18)
    c: Distance(g17,g-2) = 1
    c: Coincident(g21,g22)
    c: Coincident(g22,g23)
    c: Coincident(g23,g24)
    c: Coincident(g24,g25)
    c: Coincident(g25,g26)
    c: Coincident(g26,g21)
    c: Equal(g21, g22-g26) x5
    c: PointOnObject(g21,g27)
    c: PointOnObject(g22,g27)
    c: PointOnObject(g23,g27)
    c: PointOnObject(g24,g27)
    c: PointOnObject(g25,g27)
    c: PointOnObject(g26,g27)
    c: Diameter(g27) = 7
    c: DistanceY(g-1,g27) = 7
    c: DistanceX(g21,g-1) = 1
    c: Vertical(g21)
    c: Coincident(g28,g29)
    c: Coincident(g29,g30)
    c: Coincident(g30,g31)
    c: Coincident(g31,g32)
    c: Coincident(g32,g33)
    c: Coincident(g33,g28)
    c: Equal(g28, g29-g33) x5
    c: PointOnObject(g28,g34)
    c: PointOnObject(g29,g34)
    c: PointOnObject(g30,g34)
    c: PointOnObject(g31,g34)
    c: PointOnObject(g32,g34)
    c: PointOnObject(g33,g34)
    c: PointOnObject(g34,g-1)
    c: Diameter(g34) = 7
    c: Vertical(g31)
    c: DistanceX(g34,g-1) = 8
    c: Coincident(g35,g36)
    c: Coincident(g36,g37)
    c: Coincident(g37,g38)
    c: Coincident(g38,g39)
    c: Coincident(g39,g40)
    c: Coincident(g40,g35)
    c: Equal(g35, g36-g40) x5
    c: PointOnObject(g35,g41)
    c: PointOnObject(g36,g41)
    c: PointOnObject(g37,g41)
    c: PointOnObject(g38,g41)
    c: PointOnObject(g39,g41)
    c: PointOnObject(g40,g41)
    c: Coincident(g42,g43)
    c: Coincident(g43,g44)
    c: Coincident(g44,g45)
    c: Coincident(g45,g46)
    c: Coincident(g46,g47)
    c: Coincident(g47,g42)
    c: Equal(g42, g43-g47) x5
    c: PointOnObject(g42,g48)
    c: PointOnObject(g43,g48)
    c: PointOnObject(g44,g48)
    c: PointOnObject(g45,g48)
    c: PointOnObject(g46,g48)
    c: PointOnObject(g47,g48)
    c: Equal(g41,g48)
    c: Diameter(g41) = 7
    c: Vertical(g39)
    c: Vertical(g43)
    c: Distance(g-2,g39) = 1
    c: Symmetric(g38,g43,g-2)
    c: Distance(g41,g-1) = 7
FEATURE [Part::Extrusion] Extrude497  label="hex112"
  Base = -> Sketch505
  Dir = (0,-1,2e-16)
  DirMode = 2
  FaceMakerClass = Part::FaceMakerBullseye
  FaceMakerMode = 3
  LengthFwd = 10
  LengthRev = 0
  Placement = pos=(36,0,7) rot=(0,0,1;0rad)
  Solid = true
  Symmetric = false
FEATURE [Sketcher::SketchObject] Sketch506
  ArcFitTolerance = 1e-06
  FullyConstrained = true
  MakeInternals = false
  Placement = pos=(0,0,0) rot=(1,0,0;1.5708rad)
  sketch-geometry (49):
    g0: LineSegment StartX=1e-16 StartY=3.5 StartZ=0 EndX=-3.03109 EndY=1.75 EndZ=0
    g1: LineSegment StartX=-3.03109 StartY=1.75 StartZ=0 EndX=-3.03109 EndY=-1.75 EndZ=0
    g2: LineSegment StartX=-3.03109 StartY=-1.75 StartZ=0 EndX=-1e-16 EndY=-3.5 EndZ=0
    g3: LineSegment StartX=-1e-16 StartY=-3.5 StartZ=0 EndX=3.03109 EndY=-1.75 EndZ=0
    g4: LineSegment StartX=3.03109 StartY=-1.75 StartZ=0 EndX=3.03109 EndY=1.75 EndZ=0
    g5: LineSegment StartX=3.03109 StartY=1.75 StartZ=0 EndX=1e-16 EndY=3.5 EndZ=0
    g6: Circle [constr] CenterX=0 CenterY=0 CenterZ=0 NormalX=0 NormalY=0 NormalZ=1 AngleXU=0 Radius=3.5
    g7: LineSegment StartX=4.96892 StartY=-1.75002 StartZ=0 EndX=8.00002 EndY=-3.5 EndZ=0
    g8: LineSegment StartX=8.00002 StartY=-3.5 StartZ=0 EndX=11.0311 EndY=-1.74998 EndZ=0
    g9: LineSegment StartX=11.0311 StartY=-1.74998 StartZ=0 EndX=11.0311 EndY=1.75002 EndZ=0
    g10: LineSegment StartX=11.0311 StartY=1.75002 StartZ=0 EndX=7.99998 EndY=3.5 EndZ=0
    g11: LineSegment StartX=7.99998 StartY=3.5 StartZ=0 EndX=4.9689 EndY=1.74998 EndZ=0
    g12: LineSegment StartX=4.9689 StartY=1.74998 StartZ=0 EndX=4.96892 EndY=-1.75002 EndZ=0
    g13: Circle [constr] CenterX=8 CenterY=0 CenterZ=0 NormalX=0 NormalY=0 NormalZ=1 AngleXU=0 Radius=3.5
    g14: LineSegment StartX=4.03109 StartY=3.5 StartZ=0 EndX=7.06218 EndY=5.25 EndZ=0
    g15: LineSegment StartX=7.06218 StartY=5.25 StartZ=0 EndX=7.06218 EndY=8.75 EndZ=0
    g16: LineSegment StartX=7.06218 StartY=8.75 StartZ=0 EndX=4.03109 EndY=10.5 EndZ=0
    g17: LineSegment StartX=4.03109 StartY=10.5 StartZ=0 EndX=1 EndY=8.75 EndZ=0
    g18: LineSegment StartX=1 StartY=8.75 StartZ=0 EndX=1 EndY=5.25 EndZ=0
    g19: LineSegment StartX=1 StartY=5.25 StartZ=0 EndX=4.03109 EndY=3.5 EndZ=0
    g20: Circle [constr] CenterX=4.03109 CenterY=7 CenterZ=0 NormalX=0 NormalY=0 NormalZ=1 AngleXU=0 Radius=3.5
    g21: LineSegment StartX=-1 StartY=5.25 StartZ=0 EndX=-1 EndY=8.75 EndZ=0
    g22: LineSegment StartX=-1 StartY=8.75 StartZ=0 EndX=-4.03109 EndY=10.5 EndZ=0
    g23: LineSegment StartX=-4.03109 StartY=10.5 StartZ=0 EndX=-7.06218 EndY=8.75 EndZ=0
    g24: LineSegment StartX=-7.06218 StartY=8.75 StartZ=0 EndX=-7.06218 EndY=5.25 EndZ=0
    g25: LineSegment StartX=-7.06218 StartY=5.25 StartZ=0 EndX=-4.03109 EndY=3.5 EndZ=0
    g26: LineSegment StartX=-4.03109 StartY=3.5 StartZ=0 EndX=-1 EndY=5.25 EndZ=0
    g27: Circle [constr] CenterX=-4.03109 CenterY=7 CenterZ=0 NormalX=0 NormalY=0 NormalZ=1 AngleXU=0 Radius=3.5
    g28: LineSegment StartX=-4.96891 StartY=-1.75 StartZ=0 EndX=-4.96891 EndY=1.75 EndZ=0
    g29: LineSegment StartX=-4.96891 StartY=1.75 StartZ=0 EndX=-8 EndY=3.5 EndZ=0
    g30: LineSegment StartX=-8 StartY=3.5 StartZ=0 EndX=-11.0311 EndY=1.75 EndZ=0
    g31: LineSegment StartX=-11.0311 StartY=1.75 StartZ=0 EndX=-11.0311 EndY=-1.75 EndZ=0
    g32: LineSegment StartX=-11.0311 StartY=-1.75 StartZ=0 EndX=-8 EndY=-3.5 EndZ=0
    g33: LineSegment StartX=-8 StartY=-3.5 StartZ=0 EndX=-4.96891 EndY=-1.75 EndZ=0
    g34: Circle [constr] CenterX=-8 CenterY=0 CenterZ=0 NormalX=0 NormalY=0 NormalZ=1 AngleXU=0 Radius=3.5
    g35: LineSegment StartX=-4.03109 StartY=-3.5 StartZ=0 EndX=-7.06218 EndY=-5.25 EndZ=0
    g36: LineSegment StartX=-7.06218 StartY=-5.25 StartZ=0 EndX=-7.06218 EndY=-8.75 EndZ=0
    g37: LineSegment StartX=-7.06218 StartY=-8.75 StartZ=0 EndX=-4.03109 EndY=-10.5 EndZ=0
    g38: LineSegment StartX=-4.03109 StartY=-10.5 StartZ=0 EndX=-1 EndY=-8.75 EndZ=0
    g39: LineSegment StartX=-1 StartY=-8.75 StartZ=0 EndX=-1 EndY=-5.25 EndZ=0
    g40: LineSegment StartX=-1 StartY=-5.25 StartZ=0 EndX=-4.03109 EndY=-3.5 EndZ=0
    g41: Circle [constr] CenterX=-4.03109 CenterY=-7 CenterZ=0 NormalX=0 NormalY=0 NormalZ=1 AngleXU=0 Radius=3.5
    g42: LineSegment StartX=4.03109 StartY=-3.5 StartZ=0 EndX=1 EndY=-5.25 EndZ=0
    g43: LineSegment StartX=1 StartY=-5.25 StartZ=0 EndX=1 EndY=-8.75 EndZ=0
    g44: LineSegment StartX=1 StartY=-8.75 StartZ=0 EndX=4.03109 EndY=-10.5 EndZ=0
    g45: LineSegment StartX=4.03109 StartY=-10.5 StartZ=0 EndX=7.06218 EndY=-8.75 EndZ=0
    g46: LineSegment StartX=7.06218 StartY=-8.75 StartZ=0 EndX=7.06218 EndY=-5.25 EndZ=0
    g47: LineSegment StartX=7.06218 StartY=-5.25 StartZ=0 EndX=4.03109 EndY=-3.5 EndZ=0
    g48: Circle [constr] CenterX=4.03109 CenterY=-7 CenterZ=0 NormalX=0 NormalY=0 NormalZ=1 AngleXU=0 Radius=3.5
  constraints (117):
    c: Coincident(g0,g1)
    c: Coincident(g1,g2)
    c: Coincident(g2,g3)
    c: Coincident(g3,g4)
    c: Coincident(g4,g5)
    c: Coincident(g5,g0)
    c: Equal(g0, g1-g5) x5
    c: PointOnObject(g0,g6)
    c: PointOnObject(g1,g6)
    c: PointOnObject(g2,g6)
    c: PointOnObject(g3,g6)
    c: PointOnObject(g4,g6)
    c: PointOnObject(g5,g6)
    c: Coincident(g6,g-1)
    c: Diameter(g6) = 7
    c: PointOnObject(g0,g-2)
    c: Coincident(g7,g8)
    c: Coincident(g8,g9)
    c: Coincident(g9,g10)
    c: Coincident(g10,g11)
    c: Coincident(g11,g12)
    c: Coincident(g12,g7)
    c: Equal(g7, g8-g12) x5
    c: PointOnObject(g7,g13)
    c: PointOnObject(g8,g13)
    c: PointOnObject(g9,g13)
    c: PointOnObject(g10,g13)
    c: PointOnObject(g11,g13)
    c: PointOnObject(g12,g13)
    c: PointOnObject(g13,g-1)
    c: Diameter(g13) = 7
    c: Distance(g6,g13) = 8
    c: Horizontal(g0,g10)
    c: Coincident(g14,g15)
    c: Coincident(g15,g16)
    c: Coincident(g16,g17)
    c: Coincident(g17,g18)
    c: Coincident(g18,g19)
    c: Coincident(g19,g14)
    c: Equal(g14, g15-g19) x5
    c: PointOnObject(g14,g20)
    c: PointOnObject(g15,g20)
    c: PointOnObject(g16,g20)
    c: PointOnObject(g17,g20)
    c: PointOnObject(g18,g20)
    c: PointOnObject(g19,g20)
    c: Diameter(g20) = 7
    c: DistanceY(g-1,g20) = 7
    c: Vertical(g18)
    c: Distance(g17,g-2) = 1
    c: Coincident(g21,g22)
    c: Coincident(g22,g23)
    c: Coincident(g23,g24)
    c: Coincident(g24,g25)
    c: Coincident(g25,g26)
    c: Coincident(g26,g21)
    c: Equal(g21, g22-g26) x5
    c: PointOnObject(g21,g27)
    c: PointOnObject(g22,g27)
    c: PointOnObject(g23,g27)
    c: PointOnObject(g24,g27)
    c: PointOnObject(g25,g27)
    c: PointOnObject(g26,g27)
    c: Diameter(g27) = 7
    c: DistanceY(g-1,g27) = 7
    c: DistanceX(g21,g-1) = 1
    c: Vertical(g21)
    c: Coincident(g28,g29)
    c: Coincident(g29,g30)
    c: Coincident(g30,g31)
    c: Coincident(g31,g32)
    c: Coincident(g32,g33)
    c: Coincident(g33,g28)
    c: Equal(g28, g29-g33) x5
    c: PointOnObject(g28,g34)
    c: PointOnObject(g29,g34)
    c: PointOnObject(g30,g34)
    c: PointOnObject(g31,g34)
    c: PointOnObject(g32,g34)
    c: PointOnObject(g33,g34)
    c: PointOnObject(g34,g-1)
    c: Diameter(g34) = 7
    c: Vertical(g31)
    c: DistanceX(g34,g-1) = 8
    c: Coincident(g35,g36)
    c: Coincident(g36,g37)
    c: Coincident(g37,g38)
    c: Coincident(g38,g39)
    c: Coincident(g39,g40)
    c: Coincident(g40,g35)
    c: Equal(g35, g36-g40) x5
    c: PointOnObject(g35,g41)
    c: PointOnObject(g36,g41)
    c: PointOnObject(g37,g41)
    c: PointOnObject(g38,g41)
    c: PointOnObject(g39,g41)
    c: PointOnObject(g40,g41)
    c: Coincident(g42,g43)
    c: Coincident(g43,g44)
    c: Coincident(g44,g45)
    c: Coincident(g45,g46)
    c: Coincident(g46,g47)
    c: Coincident(g47,g42)
    c: Equal(g42, g43-g47) x5
    c: PointOnObject(g42,g48)
    c: PointOnObject(g43,g48)
    c: PointOnObject(g44,g48)
    c: PointOnObject(g45,g48)
    c: PointOnObject(g46,g48)
    c: PointOnObject(g47,g48)
    c: Equal(g41,g48)
    c: Diameter(g41) = 7
    c: Vertical(g39)
    c: Vertical(g43)
    c: Distance(g-2,g39) = 1
    c: Symmetric(g38,g43,g-2)
    c: Distance(g41,g-1) = 7
FEATURE [Part::Extrusion] Extrude498  label="hex113"
  Base = -> Sketch506
  Dir = (0,-1,2e-16)
  DirMode = 2
  FaceMakerClass = Part::FaceMakerBullseye
  FaceMakerMode = 3
  LengthFwd = 10
  LengthRev = 0
  Placement = pos=(32,0,28) rot=(0,0,1;0rad)
  Solid = true
  Symmetric = false
FEATURE [Sketcher::SketchObject] Sketch507
  ArcFitTolerance = 1e-06
  FullyConstrained = true
  MakeInternals = false
  Placement = pos=(0,0,0) rot=(1,0,0;1.5708rad)
  sketch-geometry (49):
    g0: LineSegment StartX=1e-16 StartY=3.5 StartZ=0 EndX=-3.03109 EndY=1.75 EndZ=0
    g1: LineSegment StartX=-3.03109 StartY=1.75 StartZ=0 EndX=-3.03109 EndY=-1.75 EndZ=0
    g2: LineSegment StartX=-3.03109 StartY=-1.75 StartZ=0 EndX=-1e-16 EndY=-3.5 EndZ=0
    g3: LineSegment StartX=-1e-16 StartY=-3.5 StartZ=0 EndX=3.03109 EndY=-1.75 EndZ=0
    g4: LineSegment StartX=3.03109 StartY=-1.75 StartZ=0 EndX=3.03109 EndY=1.75 EndZ=0
    g5: LineSegment StartX=3.03109 StartY=1.75 StartZ=0 EndX=1e-16 EndY=3.5 EndZ=0
    g6: Circle [constr] CenterX=0 CenterY=0 CenterZ=0 NormalX=0 NormalY=0 NormalZ=1 AngleXU=0 Radius=3.5
    g7: LineSegment StartX=4.96892 StartY=-1.75002 StartZ=0 EndX=8.00002 EndY=-3.5 EndZ=0
    g8: LineSegment StartX=8.00002 StartY=-3.5 StartZ=0 EndX=11.0311 EndY=-1.74998 EndZ=0
    g9: LineSegment StartX=11.0311 StartY=-1.74998 StartZ=0 EndX=11.0311 EndY=1.75002 EndZ=0
    g10: LineSegment StartX=11.0311 StartY=1.75002 StartZ=0 EndX=7.99998 EndY=3.5 EndZ=0
    g11: LineSegment StartX=7.99998 StartY=3.5 StartZ=0 EndX=4.9689 EndY=1.74998 EndZ=0
    g12: LineSegment StartX=4.9689 StartY=1.74998 StartZ=0 EndX=4.96892 EndY=-1.75002 EndZ=0
    g13: Circle [constr] CenterX=8 CenterY=0 CenterZ=0 NormalX=0 NormalY=0 NormalZ=1 AngleXU=0 Radius=3.5
    g14: LineSegment StartX=4.03109 StartY=3.5 StartZ=0 EndX=7.06218 EndY=5.25 EndZ=0
    g15: LineSegment StartX=7.06218 StartY=5.25 StartZ=0 EndX=7.06218 EndY=8.75 EndZ=0
    g16: LineSegment StartX=7.06218 StartY=8.75 StartZ=0 EndX=4.03109 EndY=10.5 EndZ=0
    g17: LineSegment StartX=4.03109 StartY=10.5 StartZ=0 EndX=1 EndY=8.75 EndZ=0
    g18: LineSegment StartX=1 StartY=8.75 StartZ=0 EndX=1 EndY=5.25 EndZ=0
    g19: LineSegment StartX=1 StartY=5.25 StartZ=0 EndX=4.03109 EndY=3.5 EndZ=0
    g20: Circle [constr] CenterX=4.03109 CenterY=7 CenterZ=0 NormalX=0 NormalY=0 NormalZ=1 AngleXU=0 Radius=3.5
    g21: LineSegment StartX=-1 StartY=5.25 StartZ=0 EndX=-1 EndY=8.75 EndZ=0
    g22: LineSegment StartX=-1 StartY=8.75 StartZ=0 EndX=-4.03109 EndY=10.5 EndZ=0
    g23: LineSegment StartX=-4.03109 StartY=10.5 StartZ=0 EndX=-7.06218 EndY=8.75 EndZ=0
    g24: LineSegment StartX=-7.06218 StartY=8.75 StartZ=0 EndX=-7.06218 EndY=5.25 EndZ=0
    g25: LineSegment StartX=-7.06218 StartY=5.25 StartZ=0 EndX=-4.03109 EndY=3.5 EndZ=0
    g26: LineSegment StartX=-4.03109 StartY=3.5 StartZ=0 EndX=-1 EndY=5.25 EndZ=0
    g27: Circle [constr] CenterX=-4.03109 CenterY=7 CenterZ=0 NormalX=0 NormalY=0 NormalZ=1 AngleXU=0 Radius=3.5
    g28: LineSegment StartX=-4.96891 StartY=-1.75 StartZ=0 EndX=-4.96891 EndY=1.75 EndZ=0
    g29: LineSegment StartX=-4.96891 StartY=1.75 StartZ=0 EndX=-8 EndY=3.5 EndZ=0
    g30: LineSegment StartX=-8 StartY=3.5 StartZ=0 EndX=-11.0311 EndY=1.75 EndZ=0
    g31: LineSegment StartX=-11.0311 StartY=1.75 StartZ=0 EndX=-11.0311 EndY=-1.75 EndZ=0
    g32: LineSegment StartX=-11.0311 StartY=-1.75 StartZ=0 EndX=-8 EndY=-3.5 EndZ=0
    g33: LineSegment StartX=-8 StartY=-3.5 StartZ=0 EndX=-4.96891 EndY=-1.75 EndZ=0
    g34: Circle [constr] CenterX=-8 CenterY=0 CenterZ=0 NormalX=0 NormalY=0 NormalZ=1 AngleXU=0 Radius=3.5
    g35: LineSegment StartX=-4.03109 StartY=-3.5 StartZ=0 EndX=-7.06218 EndY=-5.25 EndZ=0
    g36: LineSegment StartX=-7.06218 StartY=-5.25 StartZ=0 EndX=-7.06218 EndY=-8.75 EndZ=0
    g37: LineSegment StartX=-7.06218 StartY=-8.75 StartZ=0 EndX=-4.03109 EndY=-10.5 EndZ=0
    g38: LineSegment StartX=-4.03109 StartY=-10.5 StartZ=0 EndX=-1 EndY=-8.75 EndZ=0
    g39: LineSegment StartX=-1 StartY=-8.75 StartZ=0 EndX=-1 EndY=-5.25 EndZ=0
    g40: LineSegment StartX=-1 StartY=-5.25 StartZ=0 EndX=-4.03109 EndY=-3.5 EndZ=0
    g41: Circle [constr] CenterX=-4.03109 CenterY=-7 CenterZ=0 NormalX=0 NormalY=0 NormalZ=1 AngleXU=0 Radius=3.5
    g42: LineSegment StartX=4.03109 StartY=-3.5 StartZ=0 EndX=1 EndY=-5.25 EndZ=0
    g43: LineSegment StartX=1 StartY=-5.25 StartZ=0 EndX=1 EndY=-8.75 EndZ=0
    g44: LineSegment StartX=1 StartY=-8.75 StartZ=0 EndX=4.03109 EndY=-10.5 EndZ=0
    g45: LineSegment StartX=4.03109 StartY=-10.5 StartZ=0 EndX=7.06218 EndY=-8.75 EndZ=0
    g46: LineSegment StartX=7.06218 StartY=-8.75 StartZ=0 EndX=7.06218 EndY=-5.25 EndZ=0
    g47: LineSegment StartX=7.06218 StartY=-5.25 StartZ=0 EndX=4.03109 EndY=-3.5 EndZ=0
    g48: Circle [constr] CenterX=4.03109 CenterY=-7 CenterZ=0 NormalX=0 NormalY=0 NormalZ=1 AngleXU=0 Radius=3.5
  constraints (117):
    c: Coincident(g0,g1)
    c: Coincident(g1,g2)
    c: Coincident(g2,g3)
    c: Coincident(g3,g4)
    c: Coincident(g4,g5)
    c: Coincident(g5,g0)
    c: Equal(g0, g1-g5) x5
    c: PointOnObject(g0,g6)
    c: PointOnObject(g1,g6)
    c: PointOnObject(g2,g6)
    c: PointOnObject(g3,g6)
    c: PointOnObject(g4,g6)
    c: PointOnObject(g5,g6)
    c: Coincident(g6,g-1)
    c: Diameter(g6) = 7
    c: PointOnObject(g0,g-2)
    c: Coincident(g7,g8)
    c: Coincident(g8,g9)
    c: Coincident(g9,g10)
    c: Coincident(g10,g11)
    c: Coincident(g11,g12)
    c: Coincident(g12,g7)
    c: Equal(g7, g8-g12) x5
    c: PointOnObject(g7,g13)
    c: PointOnObject(g8,g13)
    c: PointOnObject(g9,g13)
    c: PointOnObject(g10,g13)
    c: PointOnObject(g11,g13)
    c: PointOnObject(g12,g13)
    c: PointOnObject(g13,g-1)
    c: Diameter(g13) = 7
    c: Distance(g6,g13) = 8
    c: Horizontal(g0,g10)
    c: Coincident(g14,g15)
    c: Coincident(g15,g16)
    c: Coincident(g16,g17)
    c: Coincident(g17,g18)
    c: Coincident(g18,g19)
    c: Coincident(g19,g14)
    c: Equal(g14, g15-g19) x5
    c: PointOnObject(g14,g20)
    c: PointOnObject(g15,g20)
    c: PointOnObject(g16,g20)
    c: PointOnObject(g17,g20)
    c: PointOnObject(g18,g20)
    c: PointOnObject(g19,g20)
    c: Diameter(g20) = 7
    c: DistanceY(g-1,g20) = 7
    c: Vertical(g18)
    c: Distance(g17,g-2) = 1
    c: Coincident(g21,g22)
    c: Coincident(g22,g23)
    c: Coincident(g23,g24)
    c: Coincident(g24,g25)
    c: Coincident(g25,g26)
    c: Coincident(g26,g21)
    c: Equal(g21, g22-g26) x5
    c: PointOnObject(g21,g27)
    c: PointOnObject(g22,g27)
    c: PointOnObject(g23,g27)
    c: PointOnObject(g24,g27)
    c: PointOnObject(g25,g27)
    c: PointOnObject(g26,g27)
    c: Diameter(g27) = 7
    c: DistanceY(g-1,g27) = 7
    c: DistanceX(g21,g-1) = 1
    c: Vertical(g21)
    c: Coincident(g28,g29)
    c: Coincident(g29,g30)
    c: Coincident(g30,g31)
    c: Coincident(g31,g32)
    c: Coincident(g32,g33)
    c: Coincident(g33,g28)
    c: Equal(g28, g29-g33) x5
    c: PointOnObject(g28,g34)
    c: PointOnObject(g29,g34)
    c: PointOnObject(g30,g34)
    c: PointOnObject(g31,g34)
    c: PointOnObject(g32,g34)
    c: PointOnObject(g33,g34)
    c: PointOnObject(g34,g-1)
    c: Diameter(g34) = 7
    c: Vertical(g31)
    c: DistanceX(g34,g-1) = 8
    c: Coincident(g35,g36)
    c: Coincident(g36,g37)
    c: Coincident(g37,g38)
    c: Coincident(g38,g39)
    c: Coincident(g39,g40)
    c: Coincident(g40,g35)
    c: Equal(g35, g36-g40) x5
    c: PointOnObject(g35,g41)
    c: PointOnObject(g36,g41)
    c: PointOnObject(g37,g41)
    c: PointOnObject(g38,g41)
    c: PointOnObject(g39,g41)
    c: PointOnObject(g40,g41)
    c: Coincident(g42,g43)
    c: Coincident(g43,g44)
    c: Coincident(g44,g45)
    c: Coincident(g45,g46)
    c: Coincident(g46,g47)
    c: Coincident(g47,g42)
    c: Equal(g42, g43-g47) x5
    c: PointOnObject(g42,g48)
    c: PointOnObject(g43,g48)
    c: PointOnObject(g44,g48)
    c: PointOnObject(g45,g48)
    c: PointOnObject(g46,g48)
    c: PointOnObject(g47,g48)
    c: Equal(g41,g48)
    c: Diameter(g41) = 7
    c: Vertical(g39)
    c: Vertical(g43)
    c: Distance(g-2,g39) = 1
    c: Symmetric(g38,g43,g-2)
    c: Distance(g41,g-1) = 7
FEATURE [Part::Extrusion] Extrude499  label="hex114"
  Base = -> Sketch507
  Dir = (0,-1,2e-16)
  DirMode = 2
  FaceMakerClass = Part::FaceMakerBullseye
  FaceMakerMode = 3
  LengthFwd = 10
  LengthRev = 0
  Placement = pos=(-40,0,-14) rot=(0,0,1;0rad)
  Solid = true
  Symmetric = false
FEATURE [Sketcher::SketchObject] Sketch508
  ArcFitTolerance = 1e-06
  FullyConstrained = true
  MakeInternals = false
  Placement = pos=(0,0,0) rot=(1,0,0;1.5708rad)
  sketch-geometry (49):
    g0: LineSegment StartX=1e-16 StartY=3.5 StartZ=0 EndX=-3.03109 EndY=1.75 EndZ=0
    g1: LineSegment StartX=-3.03109 StartY=1.75 StartZ=0 EndX=-3.03109 EndY=-1.75 EndZ=0
    g2: LineSegment StartX=-3.03109 StartY=-1.75 StartZ=0 EndX=-1e-16 EndY=-3.5 EndZ=0
    g3: LineSegment StartX=-1e-16 StartY=-3.5 StartZ=0 EndX=3.03109 EndY=-1.75 EndZ=0
    g4: LineSegment StartX=3.03109 StartY=-1.75 StartZ=0 EndX=3.03109 EndY=1.75 EndZ=0
    g5: LineSegment StartX=3.03109 StartY=1.75 StartZ=0 EndX=1e-16 EndY=3.5 EndZ=0
    g6: Circle [constr] CenterX=0 CenterY=0 CenterZ=0 NormalX=0 NormalY=0 NormalZ=1 AngleXU=0 Radius=3.5
    g7: LineSegment StartX=4.96892 StartY=-1.75002 StartZ=0 EndX=8.00002 EndY=-3.5 EndZ=0
    g8: LineSegment StartX=8.00002 StartY=-3.5 StartZ=0 EndX=11.0311 EndY=-1.74998 EndZ=0
    g9: LineSegment StartX=11.0311 StartY=-1.74998 StartZ=0 EndX=11.0311 EndY=1.75002 EndZ=0
    g10: LineSegment StartX=11.0311 StartY=1.75002 StartZ=0 EndX=7.99998 EndY=3.5 EndZ=0
    g11: LineSegment StartX=7.99998 StartY=3.5 StartZ=0 EndX=4.9689 EndY=1.74998 EndZ=0
    g12: LineSegment StartX=4.9689 StartY=1.74998 StartZ=0 EndX=4.96892 EndY=-1.75002 EndZ=0
    g13: Circle [constr] CenterX=8 CenterY=0 CenterZ=0 NormalX=0 NormalY=0 NormalZ=1 AngleXU=0 Radius=3.5
    g14: LineSegment StartX=4.03109 StartY=3.5 StartZ=0 EndX=7.06218 EndY=5.25 EndZ=0
    g15: LineSegment StartX=7.06218 StartY=5.25 StartZ=0 EndX=7.06218 EndY=8.75 EndZ=0
    g16: LineSegment StartX=7.06218 StartY=8.75 StartZ=0 EndX=4.03109 EndY=10.5 EndZ=0
    g17: LineSegment StartX=4.03109 StartY=10.5 StartZ=0 EndX=1 EndY=8.75 EndZ=0
    g18: LineSegment StartX=1 StartY=8.75 StartZ=0 EndX=1 EndY=5.25 EndZ=0
    g19: LineSegment StartX=1 StartY=5.25 StartZ=0 EndX=4.03109 EndY=3.5 EndZ=0
    g20: Circle [constr] CenterX=4.03109 CenterY=7 CenterZ=0 NormalX=0 NormalY=0 NormalZ=1 AngleXU=0 Radius=3.5
    g21: LineSegment StartX=-1 StartY=5.25 StartZ=0 EndX=-1 EndY=8.75 EndZ=0
    g22: LineSegment StartX=-1 StartY=8.75 StartZ=0 EndX=-4.03109 EndY=10.5 EndZ=0
    g23: LineSegment StartX=-4.03109 StartY=10.5 StartZ=0 EndX=-7.06218 EndY=8.75 EndZ=0
    g24: LineSegment StartX=-7.06218 StartY=8.75 StartZ=0 EndX=-7.06218 EndY=5.25 EndZ=0
    g25: LineSegment StartX=-7.06218 StartY=5.25 StartZ=0 EndX=-4.03109 EndY=3.5 EndZ=0
    g26: LineSegment StartX=-4.03109 StartY=3.5 StartZ=0 EndX=-1 EndY=5.25 EndZ=0
    g27: Circle [constr] CenterX=-4.03109 CenterY=7 CenterZ=0 NormalX=0 NormalY=0 NormalZ=1 AngleXU=0 Radius=3.5
    g28: LineSegment StartX=-4.96891 StartY=-1.75 StartZ=0 EndX=-4.96891 EndY=1.75 EndZ=0
    g29: LineSegment StartX=-4.96891 StartY=1.75 StartZ=0 EndX=-8 EndY=3.5 EndZ=0
    g30: LineSegment StartX=-8 StartY=3.5 StartZ=0 EndX=-11.0311 EndY=1.75 EndZ=0
    g31: LineSegment StartX=-11.0311 StartY=1.75 StartZ=0 EndX=-11.0311 EndY=-1.75 EndZ=0
    g32: LineSegment StartX=-11.0311 StartY=-1.75 StartZ=0 EndX=-8 EndY=-3.5 EndZ=0
    g33: LineSegment StartX=-8 StartY=-3.5 StartZ=0 EndX=-4.96891 EndY=-1.75 EndZ=0
    g34: Circle [constr] CenterX=-8 CenterY=0 CenterZ=0 NormalX=0 NormalY=0 NormalZ=1 AngleXU=0 Radius=3.5
    g35: LineSegment StartX=-4.03109 StartY=-3.5 StartZ=0 EndX=-7.06218 EndY=-5.25 EndZ=0
    g36: LineSegment StartX=-7.06218 StartY=-5.25 StartZ=0 EndX=-7.06218 EndY=-8.75 EndZ=0
    g37: LineSegment StartX=-7.06218 StartY=-8.75 StartZ=0 EndX=-4.03109 EndY=-10.5 EndZ=0
    g38: LineSegment StartX=-4.03109 StartY=-10.5 StartZ=0 EndX=-1 EndY=-8.75 EndZ=0
    g39: LineSegment StartX=-1 StartY=-8.75 StartZ=0 EndX=-1 EndY=-5.25 EndZ=0
    g40: LineSegment StartX=-1 StartY=-5.25 StartZ=0 EndX=-4.03109 EndY=-3.5 EndZ=0
    g41: Circle [constr] CenterX=-4.03109 CenterY=-7 CenterZ=0 NormalX=0 NormalY=0 NormalZ=1 AngleXU=0 Radius=3.5
    g42: LineSegment StartX=4.03109 StartY=-3.5 StartZ=0 EndX=1 EndY=-5.25 EndZ=0
    g43: LineSegment StartX=1 StartY=-5.25 StartZ=0 EndX=1 EndY=-8.75 EndZ=0
    g44: LineSegment StartX=1 StartY=-8.75 StartZ=0 EndX=4.03109 EndY=-10.5 EndZ=0
    g45: LineSegment StartX=4.03109 StartY=-10.5 StartZ=0 EndX=7.06218 EndY=-8.75 EndZ=0
    g46: LineSegment StartX=7.06218 StartY=-8.75 StartZ=0 EndX=7.06218 EndY=-5.25 EndZ=0
    g47: LineSegment StartX=7.06218 StartY=-5.25 StartZ=0 EndX=4.03109 EndY=-3.5 EndZ=0
    g48: Circle [constr] CenterX=4.03109 CenterY=-7 CenterZ=0 NormalX=0 NormalY=0 NormalZ=1 AngleXU=0 Radius=3.5
  constraints (117):
    c: Coincident(g0,g1)
    c: Coincident(g1,g2)
    c: Coincident(g2,g3)
    c: Coincident(g3,g4)
    c: Coincident(g4,g5)
    c: Coincident(g5,g0)
    c: Equal(g0, g1-g5) x5
    c: PointOnObject(g0,g6)
    c: PointOnObject(g1,g6)
    c: PointOnObject(g2,g6)
    c: PointOnObject(g3,g6)
    c: PointOnObject(g4,g6)
    c: PointOnObject(g5,g6)
    c: Coincident(g6,g-1)
    c: Diameter(g6) = 7
    c: PointOnObject(g0,g-2)
    c: Coincident(g7,g8)
    c: Coincident(g8,g9)
    c: Coincident(g9,g10)
    c: Coincident(g10,g11)
    c: Coincident(g11,g12)
    c: Coincident(g12,g7)
    c: Equal(g7, g8-g12) x5
    c: PointOnObject(g7,g13)
    c: PointOnObject(g8,g13)
    c: PointOnObject(g9,g13)
    c: PointOnObject(g10,g13)
    c: PointOnObject(g11,g13)
    c: PointOnObject(g12,g13)
    c: PointOnObject(g13,g-1)
    c: Diameter(g13) = 7
    c: Distance(g6,g13) = 8
    c: Horizontal(g0,g10)
    c: Coincident(g14,g15)
    c: Coincident(g15,g16)
    c: Coincident(g16,g17)
    c: Coincident(g17,g18)
    c: Coincident(g18,g19)
    c: Coincident(g19,g14)
    c: Equal(g14, g15-g19) x5
    c: PointOnObject(g14,g20)
    c: PointOnObject(g15,g20)
    c: PointOnObject(g16,g20)
    c: PointOnObject(g17,g20)
    c: PointOnObject(g18,g20)
    c: PointOnObject(g19,g20)
    c: Diameter(g20) = 7
    c: DistanceY(g-1,g20) = 7
    c: Vertical(g18)
    c: Distance(g17,g-2) = 1
    c: Coincident(g21,g22)
    c: Coincident(g22,g23)
    c: Coincident(g23,g24)
    c: Coincident(g24,g25)
    c: Coincident(g25,g26)
    c: Coincident(g26,g21)
    c: Equal(g21, g22-g26) x5
    c: PointOnObject(g21,g27)
    c: PointOnObject(g22,g27)
    c: PointOnObject(g23,g27)
    c: PointOnObject(g24,g27)
    c: PointOnObject(g25,g27)
    c: PointOnObject(g26,g27)
    c: Diameter(g27) = 7
    c: DistanceY(g-1,g27) = 7
    c: DistanceX(g21,g-1) = 1
    c: Vertical(g21)
    c: Coincident(g28,g29)
    c: Coincident(g29,g30)
    c: Coincident(g30,g31)
    c: Coincident(g31,g32)
    c: Coincident(g32,g33)
    c: Coincident(g33,g28)
    c: Equal(g28, g29-g33) x5
    c: PointOnObject(g28,g34)
    c: PointOnObject(g29,g34)
    c: PointOnObject(g30,g34)
    c: PointOnObject(g31,g34)
    c: PointOnObject(g32,g34)
    c: PointOnObject(g33,g34)
    c: PointOnObject(g34,g-1)
    c: Diameter(g34) = 7
    c: Vertical(g31)
    c: DistanceX(g34,g-1) = 8
    c: Coincident(g35,g36)
    c: Coincident(g36,g37)
    c: Coincident(g37,g38)
    c: Coincident(g38,g39)
    c: Coincident(g39,g40)
    c: Coincident(g40,g35)
    c: Equal(g35, g36-g40) x5
    c: PointOnObject(g35,g41)
    c: PointOnObject(g36,g41)
    c: PointOnObject(g37,g41)
    c: PointOnObject(g38,g41)
    c: PointOnObject(g39,g41)
    c: PointOnObject(g40,g41)
    c: Coincident(g42,g43)
    c: Coincident(g43,g44)
    c: Coincident(g44,g45)
    c: Coincident(g45,g46)
    c: Coincident(g46,g47)
    c: Coincident(g47,g42)
    c: Equal(g42, g43-g47) x5
    c: PointOnObject(g42,g48)
    c: PointOnObject(g43,g48)
    c: PointOnObject(g44,g48)
    c: PointOnObject(g45,g48)
    c: PointOnObject(g46,g48)
    c: PointOnObject(g47,g48)
    c: Equal(g41,g48)
    c: Diameter(g41) = 7
    c: Vertical(g39)
    c: Vertical(g43)
    c: Distance(g-2,g39) = 1
    c: Symmetric(g38,g43,g-2)
    c: Distance(g41,g-1) = 7
FEATURE [Part::Extrusion] Extrude500  label="hex115"
  Base = -> Sketch508
  Dir = (0,-1,2e-16)
  DirMode = 2
  FaceMakerClass = Part::FaceMakerBullseye
  FaceMakerMode = 3
  LengthFwd = 10
  LengthRev = 0
  Placement = pos=(-24,0,-28) rot=(0,0,1;0rad)
  Solid = true
  Symmetric = false
FEATURE [Sketcher::SketchObject] Sketch509
  ArcFitTolerance = 1e-06
  FullyConstrained = true
  MakeInternals = false
  Placement = pos=(0,0,0) rot=(1,0,0;1.5708rad)
  sketch-geometry (49):
    g0: LineSegment StartX=1e-16 StartY=3.5 StartZ=0 EndX=-3.03109 EndY=1.75 EndZ=0
    g1: LineSegment StartX=-3.03109 StartY=1.75 StartZ=0 EndX=-3.03109 EndY=-1.75 EndZ=0
    g2: LineSegment StartX=-3.03109 StartY=-1.75 StartZ=0 EndX=-1e-16 EndY=-3.5 EndZ=0
    g3: LineSegment StartX=-1e-16 StartY=-3.5 StartZ=0 EndX=3.03109 EndY=-1.75 EndZ=0
    g4: LineSegment StartX=3.03109 StartY=-1.75 StartZ=0 EndX=3.03109 EndY=1.75 EndZ=0
    g5: LineSegment StartX=3.03109 StartY=1.75 StartZ=0 EndX=1e-16 EndY=3.5 EndZ=0
    g6: Circle [constr] CenterX=0 CenterY=0 CenterZ=0 NormalX=0 NormalY=0 NormalZ=1 AngleXU=0 Radius=3.5
    g7: LineSegment StartX=4.96892 StartY=-1.75002 StartZ=0 EndX=8.00002 EndY=-3.5 EndZ=0
    g8: LineSegment StartX=8.00002 StartY=-3.5 StartZ=0 EndX=11.0311 EndY=-1.74998 EndZ=0
    g9: LineSegment StartX=11.0311 StartY=-1.74998 StartZ=0 EndX=11.0311 EndY=1.75002 EndZ=0
    g10: LineSegment StartX=11.0311 StartY=1.75002 StartZ=0 EndX=7.99998 EndY=3.5 EndZ=0
    g11: LineSegment StartX=7.99998 StartY=3.5 StartZ=0 EndX=4.9689 EndY=1.74998 EndZ=0
    g12: LineSegment StartX=4.9689 StartY=1.74998 StartZ=0 EndX=4.96892 EndY=-1.75002 EndZ=0
    g13: Circle [constr] CenterX=8 CenterY=0 CenterZ=0 NormalX=0 NormalY=0 NormalZ=1 AngleXU=0 Radius=3.5
    g14: LineSegment StartX=4.03109 StartY=3.5 StartZ=0 EndX=7.06218 EndY=5.25 EndZ=0
    g15: LineSegment StartX=7.06218 StartY=5.25 StartZ=0 EndX=7.06218 EndY=8.75 EndZ=0
    g16: LineSegment StartX=7.06218 StartY=8.75 StartZ=0 EndX=4.03109 EndY=10.5 EndZ=0
    g17: LineSegment StartX=4.03109 StartY=10.5 StartZ=0 EndX=1 EndY=8.75 EndZ=0
    g18: LineSegment StartX=1 StartY=8.75 StartZ=0 EndX=1 EndY=5.25 EndZ=0
    g19: LineSegment StartX=1 StartY=5.25 StartZ=0 EndX=4.03109 EndY=3.5 EndZ=0
    g20: Circle [constr] CenterX=4.03109 CenterY=7 CenterZ=0 NormalX=0 NormalY=0 NormalZ=1 AngleXU=0 Radius=3.5
    g21: LineSegment StartX=-1 StartY=5.25 StartZ=0 EndX=-1 EndY=8.75 EndZ=0
    g22: LineSegment StartX=-1 StartY=8.75 StartZ=0 EndX=-4.03109 EndY=10.5 EndZ=0
    g23: LineSegment StartX=-4.03109 StartY=10.5 StartZ=0 EndX=-7.06218 EndY=8.75 EndZ=0
    g24: LineSegment StartX=-7.06218 StartY=8.75 StartZ=0 EndX=-7.06218 EndY=5.25 EndZ=0
    g25: LineSegment StartX=-7.06218 StartY=5.25 StartZ=0 EndX=-4.03109 EndY=3.5 EndZ=0
    g26: LineSegment StartX=-4.03109 StartY=3.5 StartZ=0 EndX=-1 EndY=5.25 EndZ=0
    g27: Circle [constr] CenterX=-4.03109 CenterY=7 CenterZ=0 NormalX=0 NormalY=0 NormalZ=1 AngleXU=0 Radius=3.5
    g28: LineSegment StartX=-4.96891 StartY=-1.75 StartZ=0 EndX=-4.96891 EndY=1.75 EndZ=0
    g29: LineSegment StartX=-4.96891 StartY=1.75 StartZ=0 EndX=-8 EndY=3.5 EndZ=0
    g30: LineSegment StartX=-8 StartY=3.5 StartZ=0 EndX=-11.0311 EndY=1.75 EndZ=0
    g31: LineSegment StartX=-11.0311 StartY=1.75 StartZ=0 EndX=-11.0311 EndY=-1.75 EndZ=0
    g32: LineSegment StartX=-11.0311 StartY=-1.75 StartZ=0 EndX=-8 EndY=-3.5 EndZ=0
    g33: LineSegment StartX=-8 StartY=-3.5 StartZ=0 EndX=-4.96891 EndY=-1.75 EndZ=0
    g34: Circle [constr] CenterX=-8 CenterY=0 CenterZ=0 NormalX=0 NormalY=0 NormalZ=1 AngleXU=0 Radius=3.5
    g35: LineSegment StartX=-4.03109 StartY=-3.5 StartZ=0 EndX=-7.06218 EndY=-5.25 EndZ=0
    g36: LineSegment StartX=-7.06218 StartY=-5.25 StartZ=0 EndX=-7.06218 EndY=-8.75 EndZ=0
    g37: LineSegment StartX=-7.06218 StartY=-8.75 StartZ=0 EndX=-4.03109 EndY=-10.5 EndZ=0
    g38: LineSegment StartX=-4.03109 StartY=-10.5 StartZ=0 EndX=-1 EndY=-8.75 EndZ=0
    g39: LineSegment StartX=-1 StartY=-8.75 StartZ=0 EndX=-1 EndY=-5.25 EndZ=0
    g40: LineSegment StartX=-1 StartY=-5.25 StartZ=0 EndX=-4.03109 EndY=-3.5 EndZ=0
    g41: Circle [constr] CenterX=-4.03109 CenterY=-7 CenterZ=0 NormalX=0 NormalY=0 NormalZ=1 AngleXU=0 Radius=3.5
    g42: LineSegment StartX=4.03109 StartY=-3.5 StartZ=0 EndX=1 EndY=-5.25 EndZ=0
    g43: LineSegment StartX=1 StartY=-5.25 StartZ=0 EndX=1 EndY=-8.75 EndZ=0
    g44: LineSegment StartX=1 StartY=-8.75 StartZ=0 EndX=4.03109 EndY=-10.5 EndZ=0
    g45: LineSegment StartX=4.03109 StartY=-10.5 StartZ=0 EndX=7.06218 EndY=-8.75 EndZ=0
    g46: LineSegment StartX=7.06218 StartY=-8.75 StartZ=0 EndX=7.06218 EndY=-5.25 EndZ=0
    g47: LineSegment StartX=7.06218 StartY=-5.25 StartZ=0 EndX=4.03109 EndY=-3.5 EndZ=0
    g48: Circle [constr] CenterX=4.03109 CenterY=-7 CenterZ=0 NormalX=0 NormalY=0 NormalZ=1 AngleXU=0 Radius=3.5
  constraints (117):
    c: Coincident(g0,g1)
    c: Coincident(g1,g2)
    c: Coincident(g2,g3)
    c: Coincident(g3,g4)
    c: Coincident(g4,g5)
    c: Coincident(g5,g0)
    c: Equal(g0, g1-g5) x5
    c: PointOnObject(g0,g6)
    c: PointOnObject(g1,g6)
    c: PointOnObject(g2,g6)
    c: PointOnObject(g3,g6)
    c: PointOnObject(g4,g6)
    c: PointOnObject(g5,g6)
    c: Coincident(g6,g-1)
    c: Diameter(g6) = 7
    c: PointOnObject(g0,g-2)
    c: Coincident(g7,g8)
    c: Coincident(g8,g9)
    c: Coincident(g9,g10)
    c: Coincident(g10,g11)
    c: Coincident(g11,g12)
    c: Coincident(g12,g7)
    c: Equal(g7, g8-g12) x5
    c: PointOnObject(g7,g13)
    c: PointOnObject(g8,g13)
    c: PointOnObject(g9,g13)
    c: PointOnObject(g10,g13)
    c: PointOnObject(g11,g13)
    c: PointOnObject(g12,g13)
    c: PointOnObject(g13,g-1)
    c: Diameter(g13) = 7
    c: Distance(g6,g13) = 8
    c: Horizontal(g0,g10)
    c: Coincident(g14,g15)
    c: Coincident(g15,g16)
    c: Coincident(g16,g17)
    c: Coincident(g17,g18)
    c: Coincident(g18,g19)
    c: Coincident(g19,g14)
    c: Equal(g14, g15-g19) x5
    c: PointOnObject(g14,g20)
    c: PointOnObject(g15,g20)
    c: PointOnObject(g16,g20)
    c: PointOnObject(g17,g20)
    c: PointOnObject(g18,g20)
    c: PointOnObject(g19,g20)
    c: Diameter(g20) = 7
    c: DistanceY(g-1,g20) = 7
    c: Vertical(g18)
    c: Distance(g17,g-2) = 1
    c: Coincident(g21,g22)
    c: Coincident(g22,g23)
    c: Coincident(g23,g24)
    c: Coincident(g24,g25)
    c: Coincident(g25,g26)
    c: Coincident(g26,g21)
    c: Equal(g21, g22-g26) x5
    c: PointOnObject(g21,g27)
    c: PointOnObject(g22,g27)
    c: PointOnObject(g23,g27)
    c: PointOnObject(g24,g27)
    c: PointOnObject(g25,g27)
    c: PointOnObject(g26,g27)
    c: Diameter(g27) = 7
    c: DistanceY(g-1,g27) = 7
    c: DistanceX(g21,g-1) = 1
    c: Vertical(g21)
    c: Coincident(g28,g29)
    c: Coincident(g29,g30)
    c: Coincident(g30,g31)
    c: Coincident(g31,g32)
    c: Coincident(g32,g33)
    c: Coincident(g33,g28)
    c: Equal(g28, g29-g33) x5
    c: PointOnObject(g28,g34)
    c: PointOnObject(g29,g34)
    c: PointOnObject(g30,g34)
    c: PointOnObject(g31,g34)
    c: PointOnObject(g32,g34)
    c: PointOnObject(g33,g34)
    c: PointOnObject(g34,g-1)
    c: Diameter(g34) = 7
    c: Vertical(g31)
    c: DistanceX(g34,g-1) = 8
    c: Coincident(g35,g36)
    c: Coincident(g36,g37)
    c: Coincident(g37,g38)
    c: Coincident(g38,g39)
    c: Coincident(g39,g40)
    c: Coincident(g40,g35)
    c: Equal(g35, g36-g40) x5
    c: PointOnObject(g35,g41)
    c: PointOnObject(g36,g41)
    c: PointOnObject(g37,g41)
    c: PointOnObject(g38,g41)
    c: PointOnObject(g39,g41)
    c: PointOnObject(g40,g41)
    c: Coincident(g42,g43)
    c: Coincident(g43,g44)
    c: Coincident(g44,g45)
    c: Coincident(g45,g46)
    c: Coincident(g46,g47)
    c: Coincident(g47,g42)
    c: Equal(g42, g43-g47) x5
    c: PointOnObject(g42,g48)
    c: PointOnObject(g43,g48)
    c: PointOnObject(g44,g48)
    c: PointOnObject(g45,g48)
    c: PointOnObject(g46,g48)
    c: PointOnObject(g47,g48)
    c: Equal(g41,g48)
    c: Diameter(g41) = 7
    c: Vertical(g39)
    c: Vertical(g43)
    c: Distance(g-2,g39) = 1
    c: Symmetric(g38,g43,g-2)
    c: Distance(g41,g-1) = 7
FEATURE [Part::Extrusion] Extrude501  label="hex116"
  Base = -> Sketch509
  Dir = (0,-1,2e-16)
  DirMode = 2
  FaceMakerClass = Part::FaceMakerBullseye
  FaceMakerMode = 3
  LengthFwd = 10
  LengthRev = 0
  Placement = pos=(-8,0,-42) rot=(0,0,1;0rad)
  Solid = true
  Symmetric = false
FEATURE [Sketcher::SketchObject] Sketch510
  ArcFitTolerance = 1e-06
  FullyConstrained = true
  MakeInternals = false
  Placement = pos=(0,0,0) rot=(1,0,0;1.5708rad)
  sketch-geometry (49):
    g0: LineSegment StartX=1e-16 StartY=3.5 StartZ=0 EndX=-3.03109 EndY=1.75 EndZ=0
    g1: LineSegment StartX=-3.03109 StartY=1.75 StartZ=0 EndX=-3.03109 EndY=-1.75 EndZ=0
    g2: LineSegment StartX=-3.03109 StartY=-1.75 StartZ=0 EndX=-1e-16 EndY=-3.5 EndZ=0
    g3: LineSegment StartX=-1e-16 StartY=-3.5 StartZ=0 EndX=3.03109 EndY=-1.75 EndZ=0
    g4: LineSegment StartX=3.03109 StartY=-1.75 StartZ=0 EndX=3.03109 EndY=1.75 EndZ=0
    g5: LineSegment StartX=3.03109 StartY=1.75 StartZ=0 EndX=1e-16 EndY=3.5 EndZ=0
    g6: Circle [constr] CenterX=0 CenterY=0 CenterZ=0 NormalX=0 NormalY=0 NormalZ=1 AngleXU=0 Radius=3.5
    g7: LineSegment StartX=4.96892 StartY=-1.75002 StartZ=0 EndX=8.00002 EndY=-3.5 EndZ=0
    g8: LineSegment StartX=8.00002 StartY=-3.5 StartZ=0 EndX=11.0311 EndY=-1.74998 EndZ=0
    g9: LineSegment StartX=11.0311 StartY=-1.74998 StartZ=0 EndX=11.0311 EndY=1.75002 EndZ=0
    g10: LineSegment StartX=11.0311 StartY=1.75002 StartZ=0 EndX=7.99998 EndY=3.5 EndZ=0
    g11: LineSegment StartX=7.99998 StartY=3.5 StartZ=0 EndX=4.9689 EndY=1.74998 EndZ=0
    g12: LineSegment StartX=4.9689 StartY=1.74998 StartZ=0 EndX=4.96892 EndY=-1.75002 EndZ=0
    g13: Circle [constr] CenterX=8 CenterY=0 CenterZ=0 NormalX=0 NormalY=0 NormalZ=1 AngleXU=0 Radius=3.5
    g14: LineSegment StartX=4.03109 StartY=3.5 StartZ=0 EndX=7.06218 EndY=5.25 EndZ=0
    g15: LineSegment StartX=7.06218 StartY=5.25 StartZ=0 EndX=7.06218 EndY=8.75 EndZ=0
    g16: LineSegment StartX=7.06218 StartY=8.75 StartZ=0 EndX=4.03109 EndY=10.5 EndZ=0
    g17: LineSegment StartX=4.03109 StartY=10.5 StartZ=0 EndX=1 EndY=8.75 EndZ=0
    g18: LineSegment StartX=1 StartY=8.75 StartZ=0 EndX=1 EndY=5.25 EndZ=0
    g19: LineSegment StartX=1 StartY=5.25 StartZ=0 EndX=4.03109 EndY=3.5 EndZ=0
    g20: Circle [constr] CenterX=4.03109 CenterY=7 CenterZ=0 NormalX=0 NormalY=0 NormalZ=1 AngleXU=0 Radius=3.5
    g21: LineSegment StartX=-1 StartY=5.25 StartZ=0 EndX=-1 EndY=8.75 EndZ=0
    g22: LineSegment StartX=-1 StartY=8.75 StartZ=0 EndX=-4.03109 EndY=10.5 EndZ=0
    g23: LineSegment StartX=-4.03109 StartY=10.5 StartZ=0 EndX=-7.06218 EndY=8.75 EndZ=0
    g24: LineSegment StartX=-7.06218 StartY=8.75 StartZ=0 EndX=-7.06218 EndY=5.25 EndZ=0
    g25: LineSegment StartX=-7.06218 StartY=5.25 StartZ=0 EndX=-4.03109 EndY=3.5 EndZ=0
    g26: LineSegment StartX=-4.03109 StartY=3.5 StartZ=0 EndX=-1 EndY=5.25 EndZ=0
    g27: Circle [constr] CenterX=-4.03109 CenterY=7 CenterZ=0 NormalX=0 NormalY=0 NormalZ=1 AngleXU=0 Radius=3.5
    g28: LineSegment StartX=-4.96891 StartY=-1.75 StartZ=0 EndX=-4.96891 EndY=1.75 EndZ=0
    g29: LineSegment StartX=-4.96891 StartY=1.75 StartZ=0 EndX=-8 EndY=3.5 EndZ=0
    g30: LineSegment StartX=-8 StartY=3.5 StartZ=0 EndX=-11.0311 EndY=1.75 EndZ=0
    g31: LineSegment StartX=-11.0311 StartY=1.75 StartZ=0 EndX=-11.0311 EndY=-1.75 EndZ=0
    g32: LineSegment StartX=-11.0311 StartY=-1.75 StartZ=0 EndX=-8 EndY=-3.5 EndZ=0
    g33: LineSegment StartX=-8 StartY=-3.5 StartZ=0 EndX=-4.96891 EndY=-1.75 EndZ=0
    g34: Circle [constr] CenterX=-8 CenterY=0 CenterZ=0 NormalX=0 NormalY=0 NormalZ=1 AngleXU=0 Radius=3.5
    g35: LineSegment StartX=-4.03109 StartY=-3.5 StartZ=0 EndX=-7.06218 EndY=-5.25 EndZ=0
    g36: LineSegment StartX=-7.06218 StartY=-5.25 StartZ=0 EndX=-7.06218 EndY=-8.75 EndZ=0
    g37: LineSegment StartX=-7.06218 StartY=-8.75 StartZ=0 EndX=-4.03109 EndY=-10.5 EndZ=0
    g38: LineSegment StartX=-4.03109 StartY=-10.5 StartZ=0 EndX=-1 EndY=-8.75 EndZ=0
    g39: LineSegment StartX=-1 StartY=-8.75 StartZ=0 EndX=-1 EndY=-5.25 EndZ=0
    g40: LineSegment StartX=-1 StartY=-5.25 StartZ=0 EndX=-4.03109 EndY=-3.5 EndZ=0
    g41: Circle [constr] CenterX=-4.03109 CenterY=-7 CenterZ=0 NormalX=0 NormalY=0 NormalZ=1 AngleXU=0 Radius=3.5
    g42: LineSegment StartX=4.03109 StartY=-3.5 StartZ=0 EndX=1 EndY=-5.25 EndZ=0
    g43: LineSegment StartX=1 StartY=-5.25 StartZ=0 EndX=1 EndY=-8.75 EndZ=0
    g44: LineSegment StartX=1 StartY=-8.75 StartZ=0 EndX=4.03109 EndY=-10.5 EndZ=0
    g45: LineSegment StartX=4.03109 StartY=-10.5 StartZ=0 EndX=7.06218 EndY=-8.75 EndZ=0
    g46: LineSegment StartX=7.06218 StartY=-8.75 StartZ=0 EndX=7.06218 EndY=-5.25 EndZ=0
    g47: LineSegment StartX=7.06218 StartY=-5.25 StartZ=0 EndX=4.03109 EndY=-3.5 EndZ=0
    g48: Circle [constr] CenterX=4.03109 CenterY=-7 CenterZ=0 NormalX=0 NormalY=0 NormalZ=1 AngleXU=0 Radius=3.5
  constraints (117):
    c: Coincident(g0,g1)
    c: Coincident(g1,g2)
    c: Coincident(g2,g3)
    c: Coincident(g3,g4)
    c: Coincident(g4,g5)
    c: Coincident(g5,g0)
    c: Equal(g0, g1-g5) x5
    c: PointOnObject(g0,g6)
    c: PointOnObject(g1,g6)
    c: PointOnObject(g2,g6)
    c: PointOnObject(g3,g6)
    c: PointOnObject(g4,g6)
    c: PointOnObject(g5,g6)
    c: Coincident(g6,g-1)
    c: Diameter(g6) = 7
    c: PointOnObject(g0,g-2)
    c: Coincident(g7,g8)
    c: Coincident(g8,g9)
    c: Coincident(g9,g10)
    c: Coincident(g10,g11)
    c: Coincident(g11,g12)
    c: Coincident(g12,g7)
    c: Equal(g7, g8-g12) x5
    c: PointOnObject(g7,g13)
    c: PointOnObject(g8,g13)
    c: PointOnObject(g9,g13)
    c: PointOnObject(g10,g13)
    c: PointOnObject(g11,g13)
    c: PointOnObject(g12,g13)
    c: PointOnObject(g13,g-1)
    c: Diameter(g13) = 7
    c: Distance(g6,g13) = 8
    c: Horizontal(g0,g10)
    c: Coincident(g14,g15)
    c: Coincident(g15,g16)
    c: Coincident(g16,g17)
    c: Coincident(g17,g18)
    c: Coincident(g18,g19)
    c: Coincident(g19,g14)
    c: Equal(g14, g15-g19) x5
    c: PointOnObject(g14,g20)
    c: PointOnObject(g15,g20)
    c: PointOnObject(g16,g20)
    c: PointOnObject(g17,g20)
    c: PointOnObject(g18,g20)
    c: PointOnObject(g19,g20)
    c: Diameter(g20) = 7
    c: DistanceY(g-1,g20) = 7
    c: Vertical(g18)
    c: Distance(g17,g-2) = 1
    c: Coincident(g21,g22)
    c: Coincident(g22,g23)
    c: Coincident(g23,g24)
    c: Coincident(g24,g25)
    c: Coincident(g25,g26)
    c: Coincident(g26,g21)
    c: Equal(g21, g22-g26) x5
    c: PointOnObject(g21,g27)
    c: PointOnObject(g22,g27)
    c: PointOnObject(g23,g27)
    c: PointOnObject(g24,g27)
    c: PointOnObject(g25,g27)
    c: PointOnObject(g26,g27)
    c: Diameter(g27) = 7
    c: DistanceY(g-1,g27) = 7
    c: DistanceX(g21,g-1) = 1
    c: Vertical(g21)
    c: Coincident(g28,g29)
    c: Coincident(g29,g30)
    c: Coincident(g30,g31)
    c: Coincident(g31,g32)
    c: Coincident(g32,g33)
    c: Coincident(g33,g28)
    c: Equal(g28, g29-g33) x5
    c: PointOnObject(g28,g34)
    c: PointOnObject(g29,g34)
    c: PointOnObject(g30,g34)
    c: PointOnObject(g31,g34)
    c: PointOnObject(g32,g34)
    c: PointOnObject(g33,g34)
    c: PointOnObject(g34,g-1)
    c: Diameter(g34) = 7
    c: Vertical(g31)
    c: DistanceX(g34,g-1) = 8
    c: Coincident(g35,g36)
    c: Coincident(g36,g37)
    c: Coincident(g37,g38)
    c: Coincident(g38,g39)
    c: Coincident(g39,g40)
    c: Coincident(g40,g35)
    c: Equal(g35, g36-g40) x5
    c: PointOnObject(g35,g41)
    c: PointOnObject(g36,g41)
    c: PointOnObject(g37,g41)
    c: PointOnObject(g38,g41)
    c: PointOnObject(g39,g41)
    c: PointOnObject(g40,g41)
    c: Coincident(g42,g43)
    c: Coincident(g43,g44)
    c: Coincident(g44,g45)
    c: Coincident(g45,g46)
    c: Coincident(g46,g47)
    c: Coincident(g47,g42)
    c: Equal(g42, g43-g47) x5
    c: PointOnObject(g42,g48)
    c: PointOnObject(g43,g48)
    c: PointOnObject(g44,g48)
    c: PointOnObject(g45,g48)
    c: PointOnObject(g46,g48)
    c: PointOnObject(g47,g48)
    c: Equal(g41,g48)
    c: Diameter(g41) = 7
    c: Vertical(g39)
    c: Vertical(g43)
    c: Distance(g-2,g39) = 1
    c: Symmetric(g38,g43,g-2)
    c: Distance(g41,g-1) = 7
FEATURE [Part::Extrusion] Extrude502  label="hex117"
  Base = -> Sketch510
  Dir = (0,-1,2e-16)
  DirMode = 2
  FaceMakerClass = Part::FaceMakerBullseye
  FaceMakerMode = 3
  LengthFwd = 10
  LengthRev = 0
  Placement = pos=(32,0,-28) rot=(0,0,1;0rad)
  Solid = true
  Symmetric = false
FEATURE [Sketcher::SketchObject] Sketch511
  ArcFitTolerance = 1e-06
  FullyConstrained = true
  MakeInternals = false
  Placement = pos=(0,0,0) rot=(1,0,0;1.5708rad)
  sketch-geometry (49):
    g0: LineSegment StartX=1e-16 StartY=3.5 StartZ=0 EndX=-3.03109 EndY=1.75 EndZ=0
    g1: LineSegment StartX=-3.03109 StartY=1.75 StartZ=0 EndX=-3.03109 EndY=-1.75 EndZ=0
    g2: LineSegment StartX=-3.03109 StartY=-1.75 StartZ=0 EndX=-1e-16 EndY=-3.5 EndZ=0
    g3: LineSegment StartX=-1e-16 StartY=-3.5 StartZ=0 EndX=3.03109 EndY=-1.75 EndZ=0
    g4: LineSegment StartX=3.03109 StartY=-1.75 StartZ=0 EndX=3.03109 EndY=1.75 EndZ=0
    g5: LineSegment StartX=3.03109 StartY=1.75 StartZ=0 EndX=1e-16 EndY=3.5 EndZ=0
    g6: Circle [constr] CenterX=0 CenterY=0 CenterZ=0 NormalX=0 NormalY=0 NormalZ=1 AngleXU=0 Radius=3.5
    g7: LineSegment StartX=4.96892 StartY=-1.75002 StartZ=0 EndX=8.00002 EndY=-3.5 EndZ=0
    g8: LineSegment StartX=8.00002 StartY=-3.5 StartZ=0 EndX=11.0311 EndY=-1.74998 EndZ=0
    g9: LineSegment StartX=11.0311 StartY=-1.74998 StartZ=0 EndX=11.0311 EndY=1.75002 EndZ=0
    g10: LineSegment StartX=11.0311 StartY=1.75002 StartZ=0 EndX=7.99998 EndY=3.5 EndZ=0
    g11: LineSegment StartX=7.99998 StartY=3.5 StartZ=0 EndX=4.9689 EndY=1.74998 EndZ=0
    g12: LineSegment StartX=4.9689 StartY=1.74998 StartZ=0 EndX=4.96892 EndY=-1.75002 EndZ=0
    g13: Circle [constr] CenterX=8 CenterY=0 CenterZ=0 NormalX=0 NormalY=0 NormalZ=1 AngleXU=0 Radius=3.5
    g14: LineSegment StartX=4.03109 StartY=3.5 StartZ=0 EndX=7.06218 EndY=5.25 EndZ=0
    g15: LineSegment StartX=7.06218 StartY=5.25 StartZ=0 EndX=7.06218 EndY=8.75 EndZ=0
    g16: LineSegment StartX=7.06218 StartY=8.75 StartZ=0 EndX=4.03109 EndY=10.5 EndZ=0
    g17: LineSegment StartX=4.03109 StartY=10.5 StartZ=0 EndX=1 EndY=8.75 EndZ=0
    g18: LineSegment StartX=1 StartY=8.75 StartZ=0 EndX=1 EndY=5.25 EndZ=0
    g19: LineSegment StartX=1 StartY=5.25 StartZ=0 EndX=4.03109 EndY=3.5 EndZ=0
    g20: Circle [constr] CenterX=4.03109 CenterY=7 CenterZ=0 NormalX=0 NormalY=0 NormalZ=1 AngleXU=0 Radius=3.5
    g21: LineSegment StartX=-1 StartY=5.25 StartZ=0 EndX=-1 EndY=8.75 EndZ=0
    g22: LineSegment StartX=-1 StartY=8.75 StartZ=0 EndX=-4.03109 EndY=10.5 EndZ=0
    g23: LineSegment StartX=-4.03109 StartY=10.5 StartZ=0 EndX=-7.06218 EndY=8.75 EndZ=0
    g24: LineSegment StartX=-7.06218 StartY=8.75 StartZ=0 EndX=-7.06218 EndY=5.25 EndZ=0
    g25: LineSegment StartX=-7.06218 StartY=5.25 StartZ=0 EndX=-4.03109 EndY=3.5 EndZ=0
    g26: LineSegment StartX=-4.03109 StartY=3.5 StartZ=0 EndX=-1 EndY=5.25 EndZ=0
    g27: Circle [constr] CenterX=-4.03109 CenterY=7 CenterZ=0 NormalX=0 NormalY=0 NormalZ=1 AngleXU=0 Radius=3.5
    g28: LineSegment StartX=-4.96891 StartY=-1.75 StartZ=0 EndX=-4.96891 EndY=1.75 EndZ=0
    g29: LineSegment StartX=-4.96891 StartY=1.75 StartZ=0 EndX=-8 EndY=3.5 EndZ=0
    g30: LineSegment StartX=-8 StartY=3.5 StartZ=0 EndX=-11.0311 EndY=1.75 EndZ=0
    g31: LineSegment StartX=-11.0311 StartY=1.75 StartZ=0 EndX=-11.0311 EndY=-1.75 EndZ=0
    g32: LineSegment StartX=-11.0311 StartY=-1.75 StartZ=0 EndX=-8 EndY=-3.5 EndZ=0
    g33: LineSegment StartX=-8 StartY=-3.5 StartZ=0 EndX=-4.96891 EndY=-1.75 EndZ=0
    g34: Circle [constr] CenterX=-8 CenterY=0 CenterZ=0 NormalX=0 NormalY=0 NormalZ=1 AngleXU=0 Radius=3.5
    g35: LineSegment StartX=-4.03109 StartY=-3.5 StartZ=0 EndX=-7.06218 EndY=-5.25 EndZ=0
    g36: LineSegment StartX=-7.06218 StartY=-5.25 StartZ=0 EndX=-7.06218 EndY=-8.75 EndZ=0
    g37: LineSegment StartX=-7.06218 StartY=-8.75 StartZ=0 EndX=-4.03109 EndY=-10.5 EndZ=0
    g38: LineSegment StartX=-4.03109 StartY=-10.5 StartZ=0 EndX=-1 EndY=-8.75 EndZ=0
    g39: LineSegment StartX=-1 StartY=-8.75 StartZ=0 EndX=-1 EndY=-5.25 EndZ=0
    g40: LineSegment StartX=-1 StartY=-5.25 StartZ=0 EndX=-4.03109 EndY=-3.5 EndZ=0
    g41: Circle [constr] CenterX=-4.03109 CenterY=-7 CenterZ=0 NormalX=0 NormalY=0 NormalZ=1 AngleXU=0 Radius=3.5
    g42: LineSegment StartX=4.03109 StartY=-3.5 StartZ=0 EndX=1 EndY=-5.25 EndZ=0
    g43: LineSegment StartX=1 StartY=-5.25 StartZ=0 EndX=1 EndY=-8.75 EndZ=0
    g44: LineSegment StartX=1 StartY=-8.75 StartZ=0 EndX=4.03109 EndY=-10.5 EndZ=0
    g45: LineSegment StartX=4.03109 StartY=-10.5 StartZ=0 EndX=7.06218 EndY=-8.75 EndZ=0
    g46: LineSegment StartX=7.06218 StartY=-8.75 StartZ=0 EndX=7.06218 EndY=-5.25 EndZ=0
    g47: LineSegment StartX=7.06218 StartY=-5.25 StartZ=0 EndX=4.03109 EndY=-3.5 EndZ=0
    g48: Circle [constr] CenterX=4.03109 CenterY=-7 CenterZ=0 NormalX=0 NormalY=0 NormalZ=1 AngleXU=0 Radius=3.5
  constraints (117):
    c: Coincident(g0,g1)
    c: Coincident(g1,g2)
    c: Coincident(g2,g3)
    c: Coincident(g3,g4)
    c: Coincident(g4,g5)
    c: Coincident(g5,g0)
    c: Equal(g0, g1-g5) x5
    c: PointOnObject(g0,g6)
    c: PointOnObject(g1,g6)
    c: PointOnObject(g2,g6)
    c: PointOnObject(g3,g6)
    c: PointOnObject(g4,g6)
    c: PointOnObject(g5,g6)
    c: Coincident(g6,g-1)
    c: Diameter(g6) = 7
    c: PointOnObject(g0,g-2)
    c: Coincident(g7,g8)
    c: Coincident(g8,g9)
    c: Coincident(g9,g10)
    c: Coincident(g10,g11)
    c: Coincident(g11,g12)
    c: Coincident(g12,g7)
    c: Equal(g7, g8-g12) x5
    c: PointOnObject(g7,g13)
    c: PointOnObject(g8,g13)
    c: PointOnObject(g9,g13)
    c: PointOnObject(g10,g13)
    c: PointOnObject(g11,g13)
    c: PointOnObject(g12,g13)
    c: PointOnObject(g13,g-1)
    c: Diameter(g13) = 7
    c: Distance(g6,g13) = 8
    c: Horizontal(g0,g10)
    c: Coincident(g14,g15)
    c: Coincident(g15,g16)
    c: Coincident(g16,g17)
    c: Coincident(g17,g18)
    c: Coincident(g18,g19)
    c: Coincident(g19,g14)
    c: Equal(g14, g15-g19) x5
    c: PointOnObject(g14,g20)
    c: PointOnObject(g15,g20)
    c: PointOnObject(g16,g20)
    c: PointOnObject(g17,g20)
    c: PointOnObject(g18,g20)
    c: PointOnObject(g19,g20)
    c: Diameter(g20) = 7
    c: DistanceY(g-1,g20) = 7
    c: Vertical(g18)
    c: Distance(g17,g-2) = 1
    c: Coincident(g21,g22)
    c: Coincident(g22,g23)
    c: Coincident(g23,g24)
    c: Coincident(g24,g25)
    c: Coincident(g25,g26)
    c: Coincident(g26,g21)
    c: Equal(g21, g22-g26) x5
    c: PointOnObject(g21,g27)
    c: PointOnObject(g22,g27)
    c: PointOnObject(g23,g27)
    c: PointOnObject(g24,g27)
    c: PointOnObject(g25,g27)
    c: PointOnObject(g26,g27)
    c: Diameter(g27) = 7
    c: DistanceY(g-1,g27) = 7
    c: DistanceX(g21,g-1) = 1
    c: Vertical(g21)
    c: Coincident(g28,g29)
    c: Coincident(g29,g30)
    c: Coincident(g30,g31)
    c: Coincident(g31,g32)
    c: Coincident(g32,g33)
    c: Coincident(g33,g28)
    c: Equal(g28, g29-g33) x5
    c: PointOnObject(g28,g34)
    c: PointOnObject(g29,g34)
    c: PointOnObject(g30,g34)
    c: PointOnObject(g31,g34)
    c: PointOnObject(g32,g34)
    c: PointOnObject(g33,g34)
    c: PointOnObject(g34,g-1)
    c: Diameter(g34) = 7
    c: Vertical(g31)
    c: DistanceX(g34,g-1) = 8
    c: Coincident(g35,g36)
    c: Coincident(g36,g37)
    c: Coincident(g37,g38)
    c: Coincident(g38,g39)
    c: Coincident(g39,g40)
    c: Coincident(g40,g35)
    c: Equal(g35, g36-g40) x5
    c: PointOnObject(g35,g41)
    c: PointOnObject(g36,g41)
    c: PointOnObject(g37,g41)
    c: PointOnObject(g38,g41)
    c: PointOnObject(g39,g41)
    c: PointOnObject(g40,g41)
    c: Coincident(g42,g43)
    c: Coincident(g43,g44)
    c: Coincident(g44,g45)
    c: Coincident(g45,g46)
    c: Coincident(g46,g47)
    c: Coincident(g47,g42)
    c: Equal(g42, g43-g47) x5
    c: PointOnObject(g42,g48)
    c: PointOnObject(g43,g48)
    c: PointOnObject(g44,g48)
    c: PointOnObject(g45,g48)
    c: PointOnObject(g46,g48)
    c: PointOnObject(g47,g48)
    c: Equal(g41,g48)
    c: Diameter(g41) = 7
    c: Vertical(g39)
    c: Vertical(g43)
    c: Distance(g-2,g39) = 1
    c: Symmetric(g38,g43,g-2)
    c: Distance(g41,g-1) = 7
FEATURE [Part::Extrusion] Extrude503  label="hex118"
  Base = -> Sketch511
  Dir = (0,-1,2e-16)
  DirMode = 2
  FaceMakerClass = Part::FaceMakerBullseye
  FaceMakerMode = 3
  LengthFwd = 10
  LengthRev = 0
  Placement = pos=(36,0,-7) rot=(0,0,1;0rad)
  Solid = true
  Symmetric = false
FEATURE [Sketcher::SketchObject] Sketch512
  ArcFitTolerance = 1e-06
  FullyConstrained = true
  MakeInternals = false
  Placement = pos=(0,0,0) rot=(1,0,0;1.5708rad)
  sketch-geometry (49):
    g0: LineSegment StartX=1e-16 StartY=3.5 StartZ=0 EndX=-3.03109 EndY=1.75 EndZ=0
    g1: LineSegment StartX=-3.03109 StartY=1.75 StartZ=0 EndX=-3.03109 EndY=-1.75 EndZ=0
    g2: LineSegment StartX=-3.03109 StartY=-1.75 StartZ=0 EndX=-1e-16 EndY=-3.5 EndZ=0
    g3: LineSegment StartX=-1e-16 StartY=-3.5 StartZ=0 EndX=3.03109 EndY=-1.75 EndZ=0
    g4: LineSegment StartX=3.03109 StartY=-1.75 StartZ=0 EndX=3.03109 EndY=1.75 EndZ=0
    g5: LineSegment StartX=3.03109 StartY=1.75 StartZ=0 EndX=1e-16 EndY=3.5 EndZ=0
    g6: Circle [constr] CenterX=0 CenterY=0 CenterZ=0 NormalX=0 NormalY=0 NormalZ=1 AngleXU=0 Radius=3.5
    g7: LineSegment StartX=4.96892 StartY=-1.75002 StartZ=0 EndX=8.00002 EndY=-3.5 EndZ=0
    g8: LineSegment StartX=8.00002 StartY=-3.5 StartZ=0 EndX=11.0311 EndY=-1.74998 EndZ=0
    g9: LineSegment StartX=11.0311 StartY=-1.74998 StartZ=0 EndX=11.0311 EndY=1.75002 EndZ=0
    g10: LineSegment StartX=11.0311 StartY=1.75002 StartZ=0 EndX=7.99998 EndY=3.5 EndZ=0
    g11: LineSegment StartX=7.99998 StartY=3.5 StartZ=0 EndX=4.9689 EndY=1.74998 EndZ=0
    g12: LineSegment StartX=4.9689 StartY=1.74998 StartZ=0 EndX=4.96892 EndY=-1.75002 EndZ=0
    g13: Circle [constr] CenterX=8 CenterY=0 CenterZ=0 NormalX=0 NormalY=0 NormalZ=1 AngleXU=0 Radius=3.5
    g14: LineSegment StartX=4.03109 StartY=3.5 StartZ=0 EndX=7.06218 EndY=5.25 EndZ=0
    g15: LineSegment StartX=7.06218 StartY=5.25 StartZ=0 EndX=7.06218 EndY=8.75 EndZ=0
    g16: LineSegment StartX=7.06218 StartY=8.75 StartZ=0 EndX=4.03109 EndY=10.5 EndZ=0
    g17: LineSegment StartX=4.03109 StartY=10.5 StartZ=0 EndX=1 EndY=8.75 EndZ=0
    g18: LineSegment StartX=1 StartY=8.75 StartZ=0 EndX=1 EndY=5.25 EndZ=0
    g19: LineSegment StartX=1 StartY=5.25 StartZ=0 EndX=4.03109 EndY=3.5 EndZ=0
    g20: Circle [constr] CenterX=4.03109 CenterY=7 CenterZ=0 NormalX=0 NormalY=0 NormalZ=1 AngleXU=0 Radius=3.5
    g21: LineSegment StartX=-1 StartY=5.25 StartZ=0 EndX=-1 EndY=8.75 EndZ=0
    g22: LineSegment StartX=-1 StartY=8.75 StartZ=0 EndX=-4.03109 EndY=10.5 EndZ=0
    g23: LineSegment StartX=-4.03109 StartY=10.5 StartZ=0 EndX=-7.06218 EndY=8.75 EndZ=0
    g24: LineSegment StartX=-7.06218 StartY=8.75 StartZ=0 EndX=-7.06218 EndY=5.25 EndZ=0
    g25: LineSegment StartX=-7.06218 StartY=5.25 StartZ=0 EndX=-4.03109 EndY=3.5 EndZ=0
    g26: LineSegment StartX=-4.03109 StartY=3.5 StartZ=0 EndX=-1 EndY=5.25 EndZ=0
    g27: Circle [constr] CenterX=-4.03109 CenterY=7 CenterZ=0 NormalX=0 NormalY=0 NormalZ=1 AngleXU=0 Radius=3.5
    g28: LineSegment StartX=-4.96891 StartY=-1.75 StartZ=0 EndX=-4.96891 EndY=1.75 EndZ=0
    g29: LineSegment StartX=-4.96891 StartY=1.75 StartZ=0 EndX=-8 EndY=3.5 EndZ=0
    g30: LineSegment StartX=-8 StartY=3.5 StartZ=0 EndX=-11.0311 EndY=1.75 EndZ=0
    g31: LineSegment StartX=-11.0311 StartY=1.75 StartZ=0 EndX=-11.0311 EndY=-1.75 EndZ=0
    g32: LineSegment StartX=-11.0311 StartY=-1.75 StartZ=0 EndX=-8 EndY=-3.5 EndZ=0
    g33: LineSegment StartX=-8 StartY=-3.5 StartZ=0 EndX=-4.96891 EndY=-1.75 EndZ=0
    g34: Circle [constr] CenterX=-8 CenterY=0 CenterZ=0 NormalX=0 NormalY=0 NormalZ=1 AngleXU=0 Radius=3.5
    g35: LineSegment StartX=-4.03109 StartY=-3.5 StartZ=0 EndX=-7.06218 EndY=-5.25 EndZ=0
    g36: LineSegment StartX=-7.06218 StartY=-5.25 StartZ=0 EndX=-7.06218 EndY=-8.75 EndZ=0
    g37: LineSegment StartX=-7.06218 StartY=-8.75 StartZ=0 EndX=-4.03109 EndY=-10.5 EndZ=0
    g38: LineSegment StartX=-4.03109 StartY=-10.5 StartZ=0 EndX=-1 EndY=-8.75 EndZ=0
    g39: LineSegment StartX=-1 StartY=-8.75 StartZ=0 EndX=-1 EndY=-5.25 EndZ=0
    g40: LineSegment StartX=-1 StartY=-5.25 StartZ=0 EndX=-4.03109 EndY=-3.5 EndZ=0
    g41: Circle [constr] CenterX=-4.03109 CenterY=-7 CenterZ=0 NormalX=0 NormalY=0 NormalZ=1 AngleXU=0 Radius=3.5
    g42: LineSegment StartX=4.03109 StartY=-3.5 StartZ=0 EndX=1 EndY=-5.25 EndZ=0
    g43: LineSegment StartX=1 StartY=-5.25 StartZ=0 EndX=1 EndY=-8.75 EndZ=0
    g44: LineSegment StartX=1 StartY=-8.75 StartZ=0 EndX=4.03109 EndY=-10.5 EndZ=0
    g45: LineSegment StartX=4.03109 StartY=-10.5 StartZ=0 EndX=7.06218 EndY=-8.75 EndZ=0
    g46: LineSegment StartX=7.06218 StartY=-8.75 StartZ=0 EndX=7.06218 EndY=-5.25 EndZ=0
    g47: LineSegment StartX=7.06218 StartY=-5.25 StartZ=0 EndX=4.03109 EndY=-3.5 EndZ=0
    g48: Circle [constr] CenterX=4.03109 CenterY=-7 CenterZ=0 NormalX=0 NormalY=0 NormalZ=1 AngleXU=0 Radius=3.5
  constraints (117):
    c: Coincident(g0,g1)
    c: Coincident(g1,g2)
    c: Coincident(g2,g3)
    c: Coincident(g3,g4)
    c: Coincident(g4,g5)
    c: Coincident(g5,g0)
    c: Equal(g0, g1-g5) x5
    c: PointOnObject(g0,g6)
    c: PointOnObject(g1,g6)
    c: PointOnObject(g2,g6)
    c: PointOnObject(g3,g6)
    c: PointOnObject(g4,g6)
    c: PointOnObject(g5,g6)
    c: Coincident(g6,g-1)
    c: Diameter(g6) = 7
    c: PointOnObject(g0,g-2)
    c: Coincident(g7,g8)
    c: Coincident(g8,g9)
    c: Coincident(g9,g10)
    c: Coincident(g10,g11)
    c: Coincident(g11,g12)
    c: Coincident(g12,g7)
    c: Equal(g7, g8-g12) x5
    c: PointOnObject(g7,g13)
    c: PointOnObject(g8,g13)
    c: PointOnObject(g9,g13)
    c: PointOnObject(g10,g13)
    c: PointOnObject(g11,g13)
    c: PointOnObject(g12,g13)
    c: PointOnObject(g13,g-1)
    c: Diameter(g13) = 7
    c: Distance(g6,g13) = 8
    c: Horizontal(g0,g10)
    c: Coincident(g14,g15)
    c: Coincident(g15,g16)
    c: Coincident(g16,g17)
    c: Coincident(g17,g18)
    c: Coincident(g18,g19)
    c: Coincident(g19,g14)
    c: Equal(g14, g15-g19) x5
    c: PointOnObject(g14,g20)
    c: PointOnObject(g15,g20)
    c: PointOnObject(g16,g20)
    c: PointOnObject(g17,g20)
    c: PointOnObject(g18,g20)
    c: PointOnObject(g19,g20)
    c: Diameter(g20) = 7
    c: DistanceY(g-1,g20) = 7
    c: Vertical(g18)
    c: Distance(g17,g-2) = 1
    c: Coincident(g21,g22)
    c: Coincident(g22,g23)
    c: Coincident(g23,g24)
    c: Coincident(g24,g25)
    c: Coincident(g25,g26)
    c: Coincident(g26,g21)
    c: Equal(g21, g22-g26) x5
    c: PointOnObject(g21,g27)
    c: PointOnObject(g22,g27)
    c: PointOnObject(g23,g27)
    c: PointOnObject(g24,g27)
    c: PointOnObject(g25,g27)
    c: PointOnObject(g26,g27)
    c: Diameter(g27) = 7
    c: DistanceY(g-1,g27) = 7
    c: DistanceX(g21,g-1) = 1
    c: Vertical(g21)
    c: Coincident(g28,g29)
    c: Coincident(g29,g30)
    c: Coincident(g30,g31)
    c: Coincident(g31,g32)
    c: Coincident(g32,g33)
    c: Coincident(g33,g28)
    c: Equal(g28, g29-g33) x5
    c: PointOnObject(g28,g34)
    c: PointOnObject(g29,g34)
    c: PointOnObject(g30,g34)
    c: PointOnObject(g31,g34)
    c: PointOnObject(g32,g34)
    c: PointOnObject(g33,g34)
    c: PointOnObject(g34,g-1)
    c: Diameter(g34) = 7
    c: Vertical(g31)
    c: DistanceX(g34,g-1) = 8
    c: Coincident(g35,g36)
    c: Coincident(g36,g37)
    c: Coincident(g37,g38)
    c: Coincident(g38,g39)
    c: Coincident(g39,g40)
    c: Coincident(g40,g35)
    c: Equal(g35, g36-g40) x5
    c: PointOnObject(g35,g41)
    c: PointOnObject(g36,g41)
    c: PointOnObject(g37,g41)
    c: PointOnObject(g38,g41)
    c: PointOnObject(g39,g41)
    c: PointOnObject(g40,g41)
    c: Coincident(g42,g43)
    c: Coincident(g43,g44)
    c: Coincident(g44,g45)
    c: Coincident(g45,g46)
    c: Coincident(g46,g47)
    c: Coincident(g47,g42)
    c: Equal(g42, g43-g47) x5
    c: PointOnObject(g42,g48)
    c: PointOnObject(g43,g48)
    c: PointOnObject(g44,g48)
    c: PointOnObject(g45,g48)
    c: PointOnObject(g46,g48)
    c: PointOnObject(g47,g48)
    c: Equal(g41,g48)
    c: Diameter(g41) = 7
    c: Vertical(g39)
    c: Vertical(g43)
    c: Distance(g-2,g39) = 1
    c: Symmetric(g38,g43,g-2)
    c: Distance(g41,g-1) = 7
FEATURE [Part::Extrusion] Extrude504  label="hex119"
  Base = -> Sketch512
  Dir = (0,-1,2e-16)
  DirMode = 2
  FaceMakerClass = Part::FaceMakerBullseye
  FaceMakerMode = 3
  LengthFwd = 10
  LengthRev = 0
  Placement = pos=(56,0,0) rot=(0,0,1;0rad)
  Solid = true
  Symmetric = false
FEATURE [Sketcher::SketchObject] Sketch513
  ArcFitTolerance = 1e-06
  FullyConstrained = true
  MakeInternals = false
  Placement = pos=(0,0,0) rot=(1,0,0;1.5708rad)
  sketch-geometry (49):
    g0: LineSegment StartX=1e-16 StartY=3.5 StartZ=0 EndX=-3.03109 EndY=1.75 EndZ=0
    g1: LineSegment StartX=-3.03109 StartY=1.75 StartZ=0 EndX=-3.03109 EndY=-1.75 EndZ=0
    g2: LineSegment StartX=-3.03109 StartY=-1.75 StartZ=0 EndX=-1e-16 EndY=-3.5 EndZ=0
    g3: LineSegment StartX=-1e-16 StartY=-3.5 StartZ=0 EndX=3.03109 EndY=-1.75 EndZ=0
    g4: LineSegment StartX=3.03109 StartY=-1.75 StartZ=0 EndX=3.03109 EndY=1.75 EndZ=0
    g5: LineSegment StartX=3.03109 StartY=1.75 StartZ=0 EndX=1e-16 EndY=3.5 EndZ=0
    g6: Circle [constr] CenterX=0 CenterY=0 CenterZ=0 NormalX=0 NormalY=0 NormalZ=1 AngleXU=0 Radius=3.5
    g7: LineSegment StartX=4.96892 StartY=-1.75002 StartZ=0 EndX=8.00002 EndY=-3.5 EndZ=0
    g8: LineSegment StartX=8.00002 StartY=-3.5 StartZ=0 EndX=11.0311 EndY=-1.74998 EndZ=0
    g9: LineSegment StartX=11.0311 StartY=-1.74998 StartZ=0 EndX=11.0311 EndY=1.75002 EndZ=0
    g10: LineSegment StartX=11.0311 StartY=1.75002 StartZ=0 EndX=7.99998 EndY=3.5 EndZ=0
    g11: LineSegment StartX=7.99998 StartY=3.5 StartZ=0 EndX=4.9689 EndY=1.74998 EndZ=0
    g12: LineSegment StartX=4.9689 StartY=1.74998 StartZ=0 EndX=4.96892 EndY=-1.75002 EndZ=0
    g13: Circle [constr] CenterX=8 CenterY=0 CenterZ=0 NormalX=0 NormalY=0 NormalZ=1 AngleXU=0 Radius=3.5
    g14: LineSegment StartX=4.03109 StartY=3.5 StartZ=0 EndX=7.06218 EndY=5.25 EndZ=0
    g15: LineSegment StartX=7.06218 StartY=5.25 StartZ=0 EndX=7.06218 EndY=8.75 EndZ=0
    g16: LineSegment StartX=7.06218 StartY=8.75 StartZ=0 EndX=4.03109 EndY=10.5 EndZ=0
    g17: LineSegment StartX=4.03109 StartY=10.5 StartZ=0 EndX=1 EndY=8.75 EndZ=0
    g18: LineSegment StartX=1 StartY=8.75 StartZ=0 EndX=1 EndY=5.25 EndZ=0
    g19: LineSegment StartX=1 StartY=5.25 StartZ=0 EndX=4.03109 EndY=3.5 EndZ=0
    g20: Circle [constr] CenterX=4.03109 CenterY=7 CenterZ=0 NormalX=0 NormalY=0 NormalZ=1 AngleXU=0 Radius=3.5
    g21: LineSegment StartX=-1 StartY=5.25 StartZ=0 EndX=-1 EndY=8.75 EndZ=0
    g22: LineSegment StartX=-1 StartY=8.75 StartZ=0 EndX=-4.03109 EndY=10.5 EndZ=0
    g23: LineSegment StartX=-4.03109 StartY=10.5 StartZ=0 EndX=-7.06218 EndY=8.75 EndZ=0
    g24: LineSegment StartX=-7.06218 StartY=8.75 StartZ=0 EndX=-7.06218 EndY=5.25 EndZ=0
    g25: LineSegment StartX=-7.06218 StartY=5.25 StartZ=0 EndX=-4.03109 EndY=3.5 EndZ=0
    g26: LineSegment StartX=-4.03109 StartY=3.5 StartZ=0 EndX=-1 EndY=5.25 EndZ=0
    g27: Circle [constr] CenterX=-4.03109 CenterY=7 CenterZ=0 NormalX=0 NormalY=0 NormalZ=1 AngleXU=0 Radius=3.5
    g28: LineSegment StartX=-4.96891 StartY=-1.75 StartZ=0 EndX=-4.96891 EndY=1.75 EndZ=0
    g29: LineSegment StartX=-4.96891 StartY=1.75 StartZ=0 EndX=-8 EndY=3.5 EndZ=0
    g30: LineSegment StartX=-8 StartY=3.5 StartZ=0 EndX=-11.0311 EndY=1.75 EndZ=0
    g31: LineSegment StartX=-11.0311 StartY=1.75 StartZ=0 EndX=-11.0311 EndY=-1.75 EndZ=0
    g32: LineSegment StartX=-11.0311 StartY=-1.75 StartZ=0 EndX=-8 EndY=-3.5 EndZ=0
    g33: LineSegment StartX=-8 StartY=-3.5 StartZ=0 EndX=-4.96891 EndY=-1.75 EndZ=0
    g34: Circle [constr] CenterX=-8 CenterY=0 CenterZ=0 NormalX=0 NormalY=0 NormalZ=1 AngleXU=0 Radius=3.5
    g35: LineSegment StartX=-4.03109 StartY=-3.5 StartZ=0 EndX=-7.06218 EndY=-5.25 EndZ=0
    g36: LineSegment StartX=-7.06218 StartY=-5.25 StartZ=0 EndX=-7.06218 EndY=-8.75 EndZ=0
    g37: LineSegment StartX=-7.06218 StartY=-8.75 StartZ=0 EndX=-4.03109 EndY=-10.5 EndZ=0
    g38: LineSegment StartX=-4.03109 StartY=-10.5 StartZ=0 EndX=-1 EndY=-8.75 EndZ=0
    g39: LineSegment StartX=-1 StartY=-8.75 StartZ=0 EndX=-1 EndY=-5.25 EndZ=0
    g40: LineSegment StartX=-1 StartY=-5.25 StartZ=0 EndX=-4.03109 EndY=-3.5 EndZ=0
    g41: Circle [constr] CenterX=-4.03109 CenterY=-7 CenterZ=0 NormalX=0 NormalY=0 NormalZ=1 AngleXU=0 Radius=3.5
    g42: LineSegment StartX=4.03109 StartY=-3.5 StartZ=0 EndX=1 EndY=-5.25 EndZ=0
    g43: LineSegment StartX=1 StartY=-5.25 StartZ=0 EndX=1 EndY=-8.75 EndZ=0
    g44: LineSegment StartX=1 StartY=-8.75 StartZ=0 EndX=4.03109 EndY=-10.5 EndZ=0
    g45: LineSegment StartX=4.03109 StartY=-10.5 StartZ=0 EndX=7.06218 EndY=-8.75 EndZ=0
    g46: LineSegment StartX=7.06218 StartY=-8.75 StartZ=0 EndX=7.06218 EndY=-5.25 EndZ=0
    g47: LineSegment StartX=7.06218 StartY=-5.25 StartZ=0 EndX=4.03109 EndY=-3.5 EndZ=0
    g48: Circle [constr] CenterX=4.03109 CenterY=-7 CenterZ=0 NormalX=0 NormalY=0 NormalZ=1 AngleXU=0 Radius=3.5
  constraints (117):
    c: Coincident(g0,g1)
    c: Coincident(g1,g2)
    c: Coincident(g2,g3)
    c: Coincident(g3,g4)
    c: Coincident(g4,g5)
    c: Coincident(g5,g0)
    c: Equal(g0, g1-g5) x5
    c: PointOnObject(g0,g6)
    c: PointOnObject(g1,g6)
    c: PointOnObject(g2,g6)
    c: PointOnObject(g3,g6)
    c: PointOnObject(g4,g6)
    c: PointOnObject(g5,g6)
    c: Coincident(g6,g-1)
    c: Diameter(g6) = 7
    c: PointOnObject(g0,g-2)
    c: Coincident(g7,g8)
    c: Coincident(g8,g9)
    c: Coincident(g9,g10)
    c: Coincident(g10,g11)
    c: Coincident(g11,g12)
    c: Coincident(g12,g7)
    c: Equal(g7, g8-g12) x5
    c: PointOnObject(g7,g13)
    c: PointOnObject(g8,g13)
    c: PointOnObject(g9,g13)
    c: PointOnObject(g10,g13)
    c: PointOnObject(g11,g13)
    c: PointOnObject(g12,g13)
    c: PointOnObject(g13,g-1)
    c: Diameter(g13) = 7
    c: Distance(g6,g13) = 8
    c: Horizontal(g0,g10)
    c: Coincident(g14,g15)
    c: Coincident(g15,g16)
    c: Coincident(g16,g17)
    c: Coincident(g17,g18)
    c: Coincident(g18,g19)
    c: Coincident(g19,g14)
    c: Equal(g14, g15-g19) x5
    c: PointOnObject(g14,g20)
    c: PointOnObject(g15,g20)
    c: PointOnObject(g16,g20)
    c: PointOnObject(g17,g20)
    c: PointOnObject(g18,g20)
    c: PointOnObject(g19,g20)
    c: Diameter(g20) = 7
    c: DistanceY(g-1,g20) = 7
    c: Vertical(g18)
    c: Distance(g17,g-2) = 1
    c: Coincident(g21,g22)
    c: Coincident(g22,g23)
    c: Coincident(g23,g24)
    c: Coincident(g24,g25)
    c: Coincident(g25,g26)
    c: Coincident(g26,g21)
    c: Equal(g21, g22-g26) x5
    c: PointOnObject(g21,g27)
    c: PointOnObject(g22,g27)
    c: PointOnObject(g23,g27)
    c: PointOnObject(g24,g27)
    c: PointOnObject(g25,g27)
    c: PointOnObject(g26,g27)
    c: Diameter(g27) = 7
    c: DistanceY(g-1,g27) = 7
    c: DistanceX(g21,g-1) = 1
    c: Vertical(g21)
    c: Coincident(g28,g29)
    c: Coincident(g29,g30)
    c: Coincident(g30,g31)
    c: Coincident(g31,g32)
    c: Coincident(g32,g33)
    c: Coincident(g33,g28)
    c: Equal(g28, g29-g33) x5
    c: PointOnObject(g28,g34)
    c: PointOnObject(g29,g34)
    c: PointOnObject(g30,g34)
    c: PointOnObject(g31,g34)
    c: PointOnObject(g32,g34)
    c: PointOnObject(g33,g34)
    c: PointOnObject(g34,g-1)
    c: Diameter(g34) = 7
    c: Vertical(g31)
    c: DistanceX(g34,g-1) = 8
    c: Coincident(g35,g36)
    c: Coincident(g36,g37)
    c: Coincident(g37,g38)
    c: Coincident(g38,g39)
    c: Coincident(g39,g40)
    c: Coincident(g40,g35)
    c: Equal(g35, g36-g40) x5
    c: PointOnObject(g35,g41)
    c: PointOnObject(g36,g41)
    c: PointOnObject(g37,g41)
    c: PointOnObject(g38,g41)
    c: PointOnObject(g39,g41)
    c: PointOnObject(g40,g41)
    c: Coincident(g42,g43)
    c: Coincident(g43,g44)
    c: Coincident(g44,g45)
    c: Coincident(g45,g46)
    c: Coincident(g46,g47)
    c: Coincident(g47,g42)
    c: Equal(g42, g43-g47) x5
    c: PointOnObject(g42,g48)
    c: PointOnObject(g43,g48)
    c: PointOnObject(g44,g48)
    c: PointOnObject(g45,g48)
    c: PointOnObject(g46,g48)
    c: PointOnObject(g47,g48)
    c: Equal(g41,g48)
    c: Diameter(g41) = 7
    c: Vertical(g39)
    c: Vertical(g43)
    c: Distance(g-2,g39) = 1
    c: Symmetric(g38,g43,g-2)
    c: Distance(g41,g-1) = 7
FEATURE [Part::Extrusion] Extrude505  label="hex120"
  Base = -> Sketch513
  Dir = (0,-1,2e-16)
  DirMode = 2
  FaceMakerClass = Part::FaceMakerBullseye
  FaceMakerMode = 3
  LengthFwd = 10
  LengthRev = 0
  Placement = pos=(52,0,-21) rot=(0,0,1;0rad)
  Solid = true
  Symmetric = false
FEATURE [Sketcher::SketchObject] Sketch514
  ArcFitTolerance = 1e-06
  FullyConstrained = true
  MakeInternals = false
  Placement = pos=(0,0,0) rot=(1,0,0;1.5708rad)
  sketch-geometry (49):
    g0: LineSegment StartX=1e-16 StartY=3.5 StartZ=0 EndX=-3.03109 EndY=1.75 EndZ=0
    g1: LineSegment StartX=-3.03109 StartY=1.75 StartZ=0 EndX=-3.03109 EndY=-1.75 EndZ=0
    g2: LineSegment StartX=-3.03109 StartY=-1.75 StartZ=0 EndX=-1e-16 EndY=-3.5 EndZ=0
    g3: LineSegment StartX=-1e-16 StartY=-3.5 StartZ=0 EndX=3.03109 EndY=-1.75 EndZ=0
    g4: LineSegment StartX=3.03109 StartY=-1.75 StartZ=0 EndX=3.03109 EndY=1.75 EndZ=0
    g5: LineSegment StartX=3.03109 StartY=1.75 StartZ=0 EndX=1e-16 EndY=3.5 EndZ=0
    g6: Circle [constr] CenterX=0 CenterY=0 CenterZ=0 NormalX=0 NormalY=0 NormalZ=1 AngleXU=0 Radius=3.5
    g7: LineSegment StartX=4.96892 StartY=-1.75002 StartZ=0 EndX=8.00002 EndY=-3.5 EndZ=0
    g8: LineSegment StartX=8.00002 StartY=-3.5 StartZ=0 EndX=11.0311 EndY=-1.74998 EndZ=0
    g9: LineSegment StartX=11.0311 StartY=-1.74998 StartZ=0 EndX=11.0311 EndY=1.75002 EndZ=0
    g10: LineSegment StartX=11.0311 StartY=1.75002 StartZ=0 EndX=7.99998 EndY=3.5 EndZ=0
    g11: LineSegment StartX=7.99998 StartY=3.5 StartZ=0 EndX=4.9689 EndY=1.74998 EndZ=0
    g12: LineSegment StartX=4.9689 StartY=1.74998 StartZ=0 EndX=4.96892 EndY=-1.75002 EndZ=0
    g13: Circle [constr] CenterX=8 CenterY=0 CenterZ=0 NormalX=0 NormalY=0 NormalZ=1 AngleXU=0 Radius=3.5
    g14: LineSegment StartX=4.03109 StartY=3.5 StartZ=0 EndX=7.06218 EndY=5.25 EndZ=0
    g15: LineSegment StartX=7.06218 StartY=5.25 StartZ=0 EndX=7.06218 EndY=8.75 EndZ=0
    g16: LineSegment StartX=7.06218 StartY=8.75 StartZ=0 EndX=4.03109 EndY=10.5 EndZ=0
    g17: LineSegment StartX=4.03109 StartY=10.5 StartZ=0 EndX=1 EndY=8.75 EndZ=0
    g18: LineSegment StartX=1 StartY=8.75 StartZ=0 EndX=1 EndY=5.25 EndZ=0
    g19: LineSegment StartX=1 StartY=5.25 StartZ=0 EndX=4.03109 EndY=3.5 EndZ=0
    g20: Circle [constr] CenterX=4.03109 CenterY=7 CenterZ=0 NormalX=0 NormalY=0 NormalZ=1 AngleXU=0 Radius=3.5
    g21: LineSegment StartX=-1 StartY=5.25 StartZ=0 EndX=-1 EndY=8.75 EndZ=0
    g22: LineSegment StartX=-1 StartY=8.75 StartZ=0 EndX=-4.03109 EndY=10.5 EndZ=0
    g23: LineSegment StartX=-4.03109 StartY=10.5 StartZ=0 EndX=-7.06218 EndY=8.75 EndZ=0
    g24: LineSegment StartX=-7.06218 StartY=8.75 StartZ=0 EndX=-7.06218 EndY=5.25 EndZ=0
    g25: LineSegment StartX=-7.06218 StartY=5.25 StartZ=0 EndX=-4.03109 EndY=3.5 EndZ=0
    g26: LineSegment StartX=-4.03109 StartY=3.5 StartZ=0 EndX=-1 EndY=5.25 EndZ=0
    g27: Circle [constr] CenterX=-4.03109 CenterY=7 CenterZ=0 NormalX=0 NormalY=0 NormalZ=1 AngleXU=0 Radius=3.5
    g28: LineSegment StartX=-4.96891 StartY=-1.75 StartZ=0 EndX=-4.96891 EndY=1.75 EndZ=0
    g29: LineSegment StartX=-4.96891 StartY=1.75 StartZ=0 EndX=-8 EndY=3.5 EndZ=0
    g30: LineSegment StartX=-8 StartY=3.5 StartZ=0 EndX=-11.0311 EndY=1.75 EndZ=0
    g31: LineSegment StartX=-11.0311 StartY=1.75 StartZ=0 EndX=-11.0311 EndY=-1.75 EndZ=0
    g32: LineSegment StartX=-11.0311 StartY=-1.75 StartZ=0 EndX=-8 EndY=-3.5 EndZ=0
    g33: LineSegment StartX=-8 StartY=-3.5 StartZ=0 EndX=-4.96891 EndY=-1.75 EndZ=0
    g34: Circle [constr] CenterX=-8 CenterY=0 CenterZ=0 NormalX=0 NormalY=0 NormalZ=1 AngleXU=0 Radius=3.5
    g35: LineSegment StartX=-4.03109 StartY=-3.5 StartZ=0 EndX=-7.06218 EndY=-5.25 EndZ=0
    g36: LineSegment StartX=-7.06218 StartY=-5.25 StartZ=0 EndX=-7.06218 EndY=-8.75 EndZ=0
    g37: LineSegment StartX=-7.06218 StartY=-8.75 StartZ=0 EndX=-4.03109 EndY=-10.5 EndZ=0
    g38: LineSegment StartX=-4.03109 StartY=-10.5 StartZ=0 EndX=-1 EndY=-8.75 EndZ=0
    g39: LineSegment StartX=-1 StartY=-8.75 StartZ=0 EndX=-1 EndY=-5.25 EndZ=0
    g40: LineSegment StartX=-1 StartY=-5.25 StartZ=0 EndX=-4.03109 EndY=-3.5 EndZ=0
    g41: Circle [constr] CenterX=-4.03109 CenterY=-7 CenterZ=0 NormalX=0 NormalY=0 NormalZ=1 AngleXU=0 Radius=3.5
    g42: LineSegment StartX=4.03109 StartY=-3.5 StartZ=0 EndX=1 EndY=-5.25 EndZ=0
    g43: LineSegment StartX=1 StartY=-5.25 StartZ=0 EndX=1 EndY=-8.75 EndZ=0
    g44: LineSegment StartX=1 StartY=-8.75 StartZ=0 EndX=4.03109 EndY=-10.5 EndZ=0
    g45: LineSegment StartX=4.03109 StartY=-10.5 StartZ=0 EndX=7.06218 EndY=-8.75 EndZ=0
    g46: LineSegment StartX=7.06218 StartY=-8.75 StartZ=0 EndX=7.06218 EndY=-5.25 EndZ=0
    g47: LineSegment StartX=7.06218 StartY=-5.25 StartZ=0 EndX=4.03109 EndY=-3.5 EndZ=0
    g48: Circle [constr] CenterX=4.03109 CenterY=-7 CenterZ=0 NormalX=0 NormalY=0 NormalZ=1 AngleXU=0 Radius=3.5
  constraints (117):
    c: Coincident(g0,g1)
    c: Coincident(g1,g2)
    c: Coincident(g2,g3)
    c: Coincident(g3,g4)
    c: Coincident(g4,g5)
    c: Coincident(g5,g0)
    c: Equal(g0, g1-g5) x5
    c: PointOnObject(g0,g6)
    c: PointOnObject(g1,g6)
    c: PointOnObject(g2,g6)
    c: PointOnObject(g3,g6)
    c: PointOnObject(g4,g6)
    c: PointOnObject(g5,g6)
    c: Coincident(g6,g-1)
    c: Diameter(g6) = 7
    c: PointOnObject(g0,g-2)
    c: Coincident(g7,g8)
    c: Coincident(g8,g9)
    c: Coincident(g9,g10)
    c: Coincident(g10,g11)
    c: Coincident(g11,g12)
    c: Coincident(g12,g7)
    c: Equal(g7, g8-g12) x5
    c: PointOnObject(g7,g13)
    c: PointOnObject(g8,g13)
    c: PointOnObject(g9,g13)
    c: PointOnObject(g10,g13)
    c: PointOnObject(g11,g13)
    c: PointOnObject(g12,g13)
    c: PointOnObject(g13,g-1)
    c: Diameter(g13) = 7
    c: Distance(g6,g13) = 8
    c: Horizontal(g0,g10)
    c: Coincident(g14,g15)
    c: Coincident(g15,g16)
    c: Coincident(g16,g17)
    c: Coincident(g17,g18)
    c: Coincident(g18,g19)
    c: Coincident(g19,g14)
    c: Equal(g14, g15-g19) x5
    c: PointOnObject(g14,g20)
    c: PointOnObject(g15,g20)
    c: PointOnObject(g16,g20)
    c: PointOnObject(g17,g20)
    c: PointOnObject(g18,g20)
    c: PointOnObject(g19,g20)
    c: Diameter(g20) = 7
    c: DistanceY(g-1,g20) = 7
    c: Vertical(g18)
    c: Distance(g17,g-2) = 1
    c: Coincident(g21,g22)
    c: Coincident(g22,g23)
    c: Coincident(g23,g24)
    c: Coincident(g24,g25)
    c: Coincident(g25,g26)
    c: Coincident(g26,g21)
    c: Equal(g21, g22-g26) x5
    c: PointOnObject(g21,g27)
    c: PointOnObject(g22,g27)
    c: PointOnObject(g23,g27)
    c: PointOnObject(g24,g27)
    c: PointOnObject(g25,g27)
    c: PointOnObject(g26,g27)
    c: Diameter(g27) = 7
    c: DistanceY(g-1,g27) = 7
    c: DistanceX(g21,g-1) = 1
    c: Vertical(g21)
    c: Coincident(g28,g29)
    c: Coincident(g29,g30)
    c: Coincident(g30,g31)
    c: Coincident(g31,g32)
    c: Coincident(g32,g33)
    c: Coincident(g33,g28)
    c: Equal(g28, g29-g33) x5
    c: PointOnObject(g28,g34)
    c: PointOnObject(g29,g34)
    c: PointOnObject(g30,g34)
    c: PointOnObject(g31,g34)
    c: PointOnObject(g32,g34)
    c: PointOnObject(g33,g34)
    c: PointOnObject(g34,g-1)
    c: Diameter(g34) = 7
    c: Vertical(g31)
    c: DistanceX(g34,g-1) = 8
    c: Coincident(g35,g36)
    c: Coincident(g36,g37)
    c: Coincident(g37,g38)
    c: Coincident(g38,g39)
    c: Coincident(g39,g40)
    c: Coincident(g40,g35)
    c: Equal(g35, g36-g40) x5
    c: PointOnObject(g35,g41)
    c: PointOnObject(g36,g41)
    c: PointOnObject(g37,g41)
    c: PointOnObject(g38,g41)
    c: PointOnObject(g39,g41)
    c: PointOnObject(g40,g41)
    c: Coincident(g42,g43)
    c: Coincident(g43,g44)
    c: Coincident(g44,g45)
    c: Coincident(g45,g46)
    c: Coincident(g46,g47)
    c: Coincident(g47,g42)
    c: Equal(g42, g43-g47) x5
    c: PointOnObject(g42,g48)
    c: PointOnObject(g43,g48)
    c: PointOnObject(g44,g48)
    c: PointOnObject(g45,g48)
    c: PointOnObject(g46,g48)
    c: PointOnObject(g47,g48)
    c: Equal(g41,g48)
    c: Diameter(g41) = 7
    c: Vertical(g39)
    c: Vertical(g43)
    c: Distance(g-2,g39) = 1
    c: Symmetric(g38,g43,g-2)
    c: Distance(g41,g-1) = 7
FEATURE [Part::Extrusion] Extrude506  label="hex121"
  Base = -> Sketch514
  Dir = (0,-1,2e-16)
  DirMode = 2
  FaceMakerClass = Part::FaceMakerBullseye
  FaceMakerMode = 3
  LengthFwd = 10
  LengthRev = 0
  Placement = pos=(-56,0,0) rot=(0,0,1;0rad)
  Solid = true
  Symmetric = false
FEATURE [Sketcher::SketchObject] Sketch515
  ArcFitTolerance = 1e-06
  FullyConstrained = true
  MakeInternals = false
  Placement = pos=(0,0,0) rot=(1,0,0;1.5708rad)
  sketch-geometry (49):
    g0: LineSegment StartX=1e-16 StartY=3.5 StartZ=0 EndX=-3.03109 EndY=1.75 EndZ=0
    g1: LineSegment StartX=-3.03109 StartY=1.75 StartZ=0 EndX=-3.03109 EndY=-1.75 EndZ=0
    g2: LineSegment StartX=-3.03109 StartY=-1.75 StartZ=0 EndX=-1e-16 EndY=-3.5 EndZ=0
    g3: LineSegment StartX=-1e-16 StartY=-3.5 StartZ=0 EndX=3.03109 EndY=-1.75 EndZ=0
    g4: LineSegment StartX=3.03109 StartY=-1.75 StartZ=0 EndX=3.03109 EndY=1.75 EndZ=0
    g5: LineSegment StartX=3.03109 StartY=1.75 StartZ=0 EndX=1e-16 EndY=3.5 EndZ=0
    g6: Circle [constr] CenterX=0 CenterY=0 CenterZ=0 NormalX=0 NormalY=0 NormalZ=1 AngleXU=0 Radius=3.5
    g7: LineSegment StartX=4.96892 StartY=-1.75002 StartZ=0 EndX=8.00002 EndY=-3.5 EndZ=0
    g8: LineSegment StartX=8.00002 StartY=-3.5 StartZ=0 EndX=11.0311 EndY=-1.74998 EndZ=0
    g9: LineSegment StartX=11.0311 StartY=-1.74998 StartZ=0 EndX=11.0311 EndY=1.75002 EndZ=0
    g10: LineSegment StartX=11.0311 StartY=1.75002 StartZ=0 EndX=7.99998 EndY=3.5 EndZ=0
    g11: LineSegment StartX=7.99998 StartY=3.5 StartZ=0 EndX=4.9689 EndY=1.74998 EndZ=0
    g12: LineSegment StartX=4.9689 StartY=1.74998 StartZ=0 EndX=4.96892 EndY=-1.75002 EndZ=0
    g13: Circle [constr] CenterX=8 CenterY=0 CenterZ=0 NormalX=0 NormalY=0 NormalZ=1 AngleXU=0 Radius=3.5
    g14: LineSegment StartX=4.03109 StartY=3.5 StartZ=0 EndX=7.06218 EndY=5.25 EndZ=0
    g15: LineSegment StartX=7.06218 StartY=5.25 StartZ=0 EndX=7.06218 EndY=8.75 EndZ=0
    g16: LineSegment StartX=7.06218 StartY=8.75 StartZ=0 EndX=4.03109 EndY=10.5 EndZ=0
    g17: LineSegment StartX=4.03109 StartY=10.5 StartZ=0 EndX=1 EndY=8.75 EndZ=0
    g18: LineSegment StartX=1 StartY=8.75 StartZ=0 EndX=1 EndY=5.25 EndZ=0
    g19: LineSegment StartX=1 StartY=5.25 StartZ=0 EndX=4.03109 EndY=3.5 EndZ=0
    g20: Circle [constr] CenterX=4.03109 CenterY=7 CenterZ=0 NormalX=0 NormalY=0 NormalZ=1 AngleXU=0 Radius=3.5
    g21: LineSegment StartX=-1 StartY=5.25 StartZ=0 EndX=-1 EndY=8.75 EndZ=0
    g22: LineSegment StartX=-1 StartY=8.75 StartZ=0 EndX=-4.03109 EndY=10.5 EndZ=0
    g23: LineSegment StartX=-4.03109 StartY=10.5 StartZ=0 EndX=-7.06218 EndY=8.75 EndZ=0
    g24: LineSegment StartX=-7.06218 StartY=8.75 StartZ=0 EndX=-7.06218 EndY=5.25 EndZ=0
    g25: LineSegment StartX=-7.06218 StartY=5.25 StartZ=0 EndX=-4.03109 EndY=3.5 EndZ=0
    g26: LineSegment StartX=-4.03109 StartY=3.5 StartZ=0 EndX=-1 EndY=5.25 EndZ=0
    g27: Circle [constr] CenterX=-4.03109 CenterY=7 CenterZ=0 NormalX=0 NormalY=0 NormalZ=1 AngleXU=0 Radius=3.5
    g28: LineSegment StartX=-4.96891 StartY=-1.75 StartZ=0 EndX=-4.96891 EndY=1.75 EndZ=0
    g29: LineSegment StartX=-4.96891 StartY=1.75 StartZ=0 EndX=-8 EndY=3.5 EndZ=0
    g30: LineSegment StartX=-8 StartY=3.5 StartZ=0 EndX=-11.0311 EndY=1.75 EndZ=0
    g31: LineSegment StartX=-11.0311 StartY=1.75 StartZ=0 EndX=-11.0311 EndY=-1.75 EndZ=0
    g32: LineSegment StartX=-11.0311 StartY=-1.75 StartZ=0 EndX=-8 EndY=-3.5 EndZ=0
    g33: LineSegment StartX=-8 StartY=-3.5 StartZ=0 EndX=-4.96891 EndY=-1.75 EndZ=0
    g34: Circle [constr] CenterX=-8 CenterY=0 CenterZ=0 NormalX=0 NormalY=0 NormalZ=1 AngleXU=0 Radius=3.5
    g35: LineSegment StartX=-4.03109 StartY=-3.5 StartZ=0 EndX=-7.06218 EndY=-5.25 EndZ=0
    g36: LineSegment StartX=-7.06218 StartY=-5.25 StartZ=0 EndX=-7.06218 EndY=-8.75 EndZ=0
    g37: LineSegment StartX=-7.06218 StartY=-8.75 StartZ=0 EndX=-4.03109 EndY=-10.5 EndZ=0
    g38: LineSegment StartX=-4.03109 StartY=-10.5 StartZ=0 EndX=-1 EndY=-8.75 EndZ=0
    g39: LineSegment StartX=-1 StartY=-8.75 StartZ=0 EndX=-1 EndY=-5.25 EndZ=0
    g40: LineSegment StartX=-1 StartY=-5.25 StartZ=0 EndX=-4.03109 EndY=-3.5 EndZ=0
    g41: Circle [constr] CenterX=-4.03109 CenterY=-7 CenterZ=0 NormalX=0 NormalY=0 NormalZ=1 AngleXU=0 Radius=3.5
    g42: LineSegment StartX=4.03109 StartY=-3.5 StartZ=0 EndX=1 EndY=-5.25 EndZ=0
    g43: LineSegment StartX=1 StartY=-5.25 StartZ=0 EndX=1 EndY=-8.75 EndZ=0
    g44: LineSegment StartX=1 StartY=-8.75 StartZ=0 EndX=4.03109 EndY=-10.5 EndZ=0
    g45: LineSegment StartX=4.03109 StartY=-10.5 StartZ=0 EndX=7.06218 EndY=-8.75 EndZ=0
    g46: LineSegment StartX=7.06218 StartY=-8.75 StartZ=0 EndX=7.06218 EndY=-5.25 EndZ=0
    g47: LineSegment StartX=7.06218 StartY=-5.25 StartZ=0 EndX=4.03109 EndY=-3.5 EndZ=0
    g48: Circle [constr] CenterX=4.03109 CenterY=-7 CenterZ=0 NormalX=0 NormalY=0 NormalZ=1 AngleXU=0 Radius=3.5
  constraints (117):
    c: Coincident(g0,g1)
    c: Coincident(g1,g2)
    c: Coincident(g2,g3)
    c: Coincident(g3,g4)
    c: Coincident(g4,g5)
    c: Coincident(g5,g0)
    c: Equal(g0, g1-g5) x5
    c: PointOnObject(g0,g6)
    c: PointOnObject(g1,g6)
    c: PointOnObject(g2,g6)
    c: PointOnObject(g3,g6)
    c: PointOnObject(g4,g6)
    c: PointOnObject(g5,g6)
    c: Coincident(g6,g-1)
    c: Diameter(g6) = 7
    c: PointOnObject(g0,g-2)
    c: Coincident(g7,g8)
    c: Coincident(g8,g9)
    c: Coincident(g9,g10)
    c: Coincident(g10,g11)
    c: Coincident(g11,g12)
    c: Coincident(g12,g7)
    c: Equal(g7, g8-g12) x5
    c: PointOnObject(g7,g13)
    c: PointOnObject(g8,g13)
    c: PointOnObject(g9,g13)
    c: PointOnObject(g10,g13)
    c: PointOnObject(g11,g13)
    c: PointOnObject(g12,g13)
    c: PointOnObject(g13,g-1)
    c: Diameter(g13) = 7
    c: Distance(g6,g13) = 8
    c: Horizontal(g0,g10)
    c: Coincident(g14,g15)
    c: Coincident(g15,g16)
    c: Coincident(g16,g17)
    c: Coincident(g17,g18)
    c: Coincident(g18,g19)
    c: Coincident(g19,g14)
    c: Equal(g14, g15-g19) x5
    c: PointOnObject(g14,g20)
    c: PointOnObject(g15,g20)
    c: PointOnObject(g16,g20)
    c: PointOnObject(g17,g20)
    c: PointOnObject(g18,g20)
    c: PointOnObject(g19,g20)
    c: Diameter(g20) = 7
    c: DistanceY(g-1,g20) = 7
    c: Vertical(g18)
    c: Distance(g17,g-2) = 1
    c: Coincident(g21,g22)
    c: Coincident(g22,g23)
    c: Coincident(g23,g24)
    c: Coincident(g24,g25)
    c: Coincident(g25,g26)
    c: Coincident(g26,g21)
    c: Equal(g21, g22-g26) x5
    c: PointOnObject(g21,g27)
    c: PointOnObject(g22,g27)
    c: PointOnObject(g23,g27)
    c: PointOnObject(g24,g27)
    c: PointOnObject(g25,g27)
    c: PointOnObject(g26,g27)
    c: Diameter(g27) = 7
    c: DistanceY(g-1,g27) = 7
    c: DistanceX(g21,g-1) = 1
    c: Vertical(g21)
    c: Coincident(g28,g29)
    c: Coincident(g29,g30)
    c: Coincident(g30,g31)
    c: Coincident(g31,g32)
    c: Coincident(g32,g33)
    c: Coincident(g33,g28)
    c: Equal(g28, g29-g33) x5
    c: PointOnObject(g28,g34)
    c: PointOnObject(g29,g34)
    c: PointOnObject(g30,g34)
    c: PointOnObject(g31,g34)
    c: PointOnObject(g32,g34)
    c: PointOnObject(g33,g34)
    c: PointOnObject(g34,g-1)
    c: Diameter(g34) = 7
    c: Vertical(g31)
    c: DistanceX(g34,g-1) = 8
    c: Coincident(g35,g36)
    c: Coincident(g36,g37)
    c: Coincident(g37,g38)
    c: Coincident(g38,g39)
    c: Coincident(g39,g40)
    c: Coincident(g40,g35)
    c: Equal(g35, g36-g40) x5
    c: PointOnObject(g35,g41)
    c: PointOnObject(g36,g41)
    c: PointOnObject(g37,g41)
    c: PointOnObject(g38,g41)
    c: PointOnObject(g39,g41)
    c: PointOnObject(g40,g41)
    c: Coincident(g42,g43)
    c: Coincident(g43,g44)
    c: Coincident(g44,g45)
    c: Coincident(g45,g46)
    c: Coincident(g46,g47)
    c: Coincident(g47,g42)
    c: Equal(g42, g43-g47) x5
    c: PointOnObject(g42,g48)
    c: PointOnObject(g43,g48)
    c: PointOnObject(g44,g48)
    c: PointOnObject(g45,g48)
    c: PointOnObject(g46,g48)
    c: PointOnObject(g47,g48)
    c: Equal(g41,g48)
    c: Diameter(g41) = 7
    c: Vertical(g39)
    c: Vertical(g43)
    c: Distance(g-2,g39) = 1
    c: Symmetric(g38,g43,g-2)
    c: Distance(g41,g-1) = 7
FEATURE [Part::Extrusion] Extrude507  label="hex122"
  Base = -> Sketch515
  Dir = (0,-1,2e-16)
  DirMode = 2
  FaceMakerClass = Part::FaceMakerBullseye
  FaceMakerMode = 3
  LengthFwd = 10
  LengthRev = 0
  Placement = pos=(-52,0,21) rot=(0,0,1;0rad)
  Solid = true
  Symmetric = false
FEATURE [Sketcher::SketchObject] Sketch516
  ArcFitTolerance = 1e-06
  FullyConstrained = true
  MakeInternals = false
  Placement = pos=(0,0,0) rot=(1,0,0;1.5708rad)
  sketch-geometry (49):
    g0: LineSegment StartX=1e-16 StartY=3.5 StartZ=0 EndX=-3.03109 EndY=1.75 EndZ=0
    g1: LineSegment StartX=-3.03109 StartY=1.75 StartZ=0 EndX=-3.03109 EndY=-1.75 EndZ=0
    g2: LineSegment StartX=-3.03109 StartY=-1.75 StartZ=0 EndX=-1e-16 EndY=-3.5 EndZ=0
    g3: LineSegment StartX=-1e-16 StartY=-3.5 StartZ=0 EndX=3.03109 EndY=-1.75 EndZ=0
    g4: LineSegment StartX=3.03109 StartY=-1.75 StartZ=0 EndX=3.03109 EndY=1.75 EndZ=0
    g5: LineSegment StartX=3.03109 StartY=1.75 StartZ=0 EndX=1e-16 EndY=3.5 EndZ=0
    g6: Circle [constr] CenterX=0 CenterY=0 CenterZ=0 NormalX=0 NormalY=0 NormalZ=1 AngleXU=0 Radius=3.5
    g7: LineSegment StartX=4.96892 StartY=-1.75002 StartZ=0 EndX=8.00002 EndY=-3.5 EndZ=0
    g8: LineSegment StartX=8.00002 StartY=-3.5 StartZ=0 EndX=11.0311 EndY=-1.74998 EndZ=0
    g9: LineSegment StartX=11.0311 StartY=-1.74998 StartZ=0 EndX=11.0311 EndY=1.75002 EndZ=0
    g10: LineSegment StartX=11.0311 StartY=1.75002 StartZ=0 EndX=7.99998 EndY=3.5 EndZ=0
    g11: LineSegment StartX=7.99998 StartY=3.5 StartZ=0 EndX=4.9689 EndY=1.74998 EndZ=0
    g12: LineSegment StartX=4.9689 StartY=1.74998 StartZ=0 EndX=4.96892 EndY=-1.75002 EndZ=0
    g13: Circle [constr] CenterX=8 CenterY=0 CenterZ=0 NormalX=0 NormalY=0 NormalZ=1 AngleXU=0 Radius=3.5
    g14: LineSegment StartX=4.03109 StartY=3.5 StartZ=0 EndX=7.06218 EndY=5.25 EndZ=0
    g15: LineSegment StartX=7.06218 StartY=5.25 StartZ=0 EndX=7.06218 EndY=8.75 EndZ=0
    g16: LineSegment StartX=7.06218 StartY=8.75 StartZ=0 EndX=4.03109 EndY=10.5 EndZ=0
    g17: LineSegment StartX=4.03109 StartY=10.5 StartZ=0 EndX=1 EndY=8.75 EndZ=0
    g18: LineSegment StartX=1 StartY=8.75 StartZ=0 EndX=1 EndY=5.25 EndZ=0
    g19: LineSegment StartX=1 StartY=5.25 StartZ=0 EndX=4.03109 EndY=3.5 EndZ=0
    g20: Circle [constr] CenterX=4.03109 CenterY=7 CenterZ=0 NormalX=0 NormalY=0 NormalZ=1 AngleXU=0 Radius=3.5
    g21: LineSegment StartX=-1 StartY=5.25 StartZ=0 EndX=-1 EndY=8.75 EndZ=0
    g22: LineSegment StartX=-1 StartY=8.75 StartZ=0 EndX=-4.03109 EndY=10.5 EndZ=0
    g23: LineSegment StartX=-4.03109 StartY=10.5 StartZ=0 EndX=-7.06218 EndY=8.75 EndZ=0
    g24: LineSegment StartX=-7.06218 StartY=8.75 StartZ=0 EndX=-7.06218 EndY=5.25 EndZ=0
    g25: LineSegment StartX=-7.06218 StartY=5.25 StartZ=0 EndX=-4.03109 EndY=3.5 EndZ=0
    g26: LineSegment StartX=-4.03109 StartY=3.5 StartZ=0 EndX=-1 EndY=5.25 EndZ=0
    g27: Circle [constr] CenterX=-4.03109 CenterY=7 CenterZ=0 NormalX=0 NormalY=0 NormalZ=1 AngleXU=0 Radius=3.5
    g28: LineSegment StartX=-4.96891 StartY=-1.75 StartZ=0 EndX=-4.96891 EndY=1.75 EndZ=0
    g29: LineSegment StartX=-4.96891 StartY=1.75 StartZ=0 EndX=-8 EndY=3.5 EndZ=0
    g30: LineSegment StartX=-8 StartY=3.5 StartZ=0 EndX=-11.0311 EndY=1.75 EndZ=0
    g31: LineSegment StartX=-11.0311 StartY=1.75 StartZ=0 EndX=-11.0311 EndY=-1.75 EndZ=0
    g32: LineSegment StartX=-11.0311 StartY=-1.75 StartZ=0 EndX=-8 EndY=-3.5 EndZ=0
    g33: LineSegment StartX=-8 StartY=-3.5 StartZ=0 EndX=-4.96891 EndY=-1.75 EndZ=0
    g34: Circle [constr] CenterX=-8 CenterY=0 CenterZ=0 NormalX=0 NormalY=0 NormalZ=1 AngleXU=0 Radius=3.5
    g35: LineSegment StartX=-4.03109 StartY=-3.5 StartZ=0 EndX=-7.06218 EndY=-5.25 EndZ=0
    g36: LineSegment StartX=-7.06218 StartY=-5.25 StartZ=0 EndX=-7.06218 EndY=-8.75 EndZ=0
    g37: LineSegment StartX=-7.06218 StartY=-8.75 StartZ=0 EndX=-4.03109 EndY=-10.5 EndZ=0
    g38: LineSegment StartX=-4.03109 StartY=-10.5 StartZ=0 EndX=-1 EndY=-8.75 EndZ=0
    g39: LineSegment StartX=-1 StartY=-8.75 StartZ=0 EndX=-1 EndY=-5.25 EndZ=0
    g40: LineSegment StartX=-1 StartY=-5.25 StartZ=0 EndX=-4.03109 EndY=-3.5 EndZ=0
    g41: Circle [constr] CenterX=-4.03109 CenterY=-7 CenterZ=0 NormalX=0 NormalY=0 NormalZ=1 AngleXU=0 Radius=3.5
    g42: LineSegment StartX=4.03109 StartY=-3.5 StartZ=0 EndX=1 EndY=-5.25 EndZ=0
    g43: LineSegment StartX=1 StartY=-5.25 StartZ=0 EndX=1 EndY=-8.75 EndZ=0
    g44: LineSegment StartX=1 StartY=-8.75 StartZ=0 EndX=4.03109 EndY=-10.5 EndZ=0
    g45: LineSegment StartX=4.03109 StartY=-10.5 StartZ=0 EndX=7.06218 EndY=-8.75 EndZ=0
    g46: LineSegment StartX=7.06218 StartY=-8.75 StartZ=0 EndX=7.06218 EndY=-5.25 EndZ=0
    g47: LineSegment StartX=7.06218 StartY=-5.25 StartZ=0 EndX=4.03109 EndY=-3.5 EndZ=0
    g48: Circle [constr] CenterX=4.03109 CenterY=-7 CenterZ=0 NormalX=0 NormalY=0 NormalZ=1 AngleXU=0 Radius=3.5
  constraints (117):
    c: Coincident(g0,g1)
    c: Coincident(g1,g2)
    c: Coincident(g2,g3)
    c: Coincident(g3,g4)
    c: Coincident(g4,g5)
    c: Coincident(g5,g0)
    c: Equal(g0, g1-g5) x5
    c: PointOnObject(g0,g6)
    c: PointOnObject(g1,g6)
    c: PointOnObject(g2,g6)
    c: PointOnObject(g3,g6)
    c: PointOnObject(g4,g6)
    c: PointOnObject(g5,g6)
    c: Coincident(g6,g-1)
    c: Diameter(g6) = 7
    c: PointOnObject(g0,g-2)
    c: Coincident(g7,g8)
    c: Coincident(g8,g9)
    c: Coincident(g9,g10)
    c: Coincident(g10,g11)
    c: Coincident(g11,g12)
    c: Coincident(g12,g7)
    c: Equal(g7, g8-g12) x5
    c: PointOnObject(g7,g13)
    c: PointOnObject(g8,g13)
    c: PointOnObject(g9,g13)
    c: PointOnObject(g10,g13)
    c: PointOnObject(g11,g13)
    c: PointOnObject(g12,g13)
    c: PointOnObject(g13,g-1)
    c: Diameter(g13) = 7
    c: Distance(g6,g13) = 8
    c: Horizontal(g0,g10)
    c: Coincident(g14,g15)
    c: Coincident(g15,g16)
    c: Coincident(g16,g17)
    c: Coincident(g17,g18)
    c: Coincident(g18,g19)
    c: Coincident(g19,g14)
    c: Equal(g14, g15-g19) x5
    c: PointOnObject(g14,g20)
    c: PointOnObject(g15,g20)
    c: PointOnObject(g16,g20)
    c: PointOnObject(g17,g20)
    c: PointOnObject(g18,g20)
    c: PointOnObject(g19,g20)
    c: Diameter(g20) = 7
    c: DistanceY(g-1,g20) = 7
    c: Vertical(g18)
    c: Distance(g17,g-2) = 1
    c: Coincident(g21,g22)
    c: Coincident(g22,g23)
    c: Coincident(g23,g24)
    c: Coincident(g24,g25)
    c: Coincident(g25,g26)
    c: Coincident(g26,g21)
    c: Equal(g21, g22-g26) x5
    c: PointOnObject(g21,g27)
    c: PointOnObject(g22,g27)
    c: PointOnObject(g23,g27)
    c: PointOnObject(g24,g27)
    c: PointOnObject(g25,g27)
    c: PointOnObject(g26,g27)
    c: Diameter(g27) = 7
    c: DistanceY(g-1,g27) = 7
    c: DistanceX(g21,g-1) = 1
    c: Vertical(g21)
    c: Coincident(g28,g29)
    c: Coincident(g29,g30)
    c: Coincident(g30,g31)
    c: Coincident(g31,g32)
    c: Coincident(g32,g33)
    c: Coincident(g33,g28)
    c: Equal(g28, g29-g33) x5
    c: PointOnObject(g28,g34)
    c: PointOnObject(g29,g34)
    c: PointOnObject(g30,g34)
    c: PointOnObject(g31,g34)
    c: PointOnObject(g32,g34)
    c: PointOnObject(g33,g34)
    c: PointOnObject(g34,g-1)
    c: Diameter(g34) = 7
    c: Vertical(g31)
    c: DistanceX(g34,g-1) = 8
    c: Coincident(g35,g36)
    c: Coincident(g36,g37)
    c: Coincident(g37,g38)
    c: Coincident(g38,g39)
    c: Coincident(g39,g40)
    c: Coincident(g40,g35)
    c: Equal(g35, g36-g40) x5
    c: PointOnObject(g35,g41)
    c: PointOnObject(g36,g41)
    c: PointOnObject(g37,g41)
    c: PointOnObject(g38,g41)
    c: PointOnObject(g39,g41)
    c: PointOnObject(g40,g41)
    c: Coincident(g42,g43)
    c: Coincident(g43,g44)
    c: Coincident(g44,g45)
    c: Coincident(g45,g46)
    c: Coincident(g46,g47)
    c: Coincident(g47,g42)
    c: Equal(g42, g43-g47) x5
    c: PointOnObject(g42,g48)
    c: PointOnObject(g43,g48)
    c: PointOnObject(g44,g48)
    c: PointOnObject(g45,g48)
    c: PointOnObject(g46,g48)
    c: PointOnObject(g47,g48)
    c: Equal(g41,g48)
    c: Diameter(g41) = 7
    c: Vertical(g39)
    c: Vertical(g43)
    c: Distance(g-2,g39) = 1
    c: Symmetric(g38,g43,g-2)
    c: Distance(g41,g-1) = 7
FEATURE [Part::Extrusion] Extrude508  label="hex123"
  Base = -> Sketch516
  Dir = (0,-1,2e-16)
  DirMode = 2
  FaceMakerClass = Part::FaceMakerBullseye
  FaceMakerMode = 3
  LengthFwd = 10
  LengthRev = 0
  Placement = pos=(52,0,21) rot=(0,0,1;0rad)
  Solid = true
  Symmetric = false
FEATURE [Sketcher::SketchObject] Sketch517
  ArcFitTolerance = 1e-06
  FullyConstrained = true
  MakeInternals = false
  Placement = pos=(0,0,0) rot=(1,0,0;1.5708rad)
  sketch-geometry (49):
    g0: LineSegment StartX=1e-16 StartY=3.5 StartZ=0 EndX=-3.03109 EndY=1.75 EndZ=0
    g1: LineSegment StartX=-3.03109 StartY=1.75 StartZ=0 EndX=-3.03109 EndY=-1.75 EndZ=0
    g2: LineSegment StartX=-3.03109 StartY=-1.75 StartZ=0 EndX=-1e-16 EndY=-3.5 EndZ=0
    g3: LineSegment StartX=-1e-16 StartY=-3.5 StartZ=0 EndX=3.03109 EndY=-1.75 EndZ=0
    g4: LineSegment StartX=3.03109 StartY=-1.75 StartZ=0 EndX=3.03109 EndY=1.75 EndZ=0
    g5: LineSegment StartX=3.03109 StartY=1.75 StartZ=0 EndX=1e-16 EndY=3.5 EndZ=0
    g6: Circle [constr] CenterX=0 CenterY=0 CenterZ=0 NormalX=0 NormalY=0 NormalZ=1 AngleXU=0 Radius=3.5
    g7: LineSegment StartX=4.96892 StartY=-1.75002 StartZ=0 EndX=8.00002 EndY=-3.5 EndZ=0
    g8: LineSegment StartX=8.00002 StartY=-3.5 StartZ=0 EndX=11.0311 EndY=-1.74998 EndZ=0
    g9: LineSegment StartX=11.0311 StartY=-1.74998 StartZ=0 EndX=11.0311 EndY=1.75002 EndZ=0
    g10: LineSegment StartX=11.0311 StartY=1.75002 StartZ=0 EndX=7.99998 EndY=3.5 EndZ=0
    g11: LineSegment StartX=7.99998 StartY=3.5 StartZ=0 EndX=4.9689 EndY=1.74998 EndZ=0
    g12: LineSegment StartX=4.9689 StartY=1.74998 StartZ=0 EndX=4.96892 EndY=-1.75002 EndZ=0
    g13: Circle [constr] CenterX=8 CenterY=0 CenterZ=0 NormalX=0 NormalY=0 NormalZ=1 AngleXU=0 Radius=3.5
    g14: LineSegment StartX=4.03109 StartY=3.5 StartZ=0 EndX=7.06218 EndY=5.25 EndZ=0
    g15: LineSegment StartX=7.06218 StartY=5.25 StartZ=0 EndX=7.06218 EndY=8.75 EndZ=0
    g16: LineSegment StartX=7.06218 StartY=8.75 StartZ=0 EndX=4.03109 EndY=10.5 EndZ=0
    g17: LineSegment StartX=4.03109 StartY=10.5 StartZ=0 EndX=1 EndY=8.75 EndZ=0
    g18: LineSegment StartX=1 StartY=8.75 StartZ=0 EndX=1 EndY=5.25 EndZ=0
    g19: LineSegment StartX=1 StartY=5.25 StartZ=0 EndX=4.03109 EndY=3.5 EndZ=0
    g20: Circle [constr] CenterX=4.03109 CenterY=7 CenterZ=0 NormalX=0 NormalY=0 NormalZ=1 AngleXU=0 Radius=3.5
    g21: LineSegment StartX=-1 StartY=5.25 StartZ=0 EndX=-1 EndY=8.75 EndZ=0
    g22: LineSegment StartX=-1 StartY=8.75 StartZ=0 EndX=-4.03109 EndY=10.5 EndZ=0
    g23: LineSegment StartX=-4.03109 StartY=10.5 StartZ=0 EndX=-7.06218 EndY=8.75 EndZ=0
    g24: LineSegment StartX=-7.06218 StartY=8.75 StartZ=0 EndX=-7.06218 EndY=5.25 EndZ=0
    g25: LineSegment StartX=-7.06218 StartY=5.25 StartZ=0 EndX=-4.03109 EndY=3.5 EndZ=0
    g26: LineSegment StartX=-4.03109 StartY=3.5 StartZ=0 EndX=-1 EndY=5.25 EndZ=0
    g27: Circle [constr] CenterX=-4.03109 CenterY=7 CenterZ=0 NormalX=0 NormalY=0 NormalZ=1 AngleXU=0 Radius=3.5
    g28: LineSegment StartX=-4.96891 StartY=-1.75 StartZ=0 EndX=-4.96891 EndY=1.75 EndZ=0
    g29: LineSegment StartX=-4.96891 StartY=1.75 StartZ=0 EndX=-8 EndY=3.5 EndZ=0
    g30: LineSegment StartX=-8 StartY=3.5 StartZ=0 EndX=-11.0311 EndY=1.75 EndZ=0
    g31: LineSegment StartX=-11.0311 StartY=1.75 StartZ=0 EndX=-11.0311 EndY=-1.75 EndZ=0
    g32: LineSegment StartX=-11.0311 StartY=-1.75 StartZ=0 EndX=-8 EndY=-3.5 EndZ=0
    g33: LineSegment StartX=-8 StartY=-3.5 StartZ=0 EndX=-4.96891 EndY=-1.75 EndZ=0
    g34: Circle [constr] CenterX=-8 CenterY=0 CenterZ=0 NormalX=0 NormalY=0 NormalZ=1 AngleXU=0 Radius=3.5
    g35: LineSegment StartX=-4.03109 StartY=-3.5 StartZ=0 EndX=-7.06218 EndY=-5.25 EndZ=0
    g36: LineSegment StartX=-7.06218 StartY=-5.25 StartZ=0 EndX=-7.06218 EndY=-8.75 EndZ=0
    g37: LineSegment StartX=-7.06218 StartY=-8.75 StartZ=0 EndX=-4.03109 EndY=-10.5 EndZ=0
    g38: LineSegment StartX=-4.03109 StartY=-10.5 StartZ=0 EndX=-1 EndY=-8.75 EndZ=0
    g39: LineSegment StartX=-1 StartY=-8.75 StartZ=0 EndX=-1 EndY=-5.25 EndZ=0
    g40: LineSegment StartX=-1 StartY=-5.25 StartZ=0 EndX=-4.03109 EndY=-3.5 EndZ=0
    g41: Circle [constr] CenterX=-4.03109 CenterY=-7 CenterZ=0 NormalX=0 NormalY=0 NormalZ=1 AngleXU=0 Radius=3.5
    g42: LineSegment StartX=4.03109 StartY=-3.5 StartZ=0 EndX=1 EndY=-5.25 EndZ=0
    g43: LineSegment StartX=1 StartY=-5.25 StartZ=0 EndX=1 EndY=-8.75 EndZ=0
    g44: LineSegment StartX=1 StartY=-8.75 StartZ=0 EndX=4.03109 EndY=-10.5 EndZ=0
    g45: LineSegment StartX=4.03109 StartY=-10.5 StartZ=0 EndX=7.06218 EndY=-8.75 EndZ=0
    g46: LineSegment StartX=7.06218 StartY=-8.75 StartZ=0 EndX=7.06218 EndY=-5.25 EndZ=0
    g47: LineSegment StartX=7.06218 StartY=-5.25 StartZ=0 EndX=4.03109 EndY=-3.5 EndZ=0
    g48: Circle [constr] CenterX=4.03109 CenterY=-7 CenterZ=0 NormalX=0 NormalY=0 NormalZ=1 AngleXU=0 Radius=3.5
  constraints (117):
    c: Coincident(g0,g1)
    c: Coincident(g1,g2)
    c: Coincident(g2,g3)
    c: Coincident(g3,g4)
    c: Coincident(g4,g5)
    c: Coincident(g5,g0)
    c: Equal(g0, g1-g5) x5
    c: PointOnObject(g0,g6)
    c: PointOnObject(g1,g6)
    c: PointOnObject(g2,g6)
    c: PointOnObject(g3,g6)
    c: PointOnObject(g4,g6)
    c: PointOnObject(g5,g6)
    c: Coincident(g6,g-1)
    c: Diameter(g6) = 7
    c: PointOnObject(g0,g-2)
    c: Coincident(g7,g8)
    c: Coincident(g8,g9)
    c: Coincident(g9,g10)
    c: Coincident(g10,g11)
    c: Coincident(g11,g12)
    c: Coincident(g12,g7)
    c: Equal(g7, g8-g12) x5
    c: PointOnObject(g7,g13)
    c: PointOnObject(g8,g13)
    c: PointOnObject(g9,g13)
    c: PointOnObject(g10,g13)
    c: PointOnObject(g11,g13)
    c: PointOnObject(g12,g13)
    c: PointOnObject(g13,g-1)
    c: Diameter(g13) = 7
    c: Distance(g6,g13) = 8
    c: Horizontal(g0,g10)
    c: Coincident(g14,g15)
    c: Coincident(g15,g16)
    c: Coincident(g16,g17)
    c: Coincident(g17,g18)
    c: Coincident(g18,g19)
    c: Coincident(g19,g14)
    c: Equal(g14, g15-g19) x5
    c: PointOnObject(g14,g20)
    c: PointOnObject(g15,g20)
    c: PointOnObject(g16,g20)
    c: PointOnObject(g17,g20)
    c: PointOnObject(g18,g20)
    c: PointOnObject(g19,g20)
    c: Diameter(g20) = 7
    c: DistanceY(g-1,g20) = 7
    c: Vertical(g18)
    c: Distance(g17,g-2) = 1
    c: Coincident(g21,g22)
    c: Coincident(g22,g23)
    c: Coincident(g23,g24)
    c: Coincident(g24,g25)
    c: Coincident(g25,g26)
    c: Coincident(g26,g21)
    c: Equal(g21, g22-g26) x5
    c: PointOnObject(g21,g27)
    c: PointOnObject(g22,g27)
    c: PointOnObject(g23,g27)
    c: PointOnObject(g24,g27)
    c: PointOnObject(g25,g27)
    c: PointOnObject(g26,g27)
    c: Diameter(g27) = 7
    c: DistanceY(g-1,g27) = 7
    c: DistanceX(g21,g-1) = 1
    c: Vertical(g21)
    c: Coincident(g28,g29)
    c: Coincident(g29,g30)
    c: Coincident(g30,g31)
    c: Coincident(g31,g32)
    c: Coincident(g32,g33)
    c: Coincident(g33,g28)
    c: Equal(g28, g29-g33) x5
    c: PointOnObject(g28,g34)
    c: PointOnObject(g29,g34)
    c: PointOnObject(g30,g34)
    c: PointOnObject(g31,g34)
    c: PointOnObject(g32,g34)
    c: PointOnObject(g33,g34)
    c: PointOnObject(g34,g-1)
    c: Diameter(g34) = 7
    c: Vertical(g31)
    c: DistanceX(g34,g-1) = 8
    c: Coincident(g35,g36)
    c: Coincident(g36,g37)
    c: Coincident(g37,g38)
    c: Coincident(g38,g39)
    c: Coincident(g39,g40)
    c: Coincident(g40,g35)
    c: Equal(g35, g36-g40) x5
    c: PointOnObject(g35,g41)
    c: PointOnObject(g36,g41)
    c: PointOnObject(g37,g41)
    c: PointOnObject(g38,g41)
    c: PointOnObject(g39,g41)
    c: PointOnObject(g40,g41)
    c: Coincident(g42,g43)
    c: Coincident(g43,g44)
    c: Coincident(g44,g45)
    c: Coincident(g45,g46)
    c: Coincident(g46,g47)
    c: Coincident(g47,g42)
    c: Equal(g42, g43-g47) x5
    c: PointOnObject(g42,g48)
    c: PointOnObject(g43,g48)
    c: PointOnObject(g44,g48)
    c: PointOnObject(g45,g48)
    c: PointOnObject(g46,g48)
    c: PointOnObject(g47,g48)
    c: Equal(g41,g48)
    c: Diameter(g41) = 7
    c: Vertical(g39)
    c: Vertical(g43)
    c: Distance(g-2,g39) = 1
    c: Symmetric(g38,g43,g-2)
    c: Distance(g41,g-1) = 7
FEATURE [Part::Extrusion] Extrude509  label="hex124"
  Base = -> Sketch517
  Dir = (0,-1,2e-16)
  DirMode = 2
  FaceMakerClass = Part::FaceMakerBullseye
  FaceMakerMode = 3
  LengthFwd = 10
  LengthRev = 0
  Placement = pos=(-32,0,28) rot=(0,0,1;0rad)
  Solid = true
  Symmetric = false
FEATURE [Sketcher::SketchObject] Sketch518
  ArcFitTolerance = 1e-06
  FullyConstrained = true
  MakeInternals = false
  Placement = pos=(0,0,0) rot=(1,0,0;1.5708rad)
  sketch-geometry (49):
    g0: LineSegment StartX=1e-16 StartY=3.5 StartZ=0 EndX=-3.03109 EndY=1.75 EndZ=0
    g1: LineSegment StartX=-3.03109 StartY=1.75 StartZ=0 EndX=-3.03109 EndY=-1.75 EndZ=0
    g2: LineSegment StartX=-3.03109 StartY=-1.75 StartZ=0 EndX=-1e-16 EndY=-3.5 EndZ=0
    g3: LineSegment StartX=-1e-16 StartY=-3.5 StartZ=0 EndX=3.03109 EndY=-1.75 EndZ=0
    g4: LineSegment StartX=3.03109 StartY=-1.75 StartZ=0 EndX=3.03109 EndY=1.75 EndZ=0
    g5: LineSegment StartX=3.03109 StartY=1.75 StartZ=0 EndX=1e-16 EndY=3.5 EndZ=0
    g6: Circle [constr] CenterX=0 CenterY=0 CenterZ=0 NormalX=0 NormalY=0 NormalZ=1 AngleXU=0 Radius=3.5
    g7: LineSegment StartX=4.96892 StartY=-1.75002 StartZ=0 EndX=8.00002 EndY=-3.5 EndZ=0
    g8: LineSegment StartX=8.00002 StartY=-3.5 StartZ=0 EndX=11.0311 EndY=-1.74998 EndZ=0
    g9: LineSegment StartX=11.0311 StartY=-1.74998 StartZ=0 EndX=11.0311 EndY=1.75002 EndZ=0
    g10: LineSegment StartX=11.0311 StartY=1.75002 StartZ=0 EndX=7.99998 EndY=3.5 EndZ=0
    g11: LineSegment StartX=7.99998 StartY=3.5 StartZ=0 EndX=4.9689 EndY=1.74998 EndZ=0
    g12: LineSegment StartX=4.9689 StartY=1.74998 StartZ=0 EndX=4.96892 EndY=-1.75002 EndZ=0
    g13: Circle [constr] CenterX=8 CenterY=0 CenterZ=0 NormalX=0 NormalY=0 NormalZ=1 AngleXU=0 Radius=3.5
    g14: LineSegment StartX=4.03109 StartY=3.5 StartZ=0 EndX=7.06218 EndY=5.25 EndZ=0
    g15: LineSegment StartX=7.06218 StartY=5.25 StartZ=0 EndX=7.06218 EndY=8.75 EndZ=0
    g16: LineSegment StartX=7.06218 StartY=8.75 StartZ=0 EndX=4.03109 EndY=10.5 EndZ=0
    g17: LineSegment StartX=4.03109 StartY=10.5 StartZ=0 EndX=1 EndY=8.75 EndZ=0
    g18: LineSegment StartX=1 StartY=8.75 StartZ=0 EndX=1 EndY=5.25 EndZ=0
    g19: LineSegment StartX=1 StartY=5.25 StartZ=0 EndX=4.03109 EndY=3.5 EndZ=0
    g20: Circle [constr] CenterX=4.03109 CenterY=7 CenterZ=0 NormalX=0 NormalY=0 NormalZ=1 AngleXU=0 Radius=3.5
    g21: LineSegment StartX=-1 StartY=5.25 StartZ=0 EndX=-1 EndY=8.75 EndZ=0
    g22: LineSegment StartX=-1 StartY=8.75 StartZ=0 EndX=-4.03109 EndY=10.5 EndZ=0
    g23: LineSegment StartX=-4.03109 StartY=10.5 StartZ=0 EndX=-7.06218 EndY=8.75 EndZ=0
    g24: LineSegment StartX=-7.06218 StartY=8.75 StartZ=0 EndX=-7.06218 EndY=5.25 EndZ=0
    g25: LineSegment StartX=-7.06218 StartY=5.25 StartZ=0 EndX=-4.03109 EndY=3.5 EndZ=0
    g26: LineSegment StartX=-4.03109 StartY=3.5 StartZ=0 EndX=-1 EndY=5.25 EndZ=0
    g27: Circle [constr] CenterX=-4.03109 CenterY=7 CenterZ=0 NormalX=0 NormalY=0 NormalZ=1 AngleXU=0 Radius=3.5
    g28: LineSegment StartX=-4.96891 StartY=-1.75 StartZ=0 EndX=-4.96891 EndY=1.75 EndZ=0
    g29: LineSegment StartX=-4.96891 StartY=1.75 StartZ=0 EndX=-8 EndY=3.5 EndZ=0
    g30: LineSegment StartX=-8 StartY=3.5 StartZ=0 EndX=-11.0311 EndY=1.75 EndZ=0
    g31: LineSegment StartX=-11.0311 StartY=1.75 StartZ=0 EndX=-11.0311 EndY=-1.75 EndZ=0
    g32: LineSegment StartX=-11.0311 StartY=-1.75 StartZ=0 EndX=-8 EndY=-3.5 EndZ=0
    g33: LineSegment StartX=-8 StartY=-3.5 StartZ=0 EndX=-4.96891 EndY=-1.75 EndZ=0
    g34: Circle [constr] CenterX=-8 CenterY=0 CenterZ=0 NormalX=0 NormalY=0 NormalZ=1 AngleXU=0 Radius=3.5
    g35: LineSegment StartX=-4.03109 StartY=-3.5 StartZ=0 EndX=-7.06218 EndY=-5.25 EndZ=0
    g36: LineSegment StartX=-7.06218 StartY=-5.25 StartZ=0 EndX=-7.06218 EndY=-8.75 EndZ=0
    g37: LineSegment StartX=-7.06218 StartY=-8.75 StartZ=0 EndX=-4.03109 EndY=-10.5 EndZ=0
    g38: LineSegment StartX=-4.03109 StartY=-10.5 StartZ=0 EndX=-1 EndY=-8.75 EndZ=0
    g39: LineSegment StartX=-1 StartY=-8.75 StartZ=0 EndX=-1 EndY=-5.25 EndZ=0
    g40: LineSegment StartX=-1 StartY=-5.25 StartZ=0 EndX=-4.03109 EndY=-3.5 EndZ=0
    g41: Circle [constr] CenterX=-4.03109 CenterY=-7 CenterZ=0 NormalX=0 NormalY=0 NormalZ=1 AngleXU=0 Radius=3.5
    g42: LineSegment StartX=4.03109 StartY=-3.5 StartZ=0 EndX=1 EndY=-5.25 EndZ=0
    g43: LineSegment StartX=1 StartY=-5.25 StartZ=0 EndX=1 EndY=-8.75 EndZ=0
    g44: LineSegment StartX=1 StartY=-8.75 StartZ=0 EndX=4.03109 EndY=-10.5 EndZ=0
    g45: LineSegment StartX=4.03109 StartY=-10.5 StartZ=0 EndX=7.06218 EndY=-8.75 EndZ=0
    g46: LineSegment StartX=7.06218 StartY=-8.75 StartZ=0 EndX=7.06218 EndY=-5.25 EndZ=0
    g47: LineSegment StartX=7.06218 StartY=-5.25 StartZ=0 EndX=4.03109 EndY=-3.5 EndZ=0
    g48: Circle [constr] CenterX=4.03109 CenterY=-7 CenterZ=0 NormalX=0 NormalY=0 NormalZ=1 AngleXU=0 Radius=3.5
  constraints (117):
    c: Coincident(g0,g1)
    c: Coincident(g1,g2)
    c: Coincident(g2,g3)
    c: Coincident(g3,g4)
    c: Coincident(g4,g5)
    c: Coincident(g5,g0)
    c: Equal(g0, g1-g5) x5
    c: PointOnObject(g0,g6)
    c: PointOnObject(g1,g6)
    c: PointOnObject(g2,g6)
    c: PointOnObject(g3,g6)
    c: PointOnObject(g4,g6)
    c: PointOnObject(g5,g6)
    c: Coincident(g6,g-1)
    c: Diameter(g6) = 7
    c: PointOnObject(g0,g-2)
    c: Coincident(g7,g8)
    c: Coincident(g8,g9)
    c: Coincident(g9,g10)
    c: Coincident(g10,g11)
    c: Coincident(g11,g12)
    c: Coincident(g12,g7)
    c: Equal(g7, g8-g12) x5
    c: PointOnObject(g7,g13)
    c: PointOnObject(g8,g13)
    c: PointOnObject(g9,g13)
    c: PointOnObject(g10,g13)
    c: PointOnObject(g11,g13)
    c: PointOnObject(g12,g13)
    c: PointOnObject(g13,g-1)
    c: Diameter(g13) = 7
    c: Distance(g6,g13) = 8
    c: Horizontal(g0,g10)
    c: Coincident(g14,g15)
    c: Coincident(g15,g16)
    c: Coincident(g16,g17)
    c: Coincident(g17,g18)
    c: Coincident(g18,g19)
    c: Coincident(g19,g14)
    c: Equal(g14, g15-g19) x5
    c: PointOnObject(g14,g20)
    c: PointOnObject(g15,g20)
    c: PointOnObject(g16,g20)
    c: PointOnObject(g17,g20)
    c: PointOnObject(g18,g20)
    c: PointOnObject(g19,g20)
    c: Diameter(g20) = 7
    c: DistanceY(g-1,g20) = 7
    c: Vertical(g18)
    c: Distance(g17,g-2) = 1
    c: Coincident(g21,g22)
    c: Coincident(g22,g23)
    c: Coincident(g23,g24)
    c: Coincident(g24,g25)
    c: Coincident(g25,g26)
    c: Coincident(g26,g21)
    c: Equal(g21, g22-g26) x5
    c: PointOnObject(g21,g27)
    c: PointOnObject(g22,g27)
    c: PointOnObject(g23,g27)
    c: PointOnObject(g24,g27)
    c: PointOnObject(g25,g27)
    c: PointOnObject(g26,g27)
    c: Diameter(g27) = 7
    c: DistanceY(g-1,g27) = 7
    c: DistanceX(g21,g-1) = 1
    c: Vertical(g21)
    c: Coincident(g28,g29)
    c: Coincident(g29,g30)
    c: Coincident(g30,g31)
    c: Coincident(g31,g32)
    c: Coincident(g32,g33)
    c: Coincident(g33,g28)
    c: Equal(g28, g29-g33) x5
    c: PointOnObject(g28,g34)
    c: PointOnObject(g29,g34)
    c: PointOnObject(g30,g34)
    c: PointOnObject(g31,g34)
    c: PointOnObject(g32,g34)
    c: PointOnObject(g33,g34)
    c: PointOnObject(g34,g-1)
    c: Diameter(g34) = 7
    c: Vertical(g31)
    c: DistanceX(g34,g-1) = 8
    c: Coincident(g35,g36)
    c: Coincident(g36,g37)
    c: Coincident(g37,g38)
    c: Coincident(g38,g39)
    c: Coincident(g39,g40)
    c: Coincident(g40,g35)
    c: Equal(g35, g36-g40) x5
    c: PointOnObject(g35,g41)
    c: PointOnObject(g36,g41)
    c: PointOnObject(g37,g41)
    c: PointOnObject(g38,g41)
    c: PointOnObject(g39,g41)
    c: PointOnObject(g40,g41)
    c: Coincident(g42,g43)
    c: Coincident(g43,g44)
    c: Coincident(g44,g45)
    c: Coincident(g45,g46)
    c: Coincident(g46,g47)
    c: Coincident(g47,g42)
    c: Equal(g42, g43-g47) x5
    c: PointOnObject(g42,g48)
    c: PointOnObject(g43,g48)
    c: PointOnObject(g44,g48)
    c: PointOnObject(g45,g48)
    c: PointOnObject(g46,g48)
    c: PointOnObject(g47,g48)
    c: Equal(g41,g48)
    c: Diameter(g41) = 7
    c: Vertical(g39)
    c: Vertical(g43)
    c: Distance(g-2,g39) = 1
    c: Symmetric(g38,g43,g-2)
    c: Distance(g41,g-1) = 7
FEATURE [Part::Extrusion] Extrude510  label="hex125"
  Base = -> Sketch518
  Dir = (0,-1,2e-16)
  DirMode = 2
  FaceMakerClass = Part::FaceMakerBullseye
  FaceMakerMode = 3
  LengthFwd = 10
  LengthRev = 0
  Placement = pos=(-12,0,35) rot=(0,0,1;0rad)
  Solid = true
  Symmetric = false
FEATURE [Sketcher::SketchObject] Sketch519
  ArcFitTolerance = 1e-06
  FullyConstrained = true
  MakeInternals = false
  Placement = pos=(0,0,0) rot=(1,0,0;1.5708rad)
  sketch-geometry (49):
    g0: LineSegment StartX=1e-16 StartY=3.5 StartZ=0 EndX=-3.03109 EndY=1.75 EndZ=0
    g1: LineSegment StartX=-3.03109 StartY=1.75 StartZ=0 EndX=-3.03109 EndY=-1.75 EndZ=0
    g2: LineSegment StartX=-3.03109 StartY=-1.75 StartZ=0 EndX=-1e-16 EndY=-3.5 EndZ=0
    g3: LineSegment StartX=-1e-16 StartY=-3.5 StartZ=0 EndX=3.03109 EndY=-1.75 EndZ=0
    g4: LineSegment StartX=3.03109 StartY=-1.75 StartZ=0 EndX=3.03109 EndY=1.75 EndZ=0
    g5: LineSegment StartX=3.03109 StartY=1.75 StartZ=0 EndX=1e-16 EndY=3.5 EndZ=0
    g6: Circle [constr] CenterX=0 CenterY=0 CenterZ=0 NormalX=0 NormalY=0 NormalZ=1 AngleXU=0 Radius=3.5
    g7: LineSegment StartX=4.96892 StartY=-1.75002 StartZ=0 EndX=8.00002 EndY=-3.5 EndZ=0
    g8: LineSegment StartX=8.00002 StartY=-3.5 StartZ=0 EndX=11.0311 EndY=-1.74998 EndZ=0
    g9: LineSegment StartX=11.0311 StartY=-1.74998 StartZ=0 EndX=11.0311 EndY=1.75002 EndZ=0
    g10: LineSegment StartX=11.0311 StartY=1.75002 StartZ=0 EndX=7.99998 EndY=3.5 EndZ=0
    g11: LineSegment StartX=7.99998 StartY=3.5 StartZ=0 EndX=4.9689 EndY=1.74998 EndZ=0
    g12: LineSegment StartX=4.9689 StartY=1.74998 StartZ=0 EndX=4.96892 EndY=-1.75002 EndZ=0
    g13: Circle [constr] CenterX=8 CenterY=0 CenterZ=0 NormalX=0 NormalY=0 NormalZ=1 AngleXU=0 Radius=3.5
    g14: LineSegment StartX=4.03109 StartY=3.5 StartZ=0 EndX=7.06218 EndY=5.25 EndZ=0
    g15: LineSegment StartX=7.06218 StartY=5.25 StartZ=0 EndX=7.06218 EndY=8.75 EndZ=0
    g16: LineSegment StartX=7.06218 StartY=8.75 StartZ=0 EndX=4.03109 EndY=10.5 EndZ=0
    g17: LineSegment StartX=4.03109 StartY=10.5 StartZ=0 EndX=1 EndY=8.75 EndZ=0
    g18: LineSegment StartX=1 StartY=8.75 StartZ=0 EndX=1 EndY=5.25 EndZ=0
    g19: LineSegment StartX=1 StartY=5.25 StartZ=0 EndX=4.03109 EndY=3.5 EndZ=0
    g20: Circle [constr] CenterX=4.03109 CenterY=7 CenterZ=0 NormalX=0 NormalY=0 NormalZ=1 AngleXU=0 Radius=3.5
    g21: LineSegment StartX=-1 StartY=5.25 StartZ=0 EndX=-1 EndY=8.75 EndZ=0
    g22: LineSegment StartX=-1 StartY=8.75 StartZ=0 EndX=-4.03109 EndY=10.5 EndZ=0
    g23: LineSegment StartX=-4.03109 StartY=10.5 StartZ=0 EndX=-7.06218 EndY=8.75 EndZ=0
    g24: LineSegment StartX=-7.06218 StartY=8.75 StartZ=0 EndX=-7.06218 EndY=5.25 EndZ=0
    g25: LineSegment StartX=-7.06218 StartY=5.25 StartZ=0 EndX=-4.03109 EndY=3.5 EndZ=0
    g26: LineSegment StartX=-4.03109 StartY=3.5 StartZ=0 EndX=-1 EndY=5.25 EndZ=0
    g27: Circle [constr] CenterX=-4.03109 CenterY=7 CenterZ=0 NormalX=0 NormalY=0 NormalZ=1 AngleXU=0 Radius=3.5
    g28: LineSegment StartX=-4.96891 StartY=-1.75 StartZ=0 EndX=-4.96891 EndY=1.75 EndZ=0
    g29: LineSegment StartX=-4.96891 StartY=1.75 StartZ=0 EndX=-8 EndY=3.5 EndZ=0
    g30: LineSegment StartX=-8 StartY=3.5 StartZ=0 EndX=-11.0311 EndY=1.75 EndZ=0
    g31: LineSegment StartX=-11.0311 StartY=1.75 StartZ=0 EndX=-11.0311 EndY=-1.75 EndZ=0
    g32: LineSegment StartX=-11.0311 StartY=-1.75 StartZ=0 EndX=-8 EndY=-3.5 EndZ=0
    g33: LineSegment StartX=-8 StartY=-3.5 StartZ=0 EndX=-4.96891 EndY=-1.75 EndZ=0
    g34: Circle [constr] CenterX=-8 CenterY=0 CenterZ=0 NormalX=0 NormalY=0 NormalZ=1 AngleXU=0 Radius=3.5
    g35: LineSegment StartX=-4.03109 StartY=-3.5 StartZ=0 EndX=-7.06218 EndY=-5.25 EndZ=0
    g36: LineSegment StartX=-7.06218 StartY=-5.25 StartZ=0 EndX=-7.06218 EndY=-8.75 EndZ=0
    g37: LineSegment StartX=-7.06218 StartY=-8.75 StartZ=0 EndX=-4.03109 EndY=-10.5 EndZ=0
    g38: LineSegment StartX=-4.03109 StartY=-10.5 StartZ=0 EndX=-1 EndY=-8.75 EndZ=0
    g39: LineSegment StartX=-1 StartY=-8.75 StartZ=0 EndX=-1 EndY=-5.25 EndZ=0
    g40: LineSegment StartX=-1 StartY=-5.25 StartZ=0 EndX=-4.03109 EndY=-3.5 EndZ=0
    g41: Circle [constr] CenterX=-4.03109 CenterY=-7 CenterZ=0 NormalX=0 NormalY=0 NormalZ=1 AngleXU=0 Radius=3.5
    g42: LineSegment StartX=4.03109 StartY=-3.5 StartZ=0 EndX=1 EndY=-5.25 EndZ=0
    g43: LineSegment StartX=1 StartY=-5.25 StartZ=0 EndX=1 EndY=-8.75 EndZ=0
    g44: LineSegment StartX=1 StartY=-8.75 StartZ=0 EndX=4.03109 EndY=-10.5 EndZ=0
    g45: LineSegment StartX=4.03109 StartY=-10.5 StartZ=0 EndX=7.06218 EndY=-8.75 EndZ=0
    g46: LineSegment StartX=7.06218 StartY=-8.75 StartZ=0 EndX=7.06218 EndY=-5.25 EndZ=0
    g47: LineSegment StartX=7.06218 StartY=-5.25 StartZ=0 EndX=4.03109 EndY=-3.5 EndZ=0
    g48: Circle [constr] CenterX=4.03109 CenterY=-7 CenterZ=0 NormalX=0 NormalY=0 NormalZ=1 AngleXU=0 Radius=3.5
  constraints (117):
    c: Coincident(g0,g1)
    c: Coincident(g1,g2)
    c: Coincident(g2,g3)
    c: Coincident(g3,g4)
    c: Coincident(g4,g5)
    c: Coincident(g5,g0)
    c: Equal(g0, g1-g5) x5
    c: PointOnObject(g0,g6)
    c: PointOnObject(g1,g6)
    c: PointOnObject(g2,g6)
    c: PointOnObject(g3,g6)
    c: PointOnObject(g4,g6)
    c: PointOnObject(g5,g6)
    c: Coincident(g6,g-1)
    c: Diameter(g6) = 7
    c: PointOnObject(g0,g-2)
    c: Coincident(g7,g8)
    c: Coincident(g8,g9)
    c: Coincident(g9,g10)
    c: Coincident(g10,g11)
    c: Coincident(g11,g12)
    c: Coincident(g12,g7)
    c: Equal(g7, g8-g12) x5
    c: PointOnObject(g7,g13)
    c: PointOnObject(g8,g13)
    c: PointOnObject(g9,g13)
    c: PointOnObject(g10,g13)
    c: PointOnObject(g11,g13)
    c: PointOnObject(g12,g13)
    c: PointOnObject(g13,g-1)
    c: Diameter(g13) = 7
    c: Distance(g6,g13) = 8
    c: Horizontal(g0,g10)
    c: Coincident(g14,g15)
    c: Coincident(g15,g16)
    c: Coincident(g16,g17)
    c: Coincident(g17,g18)
    c: Coincident(g18,g19)
    c: Coincident(g19,g14)
    c: Equal(g14, g15-g19) x5
    c: PointOnObject(g14,g20)
    c: PointOnObject(g15,g20)
    c: PointOnObject(g16,g20)
    c: PointOnObject(g17,g20)
    c: PointOnObject(g18,g20)
    c: PointOnObject(g19,g20)
    c: Diameter(g20) = 7
    c: DistanceY(g-1,g20) = 7
    c: Vertical(g18)
    c: Distance(g17,g-2) = 1
    c: Coincident(g21,g22)
    c: Coincident(g22,g23)
    c: Coincident(g23,g24)
    c: Coincident(g24,g25)
    c: Coincident(g25,g26)
    c: Coincident(g26,g21)
    c: Equal(g21, g22-g26) x5
    c: PointOnObject(g21,g27)
    c: PointOnObject(g22,g27)
    c: PointOnObject(g23,g27)
    c: PointOnObject(g24,g27)
    c: PointOnObject(g25,g27)
    c: PointOnObject(g26,g27)
    c: Diameter(g27) = 7
    c: DistanceY(g-1,g27) = 7
    c: DistanceX(g21,g-1) = 1
    c: Vertical(g21)
    c: Coincident(g28,g29)
    c: Coincident(g29,g30)
    c: Coincident(g30,g31)
    c: Coincident(g31,g32)
    c: Coincident(g32,g33)
    c: Coincident(g33,g28)
    c: Equal(g28, g29-g33) x5
    c: PointOnObject(g28,g34)
    c: PointOnObject(g29,g34)
    c: PointOnObject(g30,g34)
    c: PointOnObject(g31,g34)
    c: PointOnObject(g32,g34)
    c: PointOnObject(g33,g34)
    c: PointOnObject(g34,g-1)
    c: Diameter(g34) = 7
    c: Vertical(g31)
    c: DistanceX(g34,g-1) = 8
    c: Coincident(g35,g36)
    c: Coincident(g36,g37)
    c: Coincident(g37,g38)
    c: Coincident(g38,g39)
    c: Coincident(g39,g40)
    c: Coincident(g40,g35)
    c: Equal(g35, g36-g40) x5
    c: PointOnObject(g35,g41)
    c: PointOnObject(g36,g41)
    c: PointOnObject(g37,g41)
    c: PointOnObject(g38,g41)
    c: PointOnObject(g39,g41)
    c: PointOnObject(g40,g41)
    c: Coincident(g42,g43)
    c: Coincident(g43,g44)
    c: Coincident(g44,g45)
    c: Coincident(g45,g46)
    c: Coincident(g46,g47)
    c: Coincident(g47,g42)
    c: Equal(g42, g43-g47) x5
    c: PointOnObject(g42,g48)
    c: PointOnObject(g43,g48)
    c: PointOnObject(g44,g48)
    c: PointOnObject(g45,g48)
    c: PointOnObject(g46,g48)
    c: PointOnObject(g47,g48)
    c: Equal(g41,g48)
    c: Diameter(g41) = 7
    c: Vertical(g39)
    c: Vertical(g43)
    c: Distance(g-2,g39) = 1
    c: Symmetric(g38,g43,g-2)
    c: Distance(g41,g-1) = 7
FEATURE [Part::Extrusion] Extrude511  label="hex126"
  Base = -> Sketch519
  Dir = (0,-1,2e-16)
  DirMode = 2
  FaceMakerClass = Part::FaceMakerBullseye
  FaceMakerMode = 3
  LengthFwd = 10
  LengthRev = 0
  Placement = pos=(-80,0,0) rot=(0,0,1;0rad)
  Solid = true
  Symmetric = false
FEATURE [Sketcher::SketchObject] Sketch520
  ArcFitTolerance = 1e-06
  FullyConstrained = true
  MakeInternals = false
  Placement = pos=(0,0,0) rot=(1,0,0;1.5708rad)
  sketch-geometry (49):
    g0: LineSegment StartX=1e-16 StartY=3.5 StartZ=0 EndX=-3.03109 EndY=1.75 EndZ=0
    g1: LineSegment StartX=-3.03109 StartY=1.75 StartZ=0 EndX=-3.03109 EndY=-1.75 EndZ=0
    g2: LineSegment StartX=-3.03109 StartY=-1.75 StartZ=0 EndX=-1e-16 EndY=-3.5 EndZ=0
    g3: LineSegment StartX=-1e-16 StartY=-3.5 StartZ=0 EndX=3.03109 EndY=-1.75 EndZ=0
    g4: LineSegment StartX=3.03109 StartY=-1.75 StartZ=0 EndX=3.03109 EndY=1.75 EndZ=0
    g5: LineSegment StartX=3.03109 StartY=1.75 StartZ=0 EndX=1e-16 EndY=3.5 EndZ=0
    g6: Circle [constr] CenterX=0 CenterY=0 CenterZ=0 NormalX=0 NormalY=0 NormalZ=1 AngleXU=0 Radius=3.5
    g7: LineSegment StartX=4.96892 StartY=-1.75002 StartZ=0 EndX=8.00002 EndY=-3.5 EndZ=0
    g8: LineSegment StartX=8.00002 StartY=-3.5 StartZ=0 EndX=11.0311 EndY=-1.74998 EndZ=0
    g9: LineSegment StartX=11.0311 StartY=-1.74998 StartZ=0 EndX=11.0311 EndY=1.75002 EndZ=0
    g10: LineSegment StartX=11.0311 StartY=1.75002 StartZ=0 EndX=7.99998 EndY=3.5 EndZ=0
    g11: LineSegment StartX=7.99998 StartY=3.5 StartZ=0 EndX=4.9689 EndY=1.74998 EndZ=0
    g12: LineSegment StartX=4.9689 StartY=1.74998 StartZ=0 EndX=4.96892 EndY=-1.75002 EndZ=0
    g13: Circle [constr] CenterX=8 CenterY=0 CenterZ=0 NormalX=0 NormalY=0 NormalZ=1 AngleXU=0 Radius=3.5
    g14: LineSegment StartX=4.03109 StartY=3.5 StartZ=0 EndX=7.06218 EndY=5.25 EndZ=0
    g15: LineSegment StartX=7.06218 StartY=5.25 StartZ=0 EndX=7.06218 EndY=8.75 EndZ=0
    g16: LineSegment StartX=7.06218 StartY=8.75 StartZ=0 EndX=4.03109 EndY=10.5 EndZ=0
    g17: LineSegment StartX=4.03109 StartY=10.5 StartZ=0 EndX=1 EndY=8.75 EndZ=0
    g18: LineSegment StartX=1 StartY=8.75 StartZ=0 EndX=1 EndY=5.25 EndZ=0
    g19: LineSegment StartX=1 StartY=5.25 StartZ=0 EndX=4.03109 EndY=3.5 EndZ=0
    g20: Circle [constr] CenterX=4.03109 CenterY=7 CenterZ=0 NormalX=0 NormalY=0 NormalZ=1 AngleXU=0 Radius=3.5
    g21: LineSegment StartX=-1 StartY=5.25 StartZ=0 EndX=-1 EndY=8.75 EndZ=0
    g22: LineSegment StartX=-1 StartY=8.75 StartZ=0 EndX=-4.03109 EndY=10.5 EndZ=0
    g23: LineSegment StartX=-4.03109 StartY=10.5 StartZ=0 EndX=-7.06218 EndY=8.75 EndZ=0
    g24: LineSegment StartX=-7.06218 StartY=8.75 StartZ=0 EndX=-7.06218 EndY=5.25 EndZ=0
    g25: LineSegment StartX=-7.06218 StartY=5.25 StartZ=0 EndX=-4.03109 EndY=3.5 EndZ=0
    g26: LineSegment StartX=-4.03109 StartY=3.5 StartZ=0 EndX=-1 EndY=5.25 EndZ=0
    g27: Circle [constr] CenterX=-4.03109 CenterY=7 CenterZ=0 NormalX=0 NormalY=0 NormalZ=1 AngleXU=0 Radius=3.5
    g28: LineSegment StartX=-4.96891 StartY=-1.75 StartZ=0 EndX=-4.96891 EndY=1.75 EndZ=0
    g29: LineSegment StartX=-4.96891 StartY=1.75 StartZ=0 EndX=-8 EndY=3.5 EndZ=0
    g30: LineSegment StartX=-8 StartY=3.5 StartZ=0 EndX=-11.0311 EndY=1.75 EndZ=0
    g31: LineSegment StartX=-11.0311 StartY=1.75 StartZ=0 EndX=-11.0311 EndY=-1.75 EndZ=0
    g32: LineSegment StartX=-11.0311 StartY=-1.75 StartZ=0 EndX=-8 EndY=-3.5 EndZ=0
    g33: LineSegment StartX=-8 StartY=-3.5 StartZ=0 EndX=-4.96891 EndY=-1.75 EndZ=0
    g34: Circle [constr] CenterX=-8 CenterY=0 CenterZ=0 NormalX=0 NormalY=0 NormalZ=1 AngleXU=0 Radius=3.5
    g35: LineSegment StartX=-4.03109 StartY=-3.5 StartZ=0 EndX=-7.06218 EndY=-5.25 EndZ=0
    g36: LineSegment StartX=-7.06218 StartY=-5.25 StartZ=0 EndX=-7.06218 EndY=-8.75 EndZ=0
    g37: LineSegment StartX=-7.06218 StartY=-8.75 StartZ=0 EndX=-4.03109 EndY=-10.5 EndZ=0
    g38: LineSegment StartX=-4.03109 StartY=-10.5 StartZ=0 EndX=-1 EndY=-8.75 EndZ=0
    g39: LineSegment StartX=-1 StartY=-8.75 StartZ=0 EndX=-1 EndY=-5.25 EndZ=0
    g40: LineSegment StartX=-1 StartY=-5.25 StartZ=0 EndX=-4.03109 EndY=-3.5 EndZ=0
    g41: Circle [constr] CenterX=-4.03109 CenterY=-7 CenterZ=0 NormalX=0 NormalY=0 NormalZ=1 AngleXU=0 Radius=3.5
    g42: LineSegment StartX=4.03109 StartY=-3.5 StartZ=0 EndX=1 EndY=-5.25 EndZ=0
    g43: LineSegment StartX=1 StartY=-5.25 StartZ=0 EndX=1 EndY=-8.75 EndZ=0
    g44: LineSegment StartX=1 StartY=-8.75 StartZ=0 EndX=4.03109 EndY=-10.5 EndZ=0
    g45: LineSegment StartX=4.03109 StartY=-10.5 StartZ=0 EndX=7.06218 EndY=-8.75 EndZ=0
    g46: LineSegment StartX=7.06218 StartY=-8.75 StartZ=0 EndX=7.06218 EndY=-5.25 EndZ=0
    g47: LineSegment StartX=7.06218 StartY=-5.25 StartZ=0 EndX=4.03109 EndY=-3.5 EndZ=0
    g48: Circle [constr] CenterX=4.03109 CenterY=-7 CenterZ=0 NormalX=0 NormalY=0 NormalZ=1 AngleXU=0 Radius=3.5
  constraints (117):
    c: Coincident(g0,g1)
    c: Coincident(g1,g2)
    c: Coincident(g2,g3)
    c: Coincident(g3,g4)
    c: Coincident(g4,g5)
    c: Coincident(g5,g0)
    c: Equal(g0, g1-g5) x5
    c: PointOnObject(g0,g6)
    c: PointOnObject(g1,g6)
    c: PointOnObject(g2,g6)
    c: PointOnObject(g3,g6)
    c: PointOnObject(g4,g6)
    c: PointOnObject(g5,g6)
    c: Coincident(g6,g-1)
    c: Diameter(g6) = 7
    c: PointOnObject(g0,g-2)
    c: Coincident(g7,g8)
    c: Coincident(g8,g9)
    c: Coincident(g9,g10)
    c: Coincident(g10,g11)
    c: Coincident(g11,g12)
    c: Coincident(g12,g7)
    c: Equal(g7, g8-g12) x5
    c: PointOnObject(g7,g13)
    c: PointOnObject(g8,g13)
    c: PointOnObject(g9,g13)
    c: PointOnObject(g10,g13)
    c: PointOnObject(g11,g13)
    c: PointOnObject(g12,g13)
    c: PointOnObject(g13,g-1)
    c: Diameter(g13) = 7
    c: Distance(g6,g13) = 8
    c: Horizontal(g0,g10)
    c: Coincident(g14,g15)
    c: Coincident(g15,g16)
    c: Coincident(g16,g17)
    c: Coincident(g17,g18)
    c: Coincident(g18,g19)
    c: Coincident(g19,g14)
    c: Equal(g14, g15-g19) x5
    c: PointOnObject(g14,g20)
    c: PointOnObject(g15,g20)
    c: PointOnObject(g16,g20)
    c: PointOnObject(g17,g20)
    c: PointOnObject(g18,g20)
    c: PointOnObject(g19,g20)
    c: Diameter(g20) = 7
    c: DistanceY(g-1,g20) = 7
    c: Vertical(g18)
    c: Distance(g17,g-2) = 1
    c: Coincident(g21,g22)
    c: Coincident(g22,g23)
    c: Coincident(g23,g24)
    c: Coincident(g24,g25)
    c: Coincident(g25,g26)
    c: Coincident(g26,g21)
    c: Equal(g21, g22-g26) x5
    c: PointOnObject(g21,g27)
    c: PointOnObject(g22,g27)
    c: PointOnObject(g23,g27)
    c: PointOnObject(g24,g27)
    c: PointOnObject(g25,g27)
    c: PointOnObject(g26,g27)
    c: Diameter(g27) = 7
    c: DistanceY(g-1,g27) = 7
    c: DistanceX(g21,g-1) = 1
    c: Vertical(g21)
    c: Coincident(g28,g29)
    c: Coincident(g29,g30)
    c: Coincident(g30,g31)
    c: Coincident(g31,g32)
    c: Coincident(g32,g33)
    c: Coincident(g33,g28)
    c: Equal(g28, g29-g33) x5
    c: PointOnObject(g28,g34)
    c: PointOnObject(g29,g34)
    c: PointOnObject(g30,g34)
    c: PointOnObject(g31,g34)
    c: PointOnObject(g32,g34)
    c: PointOnObject(g33,g34)
    c: PointOnObject(g34,g-1)
    c: Diameter(g34) = 7
    c: Vertical(g31)
    c: DistanceX(g34,g-1) = 8
    c: Coincident(g35,g36)
    c: Coincident(g36,g37)
    c: Coincident(g37,g38)
    c: Coincident(g38,g39)
    c: Coincident(g39,g40)
    c: Coincident(g40,g35)
    c: Equal(g35, g36-g40) x5
    c: PointOnObject(g35,g41)
    c: PointOnObject(g36,g41)
    c: PointOnObject(g37,g41)
    c: PointOnObject(g38,g41)
    c: PointOnObject(g39,g41)
    c: PointOnObject(g40,g41)
    c: Coincident(g42,g43)
    c: Coincident(g43,g44)
    c: Coincident(g44,g45)
    c: Coincident(g45,g46)
    c: Coincident(g46,g47)
    c: Coincident(g47,g42)
    c: Equal(g42, g43-g47) x5
    c: PointOnObject(g42,g48)
    c: PointOnObject(g43,g48)
    c: PointOnObject(g44,g48)
    c: PointOnObject(g45,g48)
    c: PointOnObject(g46,g48)
    c: PointOnObject(g47,g48)
    c: Equal(g41,g48)
    c: Diameter(g41) = 7
    c: Vertical(g39)
    c: Vertical(g43)
    c: Distance(g-2,g39) = 1
    c: Symmetric(g38,g43,g-2)
    c: Distance(g41,g-1) = 7
FEATURE [Part::Extrusion] Extrude512  label="hex127"
  Base = -> Sketch520
  Dir = (0,-1,2e-16)
  DirMode = 2
  FaceMakerClass = Part::FaceMakerBullseye
  FaceMakerMode = 3
  LengthFwd = 10
  LengthRev = 0
  Placement = pos=(-104,0,0) rot=(0,0,1;0rad)
  Solid = true
  Symmetric = false
FEATURE [Sketcher::SketchObject] Sketch521
  ArcFitTolerance = 1e-06
  FullyConstrained = true
  MakeInternals = false
  Placement = pos=(0,0,0) rot=(1,0,0;1.5708rad)
  sketch-geometry (49):
    g0: LineSegment StartX=1e-16 StartY=3.5 StartZ=0 EndX=-3.03109 EndY=1.75 EndZ=0
    g1: LineSegment StartX=-3.03109 StartY=1.75 StartZ=0 EndX=-3.03109 EndY=-1.75 EndZ=0
    g2: LineSegment StartX=-3.03109 StartY=-1.75 StartZ=0 EndX=-1e-16 EndY=-3.5 EndZ=0
    g3: LineSegment StartX=-1e-16 StartY=-3.5 StartZ=0 EndX=3.03109 EndY=-1.75 EndZ=0
    g4: LineSegment StartX=3.03109 StartY=-1.75 StartZ=0 EndX=3.03109 EndY=1.75 EndZ=0
    g5: LineSegment StartX=3.03109 StartY=1.75 StartZ=0 EndX=1e-16 EndY=3.5 EndZ=0
    g6: Circle [constr] CenterX=0 CenterY=0 CenterZ=0 NormalX=0 NormalY=0 NormalZ=1 AngleXU=0 Radius=3.5
    g7: LineSegment StartX=4.96892 StartY=-1.75002 StartZ=0 EndX=8.00002 EndY=-3.5 EndZ=0
    g8: LineSegment StartX=8.00002 StartY=-3.5 StartZ=0 EndX=11.0311 EndY=-1.74998 EndZ=0
    g9: LineSegment StartX=11.0311 StartY=-1.74998 StartZ=0 EndX=11.0311 EndY=1.75002 EndZ=0
    g10: LineSegment StartX=11.0311 StartY=1.75002 StartZ=0 EndX=7.99998 EndY=3.5 EndZ=0
    g11: LineSegment StartX=7.99998 StartY=3.5 StartZ=0 EndX=4.9689 EndY=1.74998 EndZ=0
    g12: LineSegment StartX=4.9689 StartY=1.74998 StartZ=0 EndX=4.96892 EndY=-1.75002 EndZ=0
    g13: Circle [constr] CenterX=8 CenterY=0 CenterZ=0 NormalX=0 NormalY=0 NormalZ=1 AngleXU=0 Radius=3.5
    g14: LineSegment StartX=4.03109 StartY=3.5 StartZ=0 EndX=7.06218 EndY=5.25 EndZ=0
    g15: LineSegment StartX=7.06218 StartY=5.25 StartZ=0 EndX=7.06218 EndY=8.75 EndZ=0
    g16: LineSegment StartX=7.06218 StartY=8.75 StartZ=0 EndX=4.03109 EndY=10.5 EndZ=0
    g17: LineSegment StartX=4.03109 StartY=10.5 StartZ=0 EndX=1 EndY=8.75 EndZ=0
    g18: LineSegment StartX=1 StartY=8.75 StartZ=0 EndX=1 EndY=5.25 EndZ=0
    g19: LineSegment StartX=1 StartY=5.25 StartZ=0 EndX=4.03109 EndY=3.5 EndZ=0
    g20: Circle [constr] CenterX=4.03109 CenterY=7 CenterZ=0 NormalX=0 NormalY=0 NormalZ=1 AngleXU=0 Radius=3.5
    g21: LineSegment StartX=-1 StartY=5.25 StartZ=0 EndX=-1 EndY=8.75 EndZ=0
    g22: LineSegment StartX=-1 StartY=8.75 StartZ=0 EndX=-4.03109 EndY=10.5 EndZ=0
    g23: LineSegment StartX=-4.03109 StartY=10.5 StartZ=0 EndX=-7.06218 EndY=8.75 EndZ=0
    g24: LineSegment StartX=-7.06218 StartY=8.75 StartZ=0 EndX=-7.06218 EndY=5.25 EndZ=0
    g25: LineSegment StartX=-7.06218 StartY=5.25 StartZ=0 EndX=-4.03109 EndY=3.5 EndZ=0
    g26: LineSegment StartX=-4.03109 StartY=3.5 StartZ=0 EndX=-1 EndY=5.25 EndZ=0
    g27: Circle [constr] CenterX=-4.03109 CenterY=7 CenterZ=0 NormalX=0 NormalY=0 NormalZ=1 AngleXU=0 Radius=3.5
    g28: LineSegment StartX=-4.96891 StartY=-1.75 StartZ=0 EndX=-4.96891 EndY=1.75 EndZ=0
    g29: LineSegment StartX=-4.96891 StartY=1.75 StartZ=0 EndX=-8 EndY=3.5 EndZ=0
    g30: LineSegment StartX=-8 StartY=3.5 StartZ=0 EndX=-11.0311 EndY=1.75 EndZ=0
    g31: LineSegment StartX=-11.0311 StartY=1.75 StartZ=0 EndX=-11.0311 EndY=-1.75 EndZ=0
    g32: LineSegment StartX=-11.0311 StartY=-1.75 StartZ=0 EndX=-8 EndY=-3.5 EndZ=0
    g33: LineSegment StartX=-8 StartY=-3.5 StartZ=0 EndX=-4.96891 EndY=-1.75 EndZ=0
    g34: Circle [constr] CenterX=-8 CenterY=0 CenterZ=0 NormalX=0 NormalY=0 NormalZ=1 AngleXU=0 Radius=3.5
    g35: LineSegment StartX=-4.03109 StartY=-3.5 StartZ=0 EndX=-7.06218 EndY=-5.25 EndZ=0
    g36: LineSegment StartX=-7.06218 StartY=-5.25 StartZ=0 EndX=-7.06218 EndY=-8.75 EndZ=0
    g37: LineSegment StartX=-7.06218 StartY=-8.75 StartZ=0 EndX=-4.03109 EndY=-10.5 EndZ=0
    g38: LineSegment StartX=-4.03109 StartY=-10.5 StartZ=0 EndX=-1 EndY=-8.75 EndZ=0
    g39: LineSegment StartX=-1 StartY=-8.75 StartZ=0 EndX=-1 EndY=-5.25 EndZ=0
    g40: LineSegment StartX=-1 StartY=-5.25 StartZ=0 EndX=-4.03109 EndY=-3.5 EndZ=0
    g41: Circle [constr] CenterX=-4.03109 CenterY=-7 CenterZ=0 NormalX=0 NormalY=0 NormalZ=1 AngleXU=0 Radius=3.5
    g42: LineSegment StartX=4.03109 StartY=-3.5 StartZ=0 EndX=1 EndY=-5.25 EndZ=0
    g43: LineSegment StartX=1 StartY=-5.25 StartZ=0 EndX=1 EndY=-8.75 EndZ=0
    g44: LineSegment StartX=1 StartY=-8.75 StartZ=0 EndX=4.03109 EndY=-10.5 EndZ=0
    g45: LineSegment StartX=4.03109 StartY=-10.5 StartZ=0 EndX=7.06218 EndY=-8.75 EndZ=0
    g46: LineSegment StartX=7.06218 StartY=-8.75 StartZ=0 EndX=7.06218 EndY=-5.25 EndZ=0
    g47: LineSegment StartX=7.06218 StartY=-5.25 StartZ=0 EndX=4.03109 EndY=-3.5 EndZ=0
    g48: Circle [constr] CenterX=4.03109 CenterY=-7 CenterZ=0 NormalX=0 NormalY=0 NormalZ=1 AngleXU=0 Radius=3.5
  constraints (117):
    c: Coincident(g0,g1)
    c: Coincident(g1,g2)
    c: Coincident(g2,g3)
    c: Coincident(g3,g4)
    c: Coincident(g4,g5)
    c: Coincident(g5,g0)
    c: Equal(g0, g1-g5) x5
    c: PointOnObject(g0,g6)
    c: PointOnObject(g1,g6)
    c: PointOnObject(g2,g6)
    c: PointOnObject(g3,g6)
    c: PointOnObject(g4,g6)
    c: PointOnObject(g5,g6)
    c: Coincident(g6,g-1)
    c: Diameter(g6) = 7
    c: PointOnObject(g0,g-2)
    c: Coincident(g7,g8)
    c: Coincident(g8,g9)
    c: Coincident(g9,g10)
    c: Coincident(g10,g11)
    c: Coincident(g11,g12)
    c: Coincident(g12,g7)
    c: Equal(g7, g8-g12) x5
    c: PointOnObject(g7,g13)
    c: PointOnObject(g8,g13)
    c: PointOnObject(g9,g13)
    c: PointOnObject(g10,g13)
    c: PointOnObject(g11,g13)
    c: PointOnObject(g12,g13)
    c: PointOnObject(g13,g-1)
    c: Diameter(g13) = 7
    c: Distance(g6,g13) = 8
    c: Horizontal(g0,g10)
    c: Coincident(g14,g15)
    c: Coincident(g15,g16)
    c: Coincident(g16,g17)
    c: Coincident(g17,g18)
    c: Coincident(g18,g19)
    c: Coincident(g19,g14)
    c: Equal(g14, g15-g19) x5
    c: PointOnObject(g14,g20)
    c: PointOnObject(g15,g20)
    c: PointOnObject(g16,g20)
    c: PointOnObject(g17,g20)
    c: PointOnObject(g18,g20)
    c: PointOnObject(g19,g20)
    c: Diameter(g20) = 7
    c: DistanceY(g-1,g20) = 7
    c: Vertical(g18)
    c: Distance(g17,g-2) = 1
    c: Coincident(g21,g22)
    c: Coincident(g22,g23)
    c: Coincident(g23,g24)
    c: Coincident(g24,g25)
    c: Coincident(g25,g26)
    c: Coincident(g26,g21)
    c: Equal(g21, g22-g26) x5
    c: PointOnObject(g21,g27)
    c: PointOnObject(g22,g27)
    c: PointOnObject(g23,g27)
    c: PointOnObject(g24,g27)
    c: PointOnObject(g25,g27)
    c: PointOnObject(g26,g27)
    c: Diameter(g27) = 7
    c: DistanceY(g-1,g27) = 7
    c: DistanceX(g21,g-1) = 1
    c: Vertical(g21)
    c: Coincident(g28,g29)
    c: Coincident(g29,g30)
    c: Coincident(g30,g31)
    c: Coincident(g31,g32)
    c: Coincident(g32,g33)
    c: Coincident(g33,g28)
    c: Equal(g28, g29-g33) x5
    c: PointOnObject(g28,g34)
    c: PointOnObject(g29,g34)
    c: PointOnObject(g30,g34)
    c: PointOnObject(g31,g34)
    c: PointOnObject(g32,g34)
    c: PointOnObject(g33,g34)
    c: PointOnObject(g34,g-1)
    c: Diameter(g34) = 7
    c: Vertical(g31)
    c: DistanceX(g34,g-1) = 8
    c: Coincident(g35,g36)
    c: Coincident(g36,g37)
    c: Coincident(g37,g38)
    c: Coincident(g38,g39)
    c: Coincident(g39,g40)
    c: Coincident(g40,g35)
    c: Equal(g35, g36-g40) x5
    c: PointOnObject(g35,g41)
    c: PointOnObject(g36,g41)
    c: PointOnObject(g37,g41)
    c: PointOnObject(g38,g41)
    c: PointOnObject(g39,g41)
    c: PointOnObject(g40,g41)
    c: Coincident(g42,g43)
    c: Coincident(g43,g44)
    c: Coincident(g44,g45)
    c: Coincident(g45,g46)
    c: Coincident(g46,g47)
    c: Coincident(g47,g42)
    c: Equal(g42, g43-g47) x5
    c: PointOnObject(g42,g48)
    c: PointOnObject(g43,g48)
    c: PointOnObject(g44,g48)
    c: PointOnObject(g45,g48)
    c: PointOnObject(g46,g48)
    c: PointOnObject(g47,g48)
    c: Equal(g41,g48)
    c: Diameter(g41) = 7
    c: Vertical(g39)
    c: Vertical(g43)
    c: Distance(g-2,g39) = 1
    c: Symmetric(g38,g43,g-2)
    c: Distance(g41,g-1) = 7
FEATURE [Part::Extrusion] Extrude513  label="hex128"
  Base = -> Sketch521
  Dir = (0,-1,2e-16)
  DirMode = 2
  FaceMakerClass = Part::FaceMakerBullseye
  FaceMakerMode = 3
  LengthFwd = 10
  LengthRev = 0
  Placement = pos=(-64,0,14) rot=(0,0,1;0rad)
  Solid = true
  Symmetric = false
FEATURE [Sketcher::SketchObject] Sketch522
  ArcFitTolerance = 1e-06
  FullyConstrained = true
  MakeInternals = false
  Placement = pos=(0,0,0) rot=(1,0,0;1.5708rad)
  sketch-geometry (49):
    g0: LineSegment StartX=1e-16 StartY=3.5 StartZ=0 EndX=-3.03109 EndY=1.75 EndZ=0
    g1: LineSegment StartX=-3.03109 StartY=1.75 StartZ=0 EndX=-3.03109 EndY=-1.75 EndZ=0
    g2: LineSegment StartX=-3.03109 StartY=-1.75 StartZ=0 EndX=-1e-16 EndY=-3.5 EndZ=0
    g3: LineSegment StartX=-1e-16 StartY=-3.5 StartZ=0 EndX=3.03109 EndY=-1.75 EndZ=0
    g4: LineSegment StartX=3.03109 StartY=-1.75 StartZ=0 EndX=3.03109 EndY=1.75 EndZ=0
    g5: LineSegment StartX=3.03109 StartY=1.75 StartZ=0 EndX=1e-16 EndY=3.5 EndZ=0
    g6: Circle [constr] CenterX=0 CenterY=0 CenterZ=0 NormalX=0 NormalY=0 NormalZ=1 AngleXU=0 Radius=3.5
    g7: LineSegment StartX=4.96892 StartY=-1.75002 StartZ=0 EndX=8.00002 EndY=-3.5 EndZ=0
    g8: LineSegment StartX=8.00002 StartY=-3.5 StartZ=0 EndX=11.0311 EndY=-1.74998 EndZ=0
    g9: LineSegment StartX=11.0311 StartY=-1.74998 StartZ=0 EndX=11.0311 EndY=1.75002 EndZ=0
    g10: LineSegment StartX=11.0311 StartY=1.75002 StartZ=0 EndX=7.99998 EndY=3.5 EndZ=0
    g11: LineSegment StartX=7.99998 StartY=3.5 StartZ=0 EndX=4.9689 EndY=1.74998 EndZ=0
    g12: LineSegment StartX=4.9689 StartY=1.74998 StartZ=0 EndX=4.96892 EndY=-1.75002 EndZ=0
    g13: Circle [constr] CenterX=8 CenterY=0 CenterZ=0 NormalX=0 NormalY=0 NormalZ=1 AngleXU=0 Radius=3.5
    g14: LineSegment StartX=4.03109 StartY=3.5 StartZ=0 EndX=7.06218 EndY=5.25 EndZ=0
    g15: LineSegment StartX=7.06218 StartY=5.25 StartZ=0 EndX=7.06218 EndY=8.75 EndZ=0
    g16: LineSegment StartX=7.06218 StartY=8.75 StartZ=0 EndX=4.03109 EndY=10.5 EndZ=0
    g17: LineSegment StartX=4.03109 StartY=10.5 StartZ=0 EndX=1 EndY=8.75 EndZ=0
    g18: LineSegment StartX=1 StartY=8.75 StartZ=0 EndX=1 EndY=5.25 EndZ=0
    g19: LineSegment StartX=1 StartY=5.25 StartZ=0 EndX=4.03109 EndY=3.5 EndZ=0
    g20: Circle [constr] CenterX=4.03109 CenterY=7 CenterZ=0 NormalX=0 NormalY=0 NormalZ=1 AngleXU=0 Radius=3.5
    g21: LineSegment StartX=-1 StartY=5.25 StartZ=0 EndX=-1 EndY=8.75 EndZ=0
    g22: LineSegment StartX=-1 StartY=8.75 StartZ=0 EndX=-4.03109 EndY=10.5 EndZ=0
    g23: LineSegment StartX=-4.03109 StartY=10.5 StartZ=0 EndX=-7.06218 EndY=8.75 EndZ=0
    g24: LineSegment StartX=-7.06218 StartY=8.75 StartZ=0 EndX=-7.06218 EndY=5.25 EndZ=0
    g25: LineSegment StartX=-7.06218 StartY=5.25 StartZ=0 EndX=-4.03109 EndY=3.5 EndZ=0
    g26: LineSegment StartX=-4.03109 StartY=3.5 StartZ=0 EndX=-1 EndY=5.25 EndZ=0
    g27: Circle [constr] CenterX=-4.03109 CenterY=7 CenterZ=0 NormalX=0 NormalY=0 NormalZ=1 AngleXU=0 Radius=3.5
    g28: LineSegment StartX=-4.96891 StartY=-1.75 StartZ=0 EndX=-4.96891 EndY=1.75 EndZ=0
    g29: LineSegment StartX=-4.96891 StartY=1.75 StartZ=0 EndX=-8 EndY=3.5 EndZ=0
    g30: LineSegment StartX=-8 StartY=3.5 StartZ=0 EndX=-11.0311 EndY=1.75 EndZ=0
    g31: LineSegment StartX=-11.0311 StartY=1.75 StartZ=0 EndX=-11.0311 EndY=-1.75 EndZ=0
    g32: LineSegment StartX=-11.0311 StartY=-1.75 StartZ=0 EndX=-8 EndY=-3.5 EndZ=0
    g33: LineSegment StartX=-8 StartY=-3.5 StartZ=0 EndX=-4.96891 EndY=-1.75 EndZ=0
    g34: Circle [constr] CenterX=-8 CenterY=0 CenterZ=0 NormalX=0 NormalY=0 NormalZ=1 AngleXU=0 Radius=3.5
    g35: LineSegment StartX=-4.03109 StartY=-3.5 StartZ=0 EndX=-7.06218 EndY=-5.25 EndZ=0
    g36: LineSegment StartX=-7.06218 StartY=-5.25 StartZ=0 EndX=-7.06218 EndY=-8.75 EndZ=0
    g37: LineSegment StartX=-7.06218 StartY=-8.75 StartZ=0 EndX=-4.03109 EndY=-10.5 EndZ=0
    g38: LineSegment StartX=-4.03109 StartY=-10.5 StartZ=0 EndX=-1 EndY=-8.75 EndZ=0
    g39: LineSegment StartX=-1 StartY=-8.75 StartZ=0 EndX=-1 EndY=-5.25 EndZ=0
    g40: LineSegment StartX=-1 StartY=-5.25 StartZ=0 EndX=-4.03109 EndY=-3.5 EndZ=0
    g41: Circle [constr] CenterX=-4.03109 CenterY=-7 CenterZ=0 NormalX=0 NormalY=0 NormalZ=1 AngleXU=0 Radius=3.5
    g42: LineSegment StartX=4.03109 StartY=-3.5 StartZ=0 EndX=1 EndY=-5.25 EndZ=0
    g43: LineSegment StartX=1 StartY=-5.25 StartZ=0 EndX=1 EndY=-8.75 EndZ=0
    g44: LineSegment StartX=1 StartY=-8.75 StartZ=0 EndX=4.03109 EndY=-10.5 EndZ=0
    g45: LineSegment StartX=4.03109 StartY=-10.5 StartZ=0 EndX=7.06218 EndY=-8.75 EndZ=0
    g46: LineSegment StartX=7.06218 StartY=-8.75 StartZ=0 EndX=7.06218 EndY=-5.25 EndZ=0
    g47: LineSegment StartX=7.06218 StartY=-5.25 StartZ=0 EndX=4.03109 EndY=-3.5 EndZ=0
    g48: Circle [constr] CenterX=4.03109 CenterY=-7 CenterZ=0 NormalX=0 NormalY=0 NormalZ=1 AngleXU=0 Radius=3.5
  constraints (117):
    c: Coincident(g0,g1)
    c: Coincident(g1,g2)
    c: Coincident(g2,g3)
    c: Coincident(g3,g4)
    c: Coincident(g4,g5)
    c: Coincident(g5,g0)
    c: Equal(g0, g1-g5) x5
    c: PointOnObject(g0,g6)
    c: PointOnObject(g1,g6)
    c: PointOnObject(g2,g6)
    c: PointOnObject(g3,g6)
    c: PointOnObject(g4,g6)
    c: PointOnObject(g5,g6)
    c: Coincident(g6,g-1)
    c: Diameter(g6) = 7
    c: PointOnObject(g0,g-2)
    c: Coincident(g7,g8)
    c: Coincident(g8,g9)
    c: Coincident(g9,g10)
    c: Coincident(g10,g11)
    c: Coincident(g11,g12)
    c: Coincident(g12,g7)
    c: Equal(g7, g8-g12) x5
    c: PointOnObject(g7,g13)
    c: PointOnObject(g8,g13)
    c: PointOnObject(g9,g13)
    c: PointOnObject(g10,g13)
    c: PointOnObject(g11,g13)
    c: PointOnObject(g12,g13)
    c: PointOnObject(g13,g-1)
    c: Diameter(g13) = 7
    c: Distance(g6,g13) = 8
    c: Horizontal(g0,g10)
    c: Coincident(g14,g15)
    c: Coincident(g15,g16)
    c: Coincident(g16,g17)
    c: Coincident(g17,g18)
    c: Coincident(g18,g19)
    c: Coincident(g19,g14)
    c: Equal(g14, g15-g19) x5
    c: PointOnObject(g14,g20)
    c: PointOnObject(g15,g20)
    c: PointOnObject(g16,g20)
    c: PointOnObject(g17,g20)
    c: PointOnObject(g18,g20)
    c: PointOnObject(g19,g20)
    c: Diameter(g20) = 7
    c: DistanceY(g-1,g20) = 7
    c: Vertical(g18)
    c: Distance(g17,g-2) = 1
    c: Coincident(g21,g22)
    c: Coincident(g22,g23)
    c: Coincident(g23,g24)
    c: Coincident(g24,g25)
    c: Coincident(g25,g26)
    c: Coincident(g26,g21)
    c: Equal(g21, g22-g26) x5
    c: PointOnObject(g21,g27)
    c: PointOnObject(g22,g27)
    c: PointOnObject(g23,g27)
    c: PointOnObject(g24,g27)
    c: PointOnObject(g25,g27)
    c: PointOnObject(g26,g27)
    c: Diameter(g27) = 7
    c: DistanceY(g-1,g27) = 7
    c: DistanceX(g21,g-1) = 1
    c: Vertical(g21)
    c: Coincident(g28,g29)
    c: Coincident(g29,g30)
    c: Coincident(g30,g31)
    c: Coincident(g31,g32)
    c: Coincident(g32,g33)
    c: Coincident(g33,g28)
    c: Equal(g28, g29-g33) x5
    c: PointOnObject(g28,g34)
    c: PointOnObject(g29,g34)
    c: PointOnObject(g30,g34)
    c: PointOnObject(g31,g34)
    c: PointOnObject(g32,g34)
    c: PointOnObject(g33,g34)
    c: PointOnObject(g34,g-1)
    c: Diameter(g34) = 7
    c: Vertical(g31)
    c: DistanceX(g34,g-1) = 8
    c: Coincident(g35,g36)
    c: Coincident(g36,g37)
    c: Coincident(g37,g38)
    c: Coincident(g38,g39)
    c: Coincident(g39,g40)
    c: Coincident(g40,g35)
    c: Equal(g35, g36-g40) x5
    c: PointOnObject(g35,g41)
    c: PointOnObject(g36,g41)
    c: PointOnObject(g37,g41)
    c: PointOnObject(g38,g41)
    c: PointOnObject(g39,g41)
    c: PointOnObject(g40,g41)
    c: Coincident(g42,g43)
    c: Coincident(g43,g44)
    c: Coincident(g44,g45)
    c: Coincident(g45,g46)
    c: Coincident(g46,g47)
    c: Coincident(g47,g42)
    c: Equal(g42, g43-g47) x5
    c: PointOnObject(g42,g48)
    c: PointOnObject(g43,g48)
    c: PointOnObject(g44,g48)
    c: PointOnObject(g45,g48)
    c: PointOnObject(g46,g48)
    c: PointOnObject(g47,g48)
    c: Equal(g41,g48)
    c: Diameter(g41) = 7
    c: Vertical(g39)
    c: Vertical(g43)
    c: Distance(g-2,g39) = 1
    c: Symmetric(g38,g43,g-2)
    c: Distance(g41,g-1) = 7
FEATURE [Part::Extrusion] Extrude514  label="hex129"
  Base = -> Sketch522
  Dir = (0,-1,2e-16)
  DirMode = 2
  FaceMakerClass = Part::FaceMakerBullseye
  FaceMakerMode = 3
  LengthFwd = 10
  LengthRev = 0
  Placement = pos=(-64,0,-14) rot=(0,0,1;0rad)
  Solid = true
  Symmetric = false
FEATURE [Sketcher::SketchObject] Sketch523
  ArcFitTolerance = 1e-06
  FullyConstrained = true
  MakeInternals = false
  Placement = pos=(0,0,0) rot=(1,0,0;1.5708rad)
  sketch-geometry (49):
    g0: LineSegment StartX=1e-16 StartY=3.5 StartZ=0 EndX=-3.03109 EndY=1.75 EndZ=0
    g1: LineSegment StartX=-3.03109 StartY=1.75 StartZ=0 EndX=-3.03109 EndY=-1.75 EndZ=0
    g2: LineSegment StartX=-3.03109 StartY=-1.75 StartZ=0 EndX=-1e-16 EndY=-3.5 EndZ=0
    g3: LineSegment StartX=-1e-16 StartY=-3.5 StartZ=0 EndX=3.03109 EndY=-1.75 EndZ=0
    g4: LineSegment StartX=3.03109 StartY=-1.75 StartZ=0 EndX=3.03109 EndY=1.75 EndZ=0
    g5: LineSegment StartX=3.03109 StartY=1.75 StartZ=0 EndX=1e-16 EndY=3.5 EndZ=0
    g6: Circle [constr] CenterX=0 CenterY=0 CenterZ=0 NormalX=0 NormalY=0 NormalZ=1 AngleXU=0 Radius=3.5
    g7: LineSegment StartX=4.96892 StartY=-1.75002 StartZ=0 EndX=8.00002 EndY=-3.5 EndZ=0
    g8: LineSegment StartX=8.00002 StartY=-3.5 StartZ=0 EndX=11.0311 EndY=-1.74998 EndZ=0
    g9: LineSegment StartX=11.0311 StartY=-1.74998 StartZ=0 EndX=11.0311 EndY=1.75002 EndZ=0
    g10: LineSegment StartX=11.0311 StartY=1.75002 StartZ=0 EndX=7.99998 EndY=3.5 EndZ=0
    g11: LineSegment StartX=7.99998 StartY=3.5 StartZ=0 EndX=4.9689 EndY=1.74998 EndZ=0
    g12: LineSegment StartX=4.9689 StartY=1.74998 StartZ=0 EndX=4.96892 EndY=-1.75002 EndZ=0
    g13: Circle [constr] CenterX=8 CenterY=0 CenterZ=0 NormalX=0 NormalY=0 NormalZ=1 AngleXU=0 Radius=3.5
    g14: LineSegment StartX=4.03109 StartY=3.5 StartZ=0 EndX=7.06218 EndY=5.25 EndZ=0
    g15: LineSegment StartX=7.06218 StartY=5.25 StartZ=0 EndX=7.06218 EndY=8.75 EndZ=0
    g16: LineSegment StartX=7.06218 StartY=8.75 StartZ=0 EndX=4.03109 EndY=10.5 EndZ=0
    g17: LineSegment StartX=4.03109 StartY=10.5 StartZ=0 EndX=1 EndY=8.75 EndZ=0
    g18: LineSegment StartX=1 StartY=8.75 StartZ=0 EndX=1 EndY=5.25 EndZ=0
    g19: LineSegment StartX=1 StartY=5.25 StartZ=0 EndX=4.03109 EndY=3.5 EndZ=0
    g20: Circle [constr] CenterX=4.03109 CenterY=7 CenterZ=0 NormalX=0 NormalY=0 NormalZ=1 AngleXU=0 Radius=3.5
    g21: LineSegment StartX=-1 StartY=5.25 StartZ=0 EndX=-1 EndY=8.75 EndZ=0
    g22: LineSegment StartX=-1 StartY=8.75 StartZ=0 EndX=-4.03109 EndY=10.5 EndZ=0
    g23: LineSegment StartX=-4.03109 StartY=10.5 StartZ=0 EndX=-7.06218 EndY=8.75 EndZ=0
    g24: LineSegment StartX=-7.06218 StartY=8.75 StartZ=0 EndX=-7.06218 EndY=5.25 EndZ=0
    g25: LineSegment StartX=-7.06218 StartY=5.25 StartZ=0 EndX=-4.03109 EndY=3.5 EndZ=0
    g26: LineSegment StartX=-4.03109 StartY=3.5 StartZ=0 EndX=-1 EndY=5.25 EndZ=0
    g27: Circle [constr] CenterX=-4.03109 CenterY=7 CenterZ=0 NormalX=0 NormalY=0 NormalZ=1 AngleXU=0 Radius=3.5
    g28: LineSegment StartX=-4.96891 StartY=-1.75 StartZ=0 EndX=-4.96891 EndY=1.75 EndZ=0
    g29: LineSegment StartX=-4.96891 StartY=1.75 StartZ=0 EndX=-8 EndY=3.5 EndZ=0
    g30: LineSegment StartX=-8 StartY=3.5 StartZ=0 EndX=-11.0311 EndY=1.75 EndZ=0
    g31: LineSegment StartX=-11.0311 StartY=1.75 StartZ=0 EndX=-11.0311 EndY=-1.75 EndZ=0
    g32: LineSegment StartX=-11.0311 StartY=-1.75 StartZ=0 EndX=-8 EndY=-3.5 EndZ=0
    g33: LineSegment StartX=-8 StartY=-3.5 StartZ=0 EndX=-4.96891 EndY=-1.75 EndZ=0
    g34: Circle [constr] CenterX=-8 CenterY=0 CenterZ=0 NormalX=0 NormalY=0 NormalZ=1 AngleXU=0 Radius=3.5
    g35: LineSegment StartX=-4.03109 StartY=-3.5 StartZ=0 EndX=-7.06218 EndY=-5.25 EndZ=0
    g36: LineSegment StartX=-7.06218 StartY=-5.25 StartZ=0 EndX=-7.06218 EndY=-8.75 EndZ=0
    g37: LineSegment StartX=-7.06218 StartY=-8.75 StartZ=0 EndX=-4.03109 EndY=-10.5 EndZ=0
    g38: LineSegment StartX=-4.03109 StartY=-10.5 StartZ=0 EndX=-1 EndY=-8.75 EndZ=0
    g39: LineSegment StartX=-1 StartY=-8.75 StartZ=0 EndX=-1 EndY=-5.25 EndZ=0
    g40: LineSegment StartX=-1 StartY=-5.25 StartZ=0 EndX=-4.03109 EndY=-3.5 EndZ=0
    g41: Circle [constr] CenterX=-4.03109 CenterY=-7 CenterZ=0 NormalX=0 NormalY=0 NormalZ=1 AngleXU=0 Radius=3.5
    g42: LineSegment StartX=4.03109 StartY=-3.5 StartZ=0 EndX=1 EndY=-5.25 EndZ=0
    g43: LineSegment StartX=1 StartY=-5.25 StartZ=0 EndX=1 EndY=-8.75 EndZ=0
    g44: LineSegment StartX=1 StartY=-8.75 StartZ=0 EndX=4.03109 EndY=-10.5 EndZ=0
    g45: LineSegment StartX=4.03109 StartY=-10.5 StartZ=0 EndX=7.06218 EndY=-8.75 EndZ=0
    g46: LineSegment StartX=7.06218 StartY=-8.75 StartZ=0 EndX=7.06218 EndY=-5.25 EndZ=0
    g47: LineSegment StartX=7.06218 StartY=-5.25 StartZ=0 EndX=4.03109 EndY=-3.5 EndZ=0
    g48: Circle [constr] CenterX=4.03109 CenterY=-7 CenterZ=0 NormalX=0 NormalY=0 NormalZ=1 AngleXU=0 Radius=3.5
  constraints (117):
    c: Coincident(g0,g1)
    c: Coincident(g1,g2)
    c: Coincident(g2,g3)
    c: Coincident(g3,g4)
    c: Coincident(g4,g5)
    c: Coincident(g5,g0)
    c: Equal(g0, g1-g5) x5
    c: PointOnObject(g0,g6)
    c: PointOnObject(g1,g6)
    c: PointOnObject(g2,g6)
    c: PointOnObject(g3,g6)
    c: PointOnObject(g4,g6)
    c: PointOnObject(g5,g6)
    c: Coincident(g6,g-1)
    c: Diameter(g6) = 7
    c: PointOnObject(g0,g-2)
    c: Coincident(g7,g8)
    c: Coincident(g8,g9)
    c: Coincident(g9,g10)
    c: Coincident(g10,g11)
    c: Coincident(g11,g12)
    c: Coincident(g12,g7)
    c: Equal(g7, g8-g12) x5
    c: PointOnObject(g7,g13)
    c: PointOnObject(g8,g13)
    c: PointOnObject(g9,g13)
    c: PointOnObject(g10,g13)
    c: PointOnObject(g11,g13)
    c: PointOnObject(g12,g13)
    c: PointOnObject(g13,g-1)
    c: Diameter(g13) = 7
    c: Distance(g6,g13) = 8
    c: Horizontal(g0,g10)
    c: Coincident(g14,g15)
    c: Coincident(g15,g16)
    c: Coincident(g16,g17)
    c: Coincident(g17,g18)
    c: Coincident(g18,g19)
    c: Coincident(g19,g14)
    c: Equal(g14, g15-g19) x5
    c: PointOnObject(g14,g20)
    c: PointOnObject(g15,g20)
    c: PointOnObject(g16,g20)
    c: PointOnObject(g17,g20)
    c: PointOnObject(g18,g20)
    c: PointOnObject(g19,g20)
    c: Diameter(g20) = 7
    c: DistanceY(g-1,g20) = 7
    c: Vertical(g18)
    c: Distance(g17,g-2) = 1
    c: Coincident(g21,g22)
    c: Coincident(g22,g23)
    c: Coincident(g23,g24)
    c: Coincident(g24,g25)
    c: Coincident(g25,g26)
    c: Coincident(g26,g21)
    c: Equal(g21, g22-g26) x5
    c: PointOnObject(g21,g27)
    c: PointOnObject(g22,g27)
    c: PointOnObject(g23,g27)
    c: PointOnObject(g24,g27)
    c: PointOnObject(g25,g27)
    c: PointOnObject(g26,g27)
    c: Diameter(g27) = 7
    c: DistanceY(g-1,g27) = 7
    c: DistanceX(g21,g-1) = 1
    c: Vertical(g21)
    c: Coincident(g28,g29)
    c: Coincident(g29,g30)
    c: Coincident(g30,g31)
    c: Coincident(g31,g32)
    c: Coincident(g32,g33)
    c: Coincident(g33,g28)
    c: Equal(g28, g29-g33) x5
    c: PointOnObject(g28,g34)
    c: PointOnObject(g29,g34)
    c: PointOnObject(g30,g34)
    c: PointOnObject(g31,g34)
    c: PointOnObject(g32,g34)
    c: PointOnObject(g33,g34)
    c: PointOnObject(g34,g-1)
    c: Diameter(g34) = 7
    c: Vertical(g31)
    c: DistanceX(g34,g-1) = 8
    c: Coincident(g35,g36)
    c: Coincident(g36,g37)
    c: Coincident(g37,g38)
    c: Coincident(g38,g39)
    c: Coincident(g39,g40)
    c: Coincident(g40,g35)
    c: Equal(g35, g36-g40) x5
    c: PointOnObject(g35,g41)
    c: PointOnObject(g36,g41)
    c: PointOnObject(g37,g41)
    c: PointOnObject(g38,g41)
    c: PointOnObject(g39,g41)
    c: PointOnObject(g40,g41)
    c: Coincident(g42,g43)
    c: Coincident(g43,g44)
    c: Coincident(g44,g45)
    c: Coincident(g45,g46)
    c: Coincident(g46,g47)
    c: Coincident(g47,g42)
    c: Equal(g42, g43-g47) x5
    c: PointOnObject(g42,g48)
    c: PointOnObject(g43,g48)
    c: PointOnObject(g44,g48)
    c: PointOnObject(g45,g48)
    c: PointOnObject(g46,g48)
    c: PointOnObject(g47,g48)
    c: Equal(g41,g48)
    c: Diameter(g41) = 7
    c: Vertical(g39)
    c: Vertical(g43)
    c: Distance(g-2,g39) = 1
    c: Symmetric(g38,g43,g-2)
    c: Distance(g41,g-1) = 7
FEATURE [Part::Extrusion] Extrude515  label="hex130"
  Base = -> Sketch523
  Dir = (0,-1,2e-16)
  DirMode = 2
  FaceMakerClass = Part::FaceMakerBullseye
  FaceMakerMode = 3
  LengthFwd = 10
  LengthRev = 0
  Placement = pos=(-48,0,-28) rot=(0,0,1;0rad)
  Solid = true
  Symmetric = false
FEATURE [Sketcher::SketchObject] Sketch524
  ArcFitTolerance = 1e-06
  FullyConstrained = true
  MakeInternals = false
  Placement = pos=(0,0,0) rot=(1,0,0;1.5708rad)
  sketch-geometry (49):
    g0: LineSegment StartX=1e-16 StartY=3.5 StartZ=0 EndX=-3.03109 EndY=1.75 EndZ=0
    g1: LineSegment StartX=-3.03109 StartY=1.75 StartZ=0 EndX=-3.03109 EndY=-1.75 EndZ=0
    g2: LineSegment StartX=-3.03109 StartY=-1.75 StartZ=0 EndX=-1e-16 EndY=-3.5 EndZ=0
    g3: LineSegment StartX=-1e-16 StartY=-3.5 StartZ=0 EndX=3.03109 EndY=-1.75 EndZ=0
    g4: LineSegment StartX=3.03109 StartY=-1.75 StartZ=0 EndX=3.03109 EndY=1.75 EndZ=0
    g5: LineSegment StartX=3.03109 StartY=1.75 StartZ=0 EndX=1e-16 EndY=3.5 EndZ=0
    g6: Circle [constr] CenterX=0 CenterY=0 CenterZ=0 NormalX=0 NormalY=0 NormalZ=1 AngleXU=0 Radius=3.5
    g7: LineSegment StartX=4.96892 StartY=-1.75002 StartZ=0 EndX=8.00002 EndY=-3.5 EndZ=0
    g8: LineSegment StartX=8.00002 StartY=-3.5 StartZ=0 EndX=11.0311 EndY=-1.74998 EndZ=0
    g9: LineSegment StartX=11.0311 StartY=-1.74998 StartZ=0 EndX=11.0311 EndY=1.75002 EndZ=0
    g10: LineSegment StartX=11.0311 StartY=1.75002 StartZ=0 EndX=7.99998 EndY=3.5 EndZ=0
    g11: LineSegment StartX=7.99998 StartY=3.5 StartZ=0 EndX=4.9689 EndY=1.74998 EndZ=0
    g12: LineSegment StartX=4.9689 StartY=1.74998 StartZ=0 EndX=4.96892 EndY=-1.75002 EndZ=0
    g13: Circle [constr] CenterX=8 CenterY=0 CenterZ=0 NormalX=0 NormalY=0 NormalZ=1 AngleXU=0 Radius=3.5
    g14: LineSegment StartX=4.03109 StartY=3.5 StartZ=0 EndX=7.06218 EndY=5.25 EndZ=0
    g15: LineSegment StartX=7.06218 StartY=5.25 StartZ=0 EndX=7.06218 EndY=8.75 EndZ=0
    g16: LineSegment StartX=7.06218 StartY=8.75 StartZ=0 EndX=4.03109 EndY=10.5 EndZ=0
    g17: LineSegment StartX=4.03109 StartY=10.5 StartZ=0 EndX=1 EndY=8.75 EndZ=0
    g18: LineSegment StartX=1 StartY=8.75 StartZ=0 EndX=1 EndY=5.25 EndZ=0
    g19: LineSegment StartX=1 StartY=5.25 StartZ=0 EndX=4.03109 EndY=3.5 EndZ=0
    g20: Circle [constr] CenterX=4.03109 CenterY=7 CenterZ=0 NormalX=0 NormalY=0 NormalZ=1 AngleXU=0 Radius=3.5
    g21: LineSegment StartX=-1 StartY=5.25 StartZ=0 EndX=-1 EndY=8.75 EndZ=0
    g22: LineSegment StartX=-1 StartY=8.75 StartZ=0 EndX=-4.03109 EndY=10.5 EndZ=0
    g23: LineSegment StartX=-4.03109 StartY=10.5 StartZ=0 EndX=-7.06218 EndY=8.75 EndZ=0
    g24: LineSegment StartX=-7.06218 StartY=8.75 StartZ=0 EndX=-7.06218 EndY=5.25 EndZ=0
    g25: LineSegment StartX=-7.06218 StartY=5.25 StartZ=0 EndX=-4.03109 EndY=3.5 EndZ=0
    g26: LineSegment StartX=-4.03109 StartY=3.5 StartZ=0 EndX=-1 EndY=5.25 EndZ=0
    g27: Circle [constr] CenterX=-4.03109 CenterY=7 CenterZ=0 NormalX=0 NormalY=0 NormalZ=1 AngleXU=0 Radius=3.5
    g28: LineSegment StartX=-4.96891 StartY=-1.75 StartZ=0 EndX=-4.96891 EndY=1.75 EndZ=0
    g29: LineSegment StartX=-4.96891 StartY=1.75 StartZ=0 EndX=-8 EndY=3.5 EndZ=0
    g30: LineSegment StartX=-8 StartY=3.5 StartZ=0 EndX=-11.0311 EndY=1.75 EndZ=0
    g31: LineSegment StartX=-11.0311 StartY=1.75 StartZ=0 EndX=-11.0311 EndY=-1.75 EndZ=0
    g32: LineSegment StartX=-11.0311 StartY=-1.75 StartZ=0 EndX=-8 EndY=-3.5 EndZ=0
    g33: LineSegment StartX=-8 StartY=-3.5 StartZ=0 EndX=-4.96891 EndY=-1.75 EndZ=0
    g34: Circle [constr] CenterX=-8 CenterY=0 CenterZ=0 NormalX=0 NormalY=0 NormalZ=1 AngleXU=0 Radius=3.5
    g35: LineSegment StartX=-4.03109 StartY=-3.5 StartZ=0 EndX=-7.06218 EndY=-5.25 EndZ=0
    g36: LineSegment StartX=-7.06218 StartY=-5.25 StartZ=0 EndX=-7.06218 EndY=-8.75 EndZ=0
    g37: LineSegment StartX=-7.06218 StartY=-8.75 StartZ=0 EndX=-4.03109 EndY=-10.5 EndZ=0
    g38: LineSegment StartX=-4.03109 StartY=-10.5 StartZ=0 EndX=-1 EndY=-8.75 EndZ=0
    g39: LineSegment StartX=-1 StartY=-8.75 StartZ=0 EndX=-1 EndY=-5.25 EndZ=0
    g40: LineSegment StartX=-1 StartY=-5.25 StartZ=0 EndX=-4.03109 EndY=-3.5 EndZ=0
    g41: Circle [constr] CenterX=-4.03109 CenterY=-7 CenterZ=0 NormalX=0 NormalY=0 NormalZ=1 AngleXU=0 Radius=3.5
    g42: LineSegment StartX=4.03109 StartY=-3.5 StartZ=0 EndX=1 EndY=-5.25 EndZ=0
    g43: LineSegment StartX=1 StartY=-5.25 StartZ=0 EndX=1 EndY=-8.75 EndZ=0
    g44: LineSegment StartX=1 StartY=-8.75 StartZ=0 EndX=4.03109 EndY=-10.5 EndZ=0
    g45: LineSegment StartX=4.03109 StartY=-10.5 StartZ=0 EndX=7.06218 EndY=-8.75 EndZ=0
    g46: LineSegment StartX=7.06218 StartY=-8.75 StartZ=0 EndX=7.06218 EndY=-5.25 EndZ=0
    g47: LineSegment StartX=7.06218 StartY=-5.25 StartZ=0 EndX=4.03109 EndY=-3.5 EndZ=0
    g48: Circle [constr] CenterX=4.03109 CenterY=-7 CenterZ=0 NormalX=0 NormalY=0 NormalZ=1 AngleXU=0 Radius=3.5
  constraints (117):
    c: Coincident(g0,g1)
    c: Coincident(g1,g2)
    c: Coincident(g2,g3)
    c: Coincident(g3,g4)
    c: Coincident(g4,g5)
    c: Coincident(g5,g0)
    c: Equal(g0, g1-g5) x5
    c: PointOnObject(g0,g6)
    c: PointOnObject(g1,g6)
    c: PointOnObject(g2,g6)
    c: PointOnObject(g3,g6)
    c: PointOnObject(g4,g6)
    c: PointOnObject(g5,g6)
    c: Coincident(g6,g-1)
    c: Diameter(g6) = 7
    c: PointOnObject(g0,g-2)
    c: Coincident(g7,g8)
    c: Coincident(g8,g9)
    c: Coincident(g9,g10)
    c: Coincident(g10,g11)
    c: Coincident(g11,g12)
    c: Coincident(g12,g7)
    c: Equal(g7, g8-g12) x5
    c: PointOnObject(g7,g13)
    c: PointOnObject(g8,g13)
    c: PointOnObject(g9,g13)
    c: PointOnObject(g10,g13)
    c: PointOnObject(g11,g13)
    c: PointOnObject(g12,g13)
    c: PointOnObject(g13,g-1)
    c: Diameter(g13) = 7
    c: Distance(g6,g13) = 8
    c: Horizontal(g0,g10)
    c: Coincident(g14,g15)
    c: Coincident(g15,g16)
    c: Coincident(g16,g17)
    c: Coincident(g17,g18)
    c: Coincident(g18,g19)
    c: Coincident(g19,g14)
    c: Equal(g14, g15-g19) x5
    c: PointOnObject(g14,g20)
    c: PointOnObject(g15,g20)
    c: PointOnObject(g16,g20)
    c: PointOnObject(g17,g20)
    c: PointOnObject(g18,g20)
    c: PointOnObject(g19,g20)
    c: Diameter(g20) = 7
    c: DistanceY(g-1,g20) = 7
    c: Vertical(g18)
    c: Distance(g17,g-2) = 1
    c: Coincident(g21,g22)
    c: Coincident(g22,g23)
    c: Coincident(g23,g24)
    c: Coincident(g24,g25)
    c: Coincident(g25,g26)
    c: Coincident(g26,g21)
    c: Equal(g21, g22-g26) x5
    c: PointOnObject(g21,g27)
    c: PointOnObject(g22,g27)
    c: PointOnObject(g23,g27)
    c: PointOnObject(g24,g27)
    c: PointOnObject(g25,g27)
    c: PointOnObject(g26,g27)
    c: Diameter(g27) = 7
    c: DistanceY(g-1,g27) = 7
    c: DistanceX(g21,g-1) = 1
    c: Vertical(g21)
    c: Coincident(g28,g29)
    c: Coincident(g29,g30)
    c: Coincident(g30,g31)
    c: Coincident(g31,g32)
    c: Coincident(g32,g33)
    c: Coincident(g33,g28)
    c: Equal(g28, g29-g33) x5
    c: PointOnObject(g28,g34)
    c: PointOnObject(g29,g34)
    c: PointOnObject(g30,g34)
    c: PointOnObject(g31,g34)
    c: PointOnObject(g32,g34)
    c: PointOnObject(g33,g34)
    c: PointOnObject(g34,g-1)
    c: Diameter(g34) = 7
    c: Vertical(g31)
    c: DistanceX(g34,g-1) = 8
    c: Coincident(g35,g36)
    c: Coincident(g36,g37)
    c: Coincident(g37,g38)
    c: Coincident(g38,g39)
    c: Coincident(g39,g40)
    c: Coincident(g40,g35)
    c: Equal(g35, g36-g40) x5
    c: PointOnObject(g35,g41)
    c: PointOnObject(g36,g41)
    c: PointOnObject(g37,g41)
    c: PointOnObject(g38,g41)
    c: PointOnObject(g39,g41)
    c: PointOnObject(g40,g41)
    c: Coincident(g42,g43)
    c: Coincident(g43,g44)
    c: Coincident(g44,g45)
    c: Coincident(g45,g46)
    c: Coincident(g46,g47)
    c: Coincident(g47,g42)
    c: Equal(g42, g43-g47) x5
    c: PointOnObject(g42,g48)
    c: PointOnObject(g43,g48)
    c: PointOnObject(g44,g48)
    c: PointOnObject(g45,g48)
    c: PointOnObject(g46,g48)
    c: PointOnObject(g47,g48)
    c: Equal(g41,g48)
    c: Diameter(g41) = 7
    c: Vertical(g39)
    c: Vertical(g43)
    c: Distance(g-2,g39) = 1
    c: Symmetric(g38,g43,g-2)
    c: Distance(g41,g-1) = 7
FEATURE [Part::Extrusion] Extrude516  label="hex131"
  Base = -> Sketch524
  Dir = (0,-1,2e-16)
  DirMode = 2
  FaceMakerClass = Part::FaceMakerBullseye
  FaceMakerMode = 3
  LengthFwd = 10
  LengthRev = 0
  Placement = pos=(-32,0,-42) rot=(0,0,1;0rad)
  Solid = true
  Symmetric = false
FEATURE [Sketcher::SketchObject] Sketch525
  ArcFitTolerance = 1e-06
  FullyConstrained = true
  MakeInternals = false
  Placement = pos=(0,0,0) rot=(1,0,0;1.5708rad)
  sketch-geometry (49):
    g0: LineSegment StartX=1e-16 StartY=3.5 StartZ=0 EndX=-3.03109 EndY=1.75 EndZ=0
    g1: LineSegment StartX=-3.03109 StartY=1.75 StartZ=0 EndX=-3.03109 EndY=-1.75 EndZ=0
    g2: LineSegment StartX=-3.03109 StartY=-1.75 StartZ=0 EndX=-1e-16 EndY=-3.5 EndZ=0
    g3: LineSegment StartX=-1e-16 StartY=-3.5 StartZ=0 EndX=3.03109 EndY=-1.75 EndZ=0
    g4: LineSegment StartX=3.03109 StartY=-1.75 StartZ=0 EndX=3.03109 EndY=1.75 EndZ=0
    g5: LineSegment StartX=3.03109 StartY=1.75 StartZ=0 EndX=1e-16 EndY=3.5 EndZ=0
    g6: Circle [constr] CenterX=0 CenterY=0 CenterZ=0 NormalX=0 NormalY=0 NormalZ=1 AngleXU=0 Radius=3.5
    g7: LineSegment StartX=4.96892 StartY=-1.75002 StartZ=0 EndX=8.00002 EndY=-3.5 EndZ=0
    g8: LineSegment StartX=8.00002 StartY=-3.5 StartZ=0 EndX=11.0311 EndY=-1.74998 EndZ=0
    g9: LineSegment StartX=11.0311 StartY=-1.74998 StartZ=0 EndX=11.0311 EndY=1.75002 EndZ=0
    g10: LineSegment StartX=11.0311 StartY=1.75002 StartZ=0 EndX=7.99998 EndY=3.5 EndZ=0
    g11: LineSegment StartX=7.99998 StartY=3.5 StartZ=0 EndX=4.9689 EndY=1.74998 EndZ=0
    g12: LineSegment StartX=4.9689 StartY=1.74998 StartZ=0 EndX=4.96892 EndY=-1.75002 EndZ=0
    g13: Circle [constr] CenterX=8 CenterY=0 CenterZ=0 NormalX=0 NormalY=0 NormalZ=1 AngleXU=0 Radius=3.5
    g14: LineSegment StartX=4.03109 StartY=3.5 StartZ=0 EndX=7.06218 EndY=5.25 EndZ=0
    g15: LineSegment StartX=7.06218 StartY=5.25 StartZ=0 EndX=7.06218 EndY=8.75 EndZ=0
    g16: LineSegment StartX=7.06218 StartY=8.75 StartZ=0 EndX=4.03109 EndY=10.5 EndZ=0
    g17: LineSegment StartX=4.03109 StartY=10.5 StartZ=0 EndX=1 EndY=8.75 EndZ=0
    g18: LineSegment StartX=1 StartY=8.75 StartZ=0 EndX=1 EndY=5.25 EndZ=0
    g19: LineSegment StartX=1 StartY=5.25 StartZ=0 EndX=4.03109 EndY=3.5 EndZ=0
    g20: Circle [constr] CenterX=4.03109 CenterY=7 CenterZ=0 NormalX=0 NormalY=0 NormalZ=1 AngleXU=0 Radius=3.5
    g21: LineSegment StartX=-1 StartY=5.25 StartZ=0 EndX=-1 EndY=8.75 EndZ=0
    g22: LineSegment StartX=-1 StartY=8.75 StartZ=0 EndX=-4.03109 EndY=10.5 EndZ=0
    g23: LineSegment StartX=-4.03109 StartY=10.5 StartZ=0 EndX=-7.06218 EndY=8.75 EndZ=0
    g24: LineSegment StartX=-7.06218 StartY=8.75 StartZ=0 EndX=-7.06218 EndY=5.25 EndZ=0
    g25: LineSegment StartX=-7.06218 StartY=5.25 StartZ=0 EndX=-4.03109 EndY=3.5 EndZ=0
    g26: LineSegment StartX=-4.03109 StartY=3.5 StartZ=0 EndX=-1 EndY=5.25 EndZ=0
    g27: Circle [constr] CenterX=-4.03109 CenterY=7 CenterZ=0 NormalX=0 NormalY=0 NormalZ=1 AngleXU=0 Radius=3.5
    g28: LineSegment StartX=-4.96891 StartY=-1.75 StartZ=0 EndX=-4.96891 EndY=1.75 EndZ=0
    g29: LineSegment StartX=-4.96891 StartY=1.75 StartZ=0 EndX=-8 EndY=3.5 EndZ=0
    g30: LineSegment StartX=-8 StartY=3.5 StartZ=0 EndX=-11.0311 EndY=1.75 EndZ=0
    g31: LineSegment StartX=-11.0311 StartY=1.75 StartZ=0 EndX=-11.0311 EndY=-1.75 EndZ=0
    g32: LineSegment StartX=-11.0311 StartY=-1.75 StartZ=0 EndX=-8 EndY=-3.5 EndZ=0
    g33: LineSegment StartX=-8 StartY=-3.5 StartZ=0 EndX=-4.96891 EndY=-1.75 EndZ=0
    g34: Circle [constr] CenterX=-8 CenterY=0 CenterZ=0 NormalX=0 NormalY=0 NormalZ=1 AngleXU=0 Radius=3.5
    g35: LineSegment StartX=-4.03109 StartY=-3.5 StartZ=0 EndX=-7.06218 EndY=-5.25 EndZ=0
    g36: LineSegment StartX=-7.06218 StartY=-5.25 StartZ=0 EndX=-7.06218 EndY=-8.75 EndZ=0
    g37: LineSegment StartX=-7.06218 StartY=-8.75 StartZ=0 EndX=-4.03109 EndY=-10.5 EndZ=0
    g38: LineSegment StartX=-4.03109 StartY=-10.5 StartZ=0 EndX=-1 EndY=-8.75 EndZ=0
    g39: LineSegment StartX=-1 StartY=-8.75 StartZ=0 EndX=-1 EndY=-5.25 EndZ=0
    g40: LineSegment StartX=-1 StartY=-5.25 StartZ=0 EndX=-4.03109 EndY=-3.5 EndZ=0
    g41: Circle [constr] CenterX=-4.03109 CenterY=-7 CenterZ=0 NormalX=0 NormalY=0 NormalZ=1 AngleXU=0 Radius=3.5
    g42: LineSegment StartX=4.03109 StartY=-3.5 StartZ=0 EndX=1 EndY=-5.25 EndZ=0
    g43: LineSegment StartX=1 StartY=-5.25 StartZ=0 EndX=1 EndY=-8.75 EndZ=0
    g44: LineSegment StartX=1 StartY=-8.75 StartZ=0 EndX=4.03109 EndY=-10.5 EndZ=0
    g45: LineSegment StartX=4.03109 StartY=-10.5 StartZ=0 EndX=7.06218 EndY=-8.75 EndZ=0
    g46: LineSegment StartX=7.06218 StartY=-8.75 StartZ=0 EndX=7.06218 EndY=-5.25 EndZ=0
    g47: LineSegment StartX=7.06218 StartY=-5.25 StartZ=0 EndX=4.03109 EndY=-3.5 EndZ=0
    g48: Circle [constr] CenterX=4.03109 CenterY=-7 CenterZ=0 NormalX=0 NormalY=0 NormalZ=1 AngleXU=0 Radius=3.5
  constraints (117):
    c: Coincident(g0,g1)
    c: Coincident(g1,g2)
    c: Coincident(g2,g3)
    c: Coincident(g3,g4)
    c: Coincident(g4,g5)
    c: Coincident(g5,g0)
    c: Equal(g0, g1-g5) x5
    c: PointOnObject(g0,g6)
    c: PointOnObject(g1,g6)
    c: PointOnObject(g2,g6)
    c: PointOnObject(g3,g6)
    c: PointOnObject(g4,g6)
    c: PointOnObject(g5,g6)
    c: Coincident(g6,g-1)
    c: Diameter(g6) = 7
    c: PointOnObject(g0,g-2)
    c: Coincident(g7,g8)
    c: Coincident(g8,g9)
    c: Coincident(g9,g10)
    c: Coincident(g10,g11)
    c: Coincident(g11,g12)
    c: Coincident(g12,g7)
    c: Equal(g7, g8-g12) x5
    c: PointOnObject(g7,g13)
    c: PointOnObject(g8,g13)
    c: PointOnObject(g9,g13)
    c: PointOnObject(g10,g13)
    c: PointOnObject(g11,g13)
    c: PointOnObject(g12,g13)
    c: PointOnObject(g13,g-1)
    c: Diameter(g13) = 7
    c: Distance(g6,g13) = 8
    c: Horizontal(g0,g10)
    c: Coincident(g14,g15)
    c: Coincident(g15,g16)
    c: Coincident(g16,g17)
    c: Coincident(g17,g18)
    c: Coincident(g18,g19)
    c: Coincident(g19,g14)
    c: Equal(g14, g15-g19) x5
    c: PointOnObject(g14,g20)
    c: PointOnObject(g15,g20)
    c: PointOnObject(g16,g20)
    c: PointOnObject(g17,g20)
    c: PointOnObject(g18,g20)
    c: PointOnObject(g19,g20)
    c: Diameter(g20) = 7
    c: DistanceY(g-1,g20) = 7
    c: Vertical(g18)
    c: Distance(g17,g-2) = 1
    c: Coincident(g21,g22)
    c: Coincident(g22,g23)
    c: Coincident(g23,g24)
    c: Coincident(g24,g25)
    c: Coincident(g25,g26)
    c: Coincident(g26,g21)
    c: Equal(g21, g22-g26) x5
    c: PointOnObject(g21,g27)
    c: PointOnObject(g22,g27)
    c: PointOnObject(g23,g27)
    c: PointOnObject(g24,g27)
    c: PointOnObject(g25,g27)
    c: PointOnObject(g26,g27)
    c: Diameter(g27) = 7
    c: DistanceY(g-1,g27) = 7
    c: DistanceX(g21,g-1) = 1
    c: Vertical(g21)
    c: Coincident(g28,g29)
    c: Coincident(g29,g30)
    c: Coincident(g30,g31)
    c: Coincident(g31,g32)
    c: Coincident(g32,g33)
    c: Coincident(g33,g28)
    c: Equal(g28, g29-g33) x5
    c: PointOnObject(g28,g34)
    c: PointOnObject(g29,g34)
    c: PointOnObject(g30,g34)
    c: PointOnObject(g31,g34)
    c: PointOnObject(g32,g34)
    c: PointOnObject(g33,g34)
    c: PointOnObject(g34,g-1)
    c: Diameter(g34) = 7
    c: Vertical(g31)
    c: DistanceX(g34,g-1) = 8
    c: Coincident(g35,g36)
    c: Coincident(g36,g37)
    c: Coincident(g37,g38)
    c: Coincident(g38,g39)
    c: Coincident(g39,g40)
    c: Coincident(g40,g35)
    c: Equal(g35, g36-g40) x5
    c: PointOnObject(g35,g41)
    c: PointOnObject(g36,g41)
    c: PointOnObject(g37,g41)
    c: PointOnObject(g38,g41)
    c: PointOnObject(g39,g41)
    c: PointOnObject(g40,g41)
    c: Coincident(g42,g43)
    c: Coincident(g43,g44)
    c: Coincident(g44,g45)
    c: Coincident(g45,g46)
    c: Coincident(g46,g47)
    c: Coincident(g47,g42)
    c: Equal(g42, g43-g47) x5
    c: PointOnObject(g42,g48)
    c: PointOnObject(g43,g48)
    c: PointOnObject(g44,g48)
    c: PointOnObject(g45,g48)
    c: PointOnObject(g46,g48)
    c: PointOnObject(g47,g48)
    c: Equal(g41,g48)
    c: Diameter(g41) = 7
    c: Vertical(g39)
    c: Vertical(g43)
    c: Distance(g-2,g39) = 1
    c: Symmetric(g38,g43,g-2)
    c: Distance(g41,g-1) = 7
FEATURE [Part::Extrusion] Extrude517  label="hex132"
  Base = -> Sketch525
  Dir = (0,-1,2e-16)
  DirMode = 2
  FaceMakerClass = Part::FaceMakerBullseye
  FaceMakerMode = 3
  LengthFwd = 10
  LengthRev = 0
  Placement = pos=(-56,0,-42) rot=(0,0,1;0rad)
  Solid = true
  Symmetric = false
FEATURE [Sketcher::SketchObject] Sketch526
  ArcFitTolerance = 1e-06
  FullyConstrained = true
  MakeInternals = false
  Placement = pos=(0,0,0) rot=(1,0,0;1.5708rad)
  sketch-geometry (49):
    g0: LineSegment StartX=1e-16 StartY=3.5 StartZ=0 EndX=-3.03109 EndY=1.75 EndZ=0
    g1: LineSegment StartX=-3.03109 StartY=1.75 StartZ=0 EndX=-3.03109 EndY=-1.75 EndZ=0
    g2: LineSegment StartX=-3.03109 StartY=-1.75 StartZ=0 EndX=-1e-16 EndY=-3.5 EndZ=0
    g3: LineSegment StartX=-1e-16 StartY=-3.5 StartZ=0 EndX=3.03109 EndY=-1.75 EndZ=0
    g4: LineSegment StartX=3.03109 StartY=-1.75 StartZ=0 EndX=3.03109 EndY=1.75 EndZ=0
    g5: LineSegment StartX=3.03109 StartY=1.75 StartZ=0 EndX=1e-16 EndY=3.5 EndZ=0
    g6: Circle [constr] CenterX=0 CenterY=0 CenterZ=0 NormalX=0 NormalY=0 NormalZ=1 AngleXU=0 Radius=3.5
    g7: LineSegment StartX=4.96892 StartY=-1.75002 StartZ=0 EndX=8.00002 EndY=-3.5 EndZ=0
    g8: LineSegment StartX=8.00002 StartY=-3.5 StartZ=0 EndX=11.0311 EndY=-1.74998 EndZ=0
    g9: LineSegment StartX=11.0311 StartY=-1.74998 StartZ=0 EndX=11.0311 EndY=1.75002 EndZ=0
    g10: LineSegment StartX=11.0311 StartY=1.75002 StartZ=0 EndX=7.99998 EndY=3.5 EndZ=0
    g11: LineSegment StartX=7.99998 StartY=3.5 StartZ=0 EndX=4.9689 EndY=1.74998 EndZ=0
    g12: LineSegment StartX=4.9689 StartY=1.74998 StartZ=0 EndX=4.96892 EndY=-1.75002 EndZ=0
    g13: Circle [constr] CenterX=8 CenterY=0 CenterZ=0 NormalX=0 NormalY=0 NormalZ=1 AngleXU=0 Radius=3.5
    g14: LineSegment StartX=4.03109 StartY=3.5 StartZ=0 EndX=7.06218 EndY=5.25 EndZ=0
    g15: LineSegment StartX=7.06218 StartY=5.25 StartZ=0 EndX=7.06218 EndY=8.75 EndZ=0
    g16: LineSegment StartX=7.06218 StartY=8.75 StartZ=0 EndX=4.03109 EndY=10.5 EndZ=0
    g17: LineSegment StartX=4.03109 StartY=10.5 StartZ=0 EndX=1 EndY=8.75 EndZ=0
    g18: LineSegment StartX=1 StartY=8.75 StartZ=0 EndX=1 EndY=5.25 EndZ=0
    g19: LineSegment StartX=1 StartY=5.25 StartZ=0 EndX=4.03109 EndY=3.5 EndZ=0
    g20: Circle [constr] CenterX=4.03109 CenterY=7 CenterZ=0 NormalX=0 NormalY=0 NormalZ=1 AngleXU=0 Radius=3.5
    g21: LineSegment StartX=-1 StartY=5.25 StartZ=0 EndX=-1 EndY=8.75 EndZ=0
    g22: LineSegment StartX=-1 StartY=8.75 StartZ=0 EndX=-4.03109 EndY=10.5 EndZ=0
    g23: LineSegment StartX=-4.03109 StartY=10.5 StartZ=0 EndX=-7.06218 EndY=8.75 EndZ=0
    g24: LineSegment StartX=-7.06218 StartY=8.75 StartZ=0 EndX=-7.06218 EndY=5.25 EndZ=0
    g25: LineSegment StartX=-7.06218 StartY=5.25 StartZ=0 EndX=-4.03109 EndY=3.5 EndZ=0
    g26: LineSegment StartX=-4.03109 StartY=3.5 StartZ=0 EndX=-1 EndY=5.25 EndZ=0
    g27: Circle [constr] CenterX=-4.03109 CenterY=7 CenterZ=0 NormalX=0 NormalY=0 NormalZ=1 AngleXU=0 Radius=3.5
    g28: LineSegment StartX=-4.96891 StartY=-1.75 StartZ=0 EndX=-4.96891 EndY=1.75 EndZ=0
    g29: LineSegment StartX=-4.96891 StartY=1.75 StartZ=0 EndX=-8 EndY=3.5 EndZ=0
    g30: LineSegment StartX=-8 StartY=3.5 StartZ=0 EndX=-11.0311 EndY=1.75 EndZ=0
    g31: LineSegment StartX=-11.0311 StartY=1.75 StartZ=0 EndX=-11.0311 EndY=-1.75 EndZ=0
    g32: LineSegment StartX=-11.0311 StartY=-1.75 StartZ=0 EndX=-8 EndY=-3.5 EndZ=0
    g33: LineSegment StartX=-8 StartY=-3.5 StartZ=0 EndX=-4.96891 EndY=-1.75 EndZ=0
    g34: Circle [constr] CenterX=-8 CenterY=0 CenterZ=0 NormalX=0 NormalY=0 NormalZ=1 AngleXU=0 Radius=3.5
    g35: LineSegment StartX=-4.03109 StartY=-3.5 StartZ=0 EndX=-7.06218 EndY=-5.25 EndZ=0
    g36: LineSegment StartX=-7.06218 StartY=-5.25 StartZ=0 EndX=-7.06218 EndY=-8.75 EndZ=0
    g37: LineSegment StartX=-7.06218 StartY=-8.75 StartZ=0 EndX=-4.03109 EndY=-10.5 EndZ=0
    g38: LineSegment StartX=-4.03109 StartY=-10.5 StartZ=0 EndX=-1 EndY=-8.75 EndZ=0
    g39: LineSegment StartX=-1 StartY=-8.75 StartZ=0 EndX=-1 EndY=-5.25 EndZ=0
    g40: LineSegment StartX=-1 StartY=-5.25 StartZ=0 EndX=-4.03109 EndY=-3.5 EndZ=0
    g41: Circle [constr] CenterX=-4.03109 CenterY=-7 CenterZ=0 NormalX=0 NormalY=0 NormalZ=1 AngleXU=0 Radius=3.5
    g42: LineSegment StartX=4.03109 StartY=-3.5 StartZ=0 EndX=1 EndY=-5.25 EndZ=0
    g43: LineSegment StartX=1 StartY=-5.25 StartZ=0 EndX=1 EndY=-8.75 EndZ=0
    g44: LineSegment StartX=1 StartY=-8.75 StartZ=0 EndX=4.03109 EndY=-10.5 EndZ=0
    g45: LineSegment StartX=4.03109 StartY=-10.5 StartZ=0 EndX=7.06218 EndY=-8.75 EndZ=0
    g46: LineSegment StartX=7.06218 StartY=-8.75 StartZ=0 EndX=7.06218 EndY=-5.25 EndZ=0
    g47: LineSegment StartX=7.06218 StartY=-5.25 StartZ=0 EndX=4.03109 EndY=-3.5 EndZ=0
    g48: Circle [constr] CenterX=4.03109 CenterY=-7 CenterZ=0 NormalX=0 NormalY=0 NormalZ=1 AngleXU=0 Radius=3.5
  constraints (117):
    c: Coincident(g0,g1)
    c: Coincident(g1,g2)
    c: Coincident(g2,g3)
    c: Coincident(g3,g4)
    c: Coincident(g4,g5)
    c: Coincident(g5,g0)
    c: Equal(g0, g1-g5) x5
    c: PointOnObject(g0,g6)
    c: PointOnObject(g1,g6)
    c: PointOnObject(g2,g6)
    c: PointOnObject(g3,g6)
    c: PointOnObject(g4,g6)
    c: PointOnObject(g5,g6)
    c: Coincident(g6,g-1)
    c: Diameter(g6) = 7
    c: PointOnObject(g0,g-2)
    c: Coincident(g7,g8)
    c: Coincident(g8,g9)
    c: Coincident(g9,g10)
    c: Coincident(g10,g11)
    c: Coincident(g11,g12)
    c: Coincident(g12,g7)
    c: Equal(g7, g8-g12) x5
    c: PointOnObject(g7,g13)
    c: PointOnObject(g8,g13)
    c: PointOnObject(g9,g13)
    c: PointOnObject(g10,g13)
    c: PointOnObject(g11,g13)
    c: PointOnObject(g12,g13)
    c: PointOnObject(g13,g-1)
    c: Diameter(g13) = 7
    c: Distance(g6,g13) = 8
    c: Horizontal(g0,g10)
    c: Coincident(g14,g15)
    c: Coincident(g15,g16)
    c: Coincident(g16,g17)
    c: Coincident(g17,g18)
    c: Coincident(g18,g19)
    c: Coincident(g19,g14)
    c: Equal(g14, g15-g19) x5
    c: PointOnObject(g14,g20)
    c: PointOnObject(g15,g20)
    c: PointOnObject(g16,g20)
    c: PointOnObject(g17,g20)
    c: PointOnObject(g18,g20)
    c: PointOnObject(g19,g20)
    c: Diameter(g20) = 7
    c: DistanceY(g-1,g20) = 7
    c: Vertical(g18)
    c: Distance(g17,g-2) = 1
    c: Coincident(g21,g22)
    c: Coincident(g22,g23)
    c: Coincident(g23,g24)
    c: Coincident(g24,g25)
    c: Coincident(g25,g26)
    c: Coincident(g26,g21)
    c: Equal(g21, g22-g26) x5
    c: PointOnObject(g21,g27)
    c: PointOnObject(g22,g27)
    c: PointOnObject(g23,g27)
    c: PointOnObject(g24,g27)
    c: PointOnObject(g25,g27)
    c: PointOnObject(g26,g27)
    c: Diameter(g27) = 7
    c: DistanceY(g-1,g27) = 7
    c: DistanceX(g21,g-1) = 1
    c: Vertical(g21)
    c: Coincident(g28,g29)
    c: Coincident(g29,g30)
    c: Coincident(g30,g31)
    c: Coincident(g31,g32)
    c: Coincident(g32,g33)
    c: Coincident(g33,g28)
    c: Equal(g28, g29-g33) x5
    c: PointOnObject(g28,g34)
    c: PointOnObject(g29,g34)
    c: PointOnObject(g30,g34)
    c: PointOnObject(g31,g34)
    c: PointOnObject(g32,g34)
    c: PointOnObject(g33,g34)
    c: PointOnObject(g34,g-1)
    c: Diameter(g34) = 7
    c: Vertical(g31)
    c: DistanceX(g34,g-1) = 8
    c: Coincident(g35,g36)
    c: Coincident(g36,g37)
    c: Coincident(g37,g38)
    c: Coincident(g38,g39)
    c: Coincident(g39,g40)
    c: Coincident(g40,g35)
    c: Equal(g35, g36-g40) x5
    c: PointOnObject(g35,g41)
    c: PointOnObject(g36,g41)
    c: PointOnObject(g37,g41)
    c: PointOnObject(g38,g41)
    c: PointOnObject(g39,g41)
    c: PointOnObject(g40,g41)
    c: Coincident(g42,g43)
    c: Coincident(g43,g44)
    c: Coincident(g44,g45)
    c: Coincident(g45,g46)
    c: Coincident(g46,g47)
    c: Coincident(g47,g42)
    c: Equal(g42, g43-g47) x5
    c: PointOnObject(g42,g48)
    c: PointOnObject(g43,g48)
    c: PointOnObject(g44,g48)
    c: PointOnObject(g45,g48)
    c: PointOnObject(g46,g48)
    c: PointOnObject(g47,g48)
    c: Equal(g41,g48)
    c: Diameter(g41) = 7
    c: Vertical(g39)
    c: Vertical(g43)
    c: Distance(g-2,g39) = 1
    c: Symmetric(g38,g43,g-2)
    c: Distance(g41,g-1) = 7
FEATURE [Part::Extrusion] Extrude518  label="hex133"
  Base = -> Sketch526
  Dir = (0,-1,2e-16)
  DirMode = 2
  FaceMakerClass = Part::FaceMakerBullseye
  FaceMakerMode = 3
  LengthFwd = 10
  LengthRev = 0
  Placement = pos=(-40,0,-56) rot=(0,0,1;0rad)
  Solid = true
  Symmetric = false
FEATURE [Sketcher::SketchObject] Sketch527
  ArcFitTolerance = 1e-06
  FullyConstrained = true
  MakeInternals = false
  Placement = pos=(0,0,0) rot=(1,0,0;1.5708rad)
  sketch-geometry (49):
    g0: LineSegment StartX=1e-16 StartY=3.5 StartZ=0 EndX=-3.03109 EndY=1.75 EndZ=0
    g1: LineSegment StartX=-3.03109 StartY=1.75 StartZ=0 EndX=-3.03109 EndY=-1.75 EndZ=0
    g2: LineSegment StartX=-3.03109 StartY=-1.75 StartZ=0 EndX=-1e-16 EndY=-3.5 EndZ=0
    g3: LineSegment StartX=-1e-16 StartY=-3.5 StartZ=0 EndX=3.03109 EndY=-1.75 EndZ=0
    g4: LineSegment StartX=3.03109 StartY=-1.75 StartZ=0 EndX=3.03109 EndY=1.75 EndZ=0
    g5: LineSegment StartX=3.03109 StartY=1.75 StartZ=0 EndX=1e-16 EndY=3.5 EndZ=0
    g6: Circle [constr] CenterX=0 CenterY=0 CenterZ=0 NormalX=0 NormalY=0 NormalZ=1 AngleXU=0 Radius=3.5
    g7: LineSegment StartX=4.96892 StartY=-1.75002 StartZ=0 EndX=8.00002 EndY=-3.5 EndZ=0
    g8: LineSegment StartX=8.00002 StartY=-3.5 StartZ=0 EndX=11.0311 EndY=-1.74998 EndZ=0
    g9: LineSegment StartX=11.0311 StartY=-1.74998 StartZ=0 EndX=11.0311 EndY=1.75002 EndZ=0
    g10: LineSegment StartX=11.0311 StartY=1.75002 StartZ=0 EndX=7.99998 EndY=3.5 EndZ=0
    g11: LineSegment StartX=7.99998 StartY=3.5 StartZ=0 EndX=4.9689 EndY=1.74998 EndZ=0
    g12: LineSegment StartX=4.9689 StartY=1.74998 StartZ=0 EndX=4.96892 EndY=-1.75002 EndZ=0
    g13: Circle [constr] CenterX=8 CenterY=0 CenterZ=0 NormalX=0 NormalY=0 NormalZ=1 AngleXU=0 Radius=3.5
    g14: LineSegment StartX=4.03109 StartY=3.5 StartZ=0 EndX=7.06218 EndY=5.25 EndZ=0
    g15: LineSegment StartX=7.06218 StartY=5.25 StartZ=0 EndX=7.06218 EndY=8.75 EndZ=0
    g16: LineSegment StartX=7.06218 StartY=8.75 StartZ=0 EndX=4.03109 EndY=10.5 EndZ=0
    g17: LineSegment StartX=4.03109 StartY=10.5 StartZ=0 EndX=1 EndY=8.75 EndZ=0
    g18: LineSegment StartX=1 StartY=8.75 StartZ=0 EndX=1 EndY=5.25 EndZ=0
    g19: LineSegment StartX=1 StartY=5.25 StartZ=0 EndX=4.03109 EndY=3.5 EndZ=0
    g20: Circle [constr] CenterX=4.03109 CenterY=7 CenterZ=0 NormalX=0 NormalY=0 NormalZ=1 AngleXU=0 Radius=3.5
    g21: LineSegment StartX=-1 StartY=5.25 StartZ=0 EndX=-1 EndY=8.75 EndZ=0
    g22: LineSegment StartX=-1 StartY=8.75 StartZ=0 EndX=-4.03109 EndY=10.5 EndZ=0
    g23: LineSegment StartX=-4.03109 StartY=10.5 StartZ=0 EndX=-7.06218 EndY=8.75 EndZ=0
    g24: LineSegment StartX=-7.06218 StartY=8.75 StartZ=0 EndX=-7.06218 EndY=5.25 EndZ=0
    g25: LineSegment StartX=-7.06218 StartY=5.25 StartZ=0 EndX=-4.03109 EndY=3.5 EndZ=0
    g26: LineSegment StartX=-4.03109 StartY=3.5 StartZ=0 EndX=-1 EndY=5.25 EndZ=0
    g27: Circle [constr] CenterX=-4.03109 CenterY=7 CenterZ=0 NormalX=0 NormalY=0 NormalZ=1 AngleXU=0 Radius=3.5
    g28: LineSegment StartX=-4.96891 StartY=-1.75 StartZ=0 EndX=-4.96891 EndY=1.75 EndZ=0
    g29: LineSegment StartX=-4.96891 StartY=1.75 StartZ=0 EndX=-8 EndY=3.5 EndZ=0
    g30: LineSegment StartX=-8 StartY=3.5 StartZ=0 EndX=-11.0311 EndY=1.75 EndZ=0
    g31: LineSegment StartX=-11.0311 StartY=1.75 StartZ=0 EndX=-11.0311 EndY=-1.75 EndZ=0
    g32: LineSegment StartX=-11.0311 StartY=-1.75 StartZ=0 EndX=-8 EndY=-3.5 EndZ=0
    g33: LineSegment StartX=-8 StartY=-3.5 StartZ=0 EndX=-4.96891 EndY=-1.75 EndZ=0
    g34: Circle [constr] CenterX=-8 CenterY=0 CenterZ=0 NormalX=0 NormalY=0 NormalZ=1 AngleXU=0 Radius=3.5
    g35: LineSegment StartX=-4.03109 StartY=-3.5 StartZ=0 EndX=-7.06218 EndY=-5.25 EndZ=0
    g36: LineSegment StartX=-7.06218 StartY=-5.25 StartZ=0 EndX=-7.06218 EndY=-8.75 EndZ=0
    g37: LineSegment StartX=-7.06218 StartY=-8.75 StartZ=0 EndX=-4.03109 EndY=-10.5 EndZ=0
    g38: LineSegment StartX=-4.03109 StartY=-10.5 StartZ=0 EndX=-1 EndY=-8.75 EndZ=0
    g39: LineSegment StartX=-1 StartY=-8.75 StartZ=0 EndX=-1 EndY=-5.25 EndZ=0
    g40: LineSegment StartX=-1 StartY=-5.25 StartZ=0 EndX=-4.03109 EndY=-3.5 EndZ=0
    g41: Circle [constr] CenterX=-4.03109 CenterY=-7 CenterZ=0 NormalX=0 NormalY=0 NormalZ=1 AngleXU=0 Radius=3.5
    g42: LineSegment StartX=4.03109 StartY=-3.5 StartZ=0 EndX=1 EndY=-5.25 EndZ=0
    g43: LineSegment StartX=1 StartY=-5.25 StartZ=0 EndX=1 EndY=-8.75 EndZ=0
    g44: LineSegment StartX=1 StartY=-8.75 StartZ=0 EndX=4.03109 EndY=-10.5 EndZ=0
    g45: LineSegment StartX=4.03109 StartY=-10.5 StartZ=0 EndX=7.06218 EndY=-8.75 EndZ=0
    g46: LineSegment StartX=7.06218 StartY=-8.75 StartZ=0 EndX=7.06218 EndY=-5.25 EndZ=0
    g47: LineSegment StartX=7.06218 StartY=-5.25 StartZ=0 EndX=4.03109 EndY=-3.5 EndZ=0
    g48: Circle [constr] CenterX=4.03109 CenterY=-7 CenterZ=0 NormalX=0 NormalY=0 NormalZ=1 AngleXU=0 Radius=3.5
  constraints (117):
    c: Coincident(g0,g1)
    c: Coincident(g1,g2)
    c: Coincident(g2,g3)
    c: Coincident(g3,g4)
    c: Coincident(g4,g5)
    c: Coincident(g5,g0)
    c: Equal(g0, g1-g5) x5
    c: PointOnObject(g0,g6)
    c: PointOnObject(g1,g6)
    c: PointOnObject(g2,g6)
    c: PointOnObject(g3,g6)
    c: PointOnObject(g4,g6)
    c: PointOnObject(g5,g6)
    c: Coincident(g6,g-1)
    c: Diameter(g6) = 7
    c: PointOnObject(g0,g-2)
    c: Coincident(g7,g8)
    c: Coincident(g8,g9)
    c: Coincident(g9,g10)
    c: Coincident(g10,g11)
    c: Coincident(g11,g12)
    c: Coincident(g12,g7)
    c: Equal(g7, g8-g12) x5
    c: PointOnObject(g7,g13)
    c: PointOnObject(g8,g13)
    c: PointOnObject(g9,g13)
    c: PointOnObject(g10,g13)
    c: PointOnObject(g11,g13)
    c: PointOnObject(g12,g13)
    c: PointOnObject(g13,g-1)
    c: Diameter(g13) = 7
    c: Distance(g6,g13) = 8
    c: Horizontal(g0,g10)
    c: Coincident(g14,g15)
    c: Coincident(g15,g16)
    c: Coincident(g16,g17)
    c: Coincident(g17,g18)
    c: Coincident(g18,g19)
    c: Coincident(g19,g14)
    c: Equal(g14, g15-g19) x5
    c: PointOnObject(g14,g20)
    c: PointOnObject(g15,g20)
    c: PointOnObject(g16,g20)
    c: PointOnObject(g17,g20)
    c: PointOnObject(g18,g20)
    c: PointOnObject(g19,g20)
    c: Diameter(g20) = 7
    c: DistanceY(g-1,g20) = 7
    c: Vertical(g18)
    c: Distance(g17,g-2) = 1
    c: Coincident(g21,g22)
    c: Coincident(g22,g23)
    c: Coincident(g23,g24)
    c: Coincident(g24,g25)
    c: Coincident(g25,g26)
    c: Coincident(g26,g21)
    c: Equal(g21, g22-g26) x5
    c: PointOnObject(g21,g27)
    c: PointOnObject(g22,g27)
    c: PointOnObject(g23,g27)
    c: PointOnObject(g24,g27)
    c: PointOnObject(g25,g27)
    c: PointOnObject(g26,g27)
    c: Diameter(g27) = 7
    c: DistanceY(g-1,g27) = 7
    c: DistanceX(g21,g-1) = 1
    c: Vertical(g21)
    c: Coincident(g28,g29)
    c: Coincident(g29,g30)
    c: Coincident(g30,g31)
    c: Coincident(g31,g32)
    c: Coincident(g32,g33)
    c: Coincident(g33,g28)
    c: Equal(g28, g29-g33) x5
    c: PointOnObject(g28,g34)
    c: PointOnObject(g29,g34)
    c: PointOnObject(g30,g34)
    c: PointOnObject(g31,g34)
    c: PointOnObject(g32,g34)
    c: PointOnObject(g33,g34)
    c: PointOnObject(g34,g-1)
    c: Diameter(g34) = 7
    c: Vertical(g31)
    c: DistanceX(g34,g-1) = 8
    c: Coincident(g35,g36)
    c: Coincident(g36,g37)
    c: Coincident(g37,g38)
    c: Coincident(g38,g39)
    c: Coincident(g39,g40)
    c: Coincident(g40,g35)
    c: Equal(g35, g36-g40) x5
    c: PointOnObject(g35,g41)
    c: PointOnObject(g36,g41)
    c: PointOnObject(g37,g41)
    c: PointOnObject(g38,g41)
    c: PointOnObject(g39,g41)
    c: PointOnObject(g40,g41)
    c: Coincident(g42,g43)
    c: Coincident(g43,g44)
    c: Coincident(g44,g45)
    c: Coincident(g45,g46)
    c: Coincident(g46,g47)
    c: Coincident(g47,g42)
    c: Equal(g42, g43-g47) x5
    c: PointOnObject(g42,g48)
    c: PointOnObject(g43,g48)
    c: PointOnObject(g44,g48)
    c: PointOnObject(g45,g48)
    c: PointOnObject(g46,g48)
    c: PointOnObject(g47,g48)
    c: Equal(g41,g48)
    c: Diameter(g41) = 7
    c: Vertical(g39)
    c: Vertical(g43)
    c: Distance(g-2,g39) = 1
    c: Symmetric(g38,g43,g-2)
    c: Distance(g41,g-1) = 7
FEATURE [Part::Extrusion] Extrude519  label="hex134"
  Base = -> Sketch527
  Dir = (0,-1,2e-16)
  DirMode = 2
  FaceMakerClass = Part::FaceMakerBullseye
  FaceMakerMode = 3
  LengthFwd = 10
  LengthRev = 0
  Placement = pos=(-16,0,-56) rot=(0,0,1;0rad)
  Solid = true
  Symmetric = false
FEATURE [Sketcher::SketchObject] Sketch528
  ArcFitTolerance = 1e-06
  FullyConstrained = true
  MakeInternals = false
  Placement = pos=(0,0,0) rot=(1,0,0;1.5708rad)
  sketch-geometry (49):
    g0: LineSegment StartX=1e-16 StartY=3.5 StartZ=0 EndX=-3.03109 EndY=1.75 EndZ=0
    g1: LineSegment StartX=-3.03109 StartY=1.75 StartZ=0 EndX=-3.03109 EndY=-1.75 EndZ=0
    g2: LineSegment StartX=-3.03109 StartY=-1.75 StartZ=0 EndX=-1e-16 EndY=-3.5 EndZ=0
    g3: LineSegment StartX=-1e-16 StartY=-3.5 StartZ=0 EndX=3.03109 EndY=-1.75 EndZ=0
    g4: LineSegment StartX=3.03109 StartY=-1.75 StartZ=0 EndX=3.03109 EndY=1.75 EndZ=0
    g5: LineSegment StartX=3.03109 StartY=1.75 StartZ=0 EndX=1e-16 EndY=3.5 EndZ=0
    g6: Circle [constr] CenterX=0 CenterY=0 CenterZ=0 NormalX=0 NormalY=0 NormalZ=1 AngleXU=0 Radius=3.5
    g7: LineSegment StartX=4.96892 StartY=-1.75002 StartZ=0 EndX=8.00002 EndY=-3.5 EndZ=0
    g8: LineSegment StartX=8.00002 StartY=-3.5 StartZ=0 EndX=11.0311 EndY=-1.74998 EndZ=0
    g9: LineSegment StartX=11.0311 StartY=-1.74998 StartZ=0 EndX=11.0311 EndY=1.75002 EndZ=0
    g10: LineSegment StartX=11.0311 StartY=1.75002 StartZ=0 EndX=7.99998 EndY=3.5 EndZ=0
    g11: LineSegment StartX=7.99998 StartY=3.5 StartZ=0 EndX=4.9689 EndY=1.74998 EndZ=0
    g12: LineSegment StartX=4.9689 StartY=1.74998 StartZ=0 EndX=4.96892 EndY=-1.75002 EndZ=0
    g13: Circle [constr] CenterX=8 CenterY=0 CenterZ=0 NormalX=0 NormalY=0 NormalZ=1 AngleXU=0 Radius=3.5
    g14: LineSegment StartX=4.03109 StartY=3.5 StartZ=0 EndX=7.06218 EndY=5.25 EndZ=0
    g15: LineSegment StartX=7.06218 StartY=5.25 StartZ=0 EndX=7.06218 EndY=8.75 EndZ=0
    g16: LineSegment StartX=7.06218 StartY=8.75 StartZ=0 EndX=4.03109 EndY=10.5 EndZ=0
    g17: LineSegment StartX=4.03109 StartY=10.5 StartZ=0 EndX=1 EndY=8.75 EndZ=0
    g18: LineSegment StartX=1 StartY=8.75 StartZ=0 EndX=1 EndY=5.25 EndZ=0
    g19: LineSegment StartX=1 StartY=5.25 StartZ=0 EndX=4.03109 EndY=3.5 EndZ=0
    g20: Circle [constr] CenterX=4.03109 CenterY=7 CenterZ=0 NormalX=0 NormalY=0 NormalZ=1 AngleXU=0 Radius=3.5
    g21: LineSegment StartX=-1 StartY=5.25 StartZ=0 EndX=-1 EndY=8.75 EndZ=0
    g22: LineSegment StartX=-1 StartY=8.75 StartZ=0 EndX=-4.03109 EndY=10.5 EndZ=0
    g23: LineSegment StartX=-4.03109 StartY=10.5 StartZ=0 EndX=-7.06218 EndY=8.75 EndZ=0
    g24: LineSegment StartX=-7.06218 StartY=8.75 StartZ=0 EndX=-7.06218 EndY=5.25 EndZ=0
    g25: LineSegment StartX=-7.06218 StartY=5.25 StartZ=0 EndX=-4.03109 EndY=3.5 EndZ=0
    g26: LineSegment StartX=-4.03109 StartY=3.5 StartZ=0 EndX=-1 EndY=5.25 EndZ=0
    g27: Circle [constr] CenterX=-4.03109 CenterY=7 CenterZ=0 NormalX=0 NormalY=0 NormalZ=1 AngleXU=0 Radius=3.5
    g28: LineSegment StartX=-4.96891 StartY=-1.75 StartZ=0 EndX=-4.96891 EndY=1.75 EndZ=0
    g29: LineSegment StartX=-4.96891 StartY=1.75 StartZ=0 EndX=-8 EndY=3.5 EndZ=0
    g30: LineSegment StartX=-8 StartY=3.5 StartZ=0 EndX=-11.0311 EndY=1.75 EndZ=0
    g31: LineSegment StartX=-11.0311 StartY=1.75 StartZ=0 EndX=-11.0311 EndY=-1.75 EndZ=0
    g32: LineSegment StartX=-11.0311 StartY=-1.75 StartZ=0 EndX=-8 EndY=-3.5 EndZ=0
    g33: LineSegment StartX=-8 StartY=-3.5 StartZ=0 EndX=-4.96891 EndY=-1.75 EndZ=0
    g34: Circle [constr] CenterX=-8 CenterY=0 CenterZ=0 NormalX=0 NormalY=0 NormalZ=1 AngleXU=0 Radius=3.5
    g35: LineSegment StartX=-4.03109 StartY=-3.5 StartZ=0 EndX=-7.06218 EndY=-5.25 EndZ=0
    g36: LineSegment StartX=-7.06218 StartY=-5.25 StartZ=0 EndX=-7.06218 EndY=-8.75 EndZ=0
    g37: LineSegment StartX=-7.06218 StartY=-8.75 StartZ=0 EndX=-4.03109 EndY=-10.5 EndZ=0
    g38: LineSegment StartX=-4.03109 StartY=-10.5 StartZ=0 EndX=-1 EndY=-8.75 EndZ=0
    g39: LineSegment StartX=-1 StartY=-8.75 StartZ=0 EndX=-1 EndY=-5.25 EndZ=0
    g40: LineSegment StartX=-1 StartY=-5.25 StartZ=0 EndX=-4.03109 EndY=-3.5 EndZ=0
    g41: Circle [constr] CenterX=-4.03109 CenterY=-7 CenterZ=0 NormalX=0 NormalY=0 NormalZ=1 AngleXU=0 Radius=3.5
    g42: LineSegment StartX=4.03109 StartY=-3.5 StartZ=0 EndX=1 EndY=-5.25 EndZ=0
    g43: LineSegment StartX=1 StartY=-5.25 StartZ=0 EndX=1 EndY=-8.75 EndZ=0
    g44: LineSegment StartX=1 StartY=-8.75 StartZ=0 EndX=4.03109 EndY=-10.5 EndZ=0
    g45: LineSegment StartX=4.03109 StartY=-10.5 StartZ=0 EndX=7.06218 EndY=-8.75 EndZ=0
    g46: LineSegment StartX=7.06218 StartY=-8.75 StartZ=0 EndX=7.06218 EndY=-5.25 EndZ=0
    g47: LineSegment StartX=7.06218 StartY=-5.25 StartZ=0 EndX=4.03109 EndY=-3.5 EndZ=0
    g48: Circle [constr] CenterX=4.03109 CenterY=-7 CenterZ=0 NormalX=0 NormalY=0 NormalZ=1 AngleXU=0 Radius=3.5
  constraints (117):
    c: Coincident(g0,g1)
    c: Coincident(g1,g2)
    c: Coincident(g2,g3)
    c: Coincident(g3,g4)
    c: Coincident(g4,g5)
    c: Coincident(g5,g0)
    c: Equal(g0, g1-g5) x5
    c: PointOnObject(g0,g6)
    c: PointOnObject(g1,g6)
    c: PointOnObject(g2,g6)
    c: PointOnObject(g3,g6)
    c: PointOnObject(g4,g6)
    c: PointOnObject(g5,g6)
    c: Coincident(g6,g-1)
    c: Diameter(g6) = 7
    c: PointOnObject(g0,g-2)
    c: Coincident(g7,g8)
    c: Coincident(g8,g9)
    c: Coincident(g9,g10)
    c: Coincident(g10,g11)
    c: Coincident(g11,g12)
    c: Coincident(g12,g7)
    c: Equal(g7, g8-g12) x5
    c: PointOnObject(g7,g13)
    c: PointOnObject(g8,g13)
    c: PointOnObject(g9,g13)
    c: PointOnObject(g10,g13)
    c: PointOnObject(g11,g13)
    c: PointOnObject(g12,g13)
    c: PointOnObject(g13,g-1)
    c: Diameter(g13) = 7
    c: Distance(g6,g13) = 8
    c: Horizontal(g0,g10)
    c: Coincident(g14,g15)
    c: Coincident(g15,g16)
    c: Coincident(g16,g17)
    c: Coincident(g17,g18)
    c: Coincident(g18,g19)
    c: Coincident(g19,g14)
    c: Equal(g14, g15-g19) x5
    c: PointOnObject(g14,g20)
    c: PointOnObject(g15,g20)
    c: PointOnObject(g16,g20)
    c: PointOnObject(g17,g20)
    c: PointOnObject(g18,g20)
    c: PointOnObject(g19,g20)
    c: Diameter(g20) = 7
    c: DistanceY(g-1,g20) = 7
    c: Vertical(g18)
    c: Distance(g17,g-2) = 1
    c: Coincident(g21,g22)
    c: Coincident(g22,g23)
    c: Coincident(g23,g24)
    c: Coincident(g24,g25)
    c: Coincident(g25,g26)
    c: Coincident(g26,g21)
    c: Equal(g21, g22-g26) x5
    c: PointOnObject(g21,g27)
    c: PointOnObject(g22,g27)
    c: PointOnObject(g23,g27)
    c: PointOnObject(g24,g27)
    c: PointOnObject(g25,g27)
    c: PointOnObject(g26,g27)
    c: Diameter(g27) = 7
    c: DistanceY(g-1,g27) = 7
    c: DistanceX(g21,g-1) = 1
    c: Vertical(g21)
    c: Coincident(g28,g29)
    c: Coincident(g29,g30)
    c: Coincident(g30,g31)
    c: Coincident(g31,g32)
    c: Coincident(g32,g33)
    c: Coincident(g33,g28)
    c: Equal(g28, g29-g33) x5
    c: PointOnObject(g28,g34)
    c: PointOnObject(g29,g34)
    c: PointOnObject(g30,g34)
    c: PointOnObject(g31,g34)
    c: PointOnObject(g32,g34)
    c: PointOnObject(g33,g34)
    c: PointOnObject(g34,g-1)
    c: Diameter(g34) = 7
    c: Vertical(g31)
    c: DistanceX(g34,g-1) = 8
    c: Coincident(g35,g36)
    c: Coincident(g36,g37)
    c: Coincident(g37,g38)
    c: Coincident(g38,g39)
    c: Coincident(g39,g40)
    c: Coincident(g40,g35)
    c: Equal(g35, g36-g40) x5
    c: PointOnObject(g35,g41)
    c: PointOnObject(g36,g41)
    c: PointOnObject(g37,g41)
    c: PointOnObject(g38,g41)
    c: PointOnObject(g39,g41)
    c: PointOnObject(g40,g41)
    c: Coincident(g42,g43)
    c: Coincident(g43,g44)
    c: Coincident(g44,g45)
    c: Coincident(g45,g46)
    c: Coincident(g46,g47)
    c: Coincident(g47,g42)
    c: Equal(g42, g43-g47) x5
    c: PointOnObject(g42,g48)
    c: PointOnObject(g43,g48)
    c: PointOnObject(g44,g48)
    c: PointOnObject(g45,g48)
    c: PointOnObject(g46,g48)
    c: PointOnObject(g47,g48)
    c: Equal(g41,g48)
    c: Diameter(g41) = 7
    c: Vertical(g39)
    c: Vertical(g43)
    c: Distance(g-2,g39) = 1
    c: Symmetric(g38,g43,g-2)
    c: Distance(g41,g-1) = 7
FEATURE [Part::Extrusion] Extrude520  label="hex135"
  Base = -> Sketch528
  Dir = (0,-1,2e-16)
  DirMode = 2
  FaceMakerClass = Part::FaceMakerBullseye
  FaceMakerMode = 3
  LengthFwd = 10
  LengthRev = 0
  Placement = pos=(8,0,-56) rot=(0,0,1;0rad)
  Solid = true
  Symmetric = false
FEATURE [Sketcher::SketchObject] Sketch529
  ArcFitTolerance = 1e-06
  FullyConstrained = true
  MakeInternals = false
  Placement = pos=(0,0,0) rot=(1,0,0;1.5708rad)
  sketch-geometry (49):
    g0: LineSegment StartX=1e-16 StartY=3.5 StartZ=0 EndX=-3.03109 EndY=1.75 EndZ=0
    g1: LineSegment StartX=-3.03109 StartY=1.75 StartZ=0 EndX=-3.03109 EndY=-1.75 EndZ=0
    g2: LineSegment StartX=-3.03109 StartY=-1.75 StartZ=0 EndX=-1e-16 EndY=-3.5 EndZ=0
    g3: LineSegment StartX=-1e-16 StartY=-3.5 StartZ=0 EndX=3.03109 EndY=-1.75 EndZ=0
    g4: LineSegment StartX=3.03109 StartY=-1.75 StartZ=0 EndX=3.03109 EndY=1.75 EndZ=0
    g5: LineSegment StartX=3.03109 StartY=1.75 StartZ=0 EndX=1e-16 EndY=3.5 EndZ=0
    g6: Circle [constr] CenterX=0 CenterY=0 CenterZ=0 NormalX=0 NormalY=0 NormalZ=1 AngleXU=0 Radius=3.5
    g7: LineSegment StartX=4.96892 StartY=-1.75002 StartZ=0 EndX=8.00002 EndY=-3.5 EndZ=0
    g8: LineSegment StartX=8.00002 StartY=-3.5 StartZ=0 EndX=11.0311 EndY=-1.74998 EndZ=0
    g9: LineSegment StartX=11.0311 StartY=-1.74998 StartZ=0 EndX=11.0311 EndY=1.75002 EndZ=0
    g10: LineSegment StartX=11.0311 StartY=1.75002 StartZ=0 EndX=7.99998 EndY=3.5 EndZ=0
    g11: LineSegment StartX=7.99998 StartY=3.5 StartZ=0 EndX=4.9689 EndY=1.74998 EndZ=0
    g12: LineSegment StartX=4.9689 StartY=1.74998 StartZ=0 EndX=4.96892 EndY=-1.75002 EndZ=0
    g13: Circle [constr] CenterX=8 CenterY=0 CenterZ=0 NormalX=0 NormalY=0 NormalZ=1 AngleXU=0 Radius=3.5
    g14: LineSegment StartX=4.03109 StartY=3.5 StartZ=0 EndX=7.06218 EndY=5.25 EndZ=0
    g15: LineSegment StartX=7.06218 StartY=5.25 StartZ=0 EndX=7.06218 EndY=8.75 EndZ=0
    g16: LineSegment StartX=7.06218 StartY=8.75 StartZ=0 EndX=4.03109 EndY=10.5 EndZ=0
    g17: LineSegment StartX=4.03109 StartY=10.5 StartZ=0 EndX=1 EndY=8.75 EndZ=0
    g18: LineSegment StartX=1 StartY=8.75 StartZ=0 EndX=1 EndY=5.25 EndZ=0
    g19: LineSegment StartX=1 StartY=5.25 StartZ=0 EndX=4.03109 EndY=3.5 EndZ=0
    g20: Circle [constr] CenterX=4.03109 CenterY=7 CenterZ=0 NormalX=0 NormalY=0 NormalZ=1 AngleXU=0 Radius=3.5
    g21: LineSegment StartX=-1 StartY=5.25 StartZ=0 EndX=-1 EndY=8.75 EndZ=0
    g22: LineSegment StartX=-1 StartY=8.75 StartZ=0 EndX=-4.03109 EndY=10.5 EndZ=0
    g23: LineSegment StartX=-4.03109 StartY=10.5 StartZ=0 EndX=-7.06218 EndY=8.75 EndZ=0
    g24: LineSegment StartX=-7.06218 StartY=8.75 StartZ=0 EndX=-7.06218 EndY=5.25 EndZ=0
    g25: LineSegment StartX=-7.06218 StartY=5.25 StartZ=0 EndX=-4.03109 EndY=3.5 EndZ=0
    g26: LineSegment StartX=-4.03109 StartY=3.5 StartZ=0 EndX=-1 EndY=5.25 EndZ=0
    g27: Circle [constr] CenterX=-4.03109 CenterY=7 CenterZ=0 NormalX=0 NormalY=0 NormalZ=1 AngleXU=0 Radius=3.5
    g28: LineSegment StartX=-4.96891 StartY=-1.75 StartZ=0 EndX=-4.96891 EndY=1.75 EndZ=0
    g29: LineSegment StartX=-4.96891 StartY=1.75 StartZ=0 EndX=-8 EndY=3.5 EndZ=0
    g30: LineSegment StartX=-8 StartY=3.5 StartZ=0 EndX=-11.0311 EndY=1.75 EndZ=0
    g31: LineSegment StartX=-11.0311 StartY=1.75 StartZ=0 EndX=-11.0311 EndY=-1.75 EndZ=0
    g32: LineSegment StartX=-11.0311 StartY=-1.75 StartZ=0 EndX=-8 EndY=-3.5 EndZ=0
    g33: LineSegment StartX=-8 StartY=-3.5 StartZ=0 EndX=-4.96891 EndY=-1.75 EndZ=0
    g34: Circle [constr] CenterX=-8 CenterY=0 CenterZ=0 NormalX=0 NormalY=0 NormalZ=1 AngleXU=0 Radius=3.5
    g35: LineSegment StartX=-4.03109 StartY=-3.5 StartZ=0 EndX=-7.06218 EndY=-5.25 EndZ=0
    g36: LineSegment StartX=-7.06218 StartY=-5.25 StartZ=0 EndX=-7.06218 EndY=-8.75 EndZ=0
    g37: LineSegment StartX=-7.06218 StartY=-8.75 StartZ=0 EndX=-4.03109 EndY=-10.5 EndZ=0
    g38: LineSegment StartX=-4.03109 StartY=-10.5 StartZ=0 EndX=-1 EndY=-8.75 EndZ=0
    g39: LineSegment StartX=-1 StartY=-8.75 StartZ=0 EndX=-1 EndY=-5.25 EndZ=0
    g40: LineSegment StartX=-1 StartY=-5.25 StartZ=0 EndX=-4.03109 EndY=-3.5 EndZ=0
    g41: Circle [constr] CenterX=-4.03109 CenterY=-7 CenterZ=0 NormalX=0 NormalY=0 NormalZ=1 AngleXU=0 Radius=3.5
    g42: LineSegment StartX=4.03109 StartY=-3.5 StartZ=0 EndX=1 EndY=-5.25 EndZ=0
    g43: LineSegment StartX=1 StartY=-5.25 StartZ=0 EndX=1 EndY=-8.75 EndZ=0
    g44: LineSegment StartX=1 StartY=-8.75 StartZ=0 EndX=4.03109 EndY=-10.5 EndZ=0
    g45: LineSegment StartX=4.03109 StartY=-10.5 StartZ=0 EndX=7.06218 EndY=-8.75 EndZ=0
    g46: LineSegment StartX=7.06218 StartY=-8.75 StartZ=0 EndX=7.06218 EndY=-5.25 EndZ=0
    g47: LineSegment StartX=7.06218 StartY=-5.25 StartZ=0 EndX=4.03109 EndY=-3.5 EndZ=0
    g48: Circle [constr] CenterX=4.03109 CenterY=-7 CenterZ=0 NormalX=0 NormalY=0 NormalZ=1 AngleXU=0 Radius=3.5
  constraints (117):
    c: Coincident(g0,g1)
    c: Coincident(g1,g2)
    c: Coincident(g2,g3)
    c: Coincident(g3,g4)
    c: Coincident(g4,g5)
    c: Coincident(g5,g0)
    c: Equal(g0, g1-g5) x5
    c: PointOnObject(g0,g6)
    c: PointOnObject(g1,g6)
    c: PointOnObject(g2,g6)
    c: PointOnObject(g3,g6)
    c: PointOnObject(g4,g6)
    c: PointOnObject(g5,g6)
    c: Coincident(g6,g-1)
    c: Diameter(g6) = 7
    c: PointOnObject(g0,g-2)
    c: Coincident(g7,g8)
    c: Coincident(g8,g9)
    c: Coincident(g9,g10)
    c: Coincident(g10,g11)
    c: Coincident(g11,g12)
    c: Coincident(g12,g7)
    c: Equal(g7, g8-g12) x5
    c: PointOnObject(g7,g13)
    c: PointOnObject(g8,g13)
    c: PointOnObject(g9,g13)
    c: PointOnObject(g10,g13)
    c: PointOnObject(g11,g13)
    c: PointOnObject(g12,g13)
    c: PointOnObject(g13,g-1)
    c: Diameter(g13) = 7
    c: Distance(g6,g13) = 8
    c: Horizontal(g0,g10)
    c: Coincident(g14,g15)
    c: Coincident(g15,g16)
    c: Coincident(g16,g17)
    c: Coincident(g17,g18)
    c: Coincident(g18,g19)
    c: Coincident(g19,g14)
    c: Equal(g14, g15-g19) x5
    c: PointOnObject(g14,g20)
    c: PointOnObject(g15,g20)
    c: PointOnObject(g16,g20)
    c: PointOnObject(g17,g20)
    c: PointOnObject(g18,g20)
    c: PointOnObject(g19,g20)
    c: Diameter(g20) = 7
    c: DistanceY(g-1,g20) = 7
    c: Vertical(g18)
    c: Distance(g17,g-2) = 1
    c: Coincident(g21,g22)
    c: Coincident(g22,g23)
    c: Coincident(g23,g24)
    c: Coincident(g24,g25)
    c: Coincident(g25,g26)
    c: Coincident(g26,g21)
    c: Equal(g21, g22-g26) x5
    c: PointOnObject(g21,g27)
    c: PointOnObject(g22,g27)
    c: PointOnObject(g23,g27)
    c: PointOnObject(g24,g27)
    c: PointOnObject(g25,g27)
    c: PointOnObject(g26,g27)
    c: Diameter(g27) = 7
    c: DistanceY(g-1,g27) = 7
    c: DistanceX(g21,g-1) = 1
    c: Vertical(g21)
    c: Coincident(g28,g29)
    c: Coincident(g29,g30)
    c: Coincident(g30,g31)
    c: Coincident(g31,g32)
    c: Coincident(g32,g33)
    c: Coincident(g33,g28)
    c: Equal(g28, g29-g33) x5
    c: PointOnObject(g28,g34)
    c: PointOnObject(g29,g34)
    c: PointOnObject(g30,g34)
    c: PointOnObject(g31,g34)
    c: PointOnObject(g32,g34)
    c: PointOnObject(g33,g34)
    c: PointOnObject(g34,g-1)
    c: Diameter(g34) = 7
    c: Vertical(g31)
    c: DistanceX(g34,g-1) = 8
    c: Coincident(g35,g36)
    c: Coincident(g36,g37)
    c: Coincident(g37,g38)
    c: Coincident(g38,g39)
    c: Coincident(g39,g40)
    c: Coincident(g40,g35)
    c: Equal(g35, g36-g40) x5
    c: PointOnObject(g35,g41)
    c: PointOnObject(g36,g41)
    c: PointOnObject(g37,g41)
    c: PointOnObject(g38,g41)
    c: PointOnObject(g39,g41)
    c: PointOnObject(g40,g41)
    c: Coincident(g42,g43)
    c: Coincident(g43,g44)
    c: Coincident(g44,g45)
    c: Coincident(g45,g46)
    c: Coincident(g46,g47)
    c: Coincident(g47,g42)
    c: Equal(g42, g43-g47) x5
    c: PointOnObject(g42,g48)
    c: PointOnObject(g43,g48)
    c: PointOnObject(g44,g48)
    c: PointOnObject(g45,g48)
    c: PointOnObject(g46,g48)
    c: PointOnObject(g47,g48)
    c: Equal(g41,g48)
    c: Diameter(g41) = 7
    c: Vertical(g39)
    c: Vertical(g43)
    c: Distance(g-2,g39) = 1
    c: Symmetric(g38,g43,g-2)
    c: Distance(g41,g-1) = 7
FEATURE [Part::Extrusion] Extrude521  label="hex136"
  Base = -> Sketch529
  Dir = (0,-1,2e-16)
  DirMode = 2
  FaceMakerClass = Part::FaceMakerBullseye
  FaceMakerMode = 3
  LengthFwd = 10
  LengthRev = 0
  Placement = pos=(28,0,-49) rot=(0,0,1;0rad)
  Solid = true
  Symmetric = false
FEATURE [Sketcher::SketchObject] Sketch530
  ArcFitTolerance = 1e-06
  FullyConstrained = true
  MakeInternals = false
  Placement = pos=(0,0,0) rot=(1,0,0;1.5708rad)
  sketch-geometry (49):
    g0: LineSegment StartX=1e-16 StartY=3.5 StartZ=0 EndX=-3.03109 EndY=1.75 EndZ=0
    g1: LineSegment StartX=-3.03109 StartY=1.75 StartZ=0 EndX=-3.03109 EndY=-1.75 EndZ=0
    g2: LineSegment StartX=-3.03109 StartY=-1.75 StartZ=0 EndX=-1e-16 EndY=-3.5 EndZ=0
    g3: LineSegment StartX=-1e-16 StartY=-3.5 StartZ=0 EndX=3.03109 EndY=-1.75 EndZ=0
    g4: LineSegment StartX=3.03109 StartY=-1.75 StartZ=0 EndX=3.03109 EndY=1.75 EndZ=0
    g5: LineSegment StartX=3.03109 StartY=1.75 StartZ=0 EndX=1e-16 EndY=3.5 EndZ=0
    g6: Circle [constr] CenterX=0 CenterY=0 CenterZ=0 NormalX=0 NormalY=0 NormalZ=1 AngleXU=0 Radius=3.5
    g7: LineSegment StartX=4.96892 StartY=-1.75002 StartZ=0 EndX=8.00002 EndY=-3.5 EndZ=0
    g8: LineSegment StartX=8.00002 StartY=-3.5 StartZ=0 EndX=11.0311 EndY=-1.74998 EndZ=0
    g9: LineSegment StartX=11.0311 StartY=-1.74998 StartZ=0 EndX=11.0311 EndY=1.75002 EndZ=0
    g10: LineSegment StartX=11.0311 StartY=1.75002 StartZ=0 EndX=7.99998 EndY=3.5 EndZ=0
    g11: LineSegment StartX=7.99998 StartY=3.5 StartZ=0 EndX=4.9689 EndY=1.74998 EndZ=0
    g12: LineSegment StartX=4.9689 StartY=1.74998 StartZ=0 EndX=4.96892 EndY=-1.75002 EndZ=0
    g13: Circle [constr] CenterX=8 CenterY=0 CenterZ=0 NormalX=0 NormalY=0 NormalZ=1 AngleXU=0 Radius=3.5
    g14: LineSegment StartX=4.03109 StartY=3.5 StartZ=0 EndX=7.06218 EndY=5.25 EndZ=0
    g15: LineSegment StartX=7.06218 StartY=5.25 StartZ=0 EndX=7.06218 EndY=8.75 EndZ=0
    g16: LineSegment StartX=7.06218 StartY=8.75 StartZ=0 EndX=4.03109 EndY=10.5 EndZ=0
    g17: LineSegment StartX=4.03109 StartY=10.5 StartZ=0 EndX=1 EndY=8.75 EndZ=0
    g18: LineSegment StartX=1 StartY=8.75 StartZ=0 EndX=1 EndY=5.25 EndZ=0
    g19: LineSegment StartX=1 StartY=5.25 StartZ=0 EndX=4.03109 EndY=3.5 EndZ=0
    g20: Circle [constr] CenterX=4.03109 CenterY=7 CenterZ=0 NormalX=0 NormalY=0 NormalZ=1 AngleXU=0 Radius=3.5
    g21: LineSegment StartX=-1 StartY=5.25 StartZ=0 EndX=-1 EndY=8.75 EndZ=0
    g22: LineSegment StartX=-1 StartY=8.75 StartZ=0 EndX=-4.03109 EndY=10.5 EndZ=0
    g23: LineSegment StartX=-4.03109 StartY=10.5 StartZ=0 EndX=-7.06218 EndY=8.75 EndZ=0
    g24: LineSegment StartX=-7.06218 StartY=8.75 StartZ=0 EndX=-7.06218 EndY=5.25 EndZ=0
    g25: LineSegment StartX=-7.06218 StartY=5.25 StartZ=0 EndX=-4.03109 EndY=3.5 EndZ=0
    g26: LineSegment StartX=-4.03109 StartY=3.5 StartZ=0 EndX=-1 EndY=5.25 EndZ=0
    g27: Circle [constr] CenterX=-4.03109 CenterY=7 CenterZ=0 NormalX=0 NormalY=0 NormalZ=1 AngleXU=0 Radius=3.5
    g28: LineSegment StartX=-4.96891 StartY=-1.75 StartZ=0 EndX=-4.96891 EndY=1.75 EndZ=0
    g29: LineSegment StartX=-4.96891 StartY=1.75 StartZ=0 EndX=-8 EndY=3.5 EndZ=0
    g30: LineSegment StartX=-8 StartY=3.5 StartZ=0 EndX=-11.0311 EndY=1.75 EndZ=0
    g31: LineSegment StartX=-11.0311 StartY=1.75 StartZ=0 EndX=-11.0311 EndY=-1.75 EndZ=0
    g32: LineSegment StartX=-11.0311 StartY=-1.75 StartZ=0 EndX=-8 EndY=-3.5 EndZ=0
    g33: LineSegment StartX=-8 StartY=-3.5 StartZ=0 EndX=-4.96891 EndY=-1.75 EndZ=0
    g34: Circle [constr] CenterX=-8 CenterY=0 CenterZ=0 NormalX=0 NormalY=0 NormalZ=1 AngleXU=0 Radius=3.5
    g35: LineSegment StartX=-4.03109 StartY=-3.5 StartZ=0 EndX=-7.06218 EndY=-5.25 EndZ=0
    g36: LineSegment StartX=-7.06218 StartY=-5.25 StartZ=0 EndX=-7.06218 EndY=-8.75 EndZ=0
    g37: LineSegment StartX=-7.06218 StartY=-8.75 StartZ=0 EndX=-4.03109 EndY=-10.5 EndZ=0
    g38: LineSegment StartX=-4.03109 StartY=-10.5 StartZ=0 EndX=-1 EndY=-8.75 EndZ=0
    g39: LineSegment StartX=-1 StartY=-8.75 StartZ=0 EndX=-1 EndY=-5.25 EndZ=0
    g40: LineSegment StartX=-1 StartY=-5.25 StartZ=0 EndX=-4.03109 EndY=-3.5 EndZ=0
    g41: Circle [constr] CenterX=-4.03109 CenterY=-7 CenterZ=0 NormalX=0 NormalY=0 NormalZ=1 AngleXU=0 Radius=3.5
    g42: LineSegment StartX=4.03109 StartY=-3.5 StartZ=0 EndX=1 EndY=-5.25 EndZ=0
    g43: LineSegment StartX=1 StartY=-5.25 StartZ=0 EndX=1 EndY=-8.75 EndZ=0
    g44: LineSegment StartX=1 StartY=-8.75 StartZ=0 EndX=4.03109 EndY=-10.5 EndZ=0
    g45: LineSegment StartX=4.03109 StartY=-10.5 StartZ=0 EndX=7.06218 EndY=-8.75 EndZ=0
    g46: LineSegment StartX=7.06218 StartY=-8.75 StartZ=0 EndX=7.06218 EndY=-5.25 EndZ=0
    g47: LineSegment StartX=7.06218 StartY=-5.25 StartZ=0 EndX=4.03109 EndY=-3.5 EndZ=0
    g48: Circle [constr] CenterX=4.03109 CenterY=-7 CenterZ=0 NormalX=0 NormalY=0 NormalZ=1 AngleXU=0 Radius=3.5
  constraints (117):
    c: Coincident(g0,g1)
    c: Coincident(g1,g2)
    c: Coincident(g2,g3)
    c: Coincident(g3,g4)
    c: Coincident(g4,g5)
    c: Coincident(g5,g0)
    c: Equal(g0, g1-g5) x5
    c: PointOnObject(g0,g6)
    c: PointOnObject(g1,g6)
    c: PointOnObject(g2,g6)
    c: PointOnObject(g3,g6)
    c: PointOnObject(g4,g6)
    c: PointOnObject(g5,g6)
    c: Coincident(g6,g-1)
    c: Diameter(g6) = 7
    c: PointOnObject(g0,g-2)
    c: Coincident(g7,g8)
    c: Coincident(g8,g9)
    c: Coincident(g9,g10)
    c: Coincident(g10,g11)
    c: Coincident(g11,g12)
    c: Coincident(g12,g7)
    c: Equal(g7, g8-g12) x5
    c: PointOnObject(g7,g13)
    c: PointOnObject(g8,g13)
    c: PointOnObject(g9,g13)
    c: PointOnObject(g10,g13)
    c: PointOnObject(g11,g13)
    c: PointOnObject(g12,g13)
    c: PointOnObject(g13,g-1)
    c: Diameter(g13) = 7
    c: Distance(g6,g13) = 8
    c: Horizontal(g0,g10)
    c: Coincident(g14,g15)
    c: Coincident(g15,g16)
    c: Coincident(g16,g17)
    c: Coincident(g17,g18)
    c: Coincident(g18,g19)
    c: Coincident(g19,g14)
    c: Equal(g14, g15-g19) x5
    c: PointOnObject(g14,g20)
    c: PointOnObject(g15,g20)
    c: PointOnObject(g16,g20)
    c: PointOnObject(g17,g20)
    c: PointOnObject(g18,g20)
    c: PointOnObject(g19,g20)
    c: Diameter(g20) = 7
    c: DistanceY(g-1,g20) = 7
    c: Vertical(g18)
    c: Distance(g17,g-2) = 1
    c: Coincident(g21,g22)
    c: Coincident(g22,g23)
    c: Coincident(g23,g24)
    c: Coincident(g24,g25)
    c: Coincident(g25,g26)
    c: Coincident(g26,g21)
    c: Equal(g21, g22-g26) x5
    c: PointOnObject(g21,g27)
    c: PointOnObject(g22,g27)
    c: PointOnObject(g23,g27)
    c: PointOnObject(g24,g27)
    c: PointOnObject(g25,g27)
    c: PointOnObject(g26,g27)
    c: Diameter(g27) = 7
    c: DistanceY(g-1,g27) = 7
    c: DistanceX(g21,g-1) = 1
    c: Vertical(g21)
    c: Coincident(g28,g29)
    c: Coincident(g29,g30)
    c: Coincident(g30,g31)
    c: Coincident(g31,g32)
    c: Coincident(g32,g33)
    c: Coincident(g33,g28)
    c: Equal(g28, g29-g33) x5
    c: PointOnObject(g28,g34)
    c: PointOnObject(g29,g34)
    c: PointOnObject(g30,g34)
    c: PointOnObject(g31,g34)
    c: PointOnObject(g32,g34)
    c: PointOnObject(g33,g34)
    c: PointOnObject(g34,g-1)
    c: Diameter(g34) = 7
    c: Vertical(g31)
    c: DistanceX(g34,g-1) = 8
    c: Coincident(g35,g36)
    c: Coincident(g36,g37)
    c: Coincident(g37,g38)
    c: Coincident(g38,g39)
    c: Coincident(g39,g40)
    c: Coincident(g40,g35)
    c: Equal(g35, g36-g40) x5
    c: PointOnObject(g35,g41)
    c: PointOnObject(g36,g41)
    c: PointOnObject(g37,g41)
    c: PointOnObject(g38,g41)
    c: PointOnObject(g39,g41)
    c: PointOnObject(g40,g41)
    c: Coincident(g42,g43)
    c: Coincident(g43,g44)
    c: Coincident(g44,g45)
    c: Coincident(g45,g46)
    c: Coincident(g46,g47)
    c: Coincident(g47,g42)
    c: Equal(g42, g43-g47) x5
    c: PointOnObject(g42,g48)
    c: PointOnObject(g43,g48)
    c: PointOnObject(g44,g48)
    c: PointOnObject(g45,g48)
    c: PointOnObject(g46,g48)
    c: PointOnObject(g47,g48)
    c: Equal(g41,g48)
    c: Diameter(g41) = 7
    c: Vertical(g39)
    c: Vertical(g43)
    c: Distance(g-2,g39) = 1
    c: Symmetric(g38,g43,g-2)
    c: Distance(g41,g-1) = 7
FEATURE [Part::Extrusion] Extrude522  label="hex137"
  Base = -> Sketch530
  Dir = (0,-1,2e-16)
  DirMode = 2
  FaceMakerClass = Part::FaceMakerBullseye
  FaceMakerMode = 3
  LengthFwd = 10
  LengthRev = 0
  Placement = pos=(48,0,-42) rot=(0,0,1;0rad)
  Solid = true
  Symmetric = false
FEATURE [Sketcher::SketchObject] Sketch531
  ArcFitTolerance = 1e-06
  FullyConstrained = true
  MakeInternals = false
  Placement = pos=(0,0,0) rot=(1,0,0;1.5708rad)
  sketch-geometry (49):
    g0: LineSegment StartX=1e-16 StartY=3.5 StartZ=0 EndX=-3.03109 EndY=1.75 EndZ=0
    g1: LineSegment StartX=-3.03109 StartY=1.75 StartZ=0 EndX=-3.03109 EndY=-1.75 EndZ=0
    g2: LineSegment StartX=-3.03109 StartY=-1.75 StartZ=0 EndX=-1e-16 EndY=-3.5 EndZ=0
    g3: LineSegment StartX=-1e-16 StartY=-3.5 StartZ=0 EndX=3.03109 EndY=-1.75 EndZ=0
    g4: LineSegment StartX=3.03109 StartY=-1.75 StartZ=0 EndX=3.03109 EndY=1.75 EndZ=0
    g5: LineSegment StartX=3.03109 StartY=1.75 StartZ=0 EndX=1e-16 EndY=3.5 EndZ=0
    g6: Circle [constr] CenterX=0 CenterY=0 CenterZ=0 NormalX=0 NormalY=0 NormalZ=1 AngleXU=0 Radius=3.5
    g7: LineSegment StartX=4.96892 StartY=-1.75002 StartZ=0 EndX=8.00002 EndY=-3.5 EndZ=0
    g8: LineSegment StartX=8.00002 StartY=-3.5 StartZ=0 EndX=11.0311 EndY=-1.74998 EndZ=0
    g9: LineSegment StartX=11.0311 StartY=-1.74998 StartZ=0 EndX=11.0311 EndY=1.75002 EndZ=0
    g10: LineSegment StartX=11.0311 StartY=1.75002 StartZ=0 EndX=7.99998 EndY=3.5 EndZ=0
    g11: LineSegment StartX=7.99998 StartY=3.5 StartZ=0 EndX=4.9689 EndY=1.74998 EndZ=0
    g12: LineSegment StartX=4.9689 StartY=1.74998 StartZ=0 EndX=4.96892 EndY=-1.75002 EndZ=0
    g13: Circle [constr] CenterX=8 CenterY=0 CenterZ=0 NormalX=0 NormalY=0 NormalZ=1 AngleXU=0 Radius=3.5
    g14: LineSegment StartX=4.03109 StartY=3.5 StartZ=0 EndX=7.06218 EndY=5.25 EndZ=0
    g15: LineSegment StartX=7.06218 StartY=5.25 StartZ=0 EndX=7.06218 EndY=8.75 EndZ=0
    g16: LineSegment StartX=7.06218 StartY=8.75 StartZ=0 EndX=4.03109 EndY=10.5 EndZ=0
    g17: LineSegment StartX=4.03109 StartY=10.5 StartZ=0 EndX=1 EndY=8.75 EndZ=0
    g18: LineSegment StartX=1 StartY=8.75 StartZ=0 EndX=1 EndY=5.25 EndZ=0
    g19: LineSegment StartX=1 StartY=5.25 StartZ=0 EndX=4.03109 EndY=3.5 EndZ=0
    g20: Circle [constr] CenterX=4.03109 CenterY=7 CenterZ=0 NormalX=0 NormalY=0 NormalZ=1 AngleXU=0 Radius=3.5
    g21: LineSegment StartX=-1 StartY=5.25 StartZ=0 EndX=-1 EndY=8.75 EndZ=0
    g22: LineSegment StartX=-1 StartY=8.75 StartZ=0 EndX=-4.03109 EndY=10.5 EndZ=0
    g23: LineSegment StartX=-4.03109 StartY=10.5 StartZ=0 EndX=-7.06218 EndY=8.75 EndZ=0
    g24: LineSegment StartX=-7.06218 StartY=8.75 StartZ=0 EndX=-7.06218 EndY=5.25 EndZ=0
    g25: LineSegment StartX=-7.06218 StartY=5.25 StartZ=0 EndX=-4.03109 EndY=3.5 EndZ=0
    g26: LineSegment StartX=-4.03109 StartY=3.5 StartZ=0 EndX=-1 EndY=5.25 EndZ=0
    g27: Circle [constr] CenterX=-4.03109 CenterY=7 CenterZ=0 NormalX=0 NormalY=0 NormalZ=1 AngleXU=0 Radius=3.5
    g28: LineSegment StartX=-4.96891 StartY=-1.75 StartZ=0 EndX=-4.96891 EndY=1.75 EndZ=0
    g29: LineSegment StartX=-4.96891 StartY=1.75 StartZ=0 EndX=-8 EndY=3.5 EndZ=0
    g30: LineSegment StartX=-8 StartY=3.5 StartZ=0 EndX=-11.0311 EndY=1.75 EndZ=0
    g31: LineSegment StartX=-11.0311 StartY=1.75 StartZ=0 EndX=-11.0311 EndY=-1.75 EndZ=0
    g32: LineSegment StartX=-11.0311 StartY=-1.75 StartZ=0 EndX=-8 EndY=-3.5 EndZ=0
    g33: LineSegment StartX=-8 StartY=-3.5 StartZ=0 EndX=-4.96891 EndY=-1.75 EndZ=0
    g34: Circle [constr] CenterX=-8 CenterY=0 CenterZ=0 NormalX=0 NormalY=0 NormalZ=1 AngleXU=0 Radius=3.5
    g35: LineSegment StartX=-4.03109 StartY=-3.5 StartZ=0 EndX=-7.06218 EndY=-5.25 EndZ=0
    g36: LineSegment StartX=-7.06218 StartY=-5.25 StartZ=0 EndX=-7.06218 EndY=-8.75 EndZ=0
    g37: LineSegment StartX=-7.06218 StartY=-8.75 StartZ=0 EndX=-4.03109 EndY=-10.5 EndZ=0
    g38: LineSegment StartX=-4.03109 StartY=-10.5 StartZ=0 EndX=-1 EndY=-8.75 EndZ=0
    g39: LineSegment StartX=-1 StartY=-8.75 StartZ=0 EndX=-1 EndY=-5.25 EndZ=0
    g40: LineSegment StartX=-1 StartY=-5.25 StartZ=0 EndX=-4.03109 EndY=-3.5 EndZ=0
    g41: Circle [constr] CenterX=-4.03109 CenterY=-7 CenterZ=0 NormalX=0 NormalY=0 NormalZ=1 AngleXU=0 Radius=3.5
    g42: LineSegment StartX=4.03109 StartY=-3.5 StartZ=0 EndX=1 EndY=-5.25 EndZ=0
    g43: LineSegment StartX=1 StartY=-5.25 StartZ=0 EndX=1 EndY=-8.75 EndZ=0
    g44: LineSegment StartX=1 StartY=-8.75 StartZ=0 EndX=4.03109 EndY=-10.5 EndZ=0
    g45: LineSegment StartX=4.03109 StartY=-10.5 StartZ=0 EndX=7.06218 EndY=-8.75 EndZ=0
    g46: LineSegment StartX=7.06218 StartY=-8.75 StartZ=0 EndX=7.06218 EndY=-5.25 EndZ=0
    g47: LineSegment StartX=7.06218 StartY=-5.25 StartZ=0 EndX=4.03109 EndY=-3.5 EndZ=0
    g48: Circle [constr] CenterX=4.03109 CenterY=-7 CenterZ=0 NormalX=0 NormalY=0 NormalZ=1 AngleXU=0 Radius=3.5
  constraints (117):
    c: Coincident(g0,g1)
    c: Coincident(g1,g2)
    c: Coincident(g2,g3)
    c: Coincident(g3,g4)
    c: Coincident(g4,g5)
    c: Coincident(g5,g0)
    c: Equal(g0, g1-g5) x5
    c: PointOnObject(g0,g6)
    c: PointOnObject(g1,g6)
    c: PointOnObject(g2,g6)
    c: PointOnObject(g3,g6)
    c: PointOnObject(g4,g6)
    c: PointOnObject(g5,g6)
    c: Coincident(g6,g-1)
    c: Diameter(g6) = 7
    c: PointOnObject(g0,g-2)
    c: Coincident(g7,g8)
    c: Coincident(g8,g9)
    c: Coincident(g9,g10)
    c: Coincident(g10,g11)
    c: Coincident(g11,g12)
    c: Coincident(g12,g7)
    c: Equal(g7, g8-g12) x5
    c: PointOnObject(g7,g13)
    c: PointOnObject(g8,g13)
    c: PointOnObject(g9,g13)
    c: PointOnObject(g10,g13)
    c: PointOnObject(g11,g13)
    c: PointOnObject(g12,g13)
    c: PointOnObject(g13,g-1)
    c: Diameter(g13) = 7
    c: Distance(g6,g13) = 8
    c: Horizontal(g0,g10)
    c: Coincident(g14,g15)
    c: Coincident(g15,g16)
    c: Coincident(g16,g17)
    c: Coincident(g17,g18)
    c: Coincident(g18,g19)
    c: Coincident(g19,g14)
    c: Equal(g14, g15-g19) x5
    c: PointOnObject(g14,g20)
    c: PointOnObject(g15,g20)
    c: PointOnObject(g16,g20)
    c: PointOnObject(g17,g20)
    c: PointOnObject(g18,g20)
    c: PointOnObject(g19,g20)
    c: Diameter(g20) = 7
    c: DistanceY(g-1,g20) = 7
    c: Vertical(g18)
    c: Distance(g17,g-2) = 1
    c: Coincident(g21,g22)
    c: Coincident(g22,g23)
    c: Coincident(g23,g24)
    c: Coincident(g24,g25)
    c: Coincident(g25,g26)
    c: Coincident(g26,g21)
    c: Equal(g21, g22-g26) x5
    c: PointOnObject(g21,g27)
    c: PointOnObject(g22,g27)
    c: PointOnObject(g23,g27)
    c: PointOnObject(g24,g27)
    c: PointOnObject(g25,g27)
    c: PointOnObject(g26,g27)
    c: Diameter(g27) = 7
    c: DistanceY(g-1,g27) = 7
    c: DistanceX(g21,g-1) = 1
    c: Vertical(g21)
    c: Coincident(g28,g29)
    c: Coincident(g29,g30)
    c: Coincident(g30,g31)
    c: Coincident(g31,g32)
    c: Coincident(g32,g33)
    c: Coincident(g33,g28)
    c: Equal(g28, g29-g33) x5
    c: PointOnObject(g28,g34)
    c: PointOnObject(g29,g34)
    c: PointOnObject(g30,g34)
    c: PointOnObject(g31,g34)
    c: PointOnObject(g32,g34)
    c: PointOnObject(g33,g34)
    c: PointOnObject(g34,g-1)
    c: Diameter(g34) = 7
    c: Vertical(g31)
    c: DistanceX(g34,g-1) = 8
    c: Coincident(g35,g36)
    c: Coincident(g36,g37)
    c: Coincident(g37,g38)
    c: Coincident(g38,g39)
    c: Coincident(g39,g40)
    c: Coincident(g40,g35)
    c: Equal(g35, g36-g40) x5
    c: PointOnObject(g35,g41)
    c: PointOnObject(g36,g41)
    c: PointOnObject(g37,g41)
    c: PointOnObject(g38,g41)
    c: PointOnObject(g39,g41)
    c: PointOnObject(g40,g41)
    c: Coincident(g42,g43)
    c: Coincident(g43,g44)
    c: Coincident(g44,g45)
    c: Coincident(g45,g46)
    c: Coincident(g46,g47)
    c: Coincident(g47,g42)
    c: Equal(g42, g43-g47) x5
    c: PointOnObject(g42,g48)
    c: PointOnObject(g43,g48)
    c: PointOnObject(g44,g48)
    c: PointOnObject(g45,g48)
    c: PointOnObject(g46,g48)
    c: PointOnObject(g47,g48)
    c: Equal(g41,g48)
    c: Diameter(g41) = 7
    c: Vertical(g39)
    c: Vertical(g43)
    c: Distance(g-2,g39) = 1
    c: Symmetric(g38,g43,g-2)
    c: Distance(g41,g-1) = 7
FEATURE [Part::Extrusion] Extrude523  label="hex138"
  Base = -> Sketch531
  Dir = (0,-1,2e-16)
  DirMode = 2
  FaceMakerClass = Part::FaceMakerBullseye
  FaceMakerMode = 3
  LengthFwd = 10
  LengthRev = 0
  Placement = pos=(68,0,-35) rot=(0,0,1;0rad)
  Solid = true
  Symmetric = false
FEATURE [Sketcher::SketchObject] Sketch532
  ArcFitTolerance = 1e-06
  FullyConstrained = true
  MakeInternals = false
  Placement = pos=(0,0,0) rot=(1,0,0;1.5708rad)
  sketch-geometry (49):
    g0: LineSegment StartX=1e-16 StartY=3.5 StartZ=0 EndX=-3.03109 EndY=1.75 EndZ=0
    g1: LineSegment StartX=-3.03109 StartY=1.75 StartZ=0 EndX=-3.03109 EndY=-1.75 EndZ=0
    g2: LineSegment StartX=-3.03109 StartY=-1.75 StartZ=0 EndX=-1e-16 EndY=-3.5 EndZ=0
    g3: LineSegment StartX=-1e-16 StartY=-3.5 StartZ=0 EndX=3.03109 EndY=-1.75 EndZ=0
    g4: LineSegment StartX=3.03109 StartY=-1.75 StartZ=0 EndX=3.03109 EndY=1.75 EndZ=0
    g5: LineSegment StartX=3.03109 StartY=1.75 StartZ=0 EndX=1e-16 EndY=3.5 EndZ=0
    g6: Circle [constr] CenterX=0 CenterY=0 CenterZ=0 NormalX=0 NormalY=0 NormalZ=1 AngleXU=0 Radius=3.5
    g7: LineSegment StartX=4.96892 StartY=-1.75002 StartZ=0 EndX=8.00002 EndY=-3.5 EndZ=0
    g8: LineSegment StartX=8.00002 StartY=-3.5 StartZ=0 EndX=11.0311 EndY=-1.74998 EndZ=0
    g9: LineSegment StartX=11.0311 StartY=-1.74998 StartZ=0 EndX=11.0311 EndY=1.75002 EndZ=0
    g10: LineSegment StartX=11.0311 StartY=1.75002 StartZ=0 EndX=7.99998 EndY=3.5 EndZ=0
    g11: LineSegment StartX=7.99998 StartY=3.5 StartZ=0 EndX=4.9689 EndY=1.74998 EndZ=0
    g12: LineSegment StartX=4.9689 StartY=1.74998 StartZ=0 EndX=4.96892 EndY=-1.75002 EndZ=0
    g13: Circle [constr] CenterX=8 CenterY=0 CenterZ=0 NormalX=0 NormalY=0 NormalZ=1 AngleXU=0 Radius=3.5
    g14: LineSegment StartX=4.03109 StartY=3.5 StartZ=0 EndX=7.06218 EndY=5.25 EndZ=0
    g15: LineSegment StartX=7.06218 StartY=5.25 StartZ=0 EndX=7.06218 EndY=8.75 EndZ=0
    g16: LineSegment StartX=7.06218 StartY=8.75 StartZ=0 EndX=4.03109 EndY=10.5 EndZ=0
    g17: LineSegment StartX=4.03109 StartY=10.5 StartZ=0 EndX=1 EndY=8.75 EndZ=0
    g18: LineSegment StartX=1 StartY=8.75 StartZ=0 EndX=1 EndY=5.25 EndZ=0
    g19: LineSegment StartX=1 StartY=5.25 StartZ=0 EndX=4.03109 EndY=3.5 EndZ=0
    g20: Circle [constr] CenterX=4.03109 CenterY=7 CenterZ=0 NormalX=0 NormalY=0 NormalZ=1 AngleXU=0 Radius=3.5
    g21: LineSegment StartX=-1 StartY=5.25 StartZ=0 EndX=-1 EndY=8.75 EndZ=0
    g22: LineSegment StartX=-1 StartY=8.75 StartZ=0 EndX=-4.03109 EndY=10.5 EndZ=0
    g23: LineSegment StartX=-4.03109 StartY=10.5 StartZ=0 EndX=-7.06218 EndY=8.75 EndZ=0
    g24: LineSegment StartX=-7.06218 StartY=8.75 StartZ=0 EndX=-7.06218 EndY=5.25 EndZ=0
    g25: LineSegment StartX=-7.06218 StartY=5.25 StartZ=0 EndX=-4.03109 EndY=3.5 EndZ=0
    g26: LineSegment StartX=-4.03109 StartY=3.5 StartZ=0 EndX=-1 EndY=5.25 EndZ=0
    g27: Circle [constr] CenterX=-4.03109 CenterY=7 CenterZ=0 NormalX=0 NormalY=0 NormalZ=1 AngleXU=0 Radius=3.5
    g28: LineSegment StartX=-4.96891 StartY=-1.75 StartZ=0 EndX=-4.96891 EndY=1.75 EndZ=0
    g29: LineSegment StartX=-4.96891 StartY=1.75 StartZ=0 EndX=-8 EndY=3.5 EndZ=0
    g30: LineSegment StartX=-8 StartY=3.5 StartZ=0 EndX=-11.0311 EndY=1.75 EndZ=0
    g31: LineSegment StartX=-11.0311 StartY=1.75 StartZ=0 EndX=-11.0311 EndY=-1.75 EndZ=0
    g32: LineSegment StartX=-11.0311 StartY=-1.75 StartZ=0 EndX=-8 EndY=-3.5 EndZ=0
    g33: LineSegment StartX=-8 StartY=-3.5 StartZ=0 EndX=-4.96891 EndY=-1.75 EndZ=0
    g34: Circle [constr] CenterX=-8 CenterY=0 CenterZ=0 NormalX=0 NormalY=0 NormalZ=1 AngleXU=0 Radius=3.5
    g35: LineSegment StartX=-4.03109 StartY=-3.5 StartZ=0 EndX=-7.06218 EndY=-5.25 EndZ=0
    g36: LineSegment StartX=-7.06218 StartY=-5.25 StartZ=0 EndX=-7.06218 EndY=-8.75 EndZ=0
    g37: LineSegment StartX=-7.06218 StartY=-8.75 StartZ=0 EndX=-4.03109 EndY=-10.5 EndZ=0
    g38: LineSegment StartX=-4.03109 StartY=-10.5 StartZ=0 EndX=-1 EndY=-8.75 EndZ=0
    g39: LineSegment StartX=-1 StartY=-8.75 StartZ=0 EndX=-1 EndY=-5.25 EndZ=0
    g40: LineSegment StartX=-1 StartY=-5.25 StartZ=0 EndX=-4.03109 EndY=-3.5 EndZ=0
    g41: Circle [constr] CenterX=-4.03109 CenterY=-7 CenterZ=0 NormalX=0 NormalY=0 NormalZ=1 AngleXU=0 Radius=3.5
    g42: LineSegment StartX=4.03109 StartY=-3.5 StartZ=0 EndX=1 EndY=-5.25 EndZ=0
    g43: LineSegment StartX=1 StartY=-5.25 StartZ=0 EndX=1 EndY=-8.75 EndZ=0
    g44: LineSegment StartX=1 StartY=-8.75 StartZ=0 EndX=4.03109 EndY=-10.5 EndZ=0
    g45: LineSegment StartX=4.03109 StartY=-10.5 StartZ=0 EndX=7.06218 EndY=-8.75 EndZ=0
    g46: LineSegment StartX=7.06218 StartY=-8.75 StartZ=0 EndX=7.06218 EndY=-5.25 EndZ=0
    g47: LineSegment StartX=7.06218 StartY=-5.25 StartZ=0 EndX=4.03109 EndY=-3.5 EndZ=0
    g48: Circle [constr] CenterX=4.03109 CenterY=-7 CenterZ=0 NormalX=0 NormalY=0 NormalZ=1 AngleXU=0 Radius=3.5
  constraints (117):
    c: Coincident(g0,g1)
    c: Coincident(g1,g2)
    c: Coincident(g2,g3)
    c: Coincident(g3,g4)
    c: Coincident(g4,g5)
    c: Coincident(g5,g0)
    c: Equal(g0, g1-g5) x5
    c: PointOnObject(g0,g6)
    c: PointOnObject(g1,g6)
    c: PointOnObject(g2,g6)
    c: PointOnObject(g3,g6)
    c: PointOnObject(g4,g6)
    c: PointOnObject(g5,g6)
    c: Coincident(g6,g-1)
    c: Diameter(g6) = 7
    c: PointOnObject(g0,g-2)
    c: Coincident(g7,g8)
    c: Coincident(g8,g9)
    c: Coincident(g9,g10)
    c: Coincident(g10,g11)
    c: Coincident(g11,g12)
    c: Coincident(g12,g7)
    c: Equal(g7, g8-g12) x5
    c: PointOnObject(g7,g13)
    c: PointOnObject(g8,g13)
    c: PointOnObject(g9,g13)
    c: PointOnObject(g10,g13)
    c: PointOnObject(g11,g13)
    c: PointOnObject(g12,g13)
    c: PointOnObject(g13,g-1)
    c: Diameter(g13) = 7
    c: Distance(g6,g13) = 8
    c: Horizontal(g0,g10)
    c: Coincident(g14,g15)
    c: Coincident(g15,g16)
    c: Coincident(g16,g17)
    c: Coincident(g17,g18)
    c: Coincident(g18,g19)
    c: Coincident(g19,g14)
    c: Equal(g14, g15-g19) x5
    c: PointOnObject(g14,g20)
    c: PointOnObject(g15,g20)
    c: PointOnObject(g16,g20)
    c: PointOnObject(g17,g20)
    c: PointOnObject(g18,g20)
    c: PointOnObject(g19,g20)
    c: Diameter(g20) = 7
    c: DistanceY(g-1,g20) = 7
    c: Vertical(g18)
    c: Distance(g17,g-2) = 1
    c: Coincident(g21,g22)
    c: Coincident(g22,g23)
    c: Coincident(g23,g24)
    c: Coincident(g24,g25)
    c: Coincident(g25,g26)
    c: Coincident(g26,g21)
    c: Equal(g21, g22-g26) x5
    c: PointOnObject(g21,g27)
    c: PointOnObject(g22,g27)
    c: PointOnObject(g23,g27)
    c: PointOnObject(g24,g27)
    c: PointOnObject(g25,g27)
    c: PointOnObject(g26,g27)
    c: Diameter(g27) = 7
    c: DistanceY(g-1,g27) = 7
    c: DistanceX(g21,g-1) = 1
    c: Vertical(g21)
    c: Coincident(g28,g29)
    c: Coincident(g29,g30)
    c: Coincident(g30,g31)
    c: Coincident(g31,g32)
    c: Coincident(g32,g33)
    c: Coincident(g33,g28)
    c: Equal(g28, g29-g33) x5
    c: PointOnObject(g28,g34)
    c: PointOnObject(g29,g34)
    c: PointOnObject(g30,g34)
    c: PointOnObject(g31,g34)
    c: PointOnObject(g32,g34)
    c: PointOnObject(g33,g34)
    c: PointOnObject(g34,g-1)
    c: Diameter(g34) = 7
    c: Vertical(g31)
    c: DistanceX(g34,g-1) = 8
    c: Coincident(g35,g36)
    c: Coincident(g36,g37)
    c: Coincident(g37,g38)
    c: Coincident(g38,g39)
    c: Coincident(g39,g40)
    c: Coincident(g40,g35)
    c: Equal(g35, g36-g40) x5
    c: PointOnObject(g35,g41)
    c: PointOnObject(g36,g41)
    c: PointOnObject(g37,g41)
    c: PointOnObject(g38,g41)
    c: PointOnObject(g39,g41)
    c: PointOnObject(g40,g41)
    c: Coincident(g42,g43)
    c: Coincident(g43,g44)
    c: Coincident(g44,g45)
    c: Coincident(g45,g46)
    c: Coincident(g46,g47)
    c: Coincident(g47,g42)
    c: Equal(g42, g43-g47) x5
    c: PointOnObject(g42,g48)
    c: PointOnObject(g43,g48)
    c: PointOnObject(g44,g48)
    c: PointOnObject(g45,g48)
    c: PointOnObject(g46,g48)
    c: PointOnObject(g47,g48)
    c: Equal(g41,g48)
    c: Diameter(g41) = 7
    c: Vertical(g39)
    c: Vertical(g43)
    c: Distance(g-2,g39) = 1
    c: Symmetric(g38,g43,g-2)
    c: Distance(g41,g-1) = 7
FEATURE [Part::Extrusion] Extrude524  label="hex139"
  Base = -> Sketch532
  Dir = (0,-1,2e-16)
  DirMode = 2
  FaceMakerClass = Part::FaceMakerBullseye
  FaceMakerMode = 3
  LengthFwd = 10
  LengthRev = 0
  Placement = pos=(72,0,-14) rot=(0,0,1;0rad)
  Solid = true
  Symmetric = false
FEATURE [Sketcher::SketchObject] Sketch533
  ArcFitTolerance = 1e-06
  FullyConstrained = true
  MakeInternals = false
  Placement = pos=(0,0,0) rot=(1,0,0;1.5708rad)
  sketch-geometry (49):
    g0: LineSegment StartX=1e-16 StartY=3.5 StartZ=0 EndX=-3.03109 EndY=1.75 EndZ=0
    g1: LineSegment StartX=-3.03109 StartY=1.75 StartZ=0 EndX=-3.03109 EndY=-1.75 EndZ=0
    g2: LineSegment StartX=-3.03109 StartY=-1.75 StartZ=0 EndX=-1e-16 EndY=-3.5 EndZ=0
    g3: LineSegment StartX=-1e-16 StartY=-3.5 StartZ=0 EndX=3.03109 EndY=-1.75 EndZ=0
    g4: LineSegment StartX=3.03109 StartY=-1.75 StartZ=0 EndX=3.03109 EndY=1.75 EndZ=0
    g5: LineSegment StartX=3.03109 StartY=1.75 StartZ=0 EndX=1e-16 EndY=3.5 EndZ=0
    g6: Circle [constr] CenterX=0 CenterY=0 CenterZ=0 NormalX=0 NormalY=0 NormalZ=1 AngleXU=0 Radius=3.5
    g7: LineSegment StartX=4.96892 StartY=-1.75002 StartZ=0 EndX=8.00002 EndY=-3.5 EndZ=0
    g8: LineSegment StartX=8.00002 StartY=-3.5 StartZ=0 EndX=11.0311 EndY=-1.74998 EndZ=0
    g9: LineSegment StartX=11.0311 StartY=-1.74998 StartZ=0 EndX=11.0311 EndY=1.75002 EndZ=0
    g10: LineSegment StartX=11.0311 StartY=1.75002 StartZ=0 EndX=7.99998 EndY=3.5 EndZ=0
    g11: LineSegment StartX=7.99998 StartY=3.5 StartZ=0 EndX=4.9689 EndY=1.74998 EndZ=0
    g12: LineSegment StartX=4.9689 StartY=1.74998 StartZ=0 EndX=4.96892 EndY=-1.75002 EndZ=0
    g13: Circle [constr] CenterX=8 CenterY=0 CenterZ=0 NormalX=0 NormalY=0 NormalZ=1 AngleXU=0 Radius=3.5
    g14: LineSegment StartX=4.03109 StartY=3.5 StartZ=0 EndX=7.06218 EndY=5.25 EndZ=0
    g15: LineSegment StartX=7.06218 StartY=5.25 StartZ=0 EndX=7.06218 EndY=8.75 EndZ=0
    g16: LineSegment StartX=7.06218 StartY=8.75 StartZ=0 EndX=4.03109 EndY=10.5 EndZ=0
    g17: LineSegment StartX=4.03109 StartY=10.5 StartZ=0 EndX=1 EndY=8.75 EndZ=0
    g18: LineSegment StartX=1 StartY=8.75 StartZ=0 EndX=1 EndY=5.25 EndZ=0
    g19: LineSegment StartX=1 StartY=5.25 StartZ=0 EndX=4.03109 EndY=3.5 EndZ=0
    g20: Circle [constr] CenterX=4.03109 CenterY=7 CenterZ=0 NormalX=0 NormalY=0 NormalZ=1 AngleXU=0 Radius=3.5
    g21: LineSegment StartX=-1 StartY=5.25 StartZ=0 EndX=-1 EndY=8.75 EndZ=0
    g22: LineSegment StartX=-1 StartY=8.75 StartZ=0 EndX=-4.03109 EndY=10.5 EndZ=0
    g23: LineSegment StartX=-4.03109 StartY=10.5 StartZ=0 EndX=-7.06218 EndY=8.75 EndZ=0
    g24: LineSegment StartX=-7.06218 StartY=8.75 StartZ=0 EndX=-7.06218 EndY=5.25 EndZ=0
    g25: LineSegment StartX=-7.06218 StartY=5.25 StartZ=0 EndX=-4.03109 EndY=3.5 EndZ=0
    g26: LineSegment StartX=-4.03109 StartY=3.5 StartZ=0 EndX=-1 EndY=5.25 EndZ=0
    g27: Circle [constr] CenterX=-4.03109 CenterY=7 CenterZ=0 NormalX=0 NormalY=0 NormalZ=1 AngleXU=0 Radius=3.5
    g28: LineSegment StartX=-4.96891 StartY=-1.75 StartZ=0 EndX=-4.96891 EndY=1.75 EndZ=0
    g29: LineSegment StartX=-4.96891 StartY=1.75 StartZ=0 EndX=-8 EndY=3.5 EndZ=0
    g30: LineSegment StartX=-8 StartY=3.5 StartZ=0 EndX=-11.0311 EndY=1.75 EndZ=0
    g31: LineSegment StartX=-11.0311 StartY=1.75 StartZ=0 EndX=-11.0311 EndY=-1.75 EndZ=0
    g32: LineSegment StartX=-11.0311 StartY=-1.75 StartZ=0 EndX=-8 EndY=-3.5 EndZ=0
    g33: LineSegment StartX=-8 StartY=-3.5 StartZ=0 EndX=-4.96891 EndY=-1.75 EndZ=0
    g34: Circle [constr] CenterX=-8 CenterY=0 CenterZ=0 NormalX=0 NormalY=0 NormalZ=1 AngleXU=0 Radius=3.5
    g35: LineSegment StartX=-4.03109 StartY=-3.5 StartZ=0 EndX=-7.06218 EndY=-5.25 EndZ=0
    g36: LineSegment StartX=-7.06218 StartY=-5.25 StartZ=0 EndX=-7.06218 EndY=-8.75 EndZ=0
    g37: LineSegment StartX=-7.06218 StartY=-8.75 StartZ=0 EndX=-4.03109 EndY=-10.5 EndZ=0
    g38: LineSegment StartX=-4.03109 StartY=-10.5 StartZ=0 EndX=-1 EndY=-8.75 EndZ=0
    g39: LineSegment StartX=-1 StartY=-8.75 StartZ=0 EndX=-1 EndY=-5.25 EndZ=0
    g40: LineSegment StartX=-1 StartY=-5.25 StartZ=0 EndX=-4.03109 EndY=-3.5 EndZ=0
    g41: Circle [constr] CenterX=-4.03109 CenterY=-7 CenterZ=0 NormalX=0 NormalY=0 NormalZ=1 AngleXU=0 Radius=3.5
    g42: LineSegment StartX=4.03109 StartY=-3.5 StartZ=0 EndX=1 EndY=-5.25 EndZ=0
    g43: LineSegment StartX=1 StartY=-5.25 StartZ=0 EndX=1 EndY=-8.75 EndZ=0
    g44: LineSegment StartX=1 StartY=-8.75 StartZ=0 EndX=4.03109 EndY=-10.5 EndZ=0
    g45: LineSegment StartX=4.03109 StartY=-10.5 StartZ=0 EndX=7.06218 EndY=-8.75 EndZ=0
    g46: LineSegment StartX=7.06218 StartY=-8.75 StartZ=0 EndX=7.06218 EndY=-5.25 EndZ=0
    g47: LineSegment StartX=7.06218 StartY=-5.25 StartZ=0 EndX=4.03109 EndY=-3.5 EndZ=0
    g48: Circle [constr] CenterX=4.03109 CenterY=-7 CenterZ=0 NormalX=0 NormalY=0 NormalZ=1 AngleXU=0 Radius=3.5
  constraints (117):
    c: Coincident(g0,g1)
    c: Coincident(g1,g2)
    c: Coincident(g2,g3)
    c: Coincident(g3,g4)
    c: Coincident(g4,g5)
    c: Coincident(g5,g0)
    c: Equal(g0, g1-g5) x5
    c: PointOnObject(g0,g6)
    c: PointOnObject(g1,g6)
    c: PointOnObject(g2,g6)
    c: PointOnObject(g3,g6)
    c: PointOnObject(g4,g6)
    c: PointOnObject(g5,g6)
    c: Coincident(g6,g-1)
    c: Diameter(g6) = 7
    c: PointOnObject(g0,g-2)
    c: Coincident(g7,g8)
    c: Coincident(g8,g9)
    c: Coincident(g9,g10)
    c: Coincident(g10,g11)
    c: Coincident(g11,g12)
    c: Coincident(g12,g7)
    c: Equal(g7, g8-g12) x5
    c: PointOnObject(g7,g13)
    c: PointOnObject(g8,g13)
    c: PointOnObject(g9,g13)
    c: PointOnObject(g10,g13)
    c: PointOnObject(g11,g13)
    c: PointOnObject(g12,g13)
    c: PointOnObject(g13,g-1)
    c: Diameter(g13) = 7
    c: Distance(g6,g13) = 8
    c: Horizontal(g0,g10)
    c: Coincident(g14,g15)
    c: Coincident(g15,g16)
    c: Coincident(g16,g17)
    c: Coincident(g17,g18)
    c: Coincident(g18,g19)
    c: Coincident(g19,g14)
    c: Equal(g14, g15-g19) x5
    c: PointOnObject(g14,g20)
    c: PointOnObject(g15,g20)
    c: PointOnObject(g16,g20)
    c: PointOnObject(g17,g20)
    c: PointOnObject(g18,g20)
    c: PointOnObject(g19,g20)
    c: Diameter(g20) = 7
    c: DistanceY(g-1,g20) = 7
    c: Vertical(g18)
    c: Distance(g17,g-2) = 1
    c: Coincident(g21,g22)
    c: Coincident(g22,g23)
    c: Coincident(g23,g24)
    c: Coincident(g24,g25)
    c: Coincident(g25,g26)
    c: Coincident(g26,g21)
    c: Equal(g21, g22-g26) x5
    c: PointOnObject(g21,g27)
    c: PointOnObject(g22,g27)
    c: PointOnObject(g23,g27)
    c: PointOnObject(g24,g27)
    c: PointOnObject(g25,g27)
    c: PointOnObject(g26,g27)
    c: Diameter(g27) = 7
    c: DistanceY(g-1,g27) = 7
    c: DistanceX(g21,g-1) = 1
    c: Vertical(g21)
    c: Coincident(g28,g29)
    c: Coincident(g29,g30)
    c: Coincident(g30,g31)
    c: Coincident(g31,g32)
    c: Coincident(g32,g33)
    c: Coincident(g33,g28)
    c: Equal(g28, g29-g33) x5
    c: PointOnObject(g28,g34)
    c: PointOnObject(g29,g34)
    c: PointOnObject(g30,g34)
    c: PointOnObject(g31,g34)
    c: PointOnObject(g32,g34)
    c: PointOnObject(g33,g34)
    c: PointOnObject(g34,g-1)
    c: Diameter(g34) = 7
    c: Vertical(g31)
    c: DistanceX(g34,g-1) = 8
    c: Coincident(g35,g36)
    c: Coincident(g36,g37)
    c: Coincident(g37,g38)
    c: Coincident(g38,g39)
    c: Coincident(g39,g40)
    c: Coincident(g40,g35)
    c: Equal(g35, g36-g40) x5
    c: PointOnObject(g35,g41)
    c: PointOnObject(g36,g41)
    c: PointOnObject(g37,g41)
    c: PointOnObject(g38,g41)
    c: PointOnObject(g39,g41)
    c: PointOnObject(g40,g41)
    c: Coincident(g42,g43)
    c: Coincident(g43,g44)
    c: Coincident(g44,g45)
    c: Coincident(g45,g46)
    c: Coincident(g46,g47)
    c: Coincident(g47,g42)
    c: Equal(g42, g43-g47) x5
    c: PointOnObject(g42,g48)
    c: PointOnObject(g43,g48)
    c: PointOnObject(g44,g48)
    c: PointOnObject(g45,g48)
    c: PointOnObject(g46,g48)
    c: PointOnObject(g47,g48)
    c: Equal(g41,g48)
    c: Diameter(g41) = 7
    c: Vertical(g39)
    c: Vertical(g43)
    c: Distance(g-2,g39) = 1
    c: Symmetric(g38,g43,g-2)
    c: Distance(g41,g-1) = 7
FEATURE [Part::Extrusion] Extrude525  label="hex140"
  Base = -> Sketch533
  Dir = (0,-1,2e-16)
  DirMode = 2
  FaceMakerClass = Part::FaceMakerBullseye
  FaceMakerMode = 3
  LengthFwd = 10
  LengthRev = 0
  Placement = pos=(72,0,14) rot=(0,0,1;0rad)
  Solid = true
  Symmetric = false
FEATURE [Sketcher::SketchObject] Sketch534
  ArcFitTolerance = 1e-06
  FullyConstrained = true
  MakeInternals = false
  Placement = pos=(0,0,0) rot=(1,0,0;1.5708rad)
  sketch-geometry (49):
    g0: LineSegment StartX=1e-16 StartY=3.5 StartZ=0 EndX=-3.03109 EndY=1.75 EndZ=0
    g1: LineSegment StartX=-3.03109 StartY=1.75 StartZ=0 EndX=-3.03109 EndY=-1.75 EndZ=0
    g2: LineSegment StartX=-3.03109 StartY=-1.75 StartZ=0 EndX=-1e-16 EndY=-3.5 EndZ=0
    g3: LineSegment StartX=-1e-16 StartY=-3.5 StartZ=0 EndX=3.03109 EndY=-1.75 EndZ=0
    g4: LineSegment StartX=3.03109 StartY=-1.75 StartZ=0 EndX=3.03109 EndY=1.75 EndZ=0
    g5: LineSegment StartX=3.03109 StartY=1.75 StartZ=0 EndX=1e-16 EndY=3.5 EndZ=0
    g6: Circle [constr] CenterX=0 CenterY=0 CenterZ=0 NormalX=0 NormalY=0 NormalZ=1 AngleXU=0 Radius=3.5
    g7: LineSegment StartX=4.96892 StartY=-1.75002 StartZ=0 EndX=8.00002 EndY=-3.5 EndZ=0
    g8: LineSegment StartX=8.00002 StartY=-3.5 StartZ=0 EndX=11.0311 EndY=-1.74998 EndZ=0
    g9: LineSegment StartX=11.0311 StartY=-1.74998 StartZ=0 EndX=11.0311 EndY=1.75002 EndZ=0
    g10: LineSegment StartX=11.0311 StartY=1.75002 StartZ=0 EndX=7.99998 EndY=3.5 EndZ=0
    g11: LineSegment StartX=7.99998 StartY=3.5 StartZ=0 EndX=4.9689 EndY=1.74998 EndZ=0
    g12: LineSegment StartX=4.9689 StartY=1.74998 StartZ=0 EndX=4.96892 EndY=-1.75002 EndZ=0
    g13: Circle [constr] CenterX=8 CenterY=0 CenterZ=0 NormalX=0 NormalY=0 NormalZ=1 AngleXU=0 Radius=3.5
    g14: LineSegment StartX=4.03109 StartY=3.5 StartZ=0 EndX=7.06218 EndY=5.25 EndZ=0
    g15: LineSegment StartX=7.06218 StartY=5.25 StartZ=0 EndX=7.06218 EndY=8.75 EndZ=0
    g16: LineSegment StartX=7.06218 StartY=8.75 StartZ=0 EndX=4.03109 EndY=10.5 EndZ=0
    g17: LineSegment StartX=4.03109 StartY=10.5 StartZ=0 EndX=1 EndY=8.75 EndZ=0
    g18: LineSegment StartX=1 StartY=8.75 StartZ=0 EndX=1 EndY=5.25 EndZ=0
    g19: LineSegment StartX=1 StartY=5.25 StartZ=0 EndX=4.03109 EndY=3.5 EndZ=0
    g20: Circle [constr] CenterX=4.03109 CenterY=7 CenterZ=0 NormalX=0 NormalY=0 NormalZ=1 AngleXU=0 Radius=3.5
    g21: LineSegment StartX=-1 StartY=5.25 StartZ=0 EndX=-1 EndY=8.75 EndZ=0
    g22: LineSegment StartX=-1 StartY=8.75 StartZ=0 EndX=-4.03109 EndY=10.5 EndZ=0
    g23: LineSegment StartX=-4.03109 StartY=10.5 StartZ=0 EndX=-7.06218 EndY=8.75 EndZ=0
    g24: LineSegment StartX=-7.06218 StartY=8.75 StartZ=0 EndX=-7.06218 EndY=5.25 EndZ=0
    g25: LineSegment StartX=-7.06218 StartY=5.25 StartZ=0 EndX=-4.03109 EndY=3.5 EndZ=0
    g26: LineSegment StartX=-4.03109 StartY=3.5 StartZ=0 EndX=-1 EndY=5.25 EndZ=0
    g27: Circle [constr] CenterX=-4.03109 CenterY=7 CenterZ=0 NormalX=0 NormalY=0 NormalZ=1 AngleXU=0 Radius=3.5
    g28: LineSegment StartX=-4.96891 StartY=-1.75 StartZ=0 EndX=-4.96891 EndY=1.75 EndZ=0
    g29: LineSegment StartX=-4.96891 StartY=1.75 StartZ=0 EndX=-8 EndY=3.5 EndZ=0
    g30: LineSegment StartX=-8 StartY=3.5 StartZ=0 EndX=-11.0311 EndY=1.75 EndZ=0
    g31: LineSegment StartX=-11.0311 StartY=1.75 StartZ=0 EndX=-11.0311 EndY=-1.75 EndZ=0
    g32: LineSegment StartX=-11.0311 StartY=-1.75 StartZ=0 EndX=-8 EndY=-3.5 EndZ=0
    g33: LineSegment StartX=-8 StartY=-3.5 StartZ=0 EndX=-4.96891 EndY=-1.75 EndZ=0
    g34: Circle [constr] CenterX=-8 CenterY=0 CenterZ=0 NormalX=0 NormalY=0 NormalZ=1 AngleXU=0 Radius=3.5
    g35: LineSegment StartX=-4.03109 StartY=-3.5 StartZ=0 EndX=-7.06218 EndY=-5.25 EndZ=0
    g36: LineSegment StartX=-7.06218 StartY=-5.25 StartZ=0 EndX=-7.06218 EndY=-8.75 EndZ=0
    g37: LineSegment StartX=-7.06218 StartY=-8.75 StartZ=0 EndX=-4.03109 EndY=-10.5 EndZ=0
    g38: LineSegment StartX=-4.03109 StartY=-10.5 StartZ=0 EndX=-1 EndY=-8.75 EndZ=0
    g39: LineSegment StartX=-1 StartY=-8.75 StartZ=0 EndX=-1 EndY=-5.25 EndZ=0
    g40: LineSegment StartX=-1 StartY=-5.25 StartZ=0 EndX=-4.03109 EndY=-3.5 EndZ=0
    g41: Circle [constr] CenterX=-4.03109 CenterY=-7 CenterZ=0 NormalX=0 NormalY=0 NormalZ=1 AngleXU=0 Radius=3.5
    g42: LineSegment StartX=4.03109 StartY=-3.5 StartZ=0 EndX=1 EndY=-5.25 EndZ=0
    g43: LineSegment StartX=1 StartY=-5.25 StartZ=0 EndX=1 EndY=-8.75 EndZ=0
    g44: LineSegment StartX=1 StartY=-8.75 StartZ=0 EndX=4.03109 EndY=-10.5 EndZ=0
    g45: LineSegment StartX=4.03109 StartY=-10.5 StartZ=0 EndX=7.06218 EndY=-8.75 EndZ=0
    g46: LineSegment StartX=7.06218 StartY=-8.75 StartZ=0 EndX=7.06218 EndY=-5.25 EndZ=0
    g47: LineSegment StartX=7.06218 StartY=-5.25 StartZ=0 EndX=4.03109 EndY=-3.5 EndZ=0
    g48: Circle [constr] CenterX=4.03109 CenterY=-7 CenterZ=0 NormalX=0 NormalY=0 NormalZ=1 AngleXU=0 Radius=3.5
  constraints (117):
    c: Coincident(g0,g1)
    c: Coincident(g1,g2)
    c: Coincident(g2,g3)
    c: Coincident(g3,g4)
    c: Coincident(g4,g5)
    c: Coincident(g5,g0)
    c: Equal(g0, g1-g5) x5
    c: PointOnObject(g0,g6)
    c: PointOnObject(g1,g6)
    c: PointOnObject(g2,g6)
    c: PointOnObject(g3,g6)
    c: PointOnObject(g4,g6)
    c: PointOnObject(g5,g6)
    c: Coincident(g6,g-1)
    c: Diameter(g6) = 7
    c: PointOnObject(g0,g-2)
    c: Coincident(g7,g8)
    c: Coincident(g8,g9)
    c: Coincident(g9,g10)
    c: Coincident(g10,g11)
    c: Coincident(g11,g12)
    c: Coincident(g12,g7)
    c: Equal(g7, g8-g12) x5
    c: PointOnObject(g7,g13)
    c: PointOnObject(g8,g13)
    c: PointOnObject(g9,g13)
    c: PointOnObject(g10,g13)
    c: PointOnObject(g11,g13)
    c: PointOnObject(g12,g13)
    c: PointOnObject(g13,g-1)
    c: Diameter(g13) = 7
    c: Distance(g6,g13) = 8
    c: Horizontal(g0,g10)
    c: Coincident(g14,g15)
    c: Coincident(g15,g16)
    c: Coincident(g16,g17)
    c: Coincident(g17,g18)
    c: Coincident(g18,g19)
    c: Coincident(g19,g14)
    c: Equal(g14, g15-g19) x5
    c: PointOnObject(g14,g20)
    c: PointOnObject(g15,g20)
    c: PointOnObject(g16,g20)
    c: PointOnObject(g17,g20)
    c: PointOnObject(g18,g20)
    c: PointOnObject(g19,g20)
    c: Diameter(g20) = 7
    c: DistanceY(g-1,g20) = 7
    c: Vertical(g18)
    c: Distance(g17,g-2) = 1
    c: Coincident(g21,g22)
    c: Coincident(g22,g23)
    c: Coincident(g23,g24)
    c: Coincident(g24,g25)
    c: Coincident(g25,g26)
    c: Coincident(g26,g21)
    c: Equal(g21, g22-g26) x5
    c: PointOnObject(g21,g27)
    c: PointOnObject(g22,g27)
    c: PointOnObject(g23,g27)
    c: PointOnObject(g24,g27)
    c: PointOnObject(g25,g27)
    c: PointOnObject(g26,g27)
    c: Diameter(g27) = 7
    c: DistanceY(g-1,g27) = 7
    c: DistanceX(g21,g-1) = 1
    c: Vertical(g21)
    c: Coincident(g28,g29)
    c: Coincident(g29,g30)
    c: Coincident(g30,g31)
    c: Coincident(g31,g32)
    c: Coincident(g32,g33)
    c: Coincident(g33,g28)
    c: Equal(g28, g29-g33) x5
    c: PointOnObject(g28,g34)
    c: PointOnObject(g29,g34)
    c: PointOnObject(g30,g34)
    c: PointOnObject(g31,g34)
    c: PointOnObject(g32,g34)
    c: PointOnObject(g33,g34)
    c: PointOnObject(g34,g-1)
    c: Diameter(g34) = 7
    c: Vertical(g31)
    c: DistanceX(g34,g-1) = 8
    c: Coincident(g35,g36)
    c: Coincident(g36,g37)
    c: Coincident(g37,g38)
    c: Coincident(g38,g39)
    c: Coincident(g39,g40)
    c: Coincident(g40,g35)
    c: Equal(g35, g36-g40) x5
    c: PointOnObject(g35,g41)
    c: PointOnObject(g36,g41)
    c: PointOnObject(g37,g41)
    c: PointOnObject(g38,g41)
    c: PointOnObject(g39,g41)
    c: PointOnObject(g40,g41)
    c: Coincident(g42,g43)
    c: Coincident(g43,g44)
    c: Coincident(g44,g45)
    c: Coincident(g45,g46)
    c: Coincident(g46,g47)
    c: Coincident(g47,g42)
    c: Equal(g42, g43-g47) x5
    c: PointOnObject(g42,g48)
    c: PointOnObject(g43,g48)
    c: PointOnObject(g44,g48)
    c: PointOnObject(g45,g48)
    c: PointOnObject(g46,g48)
    c: PointOnObject(g47,g48)
    c: Equal(g41,g48)
    c: Diameter(g41) = 7
    c: Vertical(g39)
    c: Vertical(g43)
    c: Distance(g-2,g39) = 1
    c: Symmetric(g38,g43,g-2)
    c: Distance(g41,g-1) = 7
FEATURE [Part::Extrusion] Extrude526  label="hex141"
  Base = -> Sketch534
  Dir = (0,-1,2e-16)
  DirMode = 2
  FaceMakerClass = Part::FaceMakerBullseye
  FaceMakerMode = 3
  LengthFwd = 10
  LengthRev = 0
  Placement = pos=(80,0,0) rot=(0,0,1;0rad)
  Solid = true
  Symmetric = false
FEATURE [Sketcher::SketchObject] Sketch535
  ArcFitTolerance = 1e-06
  FullyConstrained = true
  MakeInternals = false
  Placement = pos=(0,0,0) rot=(1,0,0;1.5708rad)
  sketch-geometry (49):
    g0: LineSegment StartX=1e-16 StartY=3.5 StartZ=0 EndX=-3.03109 EndY=1.75 EndZ=0
    g1: LineSegment StartX=-3.03109 StartY=1.75 StartZ=0 EndX=-3.03109 EndY=-1.75 EndZ=0
    g2: LineSegment StartX=-3.03109 StartY=-1.75 StartZ=0 EndX=-1e-16 EndY=-3.5 EndZ=0
    g3: LineSegment StartX=-1e-16 StartY=-3.5 StartZ=0 EndX=3.03109 EndY=-1.75 EndZ=0
    g4: LineSegment StartX=3.03109 StartY=-1.75 StartZ=0 EndX=3.03109 EndY=1.75 EndZ=0
    g5: LineSegment StartX=3.03109 StartY=1.75 StartZ=0 EndX=1e-16 EndY=3.5 EndZ=0
    g6: Circle [constr] CenterX=0 CenterY=0 CenterZ=0 NormalX=0 NormalY=0 NormalZ=1 AngleXU=0 Radius=3.5
    g7: LineSegment StartX=4.96892 StartY=-1.75002 StartZ=0 EndX=8.00002 EndY=-3.5 EndZ=0
    g8: LineSegment StartX=8.00002 StartY=-3.5 StartZ=0 EndX=11.0311 EndY=-1.74998 EndZ=0
    g9: LineSegment StartX=11.0311 StartY=-1.74998 StartZ=0 EndX=11.0311 EndY=1.75002 EndZ=0
    g10: LineSegment StartX=11.0311 StartY=1.75002 StartZ=0 EndX=7.99998 EndY=3.5 EndZ=0
    g11: LineSegment StartX=7.99998 StartY=3.5 StartZ=0 EndX=4.9689 EndY=1.74998 EndZ=0
    g12: LineSegment StartX=4.9689 StartY=1.74998 StartZ=0 EndX=4.96892 EndY=-1.75002 EndZ=0
    g13: Circle [constr] CenterX=8 CenterY=0 CenterZ=0 NormalX=0 NormalY=0 NormalZ=1 AngleXU=0 Radius=3.5
    g14: LineSegment StartX=4.03109 StartY=3.5 StartZ=0 EndX=7.06218 EndY=5.25 EndZ=0
    g15: LineSegment StartX=7.06218 StartY=5.25 StartZ=0 EndX=7.06218 EndY=8.75 EndZ=0
    g16: LineSegment StartX=7.06218 StartY=8.75 StartZ=0 EndX=4.03109 EndY=10.5 EndZ=0
    g17: LineSegment StartX=4.03109 StartY=10.5 StartZ=0 EndX=1 EndY=8.75 EndZ=0
    g18: LineSegment StartX=1 StartY=8.75 StartZ=0 EndX=1 EndY=5.25 EndZ=0
    g19: LineSegment StartX=1 StartY=5.25 StartZ=0 EndX=4.03109 EndY=3.5 EndZ=0
    g20: Circle [constr] CenterX=4.03109 CenterY=7 CenterZ=0 NormalX=0 NormalY=0 NormalZ=1 AngleXU=0 Radius=3.5
    g21: LineSegment StartX=-1 StartY=5.25 StartZ=0 EndX=-1 EndY=8.75 EndZ=0
    g22: LineSegment StartX=-1 StartY=8.75 StartZ=0 EndX=-4.03109 EndY=10.5 EndZ=0
    g23: LineSegment StartX=-4.03109 StartY=10.5 StartZ=0 EndX=-7.06218 EndY=8.75 EndZ=0
    g24: LineSegment StartX=-7.06218 StartY=8.75 StartZ=0 EndX=-7.06218 EndY=5.25 EndZ=0
    g25: LineSegment StartX=-7.06218 StartY=5.25 StartZ=0 EndX=-4.03109 EndY=3.5 EndZ=0
    g26: LineSegment StartX=-4.03109 StartY=3.5 StartZ=0 EndX=-1 EndY=5.25 EndZ=0
    g27: Circle [constr] CenterX=-4.03109 CenterY=7 CenterZ=0 NormalX=0 NormalY=0 NormalZ=1 AngleXU=0 Radius=3.5
    g28: LineSegment StartX=-4.96891 StartY=-1.75 StartZ=0 EndX=-4.96891 EndY=1.75 EndZ=0
    g29: LineSegment StartX=-4.96891 StartY=1.75 StartZ=0 EndX=-8 EndY=3.5 EndZ=0
    g30: LineSegment StartX=-8 StartY=3.5 StartZ=0 EndX=-11.0311 EndY=1.75 EndZ=0
    g31: LineSegment StartX=-11.0311 StartY=1.75 StartZ=0 EndX=-11.0311 EndY=-1.75 EndZ=0
    g32: LineSegment StartX=-11.0311 StartY=-1.75 StartZ=0 EndX=-8 EndY=-3.5 EndZ=0
    g33: LineSegment StartX=-8 StartY=-3.5 StartZ=0 EndX=-4.96891 EndY=-1.75 EndZ=0
    g34: Circle [constr] CenterX=-8 CenterY=0 CenterZ=0 NormalX=0 NormalY=0 NormalZ=1 AngleXU=0 Radius=3.5
    g35: LineSegment StartX=-4.03109 StartY=-3.5 StartZ=0 EndX=-7.06218 EndY=-5.25 EndZ=0
    g36: LineSegment StartX=-7.06218 StartY=-5.25 StartZ=0 EndX=-7.06218 EndY=-8.75 EndZ=0
    g37: LineSegment StartX=-7.06218 StartY=-8.75 StartZ=0 EndX=-4.03109 EndY=-10.5 EndZ=0
    g38: LineSegment StartX=-4.03109 StartY=-10.5 StartZ=0 EndX=-1 EndY=-8.75 EndZ=0
    g39: LineSegment StartX=-1 StartY=-8.75 StartZ=0 EndX=-1 EndY=-5.25 EndZ=0
    g40: LineSegment StartX=-1 StartY=-5.25 StartZ=0 EndX=-4.03109 EndY=-3.5 EndZ=0
    g41: Circle [constr] CenterX=-4.03109 CenterY=-7 CenterZ=0 NormalX=0 NormalY=0 NormalZ=1 AngleXU=0 Radius=3.5
    g42: LineSegment StartX=4.03109 StartY=-3.5 StartZ=0 EndX=1 EndY=-5.25 EndZ=0
    g43: LineSegment StartX=1 StartY=-5.25 StartZ=0 EndX=1 EndY=-8.75 EndZ=0
    g44: LineSegment StartX=1 StartY=-8.75 StartZ=0 EndX=4.03109 EndY=-10.5 EndZ=0
    g45: LineSegment StartX=4.03109 StartY=-10.5 StartZ=0 EndX=7.06218 EndY=-8.75 EndZ=0
    g46: LineSegment StartX=7.06218 StartY=-8.75 StartZ=0 EndX=7.06218 EndY=-5.25 EndZ=0
    g47: LineSegment StartX=7.06218 StartY=-5.25 StartZ=0 EndX=4.03109 EndY=-3.5 EndZ=0
    g48: Circle [constr] CenterX=4.03109 CenterY=-7 CenterZ=0 NormalX=0 NormalY=0 NormalZ=1 AngleXU=0 Radius=3.5
  constraints (117):
    c: Coincident(g0,g1)
    c: Coincident(g1,g2)
    c: Coincident(g2,g3)
    c: Coincident(g3,g4)
    c: Coincident(g4,g5)
    c: Coincident(g5,g0)
    c: Equal(g0, g1-g5) x5
    c: PointOnObject(g0,g6)
    c: PointOnObject(g1,g6)
    c: PointOnObject(g2,g6)
    c: PointOnObject(g3,g6)
    c: PointOnObject(g4,g6)
    c: PointOnObject(g5,g6)
    c: Coincident(g6,g-1)
    c: Diameter(g6) = 7
    c: PointOnObject(g0,g-2)
    c: Coincident(g7,g8)
    c: Coincident(g8,g9)
    c: Coincident(g9,g10)
    c: Coincident(g10,g11)
    c: Coincident(g11,g12)
    c: Coincident(g12,g7)
    c: Equal(g7, g8-g12) x5
    c: PointOnObject(g7,g13)
    c: PointOnObject(g8,g13)
    c: PointOnObject(g9,g13)
    c: PointOnObject(g10,g13)
    c: PointOnObject(g11,g13)
    c: PointOnObject(g12,g13)
    c: PointOnObject(g13,g-1)
    c: Diameter(g13) = 7
    c: Distance(g6,g13) = 8
    c: Horizontal(g0,g10)
    c: Coincident(g14,g15)
    c: Coincident(g15,g16)
    c: Coincident(g16,g17)
    c: Coincident(g17,g18)
    c: Coincident(g18,g19)
    c: Coincident(g19,g14)
    c: Equal(g14, g15-g19) x5
    c: PointOnObject(g14,g20)
    c: PointOnObject(g15,g20)
    c: PointOnObject(g16,g20)
    c: PointOnObject(g17,g20)
    c: PointOnObject(g18,g20)
    c: PointOnObject(g19,g20)
    c: Diameter(g20) = 7
    c: DistanceY(g-1,g20) = 7
    c: Vertical(g18)
    c: Distance(g17,g-2) = 1
    c: Coincident(g21,g22)
    c: Coincident(g22,g23)
    c: Coincident(g23,g24)
    c: Coincident(g24,g25)
    c: Coincident(g25,g26)
    c: Coincident(g26,g21)
    c: Equal(g21, g22-g26) x5
    c: PointOnObject(g21,g27)
    c: PointOnObject(g22,g27)
    c: PointOnObject(g23,g27)
    c: PointOnObject(g24,g27)
    c: PointOnObject(g25,g27)
    c: PointOnObject(g26,g27)
    c: Diameter(g27) = 7
    c: DistanceY(g-1,g27) = 7
    c: DistanceX(g21,g-1) = 1
    c: Vertical(g21)
    c: Coincident(g28,g29)
    c: Coincident(g29,g30)
    c: Coincident(g30,g31)
    c: Coincident(g31,g32)
    c: Coincident(g32,g33)
    c: Coincident(g33,g28)
    c: Equal(g28, g29-g33) x5
    c: PointOnObject(g28,g34)
    c: PointOnObject(g29,g34)
    c: PointOnObject(g30,g34)
    c: PointOnObject(g31,g34)
    c: PointOnObject(g32,g34)
    c: PointOnObject(g33,g34)
    c: PointOnObject(g34,g-1)
    c: Diameter(g34) = 7
    c: Vertical(g31)
    c: DistanceX(g34,g-1) = 8
    c: Coincident(g35,g36)
    c: Coincident(g36,g37)
    c: Coincident(g37,g38)
    c: Coincident(g38,g39)
    c: Coincident(g39,g40)
    c: Coincident(g40,g35)
    c: Equal(g35, g36-g40) x5
    c: PointOnObject(g35,g41)
    c: PointOnObject(g36,g41)
    c: PointOnObject(g37,g41)
    c: PointOnObject(g38,g41)
    c: PointOnObject(g39,g41)
    c: PointOnObject(g40,g41)
    c: Coincident(g42,g43)
    c: Coincident(g43,g44)
    c: Coincident(g44,g45)
    c: Coincident(g45,g46)
    c: Coincident(g46,g47)
    c: Coincident(g47,g42)
    c: Equal(g42, g43-g47) x5
    c: PointOnObject(g42,g48)
    c: PointOnObject(g43,g48)
    c: PointOnObject(g44,g48)
    c: PointOnObject(g45,g48)
    c: PointOnObject(g46,g48)
    c: PointOnObject(g47,g48)
    c: Equal(g41,g48)
    c: Diameter(g41) = 7
    c: Vertical(g39)
    c: Vertical(g43)
    c: Distance(g-2,g39) = 1
    c: Symmetric(g38,g43,g-2)
    c: Distance(g41,g-1) = 7
FEATURE [Part::Extrusion] Extrude527  label="hex142"
  Base = -> Sketch535
  Dir = (0,-1,2e-16)
  DirMode = 2
  FaceMakerClass = Part::FaceMakerBullseye
  FaceMakerMode = 3
  LengthFwd = 10
  LengthRev = 0
  Placement = pos=(104,0,0) rot=(0,0,1;0rad)
  Solid = true
  Symmetric = false
FEATURE [Sketcher::SketchObject] Sketch536
  ArcFitTolerance = 1e-06
  FullyConstrained = true
  MakeInternals = false
  Placement = pos=(0,0,0) rot=(1,0,0;1.5708rad)
  sketch-geometry (49):
    g0: LineSegment StartX=1e-16 StartY=3.5 StartZ=0 EndX=-3.03109 EndY=1.75 EndZ=0
    g1: LineSegment StartX=-3.03109 StartY=1.75 StartZ=0 EndX=-3.03109 EndY=-1.75 EndZ=0
    g2: LineSegment StartX=-3.03109 StartY=-1.75 StartZ=0 EndX=-1e-16 EndY=-3.5 EndZ=0
    g3: LineSegment StartX=-1e-16 StartY=-3.5 StartZ=0 EndX=3.03109 EndY=-1.75 EndZ=0
    g4: LineSegment StartX=3.03109 StartY=-1.75 StartZ=0 EndX=3.03109 EndY=1.75 EndZ=0
    g5: LineSegment StartX=3.03109 StartY=1.75 StartZ=0 EndX=1e-16 EndY=3.5 EndZ=0
    g6: Circle [constr] CenterX=0 CenterY=0 CenterZ=0 NormalX=0 NormalY=0 NormalZ=1 AngleXU=0 Radius=3.5
    g7: LineSegment StartX=4.96892 StartY=-1.75002 StartZ=0 EndX=8.00002 EndY=-3.5 EndZ=0
    g8: LineSegment StartX=8.00002 StartY=-3.5 StartZ=0 EndX=11.0311 EndY=-1.74998 EndZ=0
    g9: LineSegment StartX=11.0311 StartY=-1.74998 StartZ=0 EndX=11.0311 EndY=1.75002 EndZ=0
    g10: LineSegment StartX=11.0311 StartY=1.75002 StartZ=0 EndX=7.99998 EndY=3.5 EndZ=0
    g11: LineSegment StartX=7.99998 StartY=3.5 StartZ=0 EndX=4.9689 EndY=1.74998 EndZ=0
    g12: LineSegment StartX=4.9689 StartY=1.74998 StartZ=0 EndX=4.96892 EndY=-1.75002 EndZ=0
    g13: Circle [constr] CenterX=8 CenterY=0 CenterZ=0 NormalX=0 NormalY=0 NormalZ=1 AngleXU=0 Radius=3.5
    g14: LineSegment StartX=4.03109 StartY=3.5 StartZ=0 EndX=7.06218 EndY=5.25 EndZ=0
    g15: LineSegment StartX=7.06218 StartY=5.25 StartZ=0 EndX=7.06218 EndY=8.75 EndZ=0
    g16: LineSegment StartX=7.06218 StartY=8.75 StartZ=0 EndX=4.03109 EndY=10.5 EndZ=0
    g17: LineSegment StartX=4.03109 StartY=10.5 StartZ=0 EndX=1 EndY=8.75 EndZ=0
    g18: LineSegment StartX=1 StartY=8.75 StartZ=0 EndX=1 EndY=5.25 EndZ=0
    g19: LineSegment StartX=1 StartY=5.25 StartZ=0 EndX=4.03109 EndY=3.5 EndZ=0
    g20: Circle [constr] CenterX=4.03109 CenterY=7 CenterZ=0 NormalX=0 NormalY=0 NormalZ=1 AngleXU=0 Radius=3.5
    g21: LineSegment StartX=-1 StartY=5.25 StartZ=0 EndX=-1 EndY=8.75 EndZ=0
    g22: LineSegment StartX=-1 StartY=8.75 StartZ=0 EndX=-4.03109 EndY=10.5 EndZ=0
    g23: LineSegment StartX=-4.03109 StartY=10.5 StartZ=0 EndX=-7.06218 EndY=8.75 EndZ=0
    g24: LineSegment StartX=-7.06218 StartY=8.75 StartZ=0 EndX=-7.06218 EndY=5.25 EndZ=0
    g25: LineSegment StartX=-7.06218 StartY=5.25 StartZ=0 EndX=-4.03109 EndY=3.5 EndZ=0
    g26: LineSegment StartX=-4.03109 StartY=3.5 StartZ=0 EndX=-1 EndY=5.25 EndZ=0
    g27: Circle [constr] CenterX=-4.03109 CenterY=7 CenterZ=0 NormalX=0 NormalY=0 NormalZ=1 AngleXU=0 Radius=3.5
    g28: LineSegment StartX=-4.96891 StartY=-1.75 StartZ=0 EndX=-4.96891 EndY=1.75 EndZ=0
    g29: LineSegment StartX=-4.96891 StartY=1.75 StartZ=0 EndX=-8 EndY=3.5 EndZ=0
    g30: LineSegment StartX=-8 StartY=3.5 StartZ=0 EndX=-11.0311 EndY=1.75 EndZ=0
    g31: LineSegment StartX=-11.0311 StartY=1.75 StartZ=0 EndX=-11.0311 EndY=-1.75 EndZ=0
    g32: LineSegment StartX=-11.0311 StartY=-1.75 StartZ=0 EndX=-8 EndY=-3.5 EndZ=0
    g33: LineSegment StartX=-8 StartY=-3.5 StartZ=0 EndX=-4.96891 EndY=-1.75 EndZ=0
    g34: Circle [constr] CenterX=-8 CenterY=0 CenterZ=0 NormalX=0 NormalY=0 NormalZ=1 AngleXU=0 Radius=3.5
    g35: LineSegment StartX=-4.03109 StartY=-3.5 StartZ=0 EndX=-7.06218 EndY=-5.25 EndZ=0
    g36: LineSegment StartX=-7.06218 StartY=-5.25 StartZ=0 EndX=-7.06218 EndY=-8.75 EndZ=0
    g37: LineSegment StartX=-7.06218 StartY=-8.75 StartZ=0 EndX=-4.03109 EndY=-10.5 EndZ=0
    g38: LineSegment StartX=-4.03109 StartY=-10.5 StartZ=0 EndX=-1 EndY=-8.75 EndZ=0
    g39: LineSegment StartX=-1 StartY=-8.75 StartZ=0 EndX=-1 EndY=-5.25 EndZ=0
    g40: LineSegment StartX=-1 StartY=-5.25 StartZ=0 EndX=-4.03109 EndY=-3.5 EndZ=0
    g41: Circle [constr] CenterX=-4.03109 CenterY=-7 CenterZ=0 NormalX=0 NormalY=0 NormalZ=1 AngleXU=0 Radius=3.5
    g42: LineSegment StartX=4.03109 StartY=-3.5 StartZ=0 EndX=1 EndY=-5.25 EndZ=0
    g43: LineSegment StartX=1 StartY=-5.25 StartZ=0 EndX=1 EndY=-8.75 EndZ=0
    g44: LineSegment StartX=1 StartY=-8.75 StartZ=0 EndX=4.03109 EndY=-10.5 EndZ=0
    g45: LineSegment StartX=4.03109 StartY=-10.5 StartZ=0 EndX=7.06218 EndY=-8.75 EndZ=0
    g46: LineSegment StartX=7.06218 StartY=-8.75 StartZ=0 EndX=7.06218 EndY=-5.25 EndZ=0
    g47: LineSegment StartX=7.06218 StartY=-5.25 StartZ=0 EndX=4.03109 EndY=-3.5 EndZ=0
    g48: Circle [constr] CenterX=4.03109 CenterY=-7 CenterZ=0 NormalX=0 NormalY=0 NormalZ=1 AngleXU=0 Radius=3.5
  constraints (117):
    c: Coincident(g0,g1)
    c: Coincident(g1,g2)
    c: Coincident(g2,g3)
    c: Coincident(g3,g4)
    c: Coincident(g4,g5)
    c: Coincident(g5,g0)
    c: Equal(g0, g1-g5) x5
    c: PointOnObject(g0,g6)
    c: PointOnObject(g1,g6)
    c: PointOnObject(g2,g6)
    c: PointOnObject(g3,g6)
    c: PointOnObject(g4,g6)
    c: PointOnObject(g5,g6)
    c: Coincident(g6,g-1)
    c: Diameter(g6) = 7
    c: PointOnObject(g0,g-2)
    c: Coincident(g7,g8)
    c: Coincident(g8,g9)
    c: Coincident(g9,g10)
    c: Coincident(g10,g11)
    c: Coincident(g11,g12)
    c: Coincident(g12,g7)
    c: Equal(g7, g8-g12) x5
    c: PointOnObject(g7,g13)
    c: PointOnObject(g8,g13)
    c: PointOnObject(g9,g13)
    c: PointOnObject(g10,g13)
    c: PointOnObject(g11,g13)
    c: PointOnObject(g12,g13)
    c: PointOnObject(g13,g-1)
    c: Diameter(g13) = 7
    c: Distance(g6,g13) = 8
    c: Horizontal(g0,g10)
    c: Coincident(g14,g15)
    c: Coincident(g15,g16)
    c: Coincident(g16,g17)
    c: Coincident(g17,g18)
    c: Coincident(g18,g19)
    c: Coincident(g19,g14)
    c: Equal(g14, g15-g19) x5
    c: PointOnObject(g14,g20)
    c: PointOnObject(g15,g20)
    c: PointOnObject(g16,g20)
    c: PointOnObject(g17,g20)
    c: PointOnObject(g18,g20)
    c: PointOnObject(g19,g20)
    c: Diameter(g20) = 7
    c: DistanceY(g-1,g20) = 7
    c: Vertical(g18)
    c: Distance(g17,g-2) = 1
    c: Coincident(g21,g22)
    c: Coincident(g22,g23)
    c: Coincident(g23,g24)
    c: Coincident(g24,g25)
    c: Coincident(g25,g26)
    c: Coincident(g26,g21)
    c: Equal(g21, g22-g26) x5
    c: PointOnObject(g21,g27)
    c: PointOnObject(g22,g27)
    c: PointOnObject(g23,g27)
    c: PointOnObject(g24,g27)
    c: PointOnObject(g25,g27)
    c: PointOnObject(g26,g27)
    c: Diameter(g27) = 7
    c: DistanceY(g-1,g27) = 7
    c: DistanceX(g21,g-1) = 1
    c: Vertical(g21)
    c: Coincident(g28,g29)
    c: Coincident(g29,g30)
    c: Coincident(g30,g31)
    c: Coincident(g31,g32)
    c: Coincident(g32,g33)
    c: Coincident(g33,g28)
    c: Equal(g28, g29-g33) x5
    c: PointOnObject(g28,g34)
    c: PointOnObject(g29,g34)
    c: PointOnObject(g30,g34)
    c: PointOnObject(g31,g34)
    c: PointOnObject(g32,g34)
    c: PointOnObject(g33,g34)
    c: PointOnObject(g34,g-1)
    c: Diameter(g34) = 7
    c: Vertical(g31)
    c: DistanceX(g34,g-1) = 8
    c: Coincident(g35,g36)
    c: Coincident(g36,g37)
    c: Coincident(g37,g38)
    c: Coincident(g38,g39)
    c: Coincident(g39,g40)
    c: Coincident(g40,g35)
    c: Equal(g35, g36-g40) x5
    c: PointOnObject(g35,g41)
    c: PointOnObject(g36,g41)
    c: PointOnObject(g37,g41)
    c: PointOnObject(g38,g41)
    c: PointOnObject(g39,g41)
    c: PointOnObject(g40,g41)
    c: Coincident(g42,g43)
    c: Coincident(g43,g44)
    c: Coincident(g44,g45)
    c: Coincident(g45,g46)
    c: Coincident(g46,g47)
    c: Coincident(g47,g42)
    c: Equal(g42, g43-g47) x5
    c: PointOnObject(g42,g48)
    c: PointOnObject(g43,g48)
    c: PointOnObject(g44,g48)
    c: PointOnObject(g45,g48)
    c: PointOnObject(g46,g48)
    c: PointOnObject(g47,g48)
    c: Equal(g41,g48)
    c: Diameter(g41) = 7
    c: Vertical(g39)
    c: Vertical(g43)
    c: Distance(g-2,g39) = 1
    c: Symmetric(g38,g43,g-2)
    c: Distance(g41,g-1) = 7
FEATURE [Part::Extrusion] Extrude528  label="hex143"
  Base = -> Sketch536
  Dir = (0,-1,2e-16)
  DirMode = 2
  FaceMakerClass = Part::FaceMakerBullseye
  FaceMakerMode = 3
  LengthFwd = 10
  LengthRev = 0
  Placement = pos=(96,0,-14) rot=(0,0,1;0rad)
  Solid = true
  Symmetric = false
FEATURE [Sketcher::SketchObject] Sketch537
  ArcFitTolerance = 1e-06
  FullyConstrained = true
  MakeInternals = false
  Placement = pos=(0,0,0) rot=(1,0,0;1.5708rad)
  sketch-geometry (49):
    g0: LineSegment StartX=1e-16 StartY=3.5 StartZ=0 EndX=-3.03109 EndY=1.75 EndZ=0
    g1: LineSegment StartX=-3.03109 StartY=1.75 StartZ=0 EndX=-3.03109 EndY=-1.75 EndZ=0
    g2: LineSegment StartX=-3.03109 StartY=-1.75 StartZ=0 EndX=-1e-16 EndY=-3.5 EndZ=0
    g3: LineSegment StartX=-1e-16 StartY=-3.5 StartZ=0 EndX=3.03109 EndY=-1.75 EndZ=0
    g4: LineSegment StartX=3.03109 StartY=-1.75 StartZ=0 EndX=3.03109 EndY=1.75 EndZ=0
    g5: LineSegment StartX=3.03109 StartY=1.75 StartZ=0 EndX=1e-16 EndY=3.5 EndZ=0
    g6: Circle [constr] CenterX=0 CenterY=0 CenterZ=0 NormalX=0 NormalY=0 NormalZ=1 AngleXU=0 Radius=3.5
    g7: LineSegment StartX=4.96892 StartY=-1.75002 StartZ=0 EndX=8.00002 EndY=-3.5 EndZ=0
    g8: LineSegment StartX=8.00002 StartY=-3.5 StartZ=0 EndX=11.0311 EndY=-1.74998 EndZ=0
    g9: LineSegment StartX=11.0311 StartY=-1.74998 StartZ=0 EndX=11.0311 EndY=1.75002 EndZ=0
    g10: LineSegment StartX=11.0311 StartY=1.75002 StartZ=0 EndX=7.99998 EndY=3.5 EndZ=0
    g11: LineSegment StartX=7.99998 StartY=3.5 StartZ=0 EndX=4.9689 EndY=1.74998 EndZ=0
    g12: LineSegment StartX=4.9689 StartY=1.74998 StartZ=0 EndX=4.96892 EndY=-1.75002 EndZ=0
    g13: Circle [constr] CenterX=8 CenterY=0 CenterZ=0 NormalX=0 NormalY=0 NormalZ=1 AngleXU=0 Radius=3.5
    g14: LineSegment StartX=4.03109 StartY=3.5 StartZ=0 EndX=7.06218 EndY=5.25 EndZ=0
    g15: LineSegment StartX=7.06218 StartY=5.25 StartZ=0 EndX=7.06218 EndY=8.75 EndZ=0
    g16: LineSegment StartX=7.06218 StartY=8.75 StartZ=0 EndX=4.03109 EndY=10.5 EndZ=0
    g17: LineSegment StartX=4.03109 StartY=10.5 StartZ=0 EndX=1 EndY=8.75 EndZ=0
    g18: LineSegment StartX=1 StartY=8.75 StartZ=0 EndX=1 EndY=5.25 EndZ=0
    g19: LineSegment StartX=1 StartY=5.25 StartZ=0 EndX=4.03109 EndY=3.5 EndZ=0
    g20: Circle [constr] CenterX=4.03109 CenterY=7 CenterZ=0 NormalX=0 NormalY=0 NormalZ=1 AngleXU=0 Radius=3.5
    g21: LineSegment StartX=-1 StartY=5.25 StartZ=0 EndX=-1 EndY=8.75 EndZ=0
    g22: LineSegment StartX=-1 StartY=8.75 StartZ=0 EndX=-4.03109 EndY=10.5 EndZ=0
    g23: LineSegment StartX=-4.03109 StartY=10.5 StartZ=0 EndX=-7.06218 EndY=8.75 EndZ=0
    g24: LineSegment StartX=-7.06218 StartY=8.75 StartZ=0 EndX=-7.06218 EndY=5.25 EndZ=0
    g25: LineSegment StartX=-7.06218 StartY=5.25 StartZ=0 EndX=-4.03109 EndY=3.5 EndZ=0
    g26: LineSegment StartX=-4.03109 StartY=3.5 StartZ=0 EndX=-1 EndY=5.25 EndZ=0
    g27: Circle [constr] CenterX=-4.03109 CenterY=7 CenterZ=0 NormalX=0 NormalY=0 NormalZ=1 AngleXU=0 Radius=3.5
    g28: LineSegment StartX=-4.96891 StartY=-1.75 StartZ=0 EndX=-4.96891 EndY=1.75 EndZ=0
    g29: LineSegment StartX=-4.96891 StartY=1.75 StartZ=0 EndX=-8 EndY=3.5 EndZ=0
    g30: LineSegment StartX=-8 StartY=3.5 StartZ=0 EndX=-11.0311 EndY=1.75 EndZ=0
    g31: LineSegment StartX=-11.0311 StartY=1.75 StartZ=0 EndX=-11.0311 EndY=-1.75 EndZ=0
    g32: LineSegment StartX=-11.0311 StartY=-1.75 StartZ=0 EndX=-8 EndY=-3.5 EndZ=0
    g33: LineSegment StartX=-8 StartY=-3.5 StartZ=0 EndX=-4.96891 EndY=-1.75 EndZ=0
    g34: Circle [constr] CenterX=-8 CenterY=0 CenterZ=0 NormalX=0 NormalY=0 NormalZ=1 AngleXU=0 Radius=3.5
    g35: LineSegment StartX=-4.03109 StartY=-3.5 StartZ=0 EndX=-7.06218 EndY=-5.25 EndZ=0
    g36: LineSegment StartX=-7.06218 StartY=-5.25 StartZ=0 EndX=-7.06218 EndY=-8.75 EndZ=0
    g37: LineSegment StartX=-7.06218 StartY=-8.75 StartZ=0 EndX=-4.03109 EndY=-10.5 EndZ=0
    g38: LineSegment StartX=-4.03109 StartY=-10.5 StartZ=0 EndX=-1 EndY=-8.75 EndZ=0
    g39: LineSegment StartX=-1 StartY=-8.75 StartZ=0 EndX=-1 EndY=-5.25 EndZ=0
    g40: LineSegment StartX=-1 StartY=-5.25 StartZ=0 EndX=-4.03109 EndY=-3.5 EndZ=0
    g41: Circle [constr] CenterX=-4.03109 CenterY=-7 CenterZ=0 NormalX=0 NormalY=0 NormalZ=1 AngleXU=0 Radius=3.5
    g42: LineSegment StartX=4.03109 StartY=-3.5 StartZ=0 EndX=1 EndY=-5.25 EndZ=0
    g43: LineSegment StartX=1 StartY=-5.25 StartZ=0 EndX=1 EndY=-8.75 EndZ=0
    g44: LineSegment StartX=1 StartY=-8.75 StartZ=0 EndX=4.03109 EndY=-10.5 EndZ=0
    g45: LineSegment StartX=4.03109 StartY=-10.5 StartZ=0 EndX=7.06218 EndY=-8.75 EndZ=0
    g46: LineSegment StartX=7.06218 StartY=-8.75 StartZ=0 EndX=7.06218 EndY=-5.25 EndZ=0
    g47: LineSegment StartX=7.06218 StartY=-5.25 StartZ=0 EndX=4.03109 EndY=-3.5 EndZ=0
    g48: Circle [constr] CenterX=4.03109 CenterY=-7 CenterZ=0 NormalX=0 NormalY=0 NormalZ=1 AngleXU=0 Radius=3.5
  constraints (117):
    c: Coincident(g0,g1)
    c: Coincident(g1,g2)
    c: Coincident(g2,g3)
    c: Coincident(g3,g4)
    c: Coincident(g4,g5)
    c: Coincident(g5,g0)
    c: Equal(g0, g1-g5) x5
    c: PointOnObject(g0,g6)
    c: PointOnObject(g1,g6)
    c: PointOnObject(g2,g6)
    c: PointOnObject(g3,g6)
    c: PointOnObject(g4,g6)
    c: PointOnObject(g5,g6)
    c: Coincident(g6,g-1)
    c: Diameter(g6) = 7
    c: PointOnObject(g0,g-2)
    c: Coincident(g7,g8)
    c: Coincident(g8,g9)
    c: Coincident(g9,g10)
    c: Coincident(g10,g11)
    c: Coincident(g11,g12)
    c: Coincident(g12,g7)
    c: Equal(g7, g8-g12) x5
    c: PointOnObject(g7,g13)
    c: PointOnObject(g8,g13)
    c: PointOnObject(g9,g13)
    c: PointOnObject(g10,g13)
    c: PointOnObject(g11,g13)
    c: PointOnObject(g12,g13)
    c: PointOnObject(g13,g-1)
    c: Diameter(g13) = 7
    c: Distance(g6,g13) = 8
    c: Horizontal(g0,g10)
    c: Coincident(g14,g15)
    c: Coincident(g15,g16)
    c: Coincident(g16,g17)
    c: Coincident(g17,g18)
    c: Coincident(g18,g19)
    c: Coincident(g19,g14)
    c: Equal(g14, g15-g19) x5
    c: PointOnObject(g14,g20)
    c: PointOnObject(g15,g20)
    c: PointOnObject(g16,g20)
    c: PointOnObject(g17,g20)
    c: PointOnObject(g18,g20)
    c: PointOnObject(g19,g20)
    c: Diameter(g20) = 7
    c: DistanceY(g-1,g20) = 7
    c: Vertical(g18)
    c: Distance(g17,g-2) = 1
    c: Coincident(g21,g22)
    c: Coincident(g22,g23)
    c: Coincident(g23,g24)
    c: Coincident(g24,g25)
    c: Coincident(g25,g26)
    c: Coincident(g26,g21)
    c: Equal(g21, g22-g26) x5
    c: PointOnObject(g21,g27)
    c: PointOnObject(g22,g27)
    c: PointOnObject(g23,g27)
    c: PointOnObject(g24,g27)
    c: PointOnObject(g25,g27)
    c: PointOnObject(g26,g27)
    c: Diameter(g27) = 7
    c: DistanceY(g-1,g27) = 7
    c: DistanceX(g21,g-1) = 1
    c: Vertical(g21)
    c: Coincident(g28,g29)
    c: Coincident(g29,g30)
    c: Coincident(g30,g31)
    c: Coincident(g31,g32)
    c: Coincident(g32,g33)
    c: Coincident(g33,g28)
    c: Equal(g28, g29-g33) x5
    c: PointOnObject(g28,g34)
    c: PointOnObject(g29,g34)
    c: PointOnObject(g30,g34)
    c: PointOnObject(g31,g34)
    c: PointOnObject(g32,g34)
    c: PointOnObject(g33,g34)
    c: PointOnObject(g34,g-1)
    c: Diameter(g34) = 7
    c: Vertical(g31)
    c: DistanceX(g34,g-1) = 8
    c: Coincident(g35,g36)
    c: Coincident(g36,g37)
    c: Coincident(g37,g38)
    c: Coincident(g38,g39)
    c: Coincident(g39,g40)
    c: Coincident(g40,g35)
    c: Equal(g35, g36-g40) x5
    c: PointOnObject(g35,g41)
    c: PointOnObject(g36,g41)
    c: PointOnObject(g37,g41)
    c: PointOnObject(g38,g41)
    c: PointOnObject(g39,g41)
    c: PointOnObject(g40,g41)
    c: Coincident(g42,g43)
    c: Coincident(g43,g44)
    c: Coincident(g44,g45)
    c: Coincident(g45,g46)
    c: Coincident(g46,g47)
    c: Coincident(g47,g42)
    c: Equal(g42, g43-g47) x5
    c: PointOnObject(g42,g48)
    c: PointOnObject(g43,g48)
    c: PointOnObject(g44,g48)
    c: PointOnObject(g45,g48)
    c: PointOnObject(g46,g48)
    c: PointOnObject(g47,g48)
    c: Equal(g41,g48)
    c: Diameter(g41) = 7
    c: Vertical(g39)
    c: Vertical(g43)
    c: Distance(g-2,g39) = 1
    c: Symmetric(g38,g43,g-2)
    c: Distance(g41,g-1) = 7
FEATURE [Part::Extrusion] Extrude529  label="hex144"
  Base = -> Sketch537
  Dir = (0,-1,2e-16)
  DirMode = 2
  FaceMakerClass = Part::FaceMakerBullseye
  FaceMakerMode = 3
  LengthFwd = 10
  LengthRev = 0
  Placement = pos=(88,0,-28) rot=(0,0,1;0rad)
  Solid = true
  Symmetric = false
FEATURE [Sketcher::SketchObject] Sketch538
  ArcFitTolerance = 1e-06
  FullyConstrained = true
  MakeInternals = false
  Placement = pos=(0,0,0) rot=(1,0,0;1.5708rad)
  sketch-geometry (49):
    g0: LineSegment StartX=1e-16 StartY=3.5 StartZ=0 EndX=-3.03109 EndY=1.75 EndZ=0
    g1: LineSegment StartX=-3.03109 StartY=1.75 StartZ=0 EndX=-3.03109 EndY=-1.75 EndZ=0
    g2: LineSegment StartX=-3.03109 StartY=-1.75 StartZ=0 EndX=-1e-16 EndY=-3.5 EndZ=0
    g3: LineSegment StartX=-1e-16 StartY=-3.5 StartZ=0 EndX=3.03109 EndY=-1.75 EndZ=0
    g4: LineSegment StartX=3.03109 StartY=-1.75 StartZ=0 EndX=3.03109 EndY=1.75 EndZ=0
    g5: LineSegment StartX=3.03109 StartY=1.75 StartZ=0 EndX=1e-16 EndY=3.5 EndZ=0
    g6: Circle [constr] CenterX=0 CenterY=0 CenterZ=0 NormalX=0 NormalY=0 NormalZ=1 AngleXU=0 Radius=3.5
    g7: LineSegment StartX=4.96892 StartY=-1.75002 StartZ=0 EndX=8.00002 EndY=-3.5 EndZ=0
    g8: LineSegment StartX=8.00002 StartY=-3.5 StartZ=0 EndX=11.0311 EndY=-1.74998 EndZ=0
    g9: LineSegment StartX=11.0311 StartY=-1.74998 StartZ=0 EndX=11.0311 EndY=1.75002 EndZ=0
    g10: LineSegment StartX=11.0311 StartY=1.75002 StartZ=0 EndX=7.99998 EndY=3.5 EndZ=0
    g11: LineSegment StartX=7.99998 StartY=3.5 StartZ=0 EndX=4.9689 EndY=1.74998 EndZ=0
    g12: LineSegment StartX=4.9689 StartY=1.74998 StartZ=0 EndX=4.96892 EndY=-1.75002 EndZ=0
    g13: Circle [constr] CenterX=8 CenterY=0 CenterZ=0 NormalX=0 NormalY=0 NormalZ=1 AngleXU=0 Radius=3.5
    g14: LineSegment StartX=4.03109 StartY=3.5 StartZ=0 EndX=7.06218 EndY=5.25 EndZ=0
    g15: LineSegment StartX=7.06218 StartY=5.25 StartZ=0 EndX=7.06218 EndY=8.75 EndZ=0
    g16: LineSegment StartX=7.06218 StartY=8.75 StartZ=0 EndX=4.03109 EndY=10.5 EndZ=0
    g17: LineSegment StartX=4.03109 StartY=10.5 StartZ=0 EndX=1 EndY=8.75 EndZ=0
    g18: LineSegment StartX=1 StartY=8.75 StartZ=0 EndX=1 EndY=5.25 EndZ=0
    g19: LineSegment StartX=1 StartY=5.25 StartZ=0 EndX=4.03109 EndY=3.5 EndZ=0
    g20: Circle [constr] CenterX=4.03109 CenterY=7 CenterZ=0 NormalX=0 NormalY=0 NormalZ=1 AngleXU=0 Radius=3.5
    g21: LineSegment StartX=-1 StartY=5.25 StartZ=0 EndX=-1 EndY=8.75 EndZ=0
    g22: LineSegment StartX=-1 StartY=8.75 StartZ=0 EndX=-4.03109 EndY=10.5 EndZ=0
    g23: LineSegment StartX=-4.03109 StartY=10.5 StartZ=0 EndX=-7.06218 EndY=8.75 EndZ=0
    g24: LineSegment StartX=-7.06218 StartY=8.75 StartZ=0 EndX=-7.06218 EndY=5.25 EndZ=0
    g25: LineSegment StartX=-7.06218 StartY=5.25 StartZ=0 EndX=-4.03109 EndY=3.5 EndZ=0
    g26: LineSegment StartX=-4.03109 StartY=3.5 StartZ=0 EndX=-1 EndY=5.25 EndZ=0
    g27: Circle [constr] CenterX=-4.03109 CenterY=7 CenterZ=0 NormalX=0 NormalY=0 NormalZ=1 AngleXU=0 Radius=3.5
    g28: LineSegment StartX=-4.96891 StartY=-1.75 StartZ=0 EndX=-4.96891 EndY=1.75 EndZ=0
    g29: LineSegment StartX=-4.96891 StartY=1.75 StartZ=0 EndX=-8 EndY=3.5 EndZ=0
    g30: LineSegment StartX=-8 StartY=3.5 StartZ=0 EndX=-11.0311 EndY=1.75 EndZ=0
    g31: LineSegment StartX=-11.0311 StartY=1.75 StartZ=0 EndX=-11.0311 EndY=-1.75 EndZ=0
    g32: LineSegment StartX=-11.0311 StartY=-1.75 StartZ=0 EndX=-8 EndY=-3.5 EndZ=0
    g33: LineSegment StartX=-8 StartY=-3.5 StartZ=0 EndX=-4.96891 EndY=-1.75 EndZ=0
    g34: Circle [constr] CenterX=-8 CenterY=0 CenterZ=0 NormalX=0 NormalY=0 NormalZ=1 AngleXU=0 Radius=3.5
    g35: LineSegment StartX=-4.03109 StartY=-3.5 StartZ=0 EndX=-7.06218 EndY=-5.25 EndZ=0
    g36: LineSegment StartX=-7.06218 StartY=-5.25 StartZ=0 EndX=-7.06218 EndY=-8.75 EndZ=0
    g37: LineSegment StartX=-7.06218 StartY=-8.75 StartZ=0 EndX=-4.03109 EndY=-10.5 EndZ=0
    g38: LineSegment StartX=-4.03109 StartY=-10.5 StartZ=0 EndX=-1 EndY=-8.75 EndZ=0
    g39: LineSegment StartX=-1 StartY=-8.75 StartZ=0 EndX=-1 EndY=-5.25 EndZ=0
    g40: LineSegment StartX=-1 StartY=-5.25 StartZ=0 EndX=-4.03109 EndY=-3.5 EndZ=0
    g41: Circle [constr] CenterX=-4.03109 CenterY=-7 CenterZ=0 NormalX=0 NormalY=0 NormalZ=1 AngleXU=0 Radius=3.5
    g42: LineSegment StartX=4.03109 StartY=-3.5 StartZ=0 EndX=1 EndY=-5.25 EndZ=0
    g43: LineSegment StartX=1 StartY=-5.25 StartZ=0 EndX=1 EndY=-8.75 EndZ=0
    g44: LineSegment StartX=1 StartY=-8.75 StartZ=0 EndX=4.03109 EndY=-10.5 EndZ=0
    g45: LineSegment StartX=4.03109 StartY=-10.5 StartZ=0 EndX=7.06218 EndY=-8.75 EndZ=0
    g46: LineSegment StartX=7.06218 StartY=-8.75 StartZ=0 EndX=7.06218 EndY=-5.25 EndZ=0
    g47: LineSegment StartX=7.06218 StartY=-5.25 StartZ=0 EndX=4.03109 EndY=-3.5 EndZ=0
    g48: Circle [constr] CenterX=4.03109 CenterY=-7 CenterZ=0 NormalX=0 NormalY=0 NormalZ=1 AngleXU=0 Radius=3.5
  constraints (117):
    c: Coincident(g0,g1)
    c: Coincident(g1,g2)
    c: Coincident(g2,g3)
    c: Coincident(g3,g4)
    c: Coincident(g4,g5)
    c: Coincident(g5,g0)
    c: Equal(g0, g1-g5) x5
    c: PointOnObject(g0,g6)
    c: PointOnObject(g1,g6)
    c: PointOnObject(g2,g6)
    c: PointOnObject(g3,g6)
    c: PointOnObject(g4,g6)
    c: PointOnObject(g5,g6)
    c: Coincident(g6,g-1)
    c: Diameter(g6) = 7
    c: PointOnObject(g0,g-2)
    c: Coincident(g7,g8)
    c: Coincident(g8,g9)
    c: Coincident(g9,g10)
    c: Coincident(g10,g11)
    c: Coincident(g11,g12)
    c: Coincident(g12,g7)
    c: Equal(g7, g8-g12) x5
    c: PointOnObject(g7,g13)
    c: PointOnObject(g8,g13)
    c: PointOnObject(g9,g13)
    c: PointOnObject(g10,g13)
    c: PointOnObject(g11,g13)
    c: PointOnObject(g12,g13)
    c: PointOnObject(g13,g-1)
    c: Diameter(g13) = 7
    c: Distance(g6,g13) = 8
    c: Horizontal(g0,g10)
    c: Coincident(g14,g15)
    c: Coincident(g15,g16)
    c: Coincident(g16,g17)
    c: Coincident(g17,g18)
    c: Coincident(g18,g19)
    c: Coincident(g19,g14)
    c: Equal(g14, g15-g19) x5
    c: PointOnObject(g14,g20)
    c: PointOnObject(g15,g20)
    c: PointOnObject(g16,g20)
    c: PointOnObject(g17,g20)
    c: PointOnObject(g18,g20)
    c: PointOnObject(g19,g20)
    c: Diameter(g20) = 7
    c: DistanceY(g-1,g20) = 7
    c: Vertical(g18)
    c: Distance(g17,g-2) = 1
    c: Coincident(g21,g22)
    c: Coincident(g22,g23)
    c: Coincident(g23,g24)
    c: Coincident(g24,g25)
    c: Coincident(g25,g26)
    c: Coincident(g26,g21)
    c: Equal(g21, g22-g26) x5
    c: PointOnObject(g21,g27)
    c: PointOnObject(g22,g27)
    c: PointOnObject(g23,g27)
    c: PointOnObject(g24,g27)
    c: PointOnObject(g25,g27)
    c: PointOnObject(g26,g27)
    c: Diameter(g27) = 7
    c: DistanceY(g-1,g27) = 7
    c: DistanceX(g21,g-1) = 1
    c: Vertical(g21)
    c: Coincident(g28,g29)
    c: Coincident(g29,g30)
    c: Coincident(g30,g31)
    c: Coincident(g31,g32)
    c: Coincident(g32,g33)
    c: Coincident(g33,g28)
    c: Equal(g28, g29-g33) x5
    c: PointOnObject(g28,g34)
    c: PointOnObject(g29,g34)
    c: PointOnObject(g30,g34)
    c: PointOnObject(g31,g34)
    c: PointOnObject(g32,g34)
    c: PointOnObject(g33,g34)
    c: PointOnObject(g34,g-1)
    c: Diameter(g34) = 7
    c: Vertical(g31)
    c: DistanceX(g34,g-1) = 8
    c: Coincident(g35,g36)
    c: Coincident(g36,g37)
    c: Coincident(g37,g38)
    c: Coincident(g38,g39)
    c: Coincident(g39,g40)
    c: Coincident(g40,g35)
    c: Equal(g35, g36-g40) x5
    c: PointOnObject(g35,g41)
    c: PointOnObject(g36,g41)
    c: PointOnObject(g37,g41)
    c: PointOnObject(g38,g41)
    c: PointOnObject(g39,g41)
    c: PointOnObject(g40,g41)
    c: Coincident(g42,g43)
    c: Coincident(g43,g44)
    c: Coincident(g44,g45)
    c: Coincident(g45,g46)
    c: Coincident(g46,g47)
    c: Coincident(g47,g42)
    c: Equal(g42, g43-g47) x5
    c: PointOnObject(g42,g48)
    c: PointOnObject(g43,g48)
    c: PointOnObject(g44,g48)
    c: PointOnObject(g45,g48)
    c: PointOnObject(g46,g48)
    c: PointOnObject(g47,g48)
    c: Equal(g41,g48)
    c: Diameter(g41) = 7
    c: Vertical(g39)
    c: Vertical(g43)
    c: Distance(g-2,g39) = 1
    c: Symmetric(g38,g43,g-2)
    c: Distance(g41,g-1) = 7
FEATURE [Part::Extrusion] Extrude530  label="hex145"
  Base = -> Sketch538
  Dir = (0,-1,2e-16)
  DirMode = 2
  FaceMakerClass = Part::FaceMakerBullseye
  FaceMakerMode = 3
  LengthFwd = 10
  LengthRev = 0
  Placement = pos=(104,0,-28) rot=(0,0,1;0rad)
  Solid = true
  Symmetric = false
FEATURE [Sketcher::SketchObject] Sketch539
  ArcFitTolerance = 1e-06
  FullyConstrained = true
  MakeInternals = false
  Placement = pos=(0,0,0) rot=(1,0,0;1.5708rad)
  sketch-geometry (49):
    g0: LineSegment StartX=1e-16 StartY=3.5 StartZ=0 EndX=-3.03109 EndY=1.75 EndZ=0
    g1: LineSegment StartX=-3.03109 StartY=1.75 StartZ=0 EndX=-3.03109 EndY=-1.75 EndZ=0
    g2: LineSegment StartX=-3.03109 StartY=-1.75 StartZ=0 EndX=-1e-16 EndY=-3.5 EndZ=0
    g3: LineSegment StartX=-1e-16 StartY=-3.5 StartZ=0 EndX=3.03109 EndY=-1.75 EndZ=0
    g4: LineSegment StartX=3.03109 StartY=-1.75 StartZ=0 EndX=3.03109 EndY=1.75 EndZ=0
    g5: LineSegment StartX=3.03109 StartY=1.75 StartZ=0 EndX=1e-16 EndY=3.5 EndZ=0
    g6: Circle [constr] CenterX=0 CenterY=0 CenterZ=0 NormalX=0 NormalY=0 NormalZ=1 AngleXU=0 Radius=3.5
    g7: LineSegment StartX=4.96892 StartY=-1.75002 StartZ=0 EndX=8.00002 EndY=-3.5 EndZ=0
    g8: LineSegment StartX=8.00002 StartY=-3.5 StartZ=0 EndX=11.0311 EndY=-1.74998 EndZ=0
    g9: LineSegment StartX=11.0311 StartY=-1.74998 StartZ=0 EndX=11.0311 EndY=1.75002 EndZ=0
    g10: LineSegment StartX=11.0311 StartY=1.75002 StartZ=0 EndX=7.99998 EndY=3.5 EndZ=0
    g11: LineSegment StartX=7.99998 StartY=3.5 StartZ=0 EndX=4.9689 EndY=1.74998 EndZ=0
    g12: LineSegment StartX=4.9689 StartY=1.74998 StartZ=0 EndX=4.96892 EndY=-1.75002 EndZ=0
    g13: Circle [constr] CenterX=8 CenterY=0 CenterZ=0 NormalX=0 NormalY=0 NormalZ=1 AngleXU=0 Radius=3.5
    g14: LineSegment StartX=4.03109 StartY=3.5 StartZ=0 EndX=7.06218 EndY=5.25 EndZ=0
    g15: LineSegment StartX=7.06218 StartY=5.25 StartZ=0 EndX=7.06218 EndY=8.75 EndZ=0
    g16: LineSegment StartX=7.06218 StartY=8.75 StartZ=0 EndX=4.03109 EndY=10.5 EndZ=0
    g17: LineSegment StartX=4.03109 StartY=10.5 StartZ=0 EndX=1 EndY=8.75 EndZ=0
    g18: LineSegment StartX=1 StartY=8.75 StartZ=0 EndX=1 EndY=5.25 EndZ=0
    g19: LineSegment StartX=1 StartY=5.25 StartZ=0 EndX=4.03109 EndY=3.5 EndZ=0
    g20: Circle [constr] CenterX=4.03109 CenterY=7 CenterZ=0 NormalX=0 NormalY=0 NormalZ=1 AngleXU=0 Radius=3.5
    g21: LineSegment StartX=-1 StartY=5.25 StartZ=0 EndX=-1 EndY=8.75 EndZ=0
    g22: LineSegment StartX=-1 StartY=8.75 StartZ=0 EndX=-4.03109 EndY=10.5 EndZ=0
    g23: LineSegment StartX=-4.03109 StartY=10.5 StartZ=0 EndX=-7.06218 EndY=8.75 EndZ=0
    g24: LineSegment StartX=-7.06218 StartY=8.75 StartZ=0 EndX=-7.06218 EndY=5.25 EndZ=0
    g25: LineSegment StartX=-7.06218 StartY=5.25 StartZ=0 EndX=-4.03109 EndY=3.5 EndZ=0
    g26: LineSegment StartX=-4.03109 StartY=3.5 StartZ=0 EndX=-1 EndY=5.25 EndZ=0
    g27: Circle [constr] CenterX=-4.03109 CenterY=7 CenterZ=0 NormalX=0 NormalY=0 NormalZ=1 AngleXU=0 Radius=3.5
    g28: LineSegment StartX=-4.96891 StartY=-1.75 StartZ=0 EndX=-4.96891 EndY=1.75 EndZ=0
    g29: LineSegment StartX=-4.96891 StartY=1.75 StartZ=0 EndX=-8 EndY=3.5 EndZ=0
    g30: LineSegment StartX=-8 StartY=3.5 StartZ=0 EndX=-11.0311 EndY=1.75 EndZ=0
    g31: LineSegment StartX=-11.0311 StartY=1.75 StartZ=0 EndX=-11.0311 EndY=-1.75 EndZ=0
    g32: LineSegment StartX=-11.0311 StartY=-1.75 StartZ=0 EndX=-8 EndY=-3.5 EndZ=0
    g33: LineSegment StartX=-8 StartY=-3.5 StartZ=0 EndX=-4.96891 EndY=-1.75 EndZ=0
    g34: Circle [constr] CenterX=-8 CenterY=0 CenterZ=0 NormalX=0 NormalY=0 NormalZ=1 AngleXU=0 Radius=3.5
    g35: LineSegment StartX=-4.03109 StartY=-3.5 StartZ=0 EndX=-7.06218 EndY=-5.25 EndZ=0
    g36: LineSegment StartX=-7.06218 StartY=-5.25 StartZ=0 EndX=-7.06218 EndY=-8.75 EndZ=0
    g37: LineSegment StartX=-7.06218 StartY=-8.75 StartZ=0 EndX=-4.03109 EndY=-10.5 EndZ=0
    g38: LineSegment StartX=-4.03109 StartY=-10.5 StartZ=0 EndX=-1 EndY=-8.75 EndZ=0
    g39: LineSegment StartX=-1 StartY=-8.75 StartZ=0 EndX=-1 EndY=-5.25 EndZ=0
    g40: LineSegment StartX=-1 StartY=-5.25 StartZ=0 EndX=-4.03109 EndY=-3.5 EndZ=0
    g41: Circle [constr] CenterX=-4.03109 CenterY=-7 CenterZ=0 NormalX=0 NormalY=0 NormalZ=1 AngleXU=0 Radius=3.5
    g42: LineSegment StartX=4.03109 StartY=-3.5 StartZ=0 EndX=1 EndY=-5.25 EndZ=0
    g43: LineSegment StartX=1 StartY=-5.25 StartZ=0 EndX=1 EndY=-8.75 EndZ=0
    g44: LineSegment StartX=1 StartY=-8.75 StartZ=0 EndX=4.03109 EndY=-10.5 EndZ=0
    g45: LineSegment StartX=4.03109 StartY=-10.5 StartZ=0 EndX=7.06218 EndY=-8.75 EndZ=0
    g46: LineSegment StartX=7.06218 StartY=-8.75 StartZ=0 EndX=7.06218 EndY=-5.25 EndZ=0
    g47: LineSegment StartX=7.06218 StartY=-5.25 StartZ=0 EndX=4.03109 EndY=-3.5 EndZ=0
    g48: Circle [constr] CenterX=4.03109 CenterY=-7 CenterZ=0 NormalX=0 NormalY=0 NormalZ=1 AngleXU=0 Radius=3.5
  constraints (117):
    c: Coincident(g0,g1)
    c: Coincident(g1,g2)
    c: Coincident(g2,g3)
    c: Coincident(g3,g4)
    c: Coincident(g4,g5)
    c: Coincident(g5,g0)
    c: Equal(g0, g1-g5) x5
    c: PointOnObject(g0,g6)
    c: PointOnObject(g1,g6)
    c: PointOnObject(g2,g6)
    c: PointOnObject(g3,g6)
    c: PointOnObject(g4,g6)
    c: PointOnObject(g5,g6)
    c: Coincident(g6,g-1)
    c: Diameter(g6) = 7
    c: PointOnObject(g0,g-2)
    c: Coincident(g7,g8)
    c: Coincident(g8,g9)
    c: Coincident(g9,g10)
    c: Coincident(g10,g11)
    c: Coincident(g11,g12)
    c: Coincident(g12,g7)
    c: Equal(g7, g8-g12) x5
    c: PointOnObject(g7,g13)
    c: PointOnObject(g8,g13)
    c: PointOnObject(g9,g13)
    c: PointOnObject(g10,g13)
    c: PointOnObject(g11,g13)
    c: PointOnObject(g12,g13)
    c: PointOnObject(g13,g-1)
    c: Diameter(g13) = 7
    c: Distance(g6,g13) = 8
    c: Horizontal(g0,g10)
    c: Coincident(g14,g15)
    c: Coincident(g15,g16)
    c: Coincident(g16,g17)
    c: Coincident(g17,g18)
    c: Coincident(g18,g19)
    c: Coincident(g19,g14)
    c: Equal(g14, g15-g19) x5
    c: PointOnObject(g14,g20)
    c: PointOnObject(g15,g20)
    c: PointOnObject(g16,g20)
    c: PointOnObject(g17,g20)
    c: PointOnObject(g18,g20)
    c: PointOnObject(g19,g20)
    c: Diameter(g20) = 7
    c: DistanceY(g-1,g20) = 7
    c: Vertical(g18)
    c: Distance(g17,g-2) = 1
    c: Coincident(g21,g22)
    c: Coincident(g22,g23)
    c: Coincident(g23,g24)
    c: Coincident(g24,g25)
    c: Coincident(g25,g26)
    c: Coincident(g26,g21)
    c: Equal(g21, g22-g26) x5
    c: PointOnObject(g21,g27)
    c: PointOnObject(g22,g27)
    c: PointOnObject(g23,g27)
    c: PointOnObject(g24,g27)
    c: PointOnObject(g25,g27)
    c: PointOnObject(g26,g27)
    c: Diameter(g27) = 7
    c: DistanceY(g-1,g27) = 7
    c: DistanceX(g21,g-1) = 1
    c: Vertical(g21)
    c: Coincident(g28,g29)
    c: Coincident(g29,g30)
    c: Coincident(g30,g31)
    c: Coincident(g31,g32)
    c: Coincident(g32,g33)
    c: Coincident(g33,g28)
    c: Equal(g28, g29-g33) x5
    c: PointOnObject(g28,g34)
    c: PointOnObject(g29,g34)
    c: PointOnObject(g30,g34)
    c: PointOnObject(g31,g34)
    c: PointOnObject(g32,g34)
    c: PointOnObject(g33,g34)
    c: PointOnObject(g34,g-1)
    c: Diameter(g34) = 7
    c: Vertical(g31)
    c: DistanceX(g34,g-1) = 8
    c: Coincident(g35,g36)
    c: Coincident(g36,g37)
    c: Coincident(g37,g38)
    c: Coincident(g38,g39)
    c: Coincident(g39,g40)
    c: Coincident(g40,g35)
    c: Equal(g35, g36-g40) x5
    c: PointOnObject(g35,g41)
    c: PointOnObject(g36,g41)
    c: PointOnObject(g37,g41)
    c: PointOnObject(g38,g41)
    c: PointOnObject(g39,g41)
    c: PointOnObject(g40,g41)
    c: Coincident(g42,g43)
    c: Coincident(g43,g44)
    c: Coincident(g44,g45)
    c: Coincident(g45,g46)
    c: Coincident(g46,g47)
    c: Coincident(g47,g42)
    c: Equal(g42, g43-g47) x5
    c: PointOnObject(g42,g48)
    c: PointOnObject(g43,g48)
    c: PointOnObject(g44,g48)
    c: PointOnObject(g45,g48)
    c: PointOnObject(g46,g48)
    c: PointOnObject(g47,g48)
    c: Equal(g41,g48)
    c: Diameter(g41) = 7
    c: Vertical(g39)
    c: Vertical(g43)
    c: Distance(g-2,g39) = 1
    c: Symmetric(g38,g43,g-2)
    c: Distance(g41,g-1) = 7
FEATURE [Part::Extrusion] Extrude531  label="hex146"
  Base = -> Sketch539
  Dir = (0,-1,2e-16)
  DirMode = 2
  FaceMakerClass = Part::FaceMakerBullseye
  FaceMakerMode = 3
  LengthFwd = 10
  LengthRev = 0
  Placement = pos=(-96,0,-14) rot=(0,0,1;0rad)
  Solid = true
  Symmetric = false
FEATURE [Sketcher::SketchObject] Sketch540
  ArcFitTolerance = 1e-06
  FullyConstrained = true
  MakeInternals = false
  Placement = pos=(0,0,0) rot=(1,0,0;1.5708rad)
  sketch-geometry (49):
    g0: LineSegment StartX=1e-16 StartY=3.5 StartZ=0 EndX=-3.03109 EndY=1.75 EndZ=0
    g1: LineSegment StartX=-3.03109 StartY=1.75 StartZ=0 EndX=-3.03109 EndY=-1.75 EndZ=0
    g2: LineSegment StartX=-3.03109 StartY=-1.75 StartZ=0 EndX=-1e-16 EndY=-3.5 EndZ=0
    g3: LineSegment StartX=-1e-16 StartY=-3.5 StartZ=0 EndX=3.03109 EndY=-1.75 EndZ=0
    g4: LineSegment StartX=3.03109 StartY=-1.75 StartZ=0 EndX=3.03109 EndY=1.75 EndZ=0
    g5: LineSegment StartX=3.03109 StartY=1.75 StartZ=0 EndX=1e-16 EndY=3.5 EndZ=0
    g6: Circle [constr] CenterX=0 CenterY=0 CenterZ=0 NormalX=0 NormalY=0 NormalZ=1 AngleXU=0 Radius=3.5
    g7: LineSegment StartX=4.96892 StartY=-1.75002 StartZ=0 EndX=8.00002 EndY=-3.5 EndZ=0
    g8: LineSegment StartX=8.00002 StartY=-3.5 StartZ=0 EndX=11.0311 EndY=-1.74998 EndZ=0
    g9: LineSegment StartX=11.0311 StartY=-1.74998 StartZ=0 EndX=11.0311 EndY=1.75002 EndZ=0
    g10: LineSegment StartX=11.0311 StartY=1.75002 StartZ=0 EndX=7.99998 EndY=3.5 EndZ=0
    g11: LineSegment StartX=7.99998 StartY=3.5 StartZ=0 EndX=4.9689 EndY=1.74998 EndZ=0
    g12: LineSegment StartX=4.9689 StartY=1.74998 StartZ=0 EndX=4.96892 EndY=-1.75002 EndZ=0
    g13: Circle [constr] CenterX=8 CenterY=0 CenterZ=0 NormalX=0 NormalY=0 NormalZ=1 AngleXU=0 Radius=3.5
    g14: LineSegment StartX=4.03109 StartY=3.5 StartZ=0 EndX=7.06218 EndY=5.25 EndZ=0
    g15: LineSegment StartX=7.06218 StartY=5.25 StartZ=0 EndX=7.06218 EndY=8.75 EndZ=0
    g16: LineSegment StartX=7.06218 StartY=8.75 StartZ=0 EndX=4.03109 EndY=10.5 EndZ=0
    g17: LineSegment StartX=4.03109 StartY=10.5 StartZ=0 EndX=1 EndY=8.75 EndZ=0
    g18: LineSegment StartX=1 StartY=8.75 StartZ=0 EndX=1 EndY=5.25 EndZ=0
    g19: LineSegment StartX=1 StartY=5.25 StartZ=0 EndX=4.03109 EndY=3.5 EndZ=0
    g20: Circle [constr] CenterX=4.03109 CenterY=7 CenterZ=0 NormalX=0 NormalY=0 NormalZ=1 AngleXU=0 Radius=3.5
    g21: LineSegment StartX=-1 StartY=5.25 StartZ=0 EndX=-1 EndY=8.75 EndZ=0
    g22: LineSegment StartX=-1 StartY=8.75 StartZ=0 EndX=-4.03109 EndY=10.5 EndZ=0
    g23: LineSegment StartX=-4.03109 StartY=10.5 StartZ=0 EndX=-7.06218 EndY=8.75 EndZ=0
    g24: LineSegment StartX=-7.06218 StartY=8.75 StartZ=0 EndX=-7.06218 EndY=5.25 EndZ=0
    g25: LineSegment StartX=-7.06218 StartY=5.25 StartZ=0 EndX=-4.03109 EndY=3.5 EndZ=0
    g26: LineSegment StartX=-4.03109 StartY=3.5 StartZ=0 EndX=-1 EndY=5.25 EndZ=0
    g27: Circle [constr] CenterX=-4.03109 CenterY=7 CenterZ=0 NormalX=0 NormalY=0 NormalZ=1 AngleXU=0 Radius=3.5
    g28: LineSegment StartX=-4.96891 StartY=-1.75 StartZ=0 EndX=-4.96891 EndY=1.75 EndZ=0
    g29: LineSegment StartX=-4.96891 StartY=1.75 StartZ=0 EndX=-8 EndY=3.5 EndZ=0
    g30: LineSegment StartX=-8 StartY=3.5 StartZ=0 EndX=-11.0311 EndY=1.75 EndZ=0
    g31: LineSegment StartX=-11.0311 StartY=1.75 StartZ=0 EndX=-11.0311 EndY=-1.75 EndZ=0
    g32: LineSegment StartX=-11.0311 StartY=-1.75 StartZ=0 EndX=-8 EndY=-3.5 EndZ=0
    g33: LineSegment StartX=-8 StartY=-3.5 StartZ=0 EndX=-4.96891 EndY=-1.75 EndZ=0
    g34: Circle [constr] CenterX=-8 CenterY=0 CenterZ=0 NormalX=0 NormalY=0 NormalZ=1 AngleXU=0 Radius=3.5
    g35: LineSegment StartX=-4.03109 StartY=-3.5 StartZ=0 EndX=-7.06218 EndY=-5.25 EndZ=0
    g36: LineSegment StartX=-7.06218 StartY=-5.25 StartZ=0 EndX=-7.06218 EndY=-8.75 EndZ=0
    g37: LineSegment StartX=-7.06218 StartY=-8.75 StartZ=0 EndX=-4.03109 EndY=-10.5 EndZ=0
    g38: LineSegment StartX=-4.03109 StartY=-10.5 StartZ=0 EndX=-1 EndY=-8.75 EndZ=0
    g39: LineSegment StartX=-1 StartY=-8.75 StartZ=0 EndX=-1 EndY=-5.25 EndZ=0
    g40: LineSegment StartX=-1 StartY=-5.25 StartZ=0 EndX=-4.03109 EndY=-3.5 EndZ=0
    g41: Circle [constr] CenterX=-4.03109 CenterY=-7 CenterZ=0 NormalX=0 NormalY=0 NormalZ=1 AngleXU=0 Radius=3.5
    g42: LineSegment StartX=4.03109 StartY=-3.5 StartZ=0 EndX=1 EndY=-5.25 EndZ=0
    g43: LineSegment StartX=1 StartY=-5.25 StartZ=0 EndX=1 EndY=-8.75 EndZ=0
    g44: LineSegment StartX=1 StartY=-8.75 StartZ=0 EndX=4.03109 EndY=-10.5 EndZ=0
    g45: LineSegment StartX=4.03109 StartY=-10.5 StartZ=0 EndX=7.06218 EndY=-8.75 EndZ=0
    g46: LineSegment StartX=7.06218 StartY=-8.75 StartZ=0 EndX=7.06218 EndY=-5.25 EndZ=0
    g47: LineSegment StartX=7.06218 StartY=-5.25 StartZ=0 EndX=4.03109 EndY=-3.5 EndZ=0
    g48: Circle [constr] CenterX=4.03109 CenterY=-7 CenterZ=0 NormalX=0 NormalY=0 NormalZ=1 AngleXU=0 Radius=3.5
  constraints (117):
    c: Coincident(g0,g1)
    c: Coincident(g1,g2)
    c: Coincident(g2,g3)
    c: Coincident(g3,g4)
    c: Coincident(g4,g5)
    c: Coincident(g5,g0)
    c: Equal(g0, g1-g5) x5
    c: PointOnObject(g0,g6)
    c: PointOnObject(g1,g6)
    c: PointOnObject(g2,g6)
    c: PointOnObject(g3,g6)
    c: PointOnObject(g4,g6)
    c: PointOnObject(g5,g6)
    c: Coincident(g6,g-1)
    c: Diameter(g6) = 7
    c: PointOnObject(g0,g-2)
    c: Coincident(g7,g8)
    c: Coincident(g8,g9)
    c: Coincident(g9,g10)
    c: Coincident(g10,g11)
    c: Coincident(g11,g12)
    c: Coincident(g12,g7)
    c: Equal(g7, g8-g12) x5
    c: PointOnObject(g7,g13)
    c: PointOnObject(g8,g13)
    c: PointOnObject(g9,g13)
    c: PointOnObject(g10,g13)
    c: PointOnObject(g11,g13)
    c: PointOnObject(g12,g13)
    c: PointOnObject(g13,g-1)
    c: Diameter(g13) = 7
    c: Distance(g6,g13) = 8
    c: Horizontal(g0,g10)
    c: Coincident(g14,g15)
    c: Coincident(g15,g16)
    c: Coincident(g16,g17)
    c: Coincident(g17,g18)
    c: Coincident(g18,g19)
    c: Coincident(g19,g14)
    c: Equal(g14, g15-g19) x5
    c: PointOnObject(g14,g20)
    c: PointOnObject(g15,g20)
    c: PointOnObject(g16,g20)
    c: PointOnObject(g17,g20)
    c: PointOnObject(g18,g20)
    c: PointOnObject(g19,g20)
    c: Diameter(g20) = 7
    c: DistanceY(g-1,g20) = 7
    c: Vertical(g18)
    c: Distance(g17,g-2) = 1
    c: Coincident(g21,g22)
    c: Coincident(g22,g23)
    c: Coincident(g23,g24)
    c: Coincident(g24,g25)
    c: Coincident(g25,g26)
    c: Coincident(g26,g21)
    c: Equal(g21, g22-g26) x5
    c: PointOnObject(g21,g27)
    c: PointOnObject(g22,g27)
    c: PointOnObject(g23,g27)
    c: PointOnObject(g24,g27)
    c: PointOnObject(g25,g27)
    c: PointOnObject(g26,g27)
    c: Diameter(g27) = 7
    c: DistanceY(g-1,g27) = 7
    c: DistanceX(g21,g-1) = 1
    c: Vertical(g21)
    c: Coincident(g28,g29)
    c: Coincident(g29,g30)
    c: Coincident(g30,g31)
    c: Coincident(g31,g32)
    c: Coincident(g32,g33)
    c: Coincident(g33,g28)
    c: Equal(g28, g29-g33) x5
    c: PointOnObject(g28,g34)
    c: PointOnObject(g29,g34)
    c: PointOnObject(g30,g34)
    c: PointOnObject(g31,g34)
    c: PointOnObject(g32,g34)
    c: PointOnObject(g33,g34)
    c: PointOnObject(g34,g-1)
    c: Diameter(g34) = 7
    c: Vertical(g31)
    c: DistanceX(g34,g-1) = 8
    c: Coincident(g35,g36)
    c: Coincident(g36,g37)
    c: Coincident(g37,g38)
    c: Coincident(g38,g39)
    c: Coincident(g39,g40)
    c: Coincident(g40,g35)
    c: Equal(g35, g36-g40) x5
    c: PointOnObject(g35,g41)
    c: PointOnObject(g36,g41)
    c: PointOnObject(g37,g41)
    c: PointOnObject(g38,g41)
    c: PointOnObject(g39,g41)
    c: PointOnObject(g40,g41)
    c: Coincident(g42,g43)
    c: Coincident(g43,g44)
    c: Coincident(g44,g45)
    c: Coincident(g45,g46)
    c: Coincident(g46,g47)
    c: Coincident(g47,g42)
    c: Equal(g42, g43-g47) x5
    c: PointOnObject(g42,g48)
    c: PointOnObject(g43,g48)
    c: PointOnObject(g44,g48)
    c: PointOnObject(g45,g48)
    c: PointOnObject(g46,g48)
    c: PointOnObject(g47,g48)
    c: Equal(g41,g48)
    c: Diameter(g41) = 7
    c: Vertical(g39)
    c: Vertical(g43)
    c: Distance(g-2,g39) = 1
    c: Symmetric(g38,g43,g-2)
    c: Distance(g41,g-1) = 7
FEATURE [Part::Extrusion] Extrude532  label="hex147"
  Base = -> Sketch540
  Dir = (0,-1,2e-16)
  DirMode = 2
  FaceMakerClass = Part::FaceMakerBullseye
  FaceMakerMode = 3
  LengthFwd = 10
  LengthRev = 0
  Placement = pos=(-68,0,-35) rot=(0,0,1;0rad)
  Solid = true
  Symmetric = false
FEATURE [Sketcher::SketchObject] Sketch541
  ArcFitTolerance = 1e-06
  FullyConstrained = true
  MakeInternals = false
  Placement = pos=(0,0,0) rot=(1,0,0;1.5708rad)
  sketch-geometry (49):
    g0: LineSegment StartX=1e-16 StartY=3.5 StartZ=0 EndX=-3.03109 EndY=1.75 EndZ=0
    g1: LineSegment StartX=-3.03109 StartY=1.75 StartZ=0 EndX=-3.03109 EndY=-1.75 EndZ=0
    g2: LineSegment StartX=-3.03109 StartY=-1.75 StartZ=0 EndX=-1e-16 EndY=-3.5 EndZ=0
    g3: LineSegment StartX=-1e-16 StartY=-3.5 StartZ=0 EndX=3.03109 EndY=-1.75 EndZ=0
    g4: LineSegment StartX=3.03109 StartY=-1.75 StartZ=0 EndX=3.03109 EndY=1.75 EndZ=0
    g5: LineSegment StartX=3.03109 StartY=1.75 StartZ=0 EndX=1e-16 EndY=3.5 EndZ=0
    g6: Circle [constr] CenterX=0 CenterY=0 CenterZ=0 NormalX=0 NormalY=0 NormalZ=1 AngleXU=0 Radius=3.5
    g7: LineSegment StartX=4.96892 StartY=-1.75002 StartZ=0 EndX=8.00002 EndY=-3.5 EndZ=0
    g8: LineSegment StartX=8.00002 StartY=-3.5 StartZ=0 EndX=11.0311 EndY=-1.74998 EndZ=0
    g9: LineSegment StartX=11.0311 StartY=-1.74998 StartZ=0 EndX=11.0311 EndY=1.75002 EndZ=0
    g10: LineSegment StartX=11.0311 StartY=1.75002 StartZ=0 EndX=7.99998 EndY=3.5 EndZ=0
    g11: LineSegment StartX=7.99998 StartY=3.5 StartZ=0 EndX=4.9689 EndY=1.74998 EndZ=0
    g12: LineSegment StartX=4.9689 StartY=1.74998 StartZ=0 EndX=4.96892 EndY=-1.75002 EndZ=0
    g13: Circle [constr] CenterX=8 CenterY=0 CenterZ=0 NormalX=0 NormalY=0 NormalZ=1 AngleXU=0 Radius=3.5
    g14: LineSegment StartX=4.03109 StartY=3.5 StartZ=0 EndX=7.06218 EndY=5.25 EndZ=0
    g15: LineSegment StartX=7.06218 StartY=5.25 StartZ=0 EndX=7.06218 EndY=8.75 EndZ=0
    g16: LineSegment StartX=7.06218 StartY=8.75 StartZ=0 EndX=4.03109 EndY=10.5 EndZ=0
    g17: LineSegment StartX=4.03109 StartY=10.5 StartZ=0 EndX=1 EndY=8.75 EndZ=0
    g18: LineSegment StartX=1 StartY=8.75 StartZ=0 EndX=1 EndY=5.25 EndZ=0
    g19: LineSegment StartX=1 StartY=5.25 StartZ=0 EndX=4.03109 EndY=3.5 EndZ=0
    g20: Circle [constr] CenterX=4.03109 CenterY=7 CenterZ=0 NormalX=0 NormalY=0 NormalZ=1 AngleXU=0 Radius=3.5
    g21: LineSegment StartX=-1 StartY=5.25 StartZ=0 EndX=-1 EndY=8.75 EndZ=0
    g22: LineSegment StartX=-1 StartY=8.75 StartZ=0 EndX=-4.03109 EndY=10.5 EndZ=0
    g23: LineSegment StartX=-4.03109 StartY=10.5 StartZ=0 EndX=-7.06218 EndY=8.75 EndZ=0
    g24: LineSegment StartX=-7.06218 StartY=8.75 StartZ=0 EndX=-7.06218 EndY=5.25 EndZ=0
    g25: LineSegment StartX=-7.06218 StartY=5.25 StartZ=0 EndX=-4.03109 EndY=3.5 EndZ=0
    g26: LineSegment StartX=-4.03109 StartY=3.5 StartZ=0 EndX=-1 EndY=5.25 EndZ=0
    g27: Circle [constr] CenterX=-4.03109 CenterY=7 CenterZ=0 NormalX=0 NormalY=0 NormalZ=1 AngleXU=0 Radius=3.5
    g28: LineSegment StartX=-4.96891 StartY=-1.75 StartZ=0 EndX=-4.96891 EndY=1.75 EndZ=0
    g29: LineSegment StartX=-4.96891 StartY=1.75 StartZ=0 EndX=-8 EndY=3.5 EndZ=0
    g30: LineSegment StartX=-8 StartY=3.5 StartZ=0 EndX=-11.0311 EndY=1.75 EndZ=0
    g31: LineSegment StartX=-11.0311 StartY=1.75 StartZ=0 EndX=-11.0311 EndY=-1.75 EndZ=0
    g32: LineSegment StartX=-11.0311 StartY=-1.75 StartZ=0 EndX=-8 EndY=-3.5 EndZ=0
    g33: LineSegment StartX=-8 StartY=-3.5 StartZ=0 EndX=-4.96891 EndY=-1.75 EndZ=0
    g34: Circle [constr] CenterX=-8 CenterY=0 CenterZ=0 NormalX=0 NormalY=0 NormalZ=1 AngleXU=0 Radius=3.5
    g35: LineSegment StartX=-4.03109 StartY=-3.5 StartZ=0 EndX=-7.06218 EndY=-5.25 EndZ=0
    g36: LineSegment StartX=-7.06218 StartY=-5.25 StartZ=0 EndX=-7.06218 EndY=-8.75 EndZ=0
    g37: LineSegment StartX=-7.06218 StartY=-8.75 StartZ=0 EndX=-4.03109 EndY=-10.5 EndZ=0
    g38: LineSegment StartX=-4.03109 StartY=-10.5 StartZ=0 EndX=-1 EndY=-8.75 EndZ=0
    g39: LineSegment StartX=-1 StartY=-8.75 StartZ=0 EndX=-1 EndY=-5.25 EndZ=0
    g40: LineSegment StartX=-1 StartY=-5.25 StartZ=0 EndX=-4.03109 EndY=-3.5 EndZ=0
    g41: Circle [constr] CenterX=-4.03109 CenterY=-7 CenterZ=0 NormalX=0 NormalY=0 NormalZ=1 AngleXU=0 Radius=3.5
    g42: LineSegment StartX=4.03109 StartY=-3.5 StartZ=0 EndX=1 EndY=-5.25 EndZ=0
    g43: LineSegment StartX=1 StartY=-5.25 StartZ=0 EndX=1 EndY=-8.75 EndZ=0
    g44: LineSegment StartX=1 StartY=-8.75 StartZ=0 EndX=4.03109 EndY=-10.5 EndZ=0
    g45: LineSegment StartX=4.03109 StartY=-10.5 StartZ=0 EndX=7.06218 EndY=-8.75 EndZ=0
    g46: LineSegment StartX=7.06218 StartY=-8.75 StartZ=0 EndX=7.06218 EndY=-5.25 EndZ=0
    g47: LineSegment StartX=7.06218 StartY=-5.25 StartZ=0 EndX=4.03109 EndY=-3.5 EndZ=0
    g48: Circle [constr] CenterX=4.03109 CenterY=-7 CenterZ=0 NormalX=0 NormalY=0 NormalZ=1 AngleXU=0 Radius=3.5
  constraints (117):
    c: Coincident(g0,g1)
    c: Coincident(g1,g2)
    c: Coincident(g2,g3)
    c: Coincident(g3,g4)
    c: Coincident(g4,g5)
    c: Coincident(g5,g0)
    c: Equal(g0, g1-g5) x5
    c: PointOnObject(g0,g6)
    c: PointOnObject(g1,g6)
    c: PointOnObject(g2,g6)
    c: PointOnObject(g3,g6)
    c: PointOnObject(g4,g6)
    c: PointOnObject(g5,g6)
    c: Coincident(g6,g-1)
    c: Diameter(g6) = 7
    c: PointOnObject(g0,g-2)
    c: Coincident(g7,g8)
    c: Coincident(g8,g9)
    c: Coincident(g9,g10)
    c: Coincident(g10,g11)
    c: Coincident(g11,g12)
    c: Coincident(g12,g7)
    c: Equal(g7, g8-g12) x5
    c: PointOnObject(g7,g13)
    c: PointOnObject(g8,g13)
    c: PointOnObject(g9,g13)
    c: PointOnObject(g10,g13)
    c: PointOnObject(g11,g13)
    c: PointOnObject(g12,g13)
    c: PointOnObject(g13,g-1)
    c: Diameter(g13) = 7
    c: Distance(g6,g13) = 8
    c: Horizontal(g0,g10)
    c: Coincident(g14,g15)
    c: Coincident(g15,g16)
    c: Coincident(g16,g17)
    c: Coincident(g17,g18)
    c: Coincident(g18,g19)
    c: Coincident(g19,g14)
    c: Equal(g14, g15-g19) x5
    c: PointOnObject(g14,g20)
    c: PointOnObject(g15,g20)
    c: PointOnObject(g16,g20)
    c: PointOnObject(g17,g20)
    c: PointOnObject(g18,g20)
    c: PointOnObject(g19,g20)
    c: Diameter(g20) = 7
    c: DistanceY(g-1,g20) = 7
    c: Vertical(g18)
    c: Distance(g17,g-2) = 1
    c: Coincident(g21,g22)
    c: Coincident(g22,g23)
    c: Coincident(g23,g24)
    c: Coincident(g24,g25)
    c: Coincident(g25,g26)
    c: Coincident(g26,g21)
    c: Equal(g21, g22-g26) x5
    c: PointOnObject(g21,g27)
    c: PointOnObject(g22,g27)
    c: PointOnObject(g23,g27)
    c: PointOnObject(g24,g27)
    c: PointOnObject(g25,g27)
    c: PointOnObject(g26,g27)
    c: Diameter(g27) = 7
    c: DistanceY(g-1,g27) = 7
    c: DistanceX(g21,g-1) = 1
    c: Vertical(g21)
    c: Coincident(g28,g29)
    c: Coincident(g29,g30)
    c: Coincident(g30,g31)
    c: Coincident(g31,g32)
    c: Coincident(g32,g33)
    c: Coincident(g33,g28)
    c: Equal(g28, g29-g33) x5
    c: PointOnObject(g28,g34)
    c: PointOnObject(g29,g34)
    c: PointOnObject(g30,g34)
    c: PointOnObject(g31,g34)
    c: PointOnObject(g32,g34)
    c: PointOnObject(g33,g34)
    c: PointOnObject(g34,g-1)
    c: Diameter(g34) = 7
    c: Vertical(g31)
    c: DistanceX(g34,g-1) = 8
    c: Coincident(g35,g36)
    c: Coincident(g36,g37)
    c: Coincident(g37,g38)
    c: Coincident(g38,g39)
    c: Coincident(g39,g40)
    c: Coincident(g40,g35)
    c: Equal(g35, g36-g40) x5
    c: PointOnObject(g35,g41)
    c: PointOnObject(g36,g41)
    c: PointOnObject(g37,g41)
    c: PointOnObject(g38,g41)
    c: PointOnObject(g39,g41)
    c: PointOnObject(g40,g41)
    c: Coincident(g42,g43)
    c: Coincident(g43,g44)
    c: Coincident(g44,g45)
    c: Coincident(g45,g46)
    c: Coincident(g46,g47)
    c: Coincident(g47,g42)
    c: Equal(g42, g43-g47) x5
    c: PointOnObject(g42,g48)
    c: PointOnObject(g43,g48)
    c: PointOnObject(g44,g48)
    c: PointOnObject(g45,g48)
    c: PointOnObject(g46,g48)
    c: PointOnObject(g47,g48)
    c: Equal(g41,g48)
    c: Diameter(g41) = 7
    c: Vertical(g39)
    c: Vertical(g43)
    c: Distance(g-2,g39) = 1
    c: Symmetric(g38,g43,g-2)
    c: Distance(g41,g-1) = 7
FEATURE [Part::Extrusion] Extrude533  label="hex148"
  Base = -> Sketch541
  Dir = (0,-1,2e-16)
  DirMode = 2
  FaceMakerClass = Part::FaceMakerBullseye
  FaceMakerMode = 3
  LengthFwd = 10
  LengthRev = 0
  Placement = pos=(-84,0,-21) rot=(0,0,1;0rad)
  Solid = true
  Symmetric = false
FEATURE [Sketcher::SketchObject] Sketch542
  ArcFitTolerance = 1e-06
  FullyConstrained = true
  MakeInternals = false
  Placement = pos=(0,0,0) rot=(1,0,0;1.5708rad)
  sketch-geometry (49):
    g0: LineSegment StartX=1e-16 StartY=3.5 StartZ=0 EndX=-3.03109 EndY=1.75 EndZ=0
    g1: LineSegment StartX=-3.03109 StartY=1.75 StartZ=0 EndX=-3.03109 EndY=-1.75 EndZ=0
    g2: LineSegment StartX=-3.03109 StartY=-1.75 StartZ=0 EndX=-1e-16 EndY=-3.5 EndZ=0
    g3: LineSegment StartX=-1e-16 StartY=-3.5 StartZ=0 EndX=3.03109 EndY=-1.75 EndZ=0
    g4: LineSegment StartX=3.03109 StartY=-1.75 StartZ=0 EndX=3.03109 EndY=1.75 EndZ=0
    g5: LineSegment StartX=3.03109 StartY=1.75 StartZ=0 EndX=1e-16 EndY=3.5 EndZ=0
    g6: Circle [constr] CenterX=0 CenterY=0 CenterZ=0 NormalX=0 NormalY=0 NormalZ=1 AngleXU=0 Radius=3.5
    g7: LineSegment StartX=4.96892 StartY=-1.75002 StartZ=0 EndX=8.00002 EndY=-3.5 EndZ=0
    g8: LineSegment StartX=8.00002 StartY=-3.5 StartZ=0 EndX=11.0311 EndY=-1.74998 EndZ=0
    g9: LineSegment StartX=11.0311 StartY=-1.74998 StartZ=0 EndX=11.0311 EndY=1.75002 EndZ=0
    g10: LineSegment StartX=11.0311 StartY=1.75002 StartZ=0 EndX=7.99998 EndY=3.5 EndZ=0
    g11: LineSegment StartX=7.99998 StartY=3.5 StartZ=0 EndX=4.9689 EndY=1.74998 EndZ=0
    g12: LineSegment StartX=4.9689 StartY=1.74998 StartZ=0 EndX=4.96892 EndY=-1.75002 EndZ=0
    g13: Circle [constr] CenterX=8 CenterY=0 CenterZ=0 NormalX=0 NormalY=0 NormalZ=1 AngleXU=0 Radius=3.5
    g14: LineSegment StartX=4.03109 StartY=3.5 StartZ=0 EndX=7.06218 EndY=5.25 EndZ=0
    g15: LineSegment StartX=7.06218 StartY=5.25 StartZ=0 EndX=7.06218 EndY=8.75 EndZ=0
    g16: LineSegment StartX=7.06218 StartY=8.75 StartZ=0 EndX=4.03109 EndY=10.5 EndZ=0
    g17: LineSegment StartX=4.03109 StartY=10.5 StartZ=0 EndX=1 EndY=8.75 EndZ=0
    g18: LineSegment StartX=1 StartY=8.75 StartZ=0 EndX=1 EndY=5.25 EndZ=0
    g19: LineSegment StartX=1 StartY=5.25 StartZ=0 EndX=4.03109 EndY=3.5 EndZ=0
    g20: Circle [constr] CenterX=4.03109 CenterY=7 CenterZ=0 NormalX=0 NormalY=0 NormalZ=1 AngleXU=0 Radius=3.5
    g21: LineSegment StartX=-1 StartY=5.25 StartZ=0 EndX=-1 EndY=8.75 EndZ=0
    g22: LineSegment StartX=-1 StartY=8.75 StartZ=0 EndX=-4.03109 EndY=10.5 EndZ=0
    g23: LineSegment StartX=-4.03109 StartY=10.5 StartZ=0 EndX=-7.06218 EndY=8.75 EndZ=0
    g24: LineSegment StartX=-7.06218 StartY=8.75 StartZ=0 EndX=-7.06218 EndY=5.25 EndZ=0
    g25: LineSegment StartX=-7.06218 StartY=5.25 StartZ=0 EndX=-4.03109 EndY=3.5 EndZ=0
    g26: LineSegment StartX=-4.03109 StartY=3.5 StartZ=0 EndX=-1 EndY=5.25 EndZ=0
    g27: Circle [constr] CenterX=-4.03109 CenterY=7 CenterZ=0 NormalX=0 NormalY=0 NormalZ=1 AngleXU=0 Radius=3.5
    g28: LineSegment StartX=-4.96891 StartY=-1.75 StartZ=0 EndX=-4.96891 EndY=1.75 EndZ=0
    g29: LineSegment StartX=-4.96891 StartY=1.75 StartZ=0 EndX=-8 EndY=3.5 EndZ=0
    g30: LineSegment StartX=-8 StartY=3.5 StartZ=0 EndX=-11.0311 EndY=1.75 EndZ=0
    g31: LineSegment StartX=-11.0311 StartY=1.75 StartZ=0 EndX=-11.0311 EndY=-1.75 EndZ=0
    g32: LineSegment StartX=-11.0311 StartY=-1.75 StartZ=0 EndX=-8 EndY=-3.5 EndZ=0
    g33: LineSegment StartX=-8 StartY=-3.5 StartZ=0 EndX=-4.96891 EndY=-1.75 EndZ=0
    g34: Circle [constr] CenterX=-8 CenterY=0 CenterZ=0 NormalX=0 NormalY=0 NormalZ=1 AngleXU=0 Radius=3.5
    g35: LineSegment StartX=-4.03109 StartY=-3.5 StartZ=0 EndX=-7.06218 EndY=-5.25 EndZ=0
    g36: LineSegment StartX=-7.06218 StartY=-5.25 StartZ=0 EndX=-7.06218 EndY=-8.75 EndZ=0
    g37: LineSegment StartX=-7.06218 StartY=-8.75 StartZ=0 EndX=-4.03109 EndY=-10.5 EndZ=0
    g38: LineSegment StartX=-4.03109 StartY=-10.5 StartZ=0 EndX=-1 EndY=-8.75 EndZ=0
    g39: LineSegment StartX=-1 StartY=-8.75 StartZ=0 EndX=-1 EndY=-5.25 EndZ=0
    g40: LineSegment StartX=-1 StartY=-5.25 StartZ=0 EndX=-4.03109 EndY=-3.5 EndZ=0
    g41: Circle [constr] CenterX=-4.03109 CenterY=-7 CenterZ=0 NormalX=0 NormalY=0 NormalZ=1 AngleXU=0 Radius=3.5
    g42: LineSegment StartX=4.03109 StartY=-3.5 StartZ=0 EndX=1 EndY=-5.25 EndZ=0
    g43: LineSegment StartX=1 StartY=-5.25 StartZ=0 EndX=1 EndY=-8.75 EndZ=0
    g44: LineSegment StartX=1 StartY=-8.75 StartZ=0 EndX=4.03109 EndY=-10.5 EndZ=0
    g45: LineSegment StartX=4.03109 StartY=-10.5 StartZ=0 EndX=7.06218 EndY=-8.75 EndZ=0
    g46: LineSegment StartX=7.06218 StartY=-8.75 StartZ=0 EndX=7.06218 EndY=-5.25 EndZ=0
    g47: LineSegment StartX=7.06218 StartY=-5.25 StartZ=0 EndX=4.03109 EndY=-3.5 EndZ=0
    g48: Circle [constr] CenterX=4.03109 CenterY=-7 CenterZ=0 NormalX=0 NormalY=0 NormalZ=1 AngleXU=0 Radius=3.5
  constraints (117):
    c: Coincident(g0,g1)
    c: Coincident(g1,g2)
    c: Coincident(g2,g3)
    c: Coincident(g3,g4)
    c: Coincident(g4,g5)
    c: Coincident(g5,g0)
    c: Equal(g0, g1-g5) x5
    c: PointOnObject(g0,g6)
    c: PointOnObject(g1,g6)
    c: PointOnObject(g2,g6)
    c: PointOnObject(g3,g6)
    c: PointOnObject(g4,g6)
    c: PointOnObject(g5,g6)
    c: Coincident(g6,g-1)
    c: Diameter(g6) = 7
    c: PointOnObject(g0,g-2)
    c: Coincident(g7,g8)
    c: Coincident(g8,g9)
    c: Coincident(g9,g10)
    c: Coincident(g10,g11)
    c: Coincident(g11,g12)
    c: Coincident(g12,g7)
    c: Equal(g7, g8-g12) x5
    c: PointOnObject(g7,g13)
    c: PointOnObject(g8,g13)
    c: PointOnObject(g9,g13)
    c: PointOnObject(g10,g13)
    c: PointOnObject(g11,g13)
    c: PointOnObject(g12,g13)
    c: PointOnObject(g13,g-1)
    c: Diameter(g13) = 7
    c: Distance(g6,g13) = 8
    c: Horizontal(g0,g10)
    c: Coincident(g14,g15)
    c: Coincident(g15,g16)
    c: Coincident(g16,g17)
    c: Coincident(g17,g18)
    c: Coincident(g18,g19)
    c: Coincident(g19,g14)
    c: Equal(g14, g15-g19) x5
    c: PointOnObject(g14,g20)
    c: PointOnObject(g15,g20)
    c: PointOnObject(g16,g20)
    c: PointOnObject(g17,g20)
    c: PointOnObject(g18,g20)
    c: PointOnObject(g19,g20)
    c: Diameter(g20) = 7
    c: DistanceY(g-1,g20) = 7
    c: Vertical(g18)
    c: Distance(g17,g-2) = 1
    c: Coincident(g21,g22)
    c: Coincident(g22,g23)
    c: Coincident(g23,g24)
    c: Coincident(g24,g25)
    c: Coincident(g25,g26)
    c: Coincident(g26,g21)
    c: Equal(g21, g22-g26) x5
    c: PointOnObject(g21,g27)
    c: PointOnObject(g22,g27)
    c: PointOnObject(g23,g27)
    c: PointOnObject(g24,g27)
    c: PointOnObject(g25,g27)
    c: PointOnObject(g26,g27)
    c: Diameter(g27) = 7
    c: DistanceY(g-1,g27) = 7
    c: DistanceX(g21,g-1) = 1
    c: Vertical(g21)
    c: Coincident(g28,g29)
    c: Coincident(g29,g30)
    c: Coincident(g30,g31)
    c: Coincident(g31,g32)
    c: Coincident(g32,g33)
    c: Coincident(g33,g28)
    c: Equal(g28, g29-g33) x5
    c: PointOnObject(g28,g34)
    c: PointOnObject(g29,g34)
    c: PointOnObject(g30,g34)
    c: PointOnObject(g31,g34)
    c: PointOnObject(g32,g34)
    c: PointOnObject(g33,g34)
    c: PointOnObject(g34,g-1)
    c: Diameter(g34) = 7
    c: Vertical(g31)
    c: DistanceX(g34,g-1) = 8
    c: Coincident(g35,g36)
    c: Coincident(g36,g37)
    c: Coincident(g37,g38)
    c: Coincident(g38,g39)
    c: Coincident(g39,g40)
    c: Coincident(g40,g35)
    c: Equal(g35, g36-g40) x5
    c: PointOnObject(g35,g41)
    c: PointOnObject(g36,g41)
    c: PointOnObject(g37,g41)
    c: PointOnObject(g38,g41)
    c: PointOnObject(g39,g41)
    c: PointOnObject(g40,g41)
    c: Coincident(g42,g43)
    c: Coincident(g43,g44)
    c: Coincident(g44,g45)
    c: Coincident(g45,g46)
    c: Coincident(g46,g47)
    c: Coincident(g47,g42)
    c: Equal(g42, g43-g47) x5
    c: PointOnObject(g42,g48)
    c: PointOnObject(g43,g48)
    c: PointOnObject(g44,g48)
    c: PointOnObject(g45,g48)
    c: PointOnObject(g46,g48)
    c: PointOnObject(g47,g48)
    c: Equal(g41,g48)
    c: Diameter(g41) = 7
    c: Vertical(g39)
    c: Vertical(g43)
    c: Distance(g-2,g39) = 1
    c: Symmetric(g38,g43,g-2)
    c: Distance(g41,g-1) = 7
FEATURE [Part::Extrusion] Extrude534  label="hex149"
  Base = -> Sketch542
  Dir = (0,-1,2e-16)
  DirMode = 2
  FaceMakerClass = Part::FaceMakerBullseye
  FaceMakerMode = 3
  LengthFwd = 10
  LengthRev = 0
  Placement = pos=(-88,0,14) rot=(0,0,1;0rad)
  Solid = true
  Symmetric = false
FEATURE [Sketcher::SketchObject] Sketch543
  ArcFitTolerance = 1e-06
  FullyConstrained = true
  MakeInternals = false
  Placement = pos=(0,0,0) rot=(1,0,0;1.5708rad)
  sketch-geometry (49):
    g0: LineSegment StartX=1e-16 StartY=3.5 StartZ=0 EndX=-3.03109 EndY=1.75 EndZ=0
    g1: LineSegment StartX=-3.03109 StartY=1.75 StartZ=0 EndX=-3.03109 EndY=-1.75 EndZ=0
    g2: LineSegment StartX=-3.03109 StartY=-1.75 StartZ=0 EndX=-1e-16 EndY=-3.5 EndZ=0
    g3: LineSegment StartX=-1e-16 StartY=-3.5 StartZ=0 EndX=3.03109 EndY=-1.75 EndZ=0
    g4: LineSegment StartX=3.03109 StartY=-1.75 StartZ=0 EndX=3.03109 EndY=1.75 EndZ=0
    g5: LineSegment StartX=3.03109 StartY=1.75 StartZ=0 EndX=1e-16 EndY=3.5 EndZ=0
    g6: Circle [constr] CenterX=0 CenterY=0 CenterZ=0 NormalX=0 NormalY=0 NormalZ=1 AngleXU=0 Radius=3.5
    g7: LineSegment StartX=4.96892 StartY=-1.75002 StartZ=0 EndX=8.00002 EndY=-3.5 EndZ=0
    g8: LineSegment StartX=8.00002 StartY=-3.5 StartZ=0 EndX=11.0311 EndY=-1.74998 EndZ=0
    g9: LineSegment StartX=11.0311 StartY=-1.74998 StartZ=0 EndX=11.0311 EndY=1.75002 EndZ=0
    g10: LineSegment StartX=11.0311 StartY=1.75002 StartZ=0 EndX=7.99998 EndY=3.5 EndZ=0
    g11: LineSegment StartX=7.99998 StartY=3.5 StartZ=0 EndX=4.9689 EndY=1.74998 EndZ=0
    g12: LineSegment StartX=4.9689 StartY=1.74998 StartZ=0 EndX=4.96892 EndY=-1.75002 EndZ=0
    g13: Circle [constr] CenterX=8 CenterY=0 CenterZ=0 NormalX=0 NormalY=0 NormalZ=1 AngleXU=0 Radius=3.5
    g14: LineSegment StartX=4.03109 StartY=3.5 StartZ=0 EndX=7.06218 EndY=5.25 EndZ=0
    g15: LineSegment StartX=7.06218 StartY=5.25 StartZ=0 EndX=7.06218 EndY=8.75 EndZ=0
    g16: LineSegment StartX=7.06218 StartY=8.75 StartZ=0 EndX=4.03109 EndY=10.5 EndZ=0
    g17: LineSegment StartX=4.03109 StartY=10.5 StartZ=0 EndX=1 EndY=8.75 EndZ=0
    g18: LineSegment StartX=1 StartY=8.75 StartZ=0 EndX=1 EndY=5.25 EndZ=0
    g19: LineSegment StartX=1 StartY=5.25 StartZ=0 EndX=4.03109 EndY=3.5 EndZ=0
    g20: Circle [constr] CenterX=4.03109 CenterY=7 CenterZ=0 NormalX=0 NormalY=0 NormalZ=1 AngleXU=0 Radius=3.5
    g21: LineSegment StartX=-1 StartY=5.25 StartZ=0 EndX=-1 EndY=8.75 EndZ=0
    g22: LineSegment StartX=-1 StartY=8.75 StartZ=0 EndX=-4.03109 EndY=10.5 EndZ=0
    g23: LineSegment StartX=-4.03109 StartY=10.5 StartZ=0 EndX=-7.06218 EndY=8.75 EndZ=0
    g24: LineSegment StartX=-7.06218 StartY=8.75 StartZ=0 EndX=-7.06218 EndY=5.25 EndZ=0
    g25: LineSegment StartX=-7.06218 StartY=5.25 StartZ=0 EndX=-4.03109 EndY=3.5 EndZ=0
    g26: LineSegment StartX=-4.03109 StartY=3.5 StartZ=0 EndX=-1 EndY=5.25 EndZ=0
    g27: Circle [constr] CenterX=-4.03109 CenterY=7 CenterZ=0 NormalX=0 NormalY=0 NormalZ=1 AngleXU=0 Radius=3.5
    g28: LineSegment StartX=-4.96891 StartY=-1.75 StartZ=0 EndX=-4.96891 EndY=1.75 EndZ=0
    g29: LineSegment StartX=-4.96891 StartY=1.75 StartZ=0 EndX=-8 EndY=3.5 EndZ=0
    g30: LineSegment StartX=-8 StartY=3.5 StartZ=0 EndX=-11.0311 EndY=1.75 EndZ=0
    g31: LineSegment StartX=-11.0311 StartY=1.75 StartZ=0 EndX=-11.0311 EndY=-1.75 EndZ=0
    g32: LineSegment StartX=-11.0311 StartY=-1.75 StartZ=0 EndX=-8 EndY=-3.5 EndZ=0
    g33: LineSegment StartX=-8 StartY=-3.5 StartZ=0 EndX=-4.96891 EndY=-1.75 EndZ=0
    g34: Circle [constr] CenterX=-8 CenterY=0 CenterZ=0 NormalX=0 NormalY=0 NormalZ=1 AngleXU=0 Radius=3.5
    g35: LineSegment StartX=-4.03109 StartY=-3.5 StartZ=0 EndX=-7.06218 EndY=-5.25 EndZ=0
    g36: LineSegment StartX=-7.06218 StartY=-5.25 StartZ=0 EndX=-7.06218 EndY=-8.75 EndZ=0
    g37: LineSegment StartX=-7.06218 StartY=-8.75 StartZ=0 EndX=-4.03109 EndY=-10.5 EndZ=0
    g38: LineSegment StartX=-4.03109 StartY=-10.5 StartZ=0 EndX=-1 EndY=-8.75 EndZ=0
    g39: LineSegment StartX=-1 StartY=-8.75 StartZ=0 EndX=-1 EndY=-5.25 EndZ=0
    g40: LineSegment StartX=-1 StartY=-5.25 StartZ=0 EndX=-4.03109 EndY=-3.5 EndZ=0
    g41: Circle [constr] CenterX=-4.03109 CenterY=-7 CenterZ=0 NormalX=0 NormalY=0 NormalZ=1 AngleXU=0 Radius=3.5
    g42: LineSegment StartX=4.03109 StartY=-3.5 StartZ=0 EndX=1 EndY=-5.25 EndZ=0
    g43: LineSegment StartX=1 StartY=-5.25 StartZ=0 EndX=1 EndY=-8.75 EndZ=0
    g44: LineSegment StartX=1 StartY=-8.75 StartZ=0 EndX=4.03109 EndY=-10.5 EndZ=0
    g45: LineSegment StartX=4.03109 StartY=-10.5 StartZ=0 EndX=7.06218 EndY=-8.75 EndZ=0
    g46: LineSegment StartX=7.06218 StartY=-8.75 StartZ=0 EndX=7.06218 EndY=-5.25 EndZ=0
    g47: LineSegment StartX=7.06218 StartY=-5.25 StartZ=0 EndX=4.03109 EndY=-3.5 EndZ=0
    g48: Circle [constr] CenterX=4.03109 CenterY=-7 CenterZ=0 NormalX=0 NormalY=0 NormalZ=1 AngleXU=0 Radius=3.5
  constraints (117):
    c: Coincident(g0,g1)
    c: Coincident(g1,g2)
    c: Coincident(g2,g3)
    c: Coincident(g3,g4)
    c: Coincident(g4,g5)
    c: Coincident(g5,g0)
    c: Equal(g0, g1-g5) x5
    c: PointOnObject(g0,g6)
    c: PointOnObject(g1,g6)
    c: PointOnObject(g2,g6)
    c: PointOnObject(g3,g6)
    c: PointOnObject(g4,g6)
    c: PointOnObject(g5,g6)
    c: Coincident(g6,g-1)
    c: Diameter(g6) = 7
    c: PointOnObject(g0,g-2)
    c: Coincident(g7,g8)
    c: Coincident(g8,g9)
    c: Coincident(g9,g10)
    c: Coincident(g10,g11)
    c: Coincident(g11,g12)
    c: Coincident(g12,g7)
    c: Equal(g7, g8-g12) x5
    c: PointOnObject(g7,g13)
    c: PointOnObject(g8,g13)
    c: PointOnObject(g9,g13)
    c: PointOnObject(g10,g13)
    c: PointOnObject(g11,g13)
    c: PointOnObject(g12,g13)
    c: PointOnObject(g13,g-1)
    c: Diameter(g13) = 7
    c: Distance(g6,g13) = 8
    c: Horizontal(g0,g10)
    c: Coincident(g14,g15)
    c: Coincident(g15,g16)
    c: Coincident(g16,g17)
    c: Coincident(g17,g18)
    c: Coincident(g18,g19)
    c: Coincident(g19,g14)
    c: Equal(g14, g15-g19) x5
    c: PointOnObject(g14,g20)
    c: PointOnObject(g15,g20)
    c: PointOnObject(g16,g20)
    c: PointOnObject(g17,g20)
    c: PointOnObject(g18,g20)
    c: PointOnObject(g19,g20)
    c: Diameter(g20) = 7
    c: DistanceY(g-1,g20) = 7
    c: Vertical(g18)
    c: Distance(g17,g-2) = 1
    c: Coincident(g21,g22)
    c: Coincident(g22,g23)
    c: Coincident(g23,g24)
    c: Coincident(g24,g25)
    c: Coincident(g25,g26)
    c: Coincident(g26,g21)
    c: Equal(g21, g22-g26) x5
    c: PointOnObject(g21,g27)
    c: PointOnObject(g22,g27)
    c: PointOnObject(g23,g27)
    c: PointOnObject(g24,g27)
    c: PointOnObject(g25,g27)
    c: PointOnObject(g26,g27)
    c: Diameter(g27) = 7
    c: DistanceY(g-1,g27) = 7
    c: DistanceX(g21,g-1) = 1
    c: Vertical(g21)
    c: Coincident(g28,g29)
    c: Coincident(g29,g30)
    c: Coincident(g30,g31)
    c: Coincident(g31,g32)
    c: Coincident(g32,g33)
    c: Coincident(g33,g28)
    c: Equal(g28, g29-g33) x5
    c: PointOnObject(g28,g34)
    c: PointOnObject(g29,g34)
    c: PointOnObject(g30,g34)
    c: PointOnObject(g31,g34)
    c: PointOnObject(g32,g34)
    c: PointOnObject(g33,g34)
    c: PointOnObject(g34,g-1)
    c: Diameter(g34) = 7
    c: Vertical(g31)
    c: DistanceX(g34,g-1) = 8
    c: Coincident(g35,g36)
    c: Coincident(g36,g37)
    c: Coincident(g37,g38)
    c: Coincident(g38,g39)
    c: Coincident(g39,g40)
    c: Coincident(g40,g35)
    c: Equal(g35, g36-g40) x5
    c: PointOnObject(g35,g41)
    c: PointOnObject(g36,g41)
    c: PointOnObject(g37,g41)
    c: PointOnObject(g38,g41)
    c: PointOnObject(g39,g41)
    c: PointOnObject(g40,g41)
    c: Coincident(g42,g43)
    c: Coincident(g43,g44)
    c: Coincident(g44,g45)
    c: Coincident(g45,g46)
    c: Coincident(g46,g47)
    c: Coincident(g47,g42)
    c: Equal(g42, g43-g47) x5
    c: PointOnObject(g42,g48)
    c: PointOnObject(g43,g48)
    c: PointOnObject(g44,g48)
    c: PointOnObject(g45,g48)
    c: PointOnObject(g46,g48)
    c: PointOnObject(g47,g48)
    c: Equal(g41,g48)
    c: Diameter(g41) = 7
    c: Vertical(g39)
    c: Vertical(g43)
    c: Distance(g-2,g39) = 1
    c: Symmetric(g38,g43,g-2)
    c: Distance(g41,g-1) = 7
FEATURE [Part::Extrusion] Extrude535  label="hex150"
  Base = -> Sketch543
  Dir = (0,-1,2e-16)
  DirMode = 2
  FaceMakerClass = Part::FaceMakerBullseye
  FaceMakerMode = 3
  LengthFwd = 10
  LengthRev = 0
  Placement = pos=(96,0,14) rot=(0,0,1;0rad)
  Solid = true
  Symmetric = false
FEATURE [Part::MultiFuse] Fusion549
  Placement = pos=(-8,0,-56) rot=(0,0,1;0rad)
  Refine = true
  Shapes = -> [Extrude486,Extrude487,Extrude488,Extrude489,Extrude490,Extrude491,Extrude492,Extrude493,Extrude494,Extrude495,Extrude496,Extrude497,Extrude498,Extrude499,Extrude500,Extrude501,Extrude502,Extrude503,Extrude504,Extrude505,Extrude506,Extrude507,Extrude508,Extrude509,Extrude510,Extrude511,Extrude512,Extrude513,Extrude514,Extrude515,Extrude516,Extrude517,Extrude518,Extrude519,Extrude520,Extrude521,+14 more]
FEATURE [Sketcher::SketchObject] Sketch544
  ArcFitTolerance = 1e-06
  FullyConstrained = true
  MakeInternals = false
  Placement = pos=(0,0,0) rot=(1,0,0;1.5708rad)
  sketch-geometry (49):
    g0: LineSegment StartX=1e-16 StartY=3.5 StartZ=0 EndX=-3.03109 EndY=1.75 EndZ=0
    g1: LineSegment StartX=-3.03109 StartY=1.75 StartZ=0 EndX=-3.03109 EndY=-1.75 EndZ=0
    g2: LineSegment StartX=-3.03109 StartY=-1.75 StartZ=0 EndX=-1e-16 EndY=-3.5 EndZ=0
    g3: LineSegment StartX=-1e-16 StartY=-3.5 StartZ=0 EndX=3.03109 EndY=-1.75 EndZ=0
    g4: LineSegment StartX=3.03109 StartY=-1.75 StartZ=0 EndX=3.03109 EndY=1.75 EndZ=0
    g5: LineSegment StartX=3.03109 StartY=1.75 StartZ=0 EndX=1e-16 EndY=3.5 EndZ=0
    g6: Circle [constr] CenterX=0 CenterY=0 CenterZ=0 NormalX=0 NormalY=0 NormalZ=1 AngleXU=0 Radius=3.5
    g7: LineSegment StartX=4.96892 StartY=-1.75002 StartZ=0 EndX=8.00002 EndY=-3.5 EndZ=0
    g8: LineSegment StartX=8.00002 StartY=-3.5 StartZ=0 EndX=11.0311 EndY=-1.74998 EndZ=0
    g9: LineSegment StartX=11.0311 StartY=-1.74998 StartZ=0 EndX=11.0311 EndY=1.75002 EndZ=0
    g10: LineSegment StartX=11.0311 StartY=1.75002 StartZ=0 EndX=7.99998 EndY=3.5 EndZ=0
    g11: LineSegment StartX=7.99998 StartY=3.5 StartZ=0 EndX=4.9689 EndY=1.74998 EndZ=0
    g12: LineSegment StartX=4.9689 StartY=1.74998 StartZ=0 EndX=4.96892 EndY=-1.75002 EndZ=0
    g13: Circle [constr] CenterX=8 CenterY=0 CenterZ=0 NormalX=0 NormalY=0 NormalZ=1 AngleXU=0 Radius=3.5
    g14: LineSegment StartX=4.03109 StartY=3.5 StartZ=0 EndX=7.06218 EndY=5.25 EndZ=0
    g15: LineSegment StartX=7.06218 StartY=5.25 StartZ=0 EndX=7.06218 EndY=8.75 EndZ=0
    g16: LineSegment StartX=7.06218 StartY=8.75 StartZ=0 EndX=4.03109 EndY=10.5 EndZ=0
    g17: LineSegment StartX=4.03109 StartY=10.5 StartZ=0 EndX=1 EndY=8.75 EndZ=0
    g18: LineSegment StartX=1 StartY=8.75 StartZ=0 EndX=1 EndY=5.25 EndZ=0
    g19: LineSegment StartX=1 StartY=5.25 StartZ=0 EndX=4.03109 EndY=3.5 EndZ=0
    g20: Circle [constr] CenterX=4.03109 CenterY=7 CenterZ=0 NormalX=0 NormalY=0 NormalZ=1 AngleXU=0 Radius=3.5
    g21: LineSegment StartX=-1 StartY=5.25 StartZ=0 EndX=-1 EndY=8.75 EndZ=0
    g22: LineSegment StartX=-1 StartY=8.75 StartZ=0 EndX=-4.03109 EndY=10.5 EndZ=0
    g23: LineSegment StartX=-4.03109 StartY=10.5 StartZ=0 EndX=-7.06218 EndY=8.75 EndZ=0
    g24: LineSegment StartX=-7.06218 StartY=8.75 StartZ=0 EndX=-7.06218 EndY=5.25 EndZ=0
    g25: LineSegment StartX=-7.06218 StartY=5.25 StartZ=0 EndX=-4.03109 EndY=3.5 EndZ=0
    g26: LineSegment StartX=-4.03109 StartY=3.5 StartZ=0 EndX=-1 EndY=5.25 EndZ=0
    g27: Circle [constr] CenterX=-4.03109 CenterY=7 CenterZ=0 NormalX=0 NormalY=0 NormalZ=1 AngleXU=0 Radius=3.5
    g28: LineSegment StartX=-4.96891 StartY=-1.75 StartZ=0 EndX=-4.96891 EndY=1.75 EndZ=0
    g29: LineSegment StartX=-4.96891 StartY=1.75 StartZ=0 EndX=-8 EndY=3.5 EndZ=0
    g30: LineSegment StartX=-8 StartY=3.5 StartZ=0 EndX=-11.0311 EndY=1.75 EndZ=0
    g31: LineSegment StartX=-11.0311 StartY=1.75 StartZ=0 EndX=-11.0311 EndY=-1.75 EndZ=0
    g32: LineSegment StartX=-11.0311 StartY=-1.75 StartZ=0 EndX=-8 EndY=-3.5 EndZ=0
    g33: LineSegment StartX=-8 StartY=-3.5 StartZ=0 EndX=-4.96891 EndY=-1.75 EndZ=0
    g34: Circle [constr] CenterX=-8 CenterY=0 CenterZ=0 NormalX=0 NormalY=0 NormalZ=1 AngleXU=0 Radius=3.5
    g35: LineSegment StartX=-4.03109 StartY=-3.5 StartZ=0 EndX=-7.06218 EndY=-5.25 EndZ=0
    g36: LineSegment StartX=-7.06218 StartY=-5.25 StartZ=0 EndX=-7.06218 EndY=-8.75 EndZ=0
    g37: LineSegment StartX=-7.06218 StartY=-8.75 StartZ=0 EndX=-4.03109 EndY=-10.5 EndZ=0
    g38: LineSegment StartX=-4.03109 StartY=-10.5 StartZ=0 EndX=-1 EndY=-8.75 EndZ=0
    g39: LineSegment StartX=-1 StartY=-8.75 StartZ=0 EndX=-1 EndY=-5.25 EndZ=0
    g40: LineSegment StartX=-1 StartY=-5.25 StartZ=0 EndX=-4.03109 EndY=-3.5 EndZ=0
    g41: Circle [constr] CenterX=-4.03109 CenterY=-7 CenterZ=0 NormalX=0 NormalY=0 NormalZ=1 AngleXU=0 Radius=3.5
    g42: LineSegment StartX=4.03109 StartY=-3.5 StartZ=0 EndX=1 EndY=-5.25 EndZ=0
    g43: LineSegment StartX=1 StartY=-5.25 StartZ=0 EndX=1 EndY=-8.75 EndZ=0
    g44: LineSegment StartX=1 StartY=-8.75 StartZ=0 EndX=4.03109 EndY=-10.5 EndZ=0
    g45: LineSegment StartX=4.03109 StartY=-10.5 StartZ=0 EndX=7.06218 EndY=-8.75 EndZ=0
    g46: LineSegment StartX=7.06218 StartY=-8.75 StartZ=0 EndX=7.06218 EndY=-5.25 EndZ=0
    g47: LineSegment StartX=7.06218 StartY=-5.25 StartZ=0 EndX=4.03109 EndY=-3.5 EndZ=0
    g48: Circle [constr] CenterX=4.03109 CenterY=-7 CenterZ=0 NormalX=0 NormalY=0 NormalZ=1 AngleXU=0 Radius=3.5
  constraints (117):
    c: Coincident(g0,g1)
    c: Coincident(g1,g2)
    c: Coincident(g2,g3)
    c: Coincident(g3,g4)
    c: Coincident(g4,g5)
    c: Coincident(g5,g0)
    c: Equal(g0, g1-g5) x5
    c: PointOnObject(g0,g6)
    c: PointOnObject(g1,g6)
    c: PointOnObject(g2,g6)
    c: PointOnObject(g3,g6)
    c: PointOnObject(g4,g6)
    c: PointOnObject(g5,g6)
    c: Coincident(g6,g-1)
    c: Diameter(g6) = 7
    c: PointOnObject(g0,g-2)
    c: Coincident(g7,g8)
    c: Coincident(g8,g9)
    c: Coincident(g9,g10)
    c: Coincident(g10,g11)
    c: Coincident(g11,g12)
    c: Coincident(g12,g7)
    c: Equal(g7, g8-g12) x5
    c: PointOnObject(g7,g13)
    c: PointOnObject(g8,g13)
    c: PointOnObject(g9,g13)
    c: PointOnObject(g10,g13)
    c: PointOnObject(g11,g13)
    c: PointOnObject(g12,g13)
    c: PointOnObject(g13,g-1)
    c: Diameter(g13) = 7
    c: Distance(g6,g13) = 8
    c: Horizontal(g0,g10)
    c: Coincident(g14,g15)
    c: Coincident(g15,g16)
    c: Coincident(g16,g17)
    c: Coincident(g17,g18)
    c: Coincident(g18,g19)
    c: Coincident(g19,g14)
    c: Equal(g14, g15-g19) x5
    c: PointOnObject(g14,g20)
    c: PointOnObject(g15,g20)
    c: PointOnObject(g16,g20)
    c: PointOnObject(g17,g20)
    c: PointOnObject(g18,g20)
    c: PointOnObject(g19,g20)
    c: Diameter(g20) = 7
    c: DistanceY(g-1,g20) = 7
    c: Vertical(g18)
    c: Distance(g17,g-2) = 1
    c: Coincident(g21,g22)
    c: Coincident(g22,g23)
    c: Coincident(g23,g24)
    c: Coincident(g24,g25)
    c: Coincident(g25,g26)
    c: Coincident(g26,g21)
    c: Equal(g21, g22-g26) x5
    c: PointOnObject(g21,g27)
    c: PointOnObject(g22,g27)
    c: PointOnObject(g23,g27)
    c: PointOnObject(g24,g27)
    c: PointOnObject(g25,g27)
    c: PointOnObject(g26,g27)
    c: Diameter(g27) = 7
    c: DistanceY(g-1,g27) = 7
    c: DistanceX(g21,g-1) = 1
    c: Vertical(g21)
    c: Coincident(g28,g29)
    c: Coincident(g29,g30)
    c: Coincident(g30,g31)
    c: Coincident(g31,g32)
    c: Coincident(g32,g33)
    c: Coincident(g33,g28)
    c: Equal(g28, g29-g33) x5
    c: PointOnObject(g28,g34)
    c: PointOnObject(g29,g34)
    c: PointOnObject(g30,g34)
    c: PointOnObject(g31,g34)
    c: PointOnObject(g32,g34)
    c: PointOnObject(g33,g34)
    c: PointOnObject(g34,g-1)
    c: Diameter(g34) = 7
    c: Vertical(g31)
    c: DistanceX(g34,g-1) = 8
    c: Coincident(g35,g36)
    c: Coincident(g36,g37)
    c: Coincident(g37,g38)
    c: Coincident(g38,g39)
    c: Coincident(g39,g40)
    c: Coincident(g40,g35)
    c: Equal(g35, g36-g40) x5
    c: PointOnObject(g35,g41)
    c: PointOnObject(g36,g41)
    c: PointOnObject(g37,g41)
    c: PointOnObject(g38,g41)
    c: PointOnObject(g39,g41)
    c: PointOnObject(g40,g41)
    c: Coincident(g42,g43)
    c: Coincident(g43,g44)
    c: Coincident(g44,g45)
    c: Coincident(g45,g46)
    c: Coincident(g46,g47)
    c: Coincident(g47,g42)
    c: Equal(g42, g43-g47) x5
    c: PointOnObject(g42,g48)
    c: PointOnObject(g43,g48)
    c: PointOnObject(g44,g48)
    c: PointOnObject(g45,g48)
    c: PointOnObject(g46,g48)
    c: PointOnObject(g47,g48)
    c: Equal(g41,g48)
    c: Diameter(g41) = 7
    c: Vertical(g39)
    c: Vertical(g43)
    c: Distance(g-2,g39) = 1
    c: Symmetric(g38,g43,g-2)
    c: Distance(g41,g-1) = 7
FEATURE [Part::Extrusion] Extrude536  label="hex151"
  Base = -> Sketch544
  Dir = (0,-1,2e-16)
  DirMode = 2
  FaceMakerClass = Part::FaceMakerBullseye
  FaceMakerMode = 3
  LengthFwd = 10
  LengthRev = 0
  Placement = pos=(100,0,-49) rot=(0,0,1;0rad)
  Solid = true
  Symmetric = false
FEATURE [Sketcher::SketchObject] Sketch545
  ArcFitTolerance = 1e-06
  FullyConstrained = true
  MakeInternals = false
  Placement = pos=(0,0,0) rot=(1,0,0;1.5708rad)
  sketch-geometry (49):
    g0: LineSegment StartX=1e-16 StartY=3.5 StartZ=0 EndX=-3.03109 EndY=1.75 EndZ=0
    g1: LineSegment StartX=-3.03109 StartY=1.75 StartZ=0 EndX=-3.03109 EndY=-1.75 EndZ=0
    g2: LineSegment StartX=-3.03109 StartY=-1.75 StartZ=0 EndX=-1e-16 EndY=-3.5 EndZ=0
    g3: LineSegment StartX=-1e-16 StartY=-3.5 StartZ=0 EndX=3.03109 EndY=-1.75 EndZ=0
    g4: LineSegment StartX=3.03109 StartY=-1.75 StartZ=0 EndX=3.03109 EndY=1.75 EndZ=0
    g5: LineSegment StartX=3.03109 StartY=1.75 StartZ=0 EndX=1e-16 EndY=3.5 EndZ=0
    g6: Circle [constr] CenterX=0 CenterY=0 CenterZ=0 NormalX=0 NormalY=0 NormalZ=1 AngleXU=0 Radius=3.5
    g7: LineSegment StartX=4.96892 StartY=-1.75002 StartZ=0 EndX=8.00002 EndY=-3.5 EndZ=0
    g8: LineSegment StartX=8.00002 StartY=-3.5 StartZ=0 EndX=11.0311 EndY=-1.74998 EndZ=0
    g9: LineSegment StartX=11.0311 StartY=-1.74998 StartZ=0 EndX=11.0311 EndY=1.75002 EndZ=0
    g10: LineSegment StartX=11.0311 StartY=1.75002 StartZ=0 EndX=7.99998 EndY=3.5 EndZ=0
    g11: LineSegment StartX=7.99998 StartY=3.5 StartZ=0 EndX=4.9689 EndY=1.74998 EndZ=0
    g12: LineSegment StartX=4.9689 StartY=1.74998 StartZ=0 EndX=4.96892 EndY=-1.75002 EndZ=0
    g13: Circle [constr] CenterX=8 CenterY=0 CenterZ=0 NormalX=0 NormalY=0 NormalZ=1 AngleXU=0 Radius=3.5
    g14: LineSegment StartX=4.03109 StartY=3.5 StartZ=0 EndX=7.06218 EndY=5.25 EndZ=0
    g15: LineSegment StartX=7.06218 StartY=5.25 StartZ=0 EndX=7.06218 EndY=8.75 EndZ=0
    g16: LineSegment StartX=7.06218 StartY=8.75 StartZ=0 EndX=4.03109 EndY=10.5 EndZ=0
    g17: LineSegment StartX=4.03109 StartY=10.5 StartZ=0 EndX=1 EndY=8.75 EndZ=0
    g18: LineSegment StartX=1 StartY=8.75 StartZ=0 EndX=1 EndY=5.25 EndZ=0
    g19: LineSegment StartX=1 StartY=5.25 StartZ=0 EndX=4.03109 EndY=3.5 EndZ=0
    g20: Circle [constr] CenterX=4.03109 CenterY=7 CenterZ=0 NormalX=0 NormalY=0 NormalZ=1 AngleXU=0 Radius=3.5
    g21: LineSegment StartX=-1 StartY=5.25 StartZ=0 EndX=-1 EndY=8.75 EndZ=0
    g22: LineSegment StartX=-1 StartY=8.75 StartZ=0 EndX=-4.03109 EndY=10.5 EndZ=0
    g23: LineSegment StartX=-4.03109 StartY=10.5 StartZ=0 EndX=-7.06218 EndY=8.75 EndZ=0
    g24: LineSegment StartX=-7.06218 StartY=8.75 StartZ=0 EndX=-7.06218 EndY=5.25 EndZ=0
    g25: LineSegment StartX=-7.06218 StartY=5.25 StartZ=0 EndX=-4.03109 EndY=3.5 EndZ=0
    g26: LineSegment StartX=-4.03109 StartY=3.5 StartZ=0 EndX=-1 EndY=5.25 EndZ=0
    g27: Circle [constr] CenterX=-4.03109 CenterY=7 CenterZ=0 NormalX=0 NormalY=0 NormalZ=1 AngleXU=0 Radius=3.5
    g28: LineSegment StartX=-4.96891 StartY=-1.75 StartZ=0 EndX=-4.96891 EndY=1.75 EndZ=0
    g29: LineSegment StartX=-4.96891 StartY=1.75 StartZ=0 EndX=-8 EndY=3.5 EndZ=0
    g30: LineSegment StartX=-8 StartY=3.5 StartZ=0 EndX=-11.0311 EndY=1.75 EndZ=0
    g31: LineSegment StartX=-11.0311 StartY=1.75 StartZ=0 EndX=-11.0311 EndY=-1.75 EndZ=0
    g32: LineSegment StartX=-11.0311 StartY=-1.75 StartZ=0 EndX=-8 EndY=-3.5 EndZ=0
    g33: LineSegment StartX=-8 StartY=-3.5 StartZ=0 EndX=-4.96891 EndY=-1.75 EndZ=0
    g34: Circle [constr] CenterX=-8 CenterY=0 CenterZ=0 NormalX=0 NormalY=0 NormalZ=1 AngleXU=0 Radius=3.5
    g35: LineSegment StartX=-4.03109 StartY=-3.5 StartZ=0 EndX=-7.06218 EndY=-5.25 EndZ=0
    g36: LineSegment StartX=-7.06218 StartY=-5.25 StartZ=0 EndX=-7.06218 EndY=-8.75 EndZ=0
    g37: LineSegment StartX=-7.06218 StartY=-8.75 StartZ=0 EndX=-4.03109 EndY=-10.5 EndZ=0
    g38: LineSegment StartX=-4.03109 StartY=-10.5 StartZ=0 EndX=-1 EndY=-8.75 EndZ=0
    g39: LineSegment StartX=-1 StartY=-8.75 StartZ=0 EndX=-1 EndY=-5.25 EndZ=0
    g40: LineSegment StartX=-1 StartY=-5.25 StartZ=0 EndX=-4.03109 EndY=-3.5 EndZ=0
    g41: Circle [constr] CenterX=-4.03109 CenterY=-7 CenterZ=0 NormalX=0 NormalY=0 NormalZ=1 AngleXU=0 Radius=3.5
    g42: LineSegment StartX=4.03109 StartY=-3.5 StartZ=0 EndX=1 EndY=-5.25 EndZ=0
    g43: LineSegment StartX=1 StartY=-5.25 StartZ=0 EndX=1 EndY=-8.75 EndZ=0
    g44: LineSegment StartX=1 StartY=-8.75 StartZ=0 EndX=4.03109 EndY=-10.5 EndZ=0
    g45: LineSegment StartX=4.03109 StartY=-10.5 StartZ=0 EndX=7.06218 EndY=-8.75 EndZ=0
    g46: LineSegment StartX=7.06218 StartY=-8.75 StartZ=0 EndX=7.06218 EndY=-5.25 EndZ=0
    g47: LineSegment StartX=7.06218 StartY=-5.25 StartZ=0 EndX=4.03109 EndY=-3.5 EndZ=0
    g48: Circle [constr] CenterX=4.03109 CenterY=-7 CenterZ=0 NormalX=0 NormalY=0 NormalZ=1 AngleXU=0 Radius=3.5
  constraints (117):
    c: Coincident(g0,g1)
    c: Coincident(g1,g2)
    c: Coincident(g2,g3)
    c: Coincident(g3,g4)
    c: Coincident(g4,g5)
    c: Coincident(g5,g0)
    c: Equal(g0, g1-g5) x5
    c: PointOnObject(g0,g6)
    c: PointOnObject(g1,g6)
    c: PointOnObject(g2,g6)
    c: PointOnObject(g3,g6)
    c: PointOnObject(g4,g6)
    c: PointOnObject(g5,g6)
    c: Coincident(g6,g-1)
    c: Diameter(g6) = 7
    c: PointOnObject(g0,g-2)
    c: Coincident(g7,g8)
    c: Coincident(g8,g9)
    c: Coincident(g9,g10)
    c: Coincident(g10,g11)
    c: Coincident(g11,g12)
    c: Coincident(g12,g7)
    c: Equal(g7, g8-g12) x5
    c: PointOnObject(g7,g13)
    c: PointOnObject(g8,g13)
    c: PointOnObject(g9,g13)
    c: PointOnObject(g10,g13)
    c: PointOnObject(g11,g13)
    c: PointOnObject(g12,g13)
    c: PointOnObject(g13,g-1)
    c: Diameter(g13) = 7
    c: Distance(g6,g13) = 8
    c: Horizontal(g0,g10)
    c: Coincident(g14,g15)
    c: Coincident(g15,g16)
    c: Coincident(g16,g17)
    c: Coincident(g17,g18)
    c: Coincident(g18,g19)
    c: Coincident(g19,g14)
    c: Equal(g14, g15-g19) x5
    c: PointOnObject(g14,g20)
    c: PointOnObject(g15,g20)
    c: PointOnObject(g16,g20)
    c: PointOnObject(g17,g20)
    c: PointOnObject(g18,g20)
    c: PointOnObject(g19,g20)
    c: Diameter(g20) = 7
    c: DistanceY(g-1,g20) = 7
    c: Vertical(g18)
    c: Distance(g17,g-2) = 1
    c: Coincident(g21,g22)
    c: Coincident(g22,g23)
    c: Coincident(g23,g24)
    c: Coincident(g24,g25)
    c: Coincident(g25,g26)
    c: Coincident(g26,g21)
    c: Equal(g21, g22-g26) x5
    c: PointOnObject(g21,g27)
    c: PointOnObject(g22,g27)
    c: PointOnObject(g23,g27)
    c: PointOnObject(g24,g27)
    c: PointOnObject(g25,g27)
    c: PointOnObject(g26,g27)
    c: Diameter(g27) = 7
    c: DistanceY(g-1,g27) = 7
    c: DistanceX(g21,g-1) = 1
    c: Vertical(g21)
    c: Coincident(g28,g29)
    c: Coincident(g29,g30)
    c: Coincident(g30,g31)
    c: Coincident(g31,g32)
    c: Coincident(g32,g33)
    c: Coincident(g33,g28)
    c: Equal(g28, g29-g33) x5
    c: PointOnObject(g28,g34)
    c: PointOnObject(g29,g34)
    c: PointOnObject(g30,g34)
    c: PointOnObject(g31,g34)
    c: PointOnObject(g32,g34)
    c: PointOnObject(g33,g34)
    c: PointOnObject(g34,g-1)
    c: Diameter(g34) = 7
    c: Vertical(g31)
    c: DistanceX(g34,g-1) = 8
    c: Coincident(g35,g36)
    c: Coincident(g36,g37)
    c: Coincident(g37,g38)
    c: Coincident(g38,g39)
    c: Coincident(g39,g40)
    c: Coincident(g40,g35)
    c: Equal(g35, g36-g40) x5
    c: PointOnObject(g35,g41)
    c: PointOnObject(g36,g41)
    c: PointOnObject(g37,g41)
    c: PointOnObject(g38,g41)
    c: PointOnObject(g39,g41)
    c: PointOnObject(g40,g41)
    c: Coincident(g42,g43)
    c: Coincident(g43,g44)
    c: Coincident(g44,g45)
    c: Coincident(g45,g46)
    c: Coincident(g46,g47)
    c: Coincident(g47,g42)
    c: Equal(g42, g43-g47) x5
    c: PointOnObject(g42,g48)
    c: PointOnObject(g43,g48)
    c: PointOnObject(g44,g48)
    c: PointOnObject(g45,g48)
    c: PointOnObject(g46,g48)
    c: PointOnObject(g47,g48)
    c: Equal(g41,g48)
    c: Diameter(g41) = 7
    c: Vertical(g39)
    c: Vertical(g43)
    c: Distance(g-2,g39) = 1
    c: Symmetric(g38,g43,g-2)
    c: Distance(g41,g-1) = 7
FEATURE [Part::Extrusion] Extrude537  label="hex152"
  Base = -> Sketch545
  Dir = (0,-1,2e-16)
  DirMode = 2
  FaceMakerClass = Part::FaceMakerBullseye
  FaceMakerMode = 3
  LengthFwd = 10
  LengthRev = 0
  Placement = pos=(-92,0,-35) rot=(0,0,1;0rad)
  Solid = true
  Symmetric = false
FEATURE [Sketcher::SketchObject] Sketch546
  ArcFitTolerance = 1e-06
  FullyConstrained = true
  MakeInternals = false
  Placement = pos=(0,0,0) rot=(1,0,0;1.5708rad)
  sketch-geometry (49):
    g0: LineSegment StartX=1e-16 StartY=3.5 StartZ=0 EndX=-3.03109 EndY=1.75 EndZ=0
    g1: LineSegment StartX=-3.03109 StartY=1.75 StartZ=0 EndX=-3.03109 EndY=-1.75 EndZ=0
    g2: LineSegment StartX=-3.03109 StartY=-1.75 StartZ=0 EndX=-1e-16 EndY=-3.5 EndZ=0
    g3: LineSegment StartX=-1e-16 StartY=-3.5 StartZ=0 EndX=3.03109 EndY=-1.75 EndZ=0
    g4: LineSegment StartX=3.03109 StartY=-1.75 StartZ=0 EndX=3.03109 EndY=1.75 EndZ=0
    g5: LineSegment StartX=3.03109 StartY=1.75 StartZ=0 EndX=1e-16 EndY=3.5 EndZ=0
    g6: Circle [constr] CenterX=0 CenterY=0 CenterZ=0 NormalX=0 NormalY=0 NormalZ=1 AngleXU=0 Radius=3.5
    g7: LineSegment StartX=4.96892 StartY=-1.75002 StartZ=0 EndX=8.00002 EndY=-3.5 EndZ=0
    g8: LineSegment StartX=8.00002 StartY=-3.5 StartZ=0 EndX=11.0311 EndY=-1.74998 EndZ=0
    g9: LineSegment StartX=11.0311 StartY=-1.74998 StartZ=0 EndX=11.0311 EndY=1.75002 EndZ=0
    g10: LineSegment StartX=11.0311 StartY=1.75002 StartZ=0 EndX=7.99998 EndY=3.5 EndZ=0
    g11: LineSegment StartX=7.99998 StartY=3.5 StartZ=0 EndX=4.9689 EndY=1.74998 EndZ=0
    g12: LineSegment StartX=4.9689 StartY=1.74998 StartZ=0 EndX=4.96892 EndY=-1.75002 EndZ=0
    g13: Circle [constr] CenterX=8 CenterY=0 CenterZ=0 NormalX=0 NormalY=0 NormalZ=1 AngleXU=0 Radius=3.5
    g14: LineSegment StartX=4.03109 StartY=3.5 StartZ=0 EndX=7.06218 EndY=5.25 EndZ=0
    g15: LineSegment StartX=7.06218 StartY=5.25 StartZ=0 EndX=7.06218 EndY=8.75 EndZ=0
    g16: LineSegment StartX=7.06218 StartY=8.75 StartZ=0 EndX=4.03109 EndY=10.5 EndZ=0
    g17: LineSegment StartX=4.03109 StartY=10.5 StartZ=0 EndX=1 EndY=8.75 EndZ=0
    g18: LineSegment StartX=1 StartY=8.75 StartZ=0 EndX=1 EndY=5.25 EndZ=0
    g19: LineSegment StartX=1 StartY=5.25 StartZ=0 EndX=4.03109 EndY=3.5 EndZ=0
    g20: Circle [constr] CenterX=4.03109 CenterY=7 CenterZ=0 NormalX=0 NormalY=0 NormalZ=1 AngleXU=0 Radius=3.5
    g21: LineSegment StartX=-1 StartY=5.25 StartZ=0 EndX=-1 EndY=8.75 EndZ=0
    g22: LineSegment StartX=-1 StartY=8.75 StartZ=0 EndX=-4.03109 EndY=10.5 EndZ=0
    g23: LineSegment StartX=-4.03109 StartY=10.5 StartZ=0 EndX=-7.06218 EndY=8.75 EndZ=0
    g24: LineSegment StartX=-7.06218 StartY=8.75 StartZ=0 EndX=-7.06218 EndY=5.25 EndZ=0
    g25: LineSegment StartX=-7.06218 StartY=5.25 StartZ=0 EndX=-4.03109 EndY=3.5 EndZ=0
    g26: LineSegment StartX=-4.03109 StartY=3.5 StartZ=0 EndX=-1 EndY=5.25 EndZ=0
    g27: Circle [constr] CenterX=-4.03109 CenterY=7 CenterZ=0 NormalX=0 NormalY=0 NormalZ=1 AngleXU=0 Radius=3.5
    g28: LineSegment StartX=-4.96891 StartY=-1.75 StartZ=0 EndX=-4.96891 EndY=1.75 EndZ=0
    g29: LineSegment StartX=-4.96891 StartY=1.75 StartZ=0 EndX=-8 EndY=3.5 EndZ=0
    g30: LineSegment StartX=-8 StartY=3.5 StartZ=0 EndX=-11.0311 EndY=1.75 EndZ=0
    g31: LineSegment StartX=-11.0311 StartY=1.75 StartZ=0 EndX=-11.0311 EndY=-1.75 EndZ=0
    g32: LineSegment StartX=-11.0311 StartY=-1.75 StartZ=0 EndX=-8 EndY=-3.5 EndZ=0
    g33: LineSegment StartX=-8 StartY=-3.5 StartZ=0 EndX=-4.96891 EndY=-1.75 EndZ=0
    g34: Circle [constr] CenterX=-8 CenterY=0 CenterZ=0 NormalX=0 NormalY=0 NormalZ=1 AngleXU=0 Radius=3.5
    g35: LineSegment StartX=-4.03109 StartY=-3.5 StartZ=0 EndX=-7.06218 EndY=-5.25 EndZ=0
    g36: LineSegment StartX=-7.06218 StartY=-5.25 StartZ=0 EndX=-7.06218 EndY=-8.75 EndZ=0
    g37: LineSegment StartX=-7.06218 StartY=-8.75 StartZ=0 EndX=-4.03109 EndY=-10.5 EndZ=0
    g38: LineSegment StartX=-4.03109 StartY=-10.5 StartZ=0 EndX=-1 EndY=-8.75 EndZ=0
    g39: LineSegment StartX=-1 StartY=-8.75 StartZ=0 EndX=-1 EndY=-5.25 EndZ=0
    g40: LineSegment StartX=-1 StartY=-5.25 StartZ=0 EndX=-4.03109 EndY=-3.5 EndZ=0
    g41: Circle [constr] CenterX=-4.03109 CenterY=-7 CenterZ=0 NormalX=0 NormalY=0 NormalZ=1 AngleXU=0 Radius=3.5
    g42: LineSegment StartX=4.03109 StartY=-3.5 StartZ=0 EndX=1 EndY=-5.25 EndZ=0
    g43: LineSegment StartX=1 StartY=-5.25 StartZ=0 EndX=1 EndY=-8.75 EndZ=0
    g44: LineSegment StartX=1 StartY=-8.75 StartZ=0 EndX=4.03109 EndY=-10.5 EndZ=0
    g45: LineSegment StartX=4.03109 StartY=-10.5 StartZ=0 EndX=7.06218 EndY=-8.75 EndZ=0
    g46: LineSegment StartX=7.06218 StartY=-8.75 StartZ=0 EndX=7.06218 EndY=-5.25 EndZ=0
    g47: LineSegment StartX=7.06218 StartY=-5.25 StartZ=0 EndX=4.03109 EndY=-3.5 EndZ=0
    g48: Circle [constr] CenterX=4.03109 CenterY=-7 CenterZ=0 NormalX=0 NormalY=0 NormalZ=1 AngleXU=0 Radius=3.5
  constraints (117):
    c: Coincident(g0,g1)
    c: Coincident(g1,g2)
    c: Coincident(g2,g3)
    c: Coincident(g3,g4)
    c: Coincident(g4,g5)
    c: Coincident(g5,g0)
    c: Equal(g0, g1-g5) x5
    c: PointOnObject(g0,g6)
    c: PointOnObject(g1,g6)
    c: PointOnObject(g2,g6)
    c: PointOnObject(g3,g6)
    c: PointOnObject(g4,g6)
    c: PointOnObject(g5,g6)
    c: Coincident(g6,g-1)
    c: Diameter(g6) = 7
    c: PointOnObject(g0,g-2)
    c: Coincident(g7,g8)
    c: Coincident(g8,g9)
    c: Coincident(g9,g10)
    c: Coincident(g10,g11)
    c: Coincident(g11,g12)
    c: Coincident(g12,g7)
    c: Equal(g7, g8-g12) x5
    c: PointOnObject(g7,g13)
    c: PointOnObject(g8,g13)
    c: PointOnObject(g9,g13)
    c: PointOnObject(g10,g13)
    c: PointOnObject(g11,g13)
    c: PointOnObject(g12,g13)
    c: PointOnObject(g13,g-1)
    c: Diameter(g13) = 7
    c: Distance(g6,g13) = 8
    c: Horizontal(g0,g10)
    c: Coincident(g14,g15)
    c: Coincident(g15,g16)
    c: Coincident(g16,g17)
    c: Coincident(g17,g18)
    c: Coincident(g18,g19)
    c: Coincident(g19,g14)
    c: Equal(g14, g15-g19) x5
    c: PointOnObject(g14,g20)
    c: PointOnObject(g15,g20)
    c: PointOnObject(g16,g20)
    c: PointOnObject(g17,g20)
    c: PointOnObject(g18,g20)
    c: PointOnObject(g19,g20)
    c: Diameter(g20) = 7
    c: DistanceY(g-1,g20) = 7
    c: Vertical(g18)
    c: Distance(g17,g-2) = 1
    c: Coincident(g21,g22)
    c: Coincident(g22,g23)
    c: Coincident(g23,g24)
    c: Coincident(g24,g25)
    c: Coincident(g25,g26)
    c: Coincident(g26,g21)
    c: Equal(g21, g22-g26) x5
    c: PointOnObject(g21,g27)
    c: PointOnObject(g22,g27)
    c: PointOnObject(g23,g27)
    c: PointOnObject(g24,g27)
    c: PointOnObject(g25,g27)
    c: PointOnObject(g26,g27)
    c: Diameter(g27) = 7
    c: DistanceY(g-1,g27) = 7
    c: DistanceX(g21,g-1) = 1
    c: Vertical(g21)
    c: Coincident(g28,g29)
    c: Coincident(g29,g30)
    c: Coincident(g30,g31)
    c: Coincident(g31,g32)
    c: Coincident(g32,g33)
    c: Coincident(g33,g28)
    c: Equal(g28, g29-g33) x5
    c: PointOnObject(g28,g34)
    c: PointOnObject(g29,g34)
    c: PointOnObject(g30,g34)
    c: PointOnObject(g31,g34)
    c: PointOnObject(g32,g34)
    c: PointOnObject(g33,g34)
    c: PointOnObject(g34,g-1)
    c: Diameter(g34) = 7
    c: Vertical(g31)
    c: DistanceX(g34,g-1) = 8
    c: Coincident(g35,g36)
    c: Coincident(g36,g37)
    c: Coincident(g37,g38)
    c: Coincident(g38,g39)
    c: Coincident(g39,g40)
    c: Coincident(g40,g35)
    c: Equal(g35, g36-g40) x5
    c: PointOnObject(g35,g41)
    c: PointOnObject(g36,g41)
    c: PointOnObject(g37,g41)
    c: PointOnObject(g38,g41)
    c: PointOnObject(g39,g41)
    c: PointOnObject(g40,g41)
    c: Coincident(g42,g43)
    c: Coincident(g43,g44)
    c: Coincident(g44,g45)
    c: Coincident(g45,g46)
    c: Coincident(g46,g47)
    c: Coincident(g47,g42)
    c: Equal(g42, g43-g47) x5
    c: PointOnObject(g42,g48)
    c: PointOnObject(g43,g48)
    c: PointOnObject(g44,g48)
    c: PointOnObject(g45,g48)
    c: PointOnObject(g46,g48)
    c: PointOnObject(g47,g48)
    c: Equal(g41,g48)
    c: Diameter(g41) = 7
    c: Vertical(g39)
    c: Vertical(g43)
    c: Distance(g-2,g39) = 1
    c: Symmetric(g38,g43,g-2)
    c: Distance(g41,g-1) = 7
FEATURE [Part::Extrusion] Extrude538  label="hex153"
  Base = -> Sketch546
  Dir = (0,-1,2e-16)
  DirMode = 2
  FaceMakerClass = Part::FaceMakerBullseye
  FaceMakerMode = 3
  LengthFwd = 10
  LengthRev = 0
  Placement = pos=(-100,0,21) rot=(0,0,1;0rad)
  Solid = true
  Symmetric = false
FEATURE [Sketcher::SketchObject] Sketch547
  ArcFitTolerance = 1e-06
  FullyConstrained = true
  MakeInternals = false
  Placement = pos=(0,0,0) rot=(1,0,0;1.5708rad)
  sketch-geometry (49):
    g0: LineSegment StartX=1e-16 StartY=3.5 StartZ=0 EndX=-3.03109 EndY=1.75 EndZ=0
    g1: LineSegment StartX=-3.03109 StartY=1.75 StartZ=0 EndX=-3.03109 EndY=-1.75 EndZ=0
    g2: LineSegment StartX=-3.03109 StartY=-1.75 StartZ=0 EndX=-1e-16 EndY=-3.5 EndZ=0
    g3: LineSegment StartX=-1e-16 StartY=-3.5 StartZ=0 EndX=3.03109 EndY=-1.75 EndZ=0
    g4: LineSegment StartX=3.03109 StartY=-1.75 StartZ=0 EndX=3.03109 EndY=1.75 EndZ=0
    g5: LineSegment StartX=3.03109 StartY=1.75 StartZ=0 EndX=1e-16 EndY=3.5 EndZ=0
    g6: Circle [constr] CenterX=0 CenterY=0 CenterZ=0 NormalX=0 NormalY=0 NormalZ=1 AngleXU=0 Radius=3.5
    g7: LineSegment StartX=4.96892 StartY=-1.75002 StartZ=0 EndX=8.00002 EndY=-3.5 EndZ=0
    g8: LineSegment StartX=8.00002 StartY=-3.5 StartZ=0 EndX=11.0311 EndY=-1.74998 EndZ=0
    g9: LineSegment StartX=11.0311 StartY=-1.74998 StartZ=0 EndX=11.0311 EndY=1.75002 EndZ=0
    g10: LineSegment StartX=11.0311 StartY=1.75002 StartZ=0 EndX=7.99998 EndY=3.5 EndZ=0
    g11: LineSegment StartX=7.99998 StartY=3.5 StartZ=0 EndX=4.9689 EndY=1.74998 EndZ=0
    g12: LineSegment StartX=4.9689 StartY=1.74998 StartZ=0 EndX=4.96892 EndY=-1.75002 EndZ=0
    g13: Circle [constr] CenterX=8 CenterY=0 CenterZ=0 NormalX=0 NormalY=0 NormalZ=1 AngleXU=0 Radius=3.5
    g14: LineSegment StartX=4.03109 StartY=3.5 StartZ=0 EndX=7.06218 EndY=5.25 EndZ=0
    g15: LineSegment StartX=7.06218 StartY=5.25 StartZ=0 EndX=7.06218 EndY=8.75 EndZ=0
    g16: LineSegment StartX=7.06218 StartY=8.75 StartZ=0 EndX=4.03109 EndY=10.5 EndZ=0
    g17: LineSegment StartX=4.03109 StartY=10.5 StartZ=0 EndX=1 EndY=8.75 EndZ=0
    g18: LineSegment StartX=1 StartY=8.75 StartZ=0 EndX=1 EndY=5.25 EndZ=0
    g19: LineSegment StartX=1 StartY=5.25 StartZ=0 EndX=4.03109 EndY=3.5 EndZ=0
    g20: Circle [constr] CenterX=4.03109 CenterY=7 CenterZ=0 NormalX=0 NormalY=0 NormalZ=1 AngleXU=0 Radius=3.5
    g21: LineSegment StartX=-1 StartY=5.25 StartZ=0 EndX=-1 EndY=8.75 EndZ=0
    g22: LineSegment StartX=-1 StartY=8.75 StartZ=0 EndX=-4.03109 EndY=10.5 EndZ=0
    g23: LineSegment StartX=-4.03109 StartY=10.5 StartZ=0 EndX=-7.06218 EndY=8.75 EndZ=0
    g24: LineSegment StartX=-7.06218 StartY=8.75 StartZ=0 EndX=-7.06218 EndY=5.25 EndZ=0
    g25: LineSegment StartX=-7.06218 StartY=5.25 StartZ=0 EndX=-4.03109 EndY=3.5 EndZ=0
    g26: LineSegment StartX=-4.03109 StartY=3.5 StartZ=0 EndX=-1 EndY=5.25 EndZ=0
    g27: Circle [constr] CenterX=-4.03109 CenterY=7 CenterZ=0 NormalX=0 NormalY=0 NormalZ=1 AngleXU=0 Radius=3.5
    g28: LineSegment StartX=-4.96891 StartY=-1.75 StartZ=0 EndX=-4.96891 EndY=1.75 EndZ=0
    g29: LineSegment StartX=-4.96891 StartY=1.75 StartZ=0 EndX=-8 EndY=3.5 EndZ=0
    g30: LineSegment StartX=-8 StartY=3.5 StartZ=0 EndX=-11.0311 EndY=1.75 EndZ=0
    g31: LineSegment StartX=-11.0311 StartY=1.75 StartZ=0 EndX=-11.0311 EndY=-1.75 EndZ=0
    g32: LineSegment StartX=-11.0311 StartY=-1.75 StartZ=0 EndX=-8 EndY=-3.5 EndZ=0
    g33: LineSegment StartX=-8 StartY=-3.5 StartZ=0 EndX=-4.96891 EndY=-1.75 EndZ=0
    g34: Circle [constr] CenterX=-8 CenterY=0 CenterZ=0 NormalX=0 NormalY=0 NormalZ=1 AngleXU=0 Radius=3.5
    g35: LineSegment StartX=-4.03109 StartY=-3.5 StartZ=0 EndX=-7.06218 EndY=-5.25 EndZ=0
    g36: LineSegment StartX=-7.06218 StartY=-5.25 StartZ=0 EndX=-7.06218 EndY=-8.75 EndZ=0
    g37: LineSegment StartX=-7.06218 StartY=-8.75 StartZ=0 EndX=-4.03109 EndY=-10.5 EndZ=0
    g38: LineSegment StartX=-4.03109 StartY=-10.5 StartZ=0 EndX=-1 EndY=-8.75 EndZ=0
    g39: LineSegment StartX=-1 StartY=-8.75 StartZ=0 EndX=-1 EndY=-5.25 EndZ=0
    g40: LineSegment StartX=-1 StartY=-5.25 StartZ=0 EndX=-4.03109 EndY=-3.5 EndZ=0
    g41: Circle [constr] CenterX=-4.03109 CenterY=-7 CenterZ=0 NormalX=0 NormalY=0 NormalZ=1 AngleXU=0 Radius=3.5
    g42: LineSegment StartX=4.03109 StartY=-3.5 StartZ=0 EndX=1 EndY=-5.25 EndZ=0
    g43: LineSegment StartX=1 StartY=-5.25 StartZ=0 EndX=1 EndY=-8.75 EndZ=0
    g44: LineSegment StartX=1 StartY=-8.75 StartZ=0 EndX=4.03109 EndY=-10.5 EndZ=0
    g45: LineSegment StartX=4.03109 StartY=-10.5 StartZ=0 EndX=7.06218 EndY=-8.75 EndZ=0
    g46: LineSegment StartX=7.06218 StartY=-8.75 StartZ=0 EndX=7.06218 EndY=-5.25 EndZ=0
    g47: LineSegment StartX=7.06218 StartY=-5.25 StartZ=0 EndX=4.03109 EndY=-3.5 EndZ=0
    g48: Circle [constr] CenterX=4.03109 CenterY=-7 CenterZ=0 NormalX=0 NormalY=0 NormalZ=1 AngleXU=0 Radius=3.5
  constraints (117):
    c: Coincident(g0,g1)
    c: Coincident(g1,g2)
    c: Coincident(g2,g3)
    c: Coincident(g3,g4)
    c: Coincident(g4,g5)
    c: Coincident(g5,g0)
    c: Equal(g0, g1-g5) x5
    c: PointOnObject(g0,g6)
    c: PointOnObject(g1,g6)
    c: PointOnObject(g2,g6)
    c: PointOnObject(g3,g6)
    c: PointOnObject(g4,g6)
    c: PointOnObject(g5,g6)
    c: Coincident(g6,g-1)
    c: Diameter(g6) = 7
    c: PointOnObject(g0,g-2)
    c: Coincident(g7,g8)
    c: Coincident(g8,g9)
    c: Coincident(g9,g10)
    c: Coincident(g10,g11)
    c: Coincident(g11,g12)
    c: Coincident(g12,g7)
    c: Equal(g7, g8-g12) x5
    c: PointOnObject(g7,g13)
    c: PointOnObject(g8,g13)
    c: PointOnObject(g9,g13)
    c: PointOnObject(g10,g13)
    c: PointOnObject(g11,g13)
    c: PointOnObject(g12,g13)
    c: PointOnObject(g13,g-1)
    c: Diameter(g13) = 7
    c: Distance(g6,g13) = 8
    c: Horizontal(g0,g10)
    c: Coincident(g14,g15)
    c: Coincident(g15,g16)
    c: Coincident(g16,g17)
    c: Coincident(g17,g18)
    c: Coincident(g18,g19)
    c: Coincident(g19,g14)
    c: Equal(g14, g15-g19) x5
    c: PointOnObject(g14,g20)
    c: PointOnObject(g15,g20)
    c: PointOnObject(g16,g20)
    c: PointOnObject(g17,g20)
    c: PointOnObject(g18,g20)
    c: PointOnObject(g19,g20)
    c: Diameter(g20) = 7
    c: DistanceY(g-1,g20) = 7
    c: Vertical(g18)
    c: Distance(g17,g-2) = 1
    c: Coincident(g21,g22)
    c: Coincident(g22,g23)
    c: Coincident(g23,g24)
    c: Coincident(g24,g25)
    c: Coincident(g25,g26)
    c: Coincident(g26,g21)
    c: Equal(g21, g22-g26) x5
    c: PointOnObject(g21,g27)
    c: PointOnObject(g22,g27)
    c: PointOnObject(g23,g27)
    c: PointOnObject(g24,g27)
    c: PointOnObject(g25,g27)
    c: PointOnObject(g26,g27)
    c: Diameter(g27) = 7
    c: DistanceY(g-1,g27) = 7
    c: DistanceX(g21,g-1) = 1
    c: Vertical(g21)
    c: Coincident(g28,g29)
    c: Coincident(g29,g30)
    c: Coincident(g30,g31)
    c: Coincident(g31,g32)
    c: Coincident(g32,g33)
    c: Coincident(g33,g28)
    c: Equal(g28, g29-g33) x5
    c: PointOnObject(g28,g34)
    c: PointOnObject(g29,g34)
    c: PointOnObject(g30,g34)
    c: PointOnObject(g31,g34)
    c: PointOnObject(g32,g34)
    c: PointOnObject(g33,g34)
    c: PointOnObject(g34,g-1)
    c: Diameter(g34) = 7
    c: Vertical(g31)
    c: DistanceX(g34,g-1) = 8
    c: Coincident(g35,g36)
    c: Coincident(g36,g37)
    c: Coincident(g37,g38)
    c: Coincident(g38,g39)
    c: Coincident(g39,g40)
    c: Coincident(g40,g35)
    c: Equal(g35, g36-g40) x5
    c: PointOnObject(g35,g41)
    c: PointOnObject(g36,g41)
    c: PointOnObject(g37,g41)
    c: PointOnObject(g38,g41)
    c: PointOnObject(g39,g41)
    c: PointOnObject(g40,g41)
    c: Coincident(g42,g43)
    c: Coincident(g43,g44)
    c: Coincident(g44,g45)
    c: Coincident(g45,g46)
    c: Coincident(g46,g47)
    c: Coincident(g47,g42)
    c: Equal(g42, g43-g47) x5
    c: PointOnObject(g42,g48)
    c: PointOnObject(g43,g48)
    c: PointOnObject(g44,g48)
    c: PointOnObject(g45,g48)
    c: PointOnObject(g46,g48)
    c: PointOnObject(g47,g48)
    c: Equal(g41,g48)
    c: Diameter(g41) = 7
    c: Vertical(g39)
    c: Vertical(g43)
    c: Distance(g-2,g39) = 1
    c: Symmetric(g38,g43,g-2)
    c: Distance(g41,g-1) = 7
FEATURE [Part::Extrusion] Extrude539  label="hex154"
  Base = -> Sketch547
  Dir = (0,-1,2e-16)
  DirMode = 2
  FaceMakerClass = Part::FaceMakerBullseye
  FaceMakerMode = 3
  LengthFwd = 10
  LengthRev = 0
  Placement = pos=(-104,0,-28) rot=(0,0,1;0rad)
  Solid = true
  Symmetric = false
FEATURE [Sketcher::SketchObject] Sketch548
  ArcFitTolerance = 1e-06
  FullyConstrained = true
  MakeInternals = false
  Placement = pos=(0,0,0) rot=(1,0,0;1.5708rad)
  sketch-geometry (49):
    g0: LineSegment StartX=1e-16 StartY=3.5 StartZ=0 EndX=-3.03109 EndY=1.75 EndZ=0
    g1: LineSegment StartX=-3.03109 StartY=1.75 StartZ=0 EndX=-3.03109 EndY=-1.75 EndZ=0
    g2: LineSegment StartX=-3.03109 StartY=-1.75 StartZ=0 EndX=-1e-16 EndY=-3.5 EndZ=0
    g3: LineSegment StartX=-1e-16 StartY=-3.5 StartZ=0 EndX=3.03109 EndY=-1.75 EndZ=0
    g4: LineSegment StartX=3.03109 StartY=-1.75 StartZ=0 EndX=3.03109 EndY=1.75 EndZ=0
    g5: LineSegment StartX=3.03109 StartY=1.75 StartZ=0 EndX=1e-16 EndY=3.5 EndZ=0
    g6: Circle [constr] CenterX=0 CenterY=0 CenterZ=0 NormalX=0 NormalY=0 NormalZ=1 AngleXU=0 Radius=3.5
    g7: LineSegment StartX=4.96892 StartY=-1.75002 StartZ=0 EndX=8.00002 EndY=-3.5 EndZ=0
    g8: LineSegment StartX=8.00002 StartY=-3.5 StartZ=0 EndX=11.0311 EndY=-1.74998 EndZ=0
    g9: LineSegment StartX=11.0311 StartY=-1.74998 StartZ=0 EndX=11.0311 EndY=1.75002 EndZ=0
    g10: LineSegment StartX=11.0311 StartY=1.75002 StartZ=0 EndX=7.99998 EndY=3.5 EndZ=0
    g11: LineSegment StartX=7.99998 StartY=3.5 StartZ=0 EndX=4.9689 EndY=1.74998 EndZ=0
    g12: LineSegment StartX=4.9689 StartY=1.74998 StartZ=0 EndX=4.96892 EndY=-1.75002 EndZ=0
    g13: Circle [constr] CenterX=8 CenterY=0 CenterZ=0 NormalX=0 NormalY=0 NormalZ=1 AngleXU=0 Radius=3.5
    g14: LineSegment StartX=4.03109 StartY=3.5 StartZ=0 EndX=7.06218 EndY=5.25 EndZ=0
    g15: LineSegment StartX=7.06218 StartY=5.25 StartZ=0 EndX=7.06218 EndY=8.75 EndZ=0
    g16: LineSegment StartX=7.06218 StartY=8.75 StartZ=0 EndX=4.03109 EndY=10.5 EndZ=0
    g17: LineSegment StartX=4.03109 StartY=10.5 StartZ=0 EndX=1 EndY=8.75 EndZ=0
    g18: LineSegment StartX=1 StartY=8.75 StartZ=0 EndX=1 EndY=5.25 EndZ=0
    g19: LineSegment StartX=1 StartY=5.25 StartZ=0 EndX=4.03109 EndY=3.5 EndZ=0
    g20: Circle [constr] CenterX=4.03109 CenterY=7 CenterZ=0 NormalX=0 NormalY=0 NormalZ=1 AngleXU=0 Radius=3.5
    g21: LineSegment StartX=-1 StartY=5.25 StartZ=0 EndX=-1 EndY=8.75 EndZ=0
    g22: LineSegment StartX=-1 StartY=8.75 StartZ=0 EndX=-4.03109 EndY=10.5 EndZ=0
    g23: LineSegment StartX=-4.03109 StartY=10.5 StartZ=0 EndX=-7.06218 EndY=8.75 EndZ=0
    g24: LineSegment StartX=-7.06218 StartY=8.75 StartZ=0 EndX=-7.06218 EndY=5.25 EndZ=0
    g25: LineSegment StartX=-7.06218 StartY=5.25 StartZ=0 EndX=-4.03109 EndY=3.5 EndZ=0
    g26: LineSegment StartX=-4.03109 StartY=3.5 StartZ=0 EndX=-1 EndY=5.25 EndZ=0
    g27: Circle [constr] CenterX=-4.03109 CenterY=7 CenterZ=0 NormalX=0 NormalY=0 NormalZ=1 AngleXU=0 Radius=3.5
    g28: LineSegment StartX=-4.96891 StartY=-1.75 StartZ=0 EndX=-4.96891 EndY=1.75 EndZ=0
    g29: LineSegment StartX=-4.96891 StartY=1.75 StartZ=0 EndX=-8 EndY=3.5 EndZ=0
    g30: LineSegment StartX=-8 StartY=3.5 StartZ=0 EndX=-11.0311 EndY=1.75 EndZ=0
    g31: LineSegment StartX=-11.0311 StartY=1.75 StartZ=0 EndX=-11.0311 EndY=-1.75 EndZ=0
    g32: LineSegment StartX=-11.0311 StartY=-1.75 StartZ=0 EndX=-8 EndY=-3.5 EndZ=0
    g33: LineSegment StartX=-8 StartY=-3.5 StartZ=0 EndX=-4.96891 EndY=-1.75 EndZ=0
    g34: Circle [constr] CenterX=-8 CenterY=0 CenterZ=0 NormalX=0 NormalY=0 NormalZ=1 AngleXU=0 Radius=3.5
    g35: LineSegment StartX=-4.03109 StartY=-3.5 StartZ=0 EndX=-7.06218 EndY=-5.25 EndZ=0
    g36: LineSegment StartX=-7.06218 StartY=-5.25 StartZ=0 EndX=-7.06218 EndY=-8.75 EndZ=0
    g37: LineSegment StartX=-7.06218 StartY=-8.75 StartZ=0 EndX=-4.03109 EndY=-10.5 EndZ=0
    g38: LineSegment StartX=-4.03109 StartY=-10.5 StartZ=0 EndX=-1 EndY=-8.75 EndZ=0
    g39: LineSegment StartX=-1 StartY=-8.75 StartZ=0 EndX=-1 EndY=-5.25 EndZ=0
    g40: LineSegment StartX=-1 StartY=-5.25 StartZ=0 EndX=-4.03109 EndY=-3.5 EndZ=0
    g41: Circle [constr] CenterX=-4.03109 CenterY=-7 CenterZ=0 NormalX=0 NormalY=0 NormalZ=1 AngleXU=0 Radius=3.5
    g42: LineSegment StartX=4.03109 StartY=-3.5 StartZ=0 EndX=1 EndY=-5.25 EndZ=0
    g43: LineSegment StartX=1 StartY=-5.25 StartZ=0 EndX=1 EndY=-8.75 EndZ=0
    g44: LineSegment StartX=1 StartY=-8.75 StartZ=0 EndX=4.03109 EndY=-10.5 EndZ=0
    g45: LineSegment StartX=4.03109 StartY=-10.5 StartZ=0 EndX=7.06218 EndY=-8.75 EndZ=0
    g46: LineSegment StartX=7.06218 StartY=-8.75 StartZ=0 EndX=7.06218 EndY=-5.25 EndZ=0
    g47: LineSegment StartX=7.06218 StartY=-5.25 StartZ=0 EndX=4.03109 EndY=-3.5 EndZ=0
    g48: Circle [constr] CenterX=4.03109 CenterY=-7 CenterZ=0 NormalX=0 NormalY=0 NormalZ=1 AngleXU=0 Radius=3.5
  constraints (117):
    c: Coincident(g0,g1)
    c: Coincident(g1,g2)
    c: Coincident(g2,g3)
    c: Coincident(g3,g4)
    c: Coincident(g4,g5)
    c: Coincident(g5,g0)
    c: Equal(g0, g1-g5) x5
    c: PointOnObject(g0,g6)
    c: PointOnObject(g1,g6)
    c: PointOnObject(g2,g6)
    c: PointOnObject(g3,g6)
    c: PointOnObject(g4,g6)
    c: PointOnObject(g5,g6)
    c: Coincident(g6,g-1)
    c: Diameter(g6) = 7
    c: PointOnObject(g0,g-2)
    c: Coincident(g7,g8)
    c: Coincident(g8,g9)
    c: Coincident(g9,g10)
    c: Coincident(g10,g11)
    c: Coincident(g11,g12)
    c: Coincident(g12,g7)
    c: Equal(g7, g8-g12) x5
    c: PointOnObject(g7,g13)
    c: PointOnObject(g8,g13)
    c: PointOnObject(g9,g13)
    c: PointOnObject(g10,g13)
    c: PointOnObject(g11,g13)
    c: PointOnObject(g12,g13)
    c: PointOnObject(g13,g-1)
    c: Diameter(g13) = 7
    c: Distance(g6,g13) = 8
    c: Horizontal(g0,g10)
    c: Coincident(g14,g15)
    c: Coincident(g15,g16)
    c: Coincident(g16,g17)
    c: Coincident(g17,g18)
    c: Coincident(g18,g19)
    c: Coincident(g19,g14)
    c: Equal(g14, g15-g19) x5
    c: PointOnObject(g14,g20)
    c: PointOnObject(g15,g20)
    c: PointOnObject(g16,g20)
    c: PointOnObject(g17,g20)
    c: PointOnObject(g18,g20)
    c: PointOnObject(g19,g20)
    c: Diameter(g20) = 7
    c: DistanceY(g-1,g20) = 7
    c: Vertical(g18)
    c: Distance(g17,g-2) = 1
    c: Coincident(g21,g22)
    c: Coincident(g22,g23)
    c: Coincident(g23,g24)
    c: Coincident(g24,g25)
    c: Coincident(g25,g26)
    c: Coincident(g26,g21)
    c: Equal(g21, g22-g26) x5
    c: PointOnObject(g21,g27)
    c: PointOnObject(g22,g27)
    c: PointOnObject(g23,g27)
    c: PointOnObject(g24,g27)
    c: PointOnObject(g25,g27)
    c: PointOnObject(g26,g27)
    c: Diameter(g27) = 7
    c: DistanceY(g-1,g27) = 7
    c: DistanceX(g21,g-1) = 1
    c: Vertical(g21)
    c: Coincident(g28,g29)
    c: Coincident(g29,g30)
    c: Coincident(g30,g31)
    c: Coincident(g31,g32)
    c: Coincident(g32,g33)
    c: Coincident(g33,g28)
    c: Equal(g28, g29-g33) x5
    c: PointOnObject(g28,g34)
    c: PointOnObject(g29,g34)
    c: PointOnObject(g30,g34)
    c: PointOnObject(g31,g34)
    c: PointOnObject(g32,g34)
    c: PointOnObject(g33,g34)
    c: PointOnObject(g34,g-1)
    c: Diameter(g34) = 7
    c: Vertical(g31)
    c: DistanceX(g34,g-1) = 8
    c: Coincident(g35,g36)
    c: Coincident(g36,g37)
    c: Coincident(g37,g38)
    c: Coincident(g38,g39)
    c: Coincident(g39,g40)
    c: Coincident(g40,g35)
    c: Equal(g35, g36-g40) x5
    c: PointOnObject(g35,g41)
    c: PointOnObject(g36,g41)
    c: PointOnObject(g37,g41)
    c: PointOnObject(g38,g41)
    c: PointOnObject(g39,g41)
    c: PointOnObject(g40,g41)
    c: Coincident(g42,g43)
    c: Coincident(g43,g44)
    c: Coincident(g44,g45)
    c: Coincident(g45,g46)
    c: Coincident(g46,g47)
    c: Coincident(g47,g42)
    c: Equal(g42, g43-g47) x5
    c: PointOnObject(g42,g48)
    c: PointOnObject(g43,g48)
    c: PointOnObject(g44,g48)
    c: PointOnObject(g45,g48)
    c: PointOnObject(g46,g48)
    c: PointOnObject(g47,g48)
    c: Equal(g41,g48)
    c: Diameter(g41) = 7
    c: Vertical(g39)
    c: Vertical(g43)
    c: Distance(g-2,g39) = 1
    c: Symmetric(g38,g43,g-2)
    c: Distance(g41,g-1) = 7
FEATURE [Part::Extrusion] Extrude540  label="hex155"
  Base = -> Sketch548
  Dir = (0,-1,2e-16)
  DirMode = 2
  FaceMakerClass = Part::FaceMakerBullseye
  FaceMakerMode = 3
  LengthFwd = 10
  LengthRev = 0
  Placement = pos=(-100,0,35) rot=(0,0,1;0rad)
  Solid = true
  Symmetric = false
FEATURE [Sketcher::SketchObject] Sketch549
  ArcFitTolerance = 1e-06
  FullyConstrained = true
  MakeInternals = false
  Placement = pos=(0,0,0) rot=(1,0,0;1.5708rad)
  sketch-geometry (49):
    g0: LineSegment StartX=1e-16 StartY=3.5 StartZ=0 EndX=-3.03109 EndY=1.75 EndZ=0
    g1: LineSegment StartX=-3.03109 StartY=1.75 StartZ=0 EndX=-3.03109 EndY=-1.75 EndZ=0
    g2: LineSegment StartX=-3.03109 StartY=-1.75 StartZ=0 EndX=-1e-16 EndY=-3.5 EndZ=0
    g3: LineSegment StartX=-1e-16 StartY=-3.5 StartZ=0 EndX=3.03109 EndY=-1.75 EndZ=0
    g4: LineSegment StartX=3.03109 StartY=-1.75 StartZ=0 EndX=3.03109 EndY=1.75 EndZ=0
    g5: LineSegment StartX=3.03109 StartY=1.75 StartZ=0 EndX=1e-16 EndY=3.5 EndZ=0
    g6: Circle [constr] CenterX=0 CenterY=0 CenterZ=0 NormalX=0 NormalY=0 NormalZ=1 AngleXU=0 Radius=3.5
    g7: LineSegment StartX=4.96892 StartY=-1.75002 StartZ=0 EndX=8.00002 EndY=-3.5 EndZ=0
    g8: LineSegment StartX=8.00002 StartY=-3.5 StartZ=0 EndX=11.0311 EndY=-1.74998 EndZ=0
    g9: LineSegment StartX=11.0311 StartY=-1.74998 StartZ=0 EndX=11.0311 EndY=1.75002 EndZ=0
    g10: LineSegment StartX=11.0311 StartY=1.75002 StartZ=0 EndX=7.99998 EndY=3.5 EndZ=0
    g11: LineSegment StartX=7.99998 StartY=3.5 StartZ=0 EndX=4.9689 EndY=1.74998 EndZ=0
    g12: LineSegment StartX=4.9689 StartY=1.74998 StartZ=0 EndX=4.96892 EndY=-1.75002 EndZ=0
    g13: Circle [constr] CenterX=8 CenterY=0 CenterZ=0 NormalX=0 NormalY=0 NormalZ=1 AngleXU=0 Radius=3.5
    g14: LineSegment StartX=4.03109 StartY=3.5 StartZ=0 EndX=7.06218 EndY=5.25 EndZ=0
    g15: LineSegment StartX=7.06218 StartY=5.25 StartZ=0 EndX=7.06218 EndY=8.75 EndZ=0
    g16: LineSegment StartX=7.06218 StartY=8.75 StartZ=0 EndX=4.03109 EndY=10.5 EndZ=0
    g17: LineSegment StartX=4.03109 StartY=10.5 StartZ=0 EndX=1 EndY=8.75 EndZ=0
    g18: LineSegment StartX=1 StartY=8.75 StartZ=0 EndX=1 EndY=5.25 EndZ=0
    g19: LineSegment StartX=1 StartY=5.25 StartZ=0 EndX=4.03109 EndY=3.5 EndZ=0
    g20: Circle [constr] CenterX=4.03109 CenterY=7 CenterZ=0 NormalX=0 NormalY=0 NormalZ=1 AngleXU=0 Radius=3.5
    g21: LineSegment StartX=-1 StartY=5.25 StartZ=0 EndX=-1 EndY=8.75 EndZ=0
    g22: LineSegment StartX=-1 StartY=8.75 StartZ=0 EndX=-4.03109 EndY=10.5 EndZ=0
    g23: LineSegment StartX=-4.03109 StartY=10.5 StartZ=0 EndX=-7.06218 EndY=8.75 EndZ=0
    g24: LineSegment StartX=-7.06218 StartY=8.75 StartZ=0 EndX=-7.06218 EndY=5.25 EndZ=0
    g25: LineSegment StartX=-7.06218 StartY=5.25 StartZ=0 EndX=-4.03109 EndY=3.5 EndZ=0
    g26: LineSegment StartX=-4.03109 StartY=3.5 StartZ=0 EndX=-1 EndY=5.25 EndZ=0
    g27: Circle [constr] CenterX=-4.03109 CenterY=7 CenterZ=0 NormalX=0 NormalY=0 NormalZ=1 AngleXU=0 Radius=3.5
    g28: LineSegment StartX=-4.96891 StartY=-1.75 StartZ=0 EndX=-4.96891 EndY=1.75 EndZ=0
    g29: LineSegment StartX=-4.96891 StartY=1.75 StartZ=0 EndX=-8 EndY=3.5 EndZ=0
    g30: LineSegment StartX=-8 StartY=3.5 StartZ=0 EndX=-11.0311 EndY=1.75 EndZ=0
    g31: LineSegment StartX=-11.0311 StartY=1.75 StartZ=0 EndX=-11.0311 EndY=-1.75 EndZ=0
    g32: LineSegment StartX=-11.0311 StartY=-1.75 StartZ=0 EndX=-8 EndY=-3.5 EndZ=0
    g33: LineSegment StartX=-8 StartY=-3.5 StartZ=0 EndX=-4.96891 EndY=-1.75 EndZ=0
    g34: Circle [constr] CenterX=-8 CenterY=0 CenterZ=0 NormalX=0 NormalY=0 NormalZ=1 AngleXU=0 Radius=3.5
    g35: LineSegment StartX=-4.03109 StartY=-3.5 StartZ=0 EndX=-7.06218 EndY=-5.25 EndZ=0
    g36: LineSegment StartX=-7.06218 StartY=-5.25 StartZ=0 EndX=-7.06218 EndY=-8.75 EndZ=0
    g37: LineSegment StartX=-7.06218 StartY=-8.75 StartZ=0 EndX=-4.03109 EndY=-10.5 EndZ=0
    g38: LineSegment StartX=-4.03109 StartY=-10.5 StartZ=0 EndX=-1 EndY=-8.75 EndZ=0
    g39: LineSegment StartX=-1 StartY=-8.75 StartZ=0 EndX=-1 EndY=-5.25 EndZ=0
    g40: LineSegment StartX=-1 StartY=-5.25 StartZ=0 EndX=-4.03109 EndY=-3.5 EndZ=0
    g41: Circle [constr] CenterX=-4.03109 CenterY=-7 CenterZ=0 NormalX=0 NormalY=0 NormalZ=1 AngleXU=0 Radius=3.5
    g42: LineSegment StartX=4.03109 StartY=-3.5 StartZ=0 EndX=1 EndY=-5.25 EndZ=0
    g43: LineSegment StartX=1 StartY=-5.25 StartZ=0 EndX=1 EndY=-8.75 EndZ=0
    g44: LineSegment StartX=1 StartY=-8.75 StartZ=0 EndX=4.03109 EndY=-10.5 EndZ=0
    g45: LineSegment StartX=4.03109 StartY=-10.5 StartZ=0 EndX=7.06218 EndY=-8.75 EndZ=0
    g46: LineSegment StartX=7.06218 StartY=-8.75 StartZ=0 EndX=7.06218 EndY=-5.25 EndZ=0
    g47: LineSegment StartX=7.06218 StartY=-5.25 StartZ=0 EndX=4.03109 EndY=-3.5 EndZ=0
    g48: Circle [constr] CenterX=4.03109 CenterY=-7 CenterZ=0 NormalX=0 NormalY=0 NormalZ=1 AngleXU=0 Radius=3.5
  constraints (117):
    c: Coincident(g0,g1)
    c: Coincident(g1,g2)
    c: Coincident(g2,g3)
    c: Coincident(g3,g4)
    c: Coincident(g4,g5)
    c: Coincident(g5,g0)
    c: Equal(g0, g1-g5) x5
    c: PointOnObject(g0,g6)
    c: PointOnObject(g1,g6)
    c: PointOnObject(g2,g6)
    c: PointOnObject(g3,g6)
    c: PointOnObject(g4,g6)
    c: PointOnObject(g5,g6)
    c: Coincident(g6,g-1)
    c: Diameter(g6) = 7
    c: PointOnObject(g0,g-2)
    c: Coincident(g7,g8)
    c: Coincident(g8,g9)
    c: Coincident(g9,g10)
    c: Coincident(g10,g11)
    c: Coincident(g11,g12)
    c: Coincident(g12,g7)
    c: Equal(g7, g8-g12) x5
    c: PointOnObject(g7,g13)
    c: PointOnObject(g8,g13)
    c: PointOnObject(g9,g13)
    c: PointOnObject(g10,g13)
    c: PointOnObject(g11,g13)
    c: PointOnObject(g12,g13)
    c: PointOnObject(g13,g-1)
    c: Diameter(g13) = 7
    c: Distance(g6,g13) = 8
    c: Horizontal(g0,g10)
    c: Coincident(g14,g15)
    c: Coincident(g15,g16)
    c: Coincident(g16,g17)
    c: Coincident(g17,g18)
    c: Coincident(g18,g19)
    c: Coincident(g19,g14)
    c: Equal(g14, g15-g19) x5
    c: PointOnObject(g14,g20)
    c: PointOnObject(g15,g20)
    c: PointOnObject(g16,g20)
    c: PointOnObject(g17,g20)
    c: PointOnObject(g18,g20)
    c: PointOnObject(g19,g20)
    c: Diameter(g20) = 7
    c: DistanceY(g-1,g20) = 7
    c: Vertical(g18)
    c: Distance(g17,g-2) = 1
    c: Coincident(g21,g22)
    c: Coincident(g22,g23)
    c: Coincident(g23,g24)
    c: Coincident(g24,g25)
    c: Coincident(g25,g26)
    c: Coincident(g26,g21)
    c: Equal(g21, g22-g26) x5
    c: PointOnObject(g21,g27)
    c: PointOnObject(g22,g27)
    c: PointOnObject(g23,g27)
    c: PointOnObject(g24,g27)
    c: PointOnObject(g25,g27)
    c: PointOnObject(g26,g27)
    c: Diameter(g27) = 7
    c: DistanceY(g-1,g27) = 7
    c: DistanceX(g21,g-1) = 1
    c: Vertical(g21)
    c: Coincident(g28,g29)
    c: Coincident(g29,g30)
    c: Coincident(g30,g31)
    c: Coincident(g31,g32)
    c: Coincident(g32,g33)
    c: Coincident(g33,g28)
    c: Equal(g28, g29-g33) x5
    c: PointOnObject(g28,g34)
    c: PointOnObject(g29,g34)
    c: PointOnObject(g30,g34)
    c: PointOnObject(g31,g34)
    c: PointOnObject(g32,g34)
    c: PointOnObject(g33,g34)
    c: PointOnObject(g34,g-1)
    c: Diameter(g34) = 7
    c: Vertical(g31)
    c: DistanceX(g34,g-1) = 8
    c: Coincident(g35,g36)
    c: Coincident(g36,g37)
    c: Coincident(g37,g38)
    c: Coincident(g38,g39)
    c: Coincident(g39,g40)
    c: Coincident(g40,g35)
    c: Equal(g35, g36-g40) x5
    c: PointOnObject(g35,g41)
    c: PointOnObject(g36,g41)
    c: PointOnObject(g37,g41)
    c: PointOnObject(g38,g41)
    c: PointOnObject(g39,g41)
    c: PointOnObject(g40,g41)
    c: Coincident(g42,g43)
    c: Coincident(g43,g44)
    c: Coincident(g44,g45)
    c: Coincident(g45,g46)
    c: Coincident(g46,g47)
    c: Coincident(g47,g42)
    c: Equal(g42, g43-g47) x5
    c: PointOnObject(g42,g48)
    c: PointOnObject(g43,g48)
    c: PointOnObject(g44,g48)
    c: PointOnObject(g45,g48)
    c: PointOnObject(g46,g48)
    c: PointOnObject(g47,g48)
    c: Equal(g41,g48)
    c: Diameter(g41) = 7
    c: Vertical(g39)
    c: Vertical(g43)
    c: Distance(g-2,g39) = 1
    c: Symmetric(g38,g43,g-2)
    c: Distance(g41,g-1) = 7
FEATURE [Part::Extrusion] Extrude541  label="hex156"
  Base = -> Sketch549
  Dir = (0,-1,2e-16)
  DirMode = 2
  FaceMakerClass = Part::FaceMakerBullseye
  FaceMakerMode = 3
  LengthFwd = 10
  LengthRev = 0
  Placement = pos=(56,0,84) rot=(0,0,1;0rad)
  Solid = true
  Symmetric = false
FEATURE [Sketcher::SketchObject] Sketch550
  ArcFitTolerance = 1e-06
  FullyConstrained = true
  MakeInternals = false
  Placement = pos=(0,0,0) rot=(1,0,0;1.5708rad)
  sketch-geometry (49):
    g0: LineSegment StartX=1e-16 StartY=3.5 StartZ=0 EndX=-3.03109 EndY=1.75 EndZ=0
    g1: LineSegment StartX=-3.03109 StartY=1.75 StartZ=0 EndX=-3.03109 EndY=-1.75 EndZ=0
    g2: LineSegment StartX=-3.03109 StartY=-1.75 StartZ=0 EndX=-1e-16 EndY=-3.5 EndZ=0
    g3: LineSegment StartX=-1e-16 StartY=-3.5 StartZ=0 EndX=3.03109 EndY=-1.75 EndZ=0
    g4: LineSegment StartX=3.03109 StartY=-1.75 StartZ=0 EndX=3.03109 EndY=1.75 EndZ=0
    g5: LineSegment StartX=3.03109 StartY=1.75 StartZ=0 EndX=1e-16 EndY=3.5 EndZ=0
    g6: Circle [constr] CenterX=0 CenterY=0 CenterZ=0 NormalX=0 NormalY=0 NormalZ=1 AngleXU=0 Radius=3.5
    g7: LineSegment StartX=4.96892 StartY=-1.75002 StartZ=0 EndX=8.00002 EndY=-3.5 EndZ=0
    g8: LineSegment StartX=8.00002 StartY=-3.5 StartZ=0 EndX=11.0311 EndY=-1.74998 EndZ=0
    g9: LineSegment StartX=11.0311 StartY=-1.74998 StartZ=0 EndX=11.0311 EndY=1.75002 EndZ=0
    g10: LineSegment StartX=11.0311 StartY=1.75002 StartZ=0 EndX=7.99998 EndY=3.5 EndZ=0
    g11: LineSegment StartX=7.99998 StartY=3.5 StartZ=0 EndX=4.9689 EndY=1.74998 EndZ=0
    g12: LineSegment StartX=4.9689 StartY=1.74998 StartZ=0 EndX=4.96892 EndY=-1.75002 EndZ=0
    g13: Circle [constr] CenterX=8 CenterY=0 CenterZ=0 NormalX=0 NormalY=0 NormalZ=1 AngleXU=0 Radius=3.5
    g14: LineSegment StartX=4.03109 StartY=3.5 StartZ=0 EndX=7.06218 EndY=5.25 EndZ=0
    g15: LineSegment StartX=7.06218 StartY=5.25 StartZ=0 EndX=7.06218 EndY=8.75 EndZ=0
    g16: LineSegment StartX=7.06218 StartY=8.75 StartZ=0 EndX=4.03109 EndY=10.5 EndZ=0
    g17: LineSegment StartX=4.03109 StartY=10.5 StartZ=0 EndX=1 EndY=8.75 EndZ=0
    g18: LineSegment StartX=1 StartY=8.75 StartZ=0 EndX=1 EndY=5.25 EndZ=0
    g19: LineSegment StartX=1 StartY=5.25 StartZ=0 EndX=4.03109 EndY=3.5 EndZ=0
    g20: Circle [constr] CenterX=4.03109 CenterY=7 CenterZ=0 NormalX=0 NormalY=0 NormalZ=1 AngleXU=0 Radius=3.5
    g21: LineSegment StartX=-1 StartY=5.25 StartZ=0 EndX=-1 EndY=8.75 EndZ=0
    g22: LineSegment StartX=-1 StartY=8.75 StartZ=0 EndX=-4.03109 EndY=10.5 EndZ=0
    g23: LineSegment StartX=-4.03109 StartY=10.5 StartZ=0 EndX=-7.06218 EndY=8.75 EndZ=0
    g24: LineSegment StartX=-7.06218 StartY=8.75 StartZ=0 EndX=-7.06218 EndY=5.25 EndZ=0
    g25: LineSegment StartX=-7.06218 StartY=5.25 StartZ=0 EndX=-4.03109 EndY=3.5 EndZ=0
    g26: LineSegment StartX=-4.03109 StartY=3.5 StartZ=0 EndX=-1 EndY=5.25 EndZ=0
    g27: Circle [constr] CenterX=-4.03109 CenterY=7 CenterZ=0 NormalX=0 NormalY=0 NormalZ=1 AngleXU=0 Radius=3.5
    g28: LineSegment StartX=-4.96891 StartY=-1.75 StartZ=0 EndX=-4.96891 EndY=1.75 EndZ=0
    g29: LineSegment StartX=-4.96891 StartY=1.75 StartZ=0 EndX=-8 EndY=3.5 EndZ=0
    g30: LineSegment StartX=-8 StartY=3.5 StartZ=0 EndX=-11.0311 EndY=1.75 EndZ=0
    g31: LineSegment StartX=-11.0311 StartY=1.75 StartZ=0 EndX=-11.0311 EndY=-1.75 EndZ=0
    g32: LineSegment StartX=-11.0311 StartY=-1.75 StartZ=0 EndX=-8 EndY=-3.5 EndZ=0
    g33: LineSegment StartX=-8 StartY=-3.5 StartZ=0 EndX=-4.96891 EndY=-1.75 EndZ=0
    g34: Circle [constr] CenterX=-8 CenterY=0 CenterZ=0 NormalX=0 NormalY=0 NormalZ=1 AngleXU=0 Radius=3.5
    g35: LineSegment StartX=-4.03109 StartY=-3.5 StartZ=0 EndX=-7.06218 EndY=-5.25 EndZ=0
    g36: LineSegment StartX=-7.06218 StartY=-5.25 StartZ=0 EndX=-7.06218 EndY=-8.75 EndZ=0
    g37: LineSegment StartX=-7.06218 StartY=-8.75 StartZ=0 EndX=-4.03109 EndY=-10.5 EndZ=0
    g38: LineSegment StartX=-4.03109 StartY=-10.5 StartZ=0 EndX=-1 EndY=-8.75 EndZ=0
    g39: LineSegment StartX=-1 StartY=-8.75 StartZ=0 EndX=-1 EndY=-5.25 EndZ=0
    g40: LineSegment StartX=-1 StartY=-5.25 StartZ=0 EndX=-4.03109 EndY=-3.5 EndZ=0
    g41: Circle [constr] CenterX=-4.03109 CenterY=-7 CenterZ=0 NormalX=0 NormalY=0 NormalZ=1 AngleXU=0 Radius=3.5
    g42: LineSegment StartX=4.03109 StartY=-3.5 StartZ=0 EndX=1 EndY=-5.25 EndZ=0
    g43: LineSegment StartX=1 StartY=-5.25 StartZ=0 EndX=1 EndY=-8.75 EndZ=0
    g44: LineSegment StartX=1 StartY=-8.75 StartZ=0 EndX=4.03109 EndY=-10.5 EndZ=0
    g45: LineSegment StartX=4.03109 StartY=-10.5 StartZ=0 EndX=7.06218 EndY=-8.75 EndZ=0
    g46: LineSegment StartX=7.06218 StartY=-8.75 StartZ=0 EndX=7.06218 EndY=-5.25 EndZ=0
    g47: LineSegment StartX=7.06218 StartY=-5.25 StartZ=0 EndX=4.03109 EndY=-3.5 EndZ=0
    g48: Circle [constr] CenterX=4.03109 CenterY=-7 CenterZ=0 NormalX=0 NormalY=0 NormalZ=1 AngleXU=0 Radius=3.5
  constraints (117):
    c: Coincident(g0,g1)
    c: Coincident(g1,g2)
    c: Coincident(g2,g3)
    c: Coincident(g3,g4)
    c: Coincident(g4,g5)
    c: Coincident(g5,g0)
    c: Equal(g0, g1-g5) x5
    c: PointOnObject(g0,g6)
    c: PointOnObject(g1,g6)
    c: PointOnObject(g2,g6)
    c: PointOnObject(g3,g6)
    c: PointOnObject(g4,g6)
    c: PointOnObject(g5,g6)
    c: Coincident(g6,g-1)
    c: Diameter(g6) = 7
    c: PointOnObject(g0,g-2)
    c: Coincident(g7,g8)
    c: Coincident(g8,g9)
    c: Coincident(g9,g10)
    c: Coincident(g10,g11)
    c: Coincident(g11,g12)
    c: Coincident(g12,g7)
    c: Equal(g7, g8-g12) x5
    c: PointOnObject(g7,g13)
    c: PointOnObject(g8,g13)
    c: PointOnObject(g9,g13)
    c: PointOnObject(g10,g13)
    c: PointOnObject(g11,g13)
    c: PointOnObject(g12,g13)
    c: PointOnObject(g13,g-1)
    c: Diameter(g13) = 7
    c: Distance(g6,g13) = 8
    c: Horizontal(g0,g10)
    c: Coincident(g14,g15)
    c: Coincident(g15,g16)
    c: Coincident(g16,g17)
    c: Coincident(g17,g18)
    c: Coincident(g18,g19)
    c: Coincident(g19,g14)
    c: Equal(g14, g15-g19) x5
    c: PointOnObject(g14,g20)
    c: PointOnObject(g15,g20)
    c: PointOnObject(g16,g20)
    c: PointOnObject(g17,g20)
    c: PointOnObject(g18,g20)
    c: PointOnObject(g19,g20)
    c: Diameter(g20) = 7
    c: DistanceY(g-1,g20) = 7
    c: Vertical(g18)
    c: Distance(g17,g-2) = 1
    c: Coincident(g21,g22)
    c: Coincident(g22,g23)
    c: Coincident(g23,g24)
    c: Coincident(g24,g25)
    c: Coincident(g25,g26)
    c: Coincident(g26,g21)
    c: Equal(g21, g22-g26) x5
    c: PointOnObject(g21,g27)
    c: PointOnObject(g22,g27)
    c: PointOnObject(g23,g27)
    c: PointOnObject(g24,g27)
    c: PointOnObject(g25,g27)
    c: PointOnObject(g26,g27)
    c: Diameter(g27) = 7
    c: DistanceY(g-1,g27) = 7
    c: DistanceX(g21,g-1) = 1
    c: Vertical(g21)
    c: Coincident(g28,g29)
    c: Coincident(g29,g30)
    c: Coincident(g30,g31)
    c: Coincident(g31,g32)
    c: Coincident(g32,g33)
    c: Coincident(g33,g28)
    c: Equal(g28, g29-g33) x5
    c: PointOnObject(g28,g34)
    c: PointOnObject(g29,g34)
    c: PointOnObject(g30,g34)
    c: PointOnObject(g31,g34)
    c: PointOnObject(g32,g34)
    c: PointOnObject(g33,g34)
    c: PointOnObject(g34,g-1)
    c: Diameter(g34) = 7
    c: Vertical(g31)
    c: DistanceX(g34,g-1) = 8
    c: Coincident(g35,g36)
    c: Coincident(g36,g37)
    c: Coincident(g37,g38)
    c: Coincident(g38,g39)
    c: Coincident(g39,g40)
    c: Coincident(g40,g35)
    c: Equal(g35, g36-g40) x5
    c: PointOnObject(g35,g41)
    c: PointOnObject(g36,g41)
    c: PointOnObject(g37,g41)
    c: PointOnObject(g38,g41)
    c: PointOnObject(g39,g41)
    c: PointOnObject(g40,g41)
    c: Coincident(g42,g43)
    c: Coincident(g43,g44)
    c: Coincident(g44,g45)
    c: Coincident(g45,g46)
    c: Coincident(g46,g47)
    c: Coincident(g47,g42)
    c: Equal(g42, g43-g47) x5
    c: PointOnObject(g42,g48)
    c: PointOnObject(g43,g48)
    c: PointOnObject(g44,g48)
    c: PointOnObject(g45,g48)
    c: PointOnObject(g46,g48)
    c: PointOnObject(g47,g48)
    c: Equal(g41,g48)
    c: Diameter(g41) = 7
    c: Vertical(g39)
    c: Vertical(g43)
    c: Distance(g-2,g39) = 1
    c: Symmetric(g38,g43,g-2)
    c: Distance(g41,g-1) = 7
FEATURE [Part::Extrusion] Extrude542  label="hex157"
  Base = -> Sketch550
  Dir = (0,-1,2e-16)
  DirMode = 2
  FaceMakerClass = Part::FaceMakerBullseye
  FaceMakerMode = 3
  LengthFwd = 10
  LengthRev = 0
  Placement = pos=(40,0,98) rot=(0,0,1;0rad)
  Solid = true
  Symmetric = false
FEATURE [Sketcher::SketchObject] Sketch551
  ArcFitTolerance = 1e-06
  FullyConstrained = true
  MakeInternals = false
  Placement = pos=(0,0,0) rot=(1,0,0;1.5708rad)
  sketch-geometry (49):
    g0: LineSegment StartX=1e-16 StartY=3.5 StartZ=0 EndX=-3.03109 EndY=1.75 EndZ=0
    g1: LineSegment StartX=-3.03109 StartY=1.75 StartZ=0 EndX=-3.03109 EndY=-1.75 EndZ=0
    g2: LineSegment StartX=-3.03109 StartY=-1.75 StartZ=0 EndX=-1e-16 EndY=-3.5 EndZ=0
    g3: LineSegment StartX=-1e-16 StartY=-3.5 StartZ=0 EndX=3.03109 EndY=-1.75 EndZ=0
    g4: LineSegment StartX=3.03109 StartY=-1.75 StartZ=0 EndX=3.03109 EndY=1.75 EndZ=0
    g5: LineSegment StartX=3.03109 StartY=1.75 StartZ=0 EndX=1e-16 EndY=3.5 EndZ=0
    g6: Circle [constr] CenterX=0 CenterY=0 CenterZ=0 NormalX=0 NormalY=0 NormalZ=1 AngleXU=0 Radius=3.5
    g7: LineSegment StartX=4.96892 StartY=-1.75002 StartZ=0 EndX=8.00002 EndY=-3.5 EndZ=0
    g8: LineSegment StartX=8.00002 StartY=-3.5 StartZ=0 EndX=11.0311 EndY=-1.74998 EndZ=0
    g9: LineSegment StartX=11.0311 StartY=-1.74998 StartZ=0 EndX=11.0311 EndY=1.75002 EndZ=0
    g10: LineSegment StartX=11.0311 StartY=1.75002 StartZ=0 EndX=7.99998 EndY=3.5 EndZ=0
    g11: LineSegment StartX=7.99998 StartY=3.5 StartZ=0 EndX=4.9689 EndY=1.74998 EndZ=0
    g12: LineSegment StartX=4.9689 StartY=1.74998 StartZ=0 EndX=4.96892 EndY=-1.75002 EndZ=0
    g13: Circle [constr] CenterX=8 CenterY=0 CenterZ=0 NormalX=0 NormalY=0 NormalZ=1 AngleXU=0 Radius=3.5
    g14: LineSegment StartX=4.03109 StartY=3.5 StartZ=0 EndX=7.06218 EndY=5.25 EndZ=0
    g15: LineSegment StartX=7.06218 StartY=5.25 StartZ=0 EndX=7.06218 EndY=8.75 EndZ=0
    g16: LineSegment StartX=7.06218 StartY=8.75 StartZ=0 EndX=4.03109 EndY=10.5 EndZ=0
    g17: LineSegment StartX=4.03109 StartY=10.5 StartZ=0 EndX=1 EndY=8.75 EndZ=0
    g18: LineSegment StartX=1 StartY=8.75 StartZ=0 EndX=1 EndY=5.25 EndZ=0
    g19: LineSegment StartX=1 StartY=5.25 StartZ=0 EndX=4.03109 EndY=3.5 EndZ=0
    g20: Circle [constr] CenterX=4.03109 CenterY=7 CenterZ=0 NormalX=0 NormalY=0 NormalZ=1 AngleXU=0 Radius=3.5
    g21: LineSegment StartX=-1 StartY=5.25 StartZ=0 EndX=-1 EndY=8.75 EndZ=0
    g22: LineSegment StartX=-1 StartY=8.75 StartZ=0 EndX=-4.03109 EndY=10.5 EndZ=0
    g23: LineSegment StartX=-4.03109 StartY=10.5 StartZ=0 EndX=-7.06218 EndY=8.75 EndZ=0
    g24: LineSegment StartX=-7.06218 StartY=8.75 StartZ=0 EndX=-7.06218 EndY=5.25 EndZ=0
    g25: LineSegment StartX=-7.06218 StartY=5.25 StartZ=0 EndX=-4.03109 EndY=3.5 EndZ=0
    g26: LineSegment StartX=-4.03109 StartY=3.5 StartZ=0 EndX=-1 EndY=5.25 EndZ=0
    g27: Circle [constr] CenterX=-4.03109 CenterY=7 CenterZ=0 NormalX=0 NormalY=0 NormalZ=1 AngleXU=0 Radius=3.5
    g28: LineSegment StartX=-4.96891 StartY=-1.75 StartZ=0 EndX=-4.96891 EndY=1.75 EndZ=0
    g29: LineSegment StartX=-4.96891 StartY=1.75 StartZ=0 EndX=-8 EndY=3.5 EndZ=0
    g30: LineSegment StartX=-8 StartY=3.5 StartZ=0 EndX=-11.0311 EndY=1.75 EndZ=0
    g31: LineSegment StartX=-11.0311 StartY=1.75 StartZ=0 EndX=-11.0311 EndY=-1.75 EndZ=0
    g32: LineSegment StartX=-11.0311 StartY=-1.75 StartZ=0 EndX=-8 EndY=-3.5 EndZ=0
    g33: LineSegment StartX=-8 StartY=-3.5 StartZ=0 EndX=-4.96891 EndY=-1.75 EndZ=0
    g34: Circle [constr] CenterX=-8 CenterY=0 CenterZ=0 NormalX=0 NormalY=0 NormalZ=1 AngleXU=0 Radius=3.5
    g35: LineSegment StartX=-4.03109 StartY=-3.5 StartZ=0 EndX=-7.06218 EndY=-5.25 EndZ=0
    g36: LineSegment StartX=-7.06218 StartY=-5.25 StartZ=0 EndX=-7.06218 EndY=-8.75 EndZ=0
    g37: LineSegment StartX=-7.06218 StartY=-8.75 StartZ=0 EndX=-4.03109 EndY=-10.5 EndZ=0
    g38: LineSegment StartX=-4.03109 StartY=-10.5 StartZ=0 EndX=-1 EndY=-8.75 EndZ=0
    g39: LineSegment StartX=-1 StartY=-8.75 StartZ=0 EndX=-1 EndY=-5.25 EndZ=0
    g40: LineSegment StartX=-1 StartY=-5.25 StartZ=0 EndX=-4.03109 EndY=-3.5 EndZ=0
    g41: Circle [constr] CenterX=-4.03109 CenterY=-7 CenterZ=0 NormalX=0 NormalY=0 NormalZ=1 AngleXU=0 Radius=3.5
    g42: LineSegment StartX=4.03109 StartY=-3.5 StartZ=0 EndX=1 EndY=-5.25 EndZ=0
    g43: LineSegment StartX=1 StartY=-5.25 StartZ=0 EndX=1 EndY=-8.75 EndZ=0
    g44: LineSegment StartX=1 StartY=-8.75 StartZ=0 EndX=4.03109 EndY=-10.5 EndZ=0
    g45: LineSegment StartX=4.03109 StartY=-10.5 StartZ=0 EndX=7.06218 EndY=-8.75 EndZ=0
    g46: LineSegment StartX=7.06218 StartY=-8.75 StartZ=0 EndX=7.06218 EndY=-5.25 EndZ=0
    g47: LineSegment StartX=7.06218 StartY=-5.25 StartZ=0 EndX=4.03109 EndY=-3.5 EndZ=0
    g48: Circle [constr] CenterX=4.03109 CenterY=-7 CenterZ=0 NormalX=0 NormalY=0 NormalZ=1 AngleXU=0 Radius=3.5
  constraints (117):
    c: Coincident(g0,g1)
    c: Coincident(g1,g2)
    c: Coincident(g2,g3)
    c: Coincident(g3,g4)
    c: Coincident(g4,g5)
    c: Coincident(g5,g0)
    c: Equal(g0, g1-g5) x5
    c: PointOnObject(g0,g6)
    c: PointOnObject(g1,g6)
    c: PointOnObject(g2,g6)
    c: PointOnObject(g3,g6)
    c: PointOnObject(g4,g6)
    c: PointOnObject(g5,g6)
    c: Coincident(g6,g-1)
    c: Diameter(g6) = 7
    c: PointOnObject(g0,g-2)
    c: Coincident(g7,g8)
    c: Coincident(g8,g9)
    c: Coincident(g9,g10)
    c: Coincident(g10,g11)
    c: Coincident(g11,g12)
    c: Coincident(g12,g7)
    c: Equal(g7, g8-g12) x5
    c: PointOnObject(g7,g13)
    c: PointOnObject(g8,g13)
    c: PointOnObject(g9,g13)
    c: PointOnObject(g10,g13)
    c: PointOnObject(g11,g13)
    c: PointOnObject(g12,g13)
    c: PointOnObject(g13,g-1)
    c: Diameter(g13) = 7
    c: Distance(g6,g13) = 8
    c: Horizontal(g0,g10)
    c: Coincident(g14,g15)
    c: Coincident(g15,g16)
    c: Coincident(g16,g17)
    c: Coincident(g17,g18)
    c: Coincident(g18,g19)
    c: Coincident(g19,g14)
    c: Equal(g14, g15-g19) x5
    c: PointOnObject(g14,g20)
    c: PointOnObject(g15,g20)
    c: PointOnObject(g16,g20)
    c: PointOnObject(g17,g20)
    c: PointOnObject(g18,g20)
    c: PointOnObject(g19,g20)
    c: Diameter(g20) = 7
    c: DistanceY(g-1,g20) = 7
    c: Vertical(g18)
    c: Distance(g17,g-2) = 1
    c: Coincident(g21,g22)
    c: Coincident(g22,g23)
    c: Coincident(g23,g24)
    c: Coincident(g24,g25)
    c: Coincident(g25,g26)
    c: Coincident(g26,g21)
    c: Equal(g21, g22-g26) x5
    c: PointOnObject(g21,g27)
    c: PointOnObject(g22,g27)
    c: PointOnObject(g23,g27)
    c: PointOnObject(g24,g27)
    c: PointOnObject(g25,g27)
    c: PointOnObject(g26,g27)
    c: Diameter(g27) = 7
    c: DistanceY(g-1,g27) = 7
    c: DistanceX(g21,g-1) = 1
    c: Vertical(g21)
    c: Coincident(g28,g29)
    c: Coincident(g29,g30)
    c: Coincident(g30,g31)
    c: Coincident(g31,g32)
    c: Coincident(g32,g33)
    c: Coincident(g33,g28)
    c: Equal(g28, g29-g33) x5
    c: PointOnObject(g28,g34)
    c: PointOnObject(g29,g34)
    c: PointOnObject(g30,g34)
    c: PointOnObject(g31,g34)
    c: PointOnObject(g32,g34)
    c: PointOnObject(g33,g34)
    c: PointOnObject(g34,g-1)
    c: Diameter(g34) = 7
    c: Vertical(g31)
    c: DistanceX(g34,g-1) = 8
    c: Coincident(g35,g36)
    c: Coincident(g36,g37)
    c: Coincident(g37,g38)
    c: Coincident(g38,g39)
    c: Coincident(g39,g40)
    c: Coincident(g40,g35)
    c: Equal(g35, g36-g40) x5
    c: PointOnObject(g35,g41)
    c: PointOnObject(g36,g41)
    c: PointOnObject(g37,g41)
    c: PointOnObject(g38,g41)
    c: PointOnObject(g39,g41)
    c: PointOnObject(g40,g41)
    c: Coincident(g42,g43)
    c: Coincident(g43,g44)
    c: Coincident(g44,g45)
    c: Coincident(g45,g46)
    c: Coincident(g46,g47)
    c: Coincident(g47,g42)
    c: Equal(g42, g43-g47) x5
    c: PointOnObject(g42,g48)
    c: PointOnObject(g43,g48)
    c: PointOnObject(g44,g48)
    c: PointOnObject(g45,g48)
    c: PointOnObject(g46,g48)
    c: PointOnObject(g47,g48)
    c: Equal(g41,g48)
    c: Diameter(g41) = 7
    c: Vertical(g39)
    c: Vertical(g43)
    c: Distance(g-2,g39) = 1
    c: Symmetric(g38,g43,g-2)
    c: Distance(g41,g-1) = 7
FEATURE [Part::Extrusion] Extrude543  label="hex158"
  Base = -> Sketch551
  Dir = (0,-1,2e-16)
  DirMode = 2
  FaceMakerClass = Part::FaceMakerBullseye
  FaceMakerMode = 3
  LengthFwd = 10
  LengthRev = 0
  Placement = pos=(20,0,105) rot=(0,0,1;0rad)
  Solid = true
  Symmetric = false
FEATURE [Sketcher::SketchObject] Sketch552
  ArcFitTolerance = 1e-06
  FullyConstrained = true
  MakeInternals = false
  Placement = pos=(0,0,0) rot=(1,0,0;1.5708rad)
  sketch-geometry (49):
    g0: LineSegment StartX=1e-16 StartY=3.5 StartZ=0 EndX=-3.03109 EndY=1.75 EndZ=0
    g1: LineSegment StartX=-3.03109 StartY=1.75 StartZ=0 EndX=-3.03109 EndY=-1.75 EndZ=0
    g2: LineSegment StartX=-3.03109 StartY=-1.75 StartZ=0 EndX=-1e-16 EndY=-3.5 EndZ=0
    g3: LineSegment StartX=-1e-16 StartY=-3.5 StartZ=0 EndX=3.03109 EndY=-1.75 EndZ=0
    g4: LineSegment StartX=3.03109 StartY=-1.75 StartZ=0 EndX=3.03109 EndY=1.75 EndZ=0
    g5: LineSegment StartX=3.03109 StartY=1.75 StartZ=0 EndX=1e-16 EndY=3.5 EndZ=0
    g6: Circle [constr] CenterX=0 CenterY=0 CenterZ=0 NormalX=0 NormalY=0 NormalZ=1 AngleXU=0 Radius=3.5
    g7: LineSegment StartX=4.96892 StartY=-1.75002 StartZ=0 EndX=8.00002 EndY=-3.5 EndZ=0
    g8: LineSegment StartX=8.00002 StartY=-3.5 StartZ=0 EndX=11.0311 EndY=-1.74998 EndZ=0
    g9: LineSegment StartX=11.0311 StartY=-1.74998 StartZ=0 EndX=11.0311 EndY=1.75002 EndZ=0
    g10: LineSegment StartX=11.0311 StartY=1.75002 StartZ=0 EndX=7.99998 EndY=3.5 EndZ=0
    g11: LineSegment StartX=7.99998 StartY=3.5 StartZ=0 EndX=4.9689 EndY=1.74998 EndZ=0
    g12: LineSegment StartX=4.9689 StartY=1.74998 StartZ=0 EndX=4.96892 EndY=-1.75002 EndZ=0
    g13: Circle [constr] CenterX=8 CenterY=0 CenterZ=0 NormalX=0 NormalY=0 NormalZ=1 AngleXU=0 Radius=3.5
    g14: LineSegment StartX=4.03109 StartY=3.5 StartZ=0 EndX=7.06218 EndY=5.25 EndZ=0
    g15: LineSegment StartX=7.06218 StartY=5.25 StartZ=0 EndX=7.06218 EndY=8.75 EndZ=0
    g16: LineSegment StartX=7.06218 StartY=8.75 StartZ=0 EndX=4.03109 EndY=10.5 EndZ=0
    g17: LineSegment StartX=4.03109 StartY=10.5 StartZ=0 EndX=1 EndY=8.75 EndZ=0
    g18: LineSegment StartX=1 StartY=8.75 StartZ=0 EndX=1 EndY=5.25 EndZ=0
    g19: LineSegment StartX=1 StartY=5.25 StartZ=0 EndX=4.03109 EndY=3.5 EndZ=0
    g20: Circle [constr] CenterX=4.03109 CenterY=7 CenterZ=0 NormalX=0 NormalY=0 NormalZ=1 AngleXU=0 Radius=3.5
    g21: LineSegment StartX=-1 StartY=5.25 StartZ=0 EndX=-1 EndY=8.75 EndZ=0
    g22: LineSegment StartX=-1 StartY=8.75 StartZ=0 EndX=-4.03109 EndY=10.5 EndZ=0
    g23: LineSegment StartX=-4.03109 StartY=10.5 StartZ=0 EndX=-7.06218 EndY=8.75 EndZ=0
    g24: LineSegment StartX=-7.06218 StartY=8.75 StartZ=0 EndX=-7.06218 EndY=5.25 EndZ=0
    g25: LineSegment StartX=-7.06218 StartY=5.25 StartZ=0 EndX=-4.03109 EndY=3.5 EndZ=0
    g26: LineSegment StartX=-4.03109 StartY=3.5 StartZ=0 EndX=-1 EndY=5.25 EndZ=0
    g27: Circle [constr] CenterX=-4.03109 CenterY=7 CenterZ=0 NormalX=0 NormalY=0 NormalZ=1 AngleXU=0 Radius=3.5
    g28: LineSegment StartX=-4.96891 StartY=-1.75 StartZ=0 EndX=-4.96891 EndY=1.75 EndZ=0
    g29: LineSegment StartX=-4.96891 StartY=1.75 StartZ=0 EndX=-8 EndY=3.5 EndZ=0
    g30: LineSegment StartX=-8 StartY=3.5 StartZ=0 EndX=-11.0311 EndY=1.75 EndZ=0
    g31: LineSegment StartX=-11.0311 StartY=1.75 StartZ=0 EndX=-11.0311 EndY=-1.75 EndZ=0
    g32: LineSegment StartX=-11.0311 StartY=-1.75 StartZ=0 EndX=-8 EndY=-3.5 EndZ=0
    g33: LineSegment StartX=-8 StartY=-3.5 StartZ=0 EndX=-4.96891 EndY=-1.75 EndZ=0
    g34: Circle [constr] CenterX=-8 CenterY=0 CenterZ=0 NormalX=0 NormalY=0 NormalZ=1 AngleXU=0 Radius=3.5
    g35: LineSegment StartX=-4.03109 StartY=-3.5 StartZ=0 EndX=-7.06218 EndY=-5.25 EndZ=0
    g36: LineSegment StartX=-7.06218 StartY=-5.25 StartZ=0 EndX=-7.06218 EndY=-8.75 EndZ=0
    g37: LineSegment StartX=-7.06218 StartY=-8.75 StartZ=0 EndX=-4.03109 EndY=-10.5 EndZ=0
    g38: LineSegment StartX=-4.03109 StartY=-10.5 StartZ=0 EndX=-1 EndY=-8.75 EndZ=0
    g39: LineSegment StartX=-1 StartY=-8.75 StartZ=0 EndX=-1 EndY=-5.25 EndZ=0
    g40: LineSegment StartX=-1 StartY=-5.25 StartZ=0 EndX=-4.03109 EndY=-3.5 EndZ=0
    g41: Circle [constr] CenterX=-4.03109 CenterY=-7 CenterZ=0 NormalX=0 NormalY=0 NormalZ=1 AngleXU=0 Radius=3.5
    g42: LineSegment StartX=4.03109 StartY=-3.5 StartZ=0 EndX=1 EndY=-5.25 EndZ=0
    g43: LineSegment StartX=1 StartY=-5.25 StartZ=0 EndX=1 EndY=-8.75 EndZ=0
    g44: LineSegment StartX=1 StartY=-8.75 StartZ=0 EndX=4.03109 EndY=-10.5 EndZ=0
    g45: LineSegment StartX=4.03109 StartY=-10.5 StartZ=0 EndX=7.06218 EndY=-8.75 EndZ=0
    g46: LineSegment StartX=7.06218 StartY=-8.75 StartZ=0 EndX=7.06218 EndY=-5.25 EndZ=0
    g47: LineSegment StartX=7.06218 StartY=-5.25 StartZ=0 EndX=4.03109 EndY=-3.5 EndZ=0
    g48: Circle [constr] CenterX=4.03109 CenterY=-7 CenterZ=0 NormalX=0 NormalY=0 NormalZ=1 AngleXU=0 Radius=3.5
  constraints (117):
    c: Coincident(g0,g1)
    c: Coincident(g1,g2)
    c: Coincident(g2,g3)
    c: Coincident(g3,g4)
    c: Coincident(g4,g5)
    c: Coincident(g5,g0)
    c: Equal(g0, g1-g5) x5
    c: PointOnObject(g0,g6)
    c: PointOnObject(g1,g6)
    c: PointOnObject(g2,g6)
    c: PointOnObject(g3,g6)
    c: PointOnObject(g4,g6)
    c: PointOnObject(g5,g6)
    c: Coincident(g6,g-1)
    c: Diameter(g6) = 7
    c: PointOnObject(g0,g-2)
    c: Coincident(g7,g8)
    c: Coincident(g8,g9)
    c: Coincident(g9,g10)
    c: Coincident(g10,g11)
    c: Coincident(g11,g12)
    c: Coincident(g12,g7)
    c: Equal(g7, g8-g12) x5
    c: PointOnObject(g7,g13)
    c: PointOnObject(g8,g13)
    c: PointOnObject(g9,g13)
    c: PointOnObject(g10,g13)
    c: PointOnObject(g11,g13)
    c: PointOnObject(g12,g13)
    c: PointOnObject(g13,g-1)
    c: Diameter(g13) = 7
    c: Distance(g6,g13) = 8
    c: Horizontal(g0,g10)
    c: Coincident(g14,g15)
    c: Coincident(g15,g16)
    c: Coincident(g16,g17)
    c: Coincident(g17,g18)
    c: Coincident(g18,g19)
    c: Coincident(g19,g14)
    c: Equal(g14, g15-g19) x5
    c: PointOnObject(g14,g20)
    c: PointOnObject(g15,g20)
    c: PointOnObject(g16,g20)
    c: PointOnObject(g17,g20)
    c: PointOnObject(g18,g20)
    c: PointOnObject(g19,g20)
    c: Diameter(g20) = 7
    c: DistanceY(g-1,g20) = 7
    c: Vertical(g18)
    c: Distance(g17,g-2) = 1
    c: Coincident(g21,g22)
    c: Coincident(g22,g23)
    c: Coincident(g23,g24)
    c: Coincident(g24,g25)
    c: Coincident(g25,g26)
    c: Coincident(g26,g21)
    c: Equal(g21, g22-g26) x5
    c: PointOnObject(g21,g27)
    c: PointOnObject(g22,g27)
    c: PointOnObject(g23,g27)
    c: PointOnObject(g24,g27)
    c: PointOnObject(g25,g27)
    c: PointOnObject(g26,g27)
    c: Diameter(g27) = 7
    c: DistanceY(g-1,g27) = 7
    c: DistanceX(g21,g-1) = 1
    c: Vertical(g21)
    c: Coincident(g28,g29)
    c: Coincident(g29,g30)
    c: Coincident(g30,g31)
    c: Coincident(g31,g32)
    c: Coincident(g32,g33)
    c: Coincident(g33,g28)
    c: Equal(g28, g29-g33) x5
    c: PointOnObject(g28,g34)
    c: PointOnObject(g29,g34)
    c: PointOnObject(g30,g34)
    c: PointOnObject(g31,g34)
    c: PointOnObject(g32,g34)
    c: PointOnObject(g33,g34)
    c: PointOnObject(g34,g-1)
    c: Diameter(g34) = 7
    c: Vertical(g31)
    c: DistanceX(g34,g-1) = 8
    c: Coincident(g35,g36)
    c: Coincident(g36,g37)
    c: Coincident(g37,g38)
    c: Coincident(g38,g39)
    c: Coincident(g39,g40)
    c: Coincident(g40,g35)
    c: Equal(g35, g36-g40) x5
    c: PointOnObject(g35,g41)
    c: PointOnObject(g36,g41)
    c: PointOnObject(g37,g41)
    c: PointOnObject(g38,g41)
    c: PointOnObject(g39,g41)
    c: PointOnObject(g40,g41)
    c: Coincident(g42,g43)
    c: Coincident(g43,g44)
    c: Coincident(g44,g45)
    c: Coincident(g45,g46)
    c: Coincident(g46,g47)
    c: Coincident(g47,g42)
    c: Equal(g42, g43-g47) x5
    c: PointOnObject(g42,g48)
    c: PointOnObject(g43,g48)
    c: PointOnObject(g44,g48)
    c: PointOnObject(g45,g48)
    c: PointOnObject(g46,g48)
    c: PointOnObject(g47,g48)
    c: Equal(g41,g48)
    c: Diameter(g41) = 7
    c: Vertical(g39)
    c: Vertical(g43)
    c: Distance(g-2,g39) = 1
    c: Symmetric(g38,g43,g-2)
    c: Distance(g41,g-1) = 7
FEATURE [Part::Extrusion] Extrude544  label="hex159"
  Base = -> Sketch552
  Dir = (0,-1,2e-16)
  DirMode = 2
  FaceMakerClass = Part::FaceMakerBullseye
  FaceMakerMode = 3
  LengthFwd = 10
  LengthRev = 0
  Placement = pos=(4,0,119) rot=(0,0,1;0rad)
  Solid = true
  Symmetric = false
FEATURE [Sketcher::SketchObject] Sketch553
  ArcFitTolerance = 1e-06
  FullyConstrained = true
  MakeInternals = false
  Placement = pos=(0,0,0) rot=(1,0,0;1.5708rad)
  sketch-geometry (49):
    g0: LineSegment StartX=1e-16 StartY=3.5 StartZ=0 EndX=-3.03109 EndY=1.75 EndZ=0
    g1: LineSegment StartX=-3.03109 StartY=1.75 StartZ=0 EndX=-3.03109 EndY=-1.75 EndZ=0
    g2: LineSegment StartX=-3.03109 StartY=-1.75 StartZ=0 EndX=-1e-16 EndY=-3.5 EndZ=0
    g3: LineSegment StartX=-1e-16 StartY=-3.5 StartZ=0 EndX=3.03109 EndY=-1.75 EndZ=0
    g4: LineSegment StartX=3.03109 StartY=-1.75 StartZ=0 EndX=3.03109 EndY=1.75 EndZ=0
    g5: LineSegment StartX=3.03109 StartY=1.75 StartZ=0 EndX=1e-16 EndY=3.5 EndZ=0
    g6: Circle [constr] CenterX=0 CenterY=0 CenterZ=0 NormalX=0 NormalY=0 NormalZ=1 AngleXU=0 Radius=3.5
    g7: LineSegment StartX=4.96892 StartY=-1.75002 StartZ=0 EndX=8.00002 EndY=-3.5 EndZ=0
    g8: LineSegment StartX=8.00002 StartY=-3.5 StartZ=0 EndX=11.0311 EndY=-1.74998 EndZ=0
    g9: LineSegment StartX=11.0311 StartY=-1.74998 StartZ=0 EndX=11.0311 EndY=1.75002 EndZ=0
    g10: LineSegment StartX=11.0311 StartY=1.75002 StartZ=0 EndX=7.99998 EndY=3.5 EndZ=0
    g11: LineSegment StartX=7.99998 StartY=3.5 StartZ=0 EndX=4.9689 EndY=1.74998 EndZ=0
    g12: LineSegment StartX=4.9689 StartY=1.74998 StartZ=0 EndX=4.96892 EndY=-1.75002 EndZ=0
    g13: Circle [constr] CenterX=8 CenterY=0 CenterZ=0 NormalX=0 NormalY=0 NormalZ=1 AngleXU=0 Radius=3.5
    g14: LineSegment StartX=4.03109 StartY=3.5 StartZ=0 EndX=7.06218 EndY=5.25 EndZ=0
    g15: LineSegment StartX=7.06218 StartY=5.25 StartZ=0 EndX=7.06218 EndY=8.75 EndZ=0
    g16: LineSegment StartX=7.06218 StartY=8.75 StartZ=0 EndX=4.03109 EndY=10.5 EndZ=0
    g17: LineSegment StartX=4.03109 StartY=10.5 StartZ=0 EndX=1 EndY=8.75 EndZ=0
    g18: LineSegment StartX=1 StartY=8.75 StartZ=0 EndX=1 EndY=5.25 EndZ=0
    g19: LineSegment StartX=1 StartY=5.25 StartZ=0 EndX=4.03109 EndY=3.5 EndZ=0
    g20: Circle [constr] CenterX=4.03109 CenterY=7 CenterZ=0 NormalX=0 NormalY=0 NormalZ=1 AngleXU=0 Radius=3.5
    g21: LineSegment StartX=-1 StartY=5.25 StartZ=0 EndX=-1 EndY=8.75 EndZ=0
    g22: LineSegment StartX=-1 StartY=8.75 StartZ=0 EndX=-4.03109 EndY=10.5 EndZ=0
    g23: LineSegment StartX=-4.03109 StartY=10.5 StartZ=0 EndX=-7.06218 EndY=8.75 EndZ=0
    g24: LineSegment StartX=-7.06218 StartY=8.75 StartZ=0 EndX=-7.06218 EndY=5.25 EndZ=0
    g25: LineSegment StartX=-7.06218 StartY=5.25 StartZ=0 EndX=-4.03109 EndY=3.5 EndZ=0
    g26: LineSegment StartX=-4.03109 StartY=3.5 StartZ=0 EndX=-1 EndY=5.25 EndZ=0
    g27: Circle [constr] CenterX=-4.03109 CenterY=7 CenterZ=0 NormalX=0 NormalY=0 NormalZ=1 AngleXU=0 Radius=3.5
    g28: LineSegment StartX=-4.96891 StartY=-1.75 StartZ=0 EndX=-4.96891 EndY=1.75 EndZ=0
    g29: LineSegment StartX=-4.96891 StartY=1.75 StartZ=0 EndX=-8 EndY=3.5 EndZ=0
    g30: LineSegment StartX=-8 StartY=3.5 StartZ=0 EndX=-11.0311 EndY=1.75 EndZ=0
    g31: LineSegment StartX=-11.0311 StartY=1.75 StartZ=0 EndX=-11.0311 EndY=-1.75 EndZ=0
    g32: LineSegment StartX=-11.0311 StartY=-1.75 StartZ=0 EndX=-8 EndY=-3.5 EndZ=0
    g33: LineSegment StartX=-8 StartY=-3.5 StartZ=0 EndX=-4.96891 EndY=-1.75 EndZ=0
    g34: Circle [constr] CenterX=-8 CenterY=0 CenterZ=0 NormalX=0 NormalY=0 NormalZ=1 AngleXU=0 Radius=3.5
    g35: LineSegment StartX=-4.03109 StartY=-3.5 StartZ=0 EndX=-7.06218 EndY=-5.25 EndZ=0
    g36: LineSegment StartX=-7.06218 StartY=-5.25 StartZ=0 EndX=-7.06218 EndY=-8.75 EndZ=0
    g37: LineSegment StartX=-7.06218 StartY=-8.75 StartZ=0 EndX=-4.03109 EndY=-10.5 EndZ=0
    g38: LineSegment StartX=-4.03109 StartY=-10.5 StartZ=0 EndX=-1 EndY=-8.75 EndZ=0
    g39: LineSegment StartX=-1 StartY=-8.75 StartZ=0 EndX=-1 EndY=-5.25 EndZ=0
    g40: LineSegment StartX=-1 StartY=-5.25 StartZ=0 EndX=-4.03109 EndY=-3.5 EndZ=0
    g41: Circle [constr] CenterX=-4.03109 CenterY=-7 CenterZ=0 NormalX=0 NormalY=0 NormalZ=1 AngleXU=0 Radius=3.5
    g42: LineSegment StartX=4.03109 StartY=-3.5 StartZ=0 EndX=1 EndY=-5.25 EndZ=0
    g43: LineSegment StartX=1 StartY=-5.25 StartZ=0 EndX=1 EndY=-8.75 EndZ=0
    g44: LineSegment StartX=1 StartY=-8.75 StartZ=0 EndX=4.03109 EndY=-10.5 EndZ=0
    g45: LineSegment StartX=4.03109 StartY=-10.5 StartZ=0 EndX=7.06218 EndY=-8.75 EndZ=0
    g46: LineSegment StartX=7.06218 StartY=-8.75 StartZ=0 EndX=7.06218 EndY=-5.25 EndZ=0
    g47: LineSegment StartX=7.06218 StartY=-5.25 StartZ=0 EndX=4.03109 EndY=-3.5 EndZ=0
    g48: Circle [constr] CenterX=4.03109 CenterY=-7 CenterZ=0 NormalX=0 NormalY=0 NormalZ=1 AngleXU=0 Radius=3.5
  constraints (117):
    c: Coincident(g0,g1)
    c: Coincident(g1,g2)
    c: Coincident(g2,g3)
    c: Coincident(g3,g4)
    c: Coincident(g4,g5)
    c: Coincident(g5,g0)
    c: Equal(g0, g1-g5) x5
    c: PointOnObject(g0,g6)
    c: PointOnObject(g1,g6)
    c: PointOnObject(g2,g6)
    c: PointOnObject(g3,g6)
    c: PointOnObject(g4,g6)
    c: PointOnObject(g5,g6)
    c: Coincident(g6,g-1)
    c: Diameter(g6) = 7
    c: PointOnObject(g0,g-2)
    c: Coincident(g7,g8)
    c: Coincident(g8,g9)
    c: Coincident(g9,g10)
    c: Coincident(g10,g11)
    c: Coincident(g11,g12)
    c: Coincident(g12,g7)
    c: Equal(g7, g8-g12) x5
    c: PointOnObject(g7,g13)
    c: PointOnObject(g8,g13)
    c: PointOnObject(g9,g13)
    c: PointOnObject(g10,g13)
    c: PointOnObject(g11,g13)
    c: PointOnObject(g12,g13)
    c: PointOnObject(g13,g-1)
    c: Diameter(g13) = 7
    c: Distance(g6,g13) = 8
    c: Horizontal(g0,g10)
    c: Coincident(g14,g15)
    c: Coincident(g15,g16)
    c: Coincident(g16,g17)
    c: Coincident(g17,g18)
    c: Coincident(g18,g19)
    c: Coincident(g19,g14)
    c: Equal(g14, g15-g19) x5
    c: PointOnObject(g14,g20)
    c: PointOnObject(g15,g20)
    c: PointOnObject(g16,g20)
    c: PointOnObject(g17,g20)
    c: PointOnObject(g18,g20)
    c: PointOnObject(g19,g20)
    c: Diameter(g20) = 7
    c: DistanceY(g-1,g20) = 7
    c: Vertical(g18)
    c: Distance(g17,g-2) = 1
    c: Coincident(g21,g22)
    c: Coincident(g22,g23)
    c: Coincident(g23,g24)
    c: Coincident(g24,g25)
    c: Coincident(g25,g26)
    c: Coincident(g26,g21)
    c: Equal(g21, g22-g26) x5
    c: PointOnObject(g21,g27)
    c: PointOnObject(g22,g27)
    c: PointOnObject(g23,g27)
    c: PointOnObject(g24,g27)
    c: PointOnObject(g25,g27)
    c: PointOnObject(g26,g27)
    c: Diameter(g27) = 7
    c: DistanceY(g-1,g27) = 7
    c: DistanceX(g21,g-1) = 1
    c: Vertical(g21)
    c: Coincident(g28,g29)
    c: Coincident(g29,g30)
    c: Coincident(g30,g31)
    c: Coincident(g31,g32)
    c: Coincident(g32,g33)
    c: Coincident(g33,g28)
    c: Equal(g28, g29-g33) x5
    c: PointOnObject(g28,g34)
    c: PointOnObject(g29,g34)
    c: PointOnObject(g30,g34)
    c: PointOnObject(g31,g34)
    c: PointOnObject(g32,g34)
    c: PointOnObject(g33,g34)
    c: PointOnObject(g34,g-1)
    c: Diameter(g34) = 7
    c: Vertical(g31)
    c: DistanceX(g34,g-1) = 8
    c: Coincident(g35,g36)
    c: Coincident(g36,g37)
    c: Coincident(g37,g38)
    c: Coincident(g38,g39)
    c: Coincident(g39,g40)
    c: Coincident(g40,g35)
    c: Equal(g35, g36-g40) x5
    c: PointOnObject(g35,g41)
    c: PointOnObject(g36,g41)
    c: PointOnObject(g37,g41)
    c: PointOnObject(g38,g41)
    c: PointOnObject(g39,g41)
    c: PointOnObject(g40,g41)
    c: Coincident(g42,g43)
    c: Coincident(g43,g44)
    c: Coincident(g44,g45)
    c: Coincident(g45,g46)
    c: Coincident(g46,g47)
    c: Coincident(g47,g42)
    c: Equal(g42, g43-g47) x5
    c: PointOnObject(g42,g48)
    c: PointOnObject(g43,g48)
    c: PointOnObject(g44,g48)
    c: PointOnObject(g45,g48)
    c: PointOnObject(g46,g48)
    c: PointOnObject(g47,g48)
    c: Equal(g41,g48)
    c: Diameter(g41) = 7
    c: Vertical(g39)
    c: Vertical(g43)
    c: Distance(g-2,g39) = 1
    c: Symmetric(g38,g43,g-2)
    c: Distance(g41,g-1) = 7
FEATURE [Part::Extrusion] Extrude545  label="hex160"
  Base = -> Sketch553
  Dir = (0,-1,2e-16)
  DirMode = 2
  FaceMakerClass = Part::FaceMakerBullseye
  FaceMakerMode = 3
  LengthFwd = 10
  LengthRev = 0
  Placement = pos=(-4,0,105) rot=(0,0,1;0rad)
  Solid = true
  Symmetric = false
FEATURE [Sketcher::SketchObject] Sketch554
  ArcFitTolerance = 1e-06
  FullyConstrained = true
  MakeInternals = false
  Placement = pos=(0,0,0) rot=(1,0,0;1.5708rad)
  sketch-geometry (49):
    g0: LineSegment StartX=1e-16 StartY=3.5 StartZ=0 EndX=-3.03109 EndY=1.75 EndZ=0
    g1: LineSegment StartX=-3.03109 StartY=1.75 StartZ=0 EndX=-3.03109 EndY=-1.75 EndZ=0
    g2: LineSegment StartX=-3.03109 StartY=-1.75 StartZ=0 EndX=-1e-16 EndY=-3.5 EndZ=0
    g3: LineSegment StartX=-1e-16 StartY=-3.5 StartZ=0 EndX=3.03109 EndY=-1.75 EndZ=0
    g4: LineSegment StartX=3.03109 StartY=-1.75 StartZ=0 EndX=3.03109 EndY=1.75 EndZ=0
    g5: LineSegment StartX=3.03109 StartY=1.75 StartZ=0 EndX=1e-16 EndY=3.5 EndZ=0
    g6: Circle [constr] CenterX=0 CenterY=0 CenterZ=0 NormalX=0 NormalY=0 NormalZ=1 AngleXU=0 Radius=3.5
    g7: LineSegment StartX=4.96892 StartY=-1.75002 StartZ=0 EndX=8.00002 EndY=-3.5 EndZ=0
    g8: LineSegment StartX=8.00002 StartY=-3.5 StartZ=0 EndX=11.0311 EndY=-1.74998 EndZ=0
    g9: LineSegment StartX=11.0311 StartY=-1.74998 StartZ=0 EndX=11.0311 EndY=1.75002 EndZ=0
    g10: LineSegment StartX=11.0311 StartY=1.75002 StartZ=0 EndX=7.99998 EndY=3.5 EndZ=0
    g11: LineSegment StartX=7.99998 StartY=3.5 StartZ=0 EndX=4.9689 EndY=1.74998 EndZ=0
    g12: LineSegment StartX=4.9689 StartY=1.74998 StartZ=0 EndX=4.96892 EndY=-1.75002 EndZ=0
    g13: Circle [constr] CenterX=8 CenterY=0 CenterZ=0 NormalX=0 NormalY=0 NormalZ=1 AngleXU=0 Radius=3.5
    g14: LineSegment StartX=4.03109 StartY=3.5 StartZ=0 EndX=7.06218 EndY=5.25 EndZ=0
    g15: LineSegment StartX=7.06218 StartY=5.25 StartZ=0 EndX=7.06218 EndY=8.75 EndZ=0
    g16: LineSegment StartX=7.06218 StartY=8.75 StartZ=0 EndX=4.03109 EndY=10.5 EndZ=0
    g17: LineSegment StartX=4.03109 StartY=10.5 StartZ=0 EndX=1 EndY=8.75 EndZ=0
    g18: LineSegment StartX=1 StartY=8.75 StartZ=0 EndX=1 EndY=5.25 EndZ=0
    g19: LineSegment StartX=1 StartY=5.25 StartZ=0 EndX=4.03109 EndY=3.5 EndZ=0
    g20: Circle [constr] CenterX=4.03109 CenterY=7 CenterZ=0 NormalX=0 NormalY=0 NormalZ=1 AngleXU=0 Radius=3.5
    g21: LineSegment StartX=-1 StartY=5.25 StartZ=0 EndX=-1 EndY=8.75 EndZ=0
    g22: LineSegment StartX=-1 StartY=8.75 StartZ=0 EndX=-4.03109 EndY=10.5 EndZ=0
    g23: LineSegment StartX=-4.03109 StartY=10.5 StartZ=0 EndX=-7.06218 EndY=8.75 EndZ=0
    g24: LineSegment StartX=-7.06218 StartY=8.75 StartZ=0 EndX=-7.06218 EndY=5.25 EndZ=0
    g25: LineSegment StartX=-7.06218 StartY=5.25 StartZ=0 EndX=-4.03109 EndY=3.5 EndZ=0
    g26: LineSegment StartX=-4.03109 StartY=3.5 StartZ=0 EndX=-1 EndY=5.25 EndZ=0
    g27: Circle [constr] CenterX=-4.03109 CenterY=7 CenterZ=0 NormalX=0 NormalY=0 NormalZ=1 AngleXU=0 Radius=3.5
    g28: LineSegment StartX=-4.96891 StartY=-1.75 StartZ=0 EndX=-4.96891 EndY=1.75 EndZ=0
    g29: LineSegment StartX=-4.96891 StartY=1.75 StartZ=0 EndX=-8 EndY=3.5 EndZ=0
    g30: LineSegment StartX=-8 StartY=3.5 StartZ=0 EndX=-11.0311 EndY=1.75 EndZ=0
    g31: LineSegment StartX=-11.0311 StartY=1.75 StartZ=0 EndX=-11.0311 EndY=-1.75 EndZ=0
    g32: LineSegment StartX=-11.0311 StartY=-1.75 StartZ=0 EndX=-8 EndY=-3.5 EndZ=0
    g33: LineSegment StartX=-8 StartY=-3.5 StartZ=0 EndX=-4.96891 EndY=-1.75 EndZ=0
    g34: Circle [constr] CenterX=-8 CenterY=0 CenterZ=0 NormalX=0 NormalY=0 NormalZ=1 AngleXU=0 Radius=3.5
    g35: LineSegment StartX=-4.03109 StartY=-3.5 StartZ=0 EndX=-7.06218 EndY=-5.25 EndZ=0
    g36: LineSegment StartX=-7.06218 StartY=-5.25 StartZ=0 EndX=-7.06218 EndY=-8.75 EndZ=0
    g37: LineSegment StartX=-7.06218 StartY=-8.75 StartZ=0 EndX=-4.03109 EndY=-10.5 EndZ=0
    g38: LineSegment StartX=-4.03109 StartY=-10.5 StartZ=0 EndX=-1 EndY=-8.75 EndZ=0
    g39: LineSegment StartX=-1 StartY=-8.75 StartZ=0 EndX=-1 EndY=-5.25 EndZ=0
    g40: LineSegment StartX=-1 StartY=-5.25 StartZ=0 EndX=-4.03109 EndY=-3.5 EndZ=0
    g41: Circle [constr] CenterX=-4.03109 CenterY=-7 CenterZ=0 NormalX=0 NormalY=0 NormalZ=1 AngleXU=0 Radius=3.5
    g42: LineSegment StartX=4.03109 StartY=-3.5 StartZ=0 EndX=1 EndY=-5.25 EndZ=0
    g43: LineSegment StartX=1 StartY=-5.25 StartZ=0 EndX=1 EndY=-8.75 EndZ=0
    g44: LineSegment StartX=1 StartY=-8.75 StartZ=0 EndX=4.03109 EndY=-10.5 EndZ=0
    g45: LineSegment StartX=4.03109 StartY=-10.5 StartZ=0 EndX=7.06218 EndY=-8.75 EndZ=0
    g46: LineSegment StartX=7.06218 StartY=-8.75 StartZ=0 EndX=7.06218 EndY=-5.25 EndZ=0
    g47: LineSegment StartX=7.06218 StartY=-5.25 StartZ=0 EndX=4.03109 EndY=-3.5 EndZ=0
    g48: Circle [constr] CenterX=4.03109 CenterY=-7 CenterZ=0 NormalX=0 NormalY=0 NormalZ=1 AngleXU=0 Radius=3.5
  constraints (117):
    c: Coincident(g0,g1)
    c: Coincident(g1,g2)
    c: Coincident(g2,g3)
    c: Coincident(g3,g4)
    c: Coincident(g4,g5)
    c: Coincident(g5,g0)
    c: Equal(g0, g1-g5) x5
    c: PointOnObject(g0,g6)
    c: PointOnObject(g1,g6)
    c: PointOnObject(g2,g6)
    c: PointOnObject(g3,g6)
    c: PointOnObject(g4,g6)
    c: PointOnObject(g5,g6)
    c: Coincident(g6,g-1)
    c: Diameter(g6) = 7
    c: PointOnObject(g0,g-2)
    c: Coincident(g7,g8)
    c: Coincident(g8,g9)
    c: Coincident(g9,g10)
    c: Coincident(g10,g11)
    c: Coincident(g11,g12)
    c: Coincident(g12,g7)
    c: Equal(g7, g8-g12) x5
    c: PointOnObject(g7,g13)
    c: PointOnObject(g8,g13)
    c: PointOnObject(g9,g13)
    c: PointOnObject(g10,g13)
    c: PointOnObject(g11,g13)
    c: PointOnObject(g12,g13)
    c: PointOnObject(g13,g-1)
    c: Diameter(g13) = 7
    c: Distance(g6,g13) = 8
    c: Horizontal(g0,g10)
    c: Coincident(g14,g15)
    c: Coincident(g15,g16)
    c: Coincident(g16,g17)
    c: Coincident(g17,g18)
    c: Coincident(g18,g19)
    c: Coincident(g19,g14)
    c: Equal(g14, g15-g19) x5
    c: PointOnObject(g14,g20)
    c: PointOnObject(g15,g20)
    c: PointOnObject(g16,g20)
    c: PointOnObject(g17,g20)
    c: PointOnObject(g18,g20)
    c: PointOnObject(g19,g20)
    c: Diameter(g20) = 7
    c: DistanceY(g-1,g20) = 7
    c: Vertical(g18)
    c: Distance(g17,g-2) = 1
    c: Coincident(g21,g22)
    c: Coincident(g22,g23)
    c: Coincident(g23,g24)
    c: Coincident(g24,g25)
    c: Coincident(g25,g26)
    c: Coincident(g26,g21)
    c: Equal(g21, g22-g26) x5
    c: PointOnObject(g21,g27)
    c: PointOnObject(g22,g27)
    c: PointOnObject(g23,g27)
    c: PointOnObject(g24,g27)
    c: PointOnObject(g25,g27)
    c: PointOnObject(g26,g27)
    c: Diameter(g27) = 7
    c: DistanceY(g-1,g27) = 7
    c: DistanceX(g21,g-1) = 1
    c: Vertical(g21)
    c: Coincident(g28,g29)
    c: Coincident(g29,g30)
    c: Coincident(g30,g31)
    c: Coincident(g31,g32)
    c: Coincident(g32,g33)
    c: Coincident(g33,g28)
    c: Equal(g28, g29-g33) x5
    c: PointOnObject(g28,g34)
    c: PointOnObject(g29,g34)
    c: PointOnObject(g30,g34)
    c: PointOnObject(g31,g34)
    c: PointOnObject(g32,g34)
    c: PointOnObject(g33,g34)
    c: PointOnObject(g34,g-1)
    c: Diameter(g34) = 7
    c: Vertical(g31)
    c: DistanceX(g34,g-1) = 8
    c: Coincident(g35,g36)
    c: Coincident(g36,g37)
    c: Coincident(g37,g38)
    c: Coincident(g38,g39)
    c: Coincident(g39,g40)
    c: Coincident(g40,g35)
    c: Equal(g35, g36-g40) x5
    c: PointOnObject(g35,g41)
    c: PointOnObject(g36,g41)
    c: PointOnObject(g37,g41)
    c: PointOnObject(g38,g41)
    c: PointOnObject(g39,g41)
    c: PointOnObject(g40,g41)
    c: Coincident(g42,g43)
    c: Coincident(g43,g44)
    c: Coincident(g44,g45)
    c: Coincident(g45,g46)
    c: Coincident(g46,g47)
    c: Coincident(g47,g42)
    c: Equal(g42, g43-g47) x5
    c: PointOnObject(g42,g48)
    c: PointOnObject(g43,g48)
    c: PointOnObject(g44,g48)
    c: PointOnObject(g45,g48)
    c: PointOnObject(g46,g48)
    c: PointOnObject(g47,g48)
    c: Equal(g41,g48)
    c: Diameter(g41) = 7
    c: Vertical(g39)
    c: Vertical(g43)
    c: Distance(g-2,g39) = 1
    c: Symmetric(g38,g43,g-2)
    c: Distance(g41,g-1) = 7
FEATURE [Part::Extrusion] Extrude546  label="hex161"
  Base = -> Sketch554
  Dir = (0,-1,2e-16)
  DirMode = 2
  FaceMakerClass = Part::FaceMakerBullseye
  FaceMakerMode = 3
  LengthFwd = 10
  LengthRev = 0
  Placement = pos=(-16,0,112) rot=(0,0,1;0rad)
  Solid = true
  Symmetric = false
FEATURE [Sketcher::SketchObject] Sketch555
  ArcFitTolerance = 1e-06
  FullyConstrained = true
  MakeInternals = false
  Placement = pos=(0,0,0) rot=(1,0,0;1.5708rad)
  sketch-geometry (49):
    g0: LineSegment StartX=1e-16 StartY=3.5 StartZ=0 EndX=-3.03109 EndY=1.75 EndZ=0
    g1: LineSegment StartX=-3.03109 StartY=1.75 StartZ=0 EndX=-3.03109 EndY=-1.75 EndZ=0
    g2: LineSegment StartX=-3.03109 StartY=-1.75 StartZ=0 EndX=-1e-16 EndY=-3.5 EndZ=0
    g3: LineSegment StartX=-1e-16 StartY=-3.5 StartZ=0 EndX=3.03109 EndY=-1.75 EndZ=0
    g4: LineSegment StartX=3.03109 StartY=-1.75 StartZ=0 EndX=3.03109 EndY=1.75 EndZ=0
    g5: LineSegment StartX=3.03109 StartY=1.75 StartZ=0 EndX=1e-16 EndY=3.5 EndZ=0
    g6: Circle [constr] CenterX=0 CenterY=0 CenterZ=0 NormalX=0 NormalY=0 NormalZ=1 AngleXU=0 Radius=3.5
    g7: LineSegment StartX=4.96892 StartY=-1.75002 StartZ=0 EndX=8.00002 EndY=-3.5 EndZ=0
    g8: LineSegment StartX=8.00002 StartY=-3.5 StartZ=0 EndX=11.0311 EndY=-1.74998 EndZ=0
    g9: LineSegment StartX=11.0311 StartY=-1.74998 StartZ=0 EndX=11.0311 EndY=1.75002 EndZ=0
    g10: LineSegment StartX=11.0311 StartY=1.75002 StartZ=0 EndX=7.99998 EndY=3.5 EndZ=0
    g11: LineSegment StartX=7.99998 StartY=3.5 StartZ=0 EndX=4.9689 EndY=1.74998 EndZ=0
    g12: LineSegment StartX=4.9689 StartY=1.74998 StartZ=0 EndX=4.96892 EndY=-1.75002 EndZ=0
    g13: Circle [constr] CenterX=8 CenterY=0 CenterZ=0 NormalX=0 NormalY=0 NormalZ=1 AngleXU=0 Radius=3.5
    g14: LineSegment StartX=4.03109 StartY=3.5 StartZ=0 EndX=7.06218 EndY=5.25 EndZ=0
    g15: LineSegment StartX=7.06218 StartY=5.25 StartZ=0 EndX=7.06218 EndY=8.75 EndZ=0
    g16: LineSegment StartX=7.06218 StartY=8.75 StartZ=0 EndX=4.03109 EndY=10.5 EndZ=0
    g17: LineSegment StartX=4.03109 StartY=10.5 StartZ=0 EndX=1 EndY=8.75 EndZ=0
    g18: LineSegment StartX=1 StartY=8.75 StartZ=0 EndX=1 EndY=5.25 EndZ=0
    g19: LineSegment StartX=1 StartY=5.25 StartZ=0 EndX=4.03109 EndY=3.5 EndZ=0
    g20: Circle [constr] CenterX=4.03109 CenterY=7 CenterZ=0 NormalX=0 NormalY=0 NormalZ=1 AngleXU=0 Radius=3.5
    g21: LineSegment StartX=-1 StartY=5.25 StartZ=0 EndX=-1 EndY=8.75 EndZ=0
    g22: LineSegment StartX=-1 StartY=8.75 StartZ=0 EndX=-4.03109 EndY=10.5 EndZ=0
    g23: LineSegment StartX=-4.03109 StartY=10.5 StartZ=0 EndX=-7.06218 EndY=8.75 EndZ=0
    g24: LineSegment StartX=-7.06218 StartY=8.75 StartZ=0 EndX=-7.06218 EndY=5.25 EndZ=0
    g25: LineSegment StartX=-7.06218 StartY=5.25 StartZ=0 EndX=-4.03109 EndY=3.5 EndZ=0
    g26: LineSegment StartX=-4.03109 StartY=3.5 StartZ=0 EndX=-1 EndY=5.25 EndZ=0
    g27: Circle [constr] CenterX=-4.03109 CenterY=7 CenterZ=0 NormalX=0 NormalY=0 NormalZ=1 AngleXU=0 Radius=3.5
    g28: LineSegment StartX=-4.96891 StartY=-1.75 StartZ=0 EndX=-4.96891 EndY=1.75 EndZ=0
    g29: LineSegment StartX=-4.96891 StartY=1.75 StartZ=0 EndX=-8 EndY=3.5 EndZ=0
    g30: LineSegment StartX=-8 StartY=3.5 StartZ=0 EndX=-11.0311 EndY=1.75 EndZ=0
    g31: LineSegment StartX=-11.0311 StartY=1.75 StartZ=0 EndX=-11.0311 EndY=-1.75 EndZ=0
    g32: LineSegment StartX=-11.0311 StartY=-1.75 StartZ=0 EndX=-8 EndY=-3.5 EndZ=0
    g33: LineSegment StartX=-8 StartY=-3.5 StartZ=0 EndX=-4.96891 EndY=-1.75 EndZ=0
    g34: Circle [constr] CenterX=-8 CenterY=0 CenterZ=0 NormalX=0 NormalY=0 NormalZ=1 AngleXU=0 Radius=3.5
    g35: LineSegment StartX=-4.03109 StartY=-3.5 StartZ=0 EndX=-7.06218 EndY=-5.25 EndZ=0
    g36: LineSegment StartX=-7.06218 StartY=-5.25 StartZ=0 EndX=-7.06218 EndY=-8.75 EndZ=0
    g37: LineSegment StartX=-7.06218 StartY=-8.75 StartZ=0 EndX=-4.03109 EndY=-10.5 EndZ=0
    g38: LineSegment StartX=-4.03109 StartY=-10.5 StartZ=0 EndX=-1 EndY=-8.75 EndZ=0
    g39: LineSegment StartX=-1 StartY=-8.75 StartZ=0 EndX=-1 EndY=-5.25 EndZ=0
    g40: LineSegment StartX=-1 StartY=-5.25 StartZ=0 EndX=-4.03109 EndY=-3.5 EndZ=0
    g41: Circle [constr] CenterX=-4.03109 CenterY=-7 CenterZ=0 NormalX=0 NormalY=0 NormalZ=1 AngleXU=0 Radius=3.5
    g42: LineSegment StartX=4.03109 StartY=-3.5 StartZ=0 EndX=1 EndY=-5.25 EndZ=0
    g43: LineSegment StartX=1 StartY=-5.25 StartZ=0 EndX=1 EndY=-8.75 EndZ=0
    g44: LineSegment StartX=1 StartY=-8.75 StartZ=0 EndX=4.03109 EndY=-10.5 EndZ=0
    g45: LineSegment StartX=4.03109 StartY=-10.5 StartZ=0 EndX=7.06218 EndY=-8.75 EndZ=0
    g46: LineSegment StartX=7.06218 StartY=-8.75 StartZ=0 EndX=7.06218 EndY=-5.25 EndZ=0
    g47: LineSegment StartX=7.06218 StartY=-5.25 StartZ=0 EndX=4.03109 EndY=-3.5 EndZ=0
    g48: Circle [constr] CenterX=4.03109 CenterY=-7 CenterZ=0 NormalX=0 NormalY=0 NormalZ=1 AngleXU=0 Radius=3.5
  constraints (117):
    c: Coincident(g0,g1)
    c: Coincident(g1,g2)
    c: Coincident(g2,g3)
    c: Coincident(g3,g4)
    c: Coincident(g4,g5)
    c: Coincident(g5,g0)
    c: Equal(g0, g1-g5) x5
    c: PointOnObject(g0,g6)
    c: PointOnObject(g1,g6)
    c: PointOnObject(g2,g6)
    c: PointOnObject(g3,g6)
    c: PointOnObject(g4,g6)
    c: PointOnObject(g5,g6)
    c: Coincident(g6,g-1)
    c: Diameter(g6) = 7
    c: PointOnObject(g0,g-2)
    c: Coincident(g7,g8)
    c: Coincident(g8,g9)
    c: Coincident(g9,g10)
    c: Coincident(g10,g11)
    c: Coincident(g11,g12)
    c: Coincident(g12,g7)
    c: Equal(g7, g8-g12) x5
    c: PointOnObject(g7,g13)
    c: PointOnObject(g8,g13)
    c: PointOnObject(g9,g13)
    c: PointOnObject(g10,g13)
    c: PointOnObject(g11,g13)
    c: PointOnObject(g12,g13)
    c: PointOnObject(g13,g-1)
    c: Diameter(g13) = 7
    c: Distance(g6,g13) = 8
    c: Horizontal(g0,g10)
    c: Coincident(g14,g15)
    c: Coincident(g15,g16)
    c: Coincident(g16,g17)
    c: Coincident(g17,g18)
    c: Coincident(g18,g19)
    c: Coincident(g19,g14)
    c: Equal(g14, g15-g19) x5
    c: PointOnObject(g14,g20)
    c: PointOnObject(g15,g20)
    c: PointOnObject(g16,g20)
    c: PointOnObject(g17,g20)
    c: PointOnObject(g18,g20)
    c: PointOnObject(g19,g20)
    c: Diameter(g20) = 7
    c: DistanceY(g-1,g20) = 7
    c: Vertical(g18)
    c: Distance(g17,g-2) = 1
    c: Coincident(g21,g22)
    c: Coincident(g22,g23)
    c: Coincident(g23,g24)
    c: Coincident(g24,g25)
    c: Coincident(g25,g26)
    c: Coincident(g26,g21)
    c: Equal(g21, g22-g26) x5
    c: PointOnObject(g21,g27)
    c: PointOnObject(g22,g27)
    c: PointOnObject(g23,g27)
    c: PointOnObject(g24,g27)
    c: PointOnObject(g25,g27)
    c: PointOnObject(g26,g27)
    c: Diameter(g27) = 7
    c: DistanceY(g-1,g27) = 7
    c: DistanceX(g21,g-1) = 1
    c: Vertical(g21)
    c: Coincident(g28,g29)
    c: Coincident(g29,g30)
    c: Coincident(g30,g31)
    c: Coincident(g31,g32)
    c: Coincident(g32,g33)
    c: Coincident(g33,g28)
    c: Equal(g28, g29-g33) x5
    c: PointOnObject(g28,g34)
    c: PointOnObject(g29,g34)
    c: PointOnObject(g30,g34)
    c: PointOnObject(g31,g34)
    c: PointOnObject(g32,g34)
    c: PointOnObject(g33,g34)
    c: PointOnObject(g34,g-1)
    c: Diameter(g34) = 7
    c: Vertical(g31)
    c: DistanceX(g34,g-1) = 8
    c: Coincident(g35,g36)
    c: Coincident(g36,g37)
    c: Coincident(g37,g38)
    c: Coincident(g38,g39)
    c: Coincident(g39,g40)
    c: Coincident(g40,g35)
    c: Equal(g35, g36-g40) x5
    c: PointOnObject(g35,g41)
    c: PointOnObject(g36,g41)
    c: PointOnObject(g37,g41)
    c: PointOnObject(g38,g41)
    c: PointOnObject(g39,g41)
    c: PointOnObject(g40,g41)
    c: Coincident(g42,g43)
    c: Coincident(g43,g44)
    c: Coincident(g44,g45)
    c: Coincident(g45,g46)
    c: Coincident(g46,g47)
    c: Coincident(g47,g42)
    c: Equal(g42, g43-g47) x5
    c: PointOnObject(g42,g48)
    c: PointOnObject(g43,g48)
    c: PointOnObject(g44,g48)
    c: PointOnObject(g45,g48)
    c: PointOnObject(g46,g48)
    c: PointOnObject(g47,g48)
    c: Equal(g41,g48)
    c: Diameter(g41) = 7
    c: Vertical(g39)
    c: Vertical(g43)
    c: Distance(g-2,g39) = 1
    c: Symmetric(g38,g43,g-2)
    c: Distance(g41,g-1) = 7
FEATURE [Part::Extrusion] Extrude547  label="hex162"
  Base = -> Sketch555
  Dir = (0,-1,2e-16)
  DirMode = 2
  FaceMakerClass = Part::FaceMakerBullseye
  FaceMakerMode = 3
  LengthFwd = 10
  LengthRev = 0
  Placement = pos=(-32,0,98) rot=(0,0,1;0rad)
  Solid = true
  Symmetric = false
FEATURE [Sketcher::SketchObject] Sketch556
  ArcFitTolerance = 1e-06
  FullyConstrained = true
  MakeInternals = false
  Placement = pos=(0,0,0) rot=(1,0,0;1.5708rad)
  sketch-geometry (49):
    g0: LineSegment StartX=1e-16 StartY=3.5 StartZ=0 EndX=-3.03109 EndY=1.75 EndZ=0
    g1: LineSegment StartX=-3.03109 StartY=1.75 StartZ=0 EndX=-3.03109 EndY=-1.75 EndZ=0
    g2: LineSegment StartX=-3.03109 StartY=-1.75 StartZ=0 EndX=-1e-16 EndY=-3.5 EndZ=0
    g3: LineSegment StartX=-1e-16 StartY=-3.5 StartZ=0 EndX=3.03109 EndY=-1.75 EndZ=0
    g4: LineSegment StartX=3.03109 StartY=-1.75 StartZ=0 EndX=3.03109 EndY=1.75 EndZ=0
    g5: LineSegment StartX=3.03109 StartY=1.75 StartZ=0 EndX=1e-16 EndY=3.5 EndZ=0
    g6: Circle [constr] CenterX=0 CenterY=0 CenterZ=0 NormalX=0 NormalY=0 NormalZ=1 AngleXU=0 Radius=3.5
    g7: LineSegment StartX=4.96892 StartY=-1.75002 StartZ=0 EndX=8.00002 EndY=-3.5 EndZ=0
    g8: LineSegment StartX=8.00002 StartY=-3.5 StartZ=0 EndX=11.0311 EndY=-1.74998 EndZ=0
    g9: LineSegment StartX=11.0311 StartY=-1.74998 StartZ=0 EndX=11.0311 EndY=1.75002 EndZ=0
    g10: LineSegment StartX=11.0311 StartY=1.75002 StartZ=0 EndX=7.99998 EndY=3.5 EndZ=0
    g11: LineSegment StartX=7.99998 StartY=3.5 StartZ=0 EndX=4.9689 EndY=1.74998 EndZ=0
    g12: LineSegment StartX=4.9689 StartY=1.74998 StartZ=0 EndX=4.96892 EndY=-1.75002 EndZ=0
    g13: Circle [constr] CenterX=8 CenterY=0 CenterZ=0 NormalX=0 NormalY=0 NormalZ=1 AngleXU=0 Radius=3.5
    g14: LineSegment StartX=4.03109 StartY=3.5 StartZ=0 EndX=7.06218 EndY=5.25 EndZ=0
    g15: LineSegment StartX=7.06218 StartY=5.25 StartZ=0 EndX=7.06218 EndY=8.75 EndZ=0
    g16: LineSegment StartX=7.06218 StartY=8.75 StartZ=0 EndX=4.03109 EndY=10.5 EndZ=0
    g17: LineSegment StartX=4.03109 StartY=10.5 StartZ=0 EndX=1 EndY=8.75 EndZ=0
    g18: LineSegment StartX=1 StartY=8.75 StartZ=0 EndX=1 EndY=5.25 EndZ=0
    g19: LineSegment StartX=1 StartY=5.25 StartZ=0 EndX=4.03109 EndY=3.5 EndZ=0
    g20: Circle [constr] CenterX=4.03109 CenterY=7 CenterZ=0 NormalX=0 NormalY=0 NormalZ=1 AngleXU=0 Radius=3.5
    g21: LineSegment StartX=-1 StartY=5.25 StartZ=0 EndX=-1 EndY=8.75 EndZ=0
    g22: LineSegment StartX=-1 StartY=8.75 StartZ=0 EndX=-4.03109 EndY=10.5 EndZ=0
    g23: LineSegment StartX=-4.03109 StartY=10.5 StartZ=0 EndX=-7.06218 EndY=8.75 EndZ=0
    g24: LineSegment StartX=-7.06218 StartY=8.75 StartZ=0 EndX=-7.06218 EndY=5.25 EndZ=0
    g25: LineSegment StartX=-7.06218 StartY=5.25 StartZ=0 EndX=-4.03109 EndY=3.5 EndZ=0
    g26: LineSegment StartX=-4.03109 StartY=3.5 StartZ=0 EndX=-1 EndY=5.25 EndZ=0
    g27: Circle [constr] CenterX=-4.03109 CenterY=7 CenterZ=0 NormalX=0 NormalY=0 NormalZ=1 AngleXU=0 Radius=3.5
    g28: LineSegment StartX=-4.96891 StartY=-1.75 StartZ=0 EndX=-4.96891 EndY=1.75 EndZ=0
    g29: LineSegment StartX=-4.96891 StartY=1.75 StartZ=0 EndX=-8 EndY=3.5 EndZ=0
    g30: LineSegment StartX=-8 StartY=3.5 StartZ=0 EndX=-11.0311 EndY=1.75 EndZ=0
    g31: LineSegment StartX=-11.0311 StartY=1.75 StartZ=0 EndX=-11.0311 EndY=-1.75 EndZ=0
    g32: LineSegment StartX=-11.0311 StartY=-1.75 StartZ=0 EndX=-8 EndY=-3.5 EndZ=0
    g33: LineSegment StartX=-8 StartY=-3.5 StartZ=0 EndX=-4.96891 EndY=-1.75 EndZ=0
    g34: Circle [constr] CenterX=-8 CenterY=0 CenterZ=0 NormalX=0 NormalY=0 NormalZ=1 AngleXU=0 Radius=3.5
    g35: LineSegment StartX=-4.03109 StartY=-3.5 StartZ=0 EndX=-7.06218 EndY=-5.25 EndZ=0
    g36: LineSegment StartX=-7.06218 StartY=-5.25 StartZ=0 EndX=-7.06218 EndY=-8.75 EndZ=0
    g37: LineSegment StartX=-7.06218 StartY=-8.75 StartZ=0 EndX=-4.03109 EndY=-10.5 EndZ=0
    g38: LineSegment StartX=-4.03109 StartY=-10.5 StartZ=0 EndX=-1 EndY=-8.75 EndZ=0
    g39: LineSegment StartX=-1 StartY=-8.75 StartZ=0 EndX=-1 EndY=-5.25 EndZ=0
    g40: LineSegment StartX=-1 StartY=-5.25 StartZ=0 EndX=-4.03109 EndY=-3.5 EndZ=0
    g41: Circle [constr] CenterX=-4.03109 CenterY=-7 CenterZ=0 NormalX=0 NormalY=0 NormalZ=1 AngleXU=0 Radius=3.5
    g42: LineSegment StartX=4.03109 StartY=-3.5 StartZ=0 EndX=1 EndY=-5.25 EndZ=0
    g43: LineSegment StartX=1 StartY=-5.25 StartZ=0 EndX=1 EndY=-8.75 EndZ=0
    g44: LineSegment StartX=1 StartY=-8.75 StartZ=0 EndX=4.03109 EndY=-10.5 EndZ=0
    g45: LineSegment StartX=4.03109 StartY=-10.5 StartZ=0 EndX=7.06218 EndY=-8.75 EndZ=0
    g46: LineSegment StartX=7.06218 StartY=-8.75 StartZ=0 EndX=7.06218 EndY=-5.25 EndZ=0
    g47: LineSegment StartX=7.06218 StartY=-5.25 StartZ=0 EndX=4.03109 EndY=-3.5 EndZ=0
    g48: Circle [constr] CenterX=4.03109 CenterY=-7 CenterZ=0 NormalX=0 NormalY=0 NormalZ=1 AngleXU=0 Radius=3.5
  constraints (117):
    c: Coincident(g0,g1)
    c: Coincident(g1,g2)
    c: Coincident(g2,g3)
    c: Coincident(g3,g4)
    c: Coincident(g4,g5)
    c: Coincident(g5,g0)
    c: Equal(g0, g1-g5) x5
    c: PointOnObject(g0,g6)
    c: PointOnObject(g1,g6)
    c: PointOnObject(g2,g6)
    c: PointOnObject(g3,g6)
    c: PointOnObject(g4,g6)
    c: PointOnObject(g5,g6)
    c: Coincident(g6,g-1)
    c: Diameter(g6) = 7
    c: PointOnObject(g0,g-2)
    c: Coincident(g7,g8)
    c: Coincident(g8,g9)
    c: Coincident(g9,g10)
    c: Coincident(g10,g11)
    c: Coincident(g11,g12)
    c: Coincident(g12,g7)
    c: Equal(g7, g8-g12) x5
    c: PointOnObject(g7,g13)
    c: PointOnObject(g8,g13)
    c: PointOnObject(g9,g13)
    c: PointOnObject(g10,g13)
    c: PointOnObject(g11,g13)
    c: PointOnObject(g12,g13)
    c: PointOnObject(g13,g-1)
    c: Diameter(g13) = 7
    c: Distance(g6,g13) = 8
    c: Horizontal(g0,g10)
    c: Coincident(g14,g15)
    c: Coincident(g15,g16)
    c: Coincident(g16,g17)
    c: Coincident(g17,g18)
    c: Coincident(g18,g19)
    c: Coincident(g19,g14)
    c: Equal(g14, g15-g19) x5
    c: PointOnObject(g14,g20)
    c: PointOnObject(g15,g20)
    c: PointOnObject(g16,g20)
    c: PointOnObject(g17,g20)
    c: PointOnObject(g18,g20)
    c: PointOnObject(g19,g20)
    c: Diameter(g20) = 7
    c: DistanceY(g-1,g20) = 7
    c: Vertical(g18)
    c: Distance(g17,g-2) = 1
    c: Coincident(g21,g22)
    c: Coincident(g22,g23)
    c: Coincident(g23,g24)
    c: Coincident(g24,g25)
    c: Coincident(g25,g26)
    c: Coincident(g26,g21)
    c: Equal(g21, g22-g26) x5
    c: PointOnObject(g21,g27)
    c: PointOnObject(g22,g27)
    c: PointOnObject(g23,g27)
    c: PointOnObject(g24,g27)
    c: PointOnObject(g25,g27)
    c: PointOnObject(g26,g27)
    c: Diameter(g27) = 7
    c: DistanceY(g-1,g27) = 7
    c: DistanceX(g21,g-1) = 1
    c: Vertical(g21)
    c: Coincident(g28,g29)
    c: Coincident(g29,g30)
    c: Coincident(g30,g31)
    c: Coincident(g31,g32)
    c: Coincident(g32,g33)
    c: Coincident(g33,g28)
    c: Equal(g28, g29-g33) x5
    c: PointOnObject(g28,g34)
    c: PointOnObject(g29,g34)
    c: PointOnObject(g30,g34)
    c: PointOnObject(g31,g34)
    c: PointOnObject(g32,g34)
    c: PointOnObject(g33,g34)
    c: PointOnObject(g34,g-1)
    c: Diameter(g34) = 7
    c: Vertical(g31)
    c: DistanceX(g34,g-1) = 8
    c: Coincident(g35,g36)
    c: Coincident(g36,g37)
    c: Coincident(g37,g38)
    c: Coincident(g38,g39)
    c: Coincident(g39,g40)
    c: Coincident(g40,g35)
    c: Equal(g35, g36-g40) x5
    c: PointOnObject(g35,g41)
    c: PointOnObject(g36,g41)
    c: PointOnObject(g37,g41)
    c: PointOnObject(g38,g41)
    c: PointOnObject(g39,g41)
    c: PointOnObject(g40,g41)
    c: Coincident(g42,g43)
    c: Coincident(g43,g44)
    c: Coincident(g44,g45)
    c: Coincident(g45,g46)
    c: Coincident(g46,g47)
    c: Coincident(g47,g42)
    c: Equal(g42, g43-g47) x5
    c: PointOnObject(g42,g48)
    c: PointOnObject(g43,g48)
    c: PointOnObject(g44,g48)
    c: PointOnObject(g45,g48)
    c: PointOnObject(g46,g48)
    c: PointOnObject(g47,g48)
    c: Equal(g41,g48)
    c: Diameter(g41) = 7
    c: Vertical(g39)
    c: Vertical(g43)
    c: Distance(g-2,g39) = 1
    c: Symmetric(g38,g43,g-2)
    c: Distance(g41,g-1) = 7
FEATURE [Part::Extrusion] Extrude548  label="hex163"
  Base = -> Sketch556
  Dir = (0,-1,2e-16)
  DirMode = 2
  FaceMakerClass = Part::FaceMakerBullseye
  FaceMakerMode = 3
  LengthFwd = 10
  LengthRev = 0
  Placement = pos=(-52,0,91) rot=(0,0,1;0rad)
  Solid = true
  Symmetric = false
FEATURE [Sketcher::SketchObject] Sketch557
  ArcFitTolerance = 1e-06
  FullyConstrained = true
  MakeInternals = false
  Placement = pos=(0,0,0) rot=(1,0,0;1.5708rad)
  sketch-geometry (49):
    g0: LineSegment StartX=1e-16 StartY=3.5 StartZ=0 EndX=-3.03109 EndY=1.75 EndZ=0
    g1: LineSegment StartX=-3.03109 StartY=1.75 StartZ=0 EndX=-3.03109 EndY=-1.75 EndZ=0
    g2: LineSegment StartX=-3.03109 StartY=-1.75 StartZ=0 EndX=-1e-16 EndY=-3.5 EndZ=0
    g3: LineSegment StartX=-1e-16 StartY=-3.5 StartZ=0 EndX=3.03109 EndY=-1.75 EndZ=0
    g4: LineSegment StartX=3.03109 StartY=-1.75 StartZ=0 EndX=3.03109 EndY=1.75 EndZ=0
    g5: LineSegment StartX=3.03109 StartY=1.75 StartZ=0 EndX=1e-16 EndY=3.5 EndZ=0
    g6: Circle [constr] CenterX=0 CenterY=0 CenterZ=0 NormalX=0 NormalY=0 NormalZ=1 AngleXU=0 Radius=3.5
    g7: LineSegment StartX=4.96892 StartY=-1.75002 StartZ=0 EndX=8.00002 EndY=-3.5 EndZ=0
    g8: LineSegment StartX=8.00002 StartY=-3.5 StartZ=0 EndX=11.0311 EndY=-1.74998 EndZ=0
    g9: LineSegment StartX=11.0311 StartY=-1.74998 StartZ=0 EndX=11.0311 EndY=1.75002 EndZ=0
    g10: LineSegment StartX=11.0311 StartY=1.75002 StartZ=0 EndX=7.99998 EndY=3.5 EndZ=0
    g11: LineSegment StartX=7.99998 StartY=3.5 StartZ=0 EndX=4.9689 EndY=1.74998 EndZ=0
    g12: LineSegment StartX=4.9689 StartY=1.74998 StartZ=0 EndX=4.96892 EndY=-1.75002 EndZ=0
    g13: Circle [constr] CenterX=8 CenterY=0 CenterZ=0 NormalX=0 NormalY=0 NormalZ=1 AngleXU=0 Radius=3.5
    g14: LineSegment StartX=4.03109 StartY=3.5 StartZ=0 EndX=7.06218 EndY=5.25 EndZ=0
    g15: LineSegment StartX=7.06218 StartY=5.25 StartZ=0 EndX=7.06218 EndY=8.75 EndZ=0
    g16: LineSegment StartX=7.06218 StartY=8.75 StartZ=0 EndX=4.03109 EndY=10.5 EndZ=0
    g17: LineSegment StartX=4.03109 StartY=10.5 StartZ=0 EndX=1 EndY=8.75 EndZ=0
    g18: LineSegment StartX=1 StartY=8.75 StartZ=0 EndX=1 EndY=5.25 EndZ=0
    g19: LineSegment StartX=1 StartY=5.25 StartZ=0 EndX=4.03109 EndY=3.5 EndZ=0
    g20: Circle [constr] CenterX=4.03109 CenterY=7 CenterZ=0 NormalX=0 NormalY=0 NormalZ=1 AngleXU=0 Radius=3.5
    g21: LineSegment StartX=-1 StartY=5.25 StartZ=0 EndX=-1 EndY=8.75 EndZ=0
    g22: LineSegment StartX=-1 StartY=8.75 StartZ=0 EndX=-4.03109 EndY=10.5 EndZ=0
    g23: LineSegment StartX=-4.03109 StartY=10.5 StartZ=0 EndX=-7.06218 EndY=8.75 EndZ=0
    g24: LineSegment StartX=-7.06218 StartY=8.75 StartZ=0 EndX=-7.06218 EndY=5.25 EndZ=0
    g25: LineSegment StartX=-7.06218 StartY=5.25 StartZ=0 EndX=-4.03109 EndY=3.5 EndZ=0
    g26: LineSegment StartX=-4.03109 StartY=3.5 StartZ=0 EndX=-1 EndY=5.25 EndZ=0
    g27: Circle [constr] CenterX=-4.03109 CenterY=7 CenterZ=0 NormalX=0 NormalY=0 NormalZ=1 AngleXU=0 Radius=3.5
    g28: LineSegment StartX=-4.96891 StartY=-1.75 StartZ=0 EndX=-4.96891 EndY=1.75 EndZ=0
    g29: LineSegment StartX=-4.96891 StartY=1.75 StartZ=0 EndX=-8 EndY=3.5 EndZ=0
    g30: LineSegment StartX=-8 StartY=3.5 StartZ=0 EndX=-11.0311 EndY=1.75 EndZ=0
    g31: LineSegment StartX=-11.0311 StartY=1.75 StartZ=0 EndX=-11.0311 EndY=-1.75 EndZ=0
    g32: LineSegment StartX=-11.0311 StartY=-1.75 StartZ=0 EndX=-8 EndY=-3.5 EndZ=0
    g33: LineSegment StartX=-8 StartY=-3.5 StartZ=0 EndX=-4.96891 EndY=-1.75 EndZ=0
    g34: Circle [constr] CenterX=-8 CenterY=0 CenterZ=0 NormalX=0 NormalY=0 NormalZ=1 AngleXU=0 Radius=3.5
    g35: LineSegment StartX=-4.03109 StartY=-3.5 StartZ=0 EndX=-7.06218 EndY=-5.25 EndZ=0
    g36: LineSegment StartX=-7.06218 StartY=-5.25 StartZ=0 EndX=-7.06218 EndY=-8.75 EndZ=0
    g37: LineSegment StartX=-7.06218 StartY=-8.75 StartZ=0 EndX=-4.03109 EndY=-10.5 EndZ=0
    g38: LineSegment StartX=-4.03109 StartY=-10.5 StartZ=0 EndX=-1 EndY=-8.75 EndZ=0
    g39: LineSegment StartX=-1 StartY=-8.75 StartZ=0 EndX=-1 EndY=-5.25 EndZ=0
    g40: LineSegment StartX=-1 StartY=-5.25 StartZ=0 EndX=-4.03109 EndY=-3.5 EndZ=0
    g41: Circle [constr] CenterX=-4.03109 CenterY=-7 CenterZ=0 NormalX=0 NormalY=0 NormalZ=1 AngleXU=0 Radius=3.5
    g42: LineSegment StartX=4.03109 StartY=-3.5 StartZ=0 EndX=1 EndY=-5.25 EndZ=0
    g43: LineSegment StartX=1 StartY=-5.25 StartZ=0 EndX=1 EndY=-8.75 EndZ=0
    g44: LineSegment StartX=1 StartY=-8.75 StartZ=0 EndX=4.03109 EndY=-10.5 EndZ=0
    g45: LineSegment StartX=4.03109 StartY=-10.5 StartZ=0 EndX=7.06218 EndY=-8.75 EndZ=0
    g46: LineSegment StartX=7.06218 StartY=-8.75 StartZ=0 EndX=7.06218 EndY=-5.25 EndZ=0
    g47: LineSegment StartX=7.06218 StartY=-5.25 StartZ=0 EndX=4.03109 EndY=-3.5 EndZ=0
    g48: Circle [constr] CenterX=4.03109 CenterY=-7 CenterZ=0 NormalX=0 NormalY=0 NormalZ=1 AngleXU=0 Radius=3.5
  constraints (117):
    c: Coincident(g0,g1)
    c: Coincident(g1,g2)
    c: Coincident(g2,g3)
    c: Coincident(g3,g4)
    c: Coincident(g4,g5)
    c: Coincident(g5,g0)
    c: Equal(g0, g1-g5) x5
    c: PointOnObject(g0,g6)
    c: PointOnObject(g1,g6)
    c: PointOnObject(g2,g6)
    c: PointOnObject(g3,g6)
    c: PointOnObject(g4,g6)
    c: PointOnObject(g5,g6)
    c: Coincident(g6,g-1)
    c: Diameter(g6) = 7
    c: PointOnObject(g0,g-2)
    c: Coincident(g7,g8)
    c: Coincident(g8,g9)
    c: Coincident(g9,g10)
    c: Coincident(g10,g11)
    c: Coincident(g11,g12)
    c: Coincident(g12,g7)
    c: Equal(g7, g8-g12) x5
    c: PointOnObject(g7,g13)
    c: PointOnObject(g8,g13)
    c: PointOnObject(g9,g13)
    c: PointOnObject(g10,g13)
    c: PointOnObject(g11,g13)
    c: PointOnObject(g12,g13)
    c: PointOnObject(g13,g-1)
    c: Diameter(g13) = 7
    c: Distance(g6,g13) = 8
    c: Horizontal(g0,g10)
    c: Coincident(g14,g15)
    c: Coincident(g15,g16)
    c: Coincident(g16,g17)
    c: Coincident(g17,g18)
    c: Coincident(g18,g19)
    c: Coincident(g19,g14)
    c: Equal(g14, g15-g19) x5
    c: PointOnObject(g14,g20)
    c: PointOnObject(g15,g20)
    c: PointOnObject(g16,g20)
    c: PointOnObject(g17,g20)
    c: PointOnObject(g18,g20)
    c: PointOnObject(g19,g20)
    c: Diameter(g20) = 7
    c: DistanceY(g-1,g20) = 7
    c: Vertical(g18)
    c: Distance(g17,g-2) = 1
    c: Coincident(g21,g22)
    c: Coincident(g22,g23)
    c: Coincident(g23,g24)
    c: Coincident(g24,g25)
    c: Coincident(g25,g26)
    c: Coincident(g26,g21)
    c: Equal(g21, g22-g26) x5
    c: PointOnObject(g21,g27)
    c: PointOnObject(g22,g27)
    c: PointOnObject(g23,g27)
    c: PointOnObject(g24,g27)
    c: PointOnObject(g25,g27)
    c: PointOnObject(g26,g27)
    c: Diameter(g27) = 7
    c: DistanceY(g-1,g27) = 7
    c: DistanceX(g21,g-1) = 1
    c: Vertical(g21)
    c: Coincident(g28,g29)
    c: Coincident(g29,g30)
    c: Coincident(g30,g31)
    c: Coincident(g31,g32)
    c: Coincident(g32,g33)
    c: Coincident(g33,g28)
    c: Equal(g28, g29-g33) x5
    c: PointOnObject(g28,g34)
    c: PointOnObject(g29,g34)
    c: PointOnObject(g30,g34)
    c: PointOnObject(g31,g34)
    c: PointOnObject(g32,g34)
    c: PointOnObject(g33,g34)
    c: PointOnObject(g34,g-1)
    c: Diameter(g34) = 7
    c: Vertical(g31)
    c: DistanceX(g34,g-1) = 8
    c: Coincident(g35,g36)
    c: Coincident(g36,g37)
    c: Coincident(g37,g38)
    c: Coincident(g38,g39)
    c: Coincident(g39,g40)
    c: Coincident(g40,g35)
    c: Equal(g35, g36-g40) x5
    c: PointOnObject(g35,g41)
    c: PointOnObject(g36,g41)
    c: PointOnObject(g37,g41)
    c: PointOnObject(g38,g41)
    c: PointOnObject(g39,g41)
    c: PointOnObject(g40,g41)
    c: Coincident(g42,g43)
    c: Coincident(g43,g44)
    c: Coincident(g44,g45)
    c: Coincident(g45,g46)
    c: Coincident(g46,g47)
    c: Coincident(g47,g42)
    c: Equal(g42, g43-g47) x5
    c: PointOnObject(g42,g48)
    c: PointOnObject(g43,g48)
    c: PointOnObject(g44,g48)
    c: PointOnObject(g45,g48)
    c: PointOnObject(g46,g48)
    c: PointOnObject(g47,g48)
    c: Equal(g41,g48)
    c: Diameter(g41) = 7
    c: Vertical(g39)
    c: Vertical(g43)
    c: Distance(g-2,g39) = 1
    c: Symmetric(g38,g43,g-2)
    c: Distance(g41,g-1) = 7
FEATURE [Part::Extrusion] Extrude549  label="hex164"
  Base = -> Sketch557
  Dir = (0,-1,2e-16)
  DirMode = 2
  FaceMakerClass = Part::FaceMakerBullseye
  FaceMakerMode = 3
  LengthFwd = 10
  LengthRev = 0
  Placement = pos=(-68,0,77) rot=(0,0,1;0rad)
  Solid = true
  Symmetric = false
FEATURE [Sketcher::SketchObject] Sketch558
  ArcFitTolerance = 1e-06
  FullyConstrained = true
  MakeInternals = false
  Placement = pos=(0,0,0) rot=(1,0,0;1.5708rad)
  sketch-geometry (49):
    g0: LineSegment StartX=1e-16 StartY=3.5 StartZ=0 EndX=-3.03109 EndY=1.75 EndZ=0
    g1: LineSegment StartX=-3.03109 StartY=1.75 StartZ=0 EndX=-3.03109 EndY=-1.75 EndZ=0
    g2: LineSegment StartX=-3.03109 StartY=-1.75 StartZ=0 EndX=-1e-16 EndY=-3.5 EndZ=0
    g3: LineSegment StartX=-1e-16 StartY=-3.5 StartZ=0 EndX=3.03109 EndY=-1.75 EndZ=0
    g4: LineSegment StartX=3.03109 StartY=-1.75 StartZ=0 EndX=3.03109 EndY=1.75 EndZ=0
    g5: LineSegment StartX=3.03109 StartY=1.75 StartZ=0 EndX=1e-16 EndY=3.5 EndZ=0
    g6: Circle [constr] CenterX=0 CenterY=0 CenterZ=0 NormalX=0 NormalY=0 NormalZ=1 AngleXU=0 Radius=3.5
    g7: LineSegment StartX=4.96892 StartY=-1.75002 StartZ=0 EndX=8.00002 EndY=-3.5 EndZ=0
    g8: LineSegment StartX=8.00002 StartY=-3.5 StartZ=0 EndX=11.0311 EndY=-1.74998 EndZ=0
    g9: LineSegment StartX=11.0311 StartY=-1.74998 StartZ=0 EndX=11.0311 EndY=1.75002 EndZ=0
    g10: LineSegment StartX=11.0311 StartY=1.75002 StartZ=0 EndX=7.99998 EndY=3.5 EndZ=0
    g11: LineSegment StartX=7.99998 StartY=3.5 StartZ=0 EndX=4.9689 EndY=1.74998 EndZ=0
    g12: LineSegment StartX=4.9689 StartY=1.74998 StartZ=0 EndX=4.96892 EndY=-1.75002 EndZ=0
    g13: Circle [constr] CenterX=8 CenterY=0 CenterZ=0 NormalX=0 NormalY=0 NormalZ=1 AngleXU=0 Radius=3.5
    g14: LineSegment StartX=4.03109 StartY=3.5 StartZ=0 EndX=7.06218 EndY=5.25 EndZ=0
    g15: LineSegment StartX=7.06218 StartY=5.25 StartZ=0 EndX=7.06218 EndY=8.75 EndZ=0
    g16: LineSegment StartX=7.06218 StartY=8.75 StartZ=0 EndX=4.03109 EndY=10.5 EndZ=0
    g17: LineSegment StartX=4.03109 StartY=10.5 StartZ=0 EndX=1 EndY=8.75 EndZ=0
    g18: LineSegment StartX=1 StartY=8.75 StartZ=0 EndX=1 EndY=5.25 EndZ=0
    g19: LineSegment StartX=1 StartY=5.25 StartZ=0 EndX=4.03109 EndY=3.5 EndZ=0
    g20: Circle [constr] CenterX=4.03109 CenterY=7 CenterZ=0 NormalX=0 NormalY=0 NormalZ=1 AngleXU=0 Radius=3.5
    g21: LineSegment StartX=-1 StartY=5.25 StartZ=0 EndX=-1 EndY=8.75 EndZ=0
    g22: LineSegment StartX=-1 StartY=8.75 StartZ=0 EndX=-4.03109 EndY=10.5 EndZ=0
    g23: LineSegment StartX=-4.03109 StartY=10.5 StartZ=0 EndX=-7.06218 EndY=8.75 EndZ=0
    g24: LineSegment StartX=-7.06218 StartY=8.75 StartZ=0 EndX=-7.06218 EndY=5.25 EndZ=0
    g25: LineSegment StartX=-7.06218 StartY=5.25 StartZ=0 EndX=-4.03109 EndY=3.5 EndZ=0
    g26: LineSegment StartX=-4.03109 StartY=3.5 StartZ=0 EndX=-1 EndY=5.25 EndZ=0
    g27: Circle [constr] CenterX=-4.03109 CenterY=7 CenterZ=0 NormalX=0 NormalY=0 NormalZ=1 AngleXU=0 Radius=3.5
    g28: LineSegment StartX=-4.96891 StartY=-1.75 StartZ=0 EndX=-4.96891 EndY=1.75 EndZ=0
    g29: LineSegment StartX=-4.96891 StartY=1.75 StartZ=0 EndX=-8 EndY=3.5 EndZ=0
    g30: LineSegment StartX=-8 StartY=3.5 StartZ=0 EndX=-11.0311 EndY=1.75 EndZ=0
    g31: LineSegment StartX=-11.0311 StartY=1.75 StartZ=0 EndX=-11.0311 EndY=-1.75 EndZ=0
    g32: LineSegment StartX=-11.0311 StartY=-1.75 StartZ=0 EndX=-8 EndY=-3.5 EndZ=0
    g33: LineSegment StartX=-8 StartY=-3.5 StartZ=0 EndX=-4.96891 EndY=-1.75 EndZ=0
    g34: Circle [constr] CenterX=-8 CenterY=0 CenterZ=0 NormalX=0 NormalY=0 NormalZ=1 AngleXU=0 Radius=3.5
    g35: LineSegment StartX=-4.03109 StartY=-3.5 StartZ=0 EndX=-7.06218 EndY=-5.25 EndZ=0
    g36: LineSegment StartX=-7.06218 StartY=-5.25 StartZ=0 EndX=-7.06218 EndY=-8.75 EndZ=0
    g37: LineSegment StartX=-7.06218 StartY=-8.75 StartZ=0 EndX=-4.03109 EndY=-10.5 EndZ=0
    g38: LineSegment StartX=-4.03109 StartY=-10.5 StartZ=0 EndX=-1 EndY=-8.75 EndZ=0
    g39: LineSegment StartX=-1 StartY=-8.75 StartZ=0 EndX=-1 EndY=-5.25 EndZ=0
    g40: LineSegment StartX=-1 StartY=-5.25 StartZ=0 EndX=-4.03109 EndY=-3.5 EndZ=0
    g41: Circle [constr] CenterX=-4.03109 CenterY=-7 CenterZ=0 NormalX=0 NormalY=0 NormalZ=1 AngleXU=0 Radius=3.5
    g42: LineSegment StartX=4.03109 StartY=-3.5 StartZ=0 EndX=1 EndY=-5.25 EndZ=0
    g43: LineSegment StartX=1 StartY=-5.25 StartZ=0 EndX=1 EndY=-8.75 EndZ=0
    g44: LineSegment StartX=1 StartY=-8.75 StartZ=0 EndX=4.03109 EndY=-10.5 EndZ=0
    g45: LineSegment StartX=4.03109 StartY=-10.5 StartZ=0 EndX=7.06218 EndY=-8.75 EndZ=0
    g46: LineSegment StartX=7.06218 StartY=-8.75 StartZ=0 EndX=7.06218 EndY=-5.25 EndZ=0
    g47: LineSegment StartX=7.06218 StartY=-5.25 StartZ=0 EndX=4.03109 EndY=-3.5 EndZ=0
    g48: Circle [constr] CenterX=4.03109 CenterY=-7 CenterZ=0 NormalX=0 NormalY=0 NormalZ=1 AngleXU=0 Radius=3.5
  constraints (117):
    c: Coincident(g0,g1)
    c: Coincident(g1,g2)
    c: Coincident(g2,g3)
    c: Coincident(g3,g4)
    c: Coincident(g4,g5)
    c: Coincident(g5,g0)
    c: Equal(g0, g1-g5) x5
    c: PointOnObject(g0,g6)
    c: PointOnObject(g1,g6)
    c: PointOnObject(g2,g6)
    c: PointOnObject(g3,g6)
    c: PointOnObject(g4,g6)
    c: PointOnObject(g5,g6)
    c: Coincident(g6,g-1)
    c: Diameter(g6) = 7
    c: PointOnObject(g0,g-2)
    c: Coincident(g7,g8)
    c: Coincident(g8,g9)
    c: Coincident(g9,g10)
    c: Coincident(g10,g11)
    c: Coincident(g11,g12)
    c: Coincident(g12,g7)
    c: Equal(g7, g8-g12) x5
    c: PointOnObject(g7,g13)
    c: PointOnObject(g8,g13)
    c: PointOnObject(g9,g13)
    c: PointOnObject(g10,g13)
    c: PointOnObject(g11,g13)
    c: PointOnObject(g12,g13)
    c: PointOnObject(g13,g-1)
    c: Diameter(g13) = 7
    c: Distance(g6,g13) = 8
    c: Horizontal(g0,g10)
    c: Coincident(g14,g15)
    c: Coincident(g15,g16)
    c: Coincident(g16,g17)
    c: Coincident(g17,g18)
    c: Coincident(g18,g19)
    c: Coincident(g19,g14)
    c: Equal(g14, g15-g19) x5
    c: PointOnObject(g14,g20)
    c: PointOnObject(g15,g20)
    c: PointOnObject(g16,g20)
    c: PointOnObject(g17,g20)
    c: PointOnObject(g18,g20)
    c: PointOnObject(g19,g20)
    c: Diameter(g20) = 7
    c: DistanceY(g-1,g20) = 7
    c: Vertical(g18)
    c: Distance(g17,g-2) = 1
    c: Coincident(g21,g22)
    c: Coincident(g22,g23)
    c: Coincident(g23,g24)
    c: Coincident(g24,g25)
    c: Coincident(g25,g26)
    c: Coincident(g26,g21)
    c: Equal(g21, g22-g26) x5
    c: PointOnObject(g21,g27)
    c: PointOnObject(g22,g27)
    c: PointOnObject(g23,g27)
    c: PointOnObject(g24,g27)
    c: PointOnObject(g25,g27)
    c: PointOnObject(g26,g27)
    c: Diameter(g27) = 7
    c: DistanceY(g-1,g27) = 7
    c: DistanceX(g21,g-1) = 1
    c: Vertical(g21)
    c: Coincident(g28,g29)
    c: Coincident(g29,g30)
    c: Coincident(g30,g31)
    c: Coincident(g31,g32)
    c: Coincident(g32,g33)
    c: Coincident(g33,g28)
    c: Equal(g28, g29-g33) x5
    c: PointOnObject(g28,g34)
    c: PointOnObject(g29,g34)
    c: PointOnObject(g30,g34)
    c: PointOnObject(g31,g34)
    c: PointOnObject(g32,g34)
    c: PointOnObject(g33,g34)
    c: PointOnObject(g34,g-1)
    c: Diameter(g34) = 7
    c: Vertical(g31)
    c: DistanceX(g34,g-1) = 8
    c: Coincident(g35,g36)
    c: Coincident(g36,g37)
    c: Coincident(g37,g38)
    c: Coincident(g38,g39)
    c: Coincident(g39,g40)
    c: Coincident(g40,g35)
    c: Equal(g35, g36-g40) x5
    c: PointOnObject(g35,g41)
    c: PointOnObject(g36,g41)
    c: PointOnObject(g37,g41)
    c: PointOnObject(g38,g41)
    c: PointOnObject(g39,g41)
    c: PointOnObject(g40,g41)
    c: Coincident(g42,g43)
    c: Coincident(g43,g44)
    c: Coincident(g44,g45)
    c: Coincident(g45,g46)
    c: Coincident(g46,g47)
    c: Coincident(g47,g42)
    c: Equal(g42, g43-g47) x5
    c: PointOnObject(g42,g48)
    c: PointOnObject(g43,g48)
    c: PointOnObject(g44,g48)
    c: PointOnObject(g45,g48)
    c: PointOnObject(g46,g48)
    c: PointOnObject(g47,g48)
    c: Equal(g41,g48)
    c: Diameter(g41) = 7
    c: Vertical(g39)
    c: Vertical(g43)
    c: Distance(g-2,g39) = 1
    c: Symmetric(g38,g43,g-2)
    c: Distance(g41,g-1) = 7
FEATURE [Part::Extrusion] Extrude550  label="hex165"
  Base = -> Sketch558
  Dir = (0,-1,2e-16)
  DirMode = 2
  FaceMakerClass = Part::FaceMakerBullseye
  FaceMakerMode = 3
  LengthFwd = 10
  LengthRev = 0
  Placement = pos=(68,0,77) rot=(0,0,1;0rad)
  Solid = true
  Symmetric = false
FEATURE [Sketcher::SketchObject] Sketch559
  ArcFitTolerance = 1e-06
  FullyConstrained = true
  MakeInternals = false
  Placement = pos=(0,0,0) rot=(1,0,0;1.5708rad)
  sketch-geometry (49):
    g0: LineSegment StartX=1e-16 StartY=3.5 StartZ=0 EndX=-3.03109 EndY=1.75 EndZ=0
    g1: LineSegment StartX=-3.03109 StartY=1.75 StartZ=0 EndX=-3.03109 EndY=-1.75 EndZ=0
    g2: LineSegment StartX=-3.03109 StartY=-1.75 StartZ=0 EndX=-1e-16 EndY=-3.5 EndZ=0
    g3: LineSegment StartX=-1e-16 StartY=-3.5 StartZ=0 EndX=3.03109 EndY=-1.75 EndZ=0
    g4: LineSegment StartX=3.03109 StartY=-1.75 StartZ=0 EndX=3.03109 EndY=1.75 EndZ=0
    g5: LineSegment StartX=3.03109 StartY=1.75 StartZ=0 EndX=1e-16 EndY=3.5 EndZ=0
    g6: Circle [constr] CenterX=0 CenterY=0 CenterZ=0 NormalX=0 NormalY=0 NormalZ=1 AngleXU=0 Radius=3.5
    g7: LineSegment StartX=4.96892 StartY=-1.75002 StartZ=0 EndX=8.00002 EndY=-3.5 EndZ=0
    g8: LineSegment StartX=8.00002 StartY=-3.5 StartZ=0 EndX=11.0311 EndY=-1.74998 EndZ=0
    g9: LineSegment StartX=11.0311 StartY=-1.74998 StartZ=0 EndX=11.0311 EndY=1.75002 EndZ=0
    g10: LineSegment StartX=11.0311 StartY=1.75002 StartZ=0 EndX=7.99998 EndY=3.5 EndZ=0
    g11: LineSegment StartX=7.99998 StartY=3.5 StartZ=0 EndX=4.9689 EndY=1.74998 EndZ=0
    g12: LineSegment StartX=4.9689 StartY=1.74998 StartZ=0 EndX=4.96892 EndY=-1.75002 EndZ=0
    g13: Circle [constr] CenterX=8 CenterY=0 CenterZ=0 NormalX=0 NormalY=0 NormalZ=1 AngleXU=0 Radius=3.5
    g14: LineSegment StartX=4.03109 StartY=3.5 StartZ=0 EndX=7.06218 EndY=5.25 EndZ=0
    g15: LineSegment StartX=7.06218 StartY=5.25 StartZ=0 EndX=7.06218 EndY=8.75 EndZ=0
    g16: LineSegment StartX=7.06218 StartY=8.75 StartZ=0 EndX=4.03109 EndY=10.5 EndZ=0
    g17: LineSegment StartX=4.03109 StartY=10.5 StartZ=0 EndX=1 EndY=8.75 EndZ=0
    g18: LineSegment StartX=1 StartY=8.75 StartZ=0 EndX=1 EndY=5.25 EndZ=0
    g19: LineSegment StartX=1 StartY=5.25 StartZ=0 EndX=4.03109 EndY=3.5 EndZ=0
    g20: Circle [constr] CenterX=4.03109 CenterY=7 CenterZ=0 NormalX=0 NormalY=0 NormalZ=1 AngleXU=0 Radius=3.5
    g21: LineSegment StartX=-1 StartY=5.25 StartZ=0 EndX=-1 EndY=8.75 EndZ=0
    g22: LineSegment StartX=-1 StartY=8.75 StartZ=0 EndX=-4.03109 EndY=10.5 EndZ=0
    g23: LineSegment StartX=-4.03109 StartY=10.5 StartZ=0 EndX=-7.06218 EndY=8.75 EndZ=0
    g24: LineSegment StartX=-7.06218 StartY=8.75 StartZ=0 EndX=-7.06218 EndY=5.25 EndZ=0
    g25: LineSegment StartX=-7.06218 StartY=5.25 StartZ=0 EndX=-4.03109 EndY=3.5 EndZ=0
    g26: LineSegment StartX=-4.03109 StartY=3.5 StartZ=0 EndX=-1 EndY=5.25 EndZ=0
    g27: Circle [constr] CenterX=-4.03109 CenterY=7 CenterZ=0 NormalX=0 NormalY=0 NormalZ=1 AngleXU=0 Radius=3.5
    g28: LineSegment StartX=-4.96891 StartY=-1.75 StartZ=0 EndX=-4.96891 EndY=1.75 EndZ=0
    g29: LineSegment StartX=-4.96891 StartY=1.75 StartZ=0 EndX=-8 EndY=3.5 EndZ=0
    g30: LineSegment StartX=-8 StartY=3.5 StartZ=0 EndX=-11.0311 EndY=1.75 EndZ=0
    g31: LineSegment StartX=-11.0311 StartY=1.75 StartZ=0 EndX=-11.0311 EndY=-1.75 EndZ=0
    g32: LineSegment StartX=-11.0311 StartY=-1.75 StartZ=0 EndX=-8 EndY=-3.5 EndZ=0
    g33: LineSegment StartX=-8 StartY=-3.5 StartZ=0 EndX=-4.96891 EndY=-1.75 EndZ=0
    g34: Circle [constr] CenterX=-8 CenterY=0 CenterZ=0 NormalX=0 NormalY=0 NormalZ=1 AngleXU=0 Radius=3.5
    g35: LineSegment StartX=-4.03109 StartY=-3.5 StartZ=0 EndX=-7.06218 EndY=-5.25 EndZ=0
    g36: LineSegment StartX=-7.06218 StartY=-5.25 StartZ=0 EndX=-7.06218 EndY=-8.75 EndZ=0
    g37: LineSegment StartX=-7.06218 StartY=-8.75 StartZ=0 EndX=-4.03109 EndY=-10.5 EndZ=0
    g38: LineSegment StartX=-4.03109 StartY=-10.5 StartZ=0 EndX=-1 EndY=-8.75 EndZ=0
    g39: LineSegment StartX=-1 StartY=-8.75 StartZ=0 EndX=-1 EndY=-5.25 EndZ=0
    g40: LineSegment StartX=-1 StartY=-5.25 StartZ=0 EndX=-4.03109 EndY=-3.5 EndZ=0
    g41: Circle [constr] CenterX=-4.03109 CenterY=-7 CenterZ=0 NormalX=0 NormalY=0 NormalZ=1 AngleXU=0 Radius=3.5
    g42: LineSegment StartX=4.03109 StartY=-3.5 StartZ=0 EndX=1 EndY=-5.25 EndZ=0
    g43: LineSegment StartX=1 StartY=-5.25 StartZ=0 EndX=1 EndY=-8.75 EndZ=0
    g44: LineSegment StartX=1 StartY=-8.75 StartZ=0 EndX=4.03109 EndY=-10.5 EndZ=0
    g45: LineSegment StartX=4.03109 StartY=-10.5 StartZ=0 EndX=7.06218 EndY=-8.75 EndZ=0
    g46: LineSegment StartX=7.06218 StartY=-8.75 StartZ=0 EndX=7.06218 EndY=-5.25 EndZ=0
    g47: LineSegment StartX=7.06218 StartY=-5.25 StartZ=0 EndX=4.03109 EndY=-3.5 EndZ=0
    g48: Circle [constr] CenterX=4.03109 CenterY=-7 CenterZ=0 NormalX=0 NormalY=0 NormalZ=1 AngleXU=0 Radius=3.5
  constraints (117):
    c: Coincident(g0,g1)
    c: Coincident(g1,g2)
    c: Coincident(g2,g3)
    c: Coincident(g3,g4)
    c: Coincident(g4,g5)
    c: Coincident(g5,g0)
    c: Equal(g0, g1-g5) x5
    c: PointOnObject(g0,g6)
    c: PointOnObject(g1,g6)
    c: PointOnObject(g2,g6)
    c: PointOnObject(g3,g6)
    c: PointOnObject(g4,g6)
    c: PointOnObject(g5,g6)
    c: Coincident(g6,g-1)
    c: Diameter(g6) = 7
    c: PointOnObject(g0,g-2)
    c: Coincident(g7,g8)
    c: Coincident(g8,g9)
    c: Coincident(g9,g10)
    c: Coincident(g10,g11)
    c: Coincident(g11,g12)
    c: Coincident(g12,g7)
    c: Equal(g7, g8-g12) x5
    c: PointOnObject(g7,g13)
    c: PointOnObject(g8,g13)
    c: PointOnObject(g9,g13)
    c: PointOnObject(g10,g13)
    c: PointOnObject(g11,g13)
    c: PointOnObject(g12,g13)
    c: PointOnObject(g13,g-1)
    c: Diameter(g13) = 7
    c: Distance(g6,g13) = 8
    c: Horizontal(g0,g10)
    c: Coincident(g14,g15)
    c: Coincident(g15,g16)
    c: Coincident(g16,g17)
    c: Coincident(g17,g18)
    c: Coincident(g18,g19)
    c: Coincident(g19,g14)
    c: Equal(g14, g15-g19) x5
    c: PointOnObject(g14,g20)
    c: PointOnObject(g15,g20)
    c: PointOnObject(g16,g20)
    c: PointOnObject(g17,g20)
    c: PointOnObject(g18,g20)
    c: PointOnObject(g19,g20)
    c: Diameter(g20) = 7
    c: DistanceY(g-1,g20) = 7
    c: Vertical(g18)
    c: Distance(g17,g-2) = 1
    c: Coincident(g21,g22)
    c: Coincident(g22,g23)
    c: Coincident(g23,g24)
    c: Coincident(g24,g25)
    c: Coincident(g25,g26)
    c: Coincident(g26,g21)
    c: Equal(g21, g22-g26) x5
    c: PointOnObject(g21,g27)
    c: PointOnObject(g22,g27)
    c: PointOnObject(g23,g27)
    c: PointOnObject(g24,g27)
    c: PointOnObject(g25,g27)
    c: PointOnObject(g26,g27)
    c: Diameter(g27) = 7
    c: DistanceY(g-1,g27) = 7
    c: DistanceX(g21,g-1) = 1
    c: Vertical(g21)
    c: Coincident(g28,g29)
    c: Coincident(g29,g30)
    c: Coincident(g30,g31)
    c: Coincident(g31,g32)
    c: Coincident(g32,g33)
    c: Coincident(g33,g28)
    c: Equal(g28, g29-g33) x5
    c: PointOnObject(g28,g34)
    c: PointOnObject(g29,g34)
    c: PointOnObject(g30,g34)
    c: PointOnObject(g31,g34)
    c: PointOnObject(g32,g34)
    c: PointOnObject(g33,g34)
    c: PointOnObject(g34,g-1)
    c: Diameter(g34) = 7
    c: Vertical(g31)
    c: DistanceX(g34,g-1) = 8
    c: Coincident(g35,g36)
    c: Coincident(g36,g37)
    c: Coincident(g37,g38)
    c: Coincident(g38,g39)
    c: Coincident(g39,g40)
    c: Coincident(g40,g35)
    c: Equal(g35, g36-g40) x5
    c: PointOnObject(g35,g41)
    c: PointOnObject(g36,g41)
    c: PointOnObject(g37,g41)
    c: PointOnObject(g38,g41)
    c: PointOnObject(g39,g41)
    c: PointOnObject(g40,g41)
    c: Coincident(g42,g43)
    c: Coincident(g43,g44)
    c: Coincident(g44,g45)
    c: Coincident(g45,g46)
    c: Coincident(g46,g47)
    c: Coincident(g47,g42)
    c: Equal(g42, g43-g47) x5
    c: PointOnObject(g42,g48)
    c: PointOnObject(g43,g48)
    c: PointOnObject(g44,g48)
    c: PointOnObject(g45,g48)
    c: PointOnObject(g46,g48)
    c: PointOnObject(g47,g48)
    c: Equal(g41,g48)
    c: Diameter(g41) = 7
    c: Vertical(g39)
    c: Vertical(g43)
    c: Distance(g-2,g39) = 1
    c: Symmetric(g38,g43,g-2)
    c: Distance(g41,g-1) = 7
FEATURE [Part::Extrusion] Extrude551  label="hex166"
  Base = -> Sketch559
  Dir = (0,-1,2e-16)
  DirMode = 2
  FaceMakerClass = Part::FaceMakerBullseye
  FaceMakerMode = 3
  LengthFwd = 10
  LengthRev = 0
  Placement = pos=(12,0,-119) rot=(0,0,1;0rad)
  Solid = true
  Symmetric = false
FEATURE [Sketcher::SketchObject] Sketch560
  ArcFitTolerance = 1e-06
  FullyConstrained = true
  MakeInternals = false
  Placement = pos=(0,0,0) rot=(1,0,0;1.5708rad)
  sketch-geometry (49):
    g0: LineSegment StartX=1e-16 StartY=3.5 StartZ=0 EndX=-3.03109 EndY=1.75 EndZ=0
    g1: LineSegment StartX=-3.03109 StartY=1.75 StartZ=0 EndX=-3.03109 EndY=-1.75 EndZ=0
    g2: LineSegment StartX=-3.03109 StartY=-1.75 StartZ=0 EndX=-1e-16 EndY=-3.5 EndZ=0
    g3: LineSegment StartX=-1e-16 StartY=-3.5 StartZ=0 EndX=3.03109 EndY=-1.75 EndZ=0
    g4: LineSegment StartX=3.03109 StartY=-1.75 StartZ=0 EndX=3.03109 EndY=1.75 EndZ=0
    g5: LineSegment StartX=3.03109 StartY=1.75 StartZ=0 EndX=1e-16 EndY=3.5 EndZ=0
    g6: Circle [constr] CenterX=0 CenterY=0 CenterZ=0 NormalX=0 NormalY=0 NormalZ=1 AngleXU=0 Radius=3.5
    g7: LineSegment StartX=4.96892 StartY=-1.75002 StartZ=0 EndX=8.00002 EndY=-3.5 EndZ=0
    g8: LineSegment StartX=8.00002 StartY=-3.5 StartZ=0 EndX=11.0311 EndY=-1.74998 EndZ=0
    g9: LineSegment StartX=11.0311 StartY=-1.74998 StartZ=0 EndX=11.0311 EndY=1.75002 EndZ=0
    g10: LineSegment StartX=11.0311 StartY=1.75002 StartZ=0 EndX=7.99998 EndY=3.5 EndZ=0
    g11: LineSegment StartX=7.99998 StartY=3.5 StartZ=0 EndX=4.9689 EndY=1.74998 EndZ=0
    g12: LineSegment StartX=4.9689 StartY=1.74998 StartZ=0 EndX=4.96892 EndY=-1.75002 EndZ=0
    g13: Circle [constr] CenterX=8 CenterY=0 CenterZ=0 NormalX=0 NormalY=0 NormalZ=1 AngleXU=0 Radius=3.5
    g14: LineSegment StartX=4.03109 StartY=3.5 StartZ=0 EndX=7.06218 EndY=5.25 EndZ=0
    g15: LineSegment StartX=7.06218 StartY=5.25 StartZ=0 EndX=7.06218 EndY=8.75 EndZ=0
    g16: LineSegment StartX=7.06218 StartY=8.75 StartZ=0 EndX=4.03109 EndY=10.5 EndZ=0
    g17: LineSegment StartX=4.03109 StartY=10.5 StartZ=0 EndX=1 EndY=8.75 EndZ=0
    g18: LineSegment StartX=1 StartY=8.75 StartZ=0 EndX=1 EndY=5.25 EndZ=0
    g19: LineSegment StartX=1 StartY=5.25 StartZ=0 EndX=4.03109 EndY=3.5 EndZ=0
    g20: Circle [constr] CenterX=4.03109 CenterY=7 CenterZ=0 NormalX=0 NormalY=0 NormalZ=1 AngleXU=0 Radius=3.5
    g21: LineSegment StartX=-1 StartY=5.25 StartZ=0 EndX=-1 EndY=8.75 EndZ=0
    g22: LineSegment StartX=-1 StartY=8.75 StartZ=0 EndX=-4.03109 EndY=10.5 EndZ=0
    g23: LineSegment StartX=-4.03109 StartY=10.5 StartZ=0 EndX=-7.06218 EndY=8.75 EndZ=0
    g24: LineSegment StartX=-7.06218 StartY=8.75 StartZ=0 EndX=-7.06218 EndY=5.25 EndZ=0
    g25: LineSegment StartX=-7.06218 StartY=5.25 StartZ=0 EndX=-4.03109 EndY=3.5 EndZ=0
    g26: LineSegment StartX=-4.03109 StartY=3.5 StartZ=0 EndX=-1 EndY=5.25 EndZ=0
    g27: Circle [constr] CenterX=-4.03109 CenterY=7 CenterZ=0 NormalX=0 NormalY=0 NormalZ=1 AngleXU=0 Radius=3.5
    g28: LineSegment StartX=-4.96891 StartY=-1.75 StartZ=0 EndX=-4.96891 EndY=1.75 EndZ=0
    g29: LineSegment StartX=-4.96891 StartY=1.75 StartZ=0 EndX=-8 EndY=3.5 EndZ=0
    g30: LineSegment StartX=-8 StartY=3.5 StartZ=0 EndX=-11.0311 EndY=1.75 EndZ=0
    g31: LineSegment StartX=-11.0311 StartY=1.75 StartZ=0 EndX=-11.0311 EndY=-1.75 EndZ=0
    g32: LineSegment StartX=-11.0311 StartY=-1.75 StartZ=0 EndX=-8 EndY=-3.5 EndZ=0
    g33: LineSegment StartX=-8 StartY=-3.5 StartZ=0 EndX=-4.96891 EndY=-1.75 EndZ=0
    g34: Circle [constr] CenterX=-8 CenterY=0 CenterZ=0 NormalX=0 NormalY=0 NormalZ=1 AngleXU=0 Radius=3.5
    g35: LineSegment StartX=-4.03109 StartY=-3.5 StartZ=0 EndX=-7.06218 EndY=-5.25 EndZ=0
    g36: LineSegment StartX=-7.06218 StartY=-5.25 StartZ=0 EndX=-7.06218 EndY=-8.75 EndZ=0
    g37: LineSegment StartX=-7.06218 StartY=-8.75 StartZ=0 EndX=-4.03109 EndY=-10.5 EndZ=0
    g38: LineSegment StartX=-4.03109 StartY=-10.5 StartZ=0 EndX=-1 EndY=-8.75 EndZ=0
    g39: LineSegment StartX=-1 StartY=-8.75 StartZ=0 EndX=-1 EndY=-5.25 EndZ=0
    g40: LineSegment StartX=-1 StartY=-5.25 StartZ=0 EndX=-4.03109 EndY=-3.5 EndZ=0
    g41: Circle [constr] CenterX=-4.03109 CenterY=-7 CenterZ=0 NormalX=0 NormalY=0 NormalZ=1 AngleXU=0 Radius=3.5
    g42: LineSegment StartX=4.03109 StartY=-3.5 StartZ=0 EndX=1 EndY=-5.25 EndZ=0
    g43: LineSegment StartX=1 StartY=-5.25 StartZ=0 EndX=1 EndY=-8.75 EndZ=0
    g44: LineSegment StartX=1 StartY=-8.75 StartZ=0 EndX=4.03109 EndY=-10.5 EndZ=0
    g45: LineSegment StartX=4.03109 StartY=-10.5 StartZ=0 EndX=7.06218 EndY=-8.75 EndZ=0
    g46: LineSegment StartX=7.06218 StartY=-8.75 StartZ=0 EndX=7.06218 EndY=-5.25 EndZ=0
    g47: LineSegment StartX=7.06218 StartY=-5.25 StartZ=0 EndX=4.03109 EndY=-3.5 EndZ=0
    g48: Circle [constr] CenterX=4.03109 CenterY=-7 CenterZ=0 NormalX=0 NormalY=0 NormalZ=1 AngleXU=0 Radius=3.5
  constraints (117):
    c: Coincident(g0,g1)
    c: Coincident(g1,g2)
    c: Coincident(g2,g3)
    c: Coincident(g3,g4)
    c: Coincident(g4,g5)
    c: Coincident(g5,g0)
    c: Equal(g0, g1-g5) x5
    c: PointOnObject(g0,g6)
    c: PointOnObject(g1,g6)
    c: PointOnObject(g2,g6)
    c: PointOnObject(g3,g6)
    c: PointOnObject(g4,g6)
    c: PointOnObject(g5,g6)
    c: Coincident(g6,g-1)
    c: Diameter(g6) = 7
    c: PointOnObject(g0,g-2)
    c: Coincident(g7,g8)
    c: Coincident(g8,g9)
    c: Coincident(g9,g10)
    c: Coincident(g10,g11)
    c: Coincident(g11,g12)
    c: Coincident(g12,g7)
    c: Equal(g7, g8-g12) x5
    c: PointOnObject(g7,g13)
    c: PointOnObject(g8,g13)
    c: PointOnObject(g9,g13)
    c: PointOnObject(g10,g13)
    c: PointOnObject(g11,g13)
    c: PointOnObject(g12,g13)
    c: PointOnObject(g13,g-1)
    c: Diameter(g13) = 7
    c: Distance(g6,g13) = 8
    c: Horizontal(g0,g10)
    c: Coincident(g14,g15)
    c: Coincident(g15,g16)
    c: Coincident(g16,g17)
    c: Coincident(g17,g18)
    c: Coincident(g18,g19)
    c: Coincident(g19,g14)
    c: Equal(g14, g15-g19) x5
    c: PointOnObject(g14,g20)
    c: PointOnObject(g15,g20)
    c: PointOnObject(g16,g20)
    c: PointOnObject(g17,g20)
    c: PointOnObject(g18,g20)
    c: PointOnObject(g19,g20)
    c: Diameter(g20) = 7
    c: DistanceY(g-1,g20) = 7
    c: Vertical(g18)
    c: Distance(g17,g-2) = 1
    c: Coincident(g21,g22)
    c: Coincident(g22,g23)
    c: Coincident(g23,g24)
    c: Coincident(g24,g25)
    c: Coincident(g25,g26)
    c: Coincident(g26,g21)
    c: Equal(g21, g22-g26) x5
    c: PointOnObject(g21,g27)
    c: PointOnObject(g22,g27)
    c: PointOnObject(g23,g27)
    c: PointOnObject(g24,g27)
    c: PointOnObject(g25,g27)
    c: PointOnObject(g26,g27)
    c: Diameter(g27) = 7
    c: DistanceY(g-1,g27) = 7
    c: DistanceX(g21,g-1) = 1
    c: Vertical(g21)
    c: Coincident(g28,g29)
    c: Coincident(g29,g30)
    c: Coincident(g30,g31)
    c: Coincident(g31,g32)
    c: Coincident(g32,g33)
    c: Coincident(g33,g28)
    c: Equal(g28, g29-g33) x5
    c: PointOnObject(g28,g34)
    c: PointOnObject(g29,g34)
    c: PointOnObject(g30,g34)
    c: PointOnObject(g31,g34)
    c: PointOnObject(g32,g34)
    c: PointOnObject(g33,g34)
    c: PointOnObject(g34,g-1)
    c: Diameter(g34) = 7
    c: Vertical(g31)
    c: DistanceX(g34,g-1) = 8
    c: Coincident(g35,g36)
    c: Coincident(g36,g37)
    c: Coincident(g37,g38)
    c: Coincident(g38,g39)
    c: Coincident(g39,g40)
    c: Coincident(g40,g35)
    c: Equal(g35, g36-g40) x5
    c: PointOnObject(g35,g41)
    c: PointOnObject(g36,g41)
    c: PointOnObject(g37,g41)
    c: PointOnObject(g38,g41)
    c: PointOnObject(g39,g41)
    c: PointOnObject(g40,g41)
    c: Coincident(g42,g43)
    c: Coincident(g43,g44)
    c: Coincident(g44,g45)
    c: Coincident(g45,g46)
    c: Coincident(g46,g47)
    c: Coincident(g47,g42)
    c: Equal(g42, g43-g47) x5
    c: PointOnObject(g42,g48)
    c: PointOnObject(g43,g48)
    c: PointOnObject(g44,g48)
    c: PointOnObject(g45,g48)
    c: PointOnObject(g46,g48)
    c: PointOnObject(g47,g48)
    c: Equal(g41,g48)
    c: Diameter(g41) = 7
    c: Vertical(g39)
    c: Vertical(g43)
    c: Distance(g-2,g39) = 1
    c: Symmetric(g38,g43,g-2)
    c: Distance(g41,g-1) = 7
FEATURE [Part::Extrusion] Extrude552  label="hex167"
  Base = -> Sketch560
  Dir = (0,-1,2e-16)
  DirMode = 2
  FaceMakerClass = Part::FaceMakerBullseye
  FaceMakerMode = 3
  LengthFwd = 10
  LengthRev = 0
  Placement = pos=(-12,0,-119) rot=(0,0,1;0rad)
  Solid = true
  Symmetric = false
FEATURE [Part::MultiFuse] Fusion550
  Refine = true
  Shapes = -> [Extrude536,Extrude537,Extrude538,Extrude539,Extrude540,Extrude541,Extrude542,Extrude543,Extrude544,Extrude545,Extrude546,Extrude547,Extrude548,Extrude549,Extrude550,Extrude551,Extrude552]
FEATURE [Sketcher::SketchObject] Sketch561
  ArcFitTolerance = 1e-06
  FullyConstrained = true
  MakeInternals = false
  Placement = pos=(0,0,0) rot=(1,0,0;1.5708rad)
  sketch-geometry (4):
    g0: LineSegment StartX=-160.43 StartY=139.16 StartZ=0 EndX=-160.43 EndY=-139.16 EndZ=0
    g1: LineSegment StartX=-160.43 StartY=-139.16 StartZ=0 EndX=160.43 EndY=-139.16 EndZ=0
    g2: LineSegment StartX=160.43 StartY=-139.16 StartZ=0 EndX=160.43 EndY=139.16 EndZ=0
    g3: LineSegment StartX=160.43 StartY=139.16 StartZ=0 EndX=-160.43 EndY=139.16 EndZ=0
  constraints (10):
    c: Coincident(g0,g1)
    c: Coincident(g1,g2)
    c: Coincident(g2,g3)
    c: Coincident(g3,g0)
    c: Vertical(g2)
    c: Horizontal(g1)
    c: Symmetric(g0,g2,g-2)
    c: Symmetric(g0,g0,g-1)
    c: Distance(g0,g-1) = 139.16
    c: DistanceX(g0,g-1) = 160.43
FEATURE [Part::MultiFuse] Fusion551  label="hexAll"
  Refine = true
  Shapes = -> [Fusion547,Fusion548,Fusion549,Fusion550]
FEATURE [Part::Extrusion] Extrude553  label="rect"
  Base = -> Sketch561
  Dir = (0,-1,2e-16)
  DirMode = 2
  FaceMakerClass = Part::FaceMakerBullseye
  FaceMakerMode = 3
  LengthFwd = 10
  LengthRev = 0
  Solid = true
  Symmetric = false
FEATURE [Part::Cut] Cut003  label="hexcut"
  Base = -> Extrude553
  Refine = true
  Tool = -> Fusion551
FEATURE [Sketcher::SketchObject] Sketch562
  ArcFitTolerance = 1e-06
  FullyConstrained = true
  MakeInternals = false
  Placement = pos=(0,0,0) rot=(1,0,0;1.5708rad)
  sketch-geometry (11):
    g0: LineSegment StartX=-179.57 StartY=155.64 StartZ=0 EndX=-179.57 EndY=-155.64 EndZ=0
    g1: LineSegment StartX=-179.57 StartY=-155.64 StartZ=0 EndX=179.57 EndY=-155.64 EndZ=0
    g2: LineSegment StartX=179.57 StartY=-155.64 StartZ=0 EndX=179.57 EndY=155.64 EndZ=0
    g3: LineSegment StartX=179.57 StartY=155.64 StartZ=0 EndX=-179.57 EndY=155.64 EndZ=0
    g4: LineSegment StartX=-2.6e-15 StartY=129 StartZ=0 EndX=-111.717 EndY=64.5 EndZ=0
    g5: LineSegment StartX=-111.717 StartY=64.5 StartZ=0 EndX=-111.717 EndY=-64.5 EndZ=0
    g6: LineSegment StartX=-111.717 StartY=-64.5 StartZ=0 EndX=-4.1519e-12 EndY=-129 EndZ=0
    g7: LineSegment StartX=-4.1519e-12 StartY=-129 StartZ=0 EndX=111.717 EndY=-64.5 EndZ=0
    g8: LineSegment StartX=111.717 StartY=-64.5 StartZ=0 EndX=111.717 EndY=64.5 EndZ=0
    g9: LineSegment StartX=111.717 StartY=64.5 StartZ=0 EndX=-2.6e-15 EndY=129 EndZ=0
    g10: Circle [constr] CenterX=0 CenterY=0 CenterZ=0 NormalX=0 NormalY=0 NormalZ=1 AngleXU=0 Radius=129
  constraints (26):
    c: Coincident(g0,g1)
    c: Coincident(g1,g2)
    c: Coincident(g2,g3)
    c: Coincident(g3,g0)
    c: Vertical(g2)
    c: Horizontal(g1)
    c: Symmetric(g0,g0,g-1)
    c: Symmetric(g0,g2,g-2)
    c: DistanceX(g0,g-1) = 179.57
    c: DistanceY(g0,g-1) = 155.64
    c: Coincident(g4,g5)
    c: Coincident(g5,g6)
    c: Coincident(g6,g7)
    c: Coincident(g7,g8)
    c: Coincident(g8,g9)
    c: Coincident(g9,g4)
    c: Equal(g4, g5-g9) x5
    c: PointOnObject(g4,g10)
    c: PointOnObject(g5,g10)
    c: PointOnObject(g6,g10)
    c: PointOnObject(g7,g10)
    c: PointOnObject(g8,g10)
    c: PointOnObject(g9,g10)
    c: Coincident(g10,g-1)
    c: Diameter(g10) = 258
    c: PointOnObject(g4,g-2)
FEATURE [Part::Extrusion] Extrude554
  Base = -> Sketch562
  Dir = (0,-1,2e-16)
  DirMode = 2
  FaceMakerClass = Part::FaceMakerBullseye
  FaceMakerMode = 3
  LengthFwd = 10
  LengthRev = 0
  Solid = true
  Symmetric = false
FEATURE [Part::Cut] Cut004  label="mesh"
  Base = -> Cut003
  Placement = pos=(0,-137,0) rot=(0,0,1;0rad)
  Refine = true
  Tool = -> Extrude554
FEATURE [Sketcher::SketchObject] Sketch563
  ArcFitTolerance = 1e-06
  FullyConstrained = true
  MakeInternals = false
  Placement = pos=(0,0,0) rot=(1,0,0;1.5708rad)
  sketch-geometry (14):
    g0: LineSegment StartX=2e-16 StartY=122 StartZ=0 EndX=-105.655 EndY=61 EndZ=0
    g1: LineSegment StartX=-105.655 StartY=61 StartZ=0 EndX=-105.655 EndY=-61 EndZ=0
    g2: LineSegment StartX=-105.655 StartY=-61 StartZ=0 EndX=-1.5e-15 EndY=-122 EndZ=0
    g3: LineSegment StartX=-1.5e-15 StartY=-122 StartZ=0 EndX=105.655 EndY=-61 EndZ=0
    g4: LineSegment StartX=105.655 StartY=-61 StartZ=0 EndX=105.655 EndY=61 EndZ=0
    g5: LineSegment StartX=105.655 StartY=61 StartZ=0 EndX=2e-16 EndY=122 EndZ=0
    g6: Circle [constr] CenterX=0 CenterY=0 CenterZ=0 NormalX=0 NormalY=0 NormalZ=1 AngleXU=0 Radius=122
    g7: LineSegment StartX=6.6e-15 StartY=129.5 StartZ=0 EndX=-112.15 EndY=64.75 EndZ=0
    g8: LineSegment StartX=-112.15 StartY=64.75 StartZ=0 EndX=-112.15 EndY=-64.75 EndZ=0
    g9: LineSegment StartX=-112.15 StartY=-64.75 StartZ=0 EndX=-1.956e-13 EndY=-129.5 EndZ=0
    g10: LineSegment StartX=-1.956e-13 StartY=-129.5 StartZ=0 EndX=112.15 EndY=-64.75 EndZ=0
    g11: LineSegment StartX=112.15 StartY=-64.75 StartZ=0 EndX=112.15 EndY=64.75 EndZ=0
    g12: LineSegment StartX=112.15 StartY=64.75 StartZ=0 EndX=6.6e-15 EndY=129.5 EndZ=0
    g13: Circle [constr] CenterX=0 CenterY=0 CenterZ=0 NormalX=0 NormalY=0 NormalZ=1 AngleXU=0 Radius=129.5
  constraints (32):
    c: Coincident(g0,g1)
    c: Coincident(g1,g2)
    c: Coincident(g2,g3)
    c: Coincident(g3,g4)
    c: Coincident(g4,g5)
    c: Coincident(g5,g0)
    c: Equal(g0, g1-g5) x5
    c: PointOnObject(g0,g6)
    c: PointOnObject(g1,g6)
    c: PointOnObject(g2,g6)
    c: PointOnObject(g3,g6)
    c: PointOnObject(g4,g6)
    c: PointOnObject(g5,g6)
    c: Coincident(g6,g-1)
    c: PointOnObject(g5,g-2)
    c: Diameter(g6) = 244
    c: Coincident(g7,g8)
    c: Coincident(g8,g9)
    c: Coincident(g9,g10)
    c: Coincident(g10,g11)
    c: Coincident(g11,g12)
    c: Coincident(g12,g7)
    c: Equal(g7, g8-g12) x5
    c: PointOnObject(g7,g13)
    c: PointOnObject(g8,g13)
    c: PointOnObject(g9,g13)
    c: PointOnObject(g10,g13)
    c: PointOnObject(g11,g13)
    c: PointOnObject(g12,g13)
    c: Coincident(g13,g6)
    c: PointOnObject(g12,g-2)
    c: Diameter(g13) = 259
FEATURE [Part::Extrusion] Extrude555  label="hexMeshBorder"
  Base = -> Sketch563
  Dir = (0,-1,2e-16)
  DirMode = 2
  FaceMakerClass = Part::FaceMakerBullseye
  FaceMakerMode = 3
  LengthFwd = 10
  LengthRev = 0
  Placement = pos=(0,-137,0) rot=(0,0,1;0rad)
  Solid = true
  Symmetric = false
FEATURE [Part::MultiFuse] Fusion552  label="hexShellFused"
  Refine = true
  Shapes = -> [Extrude,Extrude385]
FEATURE [Part::MultiFuse] Fusion553  label="meshFused"
  Refine = true
  Shapes = -> [Extrude555,Cut004]
FEATURE [Part::MultiFuse] Fusion554
  Refine = true
  Shapes = -> [Cut002,Extrude384]
FEATURE [Sketcher::SketchObject] Sketch564
  ArcFitTolerance = 1e-06
  FullyConstrained = true
  MakeInternals = false
  Placement = pos=(0,0,0) rot=(1,0,0;1.5708rad)
  sketch-geometry (12):
    g0: Circle CenterX=-103.923 CenterY=60 CenterZ=0 NormalX=0 NormalY=0 NormalZ=1 AngleXU=0 Radius=5
    g1: Circle CenterX=0 CenterY=120 CenterZ=0 NormalX=0 NormalY=0 NormalZ=1 AngleXU=0 Radius=5
    g2: Circle CenterX=103.923 CenterY=60 CenterZ=0 NormalX=0 NormalY=0 NormalZ=1 AngleXU=0 Radius=5
    g3: Circle CenterX=103.923 CenterY=-60 CenterZ=0 NormalX=0 NormalY=0 NormalZ=1 AngleXU=0 Radius=5
    g4: Circle CenterX=0 CenterY=-120 CenterZ=0 NormalX=0 NormalY=0 NormalZ=1 AngleXU=0 Radius=5
    g5: Circle CenterX=-103.923 CenterY=-60 CenterZ=0 NormalX=0 NormalY=0 NormalZ=1 AngleXU=0 Radius=5
    g6: Circle CenterX=-103.923 CenterY=60 CenterZ=0 NormalX=0 NormalY=0 NormalZ=1 AngleXU=0 Radius=1.625
    g7: Circle CenterX=0 CenterY=120 CenterZ=0 NormalX=0 NormalY=0 NormalZ=1 AngleXU=0 Radius=1.625
    g8: Circle CenterX=103.923 CenterY=60 CenterZ=0 NormalX=0 NormalY=0 NormalZ=1 AngleXU=0 Radius=1.625
    g9: Circle CenterX=103.923 CenterY=-60 CenterZ=0 NormalX=0 NormalY=0 NormalZ=1 AngleXU=0 Radius=1.625
    g10: Circle CenterX=0 CenterY=-120 CenterZ=0 NormalX=0 NormalY=0 NormalZ=1 AngleXU=0 Radius=1.625
    g11: Circle CenterX=-103.923 CenterY=-60 CenterZ=0 NormalX=0 NormalY=0 NormalZ=1 AngleXU=0 Radius=1.625
  constraints (22):
    c: PointOnObject(g1,g-2)
    c: PointOnObject(g4,g-2)
    c: Equal(g0, g1-g5) x5
    c: Diameter(g0) = 10
    c: Coincident(g6,g0)
    c: Coincident(g7,g1)
    c: Coincident(g8,g2)
    c: Coincident(g9,g3)
    c: Coincident(g10,g4)
    c: Coincident(g11,g5)
    c: Equal(g6, g7-g11) x5
    c: Diameter(g6) = 3.25
    c: DistanceY(g-1,g1) = 120
    c: Distance(g-1,g0) = 120
    c: Distance(g0,g-1) = 60
    c: Distance(g2,g-1) = 120
    c: Distance(g2,g-1) = 60
    c: DistanceY(g4,g-1) = 120
    c: Distance(g3,g-1) = 60
    c: Distance(g5,g-1) = 120
    c: Distance(g5,g-1) = 60
    c: Distance(g3,g-1) = 120
FEATURE [Part::Extrusion] Extrude556  label="backm3"
  Base = -> Sketch564
  Dir = (0,-1,2e-16)
  DirMode = 2
  FaceMakerClass = Part::FaceMakerBullseye
  FaceMakerMode = 3
  LengthFwd = 40
  LengthRev = 0
  Placement = pos=(0,27,0) rot=(0,0,1;0rad)
  Solid = true
  Symmetric = false
FEATURE [Sketcher::SketchObject] Sketch565
  ArcFitTolerance = 1e-06
  FullyConstrained = true
  MakeInternals = false
  Placement = pos=(0,0,0) rot=(1,0,0;1.5708rad)
  sketch-geometry (12):
    g0: Circle CenterX=-103.923 CenterY=60 CenterZ=0 NormalX=0 NormalY=0 NormalZ=1 AngleXU=0 Radius=10
    g1: Circle CenterX=0 CenterY=120 CenterZ=0 NormalX=0 NormalY=0 NormalZ=1 AngleXU=0 Radius=10
    g2: Circle CenterX=103.923 CenterY=60 CenterZ=0 NormalX=0 NormalY=0 NormalZ=1 AngleXU=0 Radius=10
    g3: Circle CenterX=103.923 CenterY=-60 CenterZ=0 NormalX=0 NormalY=0 NormalZ=1 AngleXU=0 Radius=10
    g4: Circle CenterX=0 CenterY=-120 CenterZ=0 NormalX=0 NormalY=0 NormalZ=1 AngleXU=0 Radius=10
    g5: Circle CenterX=-103.923 CenterY=-60 CenterZ=0 NormalX=0 NormalY=0 NormalZ=1 AngleXU=0 Radius=10
    g6: Circle CenterX=-103.923 CenterY=60 CenterZ=0 NormalX=0 NormalY=0 NormalZ=1 AngleXU=0 Radius=6
    g7: Circle CenterX=0 CenterY=120 CenterZ=0 NormalX=0 NormalY=0 NormalZ=1 AngleXU=0 Radius=6
    g8: Circle CenterX=103.923 CenterY=60 CenterZ=0 NormalX=0 NormalY=0 NormalZ=1 AngleXU=0 Radius=6
    g9: Circle CenterX=103.923 CenterY=-60 CenterZ=0 NormalX=0 NormalY=0 NormalZ=1 AngleXU=0 Radius=6
    g10: Circle CenterX=0 CenterY=-120 CenterZ=0 NormalX=0 NormalY=0 NormalZ=1 AngleXU=0 Radius=6
    g11: Circle CenterX=-103.923 CenterY=-60 CenterZ=0 NormalX=0 NormalY=0 NormalZ=1 AngleXU=0 Radius=6
  constraints (22):
    c: PointOnObject(g1,g-2)
    c: PointOnObject(g4,g-2)
    c: Equal(g0, g1-g5) x5
    c: Diameter(g0) = 20
    c: Coincident(g6,g0)
    c: Coincident(g7,g1)
    c: Coincident(g8,g2)
    c: Coincident(g9,g3)
    c: Coincident(g10,g4)
    c: Coincident(g11,g5)
    c: Equal(g6, g7-g11) x5
    c: Diameter(g6) = 12
    c: DistanceY(g-1,g1) = 120
    c: Distance(g-1,g0) = 120
    c: Distance(g0,g-1) = 60
    c: Distance(g2,g-1) = 120
    c: Distance(g2,g-1) = 60
    c: DistanceY(g4,g-1) = 120
    c: Distance(g3,g-1) = 60
    c: Distance(g5,g-1) = 120
    c: Distance(g5,g-1) = 60
    c: Distance(g3,g-1) = 120
FEATURE [Part::Extrusion] Extrude557  label="hexm3"
  Base = -> Sketch565
  Dir = (0,-1,2e-16)
  DirMode = 2
  FaceMakerClass = Part::FaceMakerBullseye
  FaceMakerMode = 3
  LengthFwd = 23
  LengthRev = 0
  Solid = true
  Symmetric = false
FEATURE [Sketcher::SketchObject] Sketch566
  ArcFitTolerance = 1e-06
  FullyConstrained = true
  MakeInternals = false
  Placement = pos=(0,0,0) rot=(1,0,0;1.5708rad)
  sketch-geometry (12):
    g0: Circle CenterX=-103.923 CenterY=60 CenterZ=0 NormalX=0 NormalY=0 NormalZ=1 AngleXU=0 Radius=6
    g1: Circle CenterX=0 CenterY=120 CenterZ=0 NormalX=0 NormalY=0 NormalZ=1 AngleXU=0 Radius=6
    g2: Circle CenterX=103.923 CenterY=60 CenterZ=0 NormalX=0 NormalY=0 NormalZ=1 AngleXU=0 Radius=6
    g3: Circle CenterX=103.923 CenterY=-60 CenterZ=0 NormalX=0 NormalY=0 NormalZ=1 AngleXU=0 Radius=6
    g4: Circle CenterX=0 CenterY=-120 CenterZ=0 NormalX=0 NormalY=0 NormalZ=1 AngleXU=0 Radius=6
    g5: Circle CenterX=-103.923 CenterY=-60 CenterZ=0 NormalX=0 NormalY=0 NormalZ=1 AngleXU=0 Radius=6
    g6: Circle CenterX=-103.923 CenterY=60 CenterZ=0 NormalX=0 NormalY=0 NormalZ=1 AngleXU=0 Radius=1.625
    g7: Circle CenterX=0 CenterY=120 CenterZ=0 NormalX=0 NormalY=0 NormalZ=1 AngleXU=0 Radius=1.625
    g8: Circle CenterX=103.923 CenterY=60 CenterZ=0 NormalX=0 NormalY=0 NormalZ=1 AngleXU=0 Radius=1.625
    g9: Circle CenterX=103.923 CenterY=-60 CenterZ=0 NormalX=0 NormalY=0 NormalZ=1 AngleXU=0 Radius=1.625
    g10: Circle CenterX=0 CenterY=-120 CenterZ=0 NormalX=0 NormalY=0 NormalZ=1 AngleXU=0 Radius=1.625
    g11: Circle CenterX=-103.923 CenterY=-60 CenterZ=0 NormalX=0 NormalY=0 NormalZ=1 AngleXU=0 Radius=1.625
  constraints (22):
    c: PointOnObject(g1,g-2)
    c: PointOnObject(g4,g-2)
    c: Equal(g0, g1-g5) x5
    c: Diameter(g0) = 12
    c: Coincident(g6,g0)
    c: Coincident(g7,g1)
    c: Coincident(g8,g2)
    c: Coincident(g9,g3)
    c: Coincident(g10,g4)
    c: Coincident(g11,g5)
    c: Equal(g6, g7-g11) x5
    c: Diameter(g6) = 3.25
    c: DistanceY(g-1,g1) = 120
    c: Distance(g-1,g0) = 120
    c: Distance(g0,g-1) = 60
    c: Distance(g2,g-1) = 120
    c: Distance(g2,g-1) = 60
    c: DistanceY(g4,g-1) = 120
    c: Distance(g3,g-1) = 60
    c: Distance(g5,g-1) = 120
    c: Distance(g5,g-1) = 60
    c: Distance(g3,g-1) = 120
FEATURE [Part::Extrusion] Extrude558  label="hexm3Inner"
  Base = -> Sketch566
  Dir = (0,-1,2e-16)
  DirMode = 2
  FaceMakerClass = Part::FaceMakerBullseye
  FaceMakerMode = 3
  LengthFwd = 10
  LengthRev = 0
  Placement = pos=(0,-13,0) rot=(0,0,1;0rad)
  Solid = true
  Symmetric = false
FEATURE [Part::MultiFuse] Fusion555  label="hexM3"
  Refine = true
  Shapes = -> [Extrude557,Extrude558]
FEATURE [Part::MultiFuse] Fusion556  label="hexM3Fused"
  Refine = true
  Shapes = -> [Fusion552,Fusion555]
FEATURE [Part::MultiFuse] Fusion557  label="fusedBackEncloser"
  Refine = true
  Shapes = -> [Fusion554,Extrude556]
FEATURE [Sketcher::SketchObject] Sketch567
  ArcFitTolerance = 1e-06
  FullyConstrained = true
  MakeInternals = false
  Placement = pos=(0,0,0) rot=(0,0.707107,0.707107;3.14159rad)
  sketch-geometry (6):
    g0: LineSegment StartX=1e-15 StartY=-25 StartZ=0 EndX=21.65 EndY=-12.5011 EndZ=0
    g1: LineSegment StartX=21.65 StartY=-12.5011 StartZ=0 EndX=21.65 EndY=2.4989 EndZ=0
    g2: LineSegment StartX=-21.65 StartY=2.4989 StartZ=0 EndX=-21.65 EndY=-12.5011 EndZ=0
    g3: LineSegment StartX=-21.65 StartY=-12.5011 StartZ=0 EndX=1e-15 EndY=-25 EndZ=0
    g4: Circle [constr] CenterX=0 CenterY=0 CenterZ=0 NormalX=0 NormalY=0 NormalZ=1 AngleXU=0 Radius=25
    g5: LineSegment StartX=-21.65 StartY=2.4989 StartZ=0 EndX=21.65 EndY=2.4989 EndZ=0
  constraints (20):
    c: Coincident(g0,g1)
    c: Coincident(g2,g3)
    c: Coincident(g3,g0)
    c: Equal(g0,g3)
    c: PointOnObject(g0,g4)
    c: PointOnObject(g2,g4)
    c: PointOnObject(g3,g4)
    c: Coincident(g4,g-1)
    c: PointOnObject(g3,g-2)
    c: Diameter(g4) = 50
    c: Coincident(g5,g2)
    c: Coincident(g5,g1)
    c: Vertical(g2)
    c: Block(g3)
    c: Block(g0)
    c: DistanceX(g2,g-1) = 21.65
    c: DistanceX(g-1,g0) = 21.65
    c: DistanceY(g2,g2) = 15
    c: DistanceY(g1,g1) = 15
    c: DistanceX(g5,g5) = 43.3
FEATURE [Part::Extrusion] Extrude559  label="standmount"
  Base = -> Sketch567
  Dir = (0,1,-2e-16)
  DirMode = 2
  FaceMakerClass = Part::FaceMakerBullseye
  FaceMakerMode = 3
  LengthFwd = 30
  LengthRev = 0
  Placement = pos=(0,150,0) rot=(0,0,1;0rad)
  Solid = true
  Symmetric = false
FEATURE [Sketcher::SketchObject] Sketch569
  ArcFitTolerance = 1e-06
  FullyConstrained = true
  MakeInternals = false
  Placement = pos=(0,0,0) rot=(0,0.707107,0.707107;3.14159rad)
  sketch-geometry (6):
    g0: LineSegment StartX=1.1e-15 StartY=-26 StartZ=0 EndX=22.5 EndY=-13.0288 EndZ=0
    g1: LineSegment StartX=22.5 StartY=-13.0288 StartZ=0 EndX=22.5 EndY=31.9712 EndZ=0
    g2: LineSegment StartX=-22.5 StartY=31.9712 StartZ=0 EndX=-22.5 EndY=-13.0288 EndZ=0
    g3: LineSegment StartX=-22.5 StartY=-13.0288 StartZ=0 EndX=1.1e-15 EndY=-26 EndZ=0
    g4: Circle [constr] CenterX=0 CenterY=0 CenterZ=0 NormalX=0 NormalY=0 NormalZ=1 AngleXU=0 Radius=26
    g5: LineSegment StartX=-22.5 StartY=31.9712 StartZ=0 EndX=22.5 EndY=31.9712 EndZ=0
  constraints (20):
    c: Coincident(g0,g1)
    c: Coincident(g2,g3)
    c: Coincident(g3,g0)
    c: Equal(g0,g3)
    c: PointOnObject(g0,g4)
    c: PointOnObject(g2,g4)
    c: PointOnObject(g3,g4)
    c: Coincident(g4,g-1)
    c: PointOnObject(g3,g-2)
    c: Diameter(g4) = 52
    c: Coincident(g5,g2)
    c: Coincident(g5,g1)
    c: Vertical(g2)
    c: Block(g3)
    c: Block(g0)
    c: DistanceX(g2,g-1) = 22.5
    c: DistanceX(g-1,g0) = 22.5
    c: DistanceY(g2,g2) = 45
    c: DistanceY(g1,g1) = 45
    c: DistanceX(g5,g5) = 45
FEATURE [Part::Extrusion] Extrude560  label="standmountcut"
  Base = -> Sketch569
  Dir = (0,1,-2e-16)
  DirMode = 2
  FaceMakerClass = Part::FaceMakerBullseye
  FaceMakerMode = 3
  LengthFwd = 30
  LengthRev = 0
  Placement = pos=(0,150,0) rot=(0,0,1;0rad)
  Solid = true
  Symmetric = false
FEATURE [Part::Cut] Cut005  label="standMountCut"
  Base = -> Box001
  Refine = true
  Tool = -> Extrude560
FEATURE [Part::Cylinder] Cylinder001  label="Cylinder"
  Angle = 360
  AttacherType = Attacher::AttachEngine3D
  FirstAngle = 0
  Height = 60
  Placement = pos=(30,165,-5) rot=(0,1,0;4.71239rad)
  Radius = 2.15
  SecondAngle = 0
FEATURE [Part::Cylinder] Cylinder002
  Angle = 360
  AttacherType = Attacher::AttachEngine3D
  FirstAngle = 0
  Height = 60
  Placement = pos=(30,165,-5) rot=(0,1,0;4.71239rad)
  Radius = 2.15
  SecondAngle = 0
FEATURE [Part::Cut] Cut006  label="standm4cut"
  Base = -> Cut005
  Refine = true
  Tool = -> Cylinder001
FEATURE [Part::Cut] Cut007  label="mountm4cut"
  Base = -> Extrude559
  Refine = true
  Tool = -> Cylinder002
FEATURE [Part::Fillet] Fillet  label="standfillet"
  Base = -> Cut006
  EdgeLinks = -> Cut006 [Edge2,Edge15,Edge26,Edge28]
  Edges = 4 edges r=3: [Edge2,Edge15,Edge26,Edge28]
FEATURE [Part::MultiFuse] Fusion558  label="backEnclsoer"
  Refine = true
  Shapes = -> [Fusion557,Cut007]
FEATURE [Sketcher::SketchObject] Sketch570
  ArcFitTolerance = 1e-06
  FullyConstrained = true
  MakeInternals = false
  Placement = pos=(0,0,0) rot=(1,0,0;1.5708rad)
  sketch-geometry (6):
    g0: Circle CenterX=0 CenterY=126 CenterZ=0 NormalX=0 NormalY=0 NormalZ=1 AngleXU=0 Radius=2.45
    g1: Circle CenterX=109.119 CenterY=-63 CenterZ=0 NormalX=0 NormalY=0 NormalZ=1 AngleXU=0 Radius=2.45
    g2: Circle CenterX=-109.119 CenterY=-63 CenterZ=0 NormalX=0 NormalY=0 NormalZ=1 AngleXU=0 Radius=2.45
    g3: Circle CenterX=0 CenterY=126 CenterZ=0 NormalX=0 NormalY=0 NormalZ=1 AngleXU=0 Radius=7
    g4: Circle CenterX=109.119 CenterY=-63 CenterZ=0 NormalX=0 NormalY=0 NormalZ=1 AngleXU=0 Radius=7
    g5: Circle CenterX=-109.119 CenterY=-63 CenterZ=0 NormalX=0 NormalY=0 NormalZ=1 AngleXU=0 Radius=7
  constraints (15):
    c: PointOnObject(g0,g-2)
    c: Equal(g0,g1)
    c: Equal(g0,g2)
    c: Diameter(g0) = 4.9
    c: DistanceY(g-1,g0) = 126
    c: Distance(g-1,g1) = 126
    c: Distance(g1,g-1) = 63
    c: Horizontal(g2,g1)
    c: Distance(g2,g-1) = 126
    c: Coincident(g3,g0)
    c: Coincident(g4,g1)
    c: Coincident(g5,g2)
    c: Equal(g3,g4)
    c: Equal(g3,g5)
    c: Diameter(g3) = 14
FEATURE [Part::Extrusion] Extrude561
  Base = -> Sketch570
  Dir = (0,-1,2e-16)
  DirMode = 2
  FaceMakerClass = Part::FaceMakerBullseye
  FaceMakerMode = 3
  LengthFwd = 10
  LengthRev = 0
  Placement = pos=(0,-125,0) rot=(0,0,1;0rad)
  Solid = true
  Symmetric = false
FEATURE [Sketcher::SketchObject] Sketch571
  ArcFitTolerance = 1e-06
  FullyConstrained = true
  MakeInternals = false
  Placement = pos=(0,0,0) rot=(1,0,0;1.5708rad)
  sketch-geometry (3):
    g0: Circle CenterX=0 CenterY=126 CenterZ=0 NormalX=0 NormalY=0 NormalZ=1 AngleXU=0 Radius=2.45
    g1: Circle CenterX=109.119 CenterY=-63 CenterZ=0 NormalX=0 NormalY=0 NormalZ=1 AngleXU=0 Radius=2.45
    g2: Circle CenterX=-109.119 CenterY=-63 CenterZ=0 NormalX=0 NormalY=0 NormalZ=1 AngleXU=0 Radius=2.45
  constraints (9):
    c: PointOnObject(g0,g-2)
    c: Equal(g0,g1)
    c: Equal(g0,g2)
    c: Diameter(g0) = 4.9
    c: DistanceY(g-1,g0) = 126
    c: Distance(g-1,g1) = 126
    c: Distance(g1,g-1) = 63
    c: Horizontal(g2,g1)
    c: Distance(g2,g-1) = 126
FEATURE [Part::Extrusion] Extrude562  label="M3HEATSETCUT"
  Base = -> Sketch571
  Dir = (0,-1,2e-16)
  DirMode = 2
  FaceMakerClass = Part::FaceMakerBullseye
  FaceMakerMode = 3
  LengthFwd = 10
  LengthRev = 0
  Placement = pos=(0,-125,0) rot=(0,0,1;0rad)
  Solid = true
  Symmetric = false
FEATURE [Sketcher::SketchObject] Sketch572
  ArcFitTolerance = 1e-06
  FullyConstrained = true
  MakeInternals = false
  Placement = pos=(0,0,0) rot=(1,0,0;1.5708rad)
  sketch-geometry (3):
    g0: Circle CenterX=0 CenterY=126 CenterZ=0 NormalX=0 NormalY=0 NormalZ=1 AngleXU=0 Radius=1.75
    g1: Circle CenterX=109.119 CenterY=-63 CenterZ=0 NormalX=0 NormalY=0 NormalZ=1 AngleXU=0 Radius=1.75
    g2: Circle CenterX=-109.119 CenterY=-63 CenterZ=0 NormalX=0 NormalY=0 NormalZ=1 AngleXU=0 Radius=1.75
  constraints (9):
    c: PointOnObject(g0,g-2)
    c: Equal(g0,g1)
    c: Equal(g0,g2)
    c: Diameter(g0) = 3.5
    c: DistanceY(g-1,g0) = 126
    c: Distance(g-1,g1) = 126
    c: Distance(g1,g-1) = 63
    c: Horizontal(g2,g1)
    c: Distance(g2,g-1) = 126
FEATURE [Part::Extrusion] Extrude563  label="M3HEATSETCUT001"
  Base = -> Sketch572
  Dir = (0,-1,2e-16)
  DirMode = 2
  FaceMakerClass = Part::FaceMakerBullseye
  FaceMakerMode = 3
  LengthFwd = 30
  LengthRev = 0
  Placement = pos=(0,-124,0) rot=(0,0,1;0rad)
  Solid = true
  Symmetric = false
FEATURE [Part::Cut] Cut008  label="hexm3mesh"
  Base = -> Fusion556
  Refine = true
  Tool = -> Extrude562
FEATURE [Part::MultiFuse] Fusion559  label="hexM3cut"
  Refine = true
  Shapes = -> [Extrude561,Cut008]
FEATURE [Part::Cut] Cut009  label="meshm3cut"
  Base = -> Fusion553
  Refine = true
  Tool = -> Extrude563
FEATURE [Sketcher::SketchObject] Sketch573
  ArcFitTolerance = 1e-06
  FullyConstrained = true
  MakeInternals = false
  Placement = pos=(0,0,0) rot=(1,0,0;1.5708rad)
  sketch-geometry (2):
    g0: Circle CenterX=0 CenterY=0 CenterZ=0 NormalX=0 NormalY=0 NormalZ=1 AngleXU=0 Radius=1.5
    g1: Circle CenterX=0 CenterY=0 CenterZ=0 NormalX=0 NormalY=0 NormalZ=1 AngleXU=0 Radius=5
  constraints (4):
    c: Coincident(g0,g-1)
    c: Coincident(g1,g0)
    c: Diameter(g0) = 3
    c: Diameter(g1) = 10
FEATURE [Part::Extrusion] Extrude564  label="pinWheelAxis001"
  Base = -> Sketch573
  Dir = (0,-1,2e-16)
  DirMode = 2
  FaceMakerClass = Part::FaceMakerBullseye
  FaceMakerMode = 3
  LengthFwd = 16
  LengthRev = 0
  Placement = pos=(0,-134,0) rot=(0,0,1;0rad)
  Solid = true
  Symmetric = false
FEATURE [Part::MultiFuse] Fusion560  label="meshPinAxis"
  Refine = true
  Shapes = -> [Cut009,Extrude564]
FEATURE [App::Part] Part  label="pinWheel"
  Group = -> [Cut,Extrude001,Extrude002,Shape,Box,Sketch001,Cut001,PW00_00,Cylinder,Adafruit_AS7341_STEMMA_QT_v005,COZIR_Sensor_v2,Part__Feature059,Compound,Part__Feature355,Part__Feature356,Extrude379,Sketch386,Sketch387,Extrude380,Extrude381,Sketch388,Sketch390,Extrude382,Fusion,Fusion545,Sketch391,Extrude383,Fusion546,Fillet096,Box001,Cut005,Cylinder001,Extrude560,Sketch569,Cut006,Fillet,Sketch567,Sketch004,+387 more]
  Origin = -> Origin001
FEATURE [Sketcher::SketchObject] Sketch574
  ArcFitTolerance = 1e-06
  FullyConstrained = true
  MakeInternals = false
  Placement = pos=(0,0,0) rot=(1,0,0;1.5708rad)
  sketch-geometry (7):
    g0: LineSegment StartX=110.851 StartY=-64 StartZ=0 EndX=110.851 EndY=64 EndZ=0
    g1: LineSegment StartX=110.851 StartY=64 StartZ=0 EndX=-1.9207e-12 EndY=128 EndZ=0
    g2: LineSegment StartX=-1.9207e-12 StartY=128 StartZ=0 EndX=-110.851 EndY=64 EndZ=0
    g3: LineSegment StartX=-110.851 StartY=64 StartZ=0 EndX=-110.851 EndY=-64 EndZ=0
    g4: LineSegment StartX=-110.851 StartY=-64 StartZ=0 EndX=-1.9558e-12 EndY=-128 EndZ=0
    g5: LineSegment StartX=-1.9558e-12 StartY=-128 StartZ=0 EndX=110.851 EndY=-64 EndZ=0
    g6: Circle [constr] CenterX=0 CenterY=0 CenterZ=0 NormalX=0 NormalY=0 NormalZ=1 AngleXU=0 Radius=128
  constraints (16):
    c: Coincident(g0,g1)
    c: Coincident(g1,g2)
    c: Coincident(g2,g3)
    c: Coincident(g3,g4)
    c: Coincident(g4,g5)
    c: Coincident(g5,g0)
    c: Equal(g0, g1-g5) x5
    c: PointOnObject(g0,g6)
    c: PointOnObject(g1,g6)
    c: PointOnObject(g2,g6)
    c: PointOnObject(g3,g6)
    c: PointOnObject(g4,g6)
    c: PointOnObject(g5,g6)
    c: Coincident(g6,g-1)
    c: Vertical(g3)
    c: DistanceY(g3,g3) = 128
